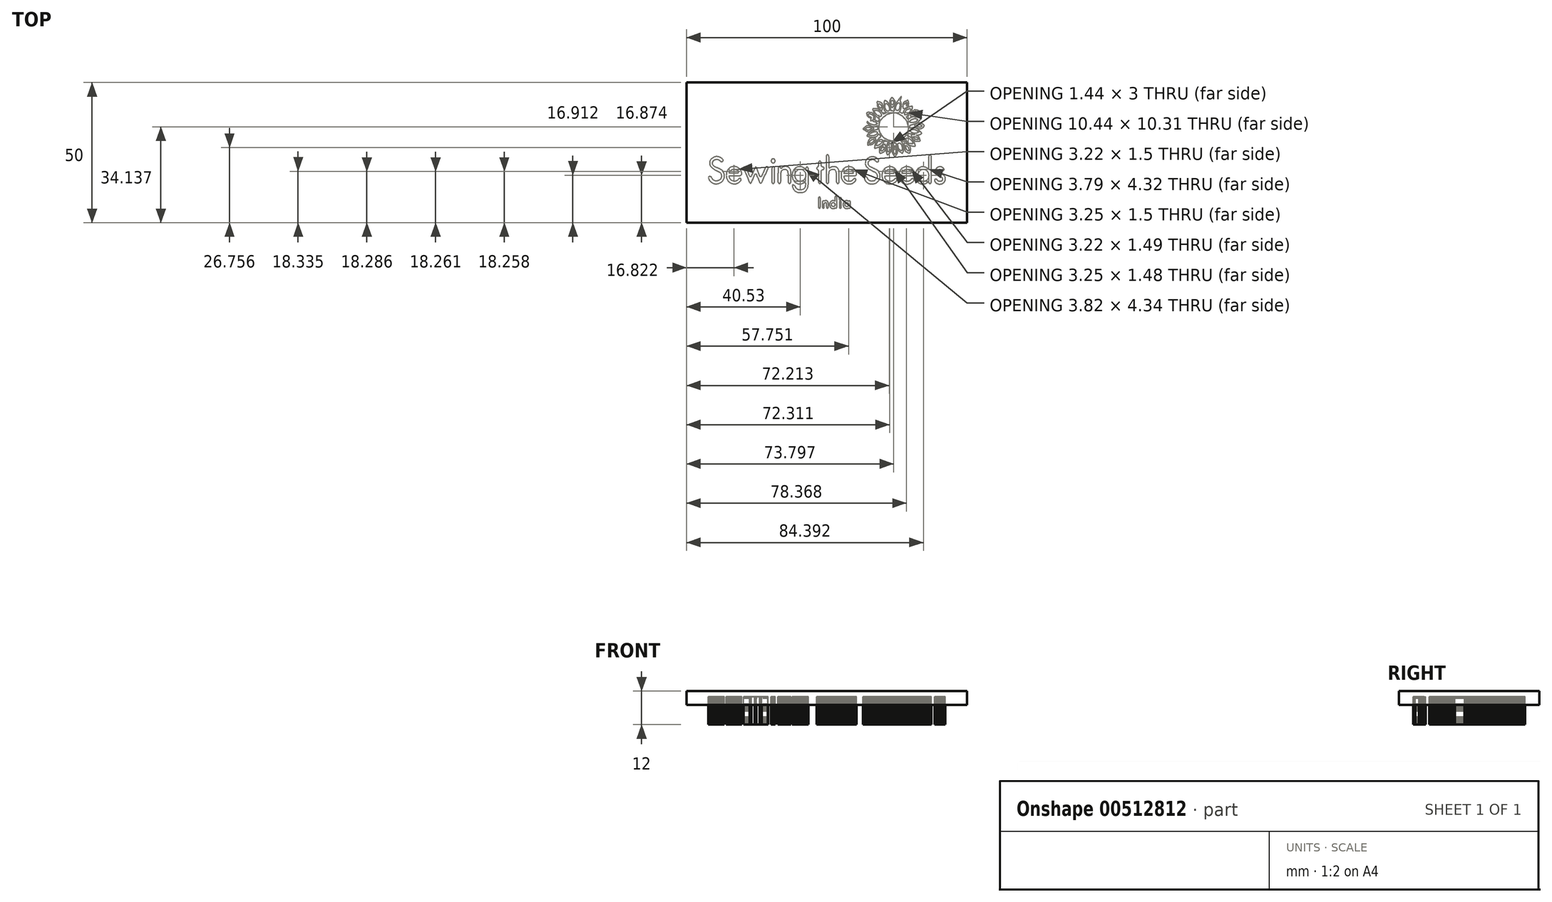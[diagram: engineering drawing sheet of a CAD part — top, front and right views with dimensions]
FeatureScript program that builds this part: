
annotation { "Feature Type Name" : "Feature", "Feature Type Description" : "" }
export const myFeature = defineFeature(function(context is Context, id is Id, definition is map)
    precondition{}
    {
        {
            var Q0;
            Q0=qCreatedBy(makeId("Top.planeOp"),FACE);
            var sketch = newSketch(context, id + "F0", { "sketchPlane" : qUnion([Q0])});
            skLineSegment(sketch, "E0", {"start": v(-2.33, -16.25) * mm, "end": v(-2.36, -16.13) * mm});
            skLineSegment(sketch, "E1", {"start": v(-2.36, -16.13) * mm, "end": v(-2.4, -16.03) * mm});
            skLineSegment(sketch, "E2", {"start": v(-2.4, -16.03) * mm, "end": v(-2.45, -15.94) * mm});
            skLineSegment(sketch, "E3", {"start": v(-2.45, -15.94) * mm, "end": v(-2.5, -15.87) * mm});
            skLineSegment(sketch, "E4", {"start": v(-2.5, -15.87) * mm, "end": v(-2.58, -15.82) * mm});
            skLineSegment(sketch, "E5", {"start": v(-2.58, -15.82) * mm, "end": v(-2.67, -15.8) * mm});
            skLineSegment(sketch, "E6", {"start": v(-2.67, -15.8) * mm, "end": v(-2.76, -15.82) * mm});
            skLineSegment(sketch, "E7", {"start": v(-2.76, -15.82) * mm, "end": v(-2.83, -15.87) * mm});
            skLineSegment(sketch, "E8", {"start": v(-2.83, -15.87) * mm, "end": v(-2.9, -15.94) * mm});
            skLineSegment(sketch, "E9", {"start": v(-2.9, -15.94) * mm, "end": v(-2.94, -16.03) * mm});
            skLineSegment(sketch, "E10", {"start": v(-2.94, -16.03) * mm, "end": v(-2.98, -16.13) * mm});
            skLineSegment(sketch, "E11", {"start": v(-2.98, -16.13) * mm, "end": v(-3.01, -16.25) * mm});
            skLineSegment(sketch, "E12", {"start": v(-3.01, -16.25) * mm, "end": v(-3.03, -16.37) * mm});
            skLineSegment(sketch, "E13", {"start": v(-3.03, -16.37) * mm, "end": v(-3.03, -16.5) * mm});
            skLineSegment(sketch, "E14", {"start": v(-3.03, -16.5) * mm, "end": v(-3.03, -16.83) * mm});
            skLineSegment(sketch, "E15", {"start": v(-3.03, -16.83) * mm, "end": v(-3.03, -17.17) * mm});
            skLineSegment(sketch, "E16", {"start": v(-3.03, -17.17) * mm, "end": v(-3.03, -17.5) * mm});
            skLineSegment(sketch, "E17", {"start": v(-3.03, -17.5) * mm, "end": v(-3.03, -17.84) * mm});
            skLineSegment(sketch, "E18", {"start": v(-3.03, -17.84) * mm, "end": v(-3.03, -18.18) * mm});
            skLineSegment(sketch, "E19", {"start": v(-3.03, -18.18) * mm, "end": v(-3.03, -18.51) * mm});
            skLineSegment(sketch, "E20", {"start": v(-3.03, -18.51) * mm, "end": v(-3.03, -18.85) * mm});
            skLineSegment(sketch, "E21", {"start": v(-3.03, -18.85) * mm, "end": v(-3.03, -19.19) * mm});
            skLineSegment(sketch, "E22", {"start": v(-3.03, -19.19) * mm, "end": v(-3.03, -19.31) * mm});
            skLineSegment(sketch, "E23", {"start": v(-3.03, -19.31) * mm, "end": v(-3.01, -19.43) * mm});
            skLineSegment(sketch, "E24", {"start": v(-3.01, -19.43) * mm, "end": v(-2.98, -19.55) * mm});
            skLineSegment(sketch, "E25", {"start": v(-2.98, -19.55) * mm, "end": v(-2.94, -19.66) * mm});
            skLineSegment(sketch, "E26", {"start": v(-2.94, -19.66) * mm, "end": v(-2.9, -19.75) * mm});
            skLineSegment(sketch, "E27", {"start": v(-2.9, -19.75) * mm, "end": v(-2.83, -19.82) * mm});
            skLineSegment(sketch, "E28", {"start": v(-2.83, -19.82) * mm, "end": v(-2.76, -19.86) * mm});
            skLineSegment(sketch, "E29", {"start": v(-2.76, -19.86) * mm, "end": v(-2.67, -19.88) * mm});
            skLineSegment(sketch, "E30", {"start": v(-2.67, -19.88) * mm, "end": v(-2.58, -19.86) * mm});
            skLineSegment(sketch, "E31", {"start": v(-2.58, -19.86) * mm, "end": v(-2.5, -19.82) * mm});
            skLineSegment(sketch, "E32", {"start": v(-2.5, -19.82) * mm, "end": v(-2.45, -19.75) * mm});
            skLineSegment(sketch, "E33", {"start": v(-2.45, -19.75) * mm, "end": v(-2.4, -19.66) * mm});
            skLineSegment(sketch, "E34", {"start": v(-2.4, -19.66) * mm, "end": v(-2.36, -19.55) * mm});
            skLineSegment(sketch, "E35", {"start": v(-2.36, -19.55) * mm, "end": v(-2.33, -19.43) * mm});
            skLineSegment(sketch, "E36", {"start": v(-2.33, -19.43) * mm, "end": v(-2.31, -19.31) * mm});
            skLineSegment(sketch, "E37", {"start": v(-2.31, -19.31) * mm, "end": v(-2.3, -19.19) * mm});
            skLineSegment(sketch, "E38", {"start": v(-2.3, -19.19) * mm, "end": v(-2.3, -18.85) * mm});
            skLineSegment(sketch, "E39", {"start": v(-2.3, -18.85) * mm, "end": v(-2.3, -18.51) * mm});
            skLineSegment(sketch, "E40", {"start": v(-2.3, -18.51) * mm, "end": v(-2.3, -18.18) * mm});
            skLineSegment(sketch, "E41", {"start": v(-2.3, -18.18) * mm, "end": v(-2.3, -17.84) * mm});
            skLineSegment(sketch, "E42", {"start": v(-2.3, -17.84) * mm, "end": v(-2.3, -17.5) * mm});
            skLineSegment(sketch, "E43", {"start": v(-2.3, -17.5) * mm, "end": v(-2.3, -17.17) * mm});
            skLineSegment(sketch, "E44", {"start": v(-2.3, -17.17) * mm, "end": v(-2.3, -16.83) * mm});
            skLineSegment(sketch, "E45", {"start": v(-2.3, -16.83) * mm, "end": v(-2.3, -16.5) * mm});
            skLineSegment(sketch, "E46", {"start": v(-2.3, -16.5) * mm, "end": v(-2.31, -16.37) * mm});
            skLineSegment(sketch, "E47", {"start": v(-2.31, -16.37) * mm, "end": v(-2.33, -16.25) * mm});
            skLineSegment(sketch, "E48", {"start": v(0.5, -17.99) * mm, "end": v(0.48, -17.86) * mm});
            skLineSegment(sketch, "E49", {"start": v(0.48, -17.86) * mm, "end": v(0.45, -17.74) * mm});
            skLineSegment(sketch, "E50", {"start": v(0.45, -17.74) * mm, "end": v(0.4, -17.64) * mm});
            skLineSegment(sketch, "E51", {"start": v(0.4, -17.64) * mm, "end": v(0.35, -17.54) * mm});
            skLineSegment(sketch, "E52", {"start": v(0.35, -17.54) * mm, "end": v(0.29, -17.46) * mm});
            skLineSegment(sketch, "E53", {"start": v(0.29, -17.46) * mm, "end": v(0.22, -17.38) * mm});
            skLineSegment(sketch, "E54", {"start": v(0.22, -17.38) * mm, "end": v(0.15, -17.33) * mm});
            skLineSegment(sketch, "E55", {"start": v(0.15, -17.33) * mm, "end": v(0.08, -17.28) * mm});
            skLineSegment(sketch, "E56", {"start": v(0.08, -17.28) * mm, "end": v(0, -17.24) * mm});
            skLineSegment(sketch, "E57", {"start": v(0, -17.24) * mm, "end": v(-0.07, -17.2) * mm});
            skLineSegment(sketch, "E58", {"start": v(-0.07, -17.2) * mm, "end": v(-0.14, -17.18) * mm});
            skLineSegment(sketch, "E59", {"start": v(-0.14, -17.18) * mm, "end": v(-0.22, -17.17) * mm});
            skLineSegment(sketch, "E60", {"start": v(-0.22, -17.17) * mm, "end": v(-0.3, -17.16) * mm});
            skLineSegment(sketch, "E61", {"start": v(-0.3, -17.16) * mm, "end": v(-0.4, -17.15) * mm});
            skLineSegment(sketch, "E62", {"start": v(-0.4, -17.15) * mm, "end": v(-0.45, -17.15) * mm});
            skLineSegment(sketch, "E63", {"start": v(-0.45, -17.15) * mm, "end": v(-0.5, -17.16) * mm});
            skLineSegment(sketch, "E64", {"start": v(-0.5, -17.16) * mm, "end": v(-0.56, -17.17) * mm});
            skLineSegment(sketch, "E65", {"start": v(-0.56, -17.17) * mm, "end": v(-0.62, -17.18) * mm});
            skLineSegment(sketch, "E66", {"start": v(-0.62, -17.18) * mm, "end": v(-0.67, -17.19) * mm});
            skLineSegment(sketch, "E67", {"start": v(-0.67, -17.19) * mm, "end": v(-0.73, -17.2) * mm});
            skLineSegment(sketch, "E68", {"start": v(-0.73, -17.2) * mm, "end": v(-0.78, -17.23) * mm});
            skLineSegment(sketch, "E69", {"start": v(-0.78, -17.23) * mm, "end": v(-0.83, -17.25) * mm});
            skLineSegment(sketch, "E70", {"start": v(-0.83, -17.25) * mm, "end": v(-0.85, -17.26) * mm});
            skLineSegment(sketch, "E71", {"start": v(-0.85, -17.26) * mm, "end": v(-0.87, -17.27) * mm});
            skLineSegment(sketch, "E72", {"start": v(-0.87, -17.27) * mm, "end": v(-0.9, -17.28) * mm});
            skLineSegment(sketch, "E73", {"start": v(-0.9, -17.28) * mm, "end": v(-0.91, -17.29) * mm});
            skLineSegment(sketch, "E74", {"start": v(-0.91, -17.29) * mm, "end": v(-0.93, -17.3) * mm});
            skLineSegment(sketch, "E75", {"start": v(-0.93, -17.3) * mm, "end": v(-0.95, -17.32) * mm});
            skLineSegment(sketch, "E76", {"start": v(-0.95, -17.32) * mm, "end": v(-0.97, -17.33) * mm});
            skLineSegment(sketch, "E77", {"start": v(-0.97, -17.33) * mm, "end": v(-1, -17.35) * mm});
            skLineSegment(sketch, "E78", {"start": v(-1, -17.35) * mm, "end": v(-1.02, -17.32) * mm});
            skLineSegment(sketch, "E79", {"start": v(-1.02, -17.32) * mm, "end": v(-1.05, -17.3) * mm});
            skLineSegment(sketch, "E80", {"start": v(-1.05, -17.3) * mm, "end": v(-1.08, -17.28) * mm});
            skLineSegment(sketch, "E81", {"start": v(-1.08, -17.28) * mm, "end": v(-1.12, -17.26) * mm});
            skLineSegment(sketch, "E82", {"start": v(-1.12, -17.26) * mm, "end": v(-1.16, -17.24) * mm});
            skLineSegment(sketch, "E83", {"start": v(-1.16, -17.24) * mm, "end": v(-1.2, -17.23) * mm});
            skLineSegment(sketch, "E84", {"start": v(-1.2, -17.23) * mm, "end": v(-1.25, -17.23) * mm});
            skLineSegment(sketch, "E85", {"start": v(-1.25, -17.23) * mm, "end": v(-1.3, -17.22) * mm});
            skLineSegment(sketch, "E86", {"start": v(-1.3, -17.22) * mm, "end": v(-1.38, -17.24) * mm});
            skLineSegment(sketch, "E87", {"start": v(-1.38, -17.24) * mm, "end": v(-1.45, -17.28) * mm});
            skLineSegment(sketch, "E88", {"start": v(-1.45, -17.28) * mm, "end": v(-1.51, -17.35) * mm});
            skLineSegment(sketch, "E89", {"start": v(-1.51, -17.35) * mm, "end": v(-1.56, -17.44) * mm});
            skLineSegment(sketch, "E90", {"start": v(-1.56, -17.44) * mm, "end": v(-1.6, -17.54) * mm});
            skLineSegment(sketch, "E91", {"start": v(-1.6, -17.54) * mm, "end": v(-1.62, -17.66) * mm});
            skLineSegment(sketch, "E92", {"start": v(-1.62, -17.66) * mm, "end": v(-1.64, -17.79) * mm});
            skLineSegment(sketch, "E93", {"start": v(-1.64, -17.79) * mm, "end": v(-1.64, -17.91) * mm});
            skLineSegment(sketch, "E94", {"start": v(-1.64, -17.91) * mm, "end": v(-1.64, -18.07) * mm});
            skLineSegment(sketch, "E95", {"start": v(-1.64, -18.07) * mm, "end": v(-1.64, -18.23) * mm});
            skLineSegment(sketch, "E96", {"start": v(-1.64, -18.23) * mm, "end": v(-1.64, -18.4) * mm});
            skLineSegment(sketch, "E97", {"start": v(-1.64, -18.4) * mm, "end": v(-1.64, -18.55) * mm});
            skLineSegment(sketch, "E98", {"start": v(-1.64, -18.55) * mm, "end": v(-1.64, -18.7) * mm});
            skLineSegment(sketch, "E99", {"start": v(-1.64, -18.7) * mm, "end": v(-1.64, -18.87) * mm});
            skLineSegment(sketch, "E100", {"start": v(-1.64, -18.87) * mm, "end": v(-1.64, -19.03) * mm});
            skLineSegment(sketch, "E101", {"start": v(-1.64, -19.03) * mm, "end": v(-1.64, -19.19) * mm});
            skLineSegment(sketch, "E102", {"start": v(-1.64, -19.19) * mm, "end": v(-1.64, -19.31) * mm});
            skLineSegment(sketch, "E103", {"start": v(-1.64, -19.31) * mm, "end": v(-1.62, -19.44) * mm});
            skLineSegment(sketch, "E104", {"start": v(-1.62, -19.44) * mm, "end": v(-1.6, -19.56) * mm});
            skLineSegment(sketch, "E105", {"start": v(-1.6, -19.56) * mm, "end": v(-1.56, -19.66) * mm});
            skLineSegment(sketch, "E106", {"start": v(-1.56, -19.66) * mm, "end": v(-1.51, -19.75) * mm});
            skLineSegment(sketch, "E107", {"start": v(-1.51, -19.75) * mm, "end": v(-1.45, -19.82) * mm});
            skLineSegment(sketch, "E108", {"start": v(-1.45, -19.82) * mm, "end": v(-1.38, -19.86) * mm});
            skLineSegment(sketch, "E109", {"start": v(-1.38, -19.86) * mm, "end": v(-1.3, -19.88) * mm});
            skLineSegment(sketch, "E110", {"start": v(-1.3, -19.88) * mm, "end": v(-1.2, -19.86) * mm});
            skLineSegment(sketch, "E111", {"start": v(-1.2, -19.86) * mm, "end": v(-1.13, -19.82) * mm});
            skLineSegment(sketch, "E112", {"start": v(-1.13, -19.82) * mm, "end": v(-1.07, -19.75) * mm});
            skLineSegment(sketch, "E113", {"start": v(-1.07, -19.75) * mm, "end": v(-1.02, -19.66) * mm});
            skLineSegment(sketch, "E114", {"start": v(-1.02, -19.66) * mm, "end": v(-0.99, -19.56) * mm});
            skLineSegment(sketch, "E115", {"start": v(-0.99, -19.56) * mm, "end": v(-0.96, -19.44) * mm});
            skLineSegment(sketch, "E116", {"start": v(-0.96, -19.44) * mm, "end": v(-0.94, -19.31) * mm});
            skLineSegment(sketch, "E117", {"start": v(-0.94, -19.31) * mm, "end": v(-0.94, -19.19) * mm});
            skLineSegment(sketch, "E118", {"start": v(-0.94, -19.19) * mm, "end": v(-0.94, -19.09) * mm});
            skLineSegment(sketch, "E119", {"start": v(-0.94, -19.09) * mm, "end": v(-0.94, -19) * mm});
            skLineSegment(sketch, "E120", {"start": v(-0.94, -19) * mm, "end": v(-0.94, -18.9) * mm});
            skLineSegment(sketch, "E121", {"start": v(-0.94, -18.9) * mm, "end": v(-0.94, -18.8) * mm});
            skLineSegment(sketch, "E122", {"start": v(-0.94, -18.8) * mm, "end": v(-0.94, -18.7) * mm});
            skLineSegment(sketch, "E123", {"start": v(-0.94, -18.7) * mm, "end": v(-0.94, -18.6) * mm});
            skLineSegment(sketch, "E124", {"start": v(-0.94, -18.6) * mm, "end": v(-0.94, -18.5) * mm});
            skLineSegment(sketch, "E125", {"start": v(-0.94, -18.5) * mm, "end": v(-0.94, -18.4) * mm});
            skLineSegment(sketch, "E126", {"start": v(-0.94, -18.4) * mm, "end": v(-0.94, -18.34) * mm});
            skLineSegment(sketch, "E127", {"start": v(-0.94, -18.34) * mm, "end": v(-0.93, -18.27) * mm});
            skLineSegment(sketch, "E128", {"start": v(-0.93, -18.27) * mm, "end": v(-0.92, -18.21) * mm});
            skLineSegment(sketch, "E129", {"start": v(-0.92, -18.21) * mm, "end": v(-0.9, -18.16) * mm});
            skLineSegment(sketch, "E130", {"start": v(-0.9, -18.16) * mm, "end": v(-0.9, -18.1) * mm});
            skLineSegment(sketch, "E131", {"start": v(-0.9, -18.1) * mm, "end": v(-0.87, -18.05) * mm});
            skLineSegment(sketch, "E132", {"start": v(-0.87, -18.05) * mm, "end": v(-0.85, -18) * mm});
            skLineSegment(sketch, "E133", {"start": v(-0.85, -18) * mm, "end": v(-0.82, -17.97) * mm});
            skLineSegment(sketch, "E134", {"start": v(-0.82, -17.97) * mm, "end": v(-0.8, -17.93) * mm});
            skLineSegment(sketch, "E135", {"start": v(-0.8, -17.93) * mm, "end": v(-0.76, -17.9) * mm});
            skLineSegment(sketch, "E136", {"start": v(-0.76, -17.9) * mm, "end": v(-0.73, -17.87) * mm});
            skLineSegment(sketch, "E137", {"start": v(-0.73, -17.87) * mm, "end": v(-0.7, -17.85) * mm});
            skLineSegment(sketch, "E138", {"start": v(-0.7, -17.85) * mm, "end": v(-0.65, -17.84) * mm});
            skLineSegment(sketch, "E139", {"start": v(-0.65, -17.84) * mm, "end": v(-0.6, -17.83) * mm});
            skLineSegment(sketch, "E140", {"start": v(-0.6, -17.83) * mm, "end": v(-0.56, -17.82) * mm});
            skLineSegment(sketch, "E141", {"start": v(-0.56, -17.82) * mm, "end": v(-0.5, -17.82) * mm});
            skLineSegment(sketch, "E142", {"start": v(-0.5, -17.82) * mm, "end": v(-0.46, -17.82) * mm});
            skLineSegment(sketch, "E143", {"start": v(-0.46, -17.82) * mm, "end": v(-0.42, -17.82) * mm});
            skLineSegment(sketch, "E144", {"start": v(-0.42, -17.82) * mm, "end": v(-0.39, -17.83) * mm});
            skLineSegment(sketch, "E145", {"start": v(-0.39, -17.83) * mm, "end": v(-0.36, -17.83) * mm});
            skLineSegment(sketch, "E146", {"start": v(-0.36, -17.83) * mm, "end": v(-0.34, -17.84) * mm});
            skLineSegment(sketch, "E147", {"start": v(-0.34, -17.84) * mm, "end": v(-0.32, -17.85) * mm});
            skLineSegment(sketch, "E148", {"start": v(-0.32, -17.85) * mm, "end": v(-0.3, -17.85) * mm});
            skLineSegment(sketch, "E149", {"start": v(-0.3, -17.85) * mm, "end": v(-0.3, -17.86) * mm});
            skLineSegment(sketch, "E150", {"start": v(-0.3, -17.86) * mm, "end": v(-0.27, -17.97) * mm});
            skLineSegment(sketch, "E151", {"start": v(-0.27, -17.97) * mm, "end": v(-0.25, -18.1) * mm});
            skLineSegment(sketch, "E152", {"start": v(-0.25, -18.1) * mm, "end": v(-0.22, -18.23) * mm});
            skLineSegment(sketch, "E153", {"start": v(-0.22, -18.23) * mm, "end": v(-0.2, -18.36) * mm});
            skLineSegment(sketch, "E154", {"start": v(-0.2, -18.36) * mm, "end": v(-0.2, -18.5) * mm});
            skLineSegment(sketch, "E155", {"start": v(-0.2, -18.5) * mm, "end": v(-0.18, -18.63) * mm});
            skLineSegment(sketch, "E156", {"start": v(-0.18, -18.63) * mm, "end": v(-0.17, -18.75) * mm});
            skLineSegment(sketch, "E157", {"start": v(-0.17, -18.75) * mm, "end": v(-0.17, -18.86) * mm});
            skLineSegment(sketch, "E158", {"start": v(-0.17, -18.86) * mm, "end": v(-0.17, -18.9) * mm});
            skLineSegment(sketch, "E159", {"start": v(-0.17, -18.9) * mm, "end": v(-0.17, -18.94) * mm});
            skLineSegment(sketch, "E160", {"start": v(-0.17, -18.94) * mm, "end": v(-0.17, -18.98) * mm});
            skLineSegment(sketch, "E161", {"start": v(-0.17, -18.98) * mm, "end": v(-0.17, -19.03) * mm});
            skLineSegment(sketch, "E162", {"start": v(-0.17, -19.03) * mm, "end": v(-0.17, -19.07) * mm});
            skLineSegment(sketch, "E163", {"start": v(-0.17, -19.07) * mm, "end": v(-0.17, -19.1) * mm});
            skLineSegment(sketch, "E164", {"start": v(-0.17, -19.1) * mm, "end": v(-0.17, -19.15) * mm});
            skLineSegment(sketch, "E165", {"start": v(-0.17, -19.15) * mm, "end": v(-0.17, -19.19) * mm});
            skLineSegment(sketch, "E166", {"start": v(-0.17, -19.19) * mm, "end": v(-0.17, -19.31) * mm});
            skLineSegment(sketch, "E167", {"start": v(-0.17, -19.31) * mm, "end": v(-0.15, -19.44) * mm});
            skLineSegment(sketch, "E168", {"start": v(-0.15, -19.44) * mm, "end": v(-0.12, -19.56) * mm});
            skLineSegment(sketch, "E169", {"start": v(-0.12, -19.56) * mm, "end": v(-0.09, -19.66) * mm});
            skLineSegment(sketch, "E170", {"start": v(-0.09, -19.66) * mm, "end": v(-0.04, -19.75) * mm});
            skLineSegment(sketch, "E171", {"start": v(-0.04, -19.75) * mm, "end": v(0.02, -19.82) * mm});
            skLineSegment(sketch, "E172", {"start": v(0.02, -19.82) * mm, "end": v(0.1, -19.86) * mm});
            skLineSegment(sketch, "E173", {"start": v(0.1, -19.86) * mm, "end": v(0.18, -19.88) * mm});
            skLineSegment(sketch, "E174", {"start": v(0.18, -19.88) * mm, "end": v(0.26, -19.86) * mm});
            skLineSegment(sketch, "E175", {"start": v(0.26, -19.86) * mm, "end": v(0.34, -19.82) * mm});
            skLineSegment(sketch, "E176", {"start": v(0.34, -19.82) * mm, "end": v(0.4, -19.75) * mm});
            skLineSegment(sketch, "E177", {"start": v(0.4, -19.75) * mm, "end": v(0.44, -19.66) * mm});
            skLineSegment(sketch, "E178", {"start": v(0.44, -19.66) * mm, "end": v(0.48, -19.56) * mm});
            skLineSegment(sketch, "E179", {"start": v(0.48, -19.56) * mm, "end": v(0.5, -19.44) * mm});
            skLineSegment(sketch, "E180", {"start": v(0.5, -19.44) * mm, "end": v(0.52, -19.31) * mm});
            skLineSegment(sketch, "E181", {"start": v(0.52, -19.31) * mm, "end": v(0.53, -19.19) * mm});
            skLineSegment(sketch, "E182", {"start": v(0.53, -19.19) * mm, "end": v(0.53, -19.07) * mm});
            skLineSegment(sketch, "E183", {"start": v(0.53, -19.07) * mm, "end": v(0.53, -18.96) * mm});
            skLineSegment(sketch, "E184", {"start": v(0.53, -18.96) * mm, "end": v(0.53, -18.84) * mm});
            skLineSegment(sketch, "E185", {"start": v(0.53, -18.84) * mm, "end": v(0.53, -18.73) * mm});
            skLineSegment(sketch, "E186", {"start": v(0.53, -18.73) * mm, "end": v(0.53, -18.62) * mm});
            skLineSegment(sketch, "E187", {"start": v(0.53, -18.62) * mm, "end": v(0.53, -18.5) * mm});
            skLineSegment(sketch, "E188", {"start": v(0.53, -18.5) * mm, "end": v(0.53, -18.39) * mm});
            skLineSegment(sketch, "E189", {"start": v(0.53, -18.39) * mm, "end": v(0.53, -18.27) * mm});
            skLineSegment(sketch, "E190", {"start": v(0.53, -18.27) * mm, "end": v(0.52, -18.13) * mm});
            skLineSegment(sketch, "E191", {"start": v(0.52, -18.13) * mm, "end": v(0.5, -17.99) * mm});
            skLineSegment(sketch, "E192", {"start": v(3.53, -15.89) * mm, "end": v(3.5, -15.77) * mm});
            skLineSegment(sketch, "E193", {"start": v(3.5, -15.77) * mm, "end": v(3.47, -15.66) * mm});
            skLineSegment(sketch, "E194", {"start": v(3.47, -15.66) * mm, "end": v(3.42, -15.58) * mm});
            skLineSegment(sketch, "E195", {"start": v(3.42, -15.58) * mm, "end": v(3.36, -15.5) * mm});
            skLineSegment(sketch, "E196", {"start": v(3.36, -15.5) * mm, "end": v(3.29, -15.46) * mm});
            skLineSegment(sketch, "E197", {"start": v(3.29, -15.46) * mm, "end": v(3.2, -15.45) * mm});
            skLineSegment(sketch, "E198", {"start": v(3.2, -15.45) * mm, "end": v(3.12, -15.46) * mm});
            skLineSegment(sketch, "E199", {"start": v(3.12, -15.46) * mm, "end": v(3.05, -15.5) * mm});
            skLineSegment(sketch, "E200", {"start": v(3.05, -15.5) * mm, "end": v(3, -15.58) * mm});
            skLineSegment(sketch, "E201", {"start": v(3, -15.58) * mm, "end": v(2.95, -15.66) * mm});
            skLineSegment(sketch, "E202", {"start": v(2.95, -15.66) * mm, "end": v(2.9, -15.77) * mm});
            skLineSegment(sketch, "E203", {"start": v(2.9, -15.77) * mm, "end": v(2.88, -15.89) * mm});
            skLineSegment(sketch, "E204", {"start": v(2.88, -15.89) * mm, "end": v(2.87, -16.01) * mm});
            skLineSegment(sketch, "E205", {"start": v(2.87, -16.01) * mm, "end": v(2.86, -16.14) * mm});
            skLineSegment(sketch, "E206", {"start": v(2.86, -16.14) * mm, "end": v(2.86, -16.3) * mm});
            skLineSegment(sketch, "E207", {"start": v(2.86, -16.3) * mm, "end": v(2.86, -16.45) * mm});
            skLineSegment(sketch, "E208", {"start": v(2.86, -16.45) * mm, "end": v(2.86, -16.6) * mm});
            skLineSegment(sketch, "E209", {"start": v(2.86, -16.6) * mm, "end": v(2.86, -16.76) * mm});
            skLineSegment(sketch, "E210", {"start": v(2.86, -16.76) * mm, "end": v(2.86, -16.91) * mm});
            skLineSegment(sketch, "E211", {"start": v(2.86, -16.91) * mm, "end": v(2.86, -17.07) * mm});
            skLineSegment(sketch, "E212", {"start": v(2.86, -17.07) * mm, "end": v(2.86, -17.22) * mm});
            skLineSegment(sketch, "E213", {"start": v(2.86, -17.22) * mm, "end": v(2.86, -17.37) * mm});
            skLineSegment(sketch, "E214", {"start": v(2.86, -17.37) * mm, "end": v(2.8, -17.33) * mm});
            skLineSegment(sketch, "E215", {"start": v(2.8, -17.33) * mm, "end": v(2.72, -17.29) * mm});
            skLineSegment(sketch, "E216", {"start": v(2.72, -17.29) * mm, "end": v(2.64, -17.25) * mm});
            skLineSegment(sketch, "E217", {"start": v(2.64, -17.25) * mm, "end": v(2.56, -17.22) * mm});
            skLineSegment(sketch, "E218", {"start": v(2.56, -17.22) * mm, "end": v(2.47, -17.2) * mm});
            skLineSegment(sketch, "E219", {"start": v(2.47, -17.2) * mm, "end": v(2.38, -17.18) * mm});
            skLineSegment(sketch, "E220", {"start": v(2.38, -17.18) * mm, "end": v(2.3, -17.17) * mm});
            skLineSegment(sketch, "E221", {"start": v(2.3, -17.17) * mm, "end": v(2.2, -17.17) * mm});
            skLineSegment(sketch, "E222", {"start": v(2.2, -17.17) * mm, "end": v(2.2, -17.17) * mm});
            skLineSegment(sketch, "E223", {"start": v(2.2, -17.17) * mm, "end": v(2.19, -17.17) * mm});
            skLineSegment(sketch, "E224", {"start": v(2.19, -17.17) * mm, "end": v(2.18, -17.17) * mm});
            skLineSegment(sketch, "E225", {"start": v(2.18, -17.17) * mm, "end": v(2.18, -17.17) * mm});
            skLineSegment(sketch, "E226", {"start": v(2.18, -17.17) * mm, "end": v(2.17, -17.17) * mm});
            skLineSegment(sketch, "E227", {"start": v(2.17, -17.17) * mm, "end": v(2.17, -17.17) * mm});
            skLineSegment(sketch, "E228", {"start": v(2.17, -17.17) * mm, "end": v(2.03, -17.17) * mm});
            skLineSegment(sketch, "E229", {"start": v(2.03, -17.17) * mm, "end": v(1.9, -17.2) * mm});
            skLineSegment(sketch, "E230", {"start": v(1.9, -17.2) * mm, "end": v(1.79, -17.23) * mm});
            skLineSegment(sketch, "E231", {"start": v(1.79, -17.23) * mm, "end": v(1.67, -17.27) * mm});
            skLineSegment(sketch, "E232", {"start": v(1.67, -17.27) * mm, "end": v(1.56, -17.33) * mm});
            skLineSegment(sketch, "E233", {"start": v(1.56, -17.33) * mm, "end": v(1.46, -17.4) * mm});
            skLineSegment(sketch, "E234", {"start": v(1.46, -17.4) * mm, "end": v(1.36, -17.5) * mm});
            skLineSegment(sketch, "E235", {"start": v(1.36, -17.5) * mm, "end": v(1.27, -17.6) * mm});
            skLineSegment(sketch, "E236", {"start": v(1.27, -17.6) * mm, "end": v(1.2, -17.7) * mm});
            skLineSegment(sketch, "E237", {"start": v(1.2, -17.7) * mm, "end": v(1.13, -17.8) * mm});
            skLineSegment(sketch, "E238", {"start": v(1.13, -17.8) * mm, "end": v(1.08, -17.92) * mm});
            skLineSegment(sketch, "E239", {"start": v(1.08, -17.92) * mm, "end": v(1.03, -18.04) * mm});
            skLineSegment(sketch, "E240", {"start": v(1.03, -18.04) * mm, "end": v(1, -18.16) * mm});
            skLineSegment(sketch, "E241", {"start": v(1, -18.16) * mm, "end": v(0.97, -18.3) * mm});
            skLineSegment(sketch, "E242", {"start": v(0.97, -18.3) * mm, "end": v(0.96, -18.42) * mm});
            skLineSegment(sketch, "E243", {"start": v(0.96, -18.42) * mm, "end": v(0.95, -18.56) * mm});
            skLineSegment(sketch, "E244", {"start": v(0.95, -18.56) * mm, "end": v(0.96, -18.7) * mm});
            skLineSegment(sketch, "E245", {"start": v(0.96, -18.7) * mm, "end": v(0.97, -18.83) * mm});
            skLineSegment(sketch, "E246", {"start": v(0.97, -18.83) * mm, "end": v(1, -18.96) * mm});
            skLineSegment(sketch, "E247", {"start": v(1, -18.96) * mm, "end": v(1.04, -19.08) * mm});
            skLineSegment(sketch, "E248", {"start": v(1.04, -19.08) * mm, "end": v(1.08, -19.2) * mm});
            skLineSegment(sketch, "E249", {"start": v(1.08, -19.2) * mm, "end": v(1.14, -19.3) * mm});
            skLineSegment(sketch, "E250", {"start": v(1.14, -19.3) * mm, "end": v(1.21, -19.42) * mm});
            skLineSegment(sketch, "E251", {"start": v(1.21, -19.42) * mm, "end": v(1.3, -19.52) * mm});
            skLineSegment(sketch, "E252", {"start": v(1.3, -19.52) * mm, "end": v(1.38, -19.62) * mm});
            skLineSegment(sketch, "E253", {"start": v(1.38, -19.62) * mm, "end": v(1.48, -19.71) * mm});
            skLineSegment(sketch, "E254", {"start": v(1.48, -19.71) * mm, "end": v(1.58, -19.79) * mm});
            skLineSegment(sketch, "E255", {"start": v(1.58, -19.79) * mm, "end": v(1.7, -19.85) * mm});
            skLineSegment(sketch, "E256", {"start": v(1.7, -19.85) * mm, "end": v(1.8, -19.9) * mm});
            skLineSegment(sketch, "E257", {"start": v(1.8, -19.9) * mm, "end": v(1.92, -19.93) * mm});
            skLineSegment(sketch, "E258", {"start": v(1.92, -19.93) * mm, "end": v(2.05, -19.95) * mm});
            skLineSegment(sketch, "E259", {"start": v(2.05, -19.95) * mm, "end": v(2.17, -19.95) * mm});
            skLineSegment(sketch, "E260", {"start": v(2.17, -19.95) * mm, "end": v(2.18, -19.95) * mm});
            skLineSegment(sketch, "E261", {"start": v(2.18, -19.95) * mm, "end": v(2.18, -19.95) * mm});
            skLineSegment(sketch, "E262", {"start": v(2.18, -19.95) * mm, "end": v(2.19, -19.95) * mm});
            skLineSegment(sketch, "E263", {"start": v(2.19, -19.95) * mm, "end": v(2.19, -19.95) * mm});
            skLineSegment(sketch, "E264", {"start": v(2.19, -19.95) * mm, "end": v(2.2, -19.95) * mm});
            skLineSegment(sketch, "E265", {"start": v(2.2, -19.95) * mm, "end": v(2.26, -19.95) * mm});
            skLineSegment(sketch, "E266", {"start": v(2.26, -19.95) * mm, "end": v(2.33, -19.95) * mm});
            skLineSegment(sketch, "E267", {"start": v(2.33, -19.95) * mm, "end": v(2.4, -19.94) * mm});
            skLineSegment(sketch, "E268", {"start": v(2.4, -19.94) * mm, "end": v(2.47, -19.93) * mm});
            skLineSegment(sketch, "E269", {"start": v(2.47, -19.93) * mm, "end": v(2.54, -19.92) * mm});
            skLineSegment(sketch, "E270", {"start": v(2.54, -19.92) * mm, "end": v(2.6, -19.9) * mm});
            skLineSegment(sketch, "E271", {"start": v(2.6, -19.9) * mm, "end": v(2.65, -19.89) * mm});
            skLineSegment(sketch, "E272", {"start": v(2.65, -19.89) * mm, "end": v(2.69, -19.86) * mm});
            skLineSegment(sketch, "E273", {"start": v(2.69, -19.86) * mm, "end": v(2.72, -19.83) * mm});
            skLineSegment(sketch, "E274", {"start": v(2.72, -19.83) * mm, "end": v(2.76, -19.8) * mm});
            skLineSegment(sketch, "E275", {"start": v(2.76, -19.8) * mm, "end": v(2.79, -19.78) * mm});
            skLineSegment(sketch, "E276", {"start": v(2.79, -19.78) * mm, "end": v(2.82, -19.76) * mm});
            skLineSegment(sketch, "E277", {"start": v(2.82, -19.76) * mm, "end": v(2.84, -19.75) * mm});
            skLineSegment(sketch, "E278", {"start": v(2.84, -19.75) * mm, "end": v(2.87, -19.73) * mm});
            skLineSegment(sketch, "E279", {"start": v(2.87, -19.73) * mm, "end": v(2.89, -19.72) * mm});
            skLineSegment(sketch, "E280", {"start": v(2.89, -19.72) * mm, "end": v(2.9, -19.7) * mm});
            skLineSegment(sketch, "E281", {"start": v(2.9, -19.7) * mm, "end": v(2.93, -19.74) * mm});
            skLineSegment(sketch, "E282", {"start": v(2.93, -19.74) * mm, "end": v(2.96, -19.78) * mm});
            skLineSegment(sketch, "E283", {"start": v(2.96, -19.78) * mm, "end": v(3, -19.8) * mm});
            skLineSegment(sketch, "E284", {"start": v(3, -19.8) * mm, "end": v(3.03, -19.83) * mm});
            skLineSegment(sketch, "E285", {"start": v(3.03, -19.83) * mm, "end": v(3.07, -19.85) * mm});
            skLineSegment(sketch, "E286", {"start": v(3.07, -19.85) * mm, "end": v(3.12, -19.86) * mm});
            skLineSegment(sketch, "E287", {"start": v(3.12, -19.86) * mm, "end": v(3.16, -19.87) * mm});
            skLineSegment(sketch, "E288", {"start": v(3.16, -19.87) * mm, "end": v(3.21, -19.88) * mm});
            skLineSegment(sketch, "E289", {"start": v(3.21, -19.88) * mm, "end": v(3.3, -19.86) * mm});
            skLineSegment(sketch, "E290", {"start": v(3.3, -19.86) * mm, "end": v(3.36, -19.82) * mm});
            skLineSegment(sketch, "E291", {"start": v(3.36, -19.82) * mm, "end": v(3.42, -19.75) * mm});
            skLineSegment(sketch, "E292", {"start": v(3.42, -19.75) * mm, "end": v(3.47, -19.66) * mm});
            skLineSegment(sketch, "E293", {"start": v(3.47, -19.66) * mm, "end": v(3.5, -19.56) * mm});
            skLineSegment(sketch, "E294", {"start": v(3.5, -19.56) * mm, "end": v(3.53, -19.44) * mm});
            skLineSegment(sketch, "E295", {"start": v(3.53, -19.44) * mm, "end": v(3.54, -19.31) * mm});
            skLineSegment(sketch, "E296", {"start": v(3.54, -19.31) * mm, "end": v(3.55, -19.19) * mm});
            skLineSegment(sketch, "E297", {"start": v(3.55, -19.19) * mm, "end": v(3.55, -18.8) * mm});
            skLineSegment(sketch, "E298", {"start": v(3.55, -18.8) * mm, "end": v(3.55, -18.42) * mm});
            skLineSegment(sketch, "E299", {"start": v(3.55, -18.42) * mm, "end": v(3.55, -18.04) * mm});
            skLineSegment(sketch, "E300", {"start": v(3.55, -18.04) * mm, "end": v(3.55, -17.66) * mm});
            skLineSegment(sketch, "E301", {"start": v(3.55, -17.66) * mm, "end": v(3.55, -17.28) * mm});
            skLineSegment(sketch, "E302", {"start": v(3.55, -17.28) * mm, "end": v(3.55, -16.9) * mm});
            skLineSegment(sketch, "E303", {"start": v(3.55, -16.9) * mm, "end": v(3.55, -16.52) * mm});
            skLineSegment(sketch, "E304", {"start": v(3.55, -16.52) * mm, "end": v(3.55, -16.14) * mm});
            skLineSegment(sketch, "E305", {"start": v(3.55, -16.14) * mm, "end": v(3.54, -16.01) * mm});
            skLineSegment(sketch, "E306", {"start": v(3.54, -16.01) * mm, "end": v(3.53, -15.89) * mm});
            skLineSegment(sketch, "E307", {"start": v(2.26, -17.82) * mm, "end": v(2.33, -17.82) * mm});
            skLineSegment(sketch, "E308", {"start": v(2.33, -17.82) * mm, "end": v(2.4, -17.83) * mm});
            skLineSegment(sketch, "E309", {"start": v(2.4, -17.83) * mm, "end": v(2.45, -17.85) * mm});
            skLineSegment(sketch, "E310", {"start": v(2.45, -17.85) * mm, "end": v(2.51, -17.87) * mm});
            skLineSegment(sketch, "E311", {"start": v(2.51, -17.87) * mm, "end": v(2.57, -17.9) * mm});
            skLineSegment(sketch, "E312", {"start": v(2.57, -17.9) * mm, "end": v(2.62, -17.93) * mm});
            skLineSegment(sketch, "E313", {"start": v(2.62, -17.93) * mm, "end": v(2.66, -17.98) * mm});
            skLineSegment(sketch, "E314", {"start": v(2.66, -17.98) * mm, "end": v(2.7, -18.02) * mm});
            skLineSegment(sketch, "E315", {"start": v(2.7, -18.02) * mm, "end": v(2.75, -18.08) * mm});
            skLineSegment(sketch, "E316", {"start": v(2.75, -18.08) * mm, "end": v(2.78, -18.13) * mm});
            skLineSegment(sketch, "E317", {"start": v(2.78, -18.13) * mm, "end": v(2.81, -18.19) * mm});
            skLineSegment(sketch, "E318", {"start": v(2.81, -18.19) * mm, "end": v(2.84, -18.25) * mm});
            skLineSegment(sketch, "E319", {"start": v(2.84, -18.25) * mm, "end": v(2.86, -18.31) * mm});
            skLineSegment(sketch, "E320", {"start": v(2.86, -18.31) * mm, "end": v(2.87, -18.38) * mm});
            skLineSegment(sketch, "E321", {"start": v(2.87, -18.38) * mm, "end": v(2.88, -18.45) * mm});
            skLineSegment(sketch, "E322", {"start": v(2.88, -18.45) * mm, "end": v(2.88, -18.53) * mm});
            skLineSegment(sketch, "E323", {"start": v(2.88, -18.53) * mm, "end": v(2.88, -18.6) * mm});
            skLineSegment(sketch, "E324", {"start": v(2.88, -18.6) * mm, "end": v(2.87, -18.68) * mm});
            skLineSegment(sketch, "E325", {"start": v(2.87, -18.68) * mm, "end": v(2.86, -18.75) * mm});
            skLineSegment(sketch, "E326", {"start": v(2.86, -18.75) * mm, "end": v(2.85, -18.82) * mm});
            skLineSegment(sketch, "E327", {"start": v(2.85, -18.82) * mm, "end": v(2.82, -18.88) * mm});
            skLineSegment(sketch, "E328", {"start": v(2.82, -18.88) * mm, "end": v(2.8, -18.94) * mm});
            skLineSegment(sketch, "E329", {"start": v(2.8, -18.94) * mm, "end": v(2.77, -19) * mm});
            skLineSegment(sketch, "E330", {"start": v(2.77, -19) * mm, "end": v(2.73, -19.05) * mm});
            skLineSegment(sketch, "E331", {"start": v(2.73, -19.05) * mm, "end": v(2.68, -19.1) * mm});
            skLineSegment(sketch, "E332", {"start": v(2.68, -19.1) * mm, "end": v(2.63, -19.15) * mm});
            skLineSegment(sketch, "E333", {"start": v(2.63, -19.15) * mm, "end": v(2.58, -19.19) * mm});
            skLineSegment(sketch, "E334", {"start": v(2.58, -19.19) * mm, "end": v(2.52, -19.22) * mm});
            skLineSegment(sketch, "E335", {"start": v(2.52, -19.22) * mm, "end": v(2.46, -19.24) * mm});
            skLineSegment(sketch, "E336", {"start": v(2.46, -19.24) * mm, "end": v(2.4, -19.26) * mm});
            skLineSegment(sketch, "E337", {"start": v(2.4, -19.26) * mm, "end": v(2.32, -19.27) * mm});
            skLineSegment(sketch, "E338", {"start": v(2.32, -19.27) * mm, "end": v(2.24, -19.28) * mm});
            skLineSegment(sketch, "E339", {"start": v(2.24, -19.28) * mm, "end": v(2.17, -19.27) * mm});
            skLineSegment(sketch, "E340", {"start": v(2.17, -19.27) * mm, "end": v(2.1, -19.26) * mm});
            skLineSegment(sketch, "E341", {"start": v(2.1, -19.26) * mm, "end": v(2.05, -19.25) * mm});
            skLineSegment(sketch, "E342", {"start": v(2.05, -19.25) * mm, "end": v(2, -19.22) * mm});
            skLineSegment(sketch, "E343", {"start": v(2, -19.22) * mm, "end": v(1.94, -19.2) * mm});
            skLineSegment(sketch, "E344", {"start": v(1.94, -19.2) * mm, "end": v(1.9, -19.16) * mm});
            skLineSegment(sketch, "E345", {"start": v(1.9, -19.16) * mm, "end": v(1.84, -19.12) * mm});
            skLineSegment(sketch, "E346", {"start": v(1.84, -19.12) * mm, "end": v(1.8, -19.07) * mm});
            skLineSegment(sketch, "E347", {"start": v(1.8, -19.07) * mm, "end": v(1.76, -19.01) * mm});
            skLineSegment(sketch, "E348", {"start": v(1.76, -19.01) * mm, "end": v(1.73, -18.96) * mm});
            skLineSegment(sketch, "E349", {"start": v(1.73, -18.96) * mm, "end": v(1.7, -18.9) * mm});
            skLineSegment(sketch, "E350", {"start": v(1.7, -18.9) * mm, "end": v(1.68, -18.84) * mm});
            skLineSegment(sketch, "E351", {"start": v(1.68, -18.84) * mm, "end": v(1.67, -18.77) * mm});
            skLineSegment(sketch, "E352", {"start": v(1.67, -18.77) * mm, "end": v(1.65, -18.7) * mm});
            skLineSegment(sketch, "E353", {"start": v(1.65, -18.7) * mm, "end": v(1.64, -18.63) * mm});
            skLineSegment(sketch, "E354", {"start": v(1.64, -18.63) * mm, "end": v(1.64, -18.55) * mm});
            skLineSegment(sketch, "E355", {"start": v(1.64, -18.55) * mm, "end": v(1.64, -18.48) * mm});
            skLineSegment(sketch, "E356", {"start": v(1.64, -18.48) * mm, "end": v(1.65, -18.4) * mm});
            skLineSegment(sketch, "E357", {"start": v(1.65, -18.4) * mm, "end": v(1.66, -18.34) * mm});
            skLineSegment(sketch, "E358", {"start": v(1.66, -18.34) * mm, "end": v(1.68, -18.27) * mm});
            skLineSegment(sketch, "E359", {"start": v(1.68, -18.27) * mm, "end": v(1.7, -18.2) * mm});
            skLineSegment(sketch, "E360", {"start": v(1.7, -18.2) * mm, "end": v(1.73, -18.15) * mm});
            skLineSegment(sketch, "E361", {"start": v(1.73, -18.15) * mm, "end": v(1.77, -18.1) * mm});
            skLineSegment(sketch, "E362", {"start": v(1.77, -18.1) * mm, "end": v(1.8, -18.04) * mm});
            skLineSegment(sketch, "E363", {"start": v(1.8, -18.04) * mm, "end": v(1.85, -17.99) * mm});
            skLineSegment(sketch, "E364", {"start": v(1.85, -17.99) * mm, "end": v(1.9, -17.94) * mm});
            skLineSegment(sketch, "E365", {"start": v(1.9, -17.94) * mm, "end": v(1.95, -17.9) * mm});
            skLineSegment(sketch, "E366", {"start": v(1.95, -17.9) * mm, "end": v(2, -17.87) * mm});
            skLineSegment(sketch, "E367", {"start": v(2, -17.87) * mm, "end": v(2.06, -17.85) * mm});
            skLineSegment(sketch, "E368", {"start": v(2.06, -17.85) * mm, "end": v(2.12, -17.83) * mm});
            skLineSegment(sketch, "E369", {"start": v(2.12, -17.83) * mm, "end": v(2.18, -17.82) * mm});
            skLineSegment(sketch, "E370", {"start": v(2.18, -17.82) * mm, "end": v(2.25, -17.82) * mm});
            skLineSegment(sketch, "E371", {"start": v(2.25, -17.82) * mm, "end": v(2.26, -17.82) * mm});
            skLineSegment(sketch, "E372", {"start": v(5.1, -17.66) * mm, "end": v(5.08, -17.54) * mm});
            skLineSegment(sketch, "E373", {"start": v(5.08, -17.54) * mm, "end": v(5.04, -17.44) * mm});
            skLineSegment(sketch, "E374", {"start": v(5.04, -17.44) * mm, "end": v(5, -17.35) * mm});
            skLineSegment(sketch, "E375", {"start": v(5, -17.35) * mm, "end": v(4.93, -17.28) * mm});
            skLineSegment(sketch, "E376", {"start": v(4.93, -17.28) * mm, "end": v(4.86, -17.24) * mm});
            skLineSegment(sketch, "E377", {"start": v(4.86, -17.24) * mm, "end": v(4.78, -17.22) * mm});
            skLineSegment(sketch, "E378", {"start": v(4.78, -17.22) * mm, "end": v(4.7, -17.24) * mm});
            skLineSegment(sketch, "E379", {"start": v(4.7, -17.24) * mm, "end": v(4.62, -17.28) * mm});
            skLineSegment(sketch, "E380", {"start": v(4.62, -17.28) * mm, "end": v(4.56, -17.35) * mm});
            skLineSegment(sketch, "E381", {"start": v(4.56, -17.35) * mm, "end": v(4.5, -17.44) * mm});
            skLineSegment(sketch, "E382", {"start": v(4.5, -17.44) * mm, "end": v(4.47, -17.54) * mm});
            skLineSegment(sketch, "E383", {"start": v(4.47, -17.54) * mm, "end": v(4.44, -17.66) * mm});
            skLineSegment(sketch, "E384", {"start": v(4.44, -17.66) * mm, "end": v(4.43, -17.79) * mm});
            skLineSegment(sketch, "E385", {"start": v(4.43, -17.79) * mm, "end": v(4.42, -17.91) * mm});
            skLineSegment(sketch, "E386", {"start": v(4.42, -17.91) * mm, "end": v(4.42, -18.07) * mm});
            skLineSegment(sketch, "E387", {"start": v(4.42, -18.07) * mm, "end": v(4.42, -18.23) * mm});
            skLineSegment(sketch, "E388", {"start": v(4.42, -18.23) * mm, "end": v(4.42, -18.4) * mm});
            skLineSegment(sketch, "E389", {"start": v(4.42, -18.4) * mm, "end": v(4.42, -18.55) * mm});
            skLineSegment(sketch, "E390", {"start": v(4.42, -18.55) * mm, "end": v(4.42, -18.7) * mm});
            skLineSegment(sketch, "E391", {"start": v(4.42, -18.7) * mm, "end": v(4.42, -18.87) * mm});
            skLineSegment(sketch, "E392", {"start": v(4.42, -18.87) * mm, "end": v(4.42, -19.03) * mm});
            skLineSegment(sketch, "E393", {"start": v(4.42, -19.03) * mm, "end": v(4.42, -19.19) * mm});
            skLineSegment(sketch, "E394", {"start": v(4.42, -19.19) * mm, "end": v(4.43, -19.31) * mm});
            skLineSegment(sketch, "E395", {"start": v(4.43, -19.31) * mm, "end": v(4.44, -19.44) * mm});
            skLineSegment(sketch, "E396", {"start": v(4.44, -19.44) * mm, "end": v(4.47, -19.56) * mm});
            skLineSegment(sketch, "E397", {"start": v(4.47, -19.56) * mm, "end": v(4.5, -19.66) * mm});
            skLineSegment(sketch, "E398", {"start": v(4.5, -19.66) * mm, "end": v(4.56, -19.75) * mm});
            skLineSegment(sketch, "E399", {"start": v(4.56, -19.75) * mm, "end": v(4.62, -19.82) * mm});
            skLineSegment(sketch, "E400", {"start": v(4.62, -19.82) * mm, "end": v(4.7, -19.86) * mm});
            skLineSegment(sketch, "E401", {"start": v(4.7, -19.86) * mm, "end": v(4.78, -19.88) * mm});
            skLineSegment(sketch, "E402", {"start": v(4.78, -19.88) * mm, "end": v(4.86, -19.86) * mm});
            skLineSegment(sketch, "E403", {"start": v(4.86, -19.86) * mm, "end": v(4.93, -19.82) * mm});
            skLineSegment(sketch, "E404", {"start": v(4.93, -19.82) * mm, "end": v(5, -19.75) * mm});
            skLineSegment(sketch, "E405", {"start": v(5, -19.75) * mm, "end": v(5.04, -19.66) * mm});
            skLineSegment(sketch, "E406", {"start": v(5.04, -19.66) * mm, "end": v(5.08, -19.56) * mm});
            skLineSegment(sketch, "E407", {"start": v(5.08, -19.56) * mm, "end": v(5.1, -19.44) * mm});
            skLineSegment(sketch, "E408", {"start": v(5.1, -19.44) * mm, "end": v(5.12, -19.31) * mm});
            skLineSegment(sketch, "E409", {"start": v(5.12, -19.31) * mm, "end": v(5.13, -19.19) * mm});
            skLineSegment(sketch, "E410", {"start": v(5.13, -19.19) * mm, "end": v(5.13, -19.03) * mm});
            skLineSegment(sketch, "E411", {"start": v(5.13, -19.03) * mm, "end": v(5.13, -18.87) * mm});
            skLineSegment(sketch, "E412", {"start": v(5.13, -18.87) * mm, "end": v(5.13, -18.7) * mm});
            skLineSegment(sketch, "E413", {"start": v(5.13, -18.7) * mm, "end": v(5.13, -18.55) * mm});
            skLineSegment(sketch, "E414", {"start": v(5.13, -18.55) * mm, "end": v(5.13, -18.4) * mm});
            skLineSegment(sketch, "E415", {"start": v(5.13, -18.4) * mm, "end": v(5.13, -18.23) * mm});
            skLineSegment(sketch, "E416", {"start": v(5.13, -18.23) * mm, "end": v(5.13, -18.07) * mm});
            skLineSegment(sketch, "E417", {"start": v(5.13, -18.07) * mm, "end": v(5.13, -17.91) * mm});
            skLineSegment(sketch, "E418", {"start": v(5.13, -17.91) * mm, "end": v(5.12, -17.79) * mm});
            skLineSegment(sketch, "E419", {"start": v(5.12, -17.79) * mm, "end": v(5.1, -17.66) * mm});
            skLineSegment(sketch, "E420", {"start": v(5.19, -16.37) * mm, "end": v(5.17, -16.32) * mm});
            skLineSegment(sketch, "E421", {"start": v(5.17, -16.32) * mm, "end": v(5.16, -16.28) * mm});
            skLineSegment(sketch, "E422", {"start": v(5.16, -16.28) * mm, "end": v(5.14, -16.24) * mm});
            skLineSegment(sketch, "E423", {"start": v(5.14, -16.24) * mm, "end": v(5.11, -16.21) * mm});
            skLineSegment(sketch, "E424", {"start": v(5.11, -16.21) * mm, "end": v(5.1, -16.18) * mm});
            skLineSegment(sketch, "E425", {"start": v(5.1, -16.18) * mm, "end": v(5.07, -16.16) * mm});
            skLineSegment(sketch, "E426", {"start": v(5.07, -16.16) * mm, "end": v(5, -16.11) * mm});
            skLineSegment(sketch, "E427", {"start": v(5, -16.11) * mm, "end": v(4.93, -16.08) * mm});
            skLineSegment(sketch, "E428", {"start": v(4.93, -16.08) * mm, "end": v(4.85, -16.06) * mm});
            skLineSegment(sketch, "E429", {"start": v(4.85, -16.06) * mm, "end": v(4.77, -16.05) * mm});
            skLineSegment(sketch, "E430", {"start": v(4.77, -16.05) * mm, "end": v(4.69, -16.06) * mm});
            skLineSegment(sketch, "E431", {"start": v(4.69, -16.06) * mm, "end": v(4.61, -16.08) * mm});
            skLineSegment(sketch, "E432", {"start": v(4.61, -16.08) * mm, "end": v(4.54, -16.11) * mm});
            skLineSegment(sketch, "E433", {"start": v(4.54, -16.11) * mm, "end": v(4.48, -16.16) * mm});
            skLineSegment(sketch, "E434", {"start": v(4.48, -16.16) * mm, "end": v(4.44, -16.2) * mm});
            skLineSegment(sketch, "E435", {"start": v(4.44, -16.2) * mm, "end": v(4.42, -16.23) * mm});
            skLineSegment(sketch, "E436", {"start": v(4.42, -16.23) * mm, "end": v(4.4, -16.26) * mm});
            skLineSegment(sketch, "E437", {"start": v(4.4, -16.26) * mm, "end": v(4.37, -16.3) * mm});
            skLineSegment(sketch, "E438", {"start": v(4.37, -16.3) * mm, "end": v(4.36, -16.35) * mm});
            skLineSegment(sketch, "E439", {"start": v(4.36, -16.35) * mm, "end": v(4.35, -16.4) * mm});
            skLineSegment(sketch, "E440", {"start": v(4.35, -16.4) * mm, "end": v(4.34, -16.44) * mm});
            skLineSegment(sketch, "E441", {"start": v(4.34, -16.44) * mm, "end": v(4.34, -16.49) * mm});
            skLineSegment(sketch, "E442", {"start": v(4.34, -16.49) * mm, "end": v(4.34, -16.53) * mm});
            skLineSegment(sketch, "E443", {"start": v(4.34, -16.53) * mm, "end": v(4.35, -16.58) * mm});
            skLineSegment(sketch, "E444", {"start": v(4.35, -16.58) * mm, "end": v(4.36, -16.62) * mm});
            skLineSegment(sketch, "E445", {"start": v(4.36, -16.62) * mm, "end": v(4.37, -16.66) * mm});
            skLineSegment(sketch, "E446", {"start": v(4.37, -16.66) * mm, "end": v(4.4, -16.7) * mm});
            skLineSegment(sketch, "E447", {"start": v(4.4, -16.7) * mm, "end": v(4.42, -16.74) * mm});
            skLineSegment(sketch, "E448", {"start": v(4.42, -16.74) * mm, "end": v(4.45, -16.77) * mm});
            skLineSegment(sketch, "E449", {"start": v(4.45, -16.77) * mm, "end": v(4.48, -16.8) * mm});
            skLineSegment(sketch, "E450", {"start": v(4.48, -16.8) * mm, "end": v(4.51, -16.83) * mm});
            skLineSegment(sketch, "E451", {"start": v(4.51, -16.83) * mm, "end": v(4.54, -16.85) * mm});
            skLineSegment(sketch, "E452", {"start": v(4.54, -16.85) * mm, "end": v(4.58, -16.87) * mm});
            skLineSegment(sketch, "E453", {"start": v(4.58, -16.87) * mm, "end": v(4.61, -16.88) * mm});
            skLineSegment(sketch, "E454", {"start": v(4.61, -16.88) * mm, "end": v(4.65, -16.9) * mm});
            skLineSegment(sketch, "E455", {"start": v(4.65, -16.9) * mm, "end": v(4.7, -16.9) * mm});
            skLineSegment(sketch, "E456", {"start": v(4.7, -16.9) * mm, "end": v(4.73, -16.9) * mm});
            skLineSegment(sketch, "E457", {"start": v(4.73, -16.9) * mm, "end": v(4.77, -16.9) * mm});
            skLineSegment(sketch, "E458", {"start": v(4.77, -16.9) * mm, "end": v(4.81, -16.9) * mm});
            skLineSegment(sketch, "E459", {"start": v(4.81, -16.9) * mm, "end": v(4.85, -16.9) * mm});
            skLineSegment(sketch, "E460", {"start": v(4.85, -16.9) * mm, "end": v(4.9, -16.9) * mm});
            skLineSegment(sketch, "E461", {"start": v(4.9, -16.9) * mm, "end": v(4.93, -16.88) * mm});
            skLineSegment(sketch, "E462", {"start": v(4.93, -16.88) * mm, "end": v(4.97, -16.87) * mm});
            skLineSegment(sketch, "E463", {"start": v(4.97, -16.87) * mm, "end": v(5, -16.85) * mm});
            skLineSegment(sketch, "E464", {"start": v(5, -16.85) * mm, "end": v(5.04, -16.83) * mm});
            skLineSegment(sketch, "E465", {"start": v(5.04, -16.83) * mm, "end": v(5.07, -16.8) * mm});
            skLineSegment(sketch, "E466", {"start": v(5.07, -16.8) * mm, "end": v(5.1, -16.77) * mm});
            skLineSegment(sketch, "E467", {"start": v(5.1, -16.77) * mm, "end": v(5.12, -16.74) * mm});
            skLineSegment(sketch, "E468", {"start": v(5.12, -16.74) * mm, "end": v(5.15, -16.7) * mm});
            skLineSegment(sketch, "E469", {"start": v(5.15, -16.7) * mm, "end": v(5.17, -16.66) * mm});
            skLineSegment(sketch, "E470", {"start": v(5.17, -16.66) * mm, "end": v(5.18, -16.62) * mm});
            skLineSegment(sketch, "E471", {"start": v(5.18, -16.62) * mm, "end": v(5.2, -16.57) * mm});
            skLineSegment(sketch, "E472", {"start": v(5.2, -16.57) * mm, "end": v(5.2, -16.53) * mm});
            skLineSegment(sketch, "E473", {"start": v(5.2, -16.53) * mm, "end": v(5.2, -16.48) * mm});
            skLineSegment(sketch, "E474", {"start": v(5.2, -16.48) * mm, "end": v(5.2, -16.42) * mm});
            skLineSegment(sketch, "E475", {"start": v(5.2, -16.42) * mm, "end": v(5.19, -16.37) * mm});
            skLineSegment(sketch, "E476", {"start": v(8.38, -17.66) * mm, "end": v(8.36, -17.54) * mm});
            skLineSegment(sketch, "E477", {"start": v(8.36, -17.54) * mm, "end": v(8.32, -17.44) * mm});
            skLineSegment(sketch, "E478", {"start": v(8.32, -17.44) * mm, "end": v(8.27, -17.35) * mm});
            skLineSegment(sketch, "E479", {"start": v(8.27, -17.35) * mm, "end": v(8.21, -17.28) * mm});
            skLineSegment(sketch, "E480", {"start": v(8.21, -17.28) * mm, "end": v(8.14, -17.24) * mm});
            skLineSegment(sketch, "E481", {"start": v(8.14, -17.24) * mm, "end": v(8.06, -17.22) * mm});
            skLineSegment(sketch, "E482", {"start": v(8.06, -17.22) * mm, "end": v(8.02, -17.23) * mm});
            skLineSegment(sketch, "E483", {"start": v(8.02, -17.23) * mm, "end": v(7.98, -17.24) * mm});
            skLineSegment(sketch, "E484", {"start": v(7.98, -17.24) * mm, "end": v(7.94, -17.25) * mm});
            skLineSegment(sketch, "E485", {"start": v(7.94, -17.25) * mm, "end": v(7.9, -17.28) * mm});
            skLineSegment(sketch, "E486", {"start": v(7.9, -17.28) * mm, "end": v(7.86, -17.3) * mm});
            skLineSegment(sketch, "E487", {"start": v(7.86, -17.3) * mm, "end": v(7.83, -17.34) * mm});
            skLineSegment(sketch, "E488", {"start": v(7.83, -17.34) * mm, "end": v(7.8, -17.38) * mm});
            skLineSegment(sketch, "E489", {"start": v(7.8, -17.38) * mm, "end": v(7.78, -17.43) * mm});
            skLineSegment(sketch, "E490", {"start": v(7.78, -17.43) * mm, "end": v(7.7, -17.37) * mm});
            skLineSegment(sketch, "E491", {"start": v(7.7, -17.37) * mm, "end": v(7.62, -17.32) * mm});
            skLineSegment(sketch, "E492", {"start": v(7.62, -17.32) * mm, "end": v(7.53, -17.28) * mm});
            skLineSegment(sketch, "E493", {"start": v(7.53, -17.28) * mm, "end": v(7.44, -17.24) * mm});
            skLineSegment(sketch, "E494", {"start": v(7.44, -17.24) * mm, "end": v(7.35, -17.21) * mm});
            skLineSegment(sketch, "E495", {"start": v(7.35, -17.21) * mm, "end": v(7.26, -17.2) * mm});
            skLineSegment(sketch, "E496", {"start": v(7.26, -17.2) * mm, "end": v(7.16, -17.18) * mm});
            skLineSegment(sketch, "E497", {"start": v(7.16, -17.18) * mm, "end": v(7.05, -17.17) * mm});
            skLineSegment(sketch, "E498", {"start": v(7.05, -17.17) * mm, "end": v(7.05, -17.17) * mm});
            skLineSegment(sketch, "E499", {"start": v(7.05, -17.17) * mm, "end": v(7.04, -17.17) * mm});
            skLineSegment(sketch, "E500", {"start": v(7.04, -17.17) * mm, "end": v(7.04, -17.17) * mm});
            skLineSegment(sketch, "E501", {"start": v(7.04, -17.17) * mm, "end": v(7.03, -17.17) * mm});
            skLineSegment(sketch, "E502", {"start": v(7.03, -17.17) * mm, "end": v(7.02, -17.17) * mm});
            skLineSegment(sketch, "E503", {"start": v(7.02, -17.17) * mm, "end": v(7.02, -17.17) * mm});
            skLineSegment(sketch, "E504", {"start": v(7.02, -17.17) * mm, "end": v(7.01, -17.17) * mm});
            skLineSegment(sketch, "E505", {"start": v(7.01, -17.17) * mm, "end": v(7, -17.17) * mm});
            skLineSegment(sketch, "E506", {"start": v(7, -17.17) * mm, "end": v(6.87, -17.18) * mm});
            skLineSegment(sketch, "E507", {"start": v(6.87, -17.18) * mm, "end": v(6.74, -17.2) * mm});
            skLineSegment(sketch, "E508", {"start": v(6.74, -17.2) * mm, "end": v(6.62, -17.23) * mm});
            skLineSegment(sketch, "E509", {"start": v(6.62, -17.23) * mm, "end": v(6.5, -17.28) * mm});
            skLineSegment(sketch, "E510", {"start": v(6.5, -17.28) * mm, "end": v(6.4, -17.34) * mm});
            skLineSegment(sketch, "E511", {"start": v(6.4, -17.34) * mm, "end": v(6.3, -17.4) * mm});
            skLineSegment(sketch, "E512", {"start": v(6.3, -17.4) * mm, "end": v(6.2, -17.5) * mm});
            skLineSegment(sketch, "E513", {"start": v(6.2, -17.5) * mm, "end": v(6.1, -17.6) * mm});
            skLineSegment(sketch, "E514", {"start": v(6.1, -17.6) * mm, "end": v(6.03, -17.7) * mm});
            skLineSegment(sketch, "E515", {"start": v(6.03, -17.7) * mm, "end": v(5.96, -17.8) * mm});
            skLineSegment(sketch, "E516", {"start": v(5.96, -17.8) * mm, "end": v(5.9, -17.92) * mm});
            skLineSegment(sketch, "E517", {"start": v(5.9, -17.92) * mm, "end": v(5.86, -18.04) * mm});
            skLineSegment(sketch, "E518", {"start": v(5.86, -18.04) * mm, "end": v(5.82, -18.16) * mm});
            skLineSegment(sketch, "E519", {"start": v(5.82, -18.16) * mm, "end": v(5.8, -18.29) * mm});
            skLineSegment(sketch, "E520", {"start": v(5.8, -18.29) * mm, "end": v(5.78, -18.42) * mm});
            skLineSegment(sketch, "E521", {"start": v(5.78, -18.42) * mm, "end": v(5.78, -18.56) * mm});
            skLineSegment(sketch, "E522", {"start": v(5.78, -18.56) * mm, "end": v(5.78, -18.7) * mm});
            skLineSegment(sketch, "E523", {"start": v(5.78, -18.7) * mm, "end": v(5.8, -18.83) * mm});
            skLineSegment(sketch, "E524", {"start": v(5.8, -18.83) * mm, "end": v(5.83, -18.96) * mm});
            skLineSegment(sketch, "E525", {"start": v(5.83, -18.96) * mm, "end": v(5.87, -19.08) * mm});
            skLineSegment(sketch, "E526", {"start": v(5.87, -19.08) * mm, "end": v(5.92, -19.2) * mm});
            skLineSegment(sketch, "E527", {"start": v(5.92, -19.2) * mm, "end": v(5.98, -19.31) * mm});
            skLineSegment(sketch, "E528", {"start": v(5.98, -19.31) * mm, "end": v(6.05, -19.42) * mm});
            skLineSegment(sketch, "E529", {"start": v(6.05, -19.42) * mm, "end": v(6.13, -19.52) * mm});
            skLineSegment(sketch, "E530", {"start": v(6.13, -19.52) * mm, "end": v(6.22, -19.62) * mm});
            skLineSegment(sketch, "E531", {"start": v(6.22, -19.62) * mm, "end": v(6.32, -19.7) * mm});
            skLineSegment(sketch, "E532", {"start": v(6.32, -19.7) * mm, "end": v(6.42, -19.78) * mm});
            skLineSegment(sketch, "E533", {"start": v(6.42, -19.78) * mm, "end": v(6.53, -19.84) * mm});
            skLineSegment(sketch, "E534", {"start": v(6.53, -19.84) * mm, "end": v(6.65, -19.89) * mm});
            skLineSegment(sketch, "E535", {"start": v(6.65, -19.89) * mm, "end": v(6.77, -19.92) * mm});
            skLineSegment(sketch, "E536", {"start": v(6.77, -19.92) * mm, "end": v(6.9, -19.94) * mm});
            skLineSegment(sketch, "E537", {"start": v(6.9, -19.94) * mm, "end": v(7.02, -19.95) * mm});
            skLineSegment(sketch, "E538", {"start": v(7.02, -19.95) * mm, "end": v(7.02, -19.95) * mm});
            skLineSegment(sketch, "E539", {"start": v(7.02, -19.95) * mm, "end": v(7.03, -19.95) * mm});
            skLineSegment(sketch, "E540", {"start": v(7.03, -19.95) * mm, "end": v(7.03, -19.95) * mm});
            skLineSegment(sketch, "E541", {"start": v(7.03, -19.95) * mm, "end": v(7.04, -19.95) * mm});
            skLineSegment(sketch, "E542", {"start": v(7.04, -19.95) * mm, "end": v(7.04, -19.95) * mm});
            skLineSegment(sketch, "E543", {"start": v(7.04, -19.95) * mm, "end": v(7.13, -19.95) * mm});
            skLineSegment(sketch, "E544", {"start": v(7.13, -19.95) * mm, "end": v(7.21, -19.94) * mm});
            skLineSegment(sketch, "E545", {"start": v(7.21, -19.94) * mm, "end": v(7.29, -19.93) * mm});
            skLineSegment(sketch, "E546", {"start": v(7.29, -19.93) * mm, "end": v(7.35, -19.92) * mm});
            skLineSegment(sketch, "E547", {"start": v(7.35, -19.92) * mm, "end": v(7.4, -19.91) * mm});
            skLineSegment(sketch, "E548", {"start": v(7.4, -19.91) * mm, "end": v(7.46, -19.9) * mm});
            skLineSegment(sketch, "E549", {"start": v(7.46, -19.9) * mm, "end": v(7.5, -19.88) * mm});
            skLineSegment(sketch, "E550", {"start": v(7.5, -19.88) * mm, "end": v(7.52, -19.86) * mm});
            skLineSegment(sketch, "E551", {"start": v(7.52, -19.86) * mm, "end": v(7.56, -19.84) * mm});
            skLineSegment(sketch, "E552", {"start": v(7.56, -19.84) * mm, "end": v(7.6, -19.81) * mm});
            skLineSegment(sketch, "E553", {"start": v(7.6, -19.81) * mm, "end": v(7.63, -19.79) * mm});
            skLineSegment(sketch, "E554", {"start": v(7.63, -19.79) * mm, "end": v(7.66, -19.77) * mm});
            skLineSegment(sketch, "E555", {"start": v(7.66, -19.77) * mm, "end": v(7.69, -19.75) * mm});
            skLineSegment(sketch, "E556", {"start": v(7.69, -19.75) * mm, "end": v(7.71, -19.73) * mm});
            skLineSegment(sketch, "E557", {"start": v(7.71, -19.73) * mm, "end": v(7.73, -19.72) * mm});
            skLineSegment(sketch, "E558", {"start": v(7.73, -19.72) * mm, "end": v(7.76, -19.7) * mm});
            skLineSegment(sketch, "E559", {"start": v(7.76, -19.7) * mm, "end": v(7.78, -19.74) * mm});
            skLineSegment(sketch, "E560", {"start": v(7.78, -19.74) * mm, "end": v(7.8, -19.78) * mm});
            skLineSegment(sketch, "E561", {"start": v(7.8, -19.78) * mm, "end": v(7.84, -19.8) * mm});
            skLineSegment(sketch, "E562", {"start": v(7.84, -19.8) * mm, "end": v(7.88, -19.83) * mm});
            skLineSegment(sketch, "E563", {"start": v(7.88, -19.83) * mm, "end": v(7.92, -19.85) * mm});
            skLineSegment(sketch, "E564", {"start": v(7.92, -19.85) * mm, "end": v(7.97, -19.87) * mm});
            skLineSegment(sketch, "E565", {"start": v(7.97, -19.87) * mm, "end": v(8.01, -19.87) * mm});
            skLineSegment(sketch, "E566", {"start": v(8.01, -19.87) * mm, "end": v(8.06, -19.88) * mm});
            skLineSegment(sketch, "E567", {"start": v(8.06, -19.88) * mm, "end": v(8.14, -19.86) * mm});
            skLineSegment(sketch, "E568", {"start": v(8.14, -19.86) * mm, "end": v(8.21, -19.82) * mm});
            skLineSegment(sketch, "E569", {"start": v(8.21, -19.82) * mm, "end": v(8.27, -19.75) * mm});
            skLineSegment(sketch, "E570", {"start": v(8.27, -19.75) * mm, "end": v(8.32, -19.66) * mm});
            skLineSegment(sketch, "E571", {"start": v(8.32, -19.66) * mm, "end": v(8.36, -19.56) * mm});
            skLineSegment(sketch, "E572", {"start": v(8.36, -19.56) * mm, "end": v(8.38, -19.44) * mm});
            skLineSegment(sketch, "E573", {"start": v(8.38, -19.44) * mm, "end": v(8.4, -19.31) * mm});
            skLineSegment(sketch, "E574", {"start": v(8.4, -19.31) * mm, "end": v(8.4, -19.19) * mm});
            skLineSegment(sketch, "E575", {"start": v(8.4, -19.19) * mm, "end": v(8.4, -19.03) * mm});
            skLineSegment(sketch, "E576", {"start": v(8.4, -19.03) * mm, "end": v(8.4, -18.87) * mm});
            skLineSegment(sketch, "E577", {"start": v(8.4, -18.87) * mm, "end": v(8.4, -18.7) * mm});
            skLineSegment(sketch, "E578", {"start": v(8.4, -18.7) * mm, "end": v(8.4, -18.55) * mm});
            skLineSegment(sketch, "E579", {"start": v(8.4, -18.55) * mm, "end": v(8.4, -18.4) * mm});
            skLineSegment(sketch, "E580", {"start": v(8.4, -18.4) * mm, "end": v(8.4, -18.23) * mm});
            skLineSegment(sketch, "E581", {"start": v(8.4, -18.23) * mm, "end": v(8.4, -18.07) * mm});
            skLineSegment(sketch, "E582", {"start": v(8.4, -18.07) * mm, "end": v(8.4, -17.91) * mm});
            skLineSegment(sketch, "E583", {"start": v(8.4, -17.91) * mm, "end": v(8.4, -17.79) * mm});
            skLineSegment(sketch, "E584", {"start": v(8.4, -17.79) * mm, "end": v(8.38, -17.66) * mm});
            skLineSegment(sketch, "E585", {"start": v(7.73, -18.61) * mm, "end": v(7.72, -18.69) * mm});
            skLineSegment(sketch, "E586", {"start": v(7.72, -18.69) * mm, "end": v(7.71, -18.76) * mm});
            skLineSegment(sketch, "E587", {"start": v(7.71, -18.76) * mm, "end": v(7.7, -18.82) * mm});
            skLineSegment(sketch, "E588", {"start": v(7.7, -18.82) * mm, "end": v(7.67, -18.89) * mm});
            skLineSegment(sketch, "E589", {"start": v(7.67, -18.89) * mm, "end": v(7.64, -18.95) * mm});
            skLineSegment(sketch, "E590", {"start": v(7.64, -18.95) * mm, "end": v(7.6, -19) * mm});
            skLineSegment(sketch, "E591", {"start": v(7.6, -19) * mm, "end": v(7.56, -19.07) * mm});
            skLineSegment(sketch, "E592", {"start": v(7.56, -19.07) * mm, "end": v(7.52, -19.12) * mm});
            skLineSegment(sketch, "E593", {"start": v(7.52, -19.12) * mm, "end": v(7.47, -19.16) * mm});
            skLineSegment(sketch, "E594", {"start": v(7.47, -19.16) * mm, "end": v(7.42, -19.2) * mm});
            skLineSegment(sketch, "E595", {"start": v(7.42, -19.2) * mm, "end": v(7.36, -19.23) * mm});
            skLineSegment(sketch, "E596", {"start": v(7.36, -19.23) * mm, "end": v(7.3, -19.26) * mm});
            skLineSegment(sketch, "E597", {"start": v(7.3, -19.26) * mm, "end": v(7.24, -19.27) * mm});
            skLineSegment(sketch, "E598", {"start": v(7.24, -19.27) * mm, "end": v(7.17, -19.28) * mm});
            skLineSegment(sketch, "E599", {"start": v(7.17, -19.28) * mm, "end": v(7.1, -19.29) * mm});
            skLineSegment(sketch, "E600", {"start": v(7.1, -19.29) * mm, "end": v(7.03, -19.28) * mm});
            skLineSegment(sketch, "E601", {"start": v(7.03, -19.28) * mm, "end": v(6.97, -19.27) * mm});
            skLineSegment(sketch, "E602", {"start": v(6.97, -19.27) * mm, "end": v(6.9, -19.25) * mm});
            skLineSegment(sketch, "E603", {"start": v(6.9, -19.25) * mm, "end": v(6.85, -19.23) * mm});
            skLineSegment(sketch, "E604", {"start": v(6.85, -19.23) * mm, "end": v(6.8, -19.2) * mm});
            skLineSegment(sketch, "E605", {"start": v(6.8, -19.2) * mm, "end": v(6.74, -19.16) * mm});
            skLineSegment(sketch, "E606", {"start": v(6.74, -19.16) * mm, "end": v(6.7, -19.1) * mm});
            skLineSegment(sketch, "E607", {"start": v(6.7, -19.1) * mm, "end": v(6.65, -19.05) * mm});
            skLineSegment(sketch, "E608", {"start": v(6.65, -19.05) * mm, "end": v(6.6, -19) * mm});
            skLineSegment(sketch, "E609", {"start": v(6.6, -19) * mm, "end": v(6.56, -18.94) * mm});
            skLineSegment(sketch, "E610", {"start": v(6.56, -18.94) * mm, "end": v(6.53, -18.87) * mm});
            skLineSegment(sketch, "E611", {"start": v(6.53, -18.87) * mm, "end": v(6.5, -18.8) * mm});
            skLineSegment(sketch, "E612", {"start": v(6.5, -18.8) * mm, "end": v(6.49, -18.74) * mm});
            skLineSegment(sketch, "E613", {"start": v(6.49, -18.74) * mm, "end": v(6.48, -18.67) * mm});
            skLineSegment(sketch, "E614", {"start": v(6.48, -18.67) * mm, "end": v(6.47, -18.6) * mm});
            skLineSegment(sketch, "E615", {"start": v(6.47, -18.6) * mm, "end": v(6.47, -18.52) * mm});
            skLineSegment(sketch, "E616", {"start": v(6.47, -18.52) * mm, "end": v(6.47, -18.45) * mm});
            skLineSegment(sketch, "E617", {"start": v(6.47, -18.45) * mm, "end": v(6.48, -18.38) * mm});
            skLineSegment(sketch, "E618", {"start": v(6.48, -18.38) * mm, "end": v(6.5, -18.31) * mm});
            skLineSegment(sketch, "E619", {"start": v(6.5, -18.31) * mm, "end": v(6.52, -18.25) * mm});
            skLineSegment(sketch, "E620", {"start": v(6.52, -18.25) * mm, "end": v(6.54, -18.2) * mm});
            skLineSegment(sketch, "E621", {"start": v(6.54, -18.2) * mm, "end": v(6.57, -18.14) * mm});
            skLineSegment(sketch, "E622", {"start": v(6.57, -18.14) * mm, "end": v(6.6, -18.08) * mm});
            skLineSegment(sketch, "E623", {"start": v(6.6, -18.08) * mm, "end": v(6.65, -18.03) * mm});
            skLineSegment(sketch, "E624", {"start": v(6.65, -18.03) * mm, "end": v(6.7, -17.98) * mm});
            skLineSegment(sketch, "E625", {"start": v(6.7, -17.98) * mm, "end": v(6.74, -17.94) * mm});
            skLineSegment(sketch, "E626", {"start": v(6.74, -17.94) * mm, "end": v(6.79, -17.9) * mm});
            skLineSegment(sketch, "E627", {"start": v(6.79, -17.9) * mm, "end": v(6.84, -17.87) * mm});
            skLineSegment(sketch, "E628", {"start": v(6.84, -17.87) * mm, "end": v(6.9, -17.85) * mm});
            skLineSegment(sketch, "E629", {"start": v(6.9, -17.85) * mm, "end": v(6.95, -17.83) * mm});
            skLineSegment(sketch, "E630", {"start": v(6.95, -17.83) * mm, "end": v(7.01, -17.82) * mm});
            skLineSegment(sketch, "E631", {"start": v(7.01, -17.82) * mm, "end": v(7.07, -17.81) * mm});
            skLineSegment(sketch, "E632", {"start": v(7.07, -17.81) * mm, "end": v(7.08, -17.81) * mm});
            skLineSegment(sketch, "E633", {"start": v(7.08, -17.81) * mm, "end": v(7.08, -17.81) * mm});
            skLineSegment(sketch, "E634", {"start": v(7.08, -17.81) * mm, "end": v(7.09, -17.81) * mm});
            skLineSegment(sketch, "E635", {"start": v(7.09, -17.81) * mm, "end": v(7.1, -17.81) * mm});
            skLineSegment(sketch, "E636", {"start": v(7.1, -17.81) * mm, "end": v(7.1, -17.81) * mm});
            skLineSegment(sketch, "E637", {"start": v(7.1, -17.81) * mm, "end": v(7.18, -17.81) * mm});
            skLineSegment(sketch, "E638", {"start": v(7.18, -17.81) * mm, "end": v(7.24, -17.82) * mm});
            skLineSegment(sketch, "E639", {"start": v(7.24, -17.82) * mm, "end": v(7.3, -17.84) * mm});
            skLineSegment(sketch, "E640", {"start": v(7.3, -17.84) * mm, "end": v(7.36, -17.86) * mm});
            skLineSegment(sketch, "E641", {"start": v(7.36, -17.86) * mm, "end": v(7.42, -17.89) * mm});
            skLineSegment(sketch, "E642", {"start": v(7.42, -17.89) * mm, "end": v(7.47, -17.92) * mm});
            skLineSegment(sketch, "E643", {"start": v(7.47, -17.92) * mm, "end": v(7.51, -17.97) * mm});
            skLineSegment(sketch, "E644", {"start": v(7.51, -17.97) * mm, "end": v(7.56, -18.01) * mm});
            skLineSegment(sketch, "E645", {"start": v(7.56, -18.01) * mm, "end": v(7.6, -18.07) * mm});
            skLineSegment(sketch, "E646", {"start": v(7.6, -18.07) * mm, "end": v(7.63, -18.12) * mm});
            skLineSegment(sketch, "E647", {"start": v(7.63, -18.12) * mm, "end": v(7.66, -18.18) * mm});
            skLineSegment(sketch, "E648", {"start": v(7.66, -18.18) * mm, "end": v(7.69, -18.25) * mm});
            skLineSegment(sketch, "E649", {"start": v(7.69, -18.25) * mm, "end": v(7.7, -18.31) * mm});
            skLineSegment(sketch, "E650", {"start": v(7.7, -18.31) * mm, "end": v(7.72, -18.38) * mm});
            skLineSegment(sketch, "E651", {"start": v(7.72, -18.38) * mm, "end": v(7.73, -18.46) * mm});
            skLineSegment(sketch, "E652", {"start": v(7.73, -18.46) * mm, "end": v(7.73, -18.54) * mm});
            skLineSegment(sketch, "E653", {"start": v(7.73, -18.54) * mm, "end": v(7.73, -18.61) * mm});
            skLineSegment(sketch, "E654", {"start": v(-36.57, -7.79) * mm, "end": v(-36.66, -7.43) * mm});
            skLineSegment(sketch, "E655", {"start": v(-36.66, -7.43) * mm, "end": v(-36.8, -7.1) * mm});
            skLineSegment(sketch, "E656", {"start": v(-36.8, -7.1) * mm, "end": v(-36.99, -6.8) * mm});
            skLineSegment(sketch, "E657", {"start": v(-36.99, -6.8) * mm, "end": v(-37.22, -6.52) * mm});
            skLineSegment(sketch, "E658", {"start": v(-37.22, -6.52) * mm, "end": v(-37.5, -6.27) * mm});
            skLineSegment(sketch, "E659", {"start": v(-37.5, -6.27) * mm, "end": v(-37.82, -6.05) * mm});
            skLineSegment(sketch, "E660", {"start": v(-37.82, -6.05) * mm, "end": v(-38.2, -5.86) * mm});
            skLineSegment(sketch, "E661", {"start": v(-38.2, -5.86) * mm, "end": v(-38.39, -5.77) * mm});
            skLineSegment(sketch, "E662", {"start": v(-38.39, -5.77) * mm, "end": v(-38.58, -5.68) * mm});
            skLineSegment(sketch, "E663", {"start": v(-38.58, -5.68) * mm, "end": v(-38.78, -5.59) * mm});
            skLineSegment(sketch, "E664", {"start": v(-38.78, -5.59) * mm, "end": v(-38.97, -5.5) * mm});
            skLineSegment(sketch, "E665", {"start": v(-38.97, -5.5) * mm, "end": v(-39.16, -5.4) * mm});
            skLineSegment(sketch, "E666", {"start": v(-39.16, -5.4) * mm, "end": v(-39.36, -5.32) * mm});
            skLineSegment(sketch, "E667", {"start": v(-39.36, -5.32) * mm, "end": v(-39.55, -5.23) * mm});
            skLineSegment(sketch, "E668", {"start": v(-39.55, -5.23) * mm, "end": v(-39.75, -5.14) * mm});
            skLineSegment(sketch, "E669", {"start": v(-39.75, -5.14) * mm, "end": v(-39.99, -5.01) * mm});
            skLineSegment(sketch, "E670", {"start": v(-39.99, -5.01) * mm, "end": v(-40.2, -4.87) * mm});
            skLineSegment(sketch, "E671", {"start": v(-40.2, -4.87) * mm, "end": v(-40.37, -4.73) * mm});
            skLineSegment(sketch, "E672", {"start": v(-40.37, -4.73) * mm, "end": v(-40.52, -4.56) * mm});
            skLineSegment(sketch, "E673", {"start": v(-40.52, -4.56) * mm, "end": v(-40.63, -4.4) * mm});
            skLineSegment(sketch, "E674", {"start": v(-40.63, -4.4) * mm, "end": v(-40.71, -4.2) * mm});
            skLineSegment(sketch, "E675", {"start": v(-40.71, -4.2) * mm, "end": v(-40.76, -4) * mm});
            skLineSegment(sketch, "E676", {"start": v(-40.76, -4) * mm, "end": v(-40.78, -3.8) * mm});
            skLineSegment(sketch, "E677", {"start": v(-40.78, -3.8) * mm, "end": v(-40.77, -3.66) * mm});
            skLineSegment(sketch, "E678", {"start": v(-40.77, -3.66) * mm, "end": v(-40.75, -3.52) * mm});
            skLineSegment(sketch, "E679", {"start": v(-40.75, -3.52) * mm, "end": v(-40.72, -3.39) * mm});
            skLineSegment(sketch, "E680", {"start": v(-40.72, -3.39) * mm, "end": v(-40.67, -3.26) * mm});
            skLineSegment(sketch, "E681", {"start": v(-40.67, -3.26) * mm, "end": v(-40.6, -3.14) * mm});
            skLineSegment(sketch, "E682", {"start": v(-40.6, -3.14) * mm, "end": v(-40.52, -3.03) * mm});
            skLineSegment(sketch, "E683", {"start": v(-40.52, -3.03) * mm, "end": v(-40.43, -2.92) * mm});
            skLineSegment(sketch, "E684", {"start": v(-40.43, -2.92) * mm, "end": v(-40.32, -2.81) * mm});
            skLineSegment(sketch, "E685", {"start": v(-40.32, -2.81) * mm, "end": v(-40.2, -2.72) * mm});
            skLineSegment(sketch, "E686", {"start": v(-40.2, -2.72) * mm, "end": v(-40.09, -2.64) * mm});
            skLineSegment(sketch, "E687", {"start": v(-40.09, -2.64) * mm, "end": v(-39.97, -2.57) * mm});
            skLineSegment(sketch, "E688", {"start": v(-39.97, -2.57) * mm, "end": v(-39.84, -2.52) * mm});
            skLineSegment(sketch, "E689", {"start": v(-39.84, -2.52) * mm, "end": v(-39.7, -2.47) * mm});
            skLineSegment(sketch, "E690", {"start": v(-39.7, -2.47) * mm, "end": v(-39.56, -2.43) * mm});
            skLineSegment(sketch, "E691", {"start": v(-39.56, -2.43) * mm, "end": v(-39.42, -2.41) * mm});
            skLineSegment(sketch, "E692", {"start": v(-39.42, -2.41) * mm, "end": v(-39.27, -2.4) * mm});
            skLineSegment(sketch, "E693", {"start": v(-39.27, -2.4) * mm, "end": v(-39.08, -2.4) * mm});
            skLineSegment(sketch, "E694", {"start": v(-39.08, -2.4) * mm, "end": v(-38.9, -2.43) * mm});
            skLineSegment(sketch, "E695", {"start": v(-38.9, -2.43) * mm, "end": v(-38.75, -2.47) * mm});
            skLineSegment(sketch, "E696", {"start": v(-38.75, -2.47) * mm, "end": v(-38.61, -2.54) * mm});
            skLineSegment(sketch, "E697", {"start": v(-38.61, -2.54) * mm, "end": v(-38.48, -2.62) * mm});
            skLineSegment(sketch, "E698", {"start": v(-38.48, -2.62) * mm, "end": v(-38.35, -2.72) * mm});
            skLineSegment(sketch, "E699", {"start": v(-38.35, -2.72) * mm, "end": v(-38.22, -2.84) * mm});
            skLineSegment(sketch, "E700", {"start": v(-38.22, -2.84) * mm, "end": v(-38.08, -2.96) * mm});
            skLineSegment(sketch, "E701", {"start": v(-38.08, -2.96) * mm, "end": v(-37.99, -3.04) * mm});
            skLineSegment(sketch, "E702", {"start": v(-37.99, -3.04) * mm, "end": v(-37.89, -3.11) * mm});
            skLineSegment(sketch, "E703", {"start": v(-37.89, -3.11) * mm, "end": v(-37.79, -3.17) * mm});
            skLineSegment(sketch, "E704", {"start": v(-37.79, -3.17) * mm, "end": v(-37.68, -3.22) * mm});
            skLineSegment(sketch, "E705", {"start": v(-37.68, -3.22) * mm, "end": v(-37.58, -3.24) * mm});
            skLineSegment(sketch, "E706", {"start": v(-37.58, -3.24) * mm, "end": v(-37.47, -3.24) * mm});
            skLineSegment(sketch, "E707", {"start": v(-37.47, -3.24) * mm, "end": v(-37.35, -3.2) * mm});
            skLineSegment(sketch, "E708", {"start": v(-37.35, -3.2) * mm, "end": v(-37.23, -3.15) * mm});
            skLineSegment(sketch, "E709", {"start": v(-37.23, -3.15) * mm, "end": v(-37.06, -2.99) * mm});
            skLineSegment(sketch, "E710", {"start": v(-37.06, -2.99) * mm, "end": v(-36.98, -2.83) * mm});
            skLineSegment(sketch, "E711", {"start": v(-36.98, -2.83) * mm, "end": v(-37, -2.67) * mm});
            skLineSegment(sketch, "E712", {"start": v(-37, -2.67) * mm, "end": v(-37.07, -2.51) * mm});
            skLineSegment(sketch, "E713", {"start": v(-37.07, -2.51) * mm, "end": v(-37.2, -2.36) * mm});
            skLineSegment(sketch, "E714", {"start": v(-37.2, -2.36) * mm, "end": v(-37.35, -2.21) * mm});
            skLineSegment(sketch, "E715", {"start": v(-37.35, -2.21) * mm, "end": v(-37.51, -2.07) * mm});
            skLineSegment(sketch, "E716", {"start": v(-37.51, -2.07) * mm, "end": v(-37.67, -1.95) * mm});
            skLineSegment(sketch, "E717", {"start": v(-37.67, -1.95) * mm, "end": v(-37.84, -1.82) * mm});
            skLineSegment(sketch, "E718", {"start": v(-37.84, -1.82) * mm, "end": v(-38.03, -1.72) * mm});
            skLineSegment(sketch, "E719", {"start": v(-38.03, -1.72) * mm, "end": v(-38.22, -1.63) * mm});
            skLineSegment(sketch, "E720", {"start": v(-38.22, -1.63) * mm, "end": v(-38.42, -1.56) * mm});
            skLineSegment(sketch, "E721", {"start": v(-38.42, -1.56) * mm, "end": v(-38.63, -1.5) * mm});
            skLineSegment(sketch, "E722", {"start": v(-38.63, -1.5) * mm, "end": v(-38.84, -1.46) * mm});
            skLineSegment(sketch, "E723", {"start": v(-38.84, -1.46) * mm, "end": v(-39.05, -1.44) * mm});
            skLineSegment(sketch, "E724", {"start": v(-39.05, -1.44) * mm, "end": v(-39.26, -1.43) * mm});
            skLineSegment(sketch, "E725", {"start": v(-39.26, -1.43) * mm, "end": v(-39.51, -1.45) * mm});
            skLineSegment(sketch, "E726", {"start": v(-39.51, -1.45) * mm, "end": v(-39.76, -1.49) * mm});
            skLineSegment(sketch, "E727", {"start": v(-39.76, -1.49) * mm, "end": v(-40, -1.54) * mm});
            skLineSegment(sketch, "E728", {"start": v(-40, -1.54) * mm, "end": v(-40.22, -1.62) * mm});
            skLineSegment(sketch, "E729", {"start": v(-40.22, -1.62) * mm, "end": v(-40.44, -1.72) * mm});
            skLineSegment(sketch, "E730", {"start": v(-40.44, -1.72) * mm, "end": v(-40.65, -1.83) * mm});
            skLineSegment(sketch, "E731", {"start": v(-40.65, -1.83) * mm, "end": v(-40.85, -1.97) * mm});
            skLineSegment(sketch, "E732", {"start": v(-40.85, -1.97) * mm, "end": v(-41.04, -2.13) * mm});
            skLineSegment(sketch, "E733", {"start": v(-41.04, -2.13) * mm, "end": v(-41.22, -2.3) * mm});
            skLineSegment(sketch, "E734", {"start": v(-41.22, -2.3) * mm, "end": v(-41.38, -2.5) * mm});
            skLineSegment(sketch, "E735", {"start": v(-41.38, -2.5) * mm, "end": v(-41.51, -2.69) * mm});
            skLineSegment(sketch, "E736", {"start": v(-41.51, -2.69) * mm, "end": v(-41.62, -2.9) * mm});
            skLineSegment(sketch, "E737", {"start": v(-41.62, -2.9) * mm, "end": v(-41.7, -3.11) * mm});
            skLineSegment(sketch, "E738", {"start": v(-41.7, -3.11) * mm, "end": v(-41.76, -3.34) * mm});
            skLineSegment(sketch, "E739", {"start": v(-41.76, -3.34) * mm, "end": v(-41.8, -3.58) * mm});
            skLineSegment(sketch, "E740", {"start": v(-41.8, -3.58) * mm, "end": v(-41.81, -3.82) * mm});
            skLineSegment(sketch, "E741", {"start": v(-41.81, -3.82) * mm, "end": v(-41.76, -4.18) * mm});
            skLineSegment(sketch, "E742", {"start": v(-41.76, -4.18) * mm, "end": v(-41.64, -4.52) * mm});
            skLineSegment(sketch, "E743", {"start": v(-41.64, -4.52) * mm, "end": v(-41.45, -4.82) * mm});
            skLineSegment(sketch, "E744", {"start": v(-41.45, -4.82) * mm, "end": v(-41.25, -5.1) * mm});
            skLineSegment(sketch, "E745", {"start": v(-41.25, -5.1) * mm, "end": v(-41.04, -5.32) * mm});
            skLineSegment(sketch, "E746", {"start": v(-41.04, -5.32) * mm, "end": v(-40.86, -5.49) * mm});
            skLineSegment(sketch, "E747", {"start": v(-40.86, -5.49) * mm, "end": v(-40.73, -5.6) * mm});
            skLineSegment(sketch, "E748", {"start": v(-40.73, -5.6) * mm, "end": v(-40.68, -5.63) * mm});
            skLineSegment(sketch, "E749", {"start": v(-40.68, -5.63) * mm, "end": v(-40.53, -5.74) * mm});
            skLineSegment(sketch, "E750", {"start": v(-40.53, -5.74) * mm, "end": v(-40.37, -5.85) * mm});
            skLineSegment(sketch, "E751", {"start": v(-40.37, -5.85) * mm, "end": v(-40.19, -5.96) * mm});
            skLineSegment(sketch, "E752", {"start": v(-40.19, -5.96) * mm, "end": v(-40, -6.08) * mm});
            skLineSegment(sketch, "E753", {"start": v(-40, -6.08) * mm, "end": v(-39.81, -6.19) * mm});
            skLineSegment(sketch, "E754", {"start": v(-39.81, -6.19) * mm, "end": v(-39.62, -6.3) * mm});
            skLineSegment(sketch, "E755", {"start": v(-39.62, -6.3) * mm, "end": v(-39.45, -6.38) * mm});
            skLineSegment(sketch, "E756", {"start": v(-39.45, -6.38) * mm, "end": v(-39.29, -6.46) * mm});
            skLineSegment(sketch, "E757", {"start": v(-39.29, -6.46) * mm, "end": v(-39.2, -6.5) * mm});
            skLineSegment(sketch, "E758", {"start": v(-39.2, -6.5) * mm, "end": v(-39.1, -6.55) * mm});
            skLineSegment(sketch, "E759", {"start": v(-39.1, -6.55) * mm, "end": v(-39.01, -6.6) * mm});
            skLineSegment(sketch, "E760", {"start": v(-39.01, -6.6) * mm, "end": v(-38.92, -6.63) * mm});
            skLineSegment(sketch, "E761", {"start": v(-38.92, -6.63) * mm, "end": v(-38.83, -6.68) * mm});
            skLineSegment(sketch, "E762", {"start": v(-38.83, -6.68) * mm, "end": v(-38.73, -6.72) * mm});
            skLineSegment(sketch, "E763", {"start": v(-38.73, -6.72) * mm, "end": v(-38.64, -6.76) * mm});
            skLineSegment(sketch, "E764", {"start": v(-38.64, -6.76) * mm, "end": v(-38.55, -6.8) * mm});
            skLineSegment(sketch, "E765", {"start": v(-38.55, -6.8) * mm, "end": v(-38.33, -6.93) * mm});
            skLineSegment(sketch, "E766", {"start": v(-38.33, -6.93) * mm, "end": v(-38.13, -7.07) * mm});
            skLineSegment(sketch, "E767", {"start": v(-38.13, -7.07) * mm, "end": v(-37.97, -7.23) * mm});
            skLineSegment(sketch, "E768", {"start": v(-37.97, -7.23) * mm, "end": v(-37.83, -7.42) * mm});
            skLineSegment(sketch, "E769", {"start": v(-37.83, -7.42) * mm, "end": v(-37.72, -7.62) * mm});
            skLineSegment(sketch, "E770", {"start": v(-37.72, -7.62) * mm, "end": v(-37.64, -7.85) * mm});
            skLineSegment(sketch, "E771", {"start": v(-37.64, -7.85) * mm, "end": v(-37.6, -8.1) * mm});
            skLineSegment(sketch, "E772", {"start": v(-37.6, -8.1) * mm, "end": v(-37.57, -8.36) * mm});
            skLineSegment(sketch, "E773", {"start": v(-37.57, -8.36) * mm, "end": v(-37.58, -8.54) * mm});
            skLineSegment(sketch, "E774", {"start": v(-37.58, -8.54) * mm, "end": v(-37.6, -8.72) * mm});
            skLineSegment(sketch, "E775", {"start": v(-37.6, -8.72) * mm, "end": v(-37.65, -8.89) * mm});
            skLineSegment(sketch, "E776", {"start": v(-37.65, -8.89) * mm, "end": v(-37.7, -9.05) * mm});
            skLineSegment(sketch, "E777", {"start": v(-37.7, -9.05) * mm, "end": v(-37.78, -9.2) * mm});
            skLineSegment(sketch, "E778", {"start": v(-37.78, -9.2) * mm, "end": v(-37.88, -9.35) * mm});
            skLineSegment(sketch, "E779", {"start": v(-37.88, -9.35) * mm, "end": v(-38, -9.5) * mm});
            skLineSegment(sketch, "E780", {"start": v(-38, -9.5) * mm, "end": v(-38.13, -9.63) * mm});
            skLineSegment(sketch, "E781", {"start": v(-38.13, -9.63) * mm, "end": v(-38.28, -9.75) * mm});
            skLineSegment(sketch, "E782", {"start": v(-38.28, -9.75) * mm, "end": v(-38.43, -9.86) * mm});
            skLineSegment(sketch, "E783", {"start": v(-38.43, -9.86) * mm, "end": v(-38.59, -9.95) * mm});
            skLineSegment(sketch, "E784", {"start": v(-38.59, -9.95) * mm, "end": v(-38.75, -10.02) * mm});
            skLineSegment(sketch, "E785", {"start": v(-38.75, -10.02) * mm, "end": v(-38.92, -10.08) * mm});
            skLineSegment(sketch, "E786", {"start": v(-38.92, -10.08) * mm, "end": v(-39.1, -10.12) * mm});
            skLineSegment(sketch, "E787", {"start": v(-39.1, -10.12) * mm, "end": v(-39.28, -10.14) * mm});
            skLineSegment(sketch, "E788", {"start": v(-39.28, -10.14) * mm, "end": v(-39.47, -10.15) * mm});
            skLineSegment(sketch, "E789", {"start": v(-39.47, -10.15) * mm, "end": v(-39.77, -10.11) * mm});
            skLineSegment(sketch, "E790", {"start": v(-39.77, -10.11) * mm, "end": v(-40.03, -10.03) * mm});
            skLineSegment(sketch, "E791", {"start": v(-40.03, -10.03) * mm, "end": v(-40.26, -9.91) * mm});
            skLineSegment(sketch, "E792", {"start": v(-40.26, -9.91) * mm, "end": v(-40.44, -9.78) * mm});
            skLineSegment(sketch, "E793", {"start": v(-40.44, -9.78) * mm, "end": v(-40.6, -9.64) * mm});
            skLineSegment(sketch, "E794", {"start": v(-40.6, -9.64) * mm, "end": v(-40.7, -9.53) * mm});
            skLineSegment(sketch, "E795", {"start": v(-40.7, -9.53) * mm, "end": v(-40.76, -9.45) * mm});
            skLineSegment(sketch, "E796", {"start": v(-40.76, -9.45) * mm, "end": v(-40.79, -9.41) * mm});
            skLineSegment(sketch, "E797", {"start": v(-40.79, -9.41) * mm, "end": v(-40.88, -9.25) * mm});
            skLineSegment(sketch, "E798", {"start": v(-40.88, -9.25) * mm, "end": v(-40.98, -9.09) * mm});
            skLineSegment(sketch, "E799", {"start": v(-40.98, -9.09) * mm, "end": v(-41.08, -8.92) * mm});
            skLineSegment(sketch, "E800", {"start": v(-41.08, -8.92) * mm, "end": v(-41.18, -8.77) * mm});
            skLineSegment(sketch, "E801", {"start": v(-41.18, -8.77) * mm, "end": v(-41.3, -8.65) * mm});
            skLineSegment(sketch, "E802", {"start": v(-41.3, -8.65) * mm, "end": v(-41.45, -8.57) * mm});
            skLineSegment(sketch, "E803", {"start": v(-41.45, -8.57) * mm, "end": v(-41.62, -8.53) * mm});
            skLineSegment(sketch, "E804", {"start": v(-41.62, -8.53) * mm, "end": v(-41.82, -8.56) * mm});
            skLineSegment(sketch, "E805", {"start": v(-41.82, -8.56) * mm, "end": v(-42.11, -8.72) * mm});
            skLineSegment(sketch, "E806", {"start": v(-42.11, -8.72) * mm, "end": v(-42.23, -8.95) * mm});
            skLineSegment(sketch, "E807", {"start": v(-42.23, -8.95) * mm, "end": v(-42.2, -9.23) * mm});
            skLineSegment(sketch, "E808", {"start": v(-42.2, -9.23) * mm, "end": v(-42.07, -9.54) * mm});
            skLineSegment(sketch, "E809", {"start": v(-42.07, -9.54) * mm, "end": v(-41.87, -9.86) * mm});
            skLineSegment(sketch, "E810", {"start": v(-41.87, -9.86) * mm, "end": v(-41.64, -10.15) * mm});
            skLineSegment(sketch, "E811", {"start": v(-41.64, -10.15) * mm, "end": v(-41.4, -10.4) * mm});
            skLineSegment(sketch, "E812", {"start": v(-41.4, -10.4) * mm, "end": v(-41.21, -10.56) * mm});
            skLineSegment(sketch, "E813", {"start": v(-41.21, -10.56) * mm, "end": v(-41.02, -10.7) * mm});
            skLineSegment(sketch, "E814", {"start": v(-41.02, -10.7) * mm, "end": v(-40.82, -10.82) * mm});
            skLineSegment(sketch, "E815", {"start": v(-40.82, -10.82) * mm, "end": v(-40.6, -10.93) * mm});
            skLineSegment(sketch, "E816", {"start": v(-40.6, -10.93) * mm, "end": v(-40.39, -11) * mm});
            skLineSegment(sketch, "E817", {"start": v(-40.39, -11) * mm, "end": v(-40.16, -11.07) * mm});
            skLineSegment(sketch, "E818", {"start": v(-40.16, -11.07) * mm, "end": v(-39.93, -11.12) * mm});
            skLineSegment(sketch, "E819", {"start": v(-39.93, -11.12) * mm, "end": v(-39.68, -11.15) * mm});
            skLineSegment(sketch, "E820", {"start": v(-39.68, -11.15) * mm, "end": v(-39.43, -11.16) * mm});
            skLineSegment(sketch, "E821", {"start": v(-39.43, -11.16) * mm, "end": v(-39.13, -11.14) * mm});
            skLineSegment(sketch, "E822", {"start": v(-39.13, -11.14) * mm, "end": v(-38.84, -11.1) * mm});
            skLineSegment(sketch, "E823", {"start": v(-38.84, -11.1) * mm, "end": v(-38.56, -11.03) * mm});
            skLineSegment(sketch, "E824", {"start": v(-38.56, -11.03) * mm, "end": v(-38.3, -10.94) * mm});
            skLineSegment(sketch, "E825", {"start": v(-38.3, -10.94) * mm, "end": v(-38.03, -10.81) * mm});
            skLineSegment(sketch, "E826", {"start": v(-38.03, -10.81) * mm, "end": v(-37.79, -10.66) * mm});
            skLineSegment(sketch, "E827", {"start": v(-37.79, -10.66) * mm, "end": v(-37.55, -10.47) * mm});
            skLineSegment(sketch, "E828", {"start": v(-37.55, -10.47) * mm, "end": v(-37.32, -10.26) * mm});
            skLineSegment(sketch, "E829", {"start": v(-37.32, -10.26) * mm, "end": v(-37.12, -10.04) * mm});
            skLineSegment(sketch, "E830", {"start": v(-37.12, -10.04) * mm, "end": v(-36.94, -9.8) * mm});
            skLineSegment(sketch, "E831", {"start": v(-36.94, -9.8) * mm, "end": v(-36.8, -9.55) * mm});
            skLineSegment(sketch, "E832", {"start": v(-36.8, -9.55) * mm, "end": v(-36.68, -9.3) * mm});
            skLineSegment(sketch, "E833", {"start": v(-36.68, -9.3) * mm, "end": v(-36.6, -9.03) * mm});
            skLineSegment(sketch, "E834", {"start": v(-36.6, -9.03) * mm, "end": v(-36.54, -8.75) * mm});
            skLineSegment(sketch, "E835", {"start": v(-36.54, -8.75) * mm, "end": v(-36.51, -8.47) * mm});
            skLineSegment(sketch, "E836", {"start": v(-36.51, -8.47) * mm, "end": v(-36.52, -8.17) * mm});
            skLineSegment(sketch, "E837", {"start": v(-36.52, -8.17) * mm, "end": v(-36.57, -7.79) * mm});
            skLineSegment(sketch, "E838", {"start": v(-30.4, -7) * mm, "end": v(-30.46, -6.77) * mm});
            skLineSegment(sketch, "E839", {"start": v(-30.46, -6.77) * mm, "end": v(-30.56, -6.54) * mm});
            skLineSegment(sketch, "E840", {"start": v(-30.56, -6.54) * mm, "end": v(-30.67, -6.32) * mm});
            skLineSegment(sketch, "E841", {"start": v(-30.67, -6.32) * mm, "end": v(-30.8, -6.11) * mm});
            skLineSegment(sketch, "E842", {"start": v(-30.8, -6.11) * mm, "end": v(-30.97, -5.91) * mm});
            skLineSegment(sketch, "E843", {"start": v(-30.97, -5.91) * mm, "end": v(-31.15, -5.73) * mm});
            skLineSegment(sketch, "E844", {"start": v(-31.15, -5.73) * mm, "end": v(-31.36, -5.56) * mm});
            skLineSegment(sketch, "E845", {"start": v(-31.36, -5.56) * mm, "end": v(-31.57, -5.4) * mm});
            skLineSegment(sketch, "E846", {"start": v(-31.57, -5.4) * mm, "end": v(-31.78, -5.28) * mm});
            skLineSegment(sketch, "E847", {"start": v(-31.78, -5.28) * mm, "end": v(-32.01, -5.18) * mm});
            skLineSegment(sketch, "E848", {"start": v(-32.01, -5.18) * mm, "end": v(-32.25, -5.1) * mm});
            skLineSegment(sketch, "E849", {"start": v(-32.25, -5.1) * mm, "end": v(-32.5, -5.03) * mm});
            skLineSegment(sketch, "E850", {"start": v(-32.5, -5.03) * mm, "end": v(-32.76, -5) * mm});
            skLineSegment(sketch, "E851", {"start": v(-32.76, -5) * mm, "end": v(-33.03, -4.98) * mm});
            skLineSegment(sketch, "E852", {"start": v(-33.03, -4.98) * mm, "end": v(-33.35, -4.98) * mm});
            skLineSegment(sketch, "E853", {"start": v(-33.35, -4.98) * mm, "end": v(-33.65, -5.02) * mm});
            skLineSegment(sketch, "E854", {"start": v(-33.65, -5.02) * mm, "end": v(-33.94, -5.1) * mm});
            skLineSegment(sketch, "E855", {"start": v(-33.94, -5.1) * mm, "end": v(-34.2, -5.2) * mm});
            skLineSegment(sketch, "E856", {"start": v(-34.2, -5.2) * mm, "end": v(-34.46, -5.33) * mm});
            skLineSegment(sketch, "E857", {"start": v(-34.46, -5.33) * mm, "end": v(-34.7, -5.5) * mm});
            skLineSegment(sketch, "E858", {"start": v(-34.7, -5.5) * mm, "end": v(-34.93, -5.69) * mm});
            skLineSegment(sketch, "E859", {"start": v(-34.93, -5.69) * mm, "end": v(-35.13, -5.91) * mm});
            skLineSegment(sketch, "E860", {"start": v(-35.13, -5.91) * mm, "end": v(-35.3, -6.14) * mm});
            skLineSegment(sketch, "E861", {"start": v(-35.3, -6.14) * mm, "end": v(-35.45, -6.38) * mm});
            skLineSegment(sketch, "E862", {"start": v(-35.45, -6.38) * mm, "end": v(-35.58, -6.64) * mm});
            skLineSegment(sketch, "E863", {"start": v(-35.58, -6.64) * mm, "end": v(-35.68, -6.9) * mm});
            skLineSegment(sketch, "E864", {"start": v(-35.68, -6.9) * mm, "end": v(-35.76, -7.18) * mm});
            skLineSegment(sketch, "E865", {"start": v(-35.76, -7.18) * mm, "end": v(-35.82, -7.47) * mm});
            skLineSegment(sketch, "E866", {"start": v(-35.82, -7.47) * mm, "end": v(-35.85, -7.78) * mm});
            skLineSegment(sketch, "E867", {"start": v(-35.85, -7.78) * mm, "end": v(-35.86, -8.1) * mm});
            skLineSegment(sketch, "E868", {"start": v(-35.86, -8.1) * mm, "end": v(-35.85, -8.4) * mm});
            skLineSegment(sketch, "E869", {"start": v(-35.85, -8.4) * mm, "end": v(-35.81, -8.7) * mm});
            skLineSegment(sketch, "E870", {"start": v(-35.81, -8.7) * mm, "end": v(-35.75, -8.98) * mm});
            skLineSegment(sketch, "E871", {"start": v(-35.75, -8.98) * mm, "end": v(-35.67, -9.25) * mm});
            skLineSegment(sketch, "E872", {"start": v(-35.67, -9.25) * mm, "end": v(-35.56, -9.51) * mm});
            skLineSegment(sketch, "E873", {"start": v(-35.56, -9.51) * mm, "end": v(-35.43, -9.76) * mm});
            skLineSegment(sketch, "E874", {"start": v(-35.43, -9.76) * mm, "end": v(-35.28, -10) * mm});
            skLineSegment(sketch, "E875", {"start": v(-35.28, -10) * mm, "end": v(-35.1, -10.22) * mm});
            skLineSegment(sketch, "E876", {"start": v(-35.1, -10.22) * mm, "end": v(-34.9, -10.43) * mm});
            skLineSegment(sketch, "E877", {"start": v(-34.9, -10.43) * mm, "end": v(-34.68, -10.62) * mm});
            skLineSegment(sketch, "E878", {"start": v(-34.68, -10.62) * mm, "end": v(-34.45, -10.78) * mm});
            skLineSegment(sketch, "E879", {"start": v(-34.45, -10.78) * mm, "end": v(-34.2, -10.91) * mm});
            skLineSegment(sketch, "E880", {"start": v(-34.2, -10.91) * mm, "end": v(-33.93, -11.02) * mm});
            skLineSegment(sketch, "E881", {"start": v(-33.93, -11.02) * mm, "end": v(-33.65, -11.1) * mm});
            skLineSegment(sketch, "E882", {"start": v(-33.65, -11.1) * mm, "end": v(-33.36, -11.14) * mm});
            skLineSegment(sketch, "E883", {"start": v(-33.36, -11.14) * mm, "end": v(-33.05, -11.17) * mm});
            skLineSegment(sketch, "E884", {"start": v(-33.05, -11.17) * mm, "end": v(-32.9, -11.17) * mm});
            skLineSegment(sketch, "E885", {"start": v(-32.9, -11.17) * mm, "end": v(-32.74, -11.15) * mm});
            skLineSegment(sketch, "E886", {"start": v(-32.74, -11.15) * mm, "end": v(-32.58, -11.13) * mm});
            skLineSegment(sketch, "E887", {"start": v(-32.58, -11.13) * mm, "end": v(-32.42, -11.1) * mm});
            skLineSegment(sketch, "E888", {"start": v(-32.42, -11.1) * mm, "end": v(-32.26, -11.06) * mm});
            skLineSegment(sketch, "E889", {"start": v(-32.26, -11.06) * mm, "end": v(-32.1, -11.01) * mm});
            skLineSegment(sketch, "E890", {"start": v(-32.1, -11.01) * mm, "end": v(-31.93, -10.95) * mm});
            skLineSegment(sketch, "E891", {"start": v(-31.93, -10.95) * mm, "end": v(-31.76, -10.88) * mm});
            skLineSegment(sketch, "E892", {"start": v(-31.76, -10.88) * mm, "end": v(-31.57, -10.78) * mm});
            skLineSegment(sketch, "E893", {"start": v(-31.57, -10.78) * mm, "end": v(-31.32, -10.62) * mm});
            skLineSegment(sketch, "E894", {"start": v(-31.32, -10.62) * mm, "end": v(-31.06, -10.42) * mm});
            skLineSegment(sketch, "E895", {"start": v(-31.06, -10.42) * mm, "end": v(-30.81, -10.19) * mm});
            skLineSegment(sketch, "E896", {"start": v(-30.81, -10.19) * mm, "end": v(-30.63, -9.94) * mm});
            skLineSegment(sketch, "E897", {"start": v(-30.63, -9.94) * mm, "end": v(-30.53, -9.7) * mm});
            skLineSegment(sketch, "E898", {"start": v(-30.53, -9.7) * mm, "end": v(-30.57, -9.47) * mm});
            skLineSegment(sketch, "E899", {"start": v(-30.57, -9.47) * mm, "end": v(-30.77, -9.27) * mm});
            skLineSegment(sketch, "E900", {"start": v(-30.77, -9.27) * mm, "end": v(-30.86, -9.23) * mm});
            skLineSegment(sketch, "E901", {"start": v(-30.86, -9.23) * mm, "end": v(-30.95, -9.2) * mm});
            skLineSegment(sketch, "E902", {"start": v(-30.95, -9.2) * mm, "end": v(-31.05, -9.2) * mm});
            skLineSegment(sketch, "E903", {"start": v(-31.05, -9.2) * mm, "end": v(-31.14, -9.22) * mm});
            skLineSegment(sketch, "E904", {"start": v(-31.14, -9.22) * mm, "end": v(-31.23, -9.25) * mm});
            skLineSegment(sketch, "E905", {"start": v(-31.23, -9.25) * mm, "end": v(-31.31, -9.3) * mm});
            skLineSegment(sketch, "E906", {"start": v(-31.31, -9.3) * mm, "end": v(-31.39, -9.35) * mm});
            skLineSegment(sketch, "E907", {"start": v(-31.39, -9.35) * mm, "end": v(-31.45, -9.43) * mm});
            skLineSegment(sketch, "E908", {"start": v(-31.45, -9.43) * mm, "end": v(-31.6, -9.61) * mm});
            skLineSegment(sketch, "E909", {"start": v(-31.6, -9.61) * mm, "end": v(-31.75, -9.78) * mm});
            skLineSegment(sketch, "E910", {"start": v(-31.75, -9.78) * mm, "end": v(-31.92, -9.92) * mm});
            skLineSegment(sketch, "E911", {"start": v(-31.92, -9.92) * mm, "end": v(-32.11, -10.03) * mm});
            skLineSegment(sketch, "E912", {"start": v(-32.11, -10.03) * mm, "end": v(-32.31, -10.12) * mm});
            skLineSegment(sketch, "E913", {"start": v(-32.31, -10.12) * mm, "end": v(-32.53, -10.18) * mm});
            skLineSegment(sketch, "E914", {"start": v(-32.53, -10.18) * mm, "end": v(-32.76, -10.22) * mm});
            skLineSegment(sketch, "E915", {"start": v(-32.76, -10.22) * mm, "end": v(-33, -10.23) * mm});
            skLineSegment(sketch, "E916", {"start": v(-33, -10.23) * mm, "end": v(-33.38, -10.19) * mm});
            skLineSegment(sketch, "E917", {"start": v(-33.38, -10.19) * mm, "end": v(-33.73, -10.07) * mm});
            skLineSegment(sketch, "E918", {"start": v(-33.73, -10.07) * mm, "end": v(-34.04, -9.9) * mm});
            skLineSegment(sketch, "E919", {"start": v(-34.04, -9.9) * mm, "end": v(-34.3, -9.67) * mm});
            skLineSegment(sketch, "E920", {"start": v(-34.3, -9.67) * mm, "end": v(-34.52, -9.39) * mm});
            skLineSegment(sketch, "E921", {"start": v(-34.52, -9.39) * mm, "end": v(-34.69, -9.07) * mm});
            skLineSegment(sketch, "E922", {"start": v(-34.69, -9.07) * mm, "end": v(-34.8, -8.72) * mm});
            skLineSegment(sketch, "E923", {"start": v(-34.8, -8.72) * mm, "end": v(-34.83, -8.35) * mm});
            skLineSegment(sketch, "E924", {"start": v(-34.83, -8.35) * mm, "end": v(-34.81, -8.33) * mm});
            skLineSegment(sketch, "E925", {"start": v(-34.81, -8.33) * mm, "end": v(-34.76, -8.3) * mm});
            skLineSegment(sketch, "E926", {"start": v(-34.76, -8.3) * mm, "end": v(-34.69, -8.28) * mm});
            skLineSegment(sketch, "E927", {"start": v(-34.69, -8.28) * mm, "end": v(-34.59, -8.27) * mm});
            skLineSegment(sketch, "E928", {"start": v(-34.59, -8.27) * mm, "end": v(-34.47, -8.25) * mm});
            skLineSegment(sketch, "E929", {"start": v(-34.47, -8.25) * mm, "end": v(-34.33, -8.24) * mm});
            skLineSegment(sketch, "E930", {"start": v(-34.33, -8.24) * mm, "end": v(-34.18, -8.23) * mm});
            skLineSegment(sketch, "E931", {"start": v(-34.18, -8.23) * mm, "end": v(-34.01, -8.23) * mm});
            skLineSegment(sketch, "E932", {"start": v(-34.01, -8.23) * mm, "end": v(-33.65, -8.23) * mm});
            skLineSegment(sketch, "E933", {"start": v(-33.65, -8.23) * mm, "end": v(-33.29, -8.23) * mm});
            skLineSegment(sketch, "E934", {"start": v(-33.29, -8.23) * mm, "end": v(-32.92, -8.23) * mm});
            skLineSegment(sketch, "E935", {"start": v(-32.92, -8.23) * mm, "end": v(-32.56, -8.23) * mm});
            skLineSegment(sketch, "E936", {"start": v(-32.56, -8.23) * mm, "end": v(-32.2, -8.23) * mm});
            skLineSegment(sketch, "E937", {"start": v(-32.2, -8.23) * mm, "end": v(-31.83, -8.23) * mm});
            skLineSegment(sketch, "E938", {"start": v(-31.83, -8.23) * mm, "end": v(-31.47, -8.23) * mm});
            skLineSegment(sketch, "E939", {"start": v(-31.47, -8.23) * mm, "end": v(-31.1, -8.23) * mm});
            skLineSegment(sketch, "E940", {"start": v(-31.1, -8.23) * mm, "end": v(-30.95, -8.22) * mm});
            skLineSegment(sketch, "E941", {"start": v(-30.95, -8.22) * mm, "end": v(-30.8, -8.18) * mm});
            skLineSegment(sketch, "E942", {"start": v(-30.8, -8.18) * mm, "end": v(-30.66, -8.11) * mm});
            skLineSegment(sketch, "E943", {"start": v(-30.66, -8.11) * mm, "end": v(-30.54, -8.02) * mm});
            skLineSegment(sketch, "E944", {"start": v(-30.54, -8.02) * mm, "end": v(-30.45, -7.92) * mm});
            skLineSegment(sketch, "E945", {"start": v(-30.45, -7.92) * mm, "end": v(-30.38, -7.8) * mm});
            skLineSegment(sketch, "E946", {"start": v(-30.38, -7.8) * mm, "end": v(-30.34, -7.66) * mm});
            skLineSegment(sketch, "E947", {"start": v(-30.34, -7.66) * mm, "end": v(-30.33, -7.52) * mm});
            skLineSegment(sketch, "E948", {"start": v(-30.33, -7.52) * mm, "end": v(-30.35, -7.26) * mm});
            skLineSegment(sketch, "E949", {"start": v(-30.35, -7.26) * mm, "end": v(-30.4, -7) * mm});
            skLineSegment(sketch, "E950", {"start": v(-31.57, -6.9) * mm, "end": v(-31.6, -7.02) * mm});
            skLineSegment(sketch, "E951", {"start": v(-31.6, -7.02) * mm, "end": v(-31.65, -7.12) * mm});
            skLineSegment(sketch, "E952", {"start": v(-31.65, -7.12) * mm, "end": v(-31.72, -7.22) * mm});
            skLineSegment(sketch, "E953", {"start": v(-31.72, -7.22) * mm, "end": v(-31.81, -7.3) * mm});
            skLineSegment(sketch, "E954", {"start": v(-31.81, -7.3) * mm, "end": v(-31.92, -7.36) * mm});
            skLineSegment(sketch, "E955", {"start": v(-31.92, -7.36) * mm, "end": v(-32.03, -7.4) * mm});
            skLineSegment(sketch, "E956", {"start": v(-32.03, -7.4) * mm, "end": v(-32.16, -7.41) * mm});
            skLineSegment(sketch, "E957", {"start": v(-32.16, -7.41) * mm, "end": v(-32.27, -7.41) * mm});
            skLineSegment(sketch, "E958", {"start": v(-32.27, -7.41) * mm, "end": v(-32.57, -7.41) * mm});
            skLineSegment(sketch, "E959", {"start": v(-32.57, -7.41) * mm, "end": v(-33, -7.41) * mm});
            skLineSegment(sketch, "E960", {"start": v(-33, -7.41) * mm, "end": v(-33.48, -7.41) * mm});
            skLineSegment(sketch, "E961", {"start": v(-33.48, -7.41) * mm, "end": v(-33.96, -7.41) * mm});
            skLineSegment(sketch, "E962", {"start": v(-33.96, -7.41) * mm, "end": v(-34.38, -7.41) * mm});
            skLineSegment(sketch, "E963", {"start": v(-34.38, -7.41) * mm, "end": v(-34.68, -7.41) * mm});
            skLineSegment(sketch, "E964", {"start": v(-34.68, -7.41) * mm, "end": v(-34.79, -7.4) * mm});
            skLineSegment(sketch, "E965", {"start": v(-34.79, -7.4) * mm, "end": v(-34.76, -7.25) * mm});
            skLineSegment(sketch, "E966", {"start": v(-34.76, -7.25) * mm, "end": v(-34.71, -7.1) * mm});
            skLineSegment(sketch, "E967", {"start": v(-34.71, -7.1) * mm, "end": v(-34.66, -6.94) * mm});
            skLineSegment(sketch, "E968", {"start": v(-34.66, -6.94) * mm, "end": v(-34.59, -6.8) * mm});
            skLineSegment(sketch, "E969", {"start": v(-34.59, -6.8) * mm, "end": v(-34.5, -6.67) * mm});
            skLineSegment(sketch, "E970", {"start": v(-34.5, -6.67) * mm, "end": v(-34.4, -6.54) * mm});
            skLineSegment(sketch, "E971", {"start": v(-34.4, -6.54) * mm, "end": v(-34.3, -6.42) * mm});
            skLineSegment(sketch, "E972", {"start": v(-34.3, -6.42) * mm, "end": v(-34.18, -6.31) * mm});
            skLineSegment(sketch, "E973", {"start": v(-34.18, -6.31) * mm, "end": v(-34.01, -6.2) * mm});
            skLineSegment(sketch, "E974", {"start": v(-34.01, -6.2) * mm, "end": v(-33.84, -6.1) * mm});
            skLineSegment(sketch, "E975", {"start": v(-33.84, -6.1) * mm, "end": v(-33.65, -6.02) * mm});
            skLineSegment(sketch, "E976", {"start": v(-33.65, -6.02) * mm, "end": v(-33.46, -5.96) * mm});
            skLineSegment(sketch, "E977", {"start": v(-33.46, -5.96) * mm, "end": v(-33.26, -5.93) * mm});
            skLineSegment(sketch, "E978", {"start": v(-33.26, -5.93) * mm, "end": v(-33.06, -5.92) * mm});
            skLineSegment(sketch, "E979", {"start": v(-33.06, -5.92) * mm, "end": v(-32.86, -5.92) * mm});
            skLineSegment(sketch, "E980", {"start": v(-32.86, -5.92) * mm, "end": v(-32.66, -5.95) * mm});
            skLineSegment(sketch, "E981", {"start": v(-32.66, -5.95) * mm, "end": v(-32.5, -5.99) * mm});
            skLineSegment(sketch, "E982", {"start": v(-32.5, -5.99) * mm, "end": v(-32.31, -6.04) * mm});
            skLineSegment(sketch, "E983", {"start": v(-32.31, -6.04) * mm, "end": v(-32.14, -6.11) * mm});
            skLineSegment(sketch, "E984", {"start": v(-32.14, -6.11) * mm, "end": v(-31.97, -6.2) * mm});
            skLineSegment(sketch, "E985", {"start": v(-31.97, -6.2) * mm, "end": v(-31.82, -6.31) * mm});
            skLineSegment(sketch, "E986", {"start": v(-31.82, -6.31) * mm, "end": v(-31.7, -6.44) * mm});
            skLineSegment(sketch, "E987", {"start": v(-31.7, -6.44) * mm, "end": v(-31.61, -6.6) * mm});
            skLineSegment(sketch, "E988", {"start": v(-31.61, -6.6) * mm, "end": v(-31.57, -6.78) * mm});
            skLineSegment(sketch, "E989", {"start": v(-31.57, -6.78) * mm, "end": v(-31.57, -6.9) * mm});
            skLineSegment(sketch, "E990", {"start": v(-20.99, -5.42) * mm, "end": v(-21.02, -5.32) * mm});
            skLineSegment(sketch, "E991", {"start": v(-21.02, -5.32) * mm, "end": v(-21.08, -5.24) * mm});
            skLineSegment(sketch, "E992", {"start": v(-21.08, -5.24) * mm, "end": v(-21.15, -5.17) * mm});
            skLineSegment(sketch, "E993", {"start": v(-21.15, -5.17) * mm, "end": v(-21.24, -5.12) * mm});
            skLineSegment(sketch, "E994", {"start": v(-21.24, -5.12) * mm, "end": v(-21.28, -5.1) * mm});
            skLineSegment(sketch, "E995", {"start": v(-21.28, -5.1) * mm, "end": v(-21.33, -5.1) * mm});
            skLineSegment(sketch, "E996", {"start": v(-21.33, -5.1) * mm, "end": v(-21.38, -5.09) * mm});
            skLineSegment(sketch, "E997", {"start": v(-21.38, -5.09) * mm, "end": v(-21.43, -5.08) * mm});
            skLineSegment(sketch, "E998", {"start": v(-21.43, -5.08) * mm, "end": v(-21.48, -5.09) * mm});
            skLineSegment(sketch, "E999", {"start": v(-21.48, -5.09) * mm, "end": v(-21.54, -5.1) * mm});
            skLineSegment(sketch, "E1000", {"start": v(-21.54, -5.1) * mm, "end": v(-21.6, -5.11) * mm});
            skLineSegment(sketch, "E1001", {"start": v(-21.6, -5.11) * mm, "end": v(-21.65, -5.14) * mm});
            skLineSegment(sketch, "E1002", {"start": v(-21.65, -5.14) * mm, "end": v(-21.77, -5.2) * mm});
            skLineSegment(sketch, "E1003", {"start": v(-21.77, -5.2) * mm, "end": v(-21.86, -5.3) * mm});
            skLineSegment(sketch, "E1004", {"start": v(-21.86, -5.3) * mm, "end": v(-21.94, -5.4) * mm});
            skLineSegment(sketch, "E1005", {"start": v(-21.94, -5.4) * mm, "end": v(-22.02, -5.52) * mm});
            skLineSegment(sketch, "E1006", {"start": v(-22.02, -5.52) * mm, "end": v(-22.08, -5.66) * mm});
            skLineSegment(sketch, "E1007", {"start": v(-22.08, -5.66) * mm, "end": v(-22.13, -5.79) * mm});
            skLineSegment(sketch, "E1008", {"start": v(-22.13, -5.79) * mm, "end": v(-22.18, -5.92) * mm});
            skLineSegment(sketch, "E1009", {"start": v(-22.18, -5.92) * mm, "end": v(-22.22, -6.04) * mm});
            skLineSegment(sketch, "E1010", {"start": v(-22.22, -6.04) * mm, "end": v(-22.26, -6.14) * mm});
            skLineSegment(sketch, "E1011", {"start": v(-22.26, -6.14) * mm, "end": v(-22.3, -6.25) * mm});
            skLineSegment(sketch, "E1012", {"start": v(-22.3, -6.25) * mm, "end": v(-22.36, -6.36) * mm});
            skLineSegment(sketch, "E1013", {"start": v(-22.36, -6.36) * mm, "end": v(-22.4, -6.46) * mm});
            skLineSegment(sketch, "E1014", {"start": v(-22.4, -6.46) * mm, "end": v(-22.45, -6.57) * mm});
            skLineSegment(sketch, "E1015", {"start": v(-22.45, -6.57) * mm, "end": v(-22.5, -6.68) * mm});
            skLineSegment(sketch, "E1016", {"start": v(-22.5, -6.68) * mm, "end": v(-22.55, -6.78) * mm});
            skLineSegment(sketch, "E1017", {"start": v(-22.55, -6.78) * mm, "end": v(-22.6, -6.89) * mm});
            skLineSegment(sketch, "E1018", {"start": v(-22.6, -6.89) * mm, "end": v(-22.69, -7.07) * mm});
            skLineSegment(sketch, "E1019", {"start": v(-22.69, -7.07) * mm, "end": v(-22.77, -7.25) * mm});
            skLineSegment(sketch, "E1020", {"start": v(-22.77, -7.25) * mm, "end": v(-22.85, -7.44) * mm});
            skLineSegment(sketch, "E1021", {"start": v(-22.85, -7.44) * mm, "end": v(-22.93, -7.62) * mm});
            skLineSegment(sketch, "E1022", {"start": v(-22.93, -7.62) * mm, "end": v(-23.02, -7.8) * mm});
            skLineSegment(sketch, "E1023", {"start": v(-23.02, -7.8) * mm, "end": v(-23.1, -7.99) * mm});
            skLineSegment(sketch, "E1024", {"start": v(-23.1, -7.99) * mm, "end": v(-23.18, -8.17) * mm});
            skLineSegment(sketch, "E1025", {"start": v(-23.18, -8.17) * mm, "end": v(-23.27, -8.35) * mm});
            skLineSegment(sketch, "E1026", {"start": v(-23.27, -8.35) * mm, "end": v(-23.34, -8.49) * mm});
            skLineSegment(sketch, "E1027", {"start": v(-23.34, -8.49) * mm, "end": v(-23.42, -8.58) * mm});
            skLineSegment(sketch, "E1028", {"start": v(-23.42, -8.58) * mm, "end": v(-23.5, -8.64) * mm});
            skLineSegment(sketch, "E1029", {"start": v(-23.5, -8.64) * mm, "end": v(-23.6, -8.66) * mm});
            skLineSegment(sketch, "E1030", {"start": v(-23.6, -8.66) * mm, "end": v(-23.68, -8.64) * mm});
            skLineSegment(sketch, "E1031", {"start": v(-23.68, -8.64) * mm, "end": v(-23.76, -8.58) * mm});
            skLineSegment(sketch, "E1032", {"start": v(-23.76, -8.58) * mm, "end": v(-23.84, -8.48) * mm});
            skLineSegment(sketch, "E1033", {"start": v(-23.84, -8.48) * mm, "end": v(-23.9, -8.34) * mm});
            skLineSegment(sketch, "E1034", {"start": v(-23.9, -8.34) * mm, "end": v(-24.05, -7.99) * mm});
            skLineSegment(sketch, "E1035", {"start": v(-24.05, -7.99) * mm, "end": v(-24.2, -7.63) * mm});
            skLineSegment(sketch, "E1036", {"start": v(-24.2, -7.63) * mm, "end": v(-24.34, -7.28) * mm});
            skLineSegment(sketch, "E1037", {"start": v(-24.34, -7.28) * mm, "end": v(-24.48, -6.93) * mm});
            skLineSegment(sketch, "E1038", {"start": v(-24.48, -6.93) * mm, "end": v(-24.62, -6.57) * mm});
            skLineSegment(sketch, "E1039", {"start": v(-24.62, -6.57) * mm, "end": v(-24.77, -6.22) * mm});
            skLineSegment(sketch, "E1040", {"start": v(-24.77, -6.22) * mm, "end": v(-24.91, -5.86) * mm});
            skLineSegment(sketch, "E1041", {"start": v(-24.91, -5.86) * mm, "end": v(-25.06, -5.51) * mm});
            skLineSegment(sketch, "E1042", {"start": v(-25.06, -5.51) * mm, "end": v(-25.12, -5.37) * mm});
            skLineSegment(sketch, "E1043", {"start": v(-25.12, -5.37) * mm, "end": v(-25.2, -5.28) * mm});
            skLineSegment(sketch, "E1044", {"start": v(-25.2, -5.28) * mm, "end": v(-25.28, -5.22) * mm});
            skLineSegment(sketch, "E1045", {"start": v(-25.28, -5.22) * mm, "end": v(-25.37, -5.2) * mm});
            skLineSegment(sketch, "E1046", {"start": v(-25.37, -5.2) * mm, "end": v(-25.45, -5.22) * mm});
            skLineSegment(sketch, "E1047", {"start": v(-25.45, -5.22) * mm, "end": v(-25.53, -5.27) * mm});
            skLineSegment(sketch, "E1048", {"start": v(-25.53, -5.27) * mm, "end": v(-25.61, -5.37) * mm});
            skLineSegment(sketch, "E1049", {"start": v(-25.61, -5.37) * mm, "end": v(-25.68, -5.5) * mm});
            skLineSegment(sketch, "E1050", {"start": v(-25.68, -5.5) * mm, "end": v(-25.84, -5.86) * mm});
            skLineSegment(sketch, "E1051", {"start": v(-25.84, -5.86) * mm, "end": v(-25.99, -6.21) * mm});
            skLineSegment(sketch, "E1052", {"start": v(-25.99, -6.21) * mm, "end": v(-26.14, -6.57) * mm});
            skLineSegment(sketch, "E1053", {"start": v(-26.14, -6.57) * mm, "end": v(-26.3, -6.92) * mm});
            skLineSegment(sketch, "E1054", {"start": v(-26.3, -6.92) * mm, "end": v(-26.45, -7.27) * mm});
            skLineSegment(sketch, "E1055", {"start": v(-26.45, -7.27) * mm, "end": v(-26.6, -7.63) * mm});
            skLineSegment(sketch, "E1056", {"start": v(-26.6, -7.63) * mm, "end": v(-26.75, -7.98) * mm});
            skLineSegment(sketch, "E1057", {"start": v(-26.75, -7.98) * mm, "end": v(-26.9, -8.34) * mm});
            skLineSegment(sketch, "E1058", {"start": v(-26.9, -8.34) * mm, "end": v(-26.98, -8.47) * mm});
            skLineSegment(sketch, "E1059", {"start": v(-26.98, -8.47) * mm, "end": v(-27.05, -8.57) * mm});
            skLineSegment(sketch, "E1060", {"start": v(-27.05, -8.57) * mm, "end": v(-27.14, -8.62) * mm});
            skLineSegment(sketch, "E1061", {"start": v(-27.14, -8.62) * mm, "end": v(-27.22, -8.64) * mm});
            skLineSegment(sketch, "E1062", {"start": v(-27.22, -8.64) * mm, "end": v(-27.3, -8.62) * mm});
            skLineSegment(sketch, "E1063", {"start": v(-27.3, -8.62) * mm, "end": v(-27.4, -8.56) * mm});
            skLineSegment(sketch, "E1064", {"start": v(-27.4, -8.56) * mm, "end": v(-27.47, -8.47) * mm});
            skLineSegment(sketch, "E1065", {"start": v(-27.47, -8.47) * mm, "end": v(-27.54, -8.33) * mm});
            skLineSegment(sketch, "E1066", {"start": v(-27.54, -8.33) * mm, "end": v(-27.63, -8.1) * mm});
            skLineSegment(sketch, "E1067", {"start": v(-27.63, -8.1) * mm, "end": v(-27.73, -7.87) * mm});
            skLineSegment(sketch, "E1068", {"start": v(-27.73, -7.87) * mm, "end": v(-27.82, -7.65) * mm});
            skLineSegment(sketch, "E1069", {"start": v(-27.82, -7.65) * mm, "end": v(-27.92, -7.42) * mm});
            skLineSegment(sketch, "E1070", {"start": v(-27.92, -7.42) * mm, "end": v(-28.01, -7.19) * mm});
            skLineSegment(sketch, "E1071", {"start": v(-28.01, -7.19) * mm, "end": v(-28.1, -6.96) * mm});
            skLineSegment(sketch, "E1072", {"start": v(-28.1, -6.96) * mm, "end": v(-28.2, -6.72) * mm});
            skLineSegment(sketch, "E1073", {"start": v(-28.2, -6.72) * mm, "end": v(-28.28, -6.5) * mm});
            skLineSegment(sketch, "E1074", {"start": v(-28.28, -6.5) * mm, "end": v(-28.34, -6.3) * mm});
            skLineSegment(sketch, "E1075", {"start": v(-28.34, -6.3) * mm, "end": v(-28.42, -6.08) * mm});
            skLineSegment(sketch, "E1076", {"start": v(-28.42, -6.08) * mm, "end": v(-28.52, -5.85) * mm});
            skLineSegment(sketch, "E1077", {"start": v(-28.52, -5.85) * mm, "end": v(-28.64, -5.62) * mm});
            skLineSegment(sketch, "E1078", {"start": v(-28.64, -5.62) * mm, "end": v(-28.78, -5.43) * mm});
            skLineSegment(sketch, "E1079", {"start": v(-28.78, -5.43) * mm, "end": v(-28.94, -5.27) * mm});
            skLineSegment(sketch, "E1080", {"start": v(-28.94, -5.27) * mm, "end": v(-29.14, -5.17) * mm});
            skLineSegment(sketch, "E1081", {"start": v(-29.14, -5.17) * mm, "end": v(-29.36, -5.15) * mm});
            skLineSegment(sketch, "E1082", {"start": v(-29.36, -5.15) * mm, "end": v(-29.48, -5.18) * mm});
            skLineSegment(sketch, "E1083", {"start": v(-29.48, -5.18) * mm, "end": v(-29.57, -5.24) * mm});
            skLineSegment(sketch, "E1084", {"start": v(-29.57, -5.24) * mm, "end": v(-29.64, -5.32) * mm});
            skLineSegment(sketch, "E1085", {"start": v(-29.64, -5.32) * mm, "end": v(-29.68, -5.42) * mm});
            skLineSegment(sketch, "E1086", {"start": v(-29.68, -5.42) * mm, "end": v(-29.7, -5.53) * mm});
            skLineSegment(sketch, "E1087", {"start": v(-29.7, -5.53) * mm, "end": v(-29.7, -5.65) * mm});
            skLineSegment(sketch, "E1088", {"start": v(-29.7, -5.65) * mm, "end": v(-29.67, -5.77) * mm});
            skLineSegment(sketch, "E1089", {"start": v(-29.67, -5.77) * mm, "end": v(-29.63, -5.88) * mm});
            skLineSegment(sketch, "E1090", {"start": v(-29.63, -5.88) * mm, "end": v(-29.54, -6.09) * mm});
            skLineSegment(sketch, "E1091", {"start": v(-29.54, -6.09) * mm, "end": v(-29.3, -6.64) * mm});
            skLineSegment(sketch, "E1092", {"start": v(-29.3, -6.64) * mm, "end": v(-28.97, -7.4) * mm});
            skLineSegment(sketch, "E1093", {"start": v(-28.97, -7.4) * mm, "end": v(-28.58, -8.29) * mm});
            skLineSegment(sketch, "E1094", {"start": v(-28.58, -8.29) * mm, "end": v(-28.2, -9.17) * mm});
            skLineSegment(sketch, "E1095", {"start": v(-28.2, -9.17) * mm, "end": v(-27.87, -9.93) * mm});
            skLineSegment(sketch, "E1096", {"start": v(-27.87, -9.93) * mm, "end": v(-27.63, -10.47) * mm});
            skLineSegment(sketch, "E1097", {"start": v(-27.63, -10.47) * mm, "end": v(-27.54, -10.68) * mm});
            skLineSegment(sketch, "E1098", {"start": v(-27.54, -10.68) * mm, "end": v(-27.47, -10.81) * mm});
            skLineSegment(sketch, "E1099", {"start": v(-27.47, -10.81) * mm, "end": v(-27.39, -10.91) * mm});
            skLineSegment(sketch, "E1100", {"start": v(-27.39, -10.91) * mm, "end": v(-27.3, -10.97) * mm});
            skLineSegment(sketch, "E1101", {"start": v(-27.3, -10.97) * mm, "end": v(-27.22, -10.99) * mm});
            skLineSegment(sketch, "E1102", {"start": v(-27.22, -10.99) * mm, "end": v(-27.13, -10.97) * mm});
            skLineSegment(sketch, "E1103", {"start": v(-27.13, -10.97) * mm, "end": v(-27.05, -10.9) * mm});
            skLineSegment(sketch, "E1104", {"start": v(-27.05, -10.9) * mm, "end": v(-26.97, -10.81) * mm});
            skLineSegment(sketch, "E1105", {"start": v(-26.97, -10.81) * mm, "end": v(-26.9, -10.68) * mm});
            skLineSegment(sketch, "E1106", {"start": v(-26.9, -10.68) * mm, "end": v(-26.75, -10.33) * mm});
            skLineSegment(sketch, "E1107", {"start": v(-26.75, -10.33) * mm, "end": v(-26.6, -9.98) * mm});
            skLineSegment(sketch, "E1108", {"start": v(-26.6, -9.98) * mm, "end": v(-26.46, -9.63) * mm});
            skLineSegment(sketch, "E1109", {"start": v(-26.46, -9.63) * mm, "end": v(-26.3, -9.29) * mm});
            skLineSegment(sketch, "E1110", {"start": v(-26.3, -9.29) * mm, "end": v(-26.16, -8.94) * mm});
            skLineSegment(sketch, "E1111", {"start": v(-26.16, -8.94) * mm, "end": v(-26.02, -8.6) * mm});
            skLineSegment(sketch, "E1112", {"start": v(-26.02, -8.6) * mm, "end": v(-25.87, -8.24) * mm});
            skLineSegment(sketch, "E1113", {"start": v(-25.87, -8.24) * mm, "end": v(-25.72, -7.9) * mm});
            skLineSegment(sketch, "E1114", {"start": v(-25.72, -7.9) * mm, "end": v(-25.65, -7.76) * mm});
            skLineSegment(sketch, "E1115", {"start": v(-25.65, -7.76) * mm, "end": v(-25.57, -7.66) * mm});
            skLineSegment(sketch, "E1116", {"start": v(-25.57, -7.66) * mm, "end": v(-25.5, -7.6) * mm});
            skLineSegment(sketch, "E1117", {"start": v(-25.5, -7.6) * mm, "end": v(-25.4, -7.59) * mm});
            skLineSegment(sketch, "E1118", {"start": v(-25.4, -7.59) * mm, "end": v(-25.32, -7.6) * mm});
            skLineSegment(sketch, "E1119", {"start": v(-25.32, -7.6) * mm, "end": v(-25.24, -7.66) * mm});
            skLineSegment(sketch, "E1120", {"start": v(-25.24, -7.66) * mm, "end": v(-25.16, -7.76) * mm});
            skLineSegment(sketch, "E1121", {"start": v(-25.16, -7.76) * mm, "end": v(-25.1, -7.9) * mm});
            skLineSegment(sketch, "E1122", {"start": v(-25.1, -7.9) * mm, "end": v(-24.95, -8.24) * mm});
            skLineSegment(sketch, "E1123", {"start": v(-24.95, -8.24) * mm, "end": v(-24.8, -8.6) * mm});
            skLineSegment(sketch, "E1124", {"start": v(-24.8, -8.6) * mm, "end": v(-24.66, -8.94) * mm});
            skLineSegment(sketch, "E1125", {"start": v(-24.66, -8.94) * mm, "end": v(-24.51, -9.29) * mm});
            skLineSegment(sketch, "E1126", {"start": v(-24.51, -9.29) * mm, "end": v(-24.37, -9.64) * mm});
            skLineSegment(sketch, "E1127", {"start": v(-24.37, -9.64) * mm, "end": v(-24.22, -9.98) * mm});
            skLineSegment(sketch, "E1128", {"start": v(-24.22, -9.98) * mm, "end": v(-24.08, -10.33) * mm});
            skLineSegment(sketch, "E1129", {"start": v(-24.08, -10.33) * mm, "end": v(-23.93, -10.68) * mm});
            skLineSegment(sketch, "E1130", {"start": v(-23.93, -10.68) * mm, "end": v(-23.86, -10.81) * mm});
            skLineSegment(sketch, "E1131", {"start": v(-23.86, -10.81) * mm, "end": v(-23.78, -10.91) * mm});
            skLineSegment(sketch, "E1132", {"start": v(-23.78, -10.91) * mm, "end": v(-23.7, -10.97) * mm});
            skLineSegment(sketch, "E1133", {"start": v(-23.7, -10.97) * mm, "end": v(-23.6, -11) * mm});
            skLineSegment(sketch, "E1134", {"start": v(-23.6, -11) * mm, "end": v(-23.52, -10.98) * mm});
            skLineSegment(sketch, "E1135", {"start": v(-23.52, -10.98) * mm, "end": v(-23.43, -10.92) * mm});
            skLineSegment(sketch, "E1136", {"start": v(-23.43, -10.92) * mm, "end": v(-23.35, -10.83) * mm});
            skLineSegment(sketch, "E1137", {"start": v(-23.35, -10.83) * mm, "end": v(-23.28, -10.7) * mm});
            skLineSegment(sketch, "E1138", {"start": v(-23.28, -10.7) * mm, "end": v(-23, -10.1) * mm});
            skLineSegment(sketch, "E1139", {"start": v(-23, -10.1) * mm, "end": v(-22.71, -9.49) * mm});
            skLineSegment(sketch, "E1140", {"start": v(-22.71, -9.49) * mm, "end": v(-22.43, -8.89) * mm});
            skLineSegment(sketch, "E1141", {"start": v(-22.43, -8.89) * mm, "end": v(-22.15, -8.29) * mm});
            skLineSegment(sketch, "E1142", {"start": v(-22.15, -8.29) * mm, "end": v(-21.87, -7.68) * mm});
            skLineSegment(sketch, "E1143", {"start": v(-21.87, -7.68) * mm, "end": v(-21.6, -7.08) * mm});
            skLineSegment(sketch, "E1144", {"start": v(-21.6, -7.08) * mm, "end": v(-21.3, -6.48) * mm});
            skLineSegment(sketch, "E1145", {"start": v(-21.3, -6.48) * mm, "end": v(-21.03, -5.88) * mm});
            skLineSegment(sketch, "E1146", {"start": v(-21.03, -5.88) * mm, "end": v(-20.99, -5.76) * mm});
            skLineSegment(sketch, "E1147", {"start": v(-20.99, -5.76) * mm, "end": v(-20.97, -5.64) * mm});
            skLineSegment(sketch, "E1148", {"start": v(-20.97, -5.64) * mm, "end": v(-20.97, -5.53) * mm});
            skLineSegment(sketch, "E1149", {"start": v(-20.97, -5.53) * mm, "end": v(-20.99, -5.42) * mm});
            skLineSegment(sketch, "E1150", {"start": v(-18.62, -5.54) * mm, "end": v(-18.65, -5.42) * mm});
            skLineSegment(sketch, "E1151", {"start": v(-18.65, -5.42) * mm, "end": v(-18.7, -5.31) * mm});
            skLineSegment(sketch, "E1152", {"start": v(-18.7, -5.31) * mm, "end": v(-18.79, -5.21) * mm});
            skLineSegment(sketch, "E1153", {"start": v(-18.79, -5.21) * mm, "end": v(-18.87, -5.16) * mm});
            skLineSegment(sketch, "E1154", {"start": v(-18.87, -5.16) * mm, "end": v(-18.96, -5.12) * mm});
            skLineSegment(sketch, "E1155", {"start": v(-18.96, -5.12) * mm, "end": v(-19.06, -5.1) * mm});
            skLineSegment(sketch, "E1156", {"start": v(-19.06, -5.1) * mm, "end": v(-19.15, -5.1) * mm});
            skLineSegment(sketch, "E1157", {"start": v(-19.15, -5.1) * mm, "end": v(-19.25, -5.13) * mm});
            skLineSegment(sketch, "E1158", {"start": v(-19.25, -5.13) * mm, "end": v(-19.34, -5.17) * mm});
            skLineSegment(sketch, "E1159", {"start": v(-19.34, -5.17) * mm, "end": v(-19.42, -5.23) * mm});
            skLineSegment(sketch, "E1160", {"start": v(-19.42, -5.23) * mm, "end": v(-19.5, -5.3) * mm});
            skLineSegment(sketch, "E1161", {"start": v(-19.5, -5.3) * mm, "end": v(-19.54, -5.38) * mm});
            skLineSegment(sketch, "E1162", {"start": v(-19.54, -5.38) * mm, "end": v(-19.57, -5.45) * mm});
            skLineSegment(sketch, "E1163", {"start": v(-19.57, -5.45) * mm, "end": v(-19.6, -5.53) * mm});
            skLineSegment(sketch, "E1164", {"start": v(-19.6, -5.53) * mm, "end": v(-19.62, -5.62) * mm});
            skLineSegment(sketch, "E1165", {"start": v(-19.62, -5.62) * mm, "end": v(-19.64, -5.7) * mm});
            skLineSegment(sketch, "E1166", {"start": v(-19.64, -5.7) * mm, "end": v(-19.65, -5.79) * mm});
            skLineSegment(sketch, "E1167", {"start": v(-19.65, -5.79) * mm, "end": v(-19.65, -5.87) * mm});
            skLineSegment(sketch, "E1168", {"start": v(-19.65, -5.87) * mm, "end": v(-19.65, -5.96) * mm});
            skLineSegment(sketch, "E1169", {"start": v(-19.65, -5.96) * mm, "end": v(-19.65, -6.15) * mm});
            skLineSegment(sketch, "E1170", {"start": v(-19.65, -6.15) * mm, "end": v(-19.65, -6.64) * mm});
            skLineSegment(sketch, "E1171", {"start": v(-19.65, -6.64) * mm, "end": v(-19.65, -7.31) * mm});
            skLineSegment(sketch, "E1172", {"start": v(-19.65, -7.31) * mm, "end": v(-19.66, -8.09) * mm});
            skLineSegment(sketch, "E1173", {"start": v(-19.66, -8.09) * mm, "end": v(-19.66, -8.86) * mm});
            skLineSegment(sketch, "E1174", {"start": v(-19.66, -8.86) * mm, "end": v(-19.66, -9.53) * mm});
            skLineSegment(sketch, "E1175", {"start": v(-19.66, -9.53) * mm, "end": v(-19.66, -10) * mm});
            skLineSegment(sketch, "E1176", {"start": v(-19.66, -10) * mm, "end": v(-19.66, -10.18) * mm});
            skLineSegment(sketch, "E1177", {"start": v(-19.66, -10.18) * mm, "end": v(-19.65, -10.34) * mm});
            skLineSegment(sketch, "E1178", {"start": v(-19.65, -10.34) * mm, "end": v(-19.62, -10.5) * mm});
            skLineSegment(sketch, "E1179", {"start": v(-19.62, -10.5) * mm, "end": v(-19.57, -10.63) * mm});
            skLineSegment(sketch, "E1180", {"start": v(-19.57, -10.63) * mm, "end": v(-19.5, -10.75) * mm});
            skLineSegment(sketch, "E1181", {"start": v(-19.5, -10.75) * mm, "end": v(-19.43, -10.85) * mm});
            skLineSegment(sketch, "E1182", {"start": v(-19.43, -10.85) * mm, "end": v(-19.34, -10.93) * mm});
            skLineSegment(sketch, "E1183", {"start": v(-19.34, -10.93) * mm, "end": v(-19.25, -10.98) * mm});
            skLineSegment(sketch, "E1184", {"start": v(-19.25, -10.98) * mm, "end": v(-19.14, -11) * mm});
            skLineSegment(sketch, "E1185", {"start": v(-19.14, -11) * mm, "end": v(-19.04, -10.98) * mm});
            skLineSegment(sketch, "E1186", {"start": v(-19.04, -10.98) * mm, "end": v(-18.94, -10.93) * mm});
            skLineSegment(sketch, "E1187", {"start": v(-18.94, -10.93) * mm, "end": v(-18.85, -10.85) * mm});
            skLineSegment(sketch, "E1188", {"start": v(-18.85, -10.85) * mm, "end": v(-18.78, -10.76) * mm});
            skLineSegment(sketch, "E1189", {"start": v(-18.78, -10.76) * mm, "end": v(-18.71, -10.63) * mm});
            skLineSegment(sketch, "E1190", {"start": v(-18.71, -10.63) * mm, "end": v(-18.67, -10.5) * mm});
            skLineSegment(sketch, "E1191", {"start": v(-18.67, -10.5) * mm, "end": v(-18.64, -10.34) * mm});
            skLineSegment(sketch, "E1192", {"start": v(-18.64, -10.34) * mm, "end": v(-18.62, -10.18) * mm});
            skLineSegment(sketch, "E1193", {"start": v(-18.62, -10.18) * mm, "end": v(-18.62, -10.08) * mm});
            skLineSegment(sketch, "E1194", {"start": v(-18.62, -10.08) * mm, "end": v(-18.62, -9.97) * mm});
            skLineSegment(sketch, "E1195", {"start": v(-18.62, -9.97) * mm, "end": v(-18.62, -9.86) * mm});
            skLineSegment(sketch, "E1196", {"start": v(-18.62, -9.86) * mm, "end": v(-18.62, -9.76) * mm});
            skLineSegment(sketch, "E1197", {"start": v(-18.62, -9.76) * mm, "end": v(-18.62, -9.65) * mm});
            skLineSegment(sketch, "E1198", {"start": v(-18.62, -9.65) * mm, "end": v(-18.62, -9.55) * mm});
            skLineSegment(sketch, "E1199", {"start": v(-18.62, -9.55) * mm, "end": v(-18.62, -9.44) * mm});
            skLineSegment(sketch, "E1200", {"start": v(-18.62, -9.44) * mm, "end": v(-18.62, -9.34) * mm});
            skLineSegment(sketch, "E1201", {"start": v(-18.62, -9.34) * mm, "end": v(-18.62, -9.05) * mm});
            skLineSegment(sketch, "E1202", {"start": v(-18.62, -9.05) * mm, "end": v(-18.62, -8.76) * mm});
            skLineSegment(sketch, "E1203", {"start": v(-18.62, -8.76) * mm, "end": v(-18.62, -8.47) * mm});
            skLineSegment(sketch, "E1204", {"start": v(-18.62, -8.47) * mm, "end": v(-18.62, -8.19) * mm});
            skLineSegment(sketch, "E1205", {"start": v(-18.62, -8.19) * mm, "end": v(-18.62, -7.9) * mm});
            skLineSegment(sketch, "E1206", {"start": v(-18.62, -7.9) * mm, "end": v(-18.62, -7.61) * mm});
            skLineSegment(sketch, "E1207", {"start": v(-18.62, -7.61) * mm, "end": v(-18.62, -7.32) * mm});
            skLineSegment(sketch, "E1208", {"start": v(-18.62, -7.32) * mm, "end": v(-18.62, -7.04) * mm});
            skLineSegment(sketch, "E1209", {"start": v(-18.62, -7.04) * mm, "end": v(-18.62, -6.93) * mm});
            skLineSegment(sketch, "E1210", {"start": v(-18.62, -6.93) * mm, "end": v(-18.62, -6.82) * mm});
            skLineSegment(sketch, "E1211", {"start": v(-18.62, -6.82) * mm, "end": v(-18.62, -6.72) * mm});
            skLineSegment(sketch, "E1212", {"start": v(-18.62, -6.72) * mm, "end": v(-18.62, -6.6) * mm});
            skLineSegment(sketch, "E1213", {"start": v(-18.62, -6.6) * mm, "end": v(-18.62, -6.5) * mm});
            skLineSegment(sketch, "E1214", {"start": v(-18.62, -6.5) * mm, "end": v(-18.62, -6.4) * mm});
            skLineSegment(sketch, "E1215", {"start": v(-18.62, -6.4) * mm, "end": v(-18.62, -6.29) * mm});
            skLineSegment(sketch, "E1216", {"start": v(-18.62, -6.29) * mm, "end": v(-18.62, -6.18) * mm});
            skLineSegment(sketch, "E1217", {"start": v(-18.62, -6.18) * mm, "end": v(-18.62, -6.06) * mm});
            skLineSegment(sketch, "E1218", {"start": v(-18.62, -6.06) * mm, "end": v(-18.6, -5.93) * mm});
            skLineSegment(sketch, "E1219", {"start": v(-18.6, -5.93) * mm, "end": v(-18.6, -5.8) * mm});
            skLineSegment(sketch, "E1220", {"start": v(-18.6, -5.8) * mm, "end": v(-18.6, -5.67) * mm});
            skLineSegment(sketch, "E1221", {"start": v(-18.6, -5.67) * mm, "end": v(-18.62, -5.54) * mm});
            skLineSegment(sketch, "E1222", {"start": v(-18.46, -2.8) * mm, "end": v(-18.47, -2.72) * mm});
            skLineSegment(sketch, "E1223", {"start": v(-18.47, -2.72) * mm, "end": v(-18.5, -2.65) * mm});
            skLineSegment(sketch, "E1224", {"start": v(-18.5, -2.65) * mm, "end": v(-18.52, -2.59) * mm});
            skLineSegment(sketch, "E1225", {"start": v(-18.52, -2.59) * mm, "end": v(-18.56, -2.53) * mm});
            skLineSegment(sketch, "E1226", {"start": v(-18.56, -2.53) * mm, "end": v(-18.6, -2.48) * mm});
            skLineSegment(sketch, "E1227", {"start": v(-18.6, -2.48) * mm, "end": v(-18.65, -2.43) * mm});
            skLineSegment(sketch, "E1228", {"start": v(-18.65, -2.43) * mm, "end": v(-18.7, -2.38) * mm});
            skLineSegment(sketch, "E1229", {"start": v(-18.7, -2.38) * mm, "end": v(-18.76, -2.35) * mm});
            skLineSegment(sketch, "E1230", {"start": v(-18.76, -2.35) * mm, "end": v(-18.82, -2.31) * mm});
            skLineSegment(sketch, "E1231", {"start": v(-18.82, -2.31) * mm, "end": v(-18.88, -2.29) * mm});
            skLineSegment(sketch, "E1232", {"start": v(-18.88, -2.29) * mm, "end": v(-18.94, -2.27) * mm});
            skLineSegment(sketch, "E1233", {"start": v(-18.94, -2.27) * mm, "end": v(-19, -2.25) * mm});
            skLineSegment(sketch, "E1234", {"start": v(-19, -2.25) * mm, "end": v(-19.08, -2.24) * mm});
            skLineSegment(sketch, "E1235", {"start": v(-19.08, -2.24) * mm, "end": v(-19.15, -2.24) * mm});
            skLineSegment(sketch, "E1236", {"start": v(-19.15, -2.24) * mm, "end": v(-19.22, -2.24) * mm});
            skLineSegment(sketch, "E1237", {"start": v(-19.22, -2.24) * mm, "end": v(-19.29, -2.25) * mm});
            skLineSegment(sketch, "E1238", {"start": v(-19.29, -2.25) * mm, "end": v(-19.35, -2.27) * mm});
            skLineSegment(sketch, "E1239", {"start": v(-19.35, -2.27) * mm, "end": v(-19.41, -2.29) * mm});
            skLineSegment(sketch, "E1240", {"start": v(-19.41, -2.29) * mm, "end": v(-19.47, -2.31) * mm});
            skLineSegment(sketch, "E1241", {"start": v(-19.47, -2.31) * mm, "end": v(-19.53, -2.34) * mm});
            skLineSegment(sketch, "E1242", {"start": v(-19.53, -2.34) * mm, "end": v(-19.58, -2.38) * mm});
            skLineSegment(sketch, "E1243", {"start": v(-19.58, -2.38) * mm, "end": v(-19.63, -2.42) * mm});
            skLineSegment(sketch, "E1244", {"start": v(-19.63, -2.42) * mm, "end": v(-19.69, -2.47) * mm});
            skLineSegment(sketch, "E1245", {"start": v(-19.69, -2.47) * mm, "end": v(-19.73, -2.53) * mm});
            skLineSegment(sketch, "E1246", {"start": v(-19.73, -2.53) * mm, "end": v(-19.77, -2.6) * mm});
            skLineSegment(sketch, "E1247", {"start": v(-19.77, -2.6) * mm, "end": v(-19.8, -2.66) * mm});
            skLineSegment(sketch, "E1248", {"start": v(-19.8, -2.66) * mm, "end": v(-19.83, -2.73) * mm});
            skLineSegment(sketch, "E1249", {"start": v(-19.83, -2.73) * mm, "end": v(-19.85, -2.8) * mm});
            skLineSegment(sketch, "E1250", {"start": v(-19.85, -2.8) * mm, "end": v(-19.86, -2.88) * mm});
            skLineSegment(sketch, "E1251", {"start": v(-19.86, -2.88) * mm, "end": v(-19.86, -2.96) * mm});
            skLineSegment(sketch, "E1252", {"start": v(-19.86, -2.96) * mm, "end": v(-19.86, -3.04) * mm});
            skLineSegment(sketch, "E1253", {"start": v(-19.86, -3.04) * mm, "end": v(-19.85, -3.11) * mm});
            skLineSegment(sketch, "E1254", {"start": v(-19.85, -3.11) * mm, "end": v(-19.83, -3.18) * mm});
            skLineSegment(sketch, "E1255", {"start": v(-19.83, -3.18) * mm, "end": v(-19.8, -3.25) * mm});
            skLineSegment(sketch, "E1256", {"start": v(-19.8, -3.25) * mm, "end": v(-19.77, -3.31) * mm});
            skLineSegment(sketch, "E1257", {"start": v(-19.77, -3.31) * mm, "end": v(-19.73, -3.37) * mm});
            skLineSegment(sketch, "E1258", {"start": v(-19.73, -3.37) * mm, "end": v(-19.69, -3.42) * mm});
            skLineSegment(sketch, "E1259", {"start": v(-19.69, -3.42) * mm, "end": v(-19.64, -3.47) * mm});
            skLineSegment(sketch, "E1260", {"start": v(-19.64, -3.47) * mm, "end": v(-19.58, -3.51) * mm});
            skLineSegment(sketch, "E1261", {"start": v(-19.58, -3.51) * mm, "end": v(-19.53, -3.55) * mm});
            skLineSegment(sketch, "E1262", {"start": v(-19.53, -3.55) * mm, "end": v(-19.47, -3.58) * mm});
            skLineSegment(sketch, "E1263", {"start": v(-19.47, -3.58) * mm, "end": v(-19.41, -3.6) * mm});
            skLineSegment(sketch, "E1264", {"start": v(-19.41, -3.6) * mm, "end": v(-19.35, -3.62) * mm});
            skLineSegment(sketch, "E1265", {"start": v(-19.35, -3.62) * mm, "end": v(-19.28, -3.63) * mm});
            skLineSegment(sketch, "E1266", {"start": v(-19.28, -3.63) * mm, "end": v(-19.21, -3.64) * mm});
            skLineSegment(sketch, "E1267", {"start": v(-19.21, -3.64) * mm, "end": v(-19.14, -3.64) * mm});
            skLineSegment(sketch, "E1268", {"start": v(-19.14, -3.64) * mm, "end": v(-19.07, -3.64) * mm});
            skLineSegment(sketch, "E1269", {"start": v(-19.07, -3.64) * mm, "end": v(-19, -3.63) * mm});
            skLineSegment(sketch, "E1270", {"start": v(-19, -3.63) * mm, "end": v(-18.94, -3.62) * mm});
            skLineSegment(sketch, "E1271", {"start": v(-18.94, -3.62) * mm, "end": v(-18.87, -3.6) * mm});
            skLineSegment(sketch, "E1272", {"start": v(-18.87, -3.6) * mm, "end": v(-18.82, -3.58) * mm});
            skLineSegment(sketch, "E1273", {"start": v(-18.82, -3.58) * mm, "end": v(-18.76, -3.55) * mm});
            skLineSegment(sketch, "E1274", {"start": v(-18.76, -3.55) * mm, "end": v(-18.7, -3.52) * mm});
            skLineSegment(sketch, "E1275", {"start": v(-18.7, -3.52) * mm, "end": v(-18.66, -3.48) * mm});
            skLineSegment(sketch, "E1276", {"start": v(-18.66, -3.48) * mm, "end": v(-18.6, -3.43) * mm});
            skLineSegment(sketch, "E1277", {"start": v(-18.6, -3.43) * mm, "end": v(-18.56, -3.37) * mm});
            skLineSegment(sketch, "E1278", {"start": v(-18.56, -3.37) * mm, "end": v(-18.53, -3.31) * mm});
            skLineSegment(sketch, "E1279", {"start": v(-18.53, -3.31) * mm, "end": v(-18.5, -3.25) * mm});
            skLineSegment(sketch, "E1280", {"start": v(-18.5, -3.25) * mm, "end": v(-18.47, -3.18) * mm});
            skLineSegment(sketch, "E1281", {"start": v(-18.47, -3.18) * mm, "end": v(-18.46, -3.1) * mm});
            skLineSegment(sketch, "E1282", {"start": v(-18.46, -3.1) * mm, "end": v(-18.45, -3.03) * mm});
            skLineSegment(sketch, "E1283", {"start": v(-18.45, -3.03) * mm, "end": v(-18.44, -2.95) * mm});
            skLineSegment(sketch, "E1284", {"start": v(-18.44, -2.95) * mm, "end": v(-18.45, -2.87) * mm});
            skLineSegment(sketch, "E1285", {"start": v(-18.45, -2.87) * mm, "end": v(-18.46, -2.8) * mm});
            skLineSegment(sketch, "E1286", {"start": v(-12.83, -6.76) * mm, "end": v(-12.88, -6.48) * mm});
            skLineSegment(sketch, "E1287", {"start": v(-12.88, -6.48) * mm, "end": v(-12.96, -6.23) * mm});
            skLineSegment(sketch, "E1288", {"start": v(-12.96, -6.23) * mm, "end": v(-13.05, -6) * mm});
            skLineSegment(sketch, "E1289", {"start": v(-13.05, -6) * mm, "end": v(-13.16, -5.79) * mm});
            skLineSegment(sketch, "E1290", {"start": v(-13.16, -5.79) * mm, "end": v(-13.3, -5.6) * mm});
            skLineSegment(sketch, "E1291", {"start": v(-13.3, -5.6) * mm, "end": v(-13.44, -5.45) * mm});
            skLineSegment(sketch, "E1292", {"start": v(-13.44, -5.45) * mm, "end": v(-13.58, -5.34) * mm});
            skLineSegment(sketch, "E1293", {"start": v(-13.58, -5.34) * mm, "end": v(-13.72, -5.24) * mm});
            skLineSegment(sketch, "E1294", {"start": v(-13.72, -5.24) * mm, "end": v(-13.87, -5.16) * mm});
            skLineSegment(sketch, "E1295", {"start": v(-13.87, -5.16) * mm, "end": v(-14.03, -5.1) * mm});
            skLineSegment(sketch, "E1296", {"start": v(-14.03, -5.1) * mm, "end": v(-14.2, -5.04) * mm});
            skLineSegment(sketch, "E1297", {"start": v(-14.2, -5.04) * mm, "end": v(-14.36, -5) * mm});
            skLineSegment(sketch, "E1298", {"start": v(-14.36, -5) * mm, "end": v(-14.54, -4.98) * mm});
            skLineSegment(sketch, "E1299", {"start": v(-14.54, -4.98) * mm, "end": v(-14.72, -4.97) * mm});
            skLineSegment(sketch, "E1300", {"start": v(-14.72, -4.97) * mm, "end": v(-14.84, -4.98) * mm});
            skLineSegment(sketch, "E1301", {"start": v(-14.84, -4.98) * mm, "end": v(-14.95, -4.99) * mm});
            skLineSegment(sketch, "E1302", {"start": v(-14.95, -4.99) * mm, "end": v(-15.07, -5) * mm});
            skLineSegment(sketch, "E1303", {"start": v(-15.07, -5) * mm, "end": v(-15.2, -5.02) * mm});
            skLineSegment(sketch, "E1304", {"start": v(-15.2, -5.02) * mm, "end": v(-15.3, -5.05) * mm});
            skLineSegment(sketch, "E1305", {"start": v(-15.3, -5.05) * mm, "end": v(-15.43, -5.09) * mm});
            skLineSegment(sketch, "E1306", {"start": v(-15.43, -5.09) * mm, "end": v(-15.55, -5.13) * mm});
            skLineSegment(sketch, "E1307", {"start": v(-15.55, -5.13) * mm, "end": v(-15.66, -5.18) * mm});
            skLineSegment(sketch, "E1308", {"start": v(-15.66, -5.18) * mm, "end": v(-15.75, -5.22) * mm});
            skLineSegment(sketch, "E1309", {"start": v(-15.75, -5.22) * mm, "end": v(-15.83, -5.27) * mm});
            skLineSegment(sketch, "E1310", {"start": v(-15.83, -5.27) * mm, "end": v(-15.9, -5.33) * mm});
            skLineSegment(sketch, "E1311", {"start": v(-15.9, -5.33) * mm, "end": v(-15.98, -5.39) * mm});
            skLineSegment(sketch, "E1312", {"start": v(-15.98, -5.39) * mm, "end": v(-16.06, -5.45) * mm});
            skLineSegment(sketch, "E1313", {"start": v(-16.06, -5.45) * mm, "end": v(-16.13, -5.52) * mm});
            skLineSegment(sketch, "E1314", {"start": v(-16.13, -5.52) * mm, "end": v(-16.2, -5.6) * mm});
            skLineSegment(sketch, "E1315", {"start": v(-16.2, -5.6) * mm, "end": v(-16.26, -5.66) * mm});
            skLineSegment(sketch, "E1316", {"start": v(-16.26, -5.66) * mm, "end": v(-16.3, -5.69) * mm});
            skLineSegment(sketch, "E1317", {"start": v(-16.3, -5.69) * mm, "end": v(-16.35, -5.67) * mm});
            skLineSegment(sketch, "E1318", {"start": v(-16.35, -5.67) * mm, "end": v(-16.39, -5.63) * mm});
            skLineSegment(sketch, "E1319", {"start": v(-16.39, -5.63) * mm, "end": v(-16.42, -5.56) * mm});
            skLineSegment(sketch, "E1320", {"start": v(-16.42, -5.56) * mm, "end": v(-16.46, -5.48) * mm});
            skLineSegment(sketch, "E1321", {"start": v(-16.46, -5.48) * mm, "end": v(-16.48, -5.4) * mm});
            skLineSegment(sketch, "E1322", {"start": v(-16.48, -5.4) * mm, "end": v(-16.5, -5.33) * mm});
            skLineSegment(sketch, "E1323", {"start": v(-16.5, -5.33) * mm, "end": v(-16.53, -5.29) * mm});
            skLineSegment(sketch, "E1324", {"start": v(-16.53, -5.29) * mm, "end": v(-16.59, -5.22) * mm});
            skLineSegment(sketch, "E1325", {"start": v(-16.59, -5.22) * mm, "end": v(-16.67, -5.17) * mm});
            skLineSegment(sketch, "E1326", {"start": v(-16.67, -5.17) * mm, "end": v(-16.76, -5.14) * mm});
            skLineSegment(sketch, "E1327", {"start": v(-16.76, -5.14) * mm, "end": v(-16.86, -5.13) * mm});
            skLineSegment(sketch, "E1328", {"start": v(-16.86, -5.13) * mm, "end": v(-16.96, -5.13) * mm});
            skLineSegment(sketch, "E1329", {"start": v(-16.96, -5.13) * mm, "end": v(-17.06, -5.14) * mm});
            skLineSegment(sketch, "E1330", {"start": v(-17.06, -5.14) * mm, "end": v(-17.15, -5.18) * mm});
            skLineSegment(sketch, "E1331", {"start": v(-17.15, -5.18) * mm, "end": v(-17.22, -5.22) * mm});
            skLineSegment(sketch, "E1332", {"start": v(-17.22, -5.22) * mm, "end": v(-17.28, -5.28) * mm});
            skLineSegment(sketch, "E1333", {"start": v(-17.28, -5.28) * mm, "end": v(-17.32, -5.34) * mm});
            skLineSegment(sketch, "E1334", {"start": v(-17.32, -5.34) * mm, "end": v(-17.36, -5.41) * mm});
            skLineSegment(sketch, "E1335", {"start": v(-17.36, -5.41) * mm, "end": v(-17.38, -5.5) * mm});
            skLineSegment(sketch, "E1336", {"start": v(-17.38, -5.5) * mm, "end": v(-17.4, -5.57) * mm});
            skLineSegment(sketch, "E1337", {"start": v(-17.4, -5.57) * mm, "end": v(-17.42, -5.65) * mm});
            skLineSegment(sketch, "E1338", {"start": v(-17.42, -5.65) * mm, "end": v(-17.42, -5.73) * mm});
            skLineSegment(sketch, "E1339", {"start": v(-17.42, -5.73) * mm, "end": v(-17.43, -5.81) * mm});
            skLineSegment(sketch, "E1340", {"start": v(-17.43, -5.81) * mm, "end": v(-17.44, -5.93) * mm});
            skLineSegment(sketch, "E1341", {"start": v(-17.44, -5.93) * mm, "end": v(-17.44, -6.05) * mm});
            skLineSegment(sketch, "E1342", {"start": v(-17.44, -6.05) * mm, "end": v(-17.44, -6.16) * mm});
            skLineSegment(sketch, "E1343", {"start": v(-17.44, -6.16) * mm, "end": v(-17.44, -6.28) * mm});
            skLineSegment(sketch, "E1344", {"start": v(-17.44, -6.28) * mm, "end": v(-17.44, -6.4) * mm});
            skLineSegment(sketch, "E1345", {"start": v(-17.44, -6.4) * mm, "end": v(-17.43, -6.52) * mm});
            skLineSegment(sketch, "E1346", {"start": v(-17.43, -6.52) * mm, "end": v(-17.43, -6.63) * mm});
            skLineSegment(sketch, "E1347", {"start": v(-17.43, -6.63) * mm, "end": v(-17.43, -6.75) * mm});
            skLineSegment(sketch, "E1348", {"start": v(-17.43, -6.75) * mm, "end": v(-17.43, -6.92) * mm});
            skLineSegment(sketch, "E1349", {"start": v(-17.43, -6.92) * mm, "end": v(-17.44, -7.1) * mm});
            skLineSegment(sketch, "E1350", {"start": v(-17.44, -7.1) * mm, "end": v(-17.44, -7.27) * mm});
            skLineSegment(sketch, "E1351", {"start": v(-17.44, -7.27) * mm, "end": v(-17.44, -7.44) * mm});
            skLineSegment(sketch, "E1352", {"start": v(-17.44, -7.44) * mm, "end": v(-17.45, -7.62) * mm});
            skLineSegment(sketch, "E1353", {"start": v(-17.45, -7.62) * mm, "end": v(-17.45, -7.8) * mm});
            skLineSegment(sketch, "E1354", {"start": v(-17.45, -7.8) * mm, "end": v(-17.45, -7.96) * mm});
            skLineSegment(sketch, "E1355", {"start": v(-17.45, -7.96) * mm, "end": v(-17.45, -8.14) * mm});
            skLineSegment(sketch, "E1356", {"start": v(-17.45, -8.14) * mm, "end": v(-17.45, -8.4) * mm});
            skLineSegment(sketch, "E1357", {"start": v(-17.45, -8.4) * mm, "end": v(-17.46, -8.65) * mm});
            skLineSegment(sketch, "E1358", {"start": v(-17.46, -8.65) * mm, "end": v(-17.46, -8.9) * mm});
            skLineSegment(sketch, "E1359", {"start": v(-17.46, -8.9) * mm, "end": v(-17.46, -9.16) * mm});
            skLineSegment(sketch, "E1360", {"start": v(-17.46, -9.16) * mm, "end": v(-17.46, -9.42) * mm});
            skLineSegment(sketch, "E1361", {"start": v(-17.46, -9.42) * mm, "end": v(-17.46, -9.67) * mm});
            skLineSegment(sketch, "E1362", {"start": v(-17.46, -9.67) * mm, "end": v(-17.46, -9.93) * mm});
            skLineSegment(sketch, "E1363", {"start": v(-17.46, -9.93) * mm, "end": v(-17.46, -10.18) * mm});
            skLineSegment(sketch, "E1364", {"start": v(-17.46, -10.18) * mm, "end": v(-17.45, -10.35) * mm});
            skLineSegment(sketch, "E1365", {"start": v(-17.45, -10.35) * mm, "end": v(-17.42, -10.5) * mm});
            skLineSegment(sketch, "E1366", {"start": v(-17.42, -10.5) * mm, "end": v(-17.37, -10.64) * mm});
            skLineSegment(sketch, "E1367", {"start": v(-17.37, -10.64) * mm, "end": v(-17.3, -10.76) * mm});
            skLineSegment(sketch, "E1368", {"start": v(-17.3, -10.76) * mm, "end": v(-17.23, -10.86) * mm});
            skLineSegment(sketch, "E1369", {"start": v(-17.23, -10.86) * mm, "end": v(-17.14, -10.93) * mm});
            skLineSegment(sketch, "E1370", {"start": v(-17.14, -10.93) * mm, "end": v(-17.05, -10.98) * mm});
            skLineSegment(sketch, "E1371", {"start": v(-17.05, -10.98) * mm, "end": v(-16.94, -11) * mm});
            skLineSegment(sketch, "E1372", {"start": v(-16.94, -11) * mm, "end": v(-16.84, -10.98) * mm});
            skLineSegment(sketch, "E1373", {"start": v(-16.84, -10.98) * mm, "end": v(-16.74, -10.93) * mm});
            skLineSegment(sketch, "E1374", {"start": v(-16.74, -10.93) * mm, "end": v(-16.65, -10.86) * mm});
            skLineSegment(sketch, "E1375", {"start": v(-16.65, -10.86) * mm, "end": v(-16.58, -10.76) * mm});
            skLineSegment(sketch, "E1376", {"start": v(-16.58, -10.76) * mm, "end": v(-16.51, -10.64) * mm});
            skLineSegment(sketch, "E1377", {"start": v(-16.51, -10.64) * mm, "end": v(-16.47, -10.5) * mm});
            skLineSegment(sketch, "E1378", {"start": v(-16.47, -10.5) * mm, "end": v(-16.43, -10.35) * mm});
            skLineSegment(sketch, "E1379", {"start": v(-16.43, -10.35) * mm, "end": v(-16.42, -10.18) * mm});
            skLineSegment(sketch, "E1380", {"start": v(-16.42, -10.18) * mm, "end": v(-16.42, -10.14) * mm});
            skLineSegment(sketch, "E1381", {"start": v(-16.42, -10.14) * mm, "end": v(-16.42, -10.09) * mm});
            skLineSegment(sketch, "E1382", {"start": v(-16.42, -10.09) * mm, "end": v(-16.42, -10.04) * mm});
            skLineSegment(sketch, "E1383", {"start": v(-16.42, -10.04) * mm, "end": v(-16.42, -10) * mm});
            skLineSegment(sketch, "E1384", {"start": v(-16.42, -10) * mm, "end": v(-16.42, -9.94) * mm});
            skLineSegment(sketch, "E1385", {"start": v(-16.42, -9.94) * mm, "end": v(-16.42, -9.9) * mm});
            skLineSegment(sketch, "E1386", {"start": v(-16.42, -9.9) * mm, "end": v(-16.42, -9.85) * mm});
            skLineSegment(sketch, "E1387", {"start": v(-16.42, -9.85) * mm, "end": v(-16.42, -9.8) * mm});
            skLineSegment(sketch, "E1388", {"start": v(-16.42, -9.8) * mm, "end": v(-16.42, -9.6) * mm});
            skLineSegment(sketch, "E1389", {"start": v(-16.42, -9.6) * mm, "end": v(-16.42, -9.4) * mm});
            skLineSegment(sketch, "E1390", {"start": v(-16.42, -9.4) * mm, "end": v(-16.42, -9.2) * mm});
            skLineSegment(sketch, "E1391", {"start": v(-16.42, -9.2) * mm, "end": v(-16.42, -9) * mm});
            skLineSegment(sketch, "E1392", {"start": v(-16.42, -9) * mm, "end": v(-16.42, -8.8) * mm});
            skLineSegment(sketch, "E1393", {"start": v(-16.42, -8.8) * mm, "end": v(-16.42, -8.6) * mm});
            skLineSegment(sketch, "E1394", {"start": v(-16.42, -8.6) * mm, "end": v(-16.42, -8.4) * mm});
            skLineSegment(sketch, "E1395", {"start": v(-16.42, -8.4) * mm, "end": v(-16.42, -8.2) * mm});
            skLineSegment(sketch, "E1396", {"start": v(-16.42, -8.2) * mm, "end": v(-16.42, -8.1) * mm});
            skLineSegment(sketch, "E1397", {"start": v(-16.42, -8.1) * mm, "end": v(-16.42, -8.02) * mm});
            skLineSegment(sketch, "E1398", {"start": v(-16.42, -8.02) * mm, "end": v(-16.42, -7.93) * mm});
            skLineSegment(sketch, "E1399", {"start": v(-16.42, -7.93) * mm, "end": v(-16.42, -7.84) * mm});
            skLineSegment(sketch, "E1400", {"start": v(-16.42, -7.84) * mm, "end": v(-16.42, -7.75) * mm});
            skLineSegment(sketch, "E1401", {"start": v(-16.42, -7.75) * mm, "end": v(-16.42, -7.66) * mm});
            skLineSegment(sketch, "E1402", {"start": v(-16.42, -7.66) * mm, "end": v(-16.42, -7.57) * mm});
            skLineSegment(sketch, "E1403", {"start": v(-16.42, -7.57) * mm, "end": v(-16.41, -7.48) * mm});
            skLineSegment(sketch, "E1404", {"start": v(-16.41, -7.48) * mm, "end": v(-16.37, -7.18) * mm});
            skLineSegment(sketch, "E1405", {"start": v(-16.37, -7.18) * mm, "end": v(-16.29, -6.89) * mm});
            skLineSegment(sketch, "E1406", {"start": v(-16.29, -6.89) * mm, "end": v(-16.17, -6.62) * mm});
            skLineSegment(sketch, "E1407", {"start": v(-16.17, -6.62) * mm, "end": v(-16.02, -6.38) * mm});
            skLineSegment(sketch, "E1408", {"start": v(-16.02, -6.38) * mm, "end": v(-15.82, -6.18) * mm});
            skLineSegment(sketch, "E1409", {"start": v(-15.82, -6.18) * mm, "end": v(-15.58, -6.02) * mm});
            skLineSegment(sketch, "E1410", {"start": v(-15.58, -6.02) * mm, "end": v(-15.3, -5.93) * mm});
            skLineSegment(sketch, "E1411", {"start": v(-15.3, -5.93) * mm, "end": v(-14.98, -5.9) * mm});
            skLineSegment(sketch, "E1412", {"start": v(-14.98, -5.9) * mm, "end": v(-14.71, -5.95) * mm});
            skLineSegment(sketch, "E1413", {"start": v(-14.71, -5.95) * mm, "end": v(-14.5, -6.04) * mm});
            skLineSegment(sketch, "E1414", {"start": v(-14.5, -6.04) * mm, "end": v(-14.33, -6.17) * mm});
            skLineSegment(sketch, "E1415", {"start": v(-14.33, -6.17) * mm, "end": v(-14.2, -6.32) * mm});
            skLineSegment(sketch, "E1416", {"start": v(-14.2, -6.32) * mm, "end": v(-14.1, -6.46) * mm});
            skLineSegment(sketch, "E1417", {"start": v(-14.1, -6.46) * mm, "end": v(-14.05, -6.59) * mm});
            skLineSegment(sketch, "E1418", {"start": v(-14.05, -6.59) * mm, "end": v(-14.02, -6.67) * mm});
            skLineSegment(sketch, "E1419", {"start": v(-14.02, -6.67) * mm, "end": v(-14, -6.7) * mm});
            skLineSegment(sketch, "E1420", {"start": v(-14, -6.7) * mm, "end": v(-13.97, -6.88) * mm});
            skLineSegment(sketch, "E1421", {"start": v(-13.97, -6.88) * mm, "end": v(-13.93, -7.08) * mm});
            skLineSegment(sketch, "E1422", {"start": v(-13.93, -7.08) * mm, "end": v(-13.9, -7.29) * mm});
            skLineSegment(sketch, "E1423", {"start": v(-13.9, -7.29) * mm, "end": v(-13.87, -7.5) * mm});
            skLineSegment(sketch, "E1424", {"start": v(-13.87, -7.5) * mm, "end": v(-13.84, -7.72) * mm});
            skLineSegment(sketch, "E1425", {"start": v(-13.84, -7.72) * mm, "end": v(-13.83, -7.93) * mm});
            skLineSegment(sketch, "E1426", {"start": v(-13.83, -7.93) * mm, "end": v(-13.82, -8.13) * mm});
            skLineSegment(sketch, "E1427", {"start": v(-13.82, -8.13) * mm, "end": v(-13.81, -8.31) * mm});
            skLineSegment(sketch, "E1428", {"start": v(-13.81, -8.31) * mm, "end": v(-13.81, -8.55) * mm});
            skLineSegment(sketch, "E1429", {"start": v(-13.81, -8.55) * mm, "end": v(-13.81, -8.78) * mm});
            skLineSegment(sketch, "E1430", {"start": v(-13.81, -8.78) * mm, "end": v(-13.81, -9.02) * mm});
            skLineSegment(sketch, "E1431", {"start": v(-13.81, -9.02) * mm, "end": v(-13.81, -9.25) * mm});
            skLineSegment(sketch, "E1432", {"start": v(-13.81, -9.25) * mm, "end": v(-13.81, -9.48) * mm});
            skLineSegment(sketch, "E1433", {"start": v(-13.81, -9.48) * mm, "end": v(-13.81, -9.72) * mm});
            skLineSegment(sketch, "E1434", {"start": v(-13.81, -9.72) * mm, "end": v(-13.81, -9.95) * mm});
            skLineSegment(sketch, "E1435", {"start": v(-13.81, -9.95) * mm, "end": v(-13.81, -10.19) * mm});
            skLineSegment(sketch, "E1436", {"start": v(-13.81, -10.19) * mm, "end": v(-13.8, -10.35) * mm});
            skLineSegment(sketch, "E1437", {"start": v(-13.8, -10.35) * mm, "end": v(-13.77, -10.5) * mm});
            skLineSegment(sketch, "E1438", {"start": v(-13.77, -10.5) * mm, "end": v(-13.73, -10.64) * mm});
            skLineSegment(sketch, "E1439", {"start": v(-13.73, -10.64) * mm, "end": v(-13.67, -10.76) * mm});
            skLineSegment(sketch, "E1440", {"start": v(-13.67, -10.76) * mm, "end": v(-13.6, -10.86) * mm});
            skLineSegment(sketch, "E1441", {"start": v(-13.6, -10.86) * mm, "end": v(-13.5, -10.94) * mm});
            skLineSegment(sketch, "E1442", {"start": v(-13.5, -10.94) * mm, "end": v(-13.4, -10.98) * mm});
            skLineSegment(sketch, "E1443", {"start": v(-13.4, -10.98) * mm, "end": v(-13.3, -11) * mm});
            skLineSegment(sketch, "E1444", {"start": v(-13.3, -11) * mm, "end": v(-13.2, -10.98) * mm});
            skLineSegment(sketch, "E1445", {"start": v(-13.2, -10.98) * mm, "end": v(-13.1, -10.94) * mm});
            skLineSegment(sketch, "E1446", {"start": v(-13.1, -10.94) * mm, "end": v(-13.02, -10.86) * mm});
            skLineSegment(sketch, "E1447", {"start": v(-13.02, -10.86) * mm, "end": v(-12.95, -10.76) * mm});
            skLineSegment(sketch, "E1448", {"start": v(-12.95, -10.76) * mm, "end": v(-12.88, -10.64) * mm});
            skLineSegment(sketch, "E1449", {"start": v(-12.88, -10.64) * mm, "end": v(-12.84, -10.5) * mm});
            skLineSegment(sketch, "E1450", {"start": v(-12.84, -10.5) * mm, "end": v(-12.8, -10.35) * mm});
            skLineSegment(sketch, "E1451", {"start": v(-12.8, -10.35) * mm, "end": v(-12.8, -10.19) * mm});
            skLineSegment(sketch, "E1452", {"start": v(-12.8, -10.19) * mm, "end": v(-12.8, -9.84) * mm});
            skLineSegment(sketch, "E1453", {"start": v(-12.8, -9.84) * mm, "end": v(-12.8, -9.49) * mm});
            skLineSegment(sketch, "E1454", {"start": v(-12.8, -9.49) * mm, "end": v(-12.8, -9.14) * mm});
            skLineSegment(sketch, "E1455", {"start": v(-12.8, -9.14) * mm, "end": v(-12.8, -8.79) * mm});
            skLineSegment(sketch, "E1456", {"start": v(-12.8, -8.79) * mm, "end": v(-12.8, -8.44) * mm});
            skLineSegment(sketch, "E1457", {"start": v(-12.8, -8.44) * mm, "end": v(-12.8, -8.09) * mm});
            skLineSegment(sketch, "E1458", {"start": v(-12.8, -8.09) * mm, "end": v(-12.8, -7.74) * mm});
            skLineSegment(sketch, "E1459", {"start": v(-12.8, -7.74) * mm, "end": v(-12.8, -7.39) * mm});
            skLineSegment(sketch, "E1460", {"start": v(-12.8, -7.39) * mm, "end": v(-12.8, -7.06) * mm});
            skLineSegment(sketch, "E1461", {"start": v(-12.8, -7.06) * mm, "end": v(-12.83, -6.76) * mm});
            skLineSegment(sketch, "E1462", {"start": v(-6.63, -5.66) * mm, "end": v(-6.68, -5.52) * mm});
            skLineSegment(sketch, "E1463", {"start": v(-6.68, -5.52) * mm, "end": v(-6.74, -5.4) * mm});
            skLineSegment(sketch, "E1464", {"start": v(-6.74, -5.4) * mm, "end": v(-6.81, -5.3) * mm});
            skLineSegment(sketch, "E1465", {"start": v(-6.81, -5.3) * mm, "end": v(-6.9, -5.22) * mm});
            skLineSegment(sketch, "E1466", {"start": v(-6.9, -5.22) * mm, "end": v(-7, -5.17) * mm});
            skLineSegment(sketch, "E1467", {"start": v(-7, -5.17) * mm, "end": v(-7.1, -5.16) * mm});
            skLineSegment(sketch, "E1468", {"start": v(-7.1, -5.16) * mm, "end": v(-7.2, -5.17) * mm});
            skLineSegment(sketch, "E1469", {"start": v(-7.2, -5.17) * mm, "end": v(-7.29, -5.22) * mm});
            skLineSegment(sketch, "E1470", {"start": v(-7.29, -5.22) * mm, "end": v(-7.37, -5.3) * mm});
            skLineSegment(sketch, "E1471", {"start": v(-7.37, -5.3) * mm, "end": v(-7.45, -5.4) * mm});
            skLineSegment(sketch, "E1472", {"start": v(-7.45, -5.4) * mm, "end": v(-7.5, -5.52) * mm});
            skLineSegment(sketch, "E1473", {"start": v(-7.5, -5.52) * mm, "end": v(-7.55, -5.65) * mm});
            skLineSegment(sketch, "E1474", {"start": v(-7.55, -5.65) * mm, "end": v(-7.58, -5.8) * mm});
            skLineSegment(sketch, "E1475", {"start": v(-7.58, -5.8) * mm, "end": v(-7.6, -5.97) * mm});
            skLineSegment(sketch, "E1476", {"start": v(-7.6, -5.97) * mm, "end": v(-7.6, -5.97) * mm});
            skLineSegment(sketch, "E1477", {"start": v(-7.6, -5.97) * mm, "end": v(-7.6, -5.98) * mm});
            skLineSegment(sketch, "E1478", {"start": v(-7.6, -5.98) * mm, "end": v(-7.6, -5.98) * mm});
            skLineSegment(sketch, "E1479", {"start": v(-7.6, -5.98) * mm, "end": v(-7.6, -5.99) * mm});
            skLineSegment(sketch, "E1480", {"start": v(-7.6, -5.99) * mm, "end": v(-7.6, -5.99) * mm});
            skLineSegment(sketch, "E1481", {"start": v(-7.6, -5.99) * mm, "end": v(-7.6, -6) * mm});
            skLineSegment(sketch, "E1482", {"start": v(-7.6, -6) * mm, "end": v(-7.8, -5.78) * mm});
            skLineSegment(sketch, "E1483", {"start": v(-7.8, -5.78) * mm, "end": v(-8, -5.59) * mm});
            skLineSegment(sketch, "E1484", {"start": v(-8, -5.59) * mm, "end": v(-8.23, -5.42) * mm});
            skLineSegment(sketch, "E1485", {"start": v(-8.23, -5.42) * mm, "end": v(-8.46, -5.29) * mm});
            skLineSegment(sketch, "E1486", {"start": v(-8.46, -5.29) * mm, "end": v(-8.7, -5.18) * mm});
            skLineSegment(sketch, "E1487", {"start": v(-8.7, -5.18) * mm, "end": v(-8.96, -5.1) * mm});
            skLineSegment(sketch, "E1488", {"start": v(-8.96, -5.1) * mm, "end": v(-9.23, -5.05) * mm});
            skLineSegment(sketch, "E1489", {"start": v(-9.23, -5.05) * mm, "end": v(-9.5, -5.03) * mm});
            skLineSegment(sketch, "E1490", {"start": v(-9.5, -5.03) * mm, "end": v(-9.81, -5.03) * mm});
            skLineSegment(sketch, "E1491", {"start": v(-9.81, -5.03) * mm, "end": v(-10.1, -5.07) * mm});
            skLineSegment(sketch, "E1492", {"start": v(-10.1, -5.07) * mm, "end": v(-10.38, -5.13) * mm});
            skLineSegment(sketch, "E1493", {"start": v(-10.38, -5.13) * mm, "end": v(-10.64, -5.22) * mm});
            skLineSegment(sketch, "E1494", {"start": v(-10.64, -5.22) * mm, "end": v(-10.9, -5.34) * mm});
            skLineSegment(sketch, "E1495", {"start": v(-10.9, -5.34) * mm, "end": v(-11.13, -5.5) * mm});
            skLineSegment(sketch, "E1496", {"start": v(-11.13, -5.5) * mm, "end": v(-11.36, -5.68) * mm});
            skLineSegment(sketch, "E1497", {"start": v(-11.36, -5.68) * mm, "end": v(-11.57, -5.88) * mm});
            skLineSegment(sketch, "E1498", {"start": v(-11.57, -5.88) * mm, "end": v(-11.76, -6.12) * mm});
            skLineSegment(sketch, "E1499", {"start": v(-11.76, -6.12) * mm, "end": v(-11.93, -6.36) * mm});
            skLineSegment(sketch, "E1500", {"start": v(-11.93, -6.36) * mm, "end": v(-12.07, -6.62) * mm});
            skLineSegment(sketch, "E1501", {"start": v(-12.07, -6.62) * mm, "end": v(-12.18, -6.89) * mm});
            skLineSegment(sketch, "E1502", {"start": v(-12.18, -6.89) * mm, "end": v(-12.27, -7.17) * mm});
            skLineSegment(sketch, "E1503", {"start": v(-12.27, -7.17) * mm, "end": v(-12.34, -7.46) * mm});
            skLineSegment(sketch, "E1504", {"start": v(-12.34, -7.46) * mm, "end": v(-12.38, -7.77) * mm});
            skLineSegment(sketch, "E1505", {"start": v(-12.38, -7.77) * mm, "end": v(-12.4, -8.1) * mm});
            skLineSegment(sketch, "E1506", {"start": v(-12.4, -8.1) * mm, "end": v(-12.38, -8.41) * mm});
            skLineSegment(sketch, "E1507", {"start": v(-12.38, -8.41) * mm, "end": v(-12.35, -8.72) * mm});
            skLineSegment(sketch, "E1508", {"start": v(-12.35, -8.72) * mm, "end": v(-12.29, -9.02) * mm});
            skLineSegment(sketch, "E1509", {"start": v(-12.29, -9.02) * mm, "end": v(-12.2, -9.3) * mm});
            skLineSegment(sketch, "E1510", {"start": v(-12.2, -9.3) * mm, "end": v(-12.1, -9.57) * mm});
            skLineSegment(sketch, "E1511", {"start": v(-12.1, -9.57) * mm, "end": v(-11.97, -9.82) * mm});
            skLineSegment(sketch, "E1512", {"start": v(-11.97, -9.82) * mm, "end": v(-11.82, -10.06) * mm});
            skLineSegment(sketch, "E1513", {"start": v(-11.82, -10.06) * mm, "end": v(-11.65, -10.29) * mm});
            skLineSegment(sketch, "E1514", {"start": v(-11.65, -10.29) * mm, "end": v(-11.45, -10.5) * mm});
            skLineSegment(sketch, "E1515", {"start": v(-11.45, -10.5) * mm, "end": v(-11.24, -10.67) * mm});
            skLineSegment(sketch, "E1516", {"start": v(-11.24, -10.67) * mm, "end": v(-11.02, -10.82) * mm});
            skLineSegment(sketch, "E1517", {"start": v(-11.02, -10.82) * mm, "end": v(-10.78, -10.95) * mm});
            skLineSegment(sketch, "E1518", {"start": v(-10.78, -10.95) * mm, "end": v(-10.53, -11.05) * mm});
            skLineSegment(sketch, "E1519", {"start": v(-10.53, -11.05) * mm, "end": v(-10.26, -11.13) * mm});
            skLineSegment(sketch, "E1520", {"start": v(-10.26, -11.13) * mm, "end": v(-9.98, -11.17) * mm});
            skLineSegment(sketch, "E1521", {"start": v(-9.98, -11.17) * mm, "end": v(-9.68, -11.2) * mm});
            skLineSegment(sketch, "E1522", {"start": v(-9.68, -11.2) * mm, "end": v(-9.39, -11.18) * mm});
            skLineSegment(sketch, "E1523", {"start": v(-9.39, -11.18) * mm, "end": v(-9.12, -11.13) * mm});
            skLineSegment(sketch, "E1524", {"start": v(-9.12, -11.13) * mm, "end": v(-8.88, -11.06) * mm});
            skLineSegment(sketch, "E1525", {"start": v(-8.88, -11.06) * mm, "end": v(-8.68, -10.97) * mm});
            skLineSegment(sketch, "E1526", {"start": v(-8.68, -10.97) * mm, "end": v(-8.5, -10.89) * mm});
            skLineSegment(sketch, "E1527", {"start": v(-8.5, -10.89) * mm, "end": v(-8.38, -10.81) * mm});
            skLineSegment(sketch, "E1528", {"start": v(-8.38, -10.81) * mm, "end": v(-8.3, -10.76) * mm});
            skLineSegment(sketch, "E1529", {"start": v(-8.3, -10.76) * mm, "end": v(-8.27, -10.74) * mm});
            skLineSegment(sketch, "E1530", {"start": v(-8.27, -10.74) * mm, "end": v(-8.14, -10.65) * mm});
            skLineSegment(sketch, "E1531", {"start": v(-8.14, -10.65) * mm, "end": v(-8.02, -10.6) * mm});
            skLineSegment(sketch, "E1532", {"start": v(-8.02, -10.6) * mm, "end": v(-7.91, -10.6) * mm});
            skLineSegment(sketch, "E1533", {"start": v(-7.91, -10.6) * mm, "end": v(-7.82, -10.62) * mm});
            skLineSegment(sketch, "E1534", {"start": v(-7.82, -10.62) * mm, "end": v(-7.74, -10.68) * mm});
            skLineSegment(sketch, "E1535", {"start": v(-7.74, -10.68) * mm, "end": v(-7.68, -10.77) * mm});
            skLineSegment(sketch, "E1536", {"start": v(-7.68, -10.77) * mm, "end": v(-7.65, -10.9) * mm});
            skLineSegment(sketch, "E1537", {"start": v(-7.65, -10.9) * mm, "end": v(-7.63, -11.05) * mm});
            skLineSegment(sketch, "E1538", {"start": v(-7.63, -11.05) * mm, "end": v(-7.63, -11.08) * mm});
            skLineSegment(sketch, "E1539", {"start": v(-7.63, -11.08) * mm, "end": v(-7.63, -11.11) * mm});
            skLineSegment(sketch, "E1540", {"start": v(-7.63, -11.11) * mm, "end": v(-7.63, -11.15) * mm});
            skLineSegment(sketch, "E1541", {"start": v(-7.63, -11.15) * mm, "end": v(-7.63, -11.18) * mm});
            skLineSegment(sketch, "E1542", {"start": v(-7.63, -11.18) * mm, "end": v(-7.63, -11.2) * mm});
            skLineSegment(sketch, "E1543", {"start": v(-7.63, -11.2) * mm, "end": v(-7.63, -11.24) * mm});
            skLineSegment(sketch, "E1544", {"start": v(-7.63, -11.24) * mm, "end": v(-7.63, -11.27) * mm});
            skLineSegment(sketch, "E1545", {"start": v(-7.63, -11.27) * mm, "end": v(-7.63, -11.3) * mm});
            skLineSegment(sketch, "E1546", {"start": v(-7.63, -11.3) * mm, "end": v(-7.66, -11.78) * mm});
            skLineSegment(sketch, "E1547", {"start": v(-7.66, -11.78) * mm, "end": v(-7.75, -12.18) * mm});
            skLineSegment(sketch, "E1548", {"start": v(-7.75, -12.18) * mm, "end": v(-7.9, -12.53) * mm});
            skLineSegment(sketch, "E1549", {"start": v(-7.9, -12.53) * mm, "end": v(-8.1, -12.81) * mm});
            skLineSegment(sketch, "E1550", {"start": v(-8.1, -12.81) * mm, "end": v(-8.37, -13.04) * mm});
            skLineSegment(sketch, "E1551", {"start": v(-8.37, -13.04) * mm, "end": v(-8.69, -13.2) * mm});
            skLineSegment(sketch, "E1552", {"start": v(-8.69, -13.2) * mm, "end": v(-9.07, -13.3) * mm});
            skLineSegment(sketch, "E1553", {"start": v(-9.07, -13.3) * mm, "end": v(-9.5, -13.35) * mm});
            skLineSegment(sketch, "E1554", {"start": v(-9.5, -13.35) * mm, "end": v(-9.69, -13.34) * mm});
            skLineSegment(sketch, "E1555", {"start": v(-9.69, -13.34) * mm, "end": v(-9.86, -13.33) * mm});
            skLineSegment(sketch, "E1556", {"start": v(-9.86, -13.33) * mm, "end": v(-10.03, -13.3) * mm});
            skLineSegment(sketch, "E1557", {"start": v(-10.03, -13.3) * mm, "end": v(-10.2, -13.24) * mm});
            skLineSegment(sketch, "E1558", {"start": v(-10.2, -13.24) * mm, "end": v(-10.35, -13.17) * mm});
            skLineSegment(sketch, "E1559", {"start": v(-10.35, -13.17) * mm, "end": v(-10.5, -13.09) * mm});
            skLineSegment(sketch, "E1560", {"start": v(-10.5, -13.09) * mm, "end": v(-10.64, -12.99) * mm});
            skLineSegment(sketch, "E1561", {"start": v(-10.64, -12.99) * mm, "end": v(-10.77, -12.87) * mm});
            skLineSegment(sketch, "E1562", {"start": v(-10.77, -12.87) * mm, "end": v(-10.9, -12.75) * mm});
            skLineSegment(sketch, "E1563", {"start": v(-10.9, -12.75) * mm, "end": v(-10.98, -12.65) * mm});
            skLineSegment(sketch, "E1564", {"start": v(-10.98, -12.65) * mm, "end": v(-11.05, -12.57) * mm});
            skLineSegment(sketch, "E1565", {"start": v(-11.05, -12.57) * mm, "end": v(-11.1, -12.5) * mm});
            skLineSegment(sketch, "E1566", {"start": v(-11.1, -12.5) * mm, "end": v(-11.13, -12.44) * mm});
            skLineSegment(sketch, "E1567", {"start": v(-11.13, -12.44) * mm, "end": v(-11.15, -12.4) * mm});
            skLineSegment(sketch, "E1568", {"start": v(-11.15, -12.4) * mm, "end": v(-11.16, -12.38) * mm});
            skLineSegment(sketch, "E1569", {"start": v(-11.16, -12.38) * mm, "end": v(-11.16, -12.37) * mm});
            skLineSegment(sketch, "E1570", {"start": v(-11.16, -12.37) * mm, "end": v(-11.21, -12.22) * mm});
            skLineSegment(sketch, "E1571", {"start": v(-11.21, -12.22) * mm, "end": v(-11.3, -12.07) * mm});
            skLineSegment(sketch, "E1572", {"start": v(-11.3, -12.07) * mm, "end": v(-11.4, -11.93) * mm});
            skLineSegment(sketch, "E1573", {"start": v(-11.4, -11.93) * mm, "end": v(-11.52, -11.81) * mm});
            skLineSegment(sketch, "E1574", {"start": v(-11.52, -11.81) * mm, "end": v(-11.66, -11.72) * mm});
            skLineSegment(sketch, "E1575", {"start": v(-11.66, -11.72) * mm, "end": v(-11.82, -11.64) * mm});
            skLineSegment(sketch, "E1576", {"start": v(-11.82, -11.64) * mm, "end": v(-11.98, -11.6) * mm});
            skLineSegment(sketch, "E1577", {"start": v(-11.98, -11.6) * mm, "end": v(-12.15, -11.58) * mm});
            skLineSegment(sketch, "E1578", {"start": v(-12.15, -11.58) * mm, "end": v(-12.17, -11.58) * mm});
            skLineSegment(sketch, "E1579", {"start": v(-12.17, -11.58) * mm, "end": v(-12.2, -11.58) * mm});
            skLineSegment(sketch, "E1580", {"start": v(-12.2, -11.58) * mm, "end": v(-12.21, -11.58) * mm});
            skLineSegment(sketch, "E1581", {"start": v(-12.21, -11.58) * mm, "end": v(-12.24, -11.58) * mm});
            skLineSegment(sketch, "E1582", {"start": v(-12.24, -11.58) * mm, "end": v(-12.26, -11.58) * mm});
            skLineSegment(sketch, "E1583", {"start": v(-12.26, -11.58) * mm, "end": v(-12.28, -11.58) * mm});
            skLineSegment(sketch, "E1584", {"start": v(-12.28, -11.58) * mm, "end": v(-12.3, -11.58) * mm});
            skLineSegment(sketch, "E1585", {"start": v(-12.3, -11.58) * mm, "end": v(-12.32, -11.58) * mm});
            skLineSegment(sketch, "E1586", {"start": v(-12.32, -11.58) * mm, "end": v(-12.3, -11.86) * mm});
            skLineSegment(sketch, "E1587", {"start": v(-12.3, -11.86) * mm, "end": v(-12.25, -12.14) * mm});
            skLineSegment(sketch, "E1588", {"start": v(-12.25, -12.14) * mm, "end": v(-12.18, -12.4) * mm});
            skLineSegment(sketch, "E1589", {"start": v(-12.18, -12.4) * mm, "end": v(-12.1, -12.64) * mm});
            skLineSegment(sketch, "E1590", {"start": v(-12.1, -12.64) * mm, "end": v(-12, -12.87) * mm});
            skLineSegment(sketch, "E1591", {"start": v(-12, -12.87) * mm, "end": v(-11.86, -13.09) * mm});
            skLineSegment(sketch, "E1592", {"start": v(-11.86, -13.09) * mm, "end": v(-11.72, -13.3) * mm});
            skLineSegment(sketch, "E1593", {"start": v(-11.72, -13.3) * mm, "end": v(-11.55, -13.48) * mm});
            skLineSegment(sketch, "E1594", {"start": v(-11.55, -13.48) * mm, "end": v(-11.36, -13.66) * mm});
            skLineSegment(sketch, "E1595", {"start": v(-11.36, -13.66) * mm, "end": v(-11.14, -13.82) * mm});
            skLineSegment(sketch, "E1596", {"start": v(-11.14, -13.82) * mm, "end": v(-10.92, -13.96) * mm});
            skLineSegment(sketch, "E1597", {"start": v(-10.92, -13.96) * mm, "end": v(-10.67, -14.07) * mm});
            skLineSegment(sketch, "E1598", {"start": v(-10.67, -14.07) * mm, "end": v(-10.41, -14.15) * mm});
            skLineSegment(sketch, "E1599", {"start": v(-10.41, -14.15) * mm, "end": v(-10.14, -14.22) * mm});
            skLineSegment(sketch, "E1600", {"start": v(-10.14, -14.22) * mm, "end": v(-9.84, -14.26) * mm});
            skLineSegment(sketch, "E1601", {"start": v(-9.84, -14.26) * mm, "end": v(-9.54, -14.27) * mm});
            skLineSegment(sketch, "E1602", {"start": v(-9.54, -14.27) * mm, "end": v(-9.19, -14.26) * mm});
            skLineSegment(sketch, "E1603", {"start": v(-9.19, -14.26) * mm, "end": v(-8.86, -14.22) * mm});
            skLineSegment(sketch, "E1604", {"start": v(-8.86, -14.22) * mm, "end": v(-8.56, -14.15) * mm});
            skLineSegment(sketch, "E1605", {"start": v(-8.56, -14.15) * mm, "end": v(-8.27, -14.06) * mm});
            skLineSegment(sketch, "E1606", {"start": v(-8.27, -14.06) * mm, "end": v(-8, -13.94) * mm});
            skLineSegment(sketch, "E1607", {"start": v(-8, -13.94) * mm, "end": v(-7.76, -13.79) * mm});
            skLineSegment(sketch, "E1608", {"start": v(-7.76, -13.79) * mm, "end": v(-7.53, -13.61) * mm});
            skLineSegment(sketch, "E1609", {"start": v(-7.53, -13.61) * mm, "end": v(-7.33, -13.4) * mm});
            skLineSegment(sketch, "E1610", {"start": v(-7.33, -13.4) * mm, "end": v(-7.16, -13.2) * mm});
            skLineSegment(sketch, "E1611", {"start": v(-7.16, -13.2) * mm, "end": v(-7.03, -12.98) * mm});
            skLineSegment(sketch, "E1612", {"start": v(-7.03, -12.98) * mm, "end": v(-6.92, -12.76) * mm});
            skLineSegment(sketch, "E1613", {"start": v(-6.92, -12.76) * mm, "end": v(-6.84, -12.56) * mm});
            skLineSegment(sketch, "E1614", {"start": v(-6.84, -12.56) * mm, "end": v(-6.79, -12.39) * mm});
            skLineSegment(sketch, "E1615", {"start": v(-6.79, -12.39) * mm, "end": v(-6.75, -12.25) * mm});
            skLineSegment(sketch, "E1616", {"start": v(-6.75, -12.25) * mm, "end": v(-6.73, -12.15) * mm});
            skLineSegment(sketch, "E1617", {"start": v(-6.73, -12.15) * mm, "end": v(-6.73, -12.12) * mm});
            skLineSegment(sketch, "E1618", {"start": v(-6.73, -12.12) * mm, "end": v(-6.7, -11.94) * mm});
            skLineSegment(sketch, "E1619", {"start": v(-6.7, -11.94) * mm, "end": v(-6.68, -11.74) * mm});
            skLineSegment(sketch, "E1620", {"start": v(-6.68, -11.74) * mm, "end": v(-6.65, -11.53) * mm});
            skLineSegment(sketch, "E1621", {"start": v(-6.65, -11.53) * mm, "end": v(-6.64, -11.31) * mm});
            skLineSegment(sketch, "E1622", {"start": v(-6.64, -11.31) * mm, "end": v(-6.62, -11.1) * mm});
            skLineSegment(sketch, "E1623", {"start": v(-6.62, -11.1) * mm, "end": v(-6.6, -10.88) * mm});
            skLineSegment(sketch, "E1624", {"start": v(-6.6, -10.88) * mm, "end": v(-6.6, -10.68) * mm});
            skLineSegment(sketch, "E1625", {"start": v(-6.6, -10.68) * mm, "end": v(-6.6, -10.5) * mm});
            skLineSegment(sketch, "E1626", {"start": v(-6.6, -10.5) * mm, "end": v(-6.6, -9.94) * mm});
            skLineSegment(sketch, "E1627", {"start": v(-6.6, -9.94) * mm, "end": v(-6.6, -9.37) * mm});
            skLineSegment(sketch, "E1628", {"start": v(-6.6, -9.37) * mm, "end": v(-6.6, -8.8) * mm});
            skLineSegment(sketch, "E1629", {"start": v(-6.6, -8.8) * mm, "end": v(-6.6, -8.24) * mm});
            skLineSegment(sketch, "E1630", {"start": v(-6.6, -8.24) * mm, "end": v(-6.6, -7.67) * mm});
            skLineSegment(sketch, "E1631", {"start": v(-6.6, -7.67) * mm, "end": v(-6.6, -7.1) * mm});
            skLineSegment(sketch, "E1632", {"start": v(-6.6, -7.1) * mm, "end": v(-6.6, -6.54) * mm});
            skLineSegment(sketch, "E1633", {"start": v(-6.6, -6.54) * mm, "end": v(-6.6, -5.97) * mm});
            skLineSegment(sketch, "E1634", {"start": v(-6.6, -5.97) * mm, "end": v(-6.6, -5.8) * mm});
            skLineSegment(sketch, "E1635", {"start": v(-6.6, -5.8) * mm, "end": v(-6.63, -5.66) * mm});
            skLineSegment(sketch, "E1636", {"start": v(-7.57, -8.3) * mm, "end": v(-7.59, -8.52) * mm});
            skLineSegment(sketch, "E1637", {"start": v(-7.59, -8.52) * mm, "end": v(-7.62, -8.72) * mm});
            skLineSegment(sketch, "E1638", {"start": v(-7.62, -8.72) * mm, "end": v(-7.68, -8.91) * mm});
            skLineSegment(sketch, "E1639", {"start": v(-7.68, -8.91) * mm, "end": v(-7.74, -9.1) * mm});
            skLineSegment(sketch, "E1640", {"start": v(-7.74, -9.1) * mm, "end": v(-7.82, -9.27) * mm});
            skLineSegment(sketch, "E1641", {"start": v(-7.82, -9.27) * mm, "end": v(-7.92, -9.43) * mm});
            skLineSegment(sketch, "E1642", {"start": v(-7.92, -9.43) * mm, "end": v(-8.03, -9.59) * mm});
            skLineSegment(sketch, "E1643", {"start": v(-8.03, -9.59) * mm, "end": v(-8.17, -9.74) * mm});
            skLineSegment(sketch, "E1644", {"start": v(-8.17, -9.74) * mm, "end": v(-8.32, -9.88) * mm});
            skLineSegment(sketch, "E1645", {"start": v(-8.32, -9.88) * mm, "end": v(-8.48, -9.99) * mm});
            skLineSegment(sketch, "E1646", {"start": v(-8.48, -9.99) * mm, "end": v(-8.66, -10.08) * mm});
            skLineSegment(sketch, "E1647", {"start": v(-8.66, -10.08) * mm, "end": v(-8.84, -10.16) * mm});
            skLineSegment(sketch, "E1648", {"start": v(-8.84, -10.16) * mm, "end": v(-9.04, -10.2) * mm});
            skLineSegment(sketch, "E1649", {"start": v(-9.04, -10.2) * mm, "end": v(-9.25, -10.24) * mm});
            skLineSegment(sketch, "E1650", {"start": v(-9.25, -10.24) * mm, "end": v(-9.48, -10.26) * mm});
            skLineSegment(sketch, "E1651", {"start": v(-9.48, -10.26) * mm, "end": v(-9.69, -10.25) * mm});
            skLineSegment(sketch, "E1652", {"start": v(-9.69, -10.25) * mm, "end": v(-9.9, -10.22) * mm});
            skLineSegment(sketch, "E1653", {"start": v(-9.9, -10.22) * mm, "end": v(-10.08, -10.17) * mm});
            skLineSegment(sketch, "E1654", {"start": v(-10.08, -10.17) * mm, "end": v(-10.27, -10.1) * mm});
            skLineSegment(sketch, "E1655", {"start": v(-10.27, -10.1) * mm, "end": v(-10.44, -10) * mm});
            skLineSegment(sketch, "E1656", {"start": v(-10.44, -10) * mm, "end": v(-10.6, -9.88) * mm});
            skLineSegment(sketch, "E1657", {"start": v(-10.6, -9.88) * mm, "end": v(-10.75, -9.73) * mm});
            skLineSegment(sketch, "E1658", {"start": v(-10.75, -9.73) * mm, "end": v(-10.9, -9.57) * mm});
            skLineSegment(sketch, "E1659", {"start": v(-10.9, -9.57) * mm, "end": v(-11.01, -9.4) * mm});
            skLineSegment(sketch, "E1660", {"start": v(-11.01, -9.4) * mm, "end": v(-11.12, -9.23) * mm});
            skLineSegment(sketch, "E1661", {"start": v(-11.12, -9.23) * mm, "end": v(-11.2, -9.04) * mm});
            skLineSegment(sketch, "E1662", {"start": v(-11.2, -9.04) * mm, "end": v(-11.27, -8.85) * mm});
            skLineSegment(sketch, "E1663", {"start": v(-11.27, -8.85) * mm, "end": v(-11.33, -8.65) * mm});
            skLineSegment(sketch, "E1664", {"start": v(-11.33, -8.65) * mm, "end": v(-11.36, -8.45) * mm});
            skLineSegment(sketch, "E1665", {"start": v(-11.36, -8.45) * mm, "end": v(-11.38, -8.24) * mm});
            skLineSegment(sketch, "E1666", {"start": v(-11.38, -8.24) * mm, "end": v(-11.38, -8.01) * mm});
            skLineSegment(sketch, "E1667", {"start": v(-11.38, -8.01) * mm, "end": v(-11.37, -7.8) * mm});
            skLineSegment(sketch, "E1668", {"start": v(-11.37, -7.8) * mm, "end": v(-11.34, -7.6) * mm});
            skLineSegment(sketch, "E1669", {"start": v(-11.34, -7.6) * mm, "end": v(-11.3, -7.41) * mm});
            skLineSegment(sketch, "E1670", {"start": v(-11.3, -7.41) * mm, "end": v(-11.24, -7.23) * mm});
            skLineSegment(sketch, "E1671", {"start": v(-11.24, -7.23) * mm, "end": v(-11.16, -7.05) * mm});
            skLineSegment(sketch, "E1672", {"start": v(-11.16, -7.05) * mm, "end": v(-11.07, -6.88) * mm});
            skLineSegment(sketch, "E1673", {"start": v(-11.07, -6.88) * mm, "end": v(-10.96, -6.72) * mm});
            skLineSegment(sketch, "E1674", {"start": v(-10.96, -6.72) * mm, "end": v(-10.84, -6.56) * mm});
            skLineSegment(sketch, "E1675", {"start": v(-10.84, -6.56) * mm, "end": v(-10.7, -6.41) * mm});
            skLineSegment(sketch, "E1676", {"start": v(-10.7, -6.41) * mm, "end": v(-10.56, -6.28) * mm});
            skLineSegment(sketch, "E1677", {"start": v(-10.56, -6.28) * mm, "end": v(-10.4, -6.17) * mm});
            skLineSegment(sketch, "E1678", {"start": v(-10.4, -6.17) * mm, "end": v(-10.24, -6.08) * mm});
            skLineSegment(sketch, "E1679", {"start": v(-10.24, -6.08) * mm, "end": v(-10.07, -6.01) * mm});
            skLineSegment(sketch, "E1680", {"start": v(-10.07, -6.01) * mm, "end": v(-9.9, -5.96) * mm});
            skLineSegment(sketch, "E1681", {"start": v(-9.9, -5.96) * mm, "end": v(-9.7, -5.93) * mm});
            skLineSegment(sketch, "E1682", {"start": v(-9.7, -5.93) * mm, "end": v(-9.51, -5.92) * mm});
            skLineSegment(sketch, "E1683", {"start": v(-9.51, -5.92) * mm, "end": v(-9.29, -5.93) * mm});
            skLineSegment(sketch, "E1684", {"start": v(-9.29, -5.93) * mm, "end": v(-9.08, -5.96) * mm});
            skLineSegment(sketch, "E1685", {"start": v(-9.08, -5.96) * mm, "end": v(-8.88, -6) * mm});
            skLineSegment(sketch, "E1686", {"start": v(-8.88, -6) * mm, "end": v(-8.7, -6.08) * mm});
            skLineSegment(sketch, "E1687", {"start": v(-8.7, -6.08) * mm, "end": v(-8.52, -6.17) * mm});
            skLineSegment(sketch, "E1688", {"start": v(-8.52, -6.17) * mm, "end": v(-8.35, -6.29) * mm});
            skLineSegment(sketch, "E1689", {"start": v(-8.35, -6.29) * mm, "end": v(-8.2, -6.42) * mm});
            skLineSegment(sketch, "E1690", {"start": v(-8.2, -6.42) * mm, "end": v(-8.06, -6.58) * mm});
            skLineSegment(sketch, "E1691", {"start": v(-8.06, -6.58) * mm, "end": v(-7.94, -6.73) * mm});
            skLineSegment(sketch, "E1692", {"start": v(-7.94, -6.73) * mm, "end": v(-7.84, -6.9) * mm});
            skLineSegment(sketch, "E1693", {"start": v(-7.84, -6.9) * mm, "end": v(-7.75, -7.08) * mm});
            skLineSegment(sketch, "E1694", {"start": v(-7.75, -7.08) * mm, "end": v(-7.68, -7.26) * mm});
            skLineSegment(sketch, "E1695", {"start": v(-7.68, -7.26) * mm, "end": v(-7.63, -7.45) * mm});
            skLineSegment(sketch, "E1696", {"start": v(-7.63, -7.45) * mm, "end": v(-7.59, -7.65) * mm});
            skLineSegment(sketch, "E1697", {"start": v(-7.59, -7.65) * mm, "end": v(-7.56, -7.86) * mm});
            skLineSegment(sketch, "E1698", {"start": v(-7.56, -7.86) * mm, "end": v(-7.56, -8.08) * mm});
            skLineSegment(sketch, "E1699", {"start": v(-7.56, -8.08) * mm, "end": v(-7.57, -8.3) * mm});
            skLineSegment(sketch, "E1700", {"start": v(-1.5, -6.06) * mm, "end": v(-1.41, -6.03) * mm});
            skLineSegment(sketch, "E1701", {"start": v(-1.41, -6.03) * mm, "end": v(-1.32, -6) * mm});
            skLineSegment(sketch, "E1702", {"start": v(-1.32, -6) * mm, "end": v(-1.25, -5.97) * mm});
            skLineSegment(sketch, "E1703", {"start": v(-1.25, -5.97) * mm, "end": v(-1.19, -5.94) * mm});
            skLineSegment(sketch, "E1704", {"start": v(-1.19, -5.94) * mm, "end": v(-1.13, -5.9) * mm});
            skLineSegment(sketch, "E1705", {"start": v(-1.13, -5.9) * mm, "end": v(-1.07, -5.87) * mm});
            skLineSegment(sketch, "E1706", {"start": v(-1.07, -5.87) * mm, "end": v(-1.03, -5.82) * mm});
            skLineSegment(sketch, "E1707", {"start": v(-1.03, -5.82) * mm, "end": v(-1, -5.76) * mm});
            skLineSegment(sketch, "E1708", {"start": v(-1, -5.76) * mm, "end": v(-0.98, -5.7) * mm});
            skLineSegment(sketch, "E1709", {"start": v(-0.98, -5.7) * mm, "end": v(-0.97, -5.61) * mm});
            skLineSegment(sketch, "E1710", {"start": v(-0.97, -5.61) * mm, "end": v(-1, -5.46) * mm});
            skLineSegment(sketch, "E1711", {"start": v(-1, -5.46) * mm, "end": v(-1.05, -5.36) * mm});
            skLineSegment(sketch, "E1712", {"start": v(-1.05, -5.36) * mm, "end": v(-1.14, -5.29) * mm});
            skLineSegment(sketch, "E1713", {"start": v(-1.14, -5.29) * mm, "end": v(-1.26, -5.24) * mm});
            skLineSegment(sketch, "E1714", {"start": v(-1.26, -5.24) * mm, "end": v(-1.38, -5.2) * mm});
            skLineSegment(sketch, "E1715", {"start": v(-1.38, -5.2) * mm, "end": v(-1.5, -5.18) * mm});
            skLineSegment(sketch, "E1716", {"start": v(-1.5, -5.18) * mm, "end": v(-1.63, -5.13) * mm});
            skLineSegment(sketch, "E1717", {"start": v(-1.63, -5.13) * mm, "end": v(-1.73, -5.06) * mm});
            skLineSegment(sketch, "E1718", {"start": v(-1.73, -5.06) * mm, "end": v(-1.8, -5) * mm});
            skLineSegment(sketch, "E1719", {"start": v(-1.8, -5) * mm, "end": v(-1.86, -4.91) * mm});
            skLineSegment(sketch, "E1720", {"start": v(-1.86, -4.91) * mm, "end": v(-1.9, -4.83) * mm});
            skLineSegment(sketch, "E1721", {"start": v(-1.9, -4.83) * mm, "end": v(-1.94, -4.74) * mm});
            skLineSegment(sketch, "E1722", {"start": v(-1.94, -4.74) * mm, "end": v(-1.97, -4.64) * mm});
            skLineSegment(sketch, "E1723", {"start": v(-1.97, -4.64) * mm, "end": v(-1.99, -4.54) * mm});
            skLineSegment(sketch, "E1724", {"start": v(-1.99, -4.54) * mm, "end": v(-2, -4.45) * mm});
            skLineSegment(sketch, "E1725", {"start": v(-2, -4.45) * mm, "end": v(-2, -4.35) * mm});
            skLineSegment(sketch, "E1726", {"start": v(-2, -4.35) * mm, "end": v(-2, -4.3) * mm});
            skLineSegment(sketch, "E1727", {"start": v(-2, -4.3) * mm, "end": v(-2, -4.24) * mm});
            skLineSegment(sketch, "E1728", {"start": v(-2, -4.24) * mm, "end": v(-2, -4.18) * mm});
            skLineSegment(sketch, "E1729", {"start": v(-2, -4.18) * mm, "end": v(-2, -4.12) * mm});
            skLineSegment(sketch, "E1730", {"start": v(-2, -4.12) * mm, "end": v(-2, -4.07) * mm});
            skLineSegment(sketch, "E1731", {"start": v(-2, -4.07) * mm, "end": v(-2, -4) * mm});
            skLineSegment(sketch, "E1732", {"start": v(-2, -4) * mm, "end": v(-2, -3.95) * mm});
            skLineSegment(sketch, "E1733", {"start": v(-2, -3.95) * mm, "end": v(-2, -3.9) * mm});
            skLineSegment(sketch, "E1734", {"start": v(-2, -3.9) * mm, "end": v(-2, -3.73) * mm});
            skLineSegment(sketch, "E1735", {"start": v(-2, -3.73) * mm, "end": v(-2.04, -3.58) * mm});
            skLineSegment(sketch, "E1736", {"start": v(-2.04, -3.58) * mm, "end": v(-2.09, -3.44) * mm});
            skLineSegment(sketch, "E1737", {"start": v(-2.09, -3.44) * mm, "end": v(-2.15, -3.32) * mm});
            skLineSegment(sketch, "E1738", {"start": v(-2.15, -3.32) * mm, "end": v(-2.23, -3.22) * mm});
            skLineSegment(sketch, "E1739", {"start": v(-2.23, -3.22) * mm, "end": v(-2.31, -3.15) * mm});
            skLineSegment(sketch, "E1740", {"start": v(-2.31, -3.15) * mm, "end": v(-2.41, -3.1) * mm});
            skLineSegment(sketch, "E1741", {"start": v(-2.41, -3.1) * mm, "end": v(-2.51, -3.08) * mm});
            skLineSegment(sketch, "E1742", {"start": v(-2.51, -3.08) * mm, "end": v(-2.62, -3.1) * mm});
            skLineSegment(sketch, "E1743", {"start": v(-2.62, -3.1) * mm, "end": v(-2.72, -3.14) * mm});
            skLineSegment(sketch, "E1744", {"start": v(-2.72, -3.14) * mm, "end": v(-2.8, -3.22) * mm});
            skLineSegment(sketch, "E1745", {"start": v(-2.8, -3.22) * mm, "end": v(-2.88, -3.32) * mm});
            skLineSegment(sketch, "E1746", {"start": v(-2.88, -3.32) * mm, "end": v(-2.94, -3.44) * mm});
            skLineSegment(sketch, "E1747", {"start": v(-2.94, -3.44) * mm, "end": v(-3, -3.58) * mm});
            skLineSegment(sketch, "E1748", {"start": v(-3, -3.58) * mm, "end": v(-3.02, -3.73) * mm});
            skLineSegment(sketch, "E1749", {"start": v(-3.02, -3.73) * mm, "end": v(-3.03, -3.9) * mm});
            skLineSegment(sketch, "E1750", {"start": v(-3.03, -3.9) * mm, "end": v(-3.03, -3.95) * mm});
            skLineSegment(sketch, "E1751", {"start": v(-3.03, -3.95) * mm, "end": v(-3.03, -4) * mm});
            skLineSegment(sketch, "E1752", {"start": v(-3.03, -4) * mm, "end": v(-3.03, -4.06) * mm});
            skLineSegment(sketch, "E1753", {"start": v(-3.03, -4.06) * mm, "end": v(-3.03, -4.12) * mm});
            skLineSegment(sketch, "E1754", {"start": v(-3.03, -4.12) * mm, "end": v(-3.03, -4.18) * mm});
            skLineSegment(sketch, "E1755", {"start": v(-3.03, -4.18) * mm, "end": v(-3.03, -4.23) * mm});
            skLineSegment(sketch, "E1756", {"start": v(-3.03, -4.23) * mm, "end": v(-3.03, -4.3) * mm});
            skLineSegment(sketch, "E1757", {"start": v(-3.03, -4.3) * mm, "end": v(-3.03, -4.35) * mm});
            skLineSegment(sketch, "E1758", {"start": v(-3.03, -4.35) * mm, "end": v(-3.03, -4.44) * mm});
            skLineSegment(sketch, "E1759", {"start": v(-3.03, -4.44) * mm, "end": v(-3.04, -4.54) * mm});
            skLineSegment(sketch, "E1760", {"start": v(-3.04, -4.54) * mm, "end": v(-3.05, -4.65) * mm});
            skLineSegment(sketch, "E1761", {"start": v(-3.05, -4.65) * mm, "end": v(-3.06, -4.75) * mm});
            skLineSegment(sketch, "E1762", {"start": v(-3.06, -4.75) * mm, "end": v(-3.09, -4.85) * mm});
            skLineSegment(sketch, "E1763", {"start": v(-3.09, -4.85) * mm, "end": v(-3.13, -4.95) * mm});
            skLineSegment(sketch, "E1764", {"start": v(-3.13, -4.95) * mm, "end": v(-3.18, -5.03) * mm});
            skLineSegment(sketch, "E1765", {"start": v(-3.18, -5.03) * mm, "end": v(-3.25, -5.1) * mm});
            skLineSegment(sketch, "E1766", {"start": v(-3.25, -5.1) * mm, "end": v(-3.29, -5.13) * mm});
            skLineSegment(sketch, "E1767", {"start": v(-3.29, -5.13) * mm, "end": v(-3.33, -5.15) * mm});
            skLineSegment(sketch, "E1768", {"start": v(-3.33, -5.15) * mm, "end": v(-3.37, -5.18) * mm});
            skLineSegment(sketch, "E1769", {"start": v(-3.37, -5.18) * mm, "end": v(-3.42, -5.2) * mm});
            skLineSegment(sketch, "E1770", {"start": v(-3.42, -5.2) * mm, "end": v(-3.46, -5.23) * mm});
            skLineSegment(sketch, "E1771", {"start": v(-3.46, -5.23) * mm, "end": v(-3.5, -5.26) * mm});
            skLineSegment(sketch, "E1772", {"start": v(-3.5, -5.26) * mm, "end": v(-3.53, -5.3) * mm});
            skLineSegment(sketch, "E1773", {"start": v(-3.53, -5.3) * mm, "end": v(-3.56, -5.34) * mm});
            skLineSegment(sketch, "E1774", {"start": v(-3.56, -5.34) * mm, "end": v(-3.59, -5.4) * mm});
            skLineSegment(sketch, "E1775", {"start": v(-3.59, -5.4) * mm, "end": v(-3.61, -5.46) * mm});
            skLineSegment(sketch, "E1776", {"start": v(-3.61, -5.46) * mm, "end": v(-3.62, -5.53) * mm});
            skLineSegment(sketch, "E1777", {"start": v(-3.62, -5.53) * mm, "end": v(-3.63, -5.6) * mm});
            skLineSegment(sketch, "E1778", {"start": v(-3.63, -5.6) * mm, "end": v(-3.62, -5.67) * mm});
            skLineSegment(sketch, "E1779", {"start": v(-3.62, -5.67) * mm, "end": v(-3.6, -5.73) * mm});
            skLineSegment(sketch, "E1780", {"start": v(-3.6, -5.73) * mm, "end": v(-3.58, -5.8) * mm});
            skLineSegment(sketch, "E1781", {"start": v(-3.58, -5.8) * mm, "end": v(-3.55, -5.86) * mm});
            skLineSegment(sketch, "E1782", {"start": v(-3.55, -5.86) * mm, "end": v(-3.5, -5.91) * mm});
            skLineSegment(sketch, "E1783", {"start": v(-3.5, -5.91) * mm, "end": v(-3.45, -5.97) * mm});
            skLineSegment(sketch, "E1784", {"start": v(-3.45, -5.97) * mm, "end": v(-3.4, -6.02) * mm});
            skLineSegment(sketch, "E1785", {"start": v(-3.4, -6.02) * mm, "end": v(-3.33, -6.06) * mm});
            skLineSegment(sketch, "E1786", {"start": v(-3.33, -6.06) * mm, "end": v(-3.27, -6.11) * mm});
            skLineSegment(sketch, "E1787", {"start": v(-3.27, -6.11) * mm, "end": v(-3.22, -6.16) * mm});
            skLineSegment(sketch, "E1788", {"start": v(-3.22, -6.16) * mm, "end": v(-3.17, -6.22) * mm});
            skLineSegment(sketch, "E1789", {"start": v(-3.17, -6.22) * mm, "end": v(-3.13, -6.29) * mm});
            skLineSegment(sketch, "E1790", {"start": v(-3.13, -6.29) * mm, "end": v(-3.1, -6.38) * mm});
            skLineSegment(sketch, "E1791", {"start": v(-3.1, -6.38) * mm, "end": v(-3.07, -6.48) * mm});
            skLineSegment(sketch, "E1792", {"start": v(-3.07, -6.48) * mm, "end": v(-3.05, -6.58) * mm});
            skLineSegment(sketch, "E1793", {"start": v(-3.05, -6.58) * mm, "end": v(-3.04, -6.69) * mm});
            skLineSegment(sketch, "E1794", {"start": v(-3.04, -6.69) * mm, "end": v(-3.04, -6.8) * mm});
            skLineSegment(sketch, "E1795", {"start": v(-3.04, -6.8) * mm, "end": v(-3.04, -6.9) * mm});
            skLineSegment(sketch, "E1796", {"start": v(-3.04, -6.9) * mm, "end": v(-3.04, -7) * mm});
            skLineSegment(sketch, "E1797", {"start": v(-3.04, -7) * mm, "end": v(-3.04, -7.1) * mm});
            skLineSegment(sketch, "E1798", {"start": v(-3.04, -7.1) * mm, "end": v(-3.04, -7.34) * mm});
            skLineSegment(sketch, "E1799", {"start": v(-3.04, -7.34) * mm, "end": v(-3.04, -7.56) * mm});
            skLineSegment(sketch, "E1800", {"start": v(-3.04, -7.56) * mm, "end": v(-3.04, -7.8) * mm});
            skLineSegment(sketch, "E1801", {"start": v(-3.04, -7.8) * mm, "end": v(-3.04, -8.02) * mm});
            skLineSegment(sketch, "E1802", {"start": v(-3.04, -8.02) * mm, "end": v(-3.04, -8.25) * mm});
            skLineSegment(sketch, "E1803", {"start": v(-3.04, -8.25) * mm, "end": v(-3.04, -8.48) * mm});
            skLineSegment(sketch, "E1804", {"start": v(-3.04, -8.48) * mm, "end": v(-3.04, -8.7) * mm});
            skLineSegment(sketch, "E1805", {"start": v(-3.04, -8.7) * mm, "end": v(-3.04, -8.94) * mm});
            skLineSegment(sketch, "E1806", {"start": v(-3.04, -8.94) * mm, "end": v(-3.04, -9.1) * mm});
            skLineSegment(sketch, "E1807", {"start": v(-3.04, -9.1) * mm, "end": v(-3.04, -9.25) * mm});
            skLineSegment(sketch, "E1808", {"start": v(-3.04, -9.25) * mm, "end": v(-3.04, -9.41) * mm});
            skLineSegment(sketch, "E1809", {"start": v(-3.04, -9.41) * mm, "end": v(-3.04, -9.57) * mm});
            skLineSegment(sketch, "E1810", {"start": v(-3.04, -9.57) * mm, "end": v(-3.04, -9.73) * mm});
            skLineSegment(sketch, "E1811", {"start": v(-3.04, -9.73) * mm, "end": v(-3.04, -9.88) * mm});
            skLineSegment(sketch, "E1812", {"start": v(-3.04, -9.88) * mm, "end": v(-3.04, -10.04) * mm});
            skLineSegment(sketch, "E1813", {"start": v(-3.04, -10.04) * mm, "end": v(-3.04, -10.2) * mm});
            skLineSegment(sketch, "E1814", {"start": v(-3.04, -10.2) * mm, "end": v(-3.03, -10.36) * mm});
            skLineSegment(sketch, "E1815", {"start": v(-3.03, -10.36) * mm, "end": v(-3, -10.52) * mm});
            skLineSegment(sketch, "E1816", {"start": v(-3, -10.52) * mm, "end": v(-2.95, -10.65) * mm});
            skLineSegment(sketch, "E1817", {"start": v(-2.95, -10.65) * mm, "end": v(-2.89, -10.77) * mm});
            skLineSegment(sketch, "E1818", {"start": v(-2.89, -10.77) * mm, "end": v(-2.81, -10.87) * mm});
            skLineSegment(sketch, "E1819", {"start": v(-2.81, -10.87) * mm, "end": v(-2.73, -10.95) * mm});
            skLineSegment(sketch, "E1820", {"start": v(-2.73, -10.95) * mm, "end": v(-2.63, -11) * mm});
            skLineSegment(sketch, "E1821", {"start": v(-2.63, -11) * mm, "end": v(-2.53, -11.01) * mm});
            skLineSegment(sketch, "E1822", {"start": v(-2.53, -11.01) * mm, "end": v(-2.42, -11) * mm});
            skLineSegment(sketch, "E1823", {"start": v(-2.42, -11) * mm, "end": v(-2.32, -10.95) * mm});
            skLineSegment(sketch, "E1824", {"start": v(-2.32, -10.95) * mm, "end": v(-2.24, -10.88) * mm});
            skLineSegment(sketch, "E1825", {"start": v(-2.24, -10.88) * mm, "end": v(-2.16, -10.78) * mm});
            skLineSegment(sketch, "E1826", {"start": v(-2.16, -10.78) * mm, "end": v(-2.1, -10.66) * mm});
            skLineSegment(sketch, "E1827", {"start": v(-2.1, -10.66) * mm, "end": v(-2.05, -10.52) * mm});
            skLineSegment(sketch, "E1828", {"start": v(-2.05, -10.52) * mm, "end": v(-2.02, -10.36) * mm});
            skLineSegment(sketch, "E1829", {"start": v(-2.02, -10.36) * mm, "end": v(-2, -10.2) * mm});
            skLineSegment(sketch, "E1830", {"start": v(-2, -10.2) * mm, "end": v(-2, -10.15) * mm});
            skLineSegment(sketch, "E1831", {"start": v(-2, -10.15) * mm, "end": v(-2, -10.1) * mm});
            skLineSegment(sketch, "E1832", {"start": v(-2, -10.1) * mm, "end": v(-2, -10.05) * mm});
            skLineSegment(sketch, "E1833", {"start": v(-2, -10.05) * mm, "end": v(-2, -10) * mm});
            skLineSegment(sketch, "E1834", {"start": v(-2, -10) * mm, "end": v(-2, -9.95) * mm});
            skLineSegment(sketch, "E1835", {"start": v(-2, -9.95) * mm, "end": v(-2, -9.9) * mm});
            skLineSegment(sketch, "E1836", {"start": v(-2, -9.9) * mm, "end": v(-2, -9.85) * mm});
            skLineSegment(sketch, "E1837", {"start": v(-2, -9.85) * mm, "end": v(-2, -9.8) * mm});
            skLineSegment(sketch, "E1838", {"start": v(-2, -9.8) * mm, "end": v(-2, -9.58) * mm});
            skLineSegment(sketch, "E1839", {"start": v(-2, -9.58) * mm, "end": v(-2, -9.36) * mm});
            skLineSegment(sketch, "E1840", {"start": v(-2, -9.36) * mm, "end": v(-2, -9.14) * mm});
            skLineSegment(sketch, "E1841", {"start": v(-2, -9.14) * mm, "end": v(-2, -8.91) * mm});
            skLineSegment(sketch, "E1842", {"start": v(-2, -8.91) * mm, "end": v(-2, -8.7) * mm});
            skLineSegment(sketch, "E1843", {"start": v(-2, -8.7) * mm, "end": v(-2, -8.47) * mm});
            skLineSegment(sketch, "E1844", {"start": v(-2, -8.47) * mm, "end": v(-2, -8.25) * mm});
            skLineSegment(sketch, "E1845", {"start": v(-2, -8.25) * mm, "end": v(-2, -8.02) * mm});
            skLineSegment(sketch, "E1846", {"start": v(-2, -8.02) * mm, "end": v(-2, -7.92) * mm});
            skLineSegment(sketch, "E1847", {"start": v(-2, -7.92) * mm, "end": v(-2, -7.82) * mm});
            skLineSegment(sketch, "E1848", {"start": v(-2, -7.82) * mm, "end": v(-2, -7.72) * mm});
            skLineSegment(sketch, "E1849", {"start": v(-2, -7.72) * mm, "end": v(-2, -7.62) * mm});
            skLineSegment(sketch, "E1850", {"start": v(-2, -7.62) * mm, "end": v(-2, -7.52) * mm});
            skLineSegment(sketch, "E1851", {"start": v(-2, -7.52) * mm, "end": v(-2, -7.42) * mm});
            skLineSegment(sketch, "E1852", {"start": v(-2, -7.42) * mm, "end": v(-2, -7.32) * mm});
            skLineSegment(sketch, "E1853", {"start": v(-2, -7.32) * mm, "end": v(-2, -7.22) * mm});
            skLineSegment(sketch, "E1854", {"start": v(-2, -7.22) * mm, "end": v(-2, -7.12) * mm});
            skLineSegment(sketch, "E1855", {"start": v(-2, -7.12) * mm, "end": v(-2, -7.01) * mm});
            skLineSegment(sketch, "E1856", {"start": v(-2, -7.01) * mm, "end": v(-2, -6.9) * mm});
            skLineSegment(sketch, "E1857", {"start": v(-2, -6.9) * mm, "end": v(-2, -6.8) * mm});
            skLineSegment(sketch, "E1858", {"start": v(-2, -6.8) * mm, "end": v(-2, -6.7) * mm});
            skLineSegment(sketch, "E1859", {"start": v(-2, -6.7) * mm, "end": v(-1.98, -6.6) * mm});
            skLineSegment(sketch, "E1860", {"start": v(-1.98, -6.6) * mm, "end": v(-1.95, -6.5) * mm});
            skLineSegment(sketch, "E1861", {"start": v(-1.95, -6.5) * mm, "end": v(-1.91, -6.4) * mm});
            skLineSegment(sketch, "E1862", {"start": v(-1.91, -6.4) * mm, "end": v(-1.86, -6.32) * mm});
            skLineSegment(sketch, "E1863", {"start": v(-1.86, -6.32) * mm, "end": v(-1.8, -6.25) * mm});
            skLineSegment(sketch, "E1864", {"start": v(-1.8, -6.25) * mm, "end": v(-1.74, -6.19) * mm});
            skLineSegment(sketch, "E1865", {"start": v(-1.74, -6.19) * mm, "end": v(-1.67, -6.14) * mm});
            skLineSegment(sketch, "E1866", {"start": v(-1.67, -6.14) * mm, "end": v(-1.59, -6.1) * mm});
            skLineSegment(sketch, "E1867", {"start": v(-1.59, -6.1) * mm, "end": v(-1.5, -6.06) * mm});
            skLineSegment(sketch, "E1868", {"start": v(4.39, -10.37) * mm, "end": v(4.4, -10.2) * mm});
            skLineSegment(sketch, "E1869", {"start": v(4.4, -10.2) * mm, "end": v(4.4, -9.9) * mm});
            skLineSegment(sketch, "E1870", {"start": v(4.4, -9.9) * mm, "end": v(4.4, -9.58) * mm});
            skLineSegment(sketch, "E1871", {"start": v(4.4, -9.58) * mm, "end": v(4.4, -9.26) * mm});
            skLineSegment(sketch, "E1872", {"start": v(4.4, -9.26) * mm, "end": v(4.4, -8.95) * mm});
            skLineSegment(sketch, "E1873", {"start": v(4.4, -8.95) * mm, "end": v(4.4, -8.63) * mm});
            skLineSegment(sketch, "E1874", {"start": v(4.4, -8.63) * mm, "end": v(4.4, -8.32) * mm});
            skLineSegment(sketch, "E1875", {"start": v(4.4, -8.32) * mm, "end": v(4.4, -8) * mm});
            skLineSegment(sketch, "E1876", {"start": v(4.4, -8) * mm, "end": v(4.4, -7.69) * mm});
            skLineSegment(sketch, "E1877", {"start": v(4.4, -7.69) * mm, "end": v(4.39, -7.25) * mm});
            skLineSegment(sketch, "E1878", {"start": v(4.39, -7.25) * mm, "end": v(4.35, -6.86) * mm});
            skLineSegment(sketch, "E1879", {"start": v(4.35, -6.86) * mm, "end": v(4.28, -6.5) * mm});
            skLineSegment(sketch, "E1880", {"start": v(4.28, -6.5) * mm, "end": v(4.2, -6.19) * mm});
            skLineSegment(sketch, "E1881", {"start": v(4.2, -6.19) * mm, "end": v(4.08, -5.91) * mm});
            skLineSegment(sketch, "E1882", {"start": v(4.08, -5.91) * mm, "end": v(3.94, -5.68) * mm});
            skLineSegment(sketch, "E1883", {"start": v(3.94, -5.68) * mm, "end": v(3.77, -5.48) * mm});
            skLineSegment(sketch, "E1884", {"start": v(3.77, -5.48) * mm, "end": v(3.57, -5.33) * mm});
            skLineSegment(sketch, "E1885", {"start": v(3.57, -5.33) * mm, "end": v(3.45, -5.26) * mm});
            skLineSegment(sketch, "E1886", {"start": v(3.45, -5.26) * mm, "end": v(3.32, -5.2) * mm});
            skLineSegment(sketch, "E1887", {"start": v(3.32, -5.2) * mm, "end": v(3.2, -5.14) * mm});
            skLineSegment(sketch, "E1888", {"start": v(3.2, -5.14) * mm, "end": v(3.05, -5.1) * mm});
            skLineSegment(sketch, "E1889", {"start": v(3.05, -5.1) * mm, "end": v(2.91, -5.06) * mm});
            skLineSegment(sketch, "E1890", {"start": v(2.91, -5.06) * mm, "end": v(2.76, -5.04) * mm});
            skLineSegment(sketch, "E1891", {"start": v(2.76, -5.04) * mm, "end": v(2.61, -5.02) * mm});
            skLineSegment(sketch, "E1892", {"start": v(2.61, -5.02) * mm, "end": v(2.46, -5.02) * mm});
            skLineSegment(sketch, "E1893", {"start": v(2.46, -5.02) * mm, "end": v(2.33, -5.02) * mm});
            skLineSegment(sketch, "E1894", {"start": v(2.33, -5.02) * mm, "end": v(2.2, -5.03) * mm});
            skLineSegment(sketch, "E1895", {"start": v(2.2, -5.03) * mm, "end": v(2.08, -5.05) * mm});
            skLineSegment(sketch, "E1896", {"start": v(2.08, -5.05) * mm, "end": v(1.95, -5.07) * mm});
            skLineSegment(sketch, "E1897", {"start": v(1.95, -5.07) * mm, "end": v(1.83, -5.1) * mm});
            skLineSegment(sketch, "E1898", {"start": v(1.83, -5.1) * mm, "end": v(1.7, -5.14) * mm});
            skLineSegment(sketch, "E1899", {"start": v(1.7, -5.14) * mm, "end": v(1.6, -5.18) * mm});
            skLineSegment(sketch, "E1900", {"start": v(1.6, -5.18) * mm, "end": v(1.47, -5.24) * mm});
            skLineSegment(sketch, "E1901", {"start": v(1.47, -5.24) * mm, "end": v(1.41, -5.27) * mm});
            skLineSegment(sketch, "E1902", {"start": v(1.41, -5.27) * mm, "end": v(1.34, -5.32) * mm});
            skLineSegment(sketch, "E1903", {"start": v(1.34, -5.32) * mm, "end": v(1.26, -5.38) * mm});
            skLineSegment(sketch, "E1904", {"start": v(1.26, -5.38) * mm, "end": v(1.18, -5.44) * mm});
            skLineSegment(sketch, "E1905", {"start": v(1.18, -5.44) * mm, "end": v(1.1, -5.49) * mm});
            skLineSegment(sketch, "E1906", {"start": v(1.1, -5.49) * mm, "end": v(1.01, -5.52) * mm});
            skLineSegment(sketch, "E1907", {"start": v(1.01, -5.52) * mm, "end": v(0.94, -5.54) * mm});
            skLineSegment(sketch, "E1908", {"start": v(0.94, -5.54) * mm, "end": v(0.87, -5.53) * mm});
            skLineSegment(sketch, "E1909", {"start": v(0.87, -5.53) * mm, "end": v(0.82, -5.5) * mm});
            skLineSegment(sketch, "E1910", {"start": v(0.82, -5.5) * mm, "end": v(0.78, -5.44) * mm});
            skLineSegment(sketch, "E1911", {"start": v(0.78, -5.44) * mm, "end": v(0.76, -5.38) * mm});
            skLineSegment(sketch, "E1912", {"start": v(0.76, -5.38) * mm, "end": v(0.74, -5.32) * mm});
            skLineSegment(sketch, "E1913", {"start": v(0.74, -5.32) * mm, "end": v(0.73, -5.25) * mm});
            skLineSegment(sketch, "E1914", {"start": v(0.73, -5.25) * mm, "end": v(0.72, -5.18) * mm});
            skLineSegment(sketch, "E1915", {"start": v(0.72, -5.18) * mm, "end": v(0.72, -5.12) * mm});
            skLineSegment(sketch, "E1916", {"start": v(0.72, -5.12) * mm, "end": v(0.72, -5.06) * mm});
            skLineSegment(sketch, "E1917", {"start": v(0.72, -5.06) * mm, "end": v(0.72, -4.9) * mm});
            skLineSegment(sketch, "E1918", {"start": v(0.72, -4.9) * mm, "end": v(0.72, -4.51) * mm});
            skLineSegment(sketch, "E1919", {"start": v(0.72, -4.51) * mm, "end": v(0.72, -3.96) * mm});
            skLineSegment(sketch, "E1920", {"start": v(0.72, -3.96) * mm, "end": v(0.72, -3.32) * mm});
            skLineSegment(sketch, "E1921", {"start": v(0.72, -3.32) * mm, "end": v(0.72, -2.68) * mm});
            skLineSegment(sketch, "E1922", {"start": v(0.72, -2.68) * mm, "end": v(0.72, -2.13) * mm});
            skLineSegment(sketch, "E1923", {"start": v(0.72, -2.13) * mm, "end": v(0.72, -1.74) * mm});
            skLineSegment(sketch, "E1924", {"start": v(0.72, -1.74) * mm, "end": v(0.72, -1.59) * mm});
            skLineSegment(sketch, "E1925", {"start": v(0.72, -1.59) * mm, "end": v(0.71, -1.42) * mm});
            skLineSegment(sketch, "E1926", {"start": v(0.71, -1.42) * mm, "end": v(0.69, -1.27) * mm});
            skLineSegment(sketch, "E1927", {"start": v(0.69, -1.27) * mm, "end": v(0.64, -1.13) * mm});
            skLineSegment(sketch, "E1928", {"start": v(0.64, -1.13) * mm, "end": v(0.58, -1.01) * mm});
            skLineSegment(sketch, "E1929", {"start": v(0.58, -1.01) * mm, "end": v(0.5, -0.91) * mm});
            skLineSegment(sketch, "E1930", {"start": v(0.5, -0.91) * mm, "end": v(0.42, -0.84) * mm});
            skLineSegment(sketch, "E1931", {"start": v(0.42, -0.84) * mm, "end": v(0.33, -0.8) * mm});
            skLineSegment(sketch, "E1932", {"start": v(0.33, -0.8) * mm, "end": v(0.23, -0.77) * mm});
            skLineSegment(sketch, "E1933", {"start": v(0.23, -0.77) * mm, "end": v(0.13, -0.79) * mm});
            skLineSegment(sketch, "E1934", {"start": v(0.13, -0.79) * mm, "end": v(0.04, -0.84) * mm});
            skLineSegment(sketch, "E1935", {"start": v(0.04, -0.84) * mm, "end": v(-0.05, -0.91) * mm});
            skLineSegment(sketch, "E1936", {"start": v(-0.05, -0.91) * mm, "end": v(-0.12, -1.01) * mm});
            skLineSegment(sketch, "E1937", {"start": v(-0.12, -1.01) * mm, "end": v(-0.18, -1.13) * mm});
            skLineSegment(sketch, "E1938", {"start": v(-0.18, -1.13) * mm, "end": v(-0.23, -1.27) * mm});
            skLineSegment(sketch, "E1939", {"start": v(-0.23, -1.27) * mm, "end": v(-0.26, -1.42) * mm});
            skLineSegment(sketch, "E1940", {"start": v(-0.26, -1.42) * mm, "end": v(-0.27, -1.59) * mm});
            skLineSegment(sketch, "E1941", {"start": v(-0.27, -1.59) * mm, "end": v(-0.27, -2.66) * mm});
            skLineSegment(sketch, "E1942", {"start": v(-0.27, -2.66) * mm, "end": v(-0.27, -3.74) * mm});
            skLineSegment(sketch, "E1943", {"start": v(-0.27, -3.74) * mm, "end": v(-0.27, -4.82) * mm});
            skLineSegment(sketch, "E1944", {"start": v(-0.27, -4.82) * mm, "end": v(-0.27, -5.9) * mm});
            skLineSegment(sketch, "E1945", {"start": v(-0.27, -5.9) * mm, "end": v(-0.28, -6.97) * mm});
            skLineSegment(sketch, "E1946", {"start": v(-0.28, -6.97) * mm, "end": v(-0.28, -8.05) * mm});
            skLineSegment(sketch, "E1947", {"start": v(-0.28, -8.05) * mm, "end": v(-0.28, -9.13) * mm});
            skLineSegment(sketch, "E1948", {"start": v(-0.28, -9.13) * mm, "end": v(-0.28, -10.2) * mm});
            skLineSegment(sketch, "E1949", {"start": v(-0.28, -10.2) * mm, "end": v(-0.27, -10.37) * mm});
            skLineSegment(sketch, "E1950", {"start": v(-0.27, -10.37) * mm, "end": v(-0.24, -10.52) * mm});
            skLineSegment(sketch, "E1951", {"start": v(-0.24, -10.52) * mm, "end": v(-0.2, -10.66) * mm});
            skLineSegment(sketch, "E1952", {"start": v(-0.2, -10.66) * mm, "end": v(-0.13, -10.78) * mm});
            skLineSegment(sketch, "E1953", {"start": v(-0.13, -10.78) * mm, "end": v(-0.06, -10.88) * mm});
            skLineSegment(sketch, "E1954", {"start": v(-0.06, -10.88) * mm, "end": v(0.02, -10.95) * mm});
            skLineSegment(sketch, "E1955", {"start": v(0.02, -10.95) * mm, "end": v(0.12, -11) * mm});
            skLineSegment(sketch, "E1956", {"start": v(0.12, -11) * mm, "end": v(0.22, -11.02) * mm});
            skLineSegment(sketch, "E1957", {"start": v(0.22, -11.02) * mm, "end": v(0.32, -11) * mm});
            skLineSegment(sketch, "E1958", {"start": v(0.32, -11) * mm, "end": v(0.4, -10.95) * mm});
            skLineSegment(sketch, "E1959", {"start": v(0.4, -10.95) * mm, "end": v(0.5, -10.88) * mm});
            skLineSegment(sketch, "E1960", {"start": v(0.5, -10.88) * mm, "end": v(0.57, -10.78) * mm});
            skLineSegment(sketch, "E1961", {"start": v(0.57, -10.78) * mm, "end": v(0.63, -10.66) * mm});
            skLineSegment(sketch, "E1962", {"start": v(0.63, -10.66) * mm, "end": v(0.68, -10.52) * mm});
            skLineSegment(sketch, "E1963", {"start": v(0.68, -10.52) * mm, "end": v(0.7, -10.37) * mm});
            skLineSegment(sketch, "E1964", {"start": v(0.7, -10.37) * mm, "end": v(0.71, -10.2) * mm});
            skLineSegment(sketch, "E1965", {"start": v(0.71, -10.2) * mm, "end": v(0.72, -9.9) * mm});
            skLineSegment(sketch, "E1966", {"start": v(0.72, -9.9) * mm, "end": v(0.72, -9.6) * mm});
            skLineSegment(sketch, "E1967", {"start": v(0.72, -9.6) * mm, "end": v(0.72, -9.3) * mm});
            skLineSegment(sketch, "E1968", {"start": v(0.72, -9.3) * mm, "end": v(0.72, -9) * mm});
            skLineSegment(sketch, "E1969", {"start": v(0.72, -9) * mm, "end": v(0.72, -8.69) * mm});
            skLineSegment(sketch, "E1970", {"start": v(0.72, -8.69) * mm, "end": v(0.72, -8.38) * mm});
            skLineSegment(sketch, "E1971", {"start": v(0.72, -8.38) * mm, "end": v(0.72, -8.08) * mm});
            skLineSegment(sketch, "E1972", {"start": v(0.72, -8.08) * mm, "end": v(0.72, -7.78) * mm});
            skLineSegment(sketch, "E1973", {"start": v(0.72, -7.78) * mm, "end": v(0.74, -7.34) * mm});
            skLineSegment(sketch, "E1974", {"start": v(0.74, -7.34) * mm, "end": v(0.8, -6.97) * mm});
            skLineSegment(sketch, "E1975", {"start": v(0.8, -6.97) * mm, "end": v(0.92, -6.65) * mm});
            skLineSegment(sketch, "E1976", {"start": v(0.92, -6.65) * mm, "end": v(1.08, -6.39) * mm});
            skLineSegment(sketch, "E1977", {"start": v(1.08, -6.39) * mm, "end": v(1.29, -6.19) * mm});
            skLineSegment(sketch, "E1978", {"start": v(1.29, -6.19) * mm, "end": v(1.54, -6.04) * mm});
            skLineSegment(sketch, "E1979", {"start": v(1.54, -6.04) * mm, "end": v(1.83, -5.95) * mm});
            skLineSegment(sketch, "E1980", {"start": v(1.83, -5.95) * mm, "end": v(2.18, -5.92) * mm});
            skLineSegment(sketch, "E1981", {"start": v(2.18, -5.92) * mm, "end": v(2.45, -5.94) * mm});
            skLineSegment(sketch, "E1982", {"start": v(2.45, -5.94) * mm, "end": v(2.67, -6.02) * mm});
            skLineSegment(sketch, "E1983", {"start": v(2.67, -6.02) * mm, "end": v(2.85, -6.14) * mm});
            skLineSegment(sketch, "E1984", {"start": v(2.85, -6.14) * mm, "end": v(3, -6.3) * mm});
            skLineSegment(sketch, "E1985", {"start": v(3, -6.3) * mm, "end": v(3.11, -6.5) * mm});
            skLineSegment(sketch, "E1986", {"start": v(3.11, -6.5) * mm, "end": v(3.2, -6.7) * mm});
            skLineSegment(sketch, "E1987", {"start": v(3.2, -6.7) * mm, "end": v(3.26, -6.94) * mm});
            skLineSegment(sketch, "E1988", {"start": v(3.26, -6.94) * mm, "end": v(3.3, -7.2) * mm});
            skLineSegment(sketch, "E1989", {"start": v(3.3, -7.2) * mm, "end": v(3.32, -7.36) * mm});
            skLineSegment(sketch, "E1990", {"start": v(3.32, -7.36) * mm, "end": v(3.33, -7.52) * mm});
            skLineSegment(sketch, "E1991", {"start": v(3.33, -7.52) * mm, "end": v(3.35, -7.69) * mm});
            skLineSegment(sketch, "E1992", {"start": v(3.35, -7.69) * mm, "end": v(3.36, -7.85) * mm});
            skLineSegment(sketch, "E1993", {"start": v(3.36, -7.85) * mm, "end": v(3.36, -8.02) * mm});
            skLineSegment(sketch, "E1994", {"start": v(3.36, -8.02) * mm, "end": v(3.37, -8.18) * mm});
            skLineSegment(sketch, "E1995", {"start": v(3.37, -8.18) * mm, "end": v(3.37, -8.35) * mm});
            skLineSegment(sketch, "E1996", {"start": v(3.37, -8.35) * mm, "end": v(3.37, -8.51) * mm});
            skLineSegment(sketch, "E1997", {"start": v(3.37, -8.51) * mm, "end": v(3.37, -8.73) * mm});
            skLineSegment(sketch, "E1998", {"start": v(3.37, -8.73) * mm, "end": v(3.37, -8.94) * mm});
            skLineSegment(sketch, "E1999", {"start": v(3.37, -8.94) * mm, "end": v(3.37, -9.15) * mm});
            skLineSegment(sketch, "E2000", {"start": v(3.37, -9.15) * mm, "end": v(3.36, -9.36) * mm});
            skLineSegment(sketch, "E2001", {"start": v(3.36, -9.36) * mm, "end": v(3.36, -9.57) * mm});
            skLineSegment(sketch, "E2002", {"start": v(3.36, -9.57) * mm, "end": v(3.36, -9.78) * mm});
            skLineSegment(sketch, "E2003", {"start": v(3.36, -9.78) * mm, "end": v(3.36, -10) * mm});
            skLineSegment(sketch, "E2004", {"start": v(3.36, -10) * mm, "end": v(3.36, -10.2) * mm});
            skLineSegment(sketch, "E2005", {"start": v(3.36, -10.2) * mm, "end": v(3.37, -10.37) * mm});
            skLineSegment(sketch, "E2006", {"start": v(3.37, -10.37) * mm, "end": v(3.4, -10.52) * mm});
            skLineSegment(sketch, "E2007", {"start": v(3.4, -10.52) * mm, "end": v(3.45, -10.66) * mm});
            skLineSegment(sketch, "E2008", {"start": v(3.45, -10.66) * mm, "end": v(3.51, -10.78) * mm});
            skLineSegment(sketch, "E2009", {"start": v(3.51, -10.78) * mm, "end": v(3.6, -10.88) * mm});
            skLineSegment(sketch, "E2010", {"start": v(3.6, -10.88) * mm, "end": v(3.68, -10.96) * mm});
            skLineSegment(sketch, "E2011", {"start": v(3.68, -10.96) * mm, "end": v(3.78, -11) * mm});
            skLineSegment(sketch, "E2012", {"start": v(3.78, -11) * mm, "end": v(3.88, -11.02) * mm});
            skLineSegment(sketch, "E2013", {"start": v(3.88, -11.02) * mm, "end": v(3.98, -11) * mm});
            skLineSegment(sketch, "E2014", {"start": v(3.98, -11) * mm, "end": v(4.08, -10.96) * mm});
            skLineSegment(sketch, "E2015", {"start": v(4.08, -10.96) * mm, "end": v(4.17, -10.88) * mm});
            skLineSegment(sketch, "E2016", {"start": v(4.17, -10.88) * mm, "end": v(4.24, -10.78) * mm});
            skLineSegment(sketch, "E2017", {"start": v(4.24, -10.78) * mm, "end": v(4.3, -10.66) * mm});
            skLineSegment(sketch, "E2018", {"start": v(4.3, -10.66) * mm, "end": v(4.36, -10.53) * mm});
            skLineSegment(sketch, "E2019", {"start": v(4.36, -10.53) * mm, "end": v(4.39, -10.37) * mm});
            skLineSegment(sketch, "E2020", {"start": v(10.52, -7.06) * mm, "end": v(10.45, -6.82) * mm});
            skLineSegment(sketch, "E2021", {"start": v(10.45, -6.82) * mm, "end": v(10.36, -6.59) * mm});
            skLineSegment(sketch, "E2022", {"start": v(10.36, -6.59) * mm, "end": v(10.25, -6.37) * mm});
            skLineSegment(sketch, "E2023", {"start": v(10.25, -6.37) * mm, "end": v(10.1, -6.16) * mm});
            skLineSegment(sketch, "E2024", {"start": v(10.1, -6.16) * mm, "end": v(9.95, -5.96) * mm});
            skLineSegment(sketch, "E2025", {"start": v(9.95, -5.96) * mm, "end": v(9.76, -5.78) * mm});
            skLineSegment(sketch, "E2026", {"start": v(9.76, -5.78) * mm, "end": v(9.56, -5.6) * mm});
            skLineSegment(sketch, "E2027", {"start": v(9.56, -5.6) * mm, "end": v(9.35, -5.46) * mm});
            skLineSegment(sketch, "E2028", {"start": v(9.35, -5.46) * mm, "end": v(9.13, -5.33) * mm});
            skLineSegment(sketch, "E2029", {"start": v(9.13, -5.33) * mm, "end": v(8.9, -5.23) * mm});
            skLineSegment(sketch, "E2030", {"start": v(8.9, -5.23) * mm, "end": v(8.66, -5.14) * mm});
            skLineSegment(sketch, "E2031", {"start": v(8.66, -5.14) * mm, "end": v(8.41, -5.08) * mm});
            skLineSegment(sketch, "E2032", {"start": v(8.41, -5.08) * mm, "end": v(8.16, -5.04) * mm});
            skLineSegment(sketch, "E2033", {"start": v(8.16, -5.04) * mm, "end": v(7.89, -5.03) * mm});
            skLineSegment(sketch, "E2034", {"start": v(7.89, -5.03) * mm, "end": v(7.57, -5.03) * mm});
            skLineSegment(sketch, "E2035", {"start": v(7.57, -5.03) * mm, "end": v(7.27, -5.07) * mm});
            skLineSegment(sketch, "E2036", {"start": v(7.27, -5.07) * mm, "end": v(6.98, -5.15) * mm});
            skLineSegment(sketch, "E2037", {"start": v(6.98, -5.15) * mm, "end": v(6.7, -5.25) * mm});
            skLineSegment(sketch, "E2038", {"start": v(6.7, -5.25) * mm, "end": v(6.45, -5.38) * mm});
            skLineSegment(sketch, "E2039", {"start": v(6.45, -5.38) * mm, "end": v(6.21, -5.54) * mm});
            skLineSegment(sketch, "E2040", {"start": v(6.21, -5.54) * mm, "end": v(6, -5.74) * mm});
            skLineSegment(sketch, "E2041", {"start": v(6, -5.74) * mm, "end": v(5.78, -5.96) * mm});
            skLineSegment(sketch, "E2042", {"start": v(5.78, -5.96) * mm, "end": v(5.61, -6.19) * mm});
            skLineSegment(sketch, "E2043", {"start": v(5.61, -6.19) * mm, "end": v(5.46, -6.43) * mm});
            skLineSegment(sketch, "E2044", {"start": v(5.46, -6.43) * mm, "end": v(5.34, -6.69) * mm});
            skLineSegment(sketch, "E2045", {"start": v(5.34, -6.69) * mm, "end": v(5.23, -6.95) * mm});
            skLineSegment(sketch, "E2046", {"start": v(5.23, -6.95) * mm, "end": v(5.15, -7.23) * mm});
            skLineSegment(sketch, "E2047", {"start": v(5.15, -7.23) * mm, "end": v(5.1, -7.52) * mm});
            skLineSegment(sketch, "E2048", {"start": v(5.1, -7.52) * mm, "end": v(5.06, -7.83) * mm});
            skLineSegment(sketch, "E2049", {"start": v(5.06, -7.83) * mm, "end": v(5.05, -8.14) * mm});
            skLineSegment(sketch, "E2050", {"start": v(5.05, -8.14) * mm, "end": v(5.07, -8.45) * mm});
            skLineSegment(sketch, "E2051", {"start": v(5.07, -8.45) * mm, "end": v(5.1, -8.75) * mm});
            skLineSegment(sketch, "E2052", {"start": v(5.1, -8.75) * mm, "end": v(5.16, -9.03) * mm});
            skLineSegment(sketch, "E2053", {"start": v(5.16, -9.03) * mm, "end": v(5.25, -9.3) * mm});
            skLineSegment(sketch, "E2054", {"start": v(5.25, -9.3) * mm, "end": v(5.35, -9.56) * mm});
            skLineSegment(sketch, "E2055", {"start": v(5.35, -9.56) * mm, "end": v(5.48, -9.8) * mm});
            skLineSegment(sketch, "E2056", {"start": v(5.48, -9.8) * mm, "end": v(5.63, -10.04) * mm});
            skLineSegment(sketch, "E2057", {"start": v(5.63, -10.04) * mm, "end": v(5.8, -10.27) * mm});
            skLineSegment(sketch, "E2058", {"start": v(5.8, -10.27) * mm, "end": v(6.06, -10.52) * mm});
            skLineSegment(sketch, "E2059", {"start": v(6.06, -10.52) * mm, "end": v(6.33, -10.73) * mm});
            skLineSegment(sketch, "E2060", {"start": v(6.33, -10.73) * mm, "end": v(6.62, -10.9) * mm});
            skLineSegment(sketch, "E2061", {"start": v(6.62, -10.9) * mm, "end": v(6.93, -11.04) * mm});
            skLineSegment(sketch, "E2062", {"start": v(6.93, -11.04) * mm, "end": v(7.26, -11.14) * mm});
            skLineSegment(sketch, "E2063", {"start": v(7.26, -11.14) * mm, "end": v(7.6, -11.2) * mm});
            skLineSegment(sketch, "E2064", {"start": v(7.6, -11.2) * mm, "end": v(7.94, -11.21) * mm});
            skLineSegment(sketch, "E2065", {"start": v(7.94, -11.21) * mm, "end": v(8.29, -11.19) * mm});
            skLineSegment(sketch, "E2066", {"start": v(8.29, -11.19) * mm, "end": v(8.38, -11.18) * mm});
            skLineSegment(sketch, "E2067", {"start": v(8.38, -11.18) * mm, "end": v(8.47, -11.16) * mm});
            skLineSegment(sketch, "E2068", {"start": v(8.47, -11.16) * mm, "end": v(8.57, -11.14) * mm});
            skLineSegment(sketch, "E2069", {"start": v(8.57, -11.14) * mm, "end": v(8.66, -11.12) * mm});
            skLineSegment(sketch, "E2070", {"start": v(8.66, -11.12) * mm, "end": v(8.75, -11.1) * mm});
            skLineSegment(sketch, "E2071", {"start": v(8.75, -11.1) * mm, "end": v(8.84, -11.07) * mm});
            skLineSegment(sketch, "E2072", {"start": v(8.84, -11.07) * mm, "end": v(8.93, -11.03) * mm});
            skLineSegment(sketch, "E2073", {"start": v(8.93, -11.03) * mm, "end": v(9.01, -11) * mm});
            skLineSegment(sketch, "E2074", {"start": v(9.01, -11) * mm, "end": v(9.16, -10.93) * mm});
            skLineSegment(sketch, "E2075", {"start": v(9.16, -10.93) * mm, "end": v(9.3, -10.86) * mm});
            skLineSegment(sketch, "E2076", {"start": v(9.3, -10.86) * mm, "end": v(9.44, -10.77) * mm});
            skLineSegment(sketch, "E2077", {"start": v(9.44, -10.77) * mm, "end": v(9.57, -10.68) * mm});
            skLineSegment(sketch, "E2078", {"start": v(9.57, -10.68) * mm, "end": v(9.7, -10.58) * mm});
            skLineSegment(sketch, "E2079", {"start": v(9.7, -10.58) * mm, "end": v(9.83, -10.48) * mm});
            skLineSegment(sketch, "E2080", {"start": v(9.83, -10.48) * mm, "end": v(9.95, -10.37) * mm});
            skLineSegment(sketch, "E2081", {"start": v(9.95, -10.37) * mm, "end": v(10.06, -10.26) * mm});
            skLineSegment(sketch, "E2082", {"start": v(10.06, -10.26) * mm, "end": v(10.11, -10.2) * mm});
            skLineSegment(sketch, "E2083", {"start": v(10.11, -10.2) * mm, "end": v(10.17, -10.14) * mm});
            skLineSegment(sketch, "E2084", {"start": v(10.17, -10.14) * mm, "end": v(10.22, -10.08) * mm});
            skLineSegment(sketch, "E2085", {"start": v(10.22, -10.08) * mm, "end": v(10.27, -10.02) * mm});
            skLineSegment(sketch, "E2086", {"start": v(10.27, -10.02) * mm, "end": v(10.3, -9.95) * mm});
            skLineSegment(sketch, "E2087", {"start": v(10.3, -9.95) * mm, "end": v(10.34, -9.88) * mm});
            skLineSegment(sketch, "E2088", {"start": v(10.34, -9.88) * mm, "end": v(10.36, -9.8) * mm});
            skLineSegment(sketch, "E2089", {"start": v(10.36, -9.8) * mm, "end": v(10.37, -9.73) * mm});
            skLineSegment(sketch, "E2090", {"start": v(10.37, -9.73) * mm, "end": v(10.36, -9.61) * mm});
            skLineSegment(sketch, "E2091", {"start": v(10.36, -9.61) * mm, "end": v(10.32, -9.5) * mm});
            skLineSegment(sketch, "E2092", {"start": v(10.32, -9.5) * mm, "end": v(10.26, -9.42) * mm});
            skLineSegment(sketch, "E2093", {"start": v(10.26, -9.42) * mm, "end": v(10.18, -9.35) * mm});
            skLineSegment(sketch, "E2094", {"start": v(10.18, -9.35) * mm, "end": v(10.08, -9.3) * mm});
            skLineSegment(sketch, "E2095", {"start": v(10.08, -9.3) * mm, "end": v(9.97, -9.26) * mm});
            skLineSegment(sketch, "E2096", {"start": v(9.97, -9.26) * mm, "end": v(9.86, -9.26) * mm});
            skLineSegment(sketch, "E2097", {"start": v(9.86, -9.26) * mm, "end": v(9.74, -9.28) * mm});
            skLineSegment(sketch, "E2098", {"start": v(9.74, -9.28) * mm, "end": v(9.65, -9.33) * mm});
            skLineSegment(sketch, "E2099", {"start": v(9.65, -9.33) * mm, "end": v(9.57, -9.38) * mm});
            skLineSegment(sketch, "E2100", {"start": v(9.57, -9.38) * mm, "end": v(9.49, -9.45) * mm});
            skLineSegment(sketch, "E2101", {"start": v(9.49, -9.45) * mm, "end": v(9.42, -9.53) * mm});
            skLineSegment(sketch, "E2102", {"start": v(9.42, -9.53) * mm, "end": v(9.35, -9.61) * mm});
            skLineSegment(sketch, "E2103", {"start": v(9.35, -9.61) * mm, "end": v(9.28, -9.7) * mm});
            skLineSegment(sketch, "E2104", {"start": v(9.28, -9.7) * mm, "end": v(9.21, -9.77) * mm});
            skLineSegment(sketch, "E2105", {"start": v(9.21, -9.77) * mm, "end": v(9.14, -9.85) * mm});
            skLineSegment(sketch, "E2106", {"start": v(9.14, -9.85) * mm, "end": v(9.01, -9.95) * mm});
            skLineSegment(sketch, "E2107", {"start": v(9.01, -9.95) * mm, "end": v(8.87, -10.04) * mm});
            skLineSegment(sketch, "E2108", {"start": v(8.87, -10.04) * mm, "end": v(8.72, -10.12) * mm});
            skLineSegment(sketch, "E2109", {"start": v(8.72, -10.12) * mm, "end": v(8.57, -10.18) * mm});
            skLineSegment(sketch, "E2110", {"start": v(8.57, -10.18) * mm, "end": v(8.4, -10.22) * mm});
            skLineSegment(sketch, "E2111", {"start": v(8.4, -10.22) * mm, "end": v(8.24, -10.25) * mm});
            skLineSegment(sketch, "E2112", {"start": v(8.24, -10.25) * mm, "end": v(8.07, -10.27) * mm});
            skLineSegment(sketch, "E2113", {"start": v(8.07, -10.27) * mm, "end": v(7.9, -10.28) * mm});
            skLineSegment(sketch, "E2114", {"start": v(7.9, -10.28) * mm, "end": v(7.53, -10.24) * mm});
            skLineSegment(sketch, "E2115", {"start": v(7.53, -10.24) * mm, "end": v(7.19, -10.13) * mm});
            skLineSegment(sketch, "E2116", {"start": v(7.19, -10.13) * mm, "end": v(6.88, -9.95) * mm});
            skLineSegment(sketch, "E2117", {"start": v(6.88, -9.95) * mm, "end": v(6.6, -9.72) * mm});
            skLineSegment(sketch, "E2118", {"start": v(6.6, -9.72) * mm, "end": v(6.39, -9.44) * mm});
            skLineSegment(sketch, "E2119", {"start": v(6.39, -9.44) * mm, "end": v(6.22, -9.12) * mm});
            skLineSegment(sketch, "E2120", {"start": v(6.22, -9.12) * mm, "end": v(6.12, -8.77) * mm});
            skLineSegment(sketch, "E2121", {"start": v(6.12, -8.77) * mm, "end": v(6.09, -8.4) * mm});
            skLineSegment(sketch, "E2122", {"start": v(6.09, -8.4) * mm, "end": v(6.1, -8.38) * mm});
            skLineSegment(sketch, "E2123", {"start": v(6.1, -8.38) * mm, "end": v(6.15, -8.35) * mm});
            skLineSegment(sketch, "E2124", {"start": v(6.15, -8.35) * mm, "end": v(6.23, -8.33) * mm});
            skLineSegment(sketch, "E2125", {"start": v(6.23, -8.33) * mm, "end": v(6.33, -8.32) * mm});
            skLineSegment(sketch, "E2126", {"start": v(6.33, -8.32) * mm, "end": v(6.45, -8.3) * mm});
            skLineSegment(sketch, "E2127", {"start": v(6.45, -8.3) * mm, "end": v(6.59, -8.3) * mm});
            skLineSegment(sketch, "E2128", {"start": v(6.59, -8.3) * mm, "end": v(6.74, -8.28) * mm});
            skLineSegment(sketch, "E2129", {"start": v(6.74, -8.28) * mm, "end": v(6.9, -8.28) * mm});
            skLineSegment(sketch, "E2130", {"start": v(6.9, -8.28) * mm, "end": v(7.26, -8.28) * mm});
            skLineSegment(sketch, "E2131", {"start": v(7.26, -8.28) * mm, "end": v(7.63, -8.28) * mm});
            skLineSegment(sketch, "E2132", {"start": v(7.63, -8.28) * mm, "end": v(8, -8.28) * mm});
            skLineSegment(sketch, "E2133", {"start": v(8, -8.28) * mm, "end": v(8.35, -8.28) * mm});
            skLineSegment(sketch, "E2134", {"start": v(8.35, -8.28) * mm, "end": v(8.72, -8.28) * mm});
            skLineSegment(sketch, "E2135", {"start": v(8.72, -8.28) * mm, "end": v(9.08, -8.28) * mm});
            skLineSegment(sketch, "E2136", {"start": v(9.08, -8.28) * mm, "end": v(9.44, -8.28) * mm});
            skLineSegment(sketch, "E2137", {"start": v(9.44, -8.28) * mm, "end": v(9.8, -8.28) * mm});
            skLineSegment(sketch, "E2138", {"start": v(9.8, -8.28) * mm, "end": v(9.97, -8.27) * mm});
            skLineSegment(sketch, "E2139", {"start": v(9.97, -8.27) * mm, "end": v(10.12, -8.23) * mm});
            skLineSegment(sketch, "E2140", {"start": v(10.12, -8.23) * mm, "end": v(10.26, -8.16) * mm});
            skLineSegment(sketch, "E2141", {"start": v(10.26, -8.16) * mm, "end": v(10.37, -8.07) * mm});
            skLineSegment(sketch, "E2142", {"start": v(10.37, -8.07) * mm, "end": v(10.47, -7.97) * mm});
            skLineSegment(sketch, "E2143", {"start": v(10.47, -7.97) * mm, "end": v(10.54, -7.85) * mm});
            skLineSegment(sketch, "E2144", {"start": v(10.54, -7.85) * mm, "end": v(10.58, -7.71) * mm});
            skLineSegment(sketch, "E2145", {"start": v(10.58, -7.71) * mm, "end": v(10.6, -7.57) * mm});
            skLineSegment(sketch, "E2146", {"start": v(10.6, -7.57) * mm, "end": v(10.57, -7.3) * mm});
            skLineSegment(sketch, "E2147", {"start": v(10.57, -7.3) * mm, "end": v(10.52, -7.06) * mm});
            skLineSegment(sketch, "E2148", {"start": v(9.35, -7.02) * mm, "end": v(9.3, -7.14) * mm});
            skLineSegment(sketch, "E2149", {"start": v(9.3, -7.14) * mm, "end": v(9.23, -7.25) * mm});
            skLineSegment(sketch, "E2150", {"start": v(9.23, -7.25) * mm, "end": v(9.13, -7.34) * mm});
            skLineSegment(sketch, "E2151", {"start": v(9.13, -7.34) * mm, "end": v(9.02, -7.4) * mm});
            skLineSegment(sketch, "E2152", {"start": v(9.02, -7.4) * mm, "end": v(8.9, -7.45) * mm});
            skLineSegment(sketch, "E2153", {"start": v(8.9, -7.45) * mm, "end": v(8.76, -7.46) * mm});
            skLineSegment(sketch, "E2154", {"start": v(8.76, -7.46) * mm, "end": v(8.65, -7.46) * mm});
            skLineSegment(sketch, "E2155", {"start": v(8.65, -7.46) * mm, "end": v(8.35, -7.46) * mm});
            skLineSegment(sketch, "E2156", {"start": v(8.35, -7.46) * mm, "end": v(7.93, -7.46) * mm});
            skLineSegment(sketch, "E2157", {"start": v(7.93, -7.46) * mm, "end": v(7.44, -7.46) * mm});
            skLineSegment(sketch, "E2158", {"start": v(7.44, -7.46) * mm, "end": v(6.96, -7.46) * mm});
            skLineSegment(sketch, "E2159", {"start": v(6.96, -7.46) * mm, "end": v(6.54, -7.46) * mm});
            skLineSegment(sketch, "E2160", {"start": v(6.54, -7.46) * mm, "end": v(6.24, -7.46) * mm});
            skLineSegment(sketch, "E2161", {"start": v(6.24, -7.46) * mm, "end": v(6.13, -7.46) * mm});
            skLineSegment(sketch, "E2162", {"start": v(6.13, -7.46) * mm, "end": v(6.16, -7.3) * mm});
            skLineSegment(sketch, "E2163", {"start": v(6.16, -7.3) * mm, "end": v(6.2, -7.14) * mm});
            skLineSegment(sketch, "E2164", {"start": v(6.2, -7.14) * mm, "end": v(6.26, -7) * mm});
            skLineSegment(sketch, "E2165", {"start": v(6.26, -7) * mm, "end": v(6.33, -6.85) * mm});
            skLineSegment(sketch, "E2166", {"start": v(6.33, -6.85) * mm, "end": v(6.41, -6.72) * mm});
            skLineSegment(sketch, "E2167", {"start": v(6.41, -6.72) * mm, "end": v(6.5, -6.6) * mm});
            skLineSegment(sketch, "E2168", {"start": v(6.5, -6.6) * mm, "end": v(6.62, -6.47) * mm});
            skLineSegment(sketch, "E2169", {"start": v(6.62, -6.47) * mm, "end": v(6.74, -6.36) * mm});
            skLineSegment(sketch, "E2170", {"start": v(6.74, -6.36) * mm, "end": v(6.82, -6.3) * mm});
            skLineSegment(sketch, "E2171", {"start": v(6.82, -6.3) * mm, "end": v(6.9, -6.24) * mm});
            skLineSegment(sketch, "E2172", {"start": v(6.9, -6.24) * mm, "end": v(7, -6.19) * mm});
            skLineSegment(sketch, "E2173", {"start": v(7, -6.19) * mm, "end": v(7.09, -6.14) * mm});
            skLineSegment(sketch, "E2174", {"start": v(7.09, -6.14) * mm, "end": v(7.18, -6.1) * mm});
            skLineSegment(sketch, "E2175", {"start": v(7.18, -6.1) * mm, "end": v(7.28, -6.06) * mm});
            skLineSegment(sketch, "E2176", {"start": v(7.28, -6.06) * mm, "end": v(7.38, -6.03) * mm});
            skLineSegment(sketch, "E2177", {"start": v(7.38, -6.03) * mm, "end": v(7.47, -6) * mm});
            skLineSegment(sketch, "E2178", {"start": v(7.47, -6) * mm, "end": v(7.72, -5.97) * mm});
            skLineSegment(sketch, "E2179", {"start": v(7.72, -5.97) * mm, "end": v(8, -5.96) * mm});
            skLineSegment(sketch, "E2180", {"start": v(8, -5.96) * mm, "end": v(8.28, -6) * mm});
            skLineSegment(sketch, "E2181", {"start": v(8.28, -6) * mm, "end": v(8.57, -6.07) * mm});
            skLineSegment(sketch, "E2182", {"start": v(8.57, -6.07) * mm, "end": v(8.85, -6.18) * mm});
            skLineSegment(sketch, "E2183", {"start": v(8.85, -6.18) * mm, "end": v(9.08, -6.33) * mm});
            skLineSegment(sketch, "E2184", {"start": v(9.08, -6.33) * mm, "end": v(9.26, -6.53) * mm});
            skLineSegment(sketch, "E2185", {"start": v(9.26, -6.53) * mm, "end": v(9.36, -6.77) * mm});
            skLineSegment(sketch, "E2186", {"start": v(9.36, -6.77) * mm, "end": v(9.37, -6.9) * mm});
            skLineSegment(sketch, "E2187", {"start": v(9.37, -6.9) * mm, "end": v(9.35, -7.02) * mm});
            skLineSegment(sketch, "E2188", {"start": v(18.91, -7.85) * mm, "end": v(18.82, -7.5) * mm});
            skLineSegment(sketch, "E2189", {"start": v(18.82, -7.5) * mm, "end": v(18.68, -7.17) * mm});
            skLineSegment(sketch, "E2190", {"start": v(18.68, -7.17) * mm, "end": v(18.49, -6.87) * mm});
            skLineSegment(sketch, "E2191", {"start": v(18.49, -6.87) * mm, "end": v(18.26, -6.6) * mm});
            skLineSegment(sketch, "E2192", {"start": v(18.26, -6.6) * mm, "end": v(17.98, -6.34) * mm});
            skLineSegment(sketch, "E2193", {"start": v(17.98, -6.34) * mm, "end": v(17.65, -6.12) * mm});
            skLineSegment(sketch, "E2194", {"start": v(17.65, -6.12) * mm, "end": v(17.28, -5.92) * mm});
            skLineSegment(sketch, "E2195", {"start": v(17.28, -5.92) * mm, "end": v(17.09, -5.83) * mm});
            skLineSegment(sketch, "E2196", {"start": v(17.09, -5.83) * mm, "end": v(16.9, -5.74) * mm});
            skLineSegment(sketch, "E2197", {"start": v(16.9, -5.74) * mm, "end": v(16.7, -5.65) * mm});
            skLineSegment(sketch, "E2198", {"start": v(16.7, -5.65) * mm, "end": v(16.5, -5.56) * mm});
            skLineSegment(sketch, "E2199", {"start": v(16.5, -5.56) * mm, "end": v(16.31, -5.47) * mm});
            skLineSegment(sketch, "E2200", {"start": v(16.31, -5.47) * mm, "end": v(16.12, -5.38) * mm});
            skLineSegment(sketch, "E2201", {"start": v(16.12, -5.38) * mm, "end": v(15.92, -5.3) * mm});
            skLineSegment(sketch, "E2202", {"start": v(15.92, -5.3) * mm, "end": v(15.73, -5.2) * mm});
            skLineSegment(sketch, "E2203", {"start": v(15.73, -5.2) * mm, "end": v(15.49, -5.08) * mm});
            skLineSegment(sketch, "E2204", {"start": v(15.49, -5.08) * mm, "end": v(15.28, -4.94) * mm});
            skLineSegment(sketch, "E2205", {"start": v(15.28, -4.94) * mm, "end": v(15.1, -4.8) * mm});
            skLineSegment(sketch, "E2206", {"start": v(15.1, -4.8) * mm, "end": v(14.96, -4.63) * mm});
            skLineSegment(sketch, "E2207", {"start": v(14.96, -4.63) * mm, "end": v(14.84, -4.46) * mm});
            skLineSegment(sketch, "E2208", {"start": v(14.84, -4.46) * mm, "end": v(14.76, -4.27) * mm});
            skLineSegment(sketch, "E2209", {"start": v(14.76, -4.27) * mm, "end": v(14.71, -4.08) * mm});
            skLineSegment(sketch, "E2210", {"start": v(14.71, -4.08) * mm, "end": v(14.7, -3.87) * mm});
            skLineSegment(sketch, "E2211", {"start": v(14.7, -3.87) * mm, "end": v(14.7, -3.72) * mm});
            skLineSegment(sketch, "E2212", {"start": v(14.7, -3.72) * mm, "end": v(14.72, -3.59) * mm});
            skLineSegment(sketch, "E2213", {"start": v(14.72, -3.59) * mm, "end": v(14.76, -3.46) * mm});
            skLineSegment(sketch, "E2214", {"start": v(14.76, -3.46) * mm, "end": v(14.8, -3.33) * mm});
            skLineSegment(sketch, "E2215", {"start": v(14.8, -3.33) * mm, "end": v(14.87, -3.2) * mm});
            skLineSegment(sketch, "E2216", {"start": v(14.87, -3.2) * mm, "end": v(14.95, -3.1) * mm});
            skLineSegment(sketch, "E2217", {"start": v(14.95, -3.1) * mm, "end": v(15.05, -2.99) * mm});
            skLineSegment(sketch, "E2218", {"start": v(15.05, -2.99) * mm, "end": v(15.15, -2.88) * mm});
            skLineSegment(sketch, "E2219", {"start": v(15.15, -2.88) * mm, "end": v(15.3, -2.77) * mm});
            skLineSegment(sketch, "E2220", {"start": v(15.3, -2.77) * mm, "end": v(15.47, -2.66) * mm});
            skLineSegment(sketch, "E2221", {"start": v(15.47, -2.66) * mm, "end": v(15.65, -2.58) * mm});
            skLineSegment(sketch, "E2222", {"start": v(15.65, -2.58) * mm, "end": v(15.83, -2.52) * mm});
            skLineSegment(sketch, "E2223", {"start": v(15.83, -2.52) * mm, "end": v(16.02, -2.48) * mm});
            skLineSegment(sketch, "E2224", {"start": v(16.02, -2.48) * mm, "end": v(16.22, -2.46) * mm});
            skLineSegment(sketch, "E2225", {"start": v(16.22, -2.46) * mm, "end": v(16.41, -2.46) * mm});
            skLineSegment(sketch, "E2226", {"start": v(16.41, -2.46) * mm, "end": v(16.6, -2.5) * mm});
            skLineSegment(sketch, "E2227", {"start": v(16.6, -2.5) * mm, "end": v(16.73, -2.54) * mm});
            skLineSegment(sketch, "E2228", {"start": v(16.73, -2.54) * mm, "end": v(16.86, -2.6) * mm});
            skLineSegment(sketch, "E2229", {"start": v(16.86, -2.6) * mm, "end": v(16.97, -2.68) * mm});
            skLineSegment(sketch, "E2230", {"start": v(16.97, -2.68) * mm, "end": v(17.08, -2.76) * mm});
            skLineSegment(sketch, "E2231", {"start": v(17.08, -2.76) * mm, "end": v(17.2, -2.85) * mm});
            skLineSegment(sketch, "E2232", {"start": v(17.2, -2.85) * mm, "end": v(17.3, -2.94) * mm});
            skLineSegment(sketch, "E2233", {"start": v(17.3, -2.94) * mm, "end": v(17.4, -3.03) * mm});
            skLineSegment(sketch, "E2234", {"start": v(17.4, -3.03) * mm, "end": v(17.52, -3.1) * mm});
            skLineSegment(sketch, "E2235", {"start": v(17.52, -3.1) * mm, "end": v(17.62, -3.18) * mm});
            skLineSegment(sketch, "E2236", {"start": v(17.62, -3.18) * mm, "end": v(17.73, -3.23) * mm});
            skLineSegment(sketch, "E2237", {"start": v(17.73, -3.23) * mm, "end": v(17.85, -3.28) * mm});
            skLineSegment(sketch, "E2238", {"start": v(17.85, -3.28) * mm, "end": v(17.96, -3.3) * mm});
            skLineSegment(sketch, "E2239", {"start": v(17.96, -3.3) * mm, "end": v(18.07, -3.3) * mm});
            skLineSegment(sketch, "E2240", {"start": v(18.07, -3.3) * mm, "end": v(18.18, -3.28) * mm});
            skLineSegment(sketch, "E2241", {"start": v(18.18, -3.28) * mm, "end": v(18.29, -3.22) * mm});
            skLineSegment(sketch, "E2242", {"start": v(18.29, -3.22) * mm, "end": v(18.39, -3.12) * mm});
            skLineSegment(sketch, "E2243", {"start": v(18.39, -3.12) * mm, "end": v(18.47, -2.92) * mm});
            skLineSegment(sketch, "E2244", {"start": v(18.47, -2.92) * mm, "end": v(18.44, -2.7) * mm});
            skLineSegment(sketch, "E2245", {"start": v(18.44, -2.7) * mm, "end": v(18.33, -2.5) * mm});
            skLineSegment(sketch, "E2246", {"start": v(18.33, -2.5) * mm, "end": v(18.15, -2.29) * mm});
            skLineSegment(sketch, "E2247", {"start": v(18.15, -2.29) * mm, "end": v(17.93, -2.1) * mm});
            skLineSegment(sketch, "E2248", {"start": v(17.93, -2.1) * mm, "end": v(17.7, -1.94) * mm});
            skLineSegment(sketch, "E2249", {"start": v(17.7, -1.94) * mm, "end": v(17.5, -1.8) * mm});
            skLineSegment(sketch, "E2250", {"start": v(17.5, -1.8) * mm, "end": v(17.33, -1.72) * mm});
            skLineSegment(sketch, "E2251", {"start": v(17.33, -1.72) * mm, "end": v(17.2, -1.67) * mm});
            skLineSegment(sketch, "E2252", {"start": v(17.2, -1.67) * mm, "end": v(17.06, -1.62) * mm});
            skLineSegment(sketch, "E2253", {"start": v(17.06, -1.62) * mm, "end": v(16.92, -1.58) * mm});
            skLineSegment(sketch, "E2254", {"start": v(16.92, -1.58) * mm, "end": v(16.78, -1.55) * mm});
            skLineSegment(sketch, "E2255", {"start": v(16.78, -1.55) * mm, "end": v(16.64, -1.53) * mm});
            skLineSegment(sketch, "E2256", {"start": v(16.64, -1.53) * mm, "end": v(16.5, -1.51) * mm});
            skLineSegment(sketch, "E2257", {"start": v(16.5, -1.51) * mm, "end": v(16.36, -1.5) * mm});
            skLineSegment(sketch, "E2258", {"start": v(16.36, -1.5) * mm, "end": v(16.21, -1.5) * mm});
            skLineSegment(sketch, "E2259", {"start": v(16.21, -1.5) * mm, "end": v(15.96, -1.52) * mm});
            skLineSegment(sketch, "E2260", {"start": v(15.96, -1.52) * mm, "end": v(15.71, -1.55) * mm});
            skLineSegment(sketch, "E2261", {"start": v(15.71, -1.55) * mm, "end": v(15.48, -1.61) * mm});
            skLineSegment(sketch, "E2262", {"start": v(15.48, -1.61) * mm, "end": v(15.25, -1.69) * mm});
            skLineSegment(sketch, "E2263", {"start": v(15.25, -1.69) * mm, "end": v(15.03, -1.78) * mm});
            skLineSegment(sketch, "E2264", {"start": v(15.03, -1.78) * mm, "end": v(14.82, -1.9) * mm});
            skLineSegment(sketch, "E2265", {"start": v(14.82, -1.9) * mm, "end": v(14.62, -2.04) * mm});
            skLineSegment(sketch, "E2266", {"start": v(14.62, -2.04) * mm, "end": v(14.43, -2.2) * mm});
            skLineSegment(sketch, "E2267", {"start": v(14.43, -2.2) * mm, "end": v(14.25, -2.37) * mm});
            skLineSegment(sketch, "E2268", {"start": v(14.25, -2.37) * mm, "end": v(14.1, -2.56) * mm});
            skLineSegment(sketch, "E2269", {"start": v(14.1, -2.56) * mm, "end": v(13.96, -2.76) * mm});
            skLineSegment(sketch, "E2270", {"start": v(13.96, -2.76) * mm, "end": v(13.86, -2.96) * mm});
            skLineSegment(sketch, "E2271", {"start": v(13.86, -2.96) * mm, "end": v(13.77, -3.18) * mm});
            skLineSegment(sketch, "E2272", {"start": v(13.77, -3.18) * mm, "end": v(13.71, -3.4) * mm});
            skLineSegment(sketch, "E2273", {"start": v(13.71, -3.4) * mm, "end": v(13.68, -3.64) * mm});
            skLineSegment(sketch, "E2274", {"start": v(13.68, -3.64) * mm, "end": v(13.66, -3.89) * mm});
            skLineSegment(sketch, "E2275", {"start": v(13.66, -3.89) * mm, "end": v(13.71, -4.25) * mm});
            skLineSegment(sketch, "E2276", {"start": v(13.71, -4.25) * mm, "end": v(13.84, -4.58) * mm});
            skLineSegment(sketch, "E2277", {"start": v(13.84, -4.58) * mm, "end": v(14.02, -4.9) * mm});
            skLineSegment(sketch, "E2278", {"start": v(14.02, -4.9) * mm, "end": v(14.23, -5.16) * mm});
            skLineSegment(sketch, "E2279", {"start": v(14.23, -5.16) * mm, "end": v(14.44, -5.39) * mm});
            skLineSegment(sketch, "E2280", {"start": v(14.44, -5.39) * mm, "end": v(14.62, -5.56) * mm});
            skLineSegment(sketch, "E2281", {"start": v(14.62, -5.56) * mm, "end": v(14.75, -5.66) * mm});
            skLineSegment(sketch, "E2282", {"start": v(14.75, -5.66) * mm, "end": v(14.8, -5.7) * mm});
            skLineSegment(sketch, "E2283", {"start": v(14.8, -5.7) * mm, "end": v(14.94, -5.8) * mm});
            skLineSegment(sketch, "E2284", {"start": v(14.94, -5.8) * mm, "end": v(15.1, -5.92) * mm});
            skLineSegment(sketch, "E2285", {"start": v(15.1, -5.92) * mm, "end": v(15.29, -6.03) * mm});
            skLineSegment(sketch, "E2286", {"start": v(15.29, -6.03) * mm, "end": v(15.48, -6.14) * mm});
            skLineSegment(sketch, "E2287", {"start": v(15.48, -6.14) * mm, "end": v(15.66, -6.26) * mm});
            skLineSegment(sketch, "E2288", {"start": v(15.66, -6.26) * mm, "end": v(15.85, -6.36) * mm});
            skLineSegment(sketch, "E2289", {"start": v(15.85, -6.36) * mm, "end": v(16.03, -6.45) * mm});
            skLineSegment(sketch, "E2290", {"start": v(16.03, -6.45) * mm, "end": v(16.19, -6.53) * mm});
            skLineSegment(sketch, "E2291", {"start": v(16.19, -6.53) * mm, "end": v(16.28, -6.57) * mm});
            skLineSegment(sketch, "E2292", {"start": v(16.28, -6.57) * mm, "end": v(16.37, -6.62) * mm});
            skLineSegment(sketch, "E2293", {"start": v(16.37, -6.62) * mm, "end": v(16.46, -6.66) * mm});
            skLineSegment(sketch, "E2294", {"start": v(16.46, -6.66) * mm, "end": v(16.56, -6.7) * mm});
            skLineSegment(sketch, "E2295", {"start": v(16.56, -6.7) * mm, "end": v(16.65, -6.74) * mm});
            skLineSegment(sketch, "E2296", {"start": v(16.65, -6.74) * mm, "end": v(16.74, -6.79) * mm});
            skLineSegment(sketch, "E2297", {"start": v(16.74, -6.79) * mm, "end": v(16.83, -6.83) * mm});
            skLineSegment(sketch, "E2298", {"start": v(16.83, -6.83) * mm, "end": v(16.93, -6.87) * mm});
            skLineSegment(sketch, "E2299", {"start": v(16.93, -6.87) * mm, "end": v(17.15, -7) * mm});
            skLineSegment(sketch, "E2300", {"start": v(17.15, -7) * mm, "end": v(17.34, -7.14) * mm});
            skLineSegment(sketch, "E2301", {"start": v(17.34, -7.14) * mm, "end": v(17.5, -7.3) * mm});
            skLineSegment(sketch, "E2302", {"start": v(17.5, -7.3) * mm, "end": v(17.65, -7.48) * mm});
            skLineSegment(sketch, "E2303", {"start": v(17.65, -7.48) * mm, "end": v(17.75, -7.69) * mm});
            skLineSegment(sketch, "E2304", {"start": v(17.75, -7.69) * mm, "end": v(17.83, -7.91) * mm});
            skLineSegment(sketch, "E2305", {"start": v(17.83, -7.91) * mm, "end": v(17.88, -8.16) * mm});
            skLineSegment(sketch, "E2306", {"start": v(17.88, -8.16) * mm, "end": v(17.9, -8.43) * mm});
            skLineSegment(sketch, "E2307", {"start": v(17.9, -8.43) * mm, "end": v(17.9, -8.61) * mm});
            skLineSegment(sketch, "E2308", {"start": v(17.9, -8.61) * mm, "end": v(17.87, -8.79) * mm});
            skLineSegment(sketch, "E2309", {"start": v(17.87, -8.79) * mm, "end": v(17.83, -8.95) * mm});
            skLineSegment(sketch, "E2310", {"start": v(17.83, -8.95) * mm, "end": v(17.77, -9.12) * mm});
            skLineSegment(sketch, "E2311", {"start": v(17.77, -9.12) * mm, "end": v(17.7, -9.27) * mm});
            skLineSegment(sketch, "E2312", {"start": v(17.7, -9.27) * mm, "end": v(17.6, -9.42) * mm});
            skLineSegment(sketch, "E2313", {"start": v(17.6, -9.42) * mm, "end": v(17.48, -9.56) * mm});
            skLineSegment(sketch, "E2314", {"start": v(17.48, -9.56) * mm, "end": v(17.34, -9.7) * mm});
            skLineSegment(sketch, "E2315", {"start": v(17.34, -9.7) * mm, "end": v(17.2, -9.82) * mm});
            skLineSegment(sketch, "E2316", {"start": v(17.2, -9.82) * mm, "end": v(17.05, -9.93) * mm});
            skLineSegment(sketch, "E2317", {"start": v(17.05, -9.93) * mm, "end": v(16.89, -10.02) * mm});
            skLineSegment(sketch, "E2318", {"start": v(16.89, -10.02) * mm, "end": v(16.72, -10.1) * mm});
            skLineSegment(sketch, "E2319", {"start": v(16.72, -10.1) * mm, "end": v(16.55, -10.15) * mm});
            skLineSegment(sketch, "E2320", {"start": v(16.55, -10.15) * mm, "end": v(16.38, -10.19) * mm});
            skLineSegment(sketch, "E2321", {"start": v(16.38, -10.19) * mm, "end": v(16.2, -10.21) * mm});
            skLineSegment(sketch, "E2322", {"start": v(16.2, -10.21) * mm, "end": v(16, -10.22) * mm});
            skLineSegment(sketch, "E2323", {"start": v(16, -10.22) * mm, "end": v(15.7, -10.18) * mm});
            skLineSegment(sketch, "E2324", {"start": v(15.7, -10.18) * mm, "end": v(15.45, -10.1) * mm});
            skLineSegment(sketch, "E2325", {"start": v(15.45, -10.1) * mm, "end": v(15.22, -9.98) * mm});
            skLineSegment(sketch, "E2326", {"start": v(15.22, -9.98) * mm, "end": v(15.03, -9.85) * mm});
            skLineSegment(sketch, "E2327", {"start": v(15.03, -9.85) * mm, "end": v(14.88, -9.71) * mm});
            skLineSegment(sketch, "E2328", {"start": v(14.88, -9.71) * mm, "end": v(14.78, -9.6) * mm});
            skLineSegment(sketch, "E2329", {"start": v(14.78, -9.6) * mm, "end": v(14.71, -9.51) * mm});
            skLineSegment(sketch, "E2330", {"start": v(14.71, -9.51) * mm, "end": v(14.69, -9.48) * mm});
            skLineSegment(sketch, "E2331", {"start": v(14.69, -9.48) * mm, "end": v(14.64, -9.41) * mm});
            skLineSegment(sketch, "E2332", {"start": v(14.64, -9.41) * mm, "end": v(14.6, -9.35) * mm});
            skLineSegment(sketch, "E2333", {"start": v(14.6, -9.35) * mm, "end": v(14.56, -9.28) * mm});
            skLineSegment(sketch, "E2334", {"start": v(14.56, -9.28) * mm, "end": v(14.51, -9.2) * mm});
            skLineSegment(sketch, "E2335", {"start": v(14.51, -9.2) * mm, "end": v(14.47, -9.14) * mm});
            skLineSegment(sketch, "E2336", {"start": v(14.47, -9.14) * mm, "end": v(14.43, -9.07) * mm});
            skLineSegment(sketch, "E2337", {"start": v(14.43, -9.07) * mm, "end": v(14.38, -9) * mm});
            skLineSegment(sketch, "E2338", {"start": v(14.38, -9) * mm, "end": v(14.34, -8.93) * mm});
            skLineSegment(sketch, "E2339", {"start": v(14.34, -8.93) * mm, "end": v(14.26, -8.82) * mm});
            skLineSegment(sketch, "E2340", {"start": v(14.26, -8.82) * mm, "end": v(14.15, -8.73) * mm});
            skLineSegment(sketch, "E2341", {"start": v(14.15, -8.73) * mm, "end": v(14.03, -8.66) * mm});
            skLineSegment(sketch, "E2342", {"start": v(14.03, -8.66) * mm, "end": v(13.9, -8.62) * mm});
            skLineSegment(sketch, "E2343", {"start": v(13.9, -8.62) * mm, "end": v(13.77, -8.6) * mm});
            skLineSegment(sketch, "E2344", {"start": v(13.77, -8.6) * mm, "end": v(13.64, -8.63) * mm});
            skLineSegment(sketch, "E2345", {"start": v(13.64, -8.63) * mm, "end": v(13.51, -8.68) * mm});
            skLineSegment(sketch, "E2346", {"start": v(13.51, -8.68) * mm, "end": v(13.4, -8.79) * mm});
            skLineSegment(sketch, "E2347", {"start": v(13.4, -8.79) * mm, "end": v(13.35, -8.87) * mm});
            skLineSegment(sketch, "E2348", {"start": v(13.35, -8.87) * mm, "end": v(13.32, -8.97) * mm});
            skLineSegment(sketch, "E2349", {"start": v(13.32, -8.97) * mm, "end": v(13.3, -9.07) * mm});
            skLineSegment(sketch, "E2350", {"start": v(13.3, -9.07) * mm, "end": v(13.31, -9.17) * mm});
            skLineSegment(sketch, "E2351", {"start": v(13.31, -9.17) * mm, "end": v(13.33, -9.28) * mm});
            skLineSegment(sketch, "E2352", {"start": v(13.33, -9.28) * mm, "end": v(13.36, -9.38) * mm});
            skLineSegment(sketch, "E2353", {"start": v(13.36, -9.38) * mm, "end": v(13.4, -9.48) * mm});
            skLineSegment(sketch, "E2354", {"start": v(13.4, -9.48) * mm, "end": v(13.44, -9.57) * mm});
            skLineSegment(sketch, "E2355", {"start": v(13.44, -9.57) * mm, "end": v(13.52, -9.73) * mm});
            skLineSegment(sketch, "E2356", {"start": v(13.52, -9.73) * mm, "end": v(13.6, -9.87) * mm});
            skLineSegment(sketch, "E2357", {"start": v(13.6, -9.87) * mm, "end": v(13.69, -10.02) * mm});
            skLineSegment(sketch, "E2358", {"start": v(13.69, -10.02) * mm, "end": v(13.79, -10.15) * mm});
            skLineSegment(sketch, "E2359", {"start": v(13.79, -10.15) * mm, "end": v(13.9, -10.28) * mm});
            skLineSegment(sketch, "E2360", {"start": v(13.9, -10.28) * mm, "end": v(14, -10.4) * mm});
            skLineSegment(sketch, "E2361", {"start": v(14, -10.4) * mm, "end": v(14.13, -10.52) * mm});
            skLineSegment(sketch, "E2362", {"start": v(14.13, -10.52) * mm, "end": v(14.26, -10.63) * mm});
            skLineSegment(sketch, "E2363", {"start": v(14.26, -10.63) * mm, "end": v(14.46, -10.77) * mm});
            skLineSegment(sketch, "E2364", {"start": v(14.46, -10.77) * mm, "end": v(14.66, -10.9) * mm});
            skLineSegment(sketch, "E2365", {"start": v(14.66, -10.9) * mm, "end": v(14.87, -11) * mm});
            skLineSegment(sketch, "E2366", {"start": v(14.87, -11) * mm, "end": v(15.09, -11.08) * mm});
            skLineSegment(sketch, "E2367", {"start": v(15.09, -11.08) * mm, "end": v(15.31, -11.14) * mm});
            skLineSegment(sketch, "E2368", {"start": v(15.31, -11.14) * mm, "end": v(15.55, -11.19) * mm});
            skLineSegment(sketch, "E2369", {"start": v(15.55, -11.19) * mm, "end": v(15.8, -11.22) * mm});
            skLineSegment(sketch, "E2370", {"start": v(15.8, -11.22) * mm, "end": v(16.04, -11.23) * mm});
            skLineSegment(sketch, "E2371", {"start": v(16.04, -11.23) * mm, "end": v(16.34, -11.21) * mm});
            skLineSegment(sketch, "E2372", {"start": v(16.34, -11.21) * mm, "end": v(16.63, -11.17) * mm});
            skLineSegment(sketch, "E2373", {"start": v(16.63, -11.17) * mm, "end": v(16.91, -11.1) * mm});
            skLineSegment(sketch, "E2374", {"start": v(16.91, -11.1) * mm, "end": v(17.18, -11) * mm});
            skLineSegment(sketch, "E2375", {"start": v(17.18, -11) * mm, "end": v(17.44, -10.88) * mm});
            skLineSegment(sketch, "E2376", {"start": v(17.44, -10.88) * mm, "end": v(17.69, -10.72) * mm});
            skLineSegment(sketch, "E2377", {"start": v(17.69, -10.72) * mm, "end": v(17.93, -10.54) * mm});
            skLineSegment(sketch, "E2378", {"start": v(17.93, -10.54) * mm, "end": v(18.15, -10.33) * mm});
            skLineSegment(sketch, "E2379", {"start": v(18.15, -10.33) * mm, "end": v(18.36, -10.1) * mm});
            skLineSegment(sketch, "E2380", {"start": v(18.36, -10.1) * mm, "end": v(18.53, -9.87) * mm});
            skLineSegment(sketch, "E2381", {"start": v(18.53, -9.87) * mm, "end": v(18.68, -9.62) * mm});
            skLineSegment(sketch, "E2382", {"start": v(18.68, -9.62) * mm, "end": v(18.8, -9.36) * mm});
            skLineSegment(sketch, "E2383", {"start": v(18.8, -9.36) * mm, "end": v(18.88, -9.1) * mm});
            skLineSegment(sketch, "E2384", {"start": v(18.88, -9.1) * mm, "end": v(18.94, -8.82) * mm});
            skLineSegment(sketch, "E2385", {"start": v(18.94, -8.82) * mm, "end": v(18.96, -8.53) * mm});
            skLineSegment(sketch, "E2386", {"start": v(18.96, -8.53) * mm, "end": v(18.96, -8.24) * mm});
            skLineSegment(sketch, "E2387", {"start": v(18.96, -8.24) * mm, "end": v(18.91, -7.85) * mm});
            skLineSegment(sketch, "E2388", {"start": v(25.08, -7.07) * mm, "end": v(25.01, -6.83) * mm});
            skLineSegment(sketch, "E2389", {"start": v(25.01, -6.83) * mm, "end": v(24.92, -6.6) * mm});
            skLineSegment(sketch, "E2390", {"start": v(24.92, -6.6) * mm, "end": v(24.8, -6.39) * mm});
            skLineSegment(sketch, "E2391", {"start": v(24.8, -6.39) * mm, "end": v(24.67, -6.18) * mm});
            skLineSegment(sketch, "E2392", {"start": v(24.67, -6.18) * mm, "end": v(24.5, -5.98) * mm});
            skLineSegment(sketch, "E2393", {"start": v(24.5, -5.98) * mm, "end": v(24.32, -5.8) * mm});
            skLineSegment(sketch, "E2394", {"start": v(24.32, -5.8) * mm, "end": v(24.12, -5.62) * mm});
            skLineSegment(sketch, "E2395", {"start": v(24.12, -5.62) * mm, "end": v(23.9, -5.48) * mm});
            skLineSegment(sketch, "E2396", {"start": v(23.9, -5.48) * mm, "end": v(23.69, -5.35) * mm});
            skLineSegment(sketch, "E2397", {"start": v(23.69, -5.35) * mm, "end": v(23.46, -5.24) * mm});
            skLineSegment(sketch, "E2398", {"start": v(23.46, -5.24) * mm, "end": v(23.22, -5.16) * mm});
            skLineSegment(sketch, "E2399", {"start": v(23.22, -5.16) * mm, "end": v(22.97, -5.1) * mm});
            skLineSegment(sketch, "E2400", {"start": v(22.97, -5.1) * mm, "end": v(22.72, -5.06) * mm});
            skLineSegment(sketch, "E2401", {"start": v(22.72, -5.06) * mm, "end": v(22.45, -5.04) * mm});
            skLineSegment(sketch, "E2402", {"start": v(22.45, -5.04) * mm, "end": v(22.13, -5.05) * mm});
            skLineSegment(sketch, "E2403", {"start": v(22.13, -5.05) * mm, "end": v(21.82, -5.1) * mm});
            skLineSegment(sketch, "E2404", {"start": v(21.82, -5.1) * mm, "end": v(21.54, -5.16) * mm});
            skLineSegment(sketch, "E2405", {"start": v(21.54, -5.16) * mm, "end": v(21.27, -5.26) * mm});
            skLineSegment(sketch, "E2406", {"start": v(21.27, -5.26) * mm, "end": v(21.01, -5.4) * mm});
            skLineSegment(sketch, "E2407", {"start": v(21.01, -5.4) * mm, "end": v(20.77, -5.56) * mm});
            skLineSegment(sketch, "E2408", {"start": v(20.77, -5.56) * mm, "end": v(20.55, -5.75) * mm});
            skLineSegment(sketch, "E2409", {"start": v(20.55, -5.75) * mm, "end": v(20.34, -5.98) * mm});
            skLineSegment(sketch, "E2410", {"start": v(20.34, -5.98) * mm, "end": v(20.17, -6.2) * mm});
            skLineSegment(sketch, "E2411", {"start": v(20.17, -6.2) * mm, "end": v(20.02, -6.45) * mm});
            skLineSegment(sketch, "E2412", {"start": v(20.02, -6.45) * mm, "end": v(19.9, -6.7) * mm});
            skLineSegment(sketch, "E2413", {"start": v(19.9, -6.7) * mm, "end": v(19.8, -6.97) * mm});
            skLineSegment(sketch, "E2414", {"start": v(19.8, -6.97) * mm, "end": v(19.71, -7.25) * mm});
            skLineSegment(sketch, "E2415", {"start": v(19.71, -7.25) * mm, "end": v(19.66, -7.54) * mm});
            skLineSegment(sketch, "E2416", {"start": v(19.66, -7.54) * mm, "end": v(19.62, -7.85) * mm});
            skLineSegment(sketch, "E2417", {"start": v(19.62, -7.85) * mm, "end": v(19.61, -8.16) * mm});
            skLineSegment(sketch, "E2418", {"start": v(19.61, -8.16) * mm, "end": v(19.63, -8.47) * mm});
            skLineSegment(sketch, "E2419", {"start": v(19.63, -8.47) * mm, "end": v(19.66, -8.77) * mm});
            skLineSegment(sketch, "E2420", {"start": v(19.66, -8.77) * mm, "end": v(19.72, -9.05) * mm});
            skLineSegment(sketch, "E2421", {"start": v(19.72, -9.05) * mm, "end": v(19.8, -9.32) * mm});
            skLineSegment(sketch, "E2422", {"start": v(19.8, -9.32) * mm, "end": v(19.91, -9.58) * mm});
            skLineSegment(sketch, "E2423", {"start": v(19.91, -9.58) * mm, "end": v(20.04, -9.83) * mm});
            skLineSegment(sketch, "E2424", {"start": v(20.04, -9.83) * mm, "end": v(20.2, -10.06) * mm});
            skLineSegment(sketch, "E2425", {"start": v(20.2, -10.06) * mm, "end": v(20.37, -10.28) * mm});
            skLineSegment(sketch, "E2426", {"start": v(20.37, -10.28) * mm, "end": v(20.57, -10.5) * mm});
            skLineSegment(sketch, "E2427", {"start": v(20.57, -10.5) * mm, "end": v(20.8, -10.69) * mm});
            skLineSegment(sketch, "E2428", {"start": v(20.8, -10.69) * mm, "end": v(21.03, -10.85) * mm});
            skLineSegment(sketch, "E2429", {"start": v(21.03, -10.85) * mm, "end": v(21.28, -10.98) * mm});
            skLineSegment(sketch, "E2430", {"start": v(21.28, -10.98) * mm, "end": v(21.54, -11.08) * mm});
            skLineSegment(sketch, "E2431", {"start": v(21.54, -11.08) * mm, "end": v(21.82, -11.16) * mm});
            skLineSegment(sketch, "E2432", {"start": v(21.82, -11.16) * mm, "end": v(22.12, -11.21) * mm});
            skLineSegment(sketch, "E2433", {"start": v(22.12, -11.21) * mm, "end": v(22.43, -11.23) * mm});
            skLineSegment(sketch, "E2434", {"start": v(22.43, -11.23) * mm, "end": v(22.68, -11.23) * mm});
            skLineSegment(sketch, "E2435", {"start": v(22.68, -11.23) * mm, "end": v(22.94, -11.2) * mm});
            skLineSegment(sketch, "E2436", {"start": v(22.94, -11.2) * mm, "end": v(23.19, -11.14) * mm});
            skLineSegment(sketch, "E2437", {"start": v(23.19, -11.14) * mm, "end": v(23.43, -11.06) * mm});
            skLineSegment(sketch, "E2438", {"start": v(23.43, -11.06) * mm, "end": v(23.67, -10.96) * mm});
            skLineSegment(sketch, "E2439", {"start": v(23.67, -10.96) * mm, "end": v(23.9, -10.84) * mm});
            skLineSegment(sketch, "E2440", {"start": v(23.9, -10.84) * mm, "end": v(24.12, -10.7) * mm});
            skLineSegment(sketch, "E2441", {"start": v(24.12, -10.7) * mm, "end": v(24.32, -10.55) * mm});
            skLineSegment(sketch, "E2442", {"start": v(24.32, -10.55) * mm, "end": v(24.41, -10.48) * mm});
            skLineSegment(sketch, "E2443", {"start": v(24.41, -10.48) * mm, "end": v(24.53, -10.38) * mm});
            skLineSegment(sketch, "E2444", {"start": v(24.53, -10.38) * mm, "end": v(24.65, -10.27) * mm});
            skLineSegment(sketch, "E2445", {"start": v(24.65, -10.27) * mm, "end": v(24.77, -10.14) * mm});
            skLineSegment(sketch, "E2446", {"start": v(24.77, -10.14) * mm, "end": v(24.88, -10) * mm});
            skLineSegment(sketch, "E2447", {"start": v(24.88, -10) * mm, "end": v(24.96, -9.86) * mm});
            skLineSegment(sketch, "E2448", {"start": v(24.96, -9.86) * mm, "end": v(25, -9.73) * mm});
            skLineSegment(sketch, "E2449", {"start": v(25, -9.73) * mm, "end": v(24.98, -9.61) * mm});
            skLineSegment(sketch, "E2450", {"start": v(24.98, -9.61) * mm, "end": v(24.94, -9.54) * mm});
            skLineSegment(sketch, "E2451", {"start": v(24.94, -9.54) * mm, "end": v(24.89, -9.47) * mm});
            skLineSegment(sketch, "E2452", {"start": v(24.89, -9.47) * mm, "end": v(24.82, -9.4) * mm});
            skLineSegment(sketch, "E2453", {"start": v(24.82, -9.4) * mm, "end": v(24.75, -9.36) * mm});
            skLineSegment(sketch, "E2454", {"start": v(24.75, -9.36) * mm, "end": v(24.66, -9.31) * mm});
            skLineSegment(sketch, "E2455", {"start": v(24.66, -9.31) * mm, "end": v(24.58, -9.28) * mm});
            skLineSegment(sketch, "E2456", {"start": v(24.58, -9.28) * mm, "end": v(24.5, -9.27) * mm});
            skLineSegment(sketch, "E2457", {"start": v(24.5, -9.27) * mm, "end": v(24.41, -9.27) * mm});
            skLineSegment(sketch, "E2458", {"start": v(24.41, -9.27) * mm, "end": v(24.33, -9.3) * mm});
            skLineSegment(sketch, "E2459", {"start": v(24.33, -9.3) * mm, "end": v(24.26, -9.32) * mm});
            skLineSegment(sketch, "E2460", {"start": v(24.26, -9.32) * mm, "end": v(24.19, -9.37) * mm});
            skLineSegment(sketch, "E2461", {"start": v(24.19, -9.37) * mm, "end": v(24.12, -9.42) * mm});
            skLineSegment(sketch, "E2462", {"start": v(24.12, -9.42) * mm, "end": v(24.06, -9.48) * mm});
            skLineSegment(sketch, "E2463", {"start": v(24.06, -9.48) * mm, "end": v(24, -9.54) * mm});
            skLineSegment(sketch, "E2464", {"start": v(24, -9.54) * mm, "end": v(23.95, -9.6) * mm});
            skLineSegment(sketch, "E2465", {"start": v(23.95, -9.6) * mm, "end": v(23.9, -9.67) * mm});
            skLineSegment(sketch, "E2466", {"start": v(23.9, -9.67) * mm, "end": v(23.86, -9.72) * mm});
            skLineSegment(sketch, "E2467", {"start": v(23.86, -9.72) * mm, "end": v(23.81, -9.76) * mm});
            skLineSegment(sketch, "E2468", {"start": v(23.81, -9.76) * mm, "end": v(23.76, -9.81) * mm});
            skLineSegment(sketch, "E2469", {"start": v(23.76, -9.81) * mm, "end": v(23.71, -9.86) * mm});
            skLineSegment(sketch, "E2470", {"start": v(23.71, -9.86) * mm, "end": v(23.66, -9.9) * mm});
            skLineSegment(sketch, "E2471", {"start": v(23.66, -9.9) * mm, "end": v(23.61, -9.94) * mm});
            skLineSegment(sketch, "E2472", {"start": v(23.61, -9.94) * mm, "end": v(23.56, -9.98) * mm});
            skLineSegment(sketch, "E2473", {"start": v(23.56, -9.98) * mm, "end": v(23.5, -10.02) * mm});
            skLineSegment(sketch, "E2474", {"start": v(23.5, -10.02) * mm, "end": v(23.38, -10.09) * mm});
            skLineSegment(sketch, "E2475", {"start": v(23.38, -10.09) * mm, "end": v(23.26, -10.14) * mm});
            skLineSegment(sketch, "E2476", {"start": v(23.26, -10.14) * mm, "end": v(23.13, -10.2) * mm});
            skLineSegment(sketch, "E2477", {"start": v(23.13, -10.2) * mm, "end": v(23, -10.23) * mm});
            skLineSegment(sketch, "E2478", {"start": v(23, -10.23) * mm, "end": v(22.87, -10.26) * mm});
            skLineSegment(sketch, "E2479", {"start": v(22.87, -10.26) * mm, "end": v(22.74, -10.28) * mm});
            skLineSegment(sketch, "E2480", {"start": v(22.74, -10.28) * mm, "end": v(22.6, -10.3) * mm});
            skLineSegment(sketch, "E2481", {"start": v(22.6, -10.3) * mm, "end": v(22.47, -10.3) * mm});
            skLineSegment(sketch, "E2482", {"start": v(22.47, -10.3) * mm, "end": v(22.34, -10.3) * mm});
            skLineSegment(sketch, "E2483", {"start": v(22.34, -10.3) * mm, "end": v(22.22, -10.28) * mm});
            skLineSegment(sketch, "E2484", {"start": v(22.22, -10.28) * mm, "end": v(22.1, -10.26) * mm});
            skLineSegment(sketch, "E2485", {"start": v(22.1, -10.26) * mm, "end": v(21.98, -10.23) * mm});
            skLineSegment(sketch, "E2486", {"start": v(21.98, -10.23) * mm, "end": v(21.86, -10.19) * mm});
            skLineSegment(sketch, "E2487", {"start": v(21.86, -10.19) * mm, "end": v(21.75, -10.14) * mm});
            skLineSegment(sketch, "E2488", {"start": v(21.75, -10.14) * mm, "end": v(21.64, -10.1) * mm});
            skLineSegment(sketch, "E2489", {"start": v(21.64, -10.1) * mm, "end": v(21.53, -10.03) * mm});
            skLineSegment(sketch, "E2490", {"start": v(21.53, -10.03) * mm, "end": v(21.33, -9.89) * mm});
            skLineSegment(sketch, "E2491", {"start": v(21.33, -9.89) * mm, "end": v(21.16, -9.72) * mm});
            skLineSegment(sketch, "E2492", {"start": v(21.16, -9.72) * mm, "end": v(21, -9.54) * mm});
            skLineSegment(sketch, "E2493", {"start": v(21, -9.54) * mm, "end": v(20.88, -9.34) * mm});
            skLineSegment(sketch, "E2494", {"start": v(20.88, -9.34) * mm, "end": v(20.78, -9.13) * mm});
            skLineSegment(sketch, "E2495", {"start": v(20.78, -9.13) * mm, "end": v(20.7, -8.9) * mm});
            skLineSegment(sketch, "E2496", {"start": v(20.7, -8.9) * mm, "end": v(20.66, -8.67) * mm});
            skLineSegment(sketch, "E2497", {"start": v(20.66, -8.67) * mm, "end": v(20.65, -8.42) * mm});
            skLineSegment(sketch, "E2498", {"start": v(20.65, -8.42) * mm, "end": v(20.66, -8.4) * mm});
            skLineSegment(sketch, "E2499", {"start": v(20.66, -8.4) * mm, "end": v(20.71, -8.37) * mm});
            skLineSegment(sketch, "E2500", {"start": v(20.71, -8.37) * mm, "end": v(20.79, -8.35) * mm});
            skLineSegment(sketch, "E2501", {"start": v(20.79, -8.35) * mm, "end": v(20.89, -8.33) * mm});
            skLineSegment(sketch, "E2502", {"start": v(20.89, -8.33) * mm, "end": v(21, -8.32) * mm});
            skLineSegment(sketch, "E2503", {"start": v(21, -8.32) * mm, "end": v(21.14, -8.3) * mm});
            skLineSegment(sketch, "E2504", {"start": v(21.14, -8.3) * mm, "end": v(21.3, -8.3) * mm});
            skLineSegment(sketch, "E2505", {"start": v(21.3, -8.3) * mm, "end": v(21.46, -8.3) * mm});
            skLineSegment(sketch, "E2506", {"start": v(21.46, -8.3) * mm, "end": v(21.82, -8.3) * mm});
            skLineSegment(sketch, "E2507", {"start": v(21.82, -8.3) * mm, "end": v(22.19, -8.3) * mm});
            skLineSegment(sketch, "E2508", {"start": v(22.19, -8.3) * mm, "end": v(22.55, -8.3) * mm});
            skLineSegment(sketch, "E2509", {"start": v(22.55, -8.3) * mm, "end": v(22.91, -8.3) * mm});
            skLineSegment(sketch, "E2510", {"start": v(22.91, -8.3) * mm, "end": v(23.28, -8.3) * mm});
            skLineSegment(sketch, "E2511", {"start": v(23.28, -8.3) * mm, "end": v(23.64, -8.3) * mm});
            skLineSegment(sketch, "E2512", {"start": v(23.64, -8.3) * mm, "end": v(24, -8.3) * mm});
            skLineSegment(sketch, "E2513", {"start": v(24, -8.3) * mm, "end": v(24.37, -8.3) * mm});
            skLineSegment(sketch, "E2514", {"start": v(24.37, -8.3) * mm, "end": v(24.53, -8.29) * mm});
            skLineSegment(sketch, "E2515", {"start": v(24.53, -8.29) * mm, "end": v(24.68, -8.25) * mm});
            skLineSegment(sketch, "E2516", {"start": v(24.68, -8.25) * mm, "end": v(24.82, -8.18) * mm});
            skLineSegment(sketch, "E2517", {"start": v(24.82, -8.18) * mm, "end": v(24.93, -8.1) * mm});
            skLineSegment(sketch, "E2518", {"start": v(24.93, -8.1) * mm, "end": v(25.03, -7.99) * mm});
            skLineSegment(sketch, "E2519", {"start": v(25.03, -7.99) * mm, "end": v(25.1, -7.86) * mm});
            skLineSegment(sketch, "E2520", {"start": v(25.1, -7.86) * mm, "end": v(25.14, -7.73) * mm});
            skLineSegment(sketch, "E2521", {"start": v(25.14, -7.73) * mm, "end": v(25.15, -7.59) * mm});
            skLineSegment(sketch, "E2522", {"start": v(25.15, -7.59) * mm, "end": v(25.13, -7.33) * mm});
            skLineSegment(sketch, "E2523", {"start": v(25.13, -7.33) * mm, "end": v(25.08, -7.07) * mm});
            skLineSegment(sketch, "E2524", {"start": v(23.91, -7.08) * mm, "end": v(23.83, -7.24) * mm});
            skLineSegment(sketch, "E2525", {"start": v(23.83, -7.24) * mm, "end": v(23.79, -7.3) * mm});
            skLineSegment(sketch, "E2526", {"start": v(23.79, -7.3) * mm, "end": v(23.73, -7.35) * mm});
            skLineSegment(sketch, "E2527", {"start": v(23.73, -7.35) * mm, "end": v(23.67, -7.39) * mm});
            skLineSegment(sketch, "E2528", {"start": v(23.67, -7.39) * mm, "end": v(23.6, -7.42) * mm});
            skLineSegment(sketch, "E2529", {"start": v(23.6, -7.42) * mm, "end": v(23.54, -7.45) * mm});
            skLineSegment(sketch, "E2530", {"start": v(23.54, -7.45) * mm, "end": v(23.47, -7.47) * mm});
            skLineSegment(sketch, "E2531", {"start": v(23.47, -7.47) * mm, "end": v(23.4, -7.48) * mm});
            skLineSegment(sketch, "E2532", {"start": v(23.4, -7.48) * mm, "end": v(23.32, -7.48) * mm});
            skLineSegment(sketch, "E2533", {"start": v(23.32, -7.48) * mm, "end": v(22.99, -7.48) * mm});
            skLineSegment(sketch, "E2534", {"start": v(22.99, -7.48) * mm, "end": v(22.66, -7.48) * mm});
            skLineSegment(sketch, "E2535", {"start": v(22.66, -7.48) * mm, "end": v(22.33, -7.48) * mm});
            skLineSegment(sketch, "E2536", {"start": v(22.33, -7.48) * mm, "end": v(22, -7.48) * mm});
            skLineSegment(sketch, "E2537", {"start": v(22, -7.48) * mm, "end": v(21.67, -7.48) * mm});
            skLineSegment(sketch, "E2538", {"start": v(21.67, -7.48) * mm, "end": v(21.34, -7.48) * mm});
            skLineSegment(sketch, "E2539", {"start": v(21.34, -7.48) * mm, "end": v(21.02, -7.48) * mm});
            skLineSegment(sketch, "E2540", {"start": v(21.02, -7.48) * mm, "end": v(20.69, -7.48) * mm});
            skLineSegment(sketch, "E2541", {"start": v(20.69, -7.48) * mm, "end": v(20.72, -7.31) * mm});
            skLineSegment(sketch, "E2542", {"start": v(20.72, -7.31) * mm, "end": v(20.76, -7.16) * mm});
            skLineSegment(sketch, "E2543", {"start": v(20.76, -7.16) * mm, "end": v(20.82, -7) * mm});
            skLineSegment(sketch, "E2544", {"start": v(20.82, -7) * mm, "end": v(20.89, -6.87) * mm});
            skLineSegment(sketch, "E2545", {"start": v(20.89, -6.87) * mm, "end": v(20.97, -6.73) * mm});
            skLineSegment(sketch, "E2546", {"start": v(20.97, -6.73) * mm, "end": v(21.07, -6.6) * mm});
            skLineSegment(sketch, "E2547", {"start": v(21.07, -6.6) * mm, "end": v(21.18, -6.49) * mm});
            skLineSegment(sketch, "E2548", {"start": v(21.18, -6.49) * mm, "end": v(21.3, -6.38) * mm});
            skLineSegment(sketch, "E2549", {"start": v(21.3, -6.38) * mm, "end": v(21.53, -6.22) * mm});
            skLineSegment(sketch, "E2550", {"start": v(21.53, -6.22) * mm, "end": v(21.78, -6.1) * mm});
            skLineSegment(sketch, "E2551", {"start": v(21.78, -6.1) * mm, "end": v(22.05, -6.03) * mm});
            skLineSegment(sketch, "E2552", {"start": v(22.05, -6.03) * mm, "end": v(22.32, -6) * mm});
            skLineSegment(sketch, "E2553", {"start": v(22.32, -6) * mm, "end": v(22.6, -6) * mm});
            skLineSegment(sketch, "E2554", {"start": v(22.6, -6) * mm, "end": v(22.87, -6.06) * mm});
            skLineSegment(sketch, "E2555", {"start": v(22.87, -6.06) * mm, "end": v(23.13, -6.14) * mm});
            skLineSegment(sketch, "E2556", {"start": v(23.13, -6.14) * mm, "end": v(23.39, -6.26) * mm});
            skLineSegment(sketch, "E2557", {"start": v(23.39, -6.26) * mm, "end": v(23.52, -6.34) * mm});
            skLineSegment(sketch, "E2558", {"start": v(23.52, -6.34) * mm, "end": v(23.65, -6.43) * mm});
            skLineSegment(sketch, "E2559", {"start": v(23.65, -6.43) * mm, "end": v(23.76, -6.54) * mm});
            skLineSegment(sketch, "E2560", {"start": v(23.76, -6.54) * mm, "end": v(23.85, -6.66) * mm});
            skLineSegment(sketch, "E2561", {"start": v(23.85, -6.66) * mm, "end": v(23.91, -6.79) * mm});
            skLineSegment(sketch, "E2562", {"start": v(23.91, -6.79) * mm, "end": v(23.94, -6.93) * mm});
            skLineSegment(sketch, "E2563", {"start": v(23.94, -6.93) * mm, "end": v(23.91, -7.08) * mm});
            skLineSegment(sketch, "E2564", {"start": v(31.15, -7.08) * mm, "end": v(31.08, -6.84) * mm});
            skLineSegment(sketch, "E2565", {"start": v(31.08, -6.84) * mm, "end": v(31, -6.61) * mm});
            skLineSegment(sketch, "E2566", {"start": v(31, -6.61) * mm, "end": v(30.88, -6.4) * mm});
            skLineSegment(sketch, "E2567", {"start": v(30.88, -6.4) * mm, "end": v(30.74, -6.19) * mm});
            skLineSegment(sketch, "E2568", {"start": v(30.74, -6.19) * mm, "end": v(30.58, -5.99) * mm});
            skLineSegment(sketch, "E2569", {"start": v(30.58, -5.99) * mm, "end": v(30.4, -5.8) * mm});
            skLineSegment(sketch, "E2570", {"start": v(30.4, -5.8) * mm, "end": v(30.2, -5.63) * mm});
            skLineSegment(sketch, "E2571", {"start": v(30.2, -5.63) * mm, "end": v(29.98, -5.48) * mm});
            skLineSegment(sketch, "E2572", {"start": v(29.98, -5.48) * mm, "end": v(29.76, -5.36) * mm});
            skLineSegment(sketch, "E2573", {"start": v(29.76, -5.36) * mm, "end": v(29.53, -5.25) * mm});
            skLineSegment(sketch, "E2574", {"start": v(29.53, -5.25) * mm, "end": v(29.3, -5.17) * mm});
            skLineSegment(sketch, "E2575", {"start": v(29.3, -5.17) * mm, "end": v(29.05, -5.1) * mm});
            skLineSegment(sketch, "E2576", {"start": v(29.05, -5.1) * mm, "end": v(28.79, -5.07) * mm});
            skLineSegment(sketch, "E2577", {"start": v(28.79, -5.07) * mm, "end": v(28.52, -5.05) * mm});
            skLineSegment(sketch, "E2578", {"start": v(28.52, -5.05) * mm, "end": v(28.2, -5.06) * mm});
            skLineSegment(sketch, "E2579", {"start": v(28.2, -5.06) * mm, "end": v(27.9, -5.1) * mm});
            skLineSegment(sketch, "E2580", {"start": v(27.9, -5.1) * mm, "end": v(27.61, -5.17) * mm});
            skLineSegment(sketch, "E2581", {"start": v(27.61, -5.17) * mm, "end": v(27.34, -5.27) * mm});
            skLineSegment(sketch, "E2582", {"start": v(27.34, -5.27) * mm, "end": v(27.08, -5.4) * mm});
            skLineSegment(sketch, "E2583", {"start": v(27.08, -5.4) * mm, "end": v(26.84, -5.57) * mm});
            skLineSegment(sketch, "E2584", {"start": v(26.84, -5.57) * mm, "end": v(26.62, -5.76) * mm});
            skLineSegment(sketch, "E2585", {"start": v(26.62, -5.76) * mm, "end": v(26.41, -5.99) * mm});
            skLineSegment(sketch, "E2586", {"start": v(26.41, -5.99) * mm, "end": v(26.24, -6.22) * mm});
            skLineSegment(sketch, "E2587", {"start": v(26.24, -6.22) * mm, "end": v(26.1, -6.46) * mm});
            skLineSegment(sketch, "E2588", {"start": v(26.1, -6.46) * mm, "end": v(25.97, -6.71) * mm});
            skLineSegment(sketch, "E2589", {"start": v(25.97, -6.71) * mm, "end": v(25.86, -6.98) * mm});
            skLineSegment(sketch, "E2590", {"start": v(25.86, -6.98) * mm, "end": v(25.79, -7.26) * mm});
            skLineSegment(sketch, "E2591", {"start": v(25.79, -7.26) * mm, "end": v(25.73, -7.55) * mm});
            skLineSegment(sketch, "E2592", {"start": v(25.73, -7.55) * mm, "end": v(25.7, -7.85) * mm});
            skLineSegment(sketch, "E2593", {"start": v(25.7, -7.85) * mm, "end": v(25.69, -8.17) * mm});
            skLineSegment(sketch, "E2594", {"start": v(25.69, -8.17) * mm, "end": v(25.7, -8.48) * mm});
            skLineSegment(sketch, "E2595", {"start": v(25.7, -8.48) * mm, "end": v(25.74, -8.77) * mm});
            skLineSegment(sketch, "E2596", {"start": v(25.74, -8.77) * mm, "end": v(25.8, -9.06) * mm});
            skLineSegment(sketch, "E2597", {"start": v(25.8, -9.06) * mm, "end": v(25.88, -9.33) * mm});
            skLineSegment(sketch, "E2598", {"start": v(25.88, -9.33) * mm, "end": v(25.98, -9.59) * mm});
            skLineSegment(sketch, "E2599", {"start": v(25.98, -9.59) * mm, "end": v(26.11, -9.83) * mm});
            skLineSegment(sketch, "E2600", {"start": v(26.11, -9.83) * mm, "end": v(26.26, -10.07) * mm});
            skLineSegment(sketch, "E2601", {"start": v(26.26, -10.07) * mm, "end": v(26.44, -10.3) * mm});
            skLineSegment(sketch, "E2602", {"start": v(26.44, -10.3) * mm, "end": v(26.64, -10.5) * mm});
            skLineSegment(sketch, "E2603", {"start": v(26.64, -10.5) * mm, "end": v(26.86, -10.7) * mm});
            skLineSegment(sketch, "E2604", {"start": v(26.86, -10.7) * mm, "end": v(27.1, -10.85) * mm});
            skLineSegment(sketch, "E2605", {"start": v(27.1, -10.85) * mm, "end": v(27.35, -10.99) * mm});
            skLineSegment(sketch, "E2606", {"start": v(27.35, -10.99) * mm, "end": v(27.61, -11.1) * mm});
            skLineSegment(sketch, "E2607", {"start": v(27.61, -11.1) * mm, "end": v(27.9, -11.17) * mm});
            skLineSegment(sketch, "E2608", {"start": v(27.9, -11.17) * mm, "end": v(28.19, -11.22) * mm});
            skLineSegment(sketch, "E2609", {"start": v(28.19, -11.22) * mm, "end": v(28.5, -11.24) * mm});
            skLineSegment(sketch, "E2610", {"start": v(28.5, -11.24) * mm, "end": v(28.6, -11.24) * mm});
            skLineSegment(sketch, "E2611", {"start": v(28.6, -11.24) * mm, "end": v(28.7, -11.24) * mm});
            skLineSegment(sketch, "E2612", {"start": v(28.7, -11.24) * mm, "end": v(28.8, -11.23) * mm});
            skLineSegment(sketch, "E2613", {"start": v(28.8, -11.23) * mm, "end": v(28.9, -11.22) * mm});
            skLineSegment(sketch, "E2614", {"start": v(28.9, -11.22) * mm, "end": v(28.99, -11.2) * mm});
            skLineSegment(sketch, "E2615", {"start": v(28.99, -11.2) * mm, "end": v(29.08, -11.2) * mm});
            skLineSegment(sketch, "E2616", {"start": v(29.08, -11.2) * mm, "end": v(29.18, -11.17) * mm});
            skLineSegment(sketch, "E2617", {"start": v(29.18, -11.17) * mm, "end": v(29.28, -11.15) * mm});
            skLineSegment(sketch, "E2618", {"start": v(29.28, -11.15) * mm, "end": v(29.42, -11.1) * mm});
            skLineSegment(sketch, "E2619", {"start": v(29.42, -11.1) * mm, "end": v(29.57, -11.05) * mm});
            skLineSegment(sketch, "E2620", {"start": v(29.57, -11.05) * mm, "end": v(29.7, -11) * mm});
            skLineSegment(sketch, "E2621", {"start": v(29.7, -11) * mm, "end": v(29.84, -10.92) * mm});
            skLineSegment(sketch, "E2622", {"start": v(29.84, -10.92) * mm, "end": v(29.98, -10.85) * mm});
            skLineSegment(sketch, "E2623", {"start": v(29.98, -10.85) * mm, "end": v(30.1, -10.77) * mm});
            skLineSegment(sketch, "E2624", {"start": v(30.1, -10.77) * mm, "end": v(30.23, -10.68) * mm});
            skLineSegment(sketch, "E2625", {"start": v(30.23, -10.68) * mm, "end": v(30.35, -10.6) * mm});
            skLineSegment(sketch, "E2626", {"start": v(30.35, -10.6) * mm, "end": v(30.46, -10.5) * mm});
            skLineSegment(sketch, "E2627", {"start": v(30.46, -10.5) * mm, "end": v(30.58, -10.42) * mm});
            skLineSegment(sketch, "E2628", {"start": v(30.58, -10.42) * mm, "end": v(30.7, -10.32) * mm});
            skLineSegment(sketch, "E2629", {"start": v(30.7, -10.32) * mm, "end": v(30.8, -10.22) * mm});
            skLineSegment(sketch, "E2630", {"start": v(30.8, -10.22) * mm, "end": v(30.91, -10.1) * mm});
            skLineSegment(sketch, "E2631", {"start": v(30.91, -10.1) * mm, "end": v(30.99, -9.98) * mm});
            skLineSegment(sketch, "E2632", {"start": v(30.99, -9.98) * mm, "end": v(31.04, -9.85) * mm});
            skLineSegment(sketch, "E2633", {"start": v(31.04, -9.85) * mm, "end": v(31.05, -9.71) * mm});
            skLineSegment(sketch, "E2634", {"start": v(31.05, -9.71) * mm, "end": v(31.03, -9.6) * mm});
            skLineSegment(sketch, "E2635", {"start": v(31.03, -9.6) * mm, "end": v(30.97, -9.5) * mm});
            skLineSegment(sketch, "E2636", {"start": v(30.97, -9.5) * mm, "end": v(30.89, -9.41) * mm});
            skLineSegment(sketch, "E2637", {"start": v(30.89, -9.41) * mm, "end": v(30.79, -9.34) * mm});
            skLineSegment(sketch, "E2638", {"start": v(30.79, -9.34) * mm, "end": v(30.68, -9.3) * mm});
            skLineSegment(sketch, "E2639", {"start": v(30.68, -9.3) * mm, "end": v(30.56, -9.27) * mm});
            skLineSegment(sketch, "E2640", {"start": v(30.56, -9.27) * mm, "end": v(30.44, -9.28) * mm});
            skLineSegment(sketch, "E2641", {"start": v(30.44, -9.28) * mm, "end": v(30.33, -9.3) * mm});
            skLineSegment(sketch, "E2642", {"start": v(30.33, -9.3) * mm, "end": v(30.23, -9.37) * mm});
            skLineSegment(sketch, "E2643", {"start": v(30.23, -9.37) * mm, "end": v(30.13, -9.45) * mm});
            skLineSegment(sketch, "E2644", {"start": v(30.13, -9.45) * mm, "end": v(30.05, -9.53) * mm});
            skLineSegment(sketch, "E2645", {"start": v(30.05, -9.53) * mm, "end": v(29.97, -9.63) * mm});
            skLineSegment(sketch, "E2646", {"start": v(29.97, -9.63) * mm, "end": v(29.9, -9.73) * mm});
            skLineSegment(sketch, "E2647", {"start": v(29.9, -9.73) * mm, "end": v(29.81, -9.82) * mm});
            skLineSegment(sketch, "E2648", {"start": v(29.81, -9.82) * mm, "end": v(29.73, -9.9) * mm});
            skLineSegment(sketch, "E2649", {"start": v(29.73, -9.9) * mm, "end": v(29.63, -9.98) * mm});
            skLineSegment(sketch, "E2650", {"start": v(29.63, -9.98) * mm, "end": v(29.51, -10.06) * mm});
            skLineSegment(sketch, "E2651", {"start": v(29.51, -10.06) * mm, "end": v(29.38, -10.13) * mm});
            skLineSegment(sketch, "E2652", {"start": v(29.38, -10.13) * mm, "end": v(29.25, -10.18) * mm});
            skLineSegment(sketch, "E2653", {"start": v(29.25, -10.18) * mm, "end": v(29.11, -10.23) * mm});
            skLineSegment(sketch, "E2654", {"start": v(29.11, -10.23) * mm, "end": v(28.97, -10.26) * mm});
            skLineSegment(sketch, "E2655", {"start": v(28.97, -10.26) * mm, "end": v(28.83, -10.28) * mm});
            skLineSegment(sketch, "E2656", {"start": v(28.83, -10.28) * mm, "end": v(28.68, -10.3) * mm});
            skLineSegment(sketch, "E2657", {"start": v(28.68, -10.3) * mm, "end": v(28.54, -10.3) * mm});
            skLineSegment(sketch, "E2658", {"start": v(28.54, -10.3) * mm, "end": v(28.45, -10.3) * mm});
            skLineSegment(sketch, "E2659", {"start": v(28.45, -10.3) * mm, "end": v(28.36, -10.3) * mm});
            skLineSegment(sketch, "E2660", {"start": v(28.36, -10.3) * mm, "end": v(28.27, -10.28) * mm});
            skLineSegment(sketch, "E2661", {"start": v(28.27, -10.28) * mm, "end": v(28.18, -10.26) * mm});
            skLineSegment(sketch, "E2662", {"start": v(28.18, -10.26) * mm, "end": v(28.09, -10.24) * mm});
            skLineSegment(sketch, "E2663", {"start": v(28.09, -10.24) * mm, "end": v(28, -10.21) * mm});
            skLineSegment(sketch, "E2664", {"start": v(28, -10.21) * mm, "end": v(27.91, -10.19) * mm});
            skLineSegment(sketch, "E2665", {"start": v(27.91, -10.19) * mm, "end": v(27.83, -10.15) * mm});
            skLineSegment(sketch, "E2666", {"start": v(27.83, -10.15) * mm, "end": v(27.6, -10.03) * mm});
            skLineSegment(sketch, "E2667", {"start": v(27.6, -10.03) * mm, "end": v(27.38, -9.87) * mm});
            skLineSegment(sketch, "E2668", {"start": v(27.38, -9.87) * mm, "end": v(27.19, -9.67) * mm});
            skLineSegment(sketch, "E2669", {"start": v(27.19, -9.67) * mm, "end": v(27.02, -9.45) * mm});
            skLineSegment(sketch, "E2670", {"start": v(27.02, -9.45) * mm, "end": v(26.9, -9.21) * mm});
            skLineSegment(sketch, "E2671", {"start": v(26.9, -9.21) * mm, "end": v(26.8, -8.96) * mm});
            skLineSegment(sketch, "E2672", {"start": v(26.8, -8.96) * mm, "end": v(26.74, -8.7) * mm});
            skLineSegment(sketch, "E2673", {"start": v(26.74, -8.7) * mm, "end": v(26.72, -8.43) * mm});
            skLineSegment(sketch, "E2674", {"start": v(26.72, -8.43) * mm, "end": v(26.74, -8.4) * mm});
            skLineSegment(sketch, "E2675", {"start": v(26.74, -8.4) * mm, "end": v(26.78, -8.38) * mm});
            skLineSegment(sketch, "E2676", {"start": v(26.78, -8.38) * mm, "end": v(26.86, -8.36) * mm});
            skLineSegment(sketch, "E2677", {"start": v(26.86, -8.36) * mm, "end": v(26.96, -8.34) * mm});
            skLineSegment(sketch, "E2678", {"start": v(26.96, -8.34) * mm, "end": v(27.08, -8.33) * mm});
            skLineSegment(sketch, "E2679", {"start": v(27.08, -8.33) * mm, "end": v(27.22, -8.31) * mm});
            skLineSegment(sketch, "E2680", {"start": v(27.22, -8.31) * mm, "end": v(27.37, -8.3) * mm});
            skLineSegment(sketch, "E2681", {"start": v(27.37, -8.3) * mm, "end": v(27.53, -8.3) * mm});
            skLineSegment(sketch, "E2682", {"start": v(27.53, -8.3) * mm, "end": v(27.9, -8.3) * mm});
            skLineSegment(sketch, "E2683", {"start": v(27.9, -8.3) * mm, "end": v(28.26, -8.3) * mm});
            skLineSegment(sketch, "E2684", {"start": v(28.26, -8.3) * mm, "end": v(28.62, -8.3) * mm});
            skLineSegment(sketch, "E2685", {"start": v(28.62, -8.3) * mm, "end": v(28.99, -8.3) * mm});
            skLineSegment(sketch, "E2686", {"start": v(28.99, -8.3) * mm, "end": v(29.35, -8.3) * mm});
            skLineSegment(sketch, "E2687", {"start": v(29.35, -8.3) * mm, "end": v(29.71, -8.3) * mm});
            skLineSegment(sketch, "E2688", {"start": v(29.71, -8.3) * mm, "end": v(30.07, -8.3) * mm});
            skLineSegment(sketch, "E2689", {"start": v(30.07, -8.3) * mm, "end": v(30.44, -8.3) * mm});
            skLineSegment(sketch, "E2690", {"start": v(30.44, -8.3) * mm, "end": v(30.6, -8.3) * mm});
            skLineSegment(sketch, "E2691", {"start": v(30.6, -8.3) * mm, "end": v(30.75, -8.25) * mm});
            skLineSegment(sketch, "E2692", {"start": v(30.75, -8.25) * mm, "end": v(30.89, -8.19) * mm});
            skLineSegment(sketch, "E2693", {"start": v(30.89, -8.19) * mm, "end": v(31, -8.1) * mm});
            skLineSegment(sketch, "E2694", {"start": v(31, -8.1) * mm, "end": v(31.1, -8) * mm});
            skLineSegment(sketch, "E2695", {"start": v(31.1, -8) * mm, "end": v(31.17, -7.87) * mm});
            skLineSegment(sketch, "E2696", {"start": v(31.17, -7.87) * mm, "end": v(31.21, -7.74) * mm});
            skLineSegment(sketch, "E2697", {"start": v(31.21, -7.74) * mm, "end": v(31.22, -7.6) * mm});
            skLineSegment(sketch, "E2698", {"start": v(31.22, -7.6) * mm, "end": v(31.2, -7.33) * mm});
            skLineSegment(sketch, "E2699", {"start": v(31.2, -7.33) * mm, "end": v(31.15, -7.08) * mm});
            skLineSegment(sketch, "E2700", {"start": v(29.95, -7.15) * mm, "end": v(29.9, -7.24) * mm});
            skLineSegment(sketch, "E2701", {"start": v(29.9, -7.24) * mm, "end": v(29.83, -7.3) * mm});
            skLineSegment(sketch, "E2702", {"start": v(29.83, -7.3) * mm, "end": v(29.76, -7.37) * mm});
            skLineSegment(sketch, "E2703", {"start": v(29.76, -7.37) * mm, "end": v(29.67, -7.42) * mm});
            skLineSegment(sketch, "E2704", {"start": v(29.67, -7.42) * mm, "end": v(29.58, -7.46) * mm});
            skLineSegment(sketch, "E2705", {"start": v(29.58, -7.46) * mm, "end": v(29.49, -7.48) * mm});
            skLineSegment(sketch, "E2706", {"start": v(29.49, -7.48) * mm, "end": v(29.4, -7.49) * mm});
            skLineSegment(sketch, "E2707", {"start": v(29.4, -7.49) * mm, "end": v(29.06, -7.49) * mm});
            skLineSegment(sketch, "E2708", {"start": v(29.06, -7.49) * mm, "end": v(28.73, -7.49) * mm});
            skLineSegment(sketch, "E2709", {"start": v(28.73, -7.49) * mm, "end": v(28.4, -7.49) * mm});
            skLineSegment(sketch, "E2710", {"start": v(28.4, -7.49) * mm, "end": v(28.07, -7.49) * mm});
            skLineSegment(sketch, "E2711", {"start": v(28.07, -7.49) * mm, "end": v(27.75, -7.49) * mm});
            skLineSegment(sketch, "E2712", {"start": v(27.75, -7.49) * mm, "end": v(27.42, -7.49) * mm});
            skLineSegment(sketch, "E2713", {"start": v(27.42, -7.49) * mm, "end": v(27.09, -7.49) * mm});
            skLineSegment(sketch, "E2714", {"start": v(27.09, -7.49) * mm, "end": v(26.76, -7.48) * mm});
            skLineSegment(sketch, "E2715", {"start": v(26.76, -7.48) * mm, "end": v(26.79, -7.32) * mm});
            skLineSegment(sketch, "E2716", {"start": v(26.79, -7.32) * mm, "end": v(26.83, -7.16) * mm});
            skLineSegment(sketch, "E2717", {"start": v(26.83, -7.16) * mm, "end": v(26.9, -7.02) * mm});
            skLineSegment(sketch, "E2718", {"start": v(26.9, -7.02) * mm, "end": v(26.96, -6.87) * mm});
            skLineSegment(sketch, "E2719", {"start": v(26.96, -6.87) * mm, "end": v(27.04, -6.74) * mm});
            skLineSegment(sketch, "E2720", {"start": v(27.04, -6.74) * mm, "end": v(27.14, -6.62) * mm});
            skLineSegment(sketch, "E2721", {"start": v(27.14, -6.62) * mm, "end": v(27.25, -6.5) * mm});
            skLineSegment(sketch, "E2722", {"start": v(27.25, -6.5) * mm, "end": v(27.37, -6.39) * mm});
            skLineSegment(sketch, "E2723", {"start": v(27.37, -6.39) * mm, "end": v(27.46, -6.32) * mm});
            skLineSegment(sketch, "E2724", {"start": v(27.46, -6.32) * mm, "end": v(27.56, -6.25) * mm});
            skLineSegment(sketch, "E2725", {"start": v(27.56, -6.25) * mm, "end": v(27.66, -6.2) * mm});
            skLineSegment(sketch, "E2726", {"start": v(27.66, -6.2) * mm, "end": v(27.77, -6.15) * mm});
            skLineSegment(sketch, "E2727", {"start": v(27.77, -6.15) * mm, "end": v(27.88, -6.1) * mm});
            skLineSegment(sketch, "E2728", {"start": v(27.88, -6.1) * mm, "end": v(27.99, -6.06) * mm});
            skLineSegment(sketch, "E2729", {"start": v(27.99, -6.06) * mm, "end": v(28.1, -6.03) * mm});
            skLineSegment(sketch, "E2730", {"start": v(28.1, -6.03) * mm, "end": v(28.2, -6.01) * mm});
            skLineSegment(sketch, "E2731", {"start": v(28.2, -6.01) * mm, "end": v(28.45, -6) * mm});
            skLineSegment(sketch, "E2732", {"start": v(28.45, -6) * mm, "end": v(28.74, -6.02) * mm});
            skLineSegment(sketch, "E2733", {"start": v(28.74, -6.02) * mm, "end": v(29.06, -6.1) * mm});
            skLineSegment(sketch, "E2734", {"start": v(29.06, -6.1) * mm, "end": v(29.37, -6.2) * mm});
            skLineSegment(sketch, "E2735", {"start": v(29.37, -6.2) * mm, "end": v(29.64, -6.35) * mm});
            skLineSegment(sketch, "E2736", {"start": v(29.64, -6.35) * mm, "end": v(29.86, -6.55) * mm});
            skLineSegment(sketch, "E2737", {"start": v(29.86, -6.55) * mm, "end": v(29.98, -6.78) * mm});
            skLineSegment(sketch, "E2738", {"start": v(29.98, -6.78) * mm, "end": v(29.98, -7.06) * mm});
            skLineSegment(sketch, "E2739", {"start": v(29.98, -7.06) * mm, "end": v(29.95, -7.15) * mm});
            skLineSegment(sketch, "E2740", {"start": v(37.18, -1.32) * mm, "end": v(37.14, -1.18) * mm});
            skLineSegment(sketch, "E2741", {"start": v(37.14, -1.18) * mm, "end": v(37.08, -1.06) * mm});
            skLineSegment(sketch, "E2742", {"start": v(37.08, -1.06) * mm, "end": v(37, -0.96) * mm});
            skLineSegment(sketch, "E2743", {"start": v(37, -0.96) * mm, "end": v(36.92, -0.88) * mm});
            skLineSegment(sketch, "E2744", {"start": v(36.92, -0.88) * mm, "end": v(36.83, -0.83) * mm});
            skLineSegment(sketch, "E2745", {"start": v(36.83, -0.83) * mm, "end": v(36.73, -0.82) * mm});
            skLineSegment(sketch, "E2746", {"start": v(36.73, -0.82) * mm, "end": v(36.64, -0.83) * mm});
            skLineSegment(sketch, "E2747", {"start": v(36.64, -0.83) * mm, "end": v(36.55, -0.88) * mm});
            skLineSegment(sketch, "E2748", {"start": v(36.55, -0.88) * mm, "end": v(36.46, -0.96) * mm});
            skLineSegment(sketch, "E2749", {"start": v(36.46, -0.96) * mm, "end": v(36.39, -1.06) * mm});
            skLineSegment(sketch, "E2750", {"start": v(36.39, -1.06) * mm, "end": v(36.33, -1.18) * mm});
            skLineSegment(sketch, "E2751", {"start": v(36.33, -1.18) * mm, "end": v(36.28, -1.32) * mm});
            skLineSegment(sketch, "E2752", {"start": v(36.28, -1.32) * mm, "end": v(36.26, -1.47) * mm});
            skLineSegment(sketch, "E2753", {"start": v(36.26, -1.47) * mm, "end": v(36.25, -1.63) * mm});
            skLineSegment(sketch, "E2754", {"start": v(36.25, -1.63) * mm, "end": v(36.25, -2.18) * mm});
            skLineSegment(sketch, "E2755", {"start": v(36.25, -2.18) * mm, "end": v(36.24, -2.73) * mm});
            skLineSegment(sketch, "E2756", {"start": v(36.24, -2.73) * mm, "end": v(36.24, -3.29) * mm});
            skLineSegment(sketch, "E2757", {"start": v(36.24, -3.29) * mm, "end": v(36.24, -3.84) * mm});
            skLineSegment(sketch, "E2758", {"start": v(36.24, -3.84) * mm, "end": v(36.24, -4.4) * mm});
            skLineSegment(sketch, "E2759", {"start": v(36.24, -4.4) * mm, "end": v(36.24, -4.94) * mm});
            skLineSegment(sketch, "E2760", {"start": v(36.24, -4.94) * mm, "end": v(36.24, -5.5) * mm});
            skLineSegment(sketch, "E2761", {"start": v(36.24, -5.5) * mm, "end": v(36.24, -6.05) * mm});
            skLineSegment(sketch, "E2762", {"start": v(36.24, -6.05) * mm, "end": v(36.04, -5.82) * mm});
            skLineSegment(sketch, "E2763", {"start": v(36.04, -5.82) * mm, "end": v(35.83, -5.63) * mm});
            skLineSegment(sketch, "E2764", {"start": v(35.83, -5.63) * mm, "end": v(35.6, -5.46) * mm});
            skLineSegment(sketch, "E2765", {"start": v(35.6, -5.46) * mm, "end": v(35.35, -5.33) * mm});
            skLineSegment(sketch, "E2766", {"start": v(35.35, -5.33) * mm, "end": v(35.1, -5.22) * mm});
            skLineSegment(sketch, "E2767", {"start": v(35.1, -5.22) * mm, "end": v(34.82, -5.14) * mm});
            skLineSegment(sketch, "E2768", {"start": v(34.82, -5.14) * mm, "end": v(34.54, -5.09) * mm});
            skLineSegment(sketch, "E2769", {"start": v(34.54, -5.09) * mm, "end": v(34.24, -5.07) * mm});
            skLineSegment(sketch, "E2770", {"start": v(34.24, -5.07) * mm, "end": v(33.94, -5.07) * mm});
            skLineSegment(sketch, "E2771", {"start": v(33.94, -5.07) * mm, "end": v(33.65, -5.11) * mm});
            skLineSegment(sketch, "E2772", {"start": v(33.65, -5.11) * mm, "end": v(33.38, -5.18) * mm});
            skLineSegment(sketch, "E2773", {"start": v(33.38, -5.18) * mm, "end": v(33.12, -5.28) * mm});
            skLineSegment(sketch, "E2774", {"start": v(33.12, -5.28) * mm, "end": v(32.88, -5.41) * mm});
            skLineSegment(sketch, "E2775", {"start": v(32.88, -5.41) * mm, "end": v(32.65, -5.58) * mm});
            skLineSegment(sketch, "E2776", {"start": v(32.65, -5.58) * mm, "end": v(32.43, -5.77) * mm});
            skLineSegment(sketch, "E2777", {"start": v(32.43, -5.77) * mm, "end": v(32.23, -6) * mm});
            skLineSegment(sketch, "E2778", {"start": v(32.23, -6) * mm, "end": v(32.06, -6.22) * mm});
            skLineSegment(sketch, "E2779", {"start": v(32.06, -6.22) * mm, "end": v(31.91, -6.46) * mm});
            skLineSegment(sketch, "E2780", {"start": v(31.91, -6.46) * mm, "end": v(31.79, -6.72) * mm});
            skLineSegment(sketch, "E2781", {"start": v(31.79, -6.72) * mm, "end": v(31.69, -6.98) * mm});
            skLineSegment(sketch, "E2782", {"start": v(31.69, -6.98) * mm, "end": v(31.6, -7.26) * mm});
            skLineSegment(sketch, "E2783", {"start": v(31.6, -7.26) * mm, "end": v(31.55, -7.55) * mm});
            skLineSegment(sketch, "E2784", {"start": v(31.55, -7.55) * mm, "end": v(31.52, -7.85) * mm});
            skLineSegment(sketch, "E2785", {"start": v(31.52, -7.85) * mm, "end": v(31.5, -8.16) * mm});
            skLineSegment(sketch, "E2786", {"start": v(31.5, -8.16) * mm, "end": v(31.52, -8.46) * mm});
            skLineSegment(sketch, "E2787", {"start": v(31.52, -8.46) * mm, "end": v(31.55, -8.76) * mm});
            skLineSegment(sketch, "E2788", {"start": v(31.55, -8.76) * mm, "end": v(31.61, -9.04) * mm});
            skLineSegment(sketch, "E2789", {"start": v(31.61, -9.04) * mm, "end": v(31.7, -9.31) * mm});
            skLineSegment(sketch, "E2790", {"start": v(31.7, -9.31) * mm, "end": v(31.8, -9.58) * mm});
            skLineSegment(sketch, "E2791", {"start": v(31.8, -9.58) * mm, "end": v(31.93, -9.83) * mm});
            skLineSegment(sketch, "E2792", {"start": v(31.93, -9.83) * mm, "end": v(32.08, -10.07) * mm});
            skLineSegment(sketch, "E2793", {"start": v(32.08, -10.07) * mm, "end": v(32.26, -10.3) * mm});
            skLineSegment(sketch, "E2794", {"start": v(32.26, -10.3) * mm, "end": v(32.46, -10.53) * mm});
            skLineSegment(sketch, "E2795", {"start": v(32.46, -10.53) * mm, "end": v(32.68, -10.72) * mm});
            skLineSegment(sketch, "E2796", {"start": v(32.68, -10.72) * mm, "end": v(32.9, -10.89) * mm});
            skLineSegment(sketch, "E2797", {"start": v(32.9, -10.89) * mm, "end": v(33.14, -11.02) * mm});
            skLineSegment(sketch, "E2798", {"start": v(33.14, -11.02) * mm, "end": v(33.4, -11.12) * mm});
            skLineSegment(sketch, "E2799", {"start": v(33.4, -11.12) * mm, "end": v(33.65, -11.2) * mm});
            skLineSegment(sketch, "E2800", {"start": v(33.65, -11.2) * mm, "end": v(33.93, -11.24) * mm});
            skLineSegment(sketch, "E2801", {"start": v(33.93, -11.24) * mm, "end": v(34.2, -11.25) * mm});
            skLineSegment(sketch, "E2802", {"start": v(34.2, -11.25) * mm, "end": v(34.51, -11.22) * mm});
            skLineSegment(sketch, "E2803", {"start": v(34.51, -11.22) * mm, "end": v(34.79, -11.17) * mm});
            skLineSegment(sketch, "E2804", {"start": v(34.79, -11.17) * mm, "end": v(35.03, -11.09) * mm});
            skLineSegment(sketch, "E2805", {"start": v(35.03, -11.09) * mm, "end": v(35.24, -11) * mm});
            skLineSegment(sketch, "E2806", {"start": v(35.24, -11) * mm, "end": v(35.4, -10.9) * mm});
            skLineSegment(sketch, "E2807", {"start": v(35.4, -10.9) * mm, "end": v(35.53, -10.83) * mm});
            skLineSegment(sketch, "E2808", {"start": v(35.53, -10.83) * mm, "end": v(35.6, -10.78) * mm});
            skLineSegment(sketch, "E2809", {"start": v(35.6, -10.78) * mm, "end": v(35.63, -10.76) * mm});
            skLineSegment(sketch, "E2810", {"start": v(35.63, -10.76) * mm, "end": v(35.68, -10.72) * mm});
            skLineSegment(sketch, "E2811", {"start": v(35.68, -10.72) * mm, "end": v(35.73, -10.68) * mm});
            skLineSegment(sketch, "E2812", {"start": v(35.73, -10.68) * mm, "end": v(35.8, -10.63) * mm});
            skLineSegment(sketch, "E2813", {"start": v(35.8, -10.63) * mm, "end": v(35.87, -10.58) * mm});
            skLineSegment(sketch, "E2814", {"start": v(35.87, -10.58) * mm, "end": v(35.94, -10.55) * mm});
            skLineSegment(sketch, "E2815", {"start": v(35.94, -10.55) * mm, "end": v(36.01, -10.52) * mm});
            skLineSegment(sketch, "E2816", {"start": v(36.01, -10.52) * mm, "end": v(36.08, -10.5) * mm});
            skLineSegment(sketch, "E2817", {"start": v(36.08, -10.5) * mm, "end": v(36.15, -10.5) * mm});
            skLineSegment(sketch, "E2818", {"start": v(36.15, -10.5) * mm, "end": v(36.2, -10.53) * mm});
            skLineSegment(sketch, "E2819", {"start": v(36.2, -10.53) * mm, "end": v(36.24, -10.57) * mm});
            skLineSegment(sketch, "E2820", {"start": v(36.24, -10.57) * mm, "end": v(36.28, -10.62) * mm});
            skLineSegment(sketch, "E2821", {"start": v(36.28, -10.62) * mm, "end": v(36.32, -10.68) * mm});
            skLineSegment(sketch, "E2822", {"start": v(36.32, -10.68) * mm, "end": v(36.35, -10.74) * mm});
            skLineSegment(sketch, "E2823", {"start": v(36.35, -10.74) * mm, "end": v(36.38, -10.8) * mm});
            skLineSegment(sketch, "E2824", {"start": v(36.38, -10.8) * mm, "end": v(36.4, -10.86) * mm});
            skLineSegment(sketch, "E2825", {"start": v(36.4, -10.86) * mm, "end": v(36.44, -10.9) * mm});
            skLineSegment(sketch, "E2826", {"start": v(36.44, -10.9) * mm, "end": v(36.48, -10.95) * mm});
            skLineSegment(sketch, "E2827", {"start": v(36.48, -10.95) * mm, "end": v(36.53, -11) * mm});
            skLineSegment(sketch, "E2828", {"start": v(36.53, -11) * mm, "end": v(36.59, -11.03) * mm});
            skLineSegment(sketch, "E2829", {"start": v(36.59, -11.03) * mm, "end": v(36.64, -11.05) * mm});
            skLineSegment(sketch, "E2830", {"start": v(36.64, -11.05) * mm, "end": v(36.7, -11.06) * mm});
            skLineSegment(sketch, "E2831", {"start": v(36.7, -11.06) * mm, "end": v(36.76, -11.06) * mm});
            skLineSegment(sketch, "E2832", {"start": v(36.76, -11.06) * mm, "end": v(36.83, -11.04) * mm});
            skLineSegment(sketch, "E2833", {"start": v(36.83, -11.04) * mm, "end": v(36.9, -11.02) * mm});
            skLineSegment(sketch, "E2834", {"start": v(36.9, -11.02) * mm, "end": v(36.98, -10.95) * mm});
            skLineSegment(sketch, "E2835", {"start": v(36.98, -10.95) * mm, "end": v(37.05, -10.87) * mm});
            skLineSegment(sketch, "E2836", {"start": v(37.05, -10.87) * mm, "end": v(37.1, -10.78) * mm});
            skLineSegment(sketch, "E2837", {"start": v(37.1, -10.78) * mm, "end": v(37.15, -10.68) * mm});
            skLineSegment(sketch, "E2838", {"start": v(37.15, -10.68) * mm, "end": v(37.18, -10.57) * mm});
            skLineSegment(sketch, "E2839", {"start": v(37.18, -10.57) * mm, "end": v(37.2, -10.46) * mm});
            skLineSegment(sketch, "E2840", {"start": v(37.2, -10.46) * mm, "end": v(37.2, -10.35) * mm});
            skLineSegment(sketch, "E2841", {"start": v(37.2, -10.35) * mm, "end": v(37.21, -10.25) * mm});
            skLineSegment(sketch, "E2842", {"start": v(37.21, -10.25) * mm, "end": v(37.21, -9.17) * mm});
            skLineSegment(sketch, "E2843", {"start": v(37.21, -9.17) * mm, "end": v(37.21, -8.1) * mm});
            skLineSegment(sketch, "E2844", {"start": v(37.21, -8.1) * mm, "end": v(37.22, -7.02) * mm});
            skLineSegment(sketch, "E2845", {"start": v(37.22, -7.02) * mm, "end": v(37.22, -5.94) * mm});
            skLineSegment(sketch, "E2846", {"start": v(37.22, -5.94) * mm, "end": v(37.22, -4.86) * mm});
            skLineSegment(sketch, "E2847", {"start": v(37.22, -4.86) * mm, "end": v(37.22, -3.79) * mm});
            skLineSegment(sketch, "E2848", {"start": v(37.22, -3.79) * mm, "end": v(37.22, -2.7) * mm});
            skLineSegment(sketch, "E2849", {"start": v(37.22, -2.7) * mm, "end": v(37.22, -1.63) * mm});
            skLineSegment(sketch, "E2850", {"start": v(37.22, -1.63) * mm, "end": v(37.21, -1.47) * mm});
            skLineSegment(sketch, "E2851", {"start": v(37.21, -1.47) * mm, "end": v(37.18, -1.32) * mm});
            skLineSegment(sketch, "E2852", {"start": v(36.28, -8.3) * mm, "end": v(36.26, -8.51) * mm});
            skLineSegment(sketch, "E2853", {"start": v(36.26, -8.51) * mm, "end": v(36.23, -8.72) * mm});
            skLineSegment(sketch, "E2854", {"start": v(36.23, -8.72) * mm, "end": v(36.18, -8.91) * mm});
            skLineSegment(sketch, "E2855", {"start": v(36.18, -8.91) * mm, "end": v(36.11, -9.1) * mm});
            skLineSegment(sketch, "E2856", {"start": v(36.11, -9.1) * mm, "end": v(36.03, -9.28) * mm});
            skLineSegment(sketch, "E2857", {"start": v(36.03, -9.28) * mm, "end": v(35.94, -9.44) * mm});
            skLineSegment(sketch, "E2858", {"start": v(35.94, -9.44) * mm, "end": v(35.83, -9.6) * mm});
            skLineSegment(sketch, "E2859", {"start": v(35.83, -9.6) * mm, "end": v(35.69, -9.76) * mm});
            skLineSegment(sketch, "E2860", {"start": v(35.69, -9.76) * mm, "end": v(35.54, -9.9) * mm});
            skLineSegment(sketch, "E2861", {"start": v(35.54, -9.9) * mm, "end": v(35.37, -10.02) * mm});
            skLineSegment(sketch, "E2862", {"start": v(35.37, -10.02) * mm, "end": v(35.2, -10.11) * mm});
            skLineSegment(sketch, "E2863", {"start": v(35.2, -10.11) * mm, "end": v(35, -10.19) * mm});
            skLineSegment(sketch, "E2864", {"start": v(35, -10.19) * mm, "end": v(34.8, -10.24) * mm});
            skLineSegment(sketch, "E2865", {"start": v(34.8, -10.24) * mm, "end": v(34.59, -10.27) * mm});
            skLineSegment(sketch, "E2866", {"start": v(34.59, -10.27) * mm, "end": v(34.36, -10.29) * mm});
            skLineSegment(sketch, "E2867", {"start": v(34.36, -10.29) * mm, "end": v(34.15, -10.28) * mm});
            skLineSegment(sketch, "E2868", {"start": v(34.15, -10.28) * mm, "end": v(33.94, -10.25) * mm});
            skLineSegment(sketch, "E2869", {"start": v(33.94, -10.25) * mm, "end": v(33.75, -10.2) * mm});
            skLineSegment(sketch, "E2870", {"start": v(33.75, -10.2) * mm, "end": v(33.57, -10.13) * mm});
            skLineSegment(sketch, "E2871", {"start": v(33.57, -10.13) * mm, "end": v(33.4, -10.03) * mm});
            skLineSegment(sketch, "E2872", {"start": v(33.4, -10.03) * mm, "end": v(33.25, -9.92) * mm});
            skLineSegment(sketch, "E2873", {"start": v(33.25, -9.92) * mm, "end": v(33.1, -9.79) * mm});
            skLineSegment(sketch, "E2874", {"start": v(33.1, -9.79) * mm, "end": v(32.97, -9.63) * mm});
            skLineSegment(sketch, "E2875", {"start": v(32.97, -9.63) * mm, "end": v(32.86, -9.48) * mm});
            skLineSegment(sketch, "E2876", {"start": v(32.86, -9.48) * mm, "end": v(32.77, -9.31) * mm});
            skLineSegment(sketch, "E2877", {"start": v(32.77, -9.31) * mm, "end": v(32.69, -9.14) * mm});
            skLineSegment(sketch, "E2878", {"start": v(32.69, -9.14) * mm, "end": v(32.62, -8.96) * mm});
            skLineSegment(sketch, "E2879", {"start": v(32.62, -8.96) * mm, "end": v(32.57, -8.77) * mm});
            skLineSegment(sketch, "E2880", {"start": v(32.57, -8.77) * mm, "end": v(32.53, -8.57) * mm});
            skLineSegment(sketch, "E2881", {"start": v(32.53, -8.57) * mm, "end": v(32.5, -8.36) * mm});
            skLineSegment(sketch, "E2882", {"start": v(32.5, -8.36) * mm, "end": v(32.5, -8.14) * mm});
            skLineSegment(sketch, "E2883", {"start": v(32.5, -8.14) * mm, "end": v(32.5, -7.92) * mm});
            skLineSegment(sketch, "E2884", {"start": v(32.5, -7.92) * mm, "end": v(32.53, -7.72) * mm});
            skLineSegment(sketch, "E2885", {"start": v(32.53, -7.72) * mm, "end": v(32.57, -7.52) * mm});
            skLineSegment(sketch, "E2886", {"start": v(32.57, -7.52) * mm, "end": v(32.62, -7.33) * mm});
            skLineSegment(sketch, "E2887", {"start": v(32.62, -7.33) * mm, "end": v(32.69, -7.14) * mm});
            skLineSegment(sketch, "E2888", {"start": v(32.69, -7.14) * mm, "end": v(32.77, -6.97) * mm});
            skLineSegment(sketch, "E2889", {"start": v(32.77, -6.97) * mm, "end": v(32.87, -6.8) * mm});
            skLineSegment(sketch, "E2890", {"start": v(32.87, -6.8) * mm, "end": v(33, -6.64) * mm});
            skLineSegment(sketch, "E2891", {"start": v(33, -6.64) * mm, "end": v(33.13, -6.48) * mm});
            skLineSegment(sketch, "E2892", {"start": v(33.13, -6.48) * mm, "end": v(33.27, -6.35) * mm});
            skLineSegment(sketch, "E2893", {"start": v(33.27, -6.35) * mm, "end": v(33.43, -6.23) * mm});
            skLineSegment(sketch, "E2894", {"start": v(33.43, -6.23) * mm, "end": v(33.6, -6.14) * mm});
            skLineSegment(sketch, "E2895", {"start": v(33.6, -6.14) * mm, "end": v(33.78, -6.06) * mm});
            skLineSegment(sketch, "E2896", {"start": v(33.78, -6.06) * mm, "end": v(33.96, -6) * mm});
            skLineSegment(sketch, "E2897", {"start": v(33.96, -6) * mm, "end": v(34.16, -5.98) * mm});
            skLineSegment(sketch, "E2898", {"start": v(34.16, -5.98) * mm, "end": v(34.36, -5.96) * mm});
            skLineSegment(sketch, "E2899", {"start": v(34.36, -5.96) * mm, "end": v(34.58, -5.97) * mm});
            skLineSegment(sketch, "E2900", {"start": v(34.58, -5.97) * mm, "end": v(34.78, -6) * mm});
            skLineSegment(sketch, "E2901", {"start": v(34.78, -6) * mm, "end": v(34.97, -6.05) * mm});
            skLineSegment(sketch, "E2902", {"start": v(34.97, -6.05) * mm, "end": v(35.15, -6.12) * mm});
            skLineSegment(sketch, "E2903", {"start": v(35.15, -6.12) * mm, "end": v(35.32, -6.21) * mm});
            skLineSegment(sketch, "E2904", {"start": v(35.32, -6.21) * mm, "end": v(35.49, -6.32) * mm});
            skLineSegment(sketch, "E2905", {"start": v(35.49, -6.32) * mm, "end": v(35.64, -6.45) * mm});
            skLineSegment(sketch, "E2906", {"start": v(35.64, -6.45) * mm, "end": v(35.77, -6.6) * mm});
            skLineSegment(sketch, "E2907", {"start": v(35.77, -6.6) * mm, "end": v(35.9, -6.76) * mm});
            skLineSegment(sketch, "E2908", {"start": v(35.9, -6.76) * mm, "end": v(36, -6.92) * mm});
            skLineSegment(sketch, "E2909", {"start": v(36, -6.92) * mm, "end": v(36.08, -7.09) * mm});
            skLineSegment(sketch, "E2910", {"start": v(36.08, -7.09) * mm, "end": v(36.15, -7.27) * mm});
            skLineSegment(sketch, "E2911", {"start": v(36.15, -7.27) * mm, "end": v(36.2, -7.46) * mm});
            skLineSegment(sketch, "E2912", {"start": v(36.2, -7.46) * mm, "end": v(36.25, -7.65) * mm});
            skLineSegment(sketch, "E2913", {"start": v(36.25, -7.65) * mm, "end": v(36.27, -7.86) * mm});
            skLineSegment(sketch, "E2914", {"start": v(36.27, -7.86) * mm, "end": v(36.29, -8.07) * mm});
            skLineSegment(sketch, "E2915", {"start": v(36.29, -8.07) * mm, "end": v(36.28, -8.3) * mm});
            skLineSegment(sketch, "E2916", {"start": v(42.23, -9.27) * mm, "end": v(42.22, -9.19) * mm});
            skLineSegment(sketch, "E2917", {"start": v(42.22, -9.19) * mm, "end": v(42.2, -9.1) * mm});
            skLineSegment(sketch, "E2918", {"start": v(42.2, -9.1) * mm, "end": v(42.2, -9.02) * mm});
            skLineSegment(sketch, "E2919", {"start": v(42.2, -9.02) * mm, "end": v(42.17, -8.93) * mm});
            skLineSegment(sketch, "E2920", {"start": v(42.17, -8.93) * mm, "end": v(42.15, -8.85) * mm});
            skLineSegment(sketch, "E2921", {"start": v(42.15, -8.85) * mm, "end": v(42.12, -8.77) * mm});
            skLineSegment(sketch, "E2922", {"start": v(42.12, -8.77) * mm, "end": v(42.1, -8.69) * mm});
            skLineSegment(sketch, "E2923", {"start": v(42.1, -8.69) * mm, "end": v(42.09, -8.68) * mm});
            skLineSegment(sketch, "E2924", {"start": v(42.09, -8.68) * mm, "end": v(42.08, -8.67) * mm});
            skLineSegment(sketch, "E2925", {"start": v(42.08, -8.67) * mm, "end": v(42.08, -8.66) * mm});
            skLineSegment(sketch, "E2926", {"start": v(42.08, -8.66) * mm, "end": v(42.07, -8.65) * mm});
            skLineSegment(sketch, "E2927", {"start": v(42.07, -8.65) * mm, "end": v(42.07, -8.64) * mm});
            skLineSegment(sketch, "E2928", {"start": v(42.07, -8.64) * mm, "end": v(42.06, -8.63) * mm});
            skLineSegment(sketch, "E2929", {"start": v(42.06, -8.63) * mm, "end": v(42.06, -8.62) * mm});
            skLineSegment(sketch, "E2930", {"start": v(42.06, -8.62) * mm, "end": v(42.06, -8.61) * mm});
            skLineSegment(sketch, "E2931", {"start": v(42.06, -8.61) * mm, "end": v(41.9, -8.38) * mm});
            skLineSegment(sketch, "E2932", {"start": v(41.9, -8.38) * mm, "end": v(41.71, -8.17) * mm});
            skLineSegment(sketch, "E2933", {"start": v(41.71, -8.17) * mm, "end": v(41.49, -7.99) * mm});
            skLineSegment(sketch, "E2934", {"start": v(41.49, -7.99) * mm, "end": v(41.24, -7.82) * mm});
            skLineSegment(sketch, "E2935", {"start": v(41.24, -7.82) * mm, "end": v(40.97, -7.68) * mm});
            skLineSegment(sketch, "E2936", {"start": v(40.97, -7.68) * mm, "end": v(40.7, -7.56) * mm});
            skLineSegment(sketch, "E2937", {"start": v(40.7, -7.56) * mm, "end": v(40.44, -7.45) * mm});
            skLineSegment(sketch, "E2938", {"start": v(40.44, -7.45) * mm, "end": v(40.18, -7.35) * mm});
            skLineSegment(sketch, "E2939", {"start": v(40.18, -7.35) * mm, "end": v(40.08, -7.31) * mm});
            skLineSegment(sketch, "E2940", {"start": v(40.08, -7.31) * mm, "end": v(39.99, -7.27) * mm});
            skLineSegment(sketch, "E2941", {"start": v(39.99, -7.27) * mm, "end": v(39.9, -7.22) * mm});
            skLineSegment(sketch, "E2942", {"start": v(39.9, -7.22) * mm, "end": v(39.82, -7.16) * mm});
            skLineSegment(sketch, "E2943", {"start": v(39.82, -7.16) * mm, "end": v(39.74, -7.1) * mm});
            skLineSegment(sketch, "E2944", {"start": v(39.74, -7.1) * mm, "end": v(39.67, -7.02) * mm});
            skLineSegment(sketch, "E2945", {"start": v(39.67, -7.02) * mm, "end": v(39.62, -6.93) * mm});
            skLineSegment(sketch, "E2946", {"start": v(39.62, -6.93) * mm, "end": v(39.57, -6.83) * mm});
            skLineSegment(sketch, "E2947", {"start": v(39.57, -6.83) * mm, "end": v(39.54, -6.7) * mm});
            skLineSegment(sketch, "E2948", {"start": v(39.54, -6.7) * mm, "end": v(39.54, -6.57) * mm});
            skLineSegment(sketch, "E2949", {"start": v(39.54, -6.57) * mm, "end": v(39.56, -6.45) * mm});
            skLineSegment(sketch, "E2950", {"start": v(39.56, -6.45) * mm, "end": v(39.62, -6.33) * mm});
            skLineSegment(sketch, "E2951", {"start": v(39.62, -6.33) * mm, "end": v(39.69, -6.23) * mm});
            skLineSegment(sketch, "E2952", {"start": v(39.69, -6.23) * mm, "end": v(39.78, -6.15) * mm});
            skLineSegment(sketch, "E2953", {"start": v(39.78, -6.15) * mm, "end": v(39.89, -6.08) * mm});
            skLineSegment(sketch, "E2954", {"start": v(39.89, -6.08) * mm, "end": v(40, -6.03) * mm});
            skLineSegment(sketch, "E2955", {"start": v(40, -6.03) * mm, "end": v(40.1, -6) * mm});
            skLineSegment(sketch, "E2956", {"start": v(40.1, -6) * mm, "end": v(40.18, -6) * mm});
            skLineSegment(sketch, "E2957", {"start": v(40.18, -6) * mm, "end": v(40.27, -6) * mm});
            skLineSegment(sketch, "E2958", {"start": v(40.27, -6) * mm, "end": v(40.36, -6.02) * mm});
            skLineSegment(sketch, "E2959", {"start": v(40.36, -6.02) * mm, "end": v(40.45, -6.04) * mm});
            skLineSegment(sketch, "E2960", {"start": v(40.45, -6.04) * mm, "end": v(40.53, -6.07) * mm});
            skLineSegment(sketch, "E2961", {"start": v(40.53, -6.07) * mm, "end": v(40.61, -6.11) * mm});
            skLineSegment(sketch, "E2962", {"start": v(40.61, -6.11) * mm, "end": v(40.69, -6.16) * mm});
            skLineSegment(sketch, "E2963", {"start": v(40.69, -6.16) * mm, "end": v(40.75, -6.22) * mm});
            skLineSegment(sketch, "E2964", {"start": v(40.75, -6.22) * mm, "end": v(40.8, -6.28) * mm});
            skLineSegment(sketch, "E2965", {"start": v(40.8, -6.28) * mm, "end": v(40.86, -6.33) * mm});
            skLineSegment(sketch, "E2966", {"start": v(40.86, -6.33) * mm, "end": v(40.92, -6.38) * mm});
            skLineSegment(sketch, "E2967", {"start": v(40.92, -6.38) * mm, "end": v(40.98, -6.42) * mm});
            skLineSegment(sketch, "E2968", {"start": v(40.98, -6.42) * mm, "end": v(41.04, -6.44) * mm});
            skLineSegment(sketch, "E2969", {"start": v(41.04, -6.44) * mm, "end": v(41.12, -6.46) * mm});
            skLineSegment(sketch, "E2970", {"start": v(41.12, -6.46) * mm, "end": v(41.21, -6.45) * mm});
            skLineSegment(sketch, "E2971", {"start": v(41.21, -6.45) * mm, "end": v(41.32, -6.43) * mm});
            skLineSegment(sketch, "E2972", {"start": v(41.32, -6.43) * mm, "end": v(41.43, -6.4) * mm});
            skLineSegment(sketch, "E2973", {"start": v(41.43, -6.4) * mm, "end": v(41.54, -6.35) * mm});
            skLineSegment(sketch, "E2974", {"start": v(41.54, -6.35) * mm, "end": v(41.64, -6.3) * mm});
            skLineSegment(sketch, "E2975", {"start": v(41.64, -6.3) * mm, "end": v(41.72, -6.22) * mm});
            skLineSegment(sketch, "E2976", {"start": v(41.72, -6.22) * mm, "end": v(41.78, -6.13) * mm});
            skLineSegment(sketch, "E2977", {"start": v(41.78, -6.13) * mm, "end": v(41.8, -6.03) * mm});
            skLineSegment(sketch, "E2978", {"start": v(41.8, -6.03) * mm, "end": v(41.77, -5.9) * mm});
            skLineSegment(sketch, "E2979", {"start": v(41.77, -5.9) * mm, "end": v(41.73, -5.82) * mm});
            skLineSegment(sketch, "E2980", {"start": v(41.73, -5.82) * mm, "end": v(41.67, -5.74) * mm});
            skLineSegment(sketch, "E2981", {"start": v(41.67, -5.74) * mm, "end": v(41.61, -5.66) * mm});
            skLineSegment(sketch, "E2982", {"start": v(41.61, -5.66) * mm, "end": v(41.54, -5.59) * mm});
            skLineSegment(sketch, "E2983", {"start": v(41.54, -5.59) * mm, "end": v(41.46, -5.52) * mm});
            skLineSegment(sketch, "E2984", {"start": v(41.46, -5.52) * mm, "end": v(41.39, -5.46) * mm});
            skLineSegment(sketch, "E2985", {"start": v(41.39, -5.46) * mm, "end": v(41.3, -5.4) * mm});
            skLineSegment(sketch, "E2986", {"start": v(41.3, -5.4) * mm, "end": v(41.23, -5.34) * mm});
            skLineSegment(sketch, "E2987", {"start": v(41.23, -5.34) * mm, "end": v(41.12, -5.27) * mm});
            skLineSegment(sketch, "E2988", {"start": v(41.12, -5.27) * mm, "end": v(41, -5.22) * mm});
            skLineSegment(sketch, "E2989", {"start": v(41, -5.22) * mm, "end": v(40.9, -5.17) * mm});
            skLineSegment(sketch, "E2990", {"start": v(40.9, -5.17) * mm, "end": v(40.77, -5.13) * mm});
            skLineSegment(sketch, "E2991", {"start": v(40.77, -5.13) * mm, "end": v(40.65, -5.1) * mm});
            skLineSegment(sketch, "E2992", {"start": v(40.65, -5.1) * mm, "end": v(40.52, -5.08) * mm});
            skLineSegment(sketch, "E2993", {"start": v(40.52, -5.08) * mm, "end": v(40.4, -5.07) * mm});
            skLineSegment(sketch, "E2994", {"start": v(40.4, -5.07) * mm, "end": v(40.27, -5.07) * mm});
            skLineSegment(sketch, "E2995", {"start": v(40.27, -5.07) * mm, "end": v(40.07, -5.07) * mm});
            skLineSegment(sketch, "E2996", {"start": v(40.07, -5.07) * mm, "end": v(39.88, -5.1) * mm});
            skLineSegment(sketch, "E2997", {"start": v(39.88, -5.1) * mm, "end": v(39.7, -5.15) * mm});
            skLineSegment(sketch, "E2998", {"start": v(39.7, -5.15) * mm, "end": v(39.54, -5.2) * mm});
            skLineSegment(sketch, "E2999", {"start": v(39.54, -5.2) * mm, "end": v(39.38, -5.3) * mm});
            skLineSegment(sketch, "E3000", {"start": v(39.38, -5.3) * mm, "end": v(39.23, -5.4) * mm});
            skLineSegment(sketch, "E3001", {"start": v(39.23, -5.4) * mm, "end": v(39.1, -5.51) * mm});
            skLineSegment(sketch, "E3002", {"start": v(39.1, -5.51) * mm, "end": v(38.97, -5.65) * mm});
            skLineSegment(sketch, "E3003", {"start": v(38.97, -5.65) * mm, "end": v(38.92, -5.71) * mm});
            skLineSegment(sketch, "E3004", {"start": v(38.92, -5.71) * mm, "end": v(38.87, -5.79) * mm});
            skLineSegment(sketch, "E3005", {"start": v(38.87, -5.79) * mm, "end": v(38.82, -5.86) * mm});
            skLineSegment(sketch, "E3006", {"start": v(38.82, -5.86) * mm, "end": v(38.78, -5.94) * mm});
            skLineSegment(sketch, "E3007", {"start": v(38.78, -5.94) * mm, "end": v(38.74, -6.02) * mm});
            skLineSegment(sketch, "E3008", {"start": v(38.74, -6.02) * mm, "end": v(38.7, -6.1) * mm});
            skLineSegment(sketch, "E3009", {"start": v(38.7, -6.1) * mm, "end": v(38.67, -6.18) * mm});
            skLineSegment(sketch, "E3010", {"start": v(38.67, -6.18) * mm, "end": v(38.64, -6.26) * mm});
            skLineSegment(sketch, "E3011", {"start": v(38.64, -6.26) * mm, "end": v(38.6, -6.4) * mm});
            skLineSegment(sketch, "E3012", {"start": v(38.6, -6.4) * mm, "end": v(38.57, -6.54) * mm});
            skLineSegment(sketch, "E3013", {"start": v(38.57, -6.54) * mm, "end": v(38.56, -6.68) * mm});
            skLineSegment(sketch, "E3014", {"start": v(38.56, -6.68) * mm, "end": v(38.57, -6.82) * mm});
            skLineSegment(sketch, "E3015", {"start": v(38.57, -6.82) * mm, "end": v(38.59, -6.97) * mm});
            skLineSegment(sketch, "E3016", {"start": v(38.59, -6.97) * mm, "end": v(38.62, -7.1) * mm});
            skLineSegment(sketch, "E3017", {"start": v(38.62, -7.1) * mm, "end": v(38.66, -7.24) * mm});
            skLineSegment(sketch, "E3018", {"start": v(38.66, -7.24) * mm, "end": v(38.72, -7.37) * mm});
            skLineSegment(sketch, "E3019", {"start": v(38.72, -7.37) * mm, "end": v(38.85, -7.56) * mm});
            skLineSegment(sketch, "E3020", {"start": v(38.85, -7.56) * mm, "end": v(39, -7.73) * mm});
            skLineSegment(sketch, "E3021", {"start": v(39, -7.73) * mm, "end": v(39.16, -7.87) * mm});
            skLineSegment(sketch, "E3022", {"start": v(39.16, -7.87) * mm, "end": v(39.34, -7.99) * mm});
            skLineSegment(sketch, "E3023", {"start": v(39.34, -7.99) * mm, "end": v(39.53, -8.1) * mm});
            skLineSegment(sketch, "E3024", {"start": v(39.53, -8.1) * mm, "end": v(39.74, -8.19) * mm});
            skLineSegment(sketch, "E3025", {"start": v(39.74, -8.19) * mm, "end": v(39.94, -8.27) * mm});
            skLineSegment(sketch, "E3026", {"start": v(39.94, -8.27) * mm, "end": v(40.15, -8.36) * mm});
            skLineSegment(sketch, "E3027", {"start": v(40.15, -8.36) * mm, "end": v(40.33, -8.44) * mm});
            skLineSegment(sketch, "E3028", {"start": v(40.33, -8.44) * mm, "end": v(40.51, -8.53) * mm});
            skLineSegment(sketch, "E3029", {"start": v(40.51, -8.53) * mm, "end": v(40.69, -8.63) * mm});
            skLineSegment(sketch, "E3030", {"start": v(40.69, -8.63) * mm, "end": v(40.85, -8.75) * mm});
            skLineSegment(sketch, "E3031", {"start": v(40.85, -8.75) * mm, "end": v(40.99, -8.9) * mm});
            skLineSegment(sketch, "E3032", {"start": v(40.99, -8.9) * mm, "end": v(41.1, -9.05) * mm});
            skLineSegment(sketch, "E3033", {"start": v(41.1, -9.05) * mm, "end": v(41.16, -9.24) * mm});
            skLineSegment(sketch, "E3034", {"start": v(41.16, -9.24) * mm, "end": v(41.18, -9.45) * mm});
            skLineSegment(sketch, "E3035", {"start": v(41.18, -9.45) * mm, "end": v(41.17, -9.55) * mm});
            skLineSegment(sketch, "E3036", {"start": v(41.17, -9.55) * mm, "end": v(41.16, -9.65) * mm});
            skLineSegment(sketch, "E3037", {"start": v(41.16, -9.65) * mm, "end": v(41.13, -9.75) * mm});
            skLineSegment(sketch, "E3038", {"start": v(41.13, -9.75) * mm, "end": v(41.1, -9.83) * mm});
            skLineSegment(sketch, "E3039", {"start": v(41.1, -9.83) * mm, "end": v(41.06, -9.91) * mm});
            skLineSegment(sketch, "E3040", {"start": v(41.06, -9.91) * mm, "end": v(41.01, -9.99) * mm});
            skLineSegment(sketch, "E3041", {"start": v(41.01, -9.99) * mm, "end": v(40.96, -10.06) * mm});
            skLineSegment(sketch, "E3042", {"start": v(40.96, -10.06) * mm, "end": v(40.9, -10.12) * mm});
            skLineSegment(sketch, "E3043", {"start": v(40.9, -10.12) * mm, "end": v(40.83, -10.17) * mm});
            skLineSegment(sketch, "E3044", {"start": v(40.83, -10.17) * mm, "end": v(40.77, -10.22) * mm});
            skLineSegment(sketch, "E3045", {"start": v(40.77, -10.22) * mm, "end": v(40.7, -10.26) * mm});
            skLineSegment(sketch, "E3046", {"start": v(40.7, -10.26) * mm, "end": v(40.63, -10.29) * mm});
            skLineSegment(sketch, "E3047", {"start": v(40.63, -10.29) * mm, "end": v(40.55, -10.3) * mm});
            skLineSegment(sketch, "E3048", {"start": v(40.55, -10.3) * mm, "end": v(40.47, -10.33) * mm});
            skLineSegment(sketch, "E3049", {"start": v(40.47, -10.33) * mm, "end": v(40.38, -10.34) * mm});
            skLineSegment(sketch, "E3050", {"start": v(40.38, -10.34) * mm, "end": v(40.29, -10.34) * mm});
            skLineSegment(sketch, "E3051", {"start": v(40.29, -10.34) * mm, "end": v(40.17, -10.33) * mm});
            skLineSegment(sketch, "E3052", {"start": v(40.17, -10.33) * mm, "end": v(40.05, -10.31) * mm});
            skLineSegment(sketch, "E3053", {"start": v(40.05, -10.31) * mm, "end": v(39.93, -10.28) * mm});
            skLineSegment(sketch, "E3054", {"start": v(39.93, -10.28) * mm, "end": v(39.82, -10.24) * mm});
            skLineSegment(sketch, "E3055", {"start": v(39.82, -10.24) * mm, "end": v(39.72, -10.18) * mm});
            skLineSegment(sketch, "E3056", {"start": v(39.72, -10.18) * mm, "end": v(39.62, -10.12) * mm});
            skLineSegment(sketch, "E3057", {"start": v(39.62, -10.12) * mm, "end": v(39.53, -10.04) * mm});
            skLineSegment(sketch, "E3058", {"start": v(39.53, -10.04) * mm, "end": v(39.44, -9.95) * mm});
            skLineSegment(sketch, "E3059", {"start": v(39.44, -9.95) * mm, "end": v(39.4, -9.9) * mm});
            skLineSegment(sketch, "E3060", {"start": v(39.4, -9.9) * mm, "end": v(39.35, -9.83) * mm});
            skLineSegment(sketch, "E3061", {"start": v(39.35, -9.83) * mm, "end": v(39.3, -9.78) * mm});
            skLineSegment(sketch, "E3062", {"start": v(39.3, -9.78) * mm, "end": v(39.26, -9.72) * mm});
            skLineSegment(sketch, "E3063", {"start": v(39.26, -9.72) * mm, "end": v(39.22, -9.67) * mm});
            skLineSegment(sketch, "E3064", {"start": v(39.22, -9.67) * mm, "end": v(39.17, -9.62) * mm});
            skLineSegment(sketch, "E3065", {"start": v(39.17, -9.62) * mm, "end": v(39.1, -9.58) * mm});
            skLineSegment(sketch, "E3066", {"start": v(39.1, -9.58) * mm, "end": v(39.03, -9.54) * mm});
            skLineSegment(sketch, "E3067", {"start": v(39.03, -9.54) * mm, "end": v(38.96, -9.52) * mm});
            skLineSegment(sketch, "E3068", {"start": v(38.96, -9.52) * mm, "end": v(38.89, -9.5) * mm});
            skLineSegment(sketch, "E3069", {"start": v(38.89, -9.5) * mm, "end": v(38.81, -9.5) * mm});
            skLineSegment(sketch, "E3070", {"start": v(38.81, -9.5) * mm, "end": v(38.74, -9.5) * mm});
            skLineSegment(sketch, "E3071", {"start": v(38.74, -9.5) * mm, "end": v(38.67, -9.52) * mm});
            skLineSegment(sketch, "E3072", {"start": v(38.67, -9.52) * mm, "end": v(38.6, -9.54) * mm});
            skLineSegment(sketch, "E3073", {"start": v(38.6, -9.54) * mm, "end": v(38.53, -9.58) * mm});
            skLineSegment(sketch, "E3074", {"start": v(38.53, -9.58) * mm, "end": v(38.47, -9.62) * mm});
            skLineSegment(sketch, "E3075", {"start": v(38.47, -9.62) * mm, "end": v(38.4, -9.7) * mm});
            skLineSegment(sketch, "E3076", {"start": v(38.4, -9.7) * mm, "end": v(38.37, -9.8) * mm});
            skLineSegment(sketch, "E3077", {"start": v(38.37, -9.8) * mm, "end": v(38.36, -9.9) * mm});
            skLineSegment(sketch, "E3078", {"start": v(38.36, -9.9) * mm, "end": v(38.37, -10) * mm});
            skLineSegment(sketch, "E3079", {"start": v(38.37, -10) * mm, "end": v(38.4, -10.12) * mm});
            skLineSegment(sketch, "E3080", {"start": v(38.4, -10.12) * mm, "end": v(38.43, -10.22) * mm});
            skLineSegment(sketch, "E3081", {"start": v(38.43, -10.22) * mm, "end": v(38.47, -10.32) * mm});
            skLineSegment(sketch, "E3082", {"start": v(38.47, -10.32) * mm, "end": v(38.51, -10.4) * mm});
            skLineSegment(sketch, "E3083", {"start": v(38.51, -10.4) * mm, "end": v(38.57, -10.49) * mm});
            skLineSegment(sketch, "E3084", {"start": v(38.57, -10.49) * mm, "end": v(38.63, -10.57) * mm});
            skLineSegment(sketch, "E3085", {"start": v(38.63, -10.57) * mm, "end": v(38.7, -10.65) * mm});
            skLineSegment(sketch, "E3086", {"start": v(38.7, -10.65) * mm, "end": v(38.77, -10.72) * mm});
            skLineSegment(sketch, "E3087", {"start": v(38.77, -10.72) * mm, "end": v(38.85, -10.79) * mm});
            skLineSegment(sketch, "E3088", {"start": v(38.85, -10.79) * mm, "end": v(38.93, -10.85) * mm});
            skLineSegment(sketch, "E3089", {"start": v(38.93, -10.85) * mm, "end": v(39.01, -10.9) * mm});
            skLineSegment(sketch, "E3090", {"start": v(39.01, -10.9) * mm, "end": v(39.1, -10.96) * mm});
            skLineSegment(sketch, "E3091", {"start": v(39.1, -10.96) * mm, "end": v(39.23, -11.03) * mm});
            skLineSegment(sketch, "E3092", {"start": v(39.23, -11.03) * mm, "end": v(39.36, -11.1) * mm});
            skLineSegment(sketch, "E3093", {"start": v(39.36, -11.1) * mm, "end": v(39.5, -11.14) * mm});
            skLineSegment(sketch, "E3094", {"start": v(39.5, -11.14) * mm, "end": v(39.64, -11.18) * mm});
            skLineSegment(sketch, "E3095", {"start": v(39.64, -11.18) * mm, "end": v(39.78, -11.21) * mm});
            skLineSegment(sketch, "E3096", {"start": v(39.78, -11.21) * mm, "end": v(39.93, -11.24) * mm});
            skLineSegment(sketch, "E3097", {"start": v(39.93, -11.24) * mm, "end": v(40.07, -11.25) * mm});
            skLineSegment(sketch, "E3098", {"start": v(40.07, -11.25) * mm, "end": v(40.22, -11.26) * mm});
            skLineSegment(sketch, "E3099", {"start": v(40.22, -11.26) * mm, "end": v(40.33, -11.25) * mm});
            skLineSegment(sketch, "E3100", {"start": v(40.33, -11.25) * mm, "end": v(40.45, -11.24) * mm});
            skLineSegment(sketch, "E3101", {"start": v(40.45, -11.24) * mm, "end": v(40.56, -11.23) * mm});
            skLineSegment(sketch, "E3102", {"start": v(40.56, -11.23) * mm, "end": v(40.67, -11.21) * mm});
            skLineSegment(sketch, "E3103", {"start": v(40.67, -11.21) * mm, "end": v(40.78, -11.19) * mm});
            skLineSegment(sketch, "E3104", {"start": v(40.78, -11.19) * mm, "end": v(40.9, -11.15) * mm});
            skLineSegment(sketch, "E3105", {"start": v(40.9, -11.15) * mm, "end": v(41, -11.12) * mm});
            skLineSegment(sketch, "E3106", {"start": v(41, -11.12) * mm, "end": v(41.1, -11.08) * mm});
            skLineSegment(sketch, "E3107", {"start": v(41.1, -11.08) * mm, "end": v(41.23, -11.01) * mm});
            skLineSegment(sketch, "E3108", {"start": v(41.23, -11.01) * mm, "end": v(41.34, -10.95) * mm});
            skLineSegment(sketch, "E3109", {"start": v(41.34, -10.95) * mm, "end": v(41.46, -10.87) * mm});
            skLineSegment(sketch, "E3110", {"start": v(41.46, -10.87) * mm, "end": v(41.56, -10.79) * mm});
            skLineSegment(sketch, "E3111", {"start": v(41.56, -10.79) * mm, "end": v(41.66, -10.7) * mm});
            skLineSegment(sketch, "E3112", {"start": v(41.66, -10.7) * mm, "end": v(41.75, -10.6) * mm});
            skLineSegment(sketch, "E3113", {"start": v(41.75, -10.6) * mm, "end": v(41.84, -10.49) * mm});
            skLineSegment(sketch, "E3114", {"start": v(41.84, -10.49) * mm, "end": v(41.92, -10.37) * mm});
            skLineSegment(sketch, "E3115", {"start": v(41.92, -10.37) * mm, "end": v(42, -10.26) * mm});
            skLineSegment(sketch, "E3116", {"start": v(42, -10.26) * mm, "end": v(42.06, -10.13) * mm});
            skLineSegment(sketch, "E3117", {"start": v(42.06, -10.13) * mm, "end": v(42.1, -10) * mm});
            skLineSegment(sketch, "E3118", {"start": v(42.1, -10) * mm, "end": v(42.15, -9.88) * mm});
            skLineSegment(sketch, "E3119", {"start": v(42.15, -9.88) * mm, "end": v(42.19, -9.76) * mm});
            skLineSegment(sketch, "E3120", {"start": v(42.19, -9.76) * mm, "end": v(42.2, -9.62) * mm});
            skLineSegment(sketch, "E3121", {"start": v(42.2, -9.62) * mm, "end": v(42.22, -9.5) * mm});
            skLineSegment(sketch, "E3122", {"start": v(42.22, -9.5) * mm, "end": v(42.23, -9.36) * mm});
            skLineSegment(sketch, "E3123", {"start": v(42.23, -9.36) * mm, "end": v(42.23, -9.27) * mm});
            skLineSegment(sketch, "E3124", {"start": v(33.78, 6.95) * mm, "end": v(33.77, 6.98) * mm});
            skLineSegment(sketch, "E3125", {"start": v(33.77, 6.98) * mm, "end": v(33.76, 7.01) * mm});
            skLineSegment(sketch, "E3126", {"start": v(33.76, 7.01) * mm, "end": v(33.74, 7.05) * mm});
            skLineSegment(sketch, "E3127", {"start": v(33.74, 7.05) * mm, "end": v(33.72, 7.08) * mm});
            skLineSegment(sketch, "E3128", {"start": v(33.72, 7.08) * mm, "end": v(33.68, 7.12) * mm});
            skLineSegment(sketch, "E3129", {"start": v(33.68, 7.12) * mm, "end": v(33.64, 7.16) * mm});
            skLineSegment(sketch, "E3130", {"start": v(33.64, 7.16) * mm, "end": v(33.63, 7.17) * mm});
            skLineSegment(sketch, "E3131", {"start": v(33.63, 7.17) * mm, "end": v(33.61, 7.18) * mm});
            skLineSegment(sketch, "E3132", {"start": v(33.61, 7.18) * mm, "end": v(33.6, 7.19) * mm});
            skLineSegment(sketch, "E3133", {"start": v(33.6, 7.19) * mm, "end": v(33.59, 7.2) * mm});
            skLineSegment(sketch, "E3134", {"start": v(33.59, 7.2) * mm, "end": v(33.57, 7.2) * mm});
            skLineSegment(sketch, "E3135", {"start": v(33.57, 7.2) * mm, "end": v(33.56, 7.22) * mm});
            skLineSegment(sketch, "E3136", {"start": v(33.56, 7.22) * mm, "end": v(33.54, 7.23) * mm});
            skLineSegment(sketch, "E3137", {"start": v(33.54, 7.23) * mm, "end": v(33.53, 7.24) * mm});
            skLineSegment(sketch, "E3138", {"start": v(33.53, 7.24) * mm, "end": v(33.5, 7.25) * mm});
            skLineSegment(sketch, "E3139", {"start": v(33.5, 7.25) * mm, "end": v(33.5, 7.26) * mm});
            skLineSegment(sketch, "E3140", {"start": v(33.5, 7.26) * mm, "end": v(33.47, 7.27) * mm});
            skLineSegment(sketch, "E3141", {"start": v(33.47, 7.27) * mm, "end": v(33.46, 7.28) * mm});
            skLineSegment(sketch, "E3142", {"start": v(33.46, 7.28) * mm, "end": v(33.44, 7.3) * mm});
            skLineSegment(sketch, "E3143", {"start": v(33.44, 7.3) * mm, "end": v(33.43, 7.3) * mm});
            skLineSegment(sketch, "E3144", {"start": v(33.43, 7.3) * mm, "end": v(33.41, 7.32) * mm});
            skLineSegment(sketch, "E3145", {"start": v(33.41, 7.32) * mm, "end": v(33.4, 7.33) * mm});
            skLineSegment(sketch, "E3146", {"start": v(33.4, 7.33) * mm, "end": v(33.37, 7.36) * mm});
            skLineSegment(sketch, "E3147", {"start": v(33.37, 7.36) * mm, "end": v(33.34, 7.39) * mm});
            skLineSegment(sketch, "E3148", {"start": v(33.34, 7.39) * mm, "end": v(33.32, 7.41) * mm});
            skLineSegment(sketch, "E3149", {"start": v(33.32, 7.41) * mm, "end": v(33.3, 7.44) * mm});
            skLineSegment(sketch, "E3150", {"start": v(33.3, 7.44) * mm, "end": v(33.27, 7.47) * mm});
            skLineSegment(sketch, "E3151", {"start": v(33.27, 7.47) * mm, "end": v(33.24, 7.5) * mm});
            skLineSegment(sketch, "E3152", {"start": v(33.24, 7.5) * mm, "end": v(33.22, 7.52) * mm});
            skLineSegment(sketch, "E3153", {"start": v(33.22, 7.52) * mm, "end": v(33.2, 7.55) * mm});
            skLineSegment(sketch, "E3154", {"start": v(33.2, 7.55) * mm, "end": v(33.16, 7.6) * mm});
            skLineSegment(sketch, "E3155", {"start": v(33.16, 7.6) * mm, "end": v(33.12, 7.63) * mm});
            skLineSegment(sketch, "E3156", {"start": v(33.12, 7.63) * mm, "end": v(33.09, 7.67) * mm});
            skLineSegment(sketch, "E3157", {"start": v(33.09, 7.67) * mm, "end": v(33.05, 7.7) * mm});
            skLineSegment(sketch, "E3158", {"start": v(33.05, 7.7) * mm, "end": v(33.01, 7.75) * mm});
            skLineSegment(sketch, "E3159", {"start": v(33.01, 7.75) * mm, "end": v(32.98, 7.78) * mm});
            skLineSegment(sketch, "E3160", {"start": v(32.98, 7.78) * mm, "end": v(32.94, 7.82) * mm});
            skLineSegment(sketch, "E3161", {"start": v(32.94, 7.82) * mm, "end": v(32.9, 7.86) * mm});
            skLineSegment(sketch, "E3162", {"start": v(32.9, 7.86) * mm, "end": v(32.82, 7.93) * mm});
            skLineSegment(sketch, "E3163", {"start": v(32.82, 7.93) * mm, "end": v(32.73, 8) * mm});
            skLineSegment(sketch, "E3164", {"start": v(32.73, 8) * mm, "end": v(32.64, 8.08) * mm});
            skLineSegment(sketch, "E3165", {"start": v(32.64, 8.08) * mm, "end": v(32.55, 8.16) * mm});
            skLineSegment(sketch, "E3166", {"start": v(32.55, 8.16) * mm, "end": v(32.46, 8.23) * mm});
            skLineSegment(sketch, "E3167", {"start": v(32.46, 8.23) * mm, "end": v(32.36, 8.3) * mm});
            skLineSegment(sketch, "E3168", {"start": v(32.36, 8.3) * mm, "end": v(32.26, 8.39) * mm});
            skLineSegment(sketch, "E3169", {"start": v(32.26, 8.39) * mm, "end": v(32.15, 8.46) * mm});
            skLineSegment(sketch, "E3170", {"start": v(32.15, 8.46) * mm, "end": v(32.12, 8.49) * mm});
            skLineSegment(sketch, "E3171", {"start": v(32.12, 8.49) * mm, "end": v(32.08, 8.5) * mm});
            skLineSegment(sketch, "E3172", {"start": v(32.08, 8.5) * mm, "end": v(32.05, 8.53) * mm});
            skLineSegment(sketch, "E3173", {"start": v(32.05, 8.53) * mm, "end": v(32, 8.55) * mm});
            skLineSegment(sketch, "E3174", {"start": v(32, 8.55) * mm, "end": v(31.97, 8.56) * mm});
            skLineSegment(sketch, "E3175", {"start": v(31.97, 8.56) * mm, "end": v(31.93, 8.58) * mm});
            skLineSegment(sketch, "E3176", {"start": v(31.93, 8.58) * mm, "end": v(31.9, 8.6) * mm});
            skLineSegment(sketch, "E3177", {"start": v(31.9, 8.6) * mm, "end": v(31.86, 8.61) * mm});
            skLineSegment(sketch, "E3178", {"start": v(31.86, 8.61) * mm, "end": v(31.85, 8.61) * mm});
            skLineSegment(sketch, "E3179", {"start": v(31.85, 8.61) * mm, "end": v(31.84, 8.62) * mm});
            skLineSegment(sketch, "E3180", {"start": v(31.84, 8.62) * mm, "end": v(31.82, 8.62) * mm});
            skLineSegment(sketch, "E3181", {"start": v(31.82, 8.62) * mm, "end": v(31.81, 8.63) * mm});
            skLineSegment(sketch, "E3182", {"start": v(31.81, 8.63) * mm, "end": v(31.8, 8.63) * mm});
            skLineSegment(sketch, "E3183", {"start": v(31.8, 8.63) * mm, "end": v(31.8, 8.64) * mm});
            skLineSegment(sketch, "E3184", {"start": v(31.8, 8.64) * mm, "end": v(31.78, 8.64) * mm});
            skLineSegment(sketch, "E3185", {"start": v(31.78, 8.64) * mm, "end": v(31.77, 8.65) * mm});
            skLineSegment(sketch, "E3186", {"start": v(31.77, 8.65) * mm, "end": v(31.75, 8.65) * mm});
            skLineSegment(sketch, "E3187", {"start": v(31.75, 8.65) * mm, "end": v(31.74, 8.66) * mm});
            skLineSegment(sketch, "E3188", {"start": v(31.74, 8.66) * mm, "end": v(31.73, 8.66) * mm});
            skLineSegment(sketch, "E3189", {"start": v(31.73, 8.66) * mm, "end": v(31.71, 8.67) * mm});
            skLineSegment(sketch, "E3190", {"start": v(31.71, 8.67) * mm, "end": v(31.7, 8.68) * mm});
            skLineSegment(sketch, "E3191", {"start": v(31.7, 8.68) * mm, "end": v(31.69, 8.68) * mm});
            skLineSegment(sketch, "E3192", {"start": v(31.69, 8.68) * mm, "end": v(31.67, 8.69) * mm});
            skLineSegment(sketch, "E3193", {"start": v(31.67, 8.69) * mm, "end": v(31.66, 8.7) * mm});
            skLineSegment(sketch, "E3194", {"start": v(31.66, 8.7) * mm, "end": v(31.61, 8.71) * mm});
            skLineSegment(sketch, "E3195", {"start": v(31.61, 8.71) * mm, "end": v(31.57, 8.73) * mm});
            skLineSegment(sketch, "E3196", {"start": v(31.57, 8.73) * mm, "end": v(31.52, 8.75) * mm});
            skLineSegment(sketch, "E3197", {"start": v(31.52, 8.75) * mm, "end": v(31.47, 8.77) * mm});
            skLineSegment(sketch, "E3198", {"start": v(31.47, 8.77) * mm, "end": v(31.43, 8.8) * mm});
            skLineSegment(sketch, "E3199", {"start": v(31.43, 8.8) * mm, "end": v(31.38, 8.8) * mm});
            skLineSegment(sketch, "E3200", {"start": v(31.38, 8.8) * mm, "end": v(31.33, 8.82) * mm});
            skLineSegment(sketch, "E3201", {"start": v(31.33, 8.82) * mm, "end": v(31.28, 8.83) * mm});
            skLineSegment(sketch, "E3202", {"start": v(31.28, 8.83) * mm, "end": v(31.25, 8.84) * mm});
            skLineSegment(sketch, "E3203", {"start": v(31.25, 8.84) * mm, "end": v(31.22, 8.84) * mm});
            skLineSegment(sketch, "E3204", {"start": v(31.22, 8.84) * mm, "end": v(31.18, 8.85) * mm});
            skLineSegment(sketch, "E3205", {"start": v(31.18, 8.85) * mm, "end": v(31.14, 8.85) * mm});
            skLineSegment(sketch, "E3206", {"start": v(31.14, 8.85) * mm, "end": v(31.1, 8.85) * mm});
            skLineSegment(sketch, "E3207", {"start": v(31.1, 8.85) * mm, "end": v(31.07, 8.85) * mm});
            skLineSegment(sketch, "E3208", {"start": v(31.07, 8.85) * mm, "end": v(31.03, 8.85) * mm});
            skLineSegment(sketch, "E3209", {"start": v(31.03, 8.85) * mm, "end": v(30.99, 8.85) * mm});
            skLineSegment(sketch, "E3210", {"start": v(30.99, 8.85) * mm, "end": v(30.97, 8.85) * mm});
            skLineSegment(sketch, "E3211", {"start": v(30.97, 8.85) * mm, "end": v(30.95, 8.85) * mm});
            skLineSegment(sketch, "E3212", {"start": v(30.95, 8.85) * mm, "end": v(30.93, 8.85) * mm});
            skLineSegment(sketch, "E3213", {"start": v(30.93, 8.85) * mm, "end": v(30.91, 8.85) * mm});
            skLineSegment(sketch, "E3214", {"start": v(30.91, 8.85) * mm, "end": v(30.9, 8.85) * mm});
            skLineSegment(sketch, "E3215", {"start": v(30.9, 8.85) * mm, "end": v(30.88, 8.85) * mm});
            skLineSegment(sketch, "E3216", {"start": v(30.88, 8.85) * mm, "end": v(30.86, 8.85) * mm});
            skLineSegment(sketch, "E3217", {"start": v(30.86, 8.85) * mm, "end": v(30.84, 8.85) * mm});
            skLineSegment(sketch, "E3218", {"start": v(30.84, 8.85) * mm, "end": v(30.72, 8.85) * mm});
            skLineSegment(sketch, "E3219", {"start": v(30.72, 8.85) * mm, "end": v(30.6, 8.84) * mm});
            skLineSegment(sketch, "E3220", {"start": v(30.6, 8.84) * mm, "end": v(30.49, 8.83) * mm});
            skLineSegment(sketch, "E3221", {"start": v(30.49, 8.83) * mm, "end": v(30.37, 8.81) * mm});
            skLineSegment(sketch, "E3222", {"start": v(30.37, 8.81) * mm, "end": v(30.25, 8.79) * mm});
            skLineSegment(sketch, "E3223", {"start": v(30.25, 8.79) * mm, "end": v(30.13, 8.76) * mm});
            skLineSegment(sketch, "E3224", {"start": v(30.13, 8.76) * mm, "end": v(30, 8.72) * mm});
            skLineSegment(sketch, "E3225", {"start": v(30, 8.72) * mm, "end": v(29.88, 8.67) * mm});
            skLineSegment(sketch, "E3226", {"start": v(29.88, 8.67) * mm, "end": v(29.84, 8.66) * mm});
            skLineSegment(sketch, "E3227", {"start": v(29.84, 8.66) * mm, "end": v(29.8, 8.66) * mm});
            skLineSegment(sketch, "E3228", {"start": v(29.8, 8.66) * mm, "end": v(29.75, 8.67) * mm});
            skLineSegment(sketch, "E3229", {"start": v(29.75, 8.67) * mm, "end": v(29.7, 8.68) * mm});
            skLineSegment(sketch, "E3230", {"start": v(29.7, 8.68) * mm, "end": v(29.66, 8.7) * mm});
            skLineSegment(sketch, "E3231", {"start": v(29.66, 8.7) * mm, "end": v(29.63, 8.74) * mm});
            skLineSegment(sketch, "E3232", {"start": v(29.63, 8.74) * mm, "end": v(29.6, 8.78) * mm});
            skLineSegment(sketch, "E3233", {"start": v(29.6, 8.78) * mm, "end": v(29.6, 8.82) * mm});
            skLineSegment(sketch, "E3234", {"start": v(29.6, 8.82) * mm, "end": v(29.58, 8.91) * mm});
            skLineSegment(sketch, "E3235", {"start": v(29.58, 8.91) * mm, "end": v(29.58, 9) * mm});
            skLineSegment(sketch, "E3236", {"start": v(29.58, 9) * mm, "end": v(29.57, 9.07) * mm});
            skLineSegment(sketch, "E3237", {"start": v(29.57, 9.07) * mm, "end": v(29.56, 9.15) * mm});
            skLineSegment(sketch, "E3238", {"start": v(29.56, 9.15) * mm, "end": v(29.56, 9.23) * mm});
            skLineSegment(sketch, "E3239", {"start": v(29.56, 9.23) * mm, "end": v(29.56, 9.3) * mm});
            skLineSegment(sketch, "E3240", {"start": v(29.56, 9.3) * mm, "end": v(29.55, 9.37) * mm});
            skLineSegment(sketch, "E3241", {"start": v(29.55, 9.37) * mm, "end": v(29.55, 9.44) * mm});
            skLineSegment(sketch, "E3242", {"start": v(29.55, 9.44) * mm, "end": v(29.55, 9.5) * mm});
            skLineSegment(sketch, "E3243", {"start": v(29.55, 9.5) * mm, "end": v(29.55, 9.56) * mm});
            skLineSegment(sketch, "E3244", {"start": v(29.55, 9.56) * mm, "end": v(29.55, 9.6) * mm});
            skLineSegment(sketch, "E3245", {"start": v(29.55, 9.6) * mm, "end": v(29.55, 9.62) * mm});
            skLineSegment(sketch, "E3246", {"start": v(29.55, 9.62) * mm, "end": v(29.55, 9.64) * mm});
            skLineSegment(sketch, "E3247", {"start": v(29.55, 9.64) * mm, "end": v(29.55, 9.65) * mm});
            skLineSegment(sketch, "E3248", {"start": v(29.55, 9.65) * mm, "end": v(29.55, 9.65) * mm});
            skLineSegment(sketch, "E3249", {"start": v(29.55, 9.65) * mm, "end": v(29.6, 9.68) * mm});
            skLineSegment(sketch, "E3250", {"start": v(29.6, 9.68) * mm, "end": v(29.66, 9.72) * mm});
            skLineSegment(sketch, "E3251", {"start": v(29.66, 9.72) * mm, "end": v(29.71, 9.75) * mm});
            skLineSegment(sketch, "E3252", {"start": v(29.71, 9.75) * mm, "end": v(29.77, 9.78) * mm});
            skLineSegment(sketch, "E3253", {"start": v(29.77, 9.78) * mm, "end": v(29.82, 9.81) * mm});
            skLineSegment(sketch, "E3254", {"start": v(29.82, 9.81) * mm, "end": v(29.86, 9.83) * mm});
            skLineSegment(sketch, "E3255", {"start": v(29.86, 9.83) * mm, "end": v(29.9, 9.85) * mm});
            skLineSegment(sketch, "E3256", {"start": v(29.9, 9.85) * mm, "end": v(29.94, 9.86) * mm});
            skLineSegment(sketch, "E3257", {"start": v(29.94, 9.86) * mm, "end": v(29.98, 9.87) * mm});
            skLineSegment(sketch, "E3258", {"start": v(29.98, 9.87) * mm, "end": v(30.06, 9.9) * mm});
            skLineSegment(sketch, "E3259", {"start": v(30.06, 9.9) * mm, "end": v(30.16, 9.92) * mm});
            skLineSegment(sketch, "E3260", {"start": v(30.16, 9.92) * mm, "end": v(30.28, 9.96) * mm});
            skLineSegment(sketch, "E3261", {"start": v(30.28, 9.96) * mm, "end": v(30.43, 10) * mm});
            skLineSegment(sketch, "E3262", {"start": v(30.43, 10) * mm, "end": v(30.58, 10.04) * mm});
            skLineSegment(sketch, "E3263", {"start": v(30.58, 10.04) * mm, "end": v(30.75, 10.09) * mm});
            skLineSegment(sketch, "E3264", {"start": v(30.75, 10.09) * mm, "end": v(30.93, 10.13) * mm});
            skLineSegment(sketch, "E3265", {"start": v(30.93, 10.13) * mm, "end": v(30.93, 10.13) * mm});
            skLineSegment(sketch, "E3266", {"start": v(30.93, 10.13) * mm, "end": v(30.93, 10.14) * mm});
            skLineSegment(sketch, "E3267", {"start": v(30.93, 10.14) * mm, "end": v(30.95, 10.14) * mm});
            skLineSegment(sketch, "E3268", {"start": v(30.95, 10.14) * mm, "end": v(30.98, 10.15) * mm});
            skLineSegment(sketch, "E3269", {"start": v(30.98, 10.15) * mm, "end": v(31.03, 10.17) * mm});
            skLineSegment(sketch, "E3270", {"start": v(31.03, 10.17) * mm, "end": v(31.1, 10.2) * mm});
            skLineSegment(sketch, "E3271", {"start": v(31.1, 10.2) * mm, "end": v(31.2, 10.25) * mm});
            skLineSegment(sketch, "E3272", {"start": v(31.2, 10.25) * mm, "end": v(31.34, 10.3) * mm});
            skLineSegment(sketch, "E3273", {"start": v(31.34, 10.3) * mm, "end": v(31.37, 10.32) * mm});
            skLineSegment(sketch, "E3274", {"start": v(31.37, 10.32) * mm, "end": v(31.4, 10.33) * mm});
            skLineSegment(sketch, "E3275", {"start": v(31.4, 10.33) * mm, "end": v(31.43, 10.34) * mm});
            skLineSegment(sketch, "E3276", {"start": v(31.43, 10.34) * mm, "end": v(31.46, 10.35) * mm});
            skLineSegment(sketch, "E3277", {"start": v(31.46, 10.35) * mm, "end": v(31.49, 10.36) * mm});
            skLineSegment(sketch, "E3278", {"start": v(31.49, 10.36) * mm, "end": v(31.52, 10.37) * mm});
            skLineSegment(sketch, "E3279", {"start": v(31.52, 10.37) * mm, "end": v(31.55, 10.38) * mm});
            skLineSegment(sketch, "E3280", {"start": v(31.55, 10.38) * mm, "end": v(31.58, 10.4) * mm});
            skLineSegment(sketch, "E3281", {"start": v(31.58, 10.4) * mm, "end": v(31.72, 10.45) * mm});
            skLineSegment(sketch, "E3282", {"start": v(31.72, 10.45) * mm, "end": v(31.85, 10.5) * mm});
            skLineSegment(sketch, "E3283", {"start": v(31.85, 10.5) * mm, "end": v(32, 10.57) * mm});
            skLineSegment(sketch, "E3284", {"start": v(32, 10.57) * mm, "end": v(32.13, 10.64) * mm});
            skLineSegment(sketch, "E3285", {"start": v(32.13, 10.64) * mm, "end": v(32.26, 10.71) * mm});
            skLineSegment(sketch, "E3286", {"start": v(32.26, 10.71) * mm, "end": v(32.38, 10.8) * mm});
            skLineSegment(sketch, "E3287", {"start": v(32.38, 10.8) * mm, "end": v(32.5, 10.9) * mm});
            skLineSegment(sketch, "E3288", {"start": v(32.5, 10.9) * mm, "end": v(32.61, 11.02) * mm});
            skLineSegment(sketch, "E3289", {"start": v(32.61, 11.02) * mm, "end": v(32.65, 11.07) * mm});
            skLineSegment(sketch, "E3290", {"start": v(32.65, 11.07) * mm, "end": v(32.7, 11.12) * mm});
            skLineSegment(sketch, "E3291", {"start": v(32.7, 11.12) * mm, "end": v(32.73, 11.16) * mm});
            skLineSegment(sketch, "E3292", {"start": v(32.73, 11.16) * mm, "end": v(32.77, 11.2) * mm});
            skLineSegment(sketch, "E3293", {"start": v(32.77, 11.2) * mm, "end": v(32.82, 11.25) * mm});
            skLineSegment(sketch, "E3294", {"start": v(32.82, 11.25) * mm, "end": v(32.86, 11.3) * mm});
            skLineSegment(sketch, "E3295", {"start": v(32.86, 11.3) * mm, "end": v(32.9, 11.34) * mm});
            skLineSegment(sketch, "E3296", {"start": v(32.9, 11.34) * mm, "end": v(32.94, 11.38) * mm});
            skLineSegment(sketch, "E3297", {"start": v(32.94, 11.38) * mm, "end": v(32.98, 11.42) * mm});
            skLineSegment(sketch, "E3298", {"start": v(32.98, 11.42) * mm, "end": v(33.02, 11.46) * mm});
            skLineSegment(sketch, "E3299", {"start": v(33.02, 11.46) * mm, "end": v(33.05, 11.5) * mm});
            skLineSegment(sketch, "E3300", {"start": v(33.05, 11.5) * mm, "end": v(33.09, 11.54) * mm});
            skLineSegment(sketch, "E3301", {"start": v(33.09, 11.54) * mm, "end": v(33.13, 11.58) * mm});
            skLineSegment(sketch, "E3302", {"start": v(33.13, 11.58) * mm, "end": v(33.16, 11.62) * mm});
            skLineSegment(sketch, "E3303", {"start": v(33.16, 11.62) * mm, "end": v(33.2, 11.66) * mm});
            skLineSegment(sketch, "E3304", {"start": v(33.2, 11.66) * mm, "end": v(33.23, 11.7) * mm});
            skLineSegment(sketch, "E3305", {"start": v(33.23, 11.7) * mm, "end": v(33.28, 11.75) * mm});
            skLineSegment(sketch, "E3306", {"start": v(33.28, 11.75) * mm, "end": v(33.31, 11.8) * mm});
            skLineSegment(sketch, "E3307", {"start": v(33.31, 11.8) * mm, "end": v(33.35, 11.84) * mm});
            skLineSegment(sketch, "E3308", {"start": v(33.35, 11.84) * mm, "end": v(33.4, 11.9) * mm});
            skLineSegment(sketch, "E3309", {"start": v(33.4, 11.9) * mm, "end": v(33.43, 11.94) * mm});
            skLineSegment(sketch, "E3310", {"start": v(33.43, 11.94) * mm, "end": v(33.47, 12) * mm});
            skLineSegment(sketch, "E3311", {"start": v(33.47, 12) * mm, "end": v(33.5, 12.04) * mm});
            skLineSegment(sketch, "E3312", {"start": v(33.5, 12.04) * mm, "end": v(33.55, 12.1) * mm});
            skLineSegment(sketch, "E3313", {"start": v(33.55, 12.1) * mm, "end": v(33.56, 12.12) * mm});
            skLineSegment(sketch, "E3314", {"start": v(33.56, 12.12) * mm, "end": v(33.57, 12.13) * mm});
            skLineSegment(sketch, "E3315", {"start": v(33.57, 12.13) * mm, "end": v(33.58, 12.14) * mm});
            skLineSegment(sketch, "E3316", {"start": v(33.58, 12.14) * mm, "end": v(33.59, 12.15) * mm});
            skLineSegment(sketch, "E3317", {"start": v(33.59, 12.15) * mm, "end": v(33.59, 12.15) * mm});
            skLineSegment(sketch, "E3318", {"start": v(33.59, 12.15) * mm, "end": v(33.6, 12.16) * mm});
            skLineSegment(sketch, "E3319", {"start": v(33.6, 12.16) * mm, "end": v(33.6, 12.16) * mm});
            skLineSegment(sketch, "E3320", {"start": v(33.6, 12.16) * mm, "end": v(33.61, 12.18) * mm});
            skLineSegment(sketch, "E3321", {"start": v(33.61, 12.18) * mm, "end": v(33.63, 12.21) * mm});
            skLineSegment(sketch, "E3322", {"start": v(33.63, 12.21) * mm, "end": v(33.66, 12.24) * mm});
            skLineSegment(sketch, "E3323", {"start": v(33.66, 12.24) * mm, "end": v(33.68, 12.27) * mm});
            skLineSegment(sketch, "E3324", {"start": v(33.68, 12.27) * mm, "end": v(33.7, 12.3) * mm});
            skLineSegment(sketch, "E3325", {"start": v(33.7, 12.3) * mm, "end": v(33.72, 12.32) * mm});
            skLineSegment(sketch, "E3326", {"start": v(33.72, 12.32) * mm, "end": v(33.73, 12.34) * mm});
            skLineSegment(sketch, "E3327", {"start": v(33.73, 12.34) * mm, "end": v(33.74, 12.36) * mm});
            skLineSegment(sketch, "E3328", {"start": v(33.74, 12.36) * mm, "end": v(33.75, 12.37) * mm});
            skLineSegment(sketch, "E3329", {"start": v(33.75, 12.37) * mm, "end": v(33.74, 12.39) * mm});
            skLineSegment(sketch, "E3330", {"start": v(33.74, 12.39) * mm, "end": v(33.73, 12.4) * mm});
            skLineSegment(sketch, "E3331", {"start": v(33.73, 12.4) * mm, "end": v(33.7, 12.41) * mm});
            skLineSegment(sketch, "E3332", {"start": v(33.7, 12.41) * mm, "end": v(33.66, 12.42) * mm});
            skLineSegment(sketch, "E3333", {"start": v(33.66, 12.42) * mm, "end": v(33.62, 12.43) * mm});
            skLineSegment(sketch, "E3334", {"start": v(33.62, 12.43) * mm, "end": v(33.57, 12.44) * mm});
            skLineSegment(sketch, "E3335", {"start": v(33.57, 12.44) * mm, "end": v(33.51, 12.44) * mm});
            skLineSegment(sketch, "E3336", {"start": v(33.51, 12.44) * mm, "end": v(33.44, 12.44) * mm});
            skLineSegment(sketch, "E3337", {"start": v(33.44, 12.44) * mm, "end": v(33.36, 12.45) * mm});
            skLineSegment(sketch, "E3338", {"start": v(33.36, 12.45) * mm, "end": v(33.27, 12.45) * mm});
            skLineSegment(sketch, "E3339", {"start": v(33.27, 12.45) * mm, "end": v(33.17, 12.45) * mm});
            skLineSegment(sketch, "E3340", {"start": v(33.17, 12.45) * mm, "end": v(33.06, 12.46) * mm});
            skLineSegment(sketch, "E3341", {"start": v(33.06, 12.46) * mm, "end": v(32.95, 12.46) * mm});
            skLineSegment(sketch, "E3342", {"start": v(32.95, 12.46) * mm, "end": v(32.84, 12.46) * mm});
            skLineSegment(sketch, "E3343", {"start": v(32.84, 12.46) * mm, "end": v(32.74, 12.47) * mm});
            skLineSegment(sketch, "E3344", {"start": v(32.74, 12.47) * mm, "end": v(32.74, 12.47) * mm});
            skLineSegment(sketch, "E3345", {"start": v(32.74, 12.47) * mm, "end": v(32.73, 12.47) * mm});
            skLineSegment(sketch, "E3346", {"start": v(32.73, 12.47) * mm, "end": v(32.72, 12.47) * mm});
            skLineSegment(sketch, "E3347", {"start": v(32.72, 12.47) * mm, "end": v(32.7, 12.47) * mm});
            skLineSegment(sketch, "E3348", {"start": v(32.7, 12.47) * mm, "end": v(32.68, 12.47) * mm});
            skLineSegment(sketch, "E3349", {"start": v(32.68, 12.47) * mm, "end": v(32.64, 12.47) * mm});
            skLineSegment(sketch, "E3350", {"start": v(32.64, 12.47) * mm, "end": v(32.58, 12.48) * mm});
            skLineSegment(sketch, "E3351", {"start": v(32.58, 12.48) * mm, "end": v(32.5, 12.48) * mm});
            skLineSegment(sketch, "E3352", {"start": v(32.5, 12.48) * mm, "end": v(32.49, 12.48) * mm});
            skLineSegment(sketch, "E3353", {"start": v(32.49, 12.48) * mm, "end": v(32.48, 12.48) * mm});
            skLineSegment(sketch, "E3354", {"start": v(32.48, 12.48) * mm, "end": v(32.47, 12.48) * mm});
            skLineSegment(sketch, "E3355", {"start": v(32.47, 12.48) * mm, "end": v(32.46, 12.49) * mm});
            skLineSegment(sketch, "E3356", {"start": v(32.46, 12.49) * mm, "end": v(32.45, 12.5) * mm});
            skLineSegment(sketch, "E3357", {"start": v(32.45, 12.5) * mm, "end": v(32.43, 12.5) * mm});
            skLineSegment(sketch, "E3358", {"start": v(32.43, 12.5) * mm, "end": v(32.42, 12.5) * mm});
            skLineSegment(sketch, "E3359", {"start": v(32.42, 12.5) * mm, "end": v(32.41, 12.5) * mm});
            skLineSegment(sketch, "E3360", {"start": v(32.41, 12.5) * mm, "end": v(32.4, 12.5) * mm});
            skLineSegment(sketch, "E3361", {"start": v(32.4, 12.5) * mm, "end": v(32.39, 12.51) * mm});
            skLineSegment(sketch, "E3362", {"start": v(32.39, 12.51) * mm, "end": v(32.37, 12.52) * mm});
            skLineSegment(sketch, "E3363", {"start": v(32.37, 12.52) * mm, "end": v(32.36, 12.52) * mm});
            skLineSegment(sketch, "E3364", {"start": v(32.36, 12.52) * mm, "end": v(32.34, 12.53) * mm});
            skLineSegment(sketch, "E3365", {"start": v(32.34, 12.53) * mm, "end": v(32.33, 12.53) * mm});
            skLineSegment(sketch, "E3366", {"start": v(32.33, 12.53) * mm, "end": v(32.31, 12.54) * mm});
            skLineSegment(sketch, "E3367", {"start": v(32.31, 12.54) * mm, "end": v(32.3, 12.54) * mm});
            skLineSegment(sketch, "E3368", {"start": v(32.3, 12.54) * mm, "end": v(32.26, 12.54) * mm});
            skLineSegment(sketch, "E3369", {"start": v(32.26, 12.54) * mm, "end": v(32.23, 12.55) * mm});
            skLineSegment(sketch, "E3370", {"start": v(32.23, 12.55) * mm, "end": v(32.2, 12.56) * mm});
            skLineSegment(sketch, "E3371", {"start": v(32.2, 12.56) * mm, "end": v(32.15, 12.56) * mm});
            skLineSegment(sketch, "E3372", {"start": v(32.15, 12.56) * mm, "end": v(32.12, 12.57) * mm});
            skLineSegment(sketch, "E3373", {"start": v(32.12, 12.57) * mm, "end": v(32.08, 12.57) * mm});
            skLineSegment(sketch, "E3374", {"start": v(32.08, 12.57) * mm, "end": v(32.05, 12.58) * mm});
            skLineSegment(sketch, "E3375", {"start": v(32.05, 12.58) * mm, "end": v(32, 12.58) * mm});
            skLineSegment(sketch, "E3376", {"start": v(32, 12.58) * mm, "end": v(31.96, 12.59) * mm});
            skLineSegment(sketch, "E3377", {"start": v(31.96, 12.59) * mm, "end": v(31.9, 12.6) * mm});
            skLineSegment(sketch, "E3378", {"start": v(31.9, 12.6) * mm, "end": v(31.85, 12.6) * mm});
            skLineSegment(sketch, "E3379", {"start": v(31.85, 12.6) * mm, "end": v(31.8, 12.61) * mm});
            skLineSegment(sketch, "E3380", {"start": v(31.8, 12.61) * mm, "end": v(31.74, 12.62) * mm});
            skLineSegment(sketch, "E3381", {"start": v(31.74, 12.62) * mm, "end": v(31.69, 12.63) * mm});
            skLineSegment(sketch, "E3382", {"start": v(31.69, 12.63) * mm, "end": v(31.63, 12.64) * mm});
            skLineSegment(sketch, "E3383", {"start": v(31.63, 12.64) * mm, "end": v(31.58, 12.65) * mm});
            skLineSegment(sketch, "E3384", {"start": v(31.58, 12.65) * mm, "end": v(31.42, 12.68) * mm});
            skLineSegment(sketch, "E3385", {"start": v(31.42, 12.68) * mm, "end": v(31.26, 12.7) * mm});
            skLineSegment(sketch, "E3386", {"start": v(31.26, 12.7) * mm, "end": v(31.1, 12.7) * mm});
            skLineSegment(sketch, "E3387", {"start": v(31.1, 12.7) * mm, "end": v(30.93, 12.7) * mm});
            skLineSegment(sketch, "E3388", {"start": v(30.93, 12.7) * mm, "end": v(30.76, 12.68) * mm});
            skLineSegment(sketch, "E3389", {"start": v(30.76, 12.68) * mm, "end": v(30.59, 12.65) * mm});
            skLineSegment(sketch, "E3390", {"start": v(30.59, 12.65) * mm, "end": v(30.41, 12.62) * mm});
            skLineSegment(sketch, "E3391", {"start": v(30.41, 12.62) * mm, "end": v(30.24, 12.57) * mm});
            skLineSegment(sketch, "E3392", {"start": v(30.24, 12.57) * mm, "end": v(30.16, 12.54) * mm});
            skLineSegment(sketch, "E3393", {"start": v(30.16, 12.54) * mm, "end": v(30.09, 12.52) * mm});
            skLineSegment(sketch, "E3394", {"start": v(30.09, 12.52) * mm, "end": v(30.01, 12.48) * mm});
            skLineSegment(sketch, "E3395", {"start": v(30.01, 12.48) * mm, "end": v(29.94, 12.45) * mm});
            skLineSegment(sketch, "E3396", {"start": v(29.94, 12.45) * mm, "end": v(29.87, 12.4) * mm});
            skLineSegment(sketch, "E3397", {"start": v(29.87, 12.4) * mm, "end": v(29.8, 12.37) * mm});
            skLineSegment(sketch, "E3398", {"start": v(29.8, 12.37) * mm, "end": v(29.74, 12.33) * mm});
            skLineSegment(sketch, "E3399", {"start": v(29.74, 12.33) * mm, "end": v(29.67, 12.29) * mm});
            skLineSegment(sketch, "E3400", {"start": v(29.67, 12.29) * mm, "end": v(29.64, 12.27) * mm});
            skLineSegment(sketch, "E3401", {"start": v(29.64, 12.27) * mm, "end": v(29.62, 12.26) * mm});
            skLineSegment(sketch, "E3402", {"start": v(29.62, 12.26) * mm, "end": v(29.6, 12.24) * mm});
            skLineSegment(sketch, "E3403", {"start": v(29.6, 12.24) * mm, "end": v(29.57, 12.23) * mm});
            skLineSegment(sketch, "E3404", {"start": v(29.57, 12.23) * mm, "end": v(29.55, 12.22) * mm});
            skLineSegment(sketch, "E3405", {"start": v(29.55, 12.22) * mm, "end": v(29.52, 12.2) * mm});
            skLineSegment(sketch, "E3406", {"start": v(29.52, 12.2) * mm, "end": v(29.5, 12.19) * mm});
            skLineSegment(sketch, "E3407", {"start": v(29.5, 12.19) * mm, "end": v(29.47, 12.17) * mm});
            skLineSegment(sketch, "E3408", {"start": v(29.47, 12.17) * mm, "end": v(29.45, 12.16) * mm});
            skLineSegment(sketch, "E3409", {"start": v(29.45, 12.16) * mm, "end": v(29.43, 12.15) * mm});
            skLineSegment(sketch, "E3410", {"start": v(29.43, 12.15) * mm, "end": v(29.41, 12.14) * mm});
            skLineSegment(sketch, "E3411", {"start": v(29.41, 12.14) * mm, "end": v(29.39, 12.12) * mm});
            skLineSegment(sketch, "E3412", {"start": v(29.39, 12.12) * mm, "end": v(29.37, 12.1) * mm});
            skLineSegment(sketch, "E3413", {"start": v(29.37, 12.1) * mm, "end": v(29.35, 12.1) * mm});
            skLineSegment(sketch, "E3414", {"start": v(29.35, 12.1) * mm, "end": v(29.33, 12.08) * mm});
            skLineSegment(sketch, "E3415", {"start": v(29.33, 12.08) * mm, "end": v(29.3, 12.07) * mm});
            skLineSegment(sketch, "E3416", {"start": v(29.3, 12.07) * mm, "end": v(29.27, 12.04) * mm});
            skLineSegment(sketch, "E3417", {"start": v(29.27, 12.04) * mm, "end": v(29.24, 12.02) * mm});
            skLineSegment(sketch, "E3418", {"start": v(29.24, 12.02) * mm, "end": v(29.2, 12) * mm});
            skLineSegment(sketch, "E3419", {"start": v(29.2, 12) * mm, "end": v(29.18, 11.98) * mm});
            skLineSegment(sketch, "E3420", {"start": v(29.18, 11.98) * mm, "end": v(29.14, 11.96) * mm});
            skLineSegment(sketch, "E3421", {"start": v(29.14, 11.96) * mm, "end": v(29.11, 11.95) * mm});
            skLineSegment(sketch, "E3422", {"start": v(29.11, 11.95) * mm, "end": v(29.08, 11.93) * mm});
            skLineSegment(sketch, "E3423", {"start": v(29.08, 11.93) * mm, "end": v(29.05, 11.92) * mm});
            skLineSegment(sketch, "E3424", {"start": v(29.05, 11.92) * mm, "end": v(29.04, 11.92) * mm});
            skLineSegment(sketch, "E3425", {"start": v(29.04, 11.92) * mm, "end": v(29.03, 11.91) * mm});
            skLineSegment(sketch, "E3426", {"start": v(29.03, 11.91) * mm, "end": v(29.02, 11.91) * mm});
            skLineSegment(sketch, "E3427", {"start": v(29.02, 11.91) * mm, "end": v(29, 11.9) * mm});
            skLineSegment(sketch, "E3428", {"start": v(29, 11.9) * mm, "end": v(29, 11.9) * mm});
            skLineSegment(sketch, "E3429", {"start": v(29, 11.9) * mm, "end": v(28.98, 11.9) * mm});
            skLineSegment(sketch, "E3430", {"start": v(28.98, 11.9) * mm, "end": v(28.97, 11.9) * mm});
            skLineSegment(sketch, "E3431", {"start": v(28.97, 11.9) * mm, "end": v(28.95, 11.9) * mm});
            skLineSegment(sketch, "E3432", {"start": v(28.95, 11.9) * mm, "end": v(28.93, 11.9) * mm});
            skLineSegment(sketch, "E3433", {"start": v(28.93, 11.9) * mm, "end": v(28.9, 11.9) * mm});
            skLineSegment(sketch, "E3434", {"start": v(28.9, 11.9) * mm, "end": v(28.9, 11.9) * mm});
            skLineSegment(sketch, "E3435", {"start": v(28.9, 11.9) * mm, "end": v(28.89, 11.9) * mm});
            skLineSegment(sketch, "E3436", {"start": v(28.89, 11.9) * mm, "end": v(28.88, 11.9) * mm});
            skLineSegment(sketch, "E3437", {"start": v(28.88, 11.9) * mm, "end": v(28.88, 11.9) * mm});
            skLineSegment(sketch, "E3438", {"start": v(28.88, 11.9) * mm, "end": v(28.86, 11.92) * mm});
            skLineSegment(sketch, "E3439", {"start": v(28.86, 11.92) * mm, "end": v(28.84, 11.94) * mm});
            skLineSegment(sketch, "E3440", {"start": v(28.84, 11.94) * mm, "end": v(28.81, 11.97) * mm});
            skLineSegment(sketch, "E3441", {"start": v(28.81, 11.97) * mm, "end": v(28.78, 12.01) * mm});
            skLineSegment(sketch, "E3442", {"start": v(28.78, 12.01) * mm, "end": v(28.75, 12.06) * mm});
            skLineSegment(sketch, "E3443", {"start": v(28.75, 12.06) * mm, "end": v(28.71, 12.12) * mm});
            skLineSegment(sketch, "E3444", {"start": v(28.71, 12.12) * mm, "end": v(28.67, 12.18) * mm});
            skLineSegment(sketch, "E3445", {"start": v(28.67, 12.18) * mm, "end": v(28.63, 12.24) * mm});
            skLineSegment(sketch, "E3446", {"start": v(28.63, 12.24) * mm, "end": v(28.63, 12.24) * mm});
            skLineSegment(sketch, "E3447", {"start": v(28.63, 12.24) * mm, "end": v(28.63, 12.25) * mm});
            skLineSegment(sketch, "E3448", {"start": v(28.63, 12.25) * mm, "end": v(28.62, 12.26) * mm});
            skLineSegment(sketch, "E3449", {"start": v(28.62, 12.26) * mm, "end": v(28.61, 12.28) * mm});
            skLineSegment(sketch, "E3450", {"start": v(28.61, 12.28) * mm, "end": v(28.6, 12.3) * mm});
            skLineSegment(sketch, "E3451", {"start": v(28.6, 12.3) * mm, "end": v(28.58, 12.34) * mm});
            skLineSegment(sketch, "E3452", {"start": v(28.58, 12.34) * mm, "end": v(28.55, 12.4) * mm});
            skLineSegment(sketch, "E3453", {"start": v(28.55, 12.4) * mm, "end": v(28.53, 12.44) * mm});
            skLineSegment(sketch, "E3454", {"start": v(28.53, 12.44) * mm, "end": v(28.5, 12.48) * mm});
            skLineSegment(sketch, "E3455", {"start": v(28.5, 12.48) * mm, "end": v(28.48, 12.52) * mm});
            skLineSegment(sketch, "E3456", {"start": v(28.48, 12.52) * mm, "end": v(28.46, 12.56) * mm});
            skLineSegment(sketch, "E3457", {"start": v(28.46, 12.56) * mm, "end": v(28.44, 12.6) * mm});
            skLineSegment(sketch, "E3458", {"start": v(28.44, 12.6) * mm, "end": v(28.41, 12.64) * mm});
            skLineSegment(sketch, "E3459", {"start": v(28.41, 12.64) * mm, "end": v(28.4, 12.69) * mm});
            skLineSegment(sketch, "E3460", {"start": v(28.4, 12.69) * mm, "end": v(28.37, 12.73) * mm});
            skLineSegment(sketch, "E3461", {"start": v(28.37, 12.73) * mm, "end": v(28.36, 12.73) * mm});
            skLineSegment(sketch, "E3462", {"start": v(28.36, 12.73) * mm, "end": v(28.36, 12.74) * mm});
            skLineSegment(sketch, "E3463", {"start": v(28.36, 12.74) * mm, "end": v(28.36, 12.74) * mm});
            skLineSegment(sketch, "E3464", {"start": v(28.36, 12.74) * mm, "end": v(28.36, 12.75) * mm});
            skLineSegment(sketch, "E3465", {"start": v(28.36, 12.75) * mm, "end": v(28.35, 12.75) * mm});
            skLineSegment(sketch, "E3466", {"start": v(28.35, 12.75) * mm, "end": v(28.35, 12.75) * mm});
            skLineSegment(sketch, "E3467", {"start": v(28.35, 12.75) * mm, "end": v(28.35, 12.76) * mm});
            skLineSegment(sketch, "E3468", {"start": v(28.35, 12.76) * mm, "end": v(28.35, 12.76) * mm});
            skLineSegment(sketch, "E3469", {"start": v(28.35, 12.76) * mm, "end": v(28.35, 12.77) * mm});
            skLineSegment(sketch, "E3470", {"start": v(28.35, 12.77) * mm, "end": v(28.36, 12.77) * mm});
            skLineSegment(sketch, "E3471", {"start": v(28.36, 12.77) * mm, "end": v(28.36, 12.78) * mm});
            skLineSegment(sketch, "E3472", {"start": v(28.36, 12.78) * mm, "end": v(28.37, 12.78) * mm});
            skLineSegment(sketch, "E3473", {"start": v(28.37, 12.78) * mm, "end": v(28.38, 12.8) * mm});
            skLineSegment(sketch, "E3474", {"start": v(28.38, 12.8) * mm, "end": v(28.39, 12.8) * mm});
            skLineSegment(sketch, "E3475", {"start": v(28.39, 12.8) * mm, "end": v(28.4, 12.8) * mm});
            skLineSegment(sketch, "E3476", {"start": v(28.4, 12.8) * mm, "end": v(28.4, 12.81) * mm});
            skLineSegment(sketch, "E3477", {"start": v(28.4, 12.81) * mm, "end": v(28.42, 12.83) * mm});
            skLineSegment(sketch, "E3478", {"start": v(28.42, 12.83) * mm, "end": v(28.44, 12.84) * mm});
            skLineSegment(sketch, "E3479", {"start": v(28.44, 12.84) * mm, "end": v(28.47, 12.87) * mm});
            skLineSegment(sketch, "E3480", {"start": v(28.47, 12.87) * mm, "end": v(28.5, 12.9) * mm});
            skLineSegment(sketch, "E3481", {"start": v(28.5, 12.9) * mm, "end": v(28.54, 12.93) * mm});
            skLineSegment(sketch, "E3482", {"start": v(28.54, 12.93) * mm, "end": v(28.58, 12.96) * mm});
            skLineSegment(sketch, "E3483", {"start": v(28.58, 12.96) * mm, "end": v(28.62, 13) * mm});
            skLineSegment(sketch, "E3484", {"start": v(28.62, 13) * mm, "end": v(28.66, 13.03) * mm});
            skLineSegment(sketch, "E3485", {"start": v(28.66, 13.03) * mm, "end": v(28.66, 13.03) * mm});
            skLineSegment(sketch, "E3486", {"start": v(28.66, 13.03) * mm, "end": v(28.67, 13.04) * mm});
            skLineSegment(sketch, "E3487", {"start": v(28.67, 13.04) * mm, "end": v(28.67, 13.04) * mm});
            skLineSegment(sketch, "E3488", {"start": v(28.67, 13.04) * mm, "end": v(28.69, 13.05) * mm});
            skLineSegment(sketch, "E3489", {"start": v(28.69, 13.05) * mm, "end": v(28.7, 13.06) * mm});
            skLineSegment(sketch, "E3490", {"start": v(28.7, 13.06) * mm, "end": v(28.74, 13.08) * mm});
            skLineSegment(sketch, "E3491", {"start": v(28.74, 13.08) * mm, "end": v(28.77, 13.1) * mm});
            skLineSegment(sketch, "E3492", {"start": v(28.77, 13.1) * mm, "end": v(28.91, 13.2) * mm});
            skLineSegment(sketch, "E3493", {"start": v(28.91, 13.2) * mm, "end": v(29.01, 13.27) * mm});
            skLineSegment(sketch, "E3494", {"start": v(29.01, 13.27) * mm, "end": v(29.09, 13.32) * mm});
            skLineSegment(sketch, "E3495", {"start": v(29.09, 13.32) * mm, "end": v(29.14, 13.36) * mm});
            skLineSegment(sketch, "E3496", {"start": v(29.14, 13.36) * mm, "end": v(29.17, 13.38) * mm});
            skLineSegment(sketch, "E3497", {"start": v(29.17, 13.38) * mm, "end": v(29.18, 13.39) * mm});
            skLineSegment(sketch, "E3498", {"start": v(29.18, 13.39) * mm, "end": v(29.2, 13.4) * mm});
            skLineSegment(sketch, "E3499", {"start": v(29.2, 13.4) * mm, "end": v(29.2, 13.4) * mm});
            skLineSegment(sketch, "E3500", {"start": v(29.2, 13.4) * mm, "end": v(29.32, 13.55) * mm});
            skLineSegment(sketch, "E3501", {"start": v(29.32, 13.55) * mm, "end": v(29.44, 13.7) * mm});
            skLineSegment(sketch, "E3502", {"start": v(29.44, 13.7) * mm, "end": v(29.54, 13.83) * mm});
            skLineSegment(sketch, "E3503", {"start": v(29.54, 13.83) * mm, "end": v(29.64, 13.95) * mm});
            skLineSegment(sketch, "E3504", {"start": v(29.64, 13.95) * mm, "end": v(29.72, 14.05) * mm});
            skLineSegment(sketch, "E3505", {"start": v(29.72, 14.05) * mm, "end": v(29.79, 14.13) * mm});
            skLineSegment(sketch, "E3506", {"start": v(29.79, 14.13) * mm, "end": v(29.83, 14.18) * mm});
            skLineSegment(sketch, "E3507", {"start": v(29.83, 14.18) * mm, "end": v(29.85, 14.2) * mm});
            skLineSegment(sketch, "E3508", {"start": v(29.85, 14.2) * mm, "end": v(29.86, 14.22) * mm});
            skLineSegment(sketch, "E3509", {"start": v(29.86, 14.22) * mm, "end": v(29.87, 14.24) * mm});
            skLineSegment(sketch, "E3510", {"start": v(29.87, 14.24) * mm, "end": v(29.9, 14.26) * mm});
            skLineSegment(sketch, "E3511", {"start": v(29.9, 14.26) * mm, "end": v(29.91, 14.3) * mm});
            skLineSegment(sketch, "E3512", {"start": v(29.91, 14.3) * mm, "end": v(29.93, 14.32) * mm});
            skLineSegment(sketch, "E3513", {"start": v(29.93, 14.32) * mm, "end": v(29.96, 14.36) * mm});
            skLineSegment(sketch, "E3514", {"start": v(29.96, 14.36) * mm, "end": v(29.98, 14.4) * mm});
            skLineSegment(sketch, "E3515", {"start": v(29.98, 14.4) * mm, "end": v(30, 14.44) * mm});
            skLineSegment(sketch, "E3516", {"start": v(30, 14.44) * mm, "end": v(30.04, 14.48) * mm});
            skLineSegment(sketch, "E3517", {"start": v(30.04, 14.48) * mm, "end": v(30.07, 14.54) * mm});
            skLineSegment(sketch, "E3518", {"start": v(30.07, 14.54) * mm, "end": v(30.1, 14.6) * mm});
            skLineSegment(sketch, "E3519", {"start": v(30.1, 14.6) * mm, "end": v(30.14, 14.67) * mm});
            skLineSegment(sketch, "E3520", {"start": v(30.14, 14.67) * mm, "end": v(30.18, 14.73) * mm});
            skLineSegment(sketch, "E3521", {"start": v(30.18, 14.73) * mm, "end": v(30.2, 14.78) * mm});
            skLineSegment(sketch, "E3522", {"start": v(30.2, 14.78) * mm, "end": v(30.22, 14.81) * mm});
            skLineSegment(sketch, "E3523", {"start": v(30.22, 14.81) * mm, "end": v(30.23, 14.83) * mm});
            skLineSegment(sketch, "E3524", {"start": v(30.23, 14.83) * mm, "end": v(30.24, 14.84) * mm});
            skLineSegment(sketch, "E3525", {"start": v(30.24, 14.84) * mm, "end": v(30.25, 14.86) * mm});
            skLineSegment(sketch, "E3526", {"start": v(30.25, 14.86) * mm, "end": v(30.26, 14.89) * mm});
            skLineSegment(sketch, "E3527", {"start": v(30.26, 14.89) * mm, "end": v(30.27, 14.92) * mm});
            skLineSegment(sketch, "E3528", {"start": v(30.27, 14.92) * mm, "end": v(30.29, 14.96) * mm});
            skLineSegment(sketch, "E3529", {"start": v(30.29, 14.96) * mm, "end": v(30.3, 15.01) * mm});
            skLineSegment(sketch, "E3530", {"start": v(30.3, 15.01) * mm, "end": v(30.33, 15.07) * mm});
            skLineSegment(sketch, "E3531", {"start": v(30.33, 15.07) * mm, "end": v(30.35, 15.12) * mm});
            skLineSegment(sketch, "E3532", {"start": v(30.35, 15.12) * mm, "end": v(30.35, 15.12) * mm});
            skLineSegment(sketch, "E3533", {"start": v(30.35, 15.12) * mm, "end": v(30.36, 15.12) * mm});
            skLineSegment(sketch, "E3534", {"start": v(30.36, 15.12) * mm, "end": v(30.36, 15.13) * mm});
            skLineSegment(sketch, "E3535", {"start": v(30.36, 15.13) * mm, "end": v(30.36, 15.14) * mm});
            skLineSegment(sketch, "E3536", {"start": v(30.36, 15.14) * mm, "end": v(30.36, 15.16) * mm});
            skLineSegment(sketch, "E3537", {"start": v(30.36, 15.16) * mm, "end": v(30.37, 15.18) * mm});
            skLineSegment(sketch, "E3538", {"start": v(30.37, 15.18) * mm, "end": v(30.37, 15.22) * mm});
            skLineSegment(sketch, "E3539", {"start": v(30.37, 15.22) * mm, "end": v(30.38, 15.27) * mm});
            skLineSegment(sketch, "E3540", {"start": v(30.38, 15.27) * mm, "end": v(30.39, 15.31) * mm});
            skLineSegment(sketch, "E3541", {"start": v(30.39, 15.31) * mm, "end": v(30.4, 15.35) * mm});
            skLineSegment(sketch, "E3542", {"start": v(30.4, 15.35) * mm, "end": v(30.4, 15.4) * mm});
            skLineSegment(sketch, "E3543", {"start": v(30.4, 15.4) * mm, "end": v(30.4, 15.44) * mm});
            skLineSegment(sketch, "E3544", {"start": v(30.4, 15.44) * mm, "end": v(30.41, 15.49) * mm});
            skLineSegment(sketch, "E3545", {"start": v(30.41, 15.49) * mm, "end": v(30.42, 15.53) * mm});
            skLineSegment(sketch, "E3546", {"start": v(30.42, 15.53) * mm, "end": v(30.42, 15.58) * mm});
            skLineSegment(sketch, "E3547", {"start": v(30.42, 15.58) * mm, "end": v(30.43, 15.62) * mm});
            skLineSegment(sketch, "E3548", {"start": v(30.43, 15.62) * mm, "end": v(30.44, 15.68) * mm});
            skLineSegment(sketch, "E3549", {"start": v(30.44, 15.68) * mm, "end": v(30.44, 15.74) * mm});
            skLineSegment(sketch, "E3550", {"start": v(30.44, 15.74) * mm, "end": v(30.45, 15.8) * mm});
            skLineSegment(sketch, "E3551", {"start": v(30.45, 15.8) * mm, "end": v(30.46, 15.85) * mm});
            skLineSegment(sketch, "E3552", {"start": v(30.46, 15.85) * mm, "end": v(30.47, 15.91) * mm});
            skLineSegment(sketch, "E3553", {"start": v(30.47, 15.91) * mm, "end": v(30.48, 15.97) * mm});
            skLineSegment(sketch, "E3554", {"start": v(30.48, 15.97) * mm, "end": v(30.49, 16.03) * mm});
            skLineSegment(sketch, "E3555", {"start": v(30.49, 16.03) * mm, "end": v(30.5, 16.08) * mm});
            skLineSegment(sketch, "E3556", {"start": v(30.5, 16.08) * mm, "end": v(30.5, 16.12) * mm});
            skLineSegment(sketch, "E3557", {"start": v(30.5, 16.12) * mm, "end": v(30.52, 16.17) * mm});
            skLineSegment(sketch, "E3558", {"start": v(30.52, 16.17) * mm, "end": v(30.52, 16.22) * mm});
            skLineSegment(sketch, "E3559", {"start": v(30.52, 16.22) * mm, "end": v(30.52, 16.27) * mm});
            skLineSegment(sketch, "E3560", {"start": v(30.52, 16.27) * mm, "end": v(30.51, 16.33) * mm});
            skLineSegment(sketch, "E3561", {"start": v(30.51, 16.33) * mm, "end": v(30.5, 16.38) * mm});
            skLineSegment(sketch, "E3562", {"start": v(30.5, 16.38) * mm, "end": v(30.46, 16.43) * mm});
            skLineSegment(sketch, "E3563", {"start": v(30.46, 16.43) * mm, "end": v(30.4, 16.47) * mm});
            skLineSegment(sketch, "E3564", {"start": v(30.4, 16.47) * mm, "end": v(30.38, 16.48) * mm});
            skLineSegment(sketch, "E3565", {"start": v(30.38, 16.48) * mm, "end": v(30.34, 16.5) * mm});
            skLineSegment(sketch, "E3566", {"start": v(30.34, 16.5) * mm, "end": v(30.3, 16.5) * mm});
            skLineSegment(sketch, "E3567", {"start": v(30.3, 16.5) * mm, "end": v(30.26, 16.5) * mm});
            skLineSegment(sketch, "E3568", {"start": v(30.26, 16.5) * mm, "end": v(30.21, 16.5) * mm});
            skLineSegment(sketch, "E3569", {"start": v(30.21, 16.5) * mm, "end": v(30.16, 16.48) * mm});
            skLineSegment(sketch, "E3570", {"start": v(30.16, 16.48) * mm, "end": v(30.12, 16.47) * mm});
            skLineSegment(sketch, "E3571", {"start": v(30.12, 16.47) * mm, "end": v(30.07, 16.46) * mm});
            skLineSegment(sketch, "E3572", {"start": v(30.07, 16.46) * mm, "end": v(30.03, 16.45) * mm});
            skLineSegment(sketch, "E3573", {"start": v(30.03, 16.45) * mm, "end": v(29.99, 16.44) * mm});
            skLineSegment(sketch, "E3574", {"start": v(29.99, 16.44) * mm, "end": v(29.95, 16.43) * mm});
            skLineSegment(sketch, "E3575", {"start": v(29.95, 16.43) * mm, "end": v(29.91, 16.42) * mm});
            skLineSegment(sketch, "E3576", {"start": v(29.91, 16.42) * mm, "end": v(29.87, 16.4) * mm});
            skLineSegment(sketch, "E3577", {"start": v(29.87, 16.4) * mm, "end": v(29.83, 16.4) * mm});
            skLineSegment(sketch, "E3578", {"start": v(29.83, 16.4) * mm, "end": v(29.8, 16.38) * mm});
            skLineSegment(sketch, "E3579", {"start": v(29.8, 16.38) * mm, "end": v(29.75, 16.37) * mm});
            skLineSegment(sketch, "E3580", {"start": v(29.75, 16.37) * mm, "end": v(29.73, 16.36) * mm});
            skLineSegment(sketch, "E3581", {"start": v(29.73, 16.36) * mm, "end": v(29.71, 16.35) * mm});
            skLineSegment(sketch, "E3582", {"start": v(29.71, 16.35) * mm, "end": v(29.7, 16.35) * mm});
            skLineSegment(sketch, "E3583", {"start": v(29.7, 16.35) * mm, "end": v(29.67, 16.34) * mm});
            skLineSegment(sketch, "E3584", {"start": v(29.67, 16.34) * mm, "end": v(29.65, 16.33) * mm});
            skLineSegment(sketch, "E3585", {"start": v(29.65, 16.33) * mm, "end": v(29.63, 16.33) * mm});
            skLineSegment(sketch, "E3586", {"start": v(29.63, 16.33) * mm, "end": v(29.61, 16.32) * mm});
            skLineSegment(sketch, "E3587", {"start": v(29.61, 16.32) * mm, "end": v(29.6, 16.32) * mm});
            skLineSegment(sketch, "E3588", {"start": v(29.6, 16.32) * mm, "end": v(29.57, 16.3) * mm});
            skLineSegment(sketch, "E3589", {"start": v(29.57, 16.3) * mm, "end": v(29.54, 16.3) * mm});
            skLineSegment(sketch, "E3590", {"start": v(29.54, 16.3) * mm, "end": v(29.52, 16.3) * mm});
            skLineSegment(sketch, "E3591", {"start": v(29.52, 16.3) * mm, "end": v(29.5, 16.29) * mm});
            skLineSegment(sketch, "E3592", {"start": v(29.5, 16.29) * mm, "end": v(29.47, 16.28) * mm});
            skLineSegment(sketch, "E3593", {"start": v(29.47, 16.28) * mm, "end": v(29.44, 16.28) * mm});
            skLineSegment(sketch, "E3594", {"start": v(29.44, 16.28) * mm, "end": v(29.42, 16.27) * mm});
            skLineSegment(sketch, "E3595", {"start": v(29.42, 16.27) * mm, "end": v(29.4, 16.26) * mm});
            skLineSegment(sketch, "E3596", {"start": v(29.4, 16.26) * mm, "end": v(29.34, 16.25) * mm});
            skLineSegment(sketch, "E3597", {"start": v(29.34, 16.25) * mm, "end": v(29.28, 16.23) * mm});
            skLineSegment(sketch, "E3598", {"start": v(29.28, 16.23) * mm, "end": v(29.22, 16.22) * mm});
            skLineSegment(sketch, "E3599", {"start": v(29.22, 16.22) * mm, "end": v(29.17, 16.2) * mm});
            skLineSegment(sketch, "E3600", {"start": v(29.17, 16.2) * mm, "end": v(29.11, 16.18) * mm});
            skLineSegment(sketch, "E3601", {"start": v(29.11, 16.18) * mm, "end": v(29.06, 16.16) * mm});
            skLineSegment(sketch, "E3602", {"start": v(29.06, 16.16) * mm, "end": v(29, 16.14) * mm});
            skLineSegment(sketch, "E3603", {"start": v(29, 16.14) * mm, "end": v(28.95, 16.11) * mm});
            skLineSegment(sketch, "E3604", {"start": v(28.95, 16.11) * mm, "end": v(28.84, 16.05) * mm});
            skLineSegment(sketch, "E3605", {"start": v(28.84, 16.05) * mm, "end": v(28.72, 15.98) * mm});
            skLineSegment(sketch, "E3606", {"start": v(28.72, 15.98) * mm, "end": v(28.6, 15.9) * mm});
            skLineSegment(sketch, "E3607", {"start": v(28.6, 15.9) * mm, "end": v(28.49, 15.83) * mm});
            skLineSegment(sketch, "E3608", {"start": v(28.49, 15.83) * mm, "end": v(28.37, 15.75) * mm});
            skLineSegment(sketch, "E3609", {"start": v(28.37, 15.75) * mm, "end": v(28.24, 15.66) * mm});
            skLineSegment(sketch, "E3610", {"start": v(28.24, 15.66) * mm, "end": v(28.12, 15.57) * mm});
            skLineSegment(sketch, "E3611", {"start": v(28.12, 15.57) * mm, "end": v(27.99, 15.48) * mm});
            skLineSegment(sketch, "E3612", {"start": v(27.99, 15.48) * mm, "end": v(27.92, 15.43) * mm});
            skLineSegment(sketch, "E3613", {"start": v(27.92, 15.43) * mm, "end": v(27.86, 15.38) * mm});
            skLineSegment(sketch, "E3614", {"start": v(27.86, 15.38) * mm, "end": v(27.78, 15.32) * mm});
            skLineSegment(sketch, "E3615", {"start": v(27.78, 15.32) * mm, "end": v(27.7, 15.25) * mm});
            skLineSegment(sketch, "E3616", {"start": v(27.7, 15.25) * mm, "end": v(27.64, 15.18) * mm});
            skLineSegment(sketch, "E3617", {"start": v(27.64, 15.18) * mm, "end": v(27.56, 15.1) * mm});
            skLineSegment(sketch, "E3618", {"start": v(27.56, 15.1) * mm, "end": v(27.5, 15.02) * mm});
            skLineSegment(sketch, "E3619", {"start": v(27.5, 15.02) * mm, "end": v(27.43, 14.94) * mm});
            skLineSegment(sketch, "E3620", {"start": v(27.43, 14.94) * mm, "end": v(27.38, 14.85) * mm});
            skLineSegment(sketch, "E3621", {"start": v(27.38, 14.85) * mm, "end": v(27.33, 14.77) * mm});
            skLineSegment(sketch, "E3622", {"start": v(27.33, 14.77) * mm, "end": v(27.28, 14.68) * mm});
            skLineSegment(sketch, "E3623", {"start": v(27.28, 14.68) * mm, "end": v(27.24, 14.58) * mm});
            skLineSegment(sketch, "E3624", {"start": v(27.24, 14.58) * mm, "end": v(27.2, 14.5) * mm});
            skLineSegment(sketch, "E3625", {"start": v(27.2, 14.5) * mm, "end": v(27.17, 14.4) * mm});
            skLineSegment(sketch, "E3626", {"start": v(27.17, 14.4) * mm, "end": v(27.14, 14.31) * mm});
            skLineSegment(sketch, "E3627", {"start": v(27.14, 14.31) * mm, "end": v(27.11, 14.22) * mm});
            skLineSegment(sketch, "E3628", {"start": v(27.11, 14.22) * mm, "end": v(27.08, 14.16) * mm});
            skLineSegment(sketch, "E3629", {"start": v(27.08, 14.16) * mm, "end": v(27.04, 14.1) * mm});
            skLineSegment(sketch, "E3630", {"start": v(27.04, 14.1) * mm, "end": v(27, 14.05) * mm});
            skLineSegment(sketch, "E3631", {"start": v(27, 14.05) * mm, "end": v(26.93, 14.02) * mm});
            skLineSegment(sketch, "E3632", {"start": v(26.93, 14.02) * mm, "end": v(26.87, 14) * mm});
            skLineSegment(sketch, "E3633", {"start": v(26.87, 14) * mm, "end": v(26.8, 14) * mm});
            skLineSegment(sketch, "E3634", {"start": v(26.8, 14) * mm, "end": v(26.74, 14) * mm});
            skLineSegment(sketch, "E3635", {"start": v(26.74, 14) * mm, "end": v(26.68, 14.03) * mm});
            skLineSegment(sketch, "E3636", {"start": v(26.68, 14.03) * mm, "end": v(26.62, 14.07) * mm});
            skLineSegment(sketch, "E3637", {"start": v(26.62, 14.07) * mm, "end": v(26.58, 14.1) * mm});
            skLineSegment(sketch, "E3638", {"start": v(26.58, 14.1) * mm, "end": v(26.55, 14.12) * mm});
            skLineSegment(sketch, "E3639", {"start": v(26.55, 14.12) * mm, "end": v(26.52, 14.13) * mm});
            skLineSegment(sketch, "E3640", {"start": v(26.52, 14.13) * mm, "end": v(26.51, 14.14) * mm});
            skLineSegment(sketch, "E3641", {"start": v(26.51, 14.14) * mm, "end": v(26.5, 14.14) * mm});
            skLineSegment(sketch, "E3642", {"start": v(26.5, 14.14) * mm, "end": v(26.5, 14.14) * mm});
            skLineSegment(sketch, "E3643", {"start": v(26.5, 14.14) * mm, "end": v(26.43, 14.19) * mm});
            skLineSegment(sketch, "E3644", {"start": v(26.43, 14.19) * mm, "end": v(26.36, 14.23) * mm});
            skLineSegment(sketch, "E3645", {"start": v(26.36, 14.23) * mm, "end": v(26.29, 14.27) * mm});
            skLineSegment(sketch, "E3646", {"start": v(26.29, 14.27) * mm, "end": v(26.23, 14.3) * mm});
            skLineSegment(sketch, "E3647", {"start": v(26.23, 14.3) * mm, "end": v(26.17, 14.34) * mm});
            skLineSegment(sketch, "E3648", {"start": v(26.17, 14.34) * mm, "end": v(26.13, 14.37) * mm});
            skLineSegment(sketch, "E3649", {"start": v(26.13, 14.37) * mm, "end": v(26.1, 14.39) * mm});
            skLineSegment(sketch, "E3650", {"start": v(26.1, 14.39) * mm, "end": v(26.08, 14.4) * mm});
            skLineSegment(sketch, "E3651", {"start": v(26.08, 14.4) * mm, "end": v(26.06, 14.4) * mm});
            skLineSegment(sketch, "E3652", {"start": v(26.06, 14.4) * mm, "end": v(26.04, 14.42) * mm});
            skLineSegment(sketch, "E3653", {"start": v(26.04, 14.42) * mm, "end": v(26.03, 14.43) * mm});
            skLineSegment(sketch, "E3654", {"start": v(26.03, 14.43) * mm, "end": v(26, 14.44) * mm});
            skLineSegment(sketch, "E3655", {"start": v(26, 14.44) * mm, "end": v(26, 14.46) * mm});
            skLineSegment(sketch, "E3656", {"start": v(26, 14.46) * mm, "end": v(25.98, 14.47) * mm});
            skLineSegment(sketch, "E3657", {"start": v(25.98, 14.47) * mm, "end": v(25.96, 14.48) * mm});
            skLineSegment(sketch, "E3658", {"start": v(25.96, 14.48) * mm, "end": v(25.94, 14.5) * mm});
            skLineSegment(sketch, "E3659", {"start": v(25.94, 14.5) * mm, "end": v(25.94, 14.5) * mm});
            skLineSegment(sketch, "E3660", {"start": v(25.94, 14.5) * mm, "end": v(25.94, 14.52) * mm});
            skLineSegment(sketch, "E3661", {"start": v(25.94, 14.52) * mm, "end": v(25.94, 14.53) * mm});
            skLineSegment(sketch, "E3662", {"start": v(25.94, 14.53) * mm, "end": v(25.93, 14.54) * mm});
            skLineSegment(sketch, "E3663", {"start": v(25.93, 14.54) * mm, "end": v(25.93, 14.55) * mm});
            skLineSegment(sketch, "E3664", {"start": v(25.93, 14.55) * mm, "end": v(25.93, 14.56) * mm});
            skLineSegment(sketch, "E3665", {"start": v(25.93, 14.56) * mm, "end": v(25.93, 14.57) * mm});
            skLineSegment(sketch, "E3666", {"start": v(25.93, 14.57) * mm, "end": v(25.93, 14.57) * mm});
            skLineSegment(sketch, "E3667", {"start": v(25.93, 14.57) * mm, "end": v(25.94, 14.6) * mm});
            skLineSegment(sketch, "E3668", {"start": v(25.94, 14.6) * mm, "end": v(25.95, 14.62) * mm});
            skLineSegment(sketch, "E3669", {"start": v(25.95, 14.62) * mm, "end": v(25.96, 14.64) * mm});
            skLineSegment(sketch, "E3670", {"start": v(25.96, 14.64) * mm, "end": v(25.97, 14.66) * mm});
            skLineSegment(sketch, "E3671", {"start": v(25.97, 14.66) * mm, "end": v(25.97, 14.68) * mm});
            skLineSegment(sketch, "E3672", {"start": v(25.97, 14.68) * mm, "end": v(25.98, 14.7) * mm});
            skLineSegment(sketch, "E3673", {"start": v(25.98, 14.7) * mm, "end": v(25.99, 14.7) * mm});
            skLineSegment(sketch, "E3674", {"start": v(25.99, 14.7) * mm, "end": v(26, 14.71) * mm});
            skLineSegment(sketch, "E3675", {"start": v(26, 14.71) * mm, "end": v(26, 14.72) * mm});
            skLineSegment(sketch, "E3676", {"start": v(26, 14.72) * mm, "end": v(26.01, 14.75) * mm});
            skLineSegment(sketch, "E3677", {"start": v(26.01, 14.75) * mm, "end": v(26.03, 14.78) * mm});
            skLineSegment(sketch, "E3678", {"start": v(26.03, 14.78) * mm, "end": v(26.06, 14.82) * mm});
            skLineSegment(sketch, "E3679", {"start": v(26.06, 14.82) * mm, "end": v(26.08, 14.86) * mm});
            skLineSegment(sketch, "E3680", {"start": v(26.08, 14.86) * mm, "end": v(26.12, 14.91) * mm});
            skLineSegment(sketch, "E3681", {"start": v(26.12, 14.91) * mm, "end": v(26.15, 14.97) * mm});
            skLineSegment(sketch, "E3682", {"start": v(26.15, 14.97) * mm, "end": v(26.18, 15.02) * mm});
            skLineSegment(sketch, "E3683", {"start": v(26.18, 15.02) * mm, "end": v(26.18, 15.02) * mm});
            skLineSegment(sketch, "E3684", {"start": v(26.18, 15.02) * mm, "end": v(26.19, 15.03) * mm});
            skLineSegment(sketch, "E3685", {"start": v(26.19, 15.03) * mm, "end": v(26.19, 15.03) * mm});
            skLineSegment(sketch, "E3686", {"start": v(26.19, 15.03) * mm, "end": v(26.2, 15.04) * mm});
            skLineSegment(sketch, "E3687", {"start": v(26.2, 15.04) * mm, "end": v(26.2, 15.06) * mm});
            skLineSegment(sketch, "E3688", {"start": v(26.2, 15.06) * mm, "end": v(26.2, 15.1) * mm});
            skLineSegment(sketch, "E3689", {"start": v(26.2, 15.1) * mm, "end": v(26.22, 15.13) * mm});
            skLineSegment(sketch, "E3690", {"start": v(26.22, 15.13) * mm, "end": v(26.24, 15.18) * mm});
            skLineSegment(sketch, "E3691", {"start": v(26.24, 15.18) * mm, "end": v(26.27, 15.28) * mm});
            skLineSegment(sketch, "E3692", {"start": v(26.27, 15.28) * mm, "end": v(26.3, 15.38) * mm});
            skLineSegment(sketch, "E3693", {"start": v(26.3, 15.38) * mm, "end": v(26.32, 15.47) * mm});
            skLineSegment(sketch, "E3694", {"start": v(26.32, 15.47) * mm, "end": v(26.35, 15.57) * mm});
            skLineSegment(sketch, "E3695", {"start": v(26.35, 15.57) * mm, "end": v(26.37, 15.66) * mm});
            skLineSegment(sketch, "E3696", {"start": v(26.37, 15.66) * mm, "end": v(26.4, 15.76) * mm});
            skLineSegment(sketch, "E3697", {"start": v(26.4, 15.76) * mm, "end": v(26.42, 15.86) * mm});
            skLineSegment(sketch, "E3698", {"start": v(26.42, 15.86) * mm, "end": v(26.45, 15.95) * mm});
            skLineSegment(sketch, "E3699", {"start": v(26.45, 15.95) * mm, "end": v(26.45, 15.98) * mm});
            skLineSegment(sketch, "E3700", {"start": v(26.45, 15.98) * mm, "end": v(26.46, 16) * mm});
            skLineSegment(sketch, "E3701", {"start": v(26.46, 16) * mm, "end": v(26.46, 16.02) * mm});
            skLineSegment(sketch, "E3702", {"start": v(26.46, 16.02) * mm, "end": v(26.47, 16.03) * mm});
            skLineSegment(sketch, "E3703", {"start": v(26.47, 16.03) * mm, "end": v(26.47, 16.03) * mm});
            skLineSegment(sketch, "E3704", {"start": v(26.47, 16.03) * mm, "end": v(26.47, 16.04) * mm});
            skLineSegment(sketch, "E3705", {"start": v(26.47, 16.04) * mm, "end": v(26.47, 16.04) * mm});
            skLineSegment(sketch, "E3706", {"start": v(26.47, 16.04) * mm, "end": v(26.48, 16.07) * mm});
            skLineSegment(sketch, "E3707", {"start": v(26.48, 16.07) * mm, "end": v(26.49, 16.1) * mm});
            skLineSegment(sketch, "E3708", {"start": v(26.49, 16.1) * mm, "end": v(26.5, 16.14) * mm});
            skLineSegment(sketch, "E3709", {"start": v(26.5, 16.14) * mm, "end": v(26.5, 16.16) * mm});
            skLineSegment(sketch, "E3710", {"start": v(26.5, 16.16) * mm, "end": v(26.5, 16.18) * mm});
            skLineSegment(sketch, "E3711", {"start": v(26.5, 16.18) * mm, "end": v(26.51, 16.2) * mm});
            skLineSegment(sketch, "E3712", {"start": v(26.51, 16.2) * mm, "end": v(26.51, 16.22) * mm});
            skLineSegment(sketch, "E3713", {"start": v(26.51, 16.22) * mm, "end": v(26.52, 16.22) * mm});
            skLineSegment(sketch, "E3714", {"start": v(26.52, 16.22) * mm, "end": v(26.52, 16.23) * mm});
            skLineSegment(sketch, "E3715", {"start": v(26.52, 16.23) * mm, "end": v(26.52, 16.24) * mm});
            skLineSegment(sketch, "E3716", {"start": v(26.52, 16.24) * mm, "end": v(26.52, 16.25) * mm});
            skLineSegment(sketch, "E3717", {"start": v(26.52, 16.25) * mm, "end": v(26.53, 16.27) * mm});
            skLineSegment(sketch, "E3718", {"start": v(26.53, 16.27) * mm, "end": v(26.54, 16.3) * mm});
            skLineSegment(sketch, "E3719", {"start": v(26.54, 16.3) * mm, "end": v(26.54, 16.32) * mm});
            skLineSegment(sketch, "E3720", {"start": v(26.54, 16.32) * mm, "end": v(26.55, 16.35) * mm});
            skLineSegment(sketch, "E3721", {"start": v(26.55, 16.35) * mm, "end": v(26.56, 16.38) * mm});
            skLineSegment(sketch, "E3722", {"start": v(26.56, 16.38) * mm, "end": v(26.56, 16.38) * mm});
            skLineSegment(sketch, "E3723", {"start": v(26.56, 16.38) * mm, "end": v(26.56, 16.39) * mm});
            skLineSegment(sketch, "E3724", {"start": v(26.56, 16.39) * mm, "end": v(26.56, 16.4) * mm});
            skLineSegment(sketch, "E3725", {"start": v(26.56, 16.4) * mm, "end": v(26.56, 16.4) * mm});
            skLineSegment(sketch, "E3726", {"start": v(26.56, 16.4) * mm, "end": v(26.56, 16.41) * mm});
            skLineSegment(sketch, "E3727", {"start": v(26.56, 16.41) * mm, "end": v(26.56, 16.43) * mm});
            skLineSegment(sketch, "E3728", {"start": v(26.56, 16.43) * mm, "end": v(26.56, 16.46) * mm});
            skLineSegment(sketch, "E3729", {"start": v(26.56, 16.46) * mm, "end": v(26.56, 16.5) * mm});
            skLineSegment(sketch, "E3730", {"start": v(26.56, 16.5) * mm, "end": v(26.55, 16.54) * mm});
            skLineSegment(sketch, "E3731", {"start": v(26.55, 16.54) * mm, "end": v(26.55, 16.58) * mm});
            skLineSegment(sketch, "E3732", {"start": v(26.55, 16.58) * mm, "end": v(26.55, 16.62) * mm});
            skLineSegment(sketch, "E3733", {"start": v(26.55, 16.62) * mm, "end": v(26.55, 16.67) * mm});
            skLineSegment(sketch, "E3734", {"start": v(26.55, 16.67) * mm, "end": v(26.55, 16.7) * mm});
            skLineSegment(sketch, "E3735", {"start": v(26.55, 16.7) * mm, "end": v(26.55, 16.75) * mm});
            skLineSegment(sketch, "E3736", {"start": v(26.55, 16.75) * mm, "end": v(26.54, 16.79) * mm});
            skLineSegment(sketch, "E3737", {"start": v(26.54, 16.79) * mm, "end": v(26.54, 16.84) * mm});
            skLineSegment(sketch, "E3738", {"start": v(26.54, 16.84) * mm, "end": v(26.54, 16.9) * mm});
            skLineSegment(sketch, "E3739", {"start": v(26.54, 16.9) * mm, "end": v(26.54, 16.95) * mm});
            skLineSegment(sketch, "E3740", {"start": v(26.54, 16.95) * mm, "end": v(26.53, 17) * mm});
            skLineSegment(sketch, "E3741", {"start": v(26.53, 17) * mm, "end": v(26.53, 17.06) * mm});
            skLineSegment(sketch, "E3742", {"start": v(26.53, 17.06) * mm, "end": v(26.53, 17.12) * mm});
            skLineSegment(sketch, "E3743", {"start": v(26.53, 17.12) * mm, "end": v(26.53, 17.17) * mm});
            skLineSegment(sketch, "E3744", {"start": v(26.53, 17.17) * mm, "end": v(26.53, 17.23) * mm});
            skLineSegment(sketch, "E3745", {"start": v(26.53, 17.23) * mm, "end": v(26.53, 17.35) * mm});
            skLineSegment(sketch, "E3746", {"start": v(26.53, 17.35) * mm, "end": v(26.51, 17.46) * mm});
            skLineSegment(sketch, "E3747", {"start": v(26.51, 17.46) * mm, "end": v(26.5, 17.57) * mm});
            skLineSegment(sketch, "E3748", {"start": v(26.5, 17.57) * mm, "end": v(26.46, 17.67) * mm});
            skLineSegment(sketch, "E3749", {"start": v(26.46, 17.67) * mm, "end": v(26.43, 17.78) * mm});
            skLineSegment(sketch, "E3750", {"start": v(26.43, 17.78) * mm, "end": v(26.4, 17.88) * mm});
            skLineSegment(sketch, "E3751", {"start": v(26.4, 17.88) * mm, "end": v(26.35, 17.98) * mm});
            skLineSegment(sketch, "E3752", {"start": v(26.35, 17.98) * mm, "end": v(26.31, 18.08) * mm});
            skLineSegment(sketch, "E3753", {"start": v(26.31, 18.08) * mm, "end": v(26.3, 18.1) * mm});
            skLineSegment(sketch, "E3754", {"start": v(26.3, 18.1) * mm, "end": v(26.29, 18.14) * mm});
            skLineSegment(sketch, "E3755", {"start": v(26.29, 18.14) * mm, "end": v(26.28, 18.16) * mm});
            skLineSegment(sketch, "E3756", {"start": v(26.28, 18.16) * mm, "end": v(26.27, 18.19) * mm});
            skLineSegment(sketch, "E3757", {"start": v(26.27, 18.19) * mm, "end": v(26.26, 18.22) * mm});
            skLineSegment(sketch, "E3758", {"start": v(26.26, 18.22) * mm, "end": v(26.25, 18.24) * mm});
            skLineSegment(sketch, "E3759", {"start": v(26.25, 18.24) * mm, "end": v(26.24, 18.27) * mm});
            skLineSegment(sketch, "E3760", {"start": v(26.24, 18.27) * mm, "end": v(26.23, 18.3) * mm});
            skLineSegment(sketch, "E3761", {"start": v(26.23, 18.3) * mm, "end": v(26.2, 18.37) * mm});
            skLineSegment(sketch, "E3762", {"start": v(26.2, 18.37) * mm, "end": v(26.18, 18.44) * mm});
            skLineSegment(sketch, "E3763", {"start": v(26.18, 18.44) * mm, "end": v(26.17, 18.5) * mm});
            skLineSegment(sketch, "E3764", {"start": v(26.17, 18.5) * mm, "end": v(26.17, 18.57) * mm});
            skLineSegment(sketch, "E3765", {"start": v(26.17, 18.57) * mm, "end": v(26.17, 18.64) * mm});
            skLineSegment(sketch, "E3766", {"start": v(26.17, 18.64) * mm, "end": v(26.18, 18.7) * mm});
            skLineSegment(sketch, "E3767", {"start": v(26.18, 18.7) * mm, "end": v(26.2, 18.77) * mm});
            skLineSegment(sketch, "E3768", {"start": v(26.2, 18.77) * mm, "end": v(26.22, 18.83) * mm});
            skLineSegment(sketch, "E3769", {"start": v(26.22, 18.83) * mm, "end": v(26.26, 18.9) * mm});
            skLineSegment(sketch, "E3770", {"start": v(26.26, 18.9) * mm, "end": v(26.28, 18.98) * mm});
            skLineSegment(sketch, "E3771", {"start": v(26.28, 18.98) * mm, "end": v(26.31, 19.06) * mm});
            skLineSegment(sketch, "E3772", {"start": v(26.31, 19.06) * mm, "end": v(26.34, 19.14) * mm});
            skLineSegment(sketch, "E3773", {"start": v(26.34, 19.14) * mm, "end": v(26.37, 19.22) * mm});
            skLineSegment(sketch, "E3774", {"start": v(26.37, 19.22) * mm, "end": v(26.4, 19.3) * mm});
            skLineSegment(sketch, "E3775", {"start": v(26.4, 19.3) * mm, "end": v(26.42, 19.38) * mm});
            skLineSegment(sketch, "E3776", {"start": v(26.42, 19.38) * mm, "end": v(26.45, 19.46) * mm});
            skLineSegment(sketch, "E3777", {"start": v(26.45, 19.46) * mm, "end": v(26.46, 19.49) * mm});
            skLineSegment(sketch, "E3778", {"start": v(26.46, 19.49) * mm, "end": v(26.47, 19.51) * mm});
            skLineSegment(sketch, "E3779", {"start": v(26.47, 19.51) * mm, "end": v(26.47, 19.53) * mm});
            skLineSegment(sketch, "E3780", {"start": v(26.47, 19.53) * mm, "end": v(26.48, 19.54) * mm});
            skLineSegment(sketch, "E3781", {"start": v(26.48, 19.54) * mm, "end": v(26.48, 19.55) * mm});
            skLineSegment(sketch, "E3782", {"start": v(26.48, 19.55) * mm, "end": v(26.48, 19.55) * mm});
            skLineSegment(sketch, "E3783", {"start": v(26.48, 19.55) * mm, "end": v(26.5, 19.6) * mm});
            skLineSegment(sketch, "E3784", {"start": v(26.5, 19.6) * mm, "end": v(26.51, 19.64) * mm});
            skLineSegment(sketch, "E3785", {"start": v(26.51, 19.64) * mm, "end": v(26.53, 19.69) * mm});
            skLineSegment(sketch, "E3786", {"start": v(26.53, 19.69) * mm, "end": v(26.54, 19.73) * mm});
            skLineSegment(sketch, "E3787", {"start": v(26.54, 19.73) * mm, "end": v(26.56, 19.77) * mm});
            skLineSegment(sketch, "E3788", {"start": v(26.56, 19.77) * mm, "end": v(26.57, 19.82) * mm});
            skLineSegment(sketch, "E3789", {"start": v(26.57, 19.82) * mm, "end": v(26.59, 19.85) * mm});
            skLineSegment(sketch, "E3790", {"start": v(26.59, 19.85) * mm, "end": v(26.6, 19.88) * mm});
            skLineSegment(sketch, "E3791", {"start": v(26.6, 19.88) * mm, "end": v(26.6, 19.9) * mm});
            skLineSegment(sketch, "E3792", {"start": v(26.6, 19.9) * mm, "end": v(26.6, 19.92) * mm});
            skLineSegment(sketch, "E3793", {"start": v(26.6, 19.92) * mm, "end": v(26.6, 19.94) * mm});
            skLineSegment(sketch, "E3794", {"start": v(26.6, 19.94) * mm, "end": v(26.6, 19.95) * mm});
            skLineSegment(sketch, "E3795", {"start": v(26.6, 19.95) * mm, "end": v(26.58, 19.95) * mm});
            skLineSegment(sketch, "E3796", {"start": v(26.58, 19.95) * mm, "end": v(26.57, 19.95) * mm});
            skLineSegment(sketch, "E3797", {"start": v(26.57, 19.95) * mm, "end": v(26.55, 19.95) * mm});
            skLineSegment(sketch, "E3798", {"start": v(26.55, 19.95) * mm, "end": v(26.53, 19.94) * mm});
            skLineSegment(sketch, "E3799", {"start": v(26.53, 19.94) * mm, "end": v(26.5, 19.92) * mm});
            skLineSegment(sketch, "E3800", {"start": v(26.5, 19.92) * mm, "end": v(26.47, 19.9) * mm});
            skLineSegment(sketch, "E3801", {"start": v(26.47, 19.9) * mm, "end": v(26.43, 19.87) * mm});
            skLineSegment(sketch, "E3802", {"start": v(26.43, 19.87) * mm, "end": v(26.39, 19.83) * mm});
            skLineSegment(sketch, "E3803", {"start": v(26.39, 19.83) * mm, "end": v(26.34, 19.8) * mm});
            skLineSegment(sketch, "E3804", {"start": v(26.34, 19.8) * mm, "end": v(26.3, 19.75) * mm});
            skLineSegment(sketch, "E3805", {"start": v(26.3, 19.75) * mm, "end": v(26.25, 19.71) * mm});
            skLineSegment(sketch, "E3806", {"start": v(26.25, 19.71) * mm, "end": v(26.2, 19.67) * mm});
            skLineSegment(sketch, "E3807", {"start": v(26.2, 19.67) * mm, "end": v(26.2, 19.67) * mm});
            skLineSegment(sketch, "E3808", {"start": v(26.2, 19.67) * mm, "end": v(26.2, 19.66) * mm});
            skLineSegment(sketch, "E3809", {"start": v(26.2, 19.66) * mm, "end": v(26.2, 19.65) * mm});
            skLineSegment(sketch, "E3810", {"start": v(26.2, 19.65) * mm, "end": v(26.18, 19.63) * mm});
            skLineSegment(sketch, "E3811", {"start": v(26.18, 19.63) * mm, "end": v(26.17, 19.6) * mm});
            skLineSegment(sketch, "E3812", {"start": v(26.17, 19.6) * mm, "end": v(26.15, 19.57) * mm});
            skLineSegment(sketch, "E3813", {"start": v(26.15, 19.57) * mm, "end": v(26.13, 19.54) * mm});
            skLineSegment(sketch, "E3814", {"start": v(26.13, 19.54) * mm, "end": v(26.1, 19.5) * mm});
            skLineSegment(sketch, "E3815", {"start": v(26.1, 19.5) * mm, "end": v(26.08, 19.48) * mm});
            skLineSegment(sketch, "E3816", {"start": v(26.08, 19.48) * mm, "end": v(26.06, 19.45) * mm});
            skLineSegment(sketch, "E3817", {"start": v(26.06, 19.45) * mm, "end": v(26.04, 19.43) * mm});
            skLineSegment(sketch, "E3818", {"start": v(26.04, 19.43) * mm, "end": v(26.01, 19.4) * mm});
            skLineSegment(sketch, "E3819", {"start": v(26.01, 19.4) * mm, "end": v(25.99, 19.39) * mm});
            skLineSegment(sketch, "E3820", {"start": v(25.99, 19.39) * mm, "end": v(25.96, 19.37) * mm});
            skLineSegment(sketch, "E3821", {"start": v(25.96, 19.37) * mm, "end": v(25.94, 19.37) * mm});
            skLineSegment(sketch, "E3822", {"start": v(25.94, 19.37) * mm, "end": v(25.93, 19.36) * mm});
            skLineSegment(sketch, "E3823", {"start": v(25.93, 19.36) * mm, "end": v(25.92, 19.36) * mm});
            skLineSegment(sketch, "E3824", {"start": v(25.92, 19.36) * mm, "end": v(25.92, 19.36) * mm});
            skLineSegment(sketch, "E3825", {"start": v(25.92, 19.36) * mm, "end": v(25.91, 19.36) * mm});
            skLineSegment(sketch, "E3826", {"start": v(25.91, 19.36) * mm, "end": v(25.91, 19.36) * mm});
            skLineSegment(sketch, "E3827", {"start": v(25.91, 19.36) * mm, "end": v(25.9, 19.34) * mm});
            skLineSegment(sketch, "E3828", {"start": v(25.9, 19.34) * mm, "end": v(25.88, 19.3) * mm});
            skLineSegment(sketch, "E3829", {"start": v(25.88, 19.3) * mm, "end": v(25.84, 19.25) * mm});
            skLineSegment(sketch, "E3830", {"start": v(25.84, 19.25) * mm, "end": v(25.8, 19.18) * mm});
            skLineSegment(sketch, "E3831", {"start": v(25.8, 19.18) * mm, "end": v(25.74, 19.1) * mm});
            skLineSegment(sketch, "E3832", {"start": v(25.74, 19.1) * mm, "end": v(25.67, 19.01) * mm});
            skLineSegment(sketch, "E3833", {"start": v(25.67, 19.01) * mm, "end": v(25.6, 18.92) * mm});
            skLineSegment(sketch, "E3834", {"start": v(25.6, 18.92) * mm, "end": v(25.53, 18.82) * mm});
            skLineSegment(sketch, "E3835", {"start": v(25.53, 18.82) * mm, "end": v(25.45, 18.71) * mm});
            skLineSegment(sketch, "E3836", {"start": v(25.45, 18.71) * mm, "end": v(25.37, 18.61) * mm});
            skLineSegment(sketch, "E3837", {"start": v(25.37, 18.61) * mm, "end": v(25.3, 18.52) * mm});
            skLineSegment(sketch, "E3838", {"start": v(25.3, 18.52) * mm, "end": v(25.24, 18.43) * mm});
            skLineSegment(sketch, "E3839", {"start": v(25.24, 18.43) * mm, "end": v(25.17, 18.35) * mm});
            skLineSegment(sketch, "E3840", {"start": v(25.17, 18.35) * mm, "end": v(25.12, 18.28) * mm});
            skLineSegment(sketch, "E3841", {"start": v(25.12, 18.28) * mm, "end": v(25.08, 18.22) * mm});
            skLineSegment(sketch, "E3842", {"start": v(25.08, 18.22) * mm, "end": v(25.06, 18.19) * mm});
            skLineSegment(sketch, "E3843", {"start": v(25.06, 18.19) * mm, "end": v(25.06, 18.19) * mm});
            skLineSegment(sketch, "E3844", {"start": v(25.06, 18.19) * mm, "end": v(25.05, 18.19) * mm});
            skLineSegment(sketch, "E3845", {"start": v(25.05, 18.19) * mm, "end": v(25.05, 18.18) * mm});
            skLineSegment(sketch, "E3846", {"start": v(25.05, 18.18) * mm, "end": v(25.05, 18.18) * mm});
            skLineSegment(sketch, "E3847", {"start": v(25.05, 18.18) * mm, "end": v(25.04, 18.17) * mm});
            skLineSegment(sketch, "E3848", {"start": v(25.04, 18.17) * mm, "end": v(25.03, 18.16) * mm});
            skLineSegment(sketch, "E3849", {"start": v(25.03, 18.16) * mm, "end": v(25.02, 18.14) * mm});
            skLineSegment(sketch, "E3850", {"start": v(25.02, 18.14) * mm, "end": v(25, 18.12) * mm});
            skLineSegment(sketch, "E3851", {"start": v(25, 18.12) * mm, "end": v(24.96, 18.07) * mm});
            skLineSegment(sketch, "E3852", {"start": v(24.96, 18.07) * mm, "end": v(24.92, 18.01) * mm});
            skLineSegment(sketch, "E3853", {"start": v(24.92, 18.01) * mm, "end": v(24.87, 17.95) * mm});
            skLineSegment(sketch, "E3854", {"start": v(24.87, 17.95) * mm, "end": v(24.83, 17.9) * mm});
            skLineSegment(sketch, "E3855", {"start": v(24.83, 17.9) * mm, "end": v(24.79, 17.84) * mm});
            skLineSegment(sketch, "E3856", {"start": v(24.79, 17.84) * mm, "end": v(24.75, 17.78) * mm});
            skLineSegment(sketch, "E3857", {"start": v(24.75, 17.78) * mm, "end": v(24.7, 17.72) * mm});
            skLineSegment(sketch, "E3858", {"start": v(24.7, 17.72) * mm, "end": v(24.67, 17.66) * mm});
            skLineSegment(sketch, "E3859", {"start": v(24.67, 17.66) * mm, "end": v(24.58, 17.5) * mm});
            skLineSegment(sketch, "E3860", {"start": v(24.58, 17.5) * mm, "end": v(24.5, 17.34) * mm});
            skLineSegment(sketch, "E3861", {"start": v(24.5, 17.34) * mm, "end": v(24.41, 17.19) * mm});
            skLineSegment(sketch, "E3862", {"start": v(24.41, 17.19) * mm, "end": v(24.34, 17.04) * mm});
            skLineSegment(sketch, "E3863", {"start": v(24.34, 17.04) * mm, "end": v(24.28, 16.9) * mm});
            skLineSegment(sketch, "E3864", {"start": v(24.28, 16.9) * mm, "end": v(24.21, 16.75) * mm});
            skLineSegment(sketch, "E3865", {"start": v(24.21, 16.75) * mm, "end": v(24.16, 16.61) * mm});
            skLineSegment(sketch, "E3866", {"start": v(24.16, 16.61) * mm, "end": v(24.1, 16.47) * mm});
            skLineSegment(sketch, "E3867", {"start": v(24.1, 16.47) * mm, "end": v(24.06, 16.3) * mm});
            skLineSegment(sketch, "E3868", {"start": v(24.06, 16.3) * mm, "end": v(24.02, 16.14) * mm});
            skLineSegment(sketch, "E3869", {"start": v(24.02, 16.14) * mm, "end": v(23.99, 15.98) * mm});
            skLineSegment(sketch, "E3870", {"start": v(23.99, 15.98) * mm, "end": v(23.97, 15.8) * mm});
            skLineSegment(sketch, "E3871", {"start": v(23.97, 15.8) * mm, "end": v(23.95, 15.63) * mm});
            skLineSegment(sketch, "E3872", {"start": v(23.95, 15.63) * mm, "end": v(23.95, 15.45) * mm});
            skLineSegment(sketch, "E3873", {"start": v(23.95, 15.45) * mm, "end": v(23.96, 15.26) * mm});
            skLineSegment(sketch, "E3874", {"start": v(23.96, 15.26) * mm, "end": v(23.98, 15.07) * mm});
            skLineSegment(sketch, "E3875", {"start": v(23.98, 15.07) * mm, "end": v(23.98, 15.04) * mm});
            skLineSegment(sketch, "E3876", {"start": v(23.98, 15.04) * mm, "end": v(23.98, 15) * mm});
            skLineSegment(sketch, "E3877", {"start": v(23.98, 15) * mm, "end": v(23.98, 14.97) * mm});
            skLineSegment(sketch, "E3878", {"start": v(23.98, 14.97) * mm, "end": v(23.97, 14.95) * mm});
            skLineSegment(sketch, "E3879", {"start": v(23.97, 14.95) * mm, "end": v(23.97, 14.92) * mm});
            skLineSegment(sketch, "E3880", {"start": v(23.97, 14.92) * mm, "end": v(23.96, 14.9) * mm});
            skLineSegment(sketch, "E3881", {"start": v(23.96, 14.9) * mm, "end": v(23.95, 14.87) * mm});
            skLineSegment(sketch, "E3882", {"start": v(23.95, 14.87) * mm, "end": v(23.93, 14.86) * mm});
            skLineSegment(sketch, "E3883", {"start": v(23.93, 14.86) * mm, "end": v(23.92, 14.85) * mm});
            skLineSegment(sketch, "E3884", {"start": v(23.92, 14.85) * mm, "end": v(23.91, 14.84) * mm});
            skLineSegment(sketch, "E3885", {"start": v(23.91, 14.84) * mm, "end": v(23.9, 14.83) * mm});
            skLineSegment(sketch, "E3886", {"start": v(23.9, 14.83) * mm, "end": v(23.89, 14.82) * mm});
            skLineSegment(sketch, "E3887", {"start": v(23.89, 14.82) * mm, "end": v(23.87, 14.82) * mm});
            skLineSegment(sketch, "E3888", {"start": v(23.87, 14.82) * mm, "end": v(23.86, 14.81) * mm});
            skLineSegment(sketch, "E3889", {"start": v(23.86, 14.81) * mm, "end": v(23.84, 14.81) * mm});
            skLineSegment(sketch, "E3890", {"start": v(23.84, 14.81) * mm, "end": v(23.83, 14.8) * mm});
            skLineSegment(sketch, "E3891", {"start": v(23.83, 14.8) * mm, "end": v(23.73, 14.8) * mm});
            skLineSegment(sketch, "E3892", {"start": v(23.73, 14.8) * mm, "end": v(23.65, 14.8) * mm});
            skLineSegment(sketch, "E3893", {"start": v(23.65, 14.8) * mm, "end": v(23.6, 14.8) * mm});
            skLineSegment(sketch, "E3894", {"start": v(23.6, 14.8) * mm, "end": v(23.56, 14.8) * mm});
            skLineSegment(sketch, "E3895", {"start": v(23.56, 14.8) * mm, "end": v(23.54, 14.8) * mm});
            skLineSegment(sketch, "E3896", {"start": v(23.54, 14.8) * mm, "end": v(23.53, 14.8) * mm});
            skLineSegment(sketch, "E3897", {"start": v(23.53, 14.8) * mm, "end": v(23.53, 14.8) * mm});
            skLineSegment(sketch, "E3898", {"start": v(23.53, 14.8) * mm, "end": v(23.52, 14.8) * mm});
            skLineSegment(sketch, "E3899", {"start": v(23.52, 14.8) * mm, "end": v(23.41, 14.8) * mm});
            skLineSegment(sketch, "E3900", {"start": v(23.41, 14.8) * mm, "end": v(23.3, 14.81) * mm});
            skLineSegment(sketch, "E3901", {"start": v(23.3, 14.81) * mm, "end": v(23.2, 14.82) * mm});
            skLineSegment(sketch, "E3902", {"start": v(23.2, 14.82) * mm, "end": v(23.12, 14.82) * mm});
            skLineSegment(sketch, "E3903", {"start": v(23.12, 14.82) * mm, "end": v(23.04, 14.83) * mm});
            skLineSegment(sketch, "E3904", {"start": v(23.04, 14.83) * mm, "end": v(22.99, 14.83) * mm});
            skLineSegment(sketch, "E3905", {"start": v(22.99, 14.83) * mm, "end": v(22.95, 14.84) * mm});
            skLineSegment(sketch, "E3906", {"start": v(22.95, 14.84) * mm, "end": v(22.93, 14.84) * mm});
            skLineSegment(sketch, "E3907", {"start": v(22.93, 14.84) * mm, "end": v(22.92, 14.85) * mm});
            skLineSegment(sketch, "E3908", {"start": v(22.92, 14.85) * mm, "end": v(22.91, 14.86) * mm});
            skLineSegment(sketch, "E3909", {"start": v(22.91, 14.86) * mm, "end": v(22.9, 14.87) * mm});
            skLineSegment(sketch, "E3910", {"start": v(22.9, 14.87) * mm, "end": v(22.9, 14.89) * mm});
            skLineSegment(sketch, "E3911", {"start": v(22.9, 14.89) * mm, "end": v(22.89, 14.9) * mm});
            skLineSegment(sketch, "E3912", {"start": v(22.89, 14.9) * mm, "end": v(22.88, 14.92) * mm});
            skLineSegment(sketch, "E3913", {"start": v(22.88, 14.92) * mm, "end": v(22.88, 14.94) * mm});
            skLineSegment(sketch, "E3914", {"start": v(22.88, 14.94) * mm, "end": v(22.87, 14.96) * mm});
            skLineSegment(sketch, "E3915", {"start": v(22.87, 14.96) * mm, "end": v(22.87, 14.99) * mm});
            skLineSegment(sketch, "E3916", {"start": v(22.87, 14.99) * mm, "end": v(22.86, 15.03) * mm});
            skLineSegment(sketch, "E3917", {"start": v(22.86, 15.03) * mm, "end": v(22.84, 15.1) * mm});
            skLineSegment(sketch, "E3918", {"start": v(22.84, 15.1) * mm, "end": v(22.83, 15.18) * mm});
            skLineSegment(sketch, "E3919", {"start": v(22.83, 15.18) * mm, "end": v(22.8, 15.27) * mm});
            skLineSegment(sketch, "E3920", {"start": v(22.8, 15.27) * mm, "end": v(22.79, 15.38) * mm});
            skLineSegment(sketch, "E3921", {"start": v(22.79, 15.38) * mm, "end": v(22.76, 15.49) * mm});
            skLineSegment(sketch, "E3922", {"start": v(22.76, 15.49) * mm, "end": v(22.74, 15.6) * mm});
            skLineSegment(sketch, "E3923", {"start": v(22.74, 15.6) * mm, "end": v(22.74, 15.6) * mm});
            skLineSegment(sketch, "E3924", {"start": v(22.74, 15.6) * mm, "end": v(22.74, 15.61) * mm});
            skLineSegment(sketch, "E3925", {"start": v(22.74, 15.61) * mm, "end": v(22.74, 15.63) * mm});
            skLineSegment(sketch, "E3926", {"start": v(22.74, 15.63) * mm, "end": v(22.74, 15.67) * mm});
            skLineSegment(sketch, "E3927", {"start": v(22.74, 15.67) * mm, "end": v(22.74, 15.72) * mm});
            skLineSegment(sketch, "E3928", {"start": v(22.74, 15.72) * mm, "end": v(22.73, 15.78) * mm});
            skLineSegment(sketch, "E3929", {"start": v(22.73, 15.78) * mm, "end": v(22.73, 15.88) * mm});
            skLineSegment(sketch, "E3930", {"start": v(22.73, 15.88) * mm, "end": v(22.72, 16.03) * mm});
            skLineSegment(sketch, "E3931", {"start": v(22.72, 16.03) * mm, "end": v(22.7, 16.18) * mm});
            skLineSegment(sketch, "E3932", {"start": v(22.7, 16.18) * mm, "end": v(22.68, 16.33) * mm});
            skLineSegment(sketch, "E3933", {"start": v(22.68, 16.33) * mm, "end": v(22.65, 16.46) * mm});
            skLineSegment(sketch, "E3934", {"start": v(22.65, 16.46) * mm, "end": v(22.6, 16.59) * mm});
            skLineSegment(sketch, "E3935", {"start": v(22.6, 16.59) * mm, "end": v(22.56, 16.7) * mm});
            skLineSegment(sketch, "E3936", {"start": v(22.56, 16.7) * mm, "end": v(22.5, 16.82) * mm});
            skLineSegment(sketch, "E3937", {"start": v(22.5, 16.82) * mm, "end": v(22.44, 16.93) * mm});
            skLineSegment(sketch, "E3938", {"start": v(22.44, 16.93) * mm, "end": v(22.42, 16.96) * mm});
            skLineSegment(sketch, "E3939", {"start": v(22.42, 16.96) * mm, "end": v(22.4, 16.98) * mm});
            skLineSegment(sketch, "E3940", {"start": v(22.4, 16.98) * mm, "end": v(22.39, 17) * mm});
            skLineSegment(sketch, "E3941", {"start": v(22.39, 17) * mm, "end": v(22.37, 17.03) * mm});
            skLineSegment(sketch, "E3942", {"start": v(22.37, 17.03) * mm, "end": v(22.35, 17.05) * mm});
            skLineSegment(sketch, "E3943", {"start": v(22.35, 17.05) * mm, "end": v(22.34, 17.07) * mm});
            skLineSegment(sketch, "E3944", {"start": v(22.34, 17.07) * mm, "end": v(22.32, 17.1) * mm});
            skLineSegment(sketch, "E3945", {"start": v(22.32, 17.1) * mm, "end": v(22.3, 17.11) * mm});
            skLineSegment(sketch, "E3946", {"start": v(22.3, 17.11) * mm, "end": v(22.29, 17.13) * mm});
            skLineSegment(sketch, "E3947", {"start": v(22.29, 17.13) * mm, "end": v(22.27, 17.15) * mm});
            skLineSegment(sketch, "E3948", {"start": v(22.27, 17.15) * mm, "end": v(22.26, 17.17) * mm});
            skLineSegment(sketch, "E3949", {"start": v(22.26, 17.17) * mm, "end": v(22.24, 17.18) * mm});
            skLineSegment(sketch, "E3950", {"start": v(22.24, 17.18) * mm, "end": v(22.23, 17.2) * mm});
            skLineSegment(sketch, "E3951", {"start": v(22.23, 17.2) * mm, "end": v(22.22, 17.22) * mm});
            skLineSegment(sketch, "E3952", {"start": v(22.22, 17.22) * mm, "end": v(22.2, 17.24) * mm});
            skLineSegment(sketch, "E3953", {"start": v(22.2, 17.24) * mm, "end": v(22.19, 17.26) * mm});
            skLineSegment(sketch, "E3954", {"start": v(22.19, 17.26) * mm, "end": v(22.18, 17.28) * mm});
            skLineSegment(sketch, "E3955", {"start": v(22.18, 17.28) * mm, "end": v(22.16, 17.3) * mm});
            skLineSegment(sketch, "E3956", {"start": v(22.16, 17.3) * mm, "end": v(22.15, 17.33) * mm});
            skLineSegment(sketch, "E3957", {"start": v(22.15, 17.33) * mm, "end": v(22.13, 17.35) * mm});
            skLineSegment(sketch, "E3958", {"start": v(22.13, 17.35) * mm, "end": v(22.12, 17.37) * mm});
            skLineSegment(sketch, "E3959", {"start": v(22.12, 17.37) * mm, "end": v(22.1, 17.4) * mm});
            skLineSegment(sketch, "E3960", {"start": v(22.1, 17.4) * mm, "end": v(22.1, 17.42) * mm});
            skLineSegment(sketch, "E3961", {"start": v(22.1, 17.42) * mm, "end": v(22.08, 17.45) * mm});
            skLineSegment(sketch, "E3962", {"start": v(22.08, 17.45) * mm, "end": v(22.06, 17.5) * mm});
            skLineSegment(sketch, "E3963", {"start": v(22.06, 17.5) * mm, "end": v(22.03, 17.55) * mm});
            skLineSegment(sketch, "E3964", {"start": v(22.03, 17.55) * mm, "end": v(22, 17.6) * mm});
            skLineSegment(sketch, "E3965", {"start": v(22, 17.6) * mm, "end": v(21.97, 17.65) * mm});
            skLineSegment(sketch, "E3966", {"start": v(21.97, 17.65) * mm, "end": v(21.94, 17.7) * mm});
            skLineSegment(sketch, "E3967", {"start": v(21.94, 17.7) * mm, "end": v(21.9, 17.74) * mm});
            skLineSegment(sketch, "E3968", {"start": v(21.9, 17.74) * mm, "end": v(21.86, 17.78) * mm});
            skLineSegment(sketch, "E3969", {"start": v(21.86, 17.78) * mm, "end": v(21.82, 17.82) * mm});
            skLineSegment(sketch, "E3970", {"start": v(21.82, 17.82) * mm, "end": v(21.78, 17.85) * mm});
            skLineSegment(sketch, "E3971", {"start": v(21.78, 17.85) * mm, "end": v(21.74, 17.88) * mm});
            skLineSegment(sketch, "E3972", {"start": v(21.74, 17.88) * mm, "end": v(21.7, 17.9) * mm});
            skLineSegment(sketch, "E3973", {"start": v(21.7, 17.9) * mm, "end": v(21.67, 17.94) * mm});
            skLineSegment(sketch, "E3974", {"start": v(21.67, 17.94) * mm, "end": v(21.64, 17.97) * mm});
            skLineSegment(sketch, "E3975", {"start": v(21.64, 17.97) * mm, "end": v(21.6, 18) * mm});
            skLineSegment(sketch, "E3976", {"start": v(21.6, 18) * mm, "end": v(21.57, 18.03) * mm});
            skLineSegment(sketch, "E3977", {"start": v(21.57, 18.03) * mm, "end": v(21.53, 18.06) * mm});
            skLineSegment(sketch, "E3978", {"start": v(21.53, 18.06) * mm, "end": v(21.46, 18.12) * mm});
            skLineSegment(sketch, "E3979", {"start": v(21.46, 18.12) * mm, "end": v(21.39, 18.19) * mm});
            skLineSegment(sketch, "E3980", {"start": v(21.39, 18.19) * mm, "end": v(21.32, 18.25) * mm});
            skLineSegment(sketch, "E3981", {"start": v(21.32, 18.25) * mm, "end": v(21.24, 18.3) * mm});
            skLineSegment(sketch, "E3982", {"start": v(21.24, 18.3) * mm, "end": v(21.16, 18.36) * mm});
            skLineSegment(sketch, "E3983", {"start": v(21.16, 18.36) * mm, "end": v(21.08, 18.41) * mm});
            skLineSegment(sketch, "E3984", {"start": v(21.08, 18.41) * mm, "end": v(21, 18.46) * mm});
            skLineSegment(sketch, "E3985", {"start": v(21, 18.46) * mm, "end": v(20.9, 18.5) * mm});
            skLineSegment(sketch, "E3986", {"start": v(20.9, 18.5) * mm, "end": v(20.87, 18.51) * mm});
            skLineSegment(sketch, "E3987", {"start": v(20.87, 18.51) * mm, "end": v(20.84, 18.52) * mm});
            skLineSegment(sketch, "E3988", {"start": v(20.84, 18.52) * mm, "end": v(20.81, 18.53) * mm});
            skLineSegment(sketch, "E3989", {"start": v(20.81, 18.53) * mm, "end": v(20.79, 18.54) * mm});
            skLineSegment(sketch, "E3990", {"start": v(20.79, 18.54) * mm, "end": v(20.76, 18.55) * mm});
            skLineSegment(sketch, "E3991", {"start": v(20.76, 18.55) * mm, "end": v(20.74, 18.55) * mm});
            skLineSegment(sketch, "E3992", {"start": v(20.74, 18.55) * mm, "end": v(20.72, 18.55) * mm});
            skLineSegment(sketch, "E3993", {"start": v(20.72, 18.55) * mm, "end": v(20.7, 18.55) * mm});
            skLineSegment(sketch, "E3994", {"start": v(20.7, 18.55) * mm, "end": v(20.64, 18.55) * mm});
            skLineSegment(sketch, "E3995", {"start": v(20.64, 18.55) * mm, "end": v(20.59, 18.53) * mm});
            skLineSegment(sketch, "E3996", {"start": v(20.59, 18.53) * mm, "end": v(20.55, 18.5) * mm});
            skLineSegment(sketch, "E3997", {"start": v(20.55, 18.5) * mm, "end": v(20.52, 18.46) * mm});
            skLineSegment(sketch, "E3998", {"start": v(20.52, 18.46) * mm, "end": v(20.5, 18.42) * mm});
            skLineSegment(sketch, "E3999", {"start": v(20.5, 18.42) * mm, "end": v(20.48, 18.38) * mm});
            skLineSegment(sketch, "E4000", {"start": v(20.48, 18.38) * mm, "end": v(20.46, 18.34) * mm});
            skLineSegment(sketch, "E4001", {"start": v(20.46, 18.34) * mm, "end": v(20.45, 18.3) * mm});
            skLineSegment(sketch, "E4002", {"start": v(20.45, 18.3) * mm, "end": v(20.43, 18.2) * mm});
            skLineSegment(sketch, "E4003", {"start": v(20.43, 18.2) * mm, "end": v(20.4, 18.11) * mm});
            skLineSegment(sketch, "E4004", {"start": v(20.4, 18.11) * mm, "end": v(20.38, 18) * mm});
            skLineSegment(sketch, "E4005", {"start": v(20.38, 18) * mm, "end": v(20.37, 17.9) * mm});
            skLineSegment(sketch, "E4006", {"start": v(20.37, 17.9) * mm, "end": v(20.35, 17.8) * mm});
            skLineSegment(sketch, "E4007", {"start": v(20.35, 17.8) * mm, "end": v(20.33, 17.68) * mm});
            skLineSegment(sketch, "E4008", {"start": v(20.33, 17.68) * mm, "end": v(20.32, 17.57) * mm});
            skLineSegment(sketch, "E4009", {"start": v(20.32, 17.57) * mm, "end": v(20.3, 17.45) * mm});
            skLineSegment(sketch, "E4010", {"start": v(20.3, 17.45) * mm, "end": v(20.3, 17.35) * mm});
            skLineSegment(sketch, "E4011", {"start": v(20.3, 17.35) * mm, "end": v(20.3, 17.28) * mm});
            skLineSegment(sketch, "E4012", {"start": v(20.3, 17.28) * mm, "end": v(20.3, 17.23) * mm});
            skLineSegment(sketch, "E4013", {"start": v(20.3, 17.23) * mm, "end": v(20.29, 17.2) * mm});
            skLineSegment(sketch, "E4014", {"start": v(20.29, 17.2) * mm, "end": v(20.29, 17.18) * mm});
            skLineSegment(sketch, "E4015", {"start": v(20.29, 17.18) * mm, "end": v(20.29, 17.17) * mm});
            skLineSegment(sketch, "E4016", {"start": v(20.29, 17.17) * mm, "end": v(20.29, 17.16) * mm});
            skLineSegment(sketch, "E4017", {"start": v(20.29, 17.16) * mm, "end": v(20.29, 17.16) * mm});
            skLineSegment(sketch, "E4018", {"start": v(20.29, 17.16) * mm, "end": v(20.28, 17.04) * mm});
            skLineSegment(sketch, "E4019", {"start": v(20.28, 17.04) * mm, "end": v(20.28, 16.93) * mm});
            skLineSegment(sketch, "E4020", {"start": v(20.28, 16.93) * mm, "end": v(20.28, 16.82) * mm});
            skLineSegment(sketch, "E4021", {"start": v(20.28, 16.82) * mm, "end": v(20.27, 16.72) * mm});
            skLineSegment(sketch, "E4022", {"start": v(20.27, 16.72) * mm, "end": v(20.27, 16.63) * mm});
            skLineSegment(sketch, "E4023", {"start": v(20.27, 16.63) * mm, "end": v(20.27, 16.55) * mm});
            skLineSegment(sketch, "E4024", {"start": v(20.27, 16.55) * mm, "end": v(20.27, 16.5) * mm});
            skLineSegment(sketch, "E4025", {"start": v(20.27, 16.5) * mm, "end": v(20.27, 16.45) * mm});
            skLineSegment(sketch, "E4026", {"start": v(20.27, 16.45) * mm, "end": v(20.27, 16.42) * mm});
            skLineSegment(sketch, "E4027", {"start": v(20.27, 16.42) * mm, "end": v(20.27, 16.39) * mm});
            skLineSegment(sketch, "E4028", {"start": v(20.27, 16.39) * mm, "end": v(20.27, 16.35) * mm});
            skLineSegment(sketch, "E4029", {"start": v(20.27, 16.35) * mm, "end": v(20.26, 16.3) * mm});
            skLineSegment(sketch, "E4030", {"start": v(20.26, 16.3) * mm, "end": v(20.26, 16.26) * mm});
            skLineSegment(sketch, "E4031", {"start": v(20.26, 16.26) * mm, "end": v(20.26, 16.21) * mm});
            skLineSegment(sketch, "E4032", {"start": v(20.26, 16.21) * mm, "end": v(20.26, 16.17) * mm});
            skLineSegment(sketch, "E4033", {"start": v(20.26, 16.17) * mm, "end": v(20.26, 16.13) * mm});
            skLineSegment(sketch, "E4034", {"start": v(20.26, 16.13) * mm, "end": v(20.26, 16.13) * mm});
            skLineSegment(sketch, "E4035", {"start": v(20.26, 16.13) * mm, "end": v(20.27, 16.13) * mm});
            skLineSegment(sketch, "E4036", {"start": v(20.27, 16.13) * mm, "end": v(20.28, 16.12) * mm});
            skLineSegment(sketch, "E4037", {"start": v(20.28, 16.12) * mm, "end": v(20.29, 16.11) * mm});
            skLineSegment(sketch, "E4038", {"start": v(20.29, 16.11) * mm, "end": v(20.3, 16.1) * mm});
            skLineSegment(sketch, "E4039", {"start": v(20.3, 16.1) * mm, "end": v(20.33, 16.08) * mm});
            skLineSegment(sketch, "E4040", {"start": v(20.33, 16.08) * mm, "end": v(20.35, 16.07) * mm});
            skLineSegment(sketch, "E4041", {"start": v(20.35, 16.07) * mm, "end": v(20.36, 16.06) * mm});
            skLineSegment(sketch, "E4042", {"start": v(20.36, 16.06) * mm, "end": v(20.37, 16.06) * mm});
            skLineSegment(sketch, "E4043", {"start": v(20.37, 16.06) * mm, "end": v(20.38, 16.05) * mm});
            skLineSegment(sketch, "E4044", {"start": v(20.38, 16.05) * mm, "end": v(20.38, 16.05) * mm});
            skLineSegment(sketch, "E4045", {"start": v(20.38, 16.05) * mm, "end": v(20.39, 16.05) * mm});
            skLineSegment(sketch, "E4046", {"start": v(20.39, 16.05) * mm, "end": v(20.39, 16.05) * mm});
            skLineSegment(sketch, "E4047", {"start": v(20.39, 16.05) * mm, "end": v(20.37, 16.03) * mm});
            skLineSegment(sketch, "E4048", {"start": v(20.37, 16.03) * mm, "end": v(20.37, 16) * mm});
            skLineSegment(sketch, "E4049", {"start": v(20.37, 16) * mm, "end": v(20.36, 15.99) * mm});
            skLineSegment(sketch, "E4050", {"start": v(20.36, 15.99) * mm, "end": v(20.35, 15.97) * mm});
            skLineSegment(sketch, "E4051", {"start": v(20.35, 15.97) * mm, "end": v(20.34, 15.96) * mm});
            skLineSegment(sketch, "E4052", {"start": v(20.34, 15.96) * mm, "end": v(20.33, 15.94) * mm});
            skLineSegment(sketch, "E4053", {"start": v(20.33, 15.94) * mm, "end": v(20.33, 15.93) * mm});
            skLineSegment(sketch, "E4054", {"start": v(20.33, 15.93) * mm, "end": v(20.33, 15.93) * mm});
            skLineSegment(sketch, "E4055", {"start": v(20.33, 15.93) * mm, "end": v(20.32, 15.92) * mm});
            skLineSegment(sketch, "E4056", {"start": v(20.32, 15.92) * mm, "end": v(20.32, 15.91) * mm});
            skLineSegment(sketch, "E4057", {"start": v(20.32, 15.91) * mm, "end": v(20.31, 15.9) * mm});
            skLineSegment(sketch, "E4058", {"start": v(20.31, 15.9) * mm, "end": v(20.3, 15.89) * mm});
            skLineSegment(sketch, "E4059", {"start": v(20.3, 15.89) * mm, "end": v(20.3, 15.87) * mm});
            skLineSegment(sketch, "E4060", {"start": v(20.3, 15.87) * mm, "end": v(20.29, 15.85) * mm});
            skLineSegment(sketch, "E4061", {"start": v(20.29, 15.85) * mm, "end": v(20.28, 15.83) * mm});
            skLineSegment(sketch, "E4062", {"start": v(20.28, 15.83) * mm, "end": v(20.26, 15.8) * mm});
            skLineSegment(sketch, "E4063", {"start": v(20.26, 15.8) * mm, "end": v(20.27, 15.8) * mm});
            skLineSegment(sketch, "E4064", {"start": v(20.27, 15.8) * mm, "end": v(20.27, 15.8) * mm});
            skLineSegment(sketch, "E4065", {"start": v(20.27, 15.8) * mm, "end": v(20.27, 15.78) * mm});
            skLineSegment(sketch, "E4066", {"start": v(20.27, 15.78) * mm, "end": v(20.28, 15.77) * mm});
            skLineSegment(sketch, "E4067", {"start": v(20.28, 15.77) * mm, "end": v(20.28, 15.74) * mm});
            skLineSegment(sketch, "E4068", {"start": v(20.28, 15.74) * mm, "end": v(20.29, 15.72) * mm});
            skLineSegment(sketch, "E4069", {"start": v(20.29, 15.72) * mm, "end": v(20.3, 15.7) * mm});
            skLineSegment(sketch, "E4070", {"start": v(20.3, 15.7) * mm, "end": v(20.3, 15.67) * mm});
            skLineSegment(sketch, "E4071", {"start": v(20.3, 15.67) * mm, "end": v(20.3, 15.64) * mm});
            skLineSegment(sketch, "E4072", {"start": v(20.3, 15.64) * mm, "end": v(20.3, 15.61) * mm});
            skLineSegment(sketch, "E4073", {"start": v(20.3, 15.61) * mm, "end": v(20.31, 15.59) * mm});
            skLineSegment(sketch, "E4074", {"start": v(20.31, 15.59) * mm, "end": v(20.32, 15.56) * mm});
            skLineSegment(sketch, "E4075", {"start": v(20.32, 15.56) * mm, "end": v(20.32, 15.53) * mm});
            skLineSegment(sketch, "E4076", {"start": v(20.32, 15.53) * mm, "end": v(20.35, 15.42) * mm});
            skLineSegment(sketch, "E4077", {"start": v(20.35, 15.42) * mm, "end": v(20.37, 15.3) * mm});
            skLineSegment(sketch, "E4078", {"start": v(20.37, 15.3) * mm, "end": v(20.4, 15.18) * mm});
            skLineSegment(sketch, "E4079", {"start": v(20.4, 15.18) * mm, "end": v(20.45, 15.06) * mm});
            skLineSegment(sketch, "E4080", {"start": v(20.45, 15.06) * mm, "end": v(20.5, 14.95) * mm});
            skLineSegment(sketch, "E4081", {"start": v(20.5, 14.95) * mm, "end": v(20.57, 14.85) * mm});
            skLineSegment(sketch, "E4082", {"start": v(20.57, 14.85) * mm, "end": v(20.66, 14.75) * mm});
            skLineSegment(sketch, "E4083", {"start": v(20.66, 14.75) * mm, "end": v(20.77, 14.66) * mm});
            skLineSegment(sketch, "E4084", {"start": v(20.77, 14.66) * mm, "end": v(20.8, 14.64) * mm});
            skLineSegment(sketch, "E4085", {"start": v(20.8, 14.64) * mm, "end": v(20.8, 14.63) * mm});
            skLineSegment(sketch, "E4086", {"start": v(20.8, 14.63) * mm, "end": v(20.83, 14.6) * mm});
            skLineSegment(sketch, "E4087", {"start": v(20.83, 14.6) * mm, "end": v(20.84, 14.58) * mm});
            skLineSegment(sketch, "E4088", {"start": v(20.84, 14.58) * mm, "end": v(20.86, 14.56) * mm});
            skLineSegment(sketch, "E4089", {"start": v(20.86, 14.56) * mm, "end": v(20.88, 14.54) * mm});
            skLineSegment(sketch, "E4090", {"start": v(20.88, 14.54) * mm, "end": v(20.9, 14.5) * mm});
            skLineSegment(sketch, "E4091", {"start": v(20.9, 14.5) * mm, "end": v(20.9, 14.48) * mm});
            skLineSegment(sketch, "E4092", {"start": v(20.9, 14.48) * mm, "end": v(20.92, 14.46) * mm});
            skLineSegment(sketch, "E4093", {"start": v(20.92, 14.46) * mm, "end": v(20.93, 14.44) * mm});
            skLineSegment(sketch, "E4094", {"start": v(20.93, 14.44) * mm, "end": v(20.94, 14.43) * mm});
            skLineSegment(sketch, "E4095", {"start": v(20.94, 14.43) * mm, "end": v(20.96, 14.4) * mm});
            skLineSegment(sketch, "E4096", {"start": v(20.96, 14.4) * mm, "end": v(20.97, 14.39) * mm});
            skLineSegment(sketch, "E4097", {"start": v(20.97, 14.39) * mm, "end": v(20.98, 14.37) * mm});
            skLineSegment(sketch, "E4098", {"start": v(20.98, 14.37) * mm, "end": v(21, 14.35) * mm});
            skLineSegment(sketch, "E4099", {"start": v(21, 14.35) * mm, "end": v(21.01, 14.33) * mm});
            skLineSegment(sketch, "E4100", {"start": v(21.01, 14.33) * mm, "end": v(21.03, 14.3) * mm});
            skLineSegment(sketch, "E4101", {"start": v(21.03, 14.3) * mm, "end": v(21.04, 14.29) * mm});
            skLineSegment(sketch, "E4102", {"start": v(21.04, 14.29) * mm, "end": v(21.05, 14.27) * mm});
            skLineSegment(sketch, "E4103", {"start": v(21.05, 14.27) * mm, "end": v(21.06, 14.25) * mm});
            skLineSegment(sketch, "E4104", {"start": v(21.06, 14.25) * mm, "end": v(21.07, 14.23) * mm});
            skLineSegment(sketch, "E4105", {"start": v(21.07, 14.23) * mm, "end": v(21.07, 14.2) * mm});
            skLineSegment(sketch, "E4106", {"start": v(21.07, 14.2) * mm, "end": v(21.07, 14.2) * mm});
            skLineSegment(sketch, "E4107", {"start": v(21.07, 14.2) * mm, "end": v(21.07, 14.17) * mm});
            skLineSegment(sketch, "E4108", {"start": v(21.07, 14.17) * mm, "end": v(21.07, 14.16) * mm});
            skLineSegment(sketch, "E4109", {"start": v(21.07, 14.16) * mm, "end": v(21.06, 14.14) * mm});
            skLineSegment(sketch, "E4110", {"start": v(21.06, 14.14) * mm, "end": v(21.05, 14.13) * mm});
            skLineSegment(sketch, "E4111", {"start": v(21.05, 14.13) * mm, "end": v(21.03, 14.11) * mm});
            skLineSegment(sketch, "E4112", {"start": v(21.03, 14.11) * mm, "end": v(21.02, 14.1) * mm});
            skLineSegment(sketch, "E4113", {"start": v(21.02, 14.1) * mm, "end": v(21, 14.1) * mm});
            skLineSegment(sketch, "E4114", {"start": v(21, 14.1) * mm, "end": v(20.99, 14.08) * mm});
            skLineSegment(sketch, "E4115", {"start": v(20.99, 14.08) * mm, "end": v(20.97, 14.08) * mm});
            skLineSegment(sketch, "E4116", {"start": v(20.97, 14.08) * mm, "end": v(20.88, 14.03) * mm});
            skLineSegment(sketch, "E4117", {"start": v(20.88, 14.03) * mm, "end": v(20.79, 14) * mm});
            skLineSegment(sketch, "E4118", {"start": v(20.79, 14) * mm, "end": v(20.7, 13.95) * mm});
            skLineSegment(sketch, "E4119", {"start": v(20.7, 13.95) * mm, "end": v(20.6, 13.9) * mm});
            skLineSegment(sketch, "E4120", {"start": v(20.6, 13.9) * mm, "end": v(20.51, 13.87) * mm});
            skLineSegment(sketch, "E4121", {"start": v(20.51, 13.87) * mm, "end": v(20.42, 13.84) * mm});
            skLineSegment(sketch, "E4122", {"start": v(20.42, 13.84) * mm, "end": v(20.33, 13.8) * mm});
            skLineSegment(sketch, "E4123", {"start": v(20.33, 13.8) * mm, "end": v(20.25, 13.77) * mm});
            skLineSegment(sketch, "E4124", {"start": v(20.25, 13.77) * mm, "end": v(20.24, 13.76) * mm});
            skLineSegment(sketch, "E4125", {"start": v(20.24, 13.76) * mm, "end": v(20.23, 13.76) * mm});
            skLineSegment(sketch, "E4126", {"start": v(20.23, 13.76) * mm, "end": v(20.22, 13.76) * mm});
            skLineSegment(sketch, "E4127", {"start": v(20.22, 13.76) * mm, "end": v(20.21, 13.76) * mm});
            skLineSegment(sketch, "E4128", {"start": v(20.21, 13.76) * mm, "end": v(20.2, 13.75) * mm});
            skLineSegment(sketch, "E4129", {"start": v(20.2, 13.75) * mm, "end": v(20.2, 13.75) * mm});
            skLineSegment(sketch, "E4130", {"start": v(20.2, 13.75) * mm, "end": v(20.19, 13.75) * mm});
            skLineSegment(sketch, "E4131", {"start": v(20.19, 13.75) * mm, "end": v(20.18, 13.75) * mm});
            skLineSegment(sketch, "E4132", {"start": v(20.18, 13.75) * mm, "end": v(20.17, 13.75) * mm});
            skLineSegment(sketch, "E4133", {"start": v(20.17, 13.75) * mm, "end": v(20.15, 13.75) * mm});
            skLineSegment(sketch, "E4134", {"start": v(20.15, 13.75) * mm, "end": v(20.14, 13.76) * mm});
            skLineSegment(sketch, "E4135", {"start": v(20.14, 13.76) * mm, "end": v(20.12, 13.77) * mm});
            skLineSegment(sketch, "E4136", {"start": v(20.12, 13.77) * mm, "end": v(20.1, 13.78) * mm});
            skLineSegment(sketch, "E4137", {"start": v(20.1, 13.78) * mm, "end": v(20.08, 13.8) * mm});
            skLineSegment(sketch, "E4138", {"start": v(20.08, 13.8) * mm, "end": v(20.06, 13.83) * mm});
            skLineSegment(sketch, "E4139", {"start": v(20.06, 13.83) * mm, "end": v(20.03, 13.86) * mm});
            skLineSegment(sketch, "E4140", {"start": v(20.03, 13.86) * mm, "end": v(20, 13.92) * mm});
            skLineSegment(sketch, "E4141", {"start": v(20, 13.92) * mm, "end": v(19.95, 13.97) * mm});
            skLineSegment(sketch, "E4142", {"start": v(19.95, 13.97) * mm, "end": v(19.9, 14.03) * mm});
            skLineSegment(sketch, "E4143", {"start": v(19.9, 14.03) * mm, "end": v(19.87, 14.09) * mm});
            skLineSegment(sketch, "E4144", {"start": v(19.87, 14.09) * mm, "end": v(19.82, 14.15) * mm});
            skLineSegment(sketch, "E4145", {"start": v(19.82, 14.15) * mm, "end": v(19.78, 14.2) * mm});
            skLineSegment(sketch, "E4146", {"start": v(19.78, 14.2) * mm, "end": v(19.74, 14.26) * mm});
            skLineSegment(sketch, "E4147", {"start": v(19.74, 14.26) * mm, "end": v(19.7, 14.3) * mm});
            skLineSegment(sketch, "E4148", {"start": v(19.7, 14.3) * mm, "end": v(19.68, 14.32) * mm});
            skLineSegment(sketch, "E4149", {"start": v(19.68, 14.32) * mm, "end": v(19.67, 14.34) * mm});
            skLineSegment(sketch, "E4150", {"start": v(19.67, 14.34) * mm, "end": v(19.66, 14.35) * mm});
            skLineSegment(sketch, "E4151", {"start": v(19.66, 14.35) * mm, "end": v(19.65, 14.37) * mm});
            skLineSegment(sketch, "E4152", {"start": v(19.65, 14.37) * mm, "end": v(19.64, 14.38) * mm});
            skLineSegment(sketch, "E4153", {"start": v(19.64, 14.38) * mm, "end": v(19.63, 14.4) * mm});
            skLineSegment(sketch, "E4154", {"start": v(19.63, 14.4) * mm, "end": v(19.62, 14.41) * mm});
            skLineSegment(sketch, "E4155", {"start": v(19.62, 14.41) * mm, "end": v(19.6, 14.43) * mm});
            skLineSegment(sketch, "E4156", {"start": v(19.6, 14.43) * mm, "end": v(19.57, 14.47) * mm});
            skLineSegment(sketch, "E4157", {"start": v(19.57, 14.47) * mm, "end": v(19.53, 14.52) * mm});
            skLineSegment(sketch, "E4158", {"start": v(19.53, 14.52) * mm, "end": v(19.5, 14.57) * mm});
            skLineSegment(sketch, "E4159", {"start": v(19.5, 14.57) * mm, "end": v(19.46, 14.61) * mm});
            skLineSegment(sketch, "E4160", {"start": v(19.46, 14.61) * mm, "end": v(19.42, 14.65) * mm});
            skLineSegment(sketch, "E4161", {"start": v(19.42, 14.65) * mm, "end": v(19.38, 14.7) * mm});
            skLineSegment(sketch, "E4162", {"start": v(19.38, 14.7) * mm, "end": v(19.34, 14.74) * mm});
            skLineSegment(sketch, "E4163", {"start": v(19.34, 14.74) * mm, "end": v(19.3, 14.77) * mm});
            skLineSegment(sketch, "E4164", {"start": v(19.3, 14.77) * mm, "end": v(19.18, 14.86) * mm});
            skLineSegment(sketch, "E4165", {"start": v(19.18, 14.86) * mm, "end": v(19.07, 14.95) * mm});
            skLineSegment(sketch, "E4166", {"start": v(19.07, 14.95) * mm, "end": v(18.95, 15.03) * mm});
            skLineSegment(sketch, "E4167", {"start": v(18.95, 15.03) * mm, "end": v(18.84, 15.1) * mm});
            skLineSegment(sketch, "E4168", {"start": v(18.84, 15.1) * mm, "end": v(18.73, 15.17) * mm});
            skLineSegment(sketch, "E4169", {"start": v(18.73, 15.17) * mm, "end": v(18.62, 15.24) * mm});
            skLineSegment(sketch, "E4170", {"start": v(18.62, 15.24) * mm, "end": v(18.52, 15.3) * mm});
            skLineSegment(sketch, "E4171", {"start": v(18.52, 15.3) * mm, "end": v(18.43, 15.36) * mm});
            skLineSegment(sketch, "E4172", {"start": v(18.43, 15.36) * mm, "end": v(18.39, 15.39) * mm});
            skLineSegment(sketch, "E4173", {"start": v(18.39, 15.39) * mm, "end": v(18.36, 15.4) * mm});
            skLineSegment(sketch, "E4174", {"start": v(18.36, 15.4) * mm, "end": v(18.34, 15.41) * mm});
            skLineSegment(sketch, "E4175", {"start": v(18.34, 15.41) * mm, "end": v(18.33, 15.42) * mm});
            skLineSegment(sketch, "E4176", {"start": v(18.33, 15.42) * mm, "end": v(18.32, 15.43) * mm});
            skLineSegment(sketch, "E4177", {"start": v(18.32, 15.43) * mm, "end": v(18.32, 15.43) * mm});
            skLineSegment(sketch, "E4178", {"start": v(18.32, 15.43) * mm, "end": v(18.31, 15.43) * mm});
            skLineSegment(sketch, "E4179", {"start": v(18.31, 15.43) * mm, "end": v(18.31, 15.43) * mm});
            skLineSegment(sketch, "E4180", {"start": v(18.31, 15.43) * mm, "end": v(18.26, 15.44) * mm});
            skLineSegment(sketch, "E4181", {"start": v(18.26, 15.44) * mm, "end": v(18.21, 15.46) * mm});
            skLineSegment(sketch, "E4182", {"start": v(18.21, 15.46) * mm, "end": v(18.16, 15.47) * mm});
            skLineSegment(sketch, "E4183", {"start": v(18.16, 15.47) * mm, "end": v(18.12, 15.49) * mm});
            skLineSegment(sketch, "E4184", {"start": v(18.12, 15.49) * mm, "end": v(18.07, 15.5) * mm});
            skLineSegment(sketch, "E4185", {"start": v(18.07, 15.5) * mm, "end": v(18.04, 15.5) * mm});
            skLineSegment(sketch, "E4186", {"start": v(18.04, 15.5) * mm, "end": v(18, 15.52) * mm});
            skLineSegment(sketch, "E4187", {"start": v(18, 15.52) * mm, "end": v(17.98, 15.52) * mm});
            skLineSegment(sketch, "E4188", {"start": v(17.98, 15.52) * mm, "end": v(17.96, 15.53) * mm});
            skLineSegment(sketch, "E4189", {"start": v(17.96, 15.53) * mm, "end": v(17.93, 15.54) * mm});
            skLineSegment(sketch, "E4190", {"start": v(17.93, 15.54) * mm, "end": v(17.9, 15.55) * mm});
            skLineSegment(sketch, "E4191", {"start": v(17.9, 15.55) * mm, "end": v(17.85, 15.56) * mm});
            skLineSegment(sketch, "E4192", {"start": v(17.85, 15.56) * mm, "end": v(17.8, 15.58) * mm});
            skLineSegment(sketch, "E4193", {"start": v(17.8, 15.58) * mm, "end": v(17.76, 15.6) * mm});
            skLineSegment(sketch, "E4194", {"start": v(17.76, 15.6) * mm, "end": v(17.71, 15.6) * mm});
            skLineSegment(sketch, "E4195", {"start": v(17.71, 15.6) * mm, "end": v(17.66, 15.62) * mm});
            skLineSegment(sketch, "E4196", {"start": v(17.66, 15.62) * mm, "end": v(17.66, 15.62) * mm});
            skLineSegment(sketch, "E4197", {"start": v(17.66, 15.62) * mm, "end": v(17.65, 15.62) * mm});
            skLineSegment(sketch, "E4198", {"start": v(17.65, 15.62) * mm, "end": v(17.65, 15.62) * mm});
            skLineSegment(sketch, "E4199", {"start": v(17.65, 15.62) * mm, "end": v(17.63, 15.62) * mm});
            skLineSegment(sketch, "E4200", {"start": v(17.63, 15.62) * mm, "end": v(17.6, 15.62) * mm});
            skLineSegment(sketch, "E4201", {"start": v(17.6, 15.62) * mm, "end": v(17.58, 15.62) * mm});
            skLineSegment(sketch, "E4202", {"start": v(17.58, 15.62) * mm, "end": v(17.53, 15.63) * mm});
            skLineSegment(sketch, "E4203", {"start": v(17.53, 15.63) * mm, "end": v(17.41, 15.63) * mm});
            skLineSegment(sketch, "E4204", {"start": v(17.41, 15.63) * mm, "end": v(17.29, 15.63) * mm});
            skLineSegment(sketch, "E4205", {"start": v(17.29, 15.63) * mm, "end": v(17.16, 15.63) * mm});
            skLineSegment(sketch, "E4206", {"start": v(17.16, 15.63) * mm, "end": v(17.04, 15.63) * mm});
            skLineSegment(sketch, "E4207", {"start": v(17.04, 15.63) * mm, "end": v(16.92, 15.63) * mm});
            skLineSegment(sketch, "E4208", {"start": v(16.92, 15.63) * mm, "end": v(16.8, 15.63) * mm});
            skLineSegment(sketch, "E4209", {"start": v(16.8, 15.63) * mm, "end": v(16.67, 15.62) * mm});
            skLineSegment(sketch, "E4210", {"start": v(16.67, 15.62) * mm, "end": v(16.55, 15.62) * mm});
            skLineSegment(sketch, "E4211", {"start": v(16.55, 15.62) * mm, "end": v(16.52, 15.62) * mm});
            skLineSegment(sketch, "E4212", {"start": v(16.52, 15.62) * mm, "end": v(16.5, 15.61) * mm});
            skLineSegment(sketch, "E4213", {"start": v(16.5, 15.61) * mm, "end": v(16.48, 15.6) * mm});
            skLineSegment(sketch, "E4214", {"start": v(16.48, 15.6) * mm, "end": v(16.45, 15.6) * mm});
            skLineSegment(sketch, "E4215", {"start": v(16.45, 15.6) * mm, "end": v(16.43, 15.6) * mm});
            skLineSegment(sketch, "E4216", {"start": v(16.43, 15.6) * mm, "end": v(16.41, 15.58) * mm});
            skLineSegment(sketch, "E4217", {"start": v(16.41, 15.58) * mm, "end": v(16.4, 15.57) * mm});
            skLineSegment(sketch, "E4218", {"start": v(16.4, 15.57) * mm, "end": v(16.37, 15.56) * mm});
            skLineSegment(sketch, "E4219", {"start": v(16.37, 15.56) * mm, "end": v(16.36, 15.56) * mm});
            skLineSegment(sketch, "E4220", {"start": v(16.36, 15.56) * mm, "end": v(16.36, 15.55) * mm});
            skLineSegment(sketch, "E4221", {"start": v(16.36, 15.55) * mm, "end": v(16.36, 15.55) * mm});
            skLineSegment(sketch, "E4222", {"start": v(16.36, 15.55) * mm, "end": v(16.35, 15.55) * mm});
            skLineSegment(sketch, "E4223", {"start": v(16.35, 15.55) * mm, "end": v(16.35, 15.55) * mm});
            skLineSegment(sketch, "E4224", {"start": v(16.35, 15.55) * mm, "end": v(16.34, 15.55) * mm});
            skLineSegment(sketch, "E4225", {"start": v(16.34, 15.55) * mm, "end": v(16.33, 15.54) * mm});
            skLineSegment(sketch, "E4226", {"start": v(16.33, 15.54) * mm, "end": v(16.32, 15.54) * mm});
            skLineSegment(sketch, "E4227", {"start": v(16.32, 15.54) * mm, "end": v(16.31, 15.53) * mm});
            skLineSegment(sketch, "E4228", {"start": v(16.31, 15.53) * mm, "end": v(16.3, 15.52) * mm});
            skLineSegment(sketch, "E4229", {"start": v(16.3, 15.52) * mm, "end": v(16.29, 15.52) * mm});
            skLineSegment(sketch, "E4230", {"start": v(16.29, 15.52) * mm, "end": v(16.28, 15.51) * mm});
            skLineSegment(sketch, "E4231", {"start": v(16.28, 15.51) * mm, "end": v(16.27, 15.51) * mm});
            skLineSegment(sketch, "E4232", {"start": v(16.27, 15.51) * mm, "end": v(16.26, 15.5) * mm});
            skLineSegment(sketch, "E4233", {"start": v(16.26, 15.5) * mm, "end": v(16.25, 15.5) * mm});
            skLineSegment(sketch, "E4234", {"start": v(16.25, 15.5) * mm, "end": v(16.25, 15.5) * mm});
            skLineSegment(sketch, "E4235", {"start": v(16.25, 15.5) * mm, "end": v(16.24, 15.48) * mm});
            skLineSegment(sketch, "E4236", {"start": v(16.24, 15.48) * mm, "end": v(16.24, 15.48) * mm});
            skLineSegment(sketch, "E4237", {"start": v(16.24, 15.48) * mm, "end": v(16.24, 15.47) * mm});
            skLineSegment(sketch, "E4238", {"start": v(16.24, 15.47) * mm, "end": v(16.24, 15.46) * mm});
            skLineSegment(sketch, "E4239", {"start": v(16.24, 15.46) * mm, "end": v(16.24, 15.45) * mm});
            skLineSegment(sketch, "E4240", {"start": v(16.24, 15.45) * mm, "end": v(16.25, 15.44) * mm});
            skLineSegment(sketch, "E4241", {"start": v(16.25, 15.44) * mm, "end": v(16.26, 15.42) * mm});
            skLineSegment(sketch, "E4242", {"start": v(16.26, 15.42) * mm, "end": v(16.26, 15.4) * mm});
            skLineSegment(sketch, "E4243", {"start": v(16.26, 15.4) * mm, "end": v(16.27, 15.38) * mm});
            skLineSegment(sketch, "E4244", {"start": v(16.27, 15.38) * mm, "end": v(16.28, 15.35) * mm});
            skLineSegment(sketch, "E4245", {"start": v(16.28, 15.35) * mm, "end": v(16.3, 15.33) * mm});
            skLineSegment(sketch, "E4246", {"start": v(16.3, 15.33) * mm, "end": v(16.3, 15.3) * mm});
            skLineSegment(sketch, "E4247", {"start": v(16.3, 15.3) * mm, "end": v(16.32, 15.27) * mm});
            skLineSegment(sketch, "E4248", {"start": v(16.32, 15.27) * mm, "end": v(16.32, 15.27) * mm});
            skLineSegment(sketch, "E4249", {"start": v(16.32, 15.27) * mm, "end": v(16.32, 15.26) * mm});
            skLineSegment(sketch, "E4250", {"start": v(16.32, 15.26) * mm, "end": v(16.33, 15.26) * mm});
            skLineSegment(sketch, "E4251", {"start": v(16.33, 15.26) * mm, "end": v(16.33, 15.24) * mm});
            skLineSegment(sketch, "E4252", {"start": v(16.33, 15.24) * mm, "end": v(16.34, 15.23) * mm});
            skLineSegment(sketch, "E4253", {"start": v(16.34, 15.23) * mm, "end": v(16.35, 15.2) * mm});
            skLineSegment(sketch, "E4254", {"start": v(16.35, 15.2) * mm, "end": v(16.4, 15.1) * mm});
            skLineSegment(sketch, "E4255", {"start": v(16.4, 15.1) * mm, "end": v(16.44, 15) * mm});
            skLineSegment(sketch, "E4256", {"start": v(16.44, 15) * mm, "end": v(16.48, 14.9) * mm});
            skLineSegment(sketch, "E4257", {"start": v(16.48, 14.9) * mm, "end": v(16.52, 14.8) * mm});
            skLineSegment(sketch, "E4258", {"start": v(16.52, 14.8) * mm, "end": v(16.55, 14.7) * mm});
            skLineSegment(sketch, "E4259", {"start": v(16.55, 14.7) * mm, "end": v(16.58, 14.6) * mm});
            skLineSegment(sketch, "E4260", {"start": v(16.58, 14.6) * mm, "end": v(16.6, 14.5) * mm});
            skLineSegment(sketch, "E4261", {"start": v(16.6, 14.5) * mm, "end": v(16.6, 14.4) * mm});
            skLineSegment(sketch, "E4262", {"start": v(16.6, 14.4) * mm, "end": v(16.6, 14.37) * mm});
            skLineSegment(sketch, "E4263", {"start": v(16.6, 14.37) * mm, "end": v(16.61, 14.35) * mm});
            skLineSegment(sketch, "E4264", {"start": v(16.61, 14.35) * mm, "end": v(16.62, 14.34) * mm});
            skLineSegment(sketch, "E4265", {"start": v(16.62, 14.34) * mm, "end": v(16.62, 14.32) * mm});
            skLineSegment(sketch, "E4266", {"start": v(16.62, 14.32) * mm, "end": v(16.63, 14.3) * mm});
            skLineSegment(sketch, "E4267", {"start": v(16.63, 14.3) * mm, "end": v(16.64, 14.29) * mm});
            skLineSegment(sketch, "E4268", {"start": v(16.64, 14.29) * mm, "end": v(16.64, 14.28) * mm});
            skLineSegment(sketch, "E4269", {"start": v(16.64, 14.28) * mm, "end": v(16.65, 14.26) * mm});
            skLineSegment(sketch, "E4270", {"start": v(16.65, 14.26) * mm, "end": v(16.66, 14.24) * mm});
            skLineSegment(sketch, "E4271", {"start": v(16.66, 14.24) * mm, "end": v(16.67, 14.22) * mm});
            skLineSegment(sketch, "E4272", {"start": v(16.67, 14.22) * mm, "end": v(16.69, 14.2) * mm});
            skLineSegment(sketch, "E4273", {"start": v(16.69, 14.2) * mm, "end": v(16.7, 14.18) * mm});
            skLineSegment(sketch, "E4274", {"start": v(16.7, 14.18) * mm, "end": v(16.7, 14.16) * mm});
            skLineSegment(sketch, "E4275", {"start": v(16.7, 14.16) * mm, "end": v(16.72, 14.14) * mm});
            skLineSegment(sketch, "E4276", {"start": v(16.72, 14.14) * mm, "end": v(16.73, 14.11) * mm});
            skLineSegment(sketch, "E4277", {"start": v(16.73, 14.11) * mm, "end": v(16.75, 14.1) * mm});
            skLineSegment(sketch, "E4278", {"start": v(16.75, 14.1) * mm, "end": v(16.77, 14.05) * mm});
            skLineSegment(sketch, "E4279", {"start": v(16.77, 14.05) * mm, "end": v(16.79, 14.01) * mm});
            skLineSegment(sketch, "E4280", {"start": v(16.79, 14.01) * mm, "end": v(16.81, 13.98) * mm});
            skLineSegment(sketch, "E4281", {"start": v(16.81, 13.98) * mm, "end": v(16.83, 13.94) * mm});
            skLineSegment(sketch, "E4282", {"start": v(16.83, 13.94) * mm, "end": v(16.86, 13.9) * mm});
            skLineSegment(sketch, "E4283", {"start": v(16.86, 13.9) * mm, "end": v(16.88, 13.86) * mm});
            skLineSegment(sketch, "E4284", {"start": v(16.88, 13.86) * mm, "end": v(16.9, 13.81) * mm});
            skLineSegment(sketch, "E4285", {"start": v(16.9, 13.81) * mm, "end": v(16.92, 13.77) * mm});
            skLineSegment(sketch, "E4286", {"start": v(16.92, 13.77) * mm, "end": v(17.02, 13.58) * mm});
            skLineSegment(sketch, "E4287", {"start": v(17.02, 13.58) * mm, "end": v(17.13, 13.4) * mm});
            skLineSegment(sketch, "E4288", {"start": v(17.13, 13.4) * mm, "end": v(17.26, 13.24) * mm});
            skLineSegment(sketch, "E4289", {"start": v(17.26, 13.24) * mm, "end": v(17.4, 13.08) * mm});
            skLineSegment(sketch, "E4290", {"start": v(17.4, 13.08) * mm, "end": v(17.54, 12.93) * mm});
            skLineSegment(sketch, "E4291", {"start": v(17.54, 12.93) * mm, "end": v(17.7, 12.8) * mm});
            skLineSegment(sketch, "E4292", {"start": v(17.7, 12.8) * mm, "end": v(17.85, 12.66) * mm});
            skLineSegment(sketch, "E4293", {"start": v(17.85, 12.66) * mm, "end": v(18, 12.53) * mm});
            skLineSegment(sketch, "E4294", {"start": v(18, 12.53) * mm, "end": v(18.05, 12.5) * mm});
            skLineSegment(sketch, "E4295", {"start": v(18.05, 12.5) * mm, "end": v(18.1, 12.45) * mm});
            skLineSegment(sketch, "E4296", {"start": v(18.1, 12.45) * mm, "end": v(18.16, 12.42) * mm});
            skLineSegment(sketch, "E4297", {"start": v(18.16, 12.42) * mm, "end": v(18.21, 12.38) * mm});
            skLineSegment(sketch, "E4298", {"start": v(18.21, 12.38) * mm, "end": v(18.27, 12.34) * mm});
            skLineSegment(sketch, "E4299", {"start": v(18.27, 12.34) * mm, "end": v(18.32, 12.31) * mm});
            skLineSegment(sketch, "E4300", {"start": v(18.32, 12.31) * mm, "end": v(18.38, 12.28) * mm});
            skLineSegment(sketch, "E4301", {"start": v(18.38, 12.28) * mm, "end": v(18.43, 12.24) * mm});
            skLineSegment(sketch, "E4302", {"start": v(18.43, 12.24) * mm, "end": v(18.45, 12.23) * mm});
            skLineSegment(sketch, "E4303", {"start": v(18.45, 12.23) * mm, "end": v(18.48, 12.22) * mm});
            skLineSegment(sketch, "E4304", {"start": v(18.48, 12.22) * mm, "end": v(18.5, 12.2) * mm});
            skLineSegment(sketch, "E4305", {"start": v(18.5, 12.2) * mm, "end": v(18.52, 12.19) * mm});
            skLineSegment(sketch, "E4306", {"start": v(18.52, 12.19) * mm, "end": v(18.54, 12.18) * mm});
            skLineSegment(sketch, "E4307", {"start": v(18.54, 12.18) * mm, "end": v(18.56, 12.16) * mm});
            skLineSegment(sketch, "E4308", {"start": v(18.56, 12.16) * mm, "end": v(18.59, 12.15) * mm});
            skLineSegment(sketch, "E4309", {"start": v(18.59, 12.15) * mm, "end": v(18.6, 12.13) * mm});
            skLineSegment(sketch, "E4310", {"start": v(18.6, 12.13) * mm, "end": v(18.64, 12.1) * mm});
            skLineSegment(sketch, "E4311", {"start": v(18.64, 12.1) * mm, "end": v(18.67, 12.08) * mm});
            skLineSegment(sketch, "E4312", {"start": v(18.67, 12.08) * mm, "end": v(18.7, 12.05) * mm});
            skLineSegment(sketch, "E4313", {"start": v(18.7, 12.05) * mm, "end": v(18.7, 12.02) * mm});
            skLineSegment(sketch, "E4314", {"start": v(18.7, 12.02) * mm, "end": v(18.71, 12) * mm});
            skLineSegment(sketch, "E4315", {"start": v(18.71, 12) * mm, "end": v(18.7, 11.96) * mm});
            skLineSegment(sketch, "E4316", {"start": v(18.7, 11.96) * mm, "end": v(18.7, 11.93) * mm});
            skLineSegment(sketch, "E4317", {"start": v(18.7, 11.93) * mm, "end": v(18.68, 11.9) * mm});
            skLineSegment(sketch, "E4318", {"start": v(18.68, 11.9) * mm, "end": v(18.63, 11.8) * mm});
            skLineSegment(sketch, "E4319", {"start": v(18.63, 11.8) * mm, "end": v(18.58, 11.7) * mm});
            skLineSegment(sketch, "E4320", {"start": v(18.58, 11.7) * mm, "end": v(18.53, 11.6) * mm});
            skLineSegment(sketch, "E4321", {"start": v(18.53, 11.6) * mm, "end": v(18.48, 11.5) * mm});
            skLineSegment(sketch, "E4322", {"start": v(18.48, 11.5) * mm, "end": v(18.42, 11.4) * mm});
            skLineSegment(sketch, "E4323", {"start": v(18.42, 11.4) * mm, "end": v(18.37, 11.3) * mm});
            skLineSegment(sketch, "E4324", {"start": v(18.37, 11.3) * mm, "end": v(18.32, 11.2) * mm});
            skLineSegment(sketch, "E4325", {"start": v(18.32, 11.2) * mm, "end": v(18.26, 11.11) * mm});
            skLineSegment(sketch, "E4326", {"start": v(18.26, 11.11) * mm, "end": v(18.24, 11.08) * mm});
            skLineSegment(sketch, "E4327", {"start": v(18.24, 11.08) * mm, "end": v(18.22, 11.05) * mm});
            skLineSegment(sketch, "E4328", {"start": v(18.22, 11.05) * mm, "end": v(18.2, 11.04) * mm});
            skLineSegment(sketch, "E4329", {"start": v(18.2, 11.04) * mm, "end": v(18.18, 11.02) * mm});
            skLineSegment(sketch, "E4330", {"start": v(18.18, 11.02) * mm, "end": v(18.16, 11.02) * mm});
            skLineSegment(sketch, "E4331", {"start": v(18.16, 11.02) * mm, "end": v(18.15, 11.01) * mm});
            skLineSegment(sketch, "E4332", {"start": v(18.15, 11.01) * mm, "end": v(18.13, 11.01) * mm});
            skLineSegment(sketch, "E4333", {"start": v(18.13, 11.01) * mm, "end": v(18.12, 11.01) * mm});
            skLineSegment(sketch, "E4334", {"start": v(18.12, 11.01) * mm, "end": v(18.1, 11.01) * mm});
            skLineSegment(sketch, "E4335", {"start": v(18.1, 11.01) * mm, "end": v(18.09, 11.02) * mm});
            skLineSegment(sketch, "E4336", {"start": v(18.09, 11.02) * mm, "end": v(18.07, 11.02) * mm});
            skLineSegment(sketch, "E4337", {"start": v(18.07, 11.02) * mm, "end": v(18.05, 11.03) * mm});
            skLineSegment(sketch, "E4338", {"start": v(18.05, 11.03) * mm, "end": v(18.02, 11.04) * mm});
            skLineSegment(sketch, "E4339", {"start": v(18.02, 11.04) * mm, "end": v(18, 11.05) * mm});
            skLineSegment(sketch, "E4340", {"start": v(18, 11.05) * mm, "end": v(17.98, 11.07) * mm});
            skLineSegment(sketch, "E4341", {"start": v(17.98, 11.07) * mm, "end": v(17.96, 11.08) * mm});
            skLineSegment(sketch, "E4342", {"start": v(17.96, 11.08) * mm, "end": v(17.89, 11.13) * mm});
            skLineSegment(sketch, "E4343", {"start": v(17.89, 11.13) * mm, "end": v(17.81, 11.19) * mm});
            skLineSegment(sketch, "E4344", {"start": v(17.81, 11.19) * mm, "end": v(17.74, 11.24) * mm});
            skLineSegment(sketch, "E4345", {"start": v(17.74, 11.24) * mm, "end": v(17.66, 11.29) * mm});
            skLineSegment(sketch, "E4346", {"start": v(17.66, 11.29) * mm, "end": v(17.57, 11.34) * mm});
            skLineSegment(sketch, "E4347", {"start": v(17.57, 11.34) * mm, "end": v(17.49, 11.4) * mm});
            skLineSegment(sketch, "E4348", {"start": v(17.49, 11.4) * mm, "end": v(17.4, 11.45) * mm});
            skLineSegment(sketch, "E4349", {"start": v(17.4, 11.45) * mm, "end": v(17.3, 11.5) * mm});
            skLineSegment(sketch, "E4350", {"start": v(17.3, 11.5) * mm, "end": v(17.25, 11.53) * mm});
            skLineSegment(sketch, "E4351", {"start": v(17.25, 11.53) * mm, "end": v(17.2, 11.55) * mm});
            skLineSegment(sketch, "E4352", {"start": v(17.2, 11.55) * mm, "end": v(17.15, 11.57) * mm});
            skLineSegment(sketch, "E4353", {"start": v(17.15, 11.57) * mm, "end": v(17.1, 11.6) * mm});
            skLineSegment(sketch, "E4354", {"start": v(17.1, 11.6) * mm, "end": v(17.04, 11.61) * mm});
            skLineSegment(sketch, "E4355", {"start": v(17.04, 11.61) * mm, "end": v(16.98, 11.63) * mm});
            skLineSegment(sketch, "E4356", {"start": v(16.98, 11.63) * mm, "end": v(16.92, 11.65) * mm});
            skLineSegment(sketch, "E4357", {"start": v(16.92, 11.65) * mm, "end": v(16.86, 11.66) * mm});
            skLineSegment(sketch, "E4358", {"start": v(16.86, 11.66) * mm, "end": v(16.79, 11.69) * mm});
            skLineSegment(sketch, "E4359", {"start": v(16.79, 11.69) * mm, "end": v(16.73, 11.7) * mm});
            skLineSegment(sketch, "E4360", {"start": v(16.73, 11.7) * mm, "end": v(16.69, 11.72) * mm});
            skLineSegment(sketch, "E4361", {"start": v(16.69, 11.72) * mm, "end": v(16.66, 11.73) * mm});
            skLineSegment(sketch, "E4362", {"start": v(16.66, 11.73) * mm, "end": v(16.64, 11.73) * mm});
            skLineSegment(sketch, "E4363", {"start": v(16.64, 11.73) * mm, "end": v(16.63, 11.73) * mm});
            skLineSegment(sketch, "E4364", {"start": v(16.63, 11.73) * mm, "end": v(16.63, 11.73) * mm});
            skLineSegment(sketch, "E4365", {"start": v(16.63, 11.73) * mm, "end": v(16.55, 11.7) * mm});
            skLineSegment(sketch, "E4366", {"start": v(16.55, 11.7) * mm, "end": v(16.47, 11.66) * mm});
            skLineSegment(sketch, "E4367", {"start": v(16.47, 11.66) * mm, "end": v(16.4, 11.63) * mm});
            skLineSegment(sketch, "E4368", {"start": v(16.4, 11.63) * mm, "end": v(16.33, 11.6) * mm});
            skLineSegment(sketch, "E4369", {"start": v(16.33, 11.6) * mm, "end": v(16.27, 11.57) * mm});
            skLineSegment(sketch, "E4370", {"start": v(16.27, 11.57) * mm, "end": v(16.22, 11.55) * mm});
            skLineSegment(sketch, "E4371", {"start": v(16.22, 11.55) * mm, "end": v(16.19, 11.53) * mm});
            skLineSegment(sketch, "E4372", {"start": v(16.19, 11.53) * mm, "end": v(16.17, 11.52) * mm});
            skLineSegment(sketch, "E4373", {"start": v(16.17, 11.52) * mm, "end": v(16.16, 11.5) * mm});
            skLineSegment(sketch, "E4374", {"start": v(16.16, 11.5) * mm, "end": v(16.15, 11.5) * mm});
            skLineSegment(sketch, "E4375", {"start": v(16.15, 11.5) * mm, "end": v(16.15, 11.48) * mm});
            skLineSegment(sketch, "E4376", {"start": v(16.15, 11.48) * mm, "end": v(16.14, 11.47) * mm});
            skLineSegment(sketch, "E4377", {"start": v(16.14, 11.47) * mm, "end": v(16.15, 11.46) * mm});
            skLineSegment(sketch, "E4378", {"start": v(16.15, 11.46) * mm, "end": v(16.15, 11.45) * mm});
            skLineSegment(sketch, "E4379", {"start": v(16.15, 11.45) * mm, "end": v(16.16, 11.44) * mm});
            skLineSegment(sketch, "E4380", {"start": v(16.16, 11.44) * mm, "end": v(16.17, 11.43) * mm});
            skLineSegment(sketch, "E4381", {"start": v(16.17, 11.43) * mm, "end": v(16.19, 11.43) * mm});
            skLineSegment(sketch, "E4382", {"start": v(16.19, 11.43) * mm, "end": v(16.2, 11.42) * mm});
            skLineSegment(sketch, "E4383", {"start": v(16.2, 11.42) * mm, "end": v(16.22, 11.41) * mm});
            skLineSegment(sketch, "E4384", {"start": v(16.22, 11.41) * mm, "end": v(16.24, 11.4) * mm});
            skLineSegment(sketch, "E4385", {"start": v(16.24, 11.4) * mm, "end": v(16.25, 11.4) * mm});
            skLineSegment(sketch, "E4386", {"start": v(16.25, 11.4) * mm, "end": v(16.26, 11.39) * mm});
            skLineSegment(sketch, "E4387", {"start": v(16.26, 11.39) * mm, "end": v(16.28, 11.38) * mm});
            skLineSegment(sketch, "E4388", {"start": v(16.28, 11.38) * mm, "end": v(16.29, 11.38) * mm});
            skLineSegment(sketch, "E4389", {"start": v(16.29, 11.38) * mm, "end": v(16.29, 11.38) * mm});
            skLineSegment(sketch, "E4390", {"start": v(16.29, 11.38) * mm, "end": v(16.3, 11.37) * mm});
            skLineSegment(sketch, "E4391", {"start": v(16.3, 11.37) * mm, "end": v(16.3, 11.37) * mm});
            skLineSegment(sketch, "E4392", {"start": v(16.3, 11.37) * mm, "end": v(16.31, 11.36) * mm});
            skLineSegment(sketch, "E4393", {"start": v(16.31, 11.36) * mm, "end": v(16.32, 11.36) * mm});
            skLineSegment(sketch, "E4394", {"start": v(16.32, 11.36) * mm, "end": v(16.33, 11.36) * mm});
            skLineSegment(sketch, "E4395", {"start": v(16.33, 11.36) * mm, "end": v(16.34, 11.35) * mm});
            skLineSegment(sketch, "E4396", {"start": v(16.34, 11.35) * mm, "end": v(16.35, 11.35) * mm});
            skLineSegment(sketch, "E4397", {"start": v(16.35, 11.35) * mm, "end": v(16.35, 11.34) * mm});
            skLineSegment(sketch, "E4398", {"start": v(16.35, 11.34) * mm, "end": v(16.36, 11.34) * mm});
            skLineSegment(sketch, "E4399", {"start": v(16.36, 11.34) * mm, "end": v(16.36, 11.34) * mm});
            skLineSegment(sketch, "E4400", {"start": v(16.36, 11.34) * mm, "end": v(16.42, 11.28) * mm});
            skLineSegment(sketch, "E4401", {"start": v(16.42, 11.28) * mm, "end": v(16.46, 11.23) * mm});
            skLineSegment(sketch, "E4402", {"start": v(16.46, 11.23) * mm, "end": v(16.49, 11.2) * mm});
            skLineSegment(sketch, "E4403", {"start": v(16.49, 11.2) * mm, "end": v(16.5, 11.18) * mm});
            skLineSegment(sketch, "E4404", {"start": v(16.5, 11.18) * mm, "end": v(16.52, 11.17) * mm});
            skLineSegment(sketch, "E4405", {"start": v(16.52, 11.17) * mm, "end": v(16.53, 11.16) * mm});
            skLineSegment(sketch, "E4406", {"start": v(16.53, 11.16) * mm, "end": v(16.53, 11.16) * mm});
            skLineSegment(sketch, "E4407", {"start": v(16.53, 11.16) * mm, "end": v(16.61, 11.15) * mm});
            skLineSegment(sketch, "E4408", {"start": v(16.61, 11.15) * mm, "end": v(16.7, 11.14) * mm});
            skLineSegment(sketch, "E4409", {"start": v(16.7, 11.14) * mm, "end": v(16.77, 11.13) * mm});
            skLineSegment(sketch, "E4410", {"start": v(16.77, 11.13) * mm, "end": v(16.84, 11.12) * mm});
            skLineSegment(sketch, "E4411", {"start": v(16.84, 11.12) * mm, "end": v(16.9, 11.1) * mm});
            skLineSegment(sketch, "E4412", {"start": v(16.9, 11.1) * mm, "end": v(16.94, 11.1) * mm});
            skLineSegment(sketch, "E4413", {"start": v(16.94, 11.1) * mm, "end": v(16.98, 11.1) * mm});
            skLineSegment(sketch, "E4414", {"start": v(16.98, 11.1) * mm, "end": v(17, 11.1) * mm});
            skLineSegment(sketch, "E4415", {"start": v(17, 11.1) * mm, "end": v(17.02, 11.1) * mm});
            skLineSegment(sketch, "E4416", {"start": v(17.02, 11.1) * mm, "end": v(17.03, 11.09) * mm});
            skLineSegment(sketch, "E4417", {"start": v(17.03, 11.09) * mm, "end": v(17.06, 11.09) * mm});
            skLineSegment(sketch, "E4418", {"start": v(17.06, 11.09) * mm, "end": v(17.08, 11.08) * mm});
            skLineSegment(sketch, "E4419", {"start": v(17.08, 11.08) * mm, "end": v(17.11, 11.08) * mm});
            skLineSegment(sketch, "E4420", {"start": v(17.11, 11.08) * mm, "end": v(17.14, 11.07) * mm});
            skLineSegment(sketch, "E4421", {"start": v(17.14, 11.07) * mm, "end": v(17.17, 11.07) * mm});
            skLineSegment(sketch, "E4422", {"start": v(17.17, 11.07) * mm, "end": v(17.2, 11.07) * mm});
            skLineSegment(sketch, "E4423", {"start": v(17.2, 11.07) * mm, "end": v(17.2, 11.07) * mm});
            skLineSegment(sketch, "E4424", {"start": v(17.2, 11.07) * mm, "end": v(17.2, 11.06) * mm});
            skLineSegment(sketch, "E4425", {"start": v(17.2, 11.06) * mm, "end": v(17.2, 11.06) * mm});
            skLineSegment(sketch, "E4426", {"start": v(17.2, 11.06) * mm, "end": v(17.22, 11.05) * mm});
            skLineSegment(sketch, "E4427", {"start": v(17.22, 11.05) * mm, "end": v(17.23, 11.04) * mm});
            skLineSegment(sketch, "E4428", {"start": v(17.23, 11.04) * mm, "end": v(17.28, 11) * mm});
            skLineSegment(sketch, "E4429", {"start": v(17.28, 11) * mm, "end": v(17.31, 10.97) * mm});
            skLineSegment(sketch, "E4430", {"start": v(17.31, 10.97) * mm, "end": v(17.34, 10.95) * mm});
            skLineSegment(sketch, "E4431", {"start": v(17.34, 10.95) * mm, "end": v(17.36, 10.94) * mm});
            skLineSegment(sketch, "E4432", {"start": v(17.36, 10.94) * mm, "end": v(17.37, 10.93) * mm});
            skLineSegment(sketch, "E4433", {"start": v(17.37, 10.93) * mm, "end": v(17.37, 10.93) * mm});
            skLineSegment(sketch, "E4434", {"start": v(17.37, 10.93) * mm, "end": v(17.38, 10.92) * mm});
            skLineSegment(sketch, "E4435", {"start": v(17.38, 10.92) * mm, "end": v(17.38, 10.92) * mm});
            skLineSegment(sketch, "E4436", {"start": v(17.38, 10.92) * mm, "end": v(17.43, 10.87) * mm});
            skLineSegment(sketch, "E4437", {"start": v(17.43, 10.87) * mm, "end": v(17.48, 10.82) * mm});
            skLineSegment(sketch, "E4438", {"start": v(17.48, 10.82) * mm, "end": v(17.53, 10.77) * mm});
            skLineSegment(sketch, "E4439", {"start": v(17.53, 10.77) * mm, "end": v(17.57, 10.73) * mm});
            skLineSegment(sketch, "E4440", {"start": v(17.57, 10.73) * mm, "end": v(17.6, 10.7) * mm});
            skLineSegment(sketch, "E4441", {"start": v(17.6, 10.7) * mm, "end": v(17.63, 10.67) * mm});
            skLineSegment(sketch, "E4442", {"start": v(17.63, 10.67) * mm, "end": v(17.65, 10.65) * mm});
            skLineSegment(sketch, "E4443", {"start": v(17.65, 10.65) * mm, "end": v(17.65, 10.64) * mm});
            skLineSegment(sketch, "E4444", {"start": v(17.65, 10.64) * mm, "end": v(17.66, 10.64) * mm});
            skLineSegment(sketch, "E4445", {"start": v(17.66, 10.64) * mm, "end": v(17.67, 10.62) * mm});
            skLineSegment(sketch, "E4446", {"start": v(17.67, 10.62) * mm, "end": v(17.68, 10.6) * mm});
            skLineSegment(sketch, "E4447", {"start": v(17.68, 10.6) * mm, "end": v(17.7, 10.58) * mm});
            skLineSegment(sketch, "E4448", {"start": v(17.7, 10.58) * mm, "end": v(17.73, 10.56) * mm});
            skLineSegment(sketch, "E4449", {"start": v(17.73, 10.56) * mm, "end": v(17.76, 10.53) * mm});
            skLineSegment(sketch, "E4450", {"start": v(17.76, 10.53) * mm, "end": v(17.79, 10.5) * mm});
            skLineSegment(sketch, "E4451", {"start": v(17.79, 10.5) * mm, "end": v(17.82, 10.46) * mm});
            skLineSegment(sketch, "E4452", {"start": v(17.82, 10.46) * mm, "end": v(17.82, 10.46) * mm});
            skLineSegment(sketch, "E4453", {"start": v(17.82, 10.46) * mm, "end": v(17.82, 10.45) * mm});
            skLineSegment(sketch, "E4454", {"start": v(17.82, 10.45) * mm, "end": v(17.83, 10.44) * mm});
            skLineSegment(sketch, "E4455", {"start": v(17.83, 10.44) * mm, "end": v(17.84, 10.42) * mm});
            skLineSegment(sketch, "E4456", {"start": v(17.84, 10.42) * mm, "end": v(17.86, 10.4) * mm});
            skLineSegment(sketch, "E4457", {"start": v(17.86, 10.4) * mm, "end": v(17.88, 10.37) * mm});
            skLineSegment(sketch, "E4458", {"start": v(17.88, 10.37) * mm, "end": v(17.9, 10.35) * mm});
            skLineSegment(sketch, "E4459", {"start": v(17.9, 10.35) * mm, "end": v(17.9, 10.34) * mm});
            skLineSegment(sketch, "E4460", {"start": v(17.9, 10.34) * mm, "end": v(17.9, 10.32) * mm});
            skLineSegment(sketch, "E4461", {"start": v(17.9, 10.32) * mm, "end": v(17.91, 10.3) * mm});
            skLineSegment(sketch, "E4462", {"start": v(17.91, 10.3) * mm, "end": v(17.92, 10.29) * mm});
            skLineSegment(sketch, "E4463", {"start": v(17.92, 10.29) * mm, "end": v(17.92, 10.27) * mm});
            skLineSegment(sketch, "E4464", {"start": v(17.92, 10.27) * mm, "end": v(17.92, 10.25) * mm});
            skLineSegment(sketch, "E4465", {"start": v(17.92, 10.25) * mm, "end": v(17.92, 10.23) * mm});
            skLineSegment(sketch, "E4466", {"start": v(17.92, 10.23) * mm, "end": v(17.91, 10.22) * mm});
            skLineSegment(sketch, "E4467", {"start": v(17.91, 10.22) * mm, "end": v(17.9, 10.2) * mm});
            skLineSegment(sketch, "E4468", {"start": v(17.9, 10.2) * mm, "end": v(17.9, 10.19) * mm});
            skLineSegment(sketch, "E4469", {"start": v(17.9, 10.19) * mm, "end": v(17.88, 10.17) * mm});
            skLineSegment(sketch, "E4470", {"start": v(17.88, 10.17) * mm, "end": v(17.86, 10.16) * mm});
            skLineSegment(sketch, "E4471", {"start": v(17.86, 10.16) * mm, "end": v(17.84, 10.15) * mm});
            skLineSegment(sketch, "E4472", {"start": v(17.84, 10.15) * mm, "end": v(17.82, 10.14) * mm});
            skLineSegment(sketch, "E4473", {"start": v(17.82, 10.14) * mm, "end": v(17.8, 10.13) * mm});
            skLineSegment(sketch, "E4474", {"start": v(17.8, 10.13) * mm, "end": v(17.78, 10.12) * mm});
            skLineSegment(sketch, "E4475", {"start": v(17.78, 10.12) * mm, "end": v(17.77, 10.12) * mm});
            skLineSegment(sketch, "E4476", {"start": v(17.77, 10.12) * mm, "end": v(17.76, 10.12) * mm});
            skLineSegment(sketch, "E4477", {"start": v(17.76, 10.12) * mm, "end": v(17.76, 10.11) * mm});
            skLineSegment(sketch, "E4478", {"start": v(17.76, 10.11) * mm, "end": v(17.75, 10.11) * mm});
            skLineSegment(sketch, "E4479", {"start": v(17.75, 10.11) * mm, "end": v(17.75, 10.11) * mm});
            skLineSegment(sketch, "E4480", {"start": v(17.75, 10.11) * mm, "end": v(17.73, 10.1) * mm});
            skLineSegment(sketch, "E4481", {"start": v(17.73, 10.1) * mm, "end": v(17.7, 10.1) * mm});
            skLineSegment(sketch, "E4482", {"start": v(17.7, 10.1) * mm, "end": v(17.7, 10.08) * mm});
            skLineSegment(sketch, "E4483", {"start": v(17.7, 10.08) * mm, "end": v(17.67, 10.08) * mm});
            skLineSegment(sketch, "E4484", {"start": v(17.67, 10.08) * mm, "end": v(17.66, 10.07) * mm});
            skLineSegment(sketch, "E4485", {"start": v(17.66, 10.07) * mm, "end": v(17.65, 10.06) * mm});
            skLineSegment(sketch, "E4486", {"start": v(17.65, 10.06) * mm, "end": v(17.64, 10.06) * mm});
            skLineSegment(sketch, "E4487", {"start": v(17.64, 10.06) * mm, "end": v(17.63, 10.06) * mm});
            skLineSegment(sketch, "E4488", {"start": v(17.63, 10.06) * mm, "end": v(17.61, 10.05) * mm});
            skLineSegment(sketch, "E4489", {"start": v(17.61, 10.05) * mm, "end": v(17.58, 10.03) * mm});
            skLineSegment(sketch, "E4490", {"start": v(17.58, 10.03) * mm, "end": v(17.53, 10.01) * mm});
            skLineSegment(sketch, "E4491", {"start": v(17.53, 10.01) * mm, "end": v(17.46, 9.98) * mm});
            skLineSegment(sketch, "E4492", {"start": v(17.46, 9.98) * mm, "end": v(17.38, 9.95) * mm});
            skLineSegment(sketch, "E4493", {"start": v(17.38, 9.95) * mm, "end": v(17.3, 9.91) * mm});
            skLineSegment(sketch, "E4494", {"start": v(17.3, 9.91) * mm, "end": v(17.2, 9.87) * mm});
            skLineSegment(sketch, "E4495", {"start": v(17.2, 9.87) * mm, "end": v(17.09, 9.83) * mm});
            skLineSegment(sketch, "E4496", {"start": v(17.09, 9.83) * mm, "end": v(17.09, 9.83) * mm});
            skLineSegment(sketch, "E4497", {"start": v(17.09, 9.83) * mm, "end": v(17.08, 9.83) * mm});
            skLineSegment(sketch, "E4498", {"start": v(17.08, 9.83) * mm, "end": v(17.07, 9.83) * mm});
            skLineSegment(sketch, "E4499", {"start": v(17.07, 9.83) * mm, "end": v(17.05, 9.83) * mm});
            skLineSegment(sketch, "E4500", {"start": v(17.05, 9.83) * mm, "end": v(17.01, 9.83) * mm});
            skLineSegment(sketch, "E4501", {"start": v(17.01, 9.83) * mm, "end": v(16.96, 9.83) * mm});
            skLineSegment(sketch, "E4502", {"start": v(16.96, 9.83) * mm, "end": v(16.88, 9.83) * mm});
            skLineSegment(sketch, "E4503", {"start": v(16.88, 9.83) * mm, "end": v(16.77, 9.83) * mm});
            skLineSegment(sketch, "E4504", {"start": v(16.77, 9.83) * mm, "end": v(16.73, 9.83) * mm});
            skLineSegment(sketch, "E4505", {"start": v(16.73, 9.83) * mm, "end": v(16.68, 9.83) * mm});
            skLineSegment(sketch, "E4506", {"start": v(16.68, 9.83) * mm, "end": v(16.63, 9.83) * mm});
            skLineSegment(sketch, "E4507", {"start": v(16.63, 9.83) * mm, "end": v(16.59, 9.84) * mm});
            skLineSegment(sketch, "E4508", {"start": v(16.59, 9.84) * mm, "end": v(16.54, 9.85) * mm});
            skLineSegment(sketch, "E4509", {"start": v(16.54, 9.85) * mm, "end": v(16.5, 9.86) * mm});
            skLineSegment(sketch, "E4510", {"start": v(16.5, 9.86) * mm, "end": v(16.45, 9.87) * mm});
            skLineSegment(sketch, "E4511", {"start": v(16.45, 9.87) * mm, "end": v(16.4, 9.88) * mm});
            skLineSegment(sketch, "E4512", {"start": v(16.4, 9.88) * mm, "end": v(16.23, 9.93) * mm});
            skLineSegment(sketch, "E4513", {"start": v(16.23, 9.93) * mm, "end": v(16.06, 9.98) * mm});
            skLineSegment(sketch, "E4514", {"start": v(16.06, 9.98) * mm, "end": v(15.9, 10.04) * mm});
            skLineSegment(sketch, "E4515", {"start": v(15.9, 10.04) * mm, "end": v(15.74, 10.1) * mm});
            skLineSegment(sketch, "E4516", {"start": v(15.74, 10.1) * mm, "end": v(15.6, 10.16) * mm});
            skLineSegment(sketch, "E4517", {"start": v(15.6, 10.16) * mm, "end": v(15.45, 10.23) * mm});
            skLineSegment(sketch, "E4518", {"start": v(15.45, 10.23) * mm, "end": v(15.32, 10.32) * mm});
            skLineSegment(sketch, "E4519", {"start": v(15.32, 10.32) * mm, "end": v(15.18, 10.4) * mm});
            skLineSegment(sketch, "E4520", {"start": v(15.18, 10.4) * mm, "end": v(15.18, 10.41) * mm});
            skLineSegment(sketch, "E4521", {"start": v(15.18, 10.41) * mm, "end": v(15.17, 10.42) * mm});
            skLineSegment(sketch, "E4522", {"start": v(15.17, 10.42) * mm, "end": v(15.16, 10.42) * mm});
            skLineSegment(sketch, "E4523", {"start": v(15.16, 10.42) * mm, "end": v(15.15, 10.43) * mm});
            skLineSegment(sketch, "E4524", {"start": v(15.15, 10.43) * mm, "end": v(15.14, 10.43) * mm});
            skLineSegment(sketch, "E4525", {"start": v(15.14, 10.43) * mm, "end": v(15.13, 10.44) * mm});
            skLineSegment(sketch, "E4526", {"start": v(15.13, 10.44) * mm, "end": v(15.12, 10.44) * mm});
            skLineSegment(sketch, "E4527", {"start": v(15.12, 10.44) * mm, "end": v(15.12, 10.45) * mm});
            skLineSegment(sketch, "E4528", {"start": v(15.12, 10.45) * mm, "end": v(15.1, 10.45) * mm});
            skLineSegment(sketch, "E4529", {"start": v(15.1, 10.45) * mm, "end": v(15.1, 10.46) * mm});
            skLineSegment(sketch, "E4530", {"start": v(15.1, 10.46) * mm, "end": v(15.09, 10.46) * mm});
            skLineSegment(sketch, "E4531", {"start": v(15.09, 10.46) * mm, "end": v(15.08, 10.47) * mm});
            skLineSegment(sketch, "E4532", {"start": v(15.08, 10.47) * mm, "end": v(15.07, 10.48) * mm});
            skLineSegment(sketch, "E4533", {"start": v(15.07, 10.48) * mm, "end": v(15.06, 10.48) * mm});
            skLineSegment(sketch, "E4534", {"start": v(15.06, 10.48) * mm, "end": v(15.05, 10.49) * mm});
            skLineSegment(sketch, "E4535", {"start": v(15.05, 10.49) * mm, "end": v(15.05, 10.5) * mm});
            skLineSegment(sketch, "E4536", {"start": v(15.05, 10.5) * mm, "end": v(15.02, 10.52) * mm});
            skLineSegment(sketch, "E4537", {"start": v(15.02, 10.52) * mm, "end": v(15, 10.55) * mm});
            skLineSegment(sketch, "E4538", {"start": v(15, 10.55) * mm, "end": v(14.97, 10.57) * mm});
            skLineSegment(sketch, "E4539", {"start": v(14.97, 10.57) * mm, "end": v(14.95, 10.6) * mm});
            skLineSegment(sketch, "E4540", {"start": v(14.95, 10.6) * mm, "end": v(14.93, 10.62) * mm});
            skLineSegment(sketch, "E4541", {"start": v(14.93, 10.62) * mm, "end": v(14.9, 10.65) * mm});
            skLineSegment(sketch, "E4542", {"start": v(14.9, 10.65) * mm, "end": v(14.88, 10.68) * mm});
            skLineSegment(sketch, "E4543", {"start": v(14.88, 10.68) * mm, "end": v(14.85, 10.7) * mm});
            skLineSegment(sketch, "E4544", {"start": v(14.85, 10.7) * mm, "end": v(14.83, 10.74) * mm});
            skLineSegment(sketch, "E4545", {"start": v(14.83, 10.74) * mm, "end": v(14.8, 10.77) * mm});
            skLineSegment(sketch, "E4546", {"start": v(14.8, 10.77) * mm, "end": v(14.77, 10.8) * mm});
            skLineSegment(sketch, "E4547", {"start": v(14.77, 10.8) * mm, "end": v(14.74, 10.83) * mm});
            skLineSegment(sketch, "E4548", {"start": v(14.74, 10.83) * mm, "end": v(14.71, 10.86) * mm});
            skLineSegment(sketch, "E4549", {"start": v(14.71, 10.86) * mm, "end": v(14.68, 10.9) * mm});
            skLineSegment(sketch, "E4550", {"start": v(14.68, 10.9) * mm, "end": v(14.65, 10.92) * mm});
            skLineSegment(sketch, "E4551", {"start": v(14.65, 10.92) * mm, "end": v(14.62, 10.95) * mm});
            skLineSegment(sketch, "E4552", {"start": v(14.62, 10.95) * mm, "end": v(14.6, 10.98) * mm});
            skLineSegment(sketch, "E4553", {"start": v(14.6, 10.98) * mm, "end": v(14.58, 11) * mm});
            skLineSegment(sketch, "E4554", {"start": v(14.58, 11) * mm, "end": v(14.56, 11) * mm});
            skLineSegment(sketch, "E4555", {"start": v(14.56, 11) * mm, "end": v(14.53, 11.02) * mm});
            skLineSegment(sketch, "E4556", {"start": v(14.53, 11.02) * mm, "end": v(14.51, 11.02) * mm});
            skLineSegment(sketch, "E4557", {"start": v(14.51, 11.02) * mm, "end": v(14.5, 11.03) * mm});
            skLineSegment(sketch, "E4558", {"start": v(14.5, 11.03) * mm, "end": v(14.48, 11.03) * mm});
            skLineSegment(sketch, "E4559", {"start": v(14.48, 11.03) * mm, "end": v(14.46, 11.03) * mm});
            skLineSegment(sketch, "E4560", {"start": v(14.46, 11.03) * mm, "end": v(14.43, 11.03) * mm});
            skLineSegment(sketch, "E4561", {"start": v(14.43, 11.03) * mm, "end": v(14.4, 11.02) * mm});
            skLineSegment(sketch, "E4562", {"start": v(14.4, 11.02) * mm, "end": v(14.37, 11) * mm});
            skLineSegment(sketch, "E4563", {"start": v(14.37, 11) * mm, "end": v(14.34, 11) * mm});
            skLineSegment(sketch, "E4564", {"start": v(14.34, 11) * mm, "end": v(14.32, 10.97) * mm});
            skLineSegment(sketch, "E4565", {"start": v(14.32, 10.97) * mm, "end": v(14.3, 10.95) * mm});
            skLineSegment(sketch, "E4566", {"start": v(14.3, 10.95) * mm, "end": v(14.27, 10.93) * mm});
            skLineSegment(sketch, "E4567", {"start": v(14.27, 10.93) * mm, "end": v(14.25, 10.9) * mm});
            skLineSegment(sketch, "E4568", {"start": v(14.25, 10.9) * mm, "end": v(14.24, 10.88) * mm});
            skLineSegment(sketch, "E4569", {"start": v(14.24, 10.88) * mm, "end": v(14.24, 10.87) * mm});
            skLineSegment(sketch, "E4570", {"start": v(14.24, 10.87) * mm, "end": v(14.23, 10.85) * mm});
            skLineSegment(sketch, "E4571", {"start": v(14.23, 10.85) * mm, "end": v(14.23, 10.82) * mm});
            skLineSegment(sketch, "E4572", {"start": v(14.23, 10.82) * mm, "end": v(14.24, 10.79) * mm});
            skLineSegment(sketch, "E4573", {"start": v(14.24, 10.79) * mm, "end": v(14.25, 10.74) * mm});
            skLineSegment(sketch, "E4574", {"start": v(14.25, 10.74) * mm, "end": v(14.28, 10.7) * mm});
            skLineSegment(sketch, "E4575", {"start": v(14.28, 10.7) * mm, "end": v(14.31, 10.64) * mm});
            skLineSegment(sketch, "E4576", {"start": v(14.31, 10.64) * mm, "end": v(14.32, 10.62) * mm});
            skLineSegment(sketch, "E4577", {"start": v(14.32, 10.62) * mm, "end": v(14.33, 10.61) * mm});
            skLineSegment(sketch, "E4578", {"start": v(14.33, 10.61) * mm, "end": v(14.35, 10.6) * mm});
            skLineSegment(sketch, "E4579", {"start": v(14.35, 10.6) * mm, "end": v(14.36, 10.6) * mm});
            skLineSegment(sketch, "E4580", {"start": v(14.36, 10.6) * mm, "end": v(14.37, 10.59) * mm});
            skLineSegment(sketch, "E4581", {"start": v(14.37, 10.59) * mm, "end": v(14.38, 10.58) * mm});
            skLineSegment(sketch, "E4582", {"start": v(14.38, 10.58) * mm, "end": v(14.4, 10.57) * mm});
            skLineSegment(sketch, "E4583", {"start": v(14.4, 10.57) * mm, "end": v(14.4, 10.57) * mm});
            skLineSegment(sketch, "E4584", {"start": v(14.4, 10.57) * mm, "end": v(14.41, 10.56) * mm});
            skLineSegment(sketch, "E4585", {"start": v(14.41, 10.56) * mm, "end": v(14.43, 10.55) * mm});
            skLineSegment(sketch, "E4586", {"start": v(14.43, 10.55) * mm, "end": v(14.44, 10.52) * mm});
            skLineSegment(sketch, "E4587", {"start": v(14.44, 10.52) * mm, "end": v(14.47, 10.5) * mm});
            skLineSegment(sketch, "E4588", {"start": v(14.47, 10.5) * mm, "end": v(14.5, 10.46) * mm});
            skLineSegment(sketch, "E4589", {"start": v(14.5, 10.46) * mm, "end": v(14.53, 10.42) * mm});
            skLineSegment(sketch, "E4590", {"start": v(14.53, 10.42) * mm, "end": v(14.56, 10.38) * mm});
            skLineSegment(sketch, "E4591", {"start": v(14.56, 10.38) * mm, "end": v(14.6, 10.33) * mm});
            skLineSegment(sketch, "E4592", {"start": v(14.6, 10.33) * mm, "end": v(14.6, 10.33) * mm});
            skLineSegment(sketch, "E4593", {"start": v(14.6, 10.33) * mm, "end": v(14.61, 10.32) * mm});
            skLineSegment(sketch, "E4594", {"start": v(14.61, 10.32) * mm, "end": v(14.63, 10.32) * mm});
            skLineSegment(sketch, "E4595", {"start": v(14.63, 10.32) * mm, "end": v(14.65, 10.3) * mm});
            skLineSegment(sketch, "E4596", {"start": v(14.65, 10.3) * mm, "end": v(14.67, 10.29) * mm});
            skLineSegment(sketch, "E4597", {"start": v(14.67, 10.29) * mm, "end": v(14.71, 10.27) * mm});
            skLineSegment(sketch, "E4598", {"start": v(14.71, 10.27) * mm, "end": v(14.75, 10.25) * mm});
            skLineSegment(sketch, "E4599", {"start": v(14.75, 10.25) * mm, "end": v(14.78, 10.22) * mm});
            skLineSegment(sketch, "E4600", {"start": v(14.78, 10.22) * mm, "end": v(14.8, 10.2) * mm});
            skLineSegment(sketch, "E4601", {"start": v(14.8, 10.2) * mm, "end": v(14.84, 10.18) * mm});
            skLineSegment(sketch, "E4602", {"start": v(14.84, 10.18) * mm, "end": v(14.86, 10.16) * mm});
            skLineSegment(sketch, "E4603", {"start": v(14.86, 10.16) * mm, "end": v(14.88, 10.14) * mm});
            skLineSegment(sketch, "E4604", {"start": v(14.88, 10.14) * mm, "end": v(14.9, 10.1) * mm});
            skLineSegment(sketch, "E4605", {"start": v(14.9, 10.1) * mm, "end": v(14.92, 10.08) * mm});
            skLineSegment(sketch, "E4606", {"start": v(14.92, 10.08) * mm, "end": v(14.93, 10.06) * mm});
            skLineSegment(sketch, "E4607", {"start": v(14.93, 10.06) * mm, "end": v(14.93, 10.05) * mm});
            skLineSegment(sketch, "E4608", {"start": v(14.93, 10.05) * mm, "end": v(14.93, 10.05) * mm});
            skLineSegment(sketch, "E4609", {"start": v(14.93, 10.05) * mm, "end": v(14.94, 10.04) * mm});
            skLineSegment(sketch, "E4610", {"start": v(14.94, 10.04) * mm, "end": v(14.94, 10.04) * mm});
            skLineSegment(sketch, "E4611", {"start": v(14.94, 10.04) * mm, "end": v(14.95, 10.03) * mm});
            skLineSegment(sketch, "E4612", {"start": v(14.95, 10.03) * mm, "end": v(14.96, 10.02) * mm});
            skLineSegment(sketch, "E4613", {"start": v(14.96, 10.02) * mm, "end": v(14.97, 10.02) * mm});
            skLineSegment(sketch, "E4614", {"start": v(14.97, 10.02) * mm, "end": v(14.99, 10.01) * mm});
            skLineSegment(sketch, "E4615", {"start": v(14.99, 10.01) * mm, "end": v(15, 10) * mm});
            skLineSegment(sketch, "E4616", {"start": v(15, 10) * mm, "end": v(15, 10) * mm});
            skLineSegment(sketch, "E4617", {"start": v(15, 10) * mm, "end": v(15.02, 10) * mm});
            skLineSegment(sketch, "E4618", {"start": v(15.02, 10) * mm, "end": v(15.02, 10) * mm});
            skLineSegment(sketch, "E4619", {"start": v(15.02, 10) * mm, "end": v(15.03, 9.99) * mm});
            skLineSegment(sketch, "E4620", {"start": v(15.03, 9.99) * mm, "end": v(15.04, 9.98) * mm});
            skLineSegment(sketch, "E4621", {"start": v(15.04, 9.98) * mm, "end": v(15.05, 9.98) * mm});
            skLineSegment(sketch, "E4622", {"start": v(15.05, 9.98) * mm, "end": v(15.07, 9.97) * mm});
            skLineSegment(sketch, "E4623", {"start": v(15.07, 9.97) * mm, "end": v(15.08, 9.96) * mm});
            skLineSegment(sketch, "E4624", {"start": v(15.08, 9.96) * mm, "end": v(15.1, 9.95) * mm});
            skLineSegment(sketch, "E4625", {"start": v(15.1, 9.95) * mm, "end": v(15.11, 9.94) * mm});
            skLineSegment(sketch, "E4626", {"start": v(15.11, 9.94) * mm, "end": v(15.13, 9.93) * mm});
            skLineSegment(sketch, "E4627", {"start": v(15.13, 9.93) * mm, "end": v(15.13, 9.93) * mm});
            skLineSegment(sketch, "E4628", {"start": v(15.13, 9.93) * mm, "end": v(15.14, 9.92) * mm});
            skLineSegment(sketch, "E4629", {"start": v(15.14, 9.92) * mm, "end": v(15.15, 9.92) * mm});
            skLineSegment(sketch, "E4630", {"start": v(15.15, 9.92) * mm, "end": v(15.15, 9.91) * mm});
            skLineSegment(sketch, "E4631", {"start": v(15.15, 9.91) * mm, "end": v(15.17, 9.9) * mm});
            skLineSegment(sketch, "E4632", {"start": v(15.17, 9.9) * mm, "end": v(15.19, 9.89) * mm});
            skLineSegment(sketch, "E4633", {"start": v(15.19, 9.89) * mm, "end": v(15.2, 9.87) * mm});
            skLineSegment(sketch, "E4634", {"start": v(15.2, 9.87) * mm, "end": v(15.23, 9.86) * mm});
            skLineSegment(sketch, "E4635", {"start": v(15.23, 9.86) * mm, "end": v(15.25, 9.84) * mm});
            skLineSegment(sketch, "E4636", {"start": v(15.25, 9.84) * mm, "end": v(15.27, 9.83) * mm});
            skLineSegment(sketch, "E4637", {"start": v(15.27, 9.83) * mm, "end": v(15.29, 9.8) * mm});
            skLineSegment(sketch, "E4638", {"start": v(15.29, 9.8) * mm, "end": v(15.3, 9.8) * mm});
            skLineSegment(sketch, "E4639", {"start": v(15.3, 9.8) * mm, "end": v(15.33, 9.78) * mm});
            skLineSegment(sketch, "E4640", {"start": v(15.33, 9.78) * mm, "end": v(15.37, 9.75) * mm});
            skLineSegment(sketch, "E4641", {"start": v(15.37, 9.75) * mm, "end": v(15.4, 9.71) * mm});
            skLineSegment(sketch, "E4642", {"start": v(15.4, 9.71) * mm, "end": v(15.45, 9.68) * mm});
            skLineSegment(sketch, "E4643", {"start": v(15.45, 9.68) * mm, "end": v(15.5, 9.65) * mm});
            skLineSegment(sketch, "E4644", {"start": v(15.5, 9.65) * mm, "end": v(15.54, 9.62) * mm});
            skLineSegment(sketch, "E4645", {"start": v(15.54, 9.62) * mm, "end": v(15.58, 9.59) * mm});
            skLineSegment(sketch, "E4646", {"start": v(15.58, 9.59) * mm, "end": v(15.63, 9.56) * mm});
            skLineSegment(sketch, "E4647", {"start": v(15.63, 9.56) * mm, "end": v(15.67, 9.53) * mm});
            skLineSegment(sketch, "E4648", {"start": v(15.67, 9.53) * mm, "end": v(15.78, 9.48) * mm});
            skLineSegment(sketch, "E4649", {"start": v(15.78, 9.48) * mm, "end": v(15.9, 9.43) * mm});
            skLineSegment(sketch, "E4650", {"start": v(15.9, 9.43) * mm, "end": v(16, 9.38) * mm});
            skLineSegment(sketch, "E4651", {"start": v(16, 9.38) * mm, "end": v(16.13, 9.35) * mm});
            skLineSegment(sketch, "E4652", {"start": v(16.13, 9.35) * mm, "end": v(16.24, 9.32) * mm});
            skLineSegment(sketch, "E4653", {"start": v(16.24, 9.32) * mm, "end": v(16.36, 9.3) * mm});
            skLineSegment(sketch, "E4654", {"start": v(16.36, 9.3) * mm, "end": v(16.48, 9.27) * mm});
            skLineSegment(sketch, "E4655", {"start": v(16.48, 9.27) * mm, "end": v(16.6, 9.26) * mm});
            skLineSegment(sketch, "E4656", {"start": v(16.6, 9.26) * mm, "end": v(16.62, 9.26) * mm});
            skLineSegment(sketch, "E4657", {"start": v(16.62, 9.26) * mm, "end": v(16.64, 9.26) * mm});
            skLineSegment(sketch, "E4658", {"start": v(16.64, 9.26) * mm, "end": v(16.66, 9.26) * mm});
            skLineSegment(sketch, "E4659", {"start": v(16.66, 9.26) * mm, "end": v(16.68, 9.25) * mm});
            skLineSegment(sketch, "E4660", {"start": v(16.68, 9.25) * mm, "end": v(16.7, 9.25) * mm});
            skLineSegment(sketch, "E4661", {"start": v(16.7, 9.25) * mm, "end": v(16.72, 9.25) * mm});
            skLineSegment(sketch, "E4662", {"start": v(16.72, 9.25) * mm, "end": v(16.74, 9.24) * mm});
            skLineSegment(sketch, "E4663", {"start": v(16.74, 9.24) * mm, "end": v(16.76, 9.24) * mm});
            skLineSegment(sketch, "E4664", {"start": v(16.76, 9.24) * mm, "end": v(16.8, 9.23) * mm});
            skLineSegment(sketch, "E4665", {"start": v(16.8, 9.23) * mm, "end": v(16.85, 9.23) * mm});
            skLineSegment(sketch, "E4666", {"start": v(16.85, 9.23) * mm, "end": v(16.9, 9.22) * mm});
            skLineSegment(sketch, "E4667", {"start": v(16.9, 9.22) * mm, "end": v(16.95, 9.22) * mm});
            skLineSegment(sketch, "E4668", {"start": v(16.95, 9.22) * mm, "end": v(17, 9.22) * mm});
            skLineSegment(sketch, "E4669", {"start": v(17, 9.22) * mm, "end": v(17.03, 9.22) * mm});
            skLineSegment(sketch, "E4670", {"start": v(17.03, 9.22) * mm, "end": v(17.07, 9.22) * mm});
            skLineSegment(sketch, "E4671", {"start": v(17.07, 9.22) * mm, "end": v(17.11, 9.23) * mm});
            skLineSegment(sketch, "E4672", {"start": v(17.11, 9.23) * mm, "end": v(17.2, 9.26) * mm});
            skLineSegment(sketch, "E4673", {"start": v(17.2, 9.26) * mm, "end": v(17.25, 9.27) * mm});
            skLineSegment(sketch, "E4674", {"start": v(17.25, 9.27) * mm, "end": v(17.3, 9.29) * mm});
            skLineSegment(sketch, "E4675", {"start": v(17.3, 9.29) * mm, "end": v(17.32, 9.3) * mm});
            skLineSegment(sketch, "E4676", {"start": v(17.32, 9.3) * mm, "end": v(17.34, 9.3) * mm});
            skLineSegment(sketch, "E4677", {"start": v(17.34, 9.3) * mm, "end": v(17.34, 9.3) * mm});
            skLineSegment(sketch, "E4678", {"start": v(17.34, 9.3) * mm, "end": v(17.35, 9.3) * mm});
            skLineSegment(sketch, "E4679", {"start": v(17.35, 9.3) * mm, "end": v(17.35, 9.3) * mm});
            skLineSegment(sketch, "E4680", {"start": v(17.35, 9.3) * mm, "end": v(17.44, 9.35) * mm});
            skLineSegment(sketch, "E4681", {"start": v(17.44, 9.35) * mm, "end": v(17.52, 9.4) * mm});
            skLineSegment(sketch, "E4682", {"start": v(17.52, 9.4) * mm, "end": v(17.6, 9.43) * mm});
            skLineSegment(sketch, "E4683", {"start": v(17.6, 9.43) * mm, "end": v(17.68, 9.47) * mm});
            skLineSegment(sketch, "E4684", {"start": v(17.68, 9.47) * mm, "end": v(17.74, 9.5) * mm});
            skLineSegment(sketch, "E4685", {"start": v(17.74, 9.5) * mm, "end": v(17.79, 9.53) * mm});
            skLineSegment(sketch, "E4686", {"start": v(17.79, 9.53) * mm, "end": v(17.83, 9.55) * mm});
            skLineSegment(sketch, "E4687", {"start": v(17.83, 9.55) * mm, "end": v(17.85, 9.56) * mm});
            skLineSegment(sketch, "E4688", {"start": v(17.85, 9.56) * mm, "end": v(17.86, 9.57) * mm});
            skLineSegment(sketch, "E4689", {"start": v(17.86, 9.57) * mm, "end": v(17.88, 9.57) * mm});
            skLineSegment(sketch, "E4690", {"start": v(17.88, 9.57) * mm, "end": v(17.9, 9.58) * mm});
            skLineSegment(sketch, "E4691", {"start": v(17.9, 9.58) * mm, "end": v(17.91, 9.59) * mm});
            skLineSegment(sketch, "E4692", {"start": v(17.91, 9.59) * mm, "end": v(17.93, 9.6) * mm});
            skLineSegment(sketch, "E4693", {"start": v(17.93, 9.6) * mm, "end": v(17.95, 9.6) * mm});
            skLineSegment(sketch, "E4694", {"start": v(17.95, 9.6) * mm, "end": v(17.96, 9.6) * mm});
            skLineSegment(sketch, "E4695", {"start": v(17.96, 9.6) * mm, "end": v(17.97, 9.61) * mm});
            skLineSegment(sketch, "E4696", {"start": v(17.97, 9.61) * mm, "end": v(17.99, 9.62) * mm});
            skLineSegment(sketch, "E4697", {"start": v(17.99, 9.62) * mm, "end": v(18, 9.62) * mm});
            skLineSegment(sketch, "E4698", {"start": v(18, 9.62) * mm, "end": v(18.02, 9.62) * mm});
            skLineSegment(sketch, "E4699", {"start": v(18.02, 9.62) * mm, "end": v(18.04, 9.62) * mm});
            skLineSegment(sketch, "E4700", {"start": v(18.04, 9.62) * mm, "end": v(18.06, 9.62) * mm});
            skLineSegment(sketch, "E4701", {"start": v(18.06, 9.62) * mm, "end": v(18.07, 9.61) * mm});
            skLineSegment(sketch, "E4702", {"start": v(18.07, 9.61) * mm, "end": v(18.08, 9.6) * mm});
            skLineSegment(sketch, "E4703", {"start": v(18.08, 9.6) * mm, "end": v(18.1, 9.6) * mm});
            skLineSegment(sketch, "E4704", {"start": v(18.1, 9.6) * mm, "end": v(18.1, 9.6) * mm});
            skLineSegment(sketch, "E4705", {"start": v(18.1, 9.6) * mm, "end": v(18.1, 9.59) * mm});
            skLineSegment(sketch, "E4706", {"start": v(18.1, 9.59) * mm, "end": v(18.09, 9.58) * mm});
            skLineSegment(sketch, "E4707", {"start": v(18.09, 9.58) * mm, "end": v(18.09, 9.56) * mm});
            skLineSegment(sketch, "E4708", {"start": v(18.09, 9.56) * mm, "end": v(18.09, 9.53) * mm});
            skLineSegment(sketch, "E4709", {"start": v(18.09, 9.53) * mm, "end": v(18.09, 9.5) * mm});
            skLineSegment(sketch, "E4710", {"start": v(18.09, 9.5) * mm, "end": v(18.08, 9.46) * mm});
            skLineSegment(sketch, "E4711", {"start": v(18.08, 9.46) * mm, "end": v(18.08, 9.42) * mm});
            skLineSegment(sketch, "E4712", {"start": v(18.08, 9.42) * mm, "end": v(18.09, 9.38) * mm});
            skLineSegment(sketch, "E4713", {"start": v(18.09, 9.38) * mm, "end": v(18.09, 9.34) * mm});
            skLineSegment(sketch, "E4714", {"start": v(18.09, 9.34) * mm, "end": v(18.09, 9.3) * mm});
            skLineSegment(sketch, "E4715", {"start": v(18.09, 9.3) * mm, "end": v(18.1, 9.26) * mm});
            skLineSegment(sketch, "E4716", {"start": v(18.1, 9.26) * mm, "end": v(18.1, 9.22) * mm});
            skLineSegment(sketch, "E4717", {"start": v(18.1, 9.22) * mm, "end": v(18.1, 9.18) * mm});
            skLineSegment(sketch, "E4718", {"start": v(18.1, 9.18) * mm, "end": v(18.1, 9.12) * mm});
            skLineSegment(sketch, "E4719", {"start": v(18.1, 9.12) * mm, "end": v(18.1, 9.07) * mm});
            skLineSegment(sketch, "E4720", {"start": v(18.1, 9.07) * mm, "end": v(18.11, 9.01) * mm});
            skLineSegment(sketch, "E4721", {"start": v(18.11, 9.01) * mm, "end": v(18.11, 8.96) * mm});
            skLineSegment(sketch, "E4722", {"start": v(18.11, 8.96) * mm, "end": v(18.11, 8.9) * mm});
            skLineSegment(sketch, "E4723", {"start": v(18.11, 8.9) * mm, "end": v(18.1, 8.85) * mm});
            skLineSegment(sketch, "E4724", {"start": v(18.1, 8.85) * mm, "end": v(18.1, 8.8) * mm});
            skLineSegment(sketch, "E4725", {"start": v(18.1, 8.8) * mm, "end": v(18.1, 8.75) * mm});
            skLineSegment(sketch, "E4726", {"start": v(18.1, 8.75) * mm, "end": v(18.08, 8.7) * mm});
            skLineSegment(sketch, "E4727", {"start": v(18.08, 8.7) * mm, "end": v(18.08, 8.66) * mm});
            skLineSegment(sketch, "E4728", {"start": v(18.08, 8.66) * mm, "end": v(18.07, 8.62) * mm});
            skLineSegment(sketch, "E4729", {"start": v(18.07, 8.62) * mm, "end": v(18.07, 8.57) * mm});
            skLineSegment(sketch, "E4730", {"start": v(18.07, 8.57) * mm, "end": v(18.07, 8.53) * mm});
            skLineSegment(sketch, "E4731", {"start": v(18.07, 8.53) * mm, "end": v(18.07, 8.49) * mm});
            skLineSegment(sketch, "E4732", {"start": v(18.07, 8.49) * mm, "end": v(18.07, 8.44) * mm});
            skLineSegment(sketch, "E4733", {"start": v(18.07, 8.44) * mm, "end": v(18.07, 8.4) * mm});
            skLineSegment(sketch, "E4734", {"start": v(18.07, 8.4) * mm, "end": v(18.07, 8.38) * mm});
            skLineSegment(sketch, "E4735", {"start": v(18.07, 8.38) * mm, "end": v(18.07, 8.36) * mm});
            skLineSegment(sketch, "E4736", {"start": v(18.07, 8.36) * mm, "end": v(18.07, 8.34) * mm});
            skLineSegment(sketch, "E4737", {"start": v(18.07, 8.34) * mm, "end": v(18.07, 8.31) * mm});
            skLineSegment(sketch, "E4738", {"start": v(18.07, 8.31) * mm, "end": v(18.07, 8.3) * mm});
            skLineSegment(sketch, "E4739", {"start": v(18.07, 8.3) * mm, "end": v(18.07, 8.27) * mm});
            skLineSegment(sketch, "E4740", {"start": v(18.07, 8.27) * mm, "end": v(18.07, 8.25) * mm});
            skLineSegment(sketch, "E4741", {"start": v(18.07, 8.25) * mm, "end": v(18.07, 8.23) * mm});
            skLineSegment(sketch, "E4742", {"start": v(18.07, 8.23) * mm, "end": v(18.07, 8.2) * mm});
            skLineSegment(sketch, "E4743", {"start": v(18.07, 8.2) * mm, "end": v(18.07, 8.16) * mm});
            skLineSegment(sketch, "E4744", {"start": v(18.07, 8.16) * mm, "end": v(18.07, 8.14) * mm});
            skLineSegment(sketch, "E4745", {"start": v(18.07, 8.14) * mm, "end": v(18.07, 8.13) * mm});
            skLineSegment(sketch, "E4746", {"start": v(18.07, 8.13) * mm, "end": v(18.07, 8.12) * mm});
            skLineSegment(sketch, "E4747", {"start": v(18.07, 8.12) * mm, "end": v(18.07, 8.11) * mm});
            skLineSegment(sketch, "E4748", {"start": v(18.07, 8.11) * mm, "end": v(18.07, 8.11) * mm});
            skLineSegment(sketch, "E4749", {"start": v(18.07, 8.11) * mm, "end": v(18.04, 8.1) * mm});
            skLineSegment(sketch, "E4750", {"start": v(18.04, 8.1) * mm, "end": v(18.02, 8.1) * mm});
            skLineSegment(sketch, "E4751", {"start": v(18.02, 8.1) * mm, "end": v(18, 8.1) * mm});
            skLineSegment(sketch, "E4752", {"start": v(18, 8.1) * mm, "end": v(17.97, 8.1) * mm});
            skLineSegment(sketch, "E4753", {"start": v(17.97, 8.1) * mm, "end": v(17.95, 8.1) * mm});
            skLineSegment(sketch, "E4754", {"start": v(17.95, 8.1) * mm, "end": v(17.94, 8.1) * mm});
            skLineSegment(sketch, "E4755", {"start": v(17.94, 8.1) * mm, "end": v(17.93, 8.1) * mm});
            skLineSegment(sketch, "E4756", {"start": v(17.93, 8.1) * mm, "end": v(17.92, 8.1) * mm});
            skLineSegment(sketch, "E4757", {"start": v(17.92, 8.1) * mm, "end": v(17.92, 8.1) * mm});
            skLineSegment(sketch, "E4758", {"start": v(17.92, 8.1) * mm, "end": v(17.9, 8.1) * mm});
            skLineSegment(sketch, "E4759", {"start": v(17.9, 8.1) * mm, "end": v(17.9, 8.1) * mm});
            skLineSegment(sketch, "E4760", {"start": v(17.9, 8.1) * mm, "end": v(17.88, 8.1) * mm});
            skLineSegment(sketch, "E4761", {"start": v(17.88, 8.1) * mm, "end": v(17.87, 8.1) * mm});
            skLineSegment(sketch, "E4762", {"start": v(17.87, 8.1) * mm, "end": v(17.87, 8.1) * mm});
            skLineSegment(sketch, "E4763", {"start": v(17.87, 8.1) * mm, "end": v(17.86, 8.1) * mm});
            skLineSegment(sketch, "E4764", {"start": v(17.86, 8.1) * mm, "end": v(17.86, 8.1) * mm});
            skLineSegment(sketch, "E4765", {"start": v(17.86, 8.1) * mm, "end": v(17.85, 8.1) * mm});
            skLineSegment(sketch, "E4766", {"start": v(17.85, 8.1) * mm, "end": v(17.84, 8.1) * mm});
            skLineSegment(sketch, "E4767", {"start": v(17.84, 8.1) * mm, "end": v(17.81, 8.1) * mm});
            skLineSegment(sketch, "E4768", {"start": v(17.81, 8.1) * mm, "end": v(17.79, 8.1) * mm});
            skLineSegment(sketch, "E4769", {"start": v(17.79, 8.1) * mm, "end": v(17.76, 8.1) * mm});
            skLineSegment(sketch, "E4770", {"start": v(17.76, 8.1) * mm, "end": v(17.74, 8.1) * mm});
            skLineSegment(sketch, "E4771", {"start": v(17.74, 8.1) * mm, "end": v(17.7, 8.1) * mm});
            skLineSegment(sketch, "E4772", {"start": v(17.7, 8.1) * mm, "end": v(17.68, 8.1) * mm});
            skLineSegment(sketch, "E4773", {"start": v(17.68, 8.1) * mm, "end": v(17.66, 8.1) * mm});
            skLineSegment(sketch, "E4774", {"start": v(17.66, 8.1) * mm, "end": v(17.63, 8.1) * mm});
            skLineSegment(sketch, "E4775", {"start": v(17.63, 8.1) * mm, "end": v(17.53, 8.07) * mm});
            skLineSegment(sketch, "E4776", {"start": v(17.53, 8.07) * mm, "end": v(17.43, 8.05) * mm});
            skLineSegment(sketch, "E4777", {"start": v(17.43, 8.05) * mm, "end": v(17.33, 8.03) * mm});
            skLineSegment(sketch, "E4778", {"start": v(17.33, 8.03) * mm, "end": v(17.24, 8) * mm});
            skLineSegment(sketch, "E4779", {"start": v(17.24, 8) * mm, "end": v(17.15, 7.99) * mm});
            skLineSegment(sketch, "E4780", {"start": v(17.15, 7.99) * mm, "end": v(17.06, 7.96) * mm});
            skLineSegment(sketch, "E4781", {"start": v(17.06, 7.96) * mm, "end": v(16.97, 7.94) * mm});
            skLineSegment(sketch, "E4782", {"start": v(16.97, 7.94) * mm, "end": v(16.88, 7.92) * mm});
            skLineSegment(sketch, "E4783", {"start": v(16.88, 7.92) * mm, "end": v(16.8, 7.9) * mm});
            skLineSegment(sketch, "E4784", {"start": v(16.8, 7.9) * mm, "end": v(16.7, 7.87) * mm});
            skLineSegment(sketch, "E4785", {"start": v(16.7, 7.87) * mm, "end": v(16.62, 7.84) * mm});
            skLineSegment(sketch, "E4786", {"start": v(16.62, 7.84) * mm, "end": v(16.54, 7.81) * mm});
            skLineSegment(sketch, "E4787", {"start": v(16.54, 7.81) * mm, "end": v(16.46, 7.79) * mm});
            skLineSegment(sketch, "E4788", {"start": v(16.46, 7.79) * mm, "end": v(16.39, 7.76) * mm});
            skLineSegment(sketch, "E4789", {"start": v(16.39, 7.76) * mm, "end": v(16.32, 7.74) * mm});
            skLineSegment(sketch, "E4790", {"start": v(16.32, 7.74) * mm, "end": v(16.25, 7.7) * mm});
            skLineSegment(sketch, "E4791", {"start": v(16.25, 7.7) * mm, "end": v(16.18, 7.68) * mm});
            skLineSegment(sketch, "E4792", {"start": v(16.18, 7.68) * mm, "end": v(16.12, 7.66) * mm});
            skLineSegment(sketch, "E4793", {"start": v(16.12, 7.66) * mm, "end": v(16.08, 7.64) * mm});
            skLineSegment(sketch, "E4794", {"start": v(16.08, 7.64) * mm, "end": v(16.06, 7.63) * mm});
            skLineSegment(sketch, "E4795", {"start": v(16.06, 7.63) * mm, "end": v(16.04, 7.62) * mm});
            skLineSegment(sketch, "E4796", {"start": v(16.04, 7.62) * mm, "end": v(16.03, 7.62) * mm});
            skLineSegment(sketch, "E4797", {"start": v(16.03, 7.62) * mm, "end": v(16.03, 7.62) * mm});
            skLineSegment(sketch, "E4798", {"start": v(16.03, 7.62) * mm, "end": v(15.94, 7.58) * mm});
            skLineSegment(sketch, "E4799", {"start": v(15.94, 7.58) * mm, "end": v(15.85, 7.54) * mm});
            skLineSegment(sketch, "E4800", {"start": v(15.85, 7.54) * mm, "end": v(15.77, 7.5) * mm});
            skLineSegment(sketch, "E4801", {"start": v(15.77, 7.5) * mm, "end": v(15.69, 7.46) * mm});
            skLineSegment(sketch, "E4802", {"start": v(15.69, 7.46) * mm, "end": v(15.62, 7.43) * mm});
            skLineSegment(sketch, "E4803", {"start": v(15.62, 7.43) * mm, "end": v(15.55, 7.4) * mm});
            skLineSegment(sketch, "E4804", {"start": v(15.55, 7.4) * mm, "end": v(15.5, 7.38) * mm});
            skLineSegment(sketch, "E4805", {"start": v(15.5, 7.38) * mm, "end": v(15.47, 7.36) * mm});
            skLineSegment(sketch, "E4806", {"start": v(15.47, 7.36) * mm, "end": v(15.43, 7.35) * mm});
            skLineSegment(sketch, "E4807", {"start": v(15.43, 7.35) * mm, "end": v(15.38, 7.31) * mm});
            skLineSegment(sketch, "E4808", {"start": v(15.38, 7.31) * mm, "end": v(15.31, 7.27) * mm});
            skLineSegment(sketch, "E4809", {"start": v(15.31, 7.27) * mm, "end": v(15.24, 7.21) * mm});
            skLineSegment(sketch, "E4810", {"start": v(15.24, 7.21) * mm, "end": v(15.15, 7.15) * mm});
            skLineSegment(sketch, "E4811", {"start": v(15.15, 7.15) * mm, "end": v(15.06, 7.08) * mm});
            skLineSegment(sketch, "E4812", {"start": v(15.06, 7.08) * mm, "end": v(14.96, 7) * mm});
            skLineSegment(sketch, "E4813", {"start": v(14.96, 7) * mm, "end": v(14.86, 6.93) * mm});
            skLineSegment(sketch, "E4814", {"start": v(14.86, 6.93) * mm, "end": v(14.86, 6.93) * mm});
            skLineSegment(sketch, "E4815", {"start": v(14.86, 6.93) * mm, "end": v(14.86, 6.92) * mm});
            skLineSegment(sketch, "E4816", {"start": v(14.86, 6.92) * mm, "end": v(14.85, 6.92) * mm});
            skLineSegment(sketch, "E4817", {"start": v(14.85, 6.92) * mm, "end": v(14.84, 6.9) * mm});
            skLineSegment(sketch, "E4818", {"start": v(14.84, 6.9) * mm, "end": v(14.82, 6.87) * mm});
            skLineSegment(sketch, "E4819", {"start": v(14.82, 6.87) * mm, "end": v(14.79, 6.83) * mm});
            skLineSegment(sketch, "E4820", {"start": v(14.79, 6.83) * mm, "end": v(14.74, 6.77) * mm});
            skLineSegment(sketch, "E4821", {"start": v(14.74, 6.77) * mm, "end": v(14.69, 6.7) * mm});
            skLineSegment(sketch, "E4822", {"start": v(14.69, 6.7) * mm, "end": v(14.67, 6.67) * mm});
            skLineSegment(sketch, "E4823", {"start": v(14.67, 6.67) * mm, "end": v(14.66, 6.65) * mm});
            skLineSegment(sketch, "E4824", {"start": v(14.66, 6.65) * mm, "end": v(14.64, 6.64) * mm});
            skLineSegment(sketch, "E4825", {"start": v(14.64, 6.64) * mm, "end": v(14.63, 6.62) * mm});
            skLineSegment(sketch, "E4826", {"start": v(14.63, 6.62) * mm, "end": v(14.62, 6.6) * mm});
            skLineSegment(sketch, "E4827", {"start": v(14.62, 6.6) * mm, "end": v(14.6, 6.58) * mm});
            skLineSegment(sketch, "E4828", {"start": v(14.6, 6.58) * mm, "end": v(14.59, 6.56) * mm});
            skLineSegment(sketch, "E4829", {"start": v(14.59, 6.56) * mm, "end": v(14.57, 6.54) * mm});
            skLineSegment(sketch, "E4830", {"start": v(14.57, 6.54) * mm, "end": v(14.54, 6.5) * mm});
            skLineSegment(sketch, "E4831", {"start": v(14.54, 6.5) * mm, "end": v(14.52, 6.47) * mm});
            skLineSegment(sketch, "E4832", {"start": v(14.52, 6.47) * mm, "end": v(14.5, 6.43) * mm});
            skLineSegment(sketch, "E4833", {"start": v(14.5, 6.43) * mm, "end": v(14.46, 6.39) * mm});
            skLineSegment(sketch, "E4834", {"start": v(14.46, 6.39) * mm, "end": v(14.44, 6.34) * mm});
            skLineSegment(sketch, "E4835", {"start": v(14.44, 6.34) * mm, "end": v(14.41, 6.3) * mm});
            skLineSegment(sketch, "E4836", {"start": v(14.41, 6.3) * mm, "end": v(14.39, 6.26) * mm});
            skLineSegment(sketch, "E4837", {"start": v(14.39, 6.26) * mm, "end": v(14.36, 6.22) * mm});
            skLineSegment(sketch, "E4838", {"start": v(14.36, 6.22) * mm, "end": v(14.35, 6.2) * mm});
            skLineSegment(sketch, "E4839", {"start": v(14.35, 6.2) * mm, "end": v(14.34, 6.19) * mm});
            skLineSegment(sketch, "E4840", {"start": v(14.34, 6.19) * mm, "end": v(14.34, 6.18) * mm});
            skLineSegment(sketch, "E4841", {"start": v(14.34, 6.18) * mm, "end": v(14.33, 6.17) * mm});
            skLineSegment(sketch, "E4842", {"start": v(14.33, 6.17) * mm, "end": v(14.33, 6.17) * mm});
            skLineSegment(sketch, "E4843", {"start": v(14.33, 6.17) * mm, "end": v(14.33, 6.16) * mm});
            skLineSegment(sketch, "E4844", {"start": v(14.33, 6.16) * mm, "end": v(14.33, 6.16) * mm});
            skLineSegment(sketch, "E4845", {"start": v(14.33, 6.16) * mm, "end": v(14.31, 6.14) * mm});
            skLineSegment(sketch, "E4846", {"start": v(14.31, 6.14) * mm, "end": v(14.3, 6.12) * mm});
            skLineSegment(sketch, "E4847", {"start": v(14.3, 6.12) * mm, "end": v(14.29, 6.1) * mm});
            skLineSegment(sketch, "E4848", {"start": v(14.29, 6.1) * mm, "end": v(14.27, 6.07) * mm});
            skLineSegment(sketch, "E4849", {"start": v(14.27, 6.07) * mm, "end": v(14.26, 6.05) * mm});
            skLineSegment(sketch, "E4850", {"start": v(14.26, 6.05) * mm, "end": v(14.25, 6.03) * mm});
            skLineSegment(sketch, "E4851", {"start": v(14.25, 6.03) * mm, "end": v(14.24, 6.01) * mm});
            skLineSegment(sketch, "E4852", {"start": v(14.24, 6.01) * mm, "end": v(14.23, 6) * mm});
            skLineSegment(sketch, "E4853", {"start": v(14.23, 6) * mm, "end": v(14.22, 5.99) * mm});
            skLineSegment(sketch, "E4854", {"start": v(14.22, 5.99) * mm, "end": v(14.22, 5.98) * mm});
            skLineSegment(sketch, "E4855", {"start": v(14.22, 5.98) * mm, "end": v(14.22, 5.97) * mm});
            skLineSegment(sketch, "E4856", {"start": v(14.22, 5.97) * mm, "end": v(14.22, 5.96) * mm});
            skLineSegment(sketch, "E4857", {"start": v(14.22, 5.96) * mm, "end": v(14.23, 5.95) * mm});
            skLineSegment(sketch, "E4858", {"start": v(14.23, 5.95) * mm, "end": v(14.23, 5.94) * mm});
            skLineSegment(sketch, "E4859", {"start": v(14.23, 5.94) * mm, "end": v(14.24, 5.93) * mm});
            skLineSegment(sketch, "E4860", {"start": v(14.24, 5.93) * mm, "end": v(14.25, 5.93) * mm});
            skLineSegment(sketch, "E4861", {"start": v(14.25, 5.93) * mm, "end": v(14.27, 5.92) * mm});
            skLineSegment(sketch, "E4862", {"start": v(14.27, 5.92) * mm, "end": v(14.29, 5.92) * mm});
            skLineSegment(sketch, "E4863", {"start": v(14.29, 5.92) * mm, "end": v(14.31, 5.9) * mm});
            skLineSegment(sketch, "E4864", {"start": v(14.31, 5.9) * mm, "end": v(14.34, 5.9) * mm});
            skLineSegment(sketch, "E4865", {"start": v(14.34, 5.9) * mm, "end": v(14.37, 5.88) * mm});
            skLineSegment(sketch, "E4866", {"start": v(14.37, 5.88) * mm, "end": v(14.4, 5.87) * mm});
            skLineSegment(sketch, "E4867", {"start": v(14.4, 5.87) * mm, "end": v(14.43, 5.86) * mm});
            skLineSegment(sketch, "E4868", {"start": v(14.43, 5.86) * mm, "end": v(14.47, 5.85) * mm});
            skLineSegment(sketch, "E4869", {"start": v(14.47, 5.85) * mm, "end": v(14.47, 5.85) * mm});
            skLineSegment(sketch, "E4870", {"start": v(14.47, 5.85) * mm, "end": v(14.47, 5.84) * mm});
            skLineSegment(sketch, "E4871", {"start": v(14.47, 5.84) * mm, "end": v(14.47, 5.84) * mm});
            skLineSegment(sketch, "E4872", {"start": v(14.47, 5.84) * mm, "end": v(14.48, 5.84) * mm});
            skLineSegment(sketch, "E4873", {"start": v(14.48, 5.84) * mm, "end": v(14.48, 5.84) * mm});
            skLineSegment(sketch, "E4874", {"start": v(14.48, 5.84) * mm, "end": v(14.5, 5.83) * mm});
            skLineSegment(sketch, "E4875", {"start": v(14.5, 5.83) * mm, "end": v(14.52, 5.82) * mm});
            skLineSegment(sketch, "E4876", {"start": v(14.52, 5.82) * mm, "end": v(14.54, 5.81) * mm});
            skLineSegment(sketch, "E4877", {"start": v(14.54, 5.81) * mm, "end": v(14.6, 5.79) * mm});
            skLineSegment(sketch, "E4878", {"start": v(14.6, 5.79) * mm, "end": v(14.66, 5.77) * mm});
            skLineSegment(sketch, "E4879", {"start": v(14.66, 5.77) * mm, "end": v(14.72, 5.74) * mm});
            skLineSegment(sketch, "E4880", {"start": v(14.72, 5.74) * mm, "end": v(14.78, 5.72) * mm});
            skLineSegment(sketch, "E4881", {"start": v(14.78, 5.72) * mm, "end": v(14.84, 5.7) * mm});
            skLineSegment(sketch, "E4882", {"start": v(14.84, 5.7) * mm, "end": v(14.9, 5.67) * mm});
            skLineSegment(sketch, "E4883", {"start": v(14.9, 5.67) * mm, "end": v(14.96, 5.65) * mm});
            skLineSegment(sketch, "E4884", {"start": v(14.96, 5.65) * mm, "end": v(15.02, 5.63) * mm});
            skLineSegment(sketch, "E4885", {"start": v(15.02, 5.63) * mm, "end": v(15.24, 5.57) * mm});
            skLineSegment(sketch, "E4886", {"start": v(15.24, 5.57) * mm, "end": v(15.46, 5.52) * mm});
            skLineSegment(sketch, "E4887", {"start": v(15.46, 5.52) * mm, "end": v(15.67, 5.48) * mm});
            skLineSegment(sketch, "E4888", {"start": v(15.67, 5.48) * mm, "end": v(15.88, 5.46) * mm});
            skLineSegment(sketch, "E4889", {"start": v(15.88, 5.46) * mm, "end": v(16.1, 5.44) * mm});
            skLineSegment(sketch, "E4890", {"start": v(16.1, 5.44) * mm, "end": v(16.3, 5.45) * mm});
            skLineSegment(sketch, "E4891", {"start": v(16.3, 5.45) * mm, "end": v(16.5, 5.46) * mm});
            skLineSegment(sketch, "E4892", {"start": v(16.5, 5.46) * mm, "end": v(16.7, 5.49) * mm});
            skLineSegment(sketch, "E4893", {"start": v(16.7, 5.49) * mm, "end": v(16.73, 5.5) * mm});
            skLineSegment(sketch, "E4894", {"start": v(16.73, 5.5) * mm, "end": v(16.75, 5.5) * mm});
            skLineSegment(sketch, "E4895", {"start": v(16.75, 5.5) * mm, "end": v(16.78, 5.5) * mm});
            skLineSegment(sketch, "E4896", {"start": v(16.78, 5.5) * mm, "end": v(16.8, 5.51) * mm});
            skLineSegment(sketch, "E4897", {"start": v(16.8, 5.51) * mm, "end": v(16.83, 5.52) * mm});
            skLineSegment(sketch, "E4898", {"start": v(16.83, 5.52) * mm, "end": v(16.86, 5.53) * mm});
            skLineSegment(sketch, "E4899", {"start": v(16.86, 5.53) * mm, "end": v(16.89, 5.53) * mm});
            skLineSegment(sketch, "E4900", {"start": v(16.89, 5.53) * mm, "end": v(16.91, 5.54) * mm});
            skLineSegment(sketch, "E4901", {"start": v(16.91, 5.54) * mm, "end": v(16.95, 5.55) * mm});
            skLineSegment(sketch, "E4902", {"start": v(16.95, 5.55) * mm, "end": v(17, 5.56) * mm});
            skLineSegment(sketch, "E4903", {"start": v(17, 5.56) * mm, "end": v(17.03, 5.57) * mm});
            skLineSegment(sketch, "E4904", {"start": v(17.03, 5.57) * mm, "end": v(17.07, 5.58) * mm});
            skLineSegment(sketch, "E4905", {"start": v(17.07, 5.58) * mm, "end": v(17.1, 5.58) * mm});
            skLineSegment(sketch, "E4906", {"start": v(17.1, 5.58) * mm, "end": v(17.14, 5.59) * mm});
            skLineSegment(sketch, "E4907", {"start": v(17.14, 5.59) * mm, "end": v(17.18, 5.6) * mm});
            skLineSegment(sketch, "E4908", {"start": v(17.18, 5.6) * mm, "end": v(17.22, 5.6) * mm});
            skLineSegment(sketch, "E4909", {"start": v(17.22, 5.6) * mm, "end": v(17.3, 5.6) * mm});
            skLineSegment(sketch, "E4910", {"start": v(17.3, 5.6) * mm, "end": v(17.39, 5.63) * mm});
            skLineSegment(sketch, "E4911", {"start": v(17.39, 5.63) * mm, "end": v(17.46, 5.65) * mm});
            skLineSegment(sketch, "E4912", {"start": v(17.46, 5.65) * mm, "end": v(17.54, 5.69) * mm});
            skLineSegment(sketch, "E4913", {"start": v(17.54, 5.69) * mm, "end": v(17.6, 5.72) * mm});
            skLineSegment(sketch, "E4914", {"start": v(17.6, 5.72) * mm, "end": v(17.68, 5.77) * mm});
            skLineSegment(sketch, "E4915", {"start": v(17.68, 5.77) * mm, "end": v(17.74, 5.8) * mm});
            skLineSegment(sketch, "E4916", {"start": v(17.74, 5.8) * mm, "end": v(17.8, 5.85) * mm});
            skLineSegment(sketch, "E4917", {"start": v(17.8, 5.85) * mm, "end": v(17.9, 5.92) * mm});
            skLineSegment(sketch, "E4918", {"start": v(17.9, 5.92) * mm, "end": v(17.98, 6) * mm});
            skLineSegment(sketch, "E4919", {"start": v(17.98, 6) * mm, "end": v(18.07, 6.07) * mm});
            skLineSegment(sketch, "E4920", {"start": v(18.07, 6.07) * mm, "end": v(18.15, 6.16) * mm});
            skLineSegment(sketch, "E4921", {"start": v(18.15, 6.16) * mm, "end": v(18.22, 6.25) * mm});
            skLineSegment(sketch, "E4922", {"start": v(18.22, 6.25) * mm, "end": v(18.3, 6.35) * mm});
            skLineSegment(sketch, "E4923", {"start": v(18.3, 6.35) * mm, "end": v(18.36, 6.45) * mm});
            skLineSegment(sketch, "E4924", {"start": v(18.36, 6.45) * mm, "end": v(18.43, 6.56) * mm});
            skLineSegment(sketch, "E4925", {"start": v(18.43, 6.56) * mm, "end": v(18.45, 6.6) * mm});
            skLineSegment(sketch, "E4926", {"start": v(18.45, 6.6) * mm, "end": v(18.48, 6.62) * mm});
            skLineSegment(sketch, "E4927", {"start": v(18.48, 6.62) * mm, "end": v(18.5, 6.63) * mm});
            skLineSegment(sketch, "E4928", {"start": v(18.5, 6.63) * mm, "end": v(18.54, 6.64) * mm});
            skLineSegment(sketch, "E4929", {"start": v(18.54, 6.64) * mm, "end": v(18.57, 6.63) * mm});
            skLineSegment(sketch, "E4930", {"start": v(18.57, 6.63) * mm, "end": v(18.6, 6.62) * mm});
            skLineSegment(sketch, "E4931", {"start": v(18.6, 6.62) * mm, "end": v(18.63, 6.6) * mm});
            skLineSegment(sketch, "E4932", {"start": v(18.63, 6.6) * mm, "end": v(18.66, 6.56) * mm});
            skLineSegment(sketch, "E4933", {"start": v(18.66, 6.56) * mm, "end": v(18.72, 6.45) * mm});
            skLineSegment(sketch, "E4934", {"start": v(18.72, 6.45) * mm, "end": v(18.78, 6.35) * mm});
            skLineSegment(sketch, "E4935", {"start": v(18.78, 6.35) * mm, "end": v(18.83, 6.25) * mm});
            skLineSegment(sketch, "E4936", {"start": v(18.83, 6.25) * mm, "end": v(18.89, 6.14) * mm});
            skLineSegment(sketch, "E4937", {"start": v(18.89, 6.14) * mm, "end": v(18.94, 6.04) * mm});
            skLineSegment(sketch, "E4938", {"start": v(18.94, 6.04) * mm, "end": v(19, 5.94) * mm});
            skLineSegment(sketch, "E4939", {"start": v(19, 5.94) * mm, "end": v(19.04, 5.85) * mm});
            skLineSegment(sketch, "E4940", {"start": v(19.04, 5.85) * mm, "end": v(19.09, 5.75) * mm});
            skLineSegment(sketch, "E4941", {"start": v(19.09, 5.75) * mm, "end": v(19.1, 5.73) * mm});
            skLineSegment(sketch, "E4942", {"start": v(19.1, 5.73) * mm, "end": v(19.1, 5.7) * mm});
            skLineSegment(sketch, "E4943", {"start": v(19.1, 5.7) * mm, "end": v(19.1, 5.67) * mm});
            skLineSegment(sketch, "E4944", {"start": v(19.1, 5.67) * mm, "end": v(19.11, 5.64) * mm});
            skLineSegment(sketch, "E4945", {"start": v(19.11, 5.64) * mm, "end": v(19.1, 5.6) * mm});
            skLineSegment(sketch, "E4946", {"start": v(19.1, 5.6) * mm, "end": v(19.1, 5.57) * mm});
            skLineSegment(sketch, "E4947", {"start": v(19.1, 5.57) * mm, "end": v(19.07, 5.54) * mm});
            skLineSegment(sketch, "E4948", {"start": v(19.07, 5.54) * mm, "end": v(19.04, 5.5) * mm});
            skLineSegment(sketch, "E4949", {"start": v(19.04, 5.5) * mm, "end": v(19, 5.47) * mm});
            skLineSegment(sketch, "E4950", {"start": v(19, 5.47) * mm, "end": v(18.97, 5.44) * mm});
            skLineSegment(sketch, "E4951", {"start": v(18.97, 5.44) * mm, "end": v(18.94, 5.4) * mm});
            skLineSegment(sketch, "E4952", {"start": v(18.94, 5.4) * mm, "end": v(18.9, 5.38) * mm});
            skLineSegment(sketch, "E4953", {"start": v(18.9, 5.38) * mm, "end": v(18.87, 5.35) * mm});
            skLineSegment(sketch, "E4954", {"start": v(18.87, 5.35) * mm, "end": v(18.83, 5.31) * mm});
            skLineSegment(sketch, "E4955", {"start": v(18.83, 5.31) * mm, "end": v(18.8, 5.28) * mm});
            skLineSegment(sketch, "E4956", {"start": v(18.8, 5.28) * mm, "end": v(18.76, 5.25) * mm});
            skLineSegment(sketch, "E4957", {"start": v(18.76, 5.25) * mm, "end": v(18.7, 5.2) * mm});
            skLineSegment(sketch, "E4958", {"start": v(18.7, 5.2) * mm, "end": v(18.65, 5.15) * mm});
            skLineSegment(sketch, "E4959", {"start": v(18.65, 5.15) * mm, "end": v(18.6, 5.1) * mm});
            skLineSegment(sketch, "E4960", {"start": v(18.6, 5.1) * mm, "end": v(18.54, 5.05) * mm});
            skLineSegment(sketch, "E4961", {"start": v(18.54, 5.05) * mm, "end": v(18.48, 5) * mm});
            skLineSegment(sketch, "E4962", {"start": v(18.48, 5) * mm, "end": v(18.42, 4.94) * mm});
            skLineSegment(sketch, "E4963", {"start": v(18.42, 4.94) * mm, "end": v(18.37, 4.89) * mm});
            skLineSegment(sketch, "E4964", {"start": v(18.37, 4.89) * mm, "end": v(18.31, 4.84) * mm});
            skLineSegment(sketch, "E4965", {"start": v(18.31, 4.84) * mm, "end": v(18.25, 4.77) * mm});
            skLineSegment(sketch, "E4966", {"start": v(18.25, 4.77) * mm, "end": v(18.18, 4.71) * mm});
            skLineSegment(sketch, "E4967", {"start": v(18.18, 4.71) * mm, "end": v(18.12, 4.64) * mm});
            skLineSegment(sketch, "E4968", {"start": v(18.12, 4.64) * mm, "end": v(18.06, 4.58) * mm});
            skLineSegment(sketch, "E4969", {"start": v(18.06, 4.58) * mm, "end": v(18, 4.5) * mm});
            skLineSegment(sketch, "E4970", {"start": v(18, 4.5) * mm, "end": v(17.93, 4.44) * mm});
            skLineSegment(sketch, "E4971", {"start": v(17.93, 4.44) * mm, "end": v(17.87, 4.37) * mm});
            skLineSegment(sketch, "E4972", {"start": v(17.87, 4.37) * mm, "end": v(17.8, 4.3) * mm});
            skLineSegment(sketch, "E4973", {"start": v(17.8, 4.3) * mm, "end": v(17.77, 4.24) * mm});
            skLineSegment(sketch, "E4974", {"start": v(17.77, 4.24) * mm, "end": v(17.74, 4.2) * mm});
            skLineSegment(sketch, "E4975", {"start": v(17.74, 4.2) * mm, "end": v(17.72, 4.18) * mm});
            skLineSegment(sketch, "E4976", {"start": v(17.72, 4.18) * mm, "end": v(17.71, 4.16) * mm});
            skLineSegment(sketch, "E4977", {"start": v(17.71, 4.16) * mm, "end": v(17.7, 4.15) * mm});
            skLineSegment(sketch, "E4978", {"start": v(17.7, 4.15) * mm, "end": v(17.7, 4.15) * mm});
            skLineSegment(sketch, "E4979", {"start": v(17.7, 4.15) * mm, "end": v(17.66, 4.08) * mm});
            skLineSegment(sketch, "E4980", {"start": v(17.66, 4.08) * mm, "end": v(17.63, 4.02) * mm});
            skLineSegment(sketch, "E4981", {"start": v(17.63, 4.02) * mm, "end": v(17.6, 3.96) * mm});
            skLineSegment(sketch, "E4982", {"start": v(17.6, 3.96) * mm, "end": v(17.56, 3.9) * mm});
            skLineSegment(sketch, "E4983", {"start": v(17.56, 3.9) * mm, "end": v(17.54, 3.85) * mm});
            skLineSegment(sketch, "E4984", {"start": v(17.54, 3.85) * mm, "end": v(17.51, 3.8) * mm});
            skLineSegment(sketch, "E4985", {"start": v(17.51, 3.8) * mm, "end": v(17.5, 3.78) * mm});
            skLineSegment(sketch, "E4986", {"start": v(17.5, 3.78) * mm, "end": v(17.49, 3.76) * mm});
            skLineSegment(sketch, "E4987", {"start": v(17.49, 3.76) * mm, "end": v(17.47, 3.74) * mm});
            skLineSegment(sketch, "E4988", {"start": v(17.47, 3.74) * mm, "end": v(17.46, 3.7) * mm});
            skLineSegment(sketch, "E4989", {"start": v(17.46, 3.7) * mm, "end": v(17.44, 3.67) * mm});
            skLineSegment(sketch, "E4990", {"start": v(17.44, 3.67) * mm, "end": v(17.42, 3.63) * mm});
            skLineSegment(sketch, "E4991", {"start": v(17.42, 3.63) * mm, "end": v(17.4, 3.59) * mm});
            skLineSegment(sketch, "E4992", {"start": v(17.4, 3.59) * mm, "end": v(17.36, 3.54) * mm});
            skLineSegment(sketch, "E4993", {"start": v(17.36, 3.54) * mm, "end": v(17.33, 3.48) * mm});
            skLineSegment(sketch, "E4994", {"start": v(17.33, 3.48) * mm, "end": v(17.3, 3.43) * mm});
            skLineSegment(sketch, "E4995", {"start": v(17.3, 3.43) * mm, "end": v(17.3, 3.43) * mm});
            skLineSegment(sketch, "E4996", {"start": v(17.3, 3.43) * mm, "end": v(17.3, 3.42) * mm});
            skLineSegment(sketch, "E4997", {"start": v(17.3, 3.42) * mm, "end": v(17.3, 3.41) * mm});
            skLineSegment(sketch, "E4998", {"start": v(17.3, 3.41) * mm, "end": v(17.3, 3.4) * mm});
            skLineSegment(sketch, "E4999", {"start": v(17.3, 3.4) * mm, "end": v(17.29, 3.37) * mm});
            skLineSegment(sketch, "E5000", {"start": v(17.29, 3.37) * mm, "end": v(17.28, 3.33) * mm});
            skLineSegment(sketch, "E5001", {"start": v(17.28, 3.33) * mm, "end": v(17.26, 3.29) * mm});
            skLineSegment(sketch, "E5002", {"start": v(17.26, 3.29) * mm, "end": v(17.24, 3.2) * mm});
            skLineSegment(sketch, "E5003", {"start": v(17.24, 3.2) * mm, "end": v(17.22, 3.12) * mm});
            skLineSegment(sketch, "E5004", {"start": v(17.22, 3.12) * mm, "end": v(17.2, 3.07) * mm});
            skLineSegment(sketch, "E5005", {"start": v(17.2, 3.07) * mm, "end": v(17.2, 3.03) * mm});
            skLineSegment(sketch, "E5006", {"start": v(17.2, 3.03) * mm, "end": v(17.19, 3.01) * mm});
            skLineSegment(sketch, "E5007", {"start": v(17.19, 3.01) * mm, "end": v(17.18, 3) * mm});
            skLineSegment(sketch, "E5008", {"start": v(17.18, 3) * mm, "end": v(17.18, 3) * mm});
            skLineSegment(sketch, "E5009", {"start": v(17.18, 3) * mm, "end": v(17.16, 2.88) * mm});
            skLineSegment(sketch, "E5010", {"start": v(17.16, 2.88) * mm, "end": v(17.13, 2.77) * mm});
            skLineSegment(sketch, "E5011", {"start": v(17.13, 2.77) * mm, "end": v(17.11, 2.67) * mm});
            skLineSegment(sketch, "E5012", {"start": v(17.11, 2.67) * mm, "end": v(17.1, 2.58) * mm});
            skLineSegment(sketch, "E5013", {"start": v(17.1, 2.58) * mm, "end": v(17.08, 2.5) * mm});
            skLineSegment(sketch, "E5014", {"start": v(17.08, 2.5) * mm, "end": v(17.07, 2.45) * mm});
            skLineSegment(sketch, "E5015", {"start": v(17.07, 2.45) * mm, "end": v(17.06, 2.41) * mm});
            skLineSegment(sketch, "E5016", {"start": v(17.06, 2.41) * mm, "end": v(17.06, 2.4) * mm});
            skLineSegment(sketch, "E5017", {"start": v(17.06, 2.4) * mm, "end": v(17.05, 2.39) * mm});
            skLineSegment(sketch, "E5018", {"start": v(17.05, 2.39) * mm, "end": v(17.05, 2.36) * mm});
            skLineSegment(sketch, "E5019", {"start": v(17.05, 2.36) * mm, "end": v(17.04, 2.32) * mm});
            skLineSegment(sketch, "E5020", {"start": v(17.04, 2.32) * mm, "end": v(17.03, 2.27) * mm});
            skLineSegment(sketch, "E5021", {"start": v(17.03, 2.27) * mm, "end": v(17.02, 2.2) * mm});
            skLineSegment(sketch, "E5022", {"start": v(17.02, 2.2) * mm, "end": v(17, 2.14) * mm});
            skLineSegment(sketch, "E5023", {"start": v(17, 2.14) * mm, "end": v(17, 2.06) * mm});
            skLineSegment(sketch, "E5024", {"start": v(17, 2.06) * mm, "end": v(16.98, 1.97) * mm});
            skLineSegment(sketch, "E5025", {"start": v(16.98, 1.97) * mm, "end": v(16.98, 1.97) * mm});
            skLineSegment(sketch, "E5026", {"start": v(16.98, 1.97) * mm, "end": v(16.98, 1.95) * mm});
            skLineSegment(sketch, "E5027", {"start": v(16.98, 1.95) * mm, "end": v(16.98, 1.93) * mm});
            skLineSegment(sketch, "E5028", {"start": v(16.98, 1.93) * mm, "end": v(16.97, 1.9) * mm});
            skLineSegment(sketch, "E5029", {"start": v(16.97, 1.9) * mm, "end": v(16.97, 1.86) * mm});
            skLineSegment(sketch, "E5030", {"start": v(16.97, 1.86) * mm, "end": v(16.96, 1.8) * mm});
            skLineSegment(sketch, "E5031", {"start": v(16.96, 1.8) * mm, "end": v(16.96, 1.77) * mm});
            skLineSegment(sketch, "E5032", {"start": v(16.96, 1.77) * mm, "end": v(16.96, 1.74) * mm});
            skLineSegment(sketch, "E5033", {"start": v(16.96, 1.74) * mm, "end": v(16.96, 1.71) * mm});
            skLineSegment(sketch, "E5034", {"start": v(16.96, 1.71) * mm, "end": v(16.97, 1.69) * mm});
            skLineSegment(sketch, "E5035", {"start": v(16.97, 1.69) * mm, "end": v(16.97, 1.67) * mm});
            skLineSegment(sketch, "E5036", {"start": v(16.97, 1.67) * mm, "end": v(16.98, 1.65) * mm});
            skLineSegment(sketch, "E5037", {"start": v(16.98, 1.65) * mm, "end": v(17, 1.64) * mm});
            skLineSegment(sketch, "E5038", {"start": v(17, 1.64) * mm, "end": v(17, 1.62) * mm});
            skLineSegment(sketch, "E5039", {"start": v(17, 1.62) * mm, "end": v(17.01, 1.6) * mm});
            skLineSegment(sketch, "E5040", {"start": v(17.01, 1.6) * mm, "end": v(17.03, 1.6) * mm});
            skLineSegment(sketch, "E5041", {"start": v(17.03, 1.6) * mm, "end": v(17.06, 1.58) * mm});
            skLineSegment(sketch, "E5042", {"start": v(17.06, 1.58) * mm, "end": v(17.08, 1.57) * mm});
            skLineSegment(sketch, "E5043", {"start": v(17.08, 1.57) * mm, "end": v(17.11, 1.57) * mm});
            skLineSegment(sketch, "E5044", {"start": v(17.11, 1.57) * mm, "end": v(17.15, 1.57) * mm});
            skLineSegment(sketch, "E5045", {"start": v(17.15, 1.57) * mm, "end": v(17.19, 1.57) * mm});
            skLineSegment(sketch, "E5046", {"start": v(17.19, 1.57) * mm, "end": v(17.23, 1.58) * mm});
            skLineSegment(sketch, "E5047", {"start": v(17.23, 1.58) * mm, "end": v(17.28, 1.6) * mm});
            skLineSegment(sketch, "E5048", {"start": v(17.28, 1.6) * mm, "end": v(17.33, 1.61) * mm});
            skLineSegment(sketch, "E5049", {"start": v(17.33, 1.61) * mm, "end": v(17.39, 1.63) * mm});
            skLineSegment(sketch, "E5050", {"start": v(17.39, 1.63) * mm, "end": v(17.44, 1.64) * mm});
            skLineSegment(sketch, "E5051", {"start": v(17.44, 1.64) * mm, "end": v(17.5, 1.66) * mm});
            skLineSegment(sketch, "E5052", {"start": v(17.5, 1.66) * mm, "end": v(17.55, 1.68) * mm});
            skLineSegment(sketch, "E5053", {"start": v(17.55, 1.68) * mm, "end": v(17.6, 1.7) * mm});
            skLineSegment(sketch, "E5054", {"start": v(17.6, 1.7) * mm, "end": v(17.66, 1.71) * mm});
            skLineSegment(sketch, "E5055", {"start": v(17.66, 1.71) * mm, "end": v(17.68, 1.72) * mm});
            skLineSegment(sketch, "E5056", {"start": v(17.68, 1.72) * mm, "end": v(17.7, 1.73) * mm});
            skLineSegment(sketch, "E5057", {"start": v(17.7, 1.73) * mm, "end": v(17.73, 1.74) * mm});
            skLineSegment(sketch, "E5058", {"start": v(17.73, 1.74) * mm, "end": v(17.75, 1.75) * mm});
            skLineSegment(sketch, "E5059", {"start": v(17.75, 1.75) * mm, "end": v(17.77, 1.75) * mm});
            skLineSegment(sketch, "E5060", {"start": v(17.77, 1.75) * mm, "end": v(17.8, 1.76) * mm});
            skLineSegment(sketch, "E5061", {"start": v(17.8, 1.76) * mm, "end": v(17.82, 1.77) * mm});
            skLineSegment(sketch, "E5062", {"start": v(17.82, 1.77) * mm, "end": v(17.84, 1.78) * mm});
            skLineSegment(sketch, "E5063", {"start": v(17.84, 1.78) * mm, "end": v(17.88, 1.8) * mm});
            skLineSegment(sketch, "E5064", {"start": v(17.88, 1.8) * mm, "end": v(17.92, 1.81) * mm});
            skLineSegment(sketch, "E5065", {"start": v(17.92, 1.81) * mm, "end": v(17.96, 1.83) * mm});
            skLineSegment(sketch, "E5066", {"start": v(17.96, 1.83) * mm, "end": v(18, 1.84) * mm});
            skLineSegment(sketch, "E5067", {"start": v(18, 1.84) * mm, "end": v(18.03, 1.85) * mm});
            skLineSegment(sketch, "E5068", {"start": v(18.03, 1.85) * mm, "end": v(18.07, 1.86) * mm});
            skLineSegment(sketch, "E5069", {"start": v(18.07, 1.86) * mm, "end": v(18.1, 1.87) * mm});
            skLineSegment(sketch, "E5070", {"start": v(18.1, 1.87) * mm, "end": v(18.15, 1.88) * mm});
            skLineSegment(sketch, "E5071", {"start": v(18.15, 1.88) * mm, "end": v(18.29, 1.92) * mm});
            skLineSegment(sketch, "E5072", {"start": v(18.29, 1.92) * mm, "end": v(18.42, 1.96) * mm});
            skLineSegment(sketch, "E5073", {"start": v(18.42, 1.96) * mm, "end": v(18.55, 2) * mm});
            skLineSegment(sketch, "E5074", {"start": v(18.55, 2) * mm, "end": v(18.68, 2.06) * mm});
            skLineSegment(sketch, "E5075", {"start": v(18.68, 2.06) * mm, "end": v(18.8, 2.11) * mm});
            skLineSegment(sketch, "E5076", {"start": v(18.8, 2.11) * mm, "end": v(18.93, 2.17) * mm});
            skLineSegment(sketch, "E5077", {"start": v(18.93, 2.17) * mm, "end": v(19.05, 2.24) * mm});
            skLineSegment(sketch, "E5078", {"start": v(19.05, 2.24) * mm, "end": v(19.16, 2.3) * mm});
            skLineSegment(sketch, "E5079", {"start": v(19.16, 2.3) * mm, "end": v(19.3, 2.39) * mm});
            skLineSegment(sketch, "E5080", {"start": v(19.3, 2.39) * mm, "end": v(19.44, 2.49) * mm});
            skLineSegment(sketch, "E5081", {"start": v(19.44, 2.49) * mm, "end": v(19.56, 2.6) * mm});
            skLineSegment(sketch, "E5082", {"start": v(19.56, 2.6) * mm, "end": v(19.67, 2.71) * mm});
            skLineSegment(sketch, "E5083", {"start": v(19.67, 2.71) * mm, "end": v(19.77, 2.83) * mm});
            skLineSegment(sketch, "E5084", {"start": v(19.77, 2.83) * mm, "end": v(19.87, 2.95) * mm});
            skLineSegment(sketch, "E5085", {"start": v(19.87, 2.95) * mm, "end": v(19.95, 3.07) * mm});
            skLineSegment(sketch, "E5086", {"start": v(19.95, 3.07) * mm, "end": v(20.03, 3.2) * mm});
            skLineSegment(sketch, "E5087", {"start": v(20.03, 3.2) * mm, "end": v(20.1, 3.3) * mm});
            skLineSegment(sketch, "E5088", {"start": v(20.1, 3.3) * mm, "end": v(20.16, 3.42) * mm});
            skLineSegment(sketch, "E5089", {"start": v(20.16, 3.42) * mm, "end": v(20.21, 3.54) * mm});
            skLineSegment(sketch, "E5090", {"start": v(20.21, 3.54) * mm, "end": v(20.26, 3.67) * mm});
            skLineSegment(sketch, "E5091", {"start": v(20.26, 3.67) * mm, "end": v(20.3, 3.8) * mm});
            skLineSegment(sketch, "E5092", {"start": v(20.3, 3.8) * mm, "end": v(20.35, 3.95) * mm});
            skLineSegment(sketch, "E5093", {"start": v(20.35, 3.95) * mm, "end": v(20.38, 4.1) * mm});
            skLineSegment(sketch, "E5094", {"start": v(20.38, 4.1) * mm, "end": v(20.4, 4.26) * mm});
            skLineSegment(sketch, "E5095", {"start": v(20.4, 4.26) * mm, "end": v(20.41, 4.3) * mm});
            skLineSegment(sketch, "E5096", {"start": v(20.41, 4.3) * mm, "end": v(20.42, 4.32) * mm});
            skLineSegment(sketch, "E5097", {"start": v(20.42, 4.32) * mm, "end": v(20.43, 4.35) * mm});
            skLineSegment(sketch, "E5098", {"start": v(20.43, 4.35) * mm, "end": v(20.45, 4.38) * mm});
            skLineSegment(sketch, "E5099", {"start": v(20.45, 4.38) * mm, "end": v(20.46, 4.4) * mm});
            skLineSegment(sketch, "E5100", {"start": v(20.46, 4.4) * mm, "end": v(20.49, 4.43) * mm});
            skLineSegment(sketch, "E5101", {"start": v(20.49, 4.43) * mm, "end": v(20.51, 4.44) * mm});
            skLineSegment(sketch, "E5102", {"start": v(20.51, 4.44) * mm, "end": v(20.54, 4.45) * mm});
            skLineSegment(sketch, "E5103", {"start": v(20.54, 4.45) * mm, "end": v(20.55, 4.45) * mm});
            skLineSegment(sketch, "E5104", {"start": v(20.55, 4.45) * mm, "end": v(20.56, 4.45) * mm});
            skLineSegment(sketch, "E5105", {"start": v(20.56, 4.45) * mm, "end": v(20.57, 4.45) * mm});
            skLineSegment(sketch, "E5106", {"start": v(20.57, 4.45) * mm, "end": v(20.59, 4.44) * mm});
            skLineSegment(sketch, "E5107", {"start": v(20.59, 4.44) * mm, "end": v(20.6, 4.44) * mm});
            skLineSegment(sketch, "E5108", {"start": v(20.6, 4.44) * mm, "end": v(20.6, 4.44) * mm});
            skLineSegment(sketch, "E5109", {"start": v(20.6, 4.44) * mm, "end": v(20.62, 4.43) * mm});
            skLineSegment(sketch, "E5110", {"start": v(20.62, 4.43) * mm, "end": v(20.63, 4.43) * mm});
            skLineSegment(sketch, "E5111", {"start": v(20.63, 4.43) * mm, "end": v(20.72, 4.39) * mm});
            skLineSegment(sketch, "E5112", {"start": v(20.72, 4.39) * mm, "end": v(20.79, 4.36) * mm});
            skLineSegment(sketch, "E5113", {"start": v(20.79, 4.36) * mm, "end": v(20.84, 4.33) * mm});
            skLineSegment(sketch, "E5114", {"start": v(20.84, 4.33) * mm, "end": v(20.87, 4.32) * mm});
            skLineSegment(sketch, "E5115", {"start": v(20.87, 4.32) * mm, "end": v(20.89, 4.31) * mm});
            skLineSegment(sketch, "E5116", {"start": v(20.89, 4.31) * mm, "end": v(20.9, 4.3) * mm});
            skLineSegment(sketch, "E5117", {"start": v(20.9, 4.3) * mm, "end": v(20.9, 4.3) * mm});
            skLineSegment(sketch, "E5118", {"start": v(20.9, 4.3) * mm, "end": v(21, 4.24) * mm});
            skLineSegment(sketch, "E5119", {"start": v(21, 4.24) * mm, "end": v(21.1, 4.18) * mm});
            skLineSegment(sketch, "E5120", {"start": v(21.1, 4.18) * mm, "end": v(21.2, 4.12) * mm});
            skLineSegment(sketch, "E5121", {"start": v(21.2, 4.12) * mm, "end": v(21.29, 4.07) * mm});
            skLineSegment(sketch, "E5122", {"start": v(21.29, 4.07) * mm, "end": v(21.36, 4.02) * mm});
            skLineSegment(sketch, "E5123", {"start": v(21.36, 4.02) * mm, "end": v(21.42, 3.99) * mm});
            skLineSegment(sketch, "E5124", {"start": v(21.42, 3.99) * mm, "end": v(21.47, 3.96) * mm});
            skLineSegment(sketch, "E5125", {"start": v(21.47, 3.96) * mm, "end": v(21.5, 3.94) * mm});
            skLineSegment(sketch, "E5126", {"start": v(21.5, 3.94) * mm, "end": v(21.51, 3.93) * mm});
            skLineSegment(sketch, "E5127", {"start": v(21.51, 3.93) * mm, "end": v(21.53, 3.9) * mm});
            skLineSegment(sketch, "E5128", {"start": v(21.53, 3.9) * mm, "end": v(21.56, 3.88) * mm});
            skLineSegment(sketch, "E5129", {"start": v(21.56, 3.88) * mm, "end": v(21.58, 3.84) * mm});
            skLineSegment(sketch, "E5130", {"start": v(21.58, 3.84) * mm, "end": v(21.61, 3.8) * mm});
            skLineSegment(sketch, "E5131", {"start": v(21.61, 3.8) * mm, "end": v(21.64, 3.76) * mm});
            skLineSegment(sketch, "E5132", {"start": v(21.64, 3.76) * mm, "end": v(21.67, 3.72) * mm});
            skLineSegment(sketch, "E5133", {"start": v(21.67, 3.72) * mm, "end": v(21.7, 3.67) * mm});
            skLineSegment(sketch, "E5134", {"start": v(21.7, 3.67) * mm, "end": v(21.7, 3.67) * mm});
            skLineSegment(sketch, "E5135", {"start": v(21.7, 3.67) * mm, "end": v(21.69, 3.66) * mm});
            skLineSegment(sketch, "E5136", {"start": v(21.69, 3.66) * mm, "end": v(21.69, 3.65) * mm});
            skLineSegment(sketch, "E5137", {"start": v(21.69, 3.65) * mm, "end": v(21.68, 3.64) * mm});
            skLineSegment(sketch, "E5138", {"start": v(21.68, 3.64) * mm, "end": v(21.68, 3.62) * mm});
            skLineSegment(sketch, "E5139", {"start": v(21.68, 3.62) * mm, "end": v(21.67, 3.6) * mm});
            skLineSegment(sketch, "E5140", {"start": v(21.67, 3.6) * mm, "end": v(21.66, 3.56) * mm});
            skLineSegment(sketch, "E5141", {"start": v(21.66, 3.56) * mm, "end": v(21.64, 3.52) * mm});
            skLineSegment(sketch, "E5142", {"start": v(21.64, 3.52) * mm, "end": v(21.63, 3.49) * mm});
            skLineSegment(sketch, "E5143", {"start": v(21.63, 3.49) * mm, "end": v(21.61, 3.45) * mm});
            skLineSegment(sketch, "E5144", {"start": v(21.61, 3.45) * mm, "end": v(21.6, 3.42) * mm});
            skLineSegment(sketch, "E5145", {"start": v(21.6, 3.42) * mm, "end": v(21.58, 3.38) * mm});
            skLineSegment(sketch, "E5146", {"start": v(21.58, 3.38) * mm, "end": v(21.57, 3.35) * mm});
            skLineSegment(sketch, "E5147", {"start": v(21.57, 3.35) * mm, "end": v(21.55, 3.31) * mm});
            skLineSegment(sketch, "E5148", {"start": v(21.55, 3.31) * mm, "end": v(21.54, 3.29) * mm});
            skLineSegment(sketch, "E5149", {"start": v(21.54, 3.29) * mm, "end": v(21.53, 3.27) * mm});
            skLineSegment(sketch, "E5150", {"start": v(21.53, 3.27) * mm, "end": v(21.52, 3.25) * mm});
            skLineSegment(sketch, "E5151", {"start": v(21.52, 3.25) * mm, "end": v(21.52, 3.24) * mm});
            skLineSegment(sketch, "E5152", {"start": v(21.52, 3.24) * mm, "end": v(21.51, 3.24) * mm});
            skLineSegment(sketch, "E5153", {"start": v(21.51, 3.24) * mm, "end": v(21.51, 3.23) * mm});
            skLineSegment(sketch, "E5154", {"start": v(21.51, 3.23) * mm, "end": v(21.51, 3.23) * mm});
            skLineSegment(sketch, "E5155", {"start": v(21.51, 3.23) * mm, "end": v(21.5, 3.2) * mm});
            skLineSegment(sketch, "E5156", {"start": v(21.5, 3.2) * mm, "end": v(21.49, 3.17) * mm});
            skLineSegment(sketch, "E5157", {"start": v(21.49, 3.17) * mm, "end": v(21.47, 3.14) * mm});
            skLineSegment(sketch, "E5158", {"start": v(21.47, 3.14) * mm, "end": v(21.46, 3.1) * mm});
            skLineSegment(sketch, "E5159", {"start": v(21.46, 3.1) * mm, "end": v(21.45, 3.08) * mm});
            skLineSegment(sketch, "E5160", {"start": v(21.45, 3.08) * mm, "end": v(21.44, 3.06) * mm});
            skLineSegment(sketch, "E5161", {"start": v(21.44, 3.06) * mm, "end": v(21.44, 3.05) * mm});
            skLineSegment(sketch, "E5162", {"start": v(21.44, 3.05) * mm, "end": v(21.43, 3.04) * mm});
            skLineSegment(sketch, "E5163", {"start": v(21.43, 3.04) * mm, "end": v(21.43, 3.02) * mm});
            skLineSegment(sketch, "E5164", {"start": v(21.43, 3.02) * mm, "end": v(21.42, 3) * mm});
            skLineSegment(sketch, "E5165", {"start": v(21.42, 3) * mm, "end": v(21.4, 2.94) * mm});
            skLineSegment(sketch, "E5166", {"start": v(21.4, 2.94) * mm, "end": v(21.38, 2.88) * mm});
            skLineSegment(sketch, "E5167", {"start": v(21.38, 2.88) * mm, "end": v(21.35, 2.81) * mm});
            skLineSegment(sketch, "E5168", {"start": v(21.35, 2.81) * mm, "end": v(21.32, 2.73) * mm});
            skLineSegment(sketch, "E5169", {"start": v(21.32, 2.73) * mm, "end": v(21.29, 2.65) * mm});
            skLineSegment(sketch, "E5170", {"start": v(21.29, 2.65) * mm, "end": v(21.25, 2.55) * mm});
            skLineSegment(sketch, "E5171", {"start": v(21.25, 2.55) * mm, "end": v(21.25, 2.55) * mm});
            skLineSegment(sketch, "E5172", {"start": v(21.25, 2.55) * mm, "end": v(21.25, 2.54) * mm});
            skLineSegment(sketch, "E5173", {"start": v(21.25, 2.54) * mm, "end": v(21.25, 2.52) * mm});
            skLineSegment(sketch, "E5174", {"start": v(21.25, 2.52) * mm, "end": v(21.24, 2.5) * mm});
            skLineSegment(sketch, "E5175", {"start": v(21.24, 2.5) * mm, "end": v(21.23, 2.45) * mm});
            skLineSegment(sketch, "E5176", {"start": v(21.23, 2.45) * mm, "end": v(21.21, 2.4) * mm});
            skLineSegment(sketch, "E5177", {"start": v(21.21, 2.4) * mm, "end": v(21.2, 2.32) * mm});
            skLineSegment(sketch, "E5178", {"start": v(21.2, 2.32) * mm, "end": v(21.19, 2.3) * mm});
            skLineSegment(sketch, "E5179", {"start": v(21.19, 2.3) * mm, "end": v(21.18, 2.27) * mm});
            skLineSegment(sketch, "E5180", {"start": v(21.18, 2.27) * mm, "end": v(21.18, 2.24) * mm});
            skLineSegment(sketch, "E5181", {"start": v(21.18, 2.24) * mm, "end": v(21.17, 2.22) * mm});
            skLineSegment(sketch, "E5182", {"start": v(21.17, 2.22) * mm, "end": v(21.16, 2.2) * mm});
            skLineSegment(sketch, "E5183", {"start": v(21.16, 2.2) * mm, "end": v(21.16, 2.17) * mm});
            skLineSegment(sketch, "E5184", {"start": v(21.16, 2.17) * mm, "end": v(21.15, 2.14) * mm});
            skLineSegment(sketch, "E5185", {"start": v(21.15, 2.14) * mm, "end": v(21.14, 2.12) * mm});
            skLineSegment(sketch, "E5186", {"start": v(21.14, 2.12) * mm, "end": v(21.12, 2.02) * mm});
            skLineSegment(sketch, "E5187", {"start": v(21.12, 2.02) * mm, "end": v(21.1, 1.92) * mm});
            skLineSegment(sketch, "E5188", {"start": v(21.1, 1.92) * mm, "end": v(21.07, 1.83) * mm});
            skLineSegment(sketch, "E5189", {"start": v(21.07, 1.83) * mm, "end": v(21.05, 1.73) * mm});
            skLineSegment(sketch, "E5190", {"start": v(21.05, 1.73) * mm, "end": v(21.04, 1.63) * mm});
            skLineSegment(sketch, "E5191", {"start": v(21.04, 1.63) * mm, "end": v(21.03, 1.52) * mm});
            skLineSegment(sketch, "E5192", {"start": v(21.03, 1.52) * mm, "end": v(21.04, 1.42) * mm});
            skLineSegment(sketch, "E5193", {"start": v(21.04, 1.42) * mm, "end": v(21.06, 1.31) * mm});
            skLineSegment(sketch, "E5194", {"start": v(21.06, 1.31) * mm, "end": v(21.06, 1.3) * mm});
            skLineSegment(sketch, "E5195", {"start": v(21.06, 1.3) * mm, "end": v(21.06, 1.3) * mm});
            skLineSegment(sketch, "E5196", {"start": v(21.06, 1.3) * mm, "end": v(21.06, 1.28) * mm});
            skLineSegment(sketch, "E5197", {"start": v(21.06, 1.28) * mm, "end": v(21.06, 1.27) * mm});
            skLineSegment(sketch, "E5198", {"start": v(21.06, 1.27) * mm, "end": v(21.07, 1.26) * mm});
            skLineSegment(sketch, "E5199", {"start": v(21.07, 1.26) * mm, "end": v(21.07, 1.25) * mm});
            skLineSegment(sketch, "E5200", {"start": v(21.07, 1.25) * mm, "end": v(21.07, 1.24) * mm});
            skLineSegment(sketch, "E5201", {"start": v(21.07, 1.24) * mm, "end": v(21.07, 1.23) * mm});
            skLineSegment(sketch, "E5202", {"start": v(21.07, 1.23) * mm, "end": v(21.08, 1.22) * mm});
            skLineSegment(sketch, "E5203", {"start": v(21.08, 1.22) * mm, "end": v(21.08, 1.2) * mm});
            skLineSegment(sketch, "E5204", {"start": v(21.08, 1.2) * mm, "end": v(21.09, 1.2) * mm});
            skLineSegment(sketch, "E5205", {"start": v(21.09, 1.2) * mm, "end": v(21.09, 1.18) * mm});
            skLineSegment(sketch, "E5206", {"start": v(21.09, 1.18) * mm, "end": v(21.1, 1.17) * mm});
            skLineSegment(sketch, "E5207", {"start": v(21.1, 1.17) * mm, "end": v(21.1, 1.15) * mm});
            skLineSegment(sketch, "E5208", {"start": v(21.1, 1.15) * mm, "end": v(21.1, 1.14) * mm});
            skLineSegment(sketch, "E5209", {"start": v(21.1, 1.14) * mm, "end": v(21.1, 1.13) * mm});
            skLineSegment(sketch, "E5210", {"start": v(21.1, 1.13) * mm, "end": v(21.1, 1.07) * mm});
            skLineSegment(sketch, "E5211", {"start": v(21.1, 1.07) * mm, "end": v(21.1, 1.02) * mm});
            skLineSegment(sketch, "E5212", {"start": v(21.1, 1.02) * mm, "end": v(21.1, 0.97) * mm});
            skLineSegment(sketch, "E5213", {"start": v(21.1, 0.97) * mm, "end": v(21.11, 0.91) * mm});
            skLineSegment(sketch, "E5214", {"start": v(21.11, 0.91) * mm, "end": v(21.12, 0.86) * mm});
            skLineSegment(sketch, "E5215", {"start": v(21.12, 0.86) * mm, "end": v(21.12, 0.8) * mm});
            skLineSegment(sketch, "E5216", {"start": v(21.12, 0.8) * mm, "end": v(21.12, 0.75) * mm});
            skLineSegment(sketch, "E5217", {"start": v(21.12, 0.75) * mm, "end": v(21.13, 0.7) * mm});
            skLineSegment(sketch, "E5218", {"start": v(21.13, 0.7) * mm, "end": v(21.13, 0.64) * mm});
            skLineSegment(sketch, "E5219", {"start": v(21.13, 0.64) * mm, "end": v(21.13, 0.59) * mm});
            skLineSegment(sketch, "E5220", {"start": v(21.13, 0.59) * mm, "end": v(21.14, 0.53) * mm});
            skLineSegment(sketch, "E5221", {"start": v(21.14, 0.53) * mm, "end": v(21.14, 0.48) * mm});
            skLineSegment(sketch, "E5222", {"start": v(21.14, 0.48) * mm, "end": v(21.14, 0.42) * mm});
            skLineSegment(sketch, "E5223", {"start": v(21.14, 0.42) * mm, "end": v(21.15, 0.36) * mm});
            skLineSegment(sketch, "E5224", {"start": v(21.15, 0.36) * mm, "end": v(21.15, 0.3) * mm});
            skLineSegment(sketch, "E5225", {"start": v(21.15, 0.3) * mm, "end": v(21.16, 0.25) * mm});
            skLineSegment(sketch, "E5226", {"start": v(21.16, 0.25) * mm, "end": v(21.16, 0.23) * mm});
            skLineSegment(sketch, "E5227", {"start": v(21.16, 0.23) * mm, "end": v(21.16, 0.21) * mm});
            skLineSegment(sketch, "E5228", {"start": v(21.16, 0.21) * mm, "end": v(21.16, 0.2) * mm});
            skLineSegment(sketch, "E5229", {"start": v(21.16, 0.2) * mm, "end": v(21.16, 0.2) * mm});
            skLineSegment(sketch, "E5230", {"start": v(21.16, 0.2) * mm, "end": v(21.16, 0.19) * mm});
            skLineSegment(sketch, "E5231", {"start": v(21.16, 0.19) * mm, "end": v(21.16, 0.18) * mm});
            skLineSegment(sketch, "E5232", {"start": v(21.16, 0.18) * mm, "end": v(21.16, 0.18) * mm});
            skLineSegment(sketch, "E5233", {"start": v(21.16, 0.18) * mm, "end": v(21.17, 0.16) * mm});
            skLineSegment(sketch, "E5234", {"start": v(21.17, 0.16) * mm, "end": v(21.18, 0.13) * mm});
            skLineSegment(sketch, "E5235", {"start": v(21.18, 0.13) * mm, "end": v(21.18, 0.1) * mm});
            skLineSegment(sketch, "E5236", {"start": v(21.18, 0.1) * mm, "end": v(21.2, 0.07) * mm});
            skLineSegment(sketch, "E5237", {"start": v(21.2, 0.07) * mm, "end": v(21.2, 0.05) * mm});
            skLineSegment(sketch, "E5238", {"start": v(21.2, 0.05) * mm, "end": v(21.2, 0.02) * mm});
            skLineSegment(sketch, "E5239", {"start": v(21.2, 0.02) * mm, "end": v(21.21, 0) * mm});
            skLineSegment(sketch, "E5240", {"start": v(21.21, 0) * mm, "end": v(21.22, -0.02) * mm});
            skLineSegment(sketch, "E5241", {"start": v(21.22, -0.02) * mm, "end": v(21.22, -0.04) * mm});
            skLineSegment(sketch, "E5242", {"start": v(21.22, -0.04) * mm, "end": v(21.23, -0.07) * mm});
            skLineSegment(sketch, "E5243", {"start": v(21.23, -0.07) * mm, "end": v(21.24, -0.1) * mm});
            skLineSegment(sketch, "E5244", {"start": v(21.24, -0.1) * mm, "end": v(21.25, -0.15) * mm});
            skLineSegment(sketch, "E5245", {"start": v(21.25, -0.15) * mm, "end": v(21.26, -0.2) * mm});
            skLineSegment(sketch, "E5246", {"start": v(21.26, -0.2) * mm, "end": v(21.28, -0.25) * mm});
            skLineSegment(sketch, "E5247", {"start": v(21.28, -0.25) * mm, "end": v(21.3, -0.3) * mm});
            skLineSegment(sketch, "E5248", {"start": v(21.3, -0.3) * mm, "end": v(21.3, -0.35) * mm});
            skLineSegment(sketch, "E5249", {"start": v(21.3, -0.35) * mm, "end": v(21.3, -0.35) * mm});
            skLineSegment(sketch, "E5250", {"start": v(21.3, -0.35) * mm, "end": v(21.3, -0.36) * mm});
            skLineSegment(sketch, "E5251", {"start": v(21.3, -0.36) * mm, "end": v(21.3, -0.36) * mm});
            skLineSegment(sketch, "E5252", {"start": v(21.3, -0.36) * mm, "end": v(21.31, -0.38) * mm});
            skLineSegment(sketch, "E5253", {"start": v(21.31, -0.38) * mm, "end": v(21.32, -0.4) * mm});
            skLineSegment(sketch, "E5254", {"start": v(21.32, -0.4) * mm, "end": v(21.33, -0.43) * mm});
            skLineSegment(sketch, "E5255", {"start": v(21.33, -0.43) * mm, "end": v(21.35, -0.47) * mm});
            skLineSegment(sketch, "E5256", {"start": v(21.35, -0.47) * mm, "end": v(21.36, -0.5) * mm});
            skLineSegment(sketch, "E5257", {"start": v(21.36, -0.5) * mm, "end": v(21.38, -0.54) * mm});
            skLineSegment(sketch, "E5258", {"start": v(21.38, -0.54) * mm, "end": v(21.4, -0.58) * mm});
            skLineSegment(sketch, "E5259", {"start": v(21.4, -0.58) * mm, "end": v(21.42, -0.62) * mm});
            skLineSegment(sketch, "E5260", {"start": v(21.42, -0.62) * mm, "end": v(21.45, -0.65) * mm});
            skLineSegment(sketch, "E5261", {"start": v(21.45, -0.65) * mm, "end": v(21.48, -0.69) * mm});
            skLineSegment(sketch, "E5262", {"start": v(21.48, -0.69) * mm, "end": v(21.51, -0.72) * mm});
            skLineSegment(sketch, "E5263", {"start": v(21.51, -0.72) * mm, "end": v(21.55, -0.74) * mm});
            skLineSegment(sketch, "E5264", {"start": v(21.55, -0.74) * mm, "end": v(21.56, -0.74) * mm});
            skLineSegment(sketch, "E5265", {"start": v(21.56, -0.74) * mm, "end": v(21.57, -0.74) * mm});
            skLineSegment(sketch, "E5266", {"start": v(21.57, -0.74) * mm, "end": v(21.57, -0.75) * mm});
            skLineSegment(sketch, "E5267", {"start": v(21.57, -0.75) * mm, "end": v(21.58, -0.75) * mm});
            skLineSegment(sketch, "E5268", {"start": v(21.58, -0.75) * mm, "end": v(21.59, -0.75) * mm});
            skLineSegment(sketch, "E5269", {"start": v(21.59, -0.75) * mm, "end": v(21.6, -0.75) * mm});
            skLineSegment(sketch, "E5270", {"start": v(21.6, -0.75) * mm, "end": v(21.6, -0.75) * mm});
            skLineSegment(sketch, "E5271", {"start": v(21.6, -0.75) * mm, "end": v(21.61, -0.75) * mm});
            skLineSegment(sketch, "E5272", {"start": v(21.61, -0.75) * mm, "end": v(21.65, -0.75) * mm});
            skLineSegment(sketch, "E5273", {"start": v(21.65, -0.75) * mm, "end": v(21.68, -0.74) * mm});
            skLineSegment(sketch, "E5274", {"start": v(21.68, -0.74) * mm, "end": v(21.72, -0.72) * mm});
            skLineSegment(sketch, "E5275", {"start": v(21.72, -0.72) * mm, "end": v(21.75, -0.7) * mm});
            skLineSegment(sketch, "E5276", {"start": v(21.75, -0.7) * mm, "end": v(21.78, -0.69) * mm});
            skLineSegment(sketch, "E5277", {"start": v(21.78, -0.69) * mm, "end": v(21.81, -0.66) * mm});
            skLineSegment(sketch, "E5278", {"start": v(21.81, -0.66) * mm, "end": v(21.84, -0.64) * mm});
            skLineSegment(sketch, "E5279", {"start": v(21.84, -0.64) * mm, "end": v(21.86, -0.62) * mm});
            skLineSegment(sketch, "E5280", {"start": v(21.86, -0.62) * mm, "end": v(21.93, -0.57) * mm});
            skLineSegment(sketch, "E5281", {"start": v(21.93, -0.57) * mm, "end": v(22, -0.51) * mm});
            skLineSegment(sketch, "E5282", {"start": v(22, -0.51) * mm, "end": v(22.06, -0.46) * mm});
            skLineSegment(sketch, "E5283", {"start": v(22.06, -0.46) * mm, "end": v(22.12, -0.4) * mm});
            skLineSegment(sketch, "E5284", {"start": v(22.12, -0.4) * mm, "end": v(22.19, -0.34) * mm});
            skLineSegment(sketch, "E5285", {"start": v(22.19, -0.34) * mm, "end": v(22.25, -0.28) * mm});
            skLineSegment(sketch, "E5286", {"start": v(22.25, -0.28) * mm, "end": v(22.31, -0.22) * mm});
            skLineSegment(sketch, "E5287", {"start": v(22.31, -0.22) * mm, "end": v(22.38, -0.15) * mm});
            skLineSegment(sketch, "E5288", {"start": v(22.38, -0.15) * mm, "end": v(22.45, -0.08) * mm});
            skLineSegment(sketch, "E5289", {"start": v(22.45, -0.08) * mm, "end": v(22.51, 0) * mm});
            skLineSegment(sketch, "E5290", {"start": v(22.51, 0) * mm, "end": v(22.58, 0.06) * mm});
            skLineSegment(sketch, "E5291", {"start": v(22.58, 0.06) * mm, "end": v(22.64, 0.13) * mm});
            skLineSegment(sketch, "E5292", {"start": v(22.64, 0.13) * mm, "end": v(22.7, 0.2) * mm});
            skLineSegment(sketch, "E5293", {"start": v(22.7, 0.2) * mm, "end": v(22.75, 0.27) * mm});
            skLineSegment(sketch, "E5294", {"start": v(22.75, 0.27) * mm, "end": v(22.8, 0.34) * mm});
            skLineSegment(sketch, "E5295", {"start": v(22.8, 0.34) * mm, "end": v(22.85, 0.4) * mm});
            skLineSegment(sketch, "E5296", {"start": v(22.85, 0.4) * mm, "end": v(22.89, 0.46) * mm});
            skLineSegment(sketch, "E5297", {"start": v(22.89, 0.46) * mm, "end": v(22.91, 0.5) * mm});
            skLineSegment(sketch, "E5298", {"start": v(22.91, 0.5) * mm, "end": v(22.93, 0.53) * mm});
            skLineSegment(sketch, "E5299", {"start": v(22.93, 0.53) * mm, "end": v(22.95, 0.55) * mm});
            skLineSegment(sketch, "E5300", {"start": v(22.95, 0.55) * mm, "end": v(22.96, 0.56) * mm});
            skLineSegment(sketch, "E5301", {"start": v(22.96, 0.56) * mm, "end": v(22.96, 0.57) * mm});
            skLineSegment(sketch, "E5302", {"start": v(22.96, 0.57) * mm, "end": v(22.96, 0.57) * mm});
            skLineSegment(sketch, "E5303", {"start": v(22.96, 0.57) * mm, "end": v(23, 0.65) * mm});
            skLineSegment(sketch, "E5304", {"start": v(23, 0.65) * mm, "end": v(23.02, 0.72) * mm});
            skLineSegment(sketch, "E5305", {"start": v(23.02, 0.72) * mm, "end": v(23.05, 0.78) * mm});
            skLineSegment(sketch, "E5306", {"start": v(23.05, 0.78) * mm, "end": v(23.08, 0.84) * mm});
            skLineSegment(sketch, "E5307", {"start": v(23.08, 0.84) * mm, "end": v(23.1, 0.89) * mm});
            skLineSegment(sketch, "E5308", {"start": v(23.1, 0.89) * mm, "end": v(23.12, 0.92) * mm});
            skLineSegment(sketch, "E5309", {"start": v(23.12, 0.92) * mm, "end": v(23.13, 0.95) * mm});
            skLineSegment(sketch, "E5310", {"start": v(23.13, 0.95) * mm, "end": v(23.13, 0.96) * mm});
            skLineSegment(sketch, "E5311", {"start": v(23.13, 0.96) * mm, "end": v(23.14, 0.98) * mm});
            skLineSegment(sketch, "E5312", {"start": v(23.14, 0.98) * mm, "end": v(23.16, 1.01) * mm});
            skLineSegment(sketch, "E5313", {"start": v(23.16, 1.01) * mm, "end": v(23.18, 1.06) * mm});
            skLineSegment(sketch, "E5314", {"start": v(23.18, 1.06) * mm, "end": v(23.2, 1.13) * mm});
            skLineSegment(sketch, "E5315", {"start": v(23.2, 1.13) * mm, "end": v(23.24, 1.2) * mm});
            skLineSegment(sketch, "E5316", {"start": v(23.24, 1.2) * mm, "end": v(23.28, 1.3) * mm});
            skLineSegment(sketch, "E5317", {"start": v(23.28, 1.3) * mm, "end": v(23.32, 1.39) * mm});
            skLineSegment(sketch, "E5318", {"start": v(23.32, 1.39) * mm, "end": v(23.37, 1.49) * mm});
            skLineSegment(sketch, "E5319", {"start": v(23.37, 1.49) * mm, "end": v(23.37, 1.49) * mm});
            skLineSegment(sketch, "E5320", {"start": v(23.37, 1.49) * mm, "end": v(23.37, 1.5) * mm});
            skLineSegment(sketch, "E5321", {"start": v(23.37, 1.5) * mm, "end": v(23.37, 1.5) * mm});
            skLineSegment(sketch, "E5322", {"start": v(23.37, 1.5) * mm, "end": v(23.38, 1.52) * mm});
            skLineSegment(sketch, "E5323", {"start": v(23.38, 1.52) * mm, "end": v(23.39, 1.55) * mm});
            skLineSegment(sketch, "E5324", {"start": v(23.39, 1.55) * mm, "end": v(23.4, 1.6) * mm});
            skLineSegment(sketch, "E5325", {"start": v(23.4, 1.6) * mm, "end": v(23.43, 1.67) * mm});
            skLineSegment(sketch, "E5326", {"start": v(23.43, 1.67) * mm, "end": v(23.46, 1.76) * mm});
            skLineSegment(sketch, "E5327", {"start": v(23.46, 1.76) * mm, "end": v(23.5, 1.93) * mm});
            skLineSegment(sketch, "E5328", {"start": v(23.5, 1.93) * mm, "end": v(23.55, 2.1) * mm});
            skLineSegment(sketch, "E5329", {"start": v(23.55, 2.1) * mm, "end": v(23.57, 2.29) * mm});
            skLineSegment(sketch, "E5330", {"start": v(23.57, 2.29) * mm, "end": v(23.57, 2.47) * mm});
            skLineSegment(sketch, "E5331", {"start": v(23.57, 2.47) * mm, "end": v(23.57, 2.66) * mm});
            skLineSegment(sketch, "E5332", {"start": v(23.57, 2.66) * mm, "end": v(23.54, 2.85) * mm});
            skLineSegment(sketch, "E5333", {"start": v(23.54, 2.85) * mm, "end": v(23.5, 3.05) * mm});
            skLineSegment(sketch, "E5334", {"start": v(23.5, 3.05) * mm, "end": v(23.46, 3.24) * mm});
            skLineSegment(sketch, "E5335", {"start": v(23.46, 3.24) * mm, "end": v(23.45, 3.28) * mm});
            skLineSegment(sketch, "E5336", {"start": v(23.45, 3.28) * mm, "end": v(23.44, 3.3) * mm});
            skLineSegment(sketch, "E5337", {"start": v(23.44, 3.3) * mm, "end": v(23.43, 3.32) * mm});
            skLineSegment(sketch, "E5338", {"start": v(23.43, 3.32) * mm, "end": v(23.43, 3.33) * mm});
            skLineSegment(sketch, "E5339", {"start": v(23.43, 3.33) * mm, "end": v(23.43, 3.34) * mm});
            skLineSegment(sketch, "E5340", {"start": v(23.43, 3.34) * mm, "end": v(23.43, 3.35) * mm});
            skLineSegment(sketch, "E5341", {"start": v(23.43, 3.35) * mm, "end": v(23.43, 3.35) * mm});
            skLineSegment(sketch, "E5342", {"start": v(23.43, 3.35) * mm, "end": v(23.43, 3.36) * mm});
            skLineSegment(sketch, "E5343", {"start": v(23.43, 3.36) * mm, "end": v(23.43, 3.36) * mm});
            skLineSegment(sketch, "E5344", {"start": v(23.43, 3.36) * mm, "end": v(23.44, 3.37) * mm});
            skLineSegment(sketch, "E5345", {"start": v(23.44, 3.37) * mm, "end": v(23.44, 3.37) * mm});
            skLineSegment(sketch, "E5346", {"start": v(23.44, 3.37) * mm, "end": v(23.45, 3.38) * mm});
            skLineSegment(sketch, "E5347", {"start": v(23.45, 3.38) * mm, "end": v(23.45, 3.38) * mm});
            skLineSegment(sketch, "E5348", {"start": v(23.45, 3.38) * mm, "end": v(23.45, 3.39) * mm});
            skLineSegment(sketch, "E5349", {"start": v(23.45, 3.39) * mm, "end": v(23.45, 3.39) * mm});
            skLineSegment(sketch, "E5350", {"start": v(23.45, 3.39) * mm, "end": v(23.46, 3.39) * mm});
            skLineSegment(sketch, "E5351", {"start": v(23.46, 3.39) * mm, "end": v(23.46, 3.39) * mm});
            skLineSegment(sketch, "E5352", {"start": v(23.46, 3.39) * mm, "end": v(23.47, 3.39) * mm});
            skLineSegment(sketch, "E5353", {"start": v(23.47, 3.39) * mm, "end": v(23.5, 3.4) * mm});
            skLineSegment(sketch, "E5354", {"start": v(23.5, 3.4) * mm, "end": v(23.51, 3.4) * mm});
            skLineSegment(sketch, "E5355", {"start": v(23.51, 3.4) * mm, "end": v(23.54, 3.4) * mm});
            skLineSegment(sketch, "E5356", {"start": v(23.54, 3.4) * mm, "end": v(23.57, 3.4) * mm});
            skLineSegment(sketch, "E5357", {"start": v(23.57, 3.4) * mm, "end": v(23.6, 3.4) * mm});
            skLineSegment(sketch, "E5358", {"start": v(23.6, 3.4) * mm, "end": v(23.62, 3.4) * mm});
            skLineSegment(sketch, "E5359", {"start": v(23.62, 3.4) * mm, "end": v(23.65, 3.4) * mm});
            skLineSegment(sketch, "E5360", {"start": v(23.65, 3.4) * mm, "end": v(23.68, 3.4) * mm});
            skLineSegment(sketch, "E5361", {"start": v(23.68, 3.4) * mm, "end": v(23.7, 3.4) * mm});
            skLineSegment(sketch, "E5362", {"start": v(23.7, 3.4) * mm, "end": v(23.73, 3.41) * mm});
            skLineSegment(sketch, "E5363", {"start": v(23.73, 3.41) * mm, "end": v(23.76, 3.41) * mm});
            skLineSegment(sketch, "E5364", {"start": v(23.76, 3.41) * mm, "end": v(23.83, 3.42) * mm});
            skLineSegment(sketch, "E5365", {"start": v(23.83, 3.42) * mm, "end": v(23.9, 3.43) * mm});
            skLineSegment(sketch, "E5366", {"start": v(23.9, 3.43) * mm, "end": v(23.98, 3.43) * mm});
            skLineSegment(sketch, "E5367", {"start": v(23.98, 3.43) * mm, "end": v(24.06, 3.44) * mm});
            skLineSegment(sketch, "E5368", {"start": v(24.06, 3.44) * mm, "end": v(24.13, 3.45) * mm});
            skLineSegment(sketch, "E5369", {"start": v(24.13, 3.45) * mm, "end": v(24.2, 3.45) * mm});
            skLineSegment(sketch, "E5370", {"start": v(24.2, 3.45) * mm, "end": v(24.28, 3.45) * mm});
            skLineSegment(sketch, "E5371", {"start": v(24.28, 3.45) * mm, "end": v(24.36, 3.45) * mm});
            skLineSegment(sketch, "E5372", {"start": v(24.36, 3.45) * mm, "end": v(24.38, 3.45) * mm});
            skLineSegment(sketch, "E5373", {"start": v(24.38, 3.45) * mm, "end": v(24.41, 3.44) * mm});
            skLineSegment(sketch, "E5374", {"start": v(24.41, 3.44) * mm, "end": v(24.44, 3.43) * mm});
            skLineSegment(sketch, "E5375", {"start": v(24.44, 3.43) * mm, "end": v(24.47, 3.42) * mm});
            skLineSegment(sketch, "E5376", {"start": v(24.47, 3.42) * mm, "end": v(24.5, 3.4) * mm});
            skLineSegment(sketch, "E5377", {"start": v(24.5, 3.4) * mm, "end": v(24.52, 3.4) * mm});
            skLineSegment(sketch, "E5378", {"start": v(24.52, 3.4) * mm, "end": v(24.53, 3.37) * mm});
            skLineSegment(sketch, "E5379", {"start": v(24.53, 3.37) * mm, "end": v(24.55, 3.36) * mm});
            skLineSegment(sketch, "E5380", {"start": v(24.55, 3.36) * mm, "end": v(24.56, 3.33) * mm});
            skLineSegment(sketch, "E5381", {"start": v(24.56, 3.33) * mm, "end": v(24.58, 3.3) * mm});
            skLineSegment(sketch, "E5382", {"start": v(24.58, 3.3) * mm, "end": v(24.6, 3.26) * mm});
            skLineSegment(sketch, "E5383", {"start": v(24.6, 3.26) * mm, "end": v(24.6, 3.22) * mm});
            skLineSegment(sketch, "E5384", {"start": v(24.6, 3.22) * mm, "end": v(24.61, 3.18) * mm});
            skLineSegment(sketch, "E5385", {"start": v(24.61, 3.18) * mm, "end": v(24.62, 3.14) * mm});
            skLineSegment(sketch, "E5386", {"start": v(24.62, 3.14) * mm, "end": v(24.63, 3.1) * mm});
            skLineSegment(sketch, "E5387", {"start": v(24.63, 3.1) * mm, "end": v(24.64, 3.06) * mm});
            skLineSegment(sketch, "E5388", {"start": v(24.64, 3.06) * mm, "end": v(24.64, 3.04) * mm});
            skLineSegment(sketch, "E5389", {"start": v(24.64, 3.04) * mm, "end": v(24.64, 3.03) * mm});
            skLineSegment(sketch, "E5390", {"start": v(24.64, 3.03) * mm, "end": v(24.64, 3.02) * mm});
            skLineSegment(sketch, "E5391", {"start": v(24.64, 3.02) * mm, "end": v(24.65, 3) * mm});
            skLineSegment(sketch, "E5392", {"start": v(24.65, 3) * mm, "end": v(24.65, 3) * mm});
            skLineSegment(sketch, "E5393", {"start": v(24.65, 3) * mm, "end": v(24.65, 2.98) * mm});
            skLineSegment(sketch, "E5394", {"start": v(24.65, 2.98) * mm, "end": v(24.65, 2.97) * mm});
            skLineSegment(sketch, "E5395", {"start": v(24.65, 2.97) * mm, "end": v(24.66, 2.95) * mm});
            skLineSegment(sketch, "E5396", {"start": v(24.66, 2.95) * mm, "end": v(24.66, 2.94) * mm});
            skLineSegment(sketch, "E5397", {"start": v(24.66, 2.94) * mm, "end": v(24.66, 2.93) * mm});
            skLineSegment(sketch, "E5398", {"start": v(24.66, 2.93) * mm, "end": v(24.66, 2.91) * mm});
            skLineSegment(sketch, "E5399", {"start": v(24.66, 2.91) * mm, "end": v(24.67, 2.9) * mm});
            skLineSegment(sketch, "E5400", {"start": v(24.67, 2.9) * mm, "end": v(24.67, 2.89) * mm});
            skLineSegment(sketch, "E5401", {"start": v(24.67, 2.89) * mm, "end": v(24.67, 2.87) * mm});
            skLineSegment(sketch, "E5402", {"start": v(24.67, 2.87) * mm, "end": v(24.67, 2.86) * mm});
            skLineSegment(sketch, "E5403", {"start": v(24.67, 2.86) * mm, "end": v(24.67, 2.84) * mm});
            skLineSegment(sketch, "E5404", {"start": v(24.67, 2.84) * mm, "end": v(24.67, 2.82) * mm});
            skLineSegment(sketch, "E5405", {"start": v(24.67, 2.82) * mm, "end": v(24.67, 2.8) * mm});
            skLineSegment(sketch, "E5406", {"start": v(24.67, 2.8) * mm, "end": v(24.68, 2.78) * mm});
            skLineSegment(sketch, "E5407", {"start": v(24.68, 2.78) * mm, "end": v(24.68, 2.76) * mm});
            skLineSegment(sketch, "E5408", {"start": v(24.68, 2.76) * mm, "end": v(24.68, 2.73) * mm});
            skLineSegment(sketch, "E5409", {"start": v(24.68, 2.73) * mm, "end": v(24.69, 2.71) * mm});
            skLineSegment(sketch, "E5410", {"start": v(24.69, 2.71) * mm, "end": v(24.7, 2.69) * mm});
            skLineSegment(sketch, "E5411", {"start": v(24.7, 2.69) * mm, "end": v(24.7, 2.67) * mm});
            skLineSegment(sketch, "E5412", {"start": v(24.7, 2.67) * mm, "end": v(24.74, 2.54) * mm});
            skLineSegment(sketch, "E5413", {"start": v(24.74, 2.54) * mm, "end": v(24.78, 2.42) * mm});
            skLineSegment(sketch, "E5414", {"start": v(24.78, 2.42) * mm, "end": v(24.82, 2.3) * mm});
            skLineSegment(sketch, "E5415", {"start": v(24.82, 2.3) * mm, "end": v(24.87, 2.18) * mm});
            skLineSegment(sketch, "E5416", {"start": v(24.87, 2.18) * mm, "end": v(24.9, 2.06) * mm});
            skLineSegment(sketch, "E5417", {"start": v(24.9, 2.06) * mm, "end": v(24.95, 1.94) * mm});
            skLineSegment(sketch, "E5418", {"start": v(24.95, 1.94) * mm, "end": v(24.99, 1.83) * mm});
            skLineSegment(sketch, "E5419", {"start": v(24.99, 1.83) * mm, "end": v(25.03, 1.72) * mm});
            skLineSegment(sketch, "E5420", {"start": v(25.03, 1.72) * mm, "end": v(25.03, 1.7) * mm});
            skLineSegment(sketch, "E5421", {"start": v(25.03, 1.7) * mm, "end": v(25.04, 1.69) * mm});
            skLineSegment(sketch, "E5422", {"start": v(25.04, 1.69) * mm, "end": v(25.04, 1.68) * mm});
            skLineSegment(sketch, "E5423", {"start": v(25.04, 1.68) * mm, "end": v(25.05, 1.66) * mm});
            skLineSegment(sketch, "E5424", {"start": v(25.05, 1.66) * mm, "end": v(25.05, 1.65) * mm});
            skLineSegment(sketch, "E5425", {"start": v(25.05, 1.65) * mm, "end": v(25.06, 1.63) * mm});
            skLineSegment(sketch, "E5426", {"start": v(25.06, 1.63) * mm, "end": v(25.06, 1.62) * mm});
            skLineSegment(sketch, "E5427", {"start": v(25.06, 1.62) * mm, "end": v(25.07, 1.6) * mm});
            skLineSegment(sketch, "E5428", {"start": v(25.07, 1.6) * mm, "end": v(25.08, 1.57) * mm});
            skLineSegment(sketch, "E5429", {"start": v(25.08, 1.57) * mm, "end": v(25.09, 1.54) * mm});
            skLineSegment(sketch, "E5430", {"start": v(25.09, 1.54) * mm, "end": v(25.1, 1.52) * mm});
            skLineSegment(sketch, "E5431", {"start": v(25.1, 1.52) * mm, "end": v(25.1, 1.5) * mm});
            skLineSegment(sketch, "E5432", {"start": v(25.1, 1.5) * mm, "end": v(25.1, 1.5) * mm});
            skLineSegment(sketch, "E5433", {"start": v(25.1, 1.5) * mm, "end": v(25.13, 1.44) * mm});
            skLineSegment(sketch, "E5434", {"start": v(25.13, 1.44) * mm, "end": v(25.15, 1.4) * mm});
            skLineSegment(sketch, "E5435", {"start": v(25.15, 1.4) * mm, "end": v(25.17, 1.35) * mm});
            skLineSegment(sketch, "E5436", {"start": v(25.17, 1.35) * mm, "end": v(25.2, 1.3) * mm});
            skLineSegment(sketch, "E5437", {"start": v(25.2, 1.3) * mm, "end": v(25.21, 1.27) * mm});
            skLineSegment(sketch, "E5438", {"start": v(25.21, 1.27) * mm, "end": v(25.23, 1.24) * mm});
            skLineSegment(sketch, "E5439", {"start": v(25.23, 1.24) * mm, "end": v(25.24, 1.22) * mm});
            skLineSegment(sketch, "E5440", {"start": v(25.24, 1.22) * mm, "end": v(25.25, 1.2) * mm});
            skLineSegment(sketch, "E5441", {"start": v(25.25, 1.2) * mm, "end": v(25.27, 1.17) * mm});
            skLineSegment(sketch, "E5442", {"start": v(25.27, 1.17) * mm, "end": v(25.3, 1.13) * mm});
            skLineSegment(sketch, "E5443", {"start": v(25.3, 1.13) * mm, "end": v(25.34, 1.06) * mm});
            skLineSegment(sketch, "E5444", {"start": v(25.34, 1.06) * mm, "end": v(25.39, 0.98) * mm});
            skLineSegment(sketch, "E5445", {"start": v(25.39, 0.98) * mm, "end": v(25.45, 0.88) * mm});
            skLineSegment(sketch, "E5446", {"start": v(25.45, 0.88) * mm, "end": v(25.51, 0.77) * mm});
            skLineSegment(sketch, "E5447", {"start": v(25.51, 0.77) * mm, "end": v(25.58, 0.66) * mm});
            skLineSegment(sketch, "E5448", {"start": v(25.58, 0.66) * mm, "end": v(25.66, 0.54) * mm});
            skLineSegment(sketch, "E5449", {"start": v(25.66, 0.54) * mm, "end": v(25.66, 0.54) * mm});
            skLineSegment(sketch, "E5450", {"start": v(25.66, 0.54) * mm, "end": v(25.66, 0.53) * mm});
            skLineSegment(sketch, "E5451", {"start": v(25.66, 0.53) * mm, "end": v(25.68, 0.53) * mm});
            skLineSegment(sketch, "E5452", {"start": v(25.68, 0.53) * mm, "end": v(25.7, 0.51) * mm});
            skLineSegment(sketch, "E5453", {"start": v(25.7, 0.51) * mm, "end": v(25.74, 0.49) * mm});
            skLineSegment(sketch, "E5454", {"start": v(25.74, 0.49) * mm, "end": v(25.8, 0.45) * mm});
            skLineSegment(sketch, "E5455", {"start": v(25.8, 0.45) * mm, "end": v(25.88, 0.4) * mm});
            skLineSegment(sketch, "E5456", {"start": v(25.88, 0.4) * mm, "end": v(25.99, 0.33) * mm});
            skLineSegment(sketch, "E5457", {"start": v(25.99, 0.33) * mm, "end": v(26.06, 0.3) * mm});
            skLineSegment(sketch, "E5458", {"start": v(26.06, 0.3) * mm, "end": v(26.13, 0.25) * mm});
            skLineSegment(sketch, "E5459", {"start": v(26.13, 0.25) * mm, "end": v(26.2, 0.2) * mm});
            skLineSegment(sketch, "E5460", {"start": v(26.2, 0.2) * mm, "end": v(26.26, 0.16) * mm});
            skLineSegment(sketch, "E5461", {"start": v(26.26, 0.16) * mm, "end": v(26.33, 0.1) * mm});
            skLineSegment(sketch, "E5462", {"start": v(26.33, 0.1) * mm, "end": v(26.4, 0.06) * mm});
            skLineSegment(sketch, "E5463", {"start": v(26.4, 0.06) * mm, "end": v(26.47, 0.01) * mm});
            skLineSegment(sketch, "E5464", {"start": v(26.47, 0.01) * mm, "end": v(26.54, -0.04) * mm});
            skLineSegment(sketch, "E5465", {"start": v(26.54, -0.04) * mm, "end": v(26.57, -0.06) * mm});
            skLineSegment(sketch, "E5466", {"start": v(26.57, -0.06) * mm, "end": v(26.6, -0.08) * mm});
            skLineSegment(sketch, "E5467", {"start": v(26.6, -0.08) * mm, "end": v(26.6, -0.09) * mm});
            skLineSegment(sketch, "E5468", {"start": v(26.6, -0.09) * mm, "end": v(26.62, -0.1) * mm});
            skLineSegment(sketch, "E5469", {"start": v(26.62, -0.1) * mm, "end": v(26.62, -0.1) * mm});
            skLineSegment(sketch, "E5470", {"start": v(26.62, -0.1) * mm, "end": v(26.63, -0.1) * mm});
            skLineSegment(sketch, "E5471", {"start": v(26.63, -0.1) * mm, "end": v(26.63, -0.1) * mm});
            skLineSegment(sketch, "E5472", {"start": v(26.63, -0.1) * mm, "end": v(26.67, -0.13) * mm});
            skLineSegment(sketch, "E5473", {"start": v(26.67, -0.13) * mm, "end": v(26.7, -0.16) * mm});
            skLineSegment(sketch, "E5474", {"start": v(26.7, -0.16) * mm, "end": v(26.74, -0.18) * mm});
            skLineSegment(sketch, "E5475", {"start": v(26.74, -0.18) * mm, "end": v(26.77, -0.2) * mm});
            skLineSegment(sketch, "E5476", {"start": v(26.77, -0.2) * mm, "end": v(26.8, -0.23) * mm});
            skLineSegment(sketch, "E5477", {"start": v(26.8, -0.23) * mm, "end": v(26.83, -0.24) * mm});
            skLineSegment(sketch, "E5478", {"start": v(26.83, -0.24) * mm, "end": v(26.85, -0.26) * mm});
            skLineSegment(sketch, "E5479", {"start": v(26.85, -0.26) * mm, "end": v(26.86, -0.26) * mm});
            skLineSegment(sketch, "E5480", {"start": v(26.86, -0.26) * mm, "end": v(26.87, -0.27) * mm});
            skLineSegment(sketch, "E5481", {"start": v(26.87, -0.27) * mm, "end": v(26.88, -0.27) * mm});
            skLineSegment(sketch, "E5482", {"start": v(26.88, -0.27) * mm, "end": v(26.89, -0.27) * mm});
            skLineSegment(sketch, "E5483", {"start": v(26.89, -0.27) * mm, "end": v(26.9, -0.27) * mm});
            skLineSegment(sketch, "E5484", {"start": v(26.9, -0.27) * mm, "end": v(26.9, -0.27) * mm});
            skLineSegment(sketch, "E5485", {"start": v(26.9, -0.27) * mm, "end": v(26.92, -0.26) * mm});
            skLineSegment(sketch, "E5486", {"start": v(26.92, -0.26) * mm, "end": v(26.92, -0.26) * mm});
            skLineSegment(sketch, "E5487", {"start": v(26.92, -0.26) * mm, "end": v(26.93, -0.25) * mm});
            skLineSegment(sketch, "E5488", {"start": v(26.93, -0.25) * mm, "end": v(26.94, -0.24) * mm});
            skLineSegment(sketch, "E5489", {"start": v(26.94, -0.24) * mm, "end": v(26.94, -0.22) * mm});
            skLineSegment(sketch, "E5490", {"start": v(26.94, -0.22) * mm, "end": v(26.95, -0.2) * mm});
            skLineSegment(sketch, "E5491", {"start": v(26.95, -0.2) * mm, "end": v(26.97, -0.18) * mm});
            skLineSegment(sketch, "E5492", {"start": v(26.97, -0.18) * mm, "end": v(26.98, -0.15) * mm});
            skLineSegment(sketch, "E5493", {"start": v(26.98, -0.15) * mm, "end": v(27, -0.13) * mm});
            skLineSegment(sketch, "E5494", {"start": v(27, -0.13) * mm, "end": v(27, -0.1) * mm});
            skLineSegment(sketch, "E5495", {"start": v(27, -0.1) * mm, "end": v(27.02, -0.08) * mm});
            skLineSegment(sketch, "E5496", {"start": v(27.02, -0.08) * mm, "end": v(27.02, -0.08) * mm});
            skLineSegment(sketch, "E5497", {"start": v(27.02, -0.08) * mm, "end": v(27.02, -0.07) * mm});
            skLineSegment(sketch, "E5498", {"start": v(27.02, -0.07) * mm, "end": v(27.03, -0.06) * mm});
            skLineSegment(sketch, "E5499", {"start": v(27.03, -0.06) * mm, "end": v(27.03, -0.05) * mm});
            skLineSegment(sketch, "E5500", {"start": v(27.03, -0.05) * mm, "end": v(27.04, -0.04) * mm});
            skLineSegment(sketch, "E5501", {"start": v(27.04, -0.04) * mm, "end": v(27.05, -0.02) * mm});
            skLineSegment(sketch, "E5502", {"start": v(27.05, -0.02) * mm, "end": v(27.08, 0.02) * mm});
            skLineSegment(sketch, "E5503", {"start": v(27.08, 0.02) * mm, "end": v(27.1, 0.07) * mm});
            skLineSegment(sketch, "E5504", {"start": v(27.1, 0.07) * mm, "end": v(27.13, 0.11) * mm});
            skLineSegment(sketch, "E5505", {"start": v(27.13, 0.11) * mm, "end": v(27.15, 0.16) * mm});
            skLineSegment(sketch, "E5506", {"start": v(27.15, 0.16) * mm, "end": v(27.17, 0.2) * mm});
            skLineSegment(sketch, "E5507", {"start": v(27.17, 0.2) * mm, "end": v(27.2, 0.25) * mm});
            skLineSegment(sketch, "E5508", {"start": v(27.2, 0.25) * mm, "end": v(27.22, 0.3) * mm});
            skLineSegment(sketch, "E5509", {"start": v(27.22, 0.3) * mm, "end": v(27.24, 0.34) * mm});
            skLineSegment(sketch, "E5510", {"start": v(27.24, 0.34) * mm, "end": v(27.25, 0.38) * mm});
            skLineSegment(sketch, "E5511", {"start": v(27.25, 0.38) * mm, "end": v(27.27, 0.43) * mm});
            skLineSegment(sketch, "E5512", {"start": v(27.27, 0.43) * mm, "end": v(27.28, 0.47) * mm});
            skLineSegment(sketch, "E5513", {"start": v(27.28, 0.47) * mm, "end": v(27.3, 0.52) * mm});
            skLineSegment(sketch, "E5514", {"start": v(27.3, 0.52) * mm, "end": v(27.3, 0.57) * mm});
            skLineSegment(sketch, "E5515", {"start": v(27.3, 0.57) * mm, "end": v(27.3, 0.62) * mm});
            skLineSegment(sketch, "E5516", {"start": v(27.3, 0.62) * mm, "end": v(27.32, 0.67) * mm});
            skLineSegment(sketch, "E5517", {"start": v(27.32, 0.67) * mm, "end": v(27.32, 0.72) * mm});
            skLineSegment(sketch, "E5518", {"start": v(27.32, 0.72) * mm, "end": v(27.32, 0.75) * mm});
            skLineSegment(sketch, "E5519", {"start": v(27.32, 0.75) * mm, "end": v(27.32, 0.78) * mm});
            skLineSegment(sketch, "E5520", {"start": v(27.32, 0.78) * mm, "end": v(27.32, 0.8) * mm});
            skLineSegment(sketch, "E5521", {"start": v(27.32, 0.8) * mm, "end": v(27.33, 0.84) * mm});
            skLineSegment(sketch, "E5522", {"start": v(27.33, 0.84) * mm, "end": v(27.33, 0.87) * mm});
            skLineSegment(sketch, "E5523", {"start": v(27.33, 0.87) * mm, "end": v(27.33, 0.9) * mm});
            skLineSegment(sketch, "E5524", {"start": v(27.33, 0.9) * mm, "end": v(27.33, 0.92) * mm});
            skLineSegment(sketch, "E5525", {"start": v(27.33, 0.92) * mm, "end": v(27.33, 0.95) * mm});
            skLineSegment(sketch, "E5526", {"start": v(27.33, 0.95) * mm, "end": v(27.34, 1.06) * mm});
            skLineSegment(sketch, "E5527", {"start": v(27.34, 1.06) * mm, "end": v(27.35, 1.17) * mm});
            skLineSegment(sketch, "E5528", {"start": v(27.35, 1.17) * mm, "end": v(27.35, 1.28) * mm});
            skLineSegment(sketch, "E5529", {"start": v(27.35, 1.28) * mm, "end": v(27.36, 1.4) * mm});
            skLineSegment(sketch, "E5530", {"start": v(27.36, 1.4) * mm, "end": v(27.36, 1.5) * mm});
            skLineSegment(sketch, "E5531", {"start": v(27.36, 1.5) * mm, "end": v(27.36, 1.62) * mm});
            skLineSegment(sketch, "E5532", {"start": v(27.36, 1.62) * mm, "end": v(27.36, 1.74) * mm});
            skLineSegment(sketch, "E5533", {"start": v(27.36, 1.74) * mm, "end": v(27.35, 1.85) * mm});
            skLineSegment(sketch, "E5534", {"start": v(27.35, 1.85) * mm, "end": v(27.35, 1.91) * mm});
            skLineSegment(sketch, "E5535", {"start": v(27.35, 1.91) * mm, "end": v(27.34, 1.98) * mm});
            skLineSegment(sketch, "E5536", {"start": v(27.34, 1.98) * mm, "end": v(27.33, 2.04) * mm});
            skLineSegment(sketch, "E5537", {"start": v(27.33, 2.04) * mm, "end": v(27.31, 2.1) * mm});
            skLineSegment(sketch, "E5538", {"start": v(27.31, 2.1) * mm, "end": v(27.3, 2.17) * mm});
            skLineSegment(sketch, "E5539", {"start": v(27.3, 2.17) * mm, "end": v(27.28, 2.23) * mm});
            skLineSegment(sketch, "E5540", {"start": v(27.28, 2.23) * mm, "end": v(27.26, 2.3) * mm});
            skLineSegment(sketch, "E5541", {"start": v(27.26, 2.3) * mm, "end": v(27.25, 2.36) * mm});
            skLineSegment(sketch, "E5542", {"start": v(27.25, 2.36) * mm, "end": v(27.23, 2.4) * mm});
            skLineSegment(sketch, "E5543", {"start": v(27.23, 2.4) * mm, "end": v(27.22, 2.44) * mm});
            skLineSegment(sketch, "E5544", {"start": v(27.22, 2.44) * mm, "end": v(27.21, 2.48) * mm});
            skLineSegment(sketch, "E5545", {"start": v(27.21, 2.48) * mm, "end": v(27.2, 2.52) * mm});
            skLineSegment(sketch, "E5546", {"start": v(27.2, 2.52) * mm, "end": v(27.2, 2.56) * mm});
            skLineSegment(sketch, "E5547", {"start": v(27.2, 2.56) * mm, "end": v(27.18, 2.6) * mm});
            skLineSegment(sketch, "E5548", {"start": v(27.18, 2.6) * mm, "end": v(27.17, 2.64) * mm});
            skLineSegment(sketch, "E5549", {"start": v(27.17, 2.64) * mm, "end": v(27.16, 2.68) * mm});
            skLineSegment(sketch, "E5550", {"start": v(27.16, 2.68) * mm, "end": v(27.14, 2.8) * mm});
            skLineSegment(sketch, "E5551", {"start": v(27.14, 2.8) * mm, "end": v(27.1, 2.92) * mm});
            skLineSegment(sketch, "E5552", {"start": v(27.1, 2.92) * mm, "end": v(27.07, 3.03) * mm});
            skLineSegment(sketch, "E5553", {"start": v(27.07, 3.03) * mm, "end": v(27.04, 3.13) * mm});
            skLineSegment(sketch, "E5554", {"start": v(27.04, 3.13) * mm, "end": v(27, 3.24) * mm});
            skLineSegment(sketch, "E5555", {"start": v(27, 3.24) * mm, "end": v(26.95, 3.33) * mm});
            skLineSegment(sketch, "E5556", {"start": v(26.95, 3.33) * mm, "end": v(26.9, 3.42) * mm});
            skLineSegment(sketch, "E5557", {"start": v(26.9, 3.42) * mm, "end": v(26.84, 3.51) * mm});
            skLineSegment(sketch, "E5558", {"start": v(26.84, 3.51) * mm, "end": v(26.8, 3.58) * mm});
            skLineSegment(sketch, "E5559", {"start": v(26.8, 3.58) * mm, "end": v(26.75, 3.64) * mm});
            skLineSegment(sketch, "E5560", {"start": v(26.75, 3.64) * mm, "end": v(26.7, 3.7) * mm});
            skLineSegment(sketch, "E5561", {"start": v(26.7, 3.7) * mm, "end": v(26.67, 3.77) * mm});
            skLineSegment(sketch, "E5562", {"start": v(26.67, 3.77) * mm, "end": v(26.64, 3.83) * mm});
            skLineSegment(sketch, "E5563", {"start": v(26.64, 3.83) * mm, "end": v(26.6, 3.88) * mm});
            skLineSegment(sketch, "E5564", {"start": v(26.6, 3.88) * mm, "end": v(26.57, 3.94) * mm});
            skLineSegment(sketch, "E5565", {"start": v(26.57, 3.94) * mm, "end": v(26.55, 4) * mm});
            skLineSegment(sketch, "E5566", {"start": v(26.55, 4) * mm, "end": v(26.54, 4) * mm});
            skLineSegment(sketch, "E5567", {"start": v(26.54, 4) * mm, "end": v(26.54, 4.02) * mm});
            skLineSegment(sketch, "E5568", {"start": v(26.54, 4.02) * mm, "end": v(26.53, 4.03) * mm});
            skLineSegment(sketch, "E5569", {"start": v(26.53, 4.03) * mm, "end": v(26.53, 4.04) * mm});
            skLineSegment(sketch, "E5570", {"start": v(26.53, 4.04) * mm, "end": v(26.53, 4.05) * mm});
            skLineSegment(sketch, "E5571", {"start": v(26.53, 4.05) * mm, "end": v(26.53, 4.06) * mm});
            skLineSegment(sketch, "E5572", {"start": v(26.53, 4.06) * mm, "end": v(26.53, 4.07) * mm});
            skLineSegment(sketch, "E5573", {"start": v(26.53, 4.07) * mm, "end": v(26.53, 4.09) * mm});
            skLineSegment(sketch, "E5574", {"start": v(26.53, 4.09) * mm, "end": v(26.53, 4.1) * mm});
            skLineSegment(sketch, "E5575", {"start": v(26.53, 4.1) * mm, "end": v(26.54, 4.1) * mm});
            skLineSegment(sketch, "E5576", {"start": v(26.54, 4.1) * mm, "end": v(26.55, 4.12) * mm});
            skLineSegment(sketch, "E5577", {"start": v(26.55, 4.12) * mm, "end": v(26.56, 4.12) * mm});
            skLineSegment(sketch, "E5578", {"start": v(26.56, 4.12) * mm, "end": v(26.57, 4.13) * mm});
            skLineSegment(sketch, "E5579", {"start": v(26.57, 4.13) * mm, "end": v(26.58, 4.14) * mm});
            skLineSegment(sketch, "E5580", {"start": v(26.58, 4.14) * mm, "end": v(26.59, 4.15) * mm});
            skLineSegment(sketch, "E5581", {"start": v(26.59, 4.15) * mm, "end": v(26.6, 4.15) * mm});
            skLineSegment(sketch, "E5582", {"start": v(26.6, 4.15) * mm, "end": v(26.67, 4.19) * mm});
            skLineSegment(sketch, "E5583", {"start": v(26.67, 4.19) * mm, "end": v(26.74, 4.22) * mm});
            skLineSegment(sketch, "E5584", {"start": v(26.74, 4.22) * mm, "end": v(26.82, 4.26) * mm});
            skLineSegment(sketch, "E5585", {"start": v(26.82, 4.26) * mm, "end": v(26.9, 4.3) * mm});
            skLineSegment(sketch, "E5586", {"start": v(26.9, 4.3) * mm, "end": v(26.97, 4.34) * mm});
            skLineSegment(sketch, "E5587", {"start": v(26.97, 4.34) * mm, "end": v(27.05, 4.39) * mm});
            skLineSegment(sketch, "E5588", {"start": v(27.05, 4.39) * mm, "end": v(27.12, 4.43) * mm});
            skLineSegment(sketch, "E5589", {"start": v(27.12, 4.43) * mm, "end": v(27.2, 4.48) * mm});
            skLineSegment(sketch, "E5590", {"start": v(27.2, 4.48) * mm, "end": v(27.26, 4.5) * mm});
            skLineSegment(sketch, "E5591", {"start": v(27.26, 4.5) * mm, "end": v(27.31, 4.52) * mm});
            skLineSegment(sketch, "E5592", {"start": v(27.31, 4.52) * mm, "end": v(27.37, 4.53) * mm});
            skLineSegment(sketch, "E5593", {"start": v(27.37, 4.53) * mm, "end": v(27.42, 4.53) * mm});
            skLineSegment(sketch, "E5594", {"start": v(27.42, 4.53) * mm, "end": v(27.47, 4.53) * mm});
            skLineSegment(sketch, "E5595", {"start": v(27.47, 4.53) * mm, "end": v(27.52, 4.5) * mm});
            skLineSegment(sketch, "E5596", {"start": v(27.52, 4.5) * mm, "end": v(27.57, 4.48) * mm});
            skLineSegment(sketch, "E5597", {"start": v(27.57, 4.48) * mm, "end": v(27.6, 4.45) * mm});
            skLineSegment(sketch, "E5598", {"start": v(27.6, 4.45) * mm, "end": v(27.67, 4.4) * mm});
            skLineSegment(sketch, "E5599", {"start": v(27.67, 4.4) * mm, "end": v(27.73, 4.33) * mm});
            skLineSegment(sketch, "E5600", {"start": v(27.73, 4.33) * mm, "end": v(27.79, 4.28) * mm});
            skLineSegment(sketch, "E5601", {"start": v(27.79, 4.28) * mm, "end": v(27.84, 4.22) * mm});
            skLineSegment(sketch, "E5602", {"start": v(27.84, 4.22) * mm, "end": v(27.89, 4.17) * mm});
            skLineSegment(sketch, "E5603", {"start": v(27.89, 4.17) * mm, "end": v(27.94, 4.12) * mm});
            skLineSegment(sketch, "E5604", {"start": v(27.94, 4.12) * mm, "end": v(27.98, 4.07) * mm});
            skLineSegment(sketch, "E5605", {"start": v(27.98, 4.07) * mm, "end": v(28.02, 4.02) * mm});
            skLineSegment(sketch, "E5606", {"start": v(28.02, 4.02) * mm, "end": v(28.05, 3.98) * mm});
            skLineSegment(sketch, "E5607", {"start": v(28.05, 3.98) * mm, "end": v(28.09, 3.94) * mm});
            skLineSegment(sketch, "E5608", {"start": v(28.09, 3.94) * mm, "end": v(28.12, 3.9) * mm});
            skLineSegment(sketch, "E5609", {"start": v(28.12, 3.9) * mm, "end": v(28.15, 3.86) * mm});
            skLineSegment(sketch, "E5610", {"start": v(28.15, 3.86) * mm, "end": v(28.18, 3.82) * mm});
            skLineSegment(sketch, "E5611", {"start": v(28.18, 3.82) * mm, "end": v(28.21, 3.78) * mm});
            skLineSegment(sketch, "E5612", {"start": v(28.21, 3.78) * mm, "end": v(28.24, 3.74) * mm});
            skLineSegment(sketch, "E5613", {"start": v(28.24, 3.74) * mm, "end": v(28.27, 3.7) * mm});
            skLineSegment(sketch, "E5614", {"start": v(28.27, 3.7) * mm, "end": v(28.31, 3.65) * mm});
            skLineSegment(sketch, "E5615", {"start": v(28.31, 3.65) * mm, "end": v(28.35, 3.6) * mm});
            skLineSegment(sketch, "E5616", {"start": v(28.35, 3.6) * mm, "end": v(28.39, 3.55) * mm});
            skLineSegment(sketch, "E5617", {"start": v(28.39, 3.55) * mm, "end": v(28.43, 3.5) * mm});
            skLineSegment(sketch, "E5618", {"start": v(28.43, 3.5) * mm, "end": v(28.46, 3.45) * mm});
            skLineSegment(sketch, "E5619", {"start": v(28.46, 3.45) * mm, "end": v(28.5, 3.4) * mm});
            skLineSegment(sketch, "E5620", {"start": v(28.5, 3.4) * mm, "end": v(28.54, 3.36) * mm});
            skLineSegment(sketch, "E5621", {"start": v(28.54, 3.36) * mm, "end": v(28.58, 3.31) * mm});
            skLineSegment(sketch, "E5622", {"start": v(28.58, 3.31) * mm, "end": v(28.6, 3.3) * mm});
            skLineSegment(sketch, "E5623", {"start": v(28.6, 3.3) * mm, "end": v(28.61, 3.28) * mm});
            skLineSegment(sketch, "E5624", {"start": v(28.61, 3.28) * mm, "end": v(28.63, 3.26) * mm});
            skLineSegment(sketch, "E5625", {"start": v(28.63, 3.26) * mm, "end": v(28.64, 3.24) * mm});
            skLineSegment(sketch, "E5626", {"start": v(28.64, 3.24) * mm, "end": v(28.65, 3.23) * mm});
            skLineSegment(sketch, "E5627", {"start": v(28.65, 3.23) * mm, "end": v(28.67, 3.2) * mm});
            skLineSegment(sketch, "E5628", {"start": v(28.67, 3.2) * mm, "end": v(28.68, 3.2) * mm});
            skLineSegment(sketch, "E5629", {"start": v(28.68, 3.2) * mm, "end": v(28.7, 3.17) * mm});
            skLineSegment(sketch, "E5630", {"start": v(28.7, 3.17) * mm, "end": v(28.75, 3.1) * mm});
            skLineSegment(sketch, "E5631", {"start": v(28.75, 3.1) * mm, "end": v(28.8, 3.04) * mm});
            skLineSegment(sketch, "E5632", {"start": v(28.8, 3.04) * mm, "end": v(28.87, 2.97) * mm});
            skLineSegment(sketch, "E5633", {"start": v(28.87, 2.97) * mm, "end": v(28.93, 2.91) * mm});
            skLineSegment(sketch, "E5634", {"start": v(28.93, 2.91) * mm, "end": v(29, 2.85) * mm});
            skLineSegment(sketch, "E5635", {"start": v(29, 2.85) * mm, "end": v(29.07, 2.8) * mm});
            skLineSegment(sketch, "E5636", {"start": v(29.07, 2.8) * mm, "end": v(29.15, 2.75) * mm});
            skLineSegment(sketch, "E5637", {"start": v(29.15, 2.75) * mm, "end": v(29.24, 2.72) * mm});
            skLineSegment(sketch, "E5638", {"start": v(29.24, 2.72) * mm, "end": v(29.3, 2.7) * mm});
            skLineSegment(sketch, "E5639", {"start": v(29.3, 2.7) * mm, "end": v(29.36, 2.68) * mm});
            skLineSegment(sketch, "E5640", {"start": v(29.36, 2.68) * mm, "end": v(29.42, 2.66) * mm});
            skLineSegment(sketch, "E5641", {"start": v(29.42, 2.66) * mm, "end": v(29.48, 2.64) * mm});
            skLineSegment(sketch, "E5642", {"start": v(29.48, 2.64) * mm, "end": v(29.54, 2.62) * mm});
            skLineSegment(sketch, "E5643", {"start": v(29.54, 2.62) * mm, "end": v(29.6, 2.6) * mm});
            skLineSegment(sketch, "E5644", {"start": v(29.6, 2.6) * mm, "end": v(29.66, 2.58) * mm});
            skLineSegment(sketch, "E5645", {"start": v(29.66, 2.58) * mm, "end": v(29.72, 2.56) * mm});
            skLineSegment(sketch, "E5646", {"start": v(29.72, 2.56) * mm, "end": v(29.74, 2.55) * mm});
            skLineSegment(sketch, "E5647", {"start": v(29.74, 2.55) * mm, "end": v(29.76, 2.55) * mm});
            skLineSegment(sketch, "E5648", {"start": v(29.76, 2.55) * mm, "end": v(29.78, 2.54) * mm});
            skLineSegment(sketch, "E5649", {"start": v(29.78, 2.54) * mm, "end": v(29.8, 2.53) * mm});
            skLineSegment(sketch, "E5650", {"start": v(29.8, 2.53) * mm, "end": v(29.83, 2.52) * mm});
            skLineSegment(sketch, "E5651", {"start": v(29.83, 2.52) * mm, "end": v(29.85, 2.52) * mm});
            skLineSegment(sketch, "E5652", {"start": v(29.85, 2.52) * mm, "end": v(29.87, 2.5) * mm});
            skLineSegment(sketch, "E5653", {"start": v(29.87, 2.5) * mm, "end": v(29.9, 2.5) * mm});
            skLineSegment(sketch, "E5654", {"start": v(29.9, 2.5) * mm, "end": v(29.95, 2.48) * mm});
            skLineSegment(sketch, "E5655", {"start": v(29.95, 2.48) * mm, "end": v(30.01, 2.46) * mm});
            skLineSegment(sketch, "E5656", {"start": v(30.01, 2.46) * mm, "end": v(30.07, 2.44) * mm});
            skLineSegment(sketch, "E5657", {"start": v(30.07, 2.44) * mm, "end": v(30.13, 2.42) * mm});
            skLineSegment(sketch, "E5658", {"start": v(30.13, 2.42) * mm, "end": v(30.19, 2.4) * mm});
            skLineSegment(sketch, "E5659", {"start": v(30.19, 2.4) * mm, "end": v(30.25, 2.4) * mm});
            skLineSegment(sketch, "E5660", {"start": v(30.25, 2.4) * mm, "end": v(30.31, 2.38) * mm});
            skLineSegment(sketch, "E5661", {"start": v(30.31, 2.38) * mm, "end": v(30.37, 2.37) * mm});
            skLineSegment(sketch, "E5662", {"start": v(30.37, 2.37) * mm, "end": v(30.45, 2.36) * mm});
            skLineSegment(sketch, "E5663", {"start": v(30.45, 2.36) * mm, "end": v(30.54, 2.35) * mm});
            skLineSegment(sketch, "E5664", {"start": v(30.54, 2.35) * mm, "end": v(30.62, 2.34) * mm});
            skLineSegment(sketch, "E5665", {"start": v(30.62, 2.34) * mm, "end": v(30.7, 2.33) * mm});
            skLineSegment(sketch, "E5666", {"start": v(30.7, 2.33) * mm, "end": v(30.78, 2.32) * mm});
            skLineSegment(sketch, "E5667", {"start": v(30.78, 2.32) * mm, "end": v(30.87, 2.32) * mm});
            skLineSegment(sketch, "E5668", {"start": v(30.87, 2.32) * mm, "end": v(30.95, 2.31) * mm});
            skLineSegment(sketch, "E5669", {"start": v(30.95, 2.31) * mm, "end": v(31.03, 2.3) * mm});
            skLineSegment(sketch, "E5670", {"start": v(31.03, 2.3) * mm, "end": v(31.07, 2.3) * mm});
            skLineSegment(sketch, "E5671", {"start": v(31.07, 2.3) * mm, "end": v(31.1, 2.3) * mm});
            skLineSegment(sketch, "E5672", {"start": v(31.1, 2.3) * mm, "end": v(31.15, 2.3) * mm});
            skLineSegment(sketch, "E5673", {"start": v(31.15, 2.3) * mm, "end": v(31.19, 2.3) * mm});
            skLineSegment(sketch, "E5674", {"start": v(31.19, 2.3) * mm, "end": v(31.23, 2.3) * mm});
            skLineSegment(sketch, "E5675", {"start": v(31.23, 2.3) * mm, "end": v(31.26, 2.29) * mm});
            skLineSegment(sketch, "E5676", {"start": v(31.26, 2.29) * mm, "end": v(31.3, 2.29) * mm});
            skLineSegment(sketch, "E5677", {"start": v(31.3, 2.29) * mm, "end": v(31.34, 2.28) * mm});
            skLineSegment(sketch, "E5678", {"start": v(31.34, 2.28) * mm, "end": v(31.37, 2.28) * mm});
            skLineSegment(sketch, "E5679", {"start": v(31.37, 2.28) * mm, "end": v(31.4, 2.28) * mm});
            skLineSegment(sketch, "E5680", {"start": v(31.4, 2.28) * mm, "end": v(31.43, 2.28) * mm});
            skLineSegment(sketch, "E5681", {"start": v(31.43, 2.28) * mm, "end": v(31.45, 2.3) * mm});
            skLineSegment(sketch, "E5682", {"start": v(31.45, 2.3) * mm, "end": v(31.47, 2.3) * mm});
            skLineSegment(sketch, "E5683", {"start": v(31.47, 2.3) * mm, "end": v(31.49, 2.31) * mm});
            skLineSegment(sketch, "E5684", {"start": v(31.49, 2.31) * mm, "end": v(31.5, 2.33) * mm});
            skLineSegment(sketch, "E5685", {"start": v(31.5, 2.33) * mm, "end": v(31.52, 2.34) * mm});
            skLineSegment(sketch, "E5686", {"start": v(31.52, 2.34) * mm, "end": v(31.53, 2.36) * mm});
            skLineSegment(sketch, "E5687", {"start": v(31.53, 2.36) * mm, "end": v(31.53, 2.37) * mm});
            skLineSegment(sketch, "E5688", {"start": v(31.53, 2.37) * mm, "end": v(31.54, 2.4) * mm});
            skLineSegment(sketch, "E5689", {"start": v(31.54, 2.4) * mm, "end": v(31.54, 2.41) * mm});
            skLineSegment(sketch, "E5690", {"start": v(31.54, 2.41) * mm, "end": v(31.54, 2.43) * mm});
            skLineSegment(sketch, "E5691", {"start": v(31.54, 2.43) * mm, "end": v(31.54, 2.46) * mm});
            skLineSegment(sketch, "E5692", {"start": v(31.54, 2.46) * mm, "end": v(31.54, 2.48) * mm});
            skLineSegment(sketch, "E5693", {"start": v(31.54, 2.48) * mm, "end": v(31.53, 2.5) * mm});
            skLineSegment(sketch, "E5694", {"start": v(31.53, 2.5) * mm, "end": v(31.52, 2.53) * mm});
            skLineSegment(sketch, "E5695", {"start": v(31.52, 2.53) * mm, "end": v(31.5, 2.56) * mm});
            skLineSegment(sketch, "E5696", {"start": v(31.5, 2.56) * mm, "end": v(31.5, 2.6) * mm});
            skLineSegment(sketch, "E5697", {"start": v(31.5, 2.6) * mm, "end": v(31.5, 2.62) * mm});
            skLineSegment(sketch, "E5698", {"start": v(31.5, 2.62) * mm, "end": v(31.48, 2.66) * mm});
            skLineSegment(sketch, "E5699", {"start": v(31.48, 2.66) * mm, "end": v(31.47, 2.69) * mm});
            skLineSegment(sketch, "E5700", {"start": v(31.47, 2.69) * mm, "end": v(31.46, 2.72) * mm});
            skLineSegment(sketch, "E5701", {"start": v(31.46, 2.72) * mm, "end": v(31.45, 2.75) * mm});
            skLineSegment(sketch, "E5702", {"start": v(31.45, 2.75) * mm, "end": v(31.43, 2.81) * mm});
            skLineSegment(sketch, "E5703", {"start": v(31.43, 2.81) * mm, "end": v(31.41, 2.88) * mm});
            skLineSegment(sketch, "E5704", {"start": v(31.41, 2.88) * mm, "end": v(31.4, 2.95) * mm});
            skLineSegment(sketch, "E5705", {"start": v(31.4, 2.95) * mm, "end": v(31.37, 3.02) * mm});
            skLineSegment(sketch, "E5706", {"start": v(31.37, 3.02) * mm, "end": v(31.35, 3.1) * mm});
            skLineSegment(sketch, "E5707", {"start": v(31.35, 3.1) * mm, "end": v(31.32, 3.16) * mm});
            skLineSegment(sketch, "E5708", {"start": v(31.32, 3.16) * mm, "end": v(31.3, 3.23) * mm});
            skLineSegment(sketch, "E5709", {"start": v(31.3, 3.23) * mm, "end": v(31.26, 3.3) * mm});
            skLineSegment(sketch, "E5710", {"start": v(31.26, 3.3) * mm, "end": v(31.2, 3.42) * mm});
            skLineSegment(sketch, "E5711", {"start": v(31.2, 3.42) * mm, "end": v(31.14, 3.54) * mm});
            skLineSegment(sketch, "E5712", {"start": v(31.14, 3.54) * mm, "end": v(31.08, 3.67) * mm});
            skLineSegment(sketch, "E5713", {"start": v(31.08, 3.67) * mm, "end": v(31.02, 3.8) * mm});
            skLineSegment(sketch, "E5714", {"start": v(31.02, 3.8) * mm, "end": v(30.95, 3.91) * mm});
            skLineSegment(sketch, "E5715", {"start": v(30.95, 3.91) * mm, "end": v(30.89, 4.04) * mm});
            skLineSegment(sketch, "E5716", {"start": v(30.89, 4.04) * mm, "end": v(30.82, 4.16) * mm});
            skLineSegment(sketch, "E5717", {"start": v(30.82, 4.16) * mm, "end": v(30.76, 4.28) * mm});
            skLineSegment(sketch, "E5718", {"start": v(30.76, 4.28) * mm, "end": v(30.74, 4.32) * mm});
            skLineSegment(sketch, "E5719", {"start": v(30.74, 4.32) * mm, "end": v(30.72, 4.36) * mm});
            skLineSegment(sketch, "E5720", {"start": v(30.72, 4.36) * mm, "end": v(30.7, 4.4) * mm});
            skLineSegment(sketch, "E5721", {"start": v(30.7, 4.4) * mm, "end": v(30.67, 4.44) * mm});
            skLineSegment(sketch, "E5722", {"start": v(30.67, 4.44) * mm, "end": v(30.65, 4.49) * mm});
            skLineSegment(sketch, "E5723", {"start": v(30.65, 4.49) * mm, "end": v(30.63, 4.53) * mm});
            skLineSegment(sketch, "E5724", {"start": v(30.63, 4.53) * mm, "end": v(30.6, 4.57) * mm});
            skLineSegment(sketch, "E5725", {"start": v(30.6, 4.57) * mm, "end": v(30.58, 4.6) * mm});
            skLineSegment(sketch, "E5726", {"start": v(30.58, 4.6) * mm, "end": v(30.51, 4.73) * mm});
            skLineSegment(sketch, "E5727", {"start": v(30.51, 4.73) * mm, "end": v(30.43, 4.85) * mm});
            skLineSegment(sketch, "E5728", {"start": v(30.43, 4.85) * mm, "end": v(30.34, 4.97) * mm});
            skLineSegment(sketch, "E5729", {"start": v(30.34, 4.97) * mm, "end": v(30.24, 5.08) * mm});
            skLineSegment(sketch, "E5730", {"start": v(30.24, 5.08) * mm, "end": v(30.13, 5.19) * mm});
            skLineSegment(sketch, "E5731", {"start": v(30.13, 5.19) * mm, "end": v(30, 5.3) * mm});
            skLineSegment(sketch, "E5732", {"start": v(30, 5.3) * mm, "end": v(29.87, 5.4) * mm});
            skLineSegment(sketch, "E5733", {"start": v(29.87, 5.4) * mm, "end": v(29.72, 5.5) * mm});
            skLineSegment(sketch, "E5734", {"start": v(29.72, 5.5) * mm, "end": v(29.64, 5.55) * mm});
            skLineSegment(sketch, "E5735", {"start": v(29.64, 5.55) * mm, "end": v(29.56, 5.6) * mm});
            skLineSegment(sketch, "E5736", {"start": v(29.56, 5.6) * mm, "end": v(29.47, 5.64) * mm});
            skLineSegment(sketch, "E5737", {"start": v(29.47, 5.64) * mm, "end": v(29.38, 5.67) * mm});
            skLineSegment(sketch, "E5738", {"start": v(29.38, 5.67) * mm, "end": v(29.3, 5.7) * mm});
            skLineSegment(sketch, "E5739", {"start": v(29.3, 5.7) * mm, "end": v(29.2, 5.74) * mm});
            skLineSegment(sketch, "E5740", {"start": v(29.2, 5.74) * mm, "end": v(29.11, 5.77) * mm});
            skLineSegment(sketch, "E5741", {"start": v(29.11, 5.77) * mm, "end": v(29.02, 5.8) * mm});
            skLineSegment(sketch, "E5742", {"start": v(29.02, 5.8) * mm, "end": v(29, 5.8) * mm});
            skLineSegment(sketch, "E5743", {"start": v(29, 5.8) * mm, "end": v(28.97, 5.82) * mm});
            skLineSegment(sketch, "E5744", {"start": v(28.97, 5.82) * mm, "end": v(28.94, 5.82) * mm});
            skLineSegment(sketch, "E5745", {"start": v(28.94, 5.82) * mm, "end": v(28.91, 5.83) * mm});
            skLineSegment(sketch, "E5746", {"start": v(28.91, 5.83) * mm, "end": v(28.89, 5.84) * mm});
            skLineSegment(sketch, "E5747", {"start": v(28.89, 5.84) * mm, "end": v(28.86, 5.85) * mm});
            skLineSegment(sketch, "E5748", {"start": v(28.86, 5.85) * mm, "end": v(28.84, 5.86) * mm});
            skLineSegment(sketch, "E5749", {"start": v(28.84, 5.86) * mm, "end": v(28.8, 5.87) * mm});
            skLineSegment(sketch, "E5750", {"start": v(28.8, 5.87) * mm, "end": v(28.78, 5.88) * mm});
            skLineSegment(sketch, "E5751", {"start": v(28.78, 5.88) * mm, "end": v(28.75, 5.9) * mm});
            skLineSegment(sketch, "E5752", {"start": v(28.75, 5.9) * mm, "end": v(28.73, 5.9) * mm});
            skLineSegment(sketch, "E5753", {"start": v(28.73, 5.9) * mm, "end": v(28.71, 5.92) * mm});
            skLineSegment(sketch, "E5754", {"start": v(28.71, 5.92) * mm, "end": v(28.7, 5.93) * mm});
            skLineSegment(sketch, "E5755", {"start": v(28.7, 5.93) * mm, "end": v(28.69, 5.94) * mm});
            skLineSegment(sketch, "E5756", {"start": v(28.69, 5.94) * mm, "end": v(28.68, 5.95) * mm});
            skLineSegment(sketch, "E5757", {"start": v(28.68, 5.95) * mm, "end": v(28.68, 5.95) * mm});
            skLineSegment(sketch, "E5758", {"start": v(28.68, 5.95) * mm, "end": v(28.67, 5.96) * mm});
            skLineSegment(sketch, "E5759", {"start": v(28.67, 5.96) * mm, "end": v(28.67, 5.97) * mm});
            skLineSegment(sketch, "E5760", {"start": v(28.67, 5.97) * mm, "end": v(28.67, 5.98) * mm});
            skLineSegment(sketch, "E5761", {"start": v(28.67, 5.98) * mm, "end": v(28.67, 6) * mm});
            skLineSegment(sketch, "E5762", {"start": v(28.67, 6) * mm, "end": v(28.67, 6) * mm});
            skLineSegment(sketch, "E5763", {"start": v(28.67, 6) * mm, "end": v(28.68, 6.02) * mm});
            skLineSegment(sketch, "E5764", {"start": v(28.68, 6.02) * mm, "end": v(28.68, 6.04) * mm});
            skLineSegment(sketch, "E5765", {"start": v(28.68, 6.04) * mm, "end": v(28.69, 6.05) * mm});
            skLineSegment(sketch, "E5766", {"start": v(28.69, 6.05) * mm, "end": v(28.73, 6.15) * mm});
            skLineSegment(sketch, "E5767", {"start": v(28.73, 6.15) * mm, "end": v(28.78, 6.26) * mm});
            skLineSegment(sketch, "E5768", {"start": v(28.78, 6.26) * mm, "end": v(28.82, 6.36) * mm});
            skLineSegment(sketch, "E5769", {"start": v(28.82, 6.36) * mm, "end": v(28.87, 6.45) * mm});
            skLineSegment(sketch, "E5770", {"start": v(28.87, 6.45) * mm, "end": v(28.92, 6.55) * mm});
            skLineSegment(sketch, "E5771", {"start": v(28.92, 6.55) * mm, "end": v(28.96, 6.64) * mm});
            skLineSegment(sketch, "E5772", {"start": v(28.96, 6.64) * mm, "end": v(29, 6.72) * mm});
            skLineSegment(sketch, "E5773", {"start": v(29, 6.72) * mm, "end": v(29.05, 6.8) * mm});
            skLineSegment(sketch, "E5774", {"start": v(29.05, 6.8) * mm, "end": v(29.06, 6.82) * mm});
            skLineSegment(sketch, "E5775", {"start": v(29.06, 6.82) * mm, "end": v(29.1, 6.84) * mm});
            skLineSegment(sketch, "E5776", {"start": v(29.1, 6.84) * mm, "end": v(29.12, 6.86) * mm});
            skLineSegment(sketch, "E5777", {"start": v(29.12, 6.86) * mm, "end": v(29.16, 6.87) * mm});
            skLineSegment(sketch, "E5778", {"start": v(29.16, 6.87) * mm, "end": v(29.2, 6.88) * mm});
            skLineSegment(sketch, "E5779", {"start": v(29.2, 6.88) * mm, "end": v(29.23, 6.88) * mm});
            skLineSegment(sketch, "E5780", {"start": v(29.23, 6.88) * mm, "end": v(29.27, 6.88) * mm});
            skLineSegment(sketch, "E5781", {"start": v(29.27, 6.88) * mm, "end": v(29.3, 6.87) * mm});
            skLineSegment(sketch, "E5782", {"start": v(29.3, 6.87) * mm, "end": v(29.33, 6.86) * mm});
            skLineSegment(sketch, "E5783", {"start": v(29.33, 6.86) * mm, "end": v(29.36, 6.85) * mm});
            skLineSegment(sketch, "E5784", {"start": v(29.36, 6.85) * mm, "end": v(29.39, 6.84) * mm});
            skLineSegment(sketch, "E5785", {"start": v(29.39, 6.84) * mm, "end": v(29.42, 6.83) * mm});
            skLineSegment(sketch, "E5786", {"start": v(29.42, 6.83) * mm, "end": v(29.45, 6.82) * mm});
            skLineSegment(sketch, "E5787", {"start": v(29.45, 6.82) * mm, "end": v(29.47, 6.81) * mm});
            skLineSegment(sketch, "E5788", {"start": v(29.47, 6.81) * mm, "end": v(29.5, 6.8) * mm});
            skLineSegment(sketch, "E5789", {"start": v(29.5, 6.8) * mm, "end": v(29.52, 6.8) * mm});
            skLineSegment(sketch, "E5790", {"start": v(29.52, 6.8) * mm, "end": v(29.55, 6.8) * mm});
            skLineSegment(sketch, "E5791", {"start": v(29.55, 6.8) * mm, "end": v(29.58, 6.8) * mm});
            skLineSegment(sketch, "E5792", {"start": v(29.58, 6.8) * mm, "end": v(29.61, 6.79) * mm});
            skLineSegment(sketch, "E5793", {"start": v(29.61, 6.79) * mm, "end": v(29.64, 6.79) * mm});
            skLineSegment(sketch, "E5794", {"start": v(29.64, 6.79) * mm, "end": v(29.67, 6.78) * mm});
            skLineSegment(sketch, "E5795", {"start": v(29.67, 6.78) * mm, "end": v(29.7, 6.78) * mm});
            skLineSegment(sketch, "E5796", {"start": v(29.7, 6.78) * mm, "end": v(29.74, 6.77) * mm});
            skLineSegment(sketch, "E5797", {"start": v(29.74, 6.77) * mm, "end": v(29.77, 6.77) * mm});
            skLineSegment(sketch, "E5798", {"start": v(29.77, 6.77) * mm, "end": v(29.8, 6.76) * mm});
            skLineSegment(sketch, "E5799", {"start": v(29.8, 6.76) * mm, "end": v(29.84, 6.76) * mm});
            skLineSegment(sketch, "E5800", {"start": v(29.84, 6.76) * mm, "end": v(29.88, 6.75) * mm});
            skLineSegment(sketch, "E5801", {"start": v(29.88, 6.75) * mm, "end": v(29.91, 6.75) * mm});
            skLineSegment(sketch, "E5802", {"start": v(29.91, 6.75) * mm, "end": v(29.95, 6.74) * mm});
            skLineSegment(sketch, "E5803", {"start": v(29.95, 6.74) * mm, "end": v(29.99, 6.74) * mm});
            skLineSegment(sketch, "E5804", {"start": v(29.99, 6.74) * mm, "end": v(30.02, 6.73) * mm});
            skLineSegment(sketch, "E5805", {"start": v(30.02, 6.73) * mm, "end": v(30.06, 6.72) * mm});
            skLineSegment(sketch, "E5806", {"start": v(30.06, 6.72) * mm, "end": v(30.2, 6.7) * mm});
            skLineSegment(sketch, "E5807", {"start": v(30.2, 6.7) * mm, "end": v(30.34, 6.67) * mm});
            skLineSegment(sketch, "E5808", {"start": v(30.34, 6.67) * mm, "end": v(30.48, 6.64) * mm});
            skLineSegment(sketch, "E5809", {"start": v(30.48, 6.64) * mm, "end": v(30.62, 6.62) * mm});
            skLineSegment(sketch, "E5810", {"start": v(30.62, 6.62) * mm, "end": v(30.75, 6.59) * mm});
            skLineSegment(sketch, "E5811", {"start": v(30.75, 6.59) * mm, "end": v(30.89, 6.56) * mm});
            skLineSegment(sketch, "E5812", {"start": v(30.89, 6.56) * mm, "end": v(31.02, 6.53) * mm});
            skLineSegment(sketch, "E5813", {"start": v(31.02, 6.53) * mm, "end": v(31.15, 6.5) * mm});
            skLineSegment(sketch, "E5814", {"start": v(31.15, 6.5) * mm, "end": v(31.17, 6.5) * mm});
            skLineSegment(sketch, "E5815", {"start": v(31.17, 6.5) * mm, "end": v(31.2, 6.5) * mm});
            skLineSegment(sketch, "E5816", {"start": v(31.2, 6.5) * mm, "end": v(31.23, 6.48) * mm});
            skLineSegment(sketch, "E5817", {"start": v(31.23, 6.48) * mm, "end": v(31.25, 6.47) * mm});
            skLineSegment(sketch, "E5818", {"start": v(31.25, 6.47) * mm, "end": v(31.28, 6.46) * mm});
            skLineSegment(sketch, "E5819", {"start": v(31.28, 6.46) * mm, "end": v(31.3, 6.45) * mm});
            skLineSegment(sketch, "E5820", {"start": v(31.3, 6.45) * mm, "end": v(31.33, 6.43) * mm});
            skLineSegment(sketch, "E5821", {"start": v(31.33, 6.43) * mm, "end": v(31.36, 6.42) * mm});
            skLineSegment(sketch, "E5822", {"start": v(31.36, 6.42) * mm, "end": v(31.37, 6.41) * mm});
            skLineSegment(sketch, "E5823", {"start": v(31.37, 6.41) * mm, "end": v(31.38, 6.4) * mm});
            skLineSegment(sketch, "E5824", {"start": v(31.38, 6.4) * mm, "end": v(31.4, 6.4) * mm});
            skLineSegment(sketch, "E5825", {"start": v(31.4, 6.4) * mm, "end": v(31.4, 6.39) * mm});
            skLineSegment(sketch, "E5826", {"start": v(31.4, 6.39) * mm, "end": v(31.4, 6.38) * mm});
            skLineSegment(sketch, "E5827", {"start": v(31.4, 6.38) * mm, "end": v(31.4, 6.38) * mm});
            skLineSegment(sketch, "E5828", {"start": v(31.4, 6.38) * mm, "end": v(31.41, 6.37) * mm});
            skLineSegment(sketch, "E5829", {"start": v(31.41, 6.37) * mm, "end": v(31.41, 6.37) * mm});
            skLineSegment(sketch, "E5830", {"start": v(31.41, 6.37) * mm, "end": v(31.41, 6.36) * mm});
            skLineSegment(sketch, "E5831", {"start": v(31.41, 6.36) * mm, "end": v(31.41, 6.36) * mm});
            skLineSegment(sketch, "E5832", {"start": v(31.41, 6.36) * mm, "end": v(31.4, 6.35) * mm});
            skLineSegment(sketch, "E5833", {"start": v(31.4, 6.35) * mm, "end": v(31.4, 6.34) * mm});
            skLineSegment(sketch, "E5834", {"start": v(31.4, 6.34) * mm, "end": v(31.4, 6.34) * mm});
            skLineSegment(sketch, "E5835", {"start": v(31.4, 6.34) * mm, "end": v(31.4, 6.33) * mm});
            skLineSegment(sketch, "E5836", {"start": v(31.4, 6.33) * mm, "end": v(31.4, 6.33) * mm});
            skLineSegment(sketch, "E5837", {"start": v(31.4, 6.33) * mm, "end": v(31.39, 6.32) * mm});
            skLineSegment(sketch, "E5838", {"start": v(31.39, 6.32) * mm, "end": v(31.38, 6.32) * mm});
            skLineSegment(sketch, "E5839", {"start": v(31.38, 6.32) * mm, "end": v(31.38, 6.32) * mm});
            skLineSegment(sketch, "E5840", {"start": v(31.38, 6.32) * mm, "end": v(31.37, 6.32) * mm});
            skLineSegment(sketch, "E5841", {"start": v(31.37, 6.32) * mm, "end": v(31.36, 6.32) * mm});
            skLineSegment(sketch, "E5842", {"start": v(31.36, 6.32) * mm, "end": v(31.35, 6.32) * mm});
            skLineSegment(sketch, "E5843", {"start": v(31.35, 6.32) * mm, "end": v(31.34, 6.32) * mm});
            skLineSegment(sketch, "E5844", {"start": v(31.34, 6.32) * mm, "end": v(31.33, 6.33) * mm});
            skLineSegment(sketch, "E5845", {"start": v(31.33, 6.33) * mm, "end": v(31.32, 6.33) * mm});
            skLineSegment(sketch, "E5846", {"start": v(31.32, 6.33) * mm, "end": v(31.3, 6.33) * mm});
            skLineSegment(sketch, "E5847", {"start": v(31.3, 6.33) * mm, "end": v(31.3, 6.34) * mm});
            skLineSegment(sketch, "E5848", {"start": v(31.3, 6.34) * mm, "end": v(31.28, 6.34) * mm});
            skLineSegment(sketch, "E5849", {"start": v(31.28, 6.34) * mm, "end": v(31.22, 6.36) * mm});
            skLineSegment(sketch, "E5850", {"start": v(31.22, 6.36) * mm, "end": v(31.16, 6.38) * mm});
            skLineSegment(sketch, "E5851", {"start": v(31.16, 6.38) * mm, "end": v(31.1, 6.39) * mm});
            skLineSegment(sketch, "E5852", {"start": v(31.1, 6.39) * mm, "end": v(31.05, 6.4) * mm});
            skLineSegment(sketch, "E5853", {"start": v(31.05, 6.4) * mm, "end": v(31, 6.4) * mm});
            skLineSegment(sketch, "E5854", {"start": v(31, 6.4) * mm, "end": v(30.95, 6.4) * mm});
            skLineSegment(sketch, "E5855", {"start": v(30.95, 6.4) * mm, "end": v(30.9, 6.4) * mm});
            skLineSegment(sketch, "E5856", {"start": v(30.9, 6.4) * mm, "end": v(30.85, 6.4) * mm});
            skLineSegment(sketch, "E5857", {"start": v(30.85, 6.4) * mm, "end": v(30.8, 6.4) * mm});
            skLineSegment(sketch, "E5858", {"start": v(30.8, 6.4) * mm, "end": v(30.75, 6.4) * mm});
            skLineSegment(sketch, "E5859", {"start": v(30.75, 6.4) * mm, "end": v(30.7, 6.39) * mm});
            skLineSegment(sketch, "E5860", {"start": v(30.7, 6.39) * mm, "end": v(30.64, 6.38) * mm});
            skLineSegment(sketch, "E5861", {"start": v(30.64, 6.38) * mm, "end": v(30.59, 6.36) * mm});
            skLineSegment(sketch, "E5862", {"start": v(30.59, 6.36) * mm, "end": v(30.54, 6.35) * mm});
            skLineSegment(sketch, "E5863", {"start": v(30.54, 6.35) * mm, "end": v(30.49, 6.34) * mm});
            skLineSegment(sketch, "E5864", {"start": v(30.49, 6.34) * mm, "end": v(30.43, 6.33) * mm});
            skLineSegment(sketch, "E5865", {"start": v(30.43, 6.33) * mm, "end": v(30.41, 6.32) * mm});
            skLineSegment(sketch, "E5866", {"start": v(30.41, 6.32) * mm, "end": v(30.4, 6.32) * mm});
            skLineSegment(sketch, "E5867", {"start": v(30.4, 6.32) * mm, "end": v(30.37, 6.31) * mm});
            skLineSegment(sketch, "E5868", {"start": v(30.37, 6.31) * mm, "end": v(30.35, 6.3) * mm});
            skLineSegment(sketch, "E5869", {"start": v(30.35, 6.3) * mm, "end": v(30.33, 6.3) * mm});
            skLineSegment(sketch, "E5870", {"start": v(30.33, 6.3) * mm, "end": v(30.3, 6.3) * mm});
            skLineSegment(sketch, "E5871", {"start": v(30.3, 6.3) * mm, "end": v(30.29, 6.3) * mm});
            skLineSegment(sketch, "E5872", {"start": v(30.29, 6.3) * mm, "end": v(30.27, 6.3) * mm});
            skLineSegment(sketch, "E5873", {"start": v(30.27, 6.3) * mm, "end": v(30.23, 6.28) * mm});
            skLineSegment(sketch, "E5874", {"start": v(30.23, 6.28) * mm, "end": v(30.19, 6.27) * mm});
            skLineSegment(sketch, "E5875", {"start": v(30.19, 6.27) * mm, "end": v(30.16, 6.25) * mm});
            skLineSegment(sketch, "E5876", {"start": v(30.16, 6.25) * mm, "end": v(30.13, 6.24) * mm});
            skLineSegment(sketch, "E5877", {"start": v(30.13, 6.24) * mm, "end": v(30.1, 6.22) * mm});
            skLineSegment(sketch, "E5878", {"start": v(30.1, 6.22) * mm, "end": v(30.08, 6.2) * mm});
            skLineSegment(sketch, "E5879", {"start": v(30.08, 6.2) * mm, "end": v(30.06, 6.17) * mm});
            skLineSegment(sketch, "E5880", {"start": v(30.06, 6.17) * mm, "end": v(30.05, 6.14) * mm});
            skLineSegment(sketch, "E5881", {"start": v(30.05, 6.14) * mm, "end": v(30.04, 6.11) * mm});
            skLineSegment(sketch, "E5882", {"start": v(30.04, 6.11) * mm, "end": v(30.03, 6.08) * mm});
            skLineSegment(sketch, "E5883", {"start": v(30.03, 6.08) * mm, "end": v(30.03, 6.05) * mm});
            skLineSegment(sketch, "E5884", {"start": v(30.03, 6.05) * mm, "end": v(30.03, 6.02) * mm});
            skLineSegment(sketch, "E5885", {"start": v(30.03, 6.02) * mm, "end": v(30.04, 5.98) * mm});
            skLineSegment(sketch, "E5886", {"start": v(30.04, 5.98) * mm, "end": v(30.05, 5.94) * mm});
            skLineSegment(sketch, "E5887", {"start": v(30.05, 5.94) * mm, "end": v(30.06, 5.9) * mm});
            skLineSegment(sketch, "E5888", {"start": v(30.06, 5.9) * mm, "end": v(30.08, 5.87) * mm});
            skLineSegment(sketch, "E5889", {"start": v(30.08, 5.87) * mm, "end": v(30.1, 5.84) * mm});
            skLineSegment(sketch, "E5890", {"start": v(30.1, 5.84) * mm, "end": v(30.11, 5.82) * mm});
            skLineSegment(sketch, "E5891", {"start": v(30.11, 5.82) * mm, "end": v(30.12, 5.8) * mm});
            skLineSegment(sketch, "E5892", {"start": v(30.12, 5.8) * mm, "end": v(30.14, 5.77) * mm});
            skLineSegment(sketch, "E5893", {"start": v(30.14, 5.77) * mm, "end": v(30.15, 5.75) * mm});
            skLineSegment(sketch, "E5894", {"start": v(30.15, 5.75) * mm, "end": v(30.16, 5.72) * mm});
            skLineSegment(sketch, "E5895", {"start": v(30.16, 5.72) * mm, "end": v(30.17, 5.7) * mm});
            skLineSegment(sketch, "E5896", {"start": v(30.17, 5.7) * mm, "end": v(30.19, 5.67) * mm});
            skLineSegment(sketch, "E5897", {"start": v(30.19, 5.67) * mm, "end": v(30.2, 5.65) * mm});
            skLineSegment(sketch, "E5898", {"start": v(30.2, 5.65) * mm, "end": v(30.2, 5.63) * mm});
            skLineSegment(sketch, "E5899", {"start": v(30.2, 5.63) * mm, "end": v(30.22, 5.61) * mm});
            skLineSegment(sketch, "E5900", {"start": v(30.22, 5.61) * mm, "end": v(30.23, 5.6) * mm});
            skLineSegment(sketch, "E5901", {"start": v(30.23, 5.6) * mm, "end": v(30.24, 5.57) * mm});
            skLineSegment(sketch, "E5902", {"start": v(30.24, 5.57) * mm, "end": v(30.25, 5.55) * mm});
            skLineSegment(sketch, "E5903", {"start": v(30.25, 5.55) * mm, "end": v(30.26, 5.53) * mm});
            skLineSegment(sketch, "E5904", {"start": v(30.26, 5.53) * mm, "end": v(30.27, 5.51) * mm});
            skLineSegment(sketch, "E5905", {"start": v(30.27, 5.51) * mm, "end": v(30.28, 5.5) * mm});
            skLineSegment(sketch, "E5906", {"start": v(30.28, 5.5) * mm, "end": v(30.3, 5.47) * mm});
            skLineSegment(sketch, "E5907", {"start": v(30.3, 5.47) * mm, "end": v(30.3, 5.45) * mm});
            skLineSegment(sketch, "E5908", {"start": v(30.3, 5.45) * mm, "end": v(30.31, 5.42) * mm});
            skLineSegment(sketch, "E5909", {"start": v(30.31, 5.42) * mm, "end": v(30.33, 5.4) * mm});
            skLineSegment(sketch, "E5910", {"start": v(30.33, 5.4) * mm, "end": v(30.34, 5.38) * mm});
            skLineSegment(sketch, "E5911", {"start": v(30.34, 5.38) * mm, "end": v(30.35, 5.36) * mm});
            skLineSegment(sketch, "E5912", {"start": v(30.35, 5.36) * mm, "end": v(30.36, 5.34) * mm});
            skLineSegment(sketch, "E5913", {"start": v(30.36, 5.34) * mm, "end": v(30.4, 5.25) * mm});
            skLineSegment(sketch, "E5914", {"start": v(30.4, 5.25) * mm, "end": v(30.45, 5.16) * mm});
            skLineSegment(sketch, "E5915", {"start": v(30.45, 5.16) * mm, "end": v(30.5, 5.07) * mm});
            skLineSegment(sketch, "E5916", {"start": v(30.5, 5.07) * mm, "end": v(30.56, 4.98) * mm});
            skLineSegment(sketch, "E5917", {"start": v(30.56, 4.98) * mm, "end": v(30.61, 4.9) * mm});
            skLineSegment(sketch, "E5918", {"start": v(30.61, 4.9) * mm, "end": v(30.68, 4.81) * mm});
            skLineSegment(sketch, "E5919", {"start": v(30.68, 4.81) * mm, "end": v(30.74, 4.73) * mm});
            skLineSegment(sketch, "E5920", {"start": v(30.74, 4.73) * mm, "end": v(30.82, 4.65) * mm});
            skLineSegment(sketch, "E5921", {"start": v(30.82, 4.65) * mm, "end": v(30.84, 4.64) * mm});
            skLineSegment(sketch, "E5922", {"start": v(30.84, 4.64) * mm, "end": v(30.85, 4.62) * mm});
            skLineSegment(sketch, "E5923", {"start": v(30.85, 4.62) * mm, "end": v(30.87, 4.6) * mm});
            skLineSegment(sketch, "E5924", {"start": v(30.87, 4.6) * mm, "end": v(30.89, 4.6) * mm});
            skLineSegment(sketch, "E5925", {"start": v(30.89, 4.6) * mm, "end": v(30.9, 4.58) * mm});
            skLineSegment(sketch, "E5926", {"start": v(30.9, 4.58) * mm, "end": v(30.92, 4.56) * mm});
            skLineSegment(sketch, "E5927", {"start": v(30.92, 4.56) * mm, "end": v(30.94, 4.55) * mm});
            skLineSegment(sketch, "E5928", {"start": v(30.94, 4.55) * mm, "end": v(30.96, 4.53) * mm});
            skLineSegment(sketch, "E5929", {"start": v(30.96, 4.53) * mm, "end": v(30.98, 4.52) * mm});
            skLineSegment(sketch, "E5930", {"start": v(30.98, 4.52) * mm, "end": v(31, 4.5) * mm});
            skLineSegment(sketch, "E5931", {"start": v(31, 4.5) * mm, "end": v(31, 4.5) * mm});
            skLineSegment(sketch, "E5932", {"start": v(31, 4.5) * mm, "end": v(31.02, 4.48) * mm});
            skLineSegment(sketch, "E5933", {"start": v(31.02, 4.48) * mm, "end": v(31.04, 4.47) * mm});
            skLineSegment(sketch, "E5934", {"start": v(31.04, 4.47) * mm, "end": v(31.06, 4.45) * mm});
            skLineSegment(sketch, "E5935", {"start": v(31.06, 4.45) * mm, "end": v(31.07, 4.44) * mm});
            skLineSegment(sketch, "E5936", {"start": v(31.07, 4.44) * mm, "end": v(31.09, 4.42) * mm});
            skLineSegment(sketch, "E5937", {"start": v(31.09, 4.42) * mm, "end": v(31.2, 4.33) * mm});
            skLineSegment(sketch, "E5938", {"start": v(31.2, 4.33) * mm, "end": v(31.31, 4.24) * mm});
            skLineSegment(sketch, "E5939", {"start": v(31.31, 4.24) * mm, "end": v(31.43, 4.17) * mm});
            skLineSegment(sketch, "E5940", {"start": v(31.43, 4.17) * mm, "end": v(31.55, 4.12) * mm});
            skLineSegment(sketch, "E5941", {"start": v(31.55, 4.12) * mm, "end": v(31.68, 4.08) * mm});
            skLineSegment(sketch, "E5942", {"start": v(31.68, 4.08) * mm, "end": v(31.8, 4.05) * mm});
            skLineSegment(sketch, "E5943", {"start": v(31.8, 4.05) * mm, "end": v(31.94, 4.04) * mm});
            skLineSegment(sketch, "E5944", {"start": v(31.94, 4.04) * mm, "end": v(32.07, 4.04) * mm});
            skLineSegment(sketch, "E5945", {"start": v(32.07, 4.04) * mm, "end": v(32.18, 4.05) * mm});
            skLineSegment(sketch, "E5946", {"start": v(32.18, 4.05) * mm, "end": v(32.3, 4.05) * mm});
            skLineSegment(sketch, "E5947", {"start": v(32.3, 4.05) * mm, "end": v(32.41, 4.06) * mm});
            skLineSegment(sketch, "E5948", {"start": v(32.41, 4.06) * mm, "end": v(32.53, 4.07) * mm});
            skLineSegment(sketch, "E5949", {"start": v(32.53, 4.07) * mm, "end": v(32.65, 4.09) * mm});
            skLineSegment(sketch, "E5950", {"start": v(32.65, 4.09) * mm, "end": v(32.76, 4.1) * mm});
            skLineSegment(sketch, "E5951", {"start": v(32.76, 4.1) * mm, "end": v(32.88, 4.11) * mm});
            skLineSegment(sketch, "E5952", {"start": v(32.88, 4.11) * mm, "end": v(33, 4.13) * mm});
            skLineSegment(sketch, "E5953", {"start": v(33, 4.13) * mm, "end": v(33.03, 4.13) * mm});
            skLineSegment(sketch, "E5954", {"start": v(33.03, 4.13) * mm, "end": v(33.06, 4.14) * mm});
            skLineSegment(sketch, "E5955", {"start": v(33.06, 4.14) * mm, "end": v(33.08, 4.15) * mm});
            skLineSegment(sketch, "E5956", {"start": v(33.08, 4.15) * mm, "end": v(33.1, 4.16) * mm});
            skLineSegment(sketch, "E5957", {"start": v(33.1, 4.16) * mm, "end": v(33.13, 4.17) * mm});
            skLineSegment(sketch, "E5958", {"start": v(33.13, 4.17) * mm, "end": v(33.16, 4.19) * mm});
            skLineSegment(sketch, "E5959", {"start": v(33.16, 4.19) * mm, "end": v(33.18, 4.2) * mm});
            skLineSegment(sketch, "E5960", {"start": v(33.18, 4.2) * mm, "end": v(33.2, 4.21) * mm});
            skLineSegment(sketch, "E5961", {"start": v(33.2, 4.21) * mm, "end": v(33.21, 4.22) * mm});
            skLineSegment(sketch, "E5962", {"start": v(33.21, 4.22) * mm, "end": v(33.22, 4.22) * mm});
            skLineSegment(sketch, "E5963", {"start": v(33.22, 4.22) * mm, "end": v(33.22, 4.22) * mm});
            skLineSegment(sketch, "E5964", {"start": v(33.22, 4.22) * mm, "end": v(33.23, 4.22) * mm});
            skLineSegment(sketch, "E5965", {"start": v(33.23, 4.22) * mm, "end": v(33.23, 4.23) * mm});
            skLineSegment(sketch, "E5966", {"start": v(33.23, 4.23) * mm, "end": v(33.23, 4.23) * mm});
            skLineSegment(sketch, "E5967", {"start": v(33.23, 4.23) * mm, "end": v(33.24, 4.23) * mm});
            skLineSegment(sketch, "E5968", {"start": v(33.24, 4.23) * mm, "end": v(33.25, 4.24) * mm});
            skLineSegment(sketch, "E5969", {"start": v(33.25, 4.24) * mm, "end": v(33.26, 4.24) * mm});
            skLineSegment(sketch, "E5970", {"start": v(33.26, 4.24) * mm, "end": v(33.28, 4.25) * mm});
            skLineSegment(sketch, "E5971", {"start": v(33.28, 4.25) * mm, "end": v(33.29, 4.26) * mm});
            skLineSegment(sketch, "E5972", {"start": v(33.29, 4.26) * mm, "end": v(33.3, 4.27) * mm});
            skLineSegment(sketch, "E5973", {"start": v(33.3, 4.27) * mm, "end": v(33.32, 4.27) * mm});
            skLineSegment(sketch, "E5974", {"start": v(33.32, 4.27) * mm, "end": v(33.33, 4.28) * mm});
            skLineSegment(sketch, "E5975", {"start": v(33.33, 4.28) * mm, "end": v(33.34, 4.28) * mm});
            skLineSegment(sketch, "E5976", {"start": v(33.34, 4.28) * mm, "end": v(33.34, 4.3) * mm});
            skLineSegment(sketch, "E5977", {"start": v(33.34, 4.3) * mm, "end": v(33.35, 4.3) * mm});
            skLineSegment(sketch, "E5978", {"start": v(33.35, 4.3) * mm, "end": v(33.35, 4.32) * mm});
            skLineSegment(sketch, "E5979", {"start": v(33.35, 4.32) * mm, "end": v(33.35, 4.33) * mm});
            skLineSegment(sketch, "E5980", {"start": v(33.35, 4.33) * mm, "end": v(33.35, 4.34) * mm});
            skLineSegment(sketch, "E5981", {"start": v(33.35, 4.34) * mm, "end": v(33.34, 4.36) * mm});
            skLineSegment(sketch, "E5982", {"start": v(33.34, 4.36) * mm, "end": v(33.33, 4.37) * mm});
            skLineSegment(sketch, "E5983", {"start": v(33.33, 4.37) * mm, "end": v(33.32, 4.38) * mm});
            skLineSegment(sketch, "E5984", {"start": v(33.32, 4.38) * mm, "end": v(33.3, 4.4) * mm});
            skLineSegment(sketch, "E5985", {"start": v(33.3, 4.4) * mm, "end": v(33.3, 4.41) * mm});
            skLineSegment(sketch, "E5986", {"start": v(33.3, 4.41) * mm, "end": v(33.29, 4.43) * mm});
            skLineSegment(sketch, "E5987", {"start": v(33.29, 4.43) * mm, "end": v(33.28, 4.44) * mm});
            skLineSegment(sketch, "E5988", {"start": v(33.28, 4.44) * mm, "end": v(33.27, 4.46) * mm});
            skLineSegment(sketch, "E5989", {"start": v(33.27, 4.46) * mm, "end": v(33.26, 4.47) * mm});
            skLineSegment(sketch, "E5990", {"start": v(33.26, 4.47) * mm, "end": v(33.25, 4.48) * mm});
            skLineSegment(sketch, "E5991", {"start": v(33.25, 4.48) * mm, "end": v(33.25, 4.48) * mm});
            skLineSegment(sketch, "E5992", {"start": v(33.25, 4.48) * mm, "end": v(33.25, 4.49) * mm});
            skLineSegment(sketch, "E5993", {"start": v(33.25, 4.49) * mm, "end": v(33.24, 4.5) * mm});
            skLineSegment(sketch, "E5994", {"start": v(33.24, 4.5) * mm, "end": v(33.24, 4.5) * mm});
            skLineSegment(sketch, "E5995", {"start": v(33.24, 4.5) * mm, "end": v(33.23, 4.52) * mm});
            skLineSegment(sketch, "E5996", {"start": v(33.23, 4.52) * mm, "end": v(33.22, 4.53) * mm});
            skLineSegment(sketch, "E5997", {"start": v(33.22, 4.53) * mm, "end": v(33.2, 4.55) * mm});
            skLineSegment(sketch, "E5998", {"start": v(33.2, 4.55) * mm, "end": v(33.2, 4.56) * mm});
            skLineSegment(sketch, "E5999", {"start": v(33.2, 4.56) * mm, "end": v(33.2, 4.58) * mm});
            skLineSegment(sketch, "E6000", {"start": v(33.2, 4.58) * mm, "end": v(33.19, 4.6) * mm});
            skLineSegment(sketch, "E6001", {"start": v(33.19, 4.6) * mm, "end": v(33.18, 4.6) * mm});
            skLineSegment(sketch, "E6002", {"start": v(33.18, 4.6) * mm, "end": v(33.17, 4.62) * mm});
            skLineSegment(sketch, "E6003", {"start": v(33.17, 4.62) * mm, "end": v(33.16, 4.66) * mm});
            skLineSegment(sketch, "E6004", {"start": v(33.16, 4.66) * mm, "end": v(33.14, 4.7) * mm});
            skLineSegment(sketch, "E6005", {"start": v(33.14, 4.7) * mm, "end": v(33.13, 4.74) * mm});
            skLineSegment(sketch, "E6006", {"start": v(33.13, 4.74) * mm, "end": v(33.12, 4.77) * mm});
            skLineSegment(sketch, "E6007", {"start": v(33.12, 4.77) * mm, "end": v(33.1, 4.81) * mm});
            skLineSegment(sketch, "E6008", {"start": v(33.1, 4.81) * mm, "end": v(33.09, 4.85) * mm});
            skLineSegment(sketch, "E6009", {"start": v(33.09, 4.85) * mm, "end": v(33.08, 4.9) * mm});
            skLineSegment(sketch, "E6010", {"start": v(33.08, 4.9) * mm, "end": v(33.06, 4.93) * mm});
            skLineSegment(sketch, "E6011", {"start": v(33.06, 4.93) * mm, "end": v(33.05, 4.98) * mm});
            skLineSegment(sketch, "E6012", {"start": v(33.05, 4.98) * mm, "end": v(33.03, 5.03) * mm});
            skLineSegment(sketch, "E6013", {"start": v(33.03, 5.03) * mm, "end": v(33.01, 5.08) * mm});
            skLineSegment(sketch, "E6014", {"start": v(33.01, 5.08) * mm, "end": v(33, 5.13) * mm});
            skLineSegment(sketch, "E6015", {"start": v(33, 5.13) * mm, "end": v(32.98, 5.18) * mm});
            skLineSegment(sketch, "E6016", {"start": v(32.98, 5.18) * mm, "end": v(32.96, 5.23) * mm});
            skLineSegment(sketch, "E6017", {"start": v(32.96, 5.23) * mm, "end": v(32.94, 5.28) * mm});
            skLineSegment(sketch, "E6018", {"start": v(32.94, 5.28) * mm, "end": v(32.92, 5.33) * mm});
            skLineSegment(sketch, "E6019", {"start": v(32.92, 5.33) * mm, "end": v(32.85, 5.47) * mm});
            skLineSegment(sketch, "E6020", {"start": v(32.85, 5.47) * mm, "end": v(32.76, 5.6) * mm});
            skLineSegment(sketch, "E6021", {"start": v(32.76, 5.6) * mm, "end": v(32.66, 5.72) * mm});
            skLineSegment(sketch, "E6022", {"start": v(32.66, 5.72) * mm, "end": v(32.55, 5.82) * mm});
            skLineSegment(sketch, "E6023", {"start": v(32.55, 5.82) * mm, "end": v(32.43, 5.9) * mm});
            skLineSegment(sketch, "E6024", {"start": v(32.43, 5.9) * mm, "end": v(32.31, 5.98) * mm});
            skLineSegment(sketch, "E6025", {"start": v(32.31, 5.98) * mm, "end": v(32.19, 6.05) * mm});
            skLineSegment(sketch, "E6026", {"start": v(32.19, 6.05) * mm, "end": v(32.06, 6.1) * mm});
            skLineSegment(sketch, "E6027", {"start": v(32.06, 6.1) * mm, "end": v(32.05, 6.11) * mm});
            skLineSegment(sketch, "E6028", {"start": v(32.05, 6.11) * mm, "end": v(32.05, 6.12) * mm});
            skLineSegment(sketch, "E6029", {"start": v(32.05, 6.12) * mm, "end": v(32.04, 6.12) * mm});
            skLineSegment(sketch, "E6030", {"start": v(32.04, 6.12) * mm, "end": v(32.03, 6.12) * mm});
            skLineSegment(sketch, "E6031", {"start": v(32.03, 6.12) * mm, "end": v(32.02, 6.13) * mm});
            skLineSegment(sketch, "E6032", {"start": v(32.02, 6.13) * mm, "end": v(32.02, 6.13) * mm});
            skLineSegment(sketch, "E6033", {"start": v(32.02, 6.13) * mm, "end": v(32, 6.13) * mm});
            skLineSegment(sketch, "E6034", {"start": v(32, 6.13) * mm, "end": v(32, 6.13) * mm});
            skLineSegment(sketch, "E6035", {"start": v(32, 6.13) * mm, "end": v(31.96, 6.15) * mm});
            skLineSegment(sketch, "E6036", {"start": v(31.96, 6.15) * mm, "end": v(31.93, 6.16) * mm});
            skLineSegment(sketch, "E6037", {"start": v(31.93, 6.16) * mm, "end": v(31.91, 6.17) * mm});
            skLineSegment(sketch, "E6038", {"start": v(31.91, 6.17) * mm, "end": v(31.9, 6.18) * mm});
            skLineSegment(sketch, "E6039", {"start": v(31.9, 6.18) * mm, "end": v(31.9, 6.2) * mm});
            skLineSegment(sketch, "E6040", {"start": v(31.9, 6.2) * mm, "end": v(31.9, 6.2) * mm});
            skLineSegment(sketch, "E6041", {"start": v(31.9, 6.2) * mm, "end": v(31.9, 6.22) * mm});
            skLineSegment(sketch, "E6042", {"start": v(31.9, 6.22) * mm, "end": v(31.9, 6.23) * mm});
            skLineSegment(sketch, "E6043", {"start": v(31.9, 6.23) * mm, "end": v(31.9, 6.25) * mm});
            skLineSegment(sketch, "E6044", {"start": v(31.9, 6.25) * mm, "end": v(31.9, 6.26) * mm});
            skLineSegment(sketch, "E6045", {"start": v(31.9, 6.26) * mm, "end": v(31.9, 6.27) * mm});
            skLineSegment(sketch, "E6046", {"start": v(31.9, 6.27) * mm, "end": v(31.9, 6.28) * mm});
            skLineSegment(sketch, "E6047", {"start": v(31.9, 6.28) * mm, "end": v(31.9, 6.28) * mm});
            skLineSegment(sketch, "E6048", {"start": v(31.9, 6.28) * mm, "end": v(31.91, 6.28) * mm});
            skLineSegment(sketch, "E6049", {"start": v(31.91, 6.28) * mm, "end": v(31.91, 6.28) * mm});
            skLineSegment(sketch, "E6050", {"start": v(31.91, 6.28) * mm, "end": v(31.94, 6.29) * mm});
            skLineSegment(sketch, "E6051", {"start": v(31.94, 6.29) * mm, "end": v(31.97, 6.29) * mm});
            skLineSegment(sketch, "E6052", {"start": v(31.97, 6.29) * mm, "end": v(32, 6.3) * mm});
            skLineSegment(sketch, "E6053", {"start": v(32, 6.3) * mm, "end": v(32.03, 6.3) * mm});
            skLineSegment(sketch, "E6054", {"start": v(32.03, 6.3) * mm, "end": v(32.05, 6.3) * mm});
            skLineSegment(sketch, "E6055", {"start": v(32.05, 6.3) * mm, "end": v(32.07, 6.3) * mm});
            skLineSegment(sketch, "E6056", {"start": v(32.07, 6.3) * mm, "end": v(32.08, 6.3) * mm});
            skLineSegment(sketch, "E6057", {"start": v(32.08, 6.3) * mm, "end": v(32.1, 6.3) * mm});
            skLineSegment(sketch, "E6058", {"start": v(32.1, 6.3) * mm, "end": v(32.1, 6.3) * mm});
            skLineSegment(sketch, "E6059", {"start": v(32.1, 6.3) * mm, "end": v(32.11, 6.3) * mm});
            skLineSegment(sketch, "E6060", {"start": v(32.11, 6.3) * mm, "end": v(32.12, 6.3) * mm});
            skLineSegment(sketch, "E6061", {"start": v(32.12, 6.3) * mm, "end": v(32.12, 6.3) * mm});
            skLineSegment(sketch, "E6062", {"start": v(32.12, 6.3) * mm, "end": v(32.13, 6.3) * mm});
            skLineSegment(sketch, "E6063", {"start": v(32.13, 6.3) * mm, "end": v(32.13, 6.3) * mm});
            skLineSegment(sketch, "E6064", {"start": v(32.13, 6.3) * mm, "end": v(32.14, 6.3) * mm});
            skLineSegment(sketch, "E6065", {"start": v(32.14, 6.3) * mm, "end": v(32.14, 6.3) * mm});
            skLineSegment(sketch, "E6066", {"start": v(32.14, 6.3) * mm, "end": v(32.15, 6.29) * mm});
            skLineSegment(sketch, "E6067", {"start": v(32.15, 6.29) * mm, "end": v(32.15, 6.29) * mm});
            skLineSegment(sketch, "E6068", {"start": v(32.15, 6.29) * mm, "end": v(32.16, 6.29) * mm});
            skLineSegment(sketch, "E6069", {"start": v(32.16, 6.29) * mm, "end": v(32.17, 6.28) * mm});
            skLineSegment(sketch, "E6070", {"start": v(32.17, 6.28) * mm, "end": v(32.18, 6.28) * mm});
            skLineSegment(sketch, "E6071", {"start": v(32.18, 6.28) * mm, "end": v(32.19, 6.28) * mm});
            skLineSegment(sketch, "E6072", {"start": v(32.19, 6.28) * mm, "end": v(32.2, 6.28) * mm});
            skLineSegment(sketch, "E6073", {"start": v(32.2, 6.28) * mm, "end": v(32.2, 6.28) * mm});
            skLineSegment(sketch, "E6074", {"start": v(32.2, 6.28) * mm, "end": v(32.21, 6.28) * mm});
            skLineSegment(sketch, "E6075", {"start": v(32.21, 6.28) * mm, "end": v(32.22, 6.28) * mm});
            skLineSegment(sketch, "E6076", {"start": v(32.22, 6.28) * mm, "end": v(32.22, 6.28) * mm});
            skLineSegment(sketch, "E6077", {"start": v(32.22, 6.28) * mm, "end": v(32.23, 6.27) * mm});
            skLineSegment(sketch, "E6078", {"start": v(32.23, 6.27) * mm, "end": v(32.24, 6.27) * mm});
            skLineSegment(sketch, "E6079", {"start": v(32.24, 6.27) * mm, "end": v(32.25, 6.27) * mm});
            skLineSegment(sketch, "E6080", {"start": v(32.25, 6.27) * mm, "end": v(32.26, 6.27) * mm});
            skLineSegment(sketch, "E6081", {"start": v(32.26, 6.27) * mm, "end": v(32.28, 6.27) * mm});
            skLineSegment(sketch, "E6082", {"start": v(32.28, 6.27) * mm, "end": v(32.29, 6.27) * mm});
            skLineSegment(sketch, "E6083", {"start": v(32.29, 6.27) * mm, "end": v(32.3, 6.27) * mm});
            skLineSegment(sketch, "E6084", {"start": v(32.3, 6.27) * mm, "end": v(32.32, 6.27) * mm});
            skLineSegment(sketch, "E6085", {"start": v(32.32, 6.27) * mm, "end": v(32.33, 6.27) * mm});
            skLineSegment(sketch, "E6086", {"start": v(32.33, 6.27) * mm, "end": v(32.35, 6.27) * mm});
            skLineSegment(sketch, "E6087", {"start": v(32.35, 6.27) * mm, "end": v(32.38, 6.27) * mm});
            skLineSegment(sketch, "E6088", {"start": v(32.38, 6.27) * mm, "end": v(32.4, 6.27) * mm});
            skLineSegment(sketch, "E6089", {"start": v(32.4, 6.27) * mm, "end": v(32.41, 6.27) * mm});
            skLineSegment(sketch, "E6090", {"start": v(32.41, 6.27) * mm, "end": v(32.43, 6.28) * mm});
            skLineSegment(sketch, "E6091", {"start": v(32.43, 6.28) * mm, "end": v(32.43, 6.28) * mm});
            skLineSegment(sketch, "E6092", {"start": v(32.43, 6.28) * mm, "end": v(32.45, 6.28) * mm});
            skLineSegment(sketch, "E6093", {"start": v(32.45, 6.28) * mm, "end": v(32.47, 6.29) * mm});
            skLineSegment(sketch, "E6094", {"start": v(32.47, 6.29) * mm, "end": v(32.51, 6.3) * mm});
            skLineSegment(sketch, "E6095", {"start": v(32.51, 6.3) * mm, "end": v(32.57, 6.3) * mm});
            skLineSegment(sketch, "E6096", {"start": v(32.57, 6.3) * mm, "end": v(32.63, 6.32) * mm});
            skLineSegment(sketch, "E6097", {"start": v(32.63, 6.32) * mm, "end": v(32.7, 6.34) * mm});
            skLineSegment(sketch, "E6098", {"start": v(32.7, 6.34) * mm, "end": v(32.77, 6.35) * mm});
            skLineSegment(sketch, "E6099", {"start": v(32.77, 6.35) * mm, "end": v(32.86, 6.37) * mm});
            skLineSegment(sketch, "E6100", {"start": v(32.86, 6.37) * mm, "end": v(32.86, 6.37) * mm});
            skLineSegment(sketch, "E6101", {"start": v(32.86, 6.37) * mm, "end": v(32.87, 6.37) * mm});
            skLineSegment(sketch, "E6102", {"start": v(32.87, 6.37) * mm, "end": v(32.88, 6.38) * mm});
            skLineSegment(sketch, "E6103", {"start": v(32.88, 6.38) * mm, "end": v(32.9, 6.39) * mm});
            skLineSegment(sketch, "E6104", {"start": v(32.9, 6.39) * mm, "end": v(32.94, 6.4) * mm});
            skLineSegment(sketch, "E6105", {"start": v(32.94, 6.4) * mm, "end": v(32.99, 6.42) * mm});
            skLineSegment(sketch, "E6106", {"start": v(32.99, 6.42) * mm, "end": v(33.05, 6.44) * mm});
            skLineSegment(sketch, "E6107", {"start": v(33.05, 6.44) * mm, "end": v(33.12, 6.46) * mm});
            skLineSegment(sketch, "E6108", {"start": v(33.12, 6.46) * mm, "end": v(33.19, 6.49) * mm});
            skLineSegment(sketch, "E6109", {"start": v(33.19, 6.49) * mm, "end": v(33.26, 6.52) * mm});
            skLineSegment(sketch, "E6110", {"start": v(33.26, 6.52) * mm, "end": v(33.32, 6.55) * mm});
            skLineSegment(sketch, "E6111", {"start": v(33.32, 6.55) * mm, "end": v(33.39, 6.58) * mm});
            skLineSegment(sketch, "E6112", {"start": v(33.39, 6.58) * mm, "end": v(33.46, 6.61) * mm});
            skLineSegment(sketch, "E6113", {"start": v(33.46, 6.61) * mm, "end": v(33.52, 6.65) * mm});
            skLineSegment(sketch, "E6114", {"start": v(33.52, 6.65) * mm, "end": v(33.6, 6.68) * mm});
            skLineSegment(sketch, "E6115", {"start": v(33.6, 6.68) * mm, "end": v(33.64, 6.7) * mm});
            skLineSegment(sketch, "E6116", {"start": v(33.64, 6.7) * mm, "end": v(33.68, 6.74) * mm});
            skLineSegment(sketch, "E6117", {"start": v(33.68, 6.74) * mm, "end": v(33.71, 6.77) * mm});
            skLineSegment(sketch, "E6118", {"start": v(33.71, 6.77) * mm, "end": v(33.73, 6.8) * mm});
            skLineSegment(sketch, "E6119", {"start": v(33.73, 6.8) * mm, "end": v(33.75, 6.82) * mm});
            skLineSegment(sketch, "E6120", {"start": v(33.75, 6.82) * mm, "end": v(33.76, 6.85) * mm});
            skLineSegment(sketch, "E6121", {"start": v(33.76, 6.85) * mm, "end": v(33.77, 6.88) * mm});
            skLineSegment(sketch, "E6122", {"start": v(33.77, 6.88) * mm, "end": v(33.78, 6.9) * mm});
            skLineSegment(sketch, "E6123", {"start": v(33.78, 6.9) * mm, "end": v(33.78, 6.93) * mm});
            skLineSegment(sketch, "E6124", {"start": v(33.78, 6.93) * mm, "end": v(33.78, 6.95) * mm});
            skLineSegment(sketch, "E6125", {"start": v(17.98, 6.76) * mm, "end": v(17.92, 6.7) * mm});
            skLineSegment(sketch, "E6126", {"start": v(17.92, 6.7) * mm, "end": v(17.86, 6.66) * mm});
            skLineSegment(sketch, "E6127", {"start": v(17.86, 6.66) * mm, "end": v(17.8, 6.61) * mm});
            skLineSegment(sketch, "E6128", {"start": v(17.8, 6.61) * mm, "end": v(17.76, 6.57) * mm});
            skLineSegment(sketch, "E6129", {"start": v(17.76, 6.57) * mm, "end": v(17.72, 6.54) * mm});
            skLineSegment(sketch, "E6130", {"start": v(17.72, 6.54) * mm, "end": v(17.68, 6.51) * mm});
            skLineSegment(sketch, "E6131", {"start": v(17.68, 6.51) * mm, "end": v(17.66, 6.5) * mm});
            skLineSegment(sketch, "E6132", {"start": v(17.66, 6.5) * mm, "end": v(17.64, 6.48) * mm});
            skLineSegment(sketch, "E6133", {"start": v(17.64, 6.48) * mm, "end": v(17.62, 6.47) * mm});
            skLineSegment(sketch, "E6134", {"start": v(17.62, 6.47) * mm, "end": v(17.59, 6.45) * mm});
            skLineSegment(sketch, "E6135", {"start": v(17.59, 6.45) * mm, "end": v(17.54, 6.42) * mm});
            skLineSegment(sketch, "E6136", {"start": v(17.54, 6.42) * mm, "end": v(17.48, 6.39) * mm});
            skLineSegment(sketch, "E6137", {"start": v(17.48, 6.39) * mm, "end": v(17.4, 6.34) * mm});
            skLineSegment(sketch, "E6138", {"start": v(17.4, 6.34) * mm, "end": v(17.32, 6.3) * mm});
            skLineSegment(sketch, "E6139", {"start": v(17.32, 6.3) * mm, "end": v(17.24, 6.24) * mm});
            skLineSegment(sketch, "E6140", {"start": v(17.24, 6.24) * mm, "end": v(17.14, 6.19) * mm});
            skLineSegment(sketch, "E6141", {"start": v(17.14, 6.19) * mm, "end": v(17.14, 6.19) * mm});
            skLineSegment(sketch, "E6142", {"start": v(17.14, 6.19) * mm, "end": v(17.13, 6.18) * mm});
            skLineSegment(sketch, "E6143", {"start": v(17.13, 6.18) * mm, "end": v(17.11, 6.18) * mm});
            skLineSegment(sketch, "E6144", {"start": v(17.11, 6.18) * mm, "end": v(17.09, 6.16) * mm});
            skLineSegment(sketch, "E6145", {"start": v(17.09, 6.16) * mm, "end": v(17.04, 6.15) * mm});
            skLineSegment(sketch, "E6146", {"start": v(17.04, 6.15) * mm, "end": v(16.99, 6.12) * mm});
            skLineSegment(sketch, "E6147", {"start": v(16.99, 6.12) * mm, "end": v(16.9, 6.09) * mm});
            skLineSegment(sketch, "E6148", {"start": v(16.9, 6.09) * mm, "end": v(16.85, 6.07) * mm});
            skLineSegment(sketch, "E6149", {"start": v(16.85, 6.07) * mm, "end": v(16.81, 6.05) * mm});
            skLineSegment(sketch, "E6150", {"start": v(16.81, 6.05) * mm, "end": v(16.78, 6.04) * mm});
            skLineSegment(sketch, "E6151", {"start": v(16.78, 6.04) * mm, "end": v(16.76, 6.03) * mm});
            skLineSegment(sketch, "E6152", {"start": v(16.76, 6.03) * mm, "end": v(16.75, 6.02) * mm});
            skLineSegment(sketch, "E6153", {"start": v(16.75, 6.02) * mm, "end": v(16.75, 6.02) * mm});
            skLineSegment(sketch, "E6154", {"start": v(16.75, 6.02) * mm, "end": v(16.74, 6.02) * mm});
            skLineSegment(sketch, "E6155", {"start": v(16.74, 6.02) * mm, "end": v(16.74, 6.02) * mm});
            skLineSegment(sketch, "E6156", {"start": v(16.74, 6.02) * mm, "end": v(16.67, 6) * mm});
            skLineSegment(sketch, "E6157", {"start": v(16.67, 6) * mm, "end": v(16.6, 6) * mm});
            skLineSegment(sketch, "E6158", {"start": v(16.6, 6) * mm, "end": v(16.53, 5.98) * mm});
            skLineSegment(sketch, "E6159", {"start": v(16.53, 5.98) * mm, "end": v(16.47, 5.97) * mm});
            skLineSegment(sketch, "E6160", {"start": v(16.47, 5.97) * mm, "end": v(16.42, 5.97) * mm});
            skLineSegment(sketch, "E6161", {"start": v(16.42, 5.97) * mm, "end": v(16.38, 5.96) * mm});
            skLineSegment(sketch, "E6162", {"start": v(16.38, 5.96) * mm, "end": v(16.35, 5.95) * mm});
            skLineSegment(sketch, "E6163", {"start": v(16.35, 5.95) * mm, "end": v(16.34, 5.95) * mm});
            skLineSegment(sketch, "E6164", {"start": v(16.34, 5.95) * mm, "end": v(16.32, 5.95) * mm});
            skLineSegment(sketch, "E6165", {"start": v(16.32, 5.95) * mm, "end": v(16.29, 5.95) * mm});
            skLineSegment(sketch, "E6166", {"start": v(16.29, 5.95) * mm, "end": v(16.23, 5.94) * mm});
            skLineSegment(sketch, "E6167", {"start": v(16.23, 5.94) * mm, "end": v(16.16, 5.94) * mm});
            skLineSegment(sketch, "E6168", {"start": v(16.16, 5.94) * mm, "end": v(16.08, 5.93) * mm});
            skLineSegment(sketch, "E6169", {"start": v(16.08, 5.93) * mm, "end": v(15.99, 5.93) * mm});
            skLineSegment(sketch, "E6170", {"start": v(15.99, 5.93) * mm, "end": v(15.89, 5.92) * mm});
            skLineSegment(sketch, "E6171", {"start": v(15.89, 5.92) * mm, "end": v(15.78, 5.91) * mm});
            skLineSegment(sketch, "E6172", {"start": v(15.78, 5.91) * mm, "end": v(15.78, 5.91) * mm});
            skLineSegment(sketch, "E6173", {"start": v(15.78, 5.91) * mm, "end": v(15.77, 5.91) * mm});
            skLineSegment(sketch, "E6174", {"start": v(15.77, 5.91) * mm, "end": v(15.76, 5.92) * mm});
            skLineSegment(sketch, "E6175", {"start": v(15.76, 5.92) * mm, "end": v(15.75, 5.92) * mm});
            skLineSegment(sketch, "E6176", {"start": v(15.75, 5.92) * mm, "end": v(15.72, 5.93) * mm});
            skLineSegment(sketch, "E6177", {"start": v(15.72, 5.93) * mm, "end": v(15.68, 5.94) * mm});
            skLineSegment(sketch, "E6178", {"start": v(15.68, 5.94) * mm, "end": v(15.62, 5.96) * mm});
            skLineSegment(sketch, "E6179", {"start": v(15.62, 5.96) * mm, "end": v(15.54, 5.98) * mm});
            skLineSegment(sketch, "E6180", {"start": v(15.54, 5.98) * mm, "end": v(15.53, 5.98) * mm});
            skLineSegment(sketch, "E6181", {"start": v(15.53, 5.98) * mm, "end": v(15.52, 5.99) * mm});
            skLineSegment(sketch, "E6182", {"start": v(15.52, 5.99) * mm, "end": v(15.5, 5.99) * mm});
            skLineSegment(sketch, "E6183", {"start": v(15.5, 5.99) * mm, "end": v(15.5, 6) * mm});
            skLineSegment(sketch, "E6184", {"start": v(15.5, 6) * mm, "end": v(15.49, 6) * mm});
            skLineSegment(sketch, "E6185", {"start": v(15.49, 6) * mm, "end": v(15.48, 6) * mm});
            skLineSegment(sketch, "E6186", {"start": v(15.48, 6) * mm, "end": v(15.47, 6) * mm});
            skLineSegment(sketch, "E6187", {"start": v(15.47, 6) * mm, "end": v(15.46, 6) * mm});
            skLineSegment(sketch, "E6188", {"start": v(15.46, 6) * mm, "end": v(15.42, 6.01) * mm});
            skLineSegment(sketch, "E6189", {"start": v(15.42, 6.01) * mm, "end": v(15.4, 6.02) * mm});
            skLineSegment(sketch, "E6190", {"start": v(15.4, 6.02) * mm, "end": v(15.36, 6.03) * mm});
            skLineSegment(sketch, "E6191", {"start": v(15.36, 6.03) * mm, "end": v(15.33, 6.04) * mm});
            skLineSegment(sketch, "E6192", {"start": v(15.33, 6.04) * mm, "end": v(15.3, 6.05) * mm});
            skLineSegment(sketch, "E6193", {"start": v(15.3, 6.05) * mm, "end": v(15.26, 6.06) * mm});
            skLineSegment(sketch, "E6194", {"start": v(15.26, 6.06) * mm, "end": v(15.22, 6.06) * mm});
            skLineSegment(sketch, "E6195", {"start": v(15.22, 6.06) * mm, "end": v(15.19, 6.06) * mm});
            skLineSegment(sketch, "E6196", {"start": v(15.19, 6.06) * mm, "end": v(15.15, 6.07) * mm});
            skLineSegment(sketch, "E6197", {"start": v(15.15, 6.07) * mm, "end": v(15.12, 6.08) * mm});
            skLineSegment(sketch, "E6198", {"start": v(15.12, 6.08) * mm, "end": v(15.1, 6.09) * mm});
            skLineSegment(sketch, "E6199", {"start": v(15.1, 6.09) * mm, "end": v(15.09, 6.1) * mm});
            skLineSegment(sketch, "E6200", {"start": v(15.09, 6.1) * mm, "end": v(15.08, 6.11) * mm});
            skLineSegment(sketch, "E6201", {"start": v(15.08, 6.11) * mm, "end": v(15.07, 6.12) * mm});
            skLineSegment(sketch, "E6202", {"start": v(15.07, 6.12) * mm, "end": v(15.07, 6.13) * mm});
            skLineSegment(sketch, "E6203", {"start": v(15.07, 6.13) * mm, "end": v(15.07, 6.14) * mm});
            skLineSegment(sketch, "E6204", {"start": v(15.07, 6.14) * mm, "end": v(15.07, 6.18) * mm});
            skLineSegment(sketch, "E6205", {"start": v(15.07, 6.18) * mm, "end": v(15.07, 6.22) * mm});
            skLineSegment(sketch, "E6206", {"start": v(15.07, 6.22) * mm, "end": v(15.07, 6.26) * mm});
            skLineSegment(sketch, "E6207", {"start": v(15.07, 6.26) * mm, "end": v(15.08, 6.3) * mm});
            skLineSegment(sketch, "E6208", {"start": v(15.08, 6.3) * mm, "end": v(15.08, 6.32) * mm});
            skLineSegment(sketch, "E6209", {"start": v(15.08, 6.32) * mm, "end": v(15.1, 6.35) * mm});
            skLineSegment(sketch, "E6210", {"start": v(15.1, 6.35) * mm, "end": v(15.1, 6.37) * mm});
            skLineSegment(sketch, "E6211", {"start": v(15.1, 6.37) * mm, "end": v(15.12, 6.4) * mm});
            skLineSegment(sketch, "E6212", {"start": v(15.12, 6.4) * mm, "end": v(15.25, 6.55) * mm});
            skLineSegment(sketch, "E6213", {"start": v(15.25, 6.55) * mm, "end": v(15.4, 6.7) * mm});
            skLineSegment(sketch, "E6214", {"start": v(15.4, 6.7) * mm, "end": v(15.55, 6.83) * mm});
            skLineSegment(sketch, "E6215", {"start": v(15.55, 6.83) * mm, "end": v(15.72, 6.95) * mm});
            skLineSegment(sketch, "E6216", {"start": v(15.72, 6.95) * mm, "end": v(15.9, 7.07) * mm});
            skLineSegment(sketch, "E6217", {"start": v(15.9, 7.07) * mm, "end": v(16.1, 7.17) * mm});
            skLineSegment(sketch, "E6218", {"start": v(16.1, 7.17) * mm, "end": v(16.3, 7.27) * mm});
            skLineSegment(sketch, "E6219", {"start": v(16.3, 7.27) * mm, "end": v(16.52, 7.35) * mm});
            skLineSegment(sketch, "E6220", {"start": v(16.52, 7.35) * mm, "end": v(16.62, 7.38) * mm});
            skLineSegment(sketch, "E6221", {"start": v(16.62, 7.38) * mm, "end": v(16.72, 7.41) * mm});
            skLineSegment(sketch, "E6222", {"start": v(16.72, 7.41) * mm, "end": v(16.8, 7.43) * mm});
            skLineSegment(sketch, "E6223", {"start": v(16.8, 7.43) * mm, "end": v(16.9, 7.45) * mm});
            skLineSegment(sketch, "E6224", {"start": v(16.9, 7.45) * mm, "end": v(16.98, 7.47) * mm});
            skLineSegment(sketch, "E6225", {"start": v(16.98, 7.47) * mm, "end": v(17.07, 7.48) * mm});
            skLineSegment(sketch, "E6226", {"start": v(17.07, 7.48) * mm, "end": v(17.15, 7.49) * mm});
            skLineSegment(sketch, "E6227", {"start": v(17.15, 7.49) * mm, "end": v(17.23, 7.49) * mm});
            skLineSegment(sketch, "E6228", {"start": v(17.23, 7.49) * mm, "end": v(17.3, 7.49) * mm});
            skLineSegment(sketch, "E6229", {"start": v(17.3, 7.49) * mm, "end": v(17.36, 7.48) * mm});
            skLineSegment(sketch, "E6230", {"start": v(17.36, 7.48) * mm, "end": v(17.42, 7.48) * mm});
            skLineSegment(sketch, "E6231", {"start": v(17.42, 7.48) * mm, "end": v(17.48, 7.47) * mm});
            skLineSegment(sketch, "E6232", {"start": v(17.48, 7.47) * mm, "end": v(17.53, 7.46) * mm});
            skLineSegment(sketch, "E6233", {"start": v(17.53, 7.46) * mm, "end": v(17.6, 7.44) * mm});
            skLineSegment(sketch, "E6234", {"start": v(17.6, 7.44) * mm, "end": v(17.65, 7.43) * mm});
            skLineSegment(sketch, "E6235", {"start": v(17.65, 7.43) * mm, "end": v(17.7, 7.41) * mm});
            skLineSegment(sketch, "E6236", {"start": v(17.7, 7.41) * mm, "end": v(17.73, 7.4) * mm});
            skLineSegment(sketch, "E6237", {"start": v(17.73, 7.4) * mm, "end": v(17.75, 7.4) * mm});
            skLineSegment(sketch, "E6238", {"start": v(17.75, 7.4) * mm, "end": v(17.78, 7.38) * mm});
            skLineSegment(sketch, "E6239", {"start": v(17.78, 7.38) * mm, "end": v(17.8, 7.37) * mm});
            skLineSegment(sketch, "E6240", {"start": v(17.8, 7.37) * mm, "end": v(17.82, 7.35) * mm});
            skLineSegment(sketch, "E6241", {"start": v(17.82, 7.35) * mm, "end": v(17.84, 7.34) * mm});
            skLineSegment(sketch, "E6242", {"start": v(17.84, 7.34) * mm, "end": v(17.87, 7.32) * mm});
            skLineSegment(sketch, "E6243", {"start": v(17.87, 7.32) * mm, "end": v(17.9, 7.3) * mm});
            skLineSegment(sketch, "E6244", {"start": v(17.9, 7.3) * mm, "end": v(17.9, 7.3) * mm});
            skLineSegment(sketch, "E6245", {"start": v(17.9, 7.3) * mm, "end": v(17.92, 7.29) * mm});
            skLineSegment(sketch, "E6246", {"start": v(17.92, 7.29) * mm, "end": v(17.92, 7.28) * mm});
            skLineSegment(sketch, "E6247", {"start": v(17.92, 7.28) * mm, "end": v(17.93, 7.27) * mm});
            skLineSegment(sketch, "E6248", {"start": v(17.93, 7.27) * mm, "end": v(17.94, 7.26) * mm});
            skLineSegment(sketch, "E6249", {"start": v(17.94, 7.26) * mm, "end": v(17.94, 7.25) * mm});
            skLineSegment(sketch, "E6250", {"start": v(17.94, 7.25) * mm, "end": v(17.95, 7.24) * mm});
            skLineSegment(sketch, "E6251", {"start": v(17.95, 7.24) * mm, "end": v(17.95, 7.24) * mm});
            skLineSegment(sketch, "E6252", {"start": v(17.95, 7.24) * mm, "end": v(17.95, 7.23) * mm});
            skLineSegment(sketch, "E6253", {"start": v(17.95, 7.23) * mm, "end": v(17.95, 7.22) * mm});
            skLineSegment(sketch, "E6254", {"start": v(17.95, 7.22) * mm, "end": v(17.95, 7.2) * mm});
            skLineSegment(sketch, "E6255", {"start": v(17.95, 7.2) * mm, "end": v(17.95, 7.18) * mm});
            skLineSegment(sketch, "E6256", {"start": v(17.95, 7.18) * mm, "end": v(17.95, 7.15) * mm});
            skLineSegment(sketch, "E6257", {"start": v(17.95, 7.15) * mm, "end": v(17.95, 7.12) * mm});
            skLineSegment(sketch, "E6258", {"start": v(17.95, 7.12) * mm, "end": v(17.96, 7.1) * mm});
            skLineSegment(sketch, "E6259", {"start": v(17.96, 7.1) * mm, "end": v(17.96, 7.06) * mm});
            skLineSegment(sketch, "E6260", {"start": v(17.96, 7.06) * mm, "end": v(17.96, 7.02) * mm});
            skLineSegment(sketch, "E6261", {"start": v(17.96, 7.02) * mm, "end": v(17.96, 7.02) * mm});
            skLineSegment(sketch, "E6262", {"start": v(17.96, 7.02) * mm, "end": v(17.96, 7.01) * mm});
            skLineSegment(sketch, "E6263", {"start": v(17.96, 7.01) * mm, "end": v(17.96, 7) * mm});
            skLineSegment(sketch, "E6264", {"start": v(17.96, 7) * mm, "end": v(17.96, 6.99) * mm});
            skLineSegment(sketch, "E6265", {"start": v(17.96, 6.99) * mm, "end": v(17.96, 6.96) * mm});
            skLineSegment(sketch, "E6266", {"start": v(17.96, 6.96) * mm, "end": v(17.97, 6.94) * mm});
            skLineSegment(sketch, "E6267", {"start": v(17.97, 6.94) * mm, "end": v(17.97, 6.88) * mm});
            skLineSegment(sketch, "E6268", {"start": v(17.97, 6.88) * mm, "end": v(17.97, 6.83) * mm});
            skLineSegment(sketch, "E6269", {"start": v(17.97, 6.83) * mm, "end": v(17.97, 6.8) * mm});
            skLineSegment(sketch, "E6270", {"start": v(17.97, 6.8) * mm, "end": v(17.98, 6.78) * mm});
            skLineSegment(sketch, "E6271", {"start": v(17.98, 6.78) * mm, "end": v(17.98, 6.77) * mm});
            skLineSegment(sketch, "E6272", {"start": v(17.98, 6.77) * mm, "end": v(17.98, 6.76) * mm});
            skLineSegment(sketch, "E6273", {"start": v(17.98, 6.76) * mm, "end": v(17.98, 6.76) * mm});
            skLineSegment(sketch, "E6274", {"start": v(27.7, 13.9) * mm, "end": v(27.7, 13.92) * mm});
            skLineSegment(sketch, "E6275", {"start": v(27.7, 13.92) * mm, "end": v(27.7, 13.95) * mm});
            skLineSegment(sketch, "E6276", {"start": v(27.7, 13.95) * mm, "end": v(27.7, 14) * mm});
            skLineSegment(sketch, "E6277", {"start": v(27.7, 14) * mm, "end": v(27.7, 14.04) * mm});
            skLineSegment(sketch, "E6278", {"start": v(27.7, 14.04) * mm, "end": v(27.7, 14.1) * mm});
            skLineSegment(sketch, "E6279", {"start": v(27.7, 14.1) * mm, "end": v(27.7, 14.16) * mm});
            skLineSegment(sketch, "E6280", {"start": v(27.7, 14.16) * mm, "end": v(27.7, 14.22) * mm});
            skLineSegment(sketch, "E6281", {"start": v(27.7, 14.22) * mm, "end": v(27.7, 14.23) * mm});
            skLineSegment(sketch, "E6282", {"start": v(27.7, 14.23) * mm, "end": v(27.7, 14.23) * mm});
            skLineSegment(sketch, "E6283", {"start": v(27.7, 14.23) * mm, "end": v(27.71, 14.23) * mm});
            skLineSegment(sketch, "E6284", {"start": v(27.71, 14.23) * mm, "end": v(27.72, 14.24) * mm});
            skLineSegment(sketch, "E6285", {"start": v(27.72, 14.24) * mm, "end": v(27.73, 14.26) * mm});
            skLineSegment(sketch, "E6286", {"start": v(27.73, 14.26) * mm, "end": v(27.75, 14.28) * mm});
            skLineSegment(sketch, "E6287", {"start": v(27.75, 14.28) * mm, "end": v(27.78, 14.31) * mm});
            skLineSegment(sketch, "E6288", {"start": v(27.78, 14.31) * mm, "end": v(27.82, 14.35) * mm});
            skLineSegment(sketch, "E6289", {"start": v(27.82, 14.35) * mm, "end": v(27.87, 14.42) * mm});
            skLineSegment(sketch, "E6290", {"start": v(27.87, 14.42) * mm, "end": v(27.92, 14.49) * mm});
            skLineSegment(sketch, "E6291", {"start": v(27.92, 14.49) * mm, "end": v(27.98, 14.55) * mm});
            skLineSegment(sketch, "E6292", {"start": v(27.98, 14.55) * mm, "end": v(28.02, 14.62) * mm});
            skLineSegment(sketch, "E6293", {"start": v(28.02, 14.62) * mm, "end": v(28.07, 14.7) * mm});
            skLineSegment(sketch, "E6294", {"start": v(28.07, 14.7) * mm, "end": v(28.11, 14.76) * mm});
            skLineSegment(sketch, "E6295", {"start": v(28.11, 14.76) * mm, "end": v(28.15, 14.84) * mm});
            skLineSegment(sketch, "E6296", {"start": v(28.15, 14.84) * mm, "end": v(28.2, 14.9) * mm});
            skLineSegment(sketch, "E6297", {"start": v(28.2, 14.9) * mm, "end": v(28.23, 14.98) * mm});
            skLineSegment(sketch, "E6298", {"start": v(28.23, 14.98) * mm, "end": v(28.27, 15.04) * mm});
            skLineSegment(sketch, "E6299", {"start": v(28.27, 15.04) * mm, "end": v(28.32, 15.1) * mm});
            skLineSegment(sketch, "E6300", {"start": v(28.32, 15.1) * mm, "end": v(28.38, 15.16) * mm});
            skLineSegment(sketch, "E6301", {"start": v(28.38, 15.16) * mm, "end": v(28.44, 15.22) * mm});
            skLineSegment(sketch, "E6302", {"start": v(28.44, 15.22) * mm, "end": v(28.5, 15.27) * mm});
            skLineSegment(sketch, "E6303", {"start": v(28.5, 15.27) * mm, "end": v(28.58, 15.33) * mm});
            skLineSegment(sketch, "E6304", {"start": v(28.58, 15.33) * mm, "end": v(28.66, 15.38) * mm});
            skLineSegment(sketch, "E6305", {"start": v(28.66, 15.38) * mm, "end": v(28.7, 15.4) * mm});
            skLineSegment(sketch, "E6306", {"start": v(28.7, 15.4) * mm, "end": v(28.75, 15.43) * mm});
            skLineSegment(sketch, "E6307", {"start": v(28.75, 15.43) * mm, "end": v(28.8, 15.45) * mm});
            skLineSegment(sketch, "E6308", {"start": v(28.8, 15.45) * mm, "end": v(28.84, 15.47) * mm});
            skLineSegment(sketch, "E6309", {"start": v(28.84, 15.47) * mm, "end": v(28.9, 15.5) * mm});
            skLineSegment(sketch, "E6310", {"start": v(28.9, 15.5) * mm, "end": v(28.94, 15.51) * mm});
            skLineSegment(sketch, "E6311", {"start": v(28.94, 15.51) * mm, "end": v(28.99, 15.53) * mm});
            skLineSegment(sketch, "E6312", {"start": v(28.99, 15.53) * mm, "end": v(29.04, 15.55) * mm});
            skLineSegment(sketch, "E6313", {"start": v(29.04, 15.55) * mm, "end": v(29.07, 15.56) * mm});
            skLineSegment(sketch, "E6314", {"start": v(29.07, 15.56) * mm, "end": v(29.1, 15.57) * mm});
            skLineSegment(sketch, "E6315", {"start": v(29.1, 15.57) * mm, "end": v(29.12, 15.58) * mm});
            skLineSegment(sketch, "E6316", {"start": v(29.12, 15.58) * mm, "end": v(29.15, 15.6) * mm});
            skLineSegment(sketch, "E6317", {"start": v(29.15, 15.6) * mm, "end": v(29.18, 15.6) * mm});
            skLineSegment(sketch, "E6318", {"start": v(29.18, 15.6) * mm, "end": v(29.2, 15.62) * mm});
            skLineSegment(sketch, "E6319", {"start": v(29.2, 15.62) * mm, "end": v(29.23, 15.63) * mm});
            skLineSegment(sketch, "E6320", {"start": v(29.23, 15.63) * mm, "end": v(29.26, 15.64) * mm});
            skLineSegment(sketch, "E6321", {"start": v(29.26, 15.64) * mm, "end": v(29.28, 15.65) * mm});
            skLineSegment(sketch, "E6322", {"start": v(29.28, 15.65) * mm, "end": v(29.3, 15.66) * mm});
            skLineSegment(sketch, "E6323", {"start": v(29.3, 15.66) * mm, "end": v(29.31, 15.67) * mm});
            skLineSegment(sketch, "E6324", {"start": v(29.31, 15.67) * mm, "end": v(29.33, 15.68) * mm});
            skLineSegment(sketch, "E6325", {"start": v(29.33, 15.68) * mm, "end": v(29.35, 15.69) * mm});
            skLineSegment(sketch, "E6326", {"start": v(29.35, 15.69) * mm, "end": v(29.37, 15.7) * mm});
            skLineSegment(sketch, "E6327", {"start": v(29.37, 15.7) * mm, "end": v(29.39, 15.7) * mm});
            skLineSegment(sketch, "E6328", {"start": v(29.39, 15.7) * mm, "end": v(29.4, 15.72) * mm});
            skLineSegment(sketch, "E6329", {"start": v(29.4, 15.72) * mm, "end": v(29.41, 15.73) * mm});
            skLineSegment(sketch, "E6330", {"start": v(29.41, 15.73) * mm, "end": v(29.42, 15.73) * mm});
            skLineSegment(sketch, "E6331", {"start": v(29.42, 15.73) * mm, "end": v(29.43, 15.74) * mm});
            skLineSegment(sketch, "E6332", {"start": v(29.43, 15.74) * mm, "end": v(29.44, 15.74) * mm});
            skLineSegment(sketch, "E6333", {"start": v(29.44, 15.74) * mm, "end": v(29.44, 15.75) * mm});
            skLineSegment(sketch, "E6334", {"start": v(29.44, 15.75) * mm, "end": v(29.45, 15.75) * mm});
            skLineSegment(sketch, "E6335", {"start": v(29.45, 15.75) * mm, "end": v(29.46, 15.76) * mm});
            skLineSegment(sketch, "E6336", {"start": v(29.46, 15.76) * mm, "end": v(29.47, 15.76) * mm});
            skLineSegment(sketch, "E6337", {"start": v(29.47, 15.76) * mm, "end": v(29.48, 15.77) * mm});
            skLineSegment(sketch, "E6338", {"start": v(29.48, 15.77) * mm, "end": v(29.49, 15.77) * mm});
            skLineSegment(sketch, "E6339", {"start": v(29.49, 15.77) * mm, "end": v(29.5, 15.77) * mm});
            skLineSegment(sketch, "E6340", {"start": v(29.5, 15.77) * mm, "end": v(29.5, 15.78) * mm});
            skLineSegment(sketch, "E6341", {"start": v(29.5, 15.78) * mm, "end": v(29.5, 15.78) * mm});
            skLineSegment(sketch, "E6342", {"start": v(29.5, 15.78) * mm, "end": v(29.51, 15.78) * mm});
            skLineSegment(sketch, "E6343", {"start": v(29.51, 15.78) * mm, "end": v(29.51, 15.78) * mm});
            skLineSegment(sketch, "E6344", {"start": v(29.51, 15.78) * mm, "end": v(29.52, 15.78) * mm});
            skLineSegment(sketch, "E6345", {"start": v(29.52, 15.78) * mm, "end": v(29.52, 15.77) * mm});
            skLineSegment(sketch, "E6346", {"start": v(29.52, 15.77) * mm, "end": v(29.53, 15.77) * mm});
            skLineSegment(sketch, "E6347", {"start": v(29.53, 15.77) * mm, "end": v(29.53, 15.77) * mm});
            skLineSegment(sketch, "E6348", {"start": v(29.53, 15.77) * mm, "end": v(29.54, 15.76) * mm});
            skLineSegment(sketch, "E6349", {"start": v(29.54, 15.76) * mm, "end": v(29.54, 15.75) * mm});
            skLineSegment(sketch, "E6350", {"start": v(29.54, 15.75) * mm, "end": v(29.55, 15.75) * mm});
            skLineSegment(sketch, "E6351", {"start": v(29.55, 15.75) * mm, "end": v(29.55, 15.74) * mm});
            skLineSegment(sketch, "E6352", {"start": v(29.55, 15.74) * mm, "end": v(29.56, 15.73) * mm});
            skLineSegment(sketch, "E6353", {"start": v(29.56, 15.73) * mm, "end": v(29.57, 15.72) * mm});
            skLineSegment(sketch, "E6354", {"start": v(29.57, 15.72) * mm, "end": v(29.58, 15.7) * mm});
            skLineSegment(sketch, "E6355", {"start": v(29.58, 15.7) * mm, "end": v(29.6, 15.69) * mm});
            skLineSegment(sketch, "E6356", {"start": v(29.6, 15.69) * mm, "end": v(29.6, 15.67) * mm});
            skLineSegment(sketch, "E6357", {"start": v(29.6, 15.67) * mm, "end": v(29.62, 15.66) * mm});
            skLineSegment(sketch, "E6358", {"start": v(29.62, 15.66) * mm, "end": v(29.63, 15.64) * mm});
            skLineSegment(sketch, "E6359", {"start": v(29.63, 15.64) * mm, "end": v(29.65, 15.63) * mm});
            skLineSegment(sketch, "E6360", {"start": v(29.65, 15.63) * mm, "end": v(29.66, 15.61) * mm});
            skLineSegment(sketch, "E6361", {"start": v(29.66, 15.61) * mm, "end": v(29.68, 15.6) * mm});
            skLineSegment(sketch, "E6362", {"start": v(29.68, 15.6) * mm, "end": v(29.7, 15.58) * mm});
            skLineSegment(sketch, "E6363", {"start": v(29.7, 15.58) * mm, "end": v(29.7, 15.56) * mm});
            skLineSegment(sketch, "E6364", {"start": v(29.7, 15.56) * mm, "end": v(29.72, 15.55) * mm});
            skLineSegment(sketch, "E6365", {"start": v(29.72, 15.55) * mm, "end": v(29.73, 15.53) * mm});
            skLineSegment(sketch, "E6366", {"start": v(29.73, 15.53) * mm, "end": v(29.74, 15.51) * mm});
            skLineSegment(sketch, "E6367", {"start": v(29.74, 15.51) * mm, "end": v(29.75, 15.5) * mm});
            skLineSegment(sketch, "E6368", {"start": v(29.75, 15.5) * mm, "end": v(29.76, 15.47) * mm});
            skLineSegment(sketch, "E6369", {"start": v(29.76, 15.47) * mm, "end": v(29.77, 15.43) * mm});
            skLineSegment(sketch, "E6370", {"start": v(29.77, 15.43) * mm, "end": v(29.79, 15.4) * mm});
            skLineSegment(sketch, "E6371", {"start": v(29.79, 15.4) * mm, "end": v(29.8, 15.35) * mm});
            skLineSegment(sketch, "E6372", {"start": v(29.8, 15.35) * mm, "end": v(29.81, 15.3) * mm});
            skLineSegment(sketch, "E6373", {"start": v(29.81, 15.3) * mm, "end": v(29.82, 15.26) * mm});
            skLineSegment(sketch, "E6374", {"start": v(29.82, 15.26) * mm, "end": v(29.82, 15.22) * mm});
            skLineSegment(sketch, "E6375", {"start": v(29.82, 15.22) * mm, "end": v(29.82, 15.18) * mm});
            skLineSegment(sketch, "E6376", {"start": v(29.82, 15.18) * mm, "end": v(29.78, 15.06) * mm});
            skLineSegment(sketch, "E6377", {"start": v(29.78, 15.06) * mm, "end": v(29.73, 14.94) * mm});
            skLineSegment(sketch, "E6378", {"start": v(29.73, 14.94) * mm, "end": v(29.68, 14.82) * mm});
            skLineSegment(sketch, "E6379", {"start": v(29.68, 14.82) * mm, "end": v(29.62, 14.7) * mm});
            skLineSegment(sketch, "E6380", {"start": v(29.62, 14.7) * mm, "end": v(29.56, 14.58) * mm});
            skLineSegment(sketch, "E6381", {"start": v(29.56, 14.58) * mm, "end": v(29.48, 14.47) * mm});
            skLineSegment(sketch, "E6382", {"start": v(29.48, 14.47) * mm, "end": v(29.39, 14.36) * mm});
            skLineSegment(sketch, "E6383", {"start": v(29.39, 14.36) * mm, "end": v(29.28, 14.26) * mm});
            skLineSegment(sketch, "E6384", {"start": v(29.28, 14.26) * mm, "end": v(29.24, 14.22) * mm});
            skLineSegment(sketch, "E6385", {"start": v(29.24, 14.22) * mm, "end": v(29.2, 14.18) * mm});
            skLineSegment(sketch, "E6386", {"start": v(29.2, 14.18) * mm, "end": v(29.15, 14.15) * mm});
            skLineSegment(sketch, "E6387", {"start": v(29.15, 14.15) * mm, "end": v(29.11, 14.1) * mm});
            skLineSegment(sketch, "E6388", {"start": v(29.11, 14.1) * mm, "end": v(29.07, 14.07) * mm});
            skLineSegment(sketch, "E6389", {"start": v(29.07, 14.07) * mm, "end": v(29.03, 14.03) * mm});
            skLineSegment(sketch, "E6390", {"start": v(29.03, 14.03) * mm, "end": v(28.99, 13.99) * mm});
            skLineSegment(sketch, "E6391", {"start": v(28.99, 13.99) * mm, "end": v(28.95, 13.95) * mm});
            skLineSegment(sketch, "E6392", {"start": v(28.95, 13.95) * mm, "end": v(28.91, 13.91) * mm});
            skLineSegment(sketch, "E6393", {"start": v(28.91, 13.91) * mm, "end": v(28.88, 13.88) * mm});
            skLineSegment(sketch, "E6394", {"start": v(28.88, 13.88) * mm, "end": v(28.84, 13.84) * mm});
            skLineSegment(sketch, "E6395", {"start": v(28.84, 13.84) * mm, "end": v(28.8, 13.8) * mm});
            skLineSegment(sketch, "E6396", {"start": v(28.8, 13.8) * mm, "end": v(28.77, 13.77) * mm});
            skLineSegment(sketch, "E6397", {"start": v(28.77, 13.77) * mm, "end": v(28.73, 13.73) * mm});
            skLineSegment(sketch, "E6398", {"start": v(28.73, 13.73) * mm, "end": v(28.69, 13.7) * mm});
            skLineSegment(sketch, "E6399", {"start": v(28.69, 13.7) * mm, "end": v(28.65, 13.67) * mm});
            skLineSegment(sketch, "E6400", {"start": v(28.65, 13.67) * mm, "end": v(28.58, 13.6) * mm});
            skLineSegment(sketch, "E6401", {"start": v(28.58, 13.6) * mm, "end": v(28.53, 13.56) * mm});
            skLineSegment(sketch, "E6402", {"start": v(28.53, 13.56) * mm, "end": v(28.5, 13.53) * mm});
            skLineSegment(sketch, "E6403", {"start": v(28.5, 13.53) * mm, "end": v(28.47, 13.5) * mm});
            skLineSegment(sketch, "E6404", {"start": v(28.47, 13.5) * mm, "end": v(28.45, 13.5) * mm});
            skLineSegment(sketch, "E6405", {"start": v(28.45, 13.5) * mm, "end": v(28.44, 13.49) * mm});
            skLineSegment(sketch, "E6406", {"start": v(28.44, 13.49) * mm, "end": v(28.44, 13.49) * mm});
            skLineSegment(sketch, "E6407", {"start": v(28.44, 13.49) * mm, "end": v(28.44, 13.48) * mm});
            skLineSegment(sketch, "E6408", {"start": v(28.44, 13.48) * mm, "end": v(28.34, 13.47) * mm});
            skLineSegment(sketch, "E6409", {"start": v(28.34, 13.47) * mm, "end": v(28.25, 13.45) * mm});
            skLineSegment(sketch, "E6410", {"start": v(28.25, 13.45) * mm, "end": v(28.16, 13.44) * mm});
            skLineSegment(sketch, "E6411", {"start": v(28.16, 13.44) * mm, "end": v(28.09, 13.42) * mm});
            skLineSegment(sketch, "E6412", {"start": v(28.09, 13.42) * mm, "end": v(28.02, 13.41) * mm});
            skLineSegment(sketch, "E6413", {"start": v(28.02, 13.41) * mm, "end": v(27.98, 13.4) * mm});
            skLineSegment(sketch, "E6414", {"start": v(27.98, 13.4) * mm, "end": v(27.94, 13.4) * mm});
            skLineSegment(sketch, "E6415", {"start": v(27.94, 13.4) * mm, "end": v(27.93, 13.4) * mm});
            skLineSegment(sketch, "E6416", {"start": v(27.93, 13.4) * mm, "end": v(27.93, 13.4) * mm});
            skLineSegment(sketch, "E6417", {"start": v(27.93, 13.4) * mm, "end": v(27.92, 13.4) * mm});
            skLineSegment(sketch, "E6418", {"start": v(27.92, 13.4) * mm, "end": v(27.92, 13.4) * mm});
            skLineSegment(sketch, "E6419", {"start": v(27.92, 13.4) * mm, "end": v(27.91, 13.4) * mm});
            skLineSegment(sketch, "E6420", {"start": v(27.91, 13.4) * mm, "end": v(27.9, 13.39) * mm});
            skLineSegment(sketch, "E6421", {"start": v(27.9, 13.39) * mm, "end": v(27.9, 13.39) * mm});
            skLineSegment(sketch, "E6422", {"start": v(27.9, 13.39) * mm, "end": v(27.89, 13.39) * mm});
            skLineSegment(sketch, "E6423", {"start": v(27.89, 13.39) * mm, "end": v(27.88, 13.4) * mm});
            skLineSegment(sketch, "E6424", {"start": v(27.88, 13.4) * mm, "end": v(27.88, 13.4) * mm});
            skLineSegment(sketch, "E6425", {"start": v(27.88, 13.4) * mm, "end": v(27.87, 13.4) * mm});
            skLineSegment(sketch, "E6426", {"start": v(27.87, 13.4) * mm, "end": v(27.87, 13.4) * mm});
            skLineSegment(sketch, "E6427", {"start": v(27.87, 13.4) * mm, "end": v(27.86, 13.42) * mm});
            skLineSegment(sketch, "E6428", {"start": v(27.86, 13.42) * mm, "end": v(27.86, 13.43) * mm});
            skLineSegment(sketch, "E6429", {"start": v(27.86, 13.43) * mm, "end": v(27.86, 13.43) * mm});
            skLineSegment(sketch, "E6430", {"start": v(27.86, 13.43) * mm, "end": v(27.86, 13.44) * mm});
            skLineSegment(sketch, "E6431", {"start": v(27.86, 13.44) * mm, "end": v(27.85, 13.44) * mm});
            skLineSegment(sketch, "E6432", {"start": v(27.85, 13.44) * mm, "end": v(27.85, 13.45) * mm});
            skLineSegment(sketch, "E6433", {"start": v(27.85, 13.45) * mm, "end": v(27.85, 13.47) * mm});
            skLineSegment(sketch, "E6434", {"start": v(27.85, 13.47) * mm, "end": v(27.84, 13.48) * mm});
            skLineSegment(sketch, "E6435", {"start": v(27.84, 13.48) * mm, "end": v(27.84, 13.5) * mm});
            skLineSegment(sketch, "E6436", {"start": v(27.84, 13.5) * mm, "end": v(27.83, 13.5) * mm});
            skLineSegment(sketch, "E6437", {"start": v(27.83, 13.5) * mm, "end": v(27.82, 13.52) * mm});
            skLineSegment(sketch, "E6438", {"start": v(27.82, 13.52) * mm, "end": v(27.82, 13.54) * mm});
            skLineSegment(sketch, "E6439", {"start": v(27.82, 13.54) * mm, "end": v(27.8, 13.55) * mm});
            skLineSegment(sketch, "E6440", {"start": v(27.8, 13.55) * mm, "end": v(27.8, 13.56) * mm});
            skLineSegment(sketch, "E6441", {"start": v(27.8, 13.56) * mm, "end": v(27.78, 13.6) * mm});
            skLineSegment(sketch, "E6442", {"start": v(27.78, 13.6) * mm, "end": v(27.76, 13.62) * mm});
            skLineSegment(sketch, "E6443", {"start": v(27.76, 13.62) * mm, "end": v(27.75, 13.63) * mm});
            skLineSegment(sketch, "E6444", {"start": v(27.75, 13.63) * mm, "end": v(27.74, 13.64) * mm});
            skLineSegment(sketch, "E6445", {"start": v(27.74, 13.64) * mm, "end": v(27.74, 13.65) * mm});
            skLineSegment(sketch, "E6446", {"start": v(27.74, 13.65) * mm, "end": v(27.74, 13.65) * mm});
            skLineSegment(sketch, "E6447", {"start": v(27.74, 13.65) * mm, "end": v(27.73, 13.7) * mm});
            skLineSegment(sketch, "E6448", {"start": v(27.73, 13.7) * mm, "end": v(27.72, 13.74) * mm});
            skLineSegment(sketch, "E6449", {"start": v(27.72, 13.74) * mm, "end": v(27.71, 13.78) * mm});
            skLineSegment(sketch, "E6450", {"start": v(27.71, 13.78) * mm, "end": v(27.7, 13.82) * mm});
            skLineSegment(sketch, "E6451", {"start": v(27.7, 13.82) * mm, "end": v(27.7, 13.85) * mm});
            skLineSegment(sketch, "E6452", {"start": v(27.7, 13.85) * mm, "end": v(27.7, 13.87) * mm});
            skLineSegment(sketch, "E6453", {"start": v(27.7, 13.87) * mm, "end": v(27.7, 13.89) * mm});
            skLineSegment(sketch, "E6454", {"start": v(27.7, 13.89) * mm, "end": v(27.7, 13.9) * mm});
            skLineSegment(sketch, "E6455", {"start": v(27.7, 13.9) * mm, "end": v(27.7, 13.9) * mm});
            skLineSegment(sketch, "E6456", {"start": v(24.5, 16.07) * mm, "end": v(24.51, 16.12) * mm});
            skLineSegment(sketch, "E6457", {"start": v(24.51, 16.12) * mm, "end": v(24.53, 16.17) * mm});
            skLineSegment(sketch, "E6458", {"start": v(24.53, 16.17) * mm, "end": v(24.54, 16.22) * mm});
            skLineSegment(sketch, "E6459", {"start": v(24.54, 16.22) * mm, "end": v(24.56, 16.28) * mm});
            skLineSegment(sketch, "E6460", {"start": v(24.56, 16.28) * mm, "end": v(24.57, 16.33) * mm});
            skLineSegment(sketch, "E6461", {"start": v(24.57, 16.33) * mm, "end": v(24.58, 16.34) * mm});
            skLineSegment(sketch, "E6462", {"start": v(24.58, 16.34) * mm, "end": v(24.58, 16.36) * mm});
            skLineSegment(sketch, "E6463", {"start": v(24.58, 16.36) * mm, "end": v(24.59, 16.37) * mm});
            skLineSegment(sketch, "E6464", {"start": v(24.59, 16.37) * mm, "end": v(24.6, 16.39) * mm});
            skLineSegment(sketch, "E6465", {"start": v(24.6, 16.39) * mm, "end": v(24.6, 16.4) * mm});
            skLineSegment(sketch, "E6466", {"start": v(24.6, 16.4) * mm, "end": v(24.6, 16.42) * mm});
            skLineSegment(sketch, "E6467", {"start": v(24.6, 16.42) * mm, "end": v(24.6, 16.43) * mm});
            skLineSegment(sketch, "E6468", {"start": v(24.6, 16.43) * mm, "end": v(24.61, 16.45) * mm});
            skLineSegment(sketch, "E6469", {"start": v(24.61, 16.45) * mm, "end": v(24.62, 16.46) * mm});
            skLineSegment(sketch, "E6470", {"start": v(24.62, 16.46) * mm, "end": v(24.62, 16.47) * mm});
            skLineSegment(sketch, "E6471", {"start": v(24.62, 16.47) * mm, "end": v(24.62, 16.48) * mm});
            skLineSegment(sketch, "E6472", {"start": v(24.62, 16.48) * mm, "end": v(24.63, 16.5) * mm});
            skLineSegment(sketch, "E6473", {"start": v(24.63, 16.5) * mm, "end": v(24.63, 16.5) * mm});
            skLineSegment(sketch, "E6474", {"start": v(24.63, 16.5) * mm, "end": v(24.63, 16.52) * mm});
            skLineSegment(sketch, "E6475", {"start": v(24.63, 16.52) * mm, "end": v(24.64, 16.53) * mm});
            skLineSegment(sketch, "E6476", {"start": v(24.64, 16.53) * mm, "end": v(24.64, 16.54) * mm});
            skLineSegment(sketch, "E6477", {"start": v(24.64, 16.54) * mm, "end": v(24.64, 16.56) * mm});
            skLineSegment(sketch, "E6478", {"start": v(24.64, 16.56) * mm, "end": v(24.65, 16.57) * mm});
            skLineSegment(sketch, "E6479", {"start": v(24.65, 16.57) * mm, "end": v(24.65, 16.59) * mm});
            skLineSegment(sketch, "E6480", {"start": v(24.65, 16.59) * mm, "end": v(24.65, 16.6) * mm});
            skLineSegment(sketch, "E6481", {"start": v(24.65, 16.6) * mm, "end": v(24.66, 16.61) * mm});
            skLineSegment(sketch, "E6482", {"start": v(24.66, 16.61) * mm, "end": v(24.66, 16.63) * mm});
            skLineSegment(sketch, "E6483", {"start": v(24.66, 16.63) * mm, "end": v(24.66, 16.64) * mm});
            skLineSegment(sketch, "E6484", {"start": v(24.66, 16.64) * mm, "end": v(24.67, 16.66) * mm});
            skLineSegment(sketch, "E6485", {"start": v(24.67, 16.66) * mm, "end": v(24.72, 16.8) * mm});
            skLineSegment(sketch, "E6486", {"start": v(24.72, 16.8) * mm, "end": v(24.77, 16.93) * mm});
            skLineSegment(sketch, "E6487", {"start": v(24.77, 16.93) * mm, "end": v(24.82, 17.06) * mm});
            skLineSegment(sketch, "E6488", {"start": v(24.82, 17.06) * mm, "end": v(24.89, 17.18) * mm});
            skLineSegment(sketch, "E6489", {"start": v(24.89, 17.18) * mm, "end": v(24.96, 17.3) * mm});
            skLineSegment(sketch, "E6490", {"start": v(24.96, 17.3) * mm, "end": v(25.05, 17.4) * mm});
            skLineSegment(sketch, "E6491", {"start": v(25.05, 17.4) * mm, "end": v(25.15, 17.5) * mm});
            skLineSegment(sketch, "E6492", {"start": v(25.15, 17.5) * mm, "end": v(25.27, 17.58) * mm});
            skLineSegment(sketch, "E6493", {"start": v(25.27, 17.58) * mm, "end": v(25.3, 17.6) * mm});
            skLineSegment(sketch, "E6494", {"start": v(25.3, 17.6) * mm, "end": v(25.32, 17.6) * mm});
            skLineSegment(sketch, "E6495", {"start": v(25.32, 17.6) * mm, "end": v(25.34, 17.62) * mm});
            skLineSegment(sketch, "E6496", {"start": v(25.34, 17.62) * mm, "end": v(25.36, 17.64) * mm});
            skLineSegment(sketch, "E6497", {"start": v(25.36, 17.64) * mm, "end": v(25.38, 17.65) * mm});
            skLineSegment(sketch, "E6498", {"start": v(25.38, 17.65) * mm, "end": v(25.4, 17.67) * mm});
            skLineSegment(sketch, "E6499", {"start": v(25.4, 17.67) * mm, "end": v(25.41, 17.68) * mm});
            skLineSegment(sketch, "E6500", {"start": v(25.41, 17.68) * mm, "end": v(25.43, 17.7) * mm});
            skLineSegment(sketch, "E6501", {"start": v(25.43, 17.7) * mm, "end": v(25.44, 17.7) * mm});
            skLineSegment(sketch, "E6502", {"start": v(25.44, 17.7) * mm, "end": v(25.45, 17.72) * mm});
            skLineSegment(sketch, "E6503", {"start": v(25.45, 17.72) * mm, "end": v(25.46, 17.72) * mm});
            skLineSegment(sketch, "E6504", {"start": v(25.46, 17.72) * mm, "end": v(25.47, 17.73) * mm});
            skLineSegment(sketch, "E6505", {"start": v(25.47, 17.73) * mm, "end": v(25.48, 17.74) * mm});
            skLineSegment(sketch, "E6506", {"start": v(25.48, 17.74) * mm, "end": v(25.49, 17.75) * mm});
            skLineSegment(sketch, "E6507", {"start": v(25.49, 17.75) * mm, "end": v(25.5, 17.75) * mm});
            skLineSegment(sketch, "E6508", {"start": v(25.5, 17.75) * mm, "end": v(25.5, 17.76) * mm});
            skLineSegment(sketch, "E6509", {"start": v(25.5, 17.76) * mm, "end": v(25.54, 17.78) * mm});
            skLineSegment(sketch, "E6510", {"start": v(25.54, 17.78) * mm, "end": v(25.56, 17.8) * mm});
            skLineSegment(sketch, "E6511", {"start": v(25.56, 17.8) * mm, "end": v(25.59, 17.82) * mm});
            skLineSegment(sketch, "E6512", {"start": v(25.59, 17.82) * mm, "end": v(25.6, 17.83) * mm});
            skLineSegment(sketch, "E6513", {"start": v(25.6, 17.83) * mm, "end": v(25.63, 17.83) * mm});
            skLineSegment(sketch, "E6514", {"start": v(25.63, 17.83) * mm, "end": v(25.65, 17.84) * mm});
            skLineSegment(sketch, "E6515", {"start": v(25.65, 17.84) * mm, "end": v(25.66, 17.84) * mm});
            skLineSegment(sketch, "E6516", {"start": v(25.66, 17.84) * mm, "end": v(25.67, 17.84) * mm});
            skLineSegment(sketch, "E6517", {"start": v(25.67, 17.84) * mm, "end": v(25.69, 17.84) * mm});
            skLineSegment(sketch, "E6518", {"start": v(25.69, 17.84) * mm, "end": v(25.7, 17.83) * mm});
            skLineSegment(sketch, "E6519", {"start": v(25.7, 17.83) * mm, "end": v(25.73, 17.82) * mm});
            skLineSegment(sketch, "E6520", {"start": v(25.73, 17.82) * mm, "end": v(25.75, 17.8) * mm});
            skLineSegment(sketch, "E6521", {"start": v(25.75, 17.8) * mm, "end": v(25.77, 17.77) * mm});
            skLineSegment(sketch, "E6522", {"start": v(25.77, 17.77) * mm, "end": v(25.8, 17.73) * mm});
            skLineSegment(sketch, "E6523", {"start": v(25.8, 17.73) * mm, "end": v(25.83, 17.67) * mm});
            skLineSegment(sketch, "E6524", {"start": v(25.83, 17.67) * mm, "end": v(25.86, 17.6) * mm});
            skLineSegment(sketch, "E6525", {"start": v(25.86, 17.6) * mm, "end": v(25.87, 17.57) * mm});
            skLineSegment(sketch, "E6526", {"start": v(25.87, 17.57) * mm, "end": v(25.88, 17.55) * mm});
            skLineSegment(sketch, "E6527", {"start": v(25.88, 17.55) * mm, "end": v(25.89, 17.52) * mm});
            skLineSegment(sketch, "E6528", {"start": v(25.89, 17.52) * mm, "end": v(25.9, 17.5) * mm});
            skLineSegment(sketch, "E6529", {"start": v(25.9, 17.5) * mm, "end": v(25.91, 17.47) * mm});
            skLineSegment(sketch, "E6530", {"start": v(25.91, 17.47) * mm, "end": v(25.92, 17.44) * mm});
            skLineSegment(sketch, "E6531", {"start": v(25.92, 17.44) * mm, "end": v(25.94, 17.42) * mm});
            skLineSegment(sketch, "E6532", {"start": v(25.94, 17.42) * mm, "end": v(25.95, 17.4) * mm});
            skLineSegment(sketch, "E6533", {"start": v(25.95, 17.4) * mm, "end": v(25.95, 17.39) * mm});
            skLineSegment(sketch, "E6534", {"start": v(25.95, 17.39) * mm, "end": v(25.96, 17.38) * mm});
            skLineSegment(sketch, "E6535", {"start": v(25.96, 17.38) * mm, "end": v(25.96, 17.38) * mm});
            skLineSegment(sketch, "E6536", {"start": v(25.96, 17.38) * mm, "end": v(25.96, 17.37) * mm});
            skLineSegment(sketch, "E6537", {"start": v(25.96, 17.37) * mm, "end": v(25.96, 17.37) * mm});
            skLineSegment(sketch, "E6538", {"start": v(25.96, 17.37) * mm, "end": v(25.97, 17.36) * mm});
            skLineSegment(sketch, "E6539", {"start": v(25.97, 17.36) * mm, "end": v(25.97, 17.35) * mm});
            skLineSegment(sketch, "E6540", {"start": v(25.97, 17.35) * mm, "end": v(25.97, 17.34) * mm});
            skLineSegment(sketch, "E6541", {"start": v(25.97, 17.34) * mm, "end": v(25.98, 17.33) * mm});
            skLineSegment(sketch, "E6542", {"start": v(25.98, 17.33) * mm, "end": v(25.98, 17.32) * mm});
            skLineSegment(sketch, "E6543", {"start": v(25.98, 17.32) * mm, "end": v(25.98, 17.31) * mm});
            skLineSegment(sketch, "E6544", {"start": v(25.98, 17.31) * mm, "end": v(25.98, 17.3) * mm});
            skLineSegment(sketch, "E6545", {"start": v(25.98, 17.3) * mm, "end": v(25.98, 17.3) * mm});
            skLineSegment(sketch, "E6546", {"start": v(25.98, 17.3) * mm, "end": v(25.98, 17.29) * mm});
            skLineSegment(sketch, "E6547", {"start": v(25.98, 17.29) * mm, "end": v(25.98, 17.26) * mm});
            skLineSegment(sketch, "E6548", {"start": v(25.98, 17.26) * mm, "end": v(25.98, 17.24) * mm});
            skLineSegment(sketch, "E6549", {"start": v(25.98, 17.24) * mm, "end": v(25.98, 17.22) * mm});
            skLineSegment(sketch, "E6550", {"start": v(25.98, 17.22) * mm, "end": v(25.98, 17.2) * mm});
            skLineSegment(sketch, "E6551", {"start": v(25.98, 17.2) * mm, "end": v(25.98, 17.17) * mm});
            skLineSegment(sketch, "E6552", {"start": v(25.98, 17.17) * mm, "end": v(25.98, 17.14) * mm});
            skLineSegment(sketch, "E6553", {"start": v(25.98, 17.14) * mm, "end": v(25.99, 17.12) * mm});
            skLineSegment(sketch, "E6554", {"start": v(25.99, 17.12) * mm, "end": v(26, 17.1) * mm});
            skLineSegment(sketch, "E6555", {"start": v(26, 17.1) * mm, "end": v(26.02, 17) * mm});
            skLineSegment(sketch, "E6556", {"start": v(26.02, 17) * mm, "end": v(26.04, 16.92) * mm});
            skLineSegment(sketch, "E6557", {"start": v(26.04, 16.92) * mm, "end": v(26.05, 16.84) * mm});
            skLineSegment(sketch, "E6558", {"start": v(26.05, 16.84) * mm, "end": v(26.05, 16.76) * mm});
            skLineSegment(sketch, "E6559", {"start": v(26.05, 16.76) * mm, "end": v(26.04, 16.7) * mm});
            skLineSegment(sketch, "E6560", {"start": v(26.04, 16.7) * mm, "end": v(26.03, 16.62) * mm});
            skLineSegment(sketch, "E6561", {"start": v(26.03, 16.62) * mm, "end": v(26.01, 16.55) * mm});
            skLineSegment(sketch, "E6562", {"start": v(26.01, 16.55) * mm, "end": v(25.98, 16.48) * mm});
            skLineSegment(sketch, "E6563", {"start": v(25.98, 16.48) * mm, "end": v(25.98, 16.46) * mm});
            skLineSegment(sketch, "E6564", {"start": v(25.98, 16.46) * mm, "end": v(25.97, 16.44) * mm});
            skLineSegment(sketch, "E6565", {"start": v(25.97, 16.44) * mm, "end": v(25.97, 16.42) * mm});
            skLineSegment(sketch, "E6566", {"start": v(25.97, 16.42) * mm, "end": v(25.96, 16.4) * mm});
            skLineSegment(sketch, "E6567", {"start": v(25.96, 16.4) * mm, "end": v(25.96, 16.38) * mm});
            skLineSegment(sketch, "E6568", {"start": v(25.96, 16.38) * mm, "end": v(25.96, 16.36) * mm});
            skLineSegment(sketch, "E6569", {"start": v(25.96, 16.36) * mm, "end": v(25.96, 16.35) * mm});
            skLineSegment(sketch, "E6570", {"start": v(25.96, 16.35) * mm, "end": v(25.96, 16.33) * mm});
            skLineSegment(sketch, "E6571", {"start": v(25.96, 16.33) * mm, "end": v(25.96, 16.32) * mm});
            skLineSegment(sketch, "E6572", {"start": v(25.96, 16.32) * mm, "end": v(25.96, 16.31) * mm});
            skLineSegment(sketch, "E6573", {"start": v(25.96, 16.31) * mm, "end": v(25.96, 16.3) * mm});
            skLineSegment(sketch, "E6574", {"start": v(25.96, 16.3) * mm, "end": v(25.96, 16.3) * mm});
            skLineSegment(sketch, "E6575", {"start": v(25.96, 16.3) * mm, "end": v(25.96, 16.28) * mm});
            skLineSegment(sketch, "E6576", {"start": v(25.96, 16.28) * mm, "end": v(25.96, 16.27) * mm});
            skLineSegment(sketch, "E6577", {"start": v(25.96, 16.27) * mm, "end": v(25.96, 16.26) * mm});
            skLineSegment(sketch, "E6578", {"start": v(25.96, 16.26) * mm, "end": v(25.96, 16.25) * mm});
            skLineSegment(sketch, "E6579", {"start": v(25.96, 16.25) * mm, "end": v(25.94, 16.18) * mm});
            skLineSegment(sketch, "E6580", {"start": v(25.94, 16.18) * mm, "end": v(25.92, 16.12) * mm});
            skLineSegment(sketch, "E6581", {"start": v(25.92, 16.12) * mm, "end": v(25.9, 16.05) * mm});
            skLineSegment(sketch, "E6582", {"start": v(25.9, 16.05) * mm, "end": v(25.9, 15.99) * mm});
            skLineSegment(sketch, "E6583", {"start": v(25.9, 15.99) * mm, "end": v(25.87, 15.92) * mm});
            skLineSegment(sketch, "E6584", {"start": v(25.87, 15.92) * mm, "end": v(25.85, 15.86) * mm});
            skLineSegment(sketch, "E6585", {"start": v(25.85, 15.86) * mm, "end": v(25.84, 15.8) * mm});
            skLineSegment(sketch, "E6586", {"start": v(25.84, 15.8) * mm, "end": v(25.81, 15.73) * mm});
            skLineSegment(sketch, "E6587", {"start": v(25.81, 15.73) * mm, "end": v(25.8, 15.7) * mm});
            skLineSegment(sketch, "E6588", {"start": v(25.8, 15.7) * mm, "end": v(25.8, 15.68) * mm});
            skLineSegment(sketch, "E6589", {"start": v(25.8, 15.68) * mm, "end": v(25.79, 15.66) * mm});
            skLineSegment(sketch, "E6590", {"start": v(25.79, 15.66) * mm, "end": v(25.78, 15.64) * mm});
            skLineSegment(sketch, "E6591", {"start": v(25.78, 15.64) * mm, "end": v(25.76, 15.61) * mm});
            skLineSegment(sketch, "E6592", {"start": v(25.76, 15.61) * mm, "end": v(25.75, 15.59) * mm});
            skLineSegment(sketch, "E6593", {"start": v(25.75, 15.59) * mm, "end": v(25.74, 15.56) * mm});
            skLineSegment(sketch, "E6594", {"start": v(25.74, 15.56) * mm, "end": v(25.73, 15.54) * mm});
            skLineSegment(sketch, "E6595", {"start": v(25.73, 15.54) * mm, "end": v(25.72, 15.51) * mm});
            skLineSegment(sketch, "E6596", {"start": v(25.72, 15.51) * mm, "end": v(25.7, 15.49) * mm});
            skLineSegment(sketch, "E6597", {"start": v(25.7, 15.49) * mm, "end": v(25.7, 15.46) * mm});
            skLineSegment(sketch, "E6598", {"start": v(25.7, 15.46) * mm, "end": v(25.68, 15.43) * mm});
            skLineSegment(sketch, "E6599", {"start": v(25.68, 15.43) * mm, "end": v(25.67, 15.4) * mm});
            skLineSegment(sketch, "E6600", {"start": v(25.67, 15.4) * mm, "end": v(25.66, 15.38) * mm});
            skLineSegment(sketch, "E6601", {"start": v(25.66, 15.38) * mm, "end": v(25.64, 15.35) * mm});
            skLineSegment(sketch, "E6602", {"start": v(25.64, 15.35) * mm, "end": v(25.63, 15.32) * mm});
            skLineSegment(sketch, "E6603", {"start": v(25.63, 15.32) * mm, "end": v(25.6, 15.25) * mm});
            skLineSegment(sketch, "E6604", {"start": v(25.6, 15.25) * mm, "end": v(25.56, 15.18) * mm});
            skLineSegment(sketch, "E6605", {"start": v(25.56, 15.18) * mm, "end": v(25.5, 15.12) * mm});
            skLineSegment(sketch, "E6606", {"start": v(25.5, 15.12) * mm, "end": v(25.45, 15.07) * mm});
            skLineSegment(sketch, "E6607", {"start": v(25.45, 15.07) * mm, "end": v(25.38, 15.03) * mm});
            skLineSegment(sketch, "E6608", {"start": v(25.38, 15.03) * mm, "end": v(25.3, 15) * mm});
            skLineSegment(sketch, "E6609", {"start": v(25.3, 15) * mm, "end": v(25.22, 14.99) * mm});
            skLineSegment(sketch, "E6610", {"start": v(25.22, 14.99) * mm, "end": v(25.14, 14.98) * mm});
            skLineSegment(sketch, "E6611", {"start": v(25.14, 14.98) * mm, "end": v(25.1, 14.98) * mm});
            skLineSegment(sketch, "E6612", {"start": v(25.1, 14.98) * mm, "end": v(25.07, 14.98) * mm});
            skLineSegment(sketch, "E6613", {"start": v(25.07, 14.98) * mm, "end": v(25.04, 15) * mm});
            skLineSegment(sketch, "E6614", {"start": v(25.04, 15) * mm, "end": v(25, 15) * mm});
            skLineSegment(sketch, "E6615", {"start": v(25, 15) * mm, "end": v(24.97, 15) * mm});
            skLineSegment(sketch, "E6616", {"start": v(24.97, 15) * mm, "end": v(24.93, 15.02) * mm});
            skLineSegment(sketch, "E6617", {"start": v(24.93, 15.02) * mm, "end": v(24.9, 15.04) * mm});
            skLineSegment(sketch, "E6618", {"start": v(24.9, 15.04) * mm, "end": v(24.87, 15.05) * mm});
            skLineSegment(sketch, "E6619", {"start": v(24.87, 15.05) * mm, "end": v(24.8, 15.1) * mm});
            skLineSegment(sketch, "E6620", {"start": v(24.8, 15.1) * mm, "end": v(24.73, 15.16) * mm});
            skLineSegment(sketch, "E6621", {"start": v(24.73, 15.16) * mm, "end": v(24.68, 15.21) * mm});
            skLineSegment(sketch, "E6622", {"start": v(24.68, 15.21) * mm, "end": v(24.64, 15.27) * mm});
            skLineSegment(sketch, "E6623", {"start": v(24.64, 15.27) * mm, "end": v(24.6, 15.34) * mm});
            skLineSegment(sketch, "E6624", {"start": v(24.6, 15.34) * mm, "end": v(24.59, 15.4) * mm});
            skLineSegment(sketch, "E6625", {"start": v(24.59, 15.4) * mm, "end": v(24.58, 15.48) * mm});
            skLineSegment(sketch, "E6626", {"start": v(24.58, 15.48) * mm, "end": v(24.58, 15.56) * mm});
            skLineSegment(sketch, "E6627", {"start": v(24.58, 15.56) * mm, "end": v(24.58, 15.61) * mm});
            skLineSegment(sketch, "E6628", {"start": v(24.58, 15.61) * mm, "end": v(24.58, 15.66) * mm});
            skLineSegment(sketch, "E6629", {"start": v(24.58, 15.66) * mm, "end": v(24.58, 15.7) * mm});
            skLineSegment(sketch, "E6630", {"start": v(24.58, 15.7) * mm, "end": v(24.57, 15.75) * mm});
            skLineSegment(sketch, "E6631", {"start": v(24.57, 15.75) * mm, "end": v(24.56, 15.8) * mm});
            skLineSegment(sketch, "E6632", {"start": v(24.56, 15.8) * mm, "end": v(24.55, 15.84) * mm});
            skLineSegment(sketch, "E6633", {"start": v(24.55, 15.84) * mm, "end": v(24.54, 15.88) * mm});
            skLineSegment(sketch, "E6634", {"start": v(24.54, 15.88) * mm, "end": v(24.53, 15.92) * mm});
            skLineSegment(sketch, "E6635", {"start": v(24.53, 15.92) * mm, "end": v(24.52, 15.97) * mm});
            skLineSegment(sketch, "E6636", {"start": v(24.52, 15.97) * mm, "end": v(24.5, 16.02) * mm});
            skLineSegment(sketch, "E6637", {"start": v(24.5, 16.02) * mm, "end": v(24.5, 16.07) * mm});
            skLineSegment(sketch, "E6638", {"start": v(21.06, 15.2) * mm, "end": v(21.03, 15.25) * mm});
            skLineSegment(sketch, "E6639", {"start": v(21.03, 15.25) * mm, "end": v(21.01, 15.3) * mm});
            skLineSegment(sketch, "E6640", {"start": v(21.01, 15.3) * mm, "end": v(21, 15.36) * mm});
            skLineSegment(sketch, "E6641", {"start": v(21, 15.36) * mm, "end": v(20.98, 15.43) * mm});
            skLineSegment(sketch, "E6642", {"start": v(20.98, 15.43) * mm, "end": v(20.96, 15.5) * mm});
            skLineSegment(sketch, "E6643", {"start": v(20.96, 15.5) * mm, "end": v(20.94, 15.56) * mm});
            skLineSegment(sketch, "E6644", {"start": v(20.94, 15.56) * mm, "end": v(20.91, 15.62) * mm});
            skLineSegment(sketch, "E6645", {"start": v(20.91, 15.62) * mm, "end": v(20.89, 15.68) * mm});
            skLineSegment(sketch, "E6646", {"start": v(20.89, 15.68) * mm, "end": v(20.86, 15.73) * mm});
            skLineSegment(sketch, "E6647", {"start": v(20.86, 15.73) * mm, "end": v(20.83, 15.78) * mm});
            skLineSegment(sketch, "E6648", {"start": v(20.83, 15.78) * mm, "end": v(20.8, 15.83) * mm});
            skLineSegment(sketch, "E6649", {"start": v(20.8, 15.83) * mm, "end": v(20.77, 15.88) * mm});
            skLineSegment(sketch, "E6650", {"start": v(20.77, 15.88) * mm, "end": v(20.75, 15.93) * mm});
            skLineSegment(sketch, "E6651", {"start": v(20.75, 15.93) * mm, "end": v(20.73, 15.99) * mm});
            skLineSegment(sketch, "E6652", {"start": v(20.73, 15.99) * mm, "end": v(20.72, 16.04) * mm});
            skLineSegment(sketch, "E6653", {"start": v(20.72, 16.04) * mm, "end": v(20.71, 16.1) * mm});
            skLineSegment(sketch, "E6654", {"start": v(20.71, 16.1) * mm, "end": v(20.71, 16.15) * mm});
            skLineSegment(sketch, "E6655", {"start": v(20.71, 16.15) * mm, "end": v(20.71, 16.2) * mm});
            skLineSegment(sketch, "E6656", {"start": v(20.71, 16.2) * mm, "end": v(20.71, 16.27) * mm});
            skLineSegment(sketch, "E6657", {"start": v(20.71, 16.27) * mm, "end": v(20.72, 16.37) * mm});
            skLineSegment(sketch, "E6658", {"start": v(20.72, 16.37) * mm, "end": v(20.72, 16.47) * mm});
            skLineSegment(sketch, "E6659", {"start": v(20.72, 16.47) * mm, "end": v(20.72, 16.57) * mm});
            skLineSegment(sketch, "E6660", {"start": v(20.72, 16.57) * mm, "end": v(20.73, 16.66) * mm});
            skLineSegment(sketch, "E6661", {"start": v(20.73, 16.66) * mm, "end": v(20.74, 16.75) * mm});
            skLineSegment(sketch, "E6662", {"start": v(20.74, 16.75) * mm, "end": v(20.75, 16.84) * mm});
            skLineSegment(sketch, "E6663", {"start": v(20.75, 16.84) * mm, "end": v(20.76, 16.92) * mm});
            skLineSegment(sketch, "E6664", {"start": v(20.76, 16.92) * mm, "end": v(20.77, 17) * mm});
            skLineSegment(sketch, "E6665", {"start": v(20.77, 17) * mm, "end": v(20.78, 17.08) * mm});
            skLineSegment(sketch, "E6666", {"start": v(20.78, 17.08) * mm, "end": v(20.8, 17.16) * mm});
            skLineSegment(sketch, "E6667", {"start": v(20.8, 17.16) * mm, "end": v(20.82, 17.23) * mm});
            skLineSegment(sketch, "E6668", {"start": v(20.82, 17.23) * mm, "end": v(20.85, 17.3) * mm});
            skLineSegment(sketch, "E6669", {"start": v(20.85, 17.3) * mm, "end": v(20.89, 17.35) * mm});
            skLineSegment(sketch, "E6670", {"start": v(20.89, 17.35) * mm, "end": v(20.93, 17.4) * mm});
            skLineSegment(sketch, "E6671", {"start": v(20.93, 17.4) * mm, "end": v(20.97, 17.45) * mm});
            skLineSegment(sketch, "E6672", {"start": v(20.97, 17.45) * mm, "end": v(21.02, 17.49) * mm});
            skLineSegment(sketch, "E6673", {"start": v(21.02, 17.49) * mm, "end": v(21.08, 17.53) * mm});
            skLineSegment(sketch, "E6674", {"start": v(21.08, 17.53) * mm, "end": v(21.14, 17.55) * mm});
            skLineSegment(sketch, "E6675", {"start": v(21.14, 17.55) * mm, "end": v(21.2, 17.56) * mm});
            skLineSegment(sketch, "E6676", {"start": v(21.2, 17.56) * mm, "end": v(21.24, 17.56) * mm});
            skLineSegment(sketch, "E6677", {"start": v(21.24, 17.56) * mm, "end": v(21.3, 17.54) * mm});
            skLineSegment(sketch, "E6678", {"start": v(21.3, 17.54) * mm, "end": v(21.35, 17.5) * mm});
            skLineSegment(sketch, "E6679", {"start": v(21.35, 17.5) * mm, "end": v(21.4, 17.47) * mm});
            skLineSegment(sketch, "E6680", {"start": v(21.4, 17.47) * mm, "end": v(21.45, 17.41) * mm});
            skLineSegment(sketch, "E6681", {"start": v(21.45, 17.41) * mm, "end": v(21.47, 17.39) * mm});
            skLineSegment(sketch, "E6682", {"start": v(21.47, 17.39) * mm, "end": v(21.49, 17.36) * mm});
            skLineSegment(sketch, "E6683", {"start": v(21.49, 17.36) * mm, "end": v(21.5, 17.34) * mm});
            skLineSegment(sketch, "E6684", {"start": v(21.5, 17.34) * mm, "end": v(21.53, 17.31) * mm});
            skLineSegment(sketch, "E6685", {"start": v(21.53, 17.31) * mm, "end": v(21.55, 17.29) * mm});
            skLineSegment(sketch, "E6686", {"start": v(21.55, 17.29) * mm, "end": v(21.58, 17.27) * mm});
            skLineSegment(sketch, "E6687", {"start": v(21.58, 17.27) * mm, "end": v(21.6, 17.24) * mm});
            skLineSegment(sketch, "E6688", {"start": v(21.6, 17.24) * mm, "end": v(21.62, 17.22) * mm});
            skLineSegment(sketch, "E6689", {"start": v(21.62, 17.22) * mm, "end": v(21.64, 17.2) * mm});
            skLineSegment(sketch, "E6690", {"start": v(21.64, 17.2) * mm, "end": v(21.66, 17.18) * mm});
            skLineSegment(sketch, "E6691", {"start": v(21.66, 17.18) * mm, "end": v(21.68, 17.16) * mm});
            skLineSegment(sketch, "E6692", {"start": v(21.68, 17.16) * mm, "end": v(21.7, 17.15) * mm});
            skLineSegment(sketch, "E6693", {"start": v(21.7, 17.15) * mm, "end": v(21.71, 17.13) * mm});
            skLineSegment(sketch, "E6694", {"start": v(21.71, 17.13) * mm, "end": v(21.73, 17.1) * mm});
            skLineSegment(sketch, "E6695", {"start": v(21.73, 17.1) * mm, "end": v(21.75, 17.09) * mm});
            skLineSegment(sketch, "E6696", {"start": v(21.75, 17.09) * mm, "end": v(21.77, 17.07) * mm});
            skLineSegment(sketch, "E6697", {"start": v(21.77, 17.07) * mm, "end": v(21.83, 17) * mm});
            skLineSegment(sketch, "E6698", {"start": v(21.83, 17) * mm, "end": v(21.9, 16.9) * mm});
            skLineSegment(sketch, "E6699", {"start": v(21.9, 16.9) * mm, "end": v(21.95, 16.82) * mm});
            skLineSegment(sketch, "E6700", {"start": v(21.95, 16.82) * mm, "end": v(22, 16.73) * mm});
            skLineSegment(sketch, "E6701", {"start": v(22, 16.73) * mm, "end": v(22.06, 16.64) * mm});
            skLineSegment(sketch, "E6702", {"start": v(22.06, 16.64) * mm, "end": v(22.1, 16.54) * mm});
            skLineSegment(sketch, "E6703", {"start": v(22.1, 16.54) * mm, "end": v(22.13, 16.44) * mm});
            skLineSegment(sketch, "E6704", {"start": v(22.13, 16.44) * mm, "end": v(22.15, 16.33) * mm});
            skLineSegment(sketch, "E6705", {"start": v(22.15, 16.33) * mm, "end": v(22.16, 16.28) * mm});
            skLineSegment(sketch, "E6706", {"start": v(22.16, 16.28) * mm, "end": v(22.17, 16.24) * mm});
            skLineSegment(sketch, "E6707", {"start": v(22.17, 16.24) * mm, "end": v(22.18, 16.19) * mm});
            skLineSegment(sketch, "E6708", {"start": v(22.18, 16.19) * mm, "end": v(22.2, 16.14) * mm});
            skLineSegment(sketch, "E6709", {"start": v(22.2, 16.14) * mm, "end": v(22.2, 16.1) * mm});
            skLineSegment(sketch, "E6710", {"start": v(22.2, 16.1) * mm, "end": v(22.21, 16.05) * mm});
            skLineSegment(sketch, "E6711", {"start": v(22.21, 16.05) * mm, "end": v(22.23, 16) * mm});
            skLineSegment(sketch, "E6712", {"start": v(22.23, 16) * mm, "end": v(22.24, 15.96) * mm});
            skLineSegment(sketch, "E6713", {"start": v(22.24, 15.96) * mm, "end": v(22.25, 15.93) * mm});
            skLineSegment(sketch, "E6714", {"start": v(22.25, 15.93) * mm, "end": v(22.25, 15.9) * mm});
            skLineSegment(sketch, "E6715", {"start": v(22.25, 15.9) * mm, "end": v(22.26, 15.89) * mm});
            skLineSegment(sketch, "E6716", {"start": v(22.26, 15.89) * mm, "end": v(22.27, 15.86) * mm});
            skLineSegment(sketch, "E6717", {"start": v(22.27, 15.86) * mm, "end": v(22.27, 15.84) * mm});
            skLineSegment(sketch, "E6718", {"start": v(22.27, 15.84) * mm, "end": v(22.28, 15.82) * mm});
            skLineSegment(sketch, "E6719", {"start": v(22.28, 15.82) * mm, "end": v(22.28, 15.8) * mm});
            skLineSegment(sketch, "E6720", {"start": v(22.28, 15.8) * mm, "end": v(22.3, 15.77) * mm});
            skLineSegment(sketch, "E6721", {"start": v(22.3, 15.77) * mm, "end": v(22.3, 15.76) * mm});
            skLineSegment(sketch, "E6722", {"start": v(22.3, 15.76) * mm, "end": v(22.3, 15.75) * mm});
            skLineSegment(sketch, "E6723", {"start": v(22.3, 15.75) * mm, "end": v(22.3, 15.74) * mm});
            skLineSegment(sketch, "E6724", {"start": v(22.3, 15.74) * mm, "end": v(22.3, 15.74) * mm});
            skLineSegment(sketch, "E6725", {"start": v(22.3, 15.74) * mm, "end": v(22.3, 15.72) * mm});
            skLineSegment(sketch, "E6726", {"start": v(22.3, 15.72) * mm, "end": v(22.3, 15.7) * mm});
            skLineSegment(sketch, "E6727", {"start": v(22.3, 15.7) * mm, "end": v(22.3, 15.7) * mm});
            skLineSegment(sketch, "E6728", {"start": v(22.3, 15.7) * mm, "end": v(22.3, 15.68) * mm});
            skLineSegment(sketch, "E6729", {"start": v(22.3, 15.68) * mm, "end": v(22.3, 15.66) * mm});
            skLineSegment(sketch, "E6730", {"start": v(22.3, 15.66) * mm, "end": v(22.31, 15.65) * mm});
            skLineSegment(sketch, "E6731", {"start": v(22.31, 15.65) * mm, "end": v(22.31, 15.65) * mm});
            skLineSegment(sketch, "E6732", {"start": v(22.31, 15.65) * mm, "end": v(22.31, 15.64) * mm});
            skLineSegment(sketch, "E6733", {"start": v(22.31, 15.64) * mm, "end": v(22.31, 15.63) * mm});
            skLineSegment(sketch, "E6734", {"start": v(22.31, 15.63) * mm, "end": v(22.31, 15.62) * mm});
            skLineSegment(sketch, "E6735", {"start": v(22.31, 15.62) * mm, "end": v(22.31, 15.61) * mm});
            skLineSegment(sketch, "E6736", {"start": v(22.31, 15.61) * mm, "end": v(22.31, 15.6) * mm});
            skLineSegment(sketch, "E6737", {"start": v(22.31, 15.6) * mm, "end": v(22.31, 15.6) * mm});
            skLineSegment(sketch, "E6738", {"start": v(22.31, 15.6) * mm, "end": v(22.31, 15.58) * mm});
            skLineSegment(sketch, "E6739", {"start": v(22.31, 15.58) * mm, "end": v(22.31, 15.56) * mm});
            skLineSegment(sketch, "E6740", {"start": v(22.31, 15.56) * mm, "end": v(22.3, 15.55) * mm});
            skLineSegment(sketch, "E6741", {"start": v(22.3, 15.55) * mm, "end": v(22.3, 15.53) * mm});
            skLineSegment(sketch, "E6742", {"start": v(22.3, 15.53) * mm, "end": v(22.3, 15.5) * mm});
            skLineSegment(sketch, "E6743", {"start": v(22.3, 15.5) * mm, "end": v(22.3, 15.48) * mm});
            skLineSegment(sketch, "E6744", {"start": v(22.3, 15.48) * mm, "end": v(22.3, 15.44) * mm});
            skLineSegment(sketch, "E6745", {"start": v(22.3, 15.44) * mm, "end": v(22.3, 15.4) * mm});
            skLineSegment(sketch, "E6746", {"start": v(22.3, 15.4) * mm, "end": v(22.29, 15.36) * mm});
            skLineSegment(sketch, "E6747", {"start": v(22.29, 15.36) * mm, "end": v(22.28, 15.31) * mm});
            skLineSegment(sketch, "E6748", {"start": v(22.28, 15.31) * mm, "end": v(22.27, 15.27) * mm});
            skLineSegment(sketch, "E6749", {"start": v(22.27, 15.27) * mm, "end": v(22.27, 15.27) * mm});
            skLineSegment(sketch, "E6750", {"start": v(22.27, 15.27) * mm, "end": v(22.27, 15.26) * mm});
            skLineSegment(sketch, "E6751", {"start": v(22.27, 15.26) * mm, "end": v(22.27, 15.26) * mm});
            skLineSegment(sketch, "E6752", {"start": v(22.27, 15.26) * mm, "end": v(22.27, 15.24) * mm});
            skLineSegment(sketch, "E6753", {"start": v(22.27, 15.24) * mm, "end": v(22.27, 15.22) * mm});
            skLineSegment(sketch, "E6754", {"start": v(22.27, 15.22) * mm, "end": v(22.26, 15.2) * mm});
            skLineSegment(sketch, "E6755", {"start": v(22.26, 15.2) * mm, "end": v(22.26, 15.16) * mm});
            skLineSegment(sketch, "E6756", {"start": v(22.26, 15.16) * mm, "end": v(22.25, 15.11) * mm});
            skLineSegment(sketch, "E6757", {"start": v(22.25, 15.11) * mm, "end": v(22.23, 15.07) * mm});
            skLineSegment(sketch, "E6758", {"start": v(22.23, 15.07) * mm, "end": v(22.2, 15.03) * mm});
            skLineSegment(sketch, "E6759", {"start": v(22.2, 15.03) * mm, "end": v(22.17, 15) * mm});
            skLineSegment(sketch, "E6760", {"start": v(22.17, 15) * mm, "end": v(22.14, 14.96) * mm});
            skLineSegment(sketch, "E6761", {"start": v(22.14, 14.96) * mm, "end": v(22.1, 14.93) * mm});
            skLineSegment(sketch, "E6762", {"start": v(22.1, 14.93) * mm, "end": v(22.06, 14.9) * mm});
            skLineSegment(sketch, "E6763", {"start": v(22.06, 14.9) * mm, "end": v(22.02, 14.87) * mm});
            skLineSegment(sketch, "E6764", {"start": v(22.02, 14.87) * mm, "end": v(22, 14.86) * mm});
            skLineSegment(sketch, "E6765", {"start": v(22, 14.86) * mm, "end": v(21.98, 14.85) * mm});
            skLineSegment(sketch, "E6766", {"start": v(21.98, 14.85) * mm, "end": v(21.96, 14.83) * mm});
            skLineSegment(sketch, "E6767", {"start": v(21.96, 14.83) * mm, "end": v(21.94, 14.82) * mm});
            skLineSegment(sketch, "E6768", {"start": v(21.94, 14.82) * mm, "end": v(21.92, 14.8) * mm});
            skLineSegment(sketch, "E6769", {"start": v(21.92, 14.8) * mm, "end": v(21.9, 14.79) * mm});
            skLineSegment(sketch, "E6770", {"start": v(21.9, 14.79) * mm, "end": v(21.88, 14.77) * mm});
            skLineSegment(sketch, "E6771", {"start": v(21.88, 14.77) * mm, "end": v(21.86, 14.75) * mm});
            skLineSegment(sketch, "E6772", {"start": v(21.86, 14.75) * mm, "end": v(21.85, 14.75) * mm});
            skLineSegment(sketch, "E6773", {"start": v(21.85, 14.75) * mm, "end": v(21.84, 14.74) * mm});
            skLineSegment(sketch, "E6774", {"start": v(21.84, 14.74) * mm, "end": v(21.83, 14.73) * mm});
            skLineSegment(sketch, "E6775", {"start": v(21.83, 14.73) * mm, "end": v(21.82, 14.72) * mm});
            skLineSegment(sketch, "E6776", {"start": v(21.82, 14.72) * mm, "end": v(21.8, 14.71) * mm});
            skLineSegment(sketch, "E6777", {"start": v(21.8, 14.71) * mm, "end": v(21.8, 14.7) * mm});
            skLineSegment(sketch, "E6778", {"start": v(21.8, 14.7) * mm, "end": v(21.79, 14.7) * mm});
            skLineSegment(sketch, "E6779", {"start": v(21.79, 14.7) * mm, "end": v(21.78, 14.7) * mm});
            skLineSegment(sketch, "E6780", {"start": v(21.78, 14.7) * mm, "end": v(21.76, 14.7) * mm});
            skLineSegment(sketch, "E6781", {"start": v(21.76, 14.7) * mm, "end": v(21.75, 14.69) * mm});
            skLineSegment(sketch, "E6782", {"start": v(21.75, 14.69) * mm, "end": v(21.74, 14.69) * mm});
            skLineSegment(sketch, "E6783", {"start": v(21.74, 14.69) * mm, "end": v(21.74, 14.69) * mm});
            skLineSegment(sketch, "E6784", {"start": v(21.74, 14.69) * mm, "end": v(21.73, 14.69) * mm});
            skLineSegment(sketch, "E6785", {"start": v(21.73, 14.69) * mm, "end": v(21.73, 14.68) * mm});
            skLineSegment(sketch, "E6786", {"start": v(21.73, 14.68) * mm, "end": v(21.73, 14.68) * mm});
            skLineSegment(sketch, "E6787", {"start": v(21.73, 14.68) * mm, "end": v(21.7, 14.69) * mm});
            skLineSegment(sketch, "E6788", {"start": v(21.7, 14.69) * mm, "end": v(21.68, 14.7) * mm});
            skLineSegment(sketch, "E6789", {"start": v(21.68, 14.7) * mm, "end": v(21.66, 14.7) * mm});
            skLineSegment(sketch, "E6790", {"start": v(21.66, 14.7) * mm, "end": v(21.63, 14.72) * mm});
            skLineSegment(sketch, "E6791", {"start": v(21.63, 14.72) * mm, "end": v(21.6, 14.73) * mm});
            skLineSegment(sketch, "E6792", {"start": v(21.6, 14.73) * mm, "end": v(21.56, 14.75) * mm});
            skLineSegment(sketch, "E6793", {"start": v(21.56, 14.75) * mm, "end": v(21.53, 14.77) * mm});
            skLineSegment(sketch, "E6794", {"start": v(21.53, 14.77) * mm, "end": v(21.5, 14.8) * mm});
            skLineSegment(sketch, "E6795", {"start": v(21.5, 14.8) * mm, "end": v(21.5, 14.8) * mm});
            skLineSegment(sketch, "E6796", {"start": v(21.5, 14.8) * mm, "end": v(21.49, 14.8) * mm});
            skLineSegment(sketch, "E6797", {"start": v(21.49, 14.8) * mm, "end": v(21.48, 14.8) * mm});
            skLineSegment(sketch, "E6798", {"start": v(21.48, 14.8) * mm, "end": v(21.46, 14.82) * mm});
            skLineSegment(sketch, "E6799", {"start": v(21.46, 14.82) * mm, "end": v(21.44, 14.84) * mm});
            skLineSegment(sketch, "E6800", {"start": v(21.44, 14.84) * mm, "end": v(21.42, 14.86) * mm});
            skLineSegment(sketch, "E6801", {"start": v(21.42, 14.86) * mm, "end": v(21.4, 14.87) * mm});
            skLineSegment(sketch, "E6802", {"start": v(21.4, 14.87) * mm, "end": v(21.38, 14.89) * mm});
            skLineSegment(sketch, "E6803", {"start": v(21.38, 14.89) * mm, "end": v(21.36, 14.9) * mm});
            skLineSegment(sketch, "E6804", {"start": v(21.36, 14.9) * mm, "end": v(21.34, 14.92) * mm});
            skLineSegment(sketch, "E6805", {"start": v(21.34, 14.92) * mm, "end": v(21.32, 14.93) * mm});
            skLineSegment(sketch, "E6806", {"start": v(21.32, 14.93) * mm, "end": v(21.3, 14.95) * mm});
            skLineSegment(sketch, "E6807", {"start": v(21.3, 14.95) * mm, "end": v(21.28, 14.96) * mm});
            skLineSegment(sketch, "E6808", {"start": v(21.28, 14.96) * mm, "end": v(21.26, 14.98) * mm});
            skLineSegment(sketch, "E6809", {"start": v(21.26, 14.98) * mm, "end": v(21.2, 15.02) * mm});
            skLineSegment(sketch, "E6810", {"start": v(21.2, 15.02) * mm, "end": v(21.16, 15.06) * mm});
            skLineSegment(sketch, "E6811", {"start": v(21.16, 15.06) * mm, "end": v(21.12, 15.1) * mm});
            skLineSegment(sketch, "E6812", {"start": v(21.12, 15.1) * mm, "end": v(21.09, 15.15) * mm});
            skLineSegment(sketch, "E6813", {"start": v(21.09, 15.15) * mm, "end": v(21.06, 15.2) * mm});
            skLineSegment(sketch, "E6814", {"start": v(18.69, 12.78) * mm, "end": v(18.66, 12.8) * mm});
            skLineSegment(sketch, "E6815", {"start": v(18.66, 12.8) * mm, "end": v(18.63, 12.8) * mm});
            skLineSegment(sketch, "E6816", {"start": v(18.63, 12.8) * mm, "end": v(18.6, 12.82) * mm});
            skLineSegment(sketch, "E6817", {"start": v(18.6, 12.82) * mm, "end": v(18.58, 12.83) * mm});
            skLineSegment(sketch, "E6818", {"start": v(18.58, 12.83) * mm, "end": v(18.57, 12.84) * mm});
            skLineSegment(sketch, "E6819", {"start": v(18.57, 12.84) * mm, "end": v(18.56, 12.85) * mm});
            skLineSegment(sketch, "E6820", {"start": v(18.56, 12.85) * mm, "end": v(18.53, 12.86) * mm});
            skLineSegment(sketch, "E6821", {"start": v(18.53, 12.86) * mm, "end": v(18.47, 12.91) * mm});
            skLineSegment(sketch, "E6822", {"start": v(18.47, 12.91) * mm, "end": v(18.38, 12.99) * mm});
            skLineSegment(sketch, "E6823", {"start": v(18.38, 12.99) * mm, "end": v(18.26, 13.08) * mm});
            skLineSegment(sketch, "E6824", {"start": v(18.26, 13.08) * mm, "end": v(18.12, 13.2) * mm});
            skLineSegment(sketch, "E6825", {"start": v(18.12, 13.2) * mm, "end": v(17.95, 13.33) * mm});
            skLineSegment(sketch, "E6826", {"start": v(17.95, 13.33) * mm, "end": v(17.77, 13.48) * mm});
            skLineSegment(sketch, "E6827", {"start": v(17.77, 13.48) * mm, "end": v(17.58, 13.63) * mm});
            skLineSegment(sketch, "E6828", {"start": v(17.58, 13.63) * mm, "end": v(17.58, 13.63) * mm});
            skLineSegment(sketch, "E6829", {"start": v(17.58, 13.63) * mm, "end": v(17.58, 13.64) * mm});
            skLineSegment(sketch, "E6830", {"start": v(17.58, 13.64) * mm, "end": v(17.57, 13.66) * mm});
            skLineSegment(sketch, "E6831", {"start": v(17.57, 13.66) * mm, "end": v(17.54, 13.7) * mm});
            skLineSegment(sketch, "E6832", {"start": v(17.54, 13.7) * mm, "end": v(17.5, 13.75) * mm});
            skLineSegment(sketch, "E6833", {"start": v(17.5, 13.75) * mm, "end": v(17.44, 13.83) * mm});
            skLineSegment(sketch, "E6834", {"start": v(17.44, 13.83) * mm, "end": v(17.35, 13.94) * mm});
            skLineSegment(sketch, "E6835", {"start": v(17.35, 13.94) * mm, "end": v(17.23, 14.1) * mm});
            skLineSegment(sketch, "E6836", {"start": v(17.23, 14.1) * mm, "end": v(17.2, 14.13) * mm});
            skLineSegment(sketch, "E6837", {"start": v(17.2, 14.13) * mm, "end": v(17.19, 14.17) * mm});
            skLineSegment(sketch, "E6838", {"start": v(17.19, 14.17) * mm, "end": v(17.17, 14.2) * mm});
            skLineSegment(sketch, "E6839", {"start": v(17.17, 14.2) * mm, "end": v(17.15, 14.24) * mm});
            skLineSegment(sketch, "E6840", {"start": v(17.15, 14.24) * mm, "end": v(17.13, 14.28) * mm});
            skLineSegment(sketch, "E6841", {"start": v(17.13, 14.28) * mm, "end": v(17.12, 14.32) * mm});
            skLineSegment(sketch, "E6842", {"start": v(17.12, 14.32) * mm, "end": v(17.1, 14.36) * mm});
            skLineSegment(sketch, "E6843", {"start": v(17.1, 14.36) * mm, "end": v(17.1, 14.4) * mm});
            skLineSegment(sketch, "E6844", {"start": v(17.1, 14.4) * mm, "end": v(17.08, 14.44) * mm});
            skLineSegment(sketch, "E6845", {"start": v(17.08, 14.44) * mm, "end": v(17.07, 14.47) * mm});
            skLineSegment(sketch, "E6846", {"start": v(17.07, 14.47) * mm, "end": v(17.06, 14.5) * mm});
            skLineSegment(sketch, "E6847", {"start": v(17.06, 14.5) * mm, "end": v(17.06, 14.51) * mm});
            skLineSegment(sketch, "E6848", {"start": v(17.06, 14.51) * mm, "end": v(17.05, 14.52) * mm});
            skLineSegment(sketch, "E6849", {"start": v(17.05, 14.52) * mm, "end": v(17.05, 14.53) * mm});
            skLineSegment(sketch, "E6850", {"start": v(17.05, 14.53) * mm, "end": v(17.05, 14.53) * mm});
            skLineSegment(sketch, "E6851", {"start": v(17.05, 14.53) * mm, "end": v(17.04, 14.6) * mm});
            skLineSegment(sketch, "E6852", {"start": v(17.04, 14.6) * mm, "end": v(17.02, 14.65) * mm});
            skLineSegment(sketch, "E6853", {"start": v(17.02, 14.65) * mm, "end": v(17, 14.7) * mm});
            skLineSegment(sketch, "E6854", {"start": v(17, 14.7) * mm, "end": v(17, 14.75) * mm});
            skLineSegment(sketch, "E6855", {"start": v(17, 14.75) * mm, "end": v(16.98, 14.8) * mm});
            skLineSegment(sketch, "E6856", {"start": v(16.98, 14.8) * mm, "end": v(16.97, 14.84) * mm});
            skLineSegment(sketch, "E6857", {"start": v(16.97, 14.84) * mm, "end": v(16.97, 14.87) * mm});
            skLineSegment(sketch, "E6858", {"start": v(16.97, 14.87) * mm, "end": v(16.96, 14.89) * mm});
            skLineSegment(sketch, "E6859", {"start": v(16.96, 14.89) * mm, "end": v(16.96, 14.9) * mm});
            skLineSegment(sketch, "E6860", {"start": v(16.96, 14.9) * mm, "end": v(16.95, 14.92) * mm});
            skLineSegment(sketch, "E6861", {"start": v(16.95, 14.92) * mm, "end": v(16.95, 14.93) * mm});
            skLineSegment(sketch, "E6862", {"start": v(16.95, 14.93) * mm, "end": v(16.95, 14.94) * mm});
            skLineSegment(sketch, "E6863", {"start": v(16.95, 14.94) * mm, "end": v(16.95, 14.95) * mm});
            skLineSegment(sketch, "E6864", {"start": v(16.95, 14.95) * mm, "end": v(16.94, 14.96) * mm});
            skLineSegment(sketch, "E6865", {"start": v(16.94, 14.96) * mm, "end": v(16.94, 14.97) * mm});
            skLineSegment(sketch, "E6866", {"start": v(16.94, 14.97) * mm, "end": v(16.94, 14.97) * mm});
            skLineSegment(sketch, "E6867", {"start": v(16.94, 14.97) * mm, "end": v(16.94, 14.98) * mm});
            skLineSegment(sketch, "E6868", {"start": v(16.94, 14.98) * mm, "end": v(16.94, 15) * mm});
            skLineSegment(sketch, "E6869", {"start": v(16.94, 15) * mm, "end": v(16.94, 15) * mm});
            skLineSegment(sketch, "E6870", {"start": v(16.94, 15) * mm, "end": v(16.94, 15.02) * mm});
            skLineSegment(sketch, "E6871", {"start": v(16.94, 15.02) * mm, "end": v(16.94, 15.04) * mm});
            skLineSegment(sketch, "E6872", {"start": v(16.94, 15.04) * mm, "end": v(16.94, 15.06) * mm});
            skLineSegment(sketch, "E6873", {"start": v(16.94, 15.06) * mm, "end": v(16.95, 15.08) * mm});
            skLineSegment(sketch, "E6874", {"start": v(16.95, 15.08) * mm, "end": v(16.95, 15.1) * mm});
            skLineSegment(sketch, "E6875", {"start": v(16.95, 15.1) * mm, "end": v(16.95, 15.1) * mm});
            skLineSegment(sketch, "E6876", {"start": v(16.95, 15.1) * mm, "end": v(16.96, 15.1) * mm});
            skLineSegment(sketch, "E6877", {"start": v(16.96, 15.1) * mm, "end": v(16.96, 15.11) * mm});
            skLineSegment(sketch, "E6878", {"start": v(16.96, 15.11) * mm, "end": v(16.97, 15.12) * mm});
            skLineSegment(sketch, "E6879", {"start": v(16.97, 15.12) * mm, "end": v(16.98, 15.13) * mm});
            skLineSegment(sketch, "E6880", {"start": v(16.98, 15.13) * mm, "end": v(17, 15.14) * mm});
            skLineSegment(sketch, "E6881", {"start": v(17, 15.14) * mm, "end": v(17, 15.14) * mm});
            skLineSegment(sketch, "E6882", {"start": v(17, 15.14) * mm, "end": v(17.02, 15.15) * mm});
            skLineSegment(sketch, "E6883", {"start": v(17.02, 15.15) * mm, "end": v(17.04, 15.15) * mm});
            skLineSegment(sketch, "E6884", {"start": v(17.04, 15.15) * mm, "end": v(17.05, 15.15) * mm});
            skLineSegment(sketch, "E6885", {"start": v(17.05, 15.15) * mm, "end": v(17.07, 15.15) * mm});
            skLineSegment(sketch, "E6886", {"start": v(17.07, 15.15) * mm, "end": v(17.08, 15.15) * mm});
            skLineSegment(sketch, "E6887", {"start": v(17.08, 15.15) * mm, "end": v(17.09, 15.15) * mm});
            skLineSegment(sketch, "E6888", {"start": v(17.09, 15.15) * mm, "end": v(17.1, 15.15) * mm});
            skLineSegment(sketch, "E6889", {"start": v(17.1, 15.15) * mm, "end": v(17.1, 15.15) * mm});
            skLineSegment(sketch, "E6890", {"start": v(17.1, 15.15) * mm, "end": v(17.11, 15.15) * mm});
            skLineSegment(sketch, "E6891", {"start": v(17.11, 15.15) * mm, "end": v(17.12, 15.15) * mm});
            skLineSegment(sketch, "E6892", {"start": v(17.12, 15.15) * mm, "end": v(17.13, 15.15) * mm});
            skLineSegment(sketch, "E6893", {"start": v(17.13, 15.15) * mm, "end": v(17.16, 15.15) * mm});
            skLineSegment(sketch, "E6894", {"start": v(17.16, 15.15) * mm, "end": v(17.2, 15.14) * mm});
            skLineSegment(sketch, "E6895", {"start": v(17.2, 15.14) * mm, "end": v(17.23, 15.14) * mm});
            skLineSegment(sketch, "E6896", {"start": v(17.23, 15.14) * mm, "end": v(17.27, 15.13) * mm});
            skLineSegment(sketch, "E6897", {"start": v(17.27, 15.13) * mm, "end": v(17.3, 15.13) * mm});
            skLineSegment(sketch, "E6898", {"start": v(17.3, 15.13) * mm, "end": v(17.34, 15.12) * mm});
            skLineSegment(sketch, "E6899", {"start": v(17.34, 15.12) * mm, "end": v(17.38, 15.12) * mm});
            skLineSegment(sketch, "E6900", {"start": v(17.38, 15.12) * mm, "end": v(17.41, 15.12) * mm});
            skLineSegment(sketch, "E6901", {"start": v(17.41, 15.12) * mm, "end": v(17.48, 15.1) * mm});
            skLineSegment(sketch, "E6902", {"start": v(17.48, 15.1) * mm, "end": v(17.56, 15.1) * mm});
            skLineSegment(sketch, "E6903", {"start": v(17.56, 15.1) * mm, "end": v(17.63, 15.1) * mm});
            skLineSegment(sketch, "E6904", {"start": v(17.63, 15.1) * mm, "end": v(17.7, 15.08) * mm});
            skLineSegment(sketch, "E6905", {"start": v(17.7, 15.08) * mm, "end": v(17.77, 15.07) * mm});
            skLineSegment(sketch, "E6906", {"start": v(17.77, 15.07) * mm, "end": v(17.84, 15.06) * mm});
            skLineSegment(sketch, "E6907", {"start": v(17.84, 15.06) * mm, "end": v(17.91, 15.04) * mm});
            skLineSegment(sketch, "E6908", {"start": v(17.91, 15.04) * mm, "end": v(17.98, 15.03) * mm});
            skLineSegment(sketch, "E6909", {"start": v(17.98, 15.03) * mm, "end": v(18.05, 15) * mm});
            skLineSegment(sketch, "E6910", {"start": v(18.05, 15) * mm, "end": v(18.12, 14.98) * mm});
            skLineSegment(sketch, "E6911", {"start": v(18.12, 14.98) * mm, "end": v(18.2, 14.95) * mm});
            skLineSegment(sketch, "E6912", {"start": v(18.2, 14.95) * mm, "end": v(18.26, 14.91) * mm});
            skLineSegment(sketch, "E6913", {"start": v(18.26, 14.91) * mm, "end": v(18.32, 14.87) * mm});
            skLineSegment(sketch, "E6914", {"start": v(18.32, 14.87) * mm, "end": v(18.38, 14.84) * mm});
            skLineSegment(sketch, "E6915", {"start": v(18.38, 14.84) * mm, "end": v(18.44, 14.8) * mm});
            skLineSegment(sketch, "E6916", {"start": v(18.44, 14.8) * mm, "end": v(18.5, 14.76) * mm});
            skLineSegment(sketch, "E6917", {"start": v(18.5, 14.76) * mm, "end": v(18.58, 14.7) * mm});
            skLineSegment(sketch, "E6918", {"start": v(18.58, 14.7) * mm, "end": v(18.64, 14.65) * mm});
            skLineSegment(sketch, "E6919", {"start": v(18.64, 14.65) * mm, "end": v(18.7, 14.62) * mm});
            skLineSegment(sketch, "E6920", {"start": v(18.7, 14.62) * mm, "end": v(18.72, 14.6) * mm});
            skLineSegment(sketch, "E6921", {"start": v(18.72, 14.6) * mm, "end": v(18.74, 14.58) * mm});
            skLineSegment(sketch, "E6922", {"start": v(18.74, 14.58) * mm, "end": v(18.75, 14.58) * mm});
            skLineSegment(sketch, "E6923", {"start": v(18.75, 14.58) * mm, "end": v(18.76, 14.57) * mm});
            skLineSegment(sketch, "E6924", {"start": v(18.76, 14.57) * mm, "end": v(18.76, 14.57) * mm});
            skLineSegment(sketch, "E6925", {"start": v(18.76, 14.57) * mm, "end": v(18.84, 14.45) * mm});
            skLineSegment(sketch, "E6926", {"start": v(18.84, 14.45) * mm, "end": v(18.93, 14.33) * mm});
            skLineSegment(sketch, "E6927", {"start": v(18.93, 14.33) * mm, "end": v(19, 14.22) * mm});
            skLineSegment(sketch, "E6928", {"start": v(19, 14.22) * mm, "end": v(19.07, 14.13) * mm});
            skLineSegment(sketch, "E6929", {"start": v(19.07, 14.13) * mm, "end": v(19.12, 14.05) * mm});
            skLineSegment(sketch, "E6930", {"start": v(19.12, 14.05) * mm, "end": v(19.17, 13.98) * mm});
            skLineSegment(sketch, "E6931", {"start": v(19.17, 13.98) * mm, "end": v(19.2, 13.94) * mm});
            skLineSegment(sketch, "E6932", {"start": v(19.2, 13.94) * mm, "end": v(19.2, 13.92) * mm});
            skLineSegment(sketch, "E6933", {"start": v(19.2, 13.92) * mm, "end": v(19.21, 13.91) * mm});
            skLineSegment(sketch, "E6934", {"start": v(19.21, 13.91) * mm, "end": v(19.23, 13.9) * mm});
            skLineSegment(sketch, "E6935", {"start": v(19.23, 13.9) * mm, "end": v(19.24, 13.86) * mm});
            skLineSegment(sketch, "E6936", {"start": v(19.24, 13.86) * mm, "end": v(19.26, 13.83) * mm});
            skLineSegment(sketch, "E6937", {"start": v(19.26, 13.83) * mm, "end": v(19.29, 13.79) * mm});
            skLineSegment(sketch, "E6938", {"start": v(19.29, 13.79) * mm, "end": v(19.31, 13.75) * mm});
            skLineSegment(sketch, "E6939", {"start": v(19.31, 13.75) * mm, "end": v(19.34, 13.7) * mm});
            skLineSegment(sketch, "E6940", {"start": v(19.34, 13.7) * mm, "end": v(19.37, 13.65) * mm});
            skLineSegment(sketch, "E6941", {"start": v(19.37, 13.65) * mm, "end": v(19.37, 13.65) * mm});
            skLineSegment(sketch, "E6942", {"start": v(19.37, 13.65) * mm, "end": v(19.37, 13.64) * mm});
            skLineSegment(sketch, "E6943", {"start": v(19.37, 13.64) * mm, "end": v(19.37, 13.63) * mm});
            skLineSegment(sketch, "E6944", {"start": v(19.37, 13.63) * mm, "end": v(19.37, 13.62) * mm});
            skLineSegment(sketch, "E6945", {"start": v(19.37, 13.62) * mm, "end": v(19.38, 13.6) * mm});
            skLineSegment(sketch, "E6946", {"start": v(19.38, 13.6) * mm, "end": v(19.39, 13.56) * mm});
            skLineSegment(sketch, "E6947", {"start": v(19.39, 13.56) * mm, "end": v(19.4, 13.51) * mm});
            skLineSegment(sketch, "E6948", {"start": v(19.4, 13.51) * mm, "end": v(19.4, 13.44) * mm});
            skLineSegment(sketch, "E6949", {"start": v(19.4, 13.44) * mm, "end": v(19.4, 13.37) * mm});
            skLineSegment(sketch, "E6950", {"start": v(19.4, 13.37) * mm, "end": v(19.4, 13.3) * mm});
            skLineSegment(sketch, "E6951", {"start": v(19.4, 13.3) * mm, "end": v(19.38, 13.22) * mm});
            skLineSegment(sketch, "E6952", {"start": v(19.38, 13.22) * mm, "end": v(19.36, 13.15) * mm});
            skLineSegment(sketch, "E6953", {"start": v(19.36, 13.15) * mm, "end": v(19.33, 13.08) * mm});
            skLineSegment(sketch, "E6954", {"start": v(19.33, 13.08) * mm, "end": v(19.3, 13.02) * mm});
            skLineSegment(sketch, "E6955", {"start": v(19.3, 13.02) * mm, "end": v(19.25, 12.96) * mm});
            skLineSegment(sketch, "E6956", {"start": v(19.25, 12.96) * mm, "end": v(19.2, 12.91) * mm});
            skLineSegment(sketch, "E6957", {"start": v(19.2, 12.91) * mm, "end": v(19.16, 12.87) * mm});
            skLineSegment(sketch, "E6958", {"start": v(19.16, 12.87) * mm, "end": v(19.1, 12.83) * mm});
            skLineSegment(sketch, "E6959", {"start": v(19.1, 12.83) * mm, "end": v(19.05, 12.8) * mm});
            skLineSegment(sketch, "E6960", {"start": v(19.05, 12.8) * mm, "end": v(19, 12.78) * mm});
            skLineSegment(sketch, "E6961", {"start": v(19, 12.78) * mm, "end": v(18.94, 12.76) * mm});
            skLineSegment(sketch, "E6962", {"start": v(18.94, 12.76) * mm, "end": v(18.88, 12.74) * mm});
            skLineSegment(sketch, "E6963", {"start": v(18.88, 12.74) * mm, "end": v(18.82, 12.74) * mm});
            skLineSegment(sketch, "E6964", {"start": v(18.82, 12.74) * mm, "end": v(18.8, 12.74) * mm});
            skLineSegment(sketch, "E6965", {"start": v(18.8, 12.74) * mm, "end": v(18.78, 12.74) * mm});
            skLineSegment(sketch, "E6966", {"start": v(18.78, 12.74) * mm, "end": v(18.77, 12.74) * mm});
            skLineSegment(sketch, "E6967", {"start": v(18.77, 12.74) * mm, "end": v(18.76, 12.74) * mm});
            skLineSegment(sketch, "E6968", {"start": v(18.76, 12.74) * mm, "end": v(18.76, 12.74) * mm});
            skLineSegment(sketch, "E6969", {"start": v(18.76, 12.74) * mm, "end": v(18.75, 12.74) * mm});
            skLineSegment(sketch, "E6970", {"start": v(18.75, 12.74) * mm, "end": v(18.75, 12.74) * mm});
            skLineSegment(sketch, "E6971", {"start": v(18.75, 12.74) * mm, "end": v(18.72, 12.76) * mm});
            skLineSegment(sketch, "E6972", {"start": v(18.72, 12.76) * mm, "end": v(18.69, 12.78) * mm});
            skLineSegment(sketch, "E6973", {"start": v(19.84, 4.31) * mm, "end": v(19.83, 4.22) * mm});
            skLineSegment(sketch, "E6974", {"start": v(19.83, 4.22) * mm, "end": v(19.8, 4.1) * mm});
            skLineSegment(sketch, "E6975", {"start": v(19.8, 4.1) * mm, "end": v(19.78, 3.99) * mm});
            skLineSegment(sketch, "E6976", {"start": v(19.78, 3.99) * mm, "end": v(19.75, 3.87) * mm});
            skLineSegment(sketch, "E6977", {"start": v(19.75, 3.87) * mm, "end": v(19.7, 3.75) * mm});
            skLineSegment(sketch, "E6978", {"start": v(19.7, 3.75) * mm, "end": v(19.63, 3.64) * mm});
            skLineSegment(sketch, "E6979", {"start": v(19.63, 3.64) * mm, "end": v(19.55, 3.53) * mm});
            skLineSegment(sketch, "E6980", {"start": v(19.55, 3.53) * mm, "end": v(19.46, 3.42) * mm});
            skLineSegment(sketch, "E6981", {"start": v(19.46, 3.42) * mm, "end": v(19.36, 3.32) * mm});
            skLineSegment(sketch, "E6982", {"start": v(19.36, 3.32) * mm, "end": v(19.24, 3.22) * mm});
            skLineSegment(sketch, "E6983", {"start": v(19.24, 3.22) * mm, "end": v(19.21, 3.2) * mm});
            skLineSegment(sketch, "E6984", {"start": v(19.21, 3.2) * mm, "end": v(19.19, 3.17) * mm});
            skLineSegment(sketch, "E6985", {"start": v(19.19, 3.17) * mm, "end": v(19.16, 3.14) * mm});
            skLineSegment(sketch, "E6986", {"start": v(19.16, 3.14) * mm, "end": v(19.13, 3.12) * mm});
            skLineSegment(sketch, "E6987", {"start": v(19.13, 3.12) * mm, "end": v(19.1, 3.1) * mm});
            skLineSegment(sketch, "E6988", {"start": v(19.1, 3.1) * mm, "end": v(19.07, 3.07) * mm});
            skLineSegment(sketch, "E6989", {"start": v(19.07, 3.07) * mm, "end": v(19.04, 3.05) * mm});
            skLineSegment(sketch, "E6990", {"start": v(19.04, 3.05) * mm, "end": v(19.01, 3.02) * mm});
            skLineSegment(sketch, "E6991", {"start": v(19.01, 3.02) * mm, "end": v(18.96, 2.98) * mm});
            skLineSegment(sketch, "E6992", {"start": v(18.96, 2.98) * mm, "end": v(18.91, 2.93) * mm});
            skLineSegment(sketch, "E6993", {"start": v(18.91, 2.93) * mm, "end": v(18.86, 2.89) * mm});
            skLineSegment(sketch, "E6994", {"start": v(18.86, 2.89) * mm, "end": v(18.8, 2.84) * mm});
            skLineSegment(sketch, "E6995", {"start": v(18.8, 2.84) * mm, "end": v(18.75, 2.8) * mm});
            skLineSegment(sketch, "E6996", {"start": v(18.75, 2.8) * mm, "end": v(18.7, 2.76) * mm});
            skLineSegment(sketch, "E6997", {"start": v(18.7, 2.76) * mm, "end": v(18.65, 2.72) * mm});
            skLineSegment(sketch, "E6998", {"start": v(18.65, 2.72) * mm, "end": v(18.6, 2.68) * mm});
            skLineSegment(sketch, "E6999", {"start": v(18.6, 2.68) * mm, "end": v(18.56, 2.66) * mm});
            skLineSegment(sketch, "E7000", {"start": v(18.56, 2.66) * mm, "end": v(18.53, 2.64) * mm});
            skLineSegment(sketch, "E7001", {"start": v(18.53, 2.64) * mm, "end": v(18.5, 2.62) * mm});
            skLineSegment(sketch, "E7002", {"start": v(18.5, 2.62) * mm, "end": v(18.45, 2.6) * mm});
            skLineSegment(sketch, "E7003", {"start": v(18.45, 2.6) * mm, "end": v(18.42, 2.6) * mm});
            skLineSegment(sketch, "E7004", {"start": v(18.42, 2.6) * mm, "end": v(18.38, 2.58) * mm});
            skLineSegment(sketch, "E7005", {"start": v(18.38, 2.58) * mm, "end": v(18.34, 2.56) * mm});
            skLineSegment(sketch, "E7006", {"start": v(18.34, 2.56) * mm, "end": v(18.3, 2.55) * mm});
            skLineSegment(sketch, "E7007", {"start": v(18.3, 2.55) * mm, "end": v(18.28, 2.55) * mm});
            skLineSegment(sketch, "E7008", {"start": v(18.28, 2.55) * mm, "end": v(18.27, 2.54) * mm});
            skLineSegment(sketch, "E7009", {"start": v(18.27, 2.54) * mm, "end": v(18.26, 2.54) * mm});
            skLineSegment(sketch, "E7010", {"start": v(18.26, 2.54) * mm, "end": v(18.25, 2.54) * mm});
            skLineSegment(sketch, "E7011", {"start": v(18.25, 2.54) * mm, "end": v(18.25, 2.54) * mm});
            skLineSegment(sketch, "E7012", {"start": v(18.25, 2.54) * mm, "end": v(18.23, 2.53) * mm});
            skLineSegment(sketch, "E7013", {"start": v(18.23, 2.53) * mm, "end": v(18.2, 2.52) * mm});
            skLineSegment(sketch, "E7014", {"start": v(18.2, 2.52) * mm, "end": v(18.19, 2.51) * mm});
            skLineSegment(sketch, "E7015", {"start": v(18.19, 2.51) * mm, "end": v(18.17, 2.5) * mm});
            skLineSegment(sketch, "E7016", {"start": v(18.17, 2.5) * mm, "end": v(18.15, 2.5) * mm});
            skLineSegment(sketch, "E7017", {"start": v(18.15, 2.5) * mm, "end": v(18.14, 2.5) * mm});
            skLineSegment(sketch, "E7018", {"start": v(18.14, 2.5) * mm, "end": v(18.13, 2.5) * mm});
            skLineSegment(sketch, "E7019", {"start": v(18.13, 2.5) * mm, "end": v(18.12, 2.49) * mm});
            skLineSegment(sketch, "E7020", {"start": v(18.12, 2.49) * mm, "end": v(18.1, 2.48) * mm});
            skLineSegment(sketch, "E7021", {"start": v(18.1, 2.48) * mm, "end": v(18.1, 2.48) * mm});
            skLineSegment(sketch, "E7022", {"start": v(18.1, 2.48) * mm, "end": v(18.08, 2.47) * mm});
            skLineSegment(sketch, "E7023", {"start": v(18.08, 2.47) * mm, "end": v(18.06, 2.46) * mm});
            skLineSegment(sketch, "E7024", {"start": v(18.06, 2.46) * mm, "end": v(18.03, 2.45) * mm});
            skLineSegment(sketch, "E7025", {"start": v(18.03, 2.45) * mm, "end": v(18, 2.44) * mm});
            skLineSegment(sketch, "E7026", {"start": v(18, 2.44) * mm, "end": v(17.98, 2.43) * mm});
            skLineSegment(sketch, "E7027", {"start": v(17.98, 2.43) * mm, "end": v(17.96, 2.42) * mm});
            skLineSegment(sketch, "E7028", {"start": v(17.96, 2.42) * mm, "end": v(17.96, 2.42) * mm});
            skLineSegment(sketch, "E7029", {"start": v(17.96, 2.42) * mm, "end": v(17.95, 2.42) * mm});
            skLineSegment(sketch, "E7030", {"start": v(17.95, 2.42) * mm, "end": v(17.95, 2.42) * mm});
            skLineSegment(sketch, "E7031", {"start": v(17.95, 2.42) * mm, "end": v(17.94, 2.42) * mm});
            skLineSegment(sketch, "E7032", {"start": v(17.94, 2.42) * mm, "end": v(17.93, 2.42) * mm});
            skLineSegment(sketch, "E7033", {"start": v(17.93, 2.42) * mm, "end": v(17.92, 2.42) * mm});
            skLineSegment(sketch, "E7034", {"start": v(17.92, 2.42) * mm, "end": v(17.9, 2.41) * mm});
            skLineSegment(sketch, "E7035", {"start": v(17.9, 2.41) * mm, "end": v(17.85, 2.4) * mm});
            skLineSegment(sketch, "E7036", {"start": v(17.85, 2.4) * mm, "end": v(17.8, 2.41) * mm});
            skLineSegment(sketch, "E7037", {"start": v(17.8, 2.41) * mm, "end": v(17.75, 2.42) * mm});
            skLineSegment(sketch, "E7038", {"start": v(17.75, 2.42) * mm, "end": v(17.71, 2.43) * mm});
            skLineSegment(sketch, "E7039", {"start": v(17.71, 2.43) * mm, "end": v(17.68, 2.46) * mm});
            skLineSegment(sketch, "E7040", {"start": v(17.68, 2.46) * mm, "end": v(17.65, 2.49) * mm});
            skLineSegment(sketch, "E7041", {"start": v(17.65, 2.49) * mm, "end": v(17.63, 2.52) * mm});
            skLineSegment(sketch, "E7042", {"start": v(17.63, 2.52) * mm, "end": v(17.6, 2.57) * mm});
            skLineSegment(sketch, "E7043", {"start": v(17.6, 2.57) * mm, "end": v(17.6, 2.58) * mm});
            skLineSegment(sketch, "E7044", {"start": v(17.6, 2.58) * mm, "end": v(17.6, 2.58) * mm});
            skLineSegment(sketch, "E7045", {"start": v(17.6, 2.58) * mm, "end": v(17.6, 2.59) * mm});
            skLineSegment(sketch, "E7046", {"start": v(17.6, 2.59) * mm, "end": v(17.6, 2.59) * mm});
            skLineSegment(sketch, "E7047", {"start": v(17.6, 2.59) * mm, "end": v(17.6, 2.6) * mm});
            skLineSegment(sketch, "E7048", {"start": v(17.6, 2.6) * mm, "end": v(17.6, 2.6) * mm});
            skLineSegment(sketch, "E7049", {"start": v(17.6, 2.6) * mm, "end": v(17.59, 2.62) * mm});
            skLineSegment(sketch, "E7050", {"start": v(17.59, 2.62) * mm, "end": v(17.59, 2.63) * mm});
            skLineSegment(sketch, "E7051", {"start": v(17.59, 2.63) * mm, "end": v(17.58, 2.65) * mm});
            skLineSegment(sketch, "E7052", {"start": v(17.58, 2.65) * mm, "end": v(17.59, 2.66) * mm});
            skLineSegment(sketch, "E7053", {"start": v(17.59, 2.66) * mm, "end": v(17.59, 2.67) * mm});
            skLineSegment(sketch, "E7054", {"start": v(17.59, 2.67) * mm, "end": v(17.59, 2.68) * mm});
            skLineSegment(sketch, "E7055", {"start": v(17.59, 2.68) * mm, "end": v(17.6, 2.7) * mm});
            skLineSegment(sketch, "E7056", {"start": v(17.6, 2.7) * mm, "end": v(17.6, 2.72) * mm});
            skLineSegment(sketch, "E7057", {"start": v(17.6, 2.72) * mm, "end": v(17.61, 2.75) * mm});
            skLineSegment(sketch, "E7058", {"start": v(17.61, 2.75) * mm, "end": v(17.62, 2.79) * mm});
            skLineSegment(sketch, "E7059", {"start": v(17.62, 2.79) * mm, "end": v(17.63, 2.83) * mm});
            skLineSegment(sketch, "E7060", {"start": v(17.63, 2.83) * mm, "end": v(17.65, 2.87) * mm});
            skLineSegment(sketch, "E7061", {"start": v(17.65, 2.87) * mm, "end": v(17.66, 2.92) * mm});
            skLineSegment(sketch, "E7062", {"start": v(17.66, 2.92) * mm, "end": v(17.68, 2.96) * mm});
            skLineSegment(sketch, "E7063", {"start": v(17.68, 2.96) * mm, "end": v(17.68, 2.96) * mm});
            skLineSegment(sketch, "E7064", {"start": v(17.68, 2.96) * mm, "end": v(17.68, 2.97) * mm});
            skLineSegment(sketch, "E7065", {"start": v(17.68, 2.97) * mm, "end": v(17.68, 2.98) * mm});
            skLineSegment(sketch, "E7066", {"start": v(17.68, 2.98) * mm, "end": v(17.69, 2.99) * mm});
            skLineSegment(sketch, "E7067", {"start": v(17.69, 2.99) * mm, "end": v(17.7, 3) * mm});
            skLineSegment(sketch, "E7068", {"start": v(17.7, 3) * mm, "end": v(17.7, 3.04) * mm});
            skLineSegment(sketch, "E7069", {"start": v(17.7, 3.04) * mm, "end": v(17.71, 3.07) * mm});
            skLineSegment(sketch, "E7070", {"start": v(17.71, 3.07) * mm, "end": v(17.76, 3.22) * mm});
            skLineSegment(sketch, "E7071", {"start": v(17.76, 3.22) * mm, "end": v(17.81, 3.36) * mm});
            skLineSegment(sketch, "E7072", {"start": v(17.81, 3.36) * mm, "end": v(17.87, 3.5) * mm});
            skLineSegment(sketch, "E7073", {"start": v(17.87, 3.5) * mm, "end": v(17.93, 3.62) * mm});
            skLineSegment(sketch, "E7074", {"start": v(17.93, 3.62) * mm, "end": v(18, 3.73) * mm});
            skLineSegment(sketch, "E7075", {"start": v(18, 3.73) * mm, "end": v(18.07, 3.83) * mm});
            skLineSegment(sketch, "E7076", {"start": v(18.07, 3.83) * mm, "end": v(18.14, 3.93) * mm});
            skLineSegment(sketch, "E7077", {"start": v(18.14, 3.93) * mm, "end": v(18.22, 4.01) * mm});
            skLineSegment(sketch, "E7078", {"start": v(18.22, 4.01) * mm, "end": v(18.32, 4.12) * mm});
            skLineSegment(sketch, "E7079", {"start": v(18.32, 4.12) * mm, "end": v(18.43, 4.23) * mm});
            skLineSegment(sketch, "E7080", {"start": v(18.43, 4.23) * mm, "end": v(18.54, 4.33) * mm});
            skLineSegment(sketch, "E7081", {"start": v(18.54, 4.33) * mm, "end": v(18.66, 4.42) * mm});
            skLineSegment(sketch, "E7082", {"start": v(18.66, 4.42) * mm, "end": v(18.77, 4.51) * mm});
            skLineSegment(sketch, "E7083", {"start": v(18.77, 4.51) * mm, "end": v(18.9, 4.59) * mm});
            skLineSegment(sketch, "E7084", {"start": v(18.9, 4.59) * mm, "end": v(19.02, 4.66) * mm});
            skLineSegment(sketch, "E7085", {"start": v(19.02, 4.66) * mm, "end": v(19.15, 4.72) * mm});
            skLineSegment(sketch, "E7086", {"start": v(19.15, 4.72) * mm, "end": v(19.17, 4.73) * mm});
            skLineSegment(sketch, "E7087", {"start": v(19.17, 4.73) * mm, "end": v(19.18, 4.73) * mm});
            skLineSegment(sketch, "E7088", {"start": v(19.18, 4.73) * mm, "end": v(19.18, 4.73) * mm});
            skLineSegment(sketch, "E7089", {"start": v(19.18, 4.73) * mm, "end": v(19.19, 4.73) * mm});
            skLineSegment(sketch, "E7090", {"start": v(19.19, 4.73) * mm, "end": v(19.2, 4.73) * mm});
            skLineSegment(sketch, "E7091", {"start": v(19.2, 4.73) * mm, "end": v(19.2, 4.74) * mm});
            skLineSegment(sketch, "E7092", {"start": v(19.2, 4.74) * mm, "end": v(19.2, 4.74) * mm});
            skLineSegment(sketch, "E7093", {"start": v(19.2, 4.74) * mm, "end": v(19.22, 4.73) * mm});
            skLineSegment(sketch, "E7094", {"start": v(19.22, 4.73) * mm, "end": v(19.25, 4.72) * mm});
            skLineSegment(sketch, "E7095", {"start": v(19.25, 4.72) * mm, "end": v(19.28, 4.72) * mm});
            skLineSegment(sketch, "E7096", {"start": v(19.28, 4.72) * mm, "end": v(19.3, 4.71) * mm});
            skLineSegment(sketch, "E7097", {"start": v(19.3, 4.71) * mm, "end": v(19.33, 4.71) * mm});
            skLineSegment(sketch, "E7098", {"start": v(19.33, 4.71) * mm, "end": v(19.35, 4.7) * mm});
            skLineSegment(sketch, "E7099", {"start": v(19.35, 4.7) * mm, "end": v(19.36, 4.7) * mm});
            skLineSegment(sketch, "E7100", {"start": v(19.36, 4.7) * mm, "end": v(19.36, 4.7) * mm});
            skLineSegment(sketch, "E7101", {"start": v(19.36, 4.7) * mm, "end": v(19.37, 4.7) * mm});
            skLineSegment(sketch, "E7102", {"start": v(19.37, 4.7) * mm, "end": v(19.38, 4.7) * mm});
            skLineSegment(sketch, "E7103", {"start": v(19.38, 4.7) * mm, "end": v(19.38, 4.7) * mm});
            skLineSegment(sketch, "E7104", {"start": v(19.38, 4.7) * mm, "end": v(19.4, 4.7) * mm});
            skLineSegment(sketch, "E7105", {"start": v(19.4, 4.7) * mm, "end": v(19.4, 4.7) * mm});
            skLineSegment(sketch, "E7106", {"start": v(19.4, 4.7) * mm, "end": v(19.41, 4.69) * mm});
            skLineSegment(sketch, "E7107", {"start": v(19.41, 4.69) * mm, "end": v(19.42, 4.69) * mm});
            skLineSegment(sketch, "E7108", {"start": v(19.42, 4.69) * mm, "end": v(19.43, 4.68) * mm});
            skLineSegment(sketch, "E7109", {"start": v(19.43, 4.68) * mm, "end": v(19.44, 4.68) * mm});
            skLineSegment(sketch, "E7110", {"start": v(19.44, 4.68) * mm, "end": v(19.44, 4.68) * mm});
            skLineSegment(sketch, "E7111", {"start": v(19.44, 4.68) * mm, "end": v(19.45, 4.68) * mm});
            skLineSegment(sketch, "E7112", {"start": v(19.45, 4.68) * mm, "end": v(19.46, 4.67) * mm});
            skLineSegment(sketch, "E7113", {"start": v(19.46, 4.67) * mm, "end": v(19.47, 4.67) * mm});
            skLineSegment(sketch, "E7114", {"start": v(19.47, 4.67) * mm, "end": v(19.48, 4.66) * mm});
            skLineSegment(sketch, "E7115", {"start": v(19.48, 4.66) * mm, "end": v(19.5, 4.65) * mm});
            skLineSegment(sketch, "E7116", {"start": v(19.5, 4.65) * mm, "end": v(19.5, 4.65) * mm});
            skLineSegment(sketch, "E7117", {"start": v(19.5, 4.65) * mm, "end": v(19.52, 4.64) * mm});
            skLineSegment(sketch, "E7118", {"start": v(19.52, 4.64) * mm, "end": v(19.53, 4.64) * mm});
            skLineSegment(sketch, "E7119", {"start": v(19.53, 4.64) * mm, "end": v(19.55, 4.63) * mm});
            skLineSegment(sketch, "E7120", {"start": v(19.55, 4.63) * mm, "end": v(19.56, 4.63) * mm});
            skLineSegment(sketch, "E7121", {"start": v(19.56, 4.63) * mm, "end": v(19.57, 4.62) * mm});
            skLineSegment(sketch, "E7122", {"start": v(19.57, 4.62) * mm, "end": v(19.67, 4.59) * mm});
            skLineSegment(sketch, "E7123", {"start": v(19.67, 4.59) * mm, "end": v(19.75, 4.55) * mm});
            skLineSegment(sketch, "E7124", {"start": v(19.75, 4.55) * mm, "end": v(19.8, 4.5) * mm});
            skLineSegment(sketch, "E7125", {"start": v(19.8, 4.5) * mm, "end": v(19.82, 4.45) * mm});
            skLineSegment(sketch, "E7126", {"start": v(19.82, 4.45) * mm, "end": v(19.84, 4.39) * mm});
            skLineSegment(sketch, "E7127", {"start": v(19.84, 4.39) * mm, "end": v(19.84, 4.31) * mm});
            skLineSegment(sketch, "E7128", {"start": v(22.93, 1.75) * mm, "end": v(22.92, 1.7) * mm});
            skLineSegment(sketch, "E7129", {"start": v(22.92, 1.7) * mm, "end": v(22.91, 1.64) * mm});
            skLineSegment(sketch, "E7130", {"start": v(22.91, 1.64) * mm, "end": v(22.9, 1.59) * mm});
            skLineSegment(sketch, "E7131", {"start": v(22.9, 1.59) * mm, "end": v(22.88, 1.54) * mm});
            skLineSegment(sketch, "E7132", {"start": v(22.88, 1.54) * mm, "end": v(22.85, 1.49) * mm});
            skLineSegment(sketch, "E7133", {"start": v(22.85, 1.49) * mm, "end": v(22.84, 1.46) * mm});
            skLineSegment(sketch, "E7134", {"start": v(22.84, 1.46) * mm, "end": v(22.82, 1.44) * mm});
            skLineSegment(sketch, "E7135", {"start": v(22.82, 1.44) * mm, "end": v(22.81, 1.41) * mm});
            skLineSegment(sketch, "E7136", {"start": v(22.81, 1.41) * mm, "end": v(22.8, 1.39) * mm});
            skLineSegment(sketch, "E7137", {"start": v(22.8, 1.39) * mm, "end": v(22.79, 1.36) * mm});
            skLineSegment(sketch, "E7138", {"start": v(22.79, 1.36) * mm, "end": v(22.77, 1.34) * mm});
            skLineSegment(sketch, "E7139", {"start": v(22.77, 1.34) * mm, "end": v(22.76, 1.31) * mm});
            skLineSegment(sketch, "E7140", {"start": v(22.76, 1.31) * mm, "end": v(22.75, 1.29) * mm});
            skLineSegment(sketch, "E7141", {"start": v(22.75, 1.29) * mm, "end": v(22.74, 1.27) * mm});
            skLineSegment(sketch, "E7142", {"start": v(22.74, 1.27) * mm, "end": v(22.74, 1.26) * mm});
            skLineSegment(sketch, "E7143", {"start": v(22.74, 1.26) * mm, "end": v(22.73, 1.24) * mm});
            skLineSegment(sketch, "E7144", {"start": v(22.73, 1.24) * mm, "end": v(22.72, 1.23) * mm});
            skLineSegment(sketch, "E7145", {"start": v(22.72, 1.23) * mm, "end": v(22.71, 1.21) * mm});
            skLineSegment(sketch, "E7146", {"start": v(22.71, 1.21) * mm, "end": v(22.7, 1.2) * mm});
            skLineSegment(sketch, "E7147", {"start": v(22.7, 1.2) * mm, "end": v(22.7, 1.18) * mm});
            skLineSegment(sketch, "E7148", {"start": v(22.7, 1.18) * mm, "end": v(22.7, 1.17) * mm});
            skLineSegment(sketch, "E7149", {"start": v(22.7, 1.17) * mm, "end": v(22.69, 1.16) * mm});
            skLineSegment(sketch, "E7150", {"start": v(22.69, 1.16) * mm, "end": v(22.68, 1.15) * mm});
            skLineSegment(sketch, "E7151", {"start": v(22.68, 1.15) * mm, "end": v(22.68, 1.14) * mm});
            skLineSegment(sketch, "E7152", {"start": v(22.68, 1.14) * mm, "end": v(22.67, 1.13) * mm});
            skLineSegment(sketch, "E7153", {"start": v(22.67, 1.13) * mm, "end": v(22.67, 1.13) * mm});
            skLineSegment(sketch, "E7154", {"start": v(22.67, 1.13) * mm, "end": v(22.66, 1.12) * mm});
            skLineSegment(sketch, "E7155", {"start": v(22.66, 1.12) * mm, "end": v(22.66, 1.11) * mm});
            skLineSegment(sketch, "E7156", {"start": v(22.66, 1.11) * mm, "end": v(22.66, 1.1) * mm});
            skLineSegment(sketch, "E7157", {"start": v(22.66, 1.1) * mm, "end": v(22.65, 1.09) * mm});
            skLineSegment(sketch, "E7158", {"start": v(22.65, 1.09) * mm, "end": v(22.64, 1.07) * mm});
            skLineSegment(sketch, "E7159", {"start": v(22.64, 1.07) * mm, "end": v(22.63, 1.06) * mm});
            skLineSegment(sketch, "E7160", {"start": v(22.63, 1.06) * mm, "end": v(22.62, 1.04) * mm});
            skLineSegment(sketch, "E7161", {"start": v(22.62, 1.04) * mm, "end": v(22.61, 1.03) * mm});
            skLineSegment(sketch, "E7162", {"start": v(22.61, 1.03) * mm, "end": v(22.6, 1.02) * mm});
            skLineSegment(sketch, "E7163", {"start": v(22.6, 1.02) * mm, "end": v(22.6, 1) * mm});
            skLineSegment(sketch, "E7164", {"start": v(22.6, 1) * mm, "end": v(22.6, 0.98) * mm});
            skLineSegment(sketch, "E7165", {"start": v(22.6, 0.98) * mm, "end": v(22.55, 0.9) * mm});
            skLineSegment(sketch, "E7166", {"start": v(22.55, 0.9) * mm, "end": v(22.5, 0.8) * mm});
            skLineSegment(sketch, "E7167", {"start": v(22.5, 0.8) * mm, "end": v(22.45, 0.72) * mm});
            skLineSegment(sketch, "E7168", {"start": v(22.45, 0.72) * mm, "end": v(22.39, 0.63) * mm});
            skLineSegment(sketch, "E7169", {"start": v(22.39, 0.63) * mm, "end": v(22.31, 0.54) * mm});
            skLineSegment(sketch, "E7170", {"start": v(22.31, 0.54) * mm, "end": v(22.23, 0.46) * mm});
            skLineSegment(sketch, "E7171", {"start": v(22.23, 0.46) * mm, "end": v(22.14, 0.37) * mm});
            skLineSegment(sketch, "E7172", {"start": v(22.14, 0.37) * mm, "end": v(22.04, 0.28) * mm});
            skLineSegment(sketch, "E7173", {"start": v(22.04, 0.28) * mm, "end": v(22.03, 0.27) * mm});
            skLineSegment(sketch, "E7174", {"start": v(22.03, 0.27) * mm, "end": v(22.02, 0.27) * mm});
            skLineSegment(sketch, "E7175", {"start": v(22.02, 0.27) * mm, "end": v(22.02, 0.26) * mm});
            skLineSegment(sketch, "E7176", {"start": v(22.02, 0.26) * mm, "end": v(22, 0.26) * mm});
            skLineSegment(sketch, "E7177", {"start": v(22, 0.26) * mm, "end": v(22, 0.26) * mm});
            skLineSegment(sketch, "E7178", {"start": v(22, 0.26) * mm, "end": v(21.99, 0.26) * mm});
            skLineSegment(sketch, "E7179", {"start": v(21.99, 0.26) * mm, "end": v(21.97, 0.26) * mm});
            skLineSegment(sketch, "E7180", {"start": v(21.97, 0.26) * mm, "end": v(21.94, 0.27) * mm});
            skLineSegment(sketch, "E7181", {"start": v(21.94, 0.27) * mm, "end": v(21.92, 0.28) * mm});
            skLineSegment(sketch, "E7182", {"start": v(21.92, 0.28) * mm, "end": v(21.9, 0.3) * mm});
            skLineSegment(sketch, "E7183", {"start": v(21.9, 0.3) * mm, "end": v(21.88, 0.3) * mm});
            skLineSegment(sketch, "E7184", {"start": v(21.88, 0.3) * mm, "end": v(21.85, 0.33) * mm});
            skLineSegment(sketch, "E7185", {"start": v(21.85, 0.33) * mm, "end": v(21.84, 0.34) * mm});
            skLineSegment(sketch, "E7186", {"start": v(21.84, 0.34) * mm, "end": v(21.82, 0.35) * mm});
            skLineSegment(sketch, "E7187", {"start": v(21.82, 0.35) * mm, "end": v(21.8, 0.37) * mm});
            skLineSegment(sketch, "E7188", {"start": v(21.8, 0.37) * mm, "end": v(21.78, 0.4) * mm});
            skLineSegment(sketch, "E7189", {"start": v(21.78, 0.4) * mm, "end": v(21.76, 0.42) * mm});
            skLineSegment(sketch, "E7190", {"start": v(21.76, 0.42) * mm, "end": v(21.75, 0.45) * mm});
            skLineSegment(sketch, "E7191", {"start": v(21.75, 0.45) * mm, "end": v(21.73, 0.48) * mm});
            skLineSegment(sketch, "E7192", {"start": v(21.73, 0.48) * mm, "end": v(21.72, 0.5) * mm});
            skLineSegment(sketch, "E7193", {"start": v(21.72, 0.5) * mm, "end": v(21.7, 0.54) * mm});
            skLineSegment(sketch, "E7194", {"start": v(21.7, 0.54) * mm, "end": v(21.7, 0.57) * mm});
            skLineSegment(sketch, "E7195", {"start": v(21.7, 0.57) * mm, "end": v(21.68, 0.65) * mm});
            skLineSegment(sketch, "E7196", {"start": v(21.68, 0.65) * mm, "end": v(21.66, 0.72) * mm});
            skLineSegment(sketch, "E7197", {"start": v(21.66, 0.72) * mm, "end": v(21.65, 0.77) * mm});
            skLineSegment(sketch, "E7198", {"start": v(21.65, 0.77) * mm, "end": v(21.64, 0.8) * mm});
            skLineSegment(sketch, "E7199", {"start": v(21.64, 0.8) * mm, "end": v(21.64, 0.82) * mm});
            skLineSegment(sketch, "E7200", {"start": v(21.64, 0.82) * mm, "end": v(21.64, 0.83) * mm});
            skLineSegment(sketch, "E7201", {"start": v(21.64, 0.83) * mm, "end": v(21.64, 0.84) * mm});
            skLineSegment(sketch, "E7202", {"start": v(21.64, 0.84) * mm, "end": v(21.64, 0.84) * mm});
            skLineSegment(sketch, "E7203", {"start": v(21.64, 0.84) * mm, "end": v(21.61, 0.95) * mm});
            skLineSegment(sketch, "E7204", {"start": v(21.61, 0.95) * mm, "end": v(21.6, 1.06) * mm});
            skLineSegment(sketch, "E7205", {"start": v(21.6, 1.06) * mm, "end": v(21.57, 1.16) * mm});
            skLineSegment(sketch, "E7206", {"start": v(21.57, 1.16) * mm, "end": v(21.55, 1.26) * mm});
            skLineSegment(sketch, "E7207", {"start": v(21.55, 1.26) * mm, "end": v(21.54, 1.34) * mm});
            skLineSegment(sketch, "E7208", {"start": v(21.54, 1.34) * mm, "end": v(21.52, 1.41) * mm});
            skLineSegment(sketch, "E7209", {"start": v(21.52, 1.41) * mm, "end": v(21.51, 1.47) * mm});
            skLineSegment(sketch, "E7210", {"start": v(21.51, 1.47) * mm, "end": v(21.5, 1.5) * mm});
            skLineSegment(sketch, "E7211", {"start": v(21.5, 1.5) * mm, "end": v(21.5, 1.52) * mm});
            skLineSegment(sketch, "E7212", {"start": v(21.5, 1.52) * mm, "end": v(21.5, 1.54) * mm});
            skLineSegment(sketch, "E7213", {"start": v(21.5, 1.54) * mm, "end": v(21.5, 1.56) * mm});
            skLineSegment(sketch, "E7214", {"start": v(21.5, 1.56) * mm, "end": v(21.5, 1.58) * mm});
            skLineSegment(sketch, "E7215", {"start": v(21.5, 1.58) * mm, "end": v(21.5, 1.6) * mm});
            skLineSegment(sketch, "E7216", {"start": v(21.5, 1.6) * mm, "end": v(21.5, 1.6) * mm});
            skLineSegment(sketch, "E7217", {"start": v(21.5, 1.6) * mm, "end": v(21.5, 1.61) * mm});
            skLineSegment(sketch, "E7218", {"start": v(21.5, 1.61) * mm, "end": v(21.5, 1.62) * mm});
            skLineSegment(sketch, "E7219", {"start": v(21.5, 1.62) * mm, "end": v(21.5, 1.62) * mm});
            skLineSegment(sketch, "E7220", {"start": v(21.5, 1.62) * mm, "end": v(21.5, 1.63) * mm});
            skLineSegment(sketch, "E7221", {"start": v(21.5, 1.63) * mm, "end": v(21.5, 1.65) * mm});
            skLineSegment(sketch, "E7222", {"start": v(21.5, 1.65) * mm, "end": v(21.5, 1.66) * mm});
            skLineSegment(sketch, "E7223", {"start": v(21.5, 1.66) * mm, "end": v(21.5, 1.68) * mm});
            skLineSegment(sketch, "E7224", {"start": v(21.5, 1.68) * mm, "end": v(21.5, 1.7) * mm});
            skLineSegment(sketch, "E7225", {"start": v(21.5, 1.7) * mm, "end": v(21.5, 1.72) * mm});
            skLineSegment(sketch, "E7226", {"start": v(21.5, 1.72) * mm, "end": v(21.5, 1.74) * mm});
            skLineSegment(sketch, "E7227", {"start": v(21.5, 1.74) * mm, "end": v(21.51, 1.78) * mm});
            skLineSegment(sketch, "E7228", {"start": v(21.51, 1.78) * mm, "end": v(21.52, 1.81) * mm});
            skLineSegment(sketch, "E7229", {"start": v(21.52, 1.81) * mm, "end": v(21.52, 1.85) * mm});
            skLineSegment(sketch, "E7230", {"start": v(21.52, 1.85) * mm, "end": v(21.52, 1.9) * mm});
            skLineSegment(sketch, "E7231", {"start": v(21.52, 1.9) * mm, "end": v(21.53, 1.94) * mm});
            skLineSegment(sketch, "E7232", {"start": v(21.53, 1.94) * mm, "end": v(21.53, 1.99) * mm});
            skLineSegment(sketch, "E7233", {"start": v(21.53, 1.99) * mm, "end": v(21.54, 2.03) * mm});
            skLineSegment(sketch, "E7234", {"start": v(21.54, 2.03) * mm, "end": v(21.54, 2.03) * mm});
            skLineSegment(sketch, "E7235", {"start": v(21.54, 2.03) * mm, "end": v(21.54, 2.04) * mm});
            skLineSegment(sketch, "E7236", {"start": v(21.54, 2.04) * mm, "end": v(21.54, 2.04) * mm});
            skLineSegment(sketch, "E7237", {"start": v(21.54, 2.04) * mm, "end": v(21.54, 2.05) * mm});
            skLineSegment(sketch, "E7238", {"start": v(21.54, 2.05) * mm, "end": v(21.54, 2.06) * mm});
            skLineSegment(sketch, "E7239", {"start": v(21.54, 2.06) * mm, "end": v(21.54, 2.08) * mm});
            skLineSegment(sketch, "E7240", {"start": v(21.54, 2.08) * mm, "end": v(21.54, 2.1) * mm});
            skLineSegment(sketch, "E7241", {"start": v(21.54, 2.1) * mm, "end": v(21.54, 2.14) * mm});
            skLineSegment(sketch, "E7242", {"start": v(21.54, 2.14) * mm, "end": v(21.55, 2.21) * mm});
            skLineSegment(sketch, "E7243", {"start": v(21.55, 2.21) * mm, "end": v(21.56, 2.28) * mm});
            skLineSegment(sketch, "E7244", {"start": v(21.56, 2.28) * mm, "end": v(21.59, 2.34) * mm});
            skLineSegment(sketch, "E7245", {"start": v(21.59, 2.34) * mm, "end": v(21.62, 2.4) * mm});
            skLineSegment(sketch, "E7246", {"start": v(21.62, 2.4) * mm, "end": v(21.66, 2.46) * mm});
            skLineSegment(sketch, "E7247", {"start": v(21.66, 2.46) * mm, "end": v(21.7, 2.52) * mm});
            skLineSegment(sketch, "E7248", {"start": v(21.7, 2.52) * mm, "end": v(21.74, 2.57) * mm});
            skLineSegment(sketch, "E7249", {"start": v(21.74, 2.57) * mm, "end": v(21.79, 2.63) * mm});
            skLineSegment(sketch, "E7250", {"start": v(21.79, 2.63) * mm, "end": v(21.8, 2.65) * mm});
            skLineSegment(sketch, "E7251", {"start": v(21.8, 2.65) * mm, "end": v(21.82, 2.67) * mm});
            skLineSegment(sketch, "E7252", {"start": v(21.82, 2.67) * mm, "end": v(21.83, 2.68) * mm});
            skLineSegment(sketch, "E7253", {"start": v(21.83, 2.68) * mm, "end": v(21.85, 2.7) * mm});
            skLineSegment(sketch, "E7254", {"start": v(21.85, 2.7) * mm, "end": v(21.86, 2.72) * mm});
            skLineSegment(sketch, "E7255", {"start": v(21.86, 2.72) * mm, "end": v(21.88, 2.74) * mm});
            skLineSegment(sketch, "E7256", {"start": v(21.88, 2.74) * mm, "end": v(21.9, 2.76) * mm});
            skLineSegment(sketch, "E7257", {"start": v(21.9, 2.76) * mm, "end": v(21.9, 2.78) * mm});
            skLineSegment(sketch, "E7258", {"start": v(21.9, 2.78) * mm, "end": v(21.91, 2.8) * mm});
            skLineSegment(sketch, "E7259", {"start": v(21.91, 2.8) * mm, "end": v(21.92, 2.8) * mm});
            skLineSegment(sketch, "E7260", {"start": v(21.92, 2.8) * mm, "end": v(21.93, 2.82) * mm});
            skLineSegment(sketch, "E7261", {"start": v(21.93, 2.82) * mm, "end": v(21.94, 2.83) * mm});
            skLineSegment(sketch, "E7262", {"start": v(21.94, 2.83) * mm, "end": v(21.95, 2.84) * mm});
            skLineSegment(sketch, "E7263", {"start": v(21.95, 2.84) * mm, "end": v(21.95, 2.85) * mm});
            skLineSegment(sketch, "E7264", {"start": v(21.95, 2.85) * mm, "end": v(21.96, 2.86) * mm});
            skLineSegment(sketch, "E7265", {"start": v(21.96, 2.86) * mm, "end": v(21.97, 2.88) * mm});
            skLineSegment(sketch, "E7266", {"start": v(21.97, 2.88) * mm, "end": v(22, 2.92) * mm});
            skLineSegment(sketch, "E7267", {"start": v(22, 2.92) * mm, "end": v(22.03, 2.96) * mm});
            skLineSegment(sketch, "E7268", {"start": v(22.03, 2.96) * mm, "end": v(22.06, 3) * mm});
            skLineSegment(sketch, "E7269", {"start": v(22.06, 3) * mm, "end": v(22.09, 3.04) * mm});
            skLineSegment(sketch, "E7270", {"start": v(22.09, 3.04) * mm, "end": v(22.12, 3.07) * mm});
            skLineSegment(sketch, "E7271", {"start": v(22.12, 3.07) * mm, "end": v(22.15, 3.11) * mm});
            skLineSegment(sketch, "E7272", {"start": v(22.15, 3.11) * mm, "end": v(22.18, 3.14) * mm});
            skLineSegment(sketch, "E7273", {"start": v(22.18, 3.14) * mm, "end": v(22.21, 3.18) * mm});
            skLineSegment(sketch, "E7274", {"start": v(22.21, 3.18) * mm, "end": v(22.24, 3.2) * mm});
            skLineSegment(sketch, "E7275", {"start": v(22.24, 3.2) * mm, "end": v(22.27, 3.22) * mm});
            skLineSegment(sketch, "E7276", {"start": v(22.27, 3.22) * mm, "end": v(22.3, 3.23) * mm});
            skLineSegment(sketch, "E7277", {"start": v(22.3, 3.23) * mm, "end": v(22.33, 3.24) * mm});
            skLineSegment(sketch, "E7278", {"start": v(22.33, 3.24) * mm, "end": v(22.36, 3.25) * mm});
            skLineSegment(sketch, "E7279", {"start": v(22.36, 3.25) * mm, "end": v(22.39, 3.25) * mm});
            skLineSegment(sketch, "E7280", {"start": v(22.39, 3.25) * mm, "end": v(22.41, 3.25) * mm});
            skLineSegment(sketch, "E7281", {"start": v(22.41, 3.25) * mm, "end": v(22.44, 3.26) * mm});
            skLineSegment(sketch, "E7282", {"start": v(22.44, 3.26) * mm, "end": v(22.5, 3.25) * mm});
            skLineSegment(sketch, "E7283", {"start": v(22.5, 3.25) * mm, "end": v(22.57, 3.24) * mm});
            skLineSegment(sketch, "E7284", {"start": v(22.57, 3.24) * mm, "end": v(22.63, 3.21) * mm});
            skLineSegment(sketch, "E7285", {"start": v(22.63, 3.21) * mm, "end": v(22.68, 3.18) * mm});
            skLineSegment(sketch, "E7286", {"start": v(22.68, 3.18) * mm, "end": v(22.73, 3.15) * mm});
            skLineSegment(sketch, "E7287", {"start": v(22.73, 3.15) * mm, "end": v(22.77, 3.1) * mm});
            skLineSegment(sketch, "E7288", {"start": v(22.77, 3.1) * mm, "end": v(22.8, 3.05) * mm});
            skLineSegment(sketch, "E7289", {"start": v(22.8, 3.05) * mm, "end": v(22.83, 3) * mm});
            skLineSegment(sketch, "E7290", {"start": v(22.83, 3) * mm, "end": v(22.83, 3) * mm});
            skLineSegment(sketch, "E7291", {"start": v(22.83, 3) * mm, "end": v(22.83, 2.98) * mm});
            skLineSegment(sketch, "E7292", {"start": v(22.83, 2.98) * mm, "end": v(22.83, 2.98) * mm});
            skLineSegment(sketch, "E7293", {"start": v(22.83, 2.98) * mm, "end": v(22.83, 2.97) * mm});
            skLineSegment(sketch, "E7294", {"start": v(22.83, 2.97) * mm, "end": v(22.83, 2.96) * mm});
            skLineSegment(sketch, "E7295", {"start": v(22.83, 2.96) * mm, "end": v(22.83, 2.95) * mm});
            skLineSegment(sketch, "E7296", {"start": v(22.83, 2.95) * mm, "end": v(22.83, 2.94) * mm});
            skLineSegment(sketch, "E7297", {"start": v(22.83, 2.94) * mm, "end": v(22.83, 2.93) * mm});
            skLineSegment(sketch, "E7298", {"start": v(22.83, 2.93) * mm, "end": v(22.83, 2.92) * mm});
            skLineSegment(sketch, "E7299", {"start": v(22.83, 2.92) * mm, "end": v(22.83, 2.91) * mm});
            skLineSegment(sketch, "E7300", {"start": v(22.83, 2.91) * mm, "end": v(22.83, 2.9) * mm});
            skLineSegment(sketch, "E7301", {"start": v(22.83, 2.9) * mm, "end": v(22.83, 2.9) * mm});
            skLineSegment(sketch, "E7302", {"start": v(22.83, 2.9) * mm, "end": v(22.83, 2.89) * mm});
            skLineSegment(sketch, "E7303", {"start": v(22.83, 2.89) * mm, "end": v(22.83, 2.88) * mm});
            skLineSegment(sketch, "E7304", {"start": v(22.83, 2.88) * mm, "end": v(22.83, 2.87) * mm});
            skLineSegment(sketch, "E7305", {"start": v(22.83, 2.87) * mm, "end": v(22.84, 2.84) * mm});
            skLineSegment(sketch, "E7306", {"start": v(22.84, 2.84) * mm, "end": v(22.84, 2.82) * mm});
            skLineSegment(sketch, "E7307", {"start": v(22.84, 2.82) * mm, "end": v(22.84, 2.8) * mm});
            skLineSegment(sketch, "E7308", {"start": v(22.84, 2.8) * mm, "end": v(22.84, 2.8) * mm});
            skLineSegment(sketch, "E7309", {"start": v(22.84, 2.8) * mm, "end": v(22.84, 2.78) * mm});
            skLineSegment(sketch, "E7310", {"start": v(22.84, 2.78) * mm, "end": v(22.84, 2.78) * mm});
            skLineSegment(sketch, "E7311", {"start": v(22.84, 2.78) * mm, "end": v(22.84, 2.74) * mm});
            skLineSegment(sketch, "E7312", {"start": v(22.84, 2.74) * mm, "end": v(22.85, 2.7) * mm});
            skLineSegment(sketch, "E7313", {"start": v(22.85, 2.7) * mm, "end": v(22.85, 2.65) * mm});
            skLineSegment(sketch, "E7314", {"start": v(22.85, 2.65) * mm, "end": v(22.86, 2.61) * mm});
            skLineSegment(sketch, "E7315", {"start": v(22.86, 2.61) * mm, "end": v(22.86, 2.57) * mm});
            skLineSegment(sketch, "E7316", {"start": v(22.86, 2.57) * mm, "end": v(22.87, 2.53) * mm});
            skLineSegment(sketch, "E7317", {"start": v(22.87, 2.53) * mm, "end": v(22.87, 2.5) * mm});
            skLineSegment(sketch, "E7318", {"start": v(22.87, 2.5) * mm, "end": v(22.87, 2.46) * mm});
            skLineSegment(sketch, "E7319", {"start": v(22.87, 2.46) * mm, "end": v(22.88, 2.43) * mm});
            skLineSegment(sketch, "E7320", {"start": v(22.88, 2.43) * mm, "end": v(22.88, 2.39) * mm});
            skLineSegment(sketch, "E7321", {"start": v(22.88, 2.39) * mm, "end": v(22.89, 2.34) * mm});
            skLineSegment(sketch, "E7322", {"start": v(22.89, 2.34) * mm, "end": v(22.9, 2.29) * mm});
            skLineSegment(sketch, "E7323", {"start": v(22.9, 2.29) * mm, "end": v(22.9, 2.23) * mm});
            skLineSegment(sketch, "E7324", {"start": v(22.9, 2.23) * mm, "end": v(22.9, 2.18) * mm});
            skLineSegment(sketch, "E7325", {"start": v(22.9, 2.18) * mm, "end": v(22.9, 2.12) * mm});
            skLineSegment(sketch, "E7326", {"start": v(22.9, 2.12) * mm, "end": v(22.91, 2.07) * mm});
            skLineSegment(sketch, "E7327", {"start": v(22.91, 2.07) * mm, "end": v(22.91, 2.07) * mm});
            skLineSegment(sketch, "E7328", {"start": v(22.91, 2.07) * mm, "end": v(22.91, 2.06) * mm});
            skLineSegment(sketch, "E7329", {"start": v(22.91, 2.06) * mm, "end": v(22.91, 2.06) * mm});
            skLineSegment(sketch, "E7330", {"start": v(22.91, 2.06) * mm, "end": v(22.92, 2.05) * mm});
            skLineSegment(sketch, "E7331", {"start": v(22.92, 2.05) * mm, "end": v(22.92, 2.03) * mm});
            skLineSegment(sketch, "E7332", {"start": v(22.92, 2.03) * mm, "end": v(22.92, 2.01) * mm});
            skLineSegment(sketch, "E7333", {"start": v(22.92, 2.01) * mm, "end": v(22.92, 1.98) * mm});
            skLineSegment(sketch, "E7334", {"start": v(22.92, 1.98) * mm, "end": v(22.93, 1.94) * mm});
            skLineSegment(sketch, "E7335", {"start": v(22.93, 1.94) * mm, "end": v(22.93, 1.87) * mm});
            skLineSegment(sketch, "E7336", {"start": v(22.93, 1.87) * mm, "end": v(22.93, 1.81) * mm});
            skLineSegment(sketch, "E7337", {"start": v(22.93, 1.81) * mm, "end": v(22.93, 1.75) * mm});
            skLineSegment(sketch, "E7338", {"start": v(26.56, 2.72) * mm, "end": v(26.6, 2.64) * mm});
            skLineSegment(sketch, "E7339", {"start": v(26.6, 2.64) * mm, "end": v(26.63, 2.56) * mm});
            skLineSegment(sketch, "E7340", {"start": v(26.63, 2.56) * mm, "end": v(26.65, 2.5) * mm});
            skLineSegment(sketch, "E7341", {"start": v(26.65, 2.5) * mm, "end": v(26.67, 2.42) * mm});
            skLineSegment(sketch, "E7342", {"start": v(26.67, 2.42) * mm, "end": v(26.68, 2.36) * mm});
            skLineSegment(sketch, "E7343", {"start": v(26.68, 2.36) * mm, "end": v(26.7, 2.29) * mm});
            skLineSegment(sketch, "E7344", {"start": v(26.7, 2.29) * mm, "end": v(26.71, 2.22) * mm});
            skLineSegment(sketch, "E7345", {"start": v(26.71, 2.22) * mm, "end": v(26.73, 2.15) * mm});
            skLineSegment(sketch, "E7346", {"start": v(26.73, 2.15) * mm, "end": v(26.74, 2.08) * mm});
            skLineSegment(sketch, "E7347", {"start": v(26.74, 2.08) * mm, "end": v(26.75, 2.01) * mm});
            skLineSegment(sketch, "E7348", {"start": v(26.75, 2.01) * mm, "end": v(26.76, 2) * mm});
            skLineSegment(sketch, "E7349", {"start": v(26.76, 2) * mm, "end": v(26.76, 1.99) * mm});
            skLineSegment(sketch, "E7350", {"start": v(26.76, 1.99) * mm, "end": v(26.76, 1.98) * mm});
            skLineSegment(sketch, "E7351", {"start": v(26.76, 1.98) * mm, "end": v(26.76, 1.97) * mm});
            skLineSegment(sketch, "E7352", {"start": v(26.76, 1.97) * mm, "end": v(26.76, 1.97) * mm});
            skLineSegment(sketch, "E7353", {"start": v(26.76, 1.97) * mm, "end": v(26.76, 1.96) * mm});
            skLineSegment(sketch, "E7354", {"start": v(26.76, 1.96) * mm, "end": v(26.76, 1.96) * mm});
            skLineSegment(sketch, "E7355", {"start": v(26.76, 1.96) * mm, "end": v(26.77, 1.95) * mm});
            skLineSegment(sketch, "E7356", {"start": v(26.77, 1.95) * mm, "end": v(26.77, 1.93) * mm});
            skLineSegment(sketch, "E7357", {"start": v(26.77, 1.93) * mm, "end": v(26.77, 1.9) * mm});
            skLineSegment(sketch, "E7358", {"start": v(26.77, 1.9) * mm, "end": v(26.77, 1.9) * mm});
            skLineSegment(sketch, "E7359", {"start": v(26.77, 1.9) * mm, "end": v(26.77, 1.88) * mm});
            skLineSegment(sketch, "E7360", {"start": v(26.77, 1.88) * mm, "end": v(26.77, 1.87) * mm});
            skLineSegment(sketch, "E7361", {"start": v(26.77, 1.87) * mm, "end": v(26.77, 1.87) * mm});
            skLineSegment(sketch, "E7362", {"start": v(26.77, 1.87) * mm, "end": v(26.77, 1.86) * mm});
            skLineSegment(sketch, "E7363", {"start": v(26.77, 1.86) * mm, "end": v(26.76, 1.86) * mm});
            skLineSegment(sketch, "E7364", {"start": v(26.76, 1.86) * mm, "end": v(26.76, 1.86) * mm});
            skLineSegment(sketch, "E7365", {"start": v(26.76, 1.86) * mm, "end": v(26.76, 1.85) * mm});
            skLineSegment(sketch, "E7366", {"start": v(26.76, 1.85) * mm, "end": v(26.76, 1.85) * mm});
            skLineSegment(sketch, "E7367", {"start": v(26.76, 1.85) * mm, "end": v(26.76, 1.84) * mm});
            skLineSegment(sketch, "E7368", {"start": v(26.76, 1.84) * mm, "end": v(26.76, 1.83) * mm});
            skLineSegment(sketch, "E7369", {"start": v(26.76, 1.83) * mm, "end": v(26.76, 1.82) * mm});
            skLineSegment(sketch, "E7370", {"start": v(26.76, 1.82) * mm, "end": v(26.76, 1.81) * mm});
            skLineSegment(sketch, "E7371", {"start": v(26.76, 1.81) * mm, "end": v(26.76, 1.79) * mm});
            skLineSegment(sketch, "E7372", {"start": v(26.76, 1.79) * mm, "end": v(26.76, 1.74) * mm});
            skLineSegment(sketch, "E7373", {"start": v(26.76, 1.74) * mm, "end": v(26.77, 1.67) * mm});
            skLineSegment(sketch, "E7374", {"start": v(26.77, 1.67) * mm, "end": v(26.78, 1.59) * mm});
            skLineSegment(sketch, "E7375", {"start": v(26.78, 1.59) * mm, "end": v(26.78, 1.49) * mm});
            skLineSegment(sketch, "E7376", {"start": v(26.78, 1.49) * mm, "end": v(26.8, 1.37) * mm});
            skLineSegment(sketch, "E7377", {"start": v(26.8, 1.37) * mm, "end": v(26.8, 1.25) * mm});
            skLineSegment(sketch, "E7378", {"start": v(26.8, 1.25) * mm, "end": v(26.8, 1.12) * mm});
            skLineSegment(sketch, "E7379", {"start": v(26.8, 1.12) * mm, "end": v(26.8, 1.12) * mm});
            skLineSegment(sketch, "E7380", {"start": v(26.8, 1.12) * mm, "end": v(26.8, 1.11) * mm});
            skLineSegment(sketch, "E7381", {"start": v(26.8, 1.11) * mm, "end": v(26.8, 1.1) * mm});
            skLineSegment(sketch, "E7382", {"start": v(26.8, 1.1) * mm, "end": v(26.8, 1.09) * mm});
            skLineSegment(sketch, "E7383", {"start": v(26.8, 1.09) * mm, "end": v(26.78, 1.06) * mm});
            skLineSegment(sketch, "E7384", {"start": v(26.78, 1.06) * mm, "end": v(26.77, 1.01) * mm});
            skLineSegment(sketch, "E7385", {"start": v(26.77, 1.01) * mm, "end": v(26.74, 0.95) * mm});
            skLineSegment(sketch, "E7386", {"start": v(26.74, 0.95) * mm, "end": v(26.7, 0.86) * mm});
            skLineSegment(sketch, "E7387", {"start": v(26.7, 0.86) * mm, "end": v(26.7, 0.86) * mm});
            skLineSegment(sketch, "E7388", {"start": v(26.7, 0.86) * mm, "end": v(26.7, 0.85) * mm});
            skLineSegment(sketch, "E7389", {"start": v(26.7, 0.85) * mm, "end": v(26.7, 0.84) * mm});
            skLineSegment(sketch, "E7390", {"start": v(26.7, 0.84) * mm, "end": v(26.7, 0.83) * mm});
            skLineSegment(sketch, "E7391", {"start": v(26.7, 0.83) * mm, "end": v(26.7, 0.82) * mm});
            skLineSegment(sketch, "E7392", {"start": v(26.7, 0.82) * mm, "end": v(26.7, 0.81) * mm});
            skLineSegment(sketch, "E7393", {"start": v(26.7, 0.81) * mm, "end": v(26.69, 0.8) * mm});
            skLineSegment(sketch, "E7394", {"start": v(26.69, 0.8) * mm, "end": v(26.69, 0.8) * mm});
            skLineSegment(sketch, "E7395", {"start": v(26.69, 0.8) * mm, "end": v(26.68, 0.78) * mm});
            skLineSegment(sketch, "E7396", {"start": v(26.68, 0.78) * mm, "end": v(26.68, 0.76) * mm});
            skLineSegment(sketch, "E7397", {"start": v(26.68, 0.76) * mm, "end": v(26.67, 0.75) * mm});
            skLineSegment(sketch, "E7398", {"start": v(26.67, 0.75) * mm, "end": v(26.67, 0.73) * mm});
            skLineSegment(sketch, "E7399", {"start": v(26.67, 0.73) * mm, "end": v(26.66, 0.72) * mm});
            skLineSegment(sketch, "E7400", {"start": v(26.66, 0.72) * mm, "end": v(26.66, 0.7) * mm});
            skLineSegment(sketch, "E7401", {"start": v(26.66, 0.7) * mm, "end": v(26.65, 0.7) * mm});
            skLineSegment(sketch, "E7402", {"start": v(26.65, 0.7) * mm, "end": v(26.64, 0.7) * mm});
            skLineSegment(sketch, "E7403", {"start": v(26.64, 0.7) * mm, "end": v(26.63, 0.68) * mm});
            skLineSegment(sketch, "E7404", {"start": v(26.63, 0.68) * mm, "end": v(26.62, 0.67) * mm});
            skLineSegment(sketch, "E7405", {"start": v(26.62, 0.67) * mm, "end": v(26.61, 0.67) * mm});
            skLineSegment(sketch, "E7406", {"start": v(26.61, 0.67) * mm, "end": v(26.61, 0.66) * mm});
            skLineSegment(sketch, "E7407", {"start": v(26.61, 0.66) * mm, "end": v(26.6, 0.66) * mm});
            skLineSegment(sketch, "E7408", {"start": v(26.6, 0.66) * mm, "end": v(26.6, 0.66) * mm});
            skLineSegment(sketch, "E7409", {"start": v(26.6, 0.66) * mm, "end": v(26.58, 0.65) * mm});
            skLineSegment(sketch, "E7410", {"start": v(26.58, 0.65) * mm, "end": v(26.55, 0.65) * mm});
            skLineSegment(sketch, "E7411", {"start": v(26.55, 0.65) * mm, "end": v(26.52, 0.66) * mm});
            skLineSegment(sketch, "E7412", {"start": v(26.52, 0.66) * mm, "end": v(26.49, 0.67) * mm});
            skLineSegment(sketch, "E7413", {"start": v(26.49, 0.67) * mm, "end": v(26.45, 0.68) * mm});
            skLineSegment(sketch, "E7414", {"start": v(26.45, 0.68) * mm, "end": v(26.4, 0.7) * mm});
            skLineSegment(sketch, "E7415", {"start": v(26.4, 0.7) * mm, "end": v(26.37, 0.71) * mm});
            skLineSegment(sketch, "E7416", {"start": v(26.37, 0.71) * mm, "end": v(26.33, 0.73) * mm});
            skLineSegment(sketch, "E7417", {"start": v(26.33, 0.73) * mm, "end": v(26.33, 0.73) * mm});
            skLineSegment(sketch, "E7418", {"start": v(26.33, 0.73) * mm, "end": v(26.32, 0.74) * mm});
            skLineSegment(sketch, "E7419", {"start": v(26.32, 0.74) * mm, "end": v(26.31, 0.74) * mm});
            skLineSegment(sketch, "E7420", {"start": v(26.31, 0.74) * mm, "end": v(26.3, 0.75) * mm});
            skLineSegment(sketch, "E7421", {"start": v(26.3, 0.75) * mm, "end": v(26.27, 0.77) * mm});
            skLineSegment(sketch, "E7422", {"start": v(26.27, 0.77) * mm, "end": v(26.24, 0.78) * mm});
            skLineSegment(sketch, "E7423", {"start": v(26.24, 0.78) * mm, "end": v(26.16, 0.83) * mm});
            skLineSegment(sketch, "E7424", {"start": v(26.16, 0.83) * mm, "end": v(26.08, 0.88) * mm});
            skLineSegment(sketch, "E7425", {"start": v(26.08, 0.88) * mm, "end": v(26, 0.93) * mm});
            skLineSegment(sketch, "E7426", {"start": v(26, 0.93) * mm, "end": v(25.92, 0.98) * mm});
            skLineSegment(sketch, "E7427", {"start": v(25.92, 0.98) * mm, "end": v(25.85, 1.04) * mm});
            skLineSegment(sketch, "E7428", {"start": v(25.85, 1.04) * mm, "end": v(25.78, 1.1) * mm});
            skLineSegment(sketch, "E7429", {"start": v(25.78, 1.1) * mm, "end": v(25.72, 1.18) * mm});
            skLineSegment(sketch, "E7430", {"start": v(25.72, 1.18) * mm, "end": v(25.67, 1.25) * mm});
            skLineSegment(sketch, "E7431", {"start": v(25.67, 1.25) * mm, "end": v(25.65, 1.3) * mm});
            skLineSegment(sketch, "E7432", {"start": v(25.65, 1.3) * mm, "end": v(25.62, 1.36) * mm});
            skLineSegment(sketch, "E7433", {"start": v(25.62, 1.36) * mm, "end": v(25.6, 1.42) * mm});
            skLineSegment(sketch, "E7434", {"start": v(25.6, 1.42) * mm, "end": v(25.57, 1.48) * mm});
            skLineSegment(sketch, "E7435", {"start": v(25.57, 1.48) * mm, "end": v(25.55, 1.54) * mm});
            skLineSegment(sketch, "E7436", {"start": v(25.55, 1.54) * mm, "end": v(25.53, 1.6) * mm});
            skLineSegment(sketch, "E7437", {"start": v(25.53, 1.6) * mm, "end": v(25.5, 1.67) * mm});
            skLineSegment(sketch, "E7438", {"start": v(25.5, 1.67) * mm, "end": v(25.5, 1.75) * mm});
            skLineSegment(sketch, "E7439", {"start": v(25.5, 1.75) * mm, "end": v(25.48, 1.78) * mm});
            skLineSegment(sketch, "E7440", {"start": v(25.48, 1.78) * mm, "end": v(25.47, 1.82) * mm});
            skLineSegment(sketch, "E7441", {"start": v(25.47, 1.82) * mm, "end": v(25.46, 1.86) * mm});
            skLineSegment(sketch, "E7442", {"start": v(25.46, 1.86) * mm, "end": v(25.46, 1.9) * mm});
            skLineSegment(sketch, "E7443", {"start": v(25.46, 1.9) * mm, "end": v(25.45, 1.94) * mm});
            skLineSegment(sketch, "E7444", {"start": v(25.45, 1.94) * mm, "end": v(25.44, 1.98) * mm});
            skLineSegment(sketch, "E7445", {"start": v(25.44, 1.98) * mm, "end": v(25.43, 2.02) * mm});
            skLineSegment(sketch, "E7446", {"start": v(25.43, 2.02) * mm, "end": v(25.43, 2.05) * mm});
            skLineSegment(sketch, "E7447", {"start": v(25.43, 2.05) * mm, "end": v(25.41, 2.13) * mm});
            skLineSegment(sketch, "E7448", {"start": v(25.41, 2.13) * mm, "end": v(25.4, 2.2) * mm});
            skLineSegment(sketch, "E7449", {"start": v(25.4, 2.2) * mm, "end": v(25.39, 2.27) * mm});
            skLineSegment(sketch, "E7450", {"start": v(25.39, 2.27) * mm, "end": v(25.37, 2.34) * mm});
            skLineSegment(sketch, "E7451", {"start": v(25.37, 2.34) * mm, "end": v(25.35, 2.42) * mm});
            skLineSegment(sketch, "E7452", {"start": v(25.35, 2.42) * mm, "end": v(25.33, 2.5) * mm});
            skLineSegment(sketch, "E7453", {"start": v(25.33, 2.5) * mm, "end": v(25.3, 2.56) * mm});
            skLineSegment(sketch, "E7454", {"start": v(25.3, 2.56) * mm, "end": v(25.28, 2.64) * mm});
            skLineSegment(sketch, "E7455", {"start": v(25.28, 2.64) * mm, "end": v(25.28, 2.64) * mm});
            skLineSegment(sketch, "E7456", {"start": v(25.28, 2.64) * mm, "end": v(25.28, 2.65) * mm});
            skLineSegment(sketch, "E7457", {"start": v(25.28, 2.65) * mm, "end": v(25.27, 2.66) * mm});
            skLineSegment(sketch, "E7458", {"start": v(25.27, 2.66) * mm, "end": v(25.27, 2.67) * mm});
            skLineSegment(sketch, "E7459", {"start": v(25.27, 2.67) * mm, "end": v(25.27, 2.68) * mm});
            skLineSegment(sketch, "E7460", {"start": v(25.27, 2.68) * mm, "end": v(25.26, 2.68) * mm});
            skLineSegment(sketch, "E7461", {"start": v(25.26, 2.68) * mm, "end": v(25.26, 2.7) * mm});
            skLineSegment(sketch, "E7462", {"start": v(25.26, 2.7) * mm, "end": v(25.26, 2.7) * mm});
            skLineSegment(sketch, "E7463", {"start": v(25.26, 2.7) * mm, "end": v(25.23, 2.75) * mm});
            skLineSegment(sketch, "E7464", {"start": v(25.23, 2.75) * mm, "end": v(25.22, 2.8) * mm});
            skLineSegment(sketch, "E7465", {"start": v(25.22, 2.8) * mm, "end": v(25.2, 2.82) * mm});
            skLineSegment(sketch, "E7466", {"start": v(25.2, 2.82) * mm, "end": v(25.2, 2.84) * mm});
            skLineSegment(sketch, "E7467", {"start": v(25.2, 2.84) * mm, "end": v(25.2, 2.85) * mm});
            skLineSegment(sketch, "E7468", {"start": v(25.2, 2.85) * mm, "end": v(25.19, 2.86) * mm});
            skLineSegment(sketch, "E7469", {"start": v(25.19, 2.86) * mm, "end": v(25.19, 2.86) * mm});
            skLineSegment(sketch, "E7470", {"start": v(25.19, 2.86) * mm, "end": v(25.2, 2.9) * mm});
            skLineSegment(sketch, "E7471", {"start": v(25.2, 2.9) * mm, "end": v(25.2, 2.94) * mm});
            skLineSegment(sketch, "E7472", {"start": v(25.2, 2.94) * mm, "end": v(25.22, 2.98) * mm});
            skLineSegment(sketch, "E7473", {"start": v(25.22, 2.98) * mm, "end": v(25.23, 3.01) * mm});
            skLineSegment(sketch, "E7474", {"start": v(25.23, 3.01) * mm, "end": v(25.24, 3.04) * mm});
            skLineSegment(sketch, "E7475", {"start": v(25.24, 3.04) * mm, "end": v(25.25, 3.07) * mm});
            skLineSegment(sketch, "E7476", {"start": v(25.25, 3.07) * mm, "end": v(25.26, 3.08) * mm});
            skLineSegment(sketch, "E7477", {"start": v(25.26, 3.08) * mm, "end": v(25.27, 3.1) * mm});
            skLineSegment(sketch, "E7478", {"start": v(25.27, 3.1) * mm, "end": v(25.28, 3.1) * mm});
            skLineSegment(sketch, "E7479", {"start": v(25.28, 3.1) * mm, "end": v(25.3, 3.13) * mm});
            skLineSegment(sketch, "E7480", {"start": v(25.3, 3.13) * mm, "end": v(25.33, 3.16) * mm});
            skLineSegment(sketch, "E7481", {"start": v(25.33, 3.16) * mm, "end": v(25.37, 3.2) * mm});
            skLineSegment(sketch, "E7482", {"start": v(25.37, 3.2) * mm, "end": v(25.41, 3.24) * mm});
            skLineSegment(sketch, "E7483", {"start": v(25.41, 3.24) * mm, "end": v(25.46, 3.29) * mm});
            skLineSegment(sketch, "E7484", {"start": v(25.46, 3.29) * mm, "end": v(25.5, 3.34) * mm});
            skLineSegment(sketch, "E7485", {"start": v(25.5, 3.34) * mm, "end": v(25.56, 3.4) * mm});
            skLineSegment(sketch, "E7486", {"start": v(25.56, 3.4) * mm, "end": v(25.56, 3.4) * mm});
            skLineSegment(sketch, "E7487", {"start": v(25.56, 3.4) * mm, "end": v(25.57, 3.4) * mm});
            skLineSegment(sketch, "E7488", {"start": v(25.57, 3.4) * mm, "end": v(25.58, 3.4) * mm});
            skLineSegment(sketch, "E7489", {"start": v(25.58, 3.4) * mm, "end": v(25.6, 3.4) * mm});
            skLineSegment(sketch, "E7490", {"start": v(25.6, 3.4) * mm, "end": v(25.64, 3.42) * mm});
            skLineSegment(sketch, "E7491", {"start": v(25.64, 3.42) * mm, "end": v(25.68, 3.43) * mm});
            skLineSegment(sketch, "E7492", {"start": v(25.68, 3.43) * mm, "end": v(25.74, 3.44) * mm});
            skLineSegment(sketch, "E7493", {"start": v(25.74, 3.44) * mm, "end": v(25.75, 3.45) * mm});
            skLineSegment(sketch, "E7494", {"start": v(25.75, 3.45) * mm, "end": v(25.77, 3.45) * mm});
            skLineSegment(sketch, "E7495", {"start": v(25.77, 3.45) * mm, "end": v(25.78, 3.45) * mm});
            skLineSegment(sketch, "E7496", {"start": v(25.78, 3.45) * mm, "end": v(25.8, 3.45) * mm});
            skLineSegment(sketch, "E7497", {"start": v(25.8, 3.45) * mm, "end": v(25.8, 3.45) * mm});
            skLineSegment(sketch, "E7498", {"start": v(25.8, 3.45) * mm, "end": v(25.82, 3.46) * mm});
            skLineSegment(sketch, "E7499", {"start": v(25.82, 3.46) * mm, "end": v(25.83, 3.46) * mm});
            skLineSegment(sketch, "E7500", {"start": v(25.83, 3.46) * mm, "end": v(25.84, 3.46) * mm});
            skLineSegment(sketch, "E7501", {"start": v(25.84, 3.46) * mm, "end": v(25.88, 3.45) * mm});
            skLineSegment(sketch, "E7502", {"start": v(25.88, 3.45) * mm, "end": v(25.92, 3.45) * mm});
            skLineSegment(sketch, "E7503", {"start": v(25.92, 3.45) * mm, "end": v(25.97, 3.43) * mm});
            skLineSegment(sketch, "E7504", {"start": v(25.97, 3.43) * mm, "end": v(26, 3.41) * mm});
            skLineSegment(sketch, "E7505", {"start": v(26, 3.41) * mm, "end": v(26.04, 3.39) * mm});
            skLineSegment(sketch, "E7506", {"start": v(26.04, 3.39) * mm, "end": v(26.08, 3.36) * mm});
            skLineSegment(sketch, "E7507", {"start": v(26.08, 3.36) * mm, "end": v(26.12, 3.32) * mm});
            skLineSegment(sketch, "E7508", {"start": v(26.12, 3.32) * mm, "end": v(26.15, 3.28) * mm});
            skLineSegment(sketch, "E7509", {"start": v(26.15, 3.28) * mm, "end": v(26.16, 3.27) * mm});
            skLineSegment(sketch, "E7510", {"start": v(26.16, 3.27) * mm, "end": v(26.18, 3.25) * mm});
            skLineSegment(sketch, "E7511", {"start": v(26.18, 3.25) * mm, "end": v(26.19, 3.23) * mm});
            skLineSegment(sketch, "E7512", {"start": v(26.19, 3.23) * mm, "end": v(26.2, 3.22) * mm});
            skLineSegment(sketch, "E7513", {"start": v(26.2, 3.22) * mm, "end": v(26.21, 3.2) * mm});
            skLineSegment(sketch, "E7514", {"start": v(26.21, 3.2) * mm, "end": v(26.23, 3.19) * mm});
            skLineSegment(sketch, "E7515", {"start": v(26.23, 3.19) * mm, "end": v(26.24, 3.17) * mm});
            skLineSegment(sketch, "E7516", {"start": v(26.24, 3.17) * mm, "end": v(26.25, 3.15) * mm});
            skLineSegment(sketch, "E7517", {"start": v(26.25, 3.15) * mm, "end": v(26.3, 3.09) * mm});
            skLineSegment(sketch, "E7518", {"start": v(26.3, 3.09) * mm, "end": v(26.36, 3.02) * mm});
            skLineSegment(sketch, "E7519", {"start": v(26.36, 3.02) * mm, "end": v(26.42, 2.94) * mm});
            skLineSegment(sketch, "E7520", {"start": v(26.42, 2.94) * mm, "end": v(26.47, 2.87) * mm});
            skLineSegment(sketch, "E7521", {"start": v(26.47, 2.87) * mm, "end": v(26.52, 2.8) * mm});
            skLineSegment(sketch, "E7522", {"start": v(26.52, 2.8) * mm, "end": v(26.56, 2.72) * mm});
            skLineSegment(sketch, "E7523", {"start": v(28.68, 5.23) * mm, "end": v(28.7, 5.22) * mm});
            skLineSegment(sketch, "E7524", {"start": v(28.7, 5.22) * mm, "end": v(28.74, 5.21) * mm});
            skLineSegment(sketch, "E7525", {"start": v(28.74, 5.21) * mm, "end": v(28.77, 5.2) * mm});
            skLineSegment(sketch, "E7526", {"start": v(28.77, 5.2) * mm, "end": v(28.8, 5.2) * mm});
            skLineSegment(sketch, "E7527", {"start": v(28.8, 5.2) * mm, "end": v(28.9, 5.18) * mm});
            skLineSegment(sketch, "E7528", {"start": v(28.9, 5.18) * mm, "end": v(29, 5.15) * mm});
            skLineSegment(sketch, "E7529", {"start": v(29, 5.15) * mm, "end": v(29.1, 5.12) * mm});
            skLineSegment(sketch, "E7530", {"start": v(29.1, 5.12) * mm, "end": v(29.2, 5.09) * mm});
            skLineSegment(sketch, "E7531", {"start": v(29.2, 5.09) * mm, "end": v(29.29, 5.05) * mm});
            skLineSegment(sketch, "E7532", {"start": v(29.29, 5.05) * mm, "end": v(29.38, 5) * mm});
            skLineSegment(sketch, "E7533", {"start": v(29.38, 5) * mm, "end": v(29.46, 4.95) * mm});
            skLineSegment(sketch, "E7534", {"start": v(29.46, 4.95) * mm, "end": v(29.54, 4.88) * mm});
            skLineSegment(sketch, "E7535", {"start": v(29.54, 4.88) * mm, "end": v(29.57, 4.85) * mm});
            skLineSegment(sketch, "E7536", {"start": v(29.57, 4.85) * mm, "end": v(29.6, 4.83) * mm});
            skLineSegment(sketch, "E7537", {"start": v(29.6, 4.83) * mm, "end": v(29.63, 4.8) * mm});
            skLineSegment(sketch, "E7538", {"start": v(29.63, 4.8) * mm, "end": v(29.66, 4.78) * mm});
            skLineSegment(sketch, "E7539", {"start": v(29.66, 4.78) * mm, "end": v(29.68, 4.76) * mm});
            skLineSegment(sketch, "E7540", {"start": v(29.68, 4.76) * mm, "end": v(29.71, 4.73) * mm});
            skLineSegment(sketch, "E7541", {"start": v(29.71, 4.73) * mm, "end": v(29.74, 4.7) * mm});
            skLineSegment(sketch, "E7542", {"start": v(29.74, 4.7) * mm, "end": v(29.77, 4.68) * mm});
            skLineSegment(sketch, "E7543", {"start": v(29.77, 4.68) * mm, "end": v(29.86, 4.6) * mm});
            skLineSegment(sketch, "E7544", {"start": v(29.86, 4.6) * mm, "end": v(29.95, 4.53) * mm});
            skLineSegment(sketch, "E7545", {"start": v(29.95, 4.53) * mm, "end": v(30.03, 4.46) * mm});
            skLineSegment(sketch, "E7546", {"start": v(30.03, 4.46) * mm, "end": v(30.1, 4.38) * mm});
            skLineSegment(sketch, "E7547", {"start": v(30.1, 4.38) * mm, "end": v(30.18, 4.3) * mm});
            skLineSegment(sketch, "E7548", {"start": v(30.18, 4.3) * mm, "end": v(30.25, 4.2) * mm});
            skLineSegment(sketch, "E7549", {"start": v(30.25, 4.2) * mm, "end": v(30.3, 4.12) * mm});
            skLineSegment(sketch, "E7550", {"start": v(30.3, 4.12) * mm, "end": v(30.36, 4.01) * mm});
            skLineSegment(sketch, "E7551", {"start": v(30.36, 4.01) * mm, "end": v(30.38, 3.95) * mm});
            skLineSegment(sketch, "E7552", {"start": v(30.38, 3.95) * mm, "end": v(30.41, 3.89) * mm});
            skLineSegment(sketch, "E7553", {"start": v(30.41, 3.89) * mm, "end": v(30.44, 3.82) * mm});
            skLineSegment(sketch, "E7554", {"start": v(30.44, 3.82) * mm, "end": v(30.46, 3.76) * mm});
            skLineSegment(sketch, "E7555", {"start": v(30.46, 3.76) * mm, "end": v(30.48, 3.7) * mm});
            skLineSegment(sketch, "E7556", {"start": v(30.48, 3.7) * mm, "end": v(30.5, 3.64) * mm});
            skLineSegment(sketch, "E7557", {"start": v(30.5, 3.64) * mm, "end": v(30.53, 3.58) * mm});
            skLineSegment(sketch, "E7558", {"start": v(30.53, 3.58) * mm, "end": v(30.55, 3.52) * mm});
            skLineSegment(sketch, "E7559", {"start": v(30.55, 3.52) * mm, "end": v(30.56, 3.5) * mm});
            skLineSegment(sketch, "E7560", {"start": v(30.56, 3.5) * mm, "end": v(30.56, 3.49) * mm});
            skLineSegment(sketch, "E7561", {"start": v(30.56, 3.49) * mm, "end": v(30.57, 3.48) * mm});
            skLineSegment(sketch, "E7562", {"start": v(30.57, 3.48) * mm, "end": v(30.57, 3.47) * mm});
            skLineSegment(sketch, "E7563", {"start": v(30.57, 3.47) * mm, "end": v(30.57, 3.47) * mm});
            skLineSegment(sketch, "E7564", {"start": v(30.57, 3.47) * mm, "end": v(30.57, 3.46) * mm});
            skLineSegment(sketch, "E7565", {"start": v(30.57, 3.46) * mm, "end": v(30.57, 3.46) * mm});
            skLineSegment(sketch, "E7566", {"start": v(30.57, 3.46) * mm, "end": v(30.58, 3.44) * mm});
            skLineSegment(sketch, "E7567", {"start": v(30.58, 3.44) * mm, "end": v(30.58, 3.4) * mm});
            skLineSegment(sketch, "E7568", {"start": v(30.58, 3.4) * mm, "end": v(30.59, 3.38) * mm});
            skLineSegment(sketch, "E7569", {"start": v(30.59, 3.38) * mm, "end": v(30.59, 3.34) * mm});
            skLineSegment(sketch, "E7570", {"start": v(30.59, 3.34) * mm, "end": v(30.59, 3.3) * mm});
            skLineSegment(sketch, "E7571", {"start": v(30.59, 3.3) * mm, "end": v(30.59, 3.26) * mm});
            skLineSegment(sketch, "E7572", {"start": v(30.59, 3.26) * mm, "end": v(30.58, 3.22) * mm});
            skLineSegment(sketch, "E7573", {"start": v(30.58, 3.22) * mm, "end": v(30.58, 3.19) * mm});
            skLineSegment(sketch, "E7574", {"start": v(30.58, 3.19) * mm, "end": v(30.58, 3.19) * mm});
            skLineSegment(sketch, "E7575", {"start": v(30.58, 3.19) * mm, "end": v(30.57, 3.18) * mm});
            skLineSegment(sketch, "E7576", {"start": v(30.57, 3.18) * mm, "end": v(30.57, 3.18) * mm});
            skLineSegment(sketch, "E7577", {"start": v(30.57, 3.18) * mm, "end": v(30.56, 3.17) * mm});
            skLineSegment(sketch, "E7578", {"start": v(30.56, 3.17) * mm, "end": v(30.55, 3.15) * mm});
            skLineSegment(sketch, "E7579", {"start": v(30.55, 3.15) * mm, "end": v(30.53, 3.14) * mm});
            skLineSegment(sketch, "E7580", {"start": v(30.53, 3.14) * mm, "end": v(30.52, 3.13) * mm});
            skLineSegment(sketch, "E7581", {"start": v(30.52, 3.13) * mm, "end": v(30.5, 3.11) * mm});
            skLineSegment(sketch, "E7582", {"start": v(30.5, 3.11) * mm, "end": v(30.48, 3.1) * mm});
            skLineSegment(sketch, "E7583", {"start": v(30.48, 3.1) * mm, "end": v(30.47, 3.1) * mm});
            skLineSegment(sketch, "E7584", {"start": v(30.47, 3.1) * mm, "end": v(30.45, 3.1) * mm});
            skLineSegment(sketch, "E7585", {"start": v(30.45, 3.1) * mm, "end": v(30.43, 3.09) * mm});
            skLineSegment(sketch, "E7586", {"start": v(30.43, 3.09) * mm, "end": v(30.4, 3.08) * mm});
            skLineSegment(sketch, "E7587", {"start": v(30.4, 3.08) * mm, "end": v(30.39, 3.08) * mm});
            skLineSegment(sketch, "E7588", {"start": v(30.39, 3.08) * mm, "end": v(30.38, 3.08) * mm});
            skLineSegment(sketch, "E7589", {"start": v(30.38, 3.08) * mm, "end": v(30.38, 3.08) * mm});
            skLineSegment(sketch, "E7590", {"start": v(30.38, 3.08) * mm, "end": v(30.37, 3.08) * mm});
            skLineSegment(sketch, "E7591", {"start": v(30.37, 3.08) * mm, "end": v(30.37, 3.08) * mm});
            skLineSegment(sketch, "E7592", {"start": v(30.37, 3.08) * mm, "end": v(30.36, 3.08) * mm});
            skLineSegment(sketch, "E7593", {"start": v(30.36, 3.08) * mm, "end": v(30.36, 3.08) * mm});
            skLineSegment(sketch, "E7594", {"start": v(30.36, 3.08) * mm, "end": v(30.35, 3.08) * mm});
            skLineSegment(sketch, "E7595", {"start": v(30.35, 3.08) * mm, "end": v(30.3, 3.1) * mm});
            skLineSegment(sketch, "E7596", {"start": v(30.3, 3.1) * mm, "end": v(30.26, 3.1) * mm});
            skLineSegment(sketch, "E7597", {"start": v(30.26, 3.1) * mm, "end": v(30.21, 3.1) * mm});
            skLineSegment(sketch, "E7598", {"start": v(30.21, 3.1) * mm, "end": v(30.16, 3.11) * mm});
            skLineSegment(sketch, "E7599", {"start": v(30.16, 3.11) * mm, "end": v(30.12, 3.12) * mm});
            skLineSegment(sketch, "E7600", {"start": v(30.12, 3.12) * mm, "end": v(30.07, 3.12) * mm});
            skLineSegment(sketch, "E7601", {"start": v(30.07, 3.12) * mm, "end": v(30.02, 3.13) * mm});
            skLineSegment(sketch, "E7602", {"start": v(30.02, 3.13) * mm, "end": v(29.97, 3.13) * mm});
            skLineSegment(sketch, "E7603", {"start": v(29.97, 3.13) * mm, "end": v(29.9, 3.14) * mm});
            skLineSegment(sketch, "E7604", {"start": v(29.9, 3.14) * mm, "end": v(29.85, 3.15) * mm});
            skLineSegment(sketch, "E7605", {"start": v(29.85, 3.15) * mm, "end": v(29.78, 3.16) * mm});
            skLineSegment(sketch, "E7606", {"start": v(29.78, 3.16) * mm, "end": v(29.72, 3.17) * mm});
            skLineSegment(sketch, "E7607", {"start": v(29.72, 3.17) * mm, "end": v(29.65, 3.18) * mm});
            skLineSegment(sketch, "E7608", {"start": v(29.65, 3.18) * mm, "end": v(29.59, 3.19) * mm});
            skLineSegment(sketch, "E7609", {"start": v(29.59, 3.19) * mm, "end": v(29.52, 3.2) * mm});
            skLineSegment(sketch, "E7610", {"start": v(29.52, 3.2) * mm, "end": v(29.46, 3.2) * mm});
            skLineSegment(sketch, "E7611", {"start": v(29.46, 3.2) * mm, "end": v(29.4, 3.21) * mm});
            skLineSegment(sketch, "E7612", {"start": v(29.4, 3.21) * mm, "end": v(29.36, 3.23) * mm});
            skLineSegment(sketch, "E7613", {"start": v(29.36, 3.23) * mm, "end": v(29.32, 3.25) * mm});
            skLineSegment(sketch, "E7614", {"start": v(29.32, 3.25) * mm, "end": v(29.28, 3.27) * mm});
            skLineSegment(sketch, "E7615", {"start": v(29.28, 3.27) * mm, "end": v(29.24, 3.3) * mm});
            skLineSegment(sketch, "E7616", {"start": v(29.24, 3.3) * mm, "end": v(29.2, 3.33) * mm});
            skLineSegment(sketch, "E7617", {"start": v(29.2, 3.33) * mm, "end": v(29.17, 3.37) * mm});
            skLineSegment(sketch, "E7618", {"start": v(29.17, 3.37) * mm, "end": v(29.14, 3.4) * mm});
            skLineSegment(sketch, "E7619", {"start": v(29.14, 3.4) * mm, "end": v(29.12, 3.44) * mm});
            skLineSegment(sketch, "E7620", {"start": v(29.12, 3.44) * mm, "end": v(29.1, 3.47) * mm});
            skLineSegment(sketch, "E7621", {"start": v(29.1, 3.47) * mm, "end": v(29.08, 3.49) * mm});
            skLineSegment(sketch, "E7622", {"start": v(29.08, 3.49) * mm, "end": v(29.07, 3.5) * mm});
            skLineSegment(sketch, "E7623", {"start": v(29.07, 3.5) * mm, "end": v(29.07, 3.5) * mm});
            skLineSegment(sketch, "E7624", {"start": v(29.07, 3.5) * mm, "end": v(29.07, 3.51) * mm});
            skLineSegment(sketch, "E7625", {"start": v(29.07, 3.51) * mm, "end": v(29.07, 3.52) * mm});
            skLineSegment(sketch, "E7626", {"start": v(29.07, 3.52) * mm, "end": v(29.07, 3.52) * mm});
            skLineSegment(sketch, "E7627", {"start": v(29.07, 3.52) * mm, "end": v(29.02, 3.55) * mm});
            skLineSegment(sketch, "E7628", {"start": v(29.02, 3.55) * mm, "end": v(28.99, 3.58) * mm});
            skLineSegment(sketch, "E7629", {"start": v(28.99, 3.58) * mm, "end": v(28.95, 3.61) * mm});
            skLineSegment(sketch, "E7630", {"start": v(28.95, 3.61) * mm, "end": v(28.92, 3.64) * mm});
            skLineSegment(sketch, "E7631", {"start": v(28.92, 3.64) * mm, "end": v(28.89, 3.66) * mm});
            skLineSegment(sketch, "E7632", {"start": v(28.89, 3.66) * mm, "end": v(28.86, 3.68) * mm});
            skLineSegment(sketch, "E7633", {"start": v(28.86, 3.68) * mm, "end": v(28.85, 3.7) * mm});
            skLineSegment(sketch, "E7634", {"start": v(28.85, 3.7) * mm, "end": v(28.84, 3.7) * mm});
            skLineSegment(sketch, "E7635", {"start": v(28.84, 3.7) * mm, "end": v(28.82, 3.72) * mm});
            skLineSegment(sketch, "E7636", {"start": v(28.82, 3.72) * mm, "end": v(28.8, 3.75) * mm});
            skLineSegment(sketch, "E7637", {"start": v(28.8, 3.75) * mm, "end": v(28.74, 3.8) * mm});
            skLineSegment(sketch, "E7638", {"start": v(28.74, 3.8) * mm, "end": v(28.68, 3.87) * mm});
            skLineSegment(sketch, "E7639", {"start": v(28.68, 3.87) * mm, "end": v(28.61, 3.95) * mm});
            skLineSegment(sketch, "E7640", {"start": v(28.61, 3.95) * mm, "end": v(28.53, 4.04) * mm});
            skLineSegment(sketch, "E7641", {"start": v(28.53, 4.04) * mm, "end": v(28.44, 4.14) * mm});
            skLineSegment(sketch, "E7642", {"start": v(28.44, 4.14) * mm, "end": v(28.35, 4.25) * mm});
            skLineSegment(sketch, "E7643", {"start": v(28.35, 4.25) * mm, "end": v(28.35, 4.25) * mm});
            skLineSegment(sketch, "E7644", {"start": v(28.35, 4.25) * mm, "end": v(28.35, 4.26) * mm});
            skLineSegment(sketch, "E7645", {"start": v(28.35, 4.26) * mm, "end": v(28.34, 4.27) * mm});
            skLineSegment(sketch, "E7646", {"start": v(28.34, 4.27) * mm, "end": v(28.33, 4.3) * mm});
            skLineSegment(sketch, "E7647", {"start": v(28.33, 4.3) * mm, "end": v(28.31, 4.36) * mm});
            skLineSegment(sketch, "E7648", {"start": v(28.31, 4.36) * mm, "end": v(28.28, 4.44) * mm});
            skLineSegment(sketch, "E7649", {"start": v(28.28, 4.44) * mm, "end": v(28.24, 4.55) * mm});
            skLineSegment(sketch, "E7650", {"start": v(28.24, 4.55) * mm, "end": v(28.2, 4.7) * mm});
            skLineSegment(sketch, "E7651", {"start": v(28.2, 4.7) * mm, "end": v(28.18, 4.76) * mm});
            skLineSegment(sketch, "E7652", {"start": v(28.18, 4.76) * mm, "end": v(28.17, 4.82) * mm});
            skLineSegment(sketch, "E7653", {"start": v(28.17, 4.82) * mm, "end": v(28.18, 4.87) * mm});
            skLineSegment(sketch, "E7654", {"start": v(28.18, 4.87) * mm, "end": v(28.2, 4.93) * mm});
            skLineSegment(sketch, "E7655", {"start": v(28.2, 4.93) * mm, "end": v(28.21, 4.99) * mm});
            skLineSegment(sketch, "E7656", {"start": v(28.21, 4.99) * mm, "end": v(28.24, 5.04) * mm});
            skLineSegment(sketch, "E7657", {"start": v(28.24, 5.04) * mm, "end": v(28.28, 5.1) * mm});
            skLineSegment(sketch, "E7658", {"start": v(28.28, 5.1) * mm, "end": v(28.32, 5.16) * mm});
            skLineSegment(sketch, "E7659", {"start": v(28.32, 5.16) * mm, "end": v(28.33, 5.19) * mm});
            skLineSegment(sketch, "E7660", {"start": v(28.33, 5.19) * mm, "end": v(28.35, 5.2) * mm});
            skLineSegment(sketch, "E7661", {"start": v(28.35, 5.2) * mm, "end": v(28.38, 5.23) * mm});
            skLineSegment(sketch, "E7662", {"start": v(28.38, 5.23) * mm, "end": v(28.4, 5.24) * mm});
            skLineSegment(sketch, "E7663", {"start": v(28.4, 5.24) * mm, "end": v(28.42, 5.25) * mm});
            skLineSegment(sketch, "E7664", {"start": v(28.42, 5.25) * mm, "end": v(28.45, 5.26) * mm});
            skLineSegment(sketch, "E7665", {"start": v(28.45, 5.26) * mm, "end": v(28.47, 5.27) * mm});
            skLineSegment(sketch, "E7666", {"start": v(28.47, 5.27) * mm, "end": v(28.5, 5.27) * mm});
            skLineSegment(sketch, "E7667", {"start": v(28.5, 5.27) * mm, "end": v(28.5, 5.27) * mm});
            skLineSegment(sketch, "E7668", {"start": v(28.5, 5.27) * mm, "end": v(28.52, 5.27) * mm});
            skLineSegment(sketch, "E7669", {"start": v(28.52, 5.27) * mm, "end": v(28.53, 5.27) * mm});
            skLineSegment(sketch, "E7670", {"start": v(28.53, 5.27) * mm, "end": v(28.54, 5.27) * mm});
            skLineSegment(sketch, "E7671", {"start": v(28.54, 5.27) * mm, "end": v(28.54, 5.26) * mm});
            skLineSegment(sketch, "E7672", {"start": v(28.54, 5.26) * mm, "end": v(28.55, 5.26) * mm});
            skLineSegment(sketch, "E7673", {"start": v(28.55, 5.26) * mm, "end": v(28.56, 5.26) * mm});
            skLineSegment(sketch, "E7674", {"start": v(28.56, 5.26) * mm, "end": v(28.57, 5.26) * mm});
            skLineSegment(sketch, "E7675", {"start": v(28.57, 5.26) * mm, "end": v(28.6, 5.25) * mm});
            skLineSegment(sketch, "E7676", {"start": v(28.6, 5.25) * mm, "end": v(28.62, 5.24) * mm});
            skLineSegment(sketch, "E7677", {"start": v(28.62, 5.24) * mm, "end": v(28.65, 5.24) * mm});
            skLineSegment(sketch, "E7678", {"start": v(28.65, 5.24) * mm, "end": v(28.68, 5.23) * mm});
            skLineSegment(sketch, "E7679", {"start": v(29.01, 8.88) * mm, "end": v(29.01, 8.85) * mm});
            skLineSegment(sketch, "E7680", {"start": v(29.01, 8.85) * mm, "end": v(29.01, 8.82) * mm});
            skLineSegment(sketch, "E7681", {"start": v(29.01, 8.82) * mm, "end": v(29.01, 8.82) * mm});
            skLineSegment(sketch, "E7682", {"start": v(29.01, 8.82) * mm, "end": v(29.01, 8.81) * mm});
            skLineSegment(sketch, "E7683", {"start": v(29.01, 8.81) * mm, "end": v(29, 8.8) * mm});
            skLineSegment(sketch, "E7684", {"start": v(29, 8.8) * mm, "end": v(29, 8.79) * mm});
            skLineSegment(sketch, "E7685", {"start": v(29, 8.79) * mm, "end": v(29, 8.77) * mm});
            skLineSegment(sketch, "E7686", {"start": v(29, 8.77) * mm, "end": v(29, 8.75) * mm});
            skLineSegment(sketch, "E7687", {"start": v(29, 8.75) * mm, "end": v(28.99, 8.58) * mm});
            skLineSegment(sketch, "E7688", {"start": v(28.99, 8.58) * mm, "end": v(28.97, 8.42) * mm});
            skLineSegment(sketch, "E7689", {"start": v(28.97, 8.42) * mm, "end": v(28.95, 8.25) * mm});
            skLineSegment(sketch, "E7690", {"start": v(28.95, 8.25) * mm, "end": v(28.93, 8.1) * mm});
            skLineSegment(sketch, "E7691", {"start": v(28.93, 8.1) * mm, "end": v(28.9, 7.94) * mm});
            skLineSegment(sketch, "E7692", {"start": v(28.9, 7.94) * mm, "end": v(28.86, 7.78) * mm});
            skLineSegment(sketch, "E7693", {"start": v(28.86, 7.78) * mm, "end": v(28.81, 7.63) * mm});
            skLineSegment(sketch, "E7694", {"start": v(28.81, 7.63) * mm, "end": v(28.76, 7.47) * mm});
            skLineSegment(sketch, "E7695", {"start": v(28.76, 7.47) * mm, "end": v(28.73, 7.42) * mm});
            skLineSegment(sketch, "E7696", {"start": v(28.73, 7.42) * mm, "end": v(28.7, 7.36) * mm});
            skLineSegment(sketch, "E7697", {"start": v(28.7, 7.36) * mm, "end": v(28.68, 7.3) * mm});
            skLineSegment(sketch, "E7698", {"start": v(28.68, 7.3) * mm, "end": v(28.65, 7.26) * mm});
            skLineSegment(sketch, "E7699", {"start": v(28.65, 7.26) * mm, "end": v(28.61, 7.2) * mm});
            skLineSegment(sketch, "E7700", {"start": v(28.61, 7.2) * mm, "end": v(28.58, 7.15) * mm});
            skLineSegment(sketch, "E7701", {"start": v(28.58, 7.15) * mm, "end": v(28.55, 7.1) * mm});
            skLineSegment(sketch, "E7702", {"start": v(28.55, 7.1) * mm, "end": v(28.51, 7.04) * mm});
            skLineSegment(sketch, "E7703", {"start": v(28.51, 7.04) * mm, "end": v(28.5, 7.01) * mm});
            skLineSegment(sketch, "E7704", {"start": v(28.5, 7.01) * mm, "end": v(28.48, 7) * mm});
            skLineSegment(sketch, "E7705", {"start": v(28.48, 7) * mm, "end": v(28.47, 6.97) * mm});
            skLineSegment(sketch, "E7706", {"start": v(28.47, 6.97) * mm, "end": v(28.45, 6.95) * mm});
            skLineSegment(sketch, "E7707", {"start": v(28.45, 6.95) * mm, "end": v(28.44, 6.92) * mm});
            skLineSegment(sketch, "E7708", {"start": v(28.44, 6.92) * mm, "end": v(28.42, 6.9) * mm});
            skLineSegment(sketch, "E7709", {"start": v(28.42, 6.9) * mm, "end": v(28.41, 6.88) * mm});
            skLineSegment(sketch, "E7710", {"start": v(28.41, 6.88) * mm, "end": v(28.4, 6.85) * mm});
            skLineSegment(sketch, "E7711", {"start": v(28.4, 6.85) * mm, "end": v(28.38, 6.83) * mm});
            skLineSegment(sketch, "E7712", {"start": v(28.38, 6.83) * mm, "end": v(28.37, 6.81) * mm});
            skLineSegment(sketch, "E7713", {"start": v(28.37, 6.81) * mm, "end": v(28.36, 6.8) * mm});
            skLineSegment(sketch, "E7714", {"start": v(28.36, 6.8) * mm, "end": v(28.34, 6.77) * mm});
            skLineSegment(sketch, "E7715", {"start": v(28.34, 6.77) * mm, "end": v(28.33, 6.75) * mm});
            skLineSegment(sketch, "E7716", {"start": v(28.33, 6.75) * mm, "end": v(28.32, 6.73) * mm});
            skLineSegment(sketch, "E7717", {"start": v(28.32, 6.73) * mm, "end": v(28.3, 6.71) * mm});
            skLineSegment(sketch, "E7718", {"start": v(28.3, 6.71) * mm, "end": v(28.29, 6.7) * mm});
            skLineSegment(sketch, "E7719", {"start": v(28.29, 6.7) * mm, "end": v(28.26, 6.65) * mm});
            skLineSegment(sketch, "E7720", {"start": v(28.26, 6.65) * mm, "end": v(28.22, 6.6) * mm});
            skLineSegment(sketch, "E7721", {"start": v(28.22, 6.6) * mm, "end": v(28.2, 6.55) * mm});
            skLineSegment(sketch, "E7722", {"start": v(28.2, 6.55) * mm, "end": v(28.16, 6.5) * mm});
            skLineSegment(sketch, "E7723", {"start": v(28.16, 6.5) * mm, "end": v(28.14, 6.46) * mm});
            skLineSegment(sketch, "E7724", {"start": v(28.14, 6.46) * mm, "end": v(28.11, 6.4) * mm});
            skLineSegment(sketch, "E7725", {"start": v(28.11, 6.4) * mm, "end": v(28.1, 6.35) * mm});
            skLineSegment(sketch, "E7726", {"start": v(28.1, 6.35) * mm, "end": v(28.08, 6.3) * mm});
            skLineSegment(sketch, "E7727", {"start": v(28.08, 6.3) * mm, "end": v(28.03, 6.16) * mm});
            skLineSegment(sketch, "E7728", {"start": v(28.03, 6.16) * mm, "end": v(27.97, 6.03) * mm});
            skLineSegment(sketch, "E7729", {"start": v(27.97, 6.03) * mm, "end": v(27.9, 5.9) * mm});
            skLineSegment(sketch, "E7730", {"start": v(27.9, 5.9) * mm, "end": v(27.82, 5.79) * mm});
            skLineSegment(sketch, "E7731", {"start": v(27.82, 5.79) * mm, "end": v(27.74, 5.67) * mm});
            skLineSegment(sketch, "E7732", {"start": v(27.74, 5.67) * mm, "end": v(27.64, 5.56) * mm});
            skLineSegment(sketch, "E7733", {"start": v(27.64, 5.56) * mm, "end": v(27.54, 5.46) * mm});
            skLineSegment(sketch, "E7734", {"start": v(27.54, 5.46) * mm, "end": v(27.44, 5.35) * mm});
            skLineSegment(sketch, "E7735", {"start": v(27.44, 5.35) * mm, "end": v(27.37, 5.29) * mm});
            skLineSegment(sketch, "E7736", {"start": v(27.37, 5.29) * mm, "end": v(27.3, 5.23) * mm});
            skLineSegment(sketch, "E7737", {"start": v(27.3, 5.23) * mm, "end": v(27.23, 5.17) * mm});
            skLineSegment(sketch, "E7738", {"start": v(27.23, 5.17) * mm, "end": v(27.15, 5.11) * mm});
            skLineSegment(sketch, "E7739", {"start": v(27.15, 5.11) * mm, "end": v(27.08, 5.06) * mm});
            skLineSegment(sketch, "E7740", {"start": v(27.08, 5.06) * mm, "end": v(27, 5) * mm});
            skLineSegment(sketch, "E7741", {"start": v(27, 5) * mm, "end": v(26.91, 4.96) * mm});
            skLineSegment(sketch, "E7742", {"start": v(26.91, 4.96) * mm, "end": v(26.83, 4.9) * mm});
            skLineSegment(sketch, "E7743", {"start": v(26.83, 4.9) * mm, "end": v(26.81, 4.9) * mm});
            skLineSegment(sketch, "E7744", {"start": v(26.81, 4.9) * mm, "end": v(26.79, 4.88) * mm});
            skLineSegment(sketch, "E7745", {"start": v(26.79, 4.88) * mm, "end": v(26.76, 4.86) * mm});
            skLineSegment(sketch, "E7746", {"start": v(26.76, 4.86) * mm, "end": v(26.74, 4.85) * mm});
            skLineSegment(sketch, "E7747", {"start": v(26.74, 4.85) * mm, "end": v(26.72, 4.84) * mm});
            skLineSegment(sketch, "E7748", {"start": v(26.72, 4.84) * mm, "end": v(26.7, 4.82) * mm});
            skLineSegment(sketch, "E7749", {"start": v(26.7, 4.82) * mm, "end": v(26.67, 4.8) * mm});
            skLineSegment(sketch, "E7750", {"start": v(26.67, 4.8) * mm, "end": v(26.65, 4.8) * mm});
            skLineSegment(sketch, "E7751", {"start": v(26.65, 4.8) * mm, "end": v(26.57, 4.74) * mm});
            skLineSegment(sketch, "E7752", {"start": v(26.57, 4.74) * mm, "end": v(26.5, 4.7) * mm});
            skLineSegment(sketch, "E7753", {"start": v(26.5, 4.7) * mm, "end": v(26.46, 4.67) * mm});
            skLineSegment(sketch, "E7754", {"start": v(26.46, 4.67) * mm, "end": v(26.43, 4.65) * mm});
            skLineSegment(sketch, "E7755", {"start": v(26.43, 4.65) * mm, "end": v(26.4, 4.64) * mm});
            skLineSegment(sketch, "E7756", {"start": v(26.4, 4.64) * mm, "end": v(26.4, 4.63) * mm});
            skLineSegment(sketch, "E7757", {"start": v(26.4, 4.63) * mm, "end": v(26.4, 4.63) * mm});
            skLineSegment(sketch, "E7758", {"start": v(26.4, 4.63) * mm, "end": v(26.28, 4.58) * mm});
            skLineSegment(sketch, "E7759", {"start": v(26.28, 4.58) * mm, "end": v(26.17, 4.54) * mm});
            skLineSegment(sketch, "E7760", {"start": v(26.17, 4.54) * mm, "end": v(26.07, 4.5) * mm});
            skLineSegment(sketch, "E7761", {"start": v(26.07, 4.5) * mm, "end": v(25.98, 4.46) * mm});
            skLineSegment(sketch, "E7762", {"start": v(25.98, 4.46) * mm, "end": v(25.9, 4.43) * mm});
            skLineSegment(sketch, "E7763", {"start": v(25.9, 4.43) * mm, "end": v(25.84, 4.4) * mm});
            skLineSegment(sketch, "E7764", {"start": v(25.84, 4.4) * mm, "end": v(25.8, 4.39) * mm});
            skLineSegment(sketch, "E7765", {"start": v(25.8, 4.39) * mm, "end": v(25.78, 4.38) * mm});
            skLineSegment(sketch, "E7766", {"start": v(25.78, 4.38) * mm, "end": v(25.76, 4.37) * mm});
            skLineSegment(sketch, "E7767", {"start": v(25.76, 4.37) * mm, "end": v(25.7, 4.36) * mm});
            skLineSegment(sketch, "E7768", {"start": v(25.7, 4.36) * mm, "end": v(25.64, 4.34) * mm});
            skLineSegment(sketch, "E7769", {"start": v(25.64, 4.34) * mm, "end": v(25.55, 4.3) * mm});
            skLineSegment(sketch, "E7770", {"start": v(25.55, 4.3) * mm, "end": v(25.44, 4.28) * mm});
            skLineSegment(sketch, "E7771", {"start": v(25.44, 4.28) * mm, "end": v(25.32, 4.24) * mm});
            skLineSegment(sketch, "E7772", {"start": v(25.32, 4.24) * mm, "end": v(25.2, 4.2) * mm});
            skLineSegment(sketch, "E7773", {"start": v(25.2, 4.2) * mm, "end": v(25.05, 4.16) * mm});
            skLineSegment(sketch, "E7774", {"start": v(25.05, 4.16) * mm, "end": v(25.05, 4.16) * mm});
            skLineSegment(sketch, "E7775", {"start": v(25.05, 4.16) * mm, "end": v(25.03, 4.15) * mm});
            skLineSegment(sketch, "E7776", {"start": v(25.03, 4.15) * mm, "end": v(25.01, 4.15) * mm});
            skLineSegment(sketch, "E7777", {"start": v(25.01, 4.15) * mm, "end": v(24.97, 4.14) * mm});
            skLineSegment(sketch, "E7778", {"start": v(24.97, 4.14) * mm, "end": v(24.9, 4.13) * mm});
            skLineSegment(sketch, "E7779", {"start": v(24.9, 4.13) * mm, "end": v(24.82, 4.11) * mm});
            skLineSegment(sketch, "E7780", {"start": v(24.82, 4.11) * mm, "end": v(24.7, 4.09) * mm});
            skLineSegment(sketch, "E7781", {"start": v(24.7, 4.09) * mm, "end": v(24.66, 4.08) * mm});
            skLineSegment(sketch, "E7782", {"start": v(24.66, 4.08) * mm, "end": v(24.61, 4.07) * mm});
            skLineSegment(sketch, "E7783", {"start": v(24.61, 4.07) * mm, "end": v(24.57, 4.06) * mm});
            skLineSegment(sketch, "E7784", {"start": v(24.57, 4.06) * mm, "end": v(24.52, 4.05) * mm});
            skLineSegment(sketch, "E7785", {"start": v(24.52, 4.05) * mm, "end": v(24.47, 4.04) * mm});
            skLineSegment(sketch, "E7786", {"start": v(24.47, 4.04) * mm, "end": v(24.43, 4.03) * mm});
            skLineSegment(sketch, "E7787", {"start": v(24.43, 4.03) * mm, "end": v(24.38, 4.02) * mm});
            skLineSegment(sketch, "E7788", {"start": v(24.38, 4.02) * mm, "end": v(24.33, 4) * mm});
            skLineSegment(sketch, "E7789", {"start": v(24.33, 4) * mm, "end": v(24.3, 4) * mm});
            skLineSegment(sketch, "E7790", {"start": v(24.3, 4) * mm, "end": v(24.28, 4) * mm});
            skLineSegment(sketch, "E7791", {"start": v(24.28, 4) * mm, "end": v(24.25, 4) * mm});
            skLineSegment(sketch, "E7792", {"start": v(24.25, 4) * mm, "end": v(24.23, 3.99) * mm});
            skLineSegment(sketch, "E7793", {"start": v(24.23, 3.99) * mm, "end": v(24.2, 3.99) * mm});
            skLineSegment(sketch, "E7794", {"start": v(24.2, 3.99) * mm, "end": v(24.17, 3.98) * mm});
            skLineSegment(sketch, "E7795", {"start": v(24.17, 3.98) * mm, "end": v(24.15, 3.98) * mm});
            skLineSegment(sketch, "E7796", {"start": v(24.15, 3.98) * mm, "end": v(24.12, 3.98) * mm});
            skLineSegment(sketch, "E7797", {"start": v(24.12, 3.98) * mm, "end": v(24.07, 3.98) * mm});
            skLineSegment(sketch, "E7798", {"start": v(24.07, 3.98) * mm, "end": v(24.02, 3.99) * mm});
            skLineSegment(sketch, "E7799", {"start": v(24.02, 3.99) * mm, "end": v(23.97, 4) * mm});
            skLineSegment(sketch, "E7800", {"start": v(23.97, 4) * mm, "end": v(23.92, 4) * mm});
            skLineSegment(sketch, "E7801", {"start": v(23.92, 4) * mm, "end": v(23.88, 4.02) * mm});
            skLineSegment(sketch, "E7802", {"start": v(23.88, 4.02) * mm, "end": v(23.83, 4.03) * mm});
            skLineSegment(sketch, "E7803", {"start": v(23.83, 4.03) * mm, "end": v(23.78, 4.05) * mm});
            skLineSegment(sketch, "E7804", {"start": v(23.78, 4.05) * mm, "end": v(23.74, 4.07) * mm});
            skLineSegment(sketch, "E7805", {"start": v(23.74, 4.07) * mm, "end": v(23.72, 4.08) * mm});
            skLineSegment(sketch, "E7806", {"start": v(23.72, 4.08) * mm, "end": v(23.7, 4.09) * mm});
            skLineSegment(sketch, "E7807", {"start": v(23.7, 4.09) * mm, "end": v(23.68, 4.1) * mm});
            skLineSegment(sketch, "E7808", {"start": v(23.68, 4.1) * mm, "end": v(23.66, 4.1) * mm});
            skLineSegment(sketch, "E7809", {"start": v(23.66, 4.1) * mm, "end": v(23.63, 4.1) * mm});
            skLineSegment(sketch, "E7810", {"start": v(23.63, 4.1) * mm, "end": v(23.61, 4.1) * mm});
            skLineSegment(sketch, "E7811", {"start": v(23.61, 4.1) * mm, "end": v(23.59, 4.1) * mm});
            skLineSegment(sketch, "E7812", {"start": v(23.59, 4.1) * mm, "end": v(23.57, 4.1) * mm});
            skLineSegment(sketch, "E7813", {"start": v(23.57, 4.1) * mm, "end": v(23.56, 4.1) * mm});
            skLineSegment(sketch, "E7814", {"start": v(23.56, 4.1) * mm, "end": v(23.56, 4.1) * mm});
            skLineSegment(sketch, "E7815", {"start": v(23.56, 4.1) * mm, "end": v(23.55, 4.1) * mm});
            skLineSegment(sketch, "E7816", {"start": v(23.55, 4.1) * mm, "end": v(23.55, 4.1) * mm});
            skLineSegment(sketch, "E7817", {"start": v(23.55, 4.1) * mm, "end": v(23.54, 4.1) * mm});
            skLineSegment(sketch, "E7818", {"start": v(23.54, 4.1) * mm, "end": v(23.54, 4.1) * mm});
            skLineSegment(sketch, "E7819", {"start": v(23.54, 4.1) * mm, "end": v(23.42, 4.1) * mm});
            skLineSegment(sketch, "E7820", {"start": v(23.42, 4.1) * mm, "end": v(23.3, 4.1) * mm});
            skLineSegment(sketch, "E7821", {"start": v(23.3, 4.1) * mm, "end": v(23.17, 4.11) * mm});
            skLineSegment(sketch, "E7822", {"start": v(23.17, 4.11) * mm, "end": v(23.05, 4.13) * mm});
            skLineSegment(sketch, "E7823", {"start": v(23.05, 4.13) * mm, "end": v(22.93, 4.15) * mm});
            skLineSegment(sketch, "E7824", {"start": v(22.93, 4.15) * mm, "end": v(22.81, 4.18) * mm});
            skLineSegment(sketch, "E7825", {"start": v(22.81, 4.18) * mm, "end": v(22.7, 4.2) * mm});
            skLineSegment(sketch, "E7826", {"start": v(22.7, 4.2) * mm, "end": v(22.58, 4.23) * mm});
            skLineSegment(sketch, "E7827", {"start": v(22.58, 4.23) * mm, "end": v(22.54, 4.24) * mm});
            skLineSegment(sketch, "E7828", {"start": v(22.54, 4.24) * mm, "end": v(22.5, 4.25) * mm});
            skLineSegment(sketch, "E7829", {"start": v(22.5, 4.25) * mm, "end": v(22.47, 4.26) * mm});
            skLineSegment(sketch, "E7830", {"start": v(22.47, 4.26) * mm, "end": v(22.43, 4.27) * mm});
            skLineSegment(sketch, "E7831", {"start": v(22.43, 4.27) * mm, "end": v(22.4, 4.28) * mm});
            skLineSegment(sketch, "E7832", {"start": v(22.4, 4.28) * mm, "end": v(22.35, 4.29) * mm});
            skLineSegment(sketch, "E7833", {"start": v(22.35, 4.29) * mm, "end": v(22.31, 4.3) * mm});
            skLineSegment(sketch, "E7834", {"start": v(22.31, 4.3) * mm, "end": v(22.27, 4.3) * mm});
            skLineSegment(sketch, "E7835", {"start": v(22.27, 4.3) * mm, "end": v(22.2, 4.32) * mm});
            skLineSegment(sketch, "E7836", {"start": v(22.2, 4.32) * mm, "end": v(22.13, 4.34) * mm});
            skLineSegment(sketch, "E7837", {"start": v(22.13, 4.34) * mm, "end": v(22.06, 4.36) * mm});
            skLineSegment(sketch, "E7838", {"start": v(22.06, 4.36) * mm, "end": v(21.99, 4.38) * mm});
            skLineSegment(sketch, "E7839", {"start": v(21.99, 4.38) * mm, "end": v(21.92, 4.4) * mm});
            skLineSegment(sketch, "E7840", {"start": v(21.92, 4.4) * mm, "end": v(21.85, 4.42) * mm});
            skLineSegment(sketch, "E7841", {"start": v(21.85, 4.42) * mm, "end": v(21.78, 4.44) * mm});
            skLineSegment(sketch, "E7842", {"start": v(21.78, 4.44) * mm, "end": v(21.7, 4.46) * mm});
            skLineSegment(sketch, "E7843", {"start": v(21.7, 4.46) * mm, "end": v(21.66, 4.48) * mm});
            skLineSegment(sketch, "E7844", {"start": v(21.66, 4.48) * mm, "end": v(21.62, 4.5) * mm});
            skLineSegment(sketch, "E7845", {"start": v(21.62, 4.5) * mm, "end": v(21.57, 4.52) * mm});
            skLineSegment(sketch, "E7846", {"start": v(21.57, 4.52) * mm, "end": v(21.52, 4.54) * mm});
            skLineSegment(sketch, "E7847", {"start": v(21.52, 4.54) * mm, "end": v(21.48, 4.56) * mm});
            skLineSegment(sketch, "E7848", {"start": v(21.48, 4.56) * mm, "end": v(21.43, 4.59) * mm});
            skLineSegment(sketch, "E7849", {"start": v(21.43, 4.59) * mm, "end": v(21.38, 4.62) * mm});
            skLineSegment(sketch, "E7850", {"start": v(21.38, 4.62) * mm, "end": v(21.34, 4.64) * mm});
            skLineSegment(sketch, "E7851", {"start": v(21.34, 4.64) * mm, "end": v(21.32, 4.65) * mm});
            skLineSegment(sketch, "E7852", {"start": v(21.32, 4.65) * mm, "end": v(21.3, 4.67) * mm});
            skLineSegment(sketch, "E7853", {"start": v(21.3, 4.67) * mm, "end": v(21.28, 4.68) * mm});
            skLineSegment(sketch, "E7854", {"start": v(21.28, 4.68) * mm, "end": v(21.26, 4.69) * mm});
            skLineSegment(sketch, "E7855", {"start": v(21.26, 4.69) * mm, "end": v(21.24, 4.7) * mm});
            skLineSegment(sketch, "E7856", {"start": v(21.24, 4.7) * mm, "end": v(21.22, 4.71) * mm});
            skLineSegment(sketch, "E7857", {"start": v(21.22, 4.71) * mm, "end": v(21.2, 4.72) * mm});
            skLineSegment(sketch, "E7858", {"start": v(21.2, 4.72) * mm, "end": v(21.17, 4.73) * mm});
            skLineSegment(sketch, "E7859", {"start": v(21.17, 4.73) * mm, "end": v(21.09, 4.78) * mm});
            skLineSegment(sketch, "E7860", {"start": v(21.09, 4.78) * mm, "end": v(21, 4.83) * mm});
            skLineSegment(sketch, "E7861", {"start": v(21, 4.83) * mm, "end": v(20.9, 4.88) * mm});
            skLineSegment(sketch, "E7862", {"start": v(20.9, 4.88) * mm, "end": v(20.82, 4.92) * mm});
            skLineSegment(sketch, "E7863", {"start": v(20.82, 4.92) * mm, "end": v(20.73, 4.97) * mm});
            skLineSegment(sketch, "E7864", {"start": v(20.73, 4.97) * mm, "end": v(20.64, 5.02) * mm});
            skLineSegment(sketch, "E7865", {"start": v(20.64, 5.02) * mm, "end": v(20.55, 5.07) * mm});
            skLineSegment(sketch, "E7866", {"start": v(20.55, 5.07) * mm, "end": v(20.47, 5.11) * mm});
            skLineSegment(sketch, "E7867", {"start": v(20.47, 5.11) * mm, "end": v(20.46, 5.12) * mm});
            skLineSegment(sketch, "E7868", {"start": v(20.46, 5.12) * mm, "end": v(20.46, 5.12) * mm});
            skLineSegment(sketch, "E7869", {"start": v(20.46, 5.12) * mm, "end": v(20.45, 5.13) * mm});
            skLineSegment(sketch, "E7870", {"start": v(20.45, 5.13) * mm, "end": v(20.45, 5.13) * mm});
            skLineSegment(sketch, "E7871", {"start": v(20.45, 5.13) * mm, "end": v(20.44, 5.13) * mm});
            skLineSegment(sketch, "E7872", {"start": v(20.44, 5.13) * mm, "end": v(20.44, 5.14) * mm});
            skLineSegment(sketch, "E7873", {"start": v(20.44, 5.14) * mm, "end": v(20.43, 5.14) * mm});
            skLineSegment(sketch, "E7874", {"start": v(20.43, 5.14) * mm, "end": v(20.4, 5.17) * mm});
            skLineSegment(sketch, "E7875", {"start": v(20.4, 5.17) * mm, "end": v(20.38, 5.2) * mm});
            skLineSegment(sketch, "E7876", {"start": v(20.38, 5.2) * mm, "end": v(20.35, 5.24) * mm});
            skLineSegment(sketch, "E7877", {"start": v(20.35, 5.24) * mm, "end": v(20.32, 5.27) * mm});
            skLineSegment(sketch, "E7878", {"start": v(20.32, 5.27) * mm, "end": v(20.29, 5.3) * mm});
            skLineSegment(sketch, "E7879", {"start": v(20.29, 5.3) * mm, "end": v(20.26, 5.33) * mm});
            skLineSegment(sketch, "E7880", {"start": v(20.26, 5.33) * mm, "end": v(20.23, 5.36) * mm});
            skLineSegment(sketch, "E7881", {"start": v(20.23, 5.36) * mm, "end": v(20.2, 5.39) * mm});
            skLineSegment(sketch, "E7882", {"start": v(20.2, 5.39) * mm, "end": v(20.13, 5.46) * mm});
            skLineSegment(sketch, "E7883", {"start": v(20.13, 5.46) * mm, "end": v(20.07, 5.53) * mm});
            skLineSegment(sketch, "E7884", {"start": v(20.07, 5.53) * mm, "end": v(20, 5.6) * mm});
            skLineSegment(sketch, "E7885", {"start": v(20, 5.6) * mm, "end": v(19.93, 5.67) * mm});
            skLineSegment(sketch, "E7886", {"start": v(19.93, 5.67) * mm, "end": v(19.87, 5.75) * mm});
            skLineSegment(sketch, "E7887", {"start": v(19.87, 5.75) * mm, "end": v(19.8, 5.82) * mm});
            skLineSegment(sketch, "E7888", {"start": v(19.8, 5.82) * mm, "end": v(19.74, 5.9) * mm});
            skLineSegment(sketch, "E7889", {"start": v(19.74, 5.9) * mm, "end": v(19.68, 5.97) * mm});
            skLineSegment(sketch, "E7890", {"start": v(19.68, 5.97) * mm, "end": v(19.64, 6.03) * mm});
            skLineSegment(sketch, "E7891", {"start": v(19.64, 6.03) * mm, "end": v(19.6, 6.09) * mm});
            skLineSegment(sketch, "E7892", {"start": v(19.6, 6.09) * mm, "end": v(19.56, 6.15) * mm});
            skLineSegment(sketch, "E7893", {"start": v(19.56, 6.15) * mm, "end": v(19.52, 6.2) * mm});
            skLineSegment(sketch, "E7894", {"start": v(19.52, 6.2) * mm, "end": v(19.49, 6.27) * mm});
            skLineSegment(sketch, "E7895", {"start": v(19.49, 6.27) * mm, "end": v(19.46, 6.33) * mm});
            skLineSegment(sketch, "E7896", {"start": v(19.46, 6.33) * mm, "end": v(19.42, 6.4) * mm});
            skLineSegment(sketch, "E7897", {"start": v(19.42, 6.4) * mm, "end": v(19.39, 6.46) * mm});
            skLineSegment(sketch, "E7898", {"start": v(19.39, 6.46) * mm, "end": v(19.38, 6.49) * mm});
            skLineSegment(sketch, "E7899", {"start": v(19.38, 6.49) * mm, "end": v(19.37, 6.5) * mm});
            skLineSegment(sketch, "E7900", {"start": v(19.37, 6.5) * mm, "end": v(19.36, 6.52) * mm});
            skLineSegment(sketch, "E7901", {"start": v(19.36, 6.52) * mm, "end": v(19.35, 6.53) * mm});
            skLineSegment(sketch, "E7902", {"start": v(19.35, 6.53) * mm, "end": v(19.35, 6.53) * mm});
            skLineSegment(sketch, "E7903", {"start": v(19.35, 6.53) * mm, "end": v(19.35, 6.54) * mm});
            skLineSegment(sketch, "E7904", {"start": v(19.35, 6.54) * mm, "end": v(19.35, 6.54) * mm});
            skLineSegment(sketch, "E7905", {"start": v(19.35, 6.54) * mm, "end": v(19.33, 6.57) * mm});
            skLineSegment(sketch, "E7906", {"start": v(19.33, 6.57) * mm, "end": v(19.32, 6.6) * mm});
            skLineSegment(sketch, "E7907", {"start": v(19.32, 6.6) * mm, "end": v(19.3, 6.63) * mm});
            skLineSegment(sketch, "E7908", {"start": v(19.3, 6.63) * mm, "end": v(19.29, 6.66) * mm});
            skLineSegment(sketch, "E7909", {"start": v(19.29, 6.66) * mm, "end": v(19.27, 6.7) * mm});
            skLineSegment(sketch, "E7910", {"start": v(19.27, 6.7) * mm, "end": v(19.26, 6.72) * mm});
            skLineSegment(sketch, "E7911", {"start": v(19.26, 6.72) * mm, "end": v(19.25, 6.75) * mm});
            skLineSegment(sketch, "E7912", {"start": v(19.25, 6.75) * mm, "end": v(19.24, 6.77) * mm});
            skLineSegment(sketch, "E7913", {"start": v(19.24, 6.77) * mm, "end": v(19.24, 6.77) * mm});
            skLineSegment(sketch, "E7914", {"start": v(19.24, 6.77) * mm, "end": v(19.23, 6.77) * mm});
            skLineSegment(sketch, "E7915", {"start": v(19.23, 6.77) * mm, "end": v(19.23, 6.78) * mm});
            skLineSegment(sketch, "E7916", {"start": v(19.23, 6.78) * mm, "end": v(19.21, 6.78) * mm});
            skLineSegment(sketch, "E7917", {"start": v(19.21, 6.78) * mm, "end": v(19.2, 6.78) * mm});
            skLineSegment(sketch, "E7918", {"start": v(19.2, 6.78) * mm, "end": v(19.16, 6.8) * mm});
            skLineSegment(sketch, "E7919", {"start": v(19.16, 6.8) * mm, "end": v(19.12, 6.8) * mm});
            skLineSegment(sketch, "E7920", {"start": v(19.12, 6.8) * mm, "end": v(19.1, 6.81) * mm});
            skLineSegment(sketch, "E7921", {"start": v(19.1, 6.81) * mm, "end": v(19.08, 6.82) * mm});
            skLineSegment(sketch, "E7922", {"start": v(19.08, 6.82) * mm, "end": v(19.07, 6.82) * mm});
            skLineSegment(sketch, "E7923", {"start": v(19.07, 6.82) * mm, "end": v(19.07, 6.82) * mm});
            skLineSegment(sketch, "E7924", {"start": v(19.07, 6.82) * mm, "end": v(19.05, 6.88) * mm});
            skLineSegment(sketch, "E7925", {"start": v(19.05, 6.88) * mm, "end": v(19.03, 6.94) * mm});
            skLineSegment(sketch, "E7926", {"start": v(19.03, 6.94) * mm, "end": v(19, 7) * mm});
            skLineSegment(sketch, "E7927", {"start": v(19, 7) * mm, "end": v(18.99, 7.05) * mm});
            skLineSegment(sketch, "E7928", {"start": v(18.99, 7.05) * mm, "end": v(18.97, 7.1) * mm});
            skLineSegment(sketch, "E7929", {"start": v(18.97, 7.1) * mm, "end": v(18.95, 7.15) * mm});
            skLineSegment(sketch, "E7930", {"start": v(18.95, 7.15) * mm, "end": v(18.94, 7.2) * mm});
            skLineSegment(sketch, "E7931", {"start": v(18.94, 7.2) * mm, "end": v(18.93, 7.23) * mm});
            skLineSegment(sketch, "E7932", {"start": v(18.93, 7.23) * mm, "end": v(18.92, 7.26) * mm});
            skLineSegment(sketch, "E7933", {"start": v(18.92, 7.26) * mm, "end": v(18.9, 7.32) * mm});
            skLineSegment(sketch, "E7934", {"start": v(18.9, 7.32) * mm, "end": v(18.87, 7.39) * mm});
            skLineSegment(sketch, "E7935", {"start": v(18.87, 7.39) * mm, "end": v(18.85, 7.47) * mm});
            skLineSegment(sketch, "E7936", {"start": v(18.85, 7.47) * mm, "end": v(18.82, 7.56) * mm});
            skLineSegment(sketch, "E7937", {"start": v(18.82, 7.56) * mm, "end": v(18.78, 7.66) * mm});
            skLineSegment(sketch, "E7938", {"start": v(18.78, 7.66) * mm, "end": v(18.75, 7.76) * mm});
            skLineSegment(sketch, "E7939", {"start": v(18.75, 7.76) * mm, "end": v(18.71, 7.86) * mm});
            skLineSegment(sketch, "E7940", {"start": v(18.71, 7.86) * mm, "end": v(18.71, 7.86) * mm});
            skLineSegment(sketch, "E7941", {"start": v(18.71, 7.86) * mm, "end": v(18.71, 7.87) * mm});
            skLineSegment(sketch, "E7942", {"start": v(18.71, 7.87) * mm, "end": v(18.7, 7.9) * mm});
            skLineSegment(sketch, "E7943", {"start": v(18.7, 7.9) * mm, "end": v(18.7, 7.92) * mm});
            skLineSegment(sketch, "E7944", {"start": v(18.7, 7.92) * mm, "end": v(18.69, 7.96) * mm});
            skLineSegment(sketch, "E7945", {"start": v(18.69, 7.96) * mm, "end": v(18.67, 8.03) * mm});
            skLineSegment(sketch, "E7946", {"start": v(18.67, 8.03) * mm, "end": v(18.65, 8.1) * mm});
            skLineSegment(sketch, "E7947", {"start": v(18.65, 8.1) * mm, "end": v(18.63, 8.18) * mm});
            skLineSegment(sketch, "E7948", {"start": v(18.63, 8.18) * mm, "end": v(18.62, 8.25) * mm});
            skLineSegment(sketch, "E7949", {"start": v(18.62, 8.25) * mm, "end": v(18.6, 8.32) * mm});
            skLineSegment(sketch, "E7950", {"start": v(18.6, 8.32) * mm, "end": v(18.6, 8.4) * mm});
            skLineSegment(sketch, "E7951", {"start": v(18.6, 8.4) * mm, "end": v(18.59, 8.46) * mm});
            skLineSegment(sketch, "E7952", {"start": v(18.59, 8.46) * mm, "end": v(18.58, 8.54) * mm});
            skLineSegment(sketch, "E7953", {"start": v(18.58, 8.54) * mm, "end": v(18.58, 8.61) * mm});
            skLineSegment(sketch, "E7954", {"start": v(18.58, 8.61) * mm, "end": v(18.58, 8.68) * mm});
            skLineSegment(sketch, "E7955", {"start": v(18.58, 8.68) * mm, "end": v(18.58, 8.77) * mm});
            skLineSegment(sketch, "E7956", {"start": v(18.58, 8.77) * mm, "end": v(18.58, 8.86) * mm});
            skLineSegment(sketch, "E7957", {"start": v(18.58, 8.86) * mm, "end": v(18.59, 8.95) * mm});
            skLineSegment(sketch, "E7958", {"start": v(18.59, 8.95) * mm, "end": v(18.6, 9.04) * mm});
            skLineSegment(sketch, "E7959", {"start": v(18.6, 9.04) * mm, "end": v(18.6, 9.13) * mm});
            skLineSegment(sketch, "E7960", {"start": v(18.6, 9.13) * mm, "end": v(18.6, 9.22) * mm});
            skLineSegment(sketch, "E7961", {"start": v(18.6, 9.22) * mm, "end": v(18.61, 9.3) * mm});
            skLineSegment(sketch, "E7962", {"start": v(18.61, 9.3) * mm, "end": v(18.62, 9.4) * mm});
            skLineSegment(sketch, "E7963", {"start": v(18.62, 9.4) * mm, "end": v(18.62, 9.42) * mm});
            skLineSegment(sketch, "E7964", {"start": v(18.62, 9.42) * mm, "end": v(18.63, 9.44) * mm});
            skLineSegment(sketch, "E7965", {"start": v(18.63, 9.44) * mm, "end": v(18.63, 9.46) * mm});
            skLineSegment(sketch, "E7966", {"start": v(18.63, 9.46) * mm, "end": v(18.63, 9.47) * mm});
            skLineSegment(sketch, "E7967", {"start": v(18.63, 9.47) * mm, "end": v(18.63, 9.47) * mm});
            skLineSegment(sketch, "E7968", {"start": v(18.63, 9.47) * mm, "end": v(18.63, 9.48) * mm});
            skLineSegment(sketch, "E7969", {"start": v(18.63, 9.48) * mm, "end": v(18.63, 9.48) * mm});
            skLineSegment(sketch, "E7970", {"start": v(18.63, 9.48) * mm, "end": v(18.63, 9.51) * mm});
            skLineSegment(sketch, "E7971", {"start": v(18.63, 9.51) * mm, "end": v(18.64, 9.55) * mm});
            skLineSegment(sketch, "E7972", {"start": v(18.64, 9.55) * mm, "end": v(18.64, 9.59) * mm});
            skLineSegment(sketch, "E7973", {"start": v(18.64, 9.59) * mm, "end": v(18.64, 9.62) * mm});
            skLineSegment(sketch, "E7974", {"start": v(18.64, 9.62) * mm, "end": v(18.64, 9.65) * mm});
            skLineSegment(sketch, "E7975", {"start": v(18.64, 9.65) * mm, "end": v(18.65, 9.68) * mm});
            skLineSegment(sketch, "E7976", {"start": v(18.65, 9.68) * mm, "end": v(18.65, 9.7) * mm});
            skLineSegment(sketch, "E7977", {"start": v(18.65, 9.7) * mm, "end": v(18.65, 9.72) * mm});
            skLineSegment(sketch, "E7978", {"start": v(18.65, 9.72) * mm, "end": v(18.65, 9.74) * mm});
            skLineSegment(sketch, "E7979", {"start": v(18.65, 9.74) * mm, "end": v(18.65, 9.77) * mm});
            skLineSegment(sketch, "E7980", {"start": v(18.65, 9.77) * mm, "end": v(18.66, 9.82) * mm});
            skLineSegment(sketch, "E7981", {"start": v(18.66, 9.82) * mm, "end": v(18.66, 9.87) * mm});
            skLineSegment(sketch, "E7982", {"start": v(18.66, 9.87) * mm, "end": v(18.66, 9.93) * mm});
            skLineSegment(sketch, "E7983", {"start": v(18.66, 9.93) * mm, "end": v(18.67, 10) * mm});
            skLineSegment(sketch, "E7984", {"start": v(18.67, 10) * mm, "end": v(18.67, 10.07) * mm});
            skLineSegment(sketch, "E7985", {"start": v(18.67, 10.07) * mm, "end": v(18.68, 10.14) * mm});
            skLineSegment(sketch, "E7986", {"start": v(18.68, 10.14) * mm, "end": v(18.68, 10.14) * mm});
            skLineSegment(sketch, "E7987", {"start": v(18.68, 10.14) * mm, "end": v(18.68, 10.15) * mm});
            skLineSegment(sketch, "E7988", {"start": v(18.68, 10.15) * mm, "end": v(18.68, 10.15) * mm});
            skLineSegment(sketch, "E7989", {"start": v(18.68, 10.15) * mm, "end": v(18.68, 10.17) * mm});
            skLineSegment(sketch, "E7990", {"start": v(18.68, 10.17) * mm, "end": v(18.69, 10.19) * mm});
            skLineSegment(sketch, "E7991", {"start": v(18.69, 10.19) * mm, "end": v(18.69, 10.22) * mm});
            skLineSegment(sketch, "E7992", {"start": v(18.69, 10.22) * mm, "end": v(18.7, 10.26) * mm});
            skLineSegment(sketch, "E7993", {"start": v(18.7, 10.26) * mm, "end": v(18.7, 10.32) * mm});
            skLineSegment(sketch, "E7994", {"start": v(18.7, 10.32) * mm, "end": v(18.7, 10.34) * mm});
            skLineSegment(sketch, "E7995", {"start": v(18.7, 10.34) * mm, "end": v(18.71, 10.36) * mm});
            skLineSegment(sketch, "E7996", {"start": v(18.71, 10.36) * mm, "end": v(18.72, 10.38) * mm});
            skLineSegment(sketch, "E7997", {"start": v(18.72, 10.38) * mm, "end": v(18.72, 10.4) * mm});
            skLineSegment(sketch, "E7998", {"start": v(18.72, 10.4) * mm, "end": v(18.73, 10.42) * mm});
            skLineSegment(sketch, "E7999", {"start": v(18.73, 10.42) * mm, "end": v(18.74, 10.44) * mm});
            skLineSegment(sketch, "E8000", {"start": v(18.74, 10.44) * mm, "end": v(18.75, 10.46) * mm});
            skLineSegment(sketch, "E8001", {"start": v(18.75, 10.46) * mm, "end": v(18.75, 10.48) * mm});
            skLineSegment(sketch, "E8002", {"start": v(18.75, 10.48) * mm, "end": v(18.76, 10.5) * mm});
            skLineSegment(sketch, "E8003", {"start": v(18.76, 10.5) * mm, "end": v(18.77, 10.52) * mm});
            skLineSegment(sketch, "E8004", {"start": v(18.77, 10.52) * mm, "end": v(18.77, 10.53) * mm});
            skLineSegment(sketch, "E8005", {"start": v(18.77, 10.53) * mm, "end": v(18.78, 10.55) * mm});
            skLineSegment(sketch, "E8006", {"start": v(18.78, 10.55) * mm, "end": v(18.78, 10.57) * mm});
            skLineSegment(sketch, "E8007", {"start": v(18.78, 10.57) * mm, "end": v(18.79, 10.59) * mm});
            skLineSegment(sketch, "E8008", {"start": v(18.79, 10.59) * mm, "end": v(18.8, 10.6) * mm});
            skLineSegment(sketch, "E8009", {"start": v(18.8, 10.6) * mm, "end": v(18.8, 10.62) * mm});
            skLineSegment(sketch, "E8010", {"start": v(18.8, 10.62) * mm, "end": v(18.8, 10.65) * mm});
            skLineSegment(sketch, "E8011", {"start": v(18.8, 10.65) * mm, "end": v(18.82, 10.68) * mm});
            skLineSegment(sketch, "E8012", {"start": v(18.82, 10.68) * mm, "end": v(18.82, 10.72) * mm});
            skLineSegment(sketch, "E8013", {"start": v(18.82, 10.72) * mm, "end": v(18.83, 10.75) * mm});
            skLineSegment(sketch, "E8014", {"start": v(18.83, 10.75) * mm, "end": v(18.84, 10.78) * mm});
            skLineSegment(sketch, "E8015", {"start": v(18.84, 10.78) * mm, "end": v(18.85, 10.81) * mm});
            skLineSegment(sketch, "E8016", {"start": v(18.85, 10.81) * mm, "end": v(18.85, 10.85) * mm});
            skLineSegment(sketch, "E8017", {"start": v(18.85, 10.85) * mm, "end": v(18.86, 10.88) * mm});
            skLineSegment(sketch, "E8018", {"start": v(18.86, 10.88) * mm, "end": v(18.87, 10.9) * mm});
            skLineSegment(sketch, "E8019", {"start": v(18.87, 10.9) * mm, "end": v(18.87, 10.93) * mm});
            skLineSegment(sketch, "E8020", {"start": v(18.87, 10.93) * mm, "end": v(18.88, 10.95) * mm});
            skLineSegment(sketch, "E8021", {"start": v(18.88, 10.95) * mm, "end": v(18.88, 10.98) * mm});
            skLineSegment(sketch, "E8022", {"start": v(18.88, 10.98) * mm, "end": v(18.89, 11) * mm});
            skLineSegment(sketch, "E8023", {"start": v(18.89, 11) * mm, "end": v(18.9, 11.03) * mm});
            skLineSegment(sketch, "E8024", {"start": v(18.9, 11.03) * mm, "end": v(18.9, 11.05) * mm});
            skLineSegment(sketch, "E8025", {"start": v(18.9, 11.05) * mm, "end": v(18.9, 11.08) * mm});
            skLineSegment(sketch, "E8026", {"start": v(18.9, 11.08) * mm, "end": v(18.94, 11.18) * mm});
            skLineSegment(sketch, "E8027", {"start": v(18.94, 11.18) * mm, "end": v(18.97, 11.28) * mm});
            skLineSegment(sketch, "E8028", {"start": v(18.97, 11.28) * mm, "end": v(19.02, 11.37) * mm});
            skLineSegment(sketch, "E8029", {"start": v(19.02, 11.37) * mm, "end": v(19.07, 11.45) * mm});
            skLineSegment(sketch, "E8030", {"start": v(19.07, 11.45) * mm, "end": v(19.13, 11.53) * mm});
            skLineSegment(sketch, "E8031", {"start": v(19.13, 11.53) * mm, "end": v(19.18, 11.61) * mm});
            skLineSegment(sketch, "E8032", {"start": v(19.18, 11.61) * mm, "end": v(19.24, 11.68) * mm});
            skLineSegment(sketch, "E8033", {"start": v(19.24, 11.68) * mm, "end": v(19.3, 11.75) * mm});
            skLineSegment(sketch, "E8034", {"start": v(19.3, 11.75) * mm, "end": v(19.34, 11.8) * mm});
            skLineSegment(sketch, "E8035", {"start": v(19.34, 11.8) * mm, "end": v(19.38, 11.84) * mm});
            skLineSegment(sketch, "E8036", {"start": v(19.38, 11.84) * mm, "end": v(19.42, 11.88) * mm});
            skLineSegment(sketch, "E8037", {"start": v(19.42, 11.88) * mm, "end": v(19.46, 11.92) * mm});
            skLineSegment(sketch, "E8038", {"start": v(19.46, 11.92) * mm, "end": v(19.5, 11.96) * mm});
            skLineSegment(sketch, "E8039", {"start": v(19.5, 11.96) * mm, "end": v(19.54, 12) * mm});
            skLineSegment(sketch, "E8040", {"start": v(19.54, 12) * mm, "end": v(19.58, 12.05) * mm});
            skLineSegment(sketch, "E8041", {"start": v(19.58, 12.05) * mm, "end": v(19.62, 12.09) * mm});
            skLineSegment(sketch, "E8042", {"start": v(19.62, 12.09) * mm, "end": v(19.67, 12.14) * mm});
            skLineSegment(sketch, "E8043", {"start": v(19.67, 12.14) * mm, "end": v(19.73, 12.2) * mm});
            skLineSegment(sketch, "E8044", {"start": v(19.73, 12.2) * mm, "end": v(19.78, 12.26) * mm});
            skLineSegment(sketch, "E8045", {"start": v(19.78, 12.26) * mm, "end": v(19.83, 12.31) * mm});
            skLineSegment(sketch, "E8046", {"start": v(19.83, 12.31) * mm, "end": v(19.89, 12.37) * mm});
            skLineSegment(sketch, "E8047", {"start": v(19.89, 12.37) * mm, "end": v(19.94, 12.43) * mm});
            skLineSegment(sketch, "E8048", {"start": v(19.94, 12.43) * mm, "end": v(20, 12.49) * mm});
            skLineSegment(sketch, "E8049", {"start": v(20, 12.49) * mm, "end": v(20.04, 12.55) * mm});
            skLineSegment(sketch, "E8050", {"start": v(20.04, 12.55) * mm, "end": v(20.09, 12.6) * mm});
            skLineSegment(sketch, "E8051", {"start": v(20.09, 12.6) * mm, "end": v(20.14, 12.65) * mm});
            skLineSegment(sketch, "E8052", {"start": v(20.14, 12.65) * mm, "end": v(20.2, 12.7) * mm});
            skLineSegment(sketch, "E8053", {"start": v(20.2, 12.7) * mm, "end": v(20.25, 12.75) * mm});
            skLineSegment(sketch, "E8054", {"start": v(20.25, 12.75) * mm, "end": v(20.3, 12.79) * mm});
            skLineSegment(sketch, "E8055", {"start": v(20.3, 12.79) * mm, "end": v(20.36, 12.83) * mm});
            skLineSegment(sketch, "E8056", {"start": v(20.36, 12.83) * mm, "end": v(20.42, 12.87) * mm});
            skLineSegment(sketch, "E8057", {"start": v(20.42, 12.87) * mm, "end": v(20.49, 12.91) * mm});
            skLineSegment(sketch, "E8058", {"start": v(20.49, 12.91) * mm, "end": v(20.52, 12.94) * mm});
            skLineSegment(sketch, "E8059", {"start": v(20.52, 12.94) * mm, "end": v(20.55, 12.96) * mm});
            skLineSegment(sketch, "E8060", {"start": v(20.55, 12.96) * mm, "end": v(20.59, 12.98) * mm});
            skLineSegment(sketch, "E8061", {"start": v(20.59, 12.98) * mm, "end": v(20.62, 13) * mm});
            skLineSegment(sketch, "E8062", {"start": v(20.62, 13) * mm, "end": v(20.65, 13.03) * mm});
            skLineSegment(sketch, "E8063", {"start": v(20.65, 13.03) * mm, "end": v(20.69, 13.06) * mm});
            skLineSegment(sketch, "E8064", {"start": v(20.69, 13.06) * mm, "end": v(20.72, 13.08) * mm});
            skLineSegment(sketch, "E8065", {"start": v(20.72, 13.08) * mm, "end": v(20.75, 13.1) * mm});
            skLineSegment(sketch, "E8066", {"start": v(20.75, 13.1) * mm, "end": v(20.78, 13.13) * mm});
            skLineSegment(sketch, "E8067", {"start": v(20.78, 13.13) * mm, "end": v(20.8, 13.14) * mm});
            skLineSegment(sketch, "E8068", {"start": v(20.8, 13.14) * mm, "end": v(20.82, 13.16) * mm});
            skLineSegment(sketch, "E8069", {"start": v(20.82, 13.16) * mm, "end": v(20.84, 13.18) * mm});
            skLineSegment(sketch, "E8070", {"start": v(20.84, 13.18) * mm, "end": v(20.86, 13.2) * mm});
            skLineSegment(sketch, "E8071", {"start": v(20.86, 13.2) * mm, "end": v(20.89, 13.23) * mm});
            skLineSegment(sketch, "E8072", {"start": v(20.89, 13.23) * mm, "end": v(20.9, 13.25) * mm});
            skLineSegment(sketch, "E8073", {"start": v(20.9, 13.25) * mm, "end": v(20.93, 13.27) * mm});
            skLineSegment(sketch, "E8074", {"start": v(20.93, 13.27) * mm, "end": v(20.95, 13.29) * mm});
            skLineSegment(sketch, "E8075", {"start": v(20.95, 13.29) * mm, "end": v(20.97, 13.3) * mm});
            skLineSegment(sketch, "E8076", {"start": v(20.97, 13.3) * mm, "end": v(20.99, 13.33) * mm});
            skLineSegment(sketch, "E8077", {"start": v(20.99, 13.33) * mm, "end": v(21, 13.35) * mm});
            skLineSegment(sketch, "E8078", {"start": v(21, 13.35) * mm, "end": v(21.03, 13.37) * mm});
            skLineSegment(sketch, "E8079", {"start": v(21.03, 13.37) * mm, "end": v(21.05, 13.39) * mm});
            skLineSegment(sketch, "E8080", {"start": v(21.05, 13.39) * mm, "end": v(21.07, 13.4) * mm});
            skLineSegment(sketch, "E8081", {"start": v(21.07, 13.4) * mm, "end": v(21.1, 13.42) * mm});
            skLineSegment(sketch, "E8082", {"start": v(21.1, 13.42) * mm, "end": v(21.2, 13.5) * mm});
            skLineSegment(sketch, "E8083", {"start": v(21.2, 13.5) * mm, "end": v(21.3, 13.57) * mm});
            skLineSegment(sketch, "E8084", {"start": v(21.3, 13.57) * mm, "end": v(21.41, 13.63) * mm});
            skLineSegment(sketch, "E8085", {"start": v(21.41, 13.63) * mm, "end": v(21.52, 13.68) * mm});
            skLineSegment(sketch, "E8086", {"start": v(21.52, 13.68) * mm, "end": v(21.63, 13.72) * mm});
            skLineSegment(sketch, "E8087", {"start": v(21.63, 13.72) * mm, "end": v(21.74, 13.76) * mm});
            skLineSegment(sketch, "E8088", {"start": v(21.74, 13.76) * mm, "end": v(21.85, 13.78) * mm});
            skLineSegment(sketch, "E8089", {"start": v(21.85, 13.78) * mm, "end": v(21.96, 13.8) * mm});
            skLineSegment(sketch, "E8090", {"start": v(21.96, 13.8) * mm, "end": v(22, 13.8) * mm});
            skLineSegment(sketch, "E8091", {"start": v(22, 13.8) * mm, "end": v(22.03, 13.8) * mm});
            skLineSegment(sketch, "E8092", {"start": v(22.03, 13.8) * mm, "end": v(22.05, 13.8) * mm});
            skLineSegment(sketch, "E8093", {"start": v(22.05, 13.8) * mm, "end": v(22.07, 13.8) * mm});
            skLineSegment(sketch, "E8094", {"start": v(22.07, 13.8) * mm, "end": v(22.08, 13.8) * mm});
            skLineSegment(sketch, "E8095", {"start": v(22.08, 13.8) * mm, "end": v(22.08, 13.8) * mm});
            skLineSegment(sketch, "E8096", {"start": v(22.08, 13.8) * mm, "end": v(22.13, 13.83) * mm});
            skLineSegment(sketch, "E8097", {"start": v(22.13, 13.83) * mm, "end": v(22.17, 13.85) * mm});
            skLineSegment(sketch, "E8098", {"start": v(22.17, 13.85) * mm, "end": v(22.2, 13.87) * mm});
            skLineSegment(sketch, "E8099", {"start": v(22.2, 13.87) * mm, "end": v(22.24, 13.89) * mm});
            skLineSegment(sketch, "E8100", {"start": v(22.24, 13.89) * mm, "end": v(22.27, 13.9) * mm});
            skLineSegment(sketch, "E8101", {"start": v(22.27, 13.9) * mm, "end": v(22.3, 13.92) * mm});
            skLineSegment(sketch, "E8102", {"start": v(22.3, 13.92) * mm, "end": v(22.3, 13.92) * mm});
            skLineSegment(sketch, "E8103", {"start": v(22.3, 13.92) * mm, "end": v(22.32, 13.93) * mm});
            skLineSegment(sketch, "E8104", {"start": v(22.32, 13.93) * mm, "end": v(22.33, 13.93) * mm});
            skLineSegment(sketch, "E8105", {"start": v(22.33, 13.93) * mm, "end": v(22.36, 13.94) * mm});
            skLineSegment(sketch, "E8106", {"start": v(22.36, 13.94) * mm, "end": v(22.42, 13.96) * mm});
            skLineSegment(sketch, "E8107", {"start": v(22.42, 13.96) * mm, "end": v(22.49, 13.99) * mm});
            skLineSegment(sketch, "E8108", {"start": v(22.49, 13.99) * mm, "end": v(22.57, 14.01) * mm});
            skLineSegment(sketch, "E8109", {"start": v(22.57, 14.01) * mm, "end": v(22.67, 14.04) * mm});
            skLineSegment(sketch, "E8110", {"start": v(22.67, 14.04) * mm, "end": v(22.77, 14.08) * mm});
            skLineSegment(sketch, "E8111", {"start": v(22.77, 14.08) * mm, "end": v(22.89, 14.12) * mm});
            skLineSegment(sketch, "E8112", {"start": v(22.89, 14.12) * mm, "end": v(22.89, 14.12) * mm});
            skLineSegment(sketch, "E8113", {"start": v(22.89, 14.12) * mm, "end": v(22.9, 14.12) * mm});
            skLineSegment(sketch, "E8114", {"start": v(22.9, 14.12) * mm, "end": v(22.9, 14.12) * mm});
            skLineSegment(sketch, "E8115", {"start": v(22.9, 14.12) * mm, "end": v(22.93, 14.12) * mm});
            skLineSegment(sketch, "E8116", {"start": v(22.93, 14.12) * mm, "end": v(22.96, 14.12) * mm});
            skLineSegment(sketch, "E8117", {"start": v(22.96, 14.12) * mm, "end": v(23.02, 14.13) * mm});
            skLineSegment(sketch, "E8118", {"start": v(23.02, 14.13) * mm, "end": v(23.1, 14.14) * mm});
            skLineSegment(sketch, "E8119", {"start": v(23.1, 14.14) * mm, "end": v(23.21, 14.15) * mm});
            skLineSegment(sketch, "E8120", {"start": v(23.21, 14.15) * mm, "end": v(23.24, 14.15) * mm});
            skLineSegment(sketch, "E8121", {"start": v(23.24, 14.15) * mm, "end": v(23.28, 14.16) * mm});
            skLineSegment(sketch, "E8122", {"start": v(23.28, 14.16) * mm, "end": v(23.31, 14.17) * mm});
            skLineSegment(sketch, "E8123", {"start": v(23.31, 14.17) * mm, "end": v(23.34, 14.17) * mm});
            skLineSegment(sketch, "E8124", {"start": v(23.34, 14.17) * mm, "end": v(23.38, 14.18) * mm});
            skLineSegment(sketch, "E8125", {"start": v(23.38, 14.18) * mm, "end": v(23.4, 14.19) * mm});
            skLineSegment(sketch, "E8126", {"start": v(23.4, 14.19) * mm, "end": v(23.44, 14.2) * mm});
            skLineSegment(sketch, "E8127", {"start": v(23.44, 14.2) * mm, "end": v(23.47, 14.2) * mm});
            skLineSegment(sketch, "E8128", {"start": v(23.47, 14.2) * mm, "end": v(23.5, 14.2) * mm});
            skLineSegment(sketch, "E8129", {"start": v(23.5, 14.2) * mm, "end": v(23.52, 14.21) * mm});
            skLineSegment(sketch, "E8130", {"start": v(23.52, 14.21) * mm, "end": v(23.55, 14.22) * mm});
            skLineSegment(sketch, "E8131", {"start": v(23.55, 14.22) * mm, "end": v(23.57, 14.22) * mm});
            skLineSegment(sketch, "E8132", {"start": v(23.57, 14.22) * mm, "end": v(23.6, 14.23) * mm});
            skLineSegment(sketch, "E8133", {"start": v(23.6, 14.23) * mm, "end": v(23.62, 14.23) * mm});
            skLineSegment(sketch, "E8134", {"start": v(23.62, 14.23) * mm, "end": v(23.64, 14.24) * mm});
            skLineSegment(sketch, "E8135", {"start": v(23.64, 14.24) * mm, "end": v(23.67, 14.24) * mm});
            skLineSegment(sketch, "E8136", {"start": v(23.67, 14.24) * mm, "end": v(23.77, 14.26) * mm});
            skLineSegment(sketch, "E8137", {"start": v(23.77, 14.26) * mm, "end": v(23.85, 14.27) * mm});
            skLineSegment(sketch, "E8138", {"start": v(23.85, 14.27) * mm, "end": v(23.9, 14.28) * mm});
            skLineSegment(sketch, "E8139", {"start": v(23.9, 14.28) * mm, "end": v(23.94, 14.29) * mm});
            skLineSegment(sketch, "E8140", {"start": v(23.94, 14.29) * mm, "end": v(23.96, 14.29) * mm});
            skLineSegment(sketch, "E8141", {"start": v(23.96, 14.29) * mm, "end": v(23.98, 14.3) * mm});
            skLineSegment(sketch, "E8142", {"start": v(23.98, 14.3) * mm, "end": v(23.98, 14.3) * mm});
            skLineSegment(sketch, "E8143", {"start": v(23.98, 14.3) * mm, "end": v(24.13, 14.27) * mm});
            skLineSegment(sketch, "E8144", {"start": v(24.13, 14.27) * mm, "end": v(24.26, 14.24) * mm});
            skLineSegment(sketch, "E8145", {"start": v(24.26, 14.24) * mm, "end": v(24.4, 14.22) * mm});
            skLineSegment(sketch, "E8146", {"start": v(24.4, 14.22) * mm, "end": v(24.5, 14.2) * mm});
            skLineSegment(sketch, "E8147", {"start": v(24.5, 14.2) * mm, "end": v(24.6, 14.19) * mm});
            skLineSegment(sketch, "E8148", {"start": v(24.6, 14.19) * mm, "end": v(24.67, 14.18) * mm});
            skLineSegment(sketch, "E8149", {"start": v(24.67, 14.18) * mm, "end": v(24.73, 14.17) * mm});
            skLineSegment(sketch, "E8150", {"start": v(24.73, 14.17) * mm, "end": v(24.75, 14.16) * mm});
            skLineSegment(sketch, "E8151", {"start": v(24.75, 14.16) * mm, "end": v(24.76, 14.16) * mm});
            skLineSegment(sketch, "E8152", {"start": v(24.76, 14.16) * mm, "end": v(24.78, 14.16) * mm});
            skLineSegment(sketch, "E8153", {"start": v(24.78, 14.16) * mm, "end": v(24.8, 14.15) * mm});
            skLineSegment(sketch, "E8154", {"start": v(24.8, 14.15) * mm, "end": v(24.81, 14.15) * mm});
            skLineSegment(sketch, "E8155", {"start": v(24.81, 14.15) * mm, "end": v(24.83, 14.14) * mm});
            skLineSegment(sketch, "E8156", {"start": v(24.83, 14.14) * mm, "end": v(24.85, 14.13) * mm});
            skLineSegment(sketch, "E8157", {"start": v(24.85, 14.13) * mm, "end": v(24.87, 14.13) * mm});
            skLineSegment(sketch, "E8158", {"start": v(24.87, 14.13) * mm, "end": v(24.9, 14.12) * mm});
            skLineSegment(sketch, "E8159", {"start": v(24.9, 14.12) * mm, "end": v(24.9, 14.12) * mm});
            skLineSegment(sketch, "E8160", {"start": v(24.9, 14.12) * mm, "end": v(24.9, 14.11) * mm});
            skLineSegment(sketch, "E8161", {"start": v(24.9, 14.11) * mm, "end": v(24.9, 14.11) * mm});
            skLineSegment(sketch, "E8162", {"start": v(24.9, 14.11) * mm, "end": v(24.92, 14.1) * mm});
            skLineSegment(sketch, "E8163", {"start": v(24.92, 14.1) * mm, "end": v(24.93, 14.1) * mm});
            skLineSegment(sketch, "E8164", {"start": v(24.93, 14.1) * mm, "end": v(24.94, 14.09) * mm});
            skLineSegment(sketch, "E8165", {"start": v(24.94, 14.09) * mm, "end": v(24.96, 14.08) * mm});
            skLineSegment(sketch, "E8166", {"start": v(24.96, 14.08) * mm, "end": v(24.98, 14.07) * mm});
            skLineSegment(sketch, "E8167", {"start": v(24.98, 14.07) * mm, "end": v(25, 14.06) * mm});
            skLineSegment(sketch, "E8168", {"start": v(25, 14.06) * mm, "end": v(25, 14.05) * mm});
            skLineSegment(sketch, "E8169", {"start": v(25, 14.05) * mm, "end": v(25.02, 14.04) * mm});
            skLineSegment(sketch, "E8170", {"start": v(25.02, 14.04) * mm, "end": v(25.04, 14.03) * mm});
            skLineSegment(sketch, "E8171", {"start": v(25.04, 14.03) * mm, "end": v(25.06, 14.03) * mm});
            skLineSegment(sketch, "E8172", {"start": v(25.06, 14.03) * mm, "end": v(25.07, 14.02) * mm});
            skLineSegment(sketch, "E8173", {"start": v(25.07, 14.02) * mm, "end": v(25.1, 14) * mm});
            skLineSegment(sketch, "E8174", {"start": v(25.1, 14) * mm, "end": v(25.14, 14) * mm});
            skLineSegment(sketch, "E8175", {"start": v(25.14, 14) * mm, "end": v(25.17, 13.98) * mm});
            skLineSegment(sketch, "E8176", {"start": v(25.17, 13.98) * mm, "end": v(25.2, 13.97) * mm});
            skLineSegment(sketch, "E8177", {"start": v(25.2, 13.97) * mm, "end": v(25.23, 13.96) * mm});
            skLineSegment(sketch, "E8178", {"start": v(25.23, 13.96) * mm, "end": v(25.26, 13.95) * mm});
            skLineSegment(sketch, "E8179", {"start": v(25.26, 13.95) * mm, "end": v(25.29, 13.94) * mm});
            skLineSegment(sketch, "E8180", {"start": v(25.29, 13.94) * mm, "end": v(25.32, 13.93) * mm});
            skLineSegment(sketch, "E8181", {"start": v(25.32, 13.93) * mm, "end": v(25.37, 13.9) * mm});
            skLineSegment(sketch, "E8182", {"start": v(25.37, 13.9) * mm, "end": v(25.41, 13.9) * mm});
            skLineSegment(sketch, "E8183", {"start": v(25.41, 13.9) * mm, "end": v(25.46, 13.88) * mm});
            skLineSegment(sketch, "E8184", {"start": v(25.46, 13.88) * mm, "end": v(25.5, 13.86) * mm});
            skLineSegment(sketch, "E8185", {"start": v(25.5, 13.86) * mm, "end": v(25.55, 13.84) * mm});
            skLineSegment(sketch, "E8186", {"start": v(25.55, 13.84) * mm, "end": v(25.59, 13.82) * mm});
            skLineSegment(sketch, "E8187", {"start": v(25.59, 13.82) * mm, "end": v(25.63, 13.8) * mm});
            skLineSegment(sketch, "E8188", {"start": v(25.63, 13.8) * mm, "end": v(25.68, 13.79) * mm});
            skLineSegment(sketch, "E8189", {"start": v(25.68, 13.79) * mm, "end": v(25.72, 13.77) * mm});
            skLineSegment(sketch, "E8190", {"start": v(25.72, 13.77) * mm, "end": v(25.76, 13.74) * mm});
            skLineSegment(sketch, "E8191", {"start": v(25.76, 13.74) * mm, "end": v(25.8, 13.72) * mm});
            skLineSegment(sketch, "E8192", {"start": v(25.8, 13.72) * mm, "end": v(25.84, 13.7) * mm});
            skLineSegment(sketch, "E8193", {"start": v(25.84, 13.7) * mm, "end": v(25.88, 13.67) * mm});
            skLineSegment(sketch, "E8194", {"start": v(25.88, 13.67) * mm, "end": v(25.92, 13.65) * mm});
            skLineSegment(sketch, "E8195", {"start": v(25.92, 13.65) * mm, "end": v(25.96, 13.62) * mm});
            skLineSegment(sketch, "E8196", {"start": v(25.96, 13.62) * mm, "end": v(26, 13.6) * mm});
            skLineSegment(sketch, "E8197", {"start": v(26, 13.6) * mm, "end": v(26.02, 13.59) * mm});
            skLineSegment(sketch, "E8198", {"start": v(26.02, 13.59) * mm, "end": v(26.05, 13.57) * mm});
            skLineSegment(sketch, "E8199", {"start": v(26.05, 13.57) * mm, "end": v(26.07, 13.56) * mm});
            skLineSegment(sketch, "E8200", {"start": v(26.07, 13.56) * mm, "end": v(26.09, 13.55) * mm});
            skLineSegment(sketch, "E8201", {"start": v(26.09, 13.55) * mm, "end": v(26.11, 13.53) * mm});
            skLineSegment(sketch, "E8202", {"start": v(26.11, 13.53) * mm, "end": v(26.13, 13.52) * mm});
            skLineSegment(sketch, "E8203", {"start": v(26.13, 13.52) * mm, "end": v(26.16, 13.5) * mm});
            skLineSegment(sketch, "E8204", {"start": v(26.16, 13.5) * mm, "end": v(26.18, 13.5) * mm});
            skLineSegment(sketch, "E8205", {"start": v(26.18, 13.5) * mm, "end": v(26.2, 13.48) * mm});
            skLineSegment(sketch, "E8206", {"start": v(26.2, 13.48) * mm, "end": v(26.22, 13.47) * mm});
            skLineSegment(sketch, "E8207", {"start": v(26.22, 13.47) * mm, "end": v(26.24, 13.46) * mm});
            skLineSegment(sketch, "E8208", {"start": v(26.24, 13.46) * mm, "end": v(26.26, 13.44) * mm});
            skLineSegment(sketch, "E8209", {"start": v(26.26, 13.44) * mm, "end": v(26.29, 13.43) * mm});
            skLineSegment(sketch, "E8210", {"start": v(26.29, 13.43) * mm, "end": v(26.3, 13.42) * mm});
            skLineSegment(sketch, "E8211", {"start": v(26.3, 13.42) * mm, "end": v(26.33, 13.4) * mm});
            skLineSegment(sketch, "E8212", {"start": v(26.33, 13.4) * mm, "end": v(26.35, 13.4) * mm});
            skLineSegment(sketch, "E8213", {"start": v(26.35, 13.4) * mm, "end": v(26.39, 13.38) * mm});
            skLineSegment(sketch, "E8214", {"start": v(26.39, 13.38) * mm, "end": v(26.42, 13.36) * mm});
            skLineSegment(sketch, "E8215", {"start": v(26.42, 13.36) * mm, "end": v(26.46, 13.34) * mm});
            skLineSegment(sketch, "E8216", {"start": v(26.46, 13.34) * mm, "end": v(26.5, 13.32) * mm});
            skLineSegment(sketch, "E8217", {"start": v(26.5, 13.32) * mm, "end": v(26.53, 13.3) * mm});
            skLineSegment(sketch, "E8218", {"start": v(26.53, 13.3) * mm, "end": v(26.57, 13.27) * mm});
            skLineSegment(sketch, "E8219", {"start": v(26.57, 13.27) * mm, "end": v(26.6, 13.25) * mm});
            skLineSegment(sketch, "E8220", {"start": v(26.6, 13.25) * mm, "end": v(26.64, 13.23) * mm});
            skLineSegment(sketch, "E8221", {"start": v(26.64, 13.23) * mm, "end": v(26.68, 13.2) * mm});
            skLineSegment(sketch, "E8222", {"start": v(26.68, 13.2) * mm, "end": v(26.72, 13.17) * mm});
            skLineSegment(sketch, "E8223", {"start": v(26.72, 13.17) * mm, "end": v(26.76, 13.15) * mm});
            skLineSegment(sketch, "E8224", {"start": v(26.76, 13.15) * mm, "end": v(26.8, 13.12) * mm});
            skLineSegment(sketch, "E8225", {"start": v(26.8, 13.12) * mm, "end": v(26.82, 13.1) * mm});
            skLineSegment(sketch, "E8226", {"start": v(26.82, 13.1) * mm, "end": v(26.86, 13.06) * mm});
            skLineSegment(sketch, "E8227", {"start": v(26.86, 13.06) * mm, "end": v(26.88, 13.04) * mm});
            skLineSegment(sketch, "E8228", {"start": v(26.88, 13.04) * mm, "end": v(26.91, 13) * mm});
            skLineSegment(sketch, "E8229", {"start": v(26.91, 13) * mm, "end": v(26.94, 12.98) * mm});
            skLineSegment(sketch, "E8230", {"start": v(26.94, 12.98) * mm, "end": v(26.97, 12.95) * mm});
            skLineSegment(sketch, "E8231", {"start": v(26.97, 12.95) * mm, "end": v(27, 12.92) * mm});
            skLineSegment(sketch, "E8232", {"start": v(27, 12.92) * mm, "end": v(27.02, 12.88) * mm});
            skLineSegment(sketch, "E8233", {"start": v(27.02, 12.88) * mm, "end": v(27.05, 12.85) * mm});
            skLineSegment(sketch, "E8234", {"start": v(27.05, 12.85) * mm, "end": v(27.07, 12.82) * mm});
            skLineSegment(sketch, "E8235", {"start": v(27.07, 12.82) * mm, "end": v(27.1, 12.79) * mm});
            skLineSegment(sketch, "E8236", {"start": v(27.1, 12.79) * mm, "end": v(27.12, 12.76) * mm});
            skLineSegment(sketch, "E8237", {"start": v(27.12, 12.76) * mm, "end": v(27.15, 12.72) * mm});
            skLineSegment(sketch, "E8238", {"start": v(27.15, 12.72) * mm, "end": v(27.19, 12.68) * mm});
            skLineSegment(sketch, "E8239", {"start": v(27.19, 12.68) * mm, "end": v(27.22, 12.64) * mm});
            skLineSegment(sketch, "E8240", {"start": v(27.22, 12.64) * mm, "end": v(27.25, 12.6) * mm});
            skLineSegment(sketch, "E8241", {"start": v(27.25, 12.6) * mm, "end": v(27.28, 12.56) * mm});
            skLineSegment(sketch, "E8242", {"start": v(27.28, 12.56) * mm, "end": v(27.32, 12.53) * mm});
            skLineSegment(sketch, "E8243", {"start": v(27.32, 12.53) * mm, "end": v(27.35, 12.49) * mm});
            skLineSegment(sketch, "E8244", {"start": v(27.35, 12.49) * mm, "end": v(27.38, 12.45) * mm});
            skLineSegment(sketch, "E8245", {"start": v(27.38, 12.45) * mm, "end": v(27.4, 12.43) * mm});
            skLineSegment(sketch, "E8246", {"start": v(27.4, 12.43) * mm, "end": v(27.43, 12.4) * mm});
            skLineSegment(sketch, "E8247", {"start": v(27.43, 12.4) * mm, "end": v(27.45, 12.4) * mm});
            skLineSegment(sketch, "E8248", {"start": v(27.45, 12.4) * mm, "end": v(27.48, 12.37) * mm});
            skLineSegment(sketch, "E8249", {"start": v(27.48, 12.37) * mm, "end": v(27.5, 12.35) * mm});
            skLineSegment(sketch, "E8250", {"start": v(27.5, 12.35) * mm, "end": v(27.52, 12.34) * mm});
            skLineSegment(sketch, "E8251", {"start": v(27.52, 12.34) * mm, "end": v(27.55, 12.32) * mm});
            skLineSegment(sketch, "E8252", {"start": v(27.55, 12.32) * mm, "end": v(27.57, 12.3) * mm});
            skLineSegment(sketch, "E8253", {"start": v(27.57, 12.3) * mm, "end": v(27.6, 12.3) * mm});
            skLineSegment(sketch, "E8254", {"start": v(27.6, 12.3) * mm, "end": v(27.61, 12.28) * mm});
            skLineSegment(sketch, "E8255", {"start": v(27.61, 12.28) * mm, "end": v(27.63, 12.26) * mm});
            skLineSegment(sketch, "E8256", {"start": v(27.63, 12.26) * mm, "end": v(27.65, 12.25) * mm});
            skLineSegment(sketch, "E8257", {"start": v(27.65, 12.25) * mm, "end": v(27.67, 12.23) * mm});
            skLineSegment(sketch, "E8258", {"start": v(27.67, 12.23) * mm, "end": v(27.69, 12.22) * mm});
            skLineSegment(sketch, "E8259", {"start": v(27.69, 12.22) * mm, "end": v(27.7, 12.2) * mm});
            skLineSegment(sketch, "E8260", {"start": v(27.7, 12.2) * mm, "end": v(27.72, 12.19) * mm});
            skLineSegment(sketch, "E8261", {"start": v(27.72, 12.19) * mm, "end": v(27.78, 12.13) * mm});
            skLineSegment(sketch, "E8262", {"start": v(27.78, 12.13) * mm, "end": v(27.83, 12.08) * mm});
            skLineSegment(sketch, "E8263", {"start": v(27.83, 12.08) * mm, "end": v(27.88, 12.02) * mm});
            skLineSegment(sketch, "E8264", {"start": v(27.88, 12.02) * mm, "end": v(27.92, 11.97) * mm});
            skLineSegment(sketch, "E8265", {"start": v(27.92, 11.97) * mm, "end": v(27.97, 11.92) * mm});
            skLineSegment(sketch, "E8266", {"start": v(27.97, 11.92) * mm, "end": v(28, 11.87) * mm});
            skLineSegment(sketch, "E8267", {"start": v(28, 11.87) * mm, "end": v(28.04, 11.82) * mm});
            skLineSegment(sketch, "E8268", {"start": v(28.04, 11.82) * mm, "end": v(28.07, 11.77) * mm});
            skLineSegment(sketch, "E8269", {"start": v(28.07, 11.77) * mm, "end": v(28.12, 11.69) * mm});
            skLineSegment(sketch, "E8270", {"start": v(28.12, 11.69) * mm, "end": v(28.17, 11.6) * mm});
            skLineSegment(sketch, "E8271", {"start": v(28.17, 11.6) * mm, "end": v(28.22, 11.52) * mm});
            skLineSegment(sketch, "E8272", {"start": v(28.22, 11.52) * mm, "end": v(28.27, 11.43) * mm});
            skLineSegment(sketch, "E8273", {"start": v(28.27, 11.43) * mm, "end": v(28.32, 11.34) * mm});
            skLineSegment(sketch, "E8274", {"start": v(28.32, 11.34) * mm, "end": v(28.37, 11.25) * mm});
            skLineSegment(sketch, "E8275", {"start": v(28.37, 11.25) * mm, "end": v(28.4, 11.16) * mm});
            skLineSegment(sketch, "E8276", {"start": v(28.4, 11.16) * mm, "end": v(28.45, 11.07) * mm});
            skLineSegment(sketch, "E8277", {"start": v(28.45, 11.07) * mm, "end": v(28.47, 11) * mm});
            skLineSegment(sketch, "E8278", {"start": v(28.47, 11) * mm, "end": v(28.5, 10.94) * mm});
            skLineSegment(sketch, "E8279", {"start": v(28.5, 10.94) * mm, "end": v(28.52, 10.87) * mm});
            skLineSegment(sketch, "E8280", {"start": v(28.52, 10.87) * mm, "end": v(28.54, 10.8) * mm});
            skLineSegment(sketch, "E8281", {"start": v(28.54, 10.8) * mm, "end": v(28.55, 10.74) * mm});
            skLineSegment(sketch, "E8282", {"start": v(28.55, 10.74) * mm, "end": v(28.57, 10.67) * mm});
            skLineSegment(sketch, "E8283", {"start": v(28.57, 10.67) * mm, "end": v(28.59, 10.6) * mm});
            skLineSegment(sketch, "E8284", {"start": v(28.59, 10.6) * mm, "end": v(28.6, 10.53) * mm});
            skLineSegment(sketch, "E8285", {"start": v(28.6, 10.53) * mm, "end": v(28.61, 10.5) * mm});
            skLineSegment(sketch, "E8286", {"start": v(28.61, 10.5) * mm, "end": v(28.62, 10.46) * mm});
            skLineSegment(sketch, "E8287", {"start": v(28.62, 10.46) * mm, "end": v(28.63, 10.43) * mm});
            skLineSegment(sketch, "E8288", {"start": v(28.63, 10.43) * mm, "end": v(28.64, 10.4) * mm});
            skLineSegment(sketch, "E8289", {"start": v(28.64, 10.4) * mm, "end": v(28.65, 10.36) * mm});
            skLineSegment(sketch, "E8290", {"start": v(28.65, 10.36) * mm, "end": v(28.66, 10.32) * mm});
            skLineSegment(sketch, "E8291", {"start": v(28.66, 10.32) * mm, "end": v(28.67, 10.28) * mm});
            skLineSegment(sketch, "E8292", {"start": v(28.67, 10.28) * mm, "end": v(28.68, 10.25) * mm});
            skLineSegment(sketch, "E8293", {"start": v(28.68, 10.25) * mm, "end": v(28.7, 10.2) * mm});
            skLineSegment(sketch, "E8294", {"start": v(28.7, 10.2) * mm, "end": v(28.7, 10.17) * mm});
            skLineSegment(sketch, "E8295", {"start": v(28.7, 10.17) * mm, "end": v(28.72, 10.12) * mm});
            skLineSegment(sketch, "E8296", {"start": v(28.72, 10.12) * mm, "end": v(28.73, 10.08) * mm});
            skLineSegment(sketch, "E8297", {"start": v(28.73, 10.08) * mm, "end": v(28.74, 10.04) * mm});
            skLineSegment(sketch, "E8298", {"start": v(28.74, 10.04) * mm, "end": v(28.75, 10) * mm});
            skLineSegment(sketch, "E8299", {"start": v(28.75, 10) * mm, "end": v(28.76, 9.96) * mm});
            skLineSegment(sketch, "E8300", {"start": v(28.76, 9.96) * mm, "end": v(28.78, 9.92) * mm});
            skLineSegment(sketch, "E8301", {"start": v(28.78, 9.92) * mm, "end": v(28.8, 9.87) * mm});
            skLineSegment(sketch, "E8302", {"start": v(28.8, 9.87) * mm, "end": v(28.8, 9.81) * mm});
            skLineSegment(sketch, "E8303", {"start": v(28.8, 9.81) * mm, "end": v(28.82, 9.76) * mm});
            skLineSegment(sketch, "E8304", {"start": v(28.82, 9.76) * mm, "end": v(28.84, 9.71) * mm});
            skLineSegment(sketch, "E8305", {"start": v(28.84, 9.71) * mm, "end": v(28.85, 9.66) * mm});
            skLineSegment(sketch, "E8306", {"start": v(28.85, 9.66) * mm, "end": v(28.87, 9.6) * mm});
            skLineSegment(sketch, "E8307", {"start": v(28.87, 9.6) * mm, "end": v(28.88, 9.55) * mm});
            skLineSegment(sketch, "E8308", {"start": v(28.88, 9.55) * mm, "end": v(28.9, 9.5) * mm});
            skLineSegment(sketch, "E8309", {"start": v(28.9, 9.5) * mm, "end": v(28.91, 9.46) * mm});
            skLineSegment(sketch, "E8310", {"start": v(28.91, 9.46) * mm, "end": v(28.92, 9.43) * mm});
            skLineSegment(sketch, "E8311", {"start": v(28.92, 9.43) * mm, "end": v(28.92, 9.4) * mm});
            skLineSegment(sketch, "E8312", {"start": v(28.92, 9.4) * mm, "end": v(28.93, 9.4) * mm});
            skLineSegment(sketch, "E8313", {"start": v(28.93, 9.4) * mm, "end": v(28.93, 9.38) * mm});
            skLineSegment(sketch, "E8314", {"start": v(28.93, 9.38) * mm, "end": v(28.93, 9.38) * mm});
            skLineSegment(sketch, "E8315", {"start": v(28.93, 9.38) * mm, "end": v(28.94, 9.33) * mm});
            skLineSegment(sketch, "E8316", {"start": v(28.94, 9.33) * mm, "end": v(28.96, 9.27) * mm});
            skLineSegment(sketch, "E8317", {"start": v(28.96, 9.27) * mm, "end": v(28.97, 9.22) * mm});
            skLineSegment(sketch, "E8318", {"start": v(28.97, 9.22) * mm, "end": v(28.98, 9.18) * mm});
            skLineSegment(sketch, "E8319", {"start": v(28.98, 9.18) * mm, "end": v(28.99, 9.13) * mm});
            skLineSegment(sketch, "E8320", {"start": v(28.99, 9.13) * mm, "end": v(29, 9.1) * mm});
            skLineSegment(sketch, "E8321", {"start": v(29, 9.1) * mm, "end": v(29, 9.07) * mm});
            skLineSegment(sketch, "E8322", {"start": v(29, 9.07) * mm, "end": v(29, 9.05) * mm});
            skLineSegment(sketch, "E8323", {"start": v(29, 9.05) * mm, "end": v(29, 9.03) * mm});
            skLineSegment(sketch, "E8324", {"start": v(29, 9.03) * mm, "end": v(29.01, 9) * mm});
            skLineSegment(sketch, "E8325", {"start": v(29.01, 9) * mm, "end": v(29.01, 8.98) * mm});
            skLineSegment(sketch, "E8326", {"start": v(29.01, 8.98) * mm, "end": v(29.02, 8.95) * mm});
            skLineSegment(sketch, "E8327", {"start": v(29.02, 8.95) * mm, "end": v(29.02, 8.91) * mm});
            skLineSegment(sketch, "E8328", {"start": v(29.02, 8.91) * mm, "end": v(29.01, 8.88) * mm});
            skLineSegment(sketch, "E8329", {"start": v(29.52, 10.88) * mm, "end": v(29.5, 10.92) * mm});
            skLineSegment(sketch, "E8330", {"start": v(29.5, 10.92) * mm, "end": v(29.5, 10.96) * mm});
            skLineSegment(sketch, "E8331", {"start": v(29.5, 10.96) * mm, "end": v(29.48, 11) * mm});
            skLineSegment(sketch, "E8332", {"start": v(29.48, 11) * mm, "end": v(29.48, 11.03) * mm});
            skLineSegment(sketch, "E8333", {"start": v(29.48, 11.03) * mm, "end": v(29.48, 11.06) * mm});
            skLineSegment(sketch, "E8334", {"start": v(29.48, 11.06) * mm, "end": v(29.48, 11.1) * mm});
            skLineSegment(sketch, "E8335", {"start": v(29.48, 11.1) * mm, "end": v(29.48, 11.13) * mm});
            skLineSegment(sketch, "E8336", {"start": v(29.48, 11.13) * mm, "end": v(29.5, 11.16) * mm});
            skLineSegment(sketch, "E8337", {"start": v(29.5, 11.16) * mm, "end": v(29.51, 11.2) * mm});
            skLineSegment(sketch, "E8338", {"start": v(29.51, 11.2) * mm, "end": v(29.53, 11.23) * mm});
            skLineSegment(sketch, "E8339", {"start": v(29.53, 11.23) * mm, "end": v(29.56, 11.26) * mm});
            skLineSegment(sketch, "E8340", {"start": v(29.56, 11.26) * mm, "end": v(29.6, 11.29) * mm});
            skLineSegment(sketch, "E8341", {"start": v(29.6, 11.29) * mm, "end": v(29.63, 11.3) * mm});
            skLineSegment(sketch, "E8342", {"start": v(29.63, 11.3) * mm, "end": v(29.66, 11.33) * mm});
            skLineSegment(sketch, "E8343", {"start": v(29.66, 11.33) * mm, "end": v(29.7, 11.36) * mm});
            skLineSegment(sketch, "E8344", {"start": v(29.7, 11.36) * mm, "end": v(29.72, 11.38) * mm});
            skLineSegment(sketch, "E8345", {"start": v(29.72, 11.38) * mm, "end": v(29.75, 11.4) * mm});
            skLineSegment(sketch, "E8346", {"start": v(29.75, 11.4) * mm, "end": v(29.78, 11.43) * mm});
            skLineSegment(sketch, "E8347", {"start": v(29.78, 11.43) * mm, "end": v(29.8, 11.46) * mm});
            skLineSegment(sketch, "E8348", {"start": v(29.8, 11.46) * mm, "end": v(29.83, 11.48) * mm});
            skLineSegment(sketch, "E8349", {"start": v(29.83, 11.48) * mm, "end": v(29.85, 11.5) * mm});
            skLineSegment(sketch, "E8350", {"start": v(29.85, 11.5) * mm, "end": v(29.86, 11.51) * mm});
            skLineSegment(sketch, "E8351", {"start": v(29.86, 11.51) * mm, "end": v(29.88, 11.53) * mm});
            skLineSegment(sketch, "E8352", {"start": v(29.88, 11.53) * mm, "end": v(29.9, 11.55) * mm});
            skLineSegment(sketch, "E8353", {"start": v(29.9, 11.55) * mm, "end": v(29.91, 11.56) * mm});
            skLineSegment(sketch, "E8354", {"start": v(29.91, 11.56) * mm, "end": v(29.93, 11.58) * mm});
            skLineSegment(sketch, "E8355", {"start": v(29.93, 11.58) * mm, "end": v(29.95, 11.6) * mm});
            skLineSegment(sketch, "E8356", {"start": v(29.95, 11.6) * mm, "end": v(29.97, 11.6) * mm});
            skLineSegment(sketch, "E8357", {"start": v(29.97, 11.6) * mm, "end": v(30.04, 11.67) * mm});
            skLineSegment(sketch, "E8358", {"start": v(30.04, 11.67) * mm, "end": v(30.1, 11.72) * mm});
            skLineSegment(sketch, "E8359", {"start": v(30.1, 11.72) * mm, "end": v(30.18, 11.77) * mm});
            skLineSegment(sketch, "E8360", {"start": v(30.18, 11.77) * mm, "end": v(30.25, 11.82) * mm});
            skLineSegment(sketch, "E8361", {"start": v(30.25, 11.82) * mm, "end": v(30.32, 11.86) * mm});
            skLineSegment(sketch, "E8362", {"start": v(30.32, 11.86) * mm, "end": v(30.4, 11.9) * mm});
            skLineSegment(sketch, "E8363", {"start": v(30.4, 11.9) * mm, "end": v(30.48, 11.92) * mm});
            skLineSegment(sketch, "E8364", {"start": v(30.48, 11.92) * mm, "end": v(30.56, 11.94) * mm});
            skLineSegment(sketch, "E8365", {"start": v(30.56, 11.94) * mm, "end": v(30.62, 11.96) * mm});
            skLineSegment(sketch, "E8366", {"start": v(30.62, 11.96) * mm, "end": v(30.67, 11.97) * mm});
            skLineSegment(sketch, "E8367", {"start": v(30.67, 11.97) * mm, "end": v(30.73, 11.99) * mm});
            skLineSegment(sketch, "E8368", {"start": v(30.73, 11.99) * mm, "end": v(30.79, 12) * mm});
            skLineSegment(sketch, "E8369", {"start": v(30.79, 12) * mm, "end": v(30.85, 12.02) * mm});
            skLineSegment(sketch, "E8370", {"start": v(30.85, 12.02) * mm, "end": v(30.9, 12.04) * mm});
            skLineSegment(sketch, "E8371", {"start": v(30.9, 12.04) * mm, "end": v(30.96, 12.06) * mm});
            skLineSegment(sketch, "E8372", {"start": v(30.96, 12.06) * mm, "end": v(31.01, 12.08) * mm});
            skLineSegment(sketch, "E8373", {"start": v(31.01, 12.08) * mm, "end": v(31.06, 12.1) * mm});
            skLineSegment(sketch, "E8374", {"start": v(31.06, 12.1) * mm, "end": v(31.1, 12.1) * mm});
            skLineSegment(sketch, "E8375", {"start": v(31.1, 12.1) * mm, "end": v(31.14, 12.12) * mm});
            skLineSegment(sketch, "E8376", {"start": v(31.14, 12.12) * mm, "end": v(31.19, 12.14) * mm});
            skLineSegment(sketch, "E8377", {"start": v(31.19, 12.14) * mm, "end": v(31.23, 12.15) * mm});
            skLineSegment(sketch, "E8378", {"start": v(31.23, 12.15) * mm, "end": v(31.28, 12.16) * mm});
            skLineSegment(sketch, "E8379", {"start": v(31.28, 12.16) * mm, "end": v(31.32, 12.18) * mm});
            skLineSegment(sketch, "E8380", {"start": v(31.32, 12.18) * mm, "end": v(31.37, 12.19) * mm});
            skLineSegment(sketch, "E8381", {"start": v(31.37, 12.19) * mm, "end": v(31.37, 12.19) * mm});
            skLineSegment(sketch, "E8382", {"start": v(31.37, 12.19) * mm, "end": v(31.38, 12.19) * mm});
            skLineSegment(sketch, "E8383", {"start": v(31.38, 12.19) * mm, "end": v(31.38, 12.19) * mm});
            skLineSegment(sketch, "E8384", {"start": v(31.38, 12.19) * mm, "end": v(31.39, 12.2) * mm});
            skLineSegment(sketch, "E8385", {"start": v(31.39, 12.2) * mm, "end": v(31.4, 12.2) * mm});
            skLineSegment(sketch, "E8386", {"start": v(31.4, 12.2) * mm, "end": v(31.4, 12.2) * mm});
            skLineSegment(sketch, "E8387", {"start": v(31.4, 12.2) * mm, "end": v(31.42, 12.2) * mm});
            skLineSegment(sketch, "E8388", {"start": v(31.42, 12.2) * mm, "end": v(31.43, 12.2) * mm});
            skLineSegment(sketch, "E8389", {"start": v(31.43, 12.2) * mm, "end": v(31.44, 12.2) * mm});
            skLineSegment(sketch, "E8390", {"start": v(31.44, 12.2) * mm, "end": v(31.45, 12.2) * mm});
            skLineSegment(sketch, "E8391", {"start": v(31.45, 12.2) * mm, "end": v(31.45, 12.2) * mm});
            skLineSegment(sketch, "E8392", {"start": v(31.45, 12.2) * mm, "end": v(31.46, 12.2) * mm});
            skLineSegment(sketch, "E8393", {"start": v(31.46, 12.2) * mm, "end": v(31.46, 12.2) * mm});
            skLineSegment(sketch, "E8394", {"start": v(31.46, 12.2) * mm, "end": v(31.48, 12.18) * mm});
            skLineSegment(sketch, "E8395", {"start": v(31.48, 12.18) * mm, "end": v(31.5, 12.18) * mm});
            skLineSegment(sketch, "E8396", {"start": v(31.5, 12.18) * mm, "end": v(31.53, 12.17) * mm});
            skLineSegment(sketch, "E8397", {"start": v(31.53, 12.17) * mm, "end": v(31.55, 12.16) * mm});
            skLineSegment(sketch, "E8398", {"start": v(31.55, 12.16) * mm, "end": v(31.57, 12.16) * mm});
            skLineSegment(sketch, "E8399", {"start": v(31.57, 12.16) * mm, "end": v(31.59, 12.16) * mm});
            skLineSegment(sketch, "E8400", {"start": v(31.59, 12.16) * mm, "end": v(31.6, 12.15) * mm});
            skLineSegment(sketch, "E8401", {"start": v(31.6, 12.15) * mm, "end": v(31.6, 12.15) * mm});
            skLineSegment(sketch, "E8402", {"start": v(31.6, 12.15) * mm, "end": v(31.61, 12.15) * mm});
            skLineSegment(sketch, "E8403", {"start": v(31.61, 12.15) * mm, "end": v(31.63, 12.14) * mm});
            skLineSegment(sketch, "E8404", {"start": v(31.63, 12.14) * mm, "end": v(31.65, 12.14) * mm});
            skLineSegment(sketch, "E8405", {"start": v(31.65, 12.14) * mm, "end": v(31.68, 12.13) * mm});
            skLineSegment(sketch, "E8406", {"start": v(31.68, 12.13) * mm, "end": v(31.7, 12.12) * mm});
            skLineSegment(sketch, "E8407", {"start": v(31.7, 12.12) * mm, "end": v(31.74, 12.1) * mm});
            skLineSegment(sketch, "E8408", {"start": v(31.74, 12.1) * mm, "end": v(31.78, 12.1) * mm});
            skLineSegment(sketch, "E8409", {"start": v(31.78, 12.1) * mm, "end": v(31.82, 12.09) * mm});
            skLineSegment(sketch, "E8410", {"start": v(31.82, 12.09) * mm, "end": v(31.82, 12.09) * mm});
            skLineSegment(sketch, "E8411", {"start": v(31.82, 12.09) * mm, "end": v(31.83, 12.08) * mm});
            skLineSegment(sketch, "E8412", {"start": v(31.83, 12.08) * mm, "end": v(31.84, 12.08) * mm});
            skLineSegment(sketch, "E8413", {"start": v(31.84, 12.08) * mm, "end": v(31.86, 12.07) * mm});
            skLineSegment(sketch, "E8414", {"start": v(31.86, 12.07) * mm, "end": v(31.88, 12.07) * mm});
            skLineSegment(sketch, "E8415", {"start": v(31.88, 12.07) * mm, "end": v(31.9, 12.06) * mm});
            skLineSegment(sketch, "E8416", {"start": v(31.9, 12.06) * mm, "end": v(31.93, 12.05) * mm});
            skLineSegment(sketch, "E8417", {"start": v(31.93, 12.05) * mm, "end": v(31.94, 12.04) * mm});
            skLineSegment(sketch, "E8418", {"start": v(31.94, 12.04) * mm, "end": v(31.96, 12.04) * mm});
            skLineSegment(sketch, "E8419", {"start": v(31.96, 12.04) * mm, "end": v(31.98, 12.03) * mm});
            skLineSegment(sketch, "E8420", {"start": v(31.98, 12.03) * mm, "end": v(32, 12.03) * mm});
            skLineSegment(sketch, "E8421", {"start": v(32, 12.03) * mm, "end": v(32.01, 12.02) * mm});
            skLineSegment(sketch, "E8422", {"start": v(32.01, 12.02) * mm, "end": v(32.03, 12.02) * mm});
            skLineSegment(sketch, "E8423", {"start": v(32.03, 12.02) * mm, "end": v(32.05, 12) * mm});
            skLineSegment(sketch, "E8424", {"start": v(32.05, 12) * mm, "end": v(32.05, 12) * mm});
            skLineSegment(sketch, "E8425", {"start": v(32.05, 12) * mm, "end": v(32.06, 12) * mm});
            skLineSegment(sketch, "E8426", {"start": v(32.06, 12) * mm, "end": v(32.06, 12) * mm});
            skLineSegment(sketch, "E8427", {"start": v(32.06, 12) * mm, "end": v(32.07, 12) * mm});
            skLineSegment(sketch, "E8428", {"start": v(32.07, 12) * mm, "end": v(32.08, 12) * mm});
            skLineSegment(sketch, "E8429", {"start": v(32.08, 12) * mm, "end": v(32.1, 12) * mm});
            skLineSegment(sketch, "E8430", {"start": v(32.1, 12) * mm, "end": v(32.1, 12) * mm});
            skLineSegment(sketch, "E8431", {"start": v(32.1, 12) * mm, "end": v(32.12, 11.99) * mm});
            skLineSegment(sketch, "E8432", {"start": v(32.12, 11.99) * mm, "end": v(32.13, 11.98) * mm});
            skLineSegment(sketch, "E8433", {"start": v(32.13, 11.98) * mm, "end": v(32.15, 11.97) * mm});
            skLineSegment(sketch, "E8434", {"start": v(32.15, 11.97) * mm, "end": v(32.16, 11.96) * mm});
            skLineSegment(sketch, "E8435", {"start": v(32.16, 11.96) * mm, "end": v(32.16, 11.96) * mm});
            skLineSegment(sketch, "E8436", {"start": v(32.16, 11.96) * mm, "end": v(32.17, 11.96) * mm});
            skLineSegment(sketch, "E8437", {"start": v(32.17, 11.96) * mm, "end": v(32.17, 11.96) * mm});
            skLineSegment(sketch, "E8438", {"start": v(32.17, 11.96) * mm, "end": v(32.18, 11.96) * mm});
            skLineSegment(sketch, "E8439", {"start": v(32.18, 11.96) * mm, "end": v(32.19, 11.95) * mm});
            skLineSegment(sketch, "E8440", {"start": v(32.19, 11.95) * mm, "end": v(32.2, 11.94) * mm});
            skLineSegment(sketch, "E8441", {"start": v(32.2, 11.94) * mm, "end": v(32.22, 11.94) * mm});
            skLineSegment(sketch, "E8442", {"start": v(32.22, 11.94) * mm, "end": v(32.23, 11.93) * mm});
            skLineSegment(sketch, "E8443", {"start": v(32.23, 11.93) * mm, "end": v(32.24, 11.93) * mm});
            skLineSegment(sketch, "E8444", {"start": v(32.24, 11.93) * mm, "end": v(32.24, 11.92) * mm});
            skLineSegment(sketch, "E8445", {"start": v(32.24, 11.92) * mm, "end": v(32.25, 11.92) * mm});
            skLineSegment(sketch, "E8446", {"start": v(32.25, 11.92) * mm, "end": v(32.25, 11.92) * mm});
            skLineSegment(sketch, "E8447", {"start": v(32.25, 11.92) * mm, "end": v(32.27, 11.9) * mm});
            skLineSegment(sketch, "E8448", {"start": v(32.27, 11.9) * mm, "end": v(32.29, 11.87) * mm});
            skLineSegment(sketch, "E8449", {"start": v(32.29, 11.87) * mm, "end": v(32.3, 11.83) * mm});
            skLineSegment(sketch, "E8450", {"start": v(32.3, 11.83) * mm, "end": v(32.3, 11.8) * mm});
            skLineSegment(sketch, "E8451", {"start": v(32.3, 11.8) * mm, "end": v(32.3, 11.74) * mm});
            skLineSegment(sketch, "E8452", {"start": v(32.3, 11.74) * mm, "end": v(32.3, 11.69) * mm});
            skLineSegment(sketch, "E8453", {"start": v(32.3, 11.69) * mm, "end": v(32.28, 11.63) * mm});
            skLineSegment(sketch, "E8454", {"start": v(32.28, 11.63) * mm, "end": v(32.26, 11.58) * mm});
            skLineSegment(sketch, "E8455", {"start": v(32.26, 11.58) * mm, "end": v(32.26, 11.58) * mm});
            skLineSegment(sketch, "E8456", {"start": v(32.26, 11.58) * mm, "end": v(32.26, 11.57) * mm});
            skLineSegment(sketch, "E8457", {"start": v(32.26, 11.57) * mm, "end": v(32.25, 11.56) * mm});
            skLineSegment(sketch, "E8458", {"start": v(32.25, 11.56) * mm, "end": v(32.25, 11.55) * mm});
            skLineSegment(sketch, "E8459", {"start": v(32.25, 11.55) * mm, "end": v(32.24, 11.54) * mm});
            skLineSegment(sketch, "E8460", {"start": v(32.24, 11.54) * mm, "end": v(32.22, 11.52) * mm});
            skLineSegment(sketch, "E8461", {"start": v(32.22, 11.52) * mm, "end": v(32.2, 11.5) * mm});
            skLineSegment(sketch, "E8462", {"start": v(32.2, 11.5) * mm, "end": v(32.18, 11.46) * mm});
            skLineSegment(sketch, "E8463", {"start": v(32.18, 11.46) * mm, "end": v(32.16, 11.44) * mm});
            skLineSegment(sketch, "E8464", {"start": v(32.16, 11.44) * mm, "end": v(32.14, 11.4) * mm});
            skLineSegment(sketch, "E8465", {"start": v(32.14, 11.4) * mm, "end": v(32.12, 11.38) * mm});
            skLineSegment(sketch, "E8466", {"start": v(32.12, 11.38) * mm, "end": v(32.1, 11.35) * mm});
            skLineSegment(sketch, "E8467", {"start": v(32.1, 11.35) * mm, "end": v(32.07, 11.33) * mm});
            skLineSegment(sketch, "E8468", {"start": v(32.07, 11.33) * mm, "end": v(32.04, 11.3) * mm});
            skLineSegment(sketch, "E8469", {"start": v(32.04, 11.3) * mm, "end": v(32.02, 11.28) * mm});
            skLineSegment(sketch, "E8470", {"start": v(32.02, 11.28) * mm, "end": v(32, 11.25) * mm});
            skLineSegment(sketch, "E8471", {"start": v(32, 11.25) * mm, "end": v(31.98, 11.23) * mm});
            skLineSegment(sketch, "E8472", {"start": v(31.98, 11.23) * mm, "end": v(31.96, 11.21) * mm});
            skLineSegment(sketch, "E8473", {"start": v(31.96, 11.21) * mm, "end": v(31.94, 11.19) * mm});
            skLineSegment(sketch, "E8474", {"start": v(31.94, 11.19) * mm, "end": v(31.92, 11.16) * mm});
            skLineSegment(sketch, "E8475", {"start": v(31.92, 11.16) * mm, "end": v(31.9, 11.14) * mm});
            skLineSegment(sketch, "E8476", {"start": v(31.9, 11.14) * mm, "end": v(31.89, 11.12) * mm});
            skLineSegment(sketch, "E8477", {"start": v(31.89, 11.12) * mm, "end": v(31.86, 11.08) * mm});
            skLineSegment(sketch, "E8478", {"start": v(31.86, 11.08) * mm, "end": v(31.83, 11.06) * mm});
            skLineSegment(sketch, "E8479", {"start": v(31.83, 11.06) * mm, "end": v(31.8, 11.03) * mm});
            skLineSegment(sketch, "E8480", {"start": v(31.8, 11.03) * mm, "end": v(31.76, 11) * mm});
            skLineSegment(sketch, "E8481", {"start": v(31.76, 11) * mm, "end": v(31.72, 10.99) * mm});
            skLineSegment(sketch, "E8482", {"start": v(31.72, 10.99) * mm, "end": v(31.68, 10.97) * mm});
            skLineSegment(sketch, "E8483", {"start": v(31.68, 10.97) * mm, "end": v(31.64, 10.95) * mm});
            skLineSegment(sketch, "E8484", {"start": v(31.64, 10.95) * mm, "end": v(31.6, 10.93) * mm});
            skLineSegment(sketch, "E8485", {"start": v(31.6, 10.93) * mm, "end": v(31.58, 10.92) * mm});
            skLineSegment(sketch, "E8486", {"start": v(31.58, 10.92) * mm, "end": v(31.57, 10.92) * mm});
            skLineSegment(sketch, "E8487", {"start": v(31.57, 10.92) * mm, "end": v(31.56, 10.91) * mm});
            skLineSegment(sketch, "E8488", {"start": v(31.56, 10.91) * mm, "end": v(31.55, 10.9) * mm});
            skLineSegment(sketch, "E8489", {"start": v(31.55, 10.9) * mm, "end": v(31.54, 10.9) * mm});
            skLineSegment(sketch, "E8490", {"start": v(31.54, 10.9) * mm, "end": v(31.53, 10.9) * mm});
            skLineSegment(sketch, "E8491", {"start": v(31.53, 10.9) * mm, "end": v(31.52, 10.9) * mm});
            skLineSegment(sketch, "E8492", {"start": v(31.52, 10.9) * mm, "end": v(31.5, 10.89) * mm});
            skLineSegment(sketch, "E8493", {"start": v(31.5, 10.89) * mm, "end": v(31.45, 10.87) * mm});
            skLineSegment(sketch, "E8494", {"start": v(31.45, 10.87) * mm, "end": v(31.4, 10.84) * mm});
            skLineSegment(sketch, "E8495", {"start": v(31.4, 10.84) * mm, "end": v(31.34, 10.83) * mm});
            skLineSegment(sketch, "E8496", {"start": v(31.34, 10.83) * mm, "end": v(31.28, 10.81) * mm});
            skLineSegment(sketch, "E8497", {"start": v(31.28, 10.81) * mm, "end": v(31.22, 10.8) * mm});
            skLineSegment(sketch, "E8498", {"start": v(31.22, 10.8) * mm, "end": v(31.17, 10.78) * mm});
            skLineSegment(sketch, "E8499", {"start": v(31.17, 10.78) * mm, "end": v(31.1, 10.77) * mm});
            skLineSegment(sketch, "E8500", {"start": v(31.1, 10.77) * mm, "end": v(31.05, 10.76) * mm});
            skLineSegment(sketch, "E8501", {"start": v(31.05, 10.76) * mm, "end": v(31.03, 10.75) * mm});
            skLineSegment(sketch, "E8502", {"start": v(31.03, 10.75) * mm, "end": v(31, 10.75) * mm});
            skLineSegment(sketch, "E8503", {"start": v(31, 10.75) * mm, "end": v(30.99, 10.74) * mm});
            skLineSegment(sketch, "E8504", {"start": v(30.99, 10.74) * mm, "end": v(30.97, 10.74) * mm});
            skLineSegment(sketch, "E8505", {"start": v(30.97, 10.74) * mm, "end": v(30.95, 10.73) * mm});
            skLineSegment(sketch, "E8506", {"start": v(30.95, 10.73) * mm, "end": v(30.93, 10.73) * mm});
            skLineSegment(sketch, "E8507", {"start": v(30.93, 10.73) * mm, "end": v(30.9, 10.73) * mm});
            skLineSegment(sketch, "E8508", {"start": v(30.9, 10.73) * mm, "end": v(30.89, 10.72) * mm});
            skLineSegment(sketch, "E8509", {"start": v(30.89, 10.72) * mm, "end": v(30.85, 10.71) * mm});
            skLineSegment(sketch, "E8510", {"start": v(30.85, 10.71) * mm, "end": v(30.83, 10.7) * mm});
            skLineSegment(sketch, "E8511", {"start": v(30.83, 10.7) * mm, "end": v(30.81, 10.7) * mm});
            skLineSegment(sketch, "E8512", {"start": v(30.81, 10.7) * mm, "end": v(30.8, 10.7) * mm});
            skLineSegment(sketch, "E8513", {"start": v(30.8, 10.7) * mm, "end": v(30.8, 10.7) * mm});
            skLineSegment(sketch, "E8514", {"start": v(30.8, 10.7) * mm, "end": v(30.79, 10.7) * mm});
            skLineSegment(sketch, "E8515", {"start": v(30.79, 10.7) * mm, "end": v(30.79, 10.7) * mm});
            skLineSegment(sketch, "E8516", {"start": v(30.79, 10.7) * mm, "end": v(30.74, 10.69) * mm});
            skLineSegment(sketch, "E8517", {"start": v(30.74, 10.69) * mm, "end": v(30.7, 10.68) * mm});
            skLineSegment(sketch, "E8518", {"start": v(30.7, 10.68) * mm, "end": v(30.66, 10.67) * mm});
            skLineSegment(sketch, "E8519", {"start": v(30.66, 10.67) * mm, "end": v(30.62, 10.66) * mm});
            skLineSegment(sketch, "E8520", {"start": v(30.62, 10.66) * mm, "end": v(30.58, 10.65) * mm});
            skLineSegment(sketch, "E8521", {"start": v(30.58, 10.65) * mm, "end": v(30.55, 10.64) * mm});
            skLineSegment(sketch, "E8522", {"start": v(30.55, 10.64) * mm, "end": v(30.52, 10.64) * mm});
            skLineSegment(sketch, "E8523", {"start": v(30.52, 10.64) * mm, "end": v(30.5, 10.63) * mm});
            skLineSegment(sketch, "E8524", {"start": v(30.5, 10.63) * mm, "end": v(30.49, 10.63) * mm});
            skLineSegment(sketch, "E8525", {"start": v(30.49, 10.63) * mm, "end": v(30.46, 10.63) * mm});
            skLineSegment(sketch, "E8526", {"start": v(30.46, 10.63) * mm, "end": v(30.44, 10.63) * mm});
            skLineSegment(sketch, "E8527", {"start": v(30.44, 10.63) * mm, "end": v(30.4, 10.63) * mm});
            skLineSegment(sketch, "E8528", {"start": v(30.4, 10.63) * mm, "end": v(30.38, 10.63) * mm});
            skLineSegment(sketch, "E8529", {"start": v(30.38, 10.63) * mm, "end": v(30.35, 10.64) * mm});
            skLineSegment(sketch, "E8530", {"start": v(30.35, 10.64) * mm, "end": v(30.32, 10.64) * mm});
            skLineSegment(sketch, "E8531", {"start": v(30.32, 10.64) * mm, "end": v(30.29, 10.64) * mm});
            skLineSegment(sketch, "E8532", {"start": v(30.29, 10.64) * mm, "end": v(30.29, 10.64) * mm});
            skLineSegment(sketch, "E8533", {"start": v(30.29, 10.64) * mm, "end": v(30.29, 10.65) * mm});
            skLineSegment(sketch, "E8534", {"start": v(30.29, 10.65) * mm, "end": v(30.28, 10.65) * mm});
            skLineSegment(sketch, "E8535", {"start": v(30.28, 10.65) * mm, "end": v(30.28, 10.65) * mm});
            skLineSegment(sketch, "E8536", {"start": v(30.28, 10.65) * mm, "end": v(30.27, 10.65) * mm});
            skLineSegment(sketch, "E8537", {"start": v(30.27, 10.65) * mm, "end": v(30.26, 10.65) * mm});
            skLineSegment(sketch, "E8538", {"start": v(30.26, 10.65) * mm, "end": v(30.24, 10.65) * mm});
            skLineSegment(sketch, "E8539", {"start": v(30.24, 10.65) * mm, "end": v(30.21, 10.66) * mm});
            skLineSegment(sketch, "E8540", {"start": v(30.21, 10.66) * mm, "end": v(30.14, 10.67) * mm});
            skLineSegment(sketch, "E8541", {"start": v(30.14, 10.67) * mm, "end": v(30.07, 10.69) * mm});
            skLineSegment(sketch, "E8542", {"start": v(30.07, 10.69) * mm, "end": v(30, 10.7) * mm});
            skLineSegment(sketch, "E8543", {"start": v(30, 10.7) * mm, "end": v(29.92, 10.72) * mm});
            skLineSegment(sketch, "E8544", {"start": v(29.92, 10.72) * mm, "end": v(29.85, 10.73) * mm});
            skLineSegment(sketch, "E8545", {"start": v(29.85, 10.73) * mm, "end": v(29.77, 10.75) * mm});
            skLineSegment(sketch, "E8546", {"start": v(29.77, 10.75) * mm, "end": v(29.7, 10.77) * mm});
            skLineSegment(sketch, "E8547", {"start": v(29.7, 10.77) * mm, "end": v(29.62, 10.78) * mm});
            skLineSegment(sketch, "E8548", {"start": v(29.62, 10.78) * mm, "end": v(29.59, 10.8) * mm});
            skLineSegment(sketch, "E8549", {"start": v(29.59, 10.8) * mm, "end": v(29.56, 10.82) * mm});
            skLineSegment(sketch, "E8550", {"start": v(29.56, 10.82) * mm, "end": v(29.53, 10.85) * mm});
            skLineSegment(sketch, "E8551", {"start": v(29.53, 10.85) * mm, "end": v(29.52, 10.88) * mm});
            skLineSegment(sketch, "E8552", {"start": v(31.97, 5.52) * mm, "end": v(32.06, 5.5) * mm});
            skLineSegment(sketch, "E8553", {"start": v(32.06, 5.5) * mm, "end": v(32.13, 5.45) * mm});
            skLineSegment(sketch, "E8554", {"start": v(32.13, 5.45) * mm, "end": v(32.2, 5.4) * mm});
            skLineSegment(sketch, "E8555", {"start": v(32.2, 5.4) * mm, "end": v(32.26, 5.33) * mm});
            skLineSegment(sketch, "E8556", {"start": v(32.26, 5.33) * mm, "end": v(32.32, 5.26) * mm});
            skLineSegment(sketch, "E8557", {"start": v(32.32, 5.26) * mm, "end": v(32.37, 5.2) * mm});
            skLineSegment(sketch, "E8558", {"start": v(32.37, 5.2) * mm, "end": v(32.43, 5.11) * mm});
            skLineSegment(sketch, "E8559", {"start": v(32.43, 5.11) * mm, "end": v(32.48, 5.04) * mm});
            skLineSegment(sketch, "E8560", {"start": v(32.48, 5.04) * mm, "end": v(32.49, 5.02) * mm});
            skLineSegment(sketch, "E8561", {"start": v(32.49, 5.02) * mm, "end": v(32.5, 5) * mm});
            skLineSegment(sketch, "E8562", {"start": v(32.5, 5) * mm, "end": v(32.5, 4.99) * mm});
            skLineSegment(sketch, "E8563", {"start": v(32.5, 4.99) * mm, "end": v(32.5, 4.98) * mm});
            skLineSegment(sketch, "E8564", {"start": v(32.5, 4.98) * mm, "end": v(32.51, 4.98) * mm});
            skLineSegment(sketch, "E8565", {"start": v(32.51, 4.98) * mm, "end": v(32.51, 4.97) * mm});
            skLineSegment(sketch, "E8566", {"start": v(32.51, 4.97) * mm, "end": v(32.51, 4.97) * mm});
            skLineSegment(sketch, "E8567", {"start": v(32.51, 4.97) * mm, "end": v(32.53, 4.95) * mm});
            skLineSegment(sketch, "E8568", {"start": v(32.53, 4.95) * mm, "end": v(32.54, 4.92) * mm});
            skLineSegment(sketch, "E8569", {"start": v(32.54, 4.92) * mm, "end": v(32.56, 4.9) * mm});
            skLineSegment(sketch, "E8570", {"start": v(32.56, 4.9) * mm, "end": v(32.57, 4.88) * mm});
            skLineSegment(sketch, "E8571", {"start": v(32.57, 4.88) * mm, "end": v(32.58, 4.86) * mm});
            skLineSegment(sketch, "E8572", {"start": v(32.58, 4.86) * mm, "end": v(32.59, 4.84) * mm});
            skLineSegment(sketch, "E8573", {"start": v(32.59, 4.84) * mm, "end": v(32.6, 4.83) * mm});
            skLineSegment(sketch, "E8574", {"start": v(32.6, 4.83) * mm, "end": v(32.6, 4.82) * mm});
            skLineSegment(sketch, "E8575", {"start": v(32.6, 4.82) * mm, "end": v(32.6, 4.8) * mm});
            skLineSegment(sketch, "E8576", {"start": v(32.6, 4.8) * mm, "end": v(32.6, 4.79) * mm});
            skLineSegment(sketch, "E8577", {"start": v(32.6, 4.79) * mm, "end": v(32.6, 4.76) * mm});
            skLineSegment(sketch, "E8578", {"start": v(32.6, 4.76) * mm, "end": v(32.58, 4.73) * mm});
            skLineSegment(sketch, "E8579", {"start": v(32.58, 4.73) * mm, "end": v(32.57, 4.7) * mm});
            skLineSegment(sketch, "E8580", {"start": v(32.57, 4.7) * mm, "end": v(32.56, 4.65) * mm});
            skLineSegment(sketch, "E8581", {"start": v(32.56, 4.65) * mm, "end": v(32.54, 4.61) * mm});
            skLineSegment(sketch, "E8582", {"start": v(32.54, 4.61) * mm, "end": v(32.52, 4.57) * mm});
            skLineSegment(sketch, "E8583", {"start": v(32.52, 4.57) * mm, "end": v(32.52, 4.57) * mm});
            skLineSegment(sketch, "E8584", {"start": v(32.52, 4.57) * mm, "end": v(32.51, 4.57) * mm});
            skLineSegment(sketch, "E8585", {"start": v(32.51, 4.57) * mm, "end": v(32.5, 4.57) * mm});
            skLineSegment(sketch, "E8586", {"start": v(32.5, 4.57) * mm, "end": v(32.5, 4.57) * mm});
            skLineSegment(sketch, "E8587", {"start": v(32.5, 4.57) * mm, "end": v(32.48, 4.57) * mm});
            skLineSegment(sketch, "E8588", {"start": v(32.48, 4.57) * mm, "end": v(32.46, 4.57) * mm});
            skLineSegment(sketch, "E8589", {"start": v(32.46, 4.57) * mm, "end": v(32.43, 4.57) * mm});
            skLineSegment(sketch, "E8590", {"start": v(32.43, 4.57) * mm, "end": v(32.42, 4.57) * mm});
            skLineSegment(sketch, "E8591", {"start": v(32.42, 4.57) * mm, "end": v(32.4, 4.57) * mm});
            skLineSegment(sketch, "E8592", {"start": v(32.4, 4.57) * mm, "end": v(32.4, 4.57) * mm});
            skLineSegment(sketch, "E8593", {"start": v(32.4, 4.57) * mm, "end": v(32.39, 4.57) * mm});
            skLineSegment(sketch, "E8594", {"start": v(32.39, 4.57) * mm, "end": v(32.38, 4.57) * mm});
            skLineSegment(sketch, "E8595", {"start": v(32.38, 4.57) * mm, "end": v(32.37, 4.57) * mm});
            skLineSegment(sketch, "E8596", {"start": v(32.37, 4.57) * mm, "end": v(32.35, 4.57) * mm});
            skLineSegment(sketch, "E8597", {"start": v(32.35, 4.57) * mm, "end": v(32.34, 4.57) * mm});
            skLineSegment(sketch, "E8598", {"start": v(32.34, 4.57) * mm, "end": v(32.32, 4.58) * mm});
            skLineSegment(sketch, "E8599", {"start": v(32.32, 4.58) * mm, "end": v(32.3, 4.58) * mm});
            skLineSegment(sketch, "E8600", {"start": v(32.3, 4.58) * mm, "end": v(32.27, 4.58) * mm});
            skLineSegment(sketch, "E8601", {"start": v(32.27, 4.58) * mm, "end": v(32.25, 4.59) * mm});
            skLineSegment(sketch, "E8602", {"start": v(32.25, 4.59) * mm, "end": v(32.23, 4.6) * mm});
            skLineSegment(sketch, "E8603", {"start": v(32.23, 4.6) * mm, "end": v(32.2, 4.6) * mm});
            skLineSegment(sketch, "E8604", {"start": v(32.2, 4.6) * mm, "end": v(32.18, 4.6) * mm});
            skLineSegment(sketch, "E8605", {"start": v(32.18, 4.6) * mm, "end": v(32.16, 4.6) * mm});
            skLineSegment(sketch, "E8606", {"start": v(32.16, 4.6) * mm, "end": v(32.1, 4.61) * mm});
            skLineSegment(sketch, "E8607", {"start": v(32.1, 4.61) * mm, "end": v(32.02, 4.62) * mm});
            skLineSegment(sketch, "E8608", {"start": v(32.02, 4.62) * mm, "end": v(31.95, 4.63) * mm});
            skLineSegment(sketch, "E8609", {"start": v(31.95, 4.63) * mm, "end": v(31.88, 4.64) * mm});
            skLineSegment(sketch, "E8610", {"start": v(31.88, 4.64) * mm, "end": v(31.81, 4.66) * mm});
            skLineSegment(sketch, "E8611", {"start": v(31.81, 4.66) * mm, "end": v(31.75, 4.67) * mm});
            skLineSegment(sketch, "E8612", {"start": v(31.75, 4.67) * mm, "end": v(31.68, 4.7) * mm});
            skLineSegment(sketch, "E8613", {"start": v(31.68, 4.7) * mm, "end": v(31.61, 4.71) * mm});
            skLineSegment(sketch, "E8614", {"start": v(31.61, 4.71) * mm, "end": v(31.58, 4.73) * mm});
            skLineSegment(sketch, "E8615", {"start": v(31.58, 4.73) * mm, "end": v(31.55, 4.73) * mm});
            skLineSegment(sketch, "E8616", {"start": v(31.55, 4.73) * mm, "end": v(31.53, 4.74) * mm});
            skLineSegment(sketch, "E8617", {"start": v(31.53, 4.74) * mm, "end": v(31.51, 4.75) * mm});
            skLineSegment(sketch, "E8618", {"start": v(31.51, 4.75) * mm, "end": v(31.5, 4.75) * mm});
            skLineSegment(sketch, "E8619", {"start": v(31.5, 4.75) * mm, "end": v(31.5, 4.75) * mm});
            skLineSegment(sketch, "E8620", {"start": v(31.5, 4.75) * mm, "end": v(31.45, 4.8) * mm});
            skLineSegment(sketch, "E8621", {"start": v(31.45, 4.8) * mm, "end": v(31.41, 4.83) * mm});
            skLineSegment(sketch, "E8622", {"start": v(31.41, 4.83) * mm, "end": v(31.37, 4.87) * mm});
            skLineSegment(sketch, "E8623", {"start": v(31.37, 4.87) * mm, "end": v(31.34, 4.9) * mm});
            skLineSegment(sketch, "E8624", {"start": v(31.34, 4.9) * mm, "end": v(31.31, 4.93) * mm});
            skLineSegment(sketch, "E8625", {"start": v(31.31, 4.93) * mm, "end": v(31.3, 4.95) * mm});
            skLineSegment(sketch, "E8626", {"start": v(31.3, 4.95) * mm, "end": v(31.28, 4.97) * mm});
            skLineSegment(sketch, "E8627", {"start": v(31.28, 4.97) * mm, "end": v(31.27, 4.97) * mm});
            skLineSegment(sketch, "E8628", {"start": v(31.27, 4.97) * mm, "end": v(31.26, 4.98) * mm});
            skLineSegment(sketch, "E8629", {"start": v(31.26, 4.98) * mm, "end": v(31.24, 5) * mm});
            skLineSegment(sketch, "E8630", {"start": v(31.24, 5) * mm, "end": v(31.2, 5.04) * mm});
            skLineSegment(sketch, "E8631", {"start": v(31.2, 5.04) * mm, "end": v(31.15, 5.09) * mm});
            skLineSegment(sketch, "E8632", {"start": v(31.15, 5.09) * mm, "end": v(31.1, 5.15) * mm});
            skLineSegment(sketch, "E8633", {"start": v(31.1, 5.15) * mm, "end": v(31.04, 5.2) * mm});
            skLineSegment(sketch, "E8634", {"start": v(31.04, 5.2) * mm, "end": v(30.97, 5.28) * mm});
            skLineSegment(sketch, "E8635", {"start": v(30.97, 5.28) * mm, "end": v(30.9, 5.35) * mm});
            skLineSegment(sketch, "E8636", {"start": v(30.9, 5.35) * mm, "end": v(30.9, 5.35) * mm});
            skLineSegment(sketch, "E8637", {"start": v(30.9, 5.35) * mm, "end": v(30.9, 5.36) * mm});
            skLineSegment(sketch, "E8638", {"start": v(30.9, 5.36) * mm, "end": v(30.89, 5.36) * mm});
            skLineSegment(sketch, "E8639", {"start": v(30.89, 5.36) * mm, "end": v(30.88, 5.38) * mm});
            skLineSegment(sketch, "E8640", {"start": v(30.88, 5.38) * mm, "end": v(30.86, 5.4) * mm});
            skLineSegment(sketch, "E8641", {"start": v(30.86, 5.4) * mm, "end": v(30.83, 5.43) * mm});
            skLineSegment(sketch, "E8642", {"start": v(30.83, 5.43) * mm, "end": v(30.8, 5.47) * mm});
            skLineSegment(sketch, "E8643", {"start": v(30.8, 5.47) * mm, "end": v(30.75, 5.53) * mm});
            skLineSegment(sketch, "E8644", {"start": v(30.75, 5.53) * mm, "end": v(30.74, 5.55) * mm});
            skLineSegment(sketch, "E8645", {"start": v(30.74, 5.55) * mm, "end": v(30.73, 5.56) * mm});
            skLineSegment(sketch, "E8646", {"start": v(30.73, 5.56) * mm, "end": v(30.73, 5.56) * mm});
            skLineSegment(sketch, "E8647", {"start": v(30.73, 5.56) * mm, "end": v(30.72, 5.57) * mm});
            skLineSegment(sketch, "E8648", {"start": v(30.72, 5.57) * mm, "end": v(30.72, 5.57) * mm});
            skLineSegment(sketch, "E8649", {"start": v(30.72, 5.57) * mm, "end": v(30.71, 5.6) * mm});
            skLineSegment(sketch, "E8650", {"start": v(30.71, 5.6) * mm, "end": v(30.71, 5.63) * mm});
            skLineSegment(sketch, "E8651", {"start": v(30.71, 5.63) * mm, "end": v(30.72, 5.66) * mm});
            skLineSegment(sketch, "E8652", {"start": v(30.72, 5.66) * mm, "end": v(30.73, 5.69) * mm});
            skLineSegment(sketch, "E8653", {"start": v(30.73, 5.69) * mm, "end": v(30.75, 5.71) * mm});
            skLineSegment(sketch, "E8654", {"start": v(30.75, 5.71) * mm, "end": v(30.77, 5.74) * mm});
            skLineSegment(sketch, "E8655", {"start": v(30.77, 5.74) * mm, "end": v(30.8, 5.76) * mm});
            skLineSegment(sketch, "E8656", {"start": v(30.8, 5.76) * mm, "end": v(30.82, 5.78) * mm});
            skLineSegment(sketch, "E8657", {"start": v(30.82, 5.78) * mm, "end": v(30.82, 5.78) * mm});
            skLineSegment(sketch, "E8658", {"start": v(30.82, 5.78) * mm, "end": v(30.83, 5.78) * mm});
            skLineSegment(sketch, "E8659", {"start": v(30.83, 5.78) * mm, "end": v(30.83, 5.78) * mm});
            skLineSegment(sketch, "E8660", {"start": v(30.83, 5.78) * mm, "end": v(30.84, 5.78) * mm});
            skLineSegment(sketch, "E8661", {"start": v(30.84, 5.78) * mm, "end": v(30.85, 5.77) * mm});
            skLineSegment(sketch, "E8662", {"start": v(30.85, 5.77) * mm, "end": v(30.86, 5.77) * mm});
            skLineSegment(sketch, "E8663", {"start": v(30.86, 5.77) * mm, "end": v(30.88, 5.77) * mm});
            skLineSegment(sketch, "E8664", {"start": v(30.88, 5.77) * mm, "end": v(31.04, 5.74) * mm});
            skLineSegment(sketch, "E8665", {"start": v(31.04, 5.74) * mm, "end": v(31.2, 5.71) * mm});
            skLineSegment(sketch, "E8666", {"start": v(31.2, 5.71) * mm, "end": v(31.34, 5.68) * mm});
            skLineSegment(sketch, "E8667", {"start": v(31.34, 5.68) * mm, "end": v(31.48, 5.65) * mm});
            skLineSegment(sketch, "E8668", {"start": v(31.48, 5.65) * mm, "end": v(31.61, 5.62) * mm});
            skLineSegment(sketch, "E8669", {"start": v(31.61, 5.62) * mm, "end": v(31.74, 5.6) * mm});
            skLineSegment(sketch, "E8670", {"start": v(31.74, 5.6) * mm, "end": v(31.86, 5.56) * mm});
            skLineSegment(sketch, "E8671", {"start": v(31.86, 5.56) * mm, "end": v(31.97, 5.52) * mm});
            skLineSegment(sketch, "E8672", {"start": v(32.64, 7.35) * mm, "end": v(32.64, 7.35) * mm});
            skLineSegment(sketch, "E8673", {"start": v(32.64, 7.35) * mm, "end": v(32.64, 7.34) * mm});
            skLineSegment(sketch, "E8674", {"start": v(32.64, 7.34) * mm, "end": v(32.64, 7.34) * mm});
            skLineSegment(sketch, "E8675", {"start": v(32.64, 7.34) * mm, "end": v(32.64, 7.33) * mm});
            skLineSegment(sketch, "E8676", {"start": v(32.64, 7.33) * mm, "end": v(32.64, 7.31) * mm});
            skLineSegment(sketch, "E8677", {"start": v(32.64, 7.31) * mm, "end": v(32.64, 7.3) * mm});
            skLineSegment(sketch, "E8678", {"start": v(32.64, 7.3) * mm, "end": v(32.63, 7.27) * mm});
            skLineSegment(sketch, "E8679", {"start": v(32.63, 7.27) * mm, "end": v(32.62, 7.24) * mm});
            skLineSegment(sketch, "E8680", {"start": v(32.62, 7.24) * mm, "end": v(32.61, 7.22) * mm});
            skLineSegment(sketch, "E8681", {"start": v(32.61, 7.22) * mm, "end": v(32.6, 7.2) * mm});
            skLineSegment(sketch, "E8682", {"start": v(32.6, 7.2) * mm, "end": v(32.58, 7.18) * mm});
            skLineSegment(sketch, "E8683", {"start": v(32.58, 7.18) * mm, "end": v(32.55, 7.16) * mm});
            skLineSegment(sketch, "E8684", {"start": v(32.55, 7.16) * mm, "end": v(32.52, 7.14) * mm});
            skLineSegment(sketch, "E8685", {"start": v(32.52, 7.14) * mm, "end": v(32.5, 7.12) * mm});
            skLineSegment(sketch, "E8686", {"start": v(32.5, 7.12) * mm, "end": v(32.46, 7.1) * mm});
            skLineSegment(sketch, "E8687", {"start": v(32.46, 7.1) * mm, "end": v(32.42, 7.1) * mm});
            skLineSegment(sketch, "E8688", {"start": v(32.42, 7.1) * mm, "end": v(32.38, 7.08) * mm});
            skLineSegment(sketch, "E8689", {"start": v(32.38, 7.08) * mm, "end": v(32.34, 7.06) * mm});
            skLineSegment(sketch, "E8690", {"start": v(32.34, 7.06) * mm, "end": v(32.3, 7.05) * mm});
            skLineSegment(sketch, "E8691", {"start": v(32.3, 7.05) * mm, "end": v(32.27, 7.03) * mm});
            skLineSegment(sketch, "E8692", {"start": v(32.27, 7.03) * mm, "end": v(32.23, 7.01) * mm});
            skLineSegment(sketch, "E8693", {"start": v(32.23, 7.01) * mm, "end": v(32.2, 7) * mm});
            skLineSegment(sketch, "E8694", {"start": v(32.2, 7) * mm, "end": v(32.16, 6.98) * mm});
            skLineSegment(sketch, "E8695", {"start": v(32.16, 6.98) * mm, "end": v(32.12, 6.96) * mm});
            skLineSegment(sketch, "E8696", {"start": v(32.12, 6.96) * mm, "end": v(32.09, 6.95) * mm});
            skLineSegment(sketch, "E8697", {"start": v(32.09, 6.95) * mm, "end": v(32.05, 6.93) * mm});
            skLineSegment(sketch, "E8698", {"start": v(32.05, 6.93) * mm, "end": v(32.02, 6.91) * mm});
            skLineSegment(sketch, "E8699", {"start": v(32.02, 6.91) * mm, "end": v(31.98, 6.9) * mm});
            skLineSegment(sketch, "E8700", {"start": v(31.98, 6.9) * mm, "end": v(31.95, 6.88) * mm});
            skLineSegment(sketch, "E8701", {"start": v(31.95, 6.88) * mm, "end": v(31.91, 6.87) * mm});
            skLineSegment(sketch, "E8702", {"start": v(31.91, 6.87) * mm, "end": v(31.88, 6.86) * mm});
            skLineSegment(sketch, "E8703", {"start": v(31.88, 6.86) * mm, "end": v(31.85, 6.85) * mm});
            skLineSegment(sketch, "E8704", {"start": v(31.85, 6.85) * mm, "end": v(31.82, 6.84) * mm});
            skLineSegment(sketch, "E8705", {"start": v(31.82, 6.84) * mm, "end": v(31.8, 6.84) * mm});
            skLineSegment(sketch, "E8706", {"start": v(31.8, 6.84) * mm, "end": v(31.76, 6.83) * mm});
            skLineSegment(sketch, "E8707", {"start": v(31.76, 6.83) * mm, "end": v(31.73, 6.83) * mm});
            skLineSegment(sketch, "E8708", {"start": v(31.73, 6.83) * mm, "end": v(31.7, 6.83) * mm});
            skLineSegment(sketch, "E8709", {"start": v(31.7, 6.83) * mm, "end": v(31.67, 6.83) * mm});
            skLineSegment(sketch, "E8710", {"start": v(31.67, 6.83) * mm, "end": v(31.64, 6.83) * mm});
            skLineSegment(sketch, "E8711", {"start": v(31.64, 6.83) * mm, "end": v(31.62, 6.83) * mm});
            skLineSegment(sketch, "E8712", {"start": v(31.62, 6.83) * mm, "end": v(31.61, 6.83) * mm});
            skLineSegment(sketch, "E8713", {"start": v(31.61, 6.83) * mm, "end": v(31.6, 6.83) * mm});
            skLineSegment(sketch, "E8714", {"start": v(31.6, 6.83) * mm, "end": v(31.6, 6.83) * mm});
            skLineSegment(sketch, "E8715", {"start": v(31.6, 6.83) * mm, "end": v(31.6, 6.82) * mm});
            skLineSegment(sketch, "E8716", {"start": v(31.6, 6.82) * mm, "end": v(31.6, 6.82) * mm});
            skLineSegment(sketch, "E8717", {"start": v(31.6, 6.82) * mm, "end": v(31.58, 6.82) * mm});
            skLineSegment(sketch, "E8718", {"start": v(31.58, 6.82) * mm, "end": v(31.56, 6.82) * mm});
            skLineSegment(sketch, "E8719", {"start": v(31.56, 6.82) * mm, "end": v(31.55, 6.82) * mm});
            skLineSegment(sketch, "E8720", {"start": v(31.55, 6.82) * mm, "end": v(31.54, 6.82) * mm});
            skLineSegment(sketch, "E8721", {"start": v(31.54, 6.82) * mm, "end": v(31.53, 6.82) * mm});
            skLineSegment(sketch, "E8722", {"start": v(31.53, 6.82) * mm, "end": v(31.52, 6.82) * mm});
            skLineSegment(sketch, "E8723", {"start": v(31.52, 6.82) * mm, "end": v(31.5, 6.82) * mm});
            skLineSegment(sketch, "E8724", {"start": v(31.5, 6.82) * mm, "end": v(31.5, 6.82) * mm});
            skLineSegment(sketch, "E8725", {"start": v(31.5, 6.82) * mm, "end": v(31.49, 6.82) * mm});
            skLineSegment(sketch, "E8726", {"start": v(31.49, 6.82) * mm, "end": v(31.45, 6.83) * mm});
            skLineSegment(sketch, "E8727", {"start": v(31.45, 6.83) * mm, "end": v(31.39, 6.84) * mm});
            skLineSegment(sketch, "E8728", {"start": v(31.39, 6.84) * mm, "end": v(31.3, 6.85) * mm});
            skLineSegment(sketch, "E8729", {"start": v(31.3, 6.85) * mm, "end": v(31.2, 6.86) * mm});
            skLineSegment(sketch, "E8730", {"start": v(31.2, 6.86) * mm, "end": v(31.1, 6.88) * mm});
            skLineSegment(sketch, "E8731", {"start": v(31.1, 6.88) * mm, "end": v(30.97, 6.9) * mm});
            skLineSegment(sketch, "E8732", {"start": v(30.97, 6.9) * mm, "end": v(30.83, 6.92) * mm});
            skLineSegment(sketch, "E8733", {"start": v(30.83, 6.92) * mm, "end": v(30.83, 6.92) * mm});
            skLineSegment(sketch, "E8734", {"start": v(30.83, 6.92) * mm, "end": v(30.82, 6.93) * mm});
            skLineSegment(sketch, "E8735", {"start": v(30.82, 6.93) * mm, "end": v(30.8, 6.94) * mm});
            skLineSegment(sketch, "E8736", {"start": v(30.8, 6.94) * mm, "end": v(30.75, 6.95) * mm});
            skLineSegment(sketch, "E8737", {"start": v(30.75, 6.95) * mm, "end": v(30.69, 6.97) * mm});
            skLineSegment(sketch, "E8738", {"start": v(30.69, 6.97) * mm, "end": v(30.6, 7) * mm});
            skLineSegment(sketch, "E8739", {"start": v(30.6, 7) * mm, "end": v(30.5, 7.03) * mm});
            skLineSegment(sketch, "E8740", {"start": v(30.5, 7.03) * mm, "end": v(30.37, 7.08) * mm});
            skLineSegment(sketch, "E8741", {"start": v(30.37, 7.08) * mm, "end": v(30.26, 7.13) * mm});
            skLineSegment(sketch, "E8742", {"start": v(30.26, 7.13) * mm, "end": v(30.16, 7.2) * mm});
            skLineSegment(sketch, "E8743", {"start": v(30.16, 7.2) * mm, "end": v(30.06, 7.26) * mm});
            skLineSegment(sketch, "E8744", {"start": v(30.06, 7.26) * mm, "end": v(29.97, 7.34) * mm});
            skLineSegment(sketch, "E8745", {"start": v(29.97, 7.34) * mm, "end": v(29.89, 7.41) * mm});
            skLineSegment(sketch, "E8746", {"start": v(29.89, 7.41) * mm, "end": v(29.81, 7.5) * mm});
            skLineSegment(sketch, "E8747", {"start": v(29.81, 7.5) * mm, "end": v(29.74, 7.57) * mm});
            skLineSegment(sketch, "E8748", {"start": v(29.74, 7.57) * mm, "end": v(29.7, 7.61) * mm});
            skLineSegment(sketch, "E8749", {"start": v(29.7, 7.61) * mm, "end": v(29.69, 7.66) * mm});
            skLineSegment(sketch, "E8750", {"start": v(29.69, 7.66) * mm, "end": v(29.67, 7.7) * mm});
            skLineSegment(sketch, "E8751", {"start": v(29.67, 7.7) * mm, "end": v(29.66, 7.76) * mm});
            skLineSegment(sketch, "E8752", {"start": v(29.66, 7.76) * mm, "end": v(29.67, 7.82) * mm});
            skLineSegment(sketch, "E8753", {"start": v(29.67, 7.82) * mm, "end": v(29.68, 7.89) * mm});
            skLineSegment(sketch, "E8754", {"start": v(29.68, 7.89) * mm, "end": v(29.7, 7.96) * mm});
            skLineSegment(sketch, "E8755", {"start": v(29.7, 7.96) * mm, "end": v(29.73, 8.03) * mm});
            skLineSegment(sketch, "E8756", {"start": v(29.73, 8.03) * mm, "end": v(29.74, 8.05) * mm});
            skLineSegment(sketch, "E8757", {"start": v(29.74, 8.05) * mm, "end": v(29.75, 8.07) * mm});
            skLineSegment(sketch, "E8758", {"start": v(29.75, 8.07) * mm, "end": v(29.77, 8.08) * mm});
            skLineSegment(sketch, "E8759", {"start": v(29.77, 8.08) * mm, "end": v(29.79, 8.1) * mm});
            skLineSegment(sketch, "E8760", {"start": v(29.79, 8.1) * mm, "end": v(29.81, 8.1) * mm});
            skLineSegment(sketch, "E8761", {"start": v(29.81, 8.1) * mm, "end": v(29.84, 8.11) * mm});
            skLineSegment(sketch, "E8762", {"start": v(29.84, 8.11) * mm, "end": v(29.88, 8.12) * mm});
            skLineSegment(sketch, "E8763", {"start": v(29.88, 8.12) * mm, "end": v(29.92, 8.12) * mm});
            skLineSegment(sketch, "E8764", {"start": v(29.92, 8.12) * mm, "end": v(29.93, 8.13) * mm});
            skLineSegment(sketch, "E8765", {"start": v(29.93, 8.13) * mm, "end": v(29.94, 8.13) * mm});
            skLineSegment(sketch, "E8766", {"start": v(29.94, 8.13) * mm, "end": v(29.95, 8.13) * mm});
            skLineSegment(sketch, "E8767", {"start": v(29.95, 8.13) * mm, "end": v(29.95, 8.13) * mm});
            skLineSegment(sketch, "E8768", {"start": v(29.95, 8.13) * mm, "end": v(29.96, 8.13) * mm});
            skLineSegment(sketch, "E8769", {"start": v(29.96, 8.13) * mm, "end": v(29.97, 8.13) * mm});
            skLineSegment(sketch, "E8770", {"start": v(29.97, 8.13) * mm, "end": v(29.98, 8.14) * mm});
            skLineSegment(sketch, "E8771", {"start": v(29.98, 8.14) * mm, "end": v(30, 8.14) * mm});
            skLineSegment(sketch, "E8772", {"start": v(30, 8.14) * mm, "end": v(30.02, 8.14) * mm});
            skLineSegment(sketch, "E8773", {"start": v(30.02, 8.14) * mm, "end": v(30.05, 8.15) * mm});
            skLineSegment(sketch, "E8774", {"start": v(30.05, 8.15) * mm, "end": v(30.08, 8.16) * mm});
            skLineSegment(sketch, "E8775", {"start": v(30.08, 8.16) * mm, "end": v(30.1, 8.18) * mm});
            skLineSegment(sketch, "E8776", {"start": v(30.1, 8.18) * mm, "end": v(30.13, 8.19) * mm});
            skLineSegment(sketch, "E8777", {"start": v(30.13, 8.19) * mm, "end": v(30.16, 8.2) * mm});
            skLineSegment(sketch, "E8778", {"start": v(30.16, 8.2) * mm, "end": v(30.19, 8.21) * mm});
            skLineSegment(sketch, "E8779", {"start": v(30.19, 8.21) * mm, "end": v(30.21, 8.23) * mm});
            skLineSegment(sketch, "E8780", {"start": v(30.21, 8.23) * mm, "end": v(30.23, 8.24) * mm});
            skLineSegment(sketch, "E8781", {"start": v(30.23, 8.24) * mm, "end": v(30.25, 8.25) * mm});
            skLineSegment(sketch, "E8782", {"start": v(30.25, 8.25) * mm, "end": v(30.26, 8.25) * mm});
            skLineSegment(sketch, "E8783", {"start": v(30.26, 8.25) * mm, "end": v(30.28, 8.26) * mm});
            skLineSegment(sketch, "E8784", {"start": v(30.28, 8.26) * mm, "end": v(30.3, 8.27) * mm});
            skLineSegment(sketch, "E8785", {"start": v(30.3, 8.27) * mm, "end": v(30.31, 8.28) * mm});
            skLineSegment(sketch, "E8786", {"start": v(30.31, 8.28) * mm, "end": v(30.33, 8.28) * mm});
            skLineSegment(sketch, "E8787", {"start": v(30.33, 8.28) * mm, "end": v(30.35, 8.3) * mm});
            skLineSegment(sketch, "E8788", {"start": v(30.35, 8.3) * mm, "end": v(30.37, 8.3) * mm});
            skLineSegment(sketch, "E8789", {"start": v(30.37, 8.3) * mm, "end": v(30.38, 8.3) * mm});
            skLineSegment(sketch, "E8790", {"start": v(30.38, 8.3) * mm, "end": v(30.4, 8.3) * mm});
            skLineSegment(sketch, "E8791", {"start": v(30.4, 8.3) * mm, "end": v(30.4, 8.31) * mm});
            skLineSegment(sketch, "E8792", {"start": v(30.4, 8.31) * mm, "end": v(30.4, 8.31) * mm});
            skLineSegment(sketch, "E8793", {"start": v(30.4, 8.31) * mm, "end": v(30.44, 8.31) * mm});
            skLineSegment(sketch, "E8794", {"start": v(30.44, 8.31) * mm, "end": v(30.46, 8.32) * mm});
            skLineSegment(sketch, "E8795", {"start": v(30.46, 8.32) * mm, "end": v(30.48, 8.32) * mm});
            skLineSegment(sketch, "E8796", {"start": v(30.48, 8.32) * mm, "end": v(30.5, 8.33) * mm});
            skLineSegment(sketch, "E8797", {"start": v(30.5, 8.33) * mm, "end": v(30.52, 8.34) * mm});
            skLineSegment(sketch, "E8798", {"start": v(30.52, 8.34) * mm, "end": v(30.53, 8.34) * mm});
            skLineSegment(sketch, "E8799", {"start": v(30.53, 8.34) * mm, "end": v(30.54, 8.35) * mm});
            skLineSegment(sketch, "E8800", {"start": v(30.54, 8.35) * mm, "end": v(30.54, 8.36) * mm});
            skLineSegment(sketch, "E8801", {"start": v(30.54, 8.36) * mm, "end": v(30.54, 8.37) * mm});
            skLineSegment(sketch, "E8802", {"start": v(30.54, 8.37) * mm, "end": v(30.54, 8.38) * mm});
            skLineSegment(sketch, "E8803", {"start": v(30.54, 8.38) * mm, "end": v(30.54, 8.38) * mm});
            skLineSegment(sketch, "E8804", {"start": v(30.54, 8.38) * mm, "end": v(30.54, 8.37) * mm});
            skLineSegment(sketch, "E8805", {"start": v(30.54, 8.37) * mm, "end": v(30.54, 8.36) * mm});
            skLineSegment(sketch, "E8806", {"start": v(30.54, 8.36) * mm, "end": v(30.55, 8.35) * mm});
            skLineSegment(sketch, "E8807", {"start": v(30.55, 8.35) * mm, "end": v(30.55, 8.34) * mm});
            skLineSegment(sketch, "E8808", {"start": v(30.55, 8.34) * mm, "end": v(30.57, 8.34) * mm});
            skLineSegment(sketch, "E8809", {"start": v(30.57, 8.34) * mm, "end": v(30.58, 8.33) * mm});
            skLineSegment(sketch, "E8810", {"start": v(30.58, 8.33) * mm, "end": v(30.6, 8.32) * mm});
            skLineSegment(sketch, "E8811", {"start": v(30.6, 8.32) * mm, "end": v(30.62, 8.32) * mm});
            skLineSegment(sketch, "E8812", {"start": v(30.62, 8.32) * mm, "end": v(30.64, 8.31) * mm});
            skLineSegment(sketch, "E8813", {"start": v(30.64, 8.31) * mm, "end": v(30.66, 8.31) * mm});
            skLineSegment(sketch, "E8814", {"start": v(30.66, 8.31) * mm, "end": v(30.66, 8.31) * mm});
            skLineSegment(sketch, "E8815", {"start": v(30.66, 8.31) * mm, "end": v(30.67, 8.31) * mm});
            skLineSegment(sketch, "E8816", {"start": v(30.67, 8.31) * mm, "end": v(30.68, 8.3) * mm});
            skLineSegment(sketch, "E8817", {"start": v(30.68, 8.3) * mm, "end": v(30.69, 8.3) * mm});
            skLineSegment(sketch, "E8818", {"start": v(30.69, 8.3) * mm, "end": v(30.7, 8.3) * mm});
            skLineSegment(sketch, "E8819", {"start": v(30.7, 8.3) * mm, "end": v(30.72, 8.3) * mm});
            skLineSegment(sketch, "E8820", {"start": v(30.72, 8.3) * mm, "end": v(30.75, 8.3) * mm});
            skLineSegment(sketch, "E8821", {"start": v(30.75, 8.3) * mm, "end": v(30.78, 8.3) * mm});
            skLineSegment(sketch, "E8822", {"start": v(30.78, 8.3) * mm, "end": v(30.81, 8.3) * mm});
            skLineSegment(sketch, "E8823", {"start": v(30.81, 8.3) * mm, "end": v(30.84, 8.3) * mm});
            skLineSegment(sketch, "E8824", {"start": v(30.84, 8.3) * mm, "end": v(30.87, 8.3) * mm});
            skLineSegment(sketch, "E8825", {"start": v(30.87, 8.3) * mm, "end": v(30.9, 8.3) * mm});
            skLineSegment(sketch, "E8826", {"start": v(30.9, 8.3) * mm, "end": v(30.93, 8.3) * mm});
            skLineSegment(sketch, "E8827", {"start": v(30.93, 8.3) * mm, "end": v(30.96, 8.3) * mm});
            skLineSegment(sketch, "E8828", {"start": v(30.96, 8.3) * mm, "end": v(31.04, 8.3) * mm});
            skLineSegment(sketch, "E8829", {"start": v(31.04, 8.3) * mm, "end": v(31.1, 8.3) * mm});
            skLineSegment(sketch, "E8830", {"start": v(31.1, 8.3) * mm, "end": v(31.15, 8.3) * mm});
            skLineSegment(sketch, "E8831", {"start": v(31.15, 8.3) * mm, "end": v(31.17, 8.3) * mm});
            skLineSegment(sketch, "E8832", {"start": v(31.17, 8.3) * mm, "end": v(31.2, 8.3) * mm});
            skLineSegment(sketch, "E8833", {"start": v(31.2, 8.3) * mm, "end": v(31.2, 8.3) * mm});
            skLineSegment(sketch, "E8834", {"start": v(31.2, 8.3) * mm, "end": v(31.29, 8.27) * mm});
            skLineSegment(sketch, "E8835", {"start": v(31.29, 8.27) * mm, "end": v(31.37, 8.23) * mm});
            skLineSegment(sketch, "E8836", {"start": v(31.37, 8.23) * mm, "end": v(31.45, 8.2) * mm});
            skLineSegment(sketch, "E8837", {"start": v(31.45, 8.2) * mm, "end": v(31.51, 8.16) * mm});
            skLineSegment(sketch, "E8838", {"start": v(31.51, 8.16) * mm, "end": v(31.57, 8.13) * mm});
            skLineSegment(sketch, "E8839", {"start": v(31.57, 8.13) * mm, "end": v(31.62, 8.11) * mm});
            skLineSegment(sketch, "E8840", {"start": v(31.62, 8.11) * mm, "end": v(31.66, 8.1) * mm});
            skLineSegment(sketch, "E8841", {"start": v(31.66, 8.1) * mm, "end": v(31.67, 8.09) * mm});
            skLineSegment(sketch, "E8842", {"start": v(31.67, 8.09) * mm, "end": v(31.69, 8.08) * mm});
            skLineSegment(sketch, "E8843", {"start": v(31.69, 8.08) * mm, "end": v(31.71, 8.06) * mm});
            skLineSegment(sketch, "E8844", {"start": v(31.71, 8.06) * mm, "end": v(31.74, 8.05) * mm});
            skLineSegment(sketch, "E8845", {"start": v(31.74, 8.05) * mm, "end": v(31.78, 8.03) * mm});
            skLineSegment(sketch, "E8846", {"start": v(31.78, 8.03) * mm, "end": v(31.82, 8) * mm});
            skLineSegment(sketch, "E8847", {"start": v(31.82, 8) * mm, "end": v(31.87, 7.97) * mm});
            skLineSegment(sketch, "E8848", {"start": v(31.87, 7.97) * mm, "end": v(31.91, 7.94) * mm});
            skLineSegment(sketch, "E8849", {"start": v(31.91, 7.94) * mm, "end": v(31.96, 7.91) * mm});
            skLineSegment(sketch, "E8850", {"start": v(31.96, 7.91) * mm, "end": v(32.02, 7.87) * mm});
            skLineSegment(sketch, "E8851", {"start": v(32.02, 7.87) * mm, "end": v(32.1, 7.82) * mm});
            skLineSegment(sketch, "E8852", {"start": v(32.1, 7.82) * mm, "end": v(32.17, 7.77) * mm});
            skLineSegment(sketch, "E8853", {"start": v(32.17, 7.77) * mm, "end": v(32.25, 7.7) * mm});
            skLineSegment(sketch, "E8854", {"start": v(32.25, 7.7) * mm, "end": v(32.33, 7.65) * mm});
            skLineSegment(sketch, "E8855", {"start": v(32.33, 7.65) * mm, "end": v(32.4, 7.6) * mm});
            skLineSegment(sketch, "E8856", {"start": v(32.4, 7.6) * mm, "end": v(32.44, 7.57) * mm});
            skLineSegment(sketch, "E8857", {"start": v(32.44, 7.57) * mm, "end": v(32.46, 7.55) * mm});
            skLineSegment(sketch, "E8858", {"start": v(32.46, 7.55) * mm, "end": v(32.47, 7.54) * mm});
            skLineSegment(sketch, "E8859", {"start": v(32.47, 7.54) * mm, "end": v(32.48, 7.53) * mm});
            skLineSegment(sketch, "E8860", {"start": v(32.48, 7.53) * mm, "end": v(32.5, 7.5) * mm});
            skLineSegment(sketch, "E8861", {"start": v(32.5, 7.5) * mm, "end": v(32.53, 7.48) * mm});
            skLineSegment(sketch, "E8862", {"start": v(32.53, 7.48) * mm, "end": v(32.55, 7.45) * mm});
            skLineSegment(sketch, "E8863", {"start": v(32.55, 7.45) * mm, "end": v(32.58, 7.42) * mm});
            skLineSegment(sketch, "E8864", {"start": v(32.58, 7.42) * mm, "end": v(32.61, 7.38) * mm});
            skLineSegment(sketch, "E8865", {"start": v(32.61, 7.38) * mm, "end": v(32.64, 7.35) * mm});
            skLineSegment(sketch, "E8866", {"start": v(27, 16.47) * mm, "end": v(27, 16.46) * mm});
            skLineSegment(sketch, "E8867", {"start": v(27, 16.46) * mm, "end": v(27, 16.46) * mm});
            skLineSegment(sketch, "E8868", {"start": v(27, 16.46) * mm, "end": v(27, 16.45) * mm});
            skLineSegment(sketch, "E8869", {"start": v(27, 16.45) * mm, "end": v(27.01, 16.44) * mm});
            skLineSegment(sketch, "E8870", {"start": v(27.01, 16.44) * mm, "end": v(27.01, 16.4) * mm});
            skLineSegment(sketch, "E8871", {"start": v(27.01, 16.4) * mm, "end": v(27.02, 16.36) * mm});
            skLineSegment(sketch, "E8872", {"start": v(27.02, 16.36) * mm, "end": v(27.02, 16.32) * mm});
            skLineSegment(sketch, "E8873", {"start": v(27.02, 16.32) * mm, "end": v(27.03, 16.28) * mm});
            skLineSegment(sketch, "E8874", {"start": v(27.03, 16.28) * mm, "end": v(27.03, 16.24) * mm});
            skLineSegment(sketch, "E8875", {"start": v(27.03, 16.24) * mm, "end": v(27.04, 16.2) * mm});
            skLineSegment(sketch, "E8876", {"start": v(27.04, 16.2) * mm, "end": v(27.04, 16.16) * mm});
            skLineSegment(sketch, "E8877", {"start": v(27.04, 16.16) * mm, "end": v(27.05, 16.12) * mm});
            skLineSegment(sketch, "E8878", {"start": v(27.05, 16.12) * mm, "end": v(27.06, 16.07) * mm});
            skLineSegment(sketch, "E8879", {"start": v(27.06, 16.07) * mm, "end": v(27.07, 16.02) * mm});
            skLineSegment(sketch, "E8880", {"start": v(27.07, 16.02) * mm, "end": v(27.08, 15.98) * mm});
            skLineSegment(sketch, "E8881", {"start": v(27.08, 15.98) * mm, "end": v(27.1, 15.93) * mm});
            skLineSegment(sketch, "E8882", {"start": v(27.1, 15.93) * mm, "end": v(27.12, 15.9) * mm});
            skLineSegment(sketch, "E8883", {"start": v(27.12, 15.9) * mm, "end": v(27.14, 15.86) * mm});
            skLineSegment(sketch, "E8884", {"start": v(27.14, 15.86) * mm, "end": v(27.17, 15.82) * mm});
            skLineSegment(sketch, "E8885", {"start": v(27.17, 15.82) * mm, "end": v(27.2, 15.8) * mm});
            skLineSegment(sketch, "E8886", {"start": v(27.2, 15.8) * mm, "end": v(27.22, 15.78) * mm});
            skLineSegment(sketch, "E8887", {"start": v(27.22, 15.78) * mm, "end": v(27.24, 15.77) * mm});
            skLineSegment(sketch, "E8888", {"start": v(27.24, 15.77) * mm, "end": v(27.27, 15.76) * mm});
            skLineSegment(sketch, "E8889", {"start": v(27.27, 15.76) * mm, "end": v(27.3, 15.75) * mm});
            skLineSegment(sketch, "E8890", {"start": v(27.3, 15.75) * mm, "end": v(27.32, 15.75) * mm});
            skLineSegment(sketch, "E8891", {"start": v(27.32, 15.75) * mm, "end": v(27.35, 15.74) * mm});
            skLineSegment(sketch, "E8892", {"start": v(27.35, 15.74) * mm, "end": v(27.38, 15.74) * mm});
            skLineSegment(sketch, "E8893", {"start": v(27.38, 15.74) * mm, "end": v(27.4, 15.74) * mm});
            skLineSegment(sketch, "E8894", {"start": v(27.4, 15.74) * mm, "end": v(27.43, 15.74) * mm});
            skLineSegment(sketch, "E8895", {"start": v(27.43, 15.74) * mm, "end": v(27.46, 15.74) * mm});
            skLineSegment(sketch, "E8896", {"start": v(27.46, 15.74) * mm, "end": v(27.48, 15.74) * mm});
            skLineSegment(sketch, "E8897", {"start": v(27.48, 15.74) * mm, "end": v(27.5, 15.75) * mm});
            skLineSegment(sketch, "E8898", {"start": v(27.5, 15.75) * mm, "end": v(27.52, 15.75) * mm});
            skLineSegment(sketch, "E8899", {"start": v(27.52, 15.75) * mm, "end": v(27.53, 15.75) * mm});
            skLineSegment(sketch, "E8900", {"start": v(27.53, 15.75) * mm, "end": v(27.55, 15.76) * mm});
            skLineSegment(sketch, "E8901", {"start": v(27.55, 15.76) * mm, "end": v(27.56, 15.76) * mm});
            skLineSegment(sketch, "E8902", {"start": v(27.56, 15.76) * mm, "end": v(27.64, 15.78) * mm});
            skLineSegment(sketch, "E8903", {"start": v(27.64, 15.78) * mm, "end": v(27.7, 15.8) * mm});
            skLineSegment(sketch, "E8904", {"start": v(27.7, 15.8) * mm, "end": v(27.78, 15.82) * mm});
            skLineSegment(sketch, "E8905", {"start": v(27.78, 15.82) * mm, "end": v(27.85, 15.84) * mm});
            skLineSegment(sketch, "E8906", {"start": v(27.85, 15.84) * mm, "end": v(27.91, 15.86) * mm});
            skLineSegment(sketch, "E8907", {"start": v(27.91, 15.86) * mm, "end": v(27.98, 15.88) * mm});
            skLineSegment(sketch, "E8908", {"start": v(27.98, 15.88) * mm, "end": v(28.04, 15.9) * mm});
            skLineSegment(sketch, "E8909", {"start": v(28.04, 15.9) * mm, "end": v(28.1, 15.94) * mm});
            skLineSegment(sketch, "E8910", {"start": v(28.1, 15.94) * mm, "end": v(28.24, 16) * mm});
            skLineSegment(sketch, "E8911", {"start": v(28.24, 16) * mm, "end": v(28.37, 16.07) * mm});
            skLineSegment(sketch, "E8912", {"start": v(28.37, 16.07) * mm, "end": v(28.5, 16.15) * mm});
            skLineSegment(sketch, "E8913", {"start": v(28.5, 16.15) * mm, "end": v(28.61, 16.23) * mm});
            skLineSegment(sketch, "E8914", {"start": v(28.61, 16.23) * mm, "end": v(28.72, 16.32) * mm});
            skLineSegment(sketch, "E8915", {"start": v(28.72, 16.32) * mm, "end": v(28.83, 16.41) * mm});
            skLineSegment(sketch, "E8916", {"start": v(28.83, 16.41) * mm, "end": v(28.93, 16.52) * mm});
            skLineSegment(sketch, "E8917", {"start": v(28.93, 16.52) * mm, "end": v(29.03, 16.62) * mm});
            skLineSegment(sketch, "E8918", {"start": v(29.03, 16.62) * mm, "end": v(29.06, 16.67) * mm});
            skLineSegment(sketch, "E8919", {"start": v(29.06, 16.67) * mm, "end": v(29.1, 16.73) * mm});
            skLineSegment(sketch, "E8920", {"start": v(29.1, 16.73) * mm, "end": v(29.13, 16.78) * mm});
            skLineSegment(sketch, "E8921", {"start": v(29.13, 16.78) * mm, "end": v(29.16, 16.85) * mm});
            skLineSegment(sketch, "E8922", {"start": v(29.16, 16.85) * mm, "end": v(29.17, 16.91) * mm});
            skLineSegment(sketch, "E8923", {"start": v(29.17, 16.91) * mm, "end": v(29.18, 16.98) * mm});
            skLineSegment(sketch, "E8924", {"start": v(29.18, 16.98) * mm, "end": v(29.17, 17.06) * mm});
            skLineSegment(sketch, "E8925", {"start": v(29.17, 17.06) * mm, "end": v(29.15, 17.14) * mm});
            skLineSegment(sketch, "E8926", {"start": v(29.15, 17.14) * mm, "end": v(29.15, 17.14) * mm});
            skLineSegment(sketch, "E8927", {"start": v(29.15, 17.14) * mm, "end": v(29.15, 17.15) * mm});
            skLineSegment(sketch, "E8928", {"start": v(29.15, 17.15) * mm, "end": v(29.15, 17.15) * mm});
            skLineSegment(sketch, "E8929", {"start": v(29.15, 17.15) * mm, "end": v(29.14, 17.16) * mm});
            skLineSegment(sketch, "E8930", {"start": v(29.14, 17.16) * mm, "end": v(29.15, 17.18) * mm});
            skLineSegment(sketch, "E8931", {"start": v(29.15, 17.18) * mm, "end": v(29.15, 17.22) * mm});
            skLineSegment(sketch, "E8932", {"start": v(29.15, 17.22) * mm, "end": v(29.15, 17.27) * mm});
            skLineSegment(sketch, "E8933", {"start": v(29.15, 17.27) * mm, "end": v(29.16, 17.33) * mm});
            skLineSegment(sketch, "E8934", {"start": v(29.16, 17.33) * mm, "end": v(29.17, 17.4) * mm});
            skLineSegment(sketch, "E8935", {"start": v(29.17, 17.4) * mm, "end": v(29.18, 17.46) * mm});
            skLineSegment(sketch, "E8936", {"start": v(29.18, 17.46) * mm, "end": v(29.19, 17.54) * mm});
            skLineSegment(sketch, "E8937", {"start": v(29.19, 17.54) * mm, "end": v(29.19, 17.54) * mm});
            skLineSegment(sketch, "E8938", {"start": v(29.19, 17.54) * mm, "end": v(29.18, 17.56) * mm});
            skLineSegment(sketch, "E8939", {"start": v(29.18, 17.56) * mm, "end": v(29.18, 17.57) * mm});
            skLineSegment(sketch, "E8940", {"start": v(29.18, 17.57) * mm, "end": v(29.17, 17.6) * mm});
            skLineSegment(sketch, "E8941", {"start": v(29.17, 17.6) * mm, "end": v(29.16, 17.64) * mm});
            skLineSegment(sketch, "E8942", {"start": v(29.16, 17.64) * mm, "end": v(29.15, 17.7) * mm});
            skLineSegment(sketch, "E8943", {"start": v(29.15, 17.7) * mm, "end": v(29.15, 17.72) * mm});
            skLineSegment(sketch, "E8944", {"start": v(29.15, 17.72) * mm, "end": v(29.14, 17.75) * mm});
            skLineSegment(sketch, "E8945", {"start": v(29.14, 17.75) * mm, "end": v(29.14, 17.77) * mm});
            skLineSegment(sketch, "E8946", {"start": v(29.14, 17.77) * mm, "end": v(29.13, 17.8) * mm});
            skLineSegment(sketch, "E8947", {"start": v(29.13, 17.8) * mm, "end": v(29.13, 17.82) * mm});
            skLineSegment(sketch, "E8948", {"start": v(29.13, 17.82) * mm, "end": v(29.12, 17.85) * mm});
            skLineSegment(sketch, "E8949", {"start": v(29.12, 17.85) * mm, "end": v(29.12, 17.87) * mm});
            skLineSegment(sketch, "E8950", {"start": v(29.12, 17.87) * mm, "end": v(29.12, 17.9) * mm});
            skLineSegment(sketch, "E8951", {"start": v(29.12, 17.9) * mm, "end": v(29.11, 17.95) * mm});
            skLineSegment(sketch, "E8952", {"start": v(29.11, 17.95) * mm, "end": v(29.11, 17.98) * mm});
            skLineSegment(sketch, "E8953", {"start": v(29.11, 17.98) * mm, "end": v(29.11, 18.01) * mm});
            skLineSegment(sketch, "E8954", {"start": v(29.11, 18.01) * mm, "end": v(29.1, 18.03) * mm});
            skLineSegment(sketch, "E8955", {"start": v(29.1, 18.03) * mm, "end": v(29.1, 18.04) * mm});
            skLineSegment(sketch, "E8956", {"start": v(29.1, 18.04) * mm, "end": v(29.1, 18.04) * mm});
            skLineSegment(sketch, "E8957", {"start": v(29.1, 18.04) * mm, "end": v(29.1, 18.05) * mm});
            skLineSegment(sketch, "E8958", {"start": v(29.1, 18.05) * mm, "end": v(29.1, 18.05) * mm});
            skLineSegment(sketch, "E8959", {"start": v(29.1, 18.05) * mm, "end": v(29.09, 18.1) * mm});
            skLineSegment(sketch, "E8960", {"start": v(29.09, 18.1) * mm, "end": v(29.07, 18.16) * mm});
            skLineSegment(sketch, "E8961", {"start": v(29.07, 18.16) * mm, "end": v(29.05, 18.21) * mm});
            skLineSegment(sketch, "E8962", {"start": v(29.05, 18.21) * mm, "end": v(29.03, 18.26) * mm});
            skLineSegment(sketch, "E8963", {"start": v(29.03, 18.26) * mm, "end": v(29.02, 18.3) * mm});
            skLineSegment(sketch, "E8964", {"start": v(29.02, 18.3) * mm, "end": v(29, 18.33) * mm});
            skLineSegment(sketch, "E8965", {"start": v(29, 18.33) * mm, "end": v(29, 18.36) * mm});
            skLineSegment(sketch, "E8966", {"start": v(29, 18.36) * mm, "end": v(28.99, 18.37) * mm});
            skLineSegment(sketch, "E8967", {"start": v(28.99, 18.37) * mm, "end": v(28.99, 18.38) * mm});
            skLineSegment(sketch, "E8968", {"start": v(28.99, 18.38) * mm, "end": v(28.98, 18.4) * mm});
            skLineSegment(sketch, "E8969", {"start": v(28.98, 18.4) * mm, "end": v(28.97, 18.42) * mm});
            skLineSegment(sketch, "E8970", {"start": v(28.97, 18.42) * mm, "end": v(28.96, 18.44) * mm});
            skLineSegment(sketch, "E8971", {"start": v(28.96, 18.44) * mm, "end": v(28.95, 18.46) * mm});
            skLineSegment(sketch, "E8972", {"start": v(28.95, 18.46) * mm, "end": v(28.94, 18.48) * mm});
            skLineSegment(sketch, "E8973", {"start": v(28.94, 18.48) * mm, "end": v(28.93, 18.5) * mm});
            skLineSegment(sketch, "E8974", {"start": v(28.93, 18.5) * mm, "end": v(28.92, 18.53) * mm});
            skLineSegment(sketch, "E8975", {"start": v(28.92, 18.53) * mm, "end": v(28.92, 18.53) * mm});
            skLineSegment(sketch, "E8976", {"start": v(28.92, 18.53) * mm, "end": v(28.91, 18.53) * mm});
            skLineSegment(sketch, "E8977", {"start": v(28.91, 18.53) * mm, "end": v(28.91, 18.53) * mm});
            skLineSegment(sketch, "E8978", {"start": v(28.91, 18.53) * mm, "end": v(28.9, 18.54) * mm});
            skLineSegment(sketch, "E8979", {"start": v(28.9, 18.54) * mm, "end": v(28.9, 18.54) * mm});
            skLineSegment(sketch, "E8980", {"start": v(28.9, 18.54) * mm, "end": v(28.9, 18.55) * mm});
            skLineSegment(sketch, "E8981", {"start": v(28.9, 18.55) * mm, "end": v(28.88, 18.57) * mm});
            skLineSegment(sketch, "E8982", {"start": v(28.88, 18.57) * mm, "end": v(28.88, 18.57) * mm});
            skLineSegment(sketch, "E8983", {"start": v(28.88, 18.57) * mm, "end": v(28.88, 18.58) * mm});
            skLineSegment(sketch, "E8984", {"start": v(28.88, 18.58) * mm, "end": v(28.87, 18.58) * mm});
            skLineSegment(sketch, "E8985", {"start": v(28.87, 18.58) * mm, "end": v(28.87, 18.58) * mm});
            skLineSegment(sketch, "E8986", {"start": v(28.87, 18.58) * mm, "end": v(28.86, 18.6) * mm});
            skLineSegment(sketch, "E8987", {"start": v(28.86, 18.6) * mm, "end": v(28.86, 18.6) * mm});
            skLineSegment(sketch, "E8988", {"start": v(28.86, 18.6) * mm, "end": v(28.85, 18.61) * mm});
            skLineSegment(sketch, "E8989", {"start": v(28.85, 18.61) * mm, "end": v(28.84, 18.62) * mm});
            skLineSegment(sketch, "E8990", {"start": v(28.84, 18.62) * mm, "end": v(28.84, 18.63) * mm});
            skLineSegment(sketch, "E8991", {"start": v(28.84, 18.63) * mm, "end": v(28.83, 18.64) * mm});
            skLineSegment(sketch, "E8992", {"start": v(28.83, 18.64) * mm, "end": v(28.82, 18.65) * mm});
            skLineSegment(sketch, "E8993", {"start": v(28.82, 18.65) * mm, "end": v(28.82, 18.66) * mm});
            skLineSegment(sketch, "E8994", {"start": v(28.82, 18.66) * mm, "end": v(28.8, 18.67) * mm});
            skLineSegment(sketch, "E8995", {"start": v(28.8, 18.67) * mm, "end": v(28.8, 18.67) * mm});
            skLineSegment(sketch, "E8996", {"start": v(28.8, 18.67) * mm, "end": v(28.79, 18.68) * mm});
            skLineSegment(sketch, "E8997", {"start": v(28.79, 18.68) * mm, "end": v(28.78, 18.68) * mm});
            skLineSegment(sketch, "E8998", {"start": v(28.78, 18.68) * mm, "end": v(28.76, 18.67) * mm});
            skLineSegment(sketch, "E8999", {"start": v(28.76, 18.67) * mm, "end": v(28.75, 18.67) * mm});
            skLineSegment(sketch, "E9000", {"start": v(28.75, 18.67) * mm, "end": v(28.73, 18.66) * mm});
            skLineSegment(sketch, "E9001", {"start": v(28.73, 18.66) * mm, "end": v(28.72, 18.65) * mm});
            skLineSegment(sketch, "E9002", {"start": v(28.72, 18.65) * mm, "end": v(28.7, 18.64) * mm});
            skLineSegment(sketch, "E9003", {"start": v(28.7, 18.64) * mm, "end": v(28.69, 18.62) * mm});
            skLineSegment(sketch, "E9004", {"start": v(28.69, 18.62) * mm, "end": v(28.67, 18.6) * mm});
            skLineSegment(sketch, "E9005", {"start": v(28.67, 18.6) * mm, "end": v(28.65, 18.6) * mm});
            skLineSegment(sketch, "E9006", {"start": v(28.65, 18.6) * mm, "end": v(28.63, 18.58) * mm});
            skLineSegment(sketch, "E9007", {"start": v(28.63, 18.58) * mm, "end": v(28.6, 18.56) * mm});
            skLineSegment(sketch, "E9008", {"start": v(28.6, 18.56) * mm, "end": v(28.59, 18.54) * mm});
            skLineSegment(sketch, "E9009", {"start": v(28.59, 18.54) * mm, "end": v(28.57, 18.53) * mm});
            skLineSegment(sketch, "E9010", {"start": v(28.57, 18.53) * mm, "end": v(28.57, 18.53) * mm});
            skLineSegment(sketch, "E9011", {"start": v(28.57, 18.53) * mm, "end": v(28.56, 18.52) * mm});
            skLineSegment(sketch, "E9012", {"start": v(28.56, 18.52) * mm, "end": v(28.56, 18.52) * mm});
            skLineSegment(sketch, "E9013", {"start": v(28.56, 18.52) * mm, "end": v(28.55, 18.5) * mm});
            skLineSegment(sketch, "E9014", {"start": v(28.55, 18.5) * mm, "end": v(28.53, 18.5) * mm});
            skLineSegment(sketch, "E9015", {"start": v(28.53, 18.5) * mm, "end": v(28.53, 18.5) * mm});
            skLineSegment(sketch, "E9016", {"start": v(28.53, 18.5) * mm, "end": v(28.52, 18.49) * mm});
            skLineSegment(sketch, "E9017", {"start": v(28.52, 18.49) * mm, "end": v(28.52, 18.49) * mm});
            skLineSegment(sketch, "E9018", {"start": v(28.52, 18.49) * mm, "end": v(28.52, 18.48) * mm});
            skLineSegment(sketch, "E9019", {"start": v(28.52, 18.48) * mm, "end": v(28.52, 18.48) * mm});
            skLineSegment(sketch, "E9020", {"start": v(28.52, 18.48) * mm, "end": v(28.51, 18.48) * mm});
            skLineSegment(sketch, "E9021", {"start": v(28.51, 18.48) * mm, "end": v(28.5, 18.47) * mm});
            skLineSegment(sketch, "E9022", {"start": v(28.5, 18.47) * mm, "end": v(28.48, 18.46) * mm});
            skLineSegment(sketch, "E9023", {"start": v(28.48, 18.46) * mm, "end": v(28.45, 18.44) * mm});
            skLineSegment(sketch, "E9024", {"start": v(28.45, 18.44) * mm, "end": v(28.42, 18.43) * mm});
            skLineSegment(sketch, "E9025", {"start": v(28.42, 18.43) * mm, "end": v(28.4, 18.4) * mm});
            skLineSegment(sketch, "E9026", {"start": v(28.4, 18.4) * mm, "end": v(28.35, 18.4) * mm});
            skLineSegment(sketch, "E9027", {"start": v(28.35, 18.4) * mm, "end": v(28.32, 18.38) * mm});
            skLineSegment(sketch, "E9028", {"start": v(28.32, 18.38) * mm, "end": v(28.32, 18.38) * mm});
            skLineSegment(sketch, "E9029", {"start": v(28.32, 18.38) * mm, "end": v(28.31, 18.37) * mm});
            skLineSegment(sketch, "E9030", {"start": v(28.31, 18.37) * mm, "end": v(28.31, 18.37) * mm});
            skLineSegment(sketch, "E9031", {"start": v(28.31, 18.37) * mm, "end": v(28.3, 18.37) * mm});
            skLineSegment(sketch, "E9032", {"start": v(28.3, 18.37) * mm, "end": v(28.3, 18.37) * mm});
            skLineSegment(sketch, "E9033", {"start": v(28.3, 18.37) * mm, "end": v(28.28, 18.36) * mm});
            skLineSegment(sketch, "E9034", {"start": v(28.28, 18.36) * mm, "end": v(28.25, 18.35) * mm});
            skLineSegment(sketch, "E9035", {"start": v(28.25, 18.35) * mm, "end": v(28.22, 18.33) * mm});
            skLineSegment(sketch, "E9036", {"start": v(28.22, 18.33) * mm, "end": v(28.19, 18.32) * mm});
            skLineSegment(sketch, "E9037", {"start": v(28.19, 18.32) * mm, "end": v(28.15, 18.3) * mm});
            skLineSegment(sketch, "E9038", {"start": v(28.15, 18.3) * mm, "end": v(28.12, 18.3) * mm});
            skLineSegment(sketch, "E9039", {"start": v(28.12, 18.3) * mm, "end": v(28.09, 18.28) * mm});
            skLineSegment(sketch, "E9040", {"start": v(28.09, 18.28) * mm, "end": v(28.05, 18.26) * mm});
            skLineSegment(sketch, "E9041", {"start": v(28.05, 18.26) * mm, "end": v(28.02, 18.25) * mm});
            skLineSegment(sketch, "E9042", {"start": v(28.02, 18.25) * mm, "end": v(27.99, 18.23) * mm});
            skLineSegment(sketch, "E9043", {"start": v(27.99, 18.23) * mm, "end": v(27.95, 18.22) * mm});
            skLineSegment(sketch, "E9044", {"start": v(27.95, 18.22) * mm, "end": v(27.94, 18.21) * mm});
            skLineSegment(sketch, "E9045", {"start": v(27.94, 18.21) * mm, "end": v(27.92, 18.2) * mm});
            skLineSegment(sketch, "E9046", {"start": v(27.92, 18.2) * mm, "end": v(27.91, 18.2) * mm});
            skLineSegment(sketch, "E9047", {"start": v(27.91, 18.2) * mm, "end": v(27.9, 18.2) * mm});
            skLineSegment(sketch, "E9048", {"start": v(27.9, 18.2) * mm, "end": v(27.88, 18.19) * mm});
            skLineSegment(sketch, "E9049", {"start": v(27.88, 18.19) * mm, "end": v(27.87, 18.18) * mm});
            skLineSegment(sketch, "E9050", {"start": v(27.87, 18.18) * mm, "end": v(27.85, 18.17) * mm});
            skLineSegment(sketch, "E9051", {"start": v(27.85, 18.17) * mm, "end": v(27.84, 18.17) * mm});
            skLineSegment(sketch, "E9052", {"start": v(27.84, 18.17) * mm, "end": v(27.75, 18.13) * mm});
            skLineSegment(sketch, "E9053", {"start": v(27.75, 18.13) * mm, "end": v(27.65, 18.09) * mm});
            skLineSegment(sketch, "E9054", {"start": v(27.65, 18.09) * mm, "end": v(27.57, 18.04) * mm});
            skLineSegment(sketch, "E9055", {"start": v(27.57, 18.04) * mm, "end": v(27.48, 17.98) * mm});
            skLineSegment(sketch, "E9056", {"start": v(27.48, 17.98) * mm, "end": v(27.4, 17.92) * mm});
            skLineSegment(sketch, "E9057", {"start": v(27.4, 17.92) * mm, "end": v(27.32, 17.84) * mm});
            skLineSegment(sketch, "E9058", {"start": v(27.32, 17.84) * mm, "end": v(27.26, 17.74) * mm});
            skLineSegment(sketch, "E9059", {"start": v(27.26, 17.74) * mm, "end": v(27.2, 17.62) * mm});
            skLineSegment(sketch, "E9060", {"start": v(27.2, 17.62) * mm, "end": v(27.17, 17.52) * mm});
            skLineSegment(sketch, "E9061", {"start": v(27.17, 17.52) * mm, "end": v(27.14, 17.44) * mm});
            skLineSegment(sketch, "E9062", {"start": v(27.14, 17.44) * mm, "end": v(27.12, 17.38) * mm});
            skLineSegment(sketch, "E9063", {"start": v(27.12, 17.38) * mm, "end": v(27.1, 17.35) * mm});
            skLineSegment(sketch, "E9064", {"start": v(27.1, 17.35) * mm, "end": v(27.1, 17.32) * mm});
            skLineSegment(sketch, "E9065", {"start": v(27.1, 17.32) * mm, "end": v(27.1, 17.31) * mm});
            skLineSegment(sketch, "E9066", {"start": v(27.1, 17.31) * mm, "end": v(27.1, 17.3) * mm});
            skLineSegment(sketch, "E9067", {"start": v(27.1, 17.3) * mm, "end": v(27.1, 17.3) * mm});
            skLineSegment(sketch, "E9068", {"start": v(27.1, 17.3) * mm, "end": v(27.07, 17.15) * mm});
            skLineSegment(sketch, "E9069", {"start": v(27.07, 17.15) * mm, "end": v(27.06, 17) * mm});
            skLineSegment(sketch, "E9070", {"start": v(27.06, 17) * mm, "end": v(27.04, 16.87) * mm});
            skLineSegment(sketch, "E9071", {"start": v(27.04, 16.87) * mm, "end": v(27.03, 16.74) * mm});
            skLineSegment(sketch, "E9072", {"start": v(27.03, 16.74) * mm, "end": v(27.02, 16.64) * mm});
            skLineSegment(sketch, "E9073", {"start": v(27.02, 16.64) * mm, "end": v(27.01, 16.56) * mm});
            skLineSegment(sketch, "E9074", {"start": v(27.01, 16.56) * mm, "end": v(27, 16.5) * mm});
            skLineSegment(sketch, "E9075", {"start": v(27, 16.5) * mm, "end": v(27, 16.47) * mm});
            skLineSegment(sketch, "E9076", {"start": v(27, 16.47) * mm, "end": v(27, 16.47) * mm});
            skLineSegment(sketch, "E9077", {"start": v(27.64, 17.24) * mm, "end": v(27.64, 17.24) * mm});
            skLineSegment(sketch, "E9078", {"start": v(27.64, 17.24) * mm, "end": v(27.65, 17.25) * mm});
            skLineSegment(sketch, "E9079", {"start": v(27.65, 17.25) * mm, "end": v(27.65, 17.26) * mm});
            skLineSegment(sketch, "E9080", {"start": v(27.65, 17.26) * mm, "end": v(27.65, 17.27) * mm});
            skLineSegment(sketch, "E9081", {"start": v(27.65, 17.27) * mm, "end": v(27.67, 17.35) * mm});
            skLineSegment(sketch, "E9082", {"start": v(27.67, 17.35) * mm, "end": v(27.7, 17.42) * mm});
            skLineSegment(sketch, "E9083", {"start": v(27.7, 17.42) * mm, "end": v(27.75, 17.49) * mm});
            skLineSegment(sketch, "E9084", {"start": v(27.75, 17.49) * mm, "end": v(27.8, 17.55) * mm});
            skLineSegment(sketch, "E9085", {"start": v(27.8, 17.55) * mm, "end": v(27.85, 17.61) * mm});
            skLineSegment(sketch, "E9086", {"start": v(27.85, 17.61) * mm, "end": v(27.92, 17.67) * mm});
            skLineSegment(sketch, "E9087", {"start": v(27.92, 17.67) * mm, "end": v(28, 17.72) * mm});
            skLineSegment(sketch, "E9088", {"start": v(28, 17.72) * mm, "end": v(28.07, 17.77) * mm});
            skLineSegment(sketch, "E9089", {"start": v(28.07, 17.77) * mm, "end": v(28.1, 17.79) * mm});
            skLineSegment(sketch, "E9090", {"start": v(28.1, 17.79) * mm, "end": v(28.12, 17.8) * mm});
            skLineSegment(sketch, "E9091", {"start": v(28.12, 17.8) * mm, "end": v(28.13, 17.8) * mm});
            skLineSegment(sketch, "E9092", {"start": v(28.13, 17.8) * mm, "end": v(28.14, 17.81) * mm});
            skLineSegment(sketch, "E9093", {"start": v(28.14, 17.81) * mm, "end": v(28.15, 17.81) * mm});
            skLineSegment(sketch, "E9094", {"start": v(28.15, 17.81) * mm, "end": v(28.15, 17.82) * mm});
            skLineSegment(sketch, "E9095", {"start": v(28.15, 17.82) * mm, "end": v(28.15, 17.82) * mm});
            skLineSegment(sketch, "E9096", {"start": v(28.15, 17.82) * mm, "end": v(28.19, 17.83) * mm});
            skLineSegment(sketch, "E9097", {"start": v(28.19, 17.83) * mm, "end": v(28.22, 17.84) * mm});
            skLineSegment(sketch, "E9098", {"start": v(28.22, 17.84) * mm, "end": v(28.25, 17.86) * mm});
            skLineSegment(sketch, "E9099", {"start": v(28.25, 17.86) * mm, "end": v(28.28, 17.87) * mm});
            skLineSegment(sketch, "E9100", {"start": v(28.28, 17.87) * mm, "end": v(28.31, 17.88) * mm});
            skLineSegment(sketch, "E9101", {"start": v(28.31, 17.88) * mm, "end": v(28.33, 17.9) * mm});
            skLineSegment(sketch, "E9102", {"start": v(28.33, 17.9) * mm, "end": v(28.35, 17.9) * mm});
            skLineSegment(sketch, "E9103", {"start": v(28.35, 17.9) * mm, "end": v(28.36, 17.9) * mm});
            skLineSegment(sketch, "E9104", {"start": v(28.36, 17.9) * mm, "end": v(28.37, 17.9) * mm});
            skLineSegment(sketch, "E9105", {"start": v(28.37, 17.9) * mm, "end": v(28.39, 17.9) * mm});
            skLineSegment(sketch, "E9106", {"start": v(28.39, 17.9) * mm, "end": v(28.4, 17.9) * mm});
            skLineSegment(sketch, "E9107", {"start": v(28.4, 17.9) * mm, "end": v(28.43, 17.9) * mm});
            skLineSegment(sketch, "E9108", {"start": v(28.43, 17.9) * mm, "end": v(28.45, 17.9) * mm});
            skLineSegment(sketch, "E9109", {"start": v(28.45, 17.9) * mm, "end": v(28.48, 17.9) * mm});
            skLineSegment(sketch, "E9110", {"start": v(28.48, 17.9) * mm, "end": v(28.5, 17.89) * mm});
            skLineSegment(sketch, "E9111", {"start": v(28.5, 17.89) * mm, "end": v(28.53, 17.88) * mm});
            skLineSegment(sketch, "E9112", {"start": v(28.53, 17.88) * mm, "end": v(28.53, 17.88) * mm});
            skLineSegment(sketch, "E9113", {"start": v(28.53, 17.88) * mm, "end": v(28.53, 17.87) * mm});
            skLineSegment(sketch, "E9114", {"start": v(28.53, 17.87) * mm, "end": v(28.53, 17.87) * mm});
            skLineSegment(sketch, "E9115", {"start": v(28.53, 17.87) * mm, "end": v(28.54, 17.86) * mm});
            skLineSegment(sketch, "E9116", {"start": v(28.54, 17.86) * mm, "end": v(28.54, 17.85) * mm});
            skLineSegment(sketch, "E9117", {"start": v(28.54, 17.85) * mm, "end": v(28.55, 17.83) * mm});
            skLineSegment(sketch, "E9118", {"start": v(28.55, 17.83) * mm, "end": v(28.57, 17.76) * mm});
            skLineSegment(sketch, "E9119", {"start": v(28.57, 17.76) * mm, "end": v(28.6, 17.7) * mm});
            skLineSegment(sketch, "E9120", {"start": v(28.6, 17.7) * mm, "end": v(28.6, 17.64) * mm});
            skLineSegment(sketch, "E9121", {"start": v(28.6, 17.64) * mm, "end": v(28.61, 17.58) * mm});
            skLineSegment(sketch, "E9122", {"start": v(28.61, 17.58) * mm, "end": v(28.62, 17.52) * mm});
            skLineSegment(sketch, "E9123", {"start": v(28.62, 17.52) * mm, "end": v(28.61, 17.46) * mm});
            skLineSegment(sketch, "E9124", {"start": v(28.61, 17.46) * mm, "end": v(28.6, 17.4) * mm});
            skLineSegment(sketch, "E9125", {"start": v(28.6, 17.4) * mm, "end": v(28.58, 17.35) * mm});
            skLineSegment(sketch, "E9126", {"start": v(28.58, 17.35) * mm, "end": v(28.57, 17.3) * mm});
            skLineSegment(sketch, "E9127", {"start": v(28.57, 17.3) * mm, "end": v(28.56, 17.27) * mm});
            skLineSegment(sketch, "E9128", {"start": v(28.56, 17.27) * mm, "end": v(28.56, 17.23) * mm});
            skLineSegment(sketch, "E9129", {"start": v(28.56, 17.23) * mm, "end": v(28.55, 17.2) * mm});
            skLineSegment(sketch, "E9130", {"start": v(28.55, 17.2) * mm, "end": v(28.55, 17.15) * mm});
            skLineSegment(sketch, "E9131", {"start": v(28.55, 17.15) * mm, "end": v(28.54, 17.12) * mm});
            skLineSegment(sketch, "E9132", {"start": v(28.54, 17.12) * mm, "end": v(28.54, 17.08) * mm});
            skLineSegment(sketch, "E9133", {"start": v(28.54, 17.08) * mm, "end": v(28.54, 17.04) * mm});
            skLineSegment(sketch, "E9134", {"start": v(28.54, 17.04) * mm, "end": v(28.54, 17.02) * mm});
            skLineSegment(sketch, "E9135", {"start": v(28.54, 17.02) * mm, "end": v(28.54, 17) * mm});
            skLineSegment(sketch, "E9136", {"start": v(28.54, 17) * mm, "end": v(28.53, 16.97) * mm});
            skLineSegment(sketch, "E9137", {"start": v(28.53, 16.97) * mm, "end": v(28.53, 16.95) * mm});
            skLineSegment(sketch, "E9138", {"start": v(28.53, 16.95) * mm, "end": v(28.53, 16.93) * mm});
            skLineSegment(sketch, "E9139", {"start": v(28.53, 16.93) * mm, "end": v(28.53, 16.91) * mm});
            skLineSegment(sketch, "E9140", {"start": v(28.53, 16.91) * mm, "end": v(28.53, 16.89) * mm});
            skLineSegment(sketch, "E9141", {"start": v(28.53, 16.89) * mm, "end": v(28.52, 16.87) * mm});
            skLineSegment(sketch, "E9142", {"start": v(28.52, 16.87) * mm, "end": v(28.52, 16.85) * mm});
            skLineSegment(sketch, "E9143", {"start": v(28.52, 16.85) * mm, "end": v(28.52, 16.83) * mm});
            skLineSegment(sketch, "E9144", {"start": v(28.52, 16.83) * mm, "end": v(28.51, 16.8) * mm});
            skLineSegment(sketch, "E9145", {"start": v(28.51, 16.8) * mm, "end": v(28.5, 16.79) * mm});
            skLineSegment(sketch, "E9146", {"start": v(28.5, 16.79) * mm, "end": v(28.5, 16.77) * mm});
            skLineSegment(sketch, "E9147", {"start": v(28.5, 16.77) * mm, "end": v(28.5, 16.75) * mm});
            skLineSegment(sketch, "E9148", {"start": v(28.5, 16.75) * mm, "end": v(28.5, 16.73) * mm});
            skLineSegment(sketch, "E9149", {"start": v(28.5, 16.73) * mm, "end": v(28.48, 16.7) * mm});
            skLineSegment(sketch, "E9150", {"start": v(28.48, 16.7) * mm, "end": v(28.47, 16.7) * mm});
            skLineSegment(sketch, "E9151", {"start": v(28.47, 16.7) * mm, "end": v(28.46, 16.67) * mm});
            skLineSegment(sketch, "E9152", {"start": v(28.46, 16.67) * mm, "end": v(28.45, 16.65) * mm});
            skLineSegment(sketch, "E9153", {"start": v(28.45, 16.65) * mm, "end": v(28.43, 16.64) * mm});
            skLineSegment(sketch, "E9154", {"start": v(28.43, 16.64) * mm, "end": v(28.4, 16.62) * mm});
            skLineSegment(sketch, "E9155", {"start": v(28.4, 16.62) * mm, "end": v(28.39, 16.6) * mm});
            skLineSegment(sketch, "E9156", {"start": v(28.39, 16.6) * mm, "end": v(28.37, 16.6) * mm});
            skLineSegment(sketch, "E9157", {"start": v(28.37, 16.6) * mm, "end": v(28.35, 16.6) * mm});
            skLineSegment(sketch, "E9158", {"start": v(28.35, 16.6) * mm, "end": v(28.33, 16.6) * mm});
            skLineSegment(sketch, "E9159", {"start": v(28.33, 16.6) * mm, "end": v(28.32, 16.61) * mm});
            skLineSegment(sketch, "E9160", {"start": v(28.32, 16.61) * mm, "end": v(28.32, 16.63) * mm});
            skLineSegment(sketch, "E9161", {"start": v(28.32, 16.63) * mm, "end": v(28.33, 16.64) * mm});
            skLineSegment(sketch, "E9162", {"start": v(28.33, 16.64) * mm, "end": v(28.34, 16.66) * mm});
            skLineSegment(sketch, "E9163", {"start": v(28.34, 16.66) * mm, "end": v(28.35, 16.67) * mm});
            skLineSegment(sketch, "E9164", {"start": v(28.35, 16.67) * mm, "end": v(28.36, 16.69) * mm});
            skLineSegment(sketch, "E9165", {"start": v(28.36, 16.69) * mm, "end": v(28.37, 16.7) * mm});
            skLineSegment(sketch, "E9166", {"start": v(28.37, 16.7) * mm, "end": v(28.38, 16.7) * mm});
            skLineSegment(sketch, "E9167", {"start": v(28.38, 16.7) * mm, "end": v(28.4, 16.7) * mm});
            skLineSegment(sketch, "E9168", {"start": v(28.4, 16.7) * mm, "end": v(28.4, 16.72) * mm});
            skLineSegment(sketch, "E9169", {"start": v(28.4, 16.72) * mm, "end": v(28.42, 16.73) * mm});
            skLineSegment(sketch, "E9170", {"start": v(28.42, 16.73) * mm, "end": v(28.43, 16.74) * mm});
            skLineSegment(sketch, "E9171", {"start": v(28.43, 16.74) * mm, "end": v(28.44, 16.75) * mm});
            skLineSegment(sketch, "E9172", {"start": v(28.44, 16.75) * mm, "end": v(28.45, 16.76) * mm});
            skLineSegment(sketch, "E9173", {"start": v(28.45, 16.76) * mm, "end": v(28.45, 16.77) * mm});
            skLineSegment(sketch, "E9174", {"start": v(28.45, 16.77) * mm, "end": v(28.45, 16.77) * mm});
            skLineSegment(sketch, "E9175", {"start": v(28.45, 16.77) * mm, "end": v(28.45, 16.78) * mm});
            skLineSegment(sketch, "E9176", {"start": v(28.45, 16.78) * mm, "end": v(28.45, 16.8) * mm});
            skLineSegment(sketch, "E9177", {"start": v(28.45, 16.8) * mm, "end": v(28.45, 16.82) * mm});
            skLineSegment(sketch, "E9178", {"start": v(28.45, 16.82) * mm, "end": v(28.45, 16.86) * mm});
            skLineSegment(sketch, "E9179", {"start": v(28.45, 16.86) * mm, "end": v(28.45, 16.92) * mm});
            skLineSegment(sketch, "E9180", {"start": v(28.45, 16.92) * mm, "end": v(28.45, 17) * mm});
            skLineSegment(sketch, "E9181", {"start": v(28.45, 17) * mm, "end": v(28.44, 17.01) * mm});
            skLineSegment(sketch, "E9182", {"start": v(28.44, 17.01) * mm, "end": v(28.44, 17.03) * mm});
            skLineSegment(sketch, "E9183", {"start": v(28.44, 17.03) * mm, "end": v(28.43, 17.05) * mm});
            skLineSegment(sketch, "E9184", {"start": v(28.43, 17.05) * mm, "end": v(28.43, 17.07) * mm});
            skLineSegment(sketch, "E9185", {"start": v(28.43, 17.07) * mm, "end": v(28.42, 17.08) * mm});
            skLineSegment(sketch, "E9186", {"start": v(28.42, 17.08) * mm, "end": v(28.4, 17.1) * mm});
            skLineSegment(sketch, "E9187", {"start": v(28.4, 17.1) * mm, "end": v(28.4, 17.11) * mm});
            skLineSegment(sketch, "E9188", {"start": v(28.4, 17.11) * mm, "end": v(28.38, 17.12) * mm});
            skLineSegment(sketch, "E9189", {"start": v(28.38, 17.12) * mm, "end": v(28.36, 17.14) * mm});
            skLineSegment(sketch, "E9190", {"start": v(28.36, 17.14) * mm, "end": v(28.35, 17.17) * mm});
            skLineSegment(sketch, "E9191", {"start": v(28.35, 17.17) * mm, "end": v(28.35, 17.2) * mm});
            skLineSegment(sketch, "E9192", {"start": v(28.35, 17.2) * mm, "end": v(28.36, 17.22) * mm});
            skLineSegment(sketch, "E9193", {"start": v(28.36, 17.22) * mm, "end": v(28.37, 17.25) * mm});
            skLineSegment(sketch, "E9194", {"start": v(28.37, 17.25) * mm, "end": v(28.38, 17.28) * mm});
            skLineSegment(sketch, "E9195", {"start": v(28.38, 17.28) * mm, "end": v(28.4, 17.3) * mm});
            skLineSegment(sketch, "E9196", {"start": v(28.4, 17.3) * mm, "end": v(28.4, 17.32) * mm});
            skLineSegment(sketch, "E9197", {"start": v(28.4, 17.32) * mm, "end": v(28.4, 17.34) * mm});
            skLineSegment(sketch, "E9198", {"start": v(28.4, 17.34) * mm, "end": v(28.4, 17.35) * mm});
            skLineSegment(sketch, "E9199", {"start": v(28.4, 17.35) * mm, "end": v(28.4, 17.36) * mm});
            skLineSegment(sketch, "E9200", {"start": v(28.4, 17.36) * mm, "end": v(28.4, 17.37) * mm});
            skLineSegment(sketch, "E9201", {"start": v(28.4, 17.37) * mm, "end": v(28.4, 17.38) * mm});
            skLineSegment(sketch, "E9202", {"start": v(28.4, 17.38) * mm, "end": v(28.4, 17.39) * mm});
            skLineSegment(sketch, "E9203", {"start": v(28.4, 17.39) * mm, "end": v(28.4, 17.4) * mm});
            skLineSegment(sketch, "E9204", {"start": v(28.4, 17.4) * mm, "end": v(28.39, 17.4) * mm});
            skLineSegment(sketch, "E9205", {"start": v(28.39, 17.4) * mm, "end": v(28.37, 17.4) * mm});
            skLineSegment(sketch, "E9206", {"start": v(28.37, 17.4) * mm, "end": v(28.36, 17.41) * mm});
            skLineSegment(sketch, "E9207", {"start": v(28.36, 17.41) * mm, "end": v(28.33, 17.42) * mm});
            skLineSegment(sketch, "E9208", {"start": v(28.33, 17.42) * mm, "end": v(28.3, 17.44) * mm});
            skLineSegment(sketch, "E9209", {"start": v(28.3, 17.44) * mm, "end": v(28.27, 17.45) * mm});
            skLineSegment(sketch, "E9210", {"start": v(28.27, 17.45) * mm, "end": v(28.24, 17.47) * mm});
            skLineSegment(sketch, "E9211", {"start": v(28.24, 17.47) * mm, "end": v(28.2, 17.48) * mm});
            skLineSegment(sketch, "E9212", {"start": v(28.2, 17.48) * mm, "end": v(28.16, 17.5) * mm});
            skLineSegment(sketch, "E9213", {"start": v(28.16, 17.5) * mm, "end": v(28.16, 17.5) * mm});
            skLineSegment(sketch, "E9214", {"start": v(28.16, 17.5) * mm, "end": v(28.15, 17.5) * mm});
            skLineSegment(sketch, "E9215", {"start": v(28.15, 17.5) * mm, "end": v(28.14, 17.5) * mm});
            skLineSegment(sketch, "E9216", {"start": v(28.14, 17.5) * mm, "end": v(28.12, 17.5) * mm});
            skLineSegment(sketch, "E9217", {"start": v(28.12, 17.5) * mm, "end": v(28.1, 17.5) * mm});
            skLineSegment(sketch, "E9218", {"start": v(28.1, 17.5) * mm, "end": v(28.07, 17.5) * mm});
            skLineSegment(sketch, "E9219", {"start": v(28.07, 17.5) * mm, "end": v(28.02, 17.5) * mm});
            skLineSegment(sketch, "E9220", {"start": v(28.02, 17.5) * mm, "end": v(27.97, 17.48) * mm});
            skLineSegment(sketch, "E9221", {"start": v(27.97, 17.48) * mm, "end": v(27.93, 17.47) * mm});
            skLineSegment(sketch, "E9222", {"start": v(27.93, 17.47) * mm, "end": v(27.88, 17.45) * mm});
            skLineSegment(sketch, "E9223", {"start": v(27.88, 17.45) * mm, "end": v(27.83, 17.42) * mm});
            skLineSegment(sketch, "E9224", {"start": v(27.83, 17.42) * mm, "end": v(27.8, 17.4) * mm});
            skLineSegment(sketch, "E9225", {"start": v(27.8, 17.4) * mm, "end": v(27.75, 17.35) * mm});
            skLineSegment(sketch, "E9226", {"start": v(27.75, 17.35) * mm, "end": v(27.7, 17.31) * mm});
            skLineSegment(sketch, "E9227", {"start": v(27.7, 17.31) * mm, "end": v(27.7, 17.3) * mm});
            skLineSegment(sketch, "E9228", {"start": v(27.7, 17.3) * mm, "end": v(27.69, 17.29) * mm});
            skLineSegment(sketch, "E9229", {"start": v(27.69, 17.29) * mm, "end": v(27.68, 17.28) * mm});
            skLineSegment(sketch, "E9230", {"start": v(27.68, 17.28) * mm, "end": v(27.68, 17.28) * mm});
            skLineSegment(sketch, "E9231", {"start": v(27.68, 17.28) * mm, "end": v(27.68, 17.27) * mm});
            skLineSegment(sketch, "E9232", {"start": v(27.68, 17.27) * mm, "end": v(27.68, 17.27) * mm});
            skLineSegment(sketch, "E9233", {"start": v(27.68, 17.27) * mm, "end": v(27.67, 17.25) * mm});
            skLineSegment(sketch, "E9234", {"start": v(27.67, 17.25) * mm, "end": v(27.66, 17.24) * mm});
            skLineSegment(sketch, "E9235", {"start": v(27.66, 17.24) * mm, "end": v(27.65, 17.23) * mm});
            skLineSegment(sketch, "E9236", {"start": v(27.65, 17.23) * mm, "end": v(27.65, 17.22) * mm});
            skLineSegment(sketch, "E9237", {"start": v(27.65, 17.22) * mm, "end": v(27.64, 17.22) * mm});
            skLineSegment(sketch, "E9238", {"start": v(27.64, 17.22) * mm, "end": v(27.64, 17.22) * mm});
            skLineSegment(sketch, "E9239", {"start": v(27.64, 17.22) * mm, "end": v(27.64, 17.24) * mm});
            skLineSegment(sketch, "E9240", {"start": v(22.35, 17.8) * mm, "end": v(22.35, 17.78) * mm});
            skLineSegment(sketch, "E9241", {"start": v(22.35, 17.78) * mm, "end": v(22.36, 17.76) * mm});
            skLineSegment(sketch, "E9242", {"start": v(22.36, 17.76) * mm, "end": v(22.36, 17.74) * mm});
            skLineSegment(sketch, "E9243", {"start": v(22.36, 17.74) * mm, "end": v(22.37, 17.7) * mm});
            skLineSegment(sketch, "E9244", {"start": v(22.37, 17.7) * mm, "end": v(22.38, 17.65) * mm});
            skLineSegment(sketch, "E9245", {"start": v(22.38, 17.65) * mm, "end": v(22.39, 17.59) * mm});
            skLineSegment(sketch, "E9246", {"start": v(22.39, 17.59) * mm, "end": v(22.4, 17.53) * mm});
            skLineSegment(sketch, "E9247", {"start": v(22.4, 17.53) * mm, "end": v(22.42, 17.46) * mm});
            skLineSegment(sketch, "E9248", {"start": v(22.42, 17.46) * mm, "end": v(22.44, 17.4) * mm});
            skLineSegment(sketch, "E9249", {"start": v(22.44, 17.4) * mm, "end": v(22.46, 17.33) * mm});
            skLineSegment(sketch, "E9250", {"start": v(22.46, 17.33) * mm, "end": v(22.48, 17.26) * mm});
            skLineSegment(sketch, "E9251", {"start": v(22.48, 17.26) * mm, "end": v(22.5, 17.19) * mm});
            skLineSegment(sketch, "E9252", {"start": v(22.5, 17.19) * mm, "end": v(22.54, 17.11) * mm});
            skLineSegment(sketch, "E9253", {"start": v(22.54, 17.11) * mm, "end": v(22.57, 17.05) * mm});
            skLineSegment(sketch, "E9254", {"start": v(22.57, 17.05) * mm, "end": v(22.6, 17) * mm});
            skLineSegment(sketch, "E9255", {"start": v(22.6, 17) * mm, "end": v(22.62, 16.93) * mm});
            skLineSegment(sketch, "E9256", {"start": v(22.62, 16.93) * mm, "end": v(22.66, 16.88) * mm});
            skLineSegment(sketch, "E9257", {"start": v(22.66, 16.88) * mm, "end": v(22.69, 16.82) * mm});
            skLineSegment(sketch, "E9258", {"start": v(22.69, 16.82) * mm, "end": v(22.72, 16.76) * mm});
            skLineSegment(sketch, "E9259", {"start": v(22.72, 16.76) * mm, "end": v(22.75, 16.71) * mm});
            skLineSegment(sketch, "E9260", {"start": v(22.75, 16.71) * mm, "end": v(22.78, 16.66) * mm});
            skLineSegment(sketch, "E9261", {"start": v(22.78, 16.66) * mm, "end": v(22.82, 16.6) * mm});
            skLineSegment(sketch, "E9262", {"start": v(22.82, 16.6) * mm, "end": v(22.85, 16.56) * mm});
            skLineSegment(sketch, "E9263", {"start": v(22.85, 16.56) * mm, "end": v(22.88, 16.5) * mm});
            skLineSegment(sketch, "E9264", {"start": v(22.88, 16.5) * mm, "end": v(22.92, 16.45) * mm});
            skLineSegment(sketch, "E9265", {"start": v(22.92, 16.45) * mm, "end": v(22.96, 16.4) * mm});
            skLineSegment(sketch, "E9266", {"start": v(22.96, 16.4) * mm, "end": v(23, 16.35) * mm});
            skLineSegment(sketch, "E9267", {"start": v(23, 16.35) * mm, "end": v(23.04, 16.3) * mm});
            skLineSegment(sketch, "E9268", {"start": v(23.04, 16.3) * mm, "end": v(23.08, 16.26) * mm});
            skLineSegment(sketch, "E9269", {"start": v(23.08, 16.26) * mm, "end": v(23.12, 16.23) * mm});
            skLineSegment(sketch, "E9270", {"start": v(23.12, 16.23) * mm, "end": v(23.15, 16.2) * mm});
            skLineSegment(sketch, "E9271", {"start": v(23.15, 16.2) * mm, "end": v(23.18, 16.18) * mm});
            skLineSegment(sketch, "E9272", {"start": v(23.18, 16.18) * mm, "end": v(23.22, 16.16) * mm});
            skLineSegment(sketch, "E9273", {"start": v(23.22, 16.16) * mm, "end": v(23.25, 16.15) * mm});
            skLineSegment(sketch, "E9274", {"start": v(23.25, 16.15) * mm, "end": v(23.28, 16.14) * mm});
            skLineSegment(sketch, "E9275", {"start": v(23.28, 16.14) * mm, "end": v(23.3, 16.14) * mm});
            skLineSegment(sketch, "E9276", {"start": v(23.3, 16.14) * mm, "end": v(23.33, 16.14) * mm});
            skLineSegment(sketch, "E9277", {"start": v(23.33, 16.14) * mm, "end": v(23.38, 16.14) * mm});
            skLineSegment(sketch, "E9278", {"start": v(23.38, 16.14) * mm, "end": v(23.42, 16.16) * mm});
            skLineSegment(sketch, "E9279", {"start": v(23.42, 16.16) * mm, "end": v(23.47, 16.18) * mm});
            skLineSegment(sketch, "E9280", {"start": v(23.47, 16.18) * mm, "end": v(23.5, 16.2) * mm});
            skLineSegment(sketch, "E9281", {"start": v(23.5, 16.2) * mm, "end": v(23.54, 16.24) * mm});
            skLineSegment(sketch, "E9282", {"start": v(23.54, 16.24) * mm, "end": v(23.58, 16.29) * mm});
            skLineSegment(sketch, "E9283", {"start": v(23.58, 16.29) * mm, "end": v(23.6, 16.34) * mm});
            skLineSegment(sketch, "E9284", {"start": v(23.6, 16.34) * mm, "end": v(23.63, 16.4) * mm});
            skLineSegment(sketch, "E9285", {"start": v(23.63, 16.4) * mm, "end": v(23.64, 16.4) * mm});
            skLineSegment(sketch, "E9286", {"start": v(23.64, 16.4) * mm, "end": v(23.64, 16.41) * mm});
            skLineSegment(sketch, "E9287", {"start": v(23.64, 16.41) * mm, "end": v(23.64, 16.42) * mm});
            skLineSegment(sketch, "E9288", {"start": v(23.64, 16.42) * mm, "end": v(23.65, 16.43) * mm});
            skLineSegment(sketch, "E9289", {"start": v(23.65, 16.43) * mm, "end": v(23.65, 16.44) * mm});
            skLineSegment(sketch, "E9290", {"start": v(23.65, 16.44) * mm, "end": v(23.66, 16.44) * mm});
            skLineSegment(sketch, "E9291", {"start": v(23.66, 16.44) * mm, "end": v(23.66, 16.45) * mm});
            skLineSegment(sketch, "E9292", {"start": v(23.66, 16.45) * mm, "end": v(23.67, 16.46) * mm});
            skLineSegment(sketch, "E9293", {"start": v(23.67, 16.46) * mm, "end": v(23.69, 16.49) * mm});
            skLineSegment(sketch, "E9294", {"start": v(23.69, 16.49) * mm, "end": v(23.7, 16.51) * mm});
            skLineSegment(sketch, "E9295", {"start": v(23.7, 16.51) * mm, "end": v(23.73, 16.54) * mm});
            skLineSegment(sketch, "E9296", {"start": v(23.73, 16.54) * mm, "end": v(23.75, 16.57) * mm});
            skLineSegment(sketch, "E9297", {"start": v(23.75, 16.57) * mm, "end": v(23.77, 16.6) * mm});
            skLineSegment(sketch, "E9298", {"start": v(23.77, 16.6) * mm, "end": v(23.8, 16.62) * mm});
            skLineSegment(sketch, "E9299", {"start": v(23.8, 16.62) * mm, "end": v(23.81, 16.65) * mm});
            skLineSegment(sketch, "E9300", {"start": v(23.81, 16.65) * mm, "end": v(23.83, 16.67) * mm});
            skLineSegment(sketch, "E9301", {"start": v(23.83, 16.67) * mm, "end": v(23.88, 16.74) * mm});
            skLineSegment(sketch, "E9302", {"start": v(23.88, 16.74) * mm, "end": v(23.94, 16.8) * mm});
            skLineSegment(sketch, "E9303", {"start": v(23.94, 16.8) * mm, "end": v(23.99, 16.88) * mm});
            skLineSegment(sketch, "E9304", {"start": v(23.99, 16.88) * mm, "end": v(24.04, 16.95) * mm});
            skLineSegment(sketch, "E9305", {"start": v(24.04, 16.95) * mm, "end": v(24.08, 17.02) * mm});
            skLineSegment(sketch, "E9306", {"start": v(24.08, 17.02) * mm, "end": v(24.12, 17.1) * mm});
            skLineSegment(sketch, "E9307", {"start": v(24.12, 17.1) * mm, "end": v(24.16, 17.18) * mm});
            skLineSegment(sketch, "E9308", {"start": v(24.16, 17.18) * mm, "end": v(24.19, 17.26) * mm});
            skLineSegment(sketch, "E9309", {"start": v(24.19, 17.26) * mm, "end": v(24.2, 17.32) * mm});
            skLineSegment(sketch, "E9310", {"start": v(24.2, 17.32) * mm, "end": v(24.22, 17.37) * mm});
            skLineSegment(sketch, "E9311", {"start": v(24.22, 17.37) * mm, "end": v(24.23, 17.4) * mm});
            skLineSegment(sketch, "E9312", {"start": v(24.23, 17.4) * mm, "end": v(24.24, 17.42) * mm});
            skLineSegment(sketch, "E9313", {"start": v(24.24, 17.42) * mm, "end": v(24.24, 17.44) * mm});
            skLineSegment(sketch, "E9314", {"start": v(24.24, 17.44) * mm, "end": v(24.24, 17.45) * mm});
            skLineSegment(sketch, "E9315", {"start": v(24.24, 17.45) * mm, "end": v(24.25, 17.45) * mm});
            skLineSegment(sketch, "E9316", {"start": v(24.25, 17.45) * mm, "end": v(24.25, 17.45) * mm});
            skLineSegment(sketch, "E9317", {"start": v(24.25, 17.45) * mm, "end": v(24.27, 17.52) * mm});
            skLineSegment(sketch, "E9318", {"start": v(24.27, 17.52) * mm, "end": v(24.3, 17.6) * mm});
            skLineSegment(sketch, "E9319", {"start": v(24.3, 17.6) * mm, "end": v(24.32, 17.67) * mm});
            skLineSegment(sketch, "E9320", {"start": v(24.32, 17.67) * mm, "end": v(24.34, 17.74) * mm});
            skLineSegment(sketch, "E9321", {"start": v(24.34, 17.74) * mm, "end": v(24.36, 17.8) * mm});
            skLineSegment(sketch, "E9322", {"start": v(24.36, 17.8) * mm, "end": v(24.38, 17.86) * mm});
            skLineSegment(sketch, "E9323", {"start": v(24.38, 17.86) * mm, "end": v(24.4, 17.9) * mm});
            skLineSegment(sketch, "E9324", {"start": v(24.4, 17.9) * mm, "end": v(24.4, 17.94) * mm});
            skLineSegment(sketch, "E9325", {"start": v(24.4, 17.94) * mm, "end": v(24.41, 17.97) * mm});
            skLineSegment(sketch, "E9326", {"start": v(24.41, 17.97) * mm, "end": v(24.42, 18) * mm});
            skLineSegment(sketch, "E9327", {"start": v(24.42, 18) * mm, "end": v(24.42, 18.02) * mm});
            skLineSegment(sketch, "E9328", {"start": v(24.42, 18.02) * mm, "end": v(24.43, 18.04) * mm});
            skLineSegment(sketch, "E9329", {"start": v(24.43, 18.04) * mm, "end": v(24.43, 18.06) * mm});
            skLineSegment(sketch, "E9330", {"start": v(24.43, 18.06) * mm, "end": v(24.43, 18.08) * mm});
            skLineSegment(sketch, "E9331", {"start": v(24.43, 18.08) * mm, "end": v(24.43, 18.1) * mm});
            skLineSegment(sketch, "E9332", {"start": v(24.43, 18.1) * mm, "end": v(24.43, 18.1) * mm});
            skLineSegment(sketch, "E9333", {"start": v(24.43, 18.1) * mm, "end": v(24.42, 18.12) * mm});
            skLineSegment(sketch, "E9334", {"start": v(24.42, 18.12) * mm, "end": v(24.42, 18.13) * mm});
            skLineSegment(sketch, "E9335", {"start": v(24.42, 18.13) * mm, "end": v(24.41, 18.14) * mm});
            skLineSegment(sketch, "E9336", {"start": v(24.41, 18.14) * mm, "end": v(24.41, 18.15) * mm});
            skLineSegment(sketch, "E9337", {"start": v(24.41, 18.15) * mm, "end": v(24.4, 18.16) * mm});
            skLineSegment(sketch, "E9338", {"start": v(24.4, 18.16) * mm, "end": v(24.4, 18.17) * mm});
            skLineSegment(sketch, "E9339", {"start": v(24.4, 18.17) * mm, "end": v(24.4, 18.17) * mm});
            skLineSegment(sketch, "E9340", {"start": v(24.4, 18.17) * mm, "end": v(24.4, 18.18) * mm});
            skLineSegment(sketch, "E9341", {"start": v(24.4, 18.18) * mm, "end": v(24.4, 18.19) * mm});
            skLineSegment(sketch, "E9342", {"start": v(24.4, 18.19) * mm, "end": v(24.38, 18.2) * mm});
            skLineSegment(sketch, "E9343", {"start": v(24.38, 18.2) * mm, "end": v(24.37, 18.22) * mm});
            skLineSegment(sketch, "E9344", {"start": v(24.37, 18.22) * mm, "end": v(24.36, 18.24) * mm});
            skLineSegment(sketch, "E9345", {"start": v(24.36, 18.24) * mm, "end": v(24.34, 18.27) * mm});
            skLineSegment(sketch, "E9346", {"start": v(24.34, 18.27) * mm, "end": v(24.33, 18.3) * mm});
            skLineSegment(sketch, "E9347", {"start": v(24.33, 18.3) * mm, "end": v(24.31, 18.32) * mm});
            skLineSegment(sketch, "E9348", {"start": v(24.31, 18.32) * mm, "end": v(24.3, 18.34) * mm});
            skLineSegment(sketch, "E9349", {"start": v(24.3, 18.34) * mm, "end": v(24.28, 18.37) * mm});
            skLineSegment(sketch, "E9350", {"start": v(24.28, 18.37) * mm, "end": v(24.25, 18.42) * mm});
            skLineSegment(sketch, "E9351", {"start": v(24.25, 18.42) * mm, "end": v(24.2, 18.48) * mm});
            skLineSegment(sketch, "E9352", {"start": v(24.2, 18.48) * mm, "end": v(24.17, 18.54) * mm});
            skLineSegment(sketch, "E9353", {"start": v(24.17, 18.54) * mm, "end": v(24.12, 18.62) * mm});
            skLineSegment(sketch, "E9354", {"start": v(24.12, 18.62) * mm, "end": v(24.06, 18.7) * mm});
            skLineSegment(sketch, "E9355", {"start": v(24.06, 18.7) * mm, "end": v(24, 18.79) * mm});
            skLineSegment(sketch, "E9356", {"start": v(24, 18.79) * mm, "end": v(23.95, 18.87) * mm});
            skLineSegment(sketch, "E9357", {"start": v(23.95, 18.87) * mm, "end": v(23.95, 18.87) * mm});
            skLineSegment(sketch, "E9358", {"start": v(23.95, 18.87) * mm, "end": v(23.95, 18.88) * mm});
            skLineSegment(sketch, "E9359", {"start": v(23.95, 18.88) * mm, "end": v(23.94, 18.88) * mm});
            skLineSegment(sketch, "E9360", {"start": v(23.94, 18.88) * mm, "end": v(23.93, 18.9) * mm});
            skLineSegment(sketch, "E9361", {"start": v(23.93, 18.9) * mm, "end": v(23.92, 18.92) * mm});
            skLineSegment(sketch, "E9362", {"start": v(23.92, 18.92) * mm, "end": v(23.9, 18.96) * mm});
            skLineSegment(sketch, "E9363", {"start": v(23.9, 18.96) * mm, "end": v(23.85, 19) * mm});
            skLineSegment(sketch, "E9364", {"start": v(23.85, 19) * mm, "end": v(23.8, 19.08) * mm});
            skLineSegment(sketch, "E9365", {"start": v(23.8, 19.08) * mm, "end": v(23.78, 19.1) * mm});
            skLineSegment(sketch, "E9366", {"start": v(23.78, 19.1) * mm, "end": v(23.76, 19.14) * mm});
            skLineSegment(sketch, "E9367", {"start": v(23.76, 19.14) * mm, "end": v(23.73, 19.17) * mm});
            skLineSegment(sketch, "E9368", {"start": v(23.73, 19.17) * mm, "end": v(23.7, 19.2) * mm});
            skLineSegment(sketch, "E9369", {"start": v(23.7, 19.2) * mm, "end": v(23.68, 19.22) * mm});
            skLineSegment(sketch, "E9370", {"start": v(23.68, 19.22) * mm, "end": v(23.66, 19.25) * mm});
            skLineSegment(sketch, "E9371", {"start": v(23.66, 19.25) * mm, "end": v(23.63, 19.27) * mm});
            skLineSegment(sketch, "E9372", {"start": v(23.63, 19.27) * mm, "end": v(23.6, 19.3) * mm});
            skLineSegment(sketch, "E9373", {"start": v(23.6, 19.3) * mm, "end": v(23.59, 19.31) * mm});
            skLineSegment(sketch, "E9374", {"start": v(23.59, 19.31) * mm, "end": v(23.57, 19.33) * mm});
            skLineSegment(sketch, "E9375", {"start": v(23.57, 19.33) * mm, "end": v(23.55, 19.35) * mm});
            skLineSegment(sketch, "E9376", {"start": v(23.55, 19.35) * mm, "end": v(23.54, 19.36) * mm});
            skLineSegment(sketch, "E9377", {"start": v(23.54, 19.36) * mm, "end": v(23.52, 19.38) * mm});
            skLineSegment(sketch, "E9378", {"start": v(23.52, 19.38) * mm, "end": v(23.5, 19.4) * mm});
            skLineSegment(sketch, "E9379", {"start": v(23.5, 19.4) * mm, "end": v(23.5, 19.41) * mm});
            skLineSegment(sketch, "E9380", {"start": v(23.5, 19.41) * mm, "end": v(23.48, 19.43) * mm});
            skLineSegment(sketch, "E9381", {"start": v(23.48, 19.43) * mm, "end": v(23.44, 19.47) * mm});
            skLineSegment(sketch, "E9382", {"start": v(23.44, 19.47) * mm, "end": v(23.41, 19.5) * mm});
            skLineSegment(sketch, "E9383", {"start": v(23.41, 19.5) * mm, "end": v(23.38, 19.53) * mm});
            skLineSegment(sketch, "E9384", {"start": v(23.38, 19.53) * mm, "end": v(23.35, 19.56) * mm});
            skLineSegment(sketch, "E9385", {"start": v(23.35, 19.56) * mm, "end": v(23.32, 19.58) * mm});
            skLineSegment(sketch, "E9386", {"start": v(23.32, 19.58) * mm, "end": v(23.3, 19.6) * mm});
            skLineSegment(sketch, "E9387", {"start": v(23.3, 19.6) * mm, "end": v(23.26, 19.6) * mm});
            skLineSegment(sketch, "E9388", {"start": v(23.26, 19.6) * mm, "end": v(23.22, 19.6) * mm});
            skLineSegment(sketch, "E9389", {"start": v(23.22, 19.6) * mm, "end": v(23.2, 19.6) * mm});
            skLineSegment(sketch, "E9390", {"start": v(23.2, 19.6) * mm, "end": v(23.17, 19.6) * mm});
            skLineSegment(sketch, "E9391", {"start": v(23.17, 19.6) * mm, "end": v(23.14, 19.59) * mm});
            skLineSegment(sketch, "E9392", {"start": v(23.14, 19.59) * mm, "end": v(23.11, 19.57) * mm});
            skLineSegment(sketch, "E9393", {"start": v(23.11, 19.57) * mm, "end": v(23.08, 19.55) * mm});
            skLineSegment(sketch, "E9394", {"start": v(23.08, 19.55) * mm, "end": v(23.05, 19.53) * mm});
            skLineSegment(sketch, "E9395", {"start": v(23.05, 19.53) * mm, "end": v(23.02, 19.5) * mm});
            skLineSegment(sketch, "E9396", {"start": v(23.02, 19.5) * mm, "end": v(22.98, 19.48) * mm});
            skLineSegment(sketch, "E9397", {"start": v(22.98, 19.48) * mm, "end": v(22.96, 19.46) * mm});
            skLineSegment(sketch, "E9398", {"start": v(22.96, 19.46) * mm, "end": v(22.94, 19.44) * mm});
            skLineSegment(sketch, "E9399", {"start": v(22.94, 19.44) * mm, "end": v(22.91, 19.41) * mm});
            skLineSegment(sketch, "E9400", {"start": v(22.91, 19.41) * mm, "end": v(22.9, 19.39) * mm});
            skLineSegment(sketch, "E9401", {"start": v(22.9, 19.39) * mm, "end": v(22.87, 19.36) * mm});
            skLineSegment(sketch, "E9402", {"start": v(22.87, 19.36) * mm, "end": v(22.85, 19.34) * mm});
            skLineSegment(sketch, "E9403", {"start": v(22.85, 19.34) * mm, "end": v(22.83, 19.3) * mm});
            skLineSegment(sketch, "E9404", {"start": v(22.83, 19.3) * mm, "end": v(22.81, 19.28) * mm});
            skLineSegment(sketch, "E9405", {"start": v(22.81, 19.28) * mm, "end": v(22.8, 19.26) * mm});
            skLineSegment(sketch, "E9406", {"start": v(22.8, 19.26) * mm, "end": v(22.8, 19.25) * mm});
            skLineSegment(sketch, "E9407", {"start": v(22.8, 19.25) * mm, "end": v(22.79, 19.23) * mm});
            skLineSegment(sketch, "E9408", {"start": v(22.79, 19.23) * mm, "end": v(22.78, 19.22) * mm});
            skLineSegment(sketch, "E9409", {"start": v(22.78, 19.22) * mm, "end": v(22.77, 19.2) * mm});
            skLineSegment(sketch, "E9410", {"start": v(22.77, 19.2) * mm, "end": v(22.76, 19.19) * mm});
            skLineSegment(sketch, "E9411", {"start": v(22.76, 19.19) * mm, "end": v(22.76, 19.17) * mm});
            skLineSegment(sketch, "E9412", {"start": v(22.76, 19.17) * mm, "end": v(22.75, 19.16) * mm});
            skLineSegment(sketch, "E9413", {"start": v(22.75, 19.16) * mm, "end": v(22.75, 19.14) * mm});
            skLineSegment(sketch, "E9414", {"start": v(22.75, 19.14) * mm, "end": v(22.74, 19.13) * mm});
            skLineSegment(sketch, "E9415", {"start": v(22.74, 19.13) * mm, "end": v(22.73, 19.11) * mm});
            skLineSegment(sketch, "E9416", {"start": v(22.73, 19.11) * mm, "end": v(22.73, 19.1) * mm});
            skLineSegment(sketch, "E9417", {"start": v(22.73, 19.1) * mm, "end": v(22.72, 19.09) * mm});
            skLineSegment(sketch, "E9418", {"start": v(22.72, 19.09) * mm, "end": v(22.71, 19.07) * mm});
            skLineSegment(sketch, "E9419", {"start": v(22.71, 19.07) * mm, "end": v(22.7, 19.06) * mm});
            skLineSegment(sketch, "E9420", {"start": v(22.7, 19.06) * mm, "end": v(22.7, 19.05) * mm});
            skLineSegment(sketch, "E9421", {"start": v(22.7, 19.05) * mm, "end": v(22.62, 18.95) * mm});
            skLineSegment(sketch, "E9422", {"start": v(22.62, 18.95) * mm, "end": v(22.56, 18.88) * mm});
            skLineSegment(sketch, "E9423", {"start": v(22.56, 18.88) * mm, "end": v(22.52, 18.82) * mm});
            skLineSegment(sketch, "E9424", {"start": v(22.52, 18.82) * mm, "end": v(22.5, 18.79) * mm});
            skLineSegment(sketch, "E9425", {"start": v(22.5, 18.79) * mm, "end": v(22.48, 18.76) * mm});
            skLineSegment(sketch, "E9426", {"start": v(22.48, 18.76) * mm, "end": v(22.47, 18.75) * mm});
            skLineSegment(sketch, "E9427", {"start": v(22.47, 18.75) * mm, "end": v(22.46, 18.75) * mm});
            skLineSegment(sketch, "E9428", {"start": v(22.46, 18.75) * mm, "end": v(22.46, 18.75) * mm});
            skLineSegment(sketch, "E9429", {"start": v(22.46, 18.75) * mm, "end": v(22.45, 18.62) * mm});
            skLineSegment(sketch, "E9430", {"start": v(22.45, 18.62) * mm, "end": v(22.43, 18.5) * mm});
            skLineSegment(sketch, "E9431", {"start": v(22.43, 18.5) * mm, "end": v(22.42, 18.4) * mm});
            skLineSegment(sketch, "E9432", {"start": v(22.42, 18.4) * mm, "end": v(22.4, 18.3) * mm});
            skLineSegment(sketch, "E9433", {"start": v(22.4, 18.3) * mm, "end": v(22.4, 18.22) * mm});
            skLineSegment(sketch, "E9434", {"start": v(22.4, 18.22) * mm, "end": v(22.39, 18.16) * mm});
            skLineSegment(sketch, "E9435", {"start": v(22.39, 18.16) * mm, "end": v(22.38, 18.12) * mm});
            skLineSegment(sketch, "E9436", {"start": v(22.38, 18.12) * mm, "end": v(22.38, 18.1) * mm});
            skLineSegment(sketch, "E9437", {"start": v(22.38, 18.1) * mm, "end": v(22.38, 18.1) * mm});
            skLineSegment(sketch, "E9438", {"start": v(22.38, 18.1) * mm, "end": v(22.38, 18.08) * mm});
            skLineSegment(sketch, "E9439", {"start": v(22.38, 18.08) * mm, "end": v(22.37, 18.05) * mm});
            skLineSegment(sketch, "E9440", {"start": v(22.37, 18.05) * mm, "end": v(22.37, 18.01) * mm});
            skLineSegment(sketch, "E9441", {"start": v(22.37, 18.01) * mm, "end": v(22.37, 17.97) * mm});
            skLineSegment(sketch, "E9442", {"start": v(22.37, 17.97) * mm, "end": v(22.36, 17.91) * mm});
            skLineSegment(sketch, "E9443", {"start": v(22.36, 17.91) * mm, "end": v(22.36, 17.86) * mm});
            skLineSegment(sketch, "E9444", {"start": v(22.36, 17.86) * mm, "end": v(22.35, 17.8) * mm});
            skLineSegment(sketch, "E9445", {"start": v(22.35, 17.8) * mm, "end": v(22.35, 17.8) * mm});
            skLineSegment(sketch, "E9446", {"start": v(22.9, 18) * mm, "end": v(22.91, 18.04) * mm});
            skLineSegment(sketch, "E9447", {"start": v(22.91, 18.04) * mm, "end": v(22.92, 18.08) * mm});
            skLineSegment(sketch, "E9448", {"start": v(22.92, 18.08) * mm, "end": v(22.93, 18.12) * mm});
            skLineSegment(sketch, "E9449", {"start": v(22.93, 18.12) * mm, "end": v(22.94, 18.16) * mm});
            skLineSegment(sketch, "E9450", {"start": v(22.94, 18.16) * mm, "end": v(22.95, 18.2) * mm});
            skLineSegment(sketch, "E9451", {"start": v(22.95, 18.2) * mm, "end": v(22.97, 18.24) * mm});
            skLineSegment(sketch, "E9452", {"start": v(22.97, 18.24) * mm, "end": v(22.98, 18.28) * mm});
            skLineSegment(sketch, "E9453", {"start": v(22.98, 18.28) * mm, "end": v(23, 18.3) * mm});
            skLineSegment(sketch, "E9454", {"start": v(23, 18.3) * mm, "end": v(23, 18.34) * mm});
            skLineSegment(sketch, "E9455", {"start": v(23, 18.34) * mm, "end": v(23.01, 18.37) * mm});
            skLineSegment(sketch, "E9456", {"start": v(23.01, 18.37) * mm, "end": v(23.02, 18.4) * mm});
            skLineSegment(sketch, "E9457", {"start": v(23.02, 18.4) * mm, "end": v(23.03, 18.43) * mm});
            skLineSegment(sketch, "E9458", {"start": v(23.03, 18.43) * mm, "end": v(23.04, 18.46) * mm});
            skLineSegment(sketch, "E9459", {"start": v(23.04, 18.46) * mm, "end": v(23.05, 18.49) * mm});
            skLineSegment(sketch, "E9460", {"start": v(23.05, 18.49) * mm, "end": v(23.06, 18.52) * mm});
            skLineSegment(sketch, "E9461", {"start": v(23.06, 18.52) * mm, "end": v(23.07, 18.56) * mm});
            skLineSegment(sketch, "E9462", {"start": v(23.07, 18.56) * mm, "end": v(23.08, 18.59) * mm});
            skLineSegment(sketch, "E9463", {"start": v(23.08, 18.59) * mm, "end": v(23.09, 18.61) * mm});
            skLineSegment(sketch, "E9464", {"start": v(23.09, 18.61) * mm, "end": v(23.1, 18.63) * mm});
            skLineSegment(sketch, "E9465", {"start": v(23.1, 18.63) * mm, "end": v(23.12, 18.65) * mm});
            skLineSegment(sketch, "E9466", {"start": v(23.12, 18.65) * mm, "end": v(23.14, 18.66) * mm});
            skLineSegment(sketch, "E9467", {"start": v(23.14, 18.66) * mm, "end": v(23.16, 18.67) * mm});
            skLineSegment(sketch, "E9468", {"start": v(23.16, 18.67) * mm, "end": v(23.19, 18.68) * mm});
            skLineSegment(sketch, "E9469", {"start": v(23.19, 18.68) * mm, "end": v(23.2, 18.69) * mm});
            skLineSegment(sketch, "E9470", {"start": v(23.2, 18.69) * mm, "end": v(23.21, 18.69) * mm});
            skLineSegment(sketch, "E9471", {"start": v(23.21, 18.69) * mm, "end": v(23.22, 18.7) * mm});
            skLineSegment(sketch, "E9472", {"start": v(23.22, 18.7) * mm, "end": v(23.24, 18.7) * mm});
            skLineSegment(sketch, "E9473", {"start": v(23.24, 18.7) * mm, "end": v(23.25, 18.7) * mm});
            skLineSegment(sketch, "E9474", {"start": v(23.25, 18.7) * mm, "end": v(23.26, 18.7) * mm});
            skLineSegment(sketch, "E9475", {"start": v(23.26, 18.7) * mm, "end": v(23.27, 18.7) * mm});
            skLineSegment(sketch, "E9476", {"start": v(23.27, 18.7) * mm, "end": v(23.28, 18.7) * mm});
            skLineSegment(sketch, "E9477", {"start": v(23.28, 18.7) * mm, "end": v(23.3, 18.7) * mm});
            skLineSegment(sketch, "E9478", {"start": v(23.3, 18.7) * mm, "end": v(23.31, 18.7) * mm});
            skLineSegment(sketch, "E9479", {"start": v(23.31, 18.7) * mm, "end": v(23.32, 18.7) * mm});
            skLineSegment(sketch, "E9480", {"start": v(23.32, 18.7) * mm, "end": v(23.33, 18.7) * mm});
            skLineSegment(sketch, "E9481", {"start": v(23.33, 18.7) * mm, "end": v(23.33, 18.7) * mm});
            skLineSegment(sketch, "E9482", {"start": v(23.33, 18.7) * mm, "end": v(23.35, 18.67) * mm});
            skLineSegment(sketch, "E9483", {"start": v(23.35, 18.67) * mm, "end": v(23.38, 18.65) * mm});
            skLineSegment(sketch, "E9484", {"start": v(23.38, 18.65) * mm, "end": v(23.4, 18.62) * mm});
            skLineSegment(sketch, "E9485", {"start": v(23.4, 18.62) * mm, "end": v(23.42, 18.6) * mm});
            skLineSegment(sketch, "E9486", {"start": v(23.42, 18.6) * mm, "end": v(23.44, 18.57) * mm});
            skLineSegment(sketch, "E9487", {"start": v(23.44, 18.57) * mm, "end": v(23.46, 18.54) * mm});
            skLineSegment(sketch, "E9488", {"start": v(23.46, 18.54) * mm, "end": v(23.48, 18.52) * mm});
            skLineSegment(sketch, "E9489", {"start": v(23.48, 18.52) * mm, "end": v(23.49, 18.5) * mm});
            skLineSegment(sketch, "E9490", {"start": v(23.49, 18.5) * mm, "end": v(23.5, 18.47) * mm});
            skLineSegment(sketch, "E9491", {"start": v(23.5, 18.47) * mm, "end": v(23.52, 18.44) * mm});
            skLineSegment(sketch, "E9492", {"start": v(23.52, 18.44) * mm, "end": v(23.55, 18.4) * mm});
            skLineSegment(sketch, "E9493", {"start": v(23.55, 18.4) * mm, "end": v(23.57, 18.36) * mm});
            skLineSegment(sketch, "E9494", {"start": v(23.57, 18.36) * mm, "end": v(23.6, 18.32) * mm});
            skLineSegment(sketch, "E9495", {"start": v(23.6, 18.32) * mm, "end": v(23.63, 18.27) * mm});
            skLineSegment(sketch, "E9496", {"start": v(23.63, 18.27) * mm, "end": v(23.66, 18.22) * mm});
            skLineSegment(sketch, "E9497", {"start": v(23.66, 18.22) * mm, "end": v(23.69, 18.17) * mm});
            skLineSegment(sketch, "E9498", {"start": v(23.69, 18.17) * mm, "end": v(23.69, 18.17) * mm});
            skLineSegment(sketch, "E9499", {"start": v(23.69, 18.17) * mm, "end": v(23.7, 18.17) * mm});
            skLineSegment(sketch, "E9500", {"start": v(23.7, 18.17) * mm, "end": v(23.7, 18.16) * mm});
            skLineSegment(sketch, "E9501", {"start": v(23.7, 18.16) * mm, "end": v(23.7, 18.14) * mm});
            skLineSegment(sketch, "E9502", {"start": v(23.7, 18.14) * mm, "end": v(23.72, 18.12) * mm});
            skLineSegment(sketch, "E9503", {"start": v(23.72, 18.12) * mm, "end": v(23.73, 18.1) * mm});
            skLineSegment(sketch, "E9504", {"start": v(23.73, 18.1) * mm, "end": v(23.75, 18.06) * mm});
            skLineSegment(sketch, "E9505", {"start": v(23.75, 18.06) * mm, "end": v(23.76, 18.04) * mm});
            skLineSegment(sketch, "E9506", {"start": v(23.76, 18.04) * mm, "end": v(23.76, 18.03) * mm});
            skLineSegment(sketch, "E9507", {"start": v(23.76, 18.03) * mm, "end": v(23.77, 18.02) * mm});
            skLineSegment(sketch, "E9508", {"start": v(23.77, 18.02) * mm, "end": v(23.77, 18.01) * mm});
            skLineSegment(sketch, "E9509", {"start": v(23.77, 18.01) * mm, "end": v(23.78, 18) * mm});
            skLineSegment(sketch, "E9510", {"start": v(23.78, 18) * mm, "end": v(23.78, 17.99) * mm});
            skLineSegment(sketch, "E9511", {"start": v(23.78, 17.99) * mm, "end": v(23.79, 17.97) * mm});
            skLineSegment(sketch, "E9512", {"start": v(23.79, 17.97) * mm, "end": v(23.79, 17.96) * mm});
            skLineSegment(sketch, "E9513", {"start": v(23.79, 17.96) * mm, "end": v(23.8, 17.96) * mm});
            skLineSegment(sketch, "E9514", {"start": v(23.8, 17.96) * mm, "end": v(23.8, 17.95) * mm});
            skLineSegment(sketch, "E9515", {"start": v(23.8, 17.95) * mm, "end": v(23.8, 17.95) * mm});
            skLineSegment(sketch, "E9516", {"start": v(23.8, 17.95) * mm, "end": v(23.8, 17.94) * mm});
            skLineSegment(sketch, "E9517", {"start": v(23.8, 17.94) * mm, "end": v(23.8, 17.94) * mm});
            skLineSegment(sketch, "E9518", {"start": v(23.8, 17.94) * mm, "end": v(23.8, 17.93) * mm});
            skLineSegment(sketch, "E9519", {"start": v(23.8, 17.93) * mm, "end": v(23.8, 17.93) * mm});
            skLineSegment(sketch, "E9520", {"start": v(23.8, 17.93) * mm, "end": v(23.8, 17.92) * mm});
            skLineSegment(sketch, "E9521", {"start": v(23.8, 17.92) * mm, "end": v(23.79, 17.91) * mm});
            skLineSegment(sketch, "E9522", {"start": v(23.79, 17.91) * mm, "end": v(23.79, 17.9) * mm});
            skLineSegment(sketch, "E9523", {"start": v(23.79, 17.9) * mm, "end": v(23.79, 17.9) * mm});
            skLineSegment(sketch, "E9524", {"start": v(23.79, 17.9) * mm, "end": v(23.78, 17.89) * mm});
            skLineSegment(sketch, "E9525", {"start": v(23.78, 17.89) * mm, "end": v(23.78, 17.88) * mm});
            skLineSegment(sketch, "E9526", {"start": v(23.78, 17.88) * mm, "end": v(23.78, 17.86) * mm});
            skLineSegment(sketch, "E9527", {"start": v(23.78, 17.86) * mm, "end": v(23.77, 17.85) * mm});
            skLineSegment(sketch, "E9528", {"start": v(23.77, 17.85) * mm, "end": v(23.77, 17.83) * mm});
            skLineSegment(sketch, "E9529", {"start": v(23.77, 17.83) * mm, "end": v(23.76, 17.82) * mm});
            skLineSegment(sketch, "E9530", {"start": v(23.76, 17.82) * mm, "end": v(23.76, 17.8) * mm});
            skLineSegment(sketch, "E9531", {"start": v(23.76, 17.8) * mm, "end": v(23.75, 17.79) * mm});
            skLineSegment(sketch, "E9532", {"start": v(23.75, 17.79) * mm, "end": v(23.75, 17.77) * mm});
            skLineSegment(sketch, "E9533", {"start": v(23.75, 17.77) * mm, "end": v(23.74, 17.75) * mm});
            skLineSegment(sketch, "E9534", {"start": v(23.74, 17.75) * mm, "end": v(23.73, 17.72) * mm});
            skLineSegment(sketch, "E9535", {"start": v(23.73, 17.72) * mm, "end": v(23.72, 17.7) * mm});
            skLineSegment(sketch, "E9536", {"start": v(23.72, 17.7) * mm, "end": v(23.7, 17.67) * mm});
            skLineSegment(sketch, "E9537", {"start": v(23.7, 17.67) * mm, "end": v(23.7, 17.64) * mm});
            skLineSegment(sketch, "E9538", {"start": v(23.7, 17.64) * mm, "end": v(23.7, 17.62) * mm});
            skLineSegment(sketch, "E9539", {"start": v(23.7, 17.62) * mm, "end": v(23.7, 17.61) * mm});
            skLineSegment(sketch, "E9540", {"start": v(23.7, 17.61) * mm, "end": v(23.69, 17.6) * mm});
            skLineSegment(sketch, "E9541", {"start": v(23.69, 17.6) * mm, "end": v(23.68, 17.58) * mm});
            skLineSegment(sketch, "E9542", {"start": v(23.68, 17.58) * mm, "end": v(23.67, 17.55) * mm});
            skLineSegment(sketch, "E9543", {"start": v(23.67, 17.55) * mm, "end": v(23.66, 17.51) * mm});
            skLineSegment(sketch, "E9544", {"start": v(23.66, 17.51) * mm, "end": v(23.64, 17.47) * mm});
            skLineSegment(sketch, "E9545", {"start": v(23.64, 17.47) * mm, "end": v(23.63, 17.43) * mm});
            skLineSegment(sketch, "E9546", {"start": v(23.63, 17.43) * mm, "end": v(23.6, 17.38) * mm});
            skLineSegment(sketch, "E9547", {"start": v(23.6, 17.38) * mm, "end": v(23.6, 17.33) * mm});
            skLineSegment(sketch, "E9548", {"start": v(23.6, 17.33) * mm, "end": v(23.6, 17.33) * mm});
            skLineSegment(sketch, "E9549", {"start": v(23.6, 17.33) * mm, "end": v(23.59, 17.33) * mm});
            skLineSegment(sketch, "E9550", {"start": v(23.59, 17.33) * mm, "end": v(23.59, 17.33) * mm});
            skLineSegment(sketch, "E9551", {"start": v(23.59, 17.33) * mm, "end": v(23.58, 17.32) * mm});
            skLineSegment(sketch, "E9552", {"start": v(23.58, 17.32) * mm, "end": v(23.58, 17.3) * mm});
            skLineSegment(sketch, "E9553", {"start": v(23.58, 17.3) * mm, "end": v(23.57, 17.29) * mm});
            skLineSegment(sketch, "E9554", {"start": v(23.57, 17.29) * mm, "end": v(23.56, 17.26) * mm});
            skLineSegment(sketch, "E9555", {"start": v(23.56, 17.26) * mm, "end": v(23.54, 17.22) * mm});
            skLineSegment(sketch, "E9556", {"start": v(23.54, 17.22) * mm, "end": v(23.52, 17.18) * mm});
            skLineSegment(sketch, "E9557", {"start": v(23.52, 17.18) * mm, "end": v(23.5, 17.15) * mm});
            skLineSegment(sketch, "E9558", {"start": v(23.5, 17.15) * mm, "end": v(23.5, 17.12) * mm});
            skLineSegment(sketch, "E9559", {"start": v(23.5, 17.12) * mm, "end": v(23.49, 17.1) * mm});
            skLineSegment(sketch, "E9560", {"start": v(23.49, 17.1) * mm, "end": v(23.48, 17.1) * mm});
            skLineSegment(sketch, "E9561", {"start": v(23.48, 17.1) * mm, "end": v(23.48, 17.1) * mm});
            skLineSegment(sketch, "E9562", {"start": v(23.48, 17.1) * mm, "end": v(23.42, 17.09) * mm});
            skLineSegment(sketch, "E9563", {"start": v(23.42, 17.09) * mm, "end": v(23.36, 17.08) * mm});
            skLineSegment(sketch, "E9564", {"start": v(23.36, 17.08) * mm, "end": v(23.31, 17.08) * mm});
            skLineSegment(sketch, "E9565", {"start": v(23.31, 17.08) * mm, "end": v(23.27, 17.08) * mm});
            skLineSegment(sketch, "E9566", {"start": v(23.27, 17.08) * mm, "end": v(23.23, 17.07) * mm});
            skLineSegment(sketch, "E9567", {"start": v(23.23, 17.07) * mm, "end": v(23.2, 17.07) * mm});
            skLineSegment(sketch, "E9568", {"start": v(23.2, 17.07) * mm, "end": v(23.17, 17.07) * mm});
            skLineSegment(sketch, "E9569", {"start": v(23.17, 17.07) * mm, "end": v(23.16, 17.07) * mm});
            skLineSegment(sketch, "E9570", {"start": v(23.16, 17.07) * mm, "end": v(23.16, 17.07) * mm});
            skLineSegment(sketch, "E9571", {"start": v(23.16, 17.07) * mm, "end": v(23.15, 17.07) * mm});
            skLineSegment(sketch, "E9572", {"start": v(23.15, 17.07) * mm, "end": v(23.13, 17.08) * mm});
            skLineSegment(sketch, "E9573", {"start": v(23.13, 17.08) * mm, "end": v(23.11, 17.1) * mm});
            skLineSegment(sketch, "E9574", {"start": v(23.11, 17.1) * mm, "end": v(23.1, 17.1) * mm});
            skLineSegment(sketch, "E9575", {"start": v(23.1, 17.1) * mm, "end": v(23.07, 17.12) * mm});
            skLineSegment(sketch, "E9576", {"start": v(23.07, 17.12) * mm, "end": v(23.05, 17.14) * mm});
            skLineSegment(sketch, "E9577", {"start": v(23.05, 17.14) * mm, "end": v(23.03, 17.16) * mm});
            skLineSegment(sketch, "E9578", {"start": v(23.03, 17.16) * mm, "end": v(23.03, 17.16) * mm});
            skLineSegment(sketch, "E9579", {"start": v(23.03, 17.16) * mm, "end": v(23.02, 17.16) * mm});
            skLineSegment(sketch, "E9580", {"start": v(23.02, 17.16) * mm, "end": v(23.02, 17.17) * mm});
            skLineSegment(sketch, "E9581", {"start": v(23.02, 17.17) * mm, "end": v(23.02, 17.18) * mm});
            skLineSegment(sketch, "E9582", {"start": v(23.02, 17.18) * mm, "end": v(23.02, 17.2) * mm});
            skLineSegment(sketch, "E9583", {"start": v(23.02, 17.2) * mm, "end": v(23.01, 17.2) * mm});
            skLineSegment(sketch, "E9584", {"start": v(23.01, 17.2) * mm, "end": v(23, 17.3) * mm});
            skLineSegment(sketch, "E9585", {"start": v(23, 17.3) * mm, "end": v(22.97, 17.39) * mm});
            skLineSegment(sketch, "E9586", {"start": v(22.97, 17.39) * mm, "end": v(22.95, 17.48) * mm});
            skLineSegment(sketch, "E9587", {"start": v(22.95, 17.48) * mm, "end": v(22.94, 17.57) * mm});
            skLineSegment(sketch, "E9588", {"start": v(22.94, 17.57) * mm, "end": v(22.92, 17.67) * mm});
            skLineSegment(sketch, "E9589", {"start": v(22.92, 17.67) * mm, "end": v(22.91, 17.77) * mm});
            skLineSegment(sketch, "E9590", {"start": v(22.91, 17.77) * mm, "end": v(22.9, 17.86) * mm});
            skLineSegment(sketch, "E9591", {"start": v(22.9, 17.86) * mm, "end": v(22.9, 17.96) * mm});
            skLineSegment(sketch, "E9592", {"start": v(22.9, 17.96) * mm, "end": v(22.9, 18) * mm});
            skLineSegment(sketch, "E9593", {"start": v(27.59, 1.64) * mm, "end": v(27.58, 1.56) * mm});
            skLineSegment(sketch, "E9594", {"start": v(27.58, 1.56) * mm, "end": v(27.58, 1.5) * mm});
            skLineSegment(sketch, "E9595", {"start": v(27.58, 1.5) * mm, "end": v(27.58, 1.46) * mm});
            skLineSegment(sketch, "E9596", {"start": v(27.58, 1.46) * mm, "end": v(27.58, 1.43) * mm});
            skLineSegment(sketch, "E9597", {"start": v(27.58, 1.43) * mm, "end": v(27.58, 1.42) * mm});
            skLineSegment(sketch, "E9598", {"start": v(27.58, 1.42) * mm, "end": v(27.58, 1.42) * mm});
            skLineSegment(sketch, "E9599", {"start": v(27.58, 1.42) * mm, "end": v(27.61, 1.32) * mm});
            skLineSegment(sketch, "E9600", {"start": v(27.61, 1.32) * mm, "end": v(27.65, 1.22) * mm});
            skLineSegment(sketch, "E9601", {"start": v(27.65, 1.22) * mm, "end": v(27.68, 1.13) * mm});
            skLineSegment(sketch, "E9602", {"start": v(27.68, 1.13) * mm, "end": v(27.7, 1.06) * mm});
            skLineSegment(sketch, "E9603", {"start": v(27.7, 1.06) * mm, "end": v(27.73, 1) * mm});
            skLineSegment(sketch, "E9604", {"start": v(27.73, 1) * mm, "end": v(27.75, 0.94) * mm});
            skLineSegment(sketch, "E9605", {"start": v(27.75, 0.94) * mm, "end": v(27.76, 0.9) * mm});
            skLineSegment(sketch, "E9606", {"start": v(27.76, 0.9) * mm, "end": v(27.77, 0.88) * mm});
            skLineSegment(sketch, "E9607", {"start": v(27.77, 0.88) * mm, "end": v(27.78, 0.86) * mm});
            skLineSegment(sketch, "E9608", {"start": v(27.78, 0.86) * mm, "end": v(27.8, 0.83) * mm});
            skLineSegment(sketch, "E9609", {"start": v(27.8, 0.83) * mm, "end": v(27.82, 0.78) * mm});
            skLineSegment(sketch, "E9610", {"start": v(27.82, 0.78) * mm, "end": v(27.85, 0.72) * mm});
            skLineSegment(sketch, "E9611", {"start": v(27.85, 0.72) * mm, "end": v(27.89, 0.65) * mm});
            skLineSegment(sketch, "E9612", {"start": v(27.89, 0.65) * mm, "end": v(27.93, 0.57) * mm});
            skLineSegment(sketch, "E9613", {"start": v(27.93, 0.57) * mm, "end": v(27.97, 0.48) * mm});
            skLineSegment(sketch, "E9614", {"start": v(27.97, 0.48) * mm, "end": v(28.02, 0.4) * mm});
            skLineSegment(sketch, "E9615", {"start": v(28.02, 0.4) * mm, "end": v(28.02, 0.4) * mm});
            skLineSegment(sketch, "E9616", {"start": v(28.02, 0.4) * mm, "end": v(28.03, 0.39) * mm});
            skLineSegment(sketch, "E9617", {"start": v(28.03, 0.39) * mm, "end": v(28.05, 0.38) * mm});
            skLineSegment(sketch, "E9618", {"start": v(28.05, 0.38) * mm, "end": v(28.08, 0.37) * mm});
            skLineSegment(sketch, "E9619", {"start": v(28.08, 0.37) * mm, "end": v(28.13, 0.35) * mm});
            skLineSegment(sketch, "E9620", {"start": v(28.13, 0.35) * mm, "end": v(28.2, 0.32) * mm});
            skLineSegment(sketch, "E9621", {"start": v(28.2, 0.32) * mm, "end": v(28.28, 0.28) * mm});
            skLineSegment(sketch, "E9622", {"start": v(28.28, 0.28) * mm, "end": v(28.31, 0.27) * mm});
            skLineSegment(sketch, "E9623", {"start": v(28.31, 0.27) * mm, "end": v(28.34, 0.26) * mm});
            skLineSegment(sketch, "E9624", {"start": v(28.34, 0.26) * mm, "end": v(28.36, 0.24) * mm});
            skLineSegment(sketch, "E9625", {"start": v(28.36, 0.24) * mm, "end": v(28.39, 0.23) * mm});
            skLineSegment(sketch, "E9626", {"start": v(28.39, 0.23) * mm, "end": v(28.41, 0.22) * mm});
            skLineSegment(sketch, "E9627", {"start": v(28.41, 0.22) * mm, "end": v(28.44, 0.2) * mm});
            skLineSegment(sketch, "E9628", {"start": v(28.44, 0.2) * mm, "end": v(28.47, 0.19) * mm});
            skLineSegment(sketch, "E9629", {"start": v(28.47, 0.19) * mm, "end": v(28.5, 0.17) * mm});
            skLineSegment(sketch, "E9630", {"start": v(28.5, 0.17) * mm, "end": v(28.5, 0.16) * mm});
            skLineSegment(sketch, "E9631", {"start": v(28.5, 0.16) * mm, "end": v(28.52, 0.16) * mm});
            skLineSegment(sketch, "E9632", {"start": v(28.52, 0.16) * mm, "end": v(28.54, 0.15) * mm});
            skLineSegment(sketch, "E9633", {"start": v(28.54, 0.15) * mm, "end": v(28.56, 0.14) * mm});
            skLineSegment(sketch, "E9634", {"start": v(28.56, 0.14) * mm, "end": v(28.57, 0.13) * mm});
            skLineSegment(sketch, "E9635", {"start": v(28.57, 0.13) * mm, "end": v(28.59, 0.12) * mm});
            skLineSegment(sketch, "E9636", {"start": v(28.59, 0.12) * mm, "end": v(28.6, 0.11) * mm});
            skLineSegment(sketch, "E9637", {"start": v(28.6, 0.11) * mm, "end": v(28.62, 0.1) * mm});
            skLineSegment(sketch, "E9638", {"start": v(28.62, 0.1) * mm, "end": v(28.71, 0.06) * mm});
            skLineSegment(sketch, "E9639", {"start": v(28.71, 0.06) * mm, "end": v(28.78, 0.02) * mm});
            skLineSegment(sketch, "E9640", {"start": v(28.78, 0.02) * mm, "end": v(28.83, 0) * mm});
            skLineSegment(sketch, "E9641", {"start": v(28.83, 0) * mm, "end": v(28.86, -0.02) * mm});
            skLineSegment(sketch, "E9642", {"start": v(28.86, -0.02) * mm, "end": v(28.88, -0.03) * mm});
            skLineSegment(sketch, "E9643", {"start": v(28.88, -0.03) * mm, "end": v(28.9, -0.03) * mm});
            skLineSegment(sketch, "E9644", {"start": v(28.9, -0.03) * mm, "end": v(28.9, -0.04) * mm});
            skLineSegment(sketch, "E9645", {"start": v(28.9, -0.04) * mm, "end": v(28.9, -0.04) * mm});
            skLineSegment(sketch, "E9646", {"start": v(28.9, -0.04) * mm, "end": v(29.02, -0.06) * mm});
            skLineSegment(sketch, "E9647", {"start": v(29.02, -0.06) * mm, "end": v(29.14, -0.08) * mm});
            skLineSegment(sketch, "E9648", {"start": v(29.14, -0.08) * mm, "end": v(29.26, -0.1) * mm});
            skLineSegment(sketch, "E9649", {"start": v(29.26, -0.1) * mm, "end": v(29.36, -0.12) * mm});
            skLineSegment(sketch, "E9650", {"start": v(29.36, -0.12) * mm, "end": v(29.44, -0.13) * mm});
            skLineSegment(sketch, "E9651", {"start": v(29.44, -0.13) * mm, "end": v(29.5, -0.14) * mm});
            skLineSegment(sketch, "E9652", {"start": v(29.5, -0.14) * mm, "end": v(29.55, -0.15) * mm});
            skLineSegment(sketch, "E9653", {"start": v(29.55, -0.15) * mm, "end": v(29.57, -0.15) * mm});
            skLineSegment(sketch, "E9654", {"start": v(29.57, -0.15) * mm, "end": v(29.58, -0.15) * mm});
            skLineSegment(sketch, "E9655", {"start": v(29.58, -0.15) * mm, "end": v(29.6, -0.14) * mm});
            skLineSegment(sketch, "E9656", {"start": v(29.6, -0.14) * mm, "end": v(29.6, -0.13) * mm});
            skLineSegment(sketch, "E9657", {"start": v(29.6, -0.13) * mm, "end": v(29.6, -0.11) * mm});
            skLineSegment(sketch, "E9658", {"start": v(29.6, -0.11) * mm, "end": v(29.62, -0.1) * mm});
            skLineSegment(sketch, "E9659", {"start": v(29.62, -0.1) * mm, "end": v(29.63, -0.07) * mm});
            skLineSegment(sketch, "E9660", {"start": v(29.63, -0.07) * mm, "end": v(29.63, -0.04) * mm});
            skLineSegment(sketch, "E9661", {"start": v(29.63, -0.04) * mm, "end": v(29.64, -0.02) * mm});
            skLineSegment(sketch, "E9662", {"start": v(29.64, -0.02) * mm, "end": v(29.65, 0.01) * mm});
            skLineSegment(sketch, "E9663", {"start": v(29.65, 0.01) * mm, "end": v(29.65, 0.06) * mm});
            skLineSegment(sketch, "E9664", {"start": v(29.65, 0.06) * mm, "end": v(29.66, 0.1) * mm});
            skLineSegment(sketch, "E9665", {"start": v(29.66, 0.1) * mm, "end": v(29.67, 0.16) * mm});
            skLineSegment(sketch, "E9666", {"start": v(29.67, 0.16) * mm, "end": v(29.68, 0.21) * mm});
            skLineSegment(sketch, "E9667", {"start": v(29.68, 0.21) * mm, "end": v(29.7, 0.27) * mm});
            skLineSegment(sketch, "E9668", {"start": v(29.7, 0.27) * mm, "end": v(29.7, 0.33) * mm});
            skLineSegment(sketch, "E9669", {"start": v(29.7, 0.33) * mm, "end": v(29.71, 0.38) * mm});
            skLineSegment(sketch, "E9670", {"start": v(29.71, 0.38) * mm, "end": v(29.71, 0.38) * mm});
            skLineSegment(sketch, "E9671", {"start": v(29.71, 0.38) * mm, "end": v(29.72, 0.39) * mm});
            skLineSegment(sketch, "E9672", {"start": v(29.72, 0.39) * mm, "end": v(29.72, 0.4) * mm});
            skLineSegment(sketch, "E9673", {"start": v(29.72, 0.4) * mm, "end": v(29.72, 0.41) * mm});
            skLineSegment(sketch, "E9674", {"start": v(29.72, 0.41) * mm, "end": v(29.73, 0.44) * mm});
            skLineSegment(sketch, "E9675", {"start": v(29.73, 0.44) * mm, "end": v(29.73, 0.47) * mm});
            skLineSegment(sketch, "E9676", {"start": v(29.73, 0.47) * mm, "end": v(29.74, 0.51) * mm});
            skLineSegment(sketch, "E9677", {"start": v(29.74, 0.51) * mm, "end": v(29.75, 0.53) * mm});
            skLineSegment(sketch, "E9678", {"start": v(29.75, 0.53) * mm, "end": v(29.75, 0.55) * mm});
            skLineSegment(sketch, "E9679", {"start": v(29.75, 0.55) * mm, "end": v(29.75, 0.57) * mm});
            skLineSegment(sketch, "E9680", {"start": v(29.75, 0.57) * mm, "end": v(29.76, 0.6) * mm});
            skLineSegment(sketch, "E9681", {"start": v(29.76, 0.6) * mm, "end": v(29.76, 0.61) * mm});
            skLineSegment(sketch, "E9682", {"start": v(29.76, 0.61) * mm, "end": v(29.77, 0.63) * mm});
            skLineSegment(sketch, "E9683", {"start": v(29.77, 0.63) * mm, "end": v(29.77, 0.65) * mm});
            skLineSegment(sketch, "E9684", {"start": v(29.77, 0.65) * mm, "end": v(29.78, 0.67) * mm});
            skLineSegment(sketch, "E9685", {"start": v(29.78, 0.67) * mm, "end": v(29.79, 0.7) * mm});
            skLineSegment(sketch, "E9686", {"start": v(29.79, 0.7) * mm, "end": v(29.8, 0.73) * mm});
            skLineSegment(sketch, "E9687", {"start": v(29.8, 0.73) * mm, "end": v(29.8, 0.77) * mm});
            skLineSegment(sketch, "E9688", {"start": v(29.8, 0.77) * mm, "end": v(29.81, 0.8) * mm});
            skLineSegment(sketch, "E9689", {"start": v(29.81, 0.8) * mm, "end": v(29.82, 0.83) * mm});
            skLineSegment(sketch, "E9690", {"start": v(29.82, 0.83) * mm, "end": v(29.82, 0.86) * mm});
            skLineSegment(sketch, "E9691", {"start": v(29.82, 0.86) * mm, "end": v(29.83, 0.9) * mm});
            skLineSegment(sketch, "E9692", {"start": v(29.83, 0.9) * mm, "end": v(29.84, 0.93) * mm});
            skLineSegment(sketch, "E9693", {"start": v(29.84, 0.93) * mm, "end": v(29.85, 1.16) * mm});
            skLineSegment(sketch, "E9694", {"start": v(29.85, 1.16) * mm, "end": v(29.85, 1.37) * mm});
            skLineSegment(sketch, "E9695", {"start": v(29.85, 1.37) * mm, "end": v(29.82, 1.58) * mm});
            skLineSegment(sketch, "E9696", {"start": v(29.82, 1.58) * mm, "end": v(29.77, 1.78) * mm});
            skLineSegment(sketch, "E9697", {"start": v(29.77, 1.78) * mm, "end": v(29.7, 1.96) * mm});
            skLineSegment(sketch, "E9698", {"start": v(29.7, 1.96) * mm, "end": v(29.6, 2.14) * mm});
            skLineSegment(sketch, "E9699", {"start": v(29.6, 2.14) * mm, "end": v(29.48, 2.3) * mm});
            skLineSegment(sketch, "E9700", {"start": v(29.48, 2.3) * mm, "end": v(29.33, 2.45) * mm});
            skLineSegment(sketch, "E9701", {"start": v(29.33, 2.45) * mm, "end": v(29.17, 2.6) * mm});
            skLineSegment(sketch, "E9702", {"start": v(29.17, 2.6) * mm, "end": v(29, 2.72) * mm});
            skLineSegment(sketch, "E9703", {"start": v(29, 2.72) * mm, "end": v(28.84, 2.84) * mm});
            skLineSegment(sketch, "E9704", {"start": v(28.84, 2.84) * mm, "end": v(28.68, 2.95) * mm});
            skLineSegment(sketch, "E9705", {"start": v(28.68, 2.95) * mm, "end": v(28.51, 3.04) * mm});
            skLineSegment(sketch, "E9706", {"start": v(28.51, 3.04) * mm, "end": v(28.35, 3.13) * mm});
            skLineSegment(sketch, "E9707", {"start": v(28.35, 3.13) * mm, "end": v(28.18, 3.2) * mm});
            skLineSegment(sketch, "E9708", {"start": v(28.18, 3.2) * mm, "end": v(28.01, 3.26) * mm});
            skLineSegment(sketch, "E9709", {"start": v(28.01, 3.26) * mm, "end": v(27.98, 3.27) * mm});
            skLineSegment(sketch, "E9710", {"start": v(27.98, 3.27) * mm, "end": v(27.94, 3.28) * mm});
            skLineSegment(sketch, "E9711", {"start": v(27.94, 3.28) * mm, "end": v(27.9, 3.29) * mm});
            skLineSegment(sketch, "E9712", {"start": v(27.9, 3.29) * mm, "end": v(27.87, 3.3) * mm});
            skLineSegment(sketch, "E9713", {"start": v(27.87, 3.3) * mm, "end": v(27.83, 3.3) * mm});
            skLineSegment(sketch, "E9714", {"start": v(27.83, 3.3) * mm, "end": v(27.79, 3.32) * mm});
            skLineSegment(sketch, "E9715", {"start": v(27.79, 3.32) * mm, "end": v(27.75, 3.33) * mm});
            skLineSegment(sketch, "E9716", {"start": v(27.75, 3.33) * mm, "end": v(27.71, 3.34) * mm});
            skLineSegment(sketch, "E9717", {"start": v(27.71, 3.34) * mm, "end": v(27.7, 3.34) * mm});
            skLineSegment(sketch, "E9718", {"start": v(27.7, 3.34) * mm, "end": v(27.68, 3.34) * mm});
            skLineSegment(sketch, "E9719", {"start": v(27.68, 3.34) * mm, "end": v(27.67, 3.34) * mm});
            skLineSegment(sketch, "E9720", {"start": v(27.67, 3.34) * mm, "end": v(27.67, 3.35) * mm});
            skLineSegment(sketch, "E9721", {"start": v(27.67, 3.35) * mm, "end": v(27.66, 3.35) * mm});
            skLineSegment(sketch, "E9722", {"start": v(27.66, 3.35) * mm, "end": v(27.66, 3.35) * mm});
            skLineSegment(sketch, "E9723", {"start": v(27.66, 3.35) * mm, "end": v(27.64, 3.35) * mm});
            skLineSegment(sketch, "E9724", {"start": v(27.64, 3.35) * mm, "end": v(27.62, 3.36) * mm});
            skLineSegment(sketch, "E9725", {"start": v(27.62, 3.36) * mm, "end": v(27.6, 3.36) * mm});
            skLineSegment(sketch, "E9726", {"start": v(27.6, 3.36) * mm, "end": v(27.57, 3.37) * mm});
            skLineSegment(sketch, "E9727", {"start": v(27.57, 3.37) * mm, "end": v(27.55, 3.37) * mm});
            skLineSegment(sketch, "E9728", {"start": v(27.55, 3.37) * mm, "end": v(27.53, 3.38) * mm});
            skLineSegment(sketch, "E9729", {"start": v(27.53, 3.38) * mm, "end": v(27.51, 3.38) * mm});
            skLineSegment(sketch, "E9730", {"start": v(27.51, 3.38) * mm, "end": v(27.5, 3.39) * mm});
            skLineSegment(sketch, "E9731", {"start": v(27.5, 3.39) * mm, "end": v(27.49, 3.39) * mm});
            skLineSegment(sketch, "E9732", {"start": v(27.49, 3.39) * mm, "end": v(27.47, 3.39) * mm});
            skLineSegment(sketch, "E9733", {"start": v(27.47, 3.39) * mm, "end": v(27.46, 3.39) * mm});
            skLineSegment(sketch, "E9734", {"start": v(27.46, 3.39) * mm, "end": v(27.46, 3.38) * mm});
            skLineSegment(sketch, "E9735", {"start": v(27.46, 3.38) * mm, "end": v(27.45, 3.37) * mm});
            skLineSegment(sketch, "E9736", {"start": v(27.45, 3.37) * mm, "end": v(27.44, 3.36) * mm});
            skLineSegment(sketch, "E9737", {"start": v(27.44, 3.36) * mm, "end": v(27.44, 3.35) * mm});
            skLineSegment(sketch, "E9738", {"start": v(27.44, 3.35) * mm, "end": v(27.44, 3.34) * mm});
            skLineSegment(sketch, "E9739", {"start": v(27.44, 3.34) * mm, "end": v(27.44, 3.33) * mm});
            skLineSegment(sketch, "E9740", {"start": v(27.44, 3.33) * mm, "end": v(27.44, 3.31) * mm});
            skLineSegment(sketch, "E9741", {"start": v(27.44, 3.31) * mm, "end": v(27.44, 3.3) * mm});
            skLineSegment(sketch, "E9742", {"start": v(27.44, 3.3) * mm, "end": v(27.44, 3.28) * mm});
            skLineSegment(sketch, "E9743", {"start": v(27.44, 3.28) * mm, "end": v(27.44, 3.27) * mm});
            skLineSegment(sketch, "E9744", {"start": v(27.44, 3.27) * mm, "end": v(27.44, 3.25) * mm});
            skLineSegment(sketch, "E9745", {"start": v(27.44, 3.25) * mm, "end": v(27.44, 3.24) * mm});
            skLineSegment(sketch, "E9746", {"start": v(27.44, 3.24) * mm, "end": v(27.44, 3.23) * mm});
            skLineSegment(sketch, "E9747", {"start": v(27.44, 3.23) * mm, "end": v(27.44, 3.23) * mm});
            skLineSegment(sketch, "E9748", {"start": v(27.44, 3.23) * mm, "end": v(27.44, 3.22) * mm});
            skLineSegment(sketch, "E9749", {"start": v(27.44, 3.22) * mm, "end": v(27.44, 3.22) * mm});
            skLineSegment(sketch, "E9750", {"start": v(27.44, 3.22) * mm, "end": v(27.44, 3.21) * mm});
            skLineSegment(sketch, "E9751", {"start": v(27.44, 3.21) * mm, "end": v(27.44, 3.2) * mm});
            skLineSegment(sketch, "E9752", {"start": v(27.44, 3.2) * mm, "end": v(27.44, 3.18) * mm});
            skLineSegment(sketch, "E9753", {"start": v(27.44, 3.18) * mm, "end": v(27.44, 3.17) * mm});
            skLineSegment(sketch, "E9754", {"start": v(27.44, 3.17) * mm, "end": v(27.44, 3.15) * mm});
            skLineSegment(sketch, "E9755", {"start": v(27.44, 3.15) * mm, "end": v(27.44, 3.14) * mm});
            skLineSegment(sketch, "E9756", {"start": v(27.44, 3.14) * mm, "end": v(27.44, 3.12) * mm});
            skLineSegment(sketch, "E9757", {"start": v(27.44, 3.12) * mm, "end": v(27.44, 3.1) * mm});
            skLineSegment(sketch, "E9758", {"start": v(27.44, 3.1) * mm, "end": v(27.44, 3.1) * mm});
            skLineSegment(sketch, "E9759", {"start": v(27.44, 3.1) * mm, "end": v(27.45, 3.07) * mm});
            skLineSegment(sketch, "E9760", {"start": v(27.45, 3.07) * mm, "end": v(27.45, 3.05) * mm});
            skLineSegment(sketch, "E9761", {"start": v(27.45, 3.05) * mm, "end": v(27.46, 3.02) * mm});
            skLineSegment(sketch, "E9762", {"start": v(27.46, 3.02) * mm, "end": v(27.46, 3) * mm});
            skLineSegment(sketch, "E9763", {"start": v(27.46, 3) * mm, "end": v(27.47, 2.98) * mm});
            skLineSegment(sketch, "E9764", {"start": v(27.47, 2.98) * mm, "end": v(27.47, 2.95) * mm});
            skLineSegment(sketch, "E9765", {"start": v(27.47, 2.95) * mm, "end": v(27.48, 2.93) * mm});
            skLineSegment(sketch, "E9766", {"start": v(27.48, 2.93) * mm, "end": v(27.49, 2.9) * mm});
            skLineSegment(sketch, "E9767", {"start": v(27.49, 2.9) * mm, "end": v(27.5, 2.87) * mm});
            skLineSegment(sketch, "E9768", {"start": v(27.5, 2.87) * mm, "end": v(27.5, 2.83) * mm});
            skLineSegment(sketch, "E9769", {"start": v(27.5, 2.83) * mm, "end": v(27.51, 2.79) * mm});
            skLineSegment(sketch, "E9770", {"start": v(27.51, 2.79) * mm, "end": v(27.52, 2.75) * mm});
            skLineSegment(sketch, "E9771", {"start": v(27.52, 2.75) * mm, "end": v(27.53, 2.7) * mm});
            skLineSegment(sketch, "E9772", {"start": v(27.53, 2.7) * mm, "end": v(27.54, 2.67) * mm});
            skLineSegment(sketch, "E9773", {"start": v(27.54, 2.67) * mm, "end": v(27.54, 2.63) * mm});
            skLineSegment(sketch, "E9774", {"start": v(27.54, 2.63) * mm, "end": v(27.55, 2.6) * mm});
            skLineSegment(sketch, "E9775", {"start": v(27.55, 2.6) * mm, "end": v(27.56, 2.5) * mm});
            skLineSegment(sketch, "E9776", {"start": v(27.56, 2.5) * mm, "end": v(27.57, 2.4) * mm});
            skLineSegment(sketch, "E9777", {"start": v(27.57, 2.4) * mm, "end": v(27.57, 2.3) * mm});
            skLineSegment(sketch, "E9778", {"start": v(27.57, 2.3) * mm, "end": v(27.58, 2.19) * mm});
            skLineSegment(sketch, "E9779", {"start": v(27.58, 2.19) * mm, "end": v(27.59, 2.08) * mm});
            skLineSegment(sketch, "E9780", {"start": v(27.59, 2.08) * mm, "end": v(27.59, 1.97) * mm});
            skLineSegment(sketch, "E9781", {"start": v(27.59, 1.97) * mm, "end": v(27.6, 1.86) * mm});
            skLineSegment(sketch, "E9782", {"start": v(27.6, 1.86) * mm, "end": v(27.59, 1.75) * mm});
            skLineSegment(sketch, "E9783", {"start": v(27.59, 1.75) * mm, "end": v(27.59, 1.64) * mm});
            skLineSegment(sketch, "E9784", {"start": v(28.09, 2.34) * mm, "end": v(28.09, 2.39) * mm});
            skLineSegment(sketch, "E9785", {"start": v(28.09, 2.39) * mm, "end": v(28.1, 2.44) * mm});
            skLineSegment(sketch, "E9786", {"start": v(28.1, 2.44) * mm, "end": v(28.1, 2.49) * mm});
            skLineSegment(sketch, "E9787", {"start": v(28.1, 2.49) * mm, "end": v(28.1, 2.54) * mm});
            skLineSegment(sketch, "E9788", {"start": v(28.1, 2.54) * mm, "end": v(28.1, 2.55) * mm});
            skLineSegment(sketch, "E9789", {"start": v(28.1, 2.55) * mm, "end": v(28.11, 2.57) * mm});
            skLineSegment(sketch, "E9790", {"start": v(28.11, 2.57) * mm, "end": v(28.12, 2.58) * mm});
            skLineSegment(sketch, "E9791", {"start": v(28.12, 2.58) * mm, "end": v(28.12, 2.58) * mm});
            skLineSegment(sketch, "E9792", {"start": v(28.12, 2.58) * mm, "end": v(28.13, 2.59) * mm});
            skLineSegment(sketch, "E9793", {"start": v(28.13, 2.59) * mm, "end": v(28.14, 2.6) * mm});
            skLineSegment(sketch, "E9794", {"start": v(28.14, 2.6) * mm, "end": v(28.15, 2.6) * mm});
            skLineSegment(sketch, "E9795", {"start": v(28.15, 2.6) * mm, "end": v(28.16, 2.6) * mm});
            skLineSegment(sketch, "E9796", {"start": v(28.16, 2.6) * mm, "end": v(28.16, 2.6) * mm});
            skLineSegment(sketch, "E9797", {"start": v(28.16, 2.6) * mm, "end": v(28.17, 2.6) * mm});
            skLineSegment(sketch, "E9798", {"start": v(28.17, 2.6) * mm, "end": v(28.17, 2.6) * mm});
            skLineSegment(sketch, "E9799", {"start": v(28.17, 2.6) * mm, "end": v(28.18, 2.6) * mm});
            skLineSegment(sketch, "E9800", {"start": v(28.18, 2.6) * mm, "end": v(28.19, 2.6) * mm});
            skLineSegment(sketch, "E9801", {"start": v(28.19, 2.6) * mm, "end": v(28.2, 2.59) * mm});
            skLineSegment(sketch, "E9802", {"start": v(28.2, 2.59) * mm, "end": v(28.2, 2.58) * mm});
            skLineSegment(sketch, "E9803", {"start": v(28.2, 2.58) * mm, "end": v(28.22, 2.57) * mm});
            skLineSegment(sketch, "E9804", {"start": v(28.22, 2.57) * mm, "end": v(28.36, 2.48) * mm});
            skLineSegment(sketch, "E9805", {"start": v(28.36, 2.48) * mm, "end": v(28.5, 2.38) * mm});
            skLineSegment(sketch, "E9806", {"start": v(28.5, 2.38) * mm, "end": v(28.63, 2.28) * mm});
            skLineSegment(sketch, "E9807", {"start": v(28.63, 2.28) * mm, "end": v(28.76, 2.18) * mm});
            skLineSegment(sketch, "E9808", {"start": v(28.76, 2.18) * mm, "end": v(28.87, 2.06) * mm});
            skLineSegment(sketch, "E9809", {"start": v(28.87, 2.06) * mm, "end": v(28.97, 1.93) * mm});
            skLineSegment(sketch, "E9810", {"start": v(28.97, 1.93) * mm, "end": v(29.05, 1.8) * mm});
            skLineSegment(sketch, "E9811", {"start": v(29.05, 1.8) * mm, "end": v(29.12, 1.64) * mm});
            skLineSegment(sketch, "E9812", {"start": v(29.12, 1.64) * mm, "end": v(29.13, 1.62) * mm});
            skLineSegment(sketch, "E9813", {"start": v(29.13, 1.62) * mm, "end": v(29.13, 1.6) * mm});
            skLineSegment(sketch, "E9814", {"start": v(29.13, 1.6) * mm, "end": v(29.13, 1.6) * mm});
            skLineSegment(sketch, "E9815", {"start": v(29.13, 1.6) * mm, "end": v(29.14, 1.6) * mm});
            skLineSegment(sketch, "E9816", {"start": v(29.14, 1.6) * mm, "end": v(29.14, 1.6) * mm});
            skLineSegment(sketch, "E9817", {"start": v(29.14, 1.6) * mm, "end": v(29.14, 1.57) * mm});
            skLineSegment(sketch, "E9818", {"start": v(29.14, 1.57) * mm, "end": v(29.14, 1.55) * mm});
            skLineSegment(sketch, "E9819", {"start": v(29.14, 1.55) * mm, "end": v(29.15, 1.53) * mm});
            skLineSegment(sketch, "E9820", {"start": v(29.15, 1.53) * mm, "end": v(29.15, 1.52) * mm});
            skLineSegment(sketch, "E9821", {"start": v(29.15, 1.52) * mm, "end": v(29.15, 1.5) * mm});
            skLineSegment(sketch, "E9822", {"start": v(29.15, 1.5) * mm, "end": v(29.15, 1.5) * mm});
            skLineSegment(sketch, "E9823", {"start": v(29.15, 1.5) * mm, "end": v(29.15, 1.49) * mm});
            skLineSegment(sketch, "E9824", {"start": v(29.15, 1.49) * mm, "end": v(29.15, 1.49) * mm});
            skLineSegment(sketch, "E9825", {"start": v(29.15, 1.49) * mm, "end": v(29.15, 1.48) * mm});
            skLineSegment(sketch, "E9826", {"start": v(29.15, 1.48) * mm, "end": v(29.15, 1.48) * mm});
            skLineSegment(sketch, "E9827", {"start": v(29.15, 1.48) * mm, "end": v(29.15, 1.47) * mm});
            skLineSegment(sketch, "E9828", {"start": v(29.15, 1.47) * mm, "end": v(29.15, 1.47) * mm});
            skLineSegment(sketch, "E9829", {"start": v(29.15, 1.47) * mm, "end": v(29.15, 1.46) * mm});
            skLineSegment(sketch, "E9830", {"start": v(29.15, 1.46) * mm, "end": v(29.15, 1.45) * mm});
            skLineSegment(sketch, "E9831", {"start": v(29.15, 1.45) * mm, "end": v(29.15, 1.44) * mm});
            skLineSegment(sketch, "E9832", {"start": v(29.15, 1.44) * mm, "end": v(29.15, 1.43) * mm});
            skLineSegment(sketch, "E9833", {"start": v(29.15, 1.43) * mm, "end": v(29.15, 1.42) * mm});
            skLineSegment(sketch, "E9834", {"start": v(29.15, 1.42) * mm, "end": v(29.15, 1.4) * mm});
            skLineSegment(sketch, "E9835", {"start": v(29.15, 1.4) * mm, "end": v(29.16, 1.38) * mm});
            skLineSegment(sketch, "E9836", {"start": v(29.16, 1.38) * mm, "end": v(29.16, 1.36) * mm});
            skLineSegment(sketch, "E9837", {"start": v(29.16, 1.36) * mm, "end": v(29.16, 1.33) * mm});
            skLineSegment(sketch, "E9838", {"start": v(29.16, 1.33) * mm, "end": v(29.17, 1.31) * mm});
            skLineSegment(sketch, "E9839", {"start": v(29.17, 1.31) * mm, "end": v(29.17, 1.3) * mm});
            skLineSegment(sketch, "E9840", {"start": v(29.17, 1.3) * mm, "end": v(29.17, 1.3) * mm});
            skLineSegment(sketch, "E9841", {"start": v(29.17, 1.3) * mm, "end": v(29.17, 1.29) * mm});
            skLineSegment(sketch, "E9842", {"start": v(29.17, 1.29) * mm, "end": v(29.17, 1.29) * mm});
            skLineSegment(sketch, "E9843", {"start": v(29.17, 1.29) * mm, "end": v(29.17, 1.28) * mm});
            skLineSegment(sketch, "E9844", {"start": v(29.17, 1.28) * mm, "end": v(29.17, 1.28) * mm});
            skLineSegment(sketch, "E9845", {"start": v(29.17, 1.28) * mm, "end": v(29.17, 1.27) * mm});
            skLineSegment(sketch, "E9846", {"start": v(29.17, 1.27) * mm, "end": v(29.18, 1.26) * mm});
            skLineSegment(sketch, "E9847", {"start": v(29.18, 1.26) * mm, "end": v(29.18, 1.24) * mm});
            skLineSegment(sketch, "E9848", {"start": v(29.18, 1.24) * mm, "end": v(29.19, 1.2) * mm});
            skLineSegment(sketch, "E9849", {"start": v(29.19, 1.2) * mm, "end": v(29.2, 1.15) * mm});
            skLineSegment(sketch, "E9850", {"start": v(29.2, 1.15) * mm, "end": v(29.2, 1.1) * mm});
            skLineSegment(sketch, "E9851", {"start": v(29.2, 1.1) * mm, "end": v(29.2, 1.06) * mm});
            skLineSegment(sketch, "E9852", {"start": v(29.2, 1.06) * mm, "end": v(29.21, 1.01) * mm});
            skLineSegment(sketch, "E9853", {"start": v(29.21, 1.01) * mm, "end": v(29.22, 0.97) * mm});
            skLineSegment(sketch, "E9854", {"start": v(29.22, 0.97) * mm, "end": v(29.22, 0.92) * mm});
            skLineSegment(sketch, "E9855", {"start": v(29.22, 0.92) * mm, "end": v(29.22, 0.87) * mm});
            skLineSegment(sketch, "E9856", {"start": v(29.22, 0.87) * mm, "end": v(29.22, 0.82) * mm});
            skLineSegment(sketch, "E9857", {"start": v(29.22, 0.82) * mm, "end": v(29.22, 0.78) * mm});
            skLineSegment(sketch, "E9858", {"start": v(29.22, 0.78) * mm, "end": v(29.22, 0.74) * mm});
            skLineSegment(sketch, "E9859", {"start": v(29.22, 0.74) * mm, "end": v(29.2, 0.7) * mm});
            skLineSegment(sketch, "E9860", {"start": v(29.2, 0.7) * mm, "end": v(29.2, 0.67) * mm});
            skLineSegment(sketch, "E9861", {"start": v(29.2, 0.67) * mm, "end": v(29.18, 0.64) * mm});
            skLineSegment(sketch, "E9862", {"start": v(29.18, 0.64) * mm, "end": v(29.15, 0.61) * mm});
            skLineSegment(sketch, "E9863", {"start": v(29.15, 0.61) * mm, "end": v(29.12, 0.59) * mm});
            skLineSegment(sketch, "E9864", {"start": v(29.12, 0.59) * mm, "end": v(29.1, 0.57) * mm});
            skLineSegment(sketch, "E9865", {"start": v(29.1, 0.57) * mm, "end": v(29.07, 0.56) * mm});
            skLineSegment(sketch, "E9866", {"start": v(29.07, 0.56) * mm, "end": v(29.04, 0.56) * mm});
            skLineSegment(sketch, "E9867", {"start": v(29.04, 0.56) * mm, "end": v(29.02, 0.56) * mm});
            skLineSegment(sketch, "E9868", {"start": v(29.02, 0.56) * mm, "end": v(29, 0.57) * mm});
            skLineSegment(sketch, "E9869", {"start": v(29, 0.57) * mm, "end": v(28.97, 0.58) * mm});
            skLineSegment(sketch, "E9870", {"start": v(28.97, 0.58) * mm, "end": v(28.95, 0.6) * mm});
            skLineSegment(sketch, "E9871", {"start": v(28.95, 0.6) * mm, "end": v(28.92, 0.62) * mm});
            skLineSegment(sketch, "E9872", {"start": v(28.92, 0.62) * mm, "end": v(28.84, 0.69) * mm});
            skLineSegment(sketch, "E9873", {"start": v(28.84, 0.69) * mm, "end": v(28.77, 0.76) * mm});
            skLineSegment(sketch, "E9874", {"start": v(28.77, 0.76) * mm, "end": v(28.7, 0.83) * mm});
            skLineSegment(sketch, "E9875", {"start": v(28.7, 0.83) * mm, "end": v(28.62, 0.9) * mm});
            skLineSegment(sketch, "E9876", {"start": v(28.62, 0.9) * mm, "end": v(28.55, 0.97) * mm});
            skLineSegment(sketch, "E9877", {"start": v(28.55, 0.97) * mm, "end": v(28.48, 1.04) * mm});
            skLineSegment(sketch, "E9878", {"start": v(28.48, 1.04) * mm, "end": v(28.41, 1.11) * mm});
            skLineSegment(sketch, "E9879", {"start": v(28.41, 1.11) * mm, "end": v(28.35, 1.19) * mm});
            skLineSegment(sketch, "E9880", {"start": v(28.35, 1.19) * mm, "end": v(28.33, 1.2) * mm});
            skLineSegment(sketch, "E9881", {"start": v(28.33, 1.2) * mm, "end": v(28.32, 1.22) * mm});
            skLineSegment(sketch, "E9882", {"start": v(28.32, 1.22) * mm, "end": v(28.3, 1.24) * mm});
            skLineSegment(sketch, "E9883", {"start": v(28.3, 1.24) * mm, "end": v(28.3, 1.27) * mm});
            skLineSegment(sketch, "E9884", {"start": v(28.3, 1.27) * mm, "end": v(28.28, 1.3) * mm});
            skLineSegment(sketch, "E9885", {"start": v(28.28, 1.3) * mm, "end": v(28.27, 1.32) * mm});
            skLineSegment(sketch, "E9886", {"start": v(28.27, 1.32) * mm, "end": v(28.26, 1.34) * mm});
            skLineSegment(sketch, "E9887", {"start": v(28.26, 1.34) * mm, "end": v(28.26, 1.37) * mm});
            skLineSegment(sketch, "E9888", {"start": v(28.26, 1.37) * mm, "end": v(28.24, 1.46) * mm});
            skLineSegment(sketch, "E9889", {"start": v(28.24, 1.46) * mm, "end": v(28.21, 1.56) * mm});
            skLineSegment(sketch, "E9890", {"start": v(28.21, 1.56) * mm, "end": v(28.2, 1.66) * mm});
            skLineSegment(sketch, "E9891", {"start": v(28.2, 1.66) * mm, "end": v(28.17, 1.76) * mm});
            skLineSegment(sketch, "E9892", {"start": v(28.17, 1.76) * mm, "end": v(28.15, 1.86) * mm});
            skLineSegment(sketch, "E9893", {"start": v(28.15, 1.86) * mm, "end": v(28.13, 1.96) * mm});
            skLineSegment(sketch, "E9894", {"start": v(28.13, 1.96) * mm, "end": v(28.11, 2.06) * mm});
            skLineSegment(sketch, "E9895", {"start": v(28.11, 2.06) * mm, "end": v(28.1, 2.17) * mm});
            skLineSegment(sketch, "E9896", {"start": v(28.1, 2.17) * mm, "end": v(28.1, 2.2) * mm});
            skLineSegment(sketch, "E9897", {"start": v(28.1, 2.2) * mm, "end": v(28.09, 2.25) * mm});
            skLineSegment(sketch, "E9898", {"start": v(28.09, 2.25) * mm, "end": v(28.09, 2.3) * mm});
            skLineSegment(sketch, "E9899", {"start": v(28.09, 2.3) * mm, "end": v(28.09, 2.34) * mm});
            skLineSegment(sketch, "E9900", {"start": v(19.62, -0.02) * mm, "end": v(19.62, -0.02) * mm});
            skLineSegment(sketch, "E9901", {"start": v(19.62, -0.02) * mm, "end": v(19.63, -0.02) * mm});
            skLineSegment(sketch, "E9902", {"start": v(19.63, -0.02) * mm, "end": v(19.65, 0) * mm});
            skLineSegment(sketch, "E9903", {"start": v(19.65, 0) * mm, "end": v(19.67, 0) * mm});
            skLineSegment(sketch, "E9904", {"start": v(19.67, 0) * mm, "end": v(19.7, 0.02) * mm});
            skLineSegment(sketch, "E9905", {"start": v(19.7, 0.02) * mm, "end": v(19.76, 0.04) * mm});
            skLineSegment(sketch, "E9906", {"start": v(19.76, 0.04) * mm, "end": v(19.82, 0.07) * mm});
            skLineSegment(sketch, "E9907", {"start": v(19.82, 0.07) * mm, "end": v(19.84, 0.08) * mm});
            skLineSegment(sketch, "E9908", {"start": v(19.84, 0.08) * mm, "end": v(19.86, 0.09) * mm});
            skLineSegment(sketch, "E9909", {"start": v(19.86, 0.09) * mm, "end": v(19.88, 0.1) * mm});
            skLineSegment(sketch, "E9910", {"start": v(19.88, 0.1) * mm, "end": v(19.9, 0.1) * mm});
            skLineSegment(sketch, "E9911", {"start": v(19.9, 0.1) * mm, "end": v(19.91, 0.1) * mm});
            skLineSegment(sketch, "E9912", {"start": v(19.91, 0.1) * mm, "end": v(19.93, 0.12) * mm});
            skLineSegment(sketch, "E9913", {"start": v(19.93, 0.12) * mm, "end": v(19.95, 0.12) * mm});
            skLineSegment(sketch, "E9914", {"start": v(19.95, 0.12) * mm, "end": v(19.96, 0.13) * mm});
            skLineSegment(sketch, "E9915", {"start": v(19.96, 0.13) * mm, "end": v(20.01, 0.15) * mm});
            skLineSegment(sketch, "E9916", {"start": v(20.01, 0.15) * mm, "end": v(20.07, 0.18) * mm});
            skLineSegment(sketch, "E9917", {"start": v(20.07, 0.18) * mm, "end": v(20.12, 0.2) * mm});
            skLineSegment(sketch, "E9918", {"start": v(20.12, 0.2) * mm, "end": v(20.17, 0.22) * mm});
            skLineSegment(sketch, "E9919", {"start": v(20.17, 0.22) * mm, "end": v(20.22, 0.25) * mm});
            skLineSegment(sketch, "E9920", {"start": v(20.22, 0.25) * mm, "end": v(20.27, 0.27) * mm});
            skLineSegment(sketch, "E9921", {"start": v(20.27, 0.27) * mm, "end": v(20.31, 0.3) * mm});
            skLineSegment(sketch, "E9922", {"start": v(20.31, 0.3) * mm, "end": v(20.36, 0.33) * mm});
            skLineSegment(sketch, "E9923", {"start": v(20.36, 0.33) * mm, "end": v(20.43, 0.37) * mm});
            skLineSegment(sketch, "E9924", {"start": v(20.43, 0.37) * mm, "end": v(20.49, 0.42) * mm});
            skLineSegment(sketch, "E9925", {"start": v(20.49, 0.42) * mm, "end": v(20.55, 0.47) * mm});
            skLineSegment(sketch, "E9926", {"start": v(20.55, 0.47) * mm, "end": v(20.6, 0.53) * mm});
            skLineSegment(sketch, "E9927", {"start": v(20.6, 0.53) * mm, "end": v(20.66, 0.6) * mm});
            skLineSegment(sketch, "E9928", {"start": v(20.66, 0.6) * mm, "end": v(20.7, 0.66) * mm});
            skLineSegment(sketch, "E9929", {"start": v(20.7, 0.66) * mm, "end": v(20.75, 0.74) * mm});
            skLineSegment(sketch, "E9930", {"start": v(20.75, 0.74) * mm, "end": v(20.78, 0.83) * mm});
            skLineSegment(sketch, "E9931", {"start": v(20.78, 0.83) * mm, "end": v(20.79, 0.86) * mm});
            skLineSegment(sketch, "E9932", {"start": v(20.79, 0.86) * mm, "end": v(20.8, 0.9) * mm});
            skLineSegment(sketch, "E9933", {"start": v(20.8, 0.9) * mm, "end": v(20.8, 0.93) * mm});
            skLineSegment(sketch, "E9934", {"start": v(20.8, 0.93) * mm, "end": v(20.82, 0.96) * mm});
            skLineSegment(sketch, "E9935", {"start": v(20.82, 0.96) * mm, "end": v(20.83, 1) * mm});
            skLineSegment(sketch, "E9936", {"start": v(20.83, 1) * mm, "end": v(20.84, 1.03) * mm});
            skLineSegment(sketch, "E9937", {"start": v(20.84, 1.03) * mm, "end": v(20.85, 1.06) * mm});
            skLineSegment(sketch, "E9938", {"start": v(20.85, 1.06) * mm, "end": v(20.87, 1.1) * mm});
            skLineSegment(sketch, "E9939", {"start": v(20.87, 1.1) * mm, "end": v(20.9, 1.2) * mm});
            skLineSegment(sketch, "E9940", {"start": v(20.9, 1.2) * mm, "end": v(20.93, 1.3) * mm});
            skLineSegment(sketch, "E9941", {"start": v(20.93, 1.3) * mm, "end": v(20.95, 1.41) * mm});
            skLineSegment(sketch, "E9942", {"start": v(20.95, 1.41) * mm, "end": v(20.97, 1.52) * mm});
            skLineSegment(sketch, "E9943", {"start": v(20.97, 1.52) * mm, "end": v(20.98, 1.63) * mm});
            skLineSegment(sketch, "E9944", {"start": v(20.98, 1.63) * mm, "end": v(20.98, 1.73) * mm});
            skLineSegment(sketch, "E9945", {"start": v(20.98, 1.73) * mm, "end": v(20.97, 1.84) * mm});
            skLineSegment(sketch, "E9946", {"start": v(20.97, 1.84) * mm, "end": v(20.96, 1.95) * mm});
            skLineSegment(sketch, "E9947", {"start": v(20.96, 1.95) * mm, "end": v(20.96, 1.99) * mm});
            skLineSegment(sketch, "E9948", {"start": v(20.96, 1.99) * mm, "end": v(20.95, 2.03) * mm});
            skLineSegment(sketch, "E9949", {"start": v(20.95, 2.03) * mm, "end": v(20.95, 2.07) * mm});
            skLineSegment(sketch, "E9950", {"start": v(20.95, 2.07) * mm, "end": v(20.94, 2.11) * mm});
            skLineSegment(sketch, "E9951", {"start": v(20.94, 2.11) * mm, "end": v(20.94, 2.15) * mm});
            skLineSegment(sketch, "E9952", {"start": v(20.94, 2.15) * mm, "end": v(20.93, 2.2) * mm});
            skLineSegment(sketch, "E9953", {"start": v(20.93, 2.2) * mm, "end": v(20.93, 2.23) * mm});
            skLineSegment(sketch, "E9954", {"start": v(20.93, 2.23) * mm, "end": v(20.92, 2.27) * mm});
            skLineSegment(sketch, "E9955", {"start": v(20.92, 2.27) * mm, "end": v(20.92, 2.32) * mm});
            skLineSegment(sketch, "E9956", {"start": v(20.92, 2.32) * mm, "end": v(20.9, 2.37) * mm});
            skLineSegment(sketch, "E9957", {"start": v(20.9, 2.37) * mm, "end": v(20.9, 2.42) * mm});
            skLineSegment(sketch, "E9958", {"start": v(20.9, 2.42) * mm, "end": v(20.9, 2.47) * mm});
            skLineSegment(sketch, "E9959", {"start": v(20.9, 2.47) * mm, "end": v(20.9, 2.52) * mm});
            skLineSegment(sketch, "E9960", {"start": v(20.9, 2.52) * mm, "end": v(20.88, 2.57) * mm});
            skLineSegment(sketch, "E9961", {"start": v(20.88, 2.57) * mm, "end": v(20.88, 2.62) * mm});
            skLineSegment(sketch, "E9962", {"start": v(20.88, 2.62) * mm, "end": v(20.87, 2.67) * mm});
            skLineSegment(sketch, "E9963", {"start": v(20.87, 2.67) * mm, "end": v(20.86, 2.72) * mm});
            skLineSegment(sketch, "E9964", {"start": v(20.86, 2.72) * mm, "end": v(20.85, 2.76) * mm});
            skLineSegment(sketch, "E9965", {"start": v(20.85, 2.76) * mm, "end": v(20.84, 2.8) * mm});
            skLineSegment(sketch, "E9966", {"start": v(20.84, 2.8) * mm, "end": v(20.83, 2.83) * mm});
            skLineSegment(sketch, "E9967", {"start": v(20.83, 2.83) * mm, "end": v(20.81, 2.86) * mm});
            skLineSegment(sketch, "E9968", {"start": v(20.81, 2.86) * mm, "end": v(20.8, 2.88) * mm});
            skLineSegment(sketch, "E9969", {"start": v(20.8, 2.88) * mm, "end": v(20.77, 2.9) * mm});
            skLineSegment(sketch, "E9970", {"start": v(20.77, 2.9) * mm, "end": v(20.75, 2.91) * mm});
            skLineSegment(sketch, "E9971", {"start": v(20.75, 2.91) * mm, "end": v(20.71, 2.92) * mm});
            skLineSegment(sketch, "E9972", {"start": v(20.71, 2.92) * mm, "end": v(20.67, 2.93) * mm});
            skLineSegment(sketch, "E9973", {"start": v(20.67, 2.93) * mm, "end": v(20.63, 2.92) * mm});
            skLineSegment(sketch, "E9974", {"start": v(20.63, 2.92) * mm, "end": v(20.6, 2.91) * mm});
            skLineSegment(sketch, "E9975", {"start": v(20.6, 2.91) * mm, "end": v(20.55, 2.9) * mm});
            skLineSegment(sketch, "E9976", {"start": v(20.55, 2.9) * mm, "end": v(20.52, 2.9) * mm});
            skLineSegment(sketch, "E9977", {"start": v(20.52, 2.9) * mm, "end": v(20.5, 2.88) * mm});
            skLineSegment(sketch, "E9978", {"start": v(20.5, 2.88) * mm, "end": v(20.47, 2.87) * mm});
            skLineSegment(sketch, "E9979", {"start": v(20.47, 2.87) * mm, "end": v(20.45, 2.86) * mm});
            skLineSegment(sketch, "E9980", {"start": v(20.45, 2.86) * mm, "end": v(20.42, 2.84) * mm});
            skLineSegment(sketch, "E9981", {"start": v(20.42, 2.84) * mm, "end": v(20.4, 2.83) * mm});
            skLineSegment(sketch, "E9982", {"start": v(20.4, 2.83) * mm, "end": v(20.37, 2.81) * mm});
            skLineSegment(sketch, "E9983", {"start": v(20.37, 2.81) * mm, "end": v(20.34, 2.8) * mm});
            skLineSegment(sketch, "E9984", {"start": v(20.34, 2.8) * mm, "end": v(20.32, 2.78) * mm});
            skLineSegment(sketch, "E9985", {"start": v(20.32, 2.78) * mm, "end": v(20.29, 2.76) * mm});
            skLineSegment(sketch, "E9986", {"start": v(20.29, 2.76) * mm, "end": v(20.26, 2.74) * mm});
            skLineSegment(sketch, "E9987", {"start": v(20.26, 2.74) * mm, "end": v(20.23, 2.72) * mm});
            skLineSegment(sketch, "E9988", {"start": v(20.23, 2.72) * mm, "end": v(20.2, 2.7) * mm});
            skLineSegment(sketch, "E9989", {"start": v(20.2, 2.7) * mm, "end": v(20.17, 2.69) * mm});
            skLineSegment(sketch, "E9990", {"start": v(20.17, 2.69) * mm, "end": v(20.14, 2.67) * mm});
            skLineSegment(sketch, "E9991", {"start": v(20.14, 2.67) * mm, "end": v(20.1, 2.65) * mm});
            skLineSegment(sketch, "E9992", {"start": v(20.1, 2.65) * mm, "end": v(20.08, 2.63) * mm});
            skLineSegment(sketch, "E9993", {"start": v(20.08, 2.63) * mm, "end": v(20.05, 2.61) * mm});
            skLineSegment(sketch, "E9994", {"start": v(20.05, 2.61) * mm, "end": v(20.01, 2.6) * mm});
            skLineSegment(sketch, "E9995", {"start": v(20.01, 2.6) * mm, "end": v(19.87, 2.53) * mm});
            skLineSegment(sketch, "E9996", {"start": v(19.87, 2.53) * mm, "end": v(19.73, 2.45) * mm});
            skLineSegment(sketch, "E9997", {"start": v(19.73, 2.45) * mm, "end": v(19.6, 2.37) * mm});
            skLineSegment(sketch, "E9998", {"start": v(19.6, 2.37) * mm, "end": v(19.46, 2.29) * mm});
            skLineSegment(sketch, "E9999", {"start": v(19.46, 2.29) * mm, "end": v(19.33, 2.2) * mm});
            skLineSegment(sketch, "E10000", {"start": v(19.33, 2.2) * mm, "end": v(19.2, 2.09) * mm});
            skLineSegment(sketch, "E10001", {"start": v(19.2, 2.09) * mm, "end": v(19.09, 1.97) * mm});
            skLineSegment(sketch, "E10002", {"start": v(19.09, 1.97) * mm, "end": v(18.98, 1.83) * mm});
            skLineSegment(sketch, "E10003", {"start": v(18.98, 1.83) * mm, "end": v(18.97, 1.82) * mm});
            skLineSegment(sketch, "E10004", {"start": v(18.97, 1.82) * mm, "end": v(18.96, 1.8) * mm});
            skLineSegment(sketch, "E10005", {"start": v(18.96, 1.8) * mm, "end": v(18.95, 1.79) * mm});
            skLineSegment(sketch, "E10006", {"start": v(18.95, 1.79) * mm, "end": v(18.94, 1.77) * mm});
            skLineSegment(sketch, "E10007", {"start": v(18.94, 1.77) * mm, "end": v(18.92, 1.76) * mm});
            skLineSegment(sketch, "E10008", {"start": v(18.92, 1.76) * mm, "end": v(18.9, 1.74) * mm});
            skLineSegment(sketch, "E10009", {"start": v(18.9, 1.74) * mm, "end": v(18.9, 1.73) * mm});
            skLineSegment(sketch, "E10010", {"start": v(18.9, 1.73) * mm, "end": v(18.88, 1.71) * mm});
            skLineSegment(sketch, "E10011", {"start": v(18.88, 1.71) * mm, "end": v(18.84, 1.66) * mm});
            skLineSegment(sketch, "E10012", {"start": v(18.84, 1.66) * mm, "end": v(18.8, 1.61) * mm});
            skLineSegment(sketch, "E10013", {"start": v(18.8, 1.61) * mm, "end": v(18.76, 1.56) * mm});
            skLineSegment(sketch, "E10014", {"start": v(18.76, 1.56) * mm, "end": v(18.73, 1.5) * mm});
            skLineSegment(sketch, "E10015", {"start": v(18.73, 1.5) * mm, "end": v(18.7, 1.44) * mm});
            skLineSegment(sketch, "E10016", {"start": v(18.7, 1.44) * mm, "end": v(18.68, 1.38) * mm});
            skLineSegment(sketch, "E10017", {"start": v(18.68, 1.38) * mm, "end": v(18.66, 1.3) * mm});
            skLineSegment(sketch, "E10018", {"start": v(18.66, 1.3) * mm, "end": v(18.66, 1.22) * mm});
            skLineSegment(sketch, "E10019", {"start": v(18.66, 1.22) * mm, "end": v(18.66, 1.21) * mm});
            skLineSegment(sketch, "E10020", {"start": v(18.66, 1.21) * mm, "end": v(18.66, 1.2) * mm});
            skLineSegment(sketch, "E10021", {"start": v(18.66, 1.2) * mm, "end": v(18.67, 1.19) * mm});
            skLineSegment(sketch, "E10022", {"start": v(18.67, 1.19) * mm, "end": v(18.67, 1.18) * mm});
            skLineSegment(sketch, "E10023", {"start": v(18.67, 1.18) * mm, "end": v(18.67, 1.17) * mm});
            skLineSegment(sketch, "E10024", {"start": v(18.67, 1.17) * mm, "end": v(18.67, 1.16) * mm});
            skLineSegment(sketch, "E10025", {"start": v(18.67, 1.16) * mm, "end": v(18.67, 1.15) * mm});
            skLineSegment(sketch, "E10026", {"start": v(18.67, 1.15) * mm, "end": v(18.68, 1.13) * mm});
            skLineSegment(sketch, "E10027", {"start": v(18.68, 1.13) * mm, "end": v(18.68, 1.13) * mm});
            skLineSegment(sketch, "E10028", {"start": v(18.68, 1.13) * mm, "end": v(18.68, 1.12) * mm});
            skLineSegment(sketch, "E10029", {"start": v(18.68, 1.12) * mm, "end": v(18.68, 1.1) * mm});
            skLineSegment(sketch, "E10030", {"start": v(18.68, 1.1) * mm, "end": v(18.68, 1.1) * mm});
            skLineSegment(sketch, "E10031", {"start": v(18.68, 1.1) * mm, "end": v(18.69, 1.1) * mm});
            skLineSegment(sketch, "E10032", {"start": v(18.69, 1.1) * mm, "end": v(18.69, 1.08) * mm});
            skLineSegment(sketch, "E10033", {"start": v(18.69, 1.08) * mm, "end": v(18.69, 1.07) * mm});
            skLineSegment(sketch, "E10034", {"start": v(18.69, 1.07) * mm, "end": v(18.69, 1.07) * mm});
            skLineSegment(sketch, "E10035", {"start": v(18.69, 1.07) * mm, "end": v(18.69, 1.04) * mm});
            skLineSegment(sketch, "E10036", {"start": v(18.69, 1.04) * mm, "end": v(18.69, 1) * mm});
            skLineSegment(sketch, "E10037", {"start": v(18.69, 1) * mm, "end": v(18.69, 0.97) * mm});
            skLineSegment(sketch, "E10038", {"start": v(18.69, 0.97) * mm, "end": v(18.69, 0.94) * mm});
            skLineSegment(sketch, "E10039", {"start": v(18.69, 0.94) * mm, "end": v(18.69, 0.91) * mm});
            skLineSegment(sketch, "E10040", {"start": v(18.69, 0.91) * mm, "end": v(18.69, 0.88) * mm});
            skLineSegment(sketch, "E10041", {"start": v(18.69, 0.88) * mm, "end": v(18.69, 0.85) * mm});
            skLineSegment(sketch, "E10042", {"start": v(18.69, 0.85) * mm, "end": v(18.69, 0.82) * mm});
            skLineSegment(sketch, "E10043", {"start": v(18.69, 0.82) * mm, "end": v(18.69, 0.77) * mm});
            skLineSegment(sketch, "E10044", {"start": v(18.69, 0.77) * mm, "end": v(18.69, 0.7) * mm});
            skLineSegment(sketch, "E10045", {"start": v(18.69, 0.7) * mm, "end": v(18.69, 0.65) * mm});
            skLineSegment(sketch, "E10046", {"start": v(18.69, 0.65) * mm, "end": v(18.69, 0.6) * mm});
            skLineSegment(sketch, "E10047", {"start": v(18.69, 0.6) * mm, "end": v(18.69, 0.54) * mm});
            skLineSegment(sketch, "E10048", {"start": v(18.69, 0.54) * mm, "end": v(18.69, 0.48) * mm});
            skLineSegment(sketch, "E10049", {"start": v(18.69, 0.48) * mm, "end": v(18.7, 0.42) * mm});
            skLineSegment(sketch, "E10050", {"start": v(18.7, 0.42) * mm, "end": v(18.7, 0.37) * mm});
            skLineSegment(sketch, "E10051", {"start": v(18.7, 0.37) * mm, "end": v(18.7, 0.3) * mm});
            skLineSegment(sketch, "E10052", {"start": v(18.7, 0.3) * mm, "end": v(18.7, 0.25) * mm});
            skLineSegment(sketch, "E10053", {"start": v(18.7, 0.25) * mm, "end": v(18.7, 0.21) * mm});
            skLineSegment(sketch, "E10054", {"start": v(18.7, 0.21) * mm, "end": v(18.7, 0.2) * mm});
            skLineSegment(sketch, "E10055", {"start": v(18.7, 0.2) * mm, "end": v(18.7, 0.18) * mm});
            skLineSegment(sketch, "E10056", {"start": v(18.7, 0.18) * mm, "end": v(18.71, 0.17) * mm});
            skLineSegment(sketch, "E10057", {"start": v(18.71, 0.17) * mm, "end": v(18.71, 0.17) * mm});
            skLineSegment(sketch, "E10058", {"start": v(18.71, 0.17) * mm, "end": v(18.75, 0.08) * mm});
            skLineSegment(sketch, "E10059", {"start": v(18.75, 0.08) * mm, "end": v(18.8, 0) * mm});
            skLineSegment(sketch, "E10060", {"start": v(18.8, 0) * mm, "end": v(18.83, -0.07) * mm});
            skLineSegment(sketch, "E10061", {"start": v(18.83, -0.07) * mm, "end": v(18.86, -0.14) * mm});
            skLineSegment(sketch, "E10062", {"start": v(18.86, -0.14) * mm, "end": v(18.89, -0.2) * mm});
            skLineSegment(sketch, "E10063", {"start": v(18.89, -0.2) * mm, "end": v(18.9, -0.24) * mm});
            skLineSegment(sketch, "E10064", {"start": v(18.9, -0.24) * mm, "end": v(18.92, -0.26) * mm});
            skLineSegment(sketch, "E10065", {"start": v(18.92, -0.26) * mm, "end": v(18.93, -0.28) * mm});
            skLineSegment(sketch, "E10066", {"start": v(18.93, -0.28) * mm, "end": v(18.94, -0.28) * mm});
            skLineSegment(sketch, "E10067", {"start": v(18.94, -0.28) * mm, "end": v(18.94, -0.28) * mm});
            skLineSegment(sketch, "E10068", {"start": v(18.94, -0.28) * mm, "end": v(18.95, -0.29) * mm});
            skLineSegment(sketch, "E10069", {"start": v(18.95, -0.29) * mm, "end": v(18.96, -0.29) * mm});
            skLineSegment(sketch, "E10070", {"start": v(18.96, -0.29) * mm, "end": v(18.97, -0.29) * mm});
            skLineSegment(sketch, "E10071", {"start": v(18.97, -0.29) * mm, "end": v(18.98, -0.29) * mm});
            skLineSegment(sketch, "E10072", {"start": v(18.98, -0.29) * mm, "end": v(18.98, -0.29) * mm});
            skLineSegment(sketch, "E10073", {"start": v(18.98, -0.29) * mm, "end": v(19, -0.29) * mm});
            skLineSegment(sketch, "E10074", {"start": v(19, -0.29) * mm, "end": v(19, -0.28) * mm});
            skLineSegment(sketch, "E10075", {"start": v(19, -0.28) * mm, "end": v(19, -0.28) * mm});
            skLineSegment(sketch, "E10076", {"start": v(19, -0.28) * mm, "end": v(19.02, -0.28) * mm});
            skLineSegment(sketch, "E10077", {"start": v(19.02, -0.28) * mm, "end": v(19.02, -0.28) * mm});
            skLineSegment(sketch, "E10078", {"start": v(19.02, -0.28) * mm, "end": v(19.03, -0.27) * mm});
            skLineSegment(sketch, "E10079", {"start": v(19.03, -0.27) * mm, "end": v(19.04, -0.27) * mm});
            skLineSegment(sketch, "E10080", {"start": v(19.04, -0.27) * mm, "end": v(19.04, -0.27) * mm});
            skLineSegment(sketch, "E10081", {"start": v(19.04, -0.27) * mm, "end": v(19.05, -0.27) * mm});
            skLineSegment(sketch, "E10082", {"start": v(19.05, -0.27) * mm, "end": v(19.05, -0.27) * mm});
            skLineSegment(sketch, "E10083", {"start": v(19.05, -0.27) * mm, "end": v(19.06, -0.26) * mm});
            skLineSegment(sketch, "E10084", {"start": v(19.06, -0.26) * mm, "end": v(19.08, -0.26) * mm});
            skLineSegment(sketch, "E10085", {"start": v(19.08, -0.26) * mm, "end": v(19.09, -0.25) * mm});
            skLineSegment(sketch, "E10086", {"start": v(19.09, -0.25) * mm, "end": v(19.1, -0.25) * mm});
            skLineSegment(sketch, "E10087", {"start": v(19.1, -0.25) * mm, "end": v(19.12, -0.24) * mm});
            skLineSegment(sketch, "E10088", {"start": v(19.12, -0.24) * mm, "end": v(19.14, -0.23) * mm});
            skLineSegment(sketch, "E10089", {"start": v(19.14, -0.23) * mm, "end": v(19.15, -0.23) * mm});
            skLineSegment(sketch, "E10090", {"start": v(19.15, -0.23) * mm, "end": v(19.17, -0.22) * mm});
            skLineSegment(sketch, "E10091", {"start": v(19.17, -0.22) * mm, "end": v(19.2, -0.2) * mm});
            skLineSegment(sketch, "E10092", {"start": v(19.2, -0.2) * mm, "end": v(19.26, -0.18) * mm});
            skLineSegment(sketch, "E10093", {"start": v(19.26, -0.18) * mm, "end": v(19.32, -0.15) * mm});
            skLineSegment(sketch, "E10094", {"start": v(19.32, -0.15) * mm, "end": v(19.38, -0.12) * mm});
            skLineSegment(sketch, "E10095", {"start": v(19.38, -0.12) * mm, "end": v(19.46, -0.1) * mm});
            skLineSegment(sketch, "E10096", {"start": v(19.46, -0.1) * mm, "end": v(19.54, -0.06) * mm});
            skLineSegment(sketch, "E10097", {"start": v(19.54, -0.06) * mm, "end": v(19.62, -0.02) * mm});
            skLineSegment(sketch, "E10098", {"start": v(19.6, 0.48) * mm, "end": v(19.57, 0.47) * mm});
            skLineSegment(sketch, "E10099", {"start": v(19.57, 0.47) * mm, "end": v(19.54, 0.46) * mm});
            skLineSegment(sketch, "E10100", {"start": v(19.54, 0.46) * mm, "end": v(19.52, 0.46) * mm});
            skLineSegment(sketch, "E10101", {"start": v(19.52, 0.46) * mm, "end": v(19.5, 0.46) * mm});
            skLineSegment(sketch, "E10102", {"start": v(19.5, 0.46) * mm, "end": v(19.46, 0.47) * mm});
            skLineSegment(sketch, "E10103", {"start": v(19.46, 0.47) * mm, "end": v(19.42, 0.5) * mm});
            skLineSegment(sketch, "E10104", {"start": v(19.42, 0.5) * mm, "end": v(19.37, 0.52) * mm});
            skLineSegment(sketch, "E10105", {"start": v(19.37, 0.52) * mm, "end": v(19.34, 0.54) * mm});
            skLineSegment(sketch, "E10106", {"start": v(19.34, 0.54) * mm, "end": v(19.31, 0.58) * mm});
            skLineSegment(sketch, "E10107", {"start": v(19.31, 0.58) * mm, "end": v(19.3, 0.61) * mm});
            skLineSegment(sketch, "E10108", {"start": v(19.3, 0.61) * mm, "end": v(19.28, 0.65) * mm});
            skLineSegment(sketch, "E10109", {"start": v(19.28, 0.65) * mm, "end": v(19.27, 0.7) * mm});
            skLineSegment(sketch, "E10110", {"start": v(19.27, 0.7) * mm, "end": v(19.27, 0.75) * mm});
            skLineSegment(sketch, "E10111", {"start": v(19.27, 0.75) * mm, "end": v(19.27, 0.75) * mm});
            skLineSegment(sketch, "E10112", {"start": v(19.27, 0.75) * mm, "end": v(19.27, 0.76) * mm});
            skLineSegment(sketch, "E10113", {"start": v(19.27, 0.76) * mm, "end": v(19.27, 0.76) * mm});
            skLineSegment(sketch, "E10114", {"start": v(19.27, 0.76) * mm, "end": v(19.27, 0.77) * mm});
            skLineSegment(sketch, "E10115", {"start": v(19.27, 0.77) * mm, "end": v(19.27, 0.77) * mm});
            skLineSegment(sketch, "E10116", {"start": v(19.27, 0.77) * mm, "end": v(19.27, 0.78) * mm});
            skLineSegment(sketch, "E10117", {"start": v(19.27, 0.78) * mm, "end": v(19.27, 0.79) * mm});
            skLineSegment(sketch, "E10118", {"start": v(19.27, 0.79) * mm, "end": v(19.27, 0.8) * mm});
            skLineSegment(sketch, "E10119", {"start": v(19.27, 0.8) * mm, "end": v(19.27, 0.8) * mm});
            skLineSegment(sketch, "E10120", {"start": v(19.27, 0.8) * mm, "end": v(19.27, 0.81) * mm});
            skLineSegment(sketch, "E10121", {"start": v(19.27, 0.81) * mm, "end": v(19.28, 0.82) * mm});
            skLineSegment(sketch, "E10122", {"start": v(19.28, 0.82) * mm, "end": v(19.28, 0.84) * mm});
            skLineSegment(sketch, "E10123", {"start": v(19.28, 0.84) * mm, "end": v(19.28, 0.88) * mm});
            skLineSegment(sketch, "E10124", {"start": v(19.28, 0.88) * mm, "end": v(19.29, 0.92) * mm});
            skLineSegment(sketch, "E10125", {"start": v(19.29, 0.92) * mm, "end": v(19.3, 0.98) * mm});
            skLineSegment(sketch, "E10126", {"start": v(19.3, 0.98) * mm, "end": v(19.3, 1.04) * mm});
            skLineSegment(sketch, "E10127", {"start": v(19.3, 1.04) * mm, "end": v(19.32, 1.1) * mm});
            skLineSegment(sketch, "E10128", {"start": v(19.32, 1.1) * mm, "end": v(19.33, 1.18) * mm});
            skLineSegment(sketch, "E10129", {"start": v(19.33, 1.18) * mm, "end": v(19.35, 1.26) * mm});
            skLineSegment(sketch, "E10130", {"start": v(19.35, 1.26) * mm, "end": v(19.4, 1.36) * mm});
            skLineSegment(sketch, "E10131", {"start": v(19.4, 1.36) * mm, "end": v(19.44, 1.47) * mm});
            skLineSegment(sketch, "E10132", {"start": v(19.44, 1.47) * mm, "end": v(19.5, 1.57) * mm});
            skLineSegment(sketch, "E10133", {"start": v(19.5, 1.57) * mm, "end": v(19.56, 1.66) * mm});
            skLineSegment(sketch, "E10134", {"start": v(19.56, 1.66) * mm, "end": v(19.61, 1.74) * mm});
            skLineSegment(sketch, "E10135", {"start": v(19.61, 1.74) * mm, "end": v(19.65, 1.8) * mm});
            skLineSegment(sketch, "E10136", {"start": v(19.65, 1.8) * mm, "end": v(19.67, 1.82) * mm});
            skLineSegment(sketch, "E10137", {"start": v(19.67, 1.82) * mm, "end": v(19.68, 1.83) * mm});
            skLineSegment(sketch, "E10138", {"start": v(19.68, 1.83) * mm, "end": v(19.7, 1.85) * mm});
            skLineSegment(sketch, "E10139", {"start": v(19.7, 1.85) * mm, "end": v(19.72, 1.87) * mm});
            skLineSegment(sketch, "E10140", {"start": v(19.72, 1.87) * mm, "end": v(19.74, 1.9) * mm});
            skLineSegment(sketch, "E10141", {"start": v(19.74, 1.9) * mm, "end": v(19.78, 1.93) * mm});
            skLineSegment(sketch, "E10142", {"start": v(19.78, 1.93) * mm, "end": v(19.8, 1.96) * mm});
            skLineSegment(sketch, "E10143", {"start": v(19.8, 1.96) * mm, "end": v(19.85, 2) * mm});
            skLineSegment(sketch, "E10144", {"start": v(19.85, 2) * mm, "end": v(19.88, 2.03) * mm});
            skLineSegment(sketch, "E10145", {"start": v(19.88, 2.03) * mm, "end": v(19.88, 2.03) * mm});
            skLineSegment(sketch, "E10146", {"start": v(19.88, 2.03) * mm, "end": v(19.89, 2.03) * mm});
            skLineSegment(sketch, "E10147", {"start": v(19.89, 2.03) * mm, "end": v(19.89, 2.04) * mm});
            skLineSegment(sketch, "E10148", {"start": v(19.89, 2.04) * mm, "end": v(19.9, 2.04) * mm});
            skLineSegment(sketch, "E10149", {"start": v(19.9, 2.04) * mm, "end": v(19.9, 2.05) * mm});
            skLineSegment(sketch, "E10150", {"start": v(19.9, 2.05) * mm, "end": v(19.92, 2.07) * mm});
            skLineSegment(sketch, "E10151", {"start": v(19.92, 2.07) * mm, "end": v(19.95, 2.09) * mm});
            skLineSegment(sketch, "E10152", {"start": v(19.95, 2.09) * mm, "end": v(19.98, 2.11) * mm});
            skLineSegment(sketch, "E10153", {"start": v(19.98, 2.11) * mm, "end": v(19.98, 2.11) * mm});
            skLineSegment(sketch, "E10154", {"start": v(19.98, 2.11) * mm, "end": v(19.98, 2.12) * mm});
            skLineSegment(sketch, "E10155", {"start": v(19.98, 2.12) * mm, "end": v(19.99, 2.12) * mm});
            skLineSegment(sketch, "E10156", {"start": v(19.99, 2.12) * mm, "end": v(19.99, 2.12) * mm});
            skLineSegment(sketch, "E10157", {"start": v(19.99, 2.12) * mm, "end": v(20, 2.12) * mm});
            skLineSegment(sketch, "E10158", {"start": v(20, 2.12) * mm, "end": v(20, 2.12) * mm});
            skLineSegment(sketch, "E10159", {"start": v(20, 2.12) * mm, "end": v(20.01, 2.12) * mm});
            skLineSegment(sketch, "E10160", {"start": v(20.01, 2.12) * mm, "end": v(20.02, 2.13) * mm});
            skLineSegment(sketch, "E10161", {"start": v(20.02, 2.13) * mm, "end": v(20.03, 2.13) * mm});
            skLineSegment(sketch, "E10162", {"start": v(20.03, 2.13) * mm, "end": v(20.03, 2.13) * mm});
            skLineSegment(sketch, "E10163", {"start": v(20.03, 2.13) * mm, "end": v(20.04, 2.13) * mm});
            skLineSegment(sketch, "E10164", {"start": v(20.04, 2.13) * mm, "end": v(20.04, 2.12) * mm});
            skLineSegment(sketch, "E10165", {"start": v(20.04, 2.12) * mm, "end": v(20.05, 2.12) * mm});
            skLineSegment(sketch, "E10166", {"start": v(20.05, 2.12) * mm, "end": v(20.07, 2.11) * mm});
            skLineSegment(sketch, "E10167", {"start": v(20.07, 2.11) * mm, "end": v(20.1, 2.1) * mm});
            skLineSegment(sketch, "E10168", {"start": v(20.1, 2.1) * mm, "end": v(20.11, 2.09) * mm});
            skLineSegment(sketch, "E10169", {"start": v(20.11, 2.09) * mm, "end": v(20.14, 2.08) * mm});
            skLineSegment(sketch, "E10170", {"start": v(20.14, 2.08) * mm, "end": v(20.16, 2.06) * mm});
            skLineSegment(sketch, "E10171", {"start": v(20.16, 2.06) * mm, "end": v(20.2, 2.05) * mm});
            skLineSegment(sketch, "E10172", {"start": v(20.2, 2.05) * mm, "end": v(20.23, 2.02) * mm});
            skLineSegment(sketch, "E10173", {"start": v(20.23, 2.02) * mm, "end": v(20.27, 2) * mm});
            skLineSegment(sketch, "E10174", {"start": v(20.27, 2) * mm, "end": v(20.31, 1.97) * mm});
            skLineSegment(sketch, "E10175", {"start": v(20.31, 1.97) * mm, "end": v(20.35, 1.94) * mm});
            skLineSegment(sketch, "E10176", {"start": v(20.35, 1.94) * mm, "end": v(20.38, 1.92) * mm});
            skLineSegment(sketch, "E10177", {"start": v(20.38, 1.92) * mm, "end": v(20.4, 1.9) * mm});
            skLineSegment(sketch, "E10178", {"start": v(20.4, 1.9) * mm, "end": v(20.41, 1.89) * mm});
            skLineSegment(sketch, "E10179", {"start": v(20.41, 1.89) * mm, "end": v(20.41, 1.89) * mm});
            skLineSegment(sketch, "E10180", {"start": v(20.41, 1.89) * mm, "end": v(20.41, 1.88) * mm});
            skLineSegment(sketch, "E10181", {"start": v(20.41, 1.88) * mm, "end": v(20.41, 1.87) * mm});
            skLineSegment(sketch, "E10182", {"start": v(20.41, 1.87) * mm, "end": v(20.42, 1.86) * mm});
            skLineSegment(sketch, "E10183", {"start": v(20.42, 1.86) * mm, "end": v(20.42, 1.85) * mm});
            skLineSegment(sketch, "E10184", {"start": v(20.42, 1.85) * mm, "end": v(20.42, 1.83) * mm});
            skLineSegment(sketch, "E10185", {"start": v(20.42, 1.83) * mm, "end": v(20.42, 1.83) * mm});
            skLineSegment(sketch, "E10186", {"start": v(20.42, 1.83) * mm, "end": v(20.42, 1.82) * mm});
            skLineSegment(sketch, "E10187", {"start": v(20.42, 1.82) * mm, "end": v(20.41, 1.82) * mm});
            skLineSegment(sketch, "E10188", {"start": v(20.41, 1.82) * mm, "end": v(20.41, 1.8) * mm});
            skLineSegment(sketch, "E10189", {"start": v(20.41, 1.8) * mm, "end": v(20.41, 1.8) * mm});
            skLineSegment(sketch, "E10190", {"start": v(20.41, 1.8) * mm, "end": v(20.4, 1.8) * mm});
            skLineSegment(sketch, "E10191", {"start": v(20.4, 1.8) * mm, "end": v(20.4, 1.79) * mm});
            skLineSegment(sketch, "E10192", {"start": v(20.4, 1.79) * mm, "end": v(20.4, 1.78) * mm});
            skLineSegment(sketch, "E10193", {"start": v(20.4, 1.78) * mm, "end": v(20.4, 1.77) * mm});
            skLineSegment(sketch, "E10194", {"start": v(20.4, 1.77) * mm, "end": v(20.4, 1.76) * mm});
            skLineSegment(sketch, "E10195", {"start": v(20.4, 1.76) * mm, "end": v(20.4, 1.75) * mm});
            skLineSegment(sketch, "E10196", {"start": v(20.4, 1.75) * mm, "end": v(20.39, 1.73) * mm});
            skLineSegment(sketch, "E10197", {"start": v(20.39, 1.73) * mm, "end": v(20.39, 1.72) * mm});
            skLineSegment(sketch, "E10198", {"start": v(20.39, 1.72) * mm, "end": v(20.38, 1.7) * mm});
            skLineSegment(sketch, "E10199", {"start": v(20.38, 1.7) * mm, "end": v(20.38, 1.69) * mm});
            skLineSegment(sketch, "E10200", {"start": v(20.38, 1.69) * mm, "end": v(20.38, 1.67) * mm});
            skLineSegment(sketch, "E10201", {"start": v(20.38, 1.67) * mm, "end": v(20.37, 1.5) * mm});
            skLineSegment(sketch, "E10202", {"start": v(20.37, 1.5) * mm, "end": v(20.33, 1.34) * mm});
            skLineSegment(sketch, "E10203", {"start": v(20.33, 1.34) * mm, "end": v(20.27, 1.2) * mm});
            skLineSegment(sketch, "E10204", {"start": v(20.27, 1.2) * mm, "end": v(20.2, 1.07) * mm});
            skLineSegment(sketch, "E10205", {"start": v(20.2, 1.07) * mm, "end": v(20.1, 0.96) * mm});
            skLineSegment(sketch, "E10206", {"start": v(20.1, 0.96) * mm, "end": v(20, 0.85) * mm});
            skLineSegment(sketch, "E10207", {"start": v(20, 0.85) * mm, "end": v(19.9, 0.75) * mm});
            skLineSegment(sketch, "E10208", {"start": v(19.9, 0.75) * mm, "end": v(19.8, 0.66) * mm});
            skLineSegment(sketch, "E10209", {"start": v(19.8, 0.66) * mm, "end": v(19.79, 0.65) * mm});
            skLineSegment(sketch, "E10210", {"start": v(19.79, 0.65) * mm, "end": v(19.78, 0.65) * mm});
            skLineSegment(sketch, "E10211", {"start": v(19.78, 0.65) * mm, "end": v(19.78, 0.65) * mm});
            skLineSegment(sketch, "E10212", {"start": v(19.78, 0.65) * mm, "end": v(19.77, 0.64) * mm});
            skLineSegment(sketch, "E10213", {"start": v(19.77, 0.64) * mm, "end": v(19.77, 0.64) * mm});
            skLineSegment(sketch, "E10214", {"start": v(19.77, 0.64) * mm, "end": v(19.76, 0.64) * mm});
            skLineSegment(sketch, "E10215", {"start": v(19.76, 0.64) * mm, "end": v(19.76, 0.64) * mm});
            skLineSegment(sketch, "E10216", {"start": v(19.76, 0.64) * mm, "end": v(19.75, 0.63) * mm});
            skLineSegment(sketch, "E10217", {"start": v(19.75, 0.63) * mm, "end": v(19.74, 0.62) * mm});
            skLineSegment(sketch, "E10218", {"start": v(19.74, 0.62) * mm, "end": v(19.73, 0.62) * mm});
            skLineSegment(sketch, "E10219", {"start": v(19.73, 0.62) * mm, "end": v(19.72, 0.6) * mm});
            skLineSegment(sketch, "E10220", {"start": v(19.72, 0.6) * mm, "end": v(19.7, 0.6) * mm});
            skLineSegment(sketch, "E10221", {"start": v(19.7, 0.6) * mm, "end": v(19.7, 0.59) * mm});
            skLineSegment(sketch, "E10222", {"start": v(19.7, 0.59) * mm, "end": v(19.69, 0.58) * mm});
            skLineSegment(sketch, "E10223", {"start": v(19.69, 0.58) * mm, "end": v(19.68, 0.57) * mm});
            skLineSegment(sketch, "E10224", {"start": v(19.68, 0.57) * mm, "end": v(19.65, 0.53) * mm});
            skLineSegment(sketch, "E10225", {"start": v(19.65, 0.53) * mm, "end": v(19.62, 0.5) * mm});
            skLineSegment(sketch, "E10226", {"start": v(19.62, 0.5) * mm, "end": v(19.6, 0.48) * mm});
            skLineSegment(sketch, "E10227", {"start": v(33.6, 10.4) * mm, "end": v(33.52, 10.43) * mm});
            skLineSegment(sketch, "E10228", {"start": v(33.52, 10.43) * mm, "end": v(33.45, 10.45) * mm});
            skLineSegment(sketch, "E10229", {"start": v(33.45, 10.45) * mm, "end": v(33.38, 10.47) * mm});
            skLineSegment(sketch, "E10230", {"start": v(33.38, 10.47) * mm, "end": v(33.3, 10.48) * mm});
            skLineSegment(sketch, "E10231", {"start": v(33.3, 10.48) * mm, "end": v(33.23, 10.5) * mm});
            skLineSegment(sketch, "E10232", {"start": v(33.23, 10.5) * mm, "end": v(33.16, 10.52) * mm});
            skLineSegment(sketch, "E10233", {"start": v(33.16, 10.52) * mm, "end": v(33.1, 10.54) * mm});
            skLineSegment(sketch, "E10234", {"start": v(33.1, 10.54) * mm, "end": v(33.06, 10.54) * mm});
            skLineSegment(sketch, "E10235", {"start": v(33.06, 10.54) * mm, "end": v(33.04, 10.55) * mm});
            skLineSegment(sketch, "E10236", {"start": v(33.04, 10.55) * mm, "end": v(33.03, 10.55) * mm});
            skLineSegment(sketch, "E10237", {"start": v(33.03, 10.55) * mm, "end": v(33.02, 10.55) * mm});
            skLineSegment(sketch, "E10238", {"start": v(33.02, 10.55) * mm, "end": v(33.01, 10.55) * mm});
            skLineSegment(sketch, "E10239", {"start": v(33.01, 10.55) * mm, "end": v(33, 10.56) * mm});
            skLineSegment(sketch, "E10240", {"start": v(33, 10.56) * mm, "end": v(33, 10.56) * mm});
            skLineSegment(sketch, "E10241", {"start": v(33, 10.56) * mm, "end": v(32.97, 10.56) * mm});
            skLineSegment(sketch, "E10242", {"start": v(32.97, 10.56) * mm, "end": v(32.94, 10.57) * mm});
            skLineSegment(sketch, "E10243", {"start": v(32.94, 10.57) * mm, "end": v(32.9, 10.58) * mm});
            skLineSegment(sketch, "E10244", {"start": v(32.9, 10.58) * mm, "end": v(32.87, 10.59) * mm});
            skLineSegment(sketch, "E10245", {"start": v(32.87, 10.59) * mm, "end": v(32.85, 10.6) * mm});
            skLineSegment(sketch, "E10246", {"start": v(32.85, 10.6) * mm, "end": v(32.82, 10.6) * mm});
            skLineSegment(sketch, "E10247", {"start": v(32.82, 10.6) * mm, "end": v(32.8, 10.6) * mm});
            skLineSegment(sketch, "E10248", {"start": v(32.8, 10.6) * mm, "end": v(32.8, 10.6) * mm});
            skLineSegment(sketch, "E10249", {"start": v(32.8, 10.6) * mm, "end": v(32.78, 10.61) * mm});
            skLineSegment(sketch, "E10250", {"start": v(32.78, 10.61) * mm, "end": v(32.78, 10.61) * mm});
            skLineSegment(sketch, "E10251", {"start": v(32.78, 10.61) * mm, "end": v(32.77, 10.6) * mm});
            skLineSegment(sketch, "E10252", {"start": v(32.77, 10.6) * mm, "end": v(32.76, 10.6) * mm});
            skLineSegment(sketch, "E10253", {"start": v(32.76, 10.6) * mm, "end": v(32.75, 10.6) * mm});
            skLineSegment(sketch, "E10254", {"start": v(32.75, 10.6) * mm, "end": v(32.75, 10.6) * mm});
            skLineSegment(sketch, "E10255", {"start": v(32.75, 10.6) * mm, "end": v(32.74, 10.6) * mm});
            skLineSegment(sketch, "E10256", {"start": v(32.74, 10.6) * mm, "end": v(32.74, 10.59) * mm});
            skLineSegment(sketch, "E10257", {"start": v(32.74, 10.59) * mm, "end": v(32.73, 10.58) * mm});
            skLineSegment(sketch, "E10258", {"start": v(32.73, 10.58) * mm, "end": v(32.7, 10.57) * mm});
            skLineSegment(sketch, "E10259", {"start": v(32.7, 10.57) * mm, "end": v(32.66, 10.55) * mm});
            skLineSegment(sketch, "E10260", {"start": v(32.66, 10.55) * mm, "end": v(32.61, 10.54) * mm});
            skLineSegment(sketch, "E10261", {"start": v(32.61, 10.54) * mm, "end": v(32.55, 10.52) * mm});
            skLineSegment(sketch, "E10262", {"start": v(32.55, 10.52) * mm, "end": v(32.48, 10.5) * mm});
            skLineSegment(sketch, "E10263", {"start": v(32.48, 10.5) * mm, "end": v(32.4, 10.48) * mm});
            skLineSegment(sketch, "E10264", {"start": v(32.4, 10.48) * mm, "end": v(32.33, 10.46) * mm});
            skLineSegment(sketch, "E10265", {"start": v(32.33, 10.46) * mm, "end": v(32.33, 10.46) * mm});
            skLineSegment(sketch, "E10266", {"start": v(32.33, 10.46) * mm, "end": v(32.32, 10.46) * mm});
            skLineSegment(sketch, "E10267", {"start": v(32.32, 10.46) * mm, "end": v(32.32, 10.46) * mm});
            skLineSegment(sketch, "E10268", {"start": v(32.32, 10.46) * mm, "end": v(32.3, 10.45) * mm});
            skLineSegment(sketch, "E10269", {"start": v(32.3, 10.45) * mm, "end": v(32.28, 10.44) * mm});
            skLineSegment(sketch, "E10270", {"start": v(32.28, 10.44) * mm, "end": v(32.25, 10.42) * mm});
            skLineSegment(sketch, "E10271", {"start": v(32.25, 10.42) * mm, "end": v(32.21, 10.4) * mm});
            skLineSegment(sketch, "E10272", {"start": v(32.21, 10.4) * mm, "end": v(32.16, 10.35) * mm});
            skLineSegment(sketch, "E10273", {"start": v(32.16, 10.35) * mm, "end": v(32.1, 10.32) * mm});
            skLineSegment(sketch, "E10274", {"start": v(32.1, 10.32) * mm, "end": v(32.04, 10.29) * mm});
            skLineSegment(sketch, "E10275", {"start": v(32.04, 10.29) * mm, "end": v(31.99, 10.25) * mm});
            skLineSegment(sketch, "E10276", {"start": v(31.99, 10.25) * mm, "end": v(31.93, 10.22) * mm});
            skLineSegment(sketch, "E10277", {"start": v(31.93, 10.22) * mm, "end": v(31.87, 10.19) * mm});
            skLineSegment(sketch, "E10278", {"start": v(31.87, 10.19) * mm, "end": v(31.81, 10.16) * mm});
            skLineSegment(sketch, "E10279", {"start": v(31.81, 10.16) * mm, "end": v(31.75, 10.13) * mm});
            skLineSegment(sketch, "E10280", {"start": v(31.75, 10.13) * mm, "end": v(31.7, 10.1) * mm});
            skLineSegment(sketch, "E10281", {"start": v(31.7, 10.1) * mm, "end": v(31.67, 10.09) * mm});
            skLineSegment(sketch, "E10282", {"start": v(31.67, 10.09) * mm, "end": v(31.65, 10.07) * mm});
            skLineSegment(sketch, "E10283", {"start": v(31.65, 10.07) * mm, "end": v(31.63, 10.06) * mm});
            skLineSegment(sketch, "E10284", {"start": v(31.63, 10.06) * mm, "end": v(31.6, 10.05) * mm});
            skLineSegment(sketch, "E10285", {"start": v(31.6, 10.05) * mm, "end": v(31.58, 10.04) * mm});
            skLineSegment(sketch, "E10286", {"start": v(31.58, 10.04) * mm, "end": v(31.56, 10.03) * mm});
            skLineSegment(sketch, "E10287", {"start": v(31.56, 10.03) * mm, "end": v(31.54, 10.02) * mm});
            skLineSegment(sketch, "E10288", {"start": v(31.54, 10.02) * mm, "end": v(31.51, 10) * mm});
            skLineSegment(sketch, "E10289", {"start": v(31.51, 10) * mm, "end": v(31.45, 9.97) * mm});
            skLineSegment(sketch, "E10290", {"start": v(31.45, 9.97) * mm, "end": v(31.4, 9.93) * mm});
            skLineSegment(sketch, "E10291", {"start": v(31.4, 9.93) * mm, "end": v(31.35, 9.9) * mm});
            skLineSegment(sketch, "E10292", {"start": v(31.35, 9.9) * mm, "end": v(31.31, 9.86) * mm});
            skLineSegment(sketch, "E10293", {"start": v(31.31, 9.86) * mm, "end": v(31.28, 9.82) * mm});
            skLineSegment(sketch, "E10294", {"start": v(31.28, 9.82) * mm, "end": v(31.26, 9.78) * mm});
            skLineSegment(sketch, "E10295", {"start": v(31.26, 9.78) * mm, "end": v(31.24, 9.73) * mm});
            skLineSegment(sketch, "E10296", {"start": v(31.24, 9.73) * mm, "end": v(31.23, 9.69) * mm});
            skLineSegment(sketch, "E10297", {"start": v(31.23, 9.69) * mm, "end": v(31.23, 9.65) * mm});
            skLineSegment(sketch, "E10298", {"start": v(31.23, 9.65) * mm, "end": v(31.24, 9.6) * mm});
            skLineSegment(sketch, "E10299", {"start": v(31.24, 9.6) * mm, "end": v(31.26, 9.56) * mm});
            skLineSegment(sketch, "E10300", {"start": v(31.26, 9.56) * mm, "end": v(31.28, 9.51) * mm});
            skLineSegment(sketch, "E10301", {"start": v(31.28, 9.51) * mm, "end": v(31.31, 9.47) * mm});
            skLineSegment(sketch, "E10302", {"start": v(31.31, 9.47) * mm, "end": v(31.35, 9.43) * mm});
            skLineSegment(sketch, "E10303", {"start": v(31.35, 9.43) * mm, "end": v(31.4, 9.38) * mm});
            skLineSegment(sketch, "E10304", {"start": v(31.4, 9.38) * mm, "end": v(31.45, 9.34) * mm});
            skLineSegment(sketch, "E10305", {"start": v(31.45, 9.34) * mm, "end": v(31.47, 9.32) * mm});
            skLineSegment(sketch, "E10306", {"start": v(31.47, 9.32) * mm, "end": v(31.49, 9.3) * mm});
            skLineSegment(sketch, "E10307", {"start": v(31.49, 9.3) * mm, "end": v(31.51, 9.3) * mm});
            skLineSegment(sketch, "E10308", {"start": v(31.51, 9.3) * mm, "end": v(31.53, 9.28) * mm});
            skLineSegment(sketch, "E10309", {"start": v(31.53, 9.28) * mm, "end": v(31.55, 9.26) * mm});
            skLineSegment(sketch, "E10310", {"start": v(31.55, 9.26) * mm, "end": v(31.57, 9.24) * mm});
            skLineSegment(sketch, "E10311", {"start": v(31.57, 9.24) * mm, "end": v(31.6, 9.23) * mm});
            skLineSegment(sketch, "E10312", {"start": v(31.6, 9.23) * mm, "end": v(31.61, 9.21) * mm});
            skLineSegment(sketch, "E10313", {"start": v(31.61, 9.21) * mm, "end": v(31.66, 9.17) * mm});
            skLineSegment(sketch, "E10314", {"start": v(31.66, 9.17) * mm, "end": v(31.72, 9.13) * mm});
            skLineSegment(sketch, "E10315", {"start": v(31.72, 9.13) * mm, "end": v(31.77, 9.1) * mm});
            skLineSegment(sketch, "E10316", {"start": v(31.77, 9.1) * mm, "end": v(31.82, 9.05) * mm});
            skLineSegment(sketch, "E10317", {"start": v(31.82, 9.05) * mm, "end": v(31.87, 9) * mm});
            skLineSegment(sketch, "E10318", {"start": v(31.87, 9) * mm, "end": v(31.93, 8.97) * mm});
            skLineSegment(sketch, "E10319", {"start": v(31.93, 8.97) * mm, "end": v(31.98, 8.93) * mm});
            skLineSegment(sketch, "E10320", {"start": v(31.98, 8.93) * mm, "end": v(32.04, 8.9) * mm});
            skLineSegment(sketch, "E10321", {"start": v(32.04, 8.9) * mm, "end": v(32.15, 8.81) * mm});
            skLineSegment(sketch, "E10322", {"start": v(32.15, 8.81) * mm, "end": v(32.27, 8.74) * mm});
            skLineSegment(sketch, "E10323", {"start": v(32.27, 8.74) * mm, "end": v(32.4, 8.67) * mm});
            skLineSegment(sketch, "E10324", {"start": v(32.4, 8.67) * mm, "end": v(32.52, 8.6) * mm});
            skLineSegment(sketch, "E10325", {"start": v(32.52, 8.6) * mm, "end": v(32.65, 8.55) * mm});
            skLineSegment(sketch, "E10326", {"start": v(32.65, 8.55) * mm, "end": v(32.79, 8.51) * mm});
            skLineSegment(sketch, "E10327", {"start": v(32.79, 8.51) * mm, "end": v(32.93, 8.48) * mm});
            skLineSegment(sketch, "E10328", {"start": v(32.93, 8.48) * mm, "end": v(33.07, 8.48) * mm});
            skLineSegment(sketch, "E10329", {"start": v(33.07, 8.48) * mm, "end": v(33.12, 8.48) * mm});
            skLineSegment(sketch, "E10330", {"start": v(33.12, 8.48) * mm, "end": v(33.18, 8.48) * mm});
            skLineSegment(sketch, "E10331", {"start": v(33.18, 8.48) * mm, "end": v(33.23, 8.49) * mm});
            skLineSegment(sketch, "E10332", {"start": v(33.23, 8.49) * mm, "end": v(33.28, 8.5) * mm});
            skLineSegment(sketch, "E10333", {"start": v(33.28, 8.5) * mm, "end": v(33.33, 8.5) * mm});
            skLineSegment(sketch, "E10334", {"start": v(33.33, 8.5) * mm, "end": v(33.38, 8.52) * mm});
            skLineSegment(sketch, "E10335", {"start": v(33.38, 8.52) * mm, "end": v(33.44, 8.54) * mm});
            skLineSegment(sketch, "E10336", {"start": v(33.44, 8.54) * mm, "end": v(33.49, 8.56) * mm});
            skLineSegment(sketch, "E10337", {"start": v(33.49, 8.56) * mm, "end": v(33.57, 8.59) * mm});
            skLineSegment(sketch, "E10338", {"start": v(33.57, 8.59) * mm, "end": v(33.66, 8.63) * mm});
            skLineSegment(sketch, "E10339", {"start": v(33.66, 8.63) * mm, "end": v(33.74, 8.67) * mm});
            skLineSegment(sketch, "E10340", {"start": v(33.74, 8.67) * mm, "end": v(33.83, 8.71) * mm});
            skLineSegment(sketch, "E10341", {"start": v(33.83, 8.71) * mm, "end": v(33.93, 8.76) * mm});
            skLineSegment(sketch, "E10342", {"start": v(33.93, 8.76) * mm, "end": v(34.02, 8.8) * mm});
            skLineSegment(sketch, "E10343", {"start": v(34.02, 8.8) * mm, "end": v(34.12, 8.86) * mm});
            skLineSegment(sketch, "E10344", {"start": v(34.12, 8.86) * mm, "end": v(34.23, 8.92) * mm});
            skLineSegment(sketch, "E10345", {"start": v(34.23, 8.92) * mm, "end": v(34.3, 8.96) * mm});
            skLineSegment(sketch, "E10346", {"start": v(34.3, 8.96) * mm, "end": v(34.35, 9) * mm});
            skLineSegment(sketch, "E10347", {"start": v(34.35, 9) * mm, "end": v(34.39, 9.02) * mm});
            skLineSegment(sketch, "E10348", {"start": v(34.39, 9.02) * mm, "end": v(34.41, 9.03) * mm});
            skLineSegment(sketch, "E10349", {"start": v(34.41, 9.03) * mm, "end": v(34.43, 9.04) * mm});
            skLineSegment(sketch, "E10350", {"start": v(34.43, 9.04) * mm, "end": v(34.43, 9.04) * mm});
            skLineSegment(sketch, "E10351", {"start": v(34.43, 9.04) * mm, "end": v(34.44, 9.05) * mm});
            skLineSegment(sketch, "E10352", {"start": v(34.44, 9.05) * mm, "end": v(34.44, 9.05) * mm});
            skLineSegment(sketch, "E10353", {"start": v(34.44, 9.05) * mm, "end": v(34.48, 9.13) * mm});
            skLineSegment(sketch, "E10354", {"start": v(34.48, 9.13) * mm, "end": v(34.52, 9.2) * mm});
            skLineSegment(sketch, "E10355", {"start": v(34.52, 9.2) * mm, "end": v(34.55, 9.28) * mm});
            skLineSegment(sketch, "E10356", {"start": v(34.55, 9.28) * mm, "end": v(34.59, 9.34) * mm});
            skLineSegment(sketch, "E10357", {"start": v(34.59, 9.34) * mm, "end": v(34.61, 9.4) * mm});
            skLineSegment(sketch, "E10358", {"start": v(34.61, 9.4) * mm, "end": v(34.63, 9.43) * mm});
            skLineSegment(sketch, "E10359", {"start": v(34.63, 9.43) * mm, "end": v(34.65, 9.46) * mm});
            skLineSegment(sketch, "E10360", {"start": v(34.65, 9.46) * mm, "end": v(34.65, 9.47) * mm});
            skLineSegment(sketch, "E10361", {"start": v(34.65, 9.47) * mm, "end": v(34.66, 9.48) * mm});
            skLineSegment(sketch, "E10362", {"start": v(34.66, 9.48) * mm, "end": v(34.66, 9.5) * mm});
            skLineSegment(sketch, "E10363", {"start": v(34.66, 9.5) * mm, "end": v(34.66, 9.52) * mm});
            skLineSegment(sketch, "E10364", {"start": v(34.66, 9.52) * mm, "end": v(34.66, 9.56) * mm});
            skLineSegment(sketch, "E10365", {"start": v(34.66, 9.56) * mm, "end": v(34.66, 9.59) * mm});
            skLineSegment(sketch, "E10366", {"start": v(34.66, 9.59) * mm, "end": v(34.66, 9.63) * mm});
            skLineSegment(sketch, "E10367", {"start": v(34.66, 9.63) * mm, "end": v(34.65, 9.66) * mm});
            skLineSegment(sketch, "E10368", {"start": v(34.65, 9.66) * mm, "end": v(34.64, 9.7) * mm});
            skLineSegment(sketch, "E10369", {"start": v(34.64, 9.7) * mm, "end": v(34.63, 9.72) * mm});
            skLineSegment(sketch, "E10370", {"start": v(34.63, 9.72) * mm, "end": v(34.62, 9.75) * mm});
            skLineSegment(sketch, "E10371", {"start": v(34.62, 9.75) * mm, "end": v(34.6, 9.78) * mm});
            skLineSegment(sketch, "E10372", {"start": v(34.6, 9.78) * mm, "end": v(34.59, 9.8) * mm});
            skLineSegment(sketch, "E10373", {"start": v(34.59, 9.8) * mm, "end": v(34.57, 9.83) * mm});
            skLineSegment(sketch, "E10374", {"start": v(34.57, 9.83) * mm, "end": v(34.56, 9.86) * mm});
            skLineSegment(sketch, "E10375", {"start": v(34.56, 9.86) * mm, "end": v(34.54, 9.87) * mm});
            skLineSegment(sketch, "E10376", {"start": v(34.54, 9.87) * mm, "end": v(34.53, 9.88) * mm});
            skLineSegment(sketch, "E10377", {"start": v(34.53, 9.88) * mm, "end": v(34.5, 9.9) * mm});
            skLineSegment(sketch, "E10378", {"start": v(34.5, 9.9) * mm, "end": v(34.47, 9.93) * mm});
            skLineSegment(sketch, "E10379", {"start": v(34.47, 9.93) * mm, "end": v(34.4, 9.97) * mm});
            skLineSegment(sketch, "E10380", {"start": v(34.4, 9.97) * mm, "end": v(34.34, 10.02) * mm});
            skLineSegment(sketch, "E10381", {"start": v(34.34, 10.02) * mm, "end": v(34.26, 10.08) * mm});
            skLineSegment(sketch, "E10382", {"start": v(34.26, 10.08) * mm, "end": v(34.17, 10.14) * mm});
            skLineSegment(sketch, "E10383", {"start": v(34.17, 10.14) * mm, "end": v(34.07, 10.21) * mm});
            skLineSegment(sketch, "E10384", {"start": v(34.07, 10.21) * mm, "end": v(33.97, 10.28) * mm});
            skLineSegment(sketch, "E10385", {"start": v(33.97, 10.28) * mm, "end": v(33.97, 10.28) * mm});
            skLineSegment(sketch, "E10386", {"start": v(33.97, 10.28) * mm, "end": v(33.96, 10.29) * mm});
            skLineSegment(sketch, "E10387", {"start": v(33.96, 10.29) * mm, "end": v(33.95, 10.29) * mm});
            skLineSegment(sketch, "E10388", {"start": v(33.95, 10.29) * mm, "end": v(33.93, 10.3) * mm});
            skLineSegment(sketch, "E10389", {"start": v(33.93, 10.3) * mm, "end": v(33.9, 10.3) * mm});
            skLineSegment(sketch, "E10390", {"start": v(33.9, 10.3) * mm, "end": v(33.84, 10.33) * mm});
            skLineSegment(sketch, "E10391", {"start": v(33.84, 10.33) * mm, "end": v(33.77, 10.35) * mm});
            skLineSegment(sketch, "E10392", {"start": v(33.77, 10.35) * mm, "end": v(33.67, 10.38) * mm});
            skLineSegment(sketch, "E10393", {"start": v(33.67, 10.38) * mm, "end": v(33.6, 10.4) * mm});
            skLineSegment(sketch, "E10394", {"start": v(33.7, 9.75) * mm, "end": v(33.72, 9.71) * mm});
            skLineSegment(sketch, "E10395", {"start": v(33.72, 9.71) * mm, "end": v(33.74, 9.67) * mm});
            skLineSegment(sketch, "E10396", {"start": v(33.74, 9.67) * mm, "end": v(33.74, 9.64) * mm});
            skLineSegment(sketch, "E10397", {"start": v(33.74, 9.64) * mm, "end": v(33.75, 9.6) * mm});
            skLineSegment(sketch, "E10398", {"start": v(33.75, 9.6) * mm, "end": v(33.75, 9.57) * mm});
            skLineSegment(sketch, "E10399", {"start": v(33.75, 9.57) * mm, "end": v(33.75, 9.52) * mm});
            skLineSegment(sketch, "E10400", {"start": v(33.75, 9.52) * mm, "end": v(33.75, 9.46) * mm});
            skLineSegment(sketch, "E10401", {"start": v(33.75, 9.46) * mm, "end": v(33.74, 9.41) * mm});
            skLineSegment(sketch, "E10402", {"start": v(33.74, 9.41) * mm, "end": v(33.72, 9.36) * mm});
            skLineSegment(sketch, "E10403", {"start": v(33.72, 9.36) * mm, "end": v(33.7, 9.32) * mm});
            skLineSegment(sketch, "E10404", {"start": v(33.7, 9.32) * mm, "end": v(33.68, 9.28) * mm});
            skLineSegment(sketch, "E10405", {"start": v(33.68, 9.28) * mm, "end": v(33.65, 9.24) * mm});
            skLineSegment(sketch, "E10406", {"start": v(33.65, 9.24) * mm, "end": v(33.62, 9.22) * mm});
            skLineSegment(sketch, "E10407", {"start": v(33.62, 9.22) * mm, "end": v(33.57, 9.19) * mm});
            skLineSegment(sketch, "E10408", {"start": v(33.57, 9.19) * mm, "end": v(33.52, 9.16) * mm});
            skLineSegment(sketch, "E10409", {"start": v(33.52, 9.16) * mm, "end": v(33.47, 9.14) * mm});
            skLineSegment(sketch, "E10410", {"start": v(33.47, 9.14) * mm, "end": v(33.42, 9.12) * mm});
            skLineSegment(sketch, "E10411", {"start": v(33.42, 9.12) * mm, "end": v(33.37, 9.1) * mm});
            skLineSegment(sketch, "E10412", {"start": v(33.37, 9.1) * mm, "end": v(33.31, 9.09) * mm});
            skLineSegment(sketch, "E10413", {"start": v(33.31, 9.09) * mm, "end": v(33.26, 9.08) * mm});
            skLineSegment(sketch, "E10414", {"start": v(33.26, 9.08) * mm, "end": v(33.2, 9.08) * mm});
            skLineSegment(sketch, "E10415", {"start": v(33.2, 9.08) * mm, "end": v(33.2, 9.08) * mm});
            skLineSegment(sketch, "E10416", {"start": v(33.2, 9.08) * mm, "end": v(33.18, 9.07) * mm});
            skLineSegment(sketch, "E10417", {"start": v(33.18, 9.07) * mm, "end": v(33.16, 9.07) * mm});
            skLineSegment(sketch, "E10418", {"start": v(33.16, 9.07) * mm, "end": v(33.15, 9.07) * mm});
            skLineSegment(sketch, "E10419", {"start": v(33.15, 9.07) * mm, "end": v(33.13, 9.07) * mm});
            skLineSegment(sketch, "E10420", {"start": v(33.13, 9.07) * mm, "end": v(33.11, 9.07) * mm});
            skLineSegment(sketch, "E10421", {"start": v(33.11, 9.07) * mm, "end": v(33.1, 9.07) * mm});
            skLineSegment(sketch, "E10422", {"start": v(33.1, 9.07) * mm, "end": v(33.08, 9.07) * mm});
            skLineSegment(sketch, "E10423", {"start": v(33.08, 9.07) * mm, "end": v(32.97, 9.08) * mm});
            skLineSegment(sketch, "E10424", {"start": v(32.97, 9.08) * mm, "end": v(32.87, 9.08) * mm});
            skLineSegment(sketch, "E10425", {"start": v(32.87, 9.08) * mm, "end": v(32.78, 9.1) * mm});
            skLineSegment(sketch, "E10426", {"start": v(32.78, 9.1) * mm, "end": v(32.69, 9.12) * mm});
            skLineSegment(sketch, "E10427", {"start": v(32.69, 9.12) * mm, "end": v(32.6, 9.14) * mm});
            skLineSegment(sketch, "E10428", {"start": v(32.6, 9.14) * mm, "end": v(32.52, 9.17) * mm});
            skLineSegment(sketch, "E10429", {"start": v(32.52, 9.17) * mm, "end": v(32.44, 9.2) * mm});
            skLineSegment(sketch, "E10430", {"start": v(32.44, 9.2) * mm, "end": v(32.37, 9.25) * mm});
            skLineSegment(sketch, "E10431", {"start": v(32.37, 9.25) * mm, "end": v(32.35, 9.26) * mm});
            skLineSegment(sketch, "E10432", {"start": v(32.35, 9.26) * mm, "end": v(32.33, 9.27) * mm});
            skLineSegment(sketch, "E10433", {"start": v(32.33, 9.27) * mm, "end": v(32.31, 9.28) * mm});
            skLineSegment(sketch, "E10434", {"start": v(32.31, 9.28) * mm, "end": v(32.29, 9.3) * mm});
            skLineSegment(sketch, "E10435", {"start": v(32.29, 9.3) * mm, "end": v(32.26, 9.3) * mm});
            skLineSegment(sketch, "E10436", {"start": v(32.26, 9.3) * mm, "end": v(32.24, 9.31) * mm});
            skLineSegment(sketch, "E10437", {"start": v(32.24, 9.31) * mm, "end": v(32.2, 9.32) * mm});
            skLineSegment(sketch, "E10438", {"start": v(32.2, 9.32) * mm, "end": v(32.18, 9.32) * mm});
            skLineSegment(sketch, "E10439", {"start": v(32.18, 9.32) * mm, "end": v(32.15, 9.32) * mm});
            skLineSegment(sketch, "E10440", {"start": v(32.15, 9.32) * mm, "end": v(32.13, 9.33) * mm});
            skLineSegment(sketch, "E10441", {"start": v(32.13, 9.33) * mm, "end": v(32.1, 9.35) * mm});
            skLineSegment(sketch, "E10442", {"start": v(32.1, 9.35) * mm, "end": v(32.09, 9.36) * mm});
            skLineSegment(sketch, "E10443", {"start": v(32.09, 9.36) * mm, "end": v(32.07, 9.39) * mm});
            skLineSegment(sketch, "E10444", {"start": v(32.07, 9.39) * mm, "end": v(32.05, 9.42) * mm});
            skLineSegment(sketch, "E10445", {"start": v(32.05, 9.42) * mm, "end": v(32.04, 9.46) * mm});
            skLineSegment(sketch, "E10446", {"start": v(32.04, 9.46) * mm, "end": v(32.02, 9.5) * mm});
            skLineSegment(sketch, "E10447", {"start": v(32.02, 9.5) * mm, "end": v(32, 9.54) * mm});
            skLineSegment(sketch, "E10448", {"start": v(32, 9.54) * mm, "end": v(31.99, 9.57) * mm});
            skLineSegment(sketch, "E10449", {"start": v(31.99, 9.57) * mm, "end": v(31.98, 9.6) * mm});
            skLineSegment(sketch, "E10450", {"start": v(31.98, 9.6) * mm, "end": v(31.97, 9.61) * mm});
            skLineSegment(sketch, "E10451", {"start": v(31.97, 9.61) * mm, "end": v(31.97, 9.62) * mm});
            skLineSegment(sketch, "E10452", {"start": v(31.97, 9.62) * mm, "end": v(31.96, 9.62) * mm});
            skLineSegment(sketch, "E10453", {"start": v(31.96, 9.62) * mm, "end": v(31.96, 9.63) * mm});
            skLineSegment(sketch, "E10454", {"start": v(31.96, 9.63) * mm, "end": v(31.96, 9.63) * mm});
            skLineSegment(sketch, "E10455", {"start": v(31.96, 9.63) * mm, "end": v(32, 9.65) * mm});
            skLineSegment(sketch, "E10456", {"start": v(32, 9.65) * mm, "end": v(32.05, 9.67) * mm});
            skLineSegment(sketch, "E10457", {"start": v(32.05, 9.67) * mm, "end": v(32.08, 9.7) * mm});
            skLineSegment(sketch, "E10458", {"start": v(32.08, 9.7) * mm, "end": v(32.12, 9.71) * mm});
            skLineSegment(sketch, "E10459", {"start": v(32.12, 9.71) * mm, "end": v(32.14, 9.73) * mm});
            skLineSegment(sketch, "E10460", {"start": v(32.14, 9.73) * mm, "end": v(32.16, 9.74) * mm});
            skLineSegment(sketch, "E10461", {"start": v(32.16, 9.74) * mm, "end": v(32.18, 9.75) * mm});
            skLineSegment(sketch, "E10462", {"start": v(32.18, 9.75) * mm, "end": v(32.19, 9.75) * mm});
            skLineSegment(sketch, "E10463", {"start": v(32.19, 9.75) * mm, "end": v(32.19, 9.75) * mm});
            skLineSegment(sketch, "E10464", {"start": v(32.19, 9.75) * mm, "end": v(32.2, 9.76) * mm});
            skLineSegment(sketch, "E10465", {"start": v(32.2, 9.76) * mm, "end": v(32.2, 9.76) * mm});
            skLineSegment(sketch, "E10466", {"start": v(32.2, 9.76) * mm, "end": v(32.22, 9.77) * mm});
            skLineSegment(sketch, "E10467", {"start": v(32.22, 9.77) * mm, "end": v(32.23, 9.77) * mm});
            skLineSegment(sketch, "E10468", {"start": v(32.23, 9.77) * mm, "end": v(32.24, 9.78) * mm});
            skLineSegment(sketch, "E10469", {"start": v(32.24, 9.78) * mm, "end": v(32.26, 9.79) * mm});
            skLineSegment(sketch, "E10470", {"start": v(32.26, 9.79) * mm, "end": v(32.27, 9.8) * mm});
            skLineSegment(sketch, "E10471", {"start": v(32.27, 9.8) * mm, "end": v(32.28, 9.8) * mm});
            skLineSegment(sketch, "E10472", {"start": v(32.28, 9.8) * mm, "end": v(32.28, 9.8) * mm});
            skLineSegment(sketch, "E10473", {"start": v(32.28, 9.8) * mm, "end": v(32.3, 9.8) * mm});
            skLineSegment(sketch, "E10474", {"start": v(32.3, 9.8) * mm, "end": v(32.3, 9.8) * mm});
            skLineSegment(sketch, "E10475", {"start": v(32.3, 9.8) * mm, "end": v(32.31, 9.81) * mm});
            skLineSegment(sketch, "E10476", {"start": v(32.31, 9.81) * mm, "end": v(32.38, 9.85) * mm});
            skLineSegment(sketch, "E10477", {"start": v(32.38, 9.85) * mm, "end": v(32.46, 9.88) * mm});
            skLineSegment(sketch, "E10478", {"start": v(32.46, 9.88) * mm, "end": v(32.53, 9.91) * mm});
            skLineSegment(sketch, "E10479", {"start": v(32.53, 9.91) * mm, "end": v(32.6, 9.94) * mm});
            skLineSegment(sketch, "E10480", {"start": v(32.6, 9.94) * mm, "end": v(32.67, 9.96) * mm});
            skLineSegment(sketch, "E10481", {"start": v(32.67, 9.96) * mm, "end": v(32.74, 9.98) * mm});
            skLineSegment(sketch, "E10482", {"start": v(32.74, 9.98) * mm, "end": v(32.81, 10) * mm});
            skLineSegment(sketch, "E10483", {"start": v(32.81, 10) * mm, "end": v(32.89, 10) * mm});
            skLineSegment(sketch, "E10484", {"start": v(32.89, 10) * mm, "end": v(32.9, 10) * mm});
            skLineSegment(sketch, "E10485", {"start": v(32.9, 10) * mm, "end": v(32.9, 10) * mm});
            skLineSegment(sketch, "E10486", {"start": v(32.9, 10) * mm, "end": v(32.91, 10) * mm});
            skLineSegment(sketch, "E10487", {"start": v(32.91, 10) * mm, "end": v(32.91, 10) * mm});
            skLineSegment(sketch, "E10488", {"start": v(32.91, 10) * mm, "end": v(32.93, 10) * mm});
            skLineSegment(sketch, "E10489", {"start": v(32.93, 10) * mm, "end": v(32.94, 10) * mm});
            skLineSegment(sketch, "E10490", {"start": v(32.94, 10) * mm, "end": v(32.95, 10) * mm});
            skLineSegment(sketch, "E10491", {"start": v(32.95, 10) * mm, "end": v(32.96, 10) * mm});
            skLineSegment(sketch, "E10492", {"start": v(32.96, 10) * mm, "end": v(32.97, 10) * mm});
            skLineSegment(sketch, "E10493", {"start": v(32.97, 10) * mm, "end": v(32.98, 10) * mm});
            skLineSegment(sketch, "E10494", {"start": v(32.98, 10) * mm, "end": v(32.98, 10) * mm});
            skLineSegment(sketch, "E10495", {"start": v(32.98, 10) * mm, "end": v(32.99, 10) * mm});
            skLineSegment(sketch, "E10496", {"start": v(32.99, 10) * mm, "end": v(33, 10) * mm});
            skLineSegment(sketch, "E10497", {"start": v(33, 10) * mm, "end": v(33.03, 9.99) * mm});
            skLineSegment(sketch, "E10498", {"start": v(33.03, 9.99) * mm, "end": v(33.07, 9.98) * mm});
            skLineSegment(sketch, "E10499", {"start": v(33.07, 9.98) * mm, "end": v(33.12, 9.98) * mm});
            skLineSegment(sketch, "E10500", {"start": v(33.12, 9.98) * mm, "end": v(33.18, 9.97) * mm});
            skLineSegment(sketch, "E10501", {"start": v(33.18, 9.97) * mm, "end": v(33.25, 9.96) * mm});
            skLineSegment(sketch, "E10502", {"start": v(33.25, 9.96) * mm, "end": v(33.33, 9.95) * mm});
            skLineSegment(sketch, "E10503", {"start": v(33.33, 9.95) * mm, "end": v(33.41, 9.94) * mm});
            skLineSegment(sketch, "E10504", {"start": v(33.41, 9.94) * mm, "end": v(33.41, 9.94) * mm});
            skLineSegment(sketch, "E10505", {"start": v(33.41, 9.94) * mm, "end": v(33.42, 9.94) * mm});
            skLineSegment(sketch, "E10506", {"start": v(33.42, 9.94) * mm, "end": v(33.42, 9.94) * mm});
            skLineSegment(sketch, "E10507", {"start": v(33.42, 9.94) * mm, "end": v(33.44, 9.93) * mm});
            skLineSegment(sketch, "E10508", {"start": v(33.44, 9.93) * mm, "end": v(33.46, 9.92) * mm});
            skLineSegment(sketch, "E10509", {"start": v(33.46, 9.92) * mm, "end": v(33.5, 9.9) * mm});
            skLineSegment(sketch, "E10510", {"start": v(33.5, 9.9) * mm, "end": v(33.54, 9.88) * mm});
            skLineSegment(sketch, "E10511", {"start": v(33.54, 9.88) * mm, "end": v(33.6, 9.84) * mm});
            skLineSegment(sketch, "E10512", {"start": v(33.6, 9.84) * mm, "end": v(33.64, 9.81) * mm});
            skLineSegment(sketch, "E10513", {"start": v(33.64, 9.81) * mm, "end": v(33.68, 9.78) * mm});
            skLineSegment(sketch, "E10514", {"start": v(33.68, 9.78) * mm, "end": v(33.7, 9.75) * mm});
            skLineSegment(sketch, "E10515", {"start": v(25.09, 0.95) * mm, "end": v(25.09, 0.96) * mm});
            skLineSegment(sketch, "E10516", {"start": v(25.09, 0.96) * mm, "end": v(25.09, 0.96) * mm});
            skLineSegment(sketch, "E10517", {"start": v(25.09, 0.96) * mm, "end": v(25.09, 0.98) * mm});
            skLineSegment(sketch, "E10518", {"start": v(25.09, 0.98) * mm, "end": v(25.09, 1.02) * mm});
            skLineSegment(sketch, "E10519", {"start": v(25.09, 1.02) * mm, "end": v(25.08, 1.06) * mm});
            skLineSegment(sketch, "E10520", {"start": v(25.08, 1.06) * mm, "end": v(25.08, 1.1) * mm});
            skLineSegment(sketch, "E10521", {"start": v(25.08, 1.1) * mm, "end": v(25.07, 1.15) * mm});
            skLineSegment(sketch, "E10522", {"start": v(25.07, 1.15) * mm, "end": v(25.07, 1.19) * mm});
            skLineSegment(sketch, "E10523", {"start": v(25.07, 1.19) * mm, "end": v(25.06, 1.23) * mm});
            skLineSegment(sketch, "E10524", {"start": v(25.06, 1.23) * mm, "end": v(25.04, 1.27) * mm});
            skLineSegment(sketch, "E10525", {"start": v(25.04, 1.27) * mm, "end": v(25.02, 1.3) * mm});
            skLineSegment(sketch, "E10526", {"start": v(25.02, 1.3) * mm, "end": v(24.97, 1.4) * mm});
            skLineSegment(sketch, "E10527", {"start": v(24.97, 1.4) * mm, "end": v(24.9, 1.5) * mm});
            skLineSegment(sketch, "E10528", {"start": v(24.9, 1.5) * mm, "end": v(24.85, 1.58) * mm});
            skLineSegment(sketch, "E10529", {"start": v(24.85, 1.58) * mm, "end": v(24.8, 1.67) * mm});
            skLineSegment(sketch, "E10530", {"start": v(24.8, 1.67) * mm, "end": v(24.73, 1.76) * mm});
            skLineSegment(sketch, "E10531", {"start": v(24.73, 1.76) * mm, "end": v(24.67, 1.85) * mm});
            skLineSegment(sketch, "E10532", {"start": v(24.67, 1.85) * mm, "end": v(24.61, 1.93) * mm});
            skLineSegment(sketch, "E10533", {"start": v(24.61, 1.93) * mm, "end": v(24.56, 2.02) * mm});
            skLineSegment(sketch, "E10534", {"start": v(24.56, 2.02) * mm, "end": v(24.54, 2.05) * mm});
            skLineSegment(sketch, "E10535", {"start": v(24.54, 2.05) * mm, "end": v(24.52, 2.08) * mm});
            skLineSegment(sketch, "E10536", {"start": v(24.52, 2.08) * mm, "end": v(24.5, 2.1) * mm});
            skLineSegment(sketch, "E10537", {"start": v(24.5, 2.1) * mm, "end": v(24.47, 2.14) * mm});
            skLineSegment(sketch, "E10538", {"start": v(24.47, 2.14) * mm, "end": v(24.46, 2.17) * mm});
            skLineSegment(sketch, "E10539", {"start": v(24.46, 2.17) * mm, "end": v(24.43, 2.2) * mm});
            skLineSegment(sketch, "E10540", {"start": v(24.43, 2.2) * mm, "end": v(24.41, 2.23) * mm});
            skLineSegment(sketch, "E10541", {"start": v(24.41, 2.23) * mm, "end": v(24.4, 2.26) * mm});
            skLineSegment(sketch, "E10542", {"start": v(24.4, 2.26) * mm, "end": v(24.38, 2.28) * mm});
            skLineSegment(sketch, "E10543", {"start": v(24.38, 2.28) * mm, "end": v(24.35, 2.3) * mm});
            skLineSegment(sketch, "E10544", {"start": v(24.35, 2.3) * mm, "end": v(24.33, 2.32) * mm});
            skLineSegment(sketch, "E10545", {"start": v(24.33, 2.32) * mm, "end": v(24.31, 2.33) * mm});
            skLineSegment(sketch, "E10546", {"start": v(24.31, 2.33) * mm, "end": v(24.3, 2.34) * mm});
            skLineSegment(sketch, "E10547", {"start": v(24.3, 2.34) * mm, "end": v(24.28, 2.34) * mm});
            skLineSegment(sketch, "E10548", {"start": v(24.28, 2.34) * mm, "end": v(24.26, 2.35) * mm});
            skLineSegment(sketch, "E10549", {"start": v(24.26, 2.35) * mm, "end": v(24.24, 2.35) * mm});
            skLineSegment(sketch, "E10550", {"start": v(24.24, 2.35) * mm, "end": v(24.22, 2.35) * mm});
            skLineSegment(sketch, "E10551", {"start": v(24.22, 2.35) * mm, "end": v(24.2, 2.34) * mm});
            skLineSegment(sketch, "E10552", {"start": v(24.2, 2.34) * mm, "end": v(24.17, 2.33) * mm});
            skLineSegment(sketch, "E10553", {"start": v(24.17, 2.33) * mm, "end": v(24.15, 2.32) * mm});
            skLineSegment(sketch, "E10554", {"start": v(24.15, 2.32) * mm, "end": v(24.13, 2.3) * mm});
            skLineSegment(sketch, "E10555", {"start": v(24.13, 2.3) * mm, "end": v(24.1, 2.28) * mm});
            skLineSegment(sketch, "E10556", {"start": v(24.1, 2.28) * mm, "end": v(24.09, 2.26) * mm});
            skLineSegment(sketch, "E10557", {"start": v(24.09, 2.26) * mm, "end": v(24.07, 2.24) * mm});
            skLineSegment(sketch, "E10558", {"start": v(24.07, 2.24) * mm, "end": v(24.03, 2.17) * mm});
            skLineSegment(sketch, "E10559", {"start": v(24.03, 2.17) * mm, "end": v(23.99, 2.1) * mm});
            skLineSegment(sketch, "E10560", {"start": v(23.99, 2.1) * mm, "end": v(23.95, 2.03) * mm});
            skLineSegment(sketch, "E10561", {"start": v(23.95, 2.03) * mm, "end": v(23.91, 1.96) * mm});
            skLineSegment(sketch, "E10562", {"start": v(23.91, 1.96) * mm, "end": v(23.87, 1.9) * mm});
            skLineSegment(sketch, "E10563", {"start": v(23.87, 1.9) * mm, "end": v(23.84, 1.83) * mm});
            skLineSegment(sketch, "E10564", {"start": v(23.84, 1.83) * mm, "end": v(23.8, 1.77) * mm});
            skLineSegment(sketch, "E10565", {"start": v(23.8, 1.77) * mm, "end": v(23.77, 1.7) * mm});
            skLineSegment(sketch, "E10566", {"start": v(23.77, 1.7) * mm, "end": v(23.76, 1.68) * mm});
            skLineSegment(sketch, "E10567", {"start": v(23.76, 1.68) * mm, "end": v(23.74, 1.65) * mm});
            skLineSegment(sketch, "E10568", {"start": v(23.74, 1.65) * mm, "end": v(23.73, 1.61) * mm});
            skLineSegment(sketch, "E10569", {"start": v(23.73, 1.61) * mm, "end": v(23.71, 1.58) * mm});
            skLineSegment(sketch, "E10570", {"start": v(23.71, 1.58) * mm, "end": v(23.7, 1.55) * mm});
            skLineSegment(sketch, "E10571", {"start": v(23.7, 1.55) * mm, "end": v(23.69, 1.52) * mm});
            skLineSegment(sketch, "E10572", {"start": v(23.69, 1.52) * mm, "end": v(23.67, 1.49) * mm});
            skLineSegment(sketch, "E10573", {"start": v(23.67, 1.49) * mm, "end": v(23.66, 1.46) * mm});
            skLineSegment(sketch, "E10574", {"start": v(23.66, 1.46) * mm, "end": v(23.64, 1.4) * mm});
            skLineSegment(sketch, "E10575", {"start": v(23.64, 1.4) * mm, "end": v(23.61, 1.36) * mm});
            skLineSegment(sketch, "E10576", {"start": v(23.61, 1.36) * mm, "end": v(23.6, 1.31) * mm});
            skLineSegment(sketch, "E10577", {"start": v(23.6, 1.31) * mm, "end": v(23.57, 1.27) * mm});
            skLineSegment(sketch, "E10578", {"start": v(23.57, 1.27) * mm, "end": v(23.55, 1.22) * mm});
            skLineSegment(sketch, "E10579", {"start": v(23.55, 1.22) * mm, "end": v(23.52, 1.18) * mm});
            skLineSegment(sketch, "E10580", {"start": v(23.52, 1.18) * mm, "end": v(23.5, 1.13) * mm});
            skLineSegment(sketch, "E10581", {"start": v(23.5, 1.13) * mm, "end": v(23.47, 1.09) * mm});
            skLineSegment(sketch, "E10582", {"start": v(23.47, 1.09) * mm, "end": v(23.43, 1.02) * mm});
            skLineSegment(sketch, "E10583", {"start": v(23.43, 1.02) * mm, "end": v(23.4, 0.96) * mm});
            skLineSegment(sketch, "E10584", {"start": v(23.4, 0.96) * mm, "end": v(23.37, 0.92) * mm});
            skLineSegment(sketch, "E10585", {"start": v(23.37, 0.92) * mm, "end": v(23.35, 0.9) * mm});
            skLineSegment(sketch, "E10586", {"start": v(23.35, 0.9) * mm, "end": v(23.34, 0.88) * mm});
            skLineSegment(sketch, "E10587", {"start": v(23.34, 0.88) * mm, "end": v(23.34, 0.87) * mm});
            skLineSegment(sketch, "E10588", {"start": v(23.34, 0.87) * mm, "end": v(23.33, 0.87) * mm});
            skLineSegment(sketch, "E10589", {"start": v(23.33, 0.87) * mm, "end": v(23.33, 0.87) * mm});
            skLineSegment(sketch, "E10590", {"start": v(23.33, 0.87) * mm, "end": v(23.31, 0.75) * mm});
            skLineSegment(sketch, "E10591", {"start": v(23.31, 0.75) * mm, "end": v(23.3, 0.65) * mm});
            skLineSegment(sketch, "E10592", {"start": v(23.3, 0.65) * mm, "end": v(23.28, 0.55) * mm});
            skLineSegment(sketch, "E10593", {"start": v(23.28, 0.55) * mm, "end": v(23.26, 0.46) * mm});
            skLineSegment(sketch, "E10594", {"start": v(23.26, 0.46) * mm, "end": v(23.25, 0.39) * mm});
            skLineSegment(sketch, "E10595", {"start": v(23.25, 0.39) * mm, "end": v(23.24, 0.33) * mm});
            skLineSegment(sketch, "E10596", {"start": v(23.24, 0.33) * mm, "end": v(23.23, 0.3) * mm});
            skLineSegment(sketch, "E10597", {"start": v(23.23, 0.3) * mm, "end": v(23.23, 0.28) * mm});
            skLineSegment(sketch, "E10598", {"start": v(23.23, 0.28) * mm, "end": v(23.23, 0.28) * mm});
            skLineSegment(sketch, "E10599", {"start": v(23.23, 0.28) * mm, "end": v(23.23, 0.27) * mm});
            skLineSegment(sketch, "E10600", {"start": v(23.23, 0.27) * mm, "end": v(23.23, 0.25) * mm});
            skLineSegment(sketch, "E10601", {"start": v(23.23, 0.25) * mm, "end": v(23.22, 0.24) * mm});
            skLineSegment(sketch, "E10602", {"start": v(23.22, 0.24) * mm, "end": v(23.22, 0.22) * mm});
            skLineSegment(sketch, "E10603", {"start": v(23.22, 0.22) * mm, "end": v(23.22, 0.2) * mm});
            skLineSegment(sketch, "E10604", {"start": v(23.22, 0.2) * mm, "end": v(23.22, 0.18) * mm});
            skLineSegment(sketch, "E10605", {"start": v(23.22, 0.18) * mm, "end": v(23.21, 0.16) * mm});
            skLineSegment(sketch, "E10606", {"start": v(23.21, 0.16) * mm, "end": v(23.21, 0.16) * mm});
            skLineSegment(sketch, "E10607", {"start": v(23.21, 0.16) * mm, "end": v(23.22, 0.16) * mm});
            skLineSegment(sketch, "E10608", {"start": v(23.22, 0.16) * mm, "end": v(23.22, 0.15) * mm});
            skLineSegment(sketch, "E10609", {"start": v(23.22, 0.15) * mm, "end": v(23.22, 0.15) * mm});
            skLineSegment(sketch, "E10610", {"start": v(23.22, 0.15) * mm, "end": v(23.22, 0.14) * mm});
            skLineSegment(sketch, "E10611", {"start": v(23.22, 0.14) * mm, "end": v(23.23, 0.12) * mm});
            skLineSegment(sketch, "E10612", {"start": v(23.23, 0.12) * mm, "end": v(23.24, 0.1) * mm});
            skLineSegment(sketch, "E10613", {"start": v(23.24, 0.1) * mm, "end": v(23.27, 0.04) * mm});
            skLineSegment(sketch, "E10614", {"start": v(23.27, 0.04) * mm, "end": v(23.3, -0.02) * mm});
            skLineSegment(sketch, "E10615", {"start": v(23.3, -0.02) * mm, "end": v(23.32, -0.08) * mm});
            skLineSegment(sketch, "E10616", {"start": v(23.32, -0.08) * mm, "end": v(23.35, -0.15) * mm});
            skLineSegment(sketch, "E10617", {"start": v(23.35, -0.15) * mm, "end": v(23.38, -0.2) * mm});
            skLineSegment(sketch, "E10618", {"start": v(23.38, -0.2) * mm, "end": v(23.41, -0.27) * mm});
            skLineSegment(sketch, "E10619", {"start": v(23.41, -0.27) * mm, "end": v(23.44, -0.33) * mm});
            skLineSegment(sketch, "E10620", {"start": v(23.44, -0.33) * mm, "end": v(23.47, -0.4) * mm});
            skLineSegment(sketch, "E10621", {"start": v(23.47, -0.4) * mm, "end": v(23.49, -0.42) * mm});
            skLineSegment(sketch, "E10622", {"start": v(23.49, -0.42) * mm, "end": v(23.5, -0.45) * mm});
            skLineSegment(sketch, "E10623", {"start": v(23.5, -0.45) * mm, "end": v(23.52, -0.47) * mm});
            skLineSegment(sketch, "E10624", {"start": v(23.52, -0.47) * mm, "end": v(23.53, -0.5) * mm});
            skLineSegment(sketch, "E10625", {"start": v(23.53, -0.5) * mm, "end": v(23.55, -0.52) * mm});
            skLineSegment(sketch, "E10626", {"start": v(23.55, -0.52) * mm, "end": v(23.56, -0.55) * mm});
            skLineSegment(sketch, "E10627", {"start": v(23.56, -0.55) * mm, "end": v(23.58, -0.57) * mm});
            skLineSegment(sketch, "E10628", {"start": v(23.58, -0.57) * mm, "end": v(23.6, -0.6) * mm});
            skLineSegment(sketch, "E10629", {"start": v(23.6, -0.6) * mm, "end": v(23.6, -0.61) * mm});
            skLineSegment(sketch, "E10630", {"start": v(23.6, -0.61) * mm, "end": v(23.61, -0.63) * mm});
            skLineSegment(sketch, "E10631", {"start": v(23.61, -0.63) * mm, "end": v(23.62, -0.64) * mm});
            skLineSegment(sketch, "E10632", {"start": v(23.62, -0.64) * mm, "end": v(23.63, -0.65) * mm});
            skLineSegment(sketch, "E10633", {"start": v(23.63, -0.65) * mm, "end": v(23.64, -0.67) * mm});
            skLineSegment(sketch, "E10634", {"start": v(23.64, -0.67) * mm, "end": v(23.64, -0.68) * mm});
            skLineSegment(sketch, "E10635", {"start": v(23.64, -0.68) * mm, "end": v(23.65, -0.7) * mm});
            skLineSegment(sketch, "E10636", {"start": v(23.65, -0.7) * mm, "end": v(23.66, -0.7) * mm});
            skLineSegment(sketch, "E10637", {"start": v(23.66, -0.7) * mm, "end": v(23.7, -0.77) * mm});
            skLineSegment(sketch, "E10638", {"start": v(23.7, -0.77) * mm, "end": v(23.72, -0.81) * mm});
            skLineSegment(sketch, "E10639", {"start": v(23.72, -0.81) * mm, "end": v(23.74, -0.84) * mm});
            skLineSegment(sketch, "E10640", {"start": v(23.74, -0.84) * mm, "end": v(23.75, -0.86) * mm});
            skLineSegment(sketch, "E10641", {"start": v(23.75, -0.86) * mm, "end": v(23.76, -0.88) * mm});
            skLineSegment(sketch, "E10642", {"start": v(23.76, -0.88) * mm, "end": v(23.77, -0.88) * mm});
            skLineSegment(sketch, "E10643", {"start": v(23.77, -0.88) * mm, "end": v(23.77, -0.89) * mm});
            skLineSegment(sketch, "E10644", {"start": v(23.77, -0.89) * mm, "end": v(23.77, -0.89) * mm});
            skLineSegment(sketch, "E10645", {"start": v(23.77, -0.89) * mm, "end": v(23.81, -0.96) * mm});
            skLineSegment(sketch, "E10646", {"start": v(23.81, -0.96) * mm, "end": v(23.86, -1.04) * mm});
            skLineSegment(sketch, "E10647", {"start": v(23.86, -1.04) * mm, "end": v(23.9, -1.12) * mm});
            skLineSegment(sketch, "E10648", {"start": v(23.9, -1.12) * mm, "end": v(23.95, -1.2) * mm});
            skLineSegment(sketch, "E10649", {"start": v(23.95, -1.2) * mm, "end": v(23.99, -1.27) * mm});
            skLineSegment(sketch, "E10650", {"start": v(23.99, -1.27) * mm, "end": v(24.03, -1.33) * mm});
            skLineSegment(sketch, "E10651", {"start": v(24.03, -1.33) * mm, "end": v(24.06, -1.38) * mm});
            skLineSegment(sketch, "E10652", {"start": v(24.06, -1.38) * mm, "end": v(24.08, -1.42) * mm});
            skLineSegment(sketch, "E10653", {"start": v(24.08, -1.42) * mm, "end": v(24.1, -1.46) * mm});
            skLineSegment(sketch, "E10654", {"start": v(24.1, -1.46) * mm, "end": v(24.12, -1.49) * mm});
            skLineSegment(sketch, "E10655", {"start": v(24.12, -1.49) * mm, "end": v(24.14, -1.51) * mm});
            skLineSegment(sketch, "E10656", {"start": v(24.14, -1.51) * mm, "end": v(24.16, -1.53) * mm});
            skLineSegment(sketch, "E10657", {"start": v(24.16, -1.53) * mm, "end": v(24.18, -1.54) * mm});
            skLineSegment(sketch, "E10658", {"start": v(24.18, -1.54) * mm, "end": v(24.2, -1.55) * mm});
            skLineSegment(sketch, "E10659", {"start": v(24.2, -1.55) * mm, "end": v(24.21, -1.55) * mm});
            skLineSegment(sketch, "E10660", {"start": v(24.21, -1.55) * mm, "end": v(24.23, -1.55) * mm});
            skLineSegment(sketch, "E10661", {"start": v(24.23, -1.55) * mm, "end": v(24.24, -1.54) * mm});
            skLineSegment(sketch, "E10662", {"start": v(24.24, -1.54) * mm, "end": v(24.25, -1.52) * mm});
            skLineSegment(sketch, "E10663", {"start": v(24.25, -1.52) * mm, "end": v(24.26, -1.51) * mm});
            skLineSegment(sketch, "E10664", {"start": v(24.26, -1.51) * mm, "end": v(24.27, -1.5) * mm});
            skLineSegment(sketch, "E10665", {"start": v(24.27, -1.5) * mm, "end": v(24.28, -1.49) * mm});
            skLineSegment(sketch, "E10666", {"start": v(24.28, -1.49) * mm, "end": v(24.3, -1.47) * mm});
            skLineSegment(sketch, "E10667", {"start": v(24.3, -1.47) * mm, "end": v(24.3, -1.46) * mm});
            skLineSegment(sketch, "E10668", {"start": v(24.3, -1.46) * mm, "end": v(24.32, -1.45) * mm});
            skLineSegment(sketch, "E10669", {"start": v(24.32, -1.45) * mm, "end": v(24.32, -1.45) * mm});
            skLineSegment(sketch, "E10670", {"start": v(24.32, -1.45) * mm, "end": v(24.32, -1.44) * mm});
            skLineSegment(sketch, "E10671", {"start": v(24.32, -1.44) * mm, "end": v(24.33, -1.44) * mm});
            skLineSegment(sketch, "E10672", {"start": v(24.33, -1.44) * mm, "end": v(24.33, -1.43) * mm});
            skLineSegment(sketch, "E10673", {"start": v(24.33, -1.43) * mm, "end": v(24.34, -1.43) * mm});
            skLineSegment(sketch, "E10674", {"start": v(24.34, -1.43) * mm, "end": v(24.36, -1.41) * mm});
            skLineSegment(sketch, "E10675", {"start": v(24.36, -1.41) * mm, "end": v(24.37, -1.4) * mm});
            skLineSegment(sketch, "E10676", {"start": v(24.37, -1.4) * mm, "end": v(24.39, -1.38) * mm});
            skLineSegment(sketch, "E10677", {"start": v(24.39, -1.38) * mm, "end": v(24.4, -1.36) * mm});
            skLineSegment(sketch, "E10678", {"start": v(24.4, -1.36) * mm, "end": v(24.42, -1.35) * mm});
            skLineSegment(sketch, "E10679", {"start": v(24.42, -1.35) * mm, "end": v(24.43, -1.33) * mm});
            skLineSegment(sketch, "E10680", {"start": v(24.43, -1.33) * mm, "end": v(24.44, -1.32) * mm});
            skLineSegment(sketch, "E10681", {"start": v(24.44, -1.32) * mm, "end": v(24.46, -1.3) * mm});
            skLineSegment(sketch, "E10682", {"start": v(24.46, -1.3) * mm, "end": v(24.47, -1.28) * mm});
            skLineSegment(sketch, "E10683", {"start": v(24.47, -1.28) * mm, "end": v(24.48, -1.26) * mm});
            skLineSegment(sketch, "E10684", {"start": v(24.48, -1.26) * mm, "end": v(24.5, -1.24) * mm});
            skLineSegment(sketch, "E10685", {"start": v(24.5, -1.24) * mm, "end": v(24.5, -1.22) * mm});
            skLineSegment(sketch, "E10686", {"start": v(24.5, -1.22) * mm, "end": v(24.52, -1.2) * mm});
            skLineSegment(sketch, "E10687", {"start": v(24.52, -1.2) * mm, "end": v(24.53, -1.18) * mm});
            skLineSegment(sketch, "E10688", {"start": v(24.53, -1.18) * mm, "end": v(24.54, -1.16) * mm});
            skLineSegment(sketch, "E10689", {"start": v(24.54, -1.16) * mm, "end": v(24.56, -1.14) * mm});
            skLineSegment(sketch, "E10690", {"start": v(24.56, -1.14) * mm, "end": v(24.57, -1.12) * mm});
            skLineSegment(sketch, "E10691", {"start": v(24.57, -1.12) * mm, "end": v(24.59, -1.09) * mm});
            skLineSegment(sketch, "E10692", {"start": v(24.59, -1.09) * mm, "end": v(24.6, -1.06) * mm});
            skLineSegment(sketch, "E10693", {"start": v(24.6, -1.06) * mm, "end": v(24.62, -1.04) * mm});
            skLineSegment(sketch, "E10694", {"start": v(24.62, -1.04) * mm, "end": v(24.64, -1.01) * mm});
            skLineSegment(sketch, "E10695", {"start": v(24.64, -1.01) * mm, "end": v(24.65, -0.99) * mm});
            skLineSegment(sketch, "E10696", {"start": v(24.65, -0.99) * mm, "end": v(24.67, -0.97) * mm});
            skLineSegment(sketch, "E10697", {"start": v(24.67, -0.97) * mm, "end": v(24.69, -0.94) * mm});
            skLineSegment(sketch, "E10698", {"start": v(24.69, -0.94) * mm, "end": v(24.8, -0.8) * mm});
            skLineSegment(sketch, "E10699", {"start": v(24.8, -0.8) * mm, "end": v(24.89, -0.66) * mm});
            skLineSegment(sketch, "E10700", {"start": v(24.89, -0.66) * mm, "end": v(24.96, -0.53) * mm});
            skLineSegment(sketch, "E10701", {"start": v(24.96, -0.53) * mm, "end": v(25.03, -0.39) * mm});
            skLineSegment(sketch, "E10702", {"start": v(25.03, -0.39) * mm, "end": v(25.08, -0.25) * mm});
            skLineSegment(sketch, "E10703", {"start": v(25.08, -0.25) * mm, "end": v(25.11, -0.1) * mm});
            skLineSegment(sketch, "E10704", {"start": v(25.11, -0.1) * mm, "end": v(25.14, 0.04) * mm});
            skLineSegment(sketch, "E10705", {"start": v(25.14, 0.04) * mm, "end": v(25.14, 0.18) * mm});
            skLineSegment(sketch, "E10706", {"start": v(25.14, 0.18) * mm, "end": v(25.14, 0.24) * mm});
            skLineSegment(sketch, "E10707", {"start": v(25.14, 0.24) * mm, "end": v(25.15, 0.28) * mm});
            skLineSegment(sketch, "E10708", {"start": v(25.15, 0.28) * mm, "end": v(25.15, 0.32) * mm});
            skLineSegment(sketch, "E10709", {"start": v(25.15, 0.32) * mm, "end": v(25.15, 0.34) * mm});
            skLineSegment(sketch, "E10710", {"start": v(25.15, 0.34) * mm, "end": v(25.15, 0.35) * mm});
            skLineSegment(sketch, "E10711", {"start": v(25.15, 0.35) * mm, "end": v(25.15, 0.36) * mm});
            skLineSegment(sketch, "E10712", {"start": v(25.15, 0.36) * mm, "end": v(25.15, 0.36) * mm});
            skLineSegment(sketch, "E10713", {"start": v(25.15, 0.36) * mm, "end": v(25.14, 0.43) * mm});
            skLineSegment(sketch, "E10714", {"start": v(25.14, 0.43) * mm, "end": v(25.13, 0.5) * mm});
            skLineSegment(sketch, "E10715", {"start": v(25.13, 0.5) * mm, "end": v(25.12, 0.57) * mm});
            skLineSegment(sketch, "E10716", {"start": v(25.12, 0.57) * mm, "end": v(25.12, 0.63) * mm});
            skLineSegment(sketch, "E10717", {"start": v(25.12, 0.63) * mm, "end": v(25.11, 0.69) * mm});
            skLineSegment(sketch, "E10718", {"start": v(25.11, 0.69) * mm, "end": v(25.1, 0.74) * mm});
            skLineSegment(sketch, "E10719", {"start": v(25.1, 0.74) * mm, "end": v(25.1, 0.77) * mm});
            skLineSegment(sketch, "E10720", {"start": v(25.1, 0.77) * mm, "end": v(25.1, 0.8) * mm});
            skLineSegment(sketch, "E10721", {"start": v(25.1, 0.8) * mm, "end": v(25.1, 0.81) * mm});
            skLineSegment(sketch, "E10722", {"start": v(25.1, 0.81) * mm, "end": v(25.1, 0.83) * mm});
            skLineSegment(sketch, "E10723", {"start": v(25.1, 0.83) * mm, "end": v(25.1, 0.85) * mm});
            skLineSegment(sketch, "E10724", {"start": v(25.1, 0.85) * mm, "end": v(25.1, 0.87) * mm});
            skLineSegment(sketch, "E10725", {"start": v(25.1, 0.87) * mm, "end": v(25.1, 0.89) * mm});
            skLineSegment(sketch, "E10726", {"start": v(25.1, 0.89) * mm, "end": v(25.1, 0.9) * mm});
            skLineSegment(sketch, "E10727", {"start": v(25.1, 0.9) * mm, "end": v(25.1, 0.93) * mm});
            skLineSegment(sketch, "E10728", {"start": v(25.1, 0.93) * mm, "end": v(25.09, 0.94) * mm});
            skLineSegment(sketch, "E10729", {"start": v(25.09, 0.94) * mm, "end": v(25.09, 0.94) * mm});
            skLineSegment(sketch, "E10730", {"start": v(25.09, 0.94) * mm, "end": v(25.09, 0.95) * mm});
            skLineSegment(sketch, "E10731", {"start": v(25.09, 0.95) * mm, "end": v(25.09, 0.95) * mm});
            skLineSegment(sketch, "E10732", {"start": v(24.59, 0.35) * mm, "end": v(24.59, 0.32) * mm});
            skLineSegment(sketch, "E10733", {"start": v(24.59, 0.32) * mm, "end": v(24.58, 0.28) * mm});
            skLineSegment(sketch, "E10734", {"start": v(24.58, 0.28) * mm, "end": v(24.58, 0.25) * mm});
            skLineSegment(sketch, "E10735", {"start": v(24.58, 0.25) * mm, "end": v(24.58, 0.25) * mm});
            skLineSegment(sketch, "E10736", {"start": v(24.58, 0.25) * mm, "end": v(24.58, 0.24) * mm});
            skLineSegment(sketch, "E10737", {"start": v(24.58, 0.24) * mm, "end": v(24.57, 0.24) * mm});
            skLineSegment(sketch, "E10738", {"start": v(24.57, 0.24) * mm, "end": v(24.57, 0.22) * mm});
            skLineSegment(sketch, "E10739", {"start": v(24.57, 0.22) * mm, "end": v(24.57, 0.2) * mm});
            skLineSegment(sketch, "E10740", {"start": v(24.57, 0.2) * mm, "end": v(24.56, 0.19) * mm});
            skLineSegment(sketch, "E10741", {"start": v(24.56, 0.19) * mm, "end": v(24.54, 0.09) * mm});
            skLineSegment(sketch, "E10742", {"start": v(24.54, 0.09) * mm, "end": v(24.52, -0.01) * mm});
            skLineSegment(sketch, "E10743", {"start": v(24.52, -0.01) * mm, "end": v(24.5, -0.1) * mm});
            skLineSegment(sketch, "E10744", {"start": v(24.5, -0.1) * mm, "end": v(24.47, -0.2) * mm});
            skLineSegment(sketch, "E10745", {"start": v(24.47, -0.2) * mm, "end": v(24.43, -0.3) * mm});
            skLineSegment(sketch, "E10746", {"start": v(24.43, -0.3) * mm, "end": v(24.39, -0.38) * mm});
            skLineSegment(sketch, "E10747", {"start": v(24.39, -0.38) * mm, "end": v(24.34, -0.46) * mm});
            skLineSegment(sketch, "E10748", {"start": v(24.34, -0.46) * mm, "end": v(24.28, -0.54) * mm});
            skLineSegment(sketch, "E10749", {"start": v(24.28, -0.54) * mm, "end": v(24.27, -0.55) * mm});
            skLineSegment(sketch, "E10750", {"start": v(24.27, -0.55) * mm, "end": v(24.27, -0.55) * mm});
            skLineSegment(sketch, "E10751", {"start": v(24.27, -0.55) * mm, "end": v(24.26, -0.56) * mm});
            skLineSegment(sketch, "E10752", {"start": v(24.26, -0.56) * mm, "end": v(24.25, -0.56) * mm});
            skLineSegment(sketch, "E10753", {"start": v(24.25, -0.56) * mm, "end": v(24.24, -0.57) * mm});
            skLineSegment(sketch, "E10754", {"start": v(24.24, -0.57) * mm, "end": v(24.22, -0.57) * mm});
            skLineSegment(sketch, "E10755", {"start": v(24.22, -0.57) * mm, "end": v(24.2, -0.57) * mm});
            skLineSegment(sketch, "E10756", {"start": v(24.2, -0.57) * mm, "end": v(24.2, -0.57) * mm});
            skLineSegment(sketch, "E10757", {"start": v(24.2, -0.57) * mm, "end": v(24.17, -0.57) * mm});
            skLineSegment(sketch, "E10758", {"start": v(24.17, -0.57) * mm, "end": v(24.15, -0.57) * mm});
            skLineSegment(sketch, "E10759", {"start": v(24.15, -0.57) * mm, "end": v(24.13, -0.56) * mm});
            skLineSegment(sketch, "E10760", {"start": v(24.13, -0.56) * mm, "end": v(24.12, -0.56) * mm});
            skLineSegment(sketch, "E10761", {"start": v(24.12, -0.56) * mm, "end": v(24.1, -0.55) * mm});
            skLineSegment(sketch, "E10762", {"start": v(24.1, -0.55) * mm, "end": v(24.1, -0.54) * mm});
            skLineSegment(sketch, "E10763", {"start": v(24.1, -0.54) * mm, "end": v(24.08, -0.54) * mm});
            skLineSegment(sketch, "E10764", {"start": v(24.08, -0.54) * mm, "end": v(24.07, -0.53) * mm});
            skLineSegment(sketch, "E10765", {"start": v(24.07, -0.53) * mm, "end": v(23.97, -0.37) * mm});
            skLineSegment(sketch, "E10766", {"start": v(23.97, -0.37) * mm, "end": v(23.9, -0.2) * mm});
            skLineSegment(sketch, "E10767", {"start": v(23.9, -0.2) * mm, "end": v(23.84, -0.04) * mm});
            skLineSegment(sketch, "E10768", {"start": v(23.84, -0.04) * mm, "end": v(23.8, 0.13) * mm});
            skLineSegment(sketch, "E10769", {"start": v(23.8, 0.13) * mm, "end": v(23.79, 0.3) * mm});
            skLineSegment(sketch, "E10770", {"start": v(23.79, 0.3) * mm, "end": v(23.8, 0.48) * mm});
            skLineSegment(sketch, "E10771", {"start": v(23.8, 0.48) * mm, "end": v(23.82, 0.66) * mm});
            skLineSegment(sketch, "E10772", {"start": v(23.82, 0.66) * mm, "end": v(23.88, 0.85) * mm});
            skLineSegment(sketch, "E10773", {"start": v(23.88, 0.85) * mm, "end": v(23.88, 0.86) * mm});
            skLineSegment(sketch, "E10774", {"start": v(23.88, 0.86) * mm, "end": v(23.89, 0.88) * mm});
            skLineSegment(sketch, "E10775", {"start": v(23.89, 0.88) * mm, "end": v(23.9, 0.9) * mm});
            skLineSegment(sketch, "E10776", {"start": v(23.9, 0.9) * mm, "end": v(23.9, 0.91) * mm});
            skLineSegment(sketch, "E10777", {"start": v(23.9, 0.91) * mm, "end": v(23.9, 0.93) * mm});
            skLineSegment(sketch, "E10778", {"start": v(23.9, 0.93) * mm, "end": v(23.9, 0.94) * mm});
            skLineSegment(sketch, "E10779", {"start": v(23.9, 0.94) * mm, "end": v(23.9, 0.96) * mm});
            skLineSegment(sketch, "E10780", {"start": v(23.9, 0.96) * mm, "end": v(23.91, 0.97) * mm});
            skLineSegment(sketch, "E10781", {"start": v(23.91, 0.97) * mm, "end": v(23.92, 1) * mm});
            skLineSegment(sketch, "E10782", {"start": v(23.92, 1) * mm, "end": v(23.93, 1.02) * mm});
            skLineSegment(sketch, "E10783", {"start": v(23.93, 1.02) * mm, "end": v(23.93, 1.04) * mm});
            skLineSegment(sketch, "E10784", {"start": v(23.93, 1.04) * mm, "end": v(23.94, 1.07) * mm});
            skLineSegment(sketch, "E10785", {"start": v(23.94, 1.07) * mm, "end": v(23.95, 1.09) * mm});
            skLineSegment(sketch, "E10786", {"start": v(23.95, 1.09) * mm, "end": v(23.96, 1.11) * mm});
            skLineSegment(sketch, "E10787", {"start": v(23.96, 1.11) * mm, "end": v(23.97, 1.14) * mm});
            skLineSegment(sketch, "E10788", {"start": v(23.97, 1.14) * mm, "end": v(23.97, 1.16) * mm});
            skLineSegment(sketch, "E10789", {"start": v(23.97, 1.16) * mm, "end": v(23.98, 1.17) * mm});
            skLineSegment(sketch, "E10790", {"start": v(23.98, 1.17) * mm, "end": v(23.98, 1.18) * mm});
            skLineSegment(sketch, "E10791", {"start": v(23.98, 1.18) * mm, "end": v(23.99, 1.2) * mm});
            skLineSegment(sketch, "E10792", {"start": v(23.99, 1.2) * mm, "end": v(23.99, 1.2) * mm});
            skLineSegment(sketch, "E10793", {"start": v(23.99, 1.2) * mm, "end": v(24, 1.22) * mm});
            skLineSegment(sketch, "E10794", {"start": v(24, 1.22) * mm, "end": v(24, 1.23) * mm});
            skLineSegment(sketch, "E10795", {"start": v(24, 1.23) * mm, "end": v(24, 1.24) * mm});
            skLineSegment(sketch, "E10796", {"start": v(24, 1.24) * mm, "end": v(24, 1.26) * mm});
            skLineSegment(sketch, "E10797", {"start": v(24, 1.26) * mm, "end": v(24, 1.26) * mm});
            skLineSegment(sketch, "E10798", {"start": v(24, 1.26) * mm, "end": v(24, 1.27) * mm});
            skLineSegment(sketch, "E10799", {"start": v(24, 1.27) * mm, "end": v(24, 1.27) * mm});
            skLineSegment(sketch, "E10800", {"start": v(24, 1.27) * mm, "end": v(24, 1.28) * mm});
            skLineSegment(sketch, "E10801", {"start": v(24, 1.28) * mm, "end": v(24, 1.29) * mm});
            skLineSegment(sketch, "E10802", {"start": v(24, 1.29) * mm, "end": v(24, 1.3) * mm});
            skLineSegment(sketch, "E10803", {"start": v(24, 1.3) * mm, "end": v(24, 1.3) * mm});
            skLineSegment(sketch, "E10804", {"start": v(24, 1.3) * mm, "end": v(24.01, 1.3) * mm});
            skLineSegment(sketch, "E10805", {"start": v(24.01, 1.3) * mm, "end": v(24.01, 1.3) * mm});
            skLineSegment(sketch, "E10806", {"start": v(24.01, 1.3) * mm, "end": v(24.02, 1.3) * mm});
            skLineSegment(sketch, "E10807", {"start": v(24.02, 1.3) * mm, "end": v(24.02, 1.3) * mm});
            skLineSegment(sketch, "E10808", {"start": v(24.02, 1.3) * mm, "end": v(24.03, 1.3) * mm});
            skLineSegment(sketch, "E10809", {"start": v(24.03, 1.3) * mm, "end": v(24.04, 1.3) * mm});
            skLineSegment(sketch, "E10810", {"start": v(24.04, 1.3) * mm, "end": v(24.04, 1.3) * mm});
            skLineSegment(sketch, "E10811", {"start": v(24.04, 1.3) * mm, "end": v(24.05, 1.3) * mm});
            skLineSegment(sketch, "E10812", {"start": v(24.05, 1.3) * mm, "end": v(24.06, 1.29) * mm});
            skLineSegment(sketch, "E10813", {"start": v(24.06, 1.29) * mm, "end": v(24.06, 1.29) * mm});
            skLineSegment(sketch, "E10814", {"start": v(24.06, 1.29) * mm, "end": v(24.07, 1.28) * mm});
            skLineSegment(sketch, "E10815", {"start": v(24.07, 1.28) * mm, "end": v(24.07, 1.28) * mm});
            skLineSegment(sketch, "E10816", {"start": v(24.07, 1.28) * mm, "end": v(24.08, 1.28) * mm});
            skLineSegment(sketch, "E10817", {"start": v(24.08, 1.28) * mm, "end": v(24.08, 1.28) * mm});
            skLineSegment(sketch, "E10818", {"start": v(24.08, 1.28) * mm, "end": v(24.09, 1.28) * mm});
            skLineSegment(sketch, "E10819", {"start": v(24.09, 1.28) * mm, "end": v(24.09, 1.28) * mm});
            skLineSegment(sketch, "E10820", {"start": v(24.09, 1.28) * mm, "end": v(24.1, 1.28) * mm});
            skLineSegment(sketch, "E10821", {"start": v(24.1, 1.28) * mm, "end": v(24.1, 1.28) * mm});
            skLineSegment(sketch, "E10822", {"start": v(24.1, 1.28) * mm, "end": v(24.11, 1.28) * mm});
            skLineSegment(sketch, "E10823", {"start": v(24.11, 1.28) * mm, "end": v(24.12, 1.29) * mm});
            skLineSegment(sketch, "E10824", {"start": v(24.12, 1.29) * mm, "end": v(24.13, 1.29) * mm});
            skLineSegment(sketch, "E10825", {"start": v(24.13, 1.29) * mm, "end": v(24.13, 1.29) * mm});
            skLineSegment(sketch, "E10826", {"start": v(24.13, 1.29) * mm, "end": v(24.14, 1.3) * mm});
            skLineSegment(sketch, "E10827", {"start": v(24.14, 1.3) * mm, "end": v(24.16, 1.3) * mm});
            skLineSegment(sketch, "E10828", {"start": v(24.16, 1.3) * mm, "end": v(24.18, 1.31) * mm});
            skLineSegment(sketch, "E10829", {"start": v(24.18, 1.31) * mm, "end": v(24.2, 1.32) * mm});
            skLineSegment(sketch, "E10830", {"start": v(24.2, 1.32) * mm, "end": v(24.22, 1.33) * mm});
            skLineSegment(sketch, "E10831", {"start": v(24.22, 1.33) * mm, "end": v(24.25, 1.35) * mm});
            skLineSegment(sketch, "E10832", {"start": v(24.25, 1.35) * mm, "end": v(24.28, 1.36) * mm});
            skLineSegment(sketch, "E10833", {"start": v(24.28, 1.36) * mm, "end": v(24.3, 1.37) * mm});
            skLineSegment(sketch, "E10834", {"start": v(24.3, 1.37) * mm, "end": v(24.3, 1.37) * mm});
            skLineSegment(sketch, "E10835", {"start": v(24.3, 1.37) * mm, "end": v(24.31, 1.37) * mm});
            skLineSegment(sketch, "E10836", {"start": v(24.31, 1.37) * mm, "end": v(24.32, 1.37) * mm});
            skLineSegment(sketch, "E10837", {"start": v(24.32, 1.37) * mm, "end": v(24.33, 1.37) * mm});
            skLineSegment(sketch, "E10838", {"start": v(24.33, 1.37) * mm, "end": v(24.34, 1.37) * mm});
            skLineSegment(sketch, "E10839", {"start": v(24.34, 1.37) * mm, "end": v(24.35, 1.37) * mm});
            skLineSegment(sketch, "E10840", {"start": v(24.35, 1.37) * mm, "end": v(24.36, 1.36) * mm});
            skLineSegment(sketch, "E10841", {"start": v(24.36, 1.36) * mm, "end": v(24.37, 1.35) * mm});
            skLineSegment(sketch, "E10842", {"start": v(24.37, 1.35) * mm, "end": v(24.38, 1.33) * mm});
            skLineSegment(sketch, "E10843", {"start": v(24.38, 1.33) * mm, "end": v(24.39, 1.31) * mm});
            skLineSegment(sketch, "E10844", {"start": v(24.39, 1.31) * mm, "end": v(24.4, 1.29) * mm});
            skLineSegment(sketch, "E10845", {"start": v(24.4, 1.29) * mm, "end": v(24.4, 1.26) * mm});
            skLineSegment(sketch, "E10846", {"start": v(24.4, 1.26) * mm, "end": v(24.42, 1.22) * mm});
            skLineSegment(sketch, "E10847", {"start": v(24.42, 1.22) * mm, "end": v(24.44, 1.15) * mm});
            skLineSegment(sketch, "E10848", {"start": v(24.44, 1.15) * mm, "end": v(24.46, 1.07) * mm});
            skLineSegment(sketch, "E10849", {"start": v(24.46, 1.07) * mm, "end": v(24.48, 1) * mm});
            skLineSegment(sketch, "E10850", {"start": v(24.48, 1) * mm, "end": v(24.5, 0.93) * mm});
            skLineSegment(sketch, "E10851", {"start": v(24.5, 0.93) * mm, "end": v(24.51, 0.85) * mm});
            skLineSegment(sketch, "E10852", {"start": v(24.51, 0.85) * mm, "end": v(24.53, 0.78) * mm});
            skLineSegment(sketch, "E10853", {"start": v(24.53, 0.78) * mm, "end": v(24.54, 0.7) * mm});
            skLineSegment(sketch, "E10854", {"start": v(24.54, 0.7) * mm, "end": v(24.56, 0.63) * mm});
            skLineSegment(sketch, "E10855", {"start": v(24.56, 0.63) * mm, "end": v(24.56, 0.6) * mm});
            skLineSegment(sketch, "E10856", {"start": v(24.56, 0.6) * mm, "end": v(24.57, 0.58) * mm});
            skLineSegment(sketch, "E10857", {"start": v(24.57, 0.58) * mm, "end": v(24.57, 0.57) * mm});
            skLineSegment(sketch, "E10858", {"start": v(24.57, 0.57) * mm, "end": v(24.57, 0.56) * mm});
            skLineSegment(sketch, "E10859", {"start": v(24.57, 0.56) * mm, "end": v(24.57, 0.55) * mm});
            skLineSegment(sketch, "E10860", {"start": v(24.57, 0.55) * mm, "end": v(24.57, 0.55) * mm});
            skLineSegment(sketch, "E10861", {"start": v(24.57, 0.55) * mm, "end": v(24.58, 0.51) * mm});
            skLineSegment(sketch, "E10862", {"start": v(24.58, 0.51) * mm, "end": v(24.58, 0.47) * mm});
            skLineSegment(sketch, "E10863", {"start": v(24.58, 0.47) * mm, "end": v(24.59, 0.43) * mm});
            skLineSegment(sketch, "E10864", {"start": v(24.59, 0.43) * mm, "end": v(24.59, 0.4) * mm});
            skLineSegment(sketch, "E10865", {"start": v(24.59, 0.4) * mm, "end": v(24.59, 0.35) * mm});
            skLineSegment(sketch, "E10866", {"start": v(14.52, 2.7) * mm, "end": v(14.56, 2.69) * mm});
            skLineSegment(sketch, "E10867", {"start": v(14.56, 2.69) * mm, "end": v(14.6, 2.69) * mm});
            skLineSegment(sketch, "E10868", {"start": v(14.6, 2.69) * mm, "end": v(14.66, 2.7) * mm});
            skLineSegment(sketch, "E10869", {"start": v(14.66, 2.7) * mm, "end": v(14.72, 2.7) * mm});
            skLineSegment(sketch, "E10870", {"start": v(14.72, 2.7) * mm, "end": v(14.78, 2.7) * mm});
            skLineSegment(sketch, "E10871", {"start": v(14.78, 2.7) * mm, "end": v(14.85, 2.72) * mm});
            skLineSegment(sketch, "E10872", {"start": v(14.85, 2.72) * mm, "end": v(14.92, 2.73) * mm});
            skLineSegment(sketch, "E10873", {"start": v(14.92, 2.73) * mm, "end": v(14.99, 2.74) * mm});
            skLineSegment(sketch, "E10874", {"start": v(14.99, 2.74) * mm, "end": v(15.06, 2.75) * mm});
            skLineSegment(sketch, "E10875", {"start": v(15.06, 2.75) * mm, "end": v(15.12, 2.76) * mm});
            skLineSegment(sketch, "E10876", {"start": v(15.12, 2.76) * mm, "end": v(15.18, 2.77) * mm});
            skLineSegment(sketch, "E10877", {"start": v(15.18, 2.77) * mm, "end": v(15.23, 2.78) * mm});
            skLineSegment(sketch, "E10878", {"start": v(15.23, 2.78) * mm, "end": v(15.28, 2.79) * mm});
            skLineSegment(sketch, "E10879", {"start": v(15.28, 2.79) * mm, "end": v(15.28, 2.79) * mm});
            skLineSegment(sketch, "E10880", {"start": v(15.28, 2.79) * mm, "end": v(15.29, 2.79) * mm});
            skLineSegment(sketch, "E10881", {"start": v(15.29, 2.79) * mm, "end": v(15.3, 2.79) * mm});
            skLineSegment(sketch, "E10882", {"start": v(15.3, 2.79) * mm, "end": v(15.31, 2.8) * mm});
            skLineSegment(sketch, "E10883", {"start": v(15.31, 2.8) * mm, "end": v(15.33, 2.8) * mm});
            skLineSegment(sketch, "E10884", {"start": v(15.33, 2.8) * mm, "end": v(15.36, 2.8) * mm});
            skLineSegment(sketch, "E10885", {"start": v(15.36, 2.8) * mm, "end": v(15.44, 2.8) * mm});
            skLineSegment(sketch, "E10886", {"start": v(15.44, 2.8) * mm, "end": v(15.52, 2.82) * mm});
            skLineSegment(sketch, "E10887", {"start": v(15.52, 2.82) * mm, "end": v(15.6, 2.83) * mm});
            skLineSegment(sketch, "E10888", {"start": v(15.6, 2.83) * mm, "end": v(15.67, 2.84) * mm});
            skLineSegment(sketch, "E10889", {"start": v(15.67, 2.84) * mm, "end": v(15.75, 2.86) * mm});
            skLineSegment(sketch, "E10890", {"start": v(15.75, 2.86) * mm, "end": v(15.82, 2.87) * mm});
            skLineSegment(sketch, "E10891", {"start": v(15.82, 2.87) * mm, "end": v(15.9, 2.89) * mm});
            skLineSegment(sketch, "E10892", {"start": v(15.9, 2.89) * mm, "end": v(15.98, 2.9) * mm});
            skLineSegment(sketch, "E10893", {"start": v(15.98, 2.9) * mm, "end": v(16.04, 2.92) * mm});
            skLineSegment(sketch, "E10894", {"start": v(16.04, 2.92) * mm, "end": v(16.1, 2.94) * mm});
            skLineSegment(sketch, "E10895", {"start": v(16.1, 2.94) * mm, "end": v(16.18, 2.97) * mm});
            skLineSegment(sketch, "E10896", {"start": v(16.18, 2.97) * mm, "end": v(16.25, 3) * mm});
            skLineSegment(sketch, "E10897", {"start": v(16.25, 3) * mm, "end": v(16.32, 3.04) * mm});
            skLineSegment(sketch, "E10898", {"start": v(16.32, 3.04) * mm, "end": v(16.38, 3.08) * mm});
            skLineSegment(sketch, "E10899", {"start": v(16.38, 3.08) * mm, "end": v(16.45, 3.12) * mm});
            skLineSegment(sketch, "E10900", {"start": v(16.45, 3.12) * mm, "end": v(16.5, 3.18) * mm});
            skLineSegment(sketch, "E10901", {"start": v(16.5, 3.18) * mm, "end": v(16.6, 3.27) * mm});
            skLineSegment(sketch, "E10902", {"start": v(16.6, 3.27) * mm, "end": v(16.69, 3.38) * mm});
            skLineSegment(sketch, "E10903", {"start": v(16.69, 3.38) * mm, "end": v(16.78, 3.48) * mm});
            skLineSegment(sketch, "E10904", {"start": v(16.78, 3.48) * mm, "end": v(16.87, 3.6) * mm});
            skLineSegment(sketch, "E10905", {"start": v(16.87, 3.6) * mm, "end": v(16.96, 3.7) * mm});
            skLineSegment(sketch, "E10906", {"start": v(16.96, 3.7) * mm, "end": v(17.05, 3.82) * mm});
            skLineSegment(sketch, "E10907", {"start": v(17.05, 3.82) * mm, "end": v(17.13, 3.94) * mm});
            skLineSegment(sketch, "E10908", {"start": v(17.13, 3.94) * mm, "end": v(17.21, 4.06) * mm});
            skLineSegment(sketch, "E10909", {"start": v(17.21, 4.06) * mm, "end": v(17.25, 4.1) * mm});
            skLineSegment(sketch, "E10910", {"start": v(17.25, 4.1) * mm, "end": v(17.27, 4.15) * mm});
            skLineSegment(sketch, "E10911", {"start": v(17.27, 4.15) * mm, "end": v(17.3, 4.18) * mm});
            skLineSegment(sketch, "E10912", {"start": v(17.3, 4.18) * mm, "end": v(17.3, 4.2) * mm});
            skLineSegment(sketch, "E10913", {"start": v(17.3, 4.2) * mm, "end": v(17.31, 4.2) * mm});
            skLineSegment(sketch, "E10914", {"start": v(17.31, 4.2) * mm, "end": v(17.32, 4.21) * mm});
            skLineSegment(sketch, "E10915", {"start": v(17.32, 4.21) * mm, "end": v(17.32, 4.21) * mm});
            skLineSegment(sketch, "E10916", {"start": v(17.32, 4.21) * mm, "end": v(17.34, 4.29) * mm});
            skLineSegment(sketch, "E10917", {"start": v(17.34, 4.29) * mm, "end": v(17.37, 4.36) * mm});
            skLineSegment(sketch, "E10918", {"start": v(17.37, 4.36) * mm, "end": v(17.39, 4.43) * mm});
            skLineSegment(sketch, "E10919", {"start": v(17.39, 4.43) * mm, "end": v(17.41, 4.49) * mm});
            skLineSegment(sketch, "E10920", {"start": v(17.41, 4.49) * mm, "end": v(17.43, 4.54) * mm});
            skLineSegment(sketch, "E10921", {"start": v(17.43, 4.54) * mm, "end": v(17.44, 4.58) * mm});
            skLineSegment(sketch, "E10922", {"start": v(17.44, 4.58) * mm, "end": v(17.45, 4.61) * mm});
            skLineSegment(sketch, "E10923", {"start": v(17.45, 4.61) * mm, "end": v(17.46, 4.63) * mm});
            skLineSegment(sketch, "E10924", {"start": v(17.46, 4.63) * mm, "end": v(17.46, 4.65) * mm});
            skLineSegment(sketch, "E10925", {"start": v(17.46, 4.65) * mm, "end": v(17.47, 4.67) * mm});
            skLineSegment(sketch, "E10926", {"start": v(17.47, 4.67) * mm, "end": v(17.47, 4.69) * mm});
            skLineSegment(sketch, "E10927", {"start": v(17.47, 4.69) * mm, "end": v(17.48, 4.71) * mm});
            skLineSegment(sketch, "E10928", {"start": v(17.48, 4.71) * mm, "end": v(17.48, 4.74) * mm});
            skLineSegment(sketch, "E10929", {"start": v(17.48, 4.74) * mm, "end": v(17.5, 4.77) * mm});
            skLineSegment(sketch, "E10930", {"start": v(17.5, 4.77) * mm, "end": v(17.5, 4.8) * mm});
            skLineSegment(sketch, "E10931", {"start": v(17.5, 4.8) * mm, "end": v(17.5, 4.84) * mm});
            skLineSegment(sketch, "E10932", {"start": v(17.5, 4.84) * mm, "end": v(17.5, 4.84) * mm});
            skLineSegment(sketch, "E10933", {"start": v(17.5, 4.84) * mm, "end": v(17.5, 4.85) * mm});
            skLineSegment(sketch, "E10934", {"start": v(17.5, 4.85) * mm, "end": v(17.49, 4.86) * mm});
            skLineSegment(sketch, "E10935", {"start": v(17.49, 4.86) * mm, "end": v(17.48, 4.87) * mm});
            skLineSegment(sketch, "E10936", {"start": v(17.48, 4.87) * mm, "end": v(17.47, 4.9) * mm});
            skLineSegment(sketch, "E10937", {"start": v(17.47, 4.9) * mm, "end": v(17.46, 4.9) * mm});
            skLineSegment(sketch, "E10938", {"start": v(17.46, 4.9) * mm, "end": v(17.45, 4.92) * mm});
            skLineSegment(sketch, "E10939", {"start": v(17.45, 4.92) * mm, "end": v(17.43, 4.94) * mm});
            skLineSegment(sketch, "E10940", {"start": v(17.43, 4.94) * mm, "end": v(17.41, 4.96) * mm});
            skLineSegment(sketch, "E10941", {"start": v(17.41, 4.96) * mm, "end": v(17.39, 4.97) * mm});
            skLineSegment(sketch, "E10942", {"start": v(17.39, 4.97) * mm, "end": v(17.36, 4.99) * mm});
            skLineSegment(sketch, "E10943", {"start": v(17.36, 4.99) * mm, "end": v(17.33, 5) * mm});
            skLineSegment(sketch, "E10944", {"start": v(17.33, 5) * mm, "end": v(17.3, 5) * mm});
            skLineSegment(sketch, "E10945", {"start": v(17.3, 5) * mm, "end": v(17.25, 5.02) * mm});
            skLineSegment(sketch, "E10946", {"start": v(17.25, 5.02) * mm, "end": v(17.2, 5.03) * mm});
            skLineSegment(sketch, "E10947", {"start": v(17.2, 5.03) * mm, "end": v(17.15, 5.04) * mm});
            skLineSegment(sketch, "E10948", {"start": v(17.15, 5.04) * mm, "end": v(17.1, 5.05) * mm});
            skLineSegment(sketch, "E10949", {"start": v(17.1, 5.05) * mm, "end": v(17.06, 5.06) * mm});
            skLineSegment(sketch, "E10950", {"start": v(17.06, 5.06) * mm, "end": v(17.01, 5.08) * mm});
            skLineSegment(sketch, "E10951", {"start": v(17.01, 5.08) * mm, "end": v(16.97, 5.09) * mm});
            skLineSegment(sketch, "E10952", {"start": v(16.97, 5.09) * mm, "end": v(16.92, 5.1) * mm});
            skLineSegment(sketch, "E10953", {"start": v(16.92, 5.1) * mm, "end": v(16.88, 5.11) * mm});
            skLineSegment(sketch, "E10954", {"start": v(16.88, 5.11) * mm, "end": v(16.84, 5.12) * mm});
            skLineSegment(sketch, "E10955", {"start": v(16.84, 5.12) * mm, "end": v(16.8, 5.13) * mm});
            skLineSegment(sketch, "E10956", {"start": v(16.8, 5.13) * mm, "end": v(16.76, 5.14) * mm});
            skLineSegment(sketch, "E10957", {"start": v(16.76, 5.14) * mm, "end": v(16.72, 5.15) * mm});
            skLineSegment(sketch, "E10958", {"start": v(16.72, 5.15) * mm, "end": v(16.67, 5.16) * mm});
            skLineSegment(sketch, "E10959", {"start": v(16.67, 5.16) * mm, "end": v(16.63, 5.17) * mm});
            skLineSegment(sketch, "E10960", {"start": v(16.63, 5.17) * mm, "end": v(16.6, 5.18) * mm});
            skLineSegment(sketch, "E10961", {"start": v(16.6, 5.18) * mm, "end": v(16.54, 5.2) * mm});
            skLineSegment(sketch, "E10962", {"start": v(16.54, 5.2) * mm, "end": v(16.5, 5.2) * mm});
            skLineSegment(sketch, "E10963", {"start": v(16.5, 5.2) * mm, "end": v(16.45, 5.2) * mm});
            skLineSegment(sketch, "E10964", {"start": v(16.45, 5.2) * mm, "end": v(16.4, 5.21) * mm});
            skLineSegment(sketch, "E10965", {"start": v(16.4, 5.21) * mm, "end": v(16.37, 5.22) * mm});
            skLineSegment(sketch, "E10966", {"start": v(16.37, 5.22) * mm, "end": v(16.33, 5.22) * mm});
            skLineSegment(sketch, "E10967", {"start": v(16.33, 5.22) * mm, "end": v(16.29, 5.21) * mm});
            skLineSegment(sketch, "E10968", {"start": v(16.29, 5.21) * mm, "end": v(16.25, 5.2) * mm});
            skLineSegment(sketch, "E10969", {"start": v(16.25, 5.2) * mm, "end": v(16.17, 5.2) * mm});
            skLineSegment(sketch, "E10970", {"start": v(16.17, 5.2) * mm, "end": v(16.11, 5.2) * mm});
            skLineSegment(sketch, "E10971", {"start": v(16.11, 5.2) * mm, "end": v(16.07, 5.19) * mm});
            skLineSegment(sketch, "E10972", {"start": v(16.07, 5.19) * mm, "end": v(16.05, 5.18) * mm});
            skLineSegment(sketch, "E10973", {"start": v(16.05, 5.18) * mm, "end": v(16.03, 5.18) * mm});
            skLineSegment(sketch, "E10974", {"start": v(16.03, 5.18) * mm, "end": v(16.02, 5.18) * mm});
            skLineSegment(sketch, "E10975", {"start": v(16.02, 5.18) * mm, "end": v(16.02, 5.18) * mm});
            skLineSegment(sketch, "E10976", {"start": v(16.02, 5.18) * mm, "end": v(15.92, 5.16) * mm});
            skLineSegment(sketch, "E10977", {"start": v(15.92, 5.16) * mm, "end": v(15.83, 5.14) * mm});
            skLineSegment(sketch, "E10978", {"start": v(15.83, 5.14) * mm, "end": v(15.75, 5.13) * mm});
            skLineSegment(sketch, "E10979", {"start": v(15.75, 5.13) * mm, "end": v(15.67, 5.11) * mm});
            skLineSegment(sketch, "E10980", {"start": v(15.67, 5.11) * mm, "end": v(15.6, 5.1) * mm});
            skLineSegment(sketch, "E10981", {"start": v(15.6, 5.1) * mm, "end": v(15.55, 5.1) * mm});
            skLineSegment(sketch, "E10982", {"start": v(15.55, 5.1) * mm, "end": v(15.51, 5.08) * mm});
            skLineSegment(sketch, "E10983", {"start": v(15.51, 5.08) * mm, "end": v(15.5, 5.08) * mm});
            skLineSegment(sketch, "E10984", {"start": v(15.5, 5.08) * mm, "end": v(15.48, 5.08) * mm});
            skLineSegment(sketch, "E10985", {"start": v(15.48, 5.08) * mm, "end": v(15.46, 5.07) * mm});
            skLineSegment(sketch, "E10986", {"start": v(15.46, 5.07) * mm, "end": v(15.44, 5.07) * mm});
            skLineSegment(sketch, "E10987", {"start": v(15.44, 5.07) * mm, "end": v(15.41, 5.06) * mm});
            skLineSegment(sketch, "E10988", {"start": v(15.41, 5.06) * mm, "end": v(15.39, 5.05) * mm});
            skLineSegment(sketch, "E10989", {"start": v(15.39, 5.05) * mm, "end": v(15.36, 5.05) * mm});
            skLineSegment(sketch, "E10990", {"start": v(15.36, 5.05) * mm, "end": v(15.34, 5.04) * mm});
            skLineSegment(sketch, "E10991", {"start": v(15.34, 5.04) * mm, "end": v(15.31, 5.03) * mm});
            skLineSegment(sketch, "E10992", {"start": v(15.31, 5.03) * mm, "end": v(15.31, 5.03) * mm});
            skLineSegment(sketch, "E10993", {"start": v(15.31, 5.03) * mm, "end": v(15.3, 5.03) * mm});
            skLineSegment(sketch, "E10994", {"start": v(15.3, 5.03) * mm, "end": v(15.3, 5.02) * mm});
            skLineSegment(sketch, "E10995", {"start": v(15.3, 5.02) * mm, "end": v(15.3, 5.01) * mm});
            skLineSegment(sketch, "E10996", {"start": v(15.3, 5.01) * mm, "end": v(15.29, 5) * mm});
            skLineSegment(sketch, "E10997", {"start": v(15.29, 5) * mm, "end": v(15.28, 4.98) * mm});
            skLineSegment(sketch, "E10998", {"start": v(15.28, 4.98) * mm, "end": v(15.26, 4.97) * mm});
            skLineSegment(sketch, "E10999", {"start": v(15.26, 4.97) * mm, "end": v(15.25, 4.95) * mm});
            skLineSegment(sketch, "E11000", {"start": v(15.25, 4.95) * mm, "end": v(15.24, 4.94) * mm});
            skLineSegment(sketch, "E11001", {"start": v(15.24, 4.94) * mm, "end": v(15.23, 4.92) * mm});
            skLineSegment(sketch, "E11002", {"start": v(15.23, 4.92) * mm, "end": v(15.21, 4.9) * mm});
            skLineSegment(sketch, "E11003", {"start": v(15.21, 4.9) * mm, "end": v(15.2, 4.89) * mm});
            skLineSegment(sketch, "E11004", {"start": v(15.2, 4.89) * mm, "end": v(15.19, 4.87) * mm});
            skLineSegment(sketch, "E11005", {"start": v(15.19, 4.87) * mm, "end": v(15.18, 4.86) * mm});
            skLineSegment(sketch, "E11006", {"start": v(15.18, 4.86) * mm, "end": v(15.14, 4.81) * mm});
            skLineSegment(sketch, "E11007", {"start": v(15.14, 4.81) * mm, "end": v(15.1, 4.76) * mm});
            skLineSegment(sketch, "E11008", {"start": v(15.1, 4.76) * mm, "end": v(15.06, 4.71) * mm});
            skLineSegment(sketch, "E11009", {"start": v(15.06, 4.71) * mm, "end": v(15.02, 4.66) * mm});
            skLineSegment(sketch, "E11010", {"start": v(15.02, 4.66) * mm, "end": v(14.99, 4.61) * mm});
            skLineSegment(sketch, "E11011", {"start": v(14.99, 4.61) * mm, "end": v(14.95, 4.56) * mm});
            skLineSegment(sketch, "E11012", {"start": v(14.95, 4.56) * mm, "end": v(14.92, 4.5) * mm});
            skLineSegment(sketch, "E11013", {"start": v(14.92, 4.5) * mm, "end": v(14.88, 4.45) * mm});
            skLineSegment(sketch, "E11014", {"start": v(14.88, 4.45) * mm, "end": v(14.86, 4.4) * mm});
            skLineSegment(sketch, "E11015", {"start": v(14.86, 4.4) * mm, "end": v(14.84, 4.36) * mm});
            skLineSegment(sketch, "E11016", {"start": v(14.84, 4.36) * mm, "end": v(14.82, 4.32) * mm});
            skLineSegment(sketch, "E11017", {"start": v(14.82, 4.32) * mm, "end": v(14.8, 4.27) * mm});
            skLineSegment(sketch, "E11018", {"start": v(14.8, 4.27) * mm, "end": v(14.78, 4.23) * mm});
            skLineSegment(sketch, "E11019", {"start": v(14.78, 4.23) * mm, "end": v(14.77, 4.18) * mm});
            skLineSegment(sketch, "E11020", {"start": v(14.77, 4.18) * mm, "end": v(14.75, 4.14) * mm});
            skLineSegment(sketch, "E11021", {"start": v(14.75, 4.14) * mm, "end": v(14.74, 4.1) * mm});
            skLineSegment(sketch, "E11022", {"start": v(14.74, 4.1) * mm, "end": v(14.73, 4.07) * mm});
            skLineSegment(sketch, "E11023", {"start": v(14.73, 4.07) * mm, "end": v(14.72, 4.05) * mm});
            skLineSegment(sketch, "E11024", {"start": v(14.72, 4.05) * mm, "end": v(14.72, 4.03) * mm});
            skLineSegment(sketch, "E11025", {"start": v(14.72, 4.03) * mm, "end": v(14.71, 4) * mm});
            skLineSegment(sketch, "E11026", {"start": v(14.71, 4) * mm, "end": v(14.7, 3.98) * mm});
            skLineSegment(sketch, "E11027", {"start": v(14.7, 3.98) * mm, "end": v(14.7, 3.96) * mm});
            skLineSegment(sketch, "E11028", {"start": v(14.7, 3.96) * mm, "end": v(14.69, 3.94) * mm});
            skLineSegment(sketch, "E11029", {"start": v(14.69, 3.94) * mm, "end": v(14.68, 3.92) * mm});
            skLineSegment(sketch, "E11030", {"start": v(14.68, 3.92) * mm, "end": v(14.68, 3.91) * mm});
            skLineSegment(sketch, "E11031", {"start": v(14.68, 3.91) * mm, "end": v(14.67, 3.9) * mm});
            skLineSegment(sketch, "E11032", {"start": v(14.67, 3.9) * mm, "end": v(14.67, 3.89) * mm});
            skLineSegment(sketch, "E11033", {"start": v(14.67, 3.89) * mm, "end": v(14.66, 3.87) * mm});
            skLineSegment(sketch, "E11034", {"start": v(14.66, 3.87) * mm, "end": v(14.65, 3.86) * mm});
            skLineSegment(sketch, "E11035", {"start": v(14.65, 3.86) * mm, "end": v(14.65, 3.85) * mm});
            skLineSegment(sketch, "E11036", {"start": v(14.65, 3.85) * mm, "end": v(14.64, 3.84) * mm});
            skLineSegment(sketch, "E11037", {"start": v(14.64, 3.84) * mm, "end": v(14.64, 3.82) * mm});
            skLineSegment(sketch, "E11038", {"start": v(14.64, 3.82) * mm, "end": v(14.62, 3.8) * mm});
            skLineSegment(sketch, "E11039", {"start": v(14.62, 3.8) * mm, "end": v(14.61, 3.77) * mm});
            skLineSegment(sketch, "E11040", {"start": v(14.61, 3.77) * mm, "end": v(14.6, 3.74) * mm});
            skLineSegment(sketch, "E11041", {"start": v(14.6, 3.74) * mm, "end": v(14.59, 3.72) * mm});
            skLineSegment(sketch, "E11042", {"start": v(14.59, 3.72) * mm, "end": v(14.58, 3.69) * mm});
            skLineSegment(sketch, "E11043", {"start": v(14.58, 3.69) * mm, "end": v(14.57, 3.66) * mm});
            skLineSegment(sketch, "E11044", {"start": v(14.57, 3.66) * mm, "end": v(14.56, 3.63) * mm});
            skLineSegment(sketch, "E11045", {"start": v(14.56, 3.63) * mm, "end": v(14.56, 3.6) * mm});
            skLineSegment(sketch, "E11046", {"start": v(14.56, 3.6) * mm, "end": v(14.55, 3.53) * mm});
            skLineSegment(sketch, "E11047", {"start": v(14.55, 3.53) * mm, "end": v(14.54, 3.47) * mm});
            skLineSegment(sketch, "E11048", {"start": v(14.54, 3.47) * mm, "end": v(14.53, 3.4) * mm});
            skLineSegment(sketch, "E11049", {"start": v(14.53, 3.4) * mm, "end": v(14.52, 3.33) * mm});
            skLineSegment(sketch, "E11050", {"start": v(14.52, 3.33) * mm, "end": v(14.52, 3.26) * mm});
            skLineSegment(sketch, "E11051", {"start": v(14.52, 3.26) * mm, "end": v(14.5, 3.2) * mm});
            skLineSegment(sketch, "E11052", {"start": v(14.5, 3.2) * mm, "end": v(14.5, 3.12) * mm});
            skLineSegment(sketch, "E11053", {"start": v(14.5, 3.12) * mm, "end": v(14.5, 3.04) * mm});
            skLineSegment(sketch, "E11054", {"start": v(14.5, 3.04) * mm, "end": v(14.5, 3.01) * mm});
            skLineSegment(sketch, "E11055", {"start": v(14.5, 3.01) * mm, "end": v(14.5, 3) * mm});
            skLineSegment(sketch, "E11056", {"start": v(14.5, 3) * mm, "end": v(14.5, 2.98) * mm});
            skLineSegment(sketch, "E11057", {"start": v(14.5, 2.98) * mm, "end": v(14.49, 2.97) * mm});
            skLineSegment(sketch, "E11058", {"start": v(14.49, 2.97) * mm, "end": v(14.49, 2.96) * mm});
            skLineSegment(sketch, "E11059", {"start": v(14.49, 2.96) * mm, "end": v(14.49, 2.96) * mm});
            skLineSegment(sketch, "E11060", {"start": v(14.49, 2.96) * mm, "end": v(14.48, 2.92) * mm});
            skLineSegment(sketch, "E11061", {"start": v(14.48, 2.92) * mm, "end": v(14.48, 2.88) * mm});
            skLineSegment(sketch, "E11062", {"start": v(14.48, 2.88) * mm, "end": v(14.48, 2.85) * mm});
            skLineSegment(sketch, "E11063", {"start": v(14.48, 2.85) * mm, "end": v(14.47, 2.81) * mm});
            skLineSegment(sketch, "E11064", {"start": v(14.47, 2.81) * mm, "end": v(14.47, 2.78) * mm});
            skLineSegment(sketch, "E11065", {"start": v(14.47, 2.78) * mm, "end": v(14.47, 2.76) * mm});
            skLineSegment(sketch, "E11066", {"start": v(14.47, 2.76) * mm, "end": v(14.47, 2.73) * mm});
            skLineSegment(sketch, "E11067", {"start": v(14.47, 2.73) * mm, "end": v(14.47, 2.72) * mm});
            skLineSegment(sketch, "E11068", {"start": v(14.47, 2.72) * mm, "end": v(14.47, 2.7) * mm});
            skLineSegment(sketch, "E11069", {"start": v(14.47, 2.7) * mm, "end": v(14.49, 2.7) * mm});
            skLineSegment(sketch, "E11070", {"start": v(14.49, 2.7) * mm, "end": v(14.52, 2.7) * mm});
            skLineSegment(sketch, "E11071", {"start": v(15.07, 3.3) * mm, "end": v(15.08, 3.33) * mm});
            skLineSegment(sketch, "E11072", {"start": v(15.08, 3.33) * mm, "end": v(15.08, 3.35) * mm});
            skLineSegment(sketch, "E11073", {"start": v(15.08, 3.35) * mm, "end": v(15.08, 3.37) * mm});
            skLineSegment(sketch, "E11074", {"start": v(15.08, 3.37) * mm, "end": v(15.11, 3.5) * mm});
            skLineSegment(sketch, "E11075", {"start": v(15.11, 3.5) * mm, "end": v(15.15, 3.64) * mm});
            skLineSegment(sketch, "E11076", {"start": v(15.15, 3.64) * mm, "end": v(15.2, 3.77) * mm});
            skLineSegment(sketch, "E11077", {"start": v(15.2, 3.77) * mm, "end": v(15.26, 3.9) * mm});
            skLineSegment(sketch, "E11078", {"start": v(15.26, 3.9) * mm, "end": v(15.33, 4.02) * mm});
            skLineSegment(sketch, "E11079", {"start": v(15.33, 4.02) * mm, "end": v(15.41, 4.14) * mm});
            skLineSegment(sketch, "E11080", {"start": v(15.41, 4.14) * mm, "end": v(15.5, 4.26) * mm});
            skLineSegment(sketch, "E11081", {"start": v(15.5, 4.26) * mm, "end": v(15.6, 4.38) * mm});
            skLineSegment(sketch, "E11082", {"start": v(15.6, 4.38) * mm, "end": v(15.66, 4.43) * mm});
            skLineSegment(sketch, "E11083", {"start": v(15.66, 4.43) * mm, "end": v(15.71, 4.47) * mm});
            skLineSegment(sketch, "E11084", {"start": v(15.71, 4.47) * mm, "end": v(15.78, 4.5) * mm});
            skLineSegment(sketch, "E11085", {"start": v(15.78, 4.5) * mm, "end": v(15.85, 4.54) * mm});
            skLineSegment(sketch, "E11086", {"start": v(15.85, 4.54) * mm, "end": v(15.92, 4.58) * mm});
            skLineSegment(sketch, "E11087", {"start": v(15.92, 4.58) * mm, "end": v(16, 4.6) * mm});
            skLineSegment(sketch, "E11088", {"start": v(16, 4.6) * mm, "end": v(16.06, 4.63) * mm});
            skLineSegment(sketch, "E11089", {"start": v(16.06, 4.63) * mm, "end": v(16.13, 4.66) * mm});
            skLineSegment(sketch, "E11090", {"start": v(16.13, 4.66) * mm, "end": v(16.18, 4.67) * mm});
            skLineSegment(sketch, "E11091", {"start": v(16.18, 4.67) * mm, "end": v(16.22, 4.69) * mm});
            skLineSegment(sketch, "E11092", {"start": v(16.22, 4.69) * mm, "end": v(16.27, 4.7) * mm});
            skLineSegment(sketch, "E11093", {"start": v(16.27, 4.7) * mm, "end": v(16.32, 4.7) * mm});
            skLineSegment(sketch, "E11094", {"start": v(16.32, 4.7) * mm, "end": v(16.37, 4.72) * mm});
            skLineSegment(sketch, "E11095", {"start": v(16.37, 4.72) * mm, "end": v(16.42, 4.73) * mm});
            skLineSegment(sketch, "E11096", {"start": v(16.42, 4.73) * mm, "end": v(16.47, 4.73) * mm});
            skLineSegment(sketch, "E11097", {"start": v(16.47, 4.73) * mm, "end": v(16.52, 4.74) * mm});
            skLineSegment(sketch, "E11098", {"start": v(16.52, 4.74) * mm, "end": v(16.54, 4.74) * mm});
            skLineSegment(sketch, "E11099", {"start": v(16.54, 4.74) * mm, "end": v(16.57, 4.75) * mm});
            skLineSegment(sketch, "E11100", {"start": v(16.57, 4.75) * mm, "end": v(16.59, 4.75) * mm});
            skLineSegment(sketch, "E11101", {"start": v(16.59, 4.75) * mm, "end": v(16.6, 4.75) * mm});
            skLineSegment(sketch, "E11102", {"start": v(16.6, 4.75) * mm, "end": v(16.63, 4.76) * mm});
            skLineSegment(sketch, "E11103", {"start": v(16.63, 4.76) * mm, "end": v(16.65, 4.76) * mm});
            skLineSegment(sketch, "E11104", {"start": v(16.65, 4.76) * mm, "end": v(16.67, 4.76) * mm});
            skLineSegment(sketch, "E11105", {"start": v(16.67, 4.76) * mm, "end": v(16.7, 4.77) * mm});
            skLineSegment(sketch, "E11106", {"start": v(16.7, 4.77) * mm, "end": v(16.7, 4.77) * mm});
            skLineSegment(sketch, "E11107", {"start": v(16.7, 4.77) * mm, "end": v(16.71, 4.77) * mm});
            skLineSegment(sketch, "E11108", {"start": v(16.71, 4.77) * mm, "end": v(16.72, 4.77) * mm});
            skLineSegment(sketch, "E11109", {"start": v(16.72, 4.77) * mm, "end": v(16.72, 4.77) * mm});
            skLineSegment(sketch, "E11110", {"start": v(16.72, 4.77) * mm, "end": v(16.73, 4.77) * mm});
            skLineSegment(sketch, "E11111", {"start": v(16.73, 4.77) * mm, "end": v(16.73, 4.77) * mm});
            skLineSegment(sketch, "E11112", {"start": v(16.73, 4.77) * mm, "end": v(16.74, 4.77) * mm});
            skLineSegment(sketch, "E11113", {"start": v(16.74, 4.77) * mm, "end": v(16.75, 4.77) * mm});
            skLineSegment(sketch, "E11114", {"start": v(16.75, 4.77) * mm, "end": v(16.76, 4.77) * mm});
            skLineSegment(sketch, "E11115", {"start": v(16.76, 4.77) * mm, "end": v(16.77, 4.76) * mm});
            skLineSegment(sketch, "E11116", {"start": v(16.77, 4.76) * mm, "end": v(16.77, 4.75) * mm});
            skLineSegment(sketch, "E11117", {"start": v(16.77, 4.75) * mm, "end": v(16.78, 4.74) * mm});
            skLineSegment(sketch, "E11118", {"start": v(16.78, 4.74) * mm, "end": v(16.78, 4.72) * mm});
            skLineSegment(sketch, "E11119", {"start": v(16.78, 4.72) * mm, "end": v(16.79, 4.7) * mm});
            skLineSegment(sketch, "E11120", {"start": v(16.79, 4.7) * mm, "end": v(16.79, 4.68) * mm});
            skLineSegment(sketch, "E11121", {"start": v(16.79, 4.68) * mm, "end": v(16.8, 4.67) * mm});
            skLineSegment(sketch, "E11122", {"start": v(16.8, 4.67) * mm, "end": v(16.8, 4.65) * mm});
            skLineSegment(sketch, "E11123", {"start": v(16.8, 4.65) * mm, "end": v(16.8, 4.64) * mm});
            skLineSegment(sketch, "E11124", {"start": v(16.8, 4.64) * mm, "end": v(16.8, 4.62) * mm});
            skLineSegment(sketch, "E11125", {"start": v(16.8, 4.62) * mm, "end": v(16.81, 4.6) * mm});
            skLineSegment(sketch, "E11126", {"start": v(16.81, 4.6) * mm, "end": v(16.83, 4.6) * mm});
            skLineSegment(sketch, "E11127", {"start": v(16.83, 4.6) * mm, "end": v(16.84, 4.58) * mm});
            skLineSegment(sketch, "E11128", {"start": v(16.84, 4.58) * mm, "end": v(16.86, 4.56) * mm});
            skLineSegment(sketch, "E11129", {"start": v(16.86, 4.56) * mm, "end": v(16.87, 4.55) * mm});
            skLineSegment(sketch, "E11130", {"start": v(16.87, 4.55) * mm, "end": v(16.88, 4.54) * mm});
            skLineSegment(sketch, "E11131", {"start": v(16.88, 4.54) * mm, "end": v(16.9, 4.52) * mm});
            skLineSegment(sketch, "E11132", {"start": v(16.9, 4.52) * mm, "end": v(16.9, 4.5) * mm});
            skLineSegment(sketch, "E11133", {"start": v(16.9, 4.5) * mm, "end": v(16.91, 4.5) * mm});
            skLineSegment(sketch, "E11134", {"start": v(16.91, 4.5) * mm, "end": v(16.91, 4.48) * mm});
            skLineSegment(sketch, "E11135", {"start": v(16.91, 4.48) * mm, "end": v(16.92, 4.47) * mm});
            skLineSegment(sketch, "E11136", {"start": v(16.92, 4.47) * mm, "end": v(16.92, 4.45) * mm});
            skLineSegment(sketch, "E11137", {"start": v(16.92, 4.45) * mm, "end": v(16.91, 4.42) * mm});
            skLineSegment(sketch, "E11138", {"start": v(16.91, 4.42) * mm, "end": v(16.9, 4.4) * mm});
            skLineSegment(sketch, "E11139", {"start": v(16.9, 4.4) * mm, "end": v(16.89, 4.37) * mm});
            skLineSegment(sketch, "E11140", {"start": v(16.89, 4.37) * mm, "end": v(16.87, 4.34) * mm});
            skLineSegment(sketch, "E11141", {"start": v(16.87, 4.34) * mm, "end": v(16.85, 4.31) * mm});
            skLineSegment(sketch, "E11142", {"start": v(16.85, 4.31) * mm, "end": v(16.83, 4.29) * mm});
            skLineSegment(sketch, "E11143", {"start": v(16.83, 4.29) * mm, "end": v(16.8, 4.26) * mm});
            skLineSegment(sketch, "E11144", {"start": v(16.8, 4.26) * mm, "end": v(16.73, 4.16) * mm});
            skLineSegment(sketch, "E11145", {"start": v(16.73, 4.16) * mm, "end": v(16.64, 4.06) * mm});
            skLineSegment(sketch, "E11146", {"start": v(16.64, 4.06) * mm, "end": v(16.56, 3.96) * mm});
            skLineSegment(sketch, "E11147", {"start": v(16.56, 3.96) * mm, "end": v(16.47, 3.86) * mm});
            skLineSegment(sketch, "E11148", {"start": v(16.47, 3.86) * mm, "end": v(16.39, 3.77) * mm});
            skLineSegment(sketch, "E11149", {"start": v(16.39, 3.77) * mm, "end": v(16.3, 3.67) * mm});
            skLineSegment(sketch, "E11150", {"start": v(16.3, 3.67) * mm, "end": v(16.21, 3.57) * mm});
            skLineSegment(sketch, "E11151", {"start": v(16.21, 3.57) * mm, "end": v(16.13, 3.48) * mm});
            skLineSegment(sketch, "E11152", {"start": v(16.13, 3.48) * mm, "end": v(16.1, 3.46) * mm});
            skLineSegment(sketch, "E11153", {"start": v(16.1, 3.46) * mm, "end": v(16.09, 3.45) * mm});
            skLineSegment(sketch, "E11154", {"start": v(16.09, 3.45) * mm, "end": v(16.07, 3.44) * mm});
            skLineSegment(sketch, "E11155", {"start": v(16.07, 3.44) * mm, "end": v(16.04, 3.43) * mm});
            skLineSegment(sketch, "E11156", {"start": v(16.04, 3.43) * mm, "end": v(16.01, 3.41) * mm});
            skLineSegment(sketch, "E11157", {"start": v(16.01, 3.41) * mm, "end": v(15.98, 3.4) * mm});
            skLineSegment(sketch, "E11158", {"start": v(15.98, 3.4) * mm, "end": v(15.95, 3.4) * mm});
            skLineSegment(sketch, "E11159", {"start": v(15.95, 3.4) * mm, "end": v(15.92, 3.38) * mm});
            skLineSegment(sketch, "E11160", {"start": v(15.92, 3.38) * mm, "end": v(15.86, 3.37) * mm});
            skLineSegment(sketch, "E11161", {"start": v(15.86, 3.37) * mm, "end": v(15.82, 3.35) * mm});
            skLineSegment(sketch, "E11162", {"start": v(15.82, 3.35) * mm, "end": v(15.79, 3.34) * mm});
            skLineSegment(sketch, "E11163", {"start": v(15.79, 3.34) * mm, "end": v(15.77, 3.33) * mm});
            skLineSegment(sketch, "E11164", {"start": v(15.77, 3.33) * mm, "end": v(15.76, 3.33) * mm});
            skLineSegment(sketch, "E11165", {"start": v(15.76, 3.33) * mm, "end": v(15.75, 3.33) * mm});
            skLineSegment(sketch, "E11166", {"start": v(15.75, 3.33) * mm, "end": v(15.75, 3.33) * mm});
            skLineSegment(sketch, "E11167", {"start": v(15.75, 3.33) * mm, "end": v(15.68, 3.3) * mm});
            skLineSegment(sketch, "E11168", {"start": v(15.68, 3.3) * mm, "end": v(15.62, 3.3) * mm});
            skLineSegment(sketch, "E11169", {"start": v(15.62, 3.3) * mm, "end": v(15.56, 3.27) * mm});
            skLineSegment(sketch, "E11170", {"start": v(15.56, 3.27) * mm, "end": v(15.51, 3.26) * mm});
            skLineSegment(sketch, "E11171", {"start": v(15.51, 3.26) * mm, "end": v(15.46, 3.24) * mm});
            skLineSegment(sketch, "E11172", {"start": v(15.46, 3.24) * mm, "end": v(15.43, 3.23) * mm});
            skLineSegment(sketch, "E11173", {"start": v(15.43, 3.23) * mm, "end": v(15.4, 3.22) * mm});
            skLineSegment(sketch, "E11174", {"start": v(15.4, 3.22) * mm, "end": v(15.38, 3.22) * mm});
            skLineSegment(sketch, "E11175", {"start": v(15.38, 3.22) * mm, "end": v(15.36, 3.22) * mm});
            skLineSegment(sketch, "E11176", {"start": v(15.36, 3.22) * mm, "end": v(15.34, 3.21) * mm});
            skLineSegment(sketch, "E11177", {"start": v(15.34, 3.21) * mm, "end": v(15.3, 3.21) * mm});
            skLineSegment(sketch, "E11178", {"start": v(15.3, 3.21) * mm, "end": v(15.27, 3.22) * mm});
            skLineSegment(sketch, "E11179", {"start": v(15.27, 3.22) * mm, "end": v(15.23, 3.22) * mm});
            skLineSegment(sketch, "E11180", {"start": v(15.23, 3.22) * mm, "end": v(15.19, 3.22) * mm});
            skLineSegment(sketch, "E11181", {"start": v(15.19, 3.22) * mm, "end": v(15.14, 3.23) * mm});
            skLineSegment(sketch, "E11182", {"start": v(15.14, 3.23) * mm, "end": v(15.1, 3.23) * mm});
            skLineSegment(sketch, "E11183", {"start": v(15.1, 3.23) * mm, "end": v(15.1, 3.23) * mm});
            skLineSegment(sketch, "E11184", {"start": v(15.1, 3.23) * mm, "end": v(15.1, 3.24) * mm});
            skLineSegment(sketch, "E11185", {"start": v(15.1, 3.24) * mm, "end": v(15.1, 3.24) * mm});
            skLineSegment(sketch, "E11186", {"start": v(15.1, 3.24) * mm, "end": v(15.09, 3.25) * mm});
            skLineSegment(sketch, "E11187", {"start": v(15.09, 3.25) * mm, "end": v(15.08, 3.25) * mm});
            skLineSegment(sketch, "E11188", {"start": v(15.08, 3.25) * mm, "end": v(15.08, 3.27) * mm});
            skLineSegment(sketch, "E11189", {"start": v(15.08, 3.27) * mm, "end": v(15.08, 3.28) * mm});
            skLineSegment(sketch, "E11190", {"start": v(15.08, 3.28) * mm, "end": v(15.07, 3.3) * mm});
            skLineSegment(sketch, "E11191", {"start": v(15.07, 3.3) * mm, "end": v(15.07, 3.3) * mm});
            skLineSegment(sketch, "E11192", {"start": v(30.32, 14.5) * mm, "end": v(30.32, 14.5) * mm});
            skLineSegment(sketch, "E11193", {"start": v(30.32, 14.5) * mm, "end": v(30.31, 14.49) * mm});
            skLineSegment(sketch, "E11194", {"start": v(30.31, 14.49) * mm, "end": v(30.3, 14.47) * mm});
            skLineSegment(sketch, "E11195", {"start": v(30.3, 14.47) * mm, "end": v(30.29, 14.44) * mm});
            skLineSegment(sketch, "E11196", {"start": v(30.29, 14.44) * mm, "end": v(30.27, 14.39) * mm});
            skLineSegment(sketch, "E11197", {"start": v(30.27, 14.39) * mm, "end": v(30.23, 14.32) * mm});
            skLineSegment(sketch, "E11198", {"start": v(30.23, 14.32) * mm, "end": v(30.2, 14.23) * mm});
            skLineSegment(sketch, "E11199", {"start": v(30.2, 14.23) * mm, "end": v(30.14, 14.12) * mm});
            skLineSegment(sketch, "E11200", {"start": v(30.14, 14.12) * mm, "end": v(30.09, 14) * mm});
            skLineSegment(sketch, "E11201", {"start": v(30.09, 14) * mm, "end": v(30.04, 13.9) * mm});
            skLineSegment(sketch, "E11202", {"start": v(30.04, 13.9) * mm, "end": v(30, 13.78) * mm});
            skLineSegment(sketch, "E11203", {"start": v(30, 13.78) * mm, "end": v(29.95, 13.68) * mm});
            skLineSegment(sketch, "E11204", {"start": v(29.95, 13.68) * mm, "end": v(29.9, 13.57) * mm});
            skLineSegment(sketch, "E11205", {"start": v(29.9, 13.57) * mm, "end": v(29.86, 13.47) * mm});
            skLineSegment(sketch, "E11206", {"start": v(29.86, 13.47) * mm, "end": v(29.82, 13.37) * mm});
            skLineSegment(sketch, "E11207", {"start": v(29.82, 13.37) * mm, "end": v(29.81, 13.34) * mm});
            skLineSegment(sketch, "E11208", {"start": v(29.81, 13.34) * mm, "end": v(29.8, 13.32) * mm});
            skLineSegment(sketch, "E11209", {"start": v(29.8, 13.32) * mm, "end": v(29.8, 13.3) * mm});
            skLineSegment(sketch, "E11210", {"start": v(29.8, 13.3) * mm, "end": v(29.8, 13.26) * mm});
            skLineSegment(sketch, "E11211", {"start": v(29.8, 13.26) * mm, "end": v(29.79, 13.24) * mm});
            skLineSegment(sketch, "E11212", {"start": v(29.79, 13.24) * mm, "end": v(29.78, 13.22) * mm});
            skLineSegment(sketch, "E11213", {"start": v(29.78, 13.22) * mm, "end": v(29.78, 13.2) * mm});
            skLineSegment(sketch, "E11214", {"start": v(29.78, 13.2) * mm, "end": v(29.78, 13.17) * mm});
            skLineSegment(sketch, "E11215", {"start": v(29.78, 13.17) * mm, "end": v(29.78, 13.16) * mm});
            skLineSegment(sketch, "E11216", {"start": v(29.78, 13.16) * mm, "end": v(29.78, 13.16) * mm});
            skLineSegment(sketch, "E11217", {"start": v(29.78, 13.16) * mm, "end": v(29.78, 13.15) * mm});
            skLineSegment(sketch, "E11218", {"start": v(29.78, 13.15) * mm, "end": v(29.78, 13.15) * mm});
            skLineSegment(sketch, "E11219", {"start": v(29.78, 13.15) * mm, "end": v(29.77, 13.14) * mm});
            skLineSegment(sketch, "E11220", {"start": v(29.77, 13.14) * mm, "end": v(29.77, 13.14) * mm});
            skLineSegment(sketch, "E11221", {"start": v(29.77, 13.14) * mm, "end": v(29.77, 13.12) * mm});
            skLineSegment(sketch, "E11222", {"start": v(29.77, 13.12) * mm, "end": v(29.77, 13.11) * mm});
            skLineSegment(sketch, "E11223", {"start": v(29.77, 13.11) * mm, "end": v(29.77, 13.1) * mm});
            skLineSegment(sketch, "E11224", {"start": v(29.77, 13.1) * mm, "end": v(29.77, 13.09) * mm});
            skLineSegment(sketch, "E11225", {"start": v(29.77, 13.09) * mm, "end": v(29.76, 13.08) * mm});
            skLineSegment(sketch, "E11226", {"start": v(29.76, 13.08) * mm, "end": v(29.76, 13.07) * mm});
            skLineSegment(sketch, "E11227", {"start": v(29.76, 13.07) * mm, "end": v(29.76, 13.06) * mm});
            skLineSegment(sketch, "E11228", {"start": v(29.76, 13.06) * mm, "end": v(29.77, 13.04) * mm});
            skLineSegment(sketch, "E11229", {"start": v(29.77, 13.04) * mm, "end": v(29.8, 13.03) * mm});
            skLineSegment(sketch, "E11230", {"start": v(29.8, 13.03) * mm, "end": v(29.81, 13.02) * mm});
            skLineSegment(sketch, "E11231", {"start": v(29.81, 13.02) * mm, "end": v(29.84, 13.02) * mm});
            skLineSegment(sketch, "E11232", {"start": v(29.84, 13.02) * mm, "end": v(29.88, 13) * mm});
            skLineSegment(sketch, "E11233", {"start": v(29.88, 13) * mm, "end": v(29.92, 13) * mm});
            skLineSegment(sketch, "E11234", {"start": v(29.92, 13) * mm, "end": v(29.96, 13) * mm});
            skLineSegment(sketch, "E11235", {"start": v(29.96, 13) * mm, "end": v(30.01, 13) * mm});
            skLineSegment(sketch, "E11236", {"start": v(30.01, 13) * mm, "end": v(30.08, 12.99) * mm});
            skLineSegment(sketch, "E11237", {"start": v(30.08, 12.99) * mm, "end": v(30.16, 12.98) * mm});
            skLineSegment(sketch, "E11238", {"start": v(30.16, 12.98) * mm, "end": v(30.25, 12.97) * mm});
            skLineSegment(sketch, "E11239", {"start": v(30.25, 12.97) * mm, "end": v(30.34, 12.97) * mm});
            skLineSegment(sketch, "E11240", {"start": v(30.34, 12.97) * mm, "end": v(30.44, 12.96) * mm});
            skLineSegment(sketch, "E11241", {"start": v(30.44, 12.96) * mm, "end": v(30.54, 12.95) * mm});
            skLineSegment(sketch, "E11242", {"start": v(30.54, 12.95) * mm, "end": v(30.64, 12.94) * mm});
            skLineSegment(sketch, "E11243", {"start": v(30.64, 12.94) * mm, "end": v(30.64, 12.94) * mm});
            skLineSegment(sketch, "E11244", {"start": v(30.64, 12.94) * mm, "end": v(30.65, 12.94) * mm});
            skLineSegment(sketch, "E11245", {"start": v(30.65, 12.94) * mm, "end": v(30.66, 12.94) * mm});
            skLineSegment(sketch, "E11246", {"start": v(30.66, 12.94) * mm, "end": v(30.67, 12.94) * mm});
            skLineSegment(sketch, "E11247", {"start": v(30.67, 12.94) * mm, "end": v(30.7, 12.94) * mm});
            skLineSegment(sketch, "E11248", {"start": v(30.7, 12.94) * mm, "end": v(30.74, 12.93) * mm});
            skLineSegment(sketch, "E11249", {"start": v(30.74, 12.93) * mm, "end": v(30.8, 12.93) * mm});
            skLineSegment(sketch, "E11250", {"start": v(30.8, 12.93) * mm, "end": v(30.87, 12.92) * mm});
            skLineSegment(sketch, "E11251", {"start": v(30.87, 12.92) * mm, "end": v(30.89, 12.92) * mm});
            skLineSegment(sketch, "E11252", {"start": v(30.89, 12.92) * mm, "end": v(30.9, 12.92) * mm});
            skLineSegment(sketch, "E11253", {"start": v(30.9, 12.92) * mm, "end": v(30.9, 12.92) * mm});
            skLineSegment(sketch, "E11254", {"start": v(30.9, 12.92) * mm, "end": v(30.92, 12.92) * mm});
            skLineSegment(sketch, "E11255", {"start": v(30.92, 12.92) * mm, "end": v(30.93, 12.92) * mm});
            skLineSegment(sketch, "E11256", {"start": v(30.93, 12.92) * mm, "end": v(30.94, 12.92) * mm});
            skLineSegment(sketch, "E11257", {"start": v(30.94, 12.92) * mm, "end": v(30.95, 12.92) * mm});
            skLineSegment(sketch, "E11258", {"start": v(30.95, 12.92) * mm, "end": v(30.96, 12.92) * mm});
            skLineSegment(sketch, "E11259", {"start": v(30.96, 12.92) * mm, "end": v(30.98, 12.92) * mm});
            skLineSegment(sketch, "E11260", {"start": v(30.98, 12.92) * mm, "end": v(31, 12.92) * mm});
            skLineSegment(sketch, "E11261", {"start": v(31, 12.92) * mm, "end": v(31.01, 12.92) * mm});
            skLineSegment(sketch, "E11262", {"start": v(31.01, 12.92) * mm, "end": v(31.03, 12.93) * mm});
            skLineSegment(sketch, "E11263", {"start": v(31.03, 12.93) * mm, "end": v(31.05, 12.93) * mm});
            skLineSegment(sketch, "E11264", {"start": v(31.05, 12.93) * mm, "end": v(31.06, 12.93) * mm});
            skLineSegment(sketch, "E11265", {"start": v(31.06, 12.93) * mm, "end": v(31.08, 12.94) * mm});
            skLineSegment(sketch, "E11266", {"start": v(31.08, 12.94) * mm, "end": v(31.1, 12.94) * mm});
            skLineSegment(sketch, "E11267", {"start": v(31.1, 12.94) * mm, "end": v(31.26, 13.01) * mm});
            skLineSegment(sketch, "E11268", {"start": v(31.26, 13.01) * mm, "end": v(31.42, 13.1) * mm});
            skLineSegment(sketch, "E11269", {"start": v(31.42, 13.1) * mm, "end": v(31.57, 13.2) * mm});
            skLineSegment(sketch, "E11270", {"start": v(31.57, 13.2) * mm, "end": v(31.72, 13.3) * mm});
            skLineSegment(sketch, "E11271", {"start": v(31.72, 13.3) * mm, "end": v(31.86, 13.4) * mm});
            skLineSegment(sketch, "E11272", {"start": v(31.86, 13.4) * mm, "end": v(32, 13.53) * mm});
            skLineSegment(sketch, "E11273", {"start": v(32, 13.53) * mm, "end": v(32.12, 13.65) * mm});
            skLineSegment(sketch, "E11274", {"start": v(32.12, 13.65) * mm, "end": v(32.25, 13.78) * mm});
            skLineSegment(sketch, "E11275", {"start": v(32.25, 13.78) * mm, "end": v(32.27, 13.8) * mm});
            skLineSegment(sketch, "E11276", {"start": v(32.27, 13.8) * mm, "end": v(32.3, 13.82) * mm});
            skLineSegment(sketch, "E11277", {"start": v(32.3, 13.82) * mm, "end": v(32.31, 13.84) * mm});
            skLineSegment(sketch, "E11278", {"start": v(32.31, 13.84) * mm, "end": v(32.33, 13.87) * mm});
            skLineSegment(sketch, "E11279", {"start": v(32.33, 13.87) * mm, "end": v(32.35, 13.9) * mm});
            skLineSegment(sketch, "E11280", {"start": v(32.35, 13.9) * mm, "end": v(32.36, 13.92) * mm});
            skLineSegment(sketch, "E11281", {"start": v(32.36, 13.92) * mm, "end": v(32.37, 13.95) * mm});
            skLineSegment(sketch, "E11282", {"start": v(32.37, 13.95) * mm, "end": v(32.39, 13.98) * mm});
            skLineSegment(sketch, "E11283", {"start": v(32.39, 13.98) * mm, "end": v(32.41, 14.05) * mm});
            skLineSegment(sketch, "E11284", {"start": v(32.41, 14.05) * mm, "end": v(32.43, 14.1) * mm});
            skLineSegment(sketch, "E11285", {"start": v(32.43, 14.1) * mm, "end": v(32.45, 14.14) * mm});
            skLineSegment(sketch, "E11286", {"start": v(32.45, 14.14) * mm, "end": v(32.46, 14.16) * mm});
            skLineSegment(sketch, "E11287", {"start": v(32.46, 14.16) * mm, "end": v(32.46, 14.18) * mm});
            skLineSegment(sketch, "E11288", {"start": v(32.46, 14.18) * mm, "end": v(32.46, 14.19) * mm});
            skLineSegment(sketch, "E11289", {"start": v(32.46, 14.19) * mm, "end": v(32.47, 14.19) * mm});
            skLineSegment(sketch, "E11290", {"start": v(32.47, 14.19) * mm, "end": v(32.47, 14.19) * mm});
            skLineSegment(sketch, "E11291", {"start": v(32.47, 14.19) * mm, "end": v(32.5, 14.28) * mm});
            skLineSegment(sketch, "E11292", {"start": v(32.5, 14.28) * mm, "end": v(32.53, 14.37) * mm});
            skLineSegment(sketch, "E11293", {"start": v(32.53, 14.37) * mm, "end": v(32.56, 14.45) * mm});
            skLineSegment(sketch, "E11294", {"start": v(32.56, 14.45) * mm, "end": v(32.6, 14.54) * mm});
            skLineSegment(sketch, "E11295", {"start": v(32.6, 14.54) * mm, "end": v(32.62, 14.61) * mm});
            skLineSegment(sketch, "E11296", {"start": v(32.62, 14.61) * mm, "end": v(32.64, 14.68) * mm});
            skLineSegment(sketch, "E11297", {"start": v(32.64, 14.68) * mm, "end": v(32.66, 14.74) * mm});
            skLineSegment(sketch, "E11298", {"start": v(32.66, 14.74) * mm, "end": v(32.68, 14.78) * mm});
            skLineSegment(sketch, "E11299", {"start": v(32.68, 14.78) * mm, "end": v(32.69, 14.82) * mm});
            skLineSegment(sketch, "E11300", {"start": v(32.69, 14.82) * mm, "end": v(32.7, 14.85) * mm});
            skLineSegment(sketch, "E11301", {"start": v(32.7, 14.85) * mm, "end": v(32.7, 14.88) * mm});
            skLineSegment(sketch, "E11302", {"start": v(32.7, 14.88) * mm, "end": v(32.68, 14.9) * mm});
            skLineSegment(sketch, "E11303", {"start": v(32.68, 14.9) * mm, "end": v(32.67, 14.93) * mm});
            skLineSegment(sketch, "E11304", {"start": v(32.67, 14.93) * mm, "end": v(32.66, 14.95) * mm});
            skLineSegment(sketch, "E11305", {"start": v(32.66, 14.95) * mm, "end": v(32.63, 14.97) * mm});
            skLineSegment(sketch, "E11306", {"start": v(32.63, 14.97) * mm, "end": v(32.6, 14.98) * mm});
            skLineSegment(sketch, "E11307", {"start": v(32.6, 14.98) * mm, "end": v(32.58, 14.98) * mm});
            skLineSegment(sketch, "E11308", {"start": v(32.58, 14.98) * mm, "end": v(32.55, 15) * mm});
            skLineSegment(sketch, "E11309", {"start": v(32.55, 15) * mm, "end": v(32.52, 15) * mm});
            skLineSegment(sketch, "E11310", {"start": v(32.52, 15) * mm, "end": v(32.49, 15) * mm});
            skLineSegment(sketch, "E11311", {"start": v(32.49, 15) * mm, "end": v(32.45, 15.01) * mm});
            skLineSegment(sketch, "E11312", {"start": v(32.45, 15.01) * mm, "end": v(32.42, 15.02) * mm});
            skLineSegment(sketch, "E11313", {"start": v(32.42, 15.02) * mm, "end": v(32.4, 15.02) * mm});
            skLineSegment(sketch, "E11314", {"start": v(32.4, 15.02) * mm, "end": v(32.37, 15.03) * mm});
            skLineSegment(sketch, "E11315", {"start": v(32.37, 15.03) * mm, "end": v(32.35, 15.04) * mm});
            skLineSegment(sketch, "E11316", {"start": v(32.35, 15.04) * mm, "end": v(32.31, 15.04) * mm});
            skLineSegment(sketch, "E11317", {"start": v(32.31, 15.04) * mm, "end": v(32.27, 15.05) * mm});
            skLineSegment(sketch, "E11318", {"start": v(32.27, 15.05) * mm, "end": v(32.23, 15.06) * mm});
            skLineSegment(sketch, "E11319", {"start": v(32.23, 15.06) * mm, "end": v(32.2, 15.07) * mm});
            skLineSegment(sketch, "E11320", {"start": v(32.2, 15.07) * mm, "end": v(32.16, 15.07) * mm});
            skLineSegment(sketch, "E11321", {"start": v(32.16, 15.07) * mm, "end": v(32.13, 15.08) * mm});
            skLineSegment(sketch, "E11322", {"start": v(32.13, 15.08) * mm, "end": v(32.11, 15.08) * mm});
            skLineSegment(sketch, "E11323", {"start": v(32.11, 15.08) * mm, "end": v(32.1, 15.09) * mm});
            skLineSegment(sketch, "E11324", {"start": v(32.1, 15.09) * mm, "end": v(32.07, 15.1) * mm});
            skLineSegment(sketch, "E11325", {"start": v(32.07, 15.1) * mm, "end": v(32.03, 15.1) * mm});
            skLineSegment(sketch, "E11326", {"start": v(32.03, 15.1) * mm, "end": v(31.98, 15.11) * mm});
            skLineSegment(sketch, "E11327", {"start": v(31.98, 15.11) * mm, "end": v(31.92, 15.12) * mm});
            skLineSegment(sketch, "E11328", {"start": v(31.92, 15.12) * mm, "end": v(31.86, 15.14) * mm});
            skLineSegment(sketch, "E11329", {"start": v(31.86, 15.14) * mm, "end": v(31.8, 15.15) * mm});
            skLineSegment(sketch, "E11330", {"start": v(31.8, 15.15) * mm, "end": v(31.72, 15.16) * mm});
            skLineSegment(sketch, "E11331", {"start": v(31.72, 15.16) * mm, "end": v(31.72, 15.16) * mm});
            skLineSegment(sketch, "E11332", {"start": v(31.72, 15.16) * mm, "end": v(31.7, 15.17) * mm});
            skLineSegment(sketch, "E11333", {"start": v(31.7, 15.17) * mm, "end": v(31.7, 15.17) * mm});
            skLineSegment(sketch, "E11334", {"start": v(31.7, 15.17) * mm, "end": v(31.68, 15.17) * mm});
            skLineSegment(sketch, "E11335", {"start": v(31.68, 15.17) * mm, "end": v(31.64, 15.18) * mm});
            skLineSegment(sketch, "E11336", {"start": v(31.64, 15.18) * mm, "end": v(31.6, 15.18) * mm});
            skLineSegment(sketch, "E11337", {"start": v(31.6, 15.18) * mm, "end": v(31.54, 15.2) * mm});
            skLineSegment(sketch, "E11338", {"start": v(31.54, 15.2) * mm, "end": v(31.46, 15.2) * mm});
            skLineSegment(sketch, "E11339", {"start": v(31.46, 15.2) * mm, "end": v(31.4, 15.21) * mm});
            skLineSegment(sketch, "E11340", {"start": v(31.4, 15.21) * mm, "end": v(31.36, 15.22) * mm});
            skLineSegment(sketch, "E11341", {"start": v(31.36, 15.22) * mm, "end": v(31.33, 15.23) * mm});
            skLineSegment(sketch, "E11342", {"start": v(31.33, 15.23) * mm, "end": v(31.32, 15.23) * mm});
            skLineSegment(sketch, "E11343", {"start": v(31.32, 15.23) * mm, "end": v(31.3, 15.23) * mm});
            skLineSegment(sketch, "E11344", {"start": v(31.3, 15.23) * mm, "end": v(31.3, 15.23) * mm});
            skLineSegment(sketch, "E11345", {"start": v(31.3, 15.23) * mm, "end": v(31.23, 15.2) * mm});
            skLineSegment(sketch, "E11346", {"start": v(31.23, 15.2) * mm, "end": v(31.16, 15.15) * mm});
            skLineSegment(sketch, "E11347", {"start": v(31.16, 15.15) * mm, "end": v(31.09, 15.12) * mm});
            skLineSegment(sketch, "E11348", {"start": v(31.09, 15.12) * mm, "end": v(31.03, 15.09) * mm});
            skLineSegment(sketch, "E11349", {"start": v(31.03, 15.09) * mm, "end": v(30.98, 15.06) * mm});
            skLineSegment(sketch, "E11350", {"start": v(30.98, 15.06) * mm, "end": v(30.93, 15.04) * mm});
            skLineSegment(sketch, "E11351", {"start": v(30.93, 15.04) * mm, "end": v(30.9, 15.02) * mm});
            skLineSegment(sketch, "E11352", {"start": v(30.9, 15.02) * mm, "end": v(30.89, 15.02) * mm});
            skLineSegment(sketch, "E11353", {"start": v(30.89, 15.02) * mm, "end": v(30.87, 15) * mm});
            skLineSegment(sketch, "E11354", {"start": v(30.87, 15) * mm, "end": v(30.83, 14.97) * mm});
            skLineSegment(sketch, "E11355", {"start": v(30.83, 14.97) * mm, "end": v(30.77, 14.92) * mm});
            skLineSegment(sketch, "E11356", {"start": v(30.77, 14.92) * mm, "end": v(30.7, 14.86) * mm});
            skLineSegment(sketch, "E11357", {"start": v(30.7, 14.86) * mm, "end": v(30.62, 14.78) * mm});
            skLineSegment(sketch, "E11358", {"start": v(30.62, 14.78) * mm, "end": v(30.53, 14.7) * mm});
            skLineSegment(sketch, "E11359", {"start": v(30.53, 14.7) * mm, "end": v(30.43, 14.6) * mm});
            skLineSegment(sketch, "E11360", {"start": v(30.43, 14.6) * mm, "end": v(30.32, 14.5) * mm});
            skLineSegment(sketch, "E11361", {"start": v(30.52, 14.03) * mm, "end": v(30.6, 14.17) * mm});
            skLineSegment(sketch, "E11362", {"start": v(30.6, 14.17) * mm, "end": v(30.7, 14.29) * mm});
            skLineSegment(sketch, "E11363", {"start": v(30.7, 14.29) * mm, "end": v(30.8, 14.4) * mm});
            skLineSegment(sketch, "E11364", {"start": v(30.8, 14.4) * mm, "end": v(30.92, 14.49) * mm});
            skLineSegment(sketch, "E11365", {"start": v(30.92, 14.49) * mm, "end": v(31.06, 14.57) * mm});
            skLineSegment(sketch, "E11366", {"start": v(31.06, 14.57) * mm, "end": v(31.2, 14.63) * mm});
            skLineSegment(sketch, "E11367", {"start": v(31.2, 14.63) * mm, "end": v(31.27, 14.65) * mm});
            skLineSegment(sketch, "E11368", {"start": v(31.27, 14.65) * mm, "end": v(31.31, 14.67) * mm});
            skLineSegment(sketch, "E11369", {"start": v(31.31, 14.67) * mm, "end": v(31.35, 14.68) * mm});
            skLineSegment(sketch, "E11370", {"start": v(31.35, 14.68) * mm, "end": v(31.37, 14.69) * mm});
            skLineSegment(sketch, "E11371", {"start": v(31.37, 14.69) * mm, "end": v(31.38, 14.7) * mm});
            skLineSegment(sketch, "E11372", {"start": v(31.38, 14.7) * mm, "end": v(31.39, 14.7) * mm});
            skLineSegment(sketch, "E11373", {"start": v(31.39, 14.7) * mm, "end": v(31.39, 14.7) * mm});
            skLineSegment(sketch, "E11374", {"start": v(31.39, 14.7) * mm, "end": v(31.4, 14.7) * mm});
            skLineSegment(sketch, "E11375", {"start": v(31.4, 14.7) * mm, "end": v(31.46, 14.7) * mm});
            skLineSegment(sketch, "E11376", {"start": v(31.46, 14.7) * mm, "end": v(31.52, 14.71) * mm});
            skLineSegment(sketch, "E11377", {"start": v(31.52, 14.71) * mm, "end": v(31.57, 14.72) * mm});
            skLineSegment(sketch, "E11378", {"start": v(31.57, 14.72) * mm, "end": v(31.62, 14.73) * mm});
            skLineSegment(sketch, "E11379", {"start": v(31.62, 14.73) * mm, "end": v(31.66, 14.74) * mm});
            skLineSegment(sketch, "E11380", {"start": v(31.66, 14.74) * mm, "end": v(31.7, 14.75) * mm});
            skLineSegment(sketch, "E11381", {"start": v(31.7, 14.75) * mm, "end": v(31.71, 14.76) * mm});
            skLineSegment(sketch, "E11382", {"start": v(31.71, 14.76) * mm, "end": v(31.72, 14.77) * mm});
            skLineSegment(sketch, "E11383", {"start": v(31.72, 14.77) * mm, "end": v(31.72, 14.78) * mm});
            skLineSegment(sketch, "E11384", {"start": v(31.72, 14.78) * mm, "end": v(31.72, 14.78) * mm});
            skLineSegment(sketch, "E11385", {"start": v(31.72, 14.78) * mm, "end": v(31.72, 14.79) * mm});
            skLineSegment(sketch, "E11386", {"start": v(31.72, 14.79) * mm, "end": v(31.72, 14.79) * mm});
            skLineSegment(sketch, "E11387", {"start": v(31.72, 14.79) * mm, "end": v(31.72, 14.78) * mm});
            skLineSegment(sketch, "E11388", {"start": v(31.72, 14.78) * mm, "end": v(31.72, 14.77) * mm});
            skLineSegment(sketch, "E11389", {"start": v(31.72, 14.77) * mm, "end": v(31.72, 14.76) * mm});
            skLineSegment(sketch, "E11390", {"start": v(31.72, 14.76) * mm, "end": v(31.73, 14.75) * mm});
            skLineSegment(sketch, "E11391", {"start": v(31.73, 14.75) * mm, "end": v(31.74, 14.74) * mm});
            skLineSegment(sketch, "E11392", {"start": v(31.74, 14.74) * mm, "end": v(31.75, 14.73) * mm});
            skLineSegment(sketch, "E11393", {"start": v(31.75, 14.73) * mm, "end": v(31.76, 14.72) * mm});
            skLineSegment(sketch, "E11394", {"start": v(31.76, 14.72) * mm, "end": v(31.77, 14.71) * mm});
            skLineSegment(sketch, "E11395", {"start": v(31.77, 14.71) * mm, "end": v(31.79, 14.7) * mm});
            skLineSegment(sketch, "E11396", {"start": v(31.79, 14.7) * mm, "end": v(31.8, 14.7) * mm});
            skLineSegment(sketch, "E11397", {"start": v(31.8, 14.7) * mm, "end": v(31.8, 14.7) * mm});
            skLineSegment(sketch, "E11398", {"start": v(31.8, 14.7) * mm, "end": v(31.81, 14.7) * mm});
            skLineSegment(sketch, "E11399", {"start": v(31.81, 14.7) * mm, "end": v(31.82, 14.69) * mm});
            skLineSegment(sketch, "E11400", {"start": v(31.82, 14.69) * mm, "end": v(31.82, 14.68) * mm});
            skLineSegment(sketch, "E11401", {"start": v(31.82, 14.68) * mm, "end": v(31.83, 14.67) * mm});
            skLineSegment(sketch, "E11402", {"start": v(31.83, 14.67) * mm, "end": v(31.85, 14.66) * mm});
            skLineSegment(sketch, "E11403", {"start": v(31.85, 14.66) * mm, "end": v(31.86, 14.64) * mm});
            skLineSegment(sketch, "E11404", {"start": v(31.86, 14.64) * mm, "end": v(31.88, 14.62) * mm});
            skLineSegment(sketch, "E11405", {"start": v(31.88, 14.62) * mm, "end": v(31.9, 14.6) * mm});
            skLineSegment(sketch, "E11406", {"start": v(31.9, 14.6) * mm, "end": v(31.9, 14.57) * mm});
            skLineSegment(sketch, "E11407", {"start": v(31.9, 14.57) * mm, "end": v(31.91, 14.54) * mm});
            skLineSegment(sketch, "E11408", {"start": v(31.91, 14.54) * mm, "end": v(31.92, 14.52) * mm});
            skLineSegment(sketch, "E11409", {"start": v(31.92, 14.52) * mm, "end": v(31.92, 14.5) * mm});
            skLineSegment(sketch, "E11410", {"start": v(31.92, 14.5) * mm, "end": v(31.92, 14.47) * mm});
            skLineSegment(sketch, "E11411", {"start": v(31.92, 14.47) * mm, "end": v(31.92, 14.4) * mm});
            skLineSegment(sketch, "E11412", {"start": v(31.92, 14.4) * mm, "end": v(31.9, 14.34) * mm});
            skLineSegment(sketch, "E11413", {"start": v(31.9, 14.34) * mm, "end": v(31.9, 14.28) * mm});
            skLineSegment(sketch, "E11414", {"start": v(31.9, 14.28) * mm, "end": v(31.87, 14.22) * mm});
            skLineSegment(sketch, "E11415", {"start": v(31.87, 14.22) * mm, "end": v(31.84, 14.17) * mm});
            skLineSegment(sketch, "E11416", {"start": v(31.84, 14.17) * mm, "end": v(31.81, 14.12) * mm});
            skLineSegment(sketch, "E11417", {"start": v(31.81, 14.12) * mm, "end": v(31.77, 14.08) * mm});
            skLineSegment(sketch, "E11418", {"start": v(31.77, 14.08) * mm, "end": v(31.72, 14.04) * mm});
            skLineSegment(sketch, "E11419", {"start": v(31.72, 14.04) * mm, "end": v(31.7, 14.02) * mm});
            skLineSegment(sketch, "E11420", {"start": v(31.7, 14.02) * mm, "end": v(31.69, 14) * mm});
            skLineSegment(sketch, "E11421", {"start": v(31.69, 14) * mm, "end": v(31.67, 13.99) * mm});
            skLineSegment(sketch, "E11422", {"start": v(31.67, 13.99) * mm, "end": v(31.65, 13.97) * mm});
            skLineSegment(sketch, "E11423", {"start": v(31.65, 13.97) * mm, "end": v(31.63, 13.95) * mm});
            skLineSegment(sketch, "E11424", {"start": v(31.63, 13.95) * mm, "end": v(31.61, 13.93) * mm});
            skLineSegment(sketch, "E11425", {"start": v(31.61, 13.93) * mm, "end": v(31.6, 13.91) * mm});
            skLineSegment(sketch, "E11426", {"start": v(31.6, 13.91) * mm, "end": v(31.57, 13.9) * mm});
            skLineSegment(sketch, "E11427", {"start": v(31.57, 13.9) * mm, "end": v(31.54, 13.87) * mm});
            skLineSegment(sketch, "E11428", {"start": v(31.54, 13.87) * mm, "end": v(31.51, 13.84) * mm});
            skLineSegment(sketch, "E11429", {"start": v(31.51, 13.84) * mm, "end": v(31.48, 13.81) * mm});
            skLineSegment(sketch, "E11430", {"start": v(31.48, 13.81) * mm, "end": v(31.45, 13.78) * mm});
            skLineSegment(sketch, "E11431", {"start": v(31.45, 13.78) * mm, "end": v(31.42, 13.76) * mm});
            skLineSegment(sketch, "E11432", {"start": v(31.42, 13.76) * mm, "end": v(31.4, 13.74) * mm});
            skLineSegment(sketch, "E11433", {"start": v(31.4, 13.74) * mm, "end": v(31.36, 13.71) * mm});
            skLineSegment(sketch, "E11434", {"start": v(31.36, 13.71) * mm, "end": v(31.33, 13.7) * mm});
            skLineSegment(sketch, "E11435", {"start": v(31.33, 13.7) * mm, "end": v(31.28, 13.67) * mm});
            skLineSegment(sketch, "E11436", {"start": v(31.28, 13.67) * mm, "end": v(31.22, 13.64) * mm});
            skLineSegment(sketch, "E11437", {"start": v(31.22, 13.64) * mm, "end": v(31.17, 13.62) * mm});
            skLineSegment(sketch, "E11438", {"start": v(31.17, 13.62) * mm, "end": v(31.1, 13.6) * mm});
            skLineSegment(sketch, "E11439", {"start": v(31.1, 13.6) * mm, "end": v(31.05, 13.58) * mm});
            skLineSegment(sketch, "E11440", {"start": v(31.05, 13.58) * mm, "end": v(30.99, 13.56) * mm});
            skLineSegment(sketch, "E11441", {"start": v(30.99, 13.56) * mm, "end": v(30.93, 13.54) * mm});
            skLineSegment(sketch, "E11442", {"start": v(30.93, 13.54) * mm, "end": v(30.87, 13.52) * mm});
            skLineSegment(sketch, "E11443", {"start": v(30.87, 13.52) * mm, "end": v(30.85, 13.51) * mm});
            skLineSegment(sketch, "E11444", {"start": v(30.85, 13.51) * mm, "end": v(30.83, 13.5) * mm});
            skLineSegment(sketch, "E11445", {"start": v(30.83, 13.5) * mm, "end": v(30.81, 13.5) * mm});
            skLineSegment(sketch, "E11446", {"start": v(30.81, 13.5) * mm, "end": v(30.8, 13.5) * mm});
            skLineSegment(sketch, "E11447", {"start": v(30.8, 13.5) * mm, "end": v(30.78, 13.5) * mm});
            skLineSegment(sketch, "E11448", {"start": v(30.78, 13.5) * mm, "end": v(30.76, 13.49) * mm});
            skLineSegment(sketch, "E11449", {"start": v(30.76, 13.49) * mm, "end": v(30.75, 13.48) * mm});
            skLineSegment(sketch, "E11450", {"start": v(30.75, 13.48) * mm, "end": v(30.73, 13.48) * mm});
            skLineSegment(sketch, "E11451", {"start": v(30.73, 13.48) * mm, "end": v(30.72, 13.47) * mm});
            skLineSegment(sketch, "E11452", {"start": v(30.72, 13.47) * mm, "end": v(30.7, 13.47) * mm});
            skLineSegment(sketch, "E11453", {"start": v(30.7, 13.47) * mm, "end": v(30.69, 13.47) * mm});
            skLineSegment(sketch, "E11454", {"start": v(30.69, 13.47) * mm, "end": v(30.67, 13.46) * mm});
            skLineSegment(sketch, "E11455", {"start": v(30.67, 13.46) * mm, "end": v(30.66, 13.46) * mm});
            skLineSegment(sketch, "E11456", {"start": v(30.66, 13.46) * mm, "end": v(30.64, 13.46) * mm});
            skLineSegment(sketch, "E11457", {"start": v(30.64, 13.46) * mm, "end": v(30.62, 13.46) * mm});
            skLineSegment(sketch, "E11458", {"start": v(30.62, 13.46) * mm, "end": v(30.6, 13.46) * mm});
            skLineSegment(sketch, "E11459", {"start": v(30.6, 13.46) * mm, "end": v(30.6, 13.46) * mm});
            skLineSegment(sketch, "E11460", {"start": v(30.6, 13.46) * mm, "end": v(30.59, 13.46) * mm});
            skLineSegment(sketch, "E11461", {"start": v(30.59, 13.46) * mm, "end": v(30.59, 13.46) * mm});
            skLineSegment(sketch, "E11462", {"start": v(30.59, 13.46) * mm, "end": v(30.58, 13.46) * mm});
            skLineSegment(sketch, "E11463", {"start": v(30.58, 13.46) * mm, "end": v(30.58, 13.46) * mm});
            skLineSegment(sketch, "E11464", {"start": v(30.58, 13.46) * mm, "end": v(30.57, 13.46) * mm});
            skLineSegment(sketch, "E11465", {"start": v(30.57, 13.46) * mm, "end": v(30.56, 13.46) * mm});
            skLineSegment(sketch, "E11466", {"start": v(30.56, 13.46) * mm, "end": v(30.55, 13.46) * mm});
            skLineSegment(sketch, "E11467", {"start": v(30.55, 13.46) * mm, "end": v(30.54, 13.46) * mm});
            skLineSegment(sketch, "E11468", {"start": v(30.54, 13.46) * mm, "end": v(30.54, 13.46) * mm});
            skLineSegment(sketch, "E11469", {"start": v(30.54, 13.46) * mm, "end": v(30.53, 13.45) * mm});
            skLineSegment(sketch, "E11470", {"start": v(30.53, 13.45) * mm, "end": v(30.53, 13.45) * mm});
            skLineSegment(sketch, "E11471", {"start": v(30.53, 13.45) * mm, "end": v(30.52, 13.45) * mm});
            skLineSegment(sketch, "E11472", {"start": v(30.52, 13.45) * mm, "end": v(30.52, 13.45) * mm});
            skLineSegment(sketch, "E11473", {"start": v(30.52, 13.45) * mm, "end": v(30.51, 13.45) * mm});
            skLineSegment(sketch, "E11474", {"start": v(30.51, 13.45) * mm, "end": v(30.5, 13.46) * mm});
            skLineSegment(sketch, "E11475", {"start": v(30.5, 13.46) * mm, "end": v(30.5, 13.46) * mm});
            skLineSegment(sketch, "E11476", {"start": v(30.5, 13.46) * mm, "end": v(30.49, 13.46) * mm});
            skLineSegment(sketch, "E11477", {"start": v(30.49, 13.46) * mm, "end": v(30.48, 13.46) * mm});
            skLineSegment(sketch, "E11478", {"start": v(30.48, 13.46) * mm, "end": v(30.46, 13.47) * mm});
            skLineSegment(sketch, "E11479", {"start": v(30.46, 13.47) * mm, "end": v(30.45, 13.47) * mm});
            skLineSegment(sketch, "E11480", {"start": v(30.45, 13.47) * mm, "end": v(30.45, 13.47) * mm});
            skLineSegment(sketch, "E11481", {"start": v(30.45, 13.47) * mm, "end": v(30.45, 13.48) * mm});
            skLineSegment(sketch, "E11482", {"start": v(30.45, 13.48) * mm, "end": v(30.45, 13.48) * mm});
            skLineSegment(sketch, "E11483", {"start": v(30.45, 13.48) * mm, "end": v(30.44, 13.49) * mm});
            skLineSegment(sketch, "E11484", {"start": v(30.44, 13.49) * mm, "end": v(30.43, 13.5) * mm});
            skLineSegment(sketch, "E11485", {"start": v(30.43, 13.5) * mm, "end": v(30.43, 13.5) * mm});
            skLineSegment(sketch, "E11486", {"start": v(30.43, 13.5) * mm, "end": v(30.41, 13.53) * mm});
            skLineSegment(sketch, "E11487", {"start": v(30.41, 13.53) * mm, "end": v(30.4, 13.55) * mm});
            skLineSegment(sketch, "E11488", {"start": v(30.4, 13.55) * mm, "end": v(30.4, 13.57) * mm});
            skLineSegment(sketch, "E11489", {"start": v(30.4, 13.57) * mm, "end": v(30.38, 13.6) * mm});
            skLineSegment(sketch, "E11490", {"start": v(30.38, 13.6) * mm, "end": v(30.38, 13.63) * mm});
            skLineSegment(sketch, "E11491", {"start": v(30.38, 13.63) * mm, "end": v(30.38, 13.65) * mm});
            skLineSegment(sketch, "E11492", {"start": v(30.38, 13.65) * mm, "end": v(30.38, 13.68) * mm});
            skLineSegment(sketch, "E11493", {"start": v(30.38, 13.68) * mm, "end": v(30.39, 13.7) * mm});
            skLineSegment(sketch, "E11494", {"start": v(30.39, 13.7) * mm, "end": v(30.45, 13.87) * mm});
            skLineSegment(sketch, "E11495", {"start": v(30.45, 13.87) * mm, "end": v(30.52, 14.03) * mm});
            skLineSegment(sketch, "E11496", {"start": v(16.73, 12.55) * mm, "end": v(16.7, 12.52) * mm});
            skLineSegment(sketch, "E11497", {"start": v(16.7, 12.52) * mm, "end": v(16.67, 12.5) * mm});
            skLineSegment(sketch, "E11498", {"start": v(16.67, 12.5) * mm, "end": v(16.64, 12.47) * mm});
            skLineSegment(sketch, "E11499", {"start": v(16.64, 12.47) * mm, "end": v(16.6, 12.44) * mm});
            skLineSegment(sketch, "E11500", {"start": v(16.6, 12.44) * mm, "end": v(16.58, 12.4) * mm});
            skLineSegment(sketch, "E11501", {"start": v(16.58, 12.4) * mm, "end": v(16.57, 12.37) * mm});
            skLineSegment(sketch, "E11502", {"start": v(16.57, 12.37) * mm, "end": v(16.57, 12.34) * mm});
            skLineSegment(sketch, "E11503", {"start": v(16.57, 12.34) * mm, "end": v(16.57, 12.31) * mm});
            skLineSegment(sketch, "E11504", {"start": v(16.57, 12.31) * mm, "end": v(16.57, 12.28) * mm});
            skLineSegment(sketch, "E11505", {"start": v(16.57, 12.28) * mm, "end": v(16.58, 12.25) * mm});
            skLineSegment(sketch, "E11506", {"start": v(16.58, 12.25) * mm, "end": v(16.6, 12.23) * mm});
            skLineSegment(sketch, "E11507", {"start": v(16.6, 12.23) * mm, "end": v(16.6, 12.2) * mm});
            skLineSegment(sketch, "E11508", {"start": v(16.6, 12.2) * mm, "end": v(16.63, 12.18) * mm});
            skLineSegment(sketch, "E11509", {"start": v(16.63, 12.18) * mm, "end": v(16.65, 12.16) * mm});
            skLineSegment(sketch, "E11510", {"start": v(16.65, 12.16) * mm, "end": v(16.68, 12.13) * mm});
            skLineSegment(sketch, "E11511", {"start": v(16.68, 12.13) * mm, "end": v(16.7, 12.12) * mm});
            skLineSegment(sketch, "E11512", {"start": v(16.7, 12.12) * mm, "end": v(16.74, 12.11) * mm});
            skLineSegment(sketch, "E11513", {"start": v(16.74, 12.11) * mm, "end": v(16.77, 12.11) * mm});
            skLineSegment(sketch, "E11514", {"start": v(16.77, 12.11) * mm, "end": v(16.8, 12.11) * mm});
            skLineSegment(sketch, "E11515", {"start": v(16.8, 12.11) * mm, "end": v(16.84, 12.12) * mm});
            skLineSegment(sketch, "E11516", {"start": v(16.84, 12.12) * mm, "end": v(16.88, 12.12) * mm});
            skLineSegment(sketch, "E11517", {"start": v(16.88, 12.12) * mm, "end": v(16.91, 12.12) * mm});
            skLineSegment(sketch, "E11518", {"start": v(16.91, 12.12) * mm, "end": v(16.91, 12.12) * mm});
            skLineSegment(sketch, "E11519", {"start": v(16.91, 12.12) * mm, "end": v(16.92, 12.12) * mm});
            skLineSegment(sketch, "E11520", {"start": v(16.92, 12.12) * mm, "end": v(16.92, 12.12) * mm});
            skLineSegment(sketch, "E11521", {"start": v(16.92, 12.12) * mm, "end": v(16.93, 12.12) * mm});
            skLineSegment(sketch, "E11522", {"start": v(16.93, 12.12) * mm, "end": v(16.94, 12.12) * mm});
            skLineSegment(sketch, "E11523", {"start": v(16.94, 12.12) * mm, "end": v(16.95, 12.12) * mm});
            skLineSegment(sketch, "E11524", {"start": v(16.95, 12.12) * mm, "end": v(16.97, 12.12) * mm});
            skLineSegment(sketch, "E11525", {"start": v(16.97, 12.12) * mm, "end": v(17.03, 12.13) * mm});
            skLineSegment(sketch, "E11526", {"start": v(17.03, 12.13) * mm, "end": v(17.1, 12.14) * mm});
            skLineSegment(sketch, "E11527", {"start": v(17.1, 12.14) * mm, "end": v(17.15, 12.17) * mm});
            skLineSegment(sketch, "E11528", {"start": v(17.15, 12.17) * mm, "end": v(17.2, 12.2) * mm});
            skLineSegment(sketch, "E11529", {"start": v(17.2, 12.2) * mm, "end": v(17.23, 12.25) * mm});
            skLineSegment(sketch, "E11530", {"start": v(17.23, 12.25) * mm, "end": v(17.26, 12.3) * mm});
            skLineSegment(sketch, "E11531", {"start": v(17.26, 12.3) * mm, "end": v(17.28, 12.35) * mm});
            skLineSegment(sketch, "E11532", {"start": v(17.28, 12.35) * mm, "end": v(17.28, 12.4) * mm});
            skLineSegment(sketch, "E11533", {"start": v(17.28, 12.4) * mm, "end": v(17.28, 12.45) * mm});
            skLineSegment(sketch, "E11534", {"start": v(17.28, 12.45) * mm, "end": v(17.27, 12.5) * mm});
            skLineSegment(sketch, "E11535", {"start": v(17.27, 12.5) * mm, "end": v(17.25, 12.53) * mm});
            skLineSegment(sketch, "E11536", {"start": v(17.25, 12.53) * mm, "end": v(17.23, 12.57) * mm});
            skLineSegment(sketch, "E11537", {"start": v(17.23, 12.57) * mm, "end": v(17.2, 12.61) * mm});
            skLineSegment(sketch, "E11538", {"start": v(17.2, 12.61) * mm, "end": v(17.18, 12.65) * mm});
            skLineSegment(sketch, "E11539", {"start": v(17.18, 12.65) * mm, "end": v(17.15, 12.68) * mm});
            skLineSegment(sketch, "E11540", {"start": v(17.15, 12.68) * mm, "end": v(17.12, 12.72) * mm});
            skLineSegment(sketch, "E11541", {"start": v(17.12, 12.72) * mm, "end": v(17.1, 12.74) * mm});
            skLineSegment(sketch, "E11542", {"start": v(17.1, 12.74) * mm, "end": v(17.09, 12.75) * mm});
            skLineSegment(sketch, "E11543", {"start": v(17.09, 12.75) * mm, "end": v(17.07, 12.77) * mm});
            skLineSegment(sketch, "E11544", {"start": v(17.07, 12.77) * mm, "end": v(17.05, 12.78) * mm});
            skLineSegment(sketch, "E11545", {"start": v(17.05, 12.78) * mm, "end": v(17.03, 12.79) * mm});
            skLineSegment(sketch, "E11546", {"start": v(17.03, 12.79) * mm, "end": v(17, 12.8) * mm});
            skLineSegment(sketch, "E11547", {"start": v(17, 12.8) * mm, "end": v(16.98, 12.8) * mm});
            skLineSegment(sketch, "E11548", {"start": v(16.98, 12.8) * mm, "end": v(16.96, 12.82) * mm});
            skLineSegment(sketch, "E11549", {"start": v(16.96, 12.82) * mm, "end": v(16.96, 12.82) * mm});
            skLineSegment(sketch, "E11550", {"start": v(16.96, 12.82) * mm, "end": v(16.95, 12.82) * mm});
            skLineSegment(sketch, "E11551", {"start": v(16.95, 12.82) * mm, "end": v(16.95, 12.82) * mm});
            skLineSegment(sketch, "E11552", {"start": v(16.95, 12.82) * mm, "end": v(16.94, 12.82) * mm});
            skLineSegment(sketch, "E11553", {"start": v(16.94, 12.82) * mm, "end": v(16.94, 12.82) * mm});
            skLineSegment(sketch, "E11554", {"start": v(16.94, 12.82) * mm, "end": v(16.94, 12.83) * mm});
            skLineSegment(sketch, "E11555", {"start": v(16.94, 12.83) * mm, "end": v(16.94, 12.83) * mm});
            skLineSegment(sketch, "E11556", {"start": v(16.94, 12.83) * mm, "end": v(16.93, 12.83) * mm});
            skLineSegment(sketch, "E11557", {"start": v(16.93, 12.83) * mm, "end": v(16.92, 12.84) * mm});
            skLineSegment(sketch, "E11558", {"start": v(16.92, 12.84) * mm, "end": v(16.9, 12.84) * mm});
            skLineSegment(sketch, "E11559", {"start": v(16.9, 12.84) * mm, "end": v(16.88, 12.85) * mm});
            skLineSegment(sketch, "E11560", {"start": v(16.88, 12.85) * mm, "end": v(16.86, 12.86) * mm});
            skLineSegment(sketch, "E11561", {"start": v(16.86, 12.86) * mm, "end": v(16.85, 12.87) * mm});
            skLineSegment(sketch, "E11562", {"start": v(16.85, 12.87) * mm, "end": v(16.83, 12.88) * mm});
            skLineSegment(sketch, "E11563", {"start": v(16.83, 12.88) * mm, "end": v(16.81, 12.89) * mm});
            skLineSegment(sketch, "E11564", {"start": v(16.81, 12.89) * mm, "end": v(16.8, 12.9) * mm});
            skLineSegment(sketch, "E11565", {"start": v(16.8, 12.9) * mm, "end": v(16.78, 12.9) * mm});
            skLineSegment(sketch, "E11566", {"start": v(16.78, 12.9) * mm, "end": v(16.77, 12.9) * mm});
            skLineSegment(sketch, "E11567", {"start": v(16.77, 12.9) * mm, "end": v(16.76, 12.89) * mm});
            skLineSegment(sketch, "E11568", {"start": v(16.76, 12.89) * mm, "end": v(16.75, 12.88) * mm});
            skLineSegment(sketch, "E11569", {"start": v(16.75, 12.88) * mm, "end": v(16.74, 12.87) * mm});
            skLineSegment(sketch, "E11570", {"start": v(16.74, 12.87) * mm, "end": v(16.74, 12.86) * mm});
            skLineSegment(sketch, "E11571", {"start": v(16.74, 12.86) * mm, "end": v(16.74, 12.84) * mm});
            skLineSegment(sketch, "E11572", {"start": v(16.74, 12.84) * mm, "end": v(16.74, 12.82) * mm});
            skLineSegment(sketch, "E11573", {"start": v(16.74, 12.82) * mm, "end": v(16.75, 12.8) * mm});
            skLineSegment(sketch, "E11574", {"start": v(16.75, 12.8) * mm, "end": v(16.75, 12.77) * mm});
            skLineSegment(sketch, "E11575", {"start": v(16.75, 12.77) * mm, "end": v(16.75, 12.74) * mm});
            skLineSegment(sketch, "E11576", {"start": v(16.75, 12.74) * mm, "end": v(16.75, 12.7) * mm});
            skLineSegment(sketch, "E11577", {"start": v(16.75, 12.7) * mm, "end": v(16.75, 12.68) * mm});
            skLineSegment(sketch, "E11578", {"start": v(16.75, 12.68) * mm, "end": v(16.76, 12.65) * mm});
            skLineSegment(sketch, "E11579", {"start": v(16.76, 12.65) * mm, "end": v(16.76, 12.62) * mm});
            skLineSegment(sketch, "E11580", {"start": v(16.76, 12.62) * mm, "end": v(16.75, 12.58) * mm});
            skLineSegment(sketch, "E11581", {"start": v(16.75, 12.58) * mm, "end": v(16.73, 12.55) * mm});
            skLineSegment(sketch, "E11582", {"start": v(17.83, 17.81) * mm, "end": v(17.83, 17.77) * mm});
            skLineSegment(sketch, "E11583", {"start": v(17.83, 17.77) * mm, "end": v(17.84, 17.74) * mm});
            skLineSegment(sketch, "E11584", {"start": v(17.84, 17.74) * mm, "end": v(17.85, 17.7) * mm});
            skLineSegment(sketch, "E11585", {"start": v(17.85, 17.7) * mm, "end": v(17.86, 17.67) * mm});
            skLineSegment(sketch, "E11586", {"start": v(17.86, 17.67) * mm, "end": v(17.86, 17.64) * mm});
            skLineSegment(sketch, "E11587", {"start": v(17.86, 17.64) * mm, "end": v(17.87, 17.6) * mm});
            skLineSegment(sketch, "E11588", {"start": v(17.87, 17.6) * mm, "end": v(17.87, 17.57) * mm});
            skLineSegment(sketch, "E11589", {"start": v(17.87, 17.57) * mm, "end": v(17.87, 17.54) * mm});
            skLineSegment(sketch, "E11590", {"start": v(17.87, 17.54) * mm, "end": v(17.88, 17.51) * mm});
            skLineSegment(sketch, "E11591", {"start": v(17.88, 17.51) * mm, "end": v(17.88, 17.48) * mm});
            skLineSegment(sketch, "E11592", {"start": v(17.88, 17.48) * mm, "end": v(17.88, 17.46) * mm});
            skLineSegment(sketch, "E11593", {"start": v(17.88, 17.46) * mm, "end": v(17.88, 17.43) * mm});
            skLineSegment(sketch, "E11594", {"start": v(17.88, 17.43) * mm, "end": v(17.88, 17.4) * mm});
            skLineSegment(sketch, "E11595", {"start": v(17.88, 17.4) * mm, "end": v(17.88, 17.38) * mm});
            skLineSegment(sketch, "E11596", {"start": v(17.88, 17.38) * mm, "end": v(17.88, 17.35) * mm});
            skLineSegment(sketch, "E11597", {"start": v(17.88, 17.35) * mm, "end": v(17.88, 17.32) * mm});
            skLineSegment(sketch, "E11598", {"start": v(17.88, 17.32) * mm, "end": v(17.88, 17.3) * mm});
            skLineSegment(sketch, "E11599", {"start": v(17.88, 17.3) * mm, "end": v(17.88, 17.27) * mm});
            skLineSegment(sketch, "E11600", {"start": v(17.88, 17.27) * mm, "end": v(17.87, 17.22) * mm});
            skLineSegment(sketch, "E11601", {"start": v(17.87, 17.22) * mm, "end": v(17.87, 17.17) * mm});
            skLineSegment(sketch, "E11602", {"start": v(17.87, 17.17) * mm, "end": v(17.87, 17.11) * mm});
            skLineSegment(sketch, "E11603", {"start": v(17.87, 17.11) * mm, "end": v(17.87, 17.06) * mm});
            skLineSegment(sketch, "E11604", {"start": v(17.87, 17.06) * mm, "end": v(17.87, 17) * mm});
            skLineSegment(sketch, "E11605", {"start": v(17.87, 17) * mm, "end": v(17.88, 16.96) * mm});
            skLineSegment(sketch, "E11606", {"start": v(17.88, 16.96) * mm, "end": v(17.89, 16.9) * mm});
            skLineSegment(sketch, "E11607", {"start": v(17.89, 16.9) * mm, "end": v(17.9, 16.85) * mm});
            skLineSegment(sketch, "E11608", {"start": v(17.9, 16.85) * mm, "end": v(17.9, 16.8) * mm});
            skLineSegment(sketch, "E11609", {"start": v(17.9, 16.8) * mm, "end": v(17.92, 16.74) * mm});
            skLineSegment(sketch, "E11610", {"start": v(17.92, 16.74) * mm, "end": v(17.94, 16.68) * mm});
            skLineSegment(sketch, "E11611", {"start": v(17.94, 16.68) * mm, "end": v(17.95, 16.63) * mm});
            skLineSegment(sketch, "E11612", {"start": v(17.95, 16.63) * mm, "end": v(17.97, 16.57) * mm});
            skLineSegment(sketch, "E11613", {"start": v(17.97, 16.57) * mm, "end": v(18, 16.52) * mm});
            skLineSegment(sketch, "E11614", {"start": v(18, 16.52) * mm, "end": v(18.01, 16.47) * mm});
            skLineSegment(sketch, "E11615", {"start": v(18.01, 16.47) * mm, "end": v(18.03, 16.41) * mm});
            skLineSegment(sketch, "E11616", {"start": v(18.03, 16.41) * mm, "end": v(18.04, 16.38) * mm});
            skLineSegment(sketch, "E11617", {"start": v(18.04, 16.38) * mm, "end": v(18.06, 16.34) * mm});
            skLineSegment(sketch, "E11618", {"start": v(18.06, 16.34) * mm, "end": v(18.07, 16.3) * mm});
            skLineSegment(sketch, "E11619", {"start": v(18.07, 16.3) * mm, "end": v(18.08, 16.27) * mm});
            skLineSegment(sketch, "E11620", {"start": v(18.08, 16.27) * mm, "end": v(18.1, 16.23) * mm});
            skLineSegment(sketch, "E11621", {"start": v(18.1, 16.23) * mm, "end": v(18.1, 16.2) * mm});
            skLineSegment(sketch, "E11622", {"start": v(18.1, 16.2) * mm, "end": v(18.12, 16.16) * mm});
            skLineSegment(sketch, "E11623", {"start": v(18.12, 16.16) * mm, "end": v(18.13, 16.13) * mm});
            skLineSegment(sketch, "E11624", {"start": v(18.13, 16.13) * mm, "end": v(18.15, 16.07) * mm});
            skLineSegment(sketch, "E11625", {"start": v(18.15, 16.07) * mm, "end": v(18.16, 16.02) * mm});
            skLineSegment(sketch, "E11626", {"start": v(18.16, 16.02) * mm, "end": v(18.17, 16) * mm});
            skLineSegment(sketch, "E11627", {"start": v(18.17, 16) * mm, "end": v(18.17, 15.97) * mm});
            skLineSegment(sketch, "E11628", {"start": v(18.17, 15.97) * mm, "end": v(18.18, 15.96) * mm});
            skLineSegment(sketch, "E11629", {"start": v(18.18, 15.96) * mm, "end": v(18.18, 15.95) * mm});
            skLineSegment(sketch, "E11630", {"start": v(18.18, 15.95) * mm, "end": v(18.18, 15.95) * mm});
            skLineSegment(sketch, "E11631", {"start": v(18.18, 15.95) * mm, "end": v(18.24, 15.9) * mm});
            skLineSegment(sketch, "E11632", {"start": v(18.24, 15.9) * mm, "end": v(18.3, 15.85) * mm});
            skLineSegment(sketch, "E11633", {"start": v(18.3, 15.85) * mm, "end": v(18.34, 15.8) * mm});
            skLineSegment(sketch, "E11634", {"start": v(18.34, 15.8) * mm, "end": v(18.4, 15.76) * mm});
            skLineSegment(sketch, "E11635", {"start": v(18.4, 15.76) * mm, "end": v(18.44, 15.72) * mm});
            skLineSegment(sketch, "E11636", {"start": v(18.44, 15.72) * mm, "end": v(18.47, 15.69) * mm});
            skLineSegment(sketch, "E11637", {"start": v(18.47, 15.69) * mm, "end": v(18.5, 15.66) * mm});
            skLineSegment(sketch, "E11638", {"start": v(18.5, 15.66) * mm, "end": v(18.52, 15.65) * mm});
            skLineSegment(sketch, "E11639", {"start": v(18.52, 15.65) * mm, "end": v(18.54, 15.64) * mm});
            skLineSegment(sketch, "E11640", {"start": v(18.54, 15.64) * mm, "end": v(18.57, 15.62) * mm});
            skLineSegment(sketch, "E11641", {"start": v(18.57, 15.62) * mm, "end": v(18.6, 15.6) * mm});
            skLineSegment(sketch, "E11642", {"start": v(18.6, 15.6) * mm, "end": v(18.63, 15.57) * mm});
            skLineSegment(sketch, "E11643", {"start": v(18.63, 15.57) * mm, "end": v(18.67, 15.55) * mm});
            skLineSegment(sketch, "E11644", {"start": v(18.67, 15.55) * mm, "end": v(18.71, 15.52) * mm});
            skLineSegment(sketch, "E11645", {"start": v(18.71, 15.52) * mm, "end": v(18.76, 15.49) * mm});
            skLineSegment(sketch, "E11646", {"start": v(18.76, 15.49) * mm, "end": v(18.8, 15.46) * mm});
            skLineSegment(sketch, "E11647", {"start": v(18.8, 15.46) * mm, "end": v(18.8, 15.46) * mm});
            skLineSegment(sketch, "E11648", {"start": v(18.8, 15.46) * mm, "end": v(18.8, 15.45) * mm});
            skLineSegment(sketch, "E11649", {"start": v(18.8, 15.45) * mm, "end": v(18.81, 15.45) * mm});
            skLineSegment(sketch, "E11650", {"start": v(18.81, 15.45) * mm, "end": v(18.82, 15.44) * mm});
            skLineSegment(sketch, "E11651", {"start": v(18.82, 15.44) * mm, "end": v(18.84, 15.43) * mm});
            skLineSegment(sketch, "E11652", {"start": v(18.84, 15.43) * mm, "end": v(18.87, 15.41) * mm});
            skLineSegment(sketch, "E11653", {"start": v(18.87, 15.41) * mm, "end": v(18.9, 15.4) * mm});
            skLineSegment(sketch, "E11654", {"start": v(18.9, 15.4) * mm, "end": v(18.93, 15.37) * mm});
            skLineSegment(sketch, "E11655", {"start": v(18.93, 15.37) * mm, "end": v(18.95, 15.36) * mm});
            skLineSegment(sketch, "E11656", {"start": v(18.95, 15.36) * mm, "end": v(18.98, 15.34) * mm});
            skLineSegment(sketch, "E11657", {"start": v(18.98, 15.34) * mm, "end": v(19, 15.33) * mm});
            skLineSegment(sketch, "E11658", {"start": v(19, 15.33) * mm, "end": v(19.03, 15.3) * mm});
            skLineSegment(sketch, "E11659", {"start": v(19.03, 15.3) * mm, "end": v(19.06, 15.3) * mm});
            skLineSegment(sketch, "E11660", {"start": v(19.06, 15.3) * mm, "end": v(19.09, 15.28) * mm});
            skLineSegment(sketch, "E11661", {"start": v(19.09, 15.28) * mm, "end": v(19.11, 15.26) * mm});
            skLineSegment(sketch, "E11662", {"start": v(19.11, 15.26) * mm, "end": v(19.14, 15.24) * mm});
            skLineSegment(sketch, "E11663", {"start": v(19.14, 15.24) * mm, "end": v(19.18, 15.22) * mm});
            skLineSegment(sketch, "E11664", {"start": v(19.18, 15.22) * mm, "end": v(19.2, 15.2) * mm});
            skLineSegment(sketch, "E11665", {"start": v(19.2, 15.2) * mm, "end": v(19.24, 15.18) * mm});
            skLineSegment(sketch, "E11666", {"start": v(19.24, 15.18) * mm, "end": v(19.27, 15.17) * mm});
            skLineSegment(sketch, "E11667", {"start": v(19.27, 15.17) * mm, "end": v(19.3, 15.15) * mm});
            skLineSegment(sketch, "E11668", {"start": v(19.3, 15.15) * mm, "end": v(19.33, 15.12) * mm});
            skLineSegment(sketch, "E11669", {"start": v(19.33, 15.12) * mm, "end": v(19.37, 15.1) * mm});
            skLineSegment(sketch, "E11670", {"start": v(19.37, 15.1) * mm, "end": v(19.38, 15.1) * mm});
            skLineSegment(sketch, "E11671", {"start": v(19.38, 15.1) * mm, "end": v(19.4, 15.08) * mm});
            skLineSegment(sketch, "E11672", {"start": v(19.4, 15.08) * mm, "end": v(19.42, 15.07) * mm});
            skLineSegment(sketch, "E11673", {"start": v(19.42, 15.07) * mm, "end": v(19.44, 15.06) * mm});
            skLineSegment(sketch, "E11674", {"start": v(19.44, 15.06) * mm, "end": v(19.46, 15.06) * mm});
            skLineSegment(sketch, "E11675", {"start": v(19.46, 15.06) * mm, "end": v(19.48, 15.06) * mm});
            skLineSegment(sketch, "E11676", {"start": v(19.48, 15.06) * mm, "end": v(19.5, 15.05) * mm});
            skLineSegment(sketch, "E11677", {"start": v(19.5, 15.05) * mm, "end": v(19.51, 15.05) * mm});
            skLineSegment(sketch, "E11678", {"start": v(19.51, 15.05) * mm, "end": v(19.53, 15.05) * mm});
            skLineSegment(sketch, "E11679", {"start": v(19.53, 15.05) * mm, "end": v(19.54, 15.05) * mm});
            skLineSegment(sketch, "E11680", {"start": v(19.54, 15.05) * mm, "end": v(19.55, 15.05) * mm});
            skLineSegment(sketch, "E11681", {"start": v(19.55, 15.05) * mm, "end": v(19.56, 15.05) * mm});
            skLineSegment(sketch, "E11682", {"start": v(19.56, 15.05) * mm, "end": v(19.56, 15.05) * mm});
            skLineSegment(sketch, "E11683", {"start": v(19.56, 15.05) * mm, "end": v(19.6, 15.1) * mm});
            skLineSegment(sketch, "E11684", {"start": v(19.6, 15.1) * mm, "end": v(19.63, 15.13) * mm});
            skLineSegment(sketch, "E11685", {"start": v(19.63, 15.13) * mm, "end": v(19.65, 15.18) * mm});
            skLineSegment(sketch, "E11686", {"start": v(19.65, 15.18) * mm, "end": v(19.68, 15.22) * mm});
            skLineSegment(sketch, "E11687", {"start": v(19.68, 15.22) * mm, "end": v(19.7, 15.25) * mm});
            skLineSegment(sketch, "E11688", {"start": v(19.7, 15.25) * mm, "end": v(19.72, 15.29) * mm});
            skLineSegment(sketch, "E11689", {"start": v(19.72, 15.29) * mm, "end": v(19.74, 15.32) * mm});
            skLineSegment(sketch, "E11690", {"start": v(19.74, 15.32) * mm, "end": v(19.75, 15.34) * mm});
            skLineSegment(sketch, "E11691", {"start": v(19.75, 15.34) * mm, "end": v(19.75, 15.37) * mm});
            skLineSegment(sketch, "E11692", {"start": v(19.75, 15.37) * mm, "end": v(19.77, 15.41) * mm});
            skLineSegment(sketch, "E11693", {"start": v(19.77, 15.41) * mm, "end": v(19.78, 15.48) * mm});
            skLineSegment(sketch, "E11694", {"start": v(19.78, 15.48) * mm, "end": v(19.8, 15.55) * mm});
            skLineSegment(sketch, "E11695", {"start": v(19.8, 15.55) * mm, "end": v(19.83, 15.64) * mm});
            skLineSegment(sketch, "E11696", {"start": v(19.83, 15.64) * mm, "end": v(19.85, 15.73) * mm});
            skLineSegment(sketch, "E11697", {"start": v(19.85, 15.73) * mm, "end": v(19.88, 15.83) * mm});
            skLineSegment(sketch, "E11698", {"start": v(19.88, 15.83) * mm, "end": v(19.9, 15.94) * mm});
            skLineSegment(sketch, "E11699", {"start": v(19.9, 15.94) * mm, "end": v(19.9, 15.94) * mm});
            skLineSegment(sketch, "E11700", {"start": v(19.9, 15.94) * mm, "end": v(19.91, 15.95) * mm});
            skLineSegment(sketch, "E11701", {"start": v(19.91, 15.95) * mm, "end": v(19.91, 15.97) * mm});
            skLineSegment(sketch, "E11702", {"start": v(19.91, 15.97) * mm, "end": v(19.92, 16) * mm});
            skLineSegment(sketch, "E11703", {"start": v(19.92, 16) * mm, "end": v(19.92, 16.05) * mm});
            skLineSegment(sketch, "E11704", {"start": v(19.92, 16.05) * mm, "end": v(19.93, 16.11) * mm});
            skLineSegment(sketch, "E11705", {"start": v(19.93, 16.11) * mm, "end": v(19.94, 16.2) * mm});
            skLineSegment(sketch, "E11706", {"start": v(19.94, 16.2) * mm, "end": v(19.94, 16.28) * mm});
            skLineSegment(sketch, "E11707", {"start": v(19.94, 16.28) * mm, "end": v(19.94, 16.36) * mm});
            skLineSegment(sketch, "E11708", {"start": v(19.94, 16.36) * mm, "end": v(19.94, 16.43) * mm});
            skLineSegment(sketch, "E11709", {"start": v(19.94, 16.43) * mm, "end": v(19.94, 16.51) * mm});
            skLineSegment(sketch, "E11710", {"start": v(19.94, 16.51) * mm, "end": v(19.93, 16.59) * mm});
            skLineSegment(sketch, "E11711", {"start": v(19.93, 16.59) * mm, "end": v(19.92, 16.66) * mm});
            skLineSegment(sketch, "E11712", {"start": v(19.92, 16.66) * mm, "end": v(19.9, 16.74) * mm});
            skLineSegment(sketch, "E11713", {"start": v(19.9, 16.74) * mm, "end": v(19.9, 16.82) * mm});
            skLineSegment(sketch, "E11714", {"start": v(19.9, 16.82) * mm, "end": v(19.9, 16.84) * mm});
            skLineSegment(sketch, "E11715", {"start": v(19.9, 16.84) * mm, "end": v(19.9, 16.86) * mm});
            skLineSegment(sketch, "E11716", {"start": v(19.9, 16.86) * mm, "end": v(19.9, 16.87) * mm});
            skLineSegment(sketch, "E11717", {"start": v(19.9, 16.87) * mm, "end": v(19.9, 16.88) * mm});
            skLineSegment(sketch, "E11718", {"start": v(19.9, 16.88) * mm, "end": v(19.9, 16.88) * mm});
            skLineSegment(sketch, "E11719", {"start": v(19.9, 16.88) * mm, "end": v(19.9, 16.89) * mm});
            skLineSegment(sketch, "E11720", {"start": v(19.9, 16.89) * mm, "end": v(19.9, 16.89) * mm});
            skLineSegment(sketch, "E11721", {"start": v(19.9, 16.89) * mm, "end": v(19.89, 16.91) * mm});
            skLineSegment(sketch, "E11722", {"start": v(19.89, 16.91) * mm, "end": v(19.88, 16.94) * mm});
            skLineSegment(sketch, "E11723", {"start": v(19.88, 16.94) * mm, "end": v(19.88, 16.96) * mm});
            skLineSegment(sketch, "E11724", {"start": v(19.88, 16.96) * mm, "end": v(19.88, 16.98) * mm});
            skLineSegment(sketch, "E11725", {"start": v(19.88, 16.98) * mm, "end": v(19.88, 17) * mm});
            skLineSegment(sketch, "E11726", {"start": v(19.88, 17) * mm, "end": v(19.87, 17.02) * mm});
            skLineSegment(sketch, "E11727", {"start": v(19.87, 17.02) * mm, "end": v(19.87, 17.03) * mm});
            skLineSegment(sketch, "E11728", {"start": v(19.87, 17.03) * mm, "end": v(19.87, 17.03) * mm});
            skLineSegment(sketch, "E11729", {"start": v(19.87, 17.03) * mm, "end": v(19.87, 17.04) * mm});
            skLineSegment(sketch, "E11730", {"start": v(19.87, 17.04) * mm, "end": v(19.87, 17.05) * mm});
            skLineSegment(sketch, "E11731", {"start": v(19.87, 17.05) * mm, "end": v(19.87, 17.07) * mm});
            skLineSegment(sketch, "E11732", {"start": v(19.87, 17.07) * mm, "end": v(19.86, 17.1) * mm});
            skLineSegment(sketch, "E11733", {"start": v(19.86, 17.1) * mm, "end": v(19.86, 17.14) * mm});
            skLineSegment(sketch, "E11734", {"start": v(19.86, 17.14) * mm, "end": v(19.86, 17.17) * mm});
            skLineSegment(sketch, "E11735", {"start": v(19.86, 17.17) * mm, "end": v(19.85, 17.22) * mm});
            skLineSegment(sketch, "E11736", {"start": v(19.85, 17.22) * mm, "end": v(19.85, 17.26) * mm});
            skLineSegment(sketch, "E11737", {"start": v(19.85, 17.26) * mm, "end": v(19.85, 17.26) * mm});
            skLineSegment(sketch, "E11738", {"start": v(19.85, 17.26) * mm, "end": v(19.84, 17.26) * mm});
            skLineSegment(sketch, "E11739", {"start": v(19.84, 17.26) * mm, "end": v(19.84, 17.27) * mm});
            skLineSegment(sketch, "E11740", {"start": v(19.84, 17.27) * mm, "end": v(19.83, 17.28) * mm});
            skLineSegment(sketch, "E11741", {"start": v(19.83, 17.28) * mm, "end": v(19.82, 17.3) * mm});
            skLineSegment(sketch, "E11742", {"start": v(19.82, 17.3) * mm, "end": v(19.8, 17.32) * mm});
            skLineSegment(sketch, "E11743", {"start": v(19.8, 17.32) * mm, "end": v(19.78, 17.35) * mm});
            skLineSegment(sketch, "E11744", {"start": v(19.78, 17.35) * mm, "end": v(19.76, 17.38) * mm});
            skLineSegment(sketch, "E11745", {"start": v(19.76, 17.38) * mm, "end": v(19.73, 17.41) * mm});
            skLineSegment(sketch, "E11746", {"start": v(19.73, 17.41) * mm, "end": v(19.7, 17.44) * mm});
            skLineSegment(sketch, "E11747", {"start": v(19.7, 17.44) * mm, "end": v(19.67, 17.47) * mm});
            skLineSegment(sketch, "E11748", {"start": v(19.67, 17.47) * mm, "end": v(19.64, 17.5) * mm});
            skLineSegment(sketch, "E11749", {"start": v(19.64, 17.5) * mm, "end": v(19.61, 17.53) * mm});
            skLineSegment(sketch, "E11750", {"start": v(19.61, 17.53) * mm, "end": v(19.58, 17.56) * mm});
            skLineSegment(sketch, "E11751", {"start": v(19.58, 17.56) * mm, "end": v(19.55, 17.58) * mm});
            skLineSegment(sketch, "E11752", {"start": v(19.55, 17.58) * mm, "end": v(19.54, 17.6) * mm});
            skLineSegment(sketch, "E11753", {"start": v(19.54, 17.6) * mm, "end": v(19.52, 17.6) * mm});
            skLineSegment(sketch, "E11754", {"start": v(19.52, 17.6) * mm, "end": v(19.5, 17.62) * mm});
            skLineSegment(sketch, "E11755", {"start": v(19.5, 17.62) * mm, "end": v(19.5, 17.63) * mm});
            skLineSegment(sketch, "E11756", {"start": v(19.5, 17.63) * mm, "end": v(19.48, 17.64) * mm});
            skLineSegment(sketch, "E11757", {"start": v(19.48, 17.64) * mm, "end": v(19.47, 17.65) * mm});
            skLineSegment(sketch, "E11758", {"start": v(19.47, 17.65) * mm, "end": v(19.46, 17.67) * mm});
            skLineSegment(sketch, "E11759", {"start": v(19.46, 17.67) * mm, "end": v(19.44, 17.68) * mm});
            skLineSegment(sketch, "E11760", {"start": v(19.44, 17.68) * mm, "end": v(19.33, 17.78) * mm});
            skLineSegment(sketch, "E11761", {"start": v(19.33, 17.78) * mm, "end": v(19.2, 17.86) * mm});
            skLineSegment(sketch, "E11762", {"start": v(19.2, 17.86) * mm, "end": v(19.08, 17.92) * mm});
            skLineSegment(sketch, "E11763", {"start": v(19.08, 17.92) * mm, "end": v(18.95, 17.97) * mm});
            skLineSegment(sketch, "E11764", {"start": v(18.95, 17.97) * mm, "end": v(18.82, 18) * mm});
            skLineSegment(sketch, "E11765", {"start": v(18.82, 18) * mm, "end": v(18.7, 18.04) * mm});
            skLineSegment(sketch, "E11766", {"start": v(18.7, 18.04) * mm, "end": v(18.56, 18.06) * mm});
            skLineSegment(sketch, "E11767", {"start": v(18.56, 18.06) * mm, "end": v(18.44, 18.09) * mm});
            skLineSegment(sketch, "E11768", {"start": v(18.44, 18.09) * mm, "end": v(18.41, 18.1) * mm});
            skLineSegment(sketch, "E11769", {"start": v(18.41, 18.1) * mm, "end": v(18.4, 18.1) * mm});
            skLineSegment(sketch, "E11770", {"start": v(18.4, 18.1) * mm, "end": v(18.38, 18.1) * mm});
            skLineSegment(sketch, "E11771", {"start": v(18.38, 18.1) * mm, "end": v(18.37, 18.1) * mm});
            skLineSegment(sketch, "E11772", {"start": v(18.37, 18.1) * mm, "end": v(18.36, 18.1) * mm});
            skLineSegment(sketch, "E11773", {"start": v(18.36, 18.1) * mm, "end": v(18.36, 18.1) * mm});
            skLineSegment(sketch, "E11774", {"start": v(18.36, 18.1) * mm, "end": v(18.33, 18.1) * mm});
            skLineSegment(sketch, "E11775", {"start": v(18.33, 18.1) * mm, "end": v(18.3, 18.11) * mm});
            skLineSegment(sketch, "E11776", {"start": v(18.3, 18.11) * mm, "end": v(18.27, 18.12) * mm});
            skLineSegment(sketch, "E11777", {"start": v(18.27, 18.12) * mm, "end": v(18.25, 18.12) * mm});
            skLineSegment(sketch, "E11778", {"start": v(18.25, 18.12) * mm, "end": v(18.23, 18.12) * mm});
            skLineSegment(sketch, "E11779", {"start": v(18.23, 18.12) * mm, "end": v(18.21, 18.13) * mm});
            skLineSegment(sketch, "E11780", {"start": v(18.21, 18.13) * mm, "end": v(18.2, 18.13) * mm});
            skLineSegment(sketch, "E11781", {"start": v(18.2, 18.13) * mm, "end": v(18.2, 18.13) * mm});
            skLineSegment(sketch, "E11782", {"start": v(18.2, 18.13) * mm, "end": v(18.19, 18.13) * mm});
            skLineSegment(sketch, "E11783", {"start": v(18.19, 18.13) * mm, "end": v(18.17, 18.13) * mm});
            skLineSegment(sketch, "E11784", {"start": v(18.17, 18.13) * mm, "end": v(18.15, 18.13) * mm});
            skLineSegment(sketch, "E11785", {"start": v(18.15, 18.13) * mm, "end": v(18.11, 18.13) * mm});
            skLineSegment(sketch, "E11786", {"start": v(18.11, 18.13) * mm, "end": v(18.08, 18.12) * mm});
            skLineSegment(sketch, "E11787", {"start": v(18.08, 18.12) * mm, "end": v(18.04, 18.12) * mm});
            skLineSegment(sketch, "E11788", {"start": v(18.04, 18.12) * mm, "end": v(18, 18.12) * mm});
            skLineSegment(sketch, "E11789", {"start": v(18, 18.12) * mm, "end": v(17.95, 18.12) * mm});
            skLineSegment(sketch, "E11790", {"start": v(17.95, 18.12) * mm, "end": v(17.95, 18.12) * mm});
            skLineSegment(sketch, "E11791", {"start": v(17.95, 18.12) * mm, "end": v(17.94, 18.11) * mm});
            skLineSegment(sketch, "E11792", {"start": v(17.94, 18.11) * mm, "end": v(17.94, 18.1) * mm});
            skLineSegment(sketch, "E11793", {"start": v(17.94, 18.1) * mm, "end": v(17.93, 18.1) * mm});
            skLineSegment(sketch, "E11794", {"start": v(17.93, 18.1) * mm, "end": v(17.92, 18.08) * mm});
            skLineSegment(sketch, "E11795", {"start": v(17.92, 18.08) * mm, "end": v(17.9, 18.06) * mm});
            skLineSegment(sketch, "E11796", {"start": v(17.9, 18.06) * mm, "end": v(17.87, 18.03) * mm});
            skLineSegment(sketch, "E11797", {"start": v(17.87, 18.03) * mm, "end": v(17.85, 18) * mm});
            skLineSegment(sketch, "E11798", {"start": v(17.85, 18) * mm, "end": v(17.84, 17.96) * mm});
            skLineSegment(sketch, "E11799", {"start": v(17.84, 17.96) * mm, "end": v(17.83, 17.92) * mm});
            skLineSegment(sketch, "E11800", {"start": v(17.83, 17.92) * mm, "end": v(17.82, 17.88) * mm});
            skLineSegment(sketch, "E11801", {"start": v(17.82, 17.88) * mm, "end": v(17.82, 17.85) * mm});
            skLineSegment(sketch, "E11802", {"start": v(17.82, 17.85) * mm, "end": v(17.83, 17.81) * mm});
            skLineSegment(sketch, "E11803", {"start": v(18.4, 17) * mm, "end": v(18.41, 17.1) * mm});
            skLineSegment(sketch, "E11804", {"start": v(18.41, 17.1) * mm, "end": v(18.43, 17.21) * mm});
            skLineSegment(sketch, "E11805", {"start": v(18.43, 17.21) * mm, "end": v(18.46, 17.32) * mm});
            skLineSegment(sketch, "E11806", {"start": v(18.46, 17.32) * mm, "end": v(18.47, 17.34) * mm});
            skLineSegment(sketch, "E11807", {"start": v(18.47, 17.34) * mm, "end": v(18.49, 17.36) * mm});
            skLineSegment(sketch, "E11808", {"start": v(18.49, 17.36) * mm, "end": v(18.51, 17.38) * mm});
            skLineSegment(sketch, "E11809", {"start": v(18.51, 17.38) * mm, "end": v(18.54, 17.4) * mm});
            skLineSegment(sketch, "E11810", {"start": v(18.54, 17.4) * mm, "end": v(18.57, 17.4) * mm});
            skLineSegment(sketch, "E11811", {"start": v(18.57, 17.4) * mm, "end": v(18.6, 17.42) * mm});
            skLineSegment(sketch, "E11812", {"start": v(18.6, 17.42) * mm, "end": v(18.64, 17.42) * mm});
            skLineSegment(sketch, "E11813", {"start": v(18.64, 17.42) * mm, "end": v(18.68, 17.43) * mm});
            skLineSegment(sketch, "E11814", {"start": v(18.68, 17.43) * mm, "end": v(18.7, 17.42) * mm});
            skLineSegment(sketch, "E11815", {"start": v(18.7, 17.42) * mm, "end": v(18.7, 17.42) * mm});
            skLineSegment(sketch, "E11816", {"start": v(18.7, 17.42) * mm, "end": v(18.72, 17.42) * mm});
            skLineSegment(sketch, "E11817", {"start": v(18.72, 17.42) * mm, "end": v(18.73, 17.42) * mm});
            skLineSegment(sketch, "E11818", {"start": v(18.73, 17.42) * mm, "end": v(18.74, 17.42) * mm});
            skLineSegment(sketch, "E11819", {"start": v(18.74, 17.42) * mm, "end": v(18.75, 17.41) * mm});
            skLineSegment(sketch, "E11820", {"start": v(18.75, 17.41) * mm, "end": v(18.76, 17.4) * mm});
            skLineSegment(sketch, "E11821", {"start": v(18.76, 17.4) * mm, "end": v(18.77, 17.4) * mm});
            skLineSegment(sketch, "E11822", {"start": v(18.77, 17.4) * mm, "end": v(18.86, 17.34) * mm});
            skLineSegment(sketch, "E11823", {"start": v(18.86, 17.34) * mm, "end": v(18.94, 17.28) * mm});
            skLineSegment(sketch, "E11824", {"start": v(18.94, 17.28) * mm, "end": v(19.02, 17.22) * mm});
            skLineSegment(sketch, "E11825", {"start": v(19.02, 17.22) * mm, "end": v(19.1, 17.15) * mm});
            skLineSegment(sketch, "E11826", {"start": v(19.1, 17.15) * mm, "end": v(19.16, 17.08) * mm});
            skLineSegment(sketch, "E11827", {"start": v(19.16, 17.08) * mm, "end": v(19.22, 17) * mm});
            skLineSegment(sketch, "E11828", {"start": v(19.22, 17) * mm, "end": v(19.27, 16.92) * mm});
            skLineSegment(sketch, "E11829", {"start": v(19.27, 16.92) * mm, "end": v(19.32, 16.84) * mm});
            skLineSegment(sketch, "E11830", {"start": v(19.32, 16.84) * mm, "end": v(19.33, 16.8) * mm});
            skLineSegment(sketch, "E11831", {"start": v(19.33, 16.8) * mm, "end": v(19.34, 16.76) * mm});
            skLineSegment(sketch, "E11832", {"start": v(19.34, 16.76) * mm, "end": v(19.36, 16.72) * mm});
            skLineSegment(sketch, "E11833", {"start": v(19.36, 16.72) * mm, "end": v(19.37, 16.68) * mm});
            skLineSegment(sketch, "E11834", {"start": v(19.37, 16.68) * mm, "end": v(19.39, 16.64) * mm});
            skLineSegment(sketch, "E11835", {"start": v(19.39, 16.64) * mm, "end": v(19.4, 16.6) * mm});
            skLineSegment(sketch, "E11836", {"start": v(19.4, 16.6) * mm, "end": v(19.41, 16.56) * mm});
            skLineSegment(sketch, "E11837", {"start": v(19.41, 16.56) * mm, "end": v(19.42, 16.52) * mm});
            skLineSegment(sketch, "E11838", {"start": v(19.42, 16.52) * mm, "end": v(19.42, 16.52) * mm});
            skLineSegment(sketch, "E11839", {"start": v(19.42, 16.52) * mm, "end": v(19.43, 16.51) * mm});
            skLineSegment(sketch, "E11840", {"start": v(19.43, 16.51) * mm, "end": v(19.43, 16.51) * mm});
            skLineSegment(sketch, "E11841", {"start": v(19.43, 16.51) * mm, "end": v(19.43, 16.5) * mm});
            skLineSegment(sketch, "E11842", {"start": v(19.43, 16.5) * mm, "end": v(19.43, 16.5) * mm});
            skLineSegment(sketch, "E11843", {"start": v(19.43, 16.5) * mm, "end": v(19.43, 16.49) * mm});
            skLineSegment(sketch, "E11844", {"start": v(19.43, 16.49) * mm, "end": v(19.43, 16.49) * mm});
            skLineSegment(sketch, "E11845", {"start": v(19.43, 16.49) * mm, "end": v(19.43, 16.48) * mm});
            skLineSegment(sketch, "E11846", {"start": v(19.43, 16.48) * mm, "end": v(19.43, 16.48) * mm});
            skLineSegment(sketch, "E11847", {"start": v(19.43, 16.48) * mm, "end": v(19.43, 16.47) * mm});
            skLineSegment(sketch, "E11848", {"start": v(19.43, 16.47) * mm, "end": v(19.43, 16.46) * mm});
            skLineSegment(sketch, "E11849", {"start": v(19.43, 16.46) * mm, "end": v(19.43, 16.46) * mm});
            skLineSegment(sketch, "E11850", {"start": v(19.43, 16.46) * mm, "end": v(19.43, 16.45) * mm});
            skLineSegment(sketch, "E11851", {"start": v(19.43, 16.45) * mm, "end": v(19.43, 16.44) * mm});
            skLineSegment(sketch, "E11852", {"start": v(19.43, 16.44) * mm, "end": v(19.43, 16.43) * mm});
            skLineSegment(sketch, "E11853", {"start": v(19.43, 16.43) * mm, "end": v(19.44, 16.41) * mm});
            skLineSegment(sketch, "E11854", {"start": v(19.44, 16.41) * mm, "end": v(19.44, 16.4) * mm});
            skLineSegment(sketch, "E11855", {"start": v(19.44, 16.4) * mm, "end": v(19.44, 16.38) * mm});
            skLineSegment(sketch, "E11856", {"start": v(19.44, 16.38) * mm, "end": v(19.44, 16.37) * mm});
            skLineSegment(sketch, "E11857", {"start": v(19.44, 16.37) * mm, "end": v(19.44, 16.35) * mm});
            skLineSegment(sketch, "E11858", {"start": v(19.44, 16.35) * mm, "end": v(19.44, 16.33) * mm});
            skLineSegment(sketch, "E11859", {"start": v(19.44, 16.33) * mm, "end": v(19.44, 16.32) * mm});
            skLineSegment(sketch, "E11860", {"start": v(19.44, 16.32) * mm, "end": v(19.44, 16.32) * mm});
            skLineSegment(sketch, "E11861", {"start": v(19.44, 16.32) * mm, "end": v(19.44, 16.31) * mm});
            skLineSegment(sketch, "E11862", {"start": v(19.44, 16.31) * mm, "end": v(19.44, 16.3) * mm});
            skLineSegment(sketch, "E11863", {"start": v(19.44, 16.3) * mm, "end": v(19.44, 16.3) * mm});
            skLineSegment(sketch, "E11864", {"start": v(19.44, 16.3) * mm, "end": v(19.44, 16.28) * mm});
            skLineSegment(sketch, "E11865", {"start": v(19.44, 16.28) * mm, "end": v(19.45, 16.25) * mm});
            skLineSegment(sketch, "E11866", {"start": v(19.45, 16.25) * mm, "end": v(19.45, 16.21) * mm});
            skLineSegment(sketch, "E11867", {"start": v(19.45, 16.21) * mm, "end": v(19.45, 16.18) * mm});
            skLineSegment(sketch, "E11868", {"start": v(19.45, 16.18) * mm, "end": v(19.45, 16.15) * mm});
            skLineSegment(sketch, "E11869", {"start": v(19.45, 16.15) * mm, "end": v(19.46, 16.11) * mm});
            skLineSegment(sketch, "E11870", {"start": v(19.46, 16.11) * mm, "end": v(19.46, 16.08) * mm});
            skLineSegment(sketch, "E11871", {"start": v(19.46, 16.08) * mm, "end": v(19.47, 16.05) * mm});
            skLineSegment(sketch, "E11872", {"start": v(19.47, 16.05) * mm, "end": v(19.47, 16.01) * mm});
            skLineSegment(sketch, "E11873", {"start": v(19.47, 16.01) * mm, "end": v(19.47, 16) * mm});
            skLineSegment(sketch, "E11874", {"start": v(19.47, 16) * mm, "end": v(19.47, 15.99) * mm});
            skLineSegment(sketch, "E11875", {"start": v(19.47, 15.99) * mm, "end": v(19.47, 15.98) * mm});
            skLineSegment(sketch, "E11876", {"start": v(19.47, 15.98) * mm, "end": v(19.47, 15.97) * mm});
            skLineSegment(sketch, "E11877", {"start": v(19.47, 15.97) * mm, "end": v(19.46, 15.96) * mm});
            skLineSegment(sketch, "E11878", {"start": v(19.46, 15.96) * mm, "end": v(19.44, 15.95) * mm});
            skLineSegment(sketch, "E11879", {"start": v(19.44, 15.95) * mm, "end": v(19.42, 15.94) * mm});
            skLineSegment(sketch, "E11880", {"start": v(19.42, 15.94) * mm, "end": v(19.4, 15.93) * mm});
            skLineSegment(sketch, "E11881", {"start": v(19.4, 15.93) * mm, "end": v(19.39, 15.92) * mm});
            skLineSegment(sketch, "E11882", {"start": v(19.39, 15.92) * mm, "end": v(19.38, 15.92) * mm});
            skLineSegment(sketch, "E11883", {"start": v(19.38, 15.92) * mm, "end": v(19.37, 15.91) * mm});
            skLineSegment(sketch, "E11884", {"start": v(19.37, 15.91) * mm, "end": v(19.36, 15.9) * mm});
            skLineSegment(sketch, "E11885", {"start": v(19.36, 15.9) * mm, "end": v(19.35, 15.9) * mm});
            skLineSegment(sketch, "E11886", {"start": v(19.35, 15.9) * mm, "end": v(19.34, 15.9) * mm});
            skLineSegment(sketch, "E11887", {"start": v(19.34, 15.9) * mm, "end": v(19.33, 15.9) * mm});
            skLineSegment(sketch, "E11888", {"start": v(19.33, 15.9) * mm, "end": v(19.32, 15.89) * mm});
            skLineSegment(sketch, "E11889", {"start": v(19.32, 15.89) * mm, "end": v(19.29, 15.87) * mm});
            skLineSegment(sketch, "E11890", {"start": v(19.29, 15.87) * mm, "end": v(19.27, 15.86) * mm});
            skLineSegment(sketch, "E11891", {"start": v(19.27, 15.86) * mm, "end": v(19.25, 15.85) * mm});
            skLineSegment(sketch, "E11892", {"start": v(19.25, 15.85) * mm, "end": v(19.24, 15.84) * mm});
            skLineSegment(sketch, "E11893", {"start": v(19.24, 15.84) * mm, "end": v(19.24, 15.84) * mm});
            skLineSegment(sketch, "E11894", {"start": v(19.24, 15.84) * mm, "end": v(19.23, 15.83) * mm});
            skLineSegment(sketch, "E11895", {"start": v(19.23, 15.83) * mm, "end": v(19.23, 15.83) * mm});
            skLineSegment(sketch, "E11896", {"start": v(19.23, 15.83) * mm, "end": v(19.21, 15.83) * mm});
            skLineSegment(sketch, "E11897", {"start": v(19.21, 15.83) * mm, "end": v(19.2, 15.82) * mm});
            skLineSegment(sketch, "E11898", {"start": v(19.2, 15.82) * mm, "end": v(19.18, 15.82) * mm});
            skLineSegment(sketch, "E11899", {"start": v(19.18, 15.82) * mm, "end": v(19.17, 15.81) * mm});
            skLineSegment(sketch, "E11900", {"start": v(19.17, 15.81) * mm, "end": v(19.16, 15.8) * mm});
            skLineSegment(sketch, "E11901", {"start": v(19.16, 15.8) * mm, "end": v(19.15, 15.8) * mm});
            skLineSegment(sketch, "E11902", {"start": v(19.15, 15.8) * mm, "end": v(19.14, 15.8) * mm});
            skLineSegment(sketch, "E11903", {"start": v(19.14, 15.8) * mm, "end": v(19.14, 15.8) * mm});
            skLineSegment(sketch, "E11904", {"start": v(19.14, 15.8) * mm, "end": v(19.13, 15.8) * mm});
            skLineSegment(sketch, "E11905", {"start": v(19.13, 15.8) * mm, "end": v(19.11, 15.8) * mm});
            skLineSegment(sketch, "E11906", {"start": v(19.11, 15.8) * mm, "end": v(19.1, 15.82) * mm});
            skLineSegment(sketch, "E11907", {"start": v(19.1, 15.82) * mm, "end": v(19.08, 15.83) * mm});
            skLineSegment(sketch, "E11908", {"start": v(19.08, 15.83) * mm, "end": v(19.05, 15.84) * mm});
            skLineSegment(sketch, "E11909", {"start": v(19.05, 15.84) * mm, "end": v(19.03, 15.86) * mm});
            skLineSegment(sketch, "E11910", {"start": v(19.03, 15.86) * mm, "end": v(19, 15.88) * mm});
            skLineSegment(sketch, "E11911", {"start": v(19, 15.88) * mm, "end": v(18.97, 15.9) * mm});
            skLineSegment(sketch, "E11912", {"start": v(18.97, 15.9) * mm, "end": v(18.9, 15.96) * mm});
            skLineSegment(sketch, "E11913", {"start": v(18.9, 15.96) * mm, "end": v(18.83, 16.02) * mm});
            skLineSegment(sketch, "E11914", {"start": v(18.83, 16.02) * mm, "end": v(18.76, 16.09) * mm});
            skLineSegment(sketch, "E11915", {"start": v(18.76, 16.09) * mm, "end": v(18.69, 16.16) * mm});
            skLineSegment(sketch, "E11916", {"start": v(18.69, 16.16) * mm, "end": v(18.63, 16.23) * mm});
            skLineSegment(sketch, "E11917", {"start": v(18.63, 16.23) * mm, "end": v(18.57, 16.31) * mm});
            skLineSegment(sketch, "E11918", {"start": v(18.57, 16.31) * mm, "end": v(18.52, 16.4) * mm});
            skLineSegment(sketch, "E11919", {"start": v(18.52, 16.4) * mm, "end": v(18.48, 16.5) * mm});
            skLineSegment(sketch, "E11920", {"start": v(18.48, 16.5) * mm, "end": v(18.45, 16.6) * mm});
            skLineSegment(sketch, "E11921", {"start": v(18.45, 16.6) * mm, "end": v(18.42, 16.7) * mm});
            skLineSegment(sketch, "E11922", {"start": v(18.42, 16.7) * mm, "end": v(18.4, 16.8) * mm});
            skLineSegment(sketch, "E11923", {"start": v(18.4, 16.8) * mm, "end": v(18.4, 16.9) * mm});
            skLineSegment(sketch, "E11924", {"start": v(18.4, 16.9) * mm, "end": v(18.4, 17) * mm});
            skLineSegment(sketch, "E11925", {"start": v(13.38, 8.08) * mm, "end": v(13.43, 8.05) * mm});
            skLineSegment(sketch, "E11926", {"start": v(13.43, 8.05) * mm, "end": v(13.47, 8.02) * mm});
            skLineSegment(sketch, "E11927", {"start": v(13.47, 8.02) * mm, "end": v(13.52, 8) * mm});
            skLineSegment(sketch, "E11928", {"start": v(13.52, 8) * mm, "end": v(13.56, 7.97) * mm});
            skLineSegment(sketch, "E11929", {"start": v(13.56, 7.97) * mm, "end": v(13.6, 7.94) * mm});
            skLineSegment(sketch, "E11930", {"start": v(13.6, 7.94) * mm, "end": v(13.65, 7.9) * mm});
            skLineSegment(sketch, "E11931", {"start": v(13.65, 7.9) * mm, "end": v(13.76, 7.82) * mm});
            skLineSegment(sketch, "E11932", {"start": v(13.76, 7.82) * mm, "end": v(13.87, 7.74) * mm});
            skLineSegment(sketch, "E11933", {"start": v(13.87, 7.74) * mm, "end": v(14, 7.66) * mm});
            skLineSegment(sketch, "E11934", {"start": v(14, 7.66) * mm, "end": v(14.12, 7.6) * mm});
            skLineSegment(sketch, "E11935", {"start": v(14.12, 7.6) * mm, "end": v(14.26, 7.53) * mm});
            skLineSegment(sketch, "E11936", {"start": v(14.26, 7.53) * mm, "end": v(14.4, 7.48) * mm});
            skLineSegment(sketch, "E11937", {"start": v(14.4, 7.48) * mm, "end": v(14.56, 7.45) * mm});
            skLineSegment(sketch, "E11938", {"start": v(14.56, 7.45) * mm, "end": v(14.72, 7.43) * mm});
            skLineSegment(sketch, "E11939", {"start": v(14.72, 7.43) * mm, "end": v(14.73, 7.43) * mm});
            skLineSegment(sketch, "E11940", {"start": v(14.73, 7.43) * mm, "end": v(14.74, 7.43) * mm});
            skLineSegment(sketch, "E11941", {"start": v(14.74, 7.43) * mm, "end": v(14.75, 7.43) * mm});
            skLineSegment(sketch, "E11942", {"start": v(14.75, 7.43) * mm, "end": v(14.76, 7.43) * mm});
            skLineSegment(sketch, "E11943", {"start": v(14.76, 7.43) * mm, "end": v(14.77, 7.43) * mm});
            skLineSegment(sketch, "E11944", {"start": v(14.77, 7.43) * mm, "end": v(14.78, 7.43) * mm});
            skLineSegment(sketch, "E11945", {"start": v(14.78, 7.43) * mm, "end": v(14.8, 7.43) * mm});
            skLineSegment(sketch, "E11946", {"start": v(14.8, 7.43) * mm, "end": v(14.8, 7.43) * mm});
            skLineSegment(sketch, "E11947", {"start": v(14.8, 7.43) * mm, "end": v(14.82, 7.43) * mm});
            skLineSegment(sketch, "E11948", {"start": v(14.82, 7.43) * mm, "end": v(14.84, 7.43) * mm});
            skLineSegment(sketch, "E11949", {"start": v(14.84, 7.43) * mm, "end": v(14.85, 7.43) * mm});
            skLineSegment(sketch, "E11950", {"start": v(14.85, 7.43) * mm, "end": v(14.87, 7.43) * mm});
            skLineSegment(sketch, "E11951", {"start": v(14.87, 7.43) * mm, "end": v(14.89, 7.42) * mm});
            skLineSegment(sketch, "E11952", {"start": v(14.89, 7.42) * mm, "end": v(14.9, 7.42) * mm});
            skLineSegment(sketch, "E11953", {"start": v(14.9, 7.42) * mm, "end": v(14.92, 7.42) * mm});
            skLineSegment(sketch, "E11954", {"start": v(14.92, 7.42) * mm, "end": v(14.94, 7.42) * mm});
            skLineSegment(sketch, "E11955", {"start": v(14.94, 7.42) * mm, "end": v(14.97, 7.42) * mm});
            skLineSegment(sketch, "E11956", {"start": v(14.97, 7.42) * mm, "end": v(15, 7.43) * mm});
            skLineSegment(sketch, "E11957", {"start": v(15, 7.43) * mm, "end": v(15.03, 7.43) * mm});
            skLineSegment(sketch, "E11958", {"start": v(15.03, 7.43) * mm, "end": v(15.06, 7.43) * mm});
            skLineSegment(sketch, "E11959", {"start": v(15.06, 7.43) * mm, "end": v(15.08, 7.44) * mm});
            skLineSegment(sketch, "E11960", {"start": v(15.08, 7.44) * mm, "end": v(15.1, 7.45) * mm});
            skLineSegment(sketch, "E11961", {"start": v(15.1, 7.45) * mm, "end": v(15.13, 7.45) * mm});
            skLineSegment(sketch, "E11962", {"start": v(15.13, 7.45) * mm, "end": v(15.15, 7.46) * mm});
            skLineSegment(sketch, "E11963", {"start": v(15.15, 7.46) * mm, "end": v(15.22, 7.5) * mm});
            skLineSegment(sketch, "E11964", {"start": v(15.22, 7.5) * mm, "end": v(15.28, 7.53) * mm});
            skLineSegment(sketch, "E11965", {"start": v(15.28, 7.53) * mm, "end": v(15.34, 7.56) * mm});
            skLineSegment(sketch, "E11966", {"start": v(15.34, 7.56) * mm, "end": v(15.4, 7.6) * mm});
            skLineSegment(sketch, "E11967", {"start": v(15.4, 7.6) * mm, "end": v(15.46, 7.63) * mm});
            skLineSegment(sketch, "E11968", {"start": v(15.46, 7.63) * mm, "end": v(15.51, 7.67) * mm});
            skLineSegment(sketch, "E11969", {"start": v(15.51, 7.67) * mm, "end": v(15.57, 7.7) * mm});
            skLineSegment(sketch, "E11970", {"start": v(15.57, 7.7) * mm, "end": v(15.63, 7.75) * mm});
            skLineSegment(sketch, "E11971", {"start": v(15.63, 7.75) * mm, "end": v(15.65, 7.76) * mm});
            skLineSegment(sketch, "E11972", {"start": v(15.65, 7.76) * mm, "end": v(15.66, 7.77) * mm});
            skLineSegment(sketch, "E11973", {"start": v(15.66, 7.77) * mm, "end": v(15.68, 7.78) * mm});
            skLineSegment(sketch, "E11974", {"start": v(15.68, 7.78) * mm, "end": v(15.68, 7.78) * mm});
            skLineSegment(sketch, "E11975", {"start": v(15.68, 7.78) * mm, "end": v(15.69, 7.79) * mm});
            skLineSegment(sketch, "E11976", {"start": v(15.69, 7.79) * mm, "end": v(15.69, 7.79) * mm});
            skLineSegment(sketch, "E11977", {"start": v(15.69, 7.79) * mm, "end": v(15.7, 7.79) * mm});
            skLineSegment(sketch, "E11978", {"start": v(15.7, 7.79) * mm, "end": v(15.7, 7.79) * mm});
            skLineSegment(sketch, "E11979", {"start": v(15.7, 7.79) * mm, "end": v(15.72, 7.8) * mm});
            skLineSegment(sketch, "E11980", {"start": v(15.72, 7.8) * mm, "end": v(15.75, 7.83) * mm});
            skLineSegment(sketch, "E11981", {"start": v(15.75, 7.83) * mm, "end": v(15.78, 7.85) * mm});
            skLineSegment(sketch, "E11982", {"start": v(15.78, 7.85) * mm, "end": v(15.82, 7.87) * mm});
            skLineSegment(sketch, "E11983", {"start": v(15.82, 7.87) * mm, "end": v(15.85, 7.9) * mm});
            skLineSegment(sketch, "E11984", {"start": v(15.85, 7.9) * mm, "end": v(15.88, 7.91) * mm});
            skLineSegment(sketch, "E11985", {"start": v(15.88, 7.91) * mm, "end": v(15.91, 7.93) * mm});
            skLineSegment(sketch, "E11986", {"start": v(15.91, 7.93) * mm, "end": v(15.94, 7.95) * mm});
            skLineSegment(sketch, "E11987", {"start": v(15.94, 7.95) * mm, "end": v(15.97, 7.97) * mm});
            skLineSegment(sketch, "E11988", {"start": v(15.97, 7.97) * mm, "end": v(16.02, 8) * mm});
            skLineSegment(sketch, "E11989", {"start": v(16.02, 8) * mm, "end": v(16.08, 8.03) * mm});
            skLineSegment(sketch, "E11990", {"start": v(16.08, 8.03) * mm, "end": v(16.14, 8.07) * mm});
            skLineSegment(sketch, "E11991", {"start": v(16.14, 8.07) * mm, "end": v(16.22, 8.12) * mm});
            skLineSegment(sketch, "E11992", {"start": v(16.22, 8.12) * mm, "end": v(16.3, 8.17) * mm});
            skLineSegment(sketch, "E11993", {"start": v(16.3, 8.17) * mm, "end": v(16.37, 8.22) * mm});
            skLineSegment(sketch, "E11994", {"start": v(16.37, 8.22) * mm, "end": v(16.45, 8.27) * mm});
            skLineSegment(sketch, "E11995", {"start": v(16.45, 8.27) * mm, "end": v(16.45, 8.27) * mm});
            skLineSegment(sketch, "E11996", {"start": v(16.45, 8.27) * mm, "end": v(16.46, 8.27) * mm});
            skLineSegment(sketch, "E11997", {"start": v(16.46, 8.27) * mm, "end": v(16.46, 8.27) * mm});
            skLineSegment(sketch, "E11998", {"start": v(16.46, 8.27) * mm, "end": v(16.48, 8.28) * mm});
            skLineSegment(sketch, "E11999", {"start": v(16.48, 8.28) * mm, "end": v(16.5, 8.3) * mm});
            skLineSegment(sketch, "E12000", {"start": v(16.5, 8.3) * mm, "end": v(16.54, 8.32) * mm});
            skLineSegment(sketch, "E12001", {"start": v(16.54, 8.32) * mm, "end": v(16.58, 8.35) * mm});
            skLineSegment(sketch, "E12002", {"start": v(16.58, 8.35) * mm, "end": v(16.65, 8.4) * mm});
            skLineSegment(sketch, "E12003", {"start": v(16.65, 8.4) * mm, "end": v(16.67, 8.4) * mm});
            skLineSegment(sketch, "E12004", {"start": v(16.67, 8.4) * mm, "end": v(16.69, 8.43) * mm});
            skLineSegment(sketch, "E12005", {"start": v(16.69, 8.43) * mm, "end": v(16.71, 8.46) * mm});
            skLineSegment(sketch, "E12006", {"start": v(16.71, 8.46) * mm, "end": v(16.74, 8.49) * mm});
            skLineSegment(sketch, "E12007", {"start": v(16.74, 8.49) * mm, "end": v(16.76, 8.53) * mm});
            skLineSegment(sketch, "E12008", {"start": v(16.76, 8.53) * mm, "end": v(16.77, 8.56) * mm});
            skLineSegment(sketch, "E12009", {"start": v(16.77, 8.56) * mm, "end": v(16.77, 8.6) * mm});
            skLineSegment(sketch, "E12010", {"start": v(16.77, 8.6) * mm, "end": v(16.76, 8.64) * mm});
            skLineSegment(sketch, "E12011", {"start": v(16.76, 8.64) * mm, "end": v(16.74, 8.67) * mm});
            skLineSegment(sketch, "E12012", {"start": v(16.74, 8.67) * mm, "end": v(16.72, 8.7) * mm});
            skLineSegment(sketch, "E12013", {"start": v(16.72, 8.7) * mm, "end": v(16.7, 8.74) * mm});
            skLineSegment(sketch, "E12014", {"start": v(16.7, 8.74) * mm, "end": v(16.67, 8.77) * mm});
            skLineSegment(sketch, "E12015", {"start": v(16.67, 8.77) * mm, "end": v(16.64, 8.8) * mm});
            skLineSegment(sketch, "E12016", {"start": v(16.64, 8.8) * mm, "end": v(16.6, 8.81) * mm});
            skLineSegment(sketch, "E12017", {"start": v(16.6, 8.81) * mm, "end": v(16.58, 8.83) * mm});
            skLineSegment(sketch, "E12018", {"start": v(16.58, 8.83) * mm, "end": v(16.54, 8.84) * mm});
            skLineSegment(sketch, "E12019", {"start": v(16.54, 8.84) * mm, "end": v(16.42, 8.86) * mm});
            skLineSegment(sketch, "E12020", {"start": v(16.42, 8.86) * mm, "end": v(16.3, 8.9) * mm});
            skLineSegment(sketch, "E12021", {"start": v(16.3, 8.9) * mm, "end": v(16.2, 8.93) * mm});
            skLineSegment(sketch, "E12022", {"start": v(16.2, 8.93) * mm, "end": v(16.08, 8.97) * mm});
            skLineSegment(sketch, "E12023", {"start": v(16.08, 8.97) * mm, "end": v(15.98, 9.02) * mm});
            skLineSegment(sketch, "E12024", {"start": v(15.98, 9.02) * mm, "end": v(15.89, 9.07) * mm});
            skLineSegment(sketch, "E12025", {"start": v(15.89, 9.07) * mm, "end": v(15.8, 9.13) * mm});
            skLineSegment(sketch, "E12026", {"start": v(15.8, 9.13) * mm, "end": v(15.7, 9.18) * mm});
            skLineSegment(sketch, "E12027", {"start": v(15.7, 9.18) * mm, "end": v(15.62, 9.24) * mm});
            skLineSegment(sketch, "E12028", {"start": v(15.62, 9.24) * mm, "end": v(15.53, 9.3) * mm});
            skLineSegment(sketch, "E12029", {"start": v(15.53, 9.3) * mm, "end": v(15.43, 9.35) * mm});
            skLineSegment(sketch, "E12030", {"start": v(15.43, 9.35) * mm, "end": v(15.33, 9.4) * mm});
            skLineSegment(sketch, "E12031", {"start": v(15.33, 9.4) * mm, "end": v(15.23, 9.45) * mm});
            skLineSegment(sketch, "E12032", {"start": v(15.23, 9.45) * mm, "end": v(15.13, 9.5) * mm});
            skLineSegment(sketch, "E12033", {"start": v(15.13, 9.5) * mm, "end": v(15.02, 9.53) * mm});
            skLineSegment(sketch, "E12034", {"start": v(15.02, 9.53) * mm, "end": v(14.9, 9.55) * mm});
            skLineSegment(sketch, "E12035", {"start": v(14.9, 9.55) * mm, "end": v(14.86, 9.56) * mm});
            skLineSegment(sketch, "E12036", {"start": v(14.86, 9.56) * mm, "end": v(14.81, 9.57) * mm});
            skLineSegment(sketch, "E12037", {"start": v(14.81, 9.57) * mm, "end": v(14.77, 9.58) * mm});
            skLineSegment(sketch, "E12038", {"start": v(14.77, 9.58) * mm, "end": v(14.72, 9.58) * mm});
            skLineSegment(sketch, "E12039", {"start": v(14.72, 9.58) * mm, "end": v(14.68, 9.58) * mm});
            skLineSegment(sketch, "E12040", {"start": v(14.68, 9.58) * mm, "end": v(14.64, 9.59) * mm});
            skLineSegment(sketch, "E12041", {"start": v(14.64, 9.59) * mm, "end": v(14.6, 9.59) * mm});
            skLineSegment(sketch, "E12042", {"start": v(14.6, 9.59) * mm, "end": v(14.57, 9.59) * mm});
            skLineSegment(sketch, "E12043", {"start": v(14.57, 9.59) * mm, "end": v(14.47, 9.59) * mm});
            skLineSegment(sketch, "E12044", {"start": v(14.47, 9.59) * mm, "end": v(14.4, 9.59) * mm});
            skLineSegment(sketch, "E12045", {"start": v(14.4, 9.59) * mm, "end": v(14.35, 9.59) * mm});
            skLineSegment(sketch, "E12046", {"start": v(14.35, 9.59) * mm, "end": v(14.32, 9.59) * mm});
            skLineSegment(sketch, "E12047", {"start": v(14.32, 9.59) * mm, "end": v(14.3, 9.59) * mm});
            skLineSegment(sketch, "E12048", {"start": v(14.3, 9.59) * mm, "end": v(14.29, 9.59) * mm});
            skLineSegment(sketch, "E12049", {"start": v(14.29, 9.59) * mm, "end": v(14.28, 9.59) * mm});
            skLineSegment(sketch, "E12050", {"start": v(14.28, 9.59) * mm, "end": v(14.28, 9.59) * mm});
            skLineSegment(sketch, "E12051", {"start": v(14.28, 9.59) * mm, "end": v(14.2, 9.53) * mm});
            skLineSegment(sketch, "E12052", {"start": v(14.2, 9.53) * mm, "end": v(14.13, 9.48) * mm});
            skLineSegment(sketch, "E12053", {"start": v(14.13, 9.48) * mm, "end": v(14.06, 9.44) * mm});
            skLineSegment(sketch, "E12054", {"start": v(14.06, 9.44) * mm, "end": v(14, 9.4) * mm});
            skLineSegment(sketch, "E12055", {"start": v(14, 9.4) * mm, "end": v(13.96, 9.37) * mm});
            skLineSegment(sketch, "E12056", {"start": v(13.96, 9.37) * mm, "end": v(13.92, 9.34) * mm});
            skLineSegment(sketch, "E12057", {"start": v(13.92, 9.34) * mm, "end": v(13.9, 9.33) * mm});
            skLineSegment(sketch, "E12058", {"start": v(13.9, 9.33) * mm, "end": v(13.89, 9.32) * mm});
            skLineSegment(sketch, "E12059", {"start": v(13.89, 9.32) * mm, "end": v(13.88, 9.31) * mm});
            skLineSegment(sketch, "E12060", {"start": v(13.88, 9.31) * mm, "end": v(13.86, 9.3) * mm});
            skLineSegment(sketch, "E12061", {"start": v(13.86, 9.3) * mm, "end": v(13.83, 9.28) * mm});
            skLineSegment(sketch, "E12062", {"start": v(13.83, 9.28) * mm, "end": v(13.79, 9.25) * mm});
            skLineSegment(sketch, "E12063", {"start": v(13.79, 9.25) * mm, "end": v(13.74, 9.2) * mm});
            skLineSegment(sketch, "E12064", {"start": v(13.74, 9.2) * mm, "end": v(13.68, 9.17) * mm});
            skLineSegment(sketch, "E12065", {"start": v(13.68, 9.17) * mm, "end": v(13.62, 9.12) * mm});
            skLineSegment(sketch, "E12066", {"start": v(13.62, 9.12) * mm, "end": v(13.55, 9.07) * mm});
            skLineSegment(sketch, "E12067", {"start": v(13.55, 9.07) * mm, "end": v(13.47, 9) * mm});
            skLineSegment(sketch, "E12068", {"start": v(13.47, 9) * mm, "end": v(13.37, 8.92) * mm});
            skLineSegment(sketch, "E12069", {"start": v(13.37, 8.92) * mm, "end": v(13.26, 8.82) * mm});
            skLineSegment(sketch, "E12070", {"start": v(13.26, 8.82) * mm, "end": v(13.15, 8.72) * mm});
            skLineSegment(sketch, "E12071", {"start": v(13.15, 8.72) * mm, "end": v(13.05, 8.62) * mm});
            skLineSegment(sketch, "E12072", {"start": v(13.05, 8.62) * mm, "end": v(12.97, 8.54) * mm});
            skLineSegment(sketch, "E12073", {"start": v(12.97, 8.54) * mm, "end": v(12.9, 8.48) * mm});
            skLineSegment(sketch, "E12074", {"start": v(12.9, 8.48) * mm, "end": v(12.88, 8.45) * mm});
            skLineSegment(sketch, "E12075", {"start": v(12.88, 8.45) * mm, "end": v(12.87, 8.44) * mm});
            skLineSegment(sketch, "E12076", {"start": v(12.87, 8.44) * mm, "end": v(12.87, 8.43) * mm});
            skLineSegment(sketch, "E12077", {"start": v(12.87, 8.43) * mm, "end": v(12.87, 8.42) * mm});
            skLineSegment(sketch, "E12078", {"start": v(12.87, 8.42) * mm, "end": v(12.87, 8.4) * mm});
            skLineSegment(sketch, "E12079", {"start": v(12.87, 8.4) * mm, "end": v(12.88, 8.4) * mm});
            skLineSegment(sketch, "E12080", {"start": v(12.88, 8.4) * mm, "end": v(12.9, 8.38) * mm});
            skLineSegment(sketch, "E12081", {"start": v(12.9, 8.38) * mm, "end": v(12.9, 8.37) * mm});
            skLineSegment(sketch, "E12082", {"start": v(12.9, 8.37) * mm, "end": v(12.93, 8.35) * mm});
            skLineSegment(sketch, "E12083", {"start": v(12.93, 8.35) * mm, "end": v(12.94, 8.34) * mm});
            skLineSegment(sketch, "E12084", {"start": v(12.94, 8.34) * mm, "end": v(12.97, 8.33) * mm});
            skLineSegment(sketch, "E12085", {"start": v(12.97, 8.33) * mm, "end": v(12.99, 8.32) * mm});
            skLineSegment(sketch, "E12086", {"start": v(12.99, 8.32) * mm, "end": v(13.01, 8.3) * mm});
            skLineSegment(sketch, "E12087", {"start": v(13.01, 8.3) * mm, "end": v(13.03, 8.29) * mm});
            skLineSegment(sketch, "E12088", {"start": v(13.03, 8.29) * mm, "end": v(13.06, 8.28) * mm});
            skLineSegment(sketch, "E12089", {"start": v(13.06, 8.28) * mm, "end": v(13.08, 8.26) * mm});
            skLineSegment(sketch, "E12090", {"start": v(13.08, 8.26) * mm, "end": v(13.1, 8.25) * mm});
            skLineSegment(sketch, "E12091", {"start": v(13.1, 8.25) * mm, "end": v(13.1, 8.25) * mm});
            skLineSegment(sketch, "E12092", {"start": v(13.1, 8.25) * mm, "end": v(13.1, 8.24) * mm});
            skLineSegment(sketch, "E12093", {"start": v(13.1, 8.24) * mm, "end": v(13.12, 8.24) * mm});
            skLineSegment(sketch, "E12094", {"start": v(13.12, 8.24) * mm, "end": v(13.13, 8.23) * mm});
            skLineSegment(sketch, "E12095", {"start": v(13.13, 8.23) * mm, "end": v(13.15, 8.22) * mm});
            skLineSegment(sketch, "E12096", {"start": v(13.15, 8.22) * mm, "end": v(13.17, 8.2) * mm});
            skLineSegment(sketch, "E12097", {"start": v(13.17, 8.2) * mm, "end": v(13.2, 8.2) * mm});
            skLineSegment(sketch, "E12098", {"start": v(13.2, 8.2) * mm, "end": v(13.21, 8.18) * mm});
            skLineSegment(sketch, "E12099", {"start": v(13.21, 8.18) * mm, "end": v(13.23, 8.17) * mm});
            skLineSegment(sketch, "E12100", {"start": v(13.23, 8.17) * mm, "end": v(13.25, 8.16) * mm});
            skLineSegment(sketch, "E12101", {"start": v(13.25, 8.16) * mm, "end": v(13.27, 8.15) * mm});
            skLineSegment(sketch, "E12102", {"start": v(13.27, 8.15) * mm, "end": v(13.3, 8.13) * mm});
            skLineSegment(sketch, "E12103", {"start": v(13.3, 8.13) * mm, "end": v(13.34, 8.1) * mm});
            skLineSegment(sketch, "E12104", {"start": v(13.34, 8.1) * mm, "end": v(13.38, 8.08) * mm});
            skLineSegment(sketch, "E12105", {"start": v(13.64, 8.5) * mm, "end": v(13.66, 8.54) * mm});
            skLineSegment(sketch, "E12106", {"start": v(13.66, 8.54) * mm, "end": v(13.68, 8.57) * mm});
            skLineSegment(sketch, "E12107", {"start": v(13.68, 8.57) * mm, "end": v(13.7, 8.6) * mm});
            skLineSegment(sketch, "E12108", {"start": v(13.7, 8.6) * mm, "end": v(13.74, 8.64) * mm});
            skLineSegment(sketch, "E12109", {"start": v(13.74, 8.64) * mm, "end": v(13.79, 8.67) * mm});
            skLineSegment(sketch, "E12110", {"start": v(13.79, 8.67) * mm, "end": v(13.84, 8.7) * mm});
            skLineSegment(sketch, "E12111", {"start": v(13.84, 8.7) * mm, "end": v(13.88, 8.73) * mm});
            skLineSegment(sketch, "E12112", {"start": v(13.88, 8.73) * mm, "end": v(13.92, 8.75) * mm});
            skLineSegment(sketch, "E12113", {"start": v(13.92, 8.75) * mm, "end": v(13.96, 8.78) * mm});
            skLineSegment(sketch, "E12114", {"start": v(13.96, 8.78) * mm, "end": v(14, 8.8) * mm});
            skLineSegment(sketch, "E12115", {"start": v(14, 8.8) * mm, "end": v(14.03, 8.83) * mm});
            skLineSegment(sketch, "E12116", {"start": v(14.03, 8.83) * mm, "end": v(14.07, 8.86) * mm});
            skLineSegment(sketch, "E12117", {"start": v(14.07, 8.86) * mm, "end": v(14.1, 8.88) * mm});
            skLineSegment(sketch, "E12118", {"start": v(14.1, 8.88) * mm, "end": v(14.14, 8.91) * mm});
            skLineSegment(sketch, "E12119", {"start": v(14.14, 8.91) * mm, "end": v(14.16, 8.93) * mm});
            skLineSegment(sketch, "E12120", {"start": v(14.16, 8.93) * mm, "end": v(14.18, 8.94) * mm});
            skLineSegment(sketch, "E12121", {"start": v(14.18, 8.94) * mm, "end": v(14.2, 8.96) * mm});
            skLineSegment(sketch, "E12122", {"start": v(14.2, 8.96) * mm, "end": v(14.23, 8.97) * mm});
            skLineSegment(sketch, "E12123", {"start": v(14.23, 8.97) * mm, "end": v(14.25, 9) * mm});
            skLineSegment(sketch, "E12124", {"start": v(14.25, 9) * mm, "end": v(14.27, 9) * mm});
            skLineSegment(sketch, "E12125", {"start": v(14.27, 9) * mm, "end": v(14.3, 9.02) * mm});
            skLineSegment(sketch, "E12126", {"start": v(14.3, 9.02) * mm, "end": v(14.31, 9.04) * mm});
            skLineSegment(sketch, "E12127", {"start": v(14.31, 9.04) * mm, "end": v(14.32, 9.04) * mm});
            skLineSegment(sketch, "E12128", {"start": v(14.32, 9.04) * mm, "end": v(14.33, 9.05) * mm});
            skLineSegment(sketch, "E12129", {"start": v(14.33, 9.05) * mm, "end": v(14.34, 9.05) * mm});
            skLineSegment(sketch, "E12130", {"start": v(14.34, 9.05) * mm, "end": v(14.34, 9.06) * mm});
            skLineSegment(sketch, "E12131", {"start": v(14.34, 9.06) * mm, "end": v(14.34, 9.06) * mm});
            skLineSegment(sketch, "E12132", {"start": v(14.34, 9.06) * mm, "end": v(14.36, 9.06) * mm});
            skLineSegment(sketch, "E12133", {"start": v(14.36, 9.06) * mm, "end": v(14.37, 9.06) * mm});
            skLineSegment(sketch, "E12134", {"start": v(14.37, 9.06) * mm, "end": v(14.38, 9.07) * mm});
            skLineSegment(sketch, "E12135", {"start": v(14.38, 9.07) * mm, "end": v(14.4, 9.07) * mm});
            skLineSegment(sketch, "E12136", {"start": v(14.4, 9.07) * mm, "end": v(14.4, 9.07) * mm});
            skLineSegment(sketch, "E12137", {"start": v(14.4, 9.07) * mm, "end": v(14.42, 9.07) * mm});
            skLineSegment(sketch, "E12138", {"start": v(14.42, 9.07) * mm, "end": v(14.42, 9.07) * mm});
            skLineSegment(sketch, "E12139", {"start": v(14.42, 9.07) * mm, "end": v(14.45, 9.07) * mm});
            skLineSegment(sketch, "E12140", {"start": v(14.45, 9.07) * mm, "end": v(14.51, 9.06) * mm});
            skLineSegment(sketch, "E12141", {"start": v(14.51, 9.06) * mm, "end": v(14.61, 9.05) * mm});
            skLineSegment(sketch, "E12142", {"start": v(14.61, 9.05) * mm, "end": v(14.74, 9.04) * mm});
            skLineSegment(sketch, "E12143", {"start": v(14.74, 9.04) * mm, "end": v(14.9, 9.02) * mm});
            skLineSegment(sketch, "E12144", {"start": v(14.9, 9.02) * mm, "end": v(15.08, 9) * mm});
            skLineSegment(sketch, "E12145", {"start": v(15.08, 9) * mm, "end": v(15.28, 8.98) * mm});
            skLineSegment(sketch, "E12146", {"start": v(15.28, 8.98) * mm, "end": v(15.49, 8.96) * mm});
            skLineSegment(sketch, "E12147", {"start": v(15.49, 8.96) * mm, "end": v(15.49, 8.96) * mm});
            skLineSegment(sketch, "E12148", {"start": v(15.49, 8.96) * mm, "end": v(15.5, 8.95) * mm});
            skLineSegment(sketch, "E12149", {"start": v(15.5, 8.95) * mm, "end": v(15.5, 8.94) * mm});
            skLineSegment(sketch, "E12150", {"start": v(15.5, 8.94) * mm, "end": v(15.54, 8.93) * mm});
            skLineSegment(sketch, "E12151", {"start": v(15.54, 8.93) * mm, "end": v(15.58, 8.9) * mm});
            skLineSegment(sketch, "E12152", {"start": v(15.58, 8.9) * mm, "end": v(15.65, 8.85) * mm});
            skLineSegment(sketch, "E12153", {"start": v(15.65, 8.85) * mm, "end": v(15.74, 8.8) * mm});
            skLineSegment(sketch, "E12154", {"start": v(15.74, 8.8) * mm, "end": v(15.87, 8.7) * mm});
            skLineSegment(sketch, "E12155", {"start": v(15.87, 8.7) * mm, "end": v(15.88, 8.7) * mm});
            skLineSegment(sketch, "E12156", {"start": v(15.88, 8.7) * mm, "end": v(15.89, 8.7) * mm});
            skLineSegment(sketch, "E12157", {"start": v(15.89, 8.7) * mm, "end": v(15.9, 8.7) * mm});
            skLineSegment(sketch, "E12158", {"start": v(15.9, 8.7) * mm, "end": v(15.9, 8.7) * mm});
            skLineSegment(sketch, "E12159", {"start": v(15.9, 8.7) * mm, "end": v(15.9, 8.69) * mm});
            skLineSegment(sketch, "E12160", {"start": v(15.9, 8.69) * mm, "end": v(15.9, 8.69) * mm});
            skLineSegment(sketch, "E12161", {"start": v(15.9, 8.69) * mm, "end": v(15.9, 8.68) * mm});
            skLineSegment(sketch, "E12162", {"start": v(15.9, 8.68) * mm, "end": v(15.92, 8.66) * mm});
            skLineSegment(sketch, "E12163", {"start": v(15.92, 8.66) * mm, "end": v(15.92, 8.65) * mm});
            skLineSegment(sketch, "E12164", {"start": v(15.92, 8.65) * mm, "end": v(15.93, 8.64) * mm});
            skLineSegment(sketch, "E12165", {"start": v(15.93, 8.64) * mm, "end": v(15.94, 8.63) * mm});
            skLineSegment(sketch, "E12166", {"start": v(15.94, 8.63) * mm, "end": v(15.94, 8.62) * mm});
            skLineSegment(sketch, "E12167", {"start": v(15.94, 8.62) * mm, "end": v(15.95, 8.62) * mm});
            skLineSegment(sketch, "E12168", {"start": v(15.95, 8.62) * mm, "end": v(15.95, 8.62) * mm});
            skLineSegment(sketch, "E12169", {"start": v(15.95, 8.62) * mm, "end": v(15.95, 8.61) * mm});
            skLineSegment(sketch, "E12170", {"start": v(15.95, 8.61) * mm, "end": v(15.94, 8.6) * mm});
            skLineSegment(sketch, "E12171", {"start": v(15.94, 8.6) * mm, "end": v(15.94, 8.58) * mm});
            skLineSegment(sketch, "E12172", {"start": v(15.94, 8.58) * mm, "end": v(15.93, 8.56) * mm});
            skLineSegment(sketch, "E12173", {"start": v(15.93, 8.56) * mm, "end": v(15.91, 8.53) * mm});
            skLineSegment(sketch, "E12174", {"start": v(15.91, 8.53) * mm, "end": v(15.9, 8.5) * mm});
            skLineSegment(sketch, "E12175", {"start": v(15.9, 8.5) * mm, "end": v(15.89, 8.47) * mm});
            skLineSegment(sketch, "E12176", {"start": v(15.89, 8.47) * mm, "end": v(15.87, 8.43) * mm});
            skLineSegment(sketch, "E12177", {"start": v(15.87, 8.43) * mm, "end": v(15.87, 8.43) * mm});
            skLineSegment(sketch, "E12178", {"start": v(15.87, 8.43) * mm, "end": v(15.86, 8.43) * mm});
            skLineSegment(sketch, "E12179", {"start": v(15.86, 8.43) * mm, "end": v(15.86, 8.43) * mm});
            skLineSegment(sketch, "E12180", {"start": v(15.86, 8.43) * mm, "end": v(15.85, 8.42) * mm});
            skLineSegment(sketch, "E12181", {"start": v(15.85, 8.42) * mm, "end": v(15.83, 8.4) * mm});
            skLineSegment(sketch, "E12182", {"start": v(15.83, 8.4) * mm, "end": v(15.8, 8.4) * mm});
            skLineSegment(sketch, "E12183", {"start": v(15.8, 8.4) * mm, "end": v(15.78, 8.38) * mm});
            skLineSegment(sketch, "E12184", {"start": v(15.78, 8.38) * mm, "end": v(15.77, 8.37) * mm});
            skLineSegment(sketch, "E12185", {"start": v(15.77, 8.37) * mm, "end": v(15.76, 8.37) * mm});
            skLineSegment(sketch, "E12186", {"start": v(15.76, 8.37) * mm, "end": v(15.75, 8.36) * mm});
            skLineSegment(sketch, "E12187", {"start": v(15.75, 8.36) * mm, "end": v(15.75, 8.36) * mm});
            skLineSegment(sketch, "E12188", {"start": v(15.75, 8.36) * mm, "end": v(15.74, 8.35) * mm});
            skLineSegment(sketch, "E12189", {"start": v(15.74, 8.35) * mm, "end": v(15.73, 8.35) * mm});
            skLineSegment(sketch, "E12190", {"start": v(15.73, 8.35) * mm, "end": v(15.73, 8.34) * mm});
            skLineSegment(sketch, "E12191", {"start": v(15.73, 8.34) * mm, "end": v(15.72, 8.34) * mm});
            skLineSegment(sketch, "E12192", {"start": v(15.72, 8.34) * mm, "end": v(15.65, 8.29) * mm});
            skLineSegment(sketch, "E12193", {"start": v(15.65, 8.29) * mm, "end": v(15.58, 8.24) * mm});
            skLineSegment(sketch, "E12194", {"start": v(15.58, 8.24) * mm, "end": v(15.5, 8.2) * mm});
            skLineSegment(sketch, "E12195", {"start": v(15.5, 8.2) * mm, "end": v(15.43, 8.16) * mm});
            skLineSegment(sketch, "E12196", {"start": v(15.43, 8.16) * mm, "end": v(15.35, 8.12) * mm});
            skLineSegment(sketch, "E12197", {"start": v(15.35, 8.12) * mm, "end": v(15.28, 8.08) * mm});
            skLineSegment(sketch, "E12198", {"start": v(15.28, 8.08) * mm, "end": v(15.2, 8.05) * mm});
            skLineSegment(sketch, "E12199", {"start": v(15.2, 8.05) * mm, "end": v(15.13, 8.02) * mm});
            skLineSegment(sketch, "E12200", {"start": v(15.13, 8.02) * mm, "end": v(15.06, 8) * mm});
            skLineSegment(sketch, "E12201", {"start": v(15.06, 8) * mm, "end": v(15, 7.98) * mm});
            skLineSegment(sketch, "E12202", {"start": v(15, 7.98) * mm, "end": v(14.94, 7.96) * mm});
            skLineSegment(sketch, "E12203", {"start": v(14.94, 7.96) * mm, "end": v(14.89, 7.95) * mm});
            skLineSegment(sketch, "E12204", {"start": v(14.89, 7.95) * mm, "end": v(14.83, 7.94) * mm});
            skLineSegment(sketch, "E12205", {"start": v(14.83, 7.94) * mm, "end": v(14.78, 7.93) * mm});
            skLineSegment(sketch, "E12206", {"start": v(14.78, 7.93) * mm, "end": v(14.73, 7.92) * mm});
            skLineSegment(sketch, "E12207", {"start": v(14.73, 7.92) * mm, "end": v(14.67, 7.92) * mm});
            skLineSegment(sketch, "E12208", {"start": v(14.67, 7.92) * mm, "end": v(14.62, 7.92) * mm});
            skLineSegment(sketch, "E12209", {"start": v(14.62, 7.92) * mm, "end": v(14.56, 7.93) * mm});
            skLineSegment(sketch, "E12210", {"start": v(14.56, 7.93) * mm, "end": v(14.5, 7.94) * mm});
            skLineSegment(sketch, "E12211", {"start": v(14.5, 7.94) * mm, "end": v(14.46, 7.95) * mm});
            skLineSegment(sketch, "E12212", {"start": v(14.46, 7.95) * mm, "end": v(14.4, 7.97) * mm});
            skLineSegment(sketch, "E12213", {"start": v(14.4, 7.97) * mm, "end": v(14.35, 8) * mm});
            skLineSegment(sketch, "E12214", {"start": v(14.35, 8) * mm, "end": v(14.3, 8.02) * mm});
            skLineSegment(sketch, "E12215", {"start": v(14.3, 8.02) * mm, "end": v(14.26, 8.05) * mm});
            skLineSegment(sketch, "E12216", {"start": v(14.26, 8.05) * mm, "end": v(14.21, 8.08) * mm});
            skLineSegment(sketch, "E12217", {"start": v(14.21, 8.08) * mm, "end": v(14.17, 8.1) * mm});
            skLineSegment(sketch, "E12218", {"start": v(14.17, 8.1) * mm, "end": v(14.12, 8.13) * mm});
            skLineSegment(sketch, "E12219", {"start": v(14.12, 8.13) * mm, "end": v(14.07, 8.15) * mm});
            skLineSegment(sketch, "E12220", {"start": v(14.07, 8.15) * mm, "end": v(14.03, 8.17) * mm});
            skLineSegment(sketch, "E12221", {"start": v(14.03, 8.17) * mm, "end": v(13.98, 8.18) * mm});
            skLineSegment(sketch, "E12222", {"start": v(13.98, 8.18) * mm, "end": v(13.93, 8.2) * mm});
            skLineSegment(sketch, "E12223", {"start": v(13.93, 8.2) * mm, "end": v(13.89, 8.21) * mm});
            skLineSegment(sketch, "E12224", {"start": v(13.89, 8.21) * mm, "end": v(13.85, 8.22) * mm});
            skLineSegment(sketch, "E12225", {"start": v(13.85, 8.22) * mm, "end": v(13.8, 8.23) * mm});
            skLineSegment(sketch, "E12226", {"start": v(13.8, 8.23) * mm, "end": v(13.77, 8.25) * mm});
            skLineSegment(sketch, "E12227", {"start": v(13.77, 8.25) * mm, "end": v(13.74, 8.28) * mm});
            skLineSegment(sketch, "E12228", {"start": v(13.74, 8.28) * mm, "end": v(13.7, 8.3) * mm});
            skLineSegment(sketch, "E12229", {"start": v(13.7, 8.3) * mm, "end": v(13.68, 8.34) * mm});
            skLineSegment(sketch, "E12230", {"start": v(13.68, 8.34) * mm, "end": v(13.66, 8.39) * mm});
            skLineSegment(sketch, "E12231", {"start": v(13.66, 8.39) * mm, "end": v(13.64, 8.44) * mm});
            skLineSegment(sketch, "E12232", {"start": v(13.64, 8.44) * mm, "end": v(13.64, 8.47) * mm});
            skLineSegment(sketch, "E12233", {"start": v(13.64, 8.47) * mm, "end": v(13.64, 8.5) * mm});
            skLineSegment(sketch, "E12234", {"start": v(14.12, 13.87) * mm, "end": v(14.13, 13.84) * mm});
            skLineSegment(sketch, "E12235", {"start": v(14.13, 13.84) * mm, "end": v(14.15, 13.8) * mm});
            skLineSegment(sketch, "E12236", {"start": v(14.15, 13.8) * mm, "end": v(14.16, 13.78) * mm});
            skLineSegment(sketch, "E12237", {"start": v(14.16, 13.78) * mm, "end": v(14.17, 13.76) * mm});
            skLineSegment(sketch, "E12238", {"start": v(14.17, 13.76) * mm, "end": v(14.18, 13.74) * mm});
            skLineSegment(sketch, "E12239", {"start": v(14.18, 13.74) * mm, "end": v(14.18, 13.73) * mm});
            skLineSegment(sketch, "E12240", {"start": v(14.18, 13.73) * mm, "end": v(14.2, 13.68) * mm});
            skLineSegment(sketch, "E12241", {"start": v(14.2, 13.68) * mm, "end": v(14.23, 13.62) * mm});
            skLineSegment(sketch, "E12242", {"start": v(14.23, 13.62) * mm, "end": v(14.24, 13.56) * mm});
            skLineSegment(sketch, "E12243", {"start": v(14.24, 13.56) * mm, "end": v(14.26, 13.5) * mm});
            skLineSegment(sketch, "E12244", {"start": v(14.26, 13.5) * mm, "end": v(14.27, 13.45) * mm});
            skLineSegment(sketch, "E12245", {"start": v(14.27, 13.45) * mm, "end": v(14.28, 13.39) * mm});
            skLineSegment(sketch, "E12246", {"start": v(14.28, 13.39) * mm, "end": v(14.3, 13.33) * mm});
            skLineSegment(sketch, "E12247", {"start": v(14.3, 13.33) * mm, "end": v(14.3, 13.27) * mm});
            skLineSegment(sketch, "E12248", {"start": v(14.3, 13.27) * mm, "end": v(14.32, 13.19) * mm});
            skLineSegment(sketch, "E12249", {"start": v(14.32, 13.19) * mm, "end": v(14.35, 13.12) * mm});
            skLineSegment(sketch, "E12250", {"start": v(14.35, 13.12) * mm, "end": v(14.4, 13.06) * mm});
            skLineSegment(sketch, "E12251", {"start": v(14.4, 13.06) * mm, "end": v(14.45, 13) * mm});
            skLineSegment(sketch, "E12252", {"start": v(14.45, 13) * mm, "end": v(14.51, 12.95) * mm});
            skLineSegment(sketch, "E12253", {"start": v(14.51, 12.95) * mm, "end": v(14.58, 12.9) * mm});
            skLineSegment(sketch, "E12254", {"start": v(14.58, 12.9) * mm, "end": v(14.64, 12.85) * mm});
            skLineSegment(sketch, "E12255", {"start": v(14.64, 12.85) * mm, "end": v(14.7, 12.8) * mm});
            skLineSegment(sketch, "E12256", {"start": v(14.7, 12.8) * mm, "end": v(14.75, 12.77) * mm});
            skLineSegment(sketch, "E12257", {"start": v(14.75, 12.77) * mm, "end": v(14.8, 12.73) * mm});
            skLineSegment(sketch, "E12258", {"start": v(14.8, 12.73) * mm, "end": v(14.84, 12.7) * mm});
            skLineSegment(sketch, "E12259", {"start": v(14.84, 12.7) * mm, "end": v(14.88, 12.65) * mm});
            skLineSegment(sketch, "E12260", {"start": v(14.88, 12.65) * mm, "end": v(14.93, 12.61) * mm});
            skLineSegment(sketch, "E12261", {"start": v(14.93, 12.61) * mm, "end": v(14.98, 12.58) * mm});
            skLineSegment(sketch, "E12262", {"start": v(14.98, 12.58) * mm, "end": v(15.03, 12.54) * mm});
            skLineSegment(sketch, "E12263", {"start": v(15.03, 12.54) * mm, "end": v(15.08, 12.52) * mm});
            skLineSegment(sketch, "E12264", {"start": v(15.08, 12.52) * mm, "end": v(15.1, 12.51) * mm});
            skLineSegment(sketch, "E12265", {"start": v(15.1, 12.51) * mm, "end": v(15.11, 12.51) * mm});
            skLineSegment(sketch, "E12266", {"start": v(15.11, 12.51) * mm, "end": v(15.13, 12.51) * mm});
            skLineSegment(sketch, "E12267", {"start": v(15.13, 12.51) * mm, "end": v(15.14, 12.52) * mm});
            skLineSegment(sketch, "E12268", {"start": v(15.14, 12.52) * mm, "end": v(15.14, 12.53) * mm});
            skLineSegment(sketch, "E12269", {"start": v(15.14, 12.53) * mm, "end": v(15.15, 12.54) * mm});
            skLineSegment(sketch, "E12270", {"start": v(15.15, 12.54) * mm, "end": v(15.15, 12.56) * mm});
            skLineSegment(sketch, "E12271", {"start": v(15.15, 12.56) * mm, "end": v(15.15, 12.58) * mm});
            skLineSegment(sketch, "E12272", {"start": v(15.15, 12.58) * mm, "end": v(15.15, 12.6) * mm});
            skLineSegment(sketch, "E12273", {"start": v(15.15, 12.6) * mm, "end": v(15.14, 12.63) * mm});
            skLineSegment(sketch, "E12274", {"start": v(15.14, 12.63) * mm, "end": v(15.14, 12.67) * mm});
            skLineSegment(sketch, "E12275", {"start": v(15.14, 12.67) * mm, "end": v(15.13, 12.72) * mm});
            skLineSegment(sketch, "E12276", {"start": v(15.13, 12.72) * mm, "end": v(15.13, 12.77) * mm});
            skLineSegment(sketch, "E12277", {"start": v(15.13, 12.77) * mm, "end": v(15.12, 12.82) * mm});
            skLineSegment(sketch, "E12278", {"start": v(15.12, 12.82) * mm, "end": v(15.11, 12.88) * mm});
            skLineSegment(sketch, "E12279", {"start": v(15.11, 12.88) * mm, "end": v(15.1, 12.93) * mm});
            skLineSegment(sketch, "E12280", {"start": v(15.1, 12.93) * mm, "end": v(15.1, 12.95) * mm});
            skLineSegment(sketch, "E12281", {"start": v(15.1, 12.95) * mm, "end": v(15.1, 12.97) * mm});
            skLineSegment(sketch, "E12282", {"start": v(15.1, 12.97) * mm, "end": v(15.08, 12.99) * mm});
            skLineSegment(sketch, "E12283", {"start": v(15.08, 12.99) * mm, "end": v(15.07, 13) * mm});
            skLineSegment(sketch, "E12284", {"start": v(15.07, 13) * mm, "end": v(15.05, 13.03) * mm});
            skLineSegment(sketch, "E12285", {"start": v(15.05, 13.03) * mm, "end": v(15.04, 13.05) * mm});
            skLineSegment(sketch, "E12286", {"start": v(15.04, 13.05) * mm, "end": v(15.02, 13.07) * mm});
            skLineSegment(sketch, "E12287", {"start": v(15.02, 13.07) * mm, "end": v(15.01, 13.08) * mm});
            skLineSegment(sketch, "E12288", {"start": v(15.01, 13.08) * mm, "end": v(14.97, 13.15) * mm});
            skLineSegment(sketch, "E12289", {"start": v(14.97, 13.15) * mm, "end": v(14.93, 13.22) * mm});
            skLineSegment(sketch, "E12290", {"start": v(14.93, 13.22) * mm, "end": v(14.88, 13.28) * mm});
            skLineSegment(sketch, "E12291", {"start": v(14.88, 13.28) * mm, "end": v(14.84, 13.34) * mm});
            skLineSegment(sketch, "E12292", {"start": v(14.84, 13.34) * mm, "end": v(14.8, 13.4) * mm});
            skLineSegment(sketch, "E12293", {"start": v(14.8, 13.4) * mm, "end": v(14.75, 13.47) * mm});
            skLineSegment(sketch, "E12294", {"start": v(14.75, 13.47) * mm, "end": v(14.7, 13.54) * mm});
            skLineSegment(sketch, "E12295", {"start": v(14.7, 13.54) * mm, "end": v(14.66, 13.6) * mm});
            skLineSegment(sketch, "E12296", {"start": v(14.66, 13.6) * mm, "end": v(14.65, 13.61) * mm});
            skLineSegment(sketch, "E12297", {"start": v(14.65, 13.61) * mm, "end": v(14.65, 13.62) * mm});
            skLineSegment(sketch, "E12298", {"start": v(14.65, 13.62) * mm, "end": v(14.64, 13.63) * mm});
            skLineSegment(sketch, "E12299", {"start": v(14.64, 13.63) * mm, "end": v(14.64, 13.64) * mm});
            skLineSegment(sketch, "E12300", {"start": v(14.64, 13.64) * mm, "end": v(14.64, 13.65) * mm});
            skLineSegment(sketch, "E12301", {"start": v(14.64, 13.65) * mm, "end": v(14.64, 13.66) * mm});
            skLineSegment(sketch, "E12302", {"start": v(14.64, 13.66) * mm, "end": v(14.64, 13.66) * mm});
            skLineSegment(sketch, "E12303", {"start": v(14.64, 13.66) * mm, "end": v(14.64, 13.67) * mm});
            skLineSegment(sketch, "E12304", {"start": v(14.64, 13.67) * mm, "end": v(14.64, 13.68) * mm});
            skLineSegment(sketch, "E12305", {"start": v(14.64, 13.68) * mm, "end": v(14.64, 13.68) * mm});
            skLineSegment(sketch, "E12306", {"start": v(14.64, 13.68) * mm, "end": v(14.65, 13.68) * mm});
            skLineSegment(sketch, "E12307", {"start": v(14.65, 13.68) * mm, "end": v(14.65, 13.68) * mm});
            skLineSegment(sketch, "E12308", {"start": v(14.65, 13.68) * mm, "end": v(14.65, 13.69) * mm});
            skLineSegment(sketch, "E12309", {"start": v(14.65, 13.69) * mm, "end": v(14.65, 13.69) * mm});
            skLineSegment(sketch, "E12310", {"start": v(14.65, 13.69) * mm, "end": v(14.66, 13.7) * mm});
            skLineSegment(sketch, "E12311", {"start": v(14.66, 13.7) * mm, "end": v(14.67, 13.7) * mm});
            skLineSegment(sketch, "E12312", {"start": v(14.67, 13.7) * mm, "end": v(14.69, 13.7) * mm});
            skLineSegment(sketch, "E12313", {"start": v(14.69, 13.7) * mm, "end": v(14.7, 13.7) * mm});
            skLineSegment(sketch, "E12314", {"start": v(14.7, 13.7) * mm, "end": v(14.71, 13.71) * mm});
            skLineSegment(sketch, "E12315", {"start": v(14.71, 13.71) * mm, "end": v(14.72, 13.72) * mm});
            skLineSegment(sketch, "E12316", {"start": v(14.72, 13.72) * mm, "end": v(14.73, 13.72) * mm});
            skLineSegment(sketch, "E12317", {"start": v(14.73, 13.72) * mm, "end": v(14.74, 13.73) * mm});
            skLineSegment(sketch, "E12318", {"start": v(14.74, 13.73) * mm, "end": v(14.75, 13.73) * mm});
            skLineSegment(sketch, "E12319", {"start": v(14.75, 13.73) * mm, "end": v(14.77, 13.74) * mm});
            skLineSegment(sketch, "E12320", {"start": v(14.77, 13.74) * mm, "end": v(14.8, 13.74) * mm});
            skLineSegment(sketch, "E12321", {"start": v(14.8, 13.74) * mm, "end": v(14.83, 13.75) * mm});
            skLineSegment(sketch, "E12322", {"start": v(14.83, 13.75) * mm, "end": v(14.86, 13.76) * mm});
            skLineSegment(sketch, "E12323", {"start": v(14.86, 13.76) * mm, "end": v(14.9, 13.77) * mm});
            skLineSegment(sketch, "E12324", {"start": v(14.9, 13.77) * mm, "end": v(14.93, 13.79) * mm});
            skLineSegment(sketch, "E12325", {"start": v(14.93, 13.79) * mm, "end": v(14.97, 13.8) * mm});
            skLineSegment(sketch, "E12326", {"start": v(14.97, 13.8) * mm, "end": v(14.97, 13.8) * mm});
            skLineSegment(sketch, "E12327", {"start": v(14.97, 13.8) * mm, "end": v(14.98, 13.8) * mm});
            skLineSegment(sketch, "E12328", {"start": v(14.98, 13.8) * mm, "end": v(14.98, 13.8) * mm});
            skLineSegment(sketch, "E12329", {"start": v(14.98, 13.8) * mm, "end": v(15, 13.8) * mm});
            skLineSegment(sketch, "E12330", {"start": v(15, 13.8) * mm, "end": v(15.01, 13.8) * mm});
            skLineSegment(sketch, "E12331", {"start": v(15.01, 13.8) * mm, "end": v(15.04, 13.8) * mm});
            skLineSegment(sketch, "E12332", {"start": v(15.04, 13.8) * mm, "end": v(15.07, 13.8) * mm});
            skLineSegment(sketch, "E12333", {"start": v(15.07, 13.8) * mm, "end": v(15.07, 13.8) * mm});
            skLineSegment(sketch, "E12334", {"start": v(15.07, 13.8) * mm, "end": v(15.08, 13.8) * mm});
            skLineSegment(sketch, "E12335", {"start": v(15.08, 13.8) * mm, "end": v(15.08, 13.8) * mm});
            skLineSegment(sketch, "E12336", {"start": v(15.08, 13.8) * mm, "end": v(15.09, 13.8) * mm});
            skLineSegment(sketch, "E12337", {"start": v(15.09, 13.8) * mm, "end": v(15.1, 13.8) * mm});
            skLineSegment(sketch, "E12338", {"start": v(15.1, 13.8) * mm, "end": v(15.1, 13.8) * mm});
            skLineSegment(sketch, "E12339", {"start": v(15.1, 13.8) * mm, "end": v(15.11, 13.8) * mm});
            skLineSegment(sketch, "E12340", {"start": v(15.11, 13.8) * mm, "end": v(15.14, 13.8) * mm});
            skLineSegment(sketch, "E12341", {"start": v(15.14, 13.8) * mm, "end": v(15.19, 13.8) * mm});
            skLineSegment(sketch, "E12342", {"start": v(15.19, 13.8) * mm, "end": v(15.25, 13.8) * mm});
            skLineSegment(sketch, "E12343", {"start": v(15.25, 13.8) * mm, "end": v(15.31, 13.8) * mm});
            skLineSegment(sketch, "E12344", {"start": v(15.31, 13.8) * mm, "end": v(15.4, 13.79) * mm});
            skLineSegment(sketch, "E12345", {"start": v(15.4, 13.79) * mm, "end": v(15.47, 13.79) * mm});
            skLineSegment(sketch, "E12346", {"start": v(15.47, 13.79) * mm, "end": v(15.56, 13.78) * mm});
            skLineSegment(sketch, "E12347", {"start": v(15.56, 13.78) * mm, "end": v(15.56, 13.78) * mm});
            skLineSegment(sketch, "E12348", {"start": v(15.56, 13.78) * mm, "end": v(15.57, 13.78) * mm});
            skLineSegment(sketch, "E12349", {"start": v(15.57, 13.78) * mm, "end": v(15.58, 13.77) * mm});
            skLineSegment(sketch, "E12350", {"start": v(15.58, 13.77) * mm, "end": v(15.6, 13.77) * mm});
            skLineSegment(sketch, "E12351", {"start": v(15.6, 13.77) * mm, "end": v(15.64, 13.75) * mm});
            skLineSegment(sketch, "E12352", {"start": v(15.64, 13.75) * mm, "end": v(15.68, 13.73) * mm});
            skLineSegment(sketch, "E12353", {"start": v(15.68, 13.73) * mm, "end": v(15.74, 13.7) * mm});
            skLineSegment(sketch, "E12354", {"start": v(15.74, 13.7) * mm, "end": v(15.84, 13.66) * mm});
            skLineSegment(sketch, "E12355", {"start": v(15.84, 13.66) * mm, "end": v(15.94, 13.6) * mm});
            skLineSegment(sketch, "E12356", {"start": v(15.94, 13.6) * mm, "end": v(16.03, 13.54) * mm});
            skLineSegment(sketch, "E12357", {"start": v(16.03, 13.54) * mm, "end": v(16.13, 13.47) * mm});
            skLineSegment(sketch, "E12358", {"start": v(16.13, 13.47) * mm, "end": v(16.22, 13.38) * mm});
            skLineSegment(sketch, "E12359", {"start": v(16.22, 13.38) * mm, "end": v(16.3, 13.29) * mm});
            skLineSegment(sketch, "E12360", {"start": v(16.3, 13.29) * mm, "end": v(16.4, 13.19) * mm});
            skLineSegment(sketch, "E12361", {"start": v(16.4, 13.19) * mm, "end": v(16.48, 13.07) * mm});
            skLineSegment(sketch, "E12362", {"start": v(16.48, 13.07) * mm, "end": v(16.5, 13.05) * mm});
            skLineSegment(sketch, "E12363", {"start": v(16.5, 13.05) * mm, "end": v(16.52, 13.03) * mm});
            skLineSegment(sketch, "E12364", {"start": v(16.52, 13.03) * mm, "end": v(16.54, 13.02) * mm});
            skLineSegment(sketch, "E12365", {"start": v(16.54, 13.02) * mm, "end": v(16.56, 13) * mm});
            skLineSegment(sketch, "E12366", {"start": v(16.56, 13) * mm, "end": v(16.58, 13) * mm});
            skLineSegment(sketch, "E12367", {"start": v(16.58, 13) * mm, "end": v(16.6, 12.99) * mm});
            skLineSegment(sketch, "E12368", {"start": v(16.6, 12.99) * mm, "end": v(16.62, 12.98) * mm});
            skLineSegment(sketch, "E12369", {"start": v(16.62, 12.98) * mm, "end": v(16.63, 12.98) * mm});
            skLineSegment(sketch, "E12370", {"start": v(16.63, 12.98) * mm, "end": v(16.64, 12.97) * mm});
            skLineSegment(sketch, "E12371", {"start": v(16.64, 12.97) * mm, "end": v(16.65, 12.97) * mm});
            skLineSegment(sketch, "E12372", {"start": v(16.65, 12.97) * mm, "end": v(16.66, 12.97) * mm});
            skLineSegment(sketch, "E12373", {"start": v(16.66, 12.97) * mm, "end": v(16.67, 12.97) * mm});
            skLineSegment(sketch, "E12374", {"start": v(16.67, 12.97) * mm, "end": v(16.67, 12.97) * mm});
            skLineSegment(sketch, "E12375", {"start": v(16.67, 12.97) * mm, "end": v(16.7, 12.96) * mm});
            skLineSegment(sketch, "E12376", {"start": v(16.7, 12.96) * mm, "end": v(16.71, 12.96) * mm});
            skLineSegment(sketch, "E12377", {"start": v(16.71, 12.96) * mm, "end": v(16.73, 12.96) * mm});
            skLineSegment(sketch, "E12378", {"start": v(16.73, 12.96) * mm, "end": v(16.76, 12.96) * mm});
            skLineSegment(sketch, "E12379", {"start": v(16.76, 12.96) * mm, "end": v(16.78, 12.95) * mm});
            skLineSegment(sketch, "E12380", {"start": v(16.78, 12.95) * mm, "end": v(16.8, 12.95) * mm});
            skLineSegment(sketch, "E12381", {"start": v(16.8, 12.95) * mm, "end": v(16.81, 12.95) * mm});
            skLineSegment(sketch, "E12382", {"start": v(16.81, 12.95) * mm, "end": v(16.83, 12.94) * mm});
            skLineSegment(sketch, "E12383", {"start": v(16.83, 12.94) * mm, "end": v(16.84, 12.94) * mm});
            skLineSegment(sketch, "E12384", {"start": v(16.84, 12.94) * mm, "end": v(16.86, 12.94) * mm});
            skLineSegment(sketch, "E12385", {"start": v(16.86, 12.94) * mm, "end": v(16.87, 12.94) * mm});
            skLineSegment(sketch, "E12386", {"start": v(16.87, 12.94) * mm, "end": v(16.88, 12.95) * mm});
            skLineSegment(sketch, "E12387", {"start": v(16.88, 12.95) * mm, "end": v(16.9, 12.95) * mm});
            skLineSegment(sketch, "E12388", {"start": v(16.9, 12.95) * mm, "end": v(16.9, 12.95) * mm});
            skLineSegment(sketch, "E12389", {"start": v(16.9, 12.95) * mm, "end": v(16.9, 12.96) * mm});
            skLineSegment(sketch, "E12390", {"start": v(16.9, 12.96) * mm, "end": v(16.91, 12.96) * mm});
            skLineSegment(sketch, "E12391", {"start": v(16.91, 12.96) * mm, "end": v(16.94, 13.02) * mm});
            skLineSegment(sketch, "E12392", {"start": v(16.94, 13.02) * mm, "end": v(16.96, 13.08) * mm});
            skLineSegment(sketch, "E12393", {"start": v(16.96, 13.08) * mm, "end": v(16.97, 13.14) * mm});
            skLineSegment(sketch, "E12394", {"start": v(16.97, 13.14) * mm, "end": v(16.97, 13.2) * mm});
            skLineSegment(sketch, "E12395", {"start": v(16.97, 13.2) * mm, "end": v(16.96, 13.26) * mm});
            skLineSegment(sketch, "E12396", {"start": v(16.96, 13.26) * mm, "end": v(16.94, 13.31) * mm});
            skLineSegment(sketch, "E12397", {"start": v(16.94, 13.31) * mm, "end": v(16.9, 13.37) * mm});
            skLineSegment(sketch, "E12398", {"start": v(16.9, 13.37) * mm, "end": v(16.87, 13.42) * mm});
            skLineSegment(sketch, "E12399", {"start": v(16.87, 13.42) * mm, "end": v(16.85, 13.44) * mm});
            skLineSegment(sketch, "E12400", {"start": v(16.85, 13.44) * mm, "end": v(16.84, 13.45) * mm});
            skLineSegment(sketch, "E12401", {"start": v(16.84, 13.45) * mm, "end": v(16.82, 13.47) * mm});
            skLineSegment(sketch, "E12402", {"start": v(16.82, 13.47) * mm, "end": v(16.8, 13.5) * mm});
            skLineSegment(sketch, "E12403", {"start": v(16.8, 13.5) * mm, "end": v(16.79, 13.51) * mm});
            skLineSegment(sketch, "E12404", {"start": v(16.79, 13.51) * mm, "end": v(16.77, 13.53) * mm});
            skLineSegment(sketch, "E12405", {"start": v(16.77, 13.53) * mm, "end": v(16.76, 13.55) * mm});
            skLineSegment(sketch, "E12406", {"start": v(16.76, 13.55) * mm, "end": v(16.74, 13.57) * mm});
            skLineSegment(sketch, "E12407", {"start": v(16.74, 13.57) * mm, "end": v(16.69, 13.64) * mm});
            skLineSegment(sketch, "E12408", {"start": v(16.69, 13.64) * mm, "end": v(16.63, 13.71) * mm});
            skLineSegment(sketch, "E12409", {"start": v(16.63, 13.71) * mm, "end": v(16.57, 13.78) * mm});
            skLineSegment(sketch, "E12410", {"start": v(16.57, 13.78) * mm, "end": v(16.5, 13.84) * mm});
            skLineSegment(sketch, "E12411", {"start": v(16.5, 13.84) * mm, "end": v(16.44, 13.9) * mm});
            skLineSegment(sketch, "E12412", {"start": v(16.44, 13.9) * mm, "end": v(16.37, 13.95) * mm});
            skLineSegment(sketch, "E12413", {"start": v(16.37, 13.95) * mm, "end": v(16.29, 14) * mm});
            skLineSegment(sketch, "E12414", {"start": v(16.29, 14) * mm, "end": v(16.2, 14.04) * mm});
            skLineSegment(sketch, "E12415", {"start": v(16.2, 14.04) * mm, "end": v(16.19, 14.05) * mm});
            skLineSegment(sketch, "E12416", {"start": v(16.19, 14.05) * mm, "end": v(16.18, 14.06) * mm});
            skLineSegment(sketch, "E12417", {"start": v(16.18, 14.06) * mm, "end": v(16.16, 14.06) * mm});
            skLineSegment(sketch, "E12418", {"start": v(16.16, 14.06) * mm, "end": v(16.15, 14.07) * mm});
            skLineSegment(sketch, "E12419", {"start": v(16.15, 14.07) * mm, "end": v(16.14, 14.08) * mm});
            skLineSegment(sketch, "E12420", {"start": v(16.14, 14.08) * mm, "end": v(16.13, 14.09) * mm});
            skLineSegment(sketch, "E12421", {"start": v(16.13, 14.09) * mm, "end": v(16.11, 14.1) * mm});
            skLineSegment(sketch, "E12422", {"start": v(16.11, 14.1) * mm, "end": v(16.1, 14.1) * mm});
            skLineSegment(sketch, "E12423", {"start": v(16.1, 14.1) * mm, "end": v(16.08, 14.12) * mm});
            skLineSegment(sketch, "E12424", {"start": v(16.08, 14.12) * mm, "end": v(16.05, 14.14) * mm});
            skLineSegment(sketch, "E12425", {"start": v(16.05, 14.14) * mm, "end": v(16.03, 14.15) * mm});
            skLineSegment(sketch, "E12426", {"start": v(16.03, 14.15) * mm, "end": v(16, 14.17) * mm});
            skLineSegment(sketch, "E12427", {"start": v(16, 14.17) * mm, "end": v(15.98, 14.18) * mm});
            skLineSegment(sketch, "E12428", {"start": v(15.98, 14.18) * mm, "end": v(15.95, 14.2) * mm});
            skLineSegment(sketch, "E12429", {"start": v(15.95, 14.2) * mm, "end": v(15.93, 14.2) * mm});
            skLineSegment(sketch, "E12430", {"start": v(15.93, 14.2) * mm, "end": v(15.9, 14.2) * mm});
            skLineSegment(sketch, "E12431", {"start": v(15.9, 14.2) * mm, "end": v(15.8, 14.22) * mm});
            skLineSegment(sketch, "E12432", {"start": v(15.8, 14.22) * mm, "end": v(15.7, 14.24) * mm});
            skLineSegment(sketch, "E12433", {"start": v(15.7, 14.24) * mm, "end": v(15.6, 14.25) * mm});
            skLineSegment(sketch, "E12434", {"start": v(15.6, 14.25) * mm, "end": v(15.5, 14.26) * mm});
            skLineSegment(sketch, "E12435", {"start": v(15.5, 14.26) * mm, "end": v(15.4, 14.27) * mm});
            skLineSegment(sketch, "E12436", {"start": v(15.4, 14.27) * mm, "end": v(15.3, 14.28) * mm});
            skLineSegment(sketch, "E12437", {"start": v(15.3, 14.28) * mm, "end": v(15.2, 14.3) * mm});
            skLineSegment(sketch, "E12438", {"start": v(15.2, 14.3) * mm, "end": v(15.1, 14.3) * mm});
            skLineSegment(sketch, "E12439", {"start": v(15.1, 14.3) * mm, "end": v(15.06, 14.31) * mm});
            skLineSegment(sketch, "E12440", {"start": v(15.06, 14.31) * mm, "end": v(15, 14.32) * mm});
            skLineSegment(sketch, "E12441", {"start": v(15, 14.32) * mm, "end": v(14.96, 14.32) * mm});
            skLineSegment(sketch, "E12442", {"start": v(14.96, 14.32) * mm, "end": v(14.92, 14.32) * mm});
            skLineSegment(sketch, "E12443", {"start": v(14.92, 14.32) * mm, "end": v(14.87, 14.32) * mm});
            skLineSegment(sketch, "E12444", {"start": v(14.87, 14.32) * mm, "end": v(14.82, 14.32) * mm});
            skLineSegment(sketch, "E12445", {"start": v(14.82, 14.32) * mm, "end": v(14.78, 14.32) * mm});
            skLineSegment(sketch, "E12446", {"start": v(14.78, 14.32) * mm, "end": v(14.73, 14.32) * mm});
            skLineSegment(sketch, "E12447", {"start": v(14.73, 14.32) * mm, "end": v(14.69, 14.31) * mm});
            skLineSegment(sketch, "E12448", {"start": v(14.69, 14.31) * mm, "end": v(14.64, 14.3) * mm});
            skLineSegment(sketch, "E12449", {"start": v(14.64, 14.3) * mm, "end": v(14.6, 14.29) * mm});
            skLineSegment(sketch, "E12450", {"start": v(14.6, 14.29) * mm, "end": v(14.56, 14.27) * mm});
            skLineSegment(sketch, "E12451", {"start": v(14.56, 14.27) * mm, "end": v(14.52, 14.25) * mm});
            skLineSegment(sketch, "E12452", {"start": v(14.52, 14.25) * mm, "end": v(14.48, 14.24) * mm});
            skLineSegment(sketch, "E12453", {"start": v(14.48, 14.24) * mm, "end": v(14.44, 14.22) * mm});
            skLineSegment(sketch, "E12454", {"start": v(14.44, 14.22) * mm, "end": v(14.4, 14.21) * mm});
            skLineSegment(sketch, "E12455", {"start": v(14.4, 14.21) * mm, "end": v(14.36, 14.2) * mm});
            skLineSegment(sketch, "E12456", {"start": v(14.36, 14.2) * mm, "end": v(14.33, 14.2) * mm});
            skLineSegment(sketch, "E12457", {"start": v(14.33, 14.2) * mm, "end": v(14.29, 14.18) * mm});
            skLineSegment(sketch, "E12458", {"start": v(14.29, 14.18) * mm, "end": v(14.25, 14.16) * mm});
            skLineSegment(sketch, "E12459", {"start": v(14.25, 14.16) * mm, "end": v(14.22, 14.14) * mm});
            skLineSegment(sketch, "E12460", {"start": v(14.22, 14.14) * mm, "end": v(14.18, 14.12) * mm});
            skLineSegment(sketch, "E12461", {"start": v(14.18, 14.12) * mm, "end": v(14.16, 14.09) * mm});
            skLineSegment(sketch, "E12462", {"start": v(14.16, 14.09) * mm, "end": v(14.13, 14.05) * mm});
            skLineSegment(sketch, "E12463", {"start": v(14.13, 14.05) * mm, "end": v(14.12, 14.02) * mm});
            skLineSegment(sketch, "E12464", {"start": v(14.12, 14.02) * mm, "end": v(14.1, 14) * mm});
            skLineSegment(sketch, "E12465", {"start": v(14.1, 14) * mm, "end": v(14.1, 13.97) * mm});
            skLineSegment(sketch, "E12466", {"start": v(14.1, 13.97) * mm, "end": v(14.1, 13.96) * mm});
            skLineSegment(sketch, "E12467", {"start": v(14.1, 13.96) * mm, "end": v(14.09, 13.95) * mm});
            skLineSegment(sketch, "E12468", {"start": v(14.09, 13.95) * mm, "end": v(14.08, 13.95) * mm});
            skLineSegment(sketch, "E12469", {"start": v(14.08, 13.95) * mm, "end": v(14.08, 13.95) * mm});
            skLineSegment(sketch, "E12470", {"start": v(14.08, 13.95) * mm, "end": v(14.1, 13.9) * mm});
            skLineSegment(sketch, "E12471", {"start": v(14.1, 13.9) * mm, "end": v(14.12, 13.87) * mm});
            skLineSegment(sketch, "E12472", {"start": v(15.9, 12.32) * mm, "end": v(15.92, 12.34) * mm});
            skLineSegment(sketch, "E12473", {"start": v(15.92, 12.34) * mm, "end": v(15.92, 12.37) * mm});
            skLineSegment(sketch, "E12474", {"start": v(15.92, 12.37) * mm, "end": v(15.92, 12.39) * mm});
            skLineSegment(sketch, "E12475", {"start": v(15.92, 12.39) * mm, "end": v(15.92, 12.4) * mm});
            skLineSegment(sketch, "E12476", {"start": v(15.92, 12.4) * mm, "end": v(15.91, 12.4) * mm});
            skLineSegment(sketch, "E12477", {"start": v(15.91, 12.4) * mm, "end": v(15.9, 12.41) * mm});
            skLineSegment(sketch, "E12478", {"start": v(15.9, 12.41) * mm, "end": v(15.9, 12.42) * mm});
            skLineSegment(sketch, "E12479", {"start": v(15.9, 12.42) * mm, "end": v(15.9, 12.43) * mm});
            skLineSegment(sketch, "E12480", {"start": v(15.9, 12.43) * mm, "end": v(15.89, 12.44) * mm});
            skLineSegment(sketch, "E12481", {"start": v(15.89, 12.44) * mm, "end": v(15.88, 12.45) * mm});
            skLineSegment(sketch, "E12482", {"start": v(15.88, 12.45) * mm, "end": v(15.87, 12.46) * mm});
            skLineSegment(sketch, "E12483", {"start": v(15.87, 12.46) * mm, "end": v(15.83, 12.48) * mm});
            skLineSegment(sketch, "E12484", {"start": v(15.83, 12.48) * mm, "end": v(15.8, 12.51) * mm});
            skLineSegment(sketch, "E12485", {"start": v(15.8, 12.51) * mm, "end": v(15.76, 12.54) * mm});
            skLineSegment(sketch, "E12486", {"start": v(15.76, 12.54) * mm, "end": v(15.72, 12.56) * mm});
            skLineSegment(sketch, "E12487", {"start": v(15.72, 12.56) * mm, "end": v(15.68, 12.59) * mm});
            skLineSegment(sketch, "E12488", {"start": v(15.68, 12.59) * mm, "end": v(15.65, 12.61) * mm});
            skLineSegment(sketch, "E12489", {"start": v(15.65, 12.61) * mm, "end": v(15.6, 12.64) * mm});
            skLineSegment(sketch, "E12490", {"start": v(15.6, 12.64) * mm, "end": v(15.57, 12.66) * mm});
            skLineSegment(sketch, "E12491", {"start": v(15.57, 12.66) * mm, "end": v(15.52, 12.68) * mm});
            skLineSegment(sketch, "E12492", {"start": v(15.52, 12.68) * mm, "end": v(15.48, 12.68) * mm});
            skLineSegment(sketch, "E12493", {"start": v(15.48, 12.68) * mm, "end": v(15.43, 12.66) * mm});
            skLineSegment(sketch, "E12494", {"start": v(15.43, 12.66) * mm, "end": v(15.38, 12.63) * mm});
            skLineSegment(sketch, "E12495", {"start": v(15.38, 12.63) * mm, "end": v(15.34, 12.59) * mm});
            skLineSegment(sketch, "E12496", {"start": v(15.34, 12.59) * mm, "end": v(15.31, 12.54) * mm});
            skLineSegment(sketch, "E12497", {"start": v(15.31, 12.54) * mm, "end": v(15.3, 12.5) * mm});
            skLineSegment(sketch, "E12498", {"start": v(15.3, 12.5) * mm, "end": v(15.28, 12.46) * mm});
            skLineSegment(sketch, "E12499", {"start": v(15.28, 12.46) * mm, "end": v(15.29, 12.42) * mm});
            skLineSegment(sketch, "E12500", {"start": v(15.29, 12.42) * mm, "end": v(15.3, 12.4) * mm});
            skLineSegment(sketch, "E12501", {"start": v(15.3, 12.4) * mm, "end": v(15.33, 12.37) * mm});
            skLineSegment(sketch, "E12502", {"start": v(15.33, 12.37) * mm, "end": v(15.36, 12.35) * mm});
            skLineSegment(sketch, "E12503", {"start": v(15.36, 12.35) * mm, "end": v(15.4, 12.33) * mm});
            skLineSegment(sketch, "E12504", {"start": v(15.4, 12.33) * mm, "end": v(15.43, 12.31) * mm});
            skLineSegment(sketch, "E12505", {"start": v(15.43, 12.31) * mm, "end": v(15.47, 12.3) * mm});
            skLineSegment(sketch, "E12506", {"start": v(15.47, 12.3) * mm, "end": v(15.5, 12.29) * mm});
            skLineSegment(sketch, "E12507", {"start": v(15.5, 12.29) * mm, "end": v(15.53, 12.28) * mm});
            skLineSegment(sketch, "E12508", {"start": v(15.53, 12.28) * mm, "end": v(15.57, 12.27) * mm});
            skLineSegment(sketch, "E12509", {"start": v(15.57, 12.27) * mm, "end": v(15.6, 12.26) * mm});
            skLineSegment(sketch, "E12510", {"start": v(15.6, 12.26) * mm, "end": v(15.64, 12.25) * mm});
            skLineSegment(sketch, "E12511", {"start": v(15.64, 12.25) * mm, "end": v(15.68, 12.25) * mm});
            skLineSegment(sketch, "E12512", {"start": v(15.68, 12.25) * mm, "end": v(15.71, 12.24) * mm});
            skLineSegment(sketch, "E12513", {"start": v(15.71, 12.24) * mm, "end": v(15.75, 12.25) * mm});
            skLineSegment(sketch, "E12514", {"start": v(15.75, 12.25) * mm, "end": v(15.78, 12.25) * mm});
            skLineSegment(sketch, "E12515", {"start": v(15.78, 12.25) * mm, "end": v(15.81, 12.26) * mm});
            skLineSegment(sketch, "E12516", {"start": v(15.81, 12.26) * mm, "end": v(15.84, 12.27) * mm});
            skLineSegment(sketch, "E12517", {"start": v(15.84, 12.27) * mm, "end": v(15.87, 12.29) * mm});
            skLineSegment(sketch, "E12518", {"start": v(15.87, 12.29) * mm, "end": v(15.89, 12.3) * mm});
            skLineSegment(sketch, "E12519", {"start": v(15.89, 12.3) * mm, "end": v(15.9, 12.32) * mm});
            skLineSegment(sketch, "E12520", {"start": v(15.86, 11.55) * mm, "end": v(15.84, 11.58) * mm});
            skLineSegment(sketch, "E12521", {"start": v(15.84, 11.58) * mm, "end": v(15.82, 11.61) * mm});
            skLineSegment(sketch, "E12522", {"start": v(15.82, 11.61) * mm, "end": v(15.79, 11.64) * mm});
            skLineSegment(sketch, "E12523", {"start": v(15.79, 11.64) * mm, "end": v(15.76, 11.65) * mm});
            skLineSegment(sketch, "E12524", {"start": v(15.76, 11.65) * mm, "end": v(15.72, 11.66) * mm});
            skLineSegment(sketch, "E12525", {"start": v(15.72, 11.66) * mm, "end": v(15.68, 11.66) * mm});
            skLineSegment(sketch, "E12526", {"start": v(15.68, 11.66) * mm, "end": v(15.64, 11.65) * mm});
            skLineSegment(sketch, "E12527", {"start": v(15.64, 11.65) * mm, "end": v(15.6, 11.64) * mm});
            skLineSegment(sketch, "E12528", {"start": v(15.6, 11.64) * mm, "end": v(15.57, 11.63) * mm});
            skLineSegment(sketch, "E12529", {"start": v(15.57, 11.63) * mm, "end": v(15.54, 11.62) * mm});
            skLineSegment(sketch, "E12530", {"start": v(15.54, 11.62) * mm, "end": v(15.51, 11.6) * mm});
            skLineSegment(sketch, "E12531", {"start": v(15.51, 11.6) * mm, "end": v(15.5, 11.58) * mm});
            skLineSegment(sketch, "E12532", {"start": v(15.5, 11.58) * mm, "end": v(15.48, 11.56) * mm});
            skLineSegment(sketch, "E12533", {"start": v(15.48, 11.56) * mm, "end": v(15.48, 11.55) * mm});
            skLineSegment(sketch, "E12534", {"start": v(15.48, 11.55) * mm, "end": v(15.48, 11.52) * mm});
            skLineSegment(sketch, "E12535", {"start": v(15.48, 11.52) * mm, "end": v(15.49, 11.5) * mm});
            skLineSegment(sketch, "E12536", {"start": v(15.49, 11.5) * mm, "end": v(15.5, 11.48) * mm});
            skLineSegment(sketch, "E12537", {"start": v(15.5, 11.48) * mm, "end": v(15.53, 11.45) * mm});
            skLineSegment(sketch, "E12538", {"start": v(15.53, 11.45) * mm, "end": v(15.56, 11.42) * mm});
            skLineSegment(sketch, "E12539", {"start": v(15.56, 11.42) * mm, "end": v(15.59, 11.4) * mm});
            skLineSegment(sketch, "E12540", {"start": v(15.59, 11.4) * mm, "end": v(15.62, 11.37) * mm});
            skLineSegment(sketch, "E12541", {"start": v(15.62, 11.37) * mm, "end": v(15.66, 11.35) * mm});
            skLineSegment(sketch, "E12542", {"start": v(15.66, 11.35) * mm, "end": v(15.7, 11.34) * mm});
            skLineSegment(sketch, "E12543", {"start": v(15.7, 11.34) * mm, "end": v(15.74, 11.33) * mm});
            skLineSegment(sketch, "E12544", {"start": v(15.74, 11.33) * mm, "end": v(15.77, 11.33) * mm});
            skLineSegment(sketch, "E12545", {"start": v(15.77, 11.33) * mm, "end": v(15.8, 11.34) * mm});
            skLineSegment(sketch, "E12546", {"start": v(15.8, 11.34) * mm, "end": v(15.83, 11.36) * mm});
            skLineSegment(sketch, "E12547", {"start": v(15.83, 11.36) * mm, "end": v(15.85, 11.4) * mm});
            skLineSegment(sketch, "E12548", {"start": v(15.85, 11.4) * mm, "end": v(15.86, 11.43) * mm});
            skLineSegment(sketch, "E12549", {"start": v(15.86, 11.43) * mm, "end": v(15.87, 11.47) * mm});
            skLineSegment(sketch, "E12550", {"start": v(15.87, 11.47) * mm, "end": v(15.87, 11.51) * mm});
            skLineSegment(sketch, "E12551", {"start": v(15.87, 11.51) * mm, "end": v(15.86, 11.55) * mm});
            skSolve(sketch);
        }
        {
            var Q0;
            Q0 = qSketchRegion(id + "F0", true);
            extrude(context, id + "F1", {"entities" : qUnion([Q0]), "oppositeDirection" : true, "depth" : 10 * mm});
        }
        {
            var Q0;
            Q0=qCreatedBy(makeId("Top.planeOp"),FACE);
            var sketch = newSketch(context, id + "F2", { "sketchPlane" : qUnion([Q0])});
            skLineSegment(sketch, "E12552.bottom", {"start": v(50, -25) * mm, "end": v(-50, -25) * mm});
            skLineSegment(sketch, "E12552.top", {"start": v(50, 25) * mm, "end": v(-50, 25) * mm});
            skLineSegment(sketch, "E12552.left", {"start": v(50, -25) * mm, "end": v(50, 25) * mm});
            skLineSegment(sketch, "E12552.right", {"start": v(-50, -25) * mm, "end": v(-50, 25) * mm});
            skPoint(sketch, "E12552.middle", {"position": v(0, 0) * mm});
            skSolve(sketch);
        }
        {
            var Q0;
            Q0 = qSketchRegion(id + "F2", true);
            extrude(context, id + "F3", {"entities" : qUnion([Q0]), "depth" : 2 * mm, "hasSecondDirection" : true, "secondDirectionOppositeDirection" : true, "secondDirectionDepth" : 3 * mm});
        }
    });
